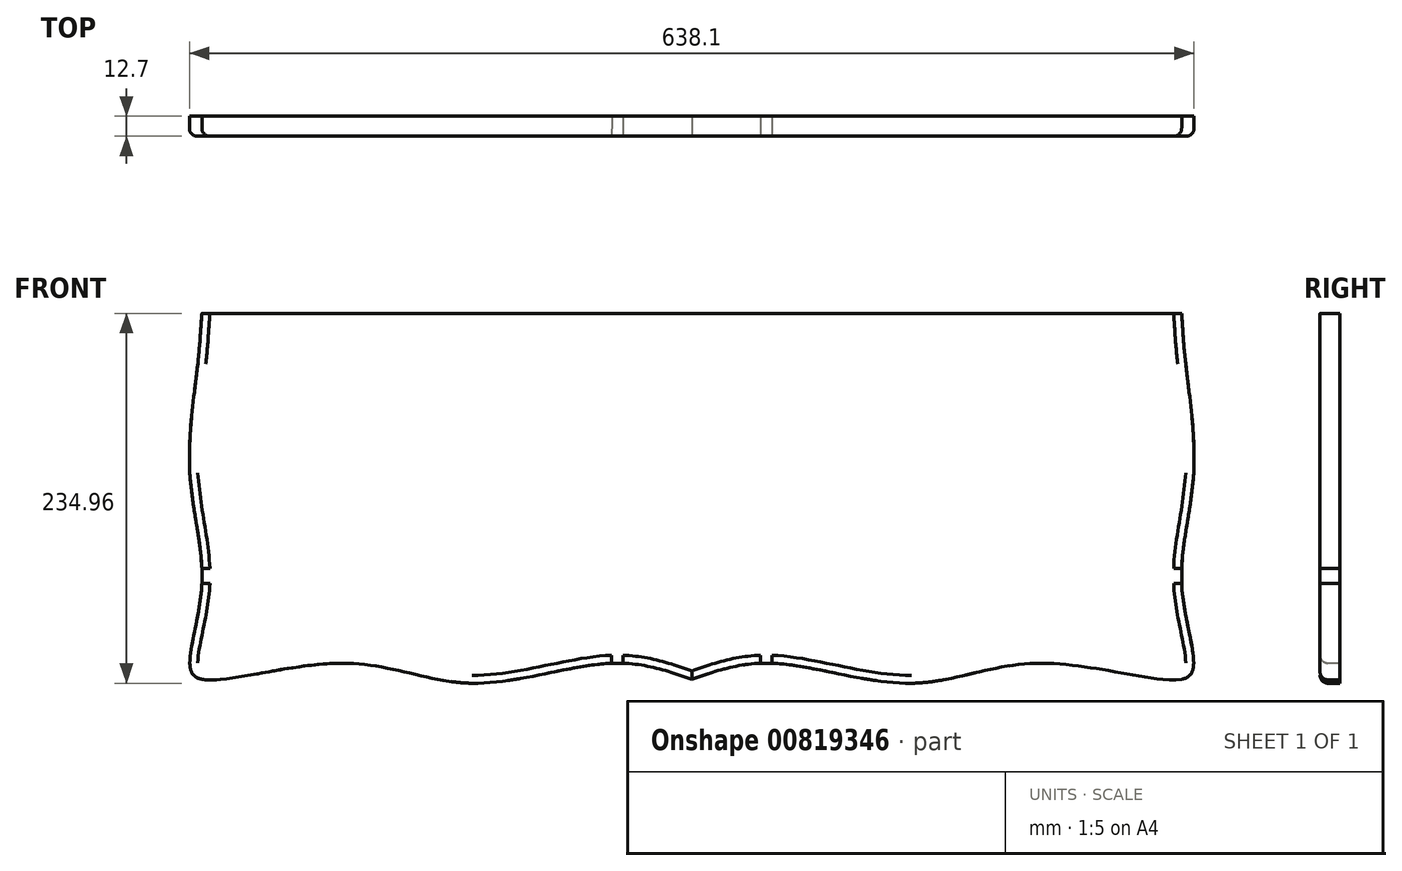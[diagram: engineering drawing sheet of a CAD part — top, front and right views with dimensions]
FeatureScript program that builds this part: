
annotation { "Feature Type Name" : "Feature", "Feature Type Description" : "" }
export const myFeature = defineFeature(function(context is Context, id is Id, definition is map)
    precondition{}
    {
        {
            var Q0;
            Q0=qCreatedBy(makeId("Front.planeOp"),FACE);
            var sketch = newSketch(context, id + "F0", { "sketchPlane" : qUnion([Q0])});
            skLineSegment(sketch, "E0.bottom", {"start": v(-290.57, 108.48) * mm, "end": v(331.73, 108.48) * mm});
            skLineSegment(sketch, "E0.top", {"start": v(-290.57, -113.77) * mm, "end": v(331.73, -113.77) * mm});
            skLineSegment(sketch, "E0.left", {"start": v(-290.57, 108.48) * mm, "end": v(-290.57, -113.77) * mm});
            skLineSegment(sketch, "E0.right", {"start": v(331.73, 108.48) * mm, "end": v(331.73, -113.77) * mm});
            skPoint(sketch, "E1", {"position": v(20.58, 108.48) * mm});
            skSolve(sketch);
        }
        {
            var Q0;
            Q0=makeQuery(id+"F0.imprint","IMPRINT",FACE,{"disambiguationData":[TD([[makeQuery(id+"F0.imprint","IMPRINT",EDGE,{"derivedFrom":sQuery(id+"F0.wireOp",EDGE,"E0.bottom")}),-1.0]])]});
            extrude(context, id + "F1", {"entities" : qUnion([Q0]), "depth" : 12.7 * mm, "offsetDistance" : 25.4 * mm});
        }
        {
            var Q0;
            {var subQ0=sQuery(id+"F0.wireOp",EDGE,"E0.right");var subQ1=sQuery(id+"F0.wireOp",EDGE,"E0.bottom");var subQ2=sQuery(id+"F0.wireOp",EDGE,"E0.left");var subQ3=sQuery(id+"F0.wireOp",EDGE,"E0.top");Q0=makeQuery(id+"FjgwLtvUwF4HY63_1.boolean.opBoolean","SPLIT",FACE,{"disambiguationData":[TD([makeQuery(id+"F1.opExtrude","SWEPT_FACE",FACE,{"disambiguationData":[OSD([subQ1])]})])],"derivedFrom":makeQuery(id+"F1.opExtrude","CAP_FACE",FACE,{"disambiguationData":[OSD([subQ1,subQ3,subQ2,subQ0])],"isStart":false})});}
            var sketch = newSketch(context, id + "F2", { "sketchPlane" : qUnion([Q0])});
            skPoint(sketch, "E2", {"position": v(-290.57, -62.97) * mm});
            skPoint(sketch, "E3", {"position": v(-290.57, 6.88) * mm});
            skPoint(sketch, "E4", {"position": v(-290.57, 76.73) * mm});
            skLineSegment(sketch, "E5", {"start": v(-290.57, 76.73) * mm, "end": v(-293.1, 76.73) * mm});
            skLineSegment(sketch, "E6", {"start": v(-290.57, 6.88) * mm, "end": v(-298.19, 6.88) * mm});
            skLineSegment(sketch, "E7", {"start": v(-290.57, -113.77) * mm, "end": v(-298.19, -113.77) * mm});
            skLineSegment(sketch, "E8", {"start": v(-290.57, -113.77) * mm, "end": v(-290.57, -123.93) * mm});
            skPoint(sketch, "E9", {"position": v(-201.67, -113.77) * mm});
            skPoint(sketch, "E10", {"position": v(20.58, -113.77) * mm});
            skPoint(sketch, "E11", {"position": v(-30.22, -113.77) * mm});
            skPoint(sketch, "E12", {"position": v(-119.12, -113.77) * mm});
            skPoint(sketch, "E13", {"position": v(71.38, -113.77) * mm});
            skPoint(sketch, "E14", {"position": v(160.28, -113.77) * mm});
            skPoint(sketch, "E15", {"position": v(242.83, -113.77) * mm});
            skPoint(sketch, "E16", {"position": v(331.73, -62.97) * mm});
            skPoint(sketch, "E17", {"position": v(331.73, 6.88) * mm});
            skPoint(sketch, "E18", {"position": v(331.73, 76.73) * mm});
            skLineSegment(sketch, "E19", {"start": v(331.73, 76.73) * mm, "end": v(334.27, 76.73) * mm});
            skLineSegment(sketch, "E20", {"start": v(331.73, 6.88) * mm, "end": v(339.35, 6.88) * mm});
            skLineSegment(sketch, "E21", {"start": v(331.73, -113.77) * mm, "end": v(339.35, -113.77) * mm});
            skLineSegment(sketch, "E22", {"start": v(331.73, -113.77) * mm, "end": v(331.73, -123.93) * mm});
            skLineSegment(sketch, "E23", {"start": v(-119.12, -113.77) * mm, "end": v(-119.12, -126.47) * mm});
            skLineSegment(sketch, "E24", {"start": v(20.58, -113.77) * mm, "end": v(20.58, -123.93) * mm});
            skLineSegment(sketch, "E25", {"start": v(160.28, -113.77) * mm, "end": v(160.28, -126.47) * mm});
            skFitSpline(sketch, "E26", {"points": [v(-290.57, 108.48) * mm, v(-293.1, 76.73) * mm, v(-298.19, 6.88) * mm, v(-290.57, -62.97) * mm, v(-298.19, -113.77) * mm, v(-290.57, -123.93) * mm, v(-201.67, -113.77) * mm, v(-119.12, -126.47) * mm, v(-30.22, -113.77) * mm, v(20.58, -123.93) * mm], "startDerivative": vector(-26.2, -341.82) * mm, "endDerivative": vector(438.15, -148.5) * mm});
            skFitSpline(sketch, "E27", {"points": [v(331.73, 108.48) * mm, v(334.27, 76.73) * mm, v(339.35, 6.88) * mm, v(331.73, -62.97) * mm, v(339.35, -113.77) * mm, v(331.73, -123.93) * mm, v(242.83, -113.77) * mm, v(160.28, -126.47) * mm, v(71.38, -113.77) * mm, v(20.58, -123.93) * mm], "startDerivative": vector(26.2, -341.82) * mm, "endDerivative": vector(-438.15, -148.5) * mm});
            skSolve(sketch);
        }
        {
            var Q0;
            {var subQ0=sQuery(id+"F2.wireOp",EDGE,"E24");Q0=makeQuery(id+"F2.imprint","IMPRINT",FACE,{"disambiguationData":[TD([[makeQuery(id+"F2.imprint","IMPRINT",EDGE,{"derivedFrom":subQ0}),-1.0]])]});}
            var Q1;
            {var subQ0=sQuery(id+"F2.wireOp",EDGE,"E24");Q1=makeQuery(id+"F2.imprint","IMPRINT",FACE,{"disambiguationData":[TD([[makeQuery(id+"F2.imprint","IMPRINT",EDGE,{"derivedFrom":subQ0}),1.0]])]});}
            var Q2;
            {var subQ0=sQuery(id+"F2.wireOp",EDGE,"E23");Q2=makeQuery(id+"F2.imprint","IMPRINT",FACE,{"disambiguationData":[TD([[makeQuery(id+"F2.imprint","IMPRINT",EDGE,{"derivedFrom":subQ0}),1.0]])]});}
            var Q3;
            {var subQ0=sQuery(id+"F2.wireOp",EDGE,"E23");Q3=makeQuery(id+"F2.imprint","IMPRINT",FACE,{"disambiguationData":[TD([[makeQuery(id+"F2.imprint","IMPRINT",EDGE,{"derivedFrom":subQ0}),-1.0]])]});}
            var Q4;
            {var subQ0=sQuery(id+"F2.wireOp",EDGE,"E8");Q4=makeQuery(id+"F2.imprint","IMPRINT",FACE,{"disambiguationData":[TD([[makeQuery(id+"F2.imprint","IMPRINT",EDGE,{"derivedFrom":subQ0}),1.0]])]});}
            var Q5;
            {var subQ0=sQuery(id+"F2.wireOp",EDGE,"E7");Q5=makeQuery(id+"F2.imprint","IMPRINT",FACE,{"disambiguationData":[TD([[makeQuery(id+"F2.imprint","IMPRINT",EDGE,{"derivedFrom":subQ0}),1.0]])]});}
            var Q6;
            {var subQ0=sQuery(id+"F2.wireOp",EDGE,"E7");Q6=makeQuery(id+"F2.imprint","IMPRINT",FACE,{"disambiguationData":[TD([[makeQuery(id+"F2.imprint","IMPRINT",EDGE,{"derivedFrom":subQ0}),-1.0]])]});}
            var Q7;
            {var subQ0=sQuery(id+"F2.wireOp",EDGE,"E6");Q7=makeQuery(id+"F2.imprint","IMPRINT",FACE,{"disambiguationData":[TD([[makeQuery(id+"F2.imprint","IMPRINT",EDGE,{"derivedFrom":subQ0}),1.0]])]});}
            var Q8;
            {var subQ0=sQuery(id+"F2.wireOp",EDGE,"E5");Q8=makeQuery(id+"F2.imprint","IMPRINT",FACE,{"disambiguationData":[TD([[makeQuery(id+"F2.imprint","IMPRINT",EDGE,{"derivedFrom":subQ0}),1.0]])]});}
            var Q9;
            {var subQ0=makeQuery(id+"F1.opExtrude","CAP_EDGE",EDGE,{"disambiguationData":[OSD([sQuery(id+"F0.wireOp",EDGE,"E0.bottom")])],"isStart":false});Q9=makeQuery(id+"F2.imprint","IMPRINT",FACE,{"disambiguationData":[TD([[makeQuery(id+"F2.imprint","IMPRINT",EDGE,{"derivedFrom":subQ0}),-1.0]])]});}
            var Q10;
            {var subQ0=sQuery(id+"F2.wireOp",EDGE,"E25");Q10=makeQuery(id+"F2.imprint","IMPRINT",FACE,{"disambiguationData":[TD([[makeQuery(id+"F2.imprint","IMPRINT",EDGE,{"derivedFrom":subQ0}),-1.0]])]});}
            var Q11;
            {var subQ0=sQuery(id+"F2.wireOp",EDGE,"E25");Q11=makeQuery(id+"F2.imprint","IMPRINT",FACE,{"disambiguationData":[TD([[makeQuery(id+"F2.imprint","IMPRINT",EDGE,{"derivedFrom":subQ0}),1.0]])]});}
            var Q12;
            {var subQ0=sQuery(id+"F2.wireOp",EDGE,"E22");Q12=makeQuery(id+"F2.imprint","IMPRINT",FACE,{"disambiguationData":[TD([[makeQuery(id+"F2.imprint","IMPRINT",EDGE,{"derivedFrom":subQ0}),-1.0]])]});}
            var Q13;
            {var subQ0=sQuery(id+"F2.wireOp",EDGE,"E21");Q13=makeQuery(id+"F2.imprint","IMPRINT",FACE,{"disambiguationData":[TD([[makeQuery(id+"F2.imprint","IMPRINT",EDGE,{"derivedFrom":subQ0}),-1.0]])]});}
            var Q14;
            {var subQ0=sQuery(id+"F2.wireOp",EDGE,"E21");Q14=makeQuery(id+"F2.imprint","IMPRINT",FACE,{"disambiguationData":[TD([[makeQuery(id+"F2.imprint","IMPRINT",EDGE,{"derivedFrom":subQ0}),1.0]])]});}
            var Q15;
            {var subQ0=sQuery(id+"F2.wireOp",EDGE,"E20");Q15=makeQuery(id+"F2.imprint","IMPRINT",FACE,{"disambiguationData":[TD([[makeQuery(id+"F2.imprint","IMPRINT",EDGE,{"derivedFrom":subQ0}),-1.0]])]});}
            var Q16;
            {var subQ0=sQuery(id+"F2.wireOp",EDGE,"E19");Q16=makeQuery(id+"F2.imprint","IMPRINT",FACE,{"disambiguationData":[TD([[makeQuery(id+"F2.imprint","IMPRINT",EDGE,{"derivedFrom":subQ0}),-1.0]])]});}
            var Q17;
            {var subQ0=sQuery(id+"F2.wireOp",EDGE,"E19");Q17=makeQuery(id+"F2.imprint","IMPRINT",FACE,{"disambiguationData":[TD([[makeQuery(id+"F2.imprint","IMPRINT",EDGE,{"derivedFrom":subQ0}),1.0]])]});}
            var Q18;
            {var subQ0=sQuery(id+"F2.wireOp",EDGE,"E5");Q18=makeQuery(id+"F2.imprint","IMPRINT",FACE,{"disambiguationData":[TD([[makeQuery(id+"F2.imprint","IMPRINT",EDGE,{"derivedFrom":subQ0}),-1.0]])]});}
            extrude(context, id + "F3", {"entities" : qUnion([Q0, Q1, Q2, Q3, Q4, Q5, Q6, Q7, Q8, Q9, Q10, Q11, Q12, Q13, Q14, Q15, Q16, Q17, Q18]), "operationType" : NewBodyOperationType.ADD, "depth" : -12.7 * mm, "offsetDistance" : 25.4 * mm});
        }
        {
            var Q0;
            {var subQ0=sQuery(id+"F2.wireOp",EDGE,"8007402e-1a4e-4a06-85a5-2af08e553504");var subQ1=sQuery(id+"F0.wireOp",EDGE,"E0.left");var subQ2=sQuery(id+"F0.wireOp",EDGE,"E0.top");var subQ3=sQuery(id+"F0.wireOp",EDGE,"E0.bottom");Q0=makeQuery(id+"F3.boolean.opBoolean","SPLIT",EDGE,{"disambiguationData":[TD([makeQuery(id+"F1.opExtrude","CAP_FACE",FACE,{"disambiguationData":[OSD([subQ3,subQ2,subQ1,sQuery(id+"F0.wireOp",EDGE,"E0.right")])],"isStart":false}),makeQuery(id+"F1.opExtrude","SWEPT_FACE",FACE,{"disambiguationData":[OSD([subQ2])]}),makeQuery(id+"F1.opExtrude","SWEPT_FACE",FACE,{"disambiguationData":[OSD([subQ1])]}),makeQuery(id+"F3.opExtrude","SWEPT_FACE",FACE,{"disambiguationData":[OSD([subQ0])]}),makeQuery(id+"F3.opExtrude","CAP_FACE",FACE,{"disambiguationData":[OSD([subQ3,sQuery(id+"FQ5JFwxVdaqARUP_1.wireOp",EDGE,"fcba4419-a2ee-464f-be9d-58f11bf3418b.sketch_text.stroke-0"),sQuery(id+"FQ5JFwxVdaqARUP_1.wireOp",EDGE,"fcba4419-a2ee-464f-be9d-58f11bf3418b.sketch_text.stroke-1"),sQuery(id+"FQ5JFwxVdaqARUP_1.wireOp",EDGE,"fcba4419-a2ee-464f-be9d-58f11bf3418b.sketch_text.stroke-2"),sQuery(id+"FQ5JFwxVdaqARUP_1.wireOp",EDGE,"fcba4419-a2ee-464f-be9d-58f11bf3418b.sketch_text.stroke-3"),sQuery(id+"FQ5JFwxVdaqARUP_1.wireOp",EDGE,"fcba4419-a2ee-464f-be9d-58f11bf3418b.sketch_text.stroke-4"),sQuery(id+"FQ5JFwxVdaqARUP_1.wireOp",EDGE,"fcba4419-a2ee-464f-be9d-58f11bf3418b.sketch_text.stroke-5"),sQuery(id+"FQ5JFwxVdaqARUP_1.wireOp",EDGE,"fcba4419-a2ee-464f-be9d-58f11bf3418b.sketch_text.stroke-6"),sQuery(id+"FQ5JFwxVdaqARUP_1.wireOp",EDGE,"fcba4419-a2ee-464f-be9d-58f11bf3418b.sketch_text.stroke-7"),sQuery(id+"FQ5JFwxVdaqARUP_1.wireOp",EDGE,"fcba4419-a2ee-464f-be9d-58f11bf3418b.sketch_text.stroke-8"),sQuery(id+"FQ5JFwxVdaqARUP_1.wireOp",EDGE,"fcba4419-a2ee-464f-be9d-58f11bf3418b.sketch_text.stroke-9"),sQuery(id+"FQ5JFwxVdaqARUP_1.wireOp",EDGE,"fcba4419-a2ee-464f-be9d-58f11bf3418b.sketch_text.stroke-10"),sQuery(id+"FQ5JFwxVdaqARUP_1.wireOp",EDGE,"fcba4419-a2ee-464f-be9d-58f11bf3418b.sketch_text.stroke-11"),sQuery(id+"FQ5JFwxVdaqARUP_1.wireOp",EDGE,"fcba4419-a2ee-464f-be9d-58f11bf3418b.sketch_text.stroke-12"),sQuery(id+"FQ5JFwxVdaqARUP_1.wireOp",EDGE,"fcba4419-a2ee-464f-be9d-58f11bf3418b.sketch_text.stroke-13"),sQuery(id+"FQ5JFwxVdaqARUP_1.wireOp",EDGE,"fcba4419-a2ee-464f-be9d-58f11bf3418b.sketch_text.stroke-14"),sQuery(id+"FQ5JFwxVdaqARUP_1.wireOp",EDGE,"fcba4419-a2ee-464f-be9d-58f11bf3418b.sketch_text.stroke-15"),sQuery(id+"FQ5JFwxVdaqARUP_1.wireOp",EDGE,"fcba4419-a2ee-464f-be9d-58f11bf3418b.sketch_text.stroke-16"),sQuery(id+"FQ5JFwxVdaqARUP_1.wireOp",EDGE,"fcba4419-a2ee-464f-be9d-58f11bf3418b.sketch_text.stroke-17"),sQuery(id+"FQ5JFwxVdaqARUP_1.wireOp",EDGE,"fcba4419-a2ee-464f-be9d-58f11bf3418b.sketch_text.stroke-18"),sQuery(id+"FQ5JFwxVdaqARUP_1.wireOp",EDGE,"fcba4419-a2ee-464f-be9d-58f11bf3418b.sketch_text.stroke-19"),sQuery(id+"FQ5JFwxVdaqARUP_1.wireOp",EDGE,"fcba4419-a2ee-464f-be9d-58f11bf3418b.sketch_text.stroke-20"),sQuery(id+"FQ5JFwxVdaqARUP_1.wireOp",EDGE,"fcba4419-a2ee-464f-be9d-58f11bf3418b.sketch_text.stroke-21"),sQuery(id+"FQ5JFwxVdaqARUP_1.wireOp",EDGE,"fcba4419-a2ee-464f-be9d-58f11bf3418b.sketch_text.stroke-22"),sQuery(id+"FQ5JFwxVdaqARUP_1.wireOp",EDGE,"fcba4419-a2ee-464f-be9d-58f11bf3418b.sketch_text.stroke-23"),sQuery(id+"FQ5JFwxVdaqARUP_1.wireOp",EDGE,"fcba4419-a2ee-464f-be9d-58f11bf3418b.sketch_text.stroke-24"),sQuery(id+"FQ5JFwxVdaqARUP_1.wireOp",EDGE,"fcba4419-a2ee-464f-be9d-58f11bf3418b.sketch_text.stroke-25"),sQuery(id+"FQ5JFwxVdaqARUP_1.wireOp",EDGE,"fcba4419-a2ee-464f-be9d-58f11bf3418b.sketch_text.stroke-26"),sQuery(id+"FQ5JFwxVdaqARUP_1.wireOp",EDGE,"fcba4419-a2ee-464f-be9d-58f11bf3418b.sketch_text.stroke-27"),sQuery(id+"FQ5JFwxVdaqARUP_1.wireOp",EDGE,"fcba4419-a2ee-464f-be9d-58f11bf3418b.sketch_text.stroke-28"),sQuery(id+"FQ5JFwxVdaqARUP_1.wireOp",EDGE,"fcba4419-a2ee-464f-be9d-58f11bf3418b.sketch_text.stroke-29"),sQuery(id+"FQ5JFwxVdaqARUP_1.wireOp",EDGE,"fcba4419-a2ee-464f-be9d-58f11bf3418b.sketch_text.stroke-30"),sQuery(id+"FQ5JFwxVdaqARUP_1.wireOp",EDGE,"fcba4419-a2ee-464f-be9d-58f11bf3418b.sketch_text.stroke-31"),sQuery(id+"FQ5JFwxVdaqARUP_1.wireOp",EDGE,"fcba4419-a2ee-464f-be9d-58f11bf3418b.sketch_text.stroke-32"),sQuery(id+"FQ5JFwxVdaqARUP_1.wireOp",EDGE,"fcba4419-a2ee-464f-be9d-58f11bf3418b.sketch_text.stroke-33"),sQuery(id+"FQ5JFwxVdaqARUP_1.wireOp",EDGE,"fcba4419-a2ee-464f-be9d-58f11bf3418b.sketch_text.stroke-34"),sQuery(id+"FQ5JFwxVdaqARUP_1.wireOp",EDGE,"fcba4419-a2ee-464f-be9d-58f11bf3418b.sketch_text.stroke-35"),sQuery(id+"FQ5JFwxVdaqARUP_1.wireOp",EDGE,"fcba4419-a2ee-464f-be9d-58f11bf3418b.sketch_text.stroke-36"),sQuery(id+"FQ5JFwxVdaqARUP_1.wireOp",EDGE,"fcba4419-a2ee-464f-be9d-58f11bf3418b.sketch_text.stroke-37"),sQuery(id+"FQ5JFwxVdaqARUP_1.wireOp",EDGE,"fcba4419-a2ee-464f-be9d-58f11bf3418b.sketch_text.stroke-38"),sQuery(id+"FQ5JFwxVdaqARUP_1.wireOp",EDGE,"fcba4419-a2ee-464f-be9d-58f11bf3418b.sketch_text.stroke-39"),sQuery(id+"FQ5JFwxVdaqARUP_1.wireOp",EDGE,"fcba4419-a2ee-464f-be9d-58f11bf3418b.sketch_text.stroke-40"),sQuery(id+"FQ5JFwxVdaqARUP_1.wireOp",EDGE,"fcba4419-a2ee-464f-be9d-58f11bf3418b.sketch_text.stroke-41"),sQuery(id+"FQ5JFwxVdaqARUP_1.wireOp",EDGE,"fcba4419-a2ee-464f-be9d-58f11bf3418b.sketch_text.stroke-42"),sQuery(id+"FQ5JFwxVdaqARUP_1.wireOp",EDGE,"fcba4419-a2ee-464f-be9d-58f11bf3418b.sketch_text.stroke-43"),sQuery(id+"FQ5JFwxVdaqARUP_1.wireOp",EDGE,"fcba4419-a2ee-464f-be9d-58f11bf3418b.sketch_text.stroke-44"),sQuery(id+"FQ5JFwxVdaqARUP_1.wireOp",EDGE,"fcba4419-a2ee-464f-be9d-58f11bf3418b.sketch_text.stroke-45"),sQuery(id+"FQ5JFwxVdaqARUP_1.wireOp",EDGE,"fcba4419-a2ee-464f-be9d-58f11bf3418b.sketch_text.stroke-46"),sQuery(id+"FQ5JFwxVdaqARUP_1.wireOp",EDGE,"fcba4419-a2ee-464f-be9d-58f11bf3418b.sketch_text.stroke-47"),sQuery(id+"FQ5JFwxVdaqARUP_1.wireOp",EDGE,"fcba4419-a2ee-464f-be9d-58f11bf3418b.sketch_text.stroke-48"),sQuery(id+"FQ5JFwxVdaqARUP_1.wireOp",EDGE,"fcba4419-a2ee-464f-be9d-58f11bf3418b.sketch_text.stroke-49"),sQuery(id+"FQ5JFwxVdaqARUP_1.wireOp",EDGE,"fcba4419-a2ee-464f-be9d-58f11bf3418b.sketch_text.stroke-50"),sQuery(id+"FQ5JFwxVdaqARUP_1.wireOp",EDGE,"fcba4419-a2ee-464f-be9d-58f11bf3418b.sketch_text.stroke-51"),sQuery(id+"FQ5JFwxVdaqARUP_1.wireOp",EDGE,"fcba4419-a2ee-464f-be9d-58f11bf3418b.sketch_text.stroke-52"),sQuery(id+"FQ5JFwxVdaqARUP_1.wireOp",EDGE,"fcba4419-a2ee-464f-be9d-58f11bf3418b.sketch_text.stroke-53"),sQuery(id+"FQ5JFwxVdaqARUP_1.wireOp",EDGE,"fcba4419-a2ee-464f-be9d-58f11bf3418b.sketch_text.stroke-54"),sQuery(id+"FQ5JFwxVdaqARUP_1.wireOp",EDGE,"fcba4419-a2ee-464f-be9d-58f11bf3418b.sketch_text.stroke-55"),sQuery(id+"FQ5JFwxVdaqARUP_1.wireOp",EDGE,"fcba4419-a2ee-464f-be9d-58f11bf3418b.sketch_text.stroke-56"),sQuery(id+"FQ5JFwxVdaqARUP_1.wireOp",EDGE,"fcba4419-a2ee-464f-be9d-58f11bf3418b.sketch_text.stroke-57"),sQuery(id+"FQ5JFwxVdaqARUP_1.wireOp",EDGE,"fcba4419-a2ee-464f-be9d-58f11bf3418b.sketch_text.stroke-58"),sQuery(id+"FQ5JFwxVdaqARUP_1.wireOp",EDGE,"fcba4419-a2ee-464f-be9d-58f11bf3418b.sketch_text.stroke-59"),sQuery(id+"FQ5JFwxVdaqARUP_1.wireOp",EDGE,"fcba4419-a2ee-464f-be9d-58f11bf3418b.sketch_text.stroke-60"),sQuery(id+"FQ5JFwxVdaqARUP_1.wireOp",EDGE,"fcba4419-a2ee-464f-be9d-58f11bf3418b.sketch_text.stroke-61"),sQuery(id+"FQ5JFwxVdaqARUP_1.wireOp",EDGE,"fcba4419-a2ee-464f-be9d-58f11bf3418b.sketch_text.stroke-62"),sQuery(id+"FQ5JFwxVdaqARUP_1.wireOp",EDGE,"fcba4419-a2ee-464f-be9d-58f11bf3418b.sketch_text.stroke-63"),sQuery(id+"FQ5JFwxVdaqARUP_1.wireOp",EDGE,"fcba4419-a2ee-464f-be9d-58f11bf3418b.sketch_text.stroke-64"),sQuery(id+"FQ5JFwxVdaqARUP_1.wireOp",EDGE,"fcba4419-a2ee-464f-be9d-58f11bf3418b.sketch_text.stroke-65"),sQuery(id+"FQ5JFwxVdaqARUP_1.wireOp",EDGE,"fcba4419-a2ee-464f-be9d-58f11bf3418b.sketch_text.stroke-66"),sQuery(id+"FQ5JFwxVdaqARUP_1.wireOp",EDGE,"fcba4419-a2ee-464f-be9d-58f11bf3418b.sketch_text.stroke-67"),sQuery(id+"FQ5JFwxVdaqARUP_1.wireOp",EDGE,"fcba4419-a2ee-464f-be9d-58f11bf3418b.sketch_text.stroke-68"),sQuery(id+"FQ5JFwxVdaqARUP_1.wireOp",EDGE,"fcba4419-a2ee-464f-be9d-58f11bf3418b.sketch_text.stroke-69"),sQuery(id+"FQ5JFwxVdaqARUP_1.wireOp",EDGE,"fcba4419-a2ee-464f-be9d-58f11bf3418b.sketch_text.stroke-70"),sQuery(id+"FQ5JFwxVdaqARUP_1.wireOp",EDGE,"fcba4419-a2ee-464f-be9d-58f11bf3418b.sketch_text.stroke-71"),sQuery(id+"FQ5JFwxVdaqARUP_1.wireOp",EDGE,"fcba4419-a2ee-464f-be9d-58f11bf3418b.sketch_text.stroke-72"),sQuery(id+"FQ5JFwxVdaqARUP_1.wireOp",EDGE,"fcba4419-a2ee-464f-be9d-58f11bf3418b.sketch_text.stroke-73"),sQuery(id+"FQ5JFwxVdaqARUP_1.wireOp",EDGE,"fcba4419-a2ee-464f-be9d-58f11bf3418b.sketch_text.stroke-74"),sQuery(id+"FQ5JFwxVdaqARUP_1.wireOp",EDGE,"fcba4419-a2ee-464f-be9d-58f11bf3418b.sketch_text.stroke-75"),sQuery(id+"FQ5JFwxVdaqARUP_1.wireOp",EDGE,"fcba4419-a2ee-464f-be9d-58f11bf3418b.sketch_text.stroke-76"),sQuery(id+"FQ5JFwxVdaqARUP_1.wireOp",EDGE,"fcba4419-a2ee-464f-be9d-58f11bf3418b.sketch_text.stroke-77"),sQuery(id+"FQ5JFwxVdaqARUP_1.wireOp",EDGE,"fcba4419-a2ee-464f-be9d-58f11bf3418b.sketch_text.stroke-78"),sQuery(id+"FQ5JFwxVdaqARUP_1.wireOp",EDGE,"fcba4419-a2ee-464f-be9d-58f11bf3418b.sketch_text.stroke-79"),sQuery(id+"FQ5JFwxVdaqARUP_1.wireOp",EDGE,"fcba4419-a2ee-464f-be9d-58f11bf3418b.sketch_text.stroke-80"),sQuery(id+"FQ5JFwxVdaqARUP_1.wireOp",EDGE,"fcba4419-a2ee-464f-be9d-58f11bf3418b.sketch_text.stroke-81"),sQuery(id+"FQ5JFwxVdaqARUP_1.wireOp",EDGE,"fcba4419-a2ee-464f-be9d-58f11bf3418b.sketch_text.stroke-82"),sQuery(id+"FQ5JFwxVdaqARUP_1.wireOp",EDGE,"fcba4419-a2ee-464f-be9d-58f11bf3418b.sketch_text.stroke-83"),sQuery(id+"FQ5JFwxVdaqARUP_1.wireOp",EDGE,"fcba4419-a2ee-464f-be9d-58f11bf3418b.sketch_text.stroke-84"),sQuery(id+"FQ5JFwxVdaqARUP_1.wireOp",EDGE,"fcba4419-a2ee-464f-be9d-58f11bf3418b.sketch_text.stroke-85"),sQuery(id+"FQ5JFwxVdaqARUP_1.wireOp",EDGE,"fcba4419-a2ee-464f-be9d-58f11bf3418b.sketch_text.stroke-86"),sQuery(id+"FQ5JFwxVdaqARUP_1.wireOp",EDGE,"fcba4419-a2ee-464f-be9d-58f11bf3418b.sketch_text.stroke-87"),sQuery(id+"FQ5JFwxVdaqARUP_1.wireOp",EDGE,"fcba4419-a2ee-464f-be9d-58f11bf3418b.sketch_text.stroke-88"),sQuery(id+"FQ5JFwxVdaqARUP_1.wireOp",EDGE,"fcba4419-a2ee-464f-be9d-58f11bf3418b.sketch_text.stroke-89"),sQuery(id+"FQ5JFwxVdaqARUP_1.wireOp",EDGE,"fcba4419-a2ee-464f-be9d-58f11bf3418b.sketch_text.stroke-90"),sQuery(id+"FQ5JFwxVdaqARUP_1.wireOp",EDGE,"fcba4419-a2ee-464f-be9d-58f11bf3418b.sketch_text.stroke-91"),sQuery(id+"FQ5JFwxVdaqARUP_1.wireOp",EDGE,"fcba4419-a2ee-464f-be9d-58f11bf3418b.sketch_text.stroke-92"),sQuery(id+"FQ5JFwxVdaqARUP_1.wireOp",EDGE,"fcba4419-a2ee-464f-be9d-58f11bf3418b.sketch_text.stroke-93"),sQuery(id+"FQ5JFwxVdaqARUP_1.wireOp",EDGE,"fcba4419-a2ee-464f-be9d-58f11bf3418b.sketch_text.stroke-94"),sQuery(id+"FQ5JFwxVdaqARUP_1.wireOp",EDGE,"fcba4419-a2ee-464f-be9d-58f11bf3418b.sketch_text.stroke-95"),sQuery(id+"FQ5JFwxVdaqARUP_1.wireOp",EDGE,"fcba4419-a2ee-464f-be9d-58f11bf3418b.sketch_text.stroke-96"),sQuery(id+"FQ5JFwxVdaqARUP_1.wireOp",EDGE,"fcba4419-a2ee-464f-be9d-58f11bf3418b.sketch_text.stroke-97"),sQuery(id+"FQ5JFwxVdaqARUP_1.wireOp",EDGE,"fcba4419-a2ee-464f-be9d-58f11bf3418b.sketch_text.stroke-98"),sQuery(id+"FQ5JFwxVdaqARUP_1.wireOp",EDGE,"fcba4419-a2ee-464f-be9d-58f11bf3418b.sketch_text.stroke-99"),sQuery(id+"FQ5JFwxVdaqARUP_1.wireOp",EDGE,"fcba4419-a2ee-464f-be9d-58f11bf3418b.sketch_text.stroke-100"),sQuery(id+"FQ5JFwxVdaqARUP_1.wireOp",EDGE,"fcba4419-a2ee-464f-be9d-58f11bf3418b.sketch_text.stroke-101"),sQuery(id+"FQ5JFwxVdaqARUP_1.wireOp",EDGE,"fcba4419-a2ee-464f-be9d-58f11bf3418b.sketch_text.stroke-102"),sQuery(id+"FQ5JFwxVdaqARUP_1.wireOp",EDGE,"fcba4419-a2ee-464f-be9d-58f11bf3418b.sketch_text.stroke-103"),sQuery(id+"FQ5JFwxVdaqARUP_1.wireOp",EDGE,"fcba4419-a2ee-464f-be9d-58f11bf3418b.sketch_text.stroke-104"),sQuery(id+"FQ5JFwxVdaqARUP_1.wireOp",EDGE,"fcba4419-a2ee-464f-be9d-58f11bf3418b.sketch_text.stroke-105"),sQuery(id+"FQ5JFwxVdaqARUP_1.wireOp",EDGE,"fcba4419-a2ee-464f-be9d-58f11bf3418b.sketch_text.stroke-106"),sQuery(id+"FQ5JFwxVdaqARUP_1.wireOp",EDGE,"fcba4419-a2ee-464f-be9d-58f11bf3418b.sketch_text.stroke-107"),sQuery(id+"FQ5JFwxVdaqARUP_1.wireOp",EDGE,"fcba4419-a2ee-464f-be9d-58f11bf3418b.sketch_text.stroke-108"),sQuery(id+"FQ5JFwxVdaqARUP_1.wireOp",EDGE,"fcba4419-a2ee-464f-be9d-58f11bf3418b.sketch_text.stroke-109"),sQuery(id+"FQ5JFwxVdaqARUP_1.wireOp",EDGE,"fcba4419-a2ee-464f-be9d-58f11bf3418b.sketch_text.stroke-110"),sQuery(id+"FQ5JFwxVdaqARUP_1.wireOp",EDGE,"fcba4419-a2ee-464f-be9d-58f11bf3418b.sketch_text.stroke-111"),sQuery(id+"FQ5JFwxVdaqARUP_1.wireOp",EDGE,"fcba4419-a2ee-464f-be9d-58f11bf3418b.sketch_text.stroke-112"),sQuery(id+"FQ5JFwxVdaqARUP_1.wireOp",EDGE,"fcba4419-a2ee-464f-be9d-58f11bf3418b.sketch_text.stroke-113"),sQuery(id+"FQ5JFwxVdaqARUP_1.wireOp",EDGE,"fcba4419-a2ee-464f-be9d-58f11bf3418b.sketch_text.stroke-114"),sQuery(id+"FQ5JFwxVdaqARUP_1.wireOp",EDGE,"fcba4419-a2ee-464f-be9d-58f11bf3418b.sketch_text.stroke-115"),sQuery(id+"FQ5JFwxVdaqARUP_1.wireOp",EDGE,"fcba4419-a2ee-464f-be9d-58f11bf3418b.sketch_text.stroke-116"),sQuery(id+"FQ5JFwxVdaqARUP_1.wireOp",EDGE,"fcba4419-a2ee-464f-be9d-58f11bf3418b.sketch_text.stroke-117"),sQuery(id+"FQ5JFwxVdaqARUP_1.wireOp",EDGE,"fcba4419-a2ee-464f-be9d-58f11bf3418b.sketch_text.stroke-118"),sQuery(id+"FQ5JFwxVdaqARUP_1.wireOp",EDGE,"fcba4419-a2ee-464f-be9d-58f11bf3418b.sketch_text.stroke-119"),sQuery(id+"FQ5JFwxVdaqARUP_1.wireOp",EDGE,"fcba4419-a2ee-464f-be9d-58f11bf3418b.sketch_text.stroke-120"),sQuery(id+"FQ5JFwxVdaqARUP_1.wireOp",EDGE,"fcba4419-a2ee-464f-be9d-58f11bf3418b.sketch_text.stroke-121"),sQuery(id+"FQ5JFwxVdaqARUP_1.wireOp",EDGE,"fcba4419-a2ee-464f-be9d-58f11bf3418b.sketch_text.stroke-122"),sQuery(id+"FQ5JFwxVdaqARUP_1.wireOp",EDGE,"fcba4419-a2ee-464f-be9d-58f11bf3418b.sketch_text.stroke-123"),sQuery(id+"FQ5JFwxVdaqARUP_1.wireOp",EDGE,"fcba4419-a2ee-464f-be9d-58f11bf3418b.sketch_text.stroke-124"),sQuery(id+"FQ5JFwxVdaqARUP_1.wireOp",EDGE,"fcba4419-a2ee-464f-be9d-58f11bf3418b.sketch_text.stroke-125"),sQuery(id+"FQ5JFwxVdaqARUP_1.wireOp",EDGE,"fcba4419-a2ee-464f-be9d-58f11bf3418b.sketch_text.stroke-126"),sQuery(id+"FQ5JFwxVdaqARUP_1.wireOp",EDGE,"fcba4419-a2ee-464f-be9d-58f11bf3418b.sketch_text.stroke-127"),sQuery(id+"FQ5JFwxVdaqARUP_1.wireOp",EDGE,"fcba4419-a2ee-464f-be9d-58f11bf3418b.sketch_text.stroke-128"),sQuery(id+"FQ5JFwxVdaqARUP_1.wireOp",EDGE,"fcba4419-a2ee-464f-be9d-58f11bf3418b.sketch_text.stroke-129"),sQuery(id+"FQ5JFwxVdaqARUP_1.wireOp",EDGE,"fcba4419-a2ee-464f-be9d-58f11bf3418b.sketch_text.stroke-130"),sQuery(id+"FQ5JFwxVdaqARUP_1.wireOp",EDGE,"fcba4419-a2ee-464f-be9d-58f11bf3418b.sketch_text.stroke-131"),sQuery(id+"FQ5JFwxVdaqARUP_1.wireOp",EDGE,"fcba4419-a2ee-464f-be9d-58f11bf3418b.sketch_text.stroke-132"),sQuery(id+"FQ5JFwxVdaqARUP_1.wireOp",EDGE,"fcba4419-a2ee-464f-be9d-58f11bf3418b.sketch_text.stroke-133"),sQuery(id+"FQ5JFwxVdaqARUP_1.wireOp",EDGE,"fcba4419-a2ee-464f-be9d-58f11bf3418b.sketch_text.stroke-134"),sQuery(id+"FQ5JFwxVdaqARUP_1.wireOp",EDGE,"fcba4419-a2ee-464f-be9d-58f11bf3418b.sketch_text.stroke-135"),sQuery(id+"FQ5JFwxVdaqARUP_1.wireOp",EDGE,"fcba4419-a2ee-464f-be9d-58f11bf3418b.sketch_text.stroke-136"),sQuery(id+"FQ5JFwxVdaqARUP_1.wireOp",EDGE,"fcba4419-a2ee-464f-be9d-58f11bf3418b.sketch_text.stroke-137"),sQuery(id+"FQ5JFwxVdaqARUP_1.wireOp",EDGE,"fcba4419-a2ee-464f-be9d-58f11bf3418b.sketch_text.stroke-138"),sQuery(id+"FQ5JFwxVdaqARUP_1.wireOp",EDGE,"fcba4419-a2ee-464f-be9d-58f11bf3418b.sketch_text.stroke-139"),sQuery(id+"FQ5JFwxVdaqARUP_1.wireOp",EDGE,"fcba4419-a2ee-464f-be9d-58f11bf3418b.sketch_text.stroke-140"),sQuery(id+"FQ5JFwxVdaqARUP_1.wireOp",EDGE,"fcba4419-a2ee-464f-be9d-58f11bf3418b.sketch_text.stroke-141"),sQuery(id+"FQ5JFwxVdaqARUP_1.wireOp",EDGE,"fcba4419-a2ee-464f-be9d-58f11bf3418b.sketch_text.stroke-142"),sQuery(id+"FQ5JFwxVdaqARUP_1.wireOp",EDGE,"fcba4419-a2ee-464f-be9d-58f11bf3418b.sketch_text.stroke-143"),sQuery(id+"FQ5JFwxVdaqARUP_1.wireOp",EDGE,"fcba4419-a2ee-464f-be9d-58f11bf3418b.sketch_text.stroke-144"),sQuery(id+"FQ5JFwxVdaqARUP_1.wireOp",EDGE,"fcba4419-a2ee-464f-be9d-58f11bf3418b.sketch_text.stroke-145"),sQuery(id+"FQ5JFwxVdaqARUP_1.wireOp",EDGE,"fcba4419-a2ee-464f-be9d-58f11bf3418b.sketch_text.stroke-146"),sQuery(id+"FQ5JFwxVdaqARUP_1.wireOp",EDGE,"fcba4419-a2ee-464f-be9d-58f11bf3418b.sketch_text.stroke-147"),sQuery(id+"FQ5JFwxVdaqARUP_1.wireOp",EDGE,"fcba4419-a2ee-464f-be9d-58f11bf3418b.sketch_text.stroke-148"),sQuery(id+"FQ5JFwxVdaqARUP_1.wireOp",EDGE,"fcba4419-a2ee-464f-be9d-58f11bf3418b.sketch_text.stroke-149"),sQuery(id+"FQ5JFwxVdaqARUP_1.wireOp",EDGE,"fcba4419-a2ee-464f-be9d-58f11bf3418b.sketch_text.stroke-150"),sQuery(id+"FQ5JFwxVdaqARUP_1.wireOp",EDGE,"fcba4419-a2ee-464f-be9d-58f11bf3418b.sketch_text.stroke-151"),sQuery(id+"FQ5JFwxVdaqARUP_1.wireOp",EDGE,"fcba4419-a2ee-464f-be9d-58f11bf3418b.sketch_text.stroke-152"),sQuery(id+"FQ5JFwxVdaqARUP_1.wireOp",EDGE,"fcba4419-a2ee-464f-be9d-58f11bf3418b.sketch_text.stroke-153"),sQuery(id+"FQ5JFwxVdaqARUP_1.wireOp",EDGE,"fcba4419-a2ee-464f-be9d-58f11bf3418b.sketch_text.stroke-154"),sQuery(id+"FQ5JFwxVdaqARUP_1.wireOp",EDGE,"fcba4419-a2ee-464f-be9d-58f11bf3418b.sketch_text.stroke-155"),sQuery(id+"FQ5JFwxVdaqARUP_1.wireOp",EDGE,"fcba4419-a2ee-464f-be9d-58f11bf3418b.sketch_text.stroke-156"),sQuery(id+"FQ5JFwxVdaqARUP_1.wireOp",EDGE,"fcba4419-a2ee-464f-be9d-58f11bf3418b.sketch_text.stroke-157"),sQuery(id+"FQ5JFwxVdaqARUP_1.wireOp",EDGE,"fcba4419-a2ee-464f-be9d-58f11bf3418b.sketch_text.stroke-158"),sQuery(id+"FQ5JFwxVdaqARUP_1.wireOp",EDGE,"fcba4419-a2ee-464f-be9d-58f11bf3418b.sketch_text.stroke-159"),sQuery(id+"FQ5JFwxVdaqARUP_1.wireOp",EDGE,"fcba4419-a2ee-464f-be9d-58f11bf3418b.sketch_text.stroke-160"),sQuery(id+"FQ5JFwxVdaqARUP_1.wireOp",EDGE,"fcba4419-a2ee-464f-be9d-58f11bf3418b.sketch_text.stroke-161"),sQuery(id+"FQ5JFwxVdaqARUP_1.wireOp",EDGE,"fcba4419-a2ee-464f-be9d-58f11bf3418b.sketch_text.stroke-162"),sQuery(id+"FQ5JFwxVdaqARUP_1.wireOp",EDGE,"fcba4419-a2ee-464f-be9d-58f11bf3418b.sketch_text.stroke-163"),sQuery(id+"FQ5JFwxVdaqARUP_1.wireOp",EDGE,"fcba4419-a2ee-464f-be9d-58f11bf3418b.sketch_text.stroke-164"),sQuery(id+"FQ5JFwxVdaqARUP_1.wireOp",EDGE,"fcba4419-a2ee-464f-be9d-58f11bf3418b.sketch_text.stroke-165"),sQuery(id+"FQ5JFwxVdaqARUP_1.wireOp",EDGE,"fcba4419-a2ee-464f-be9d-58f11bf3418b.sketch_text.stroke-166"),sQuery(id+"FQ5JFwxVdaqARUP_1.wireOp",EDGE,"fcba4419-a2ee-464f-be9d-58f11bf3418b.sketch_text.stroke-167"),sQuery(id+"FQ5JFwxVdaqARUP_1.wireOp",EDGE,"fcba4419-a2ee-464f-be9d-58f11bf3418b.sketch_text.stroke-168"),sQuery(id+"FQ5JFwxVdaqARUP_1.wireOp",EDGE,"fcba4419-a2ee-464f-be9d-58f11bf3418b.sketch_text.stroke-169"),sQuery(id+"FQ5JFwxVdaqARUP_1.wireOp",EDGE,"fcba4419-a2ee-464f-be9d-58f11bf3418b.sketch_text.stroke-170"),sQuery(id+"FQ5JFwxVdaqARUP_1.wireOp",EDGE,"fcba4419-a2ee-464f-be9d-58f11bf3418b.sketch_text.stroke-171"),sQuery(id+"FQ5JFwxVdaqARUP_1.wireOp",EDGE,"fcba4419-a2ee-464f-be9d-58f11bf3418b.sketch_text.stroke-172"),sQuery(id+"FQ5JFwxVdaqARUP_1.wireOp",EDGE,"fcba4419-a2ee-464f-be9d-58f11bf3418b.sketch_text.stroke-173"),sQuery(id+"FHMxAyK4CFUKdhS_1.wireOp",EDGE,"1cb9c079-ea9b-4899-8069-e0e3048e911d.sketch_text.stroke-0"),sQuery(id+"FHMxAyK4CFUKdhS_1.wireOp",EDGE,"1cb9c079-ea9b-4899-8069-e0e3048e911d.sketch_text.stroke-1"),sQuery(id+"FHMxAyK4CFUKdhS_1.wireOp",EDGE,"1cb9c079-ea9b-4899-8069-e0e3048e911d.sketch_text.stroke-2"),sQuery(id+"FHMxAyK4CFUKdhS_1.wireOp",EDGE,"1cb9c079-ea9b-4899-8069-e0e3048e911d.sketch_text.stroke-3"),sQuery(id+"FHMxAyK4CFUKdhS_1.wireOp",EDGE,"1cb9c079-ea9b-4899-8069-e0e3048e911d.sketch_text.stroke-4"),sQuery(id+"FHMxAyK4CFUKdhS_1.wireOp",EDGE,"1cb9c079-ea9b-4899-8069-e0e3048e911d.sketch_text.stroke-5"),sQuery(id+"FHMxAyK4CFUKdhS_1.wireOp",EDGE,"1cb9c079-ea9b-4899-8069-e0e3048e911d.sketch_text.stroke-6"),sQuery(id+"FHMxAyK4CFUKdhS_1.wireOp",EDGE,"1cb9c079-ea9b-4899-8069-e0e3048e911d.sketch_text.stroke-7"),sQuery(id+"FHMxAyK4CFUKdhS_1.wireOp",EDGE,"1cb9c079-ea9b-4899-8069-e0e3048e911d.sketch_text.stroke-8"),sQuery(id+"FHMxAyK4CFUKdhS_1.wireOp",EDGE,"1cb9c079-ea9b-4899-8069-e0e3048e911d.sketch_text.stroke-9"),sQuery(id+"FHMxAyK4CFUKdhS_1.wireOp",EDGE,"1cb9c079-ea9b-4899-8069-e0e3048e911d.sketch_text.stroke-10"),sQuery(id+"FHMxAyK4CFUKdhS_1.wireOp",EDGE,"1cb9c079-ea9b-4899-8069-e0e3048e911d.sketch_text.stroke-11"),sQuery(id+"FHMxAyK4CFUKdhS_1.wireOp",EDGE,"1cb9c079-ea9b-4899-8069-e0e3048e911d.sketch_text.stroke-12"),sQuery(id+"FHMxAyK4CFUKdhS_1.wireOp",EDGE,"1cb9c079-ea9b-4899-8069-e0e3048e911d.sketch_text.stroke-13"),sQuery(id+"FHMxAyK4CFUKdhS_1.wireOp",EDGE,"1cb9c079-ea9b-4899-8069-e0e3048e911d.sketch_text.stroke-14"),sQuery(id+"FHMxAyK4CFUKdhS_1.wireOp",EDGE,"1cb9c079-ea9b-4899-8069-e0e3048e911d.sketch_text.stroke-15"),sQuery(id+"FHMxAyK4CFUKdhS_1.wireOp",EDGE,"1cb9c079-ea9b-4899-8069-e0e3048e911d.sketch_text.stroke-16"),sQuery(id+"FHMxAyK4CFUKdhS_1.wireOp",EDGE,"1cb9c079-ea9b-4899-8069-e0e3048e911d.sketch_text.stroke-17"),sQuery(id+"FHMxAyK4CFUKdhS_1.wireOp",EDGE,"1cb9c079-ea9b-4899-8069-e0e3048e911d.sketch_text.stroke-18"),sQuery(id+"FHMxAyK4CFUKdhS_1.wireOp",EDGE,"1cb9c079-ea9b-4899-8069-e0e3048e911d.sketch_text.stroke-19"),sQuery(id+"FHMxAyK4CFUKdhS_1.wireOp",EDGE,"1cb9c079-ea9b-4899-8069-e0e3048e911d.sketch_text.stroke-20"),sQuery(id+"FHMxAyK4CFUKdhS_1.wireOp",EDGE,"1cb9c079-ea9b-4899-8069-e0e3048e911d.sketch_text.stroke-21"),sQuery(id+"FHMxAyK4CFUKdhS_1.wireOp",EDGE,"1cb9c079-ea9b-4899-8069-e0e3048e911d.sketch_text.stroke-22"),sQuery(id+"FHMxAyK4CFUKdhS_1.wireOp",EDGE,"1cb9c079-ea9b-4899-8069-e0e3048e911d.sketch_text.stroke-23"),sQuery(id+"FHMxAyK4CFUKdhS_1.wireOp",EDGE,"1cb9c079-ea9b-4899-8069-e0e3048e911d.sketch_text.stroke-24"),sQuery(id+"FHMxAyK4CFUKdhS_1.wireOp",EDGE,"1cb9c079-ea9b-4899-8069-e0e3048e911d.sketch_text.stroke-25"),sQuery(id+"FHMxAyK4CFUKdhS_1.wireOp",EDGE,"1cb9c079-ea9b-4899-8069-e0e3048e911d.sketch_text.stroke-26"),sQuery(id+"FHMxAyK4CFUKdhS_1.wireOp",EDGE,"1cb9c079-ea9b-4899-8069-e0e3048e911d.sketch_text.stroke-27"),sQuery(id+"FHMxAyK4CFUKdhS_1.wireOp",EDGE,"1cb9c079-ea9b-4899-8069-e0e3048e911d.sketch_text.stroke-28"),sQuery(id+"FHMxAyK4CFUKdhS_1.wireOp",EDGE,"1cb9c079-ea9b-4899-8069-e0e3048e911d.sketch_text.stroke-29"),sQuery(id+"FHMxAyK4CFUKdhS_1.wireOp",EDGE,"1cb9c079-ea9b-4899-8069-e0e3048e911d.sketch_text.stroke-30"),sQuery(id+"FHMxAyK4CFUKdhS_1.wireOp",EDGE,"1cb9c079-ea9b-4899-8069-e0e3048e911d.sketch_text.stroke-31"),sQuery(id+"FHMxAyK4CFUKdhS_1.wireOp",EDGE,"1cb9c079-ea9b-4899-8069-e0e3048e911d.sketch_text.stroke-32"),sQuery(id+"FHMxAyK4CFUKdhS_1.wireOp",EDGE,"1cb9c079-ea9b-4899-8069-e0e3048e911d.sketch_text.stroke-33"),sQuery(id+"FHMxAyK4CFUKdhS_1.wireOp",EDGE,"1cb9c079-ea9b-4899-8069-e0e3048e911d.sketch_text.stroke-34"),sQuery(id+"FHMxAyK4CFUKdhS_1.wireOp",EDGE,"1cb9c079-ea9b-4899-8069-e0e3048e911d.sketch_text.stroke-35"),sQuery(id+"FHMxAyK4CFUKdhS_1.wireOp",EDGE,"1cb9c079-ea9b-4899-8069-e0e3048e911d.sketch_text.stroke-36"),sQuery(id+"FHMxAyK4CFUKdhS_1.wireOp",EDGE,"1cb9c079-ea9b-4899-8069-e0e3048e911d.sketch_text.stroke-37"),sQuery(id+"FHMxAyK4CFUKdhS_1.wireOp",EDGE,"1cb9c079-ea9b-4899-8069-e0e3048e911d.sketch_text.stroke-38"),sQuery(id+"FHMxAyK4CFUKdhS_1.wireOp",EDGE,"1cb9c079-ea9b-4899-8069-e0e3048e911d.sketch_text.stroke-39"),sQuery(id+"FHMxAyK4CFUKdhS_1.wireOp",EDGE,"1cb9c079-ea9b-4899-8069-e0e3048e911d.sketch_text.stroke-40"),sQuery(id+"FHMxAyK4CFUKdhS_1.wireOp",EDGE,"1cb9c079-ea9b-4899-8069-e0e3048e911d.sketch_text.stroke-41"),sQuery(id+"FHMxAyK4CFUKdhS_1.wireOp",EDGE,"1cb9c079-ea9b-4899-8069-e0e3048e911d.sketch_text.stroke-42"),sQuery(id+"FHMxAyK4CFUKdhS_1.wireOp",EDGE,"1cb9c079-ea9b-4899-8069-e0e3048e911d.sketch_text.stroke-43"),sQuery(id+"FHMxAyK4CFUKdhS_1.wireOp",EDGE,"1cb9c079-ea9b-4899-8069-e0e3048e911d.sketch_text.stroke-44"),sQuery(id+"FHMxAyK4CFUKdhS_1.wireOp",EDGE,"1cb9c079-ea9b-4899-8069-e0e3048e911d.sketch_text.stroke-45"),sQuery(id+"FHMxAyK4CFUKdhS_1.wireOp",EDGE,"1cb9c079-ea9b-4899-8069-e0e3048e911d.sketch_text.stroke-46"),sQuery(id+"FHMxAyK4CFUKdhS_1.wireOp",EDGE,"1cb9c079-ea9b-4899-8069-e0e3048e911d.sketch_text.stroke-47"),sQuery(id+"FHMxAyK4CFUKdhS_1.wireOp",EDGE,"1cb9c079-ea9b-4899-8069-e0e3048e911d.sketch_text.stroke-48"),sQuery(id+"FHMxAyK4CFUKdhS_1.wireOp",EDGE,"1cb9c079-ea9b-4899-8069-e0e3048e911d.sketch_text.stroke-49"),sQuery(id+"FHMxAyK4CFUKdhS_1.wireOp",EDGE,"1cb9c079-ea9b-4899-8069-e0e3048e911d.sketch_text.stroke-50"),sQuery(id+"FHMxAyK4CFUKdhS_1.wireOp",EDGE,"1cb9c079-ea9b-4899-8069-e0e3048e911d.sketch_text.stroke-51"),sQuery(id+"FHMxAyK4CFUKdhS_1.wireOp",EDGE,"1cb9c079-ea9b-4899-8069-e0e3048e911d.sketch_text.stroke-52"),sQuery(id+"FHMxAyK4CFUKdhS_1.wireOp",EDGE,"1cb9c079-ea9b-4899-8069-e0e3048e911d.sketch_text.stroke-53"),sQuery(id+"FHMxAyK4CFUKdhS_1.wireOp",EDGE,"1cb9c079-ea9b-4899-8069-e0e3048e911d.sketch_text.stroke-54"),sQuery(id+"FHMxAyK4CFUKdhS_1.wireOp",EDGE,"1cb9c079-ea9b-4899-8069-e0e3048e911d.sketch_text.stroke-55"),sQuery(id+"FHMxAyK4CFUKdhS_1.wireOp",EDGE,"1cb9c079-ea9b-4899-8069-e0e3048e911d.sketch_text.stroke-56"),sQuery(id+"FHMxAyK4CFUKdhS_1.wireOp",EDGE,"1cb9c079-ea9b-4899-8069-e0e3048e911d.sketch_text.stroke-57"),sQuery(id+"FHMxAyK4CFUKdhS_1.wireOp",EDGE,"1cb9c079-ea9b-4899-8069-e0e3048e911d.sketch_text.stroke-58"),sQuery(id+"FHMxAyK4CFUKdhS_1.wireOp",EDGE,"1cb9c079-ea9b-4899-8069-e0e3048e911d.sketch_text.stroke-59"),sQuery(id+"FHMxAyK4CFUKdhS_1.wireOp",EDGE,"1cb9c079-ea9b-4899-8069-e0e3048e911d.sketch_text.stroke-60"),sQuery(id+"FHMxAyK4CFUKdhS_1.wireOp",EDGE,"1cb9c079-ea9b-4899-8069-e0e3048e911d.sketch_text.stroke-61"),sQuery(id+"FHMxAyK4CFUKdhS_1.wireOp",EDGE,"1cb9c079-ea9b-4899-8069-e0e3048e911d.sketch_text.stroke-62"),sQuery(id+"FHMxAyK4CFUKdhS_1.wireOp",EDGE,"1cb9c079-ea9b-4899-8069-e0e3048e911d.sketch_text.stroke-71"),sQuery(id+"FHMxAyK4CFUKdhS_1.wireOp",EDGE,"1cb9c079-ea9b-4899-8069-e0e3048e911d.sketch_text.stroke-72"),sQuery(id+"FHMxAyK4CFUKdhS_1.wireOp",EDGE,"1cb9c079-ea9b-4899-8069-e0e3048e911d.sketch_text.stroke-73"),sQuery(id+"FHMxAyK4CFUKdhS_1.wireOp",EDGE,"1cb9c079-ea9b-4899-8069-e0e3048e911d.sketch_text.stroke-74"),sQuery(id+"FHMxAyK4CFUKdhS_1.wireOp",EDGE,"1cb9c079-ea9b-4899-8069-e0e3048e911d.sketch_text.stroke-75"),sQuery(id+"FHMxAyK4CFUKdhS_1.wireOp",EDGE,"1cb9c079-ea9b-4899-8069-e0e3048e911d.sketch_text.stroke-76"),sQuery(id+"FHMxAyK4CFUKdhS_1.wireOp",EDGE,"1cb9c079-ea9b-4899-8069-e0e3048e911d.sketch_text.stroke-77"),sQuery(id+"FHMxAyK4CFUKdhS_1.wireOp",EDGE,"1cb9c079-ea9b-4899-8069-e0e3048e911d.sketch_text.stroke-78"),sQuery(id+"FHMxAyK4CFUKdhS_1.wireOp",EDGE,"1cb9c079-ea9b-4899-8069-e0e3048e911d.sketch_text.stroke-79"),sQuery(id+"FHMxAyK4CFUKdhS_1.wireOp",EDGE,"1cb9c079-ea9b-4899-8069-e0e3048e911d.sketch_text.stroke-80"),sQuery(id+"FHMxAyK4CFUKdhS_1.wireOp",EDGE,"1cb9c079-ea9b-4899-8069-e0e3048e911d.sketch_text.stroke-81"),sQuery(id+"FHMxAyK4CFUKdhS_1.wireOp",EDGE,"1cb9c079-ea9b-4899-8069-e0e3048e911d.sketch_text.stroke-82"),sQuery(id+"FHMxAyK4CFUKdhS_1.wireOp",EDGE,"1cb9c079-ea9b-4899-8069-e0e3048e911d.sketch_text.stroke-83"),sQuery(id+"FHMxAyK4CFUKdhS_1.wireOp",EDGE,"1cb9c079-ea9b-4899-8069-e0e3048e911d.sketch_text.stroke-84"),sQuery(id+"FHMxAyK4CFUKdhS_1.wireOp",EDGE,"1cb9c079-ea9b-4899-8069-e0e3048e911d.sketch_text.stroke-85"),sQuery(id+"FHMxAyK4CFUKdhS_1.wireOp",EDGE,"1cb9c079-ea9b-4899-8069-e0e3048e911d.sketch_text.stroke-86"),sQuery(id+"FHMxAyK4CFUKdhS_1.wireOp",EDGE,"1cb9c079-ea9b-4899-8069-e0e3048e911d.sketch_text.stroke-87"),sQuery(id+"FHMxAyK4CFUKdhS_1.wireOp",EDGE,"1cb9c079-ea9b-4899-8069-e0e3048e911d.sketch_text.stroke-88"),sQuery(id+"FHMxAyK4CFUKdhS_1.wireOp",EDGE,"1cb9c079-ea9b-4899-8069-e0e3048e911d.sketch_text.stroke-89"),sQuery(id+"FHMxAyK4CFUKdhS_1.wireOp",EDGE,"1cb9c079-ea9b-4899-8069-e0e3048e911d.sketch_text.stroke-90"),sQuery(id+"FHMxAyK4CFUKdhS_1.wireOp",EDGE,"1cb9c079-ea9b-4899-8069-e0e3048e911d.sketch_text.stroke-91"),sQuery(id+"FHMxAyK4CFUKdhS_1.wireOp",EDGE,"1cb9c079-ea9b-4899-8069-e0e3048e911d.sketch_text.stroke-92"),sQuery(id+"FHMxAyK4CFUKdhS_1.wireOp",EDGE,"1cb9c079-ea9b-4899-8069-e0e3048e911d.sketch_text.stroke-93"),sQuery(id+"FHMxAyK4CFUKdhS_1.wireOp",EDGE,"1cb9c079-ea9b-4899-8069-e0e3048e911d.sketch_text.stroke-94"),sQuery(id+"FHMxAyK4CFUKdhS_1.wireOp",EDGE,"1cb9c079-ea9b-4899-8069-e0e3048e911d.sketch_text.stroke-95"),sQuery(id+"FHMxAyK4CFUKdhS_1.wireOp",EDGE,"1cb9c079-ea9b-4899-8069-e0e3048e911d.sketch_text.stroke-96"),sQuery(id+"FHMxAyK4CFUKdhS_1.wireOp",EDGE,"1cb9c079-ea9b-4899-8069-e0e3048e911d.sketch_text.stroke-97"),sQuery(id+"FHMxAyK4CFUKdhS_1.wireOp",EDGE,"1cb9c079-ea9b-4899-8069-e0e3048e911d.sketch_text.stroke-103"),sQuery(id+"FHMxAyK4CFUKdhS_1.wireOp",EDGE,"1cb9c079-ea9b-4899-8069-e0e3048e911d.sketch_text.stroke-104"),sQuery(id+"FHMxAyK4CFUKdhS_1.wireOp",EDGE,"1cb9c079-ea9b-4899-8069-e0e3048e911d.sketch_text.stroke-105"),sQuery(id+"FHMxAyK4CFUKdhS_1.wireOp",EDGE,"1cb9c079-ea9b-4899-8069-e0e3048e911d.sketch_text.stroke-106"),sQuery(id+"FHMxAyK4CFUKdhS_1.wireOp",EDGE,"1cb9c079-ea9b-4899-8069-e0e3048e911d.sketch_text.stroke-107"),sQuery(id+"FHMxAyK4CFUKdhS_1.wireOp",EDGE,"1cb9c079-ea9b-4899-8069-e0e3048e911d.sketch_text.stroke-108"),sQuery(id+"FHMxAyK4CFUKdhS_1.wireOp",EDGE,"1cb9c079-ea9b-4899-8069-e0e3048e911d.sketch_text.stroke-109"),sQuery(id+"FHMxAyK4CFUKdhS_1.wireOp",EDGE,"1cb9c079-ea9b-4899-8069-e0e3048e911d.sketch_text.stroke-110"),sQuery(id+"FHMxAyK4CFUKdhS_1.wireOp",EDGE,"1cb9c079-ea9b-4899-8069-e0e3048e911d.sketch_text.stroke-111"),sQuery(id+"FHMxAyK4CFUKdhS_1.wireOp",EDGE,"1cb9c079-ea9b-4899-8069-e0e3048e911d.sketch_text.stroke-112"),sQuery(id+"FHMxAyK4CFUKdhS_1.wireOp",EDGE,"1cb9c079-ea9b-4899-8069-e0e3048e911d.sketch_text.stroke-113"),sQuery(id+"FHMxAyK4CFUKdhS_1.wireOp",EDGE,"1cb9c079-ea9b-4899-8069-e0e3048e911d.sketch_text.stroke-114"),sQuery(id+"FHMxAyK4CFUKdhS_1.wireOp",EDGE,"1cb9c079-ea9b-4899-8069-e0e3048e911d.sketch_text.stroke-115"),sQuery(id+"FHMxAyK4CFUKdhS_1.wireOp",EDGE,"1cb9c079-ea9b-4899-8069-e0e3048e911d.sketch_text.stroke-116"),sQuery(id+"FHMxAyK4CFUKdhS_1.wireOp",EDGE,"1cb9c079-ea9b-4899-8069-e0e3048e911d.sketch_text.stroke-117"),sQuery(id+"FHMxAyK4CFUKdhS_1.wireOp",EDGE,"1cb9c079-ea9b-4899-8069-e0e3048e911d.sketch_text.stroke-118"),sQuery(id+"FHMxAyK4CFUKdhS_1.wireOp",EDGE,"1cb9c079-ea9b-4899-8069-e0e3048e911d.sketch_text.stroke-119"),sQuery(id+"FHMxAyK4CFUKdhS_1.wireOp",EDGE,"1cb9c079-ea9b-4899-8069-e0e3048e911d.sketch_text.stroke-120"),sQuery(id+"FHMxAyK4CFUKdhS_1.wireOp",EDGE,"1cb9c079-ea9b-4899-8069-e0e3048e911d.sketch_text.stroke-121"),sQuery(id+"FHMxAyK4CFUKdhS_1.wireOp",EDGE,"1cb9c079-ea9b-4899-8069-e0e3048e911d.sketch_text.stroke-122"),sQuery(id+"FHMxAyK4CFUKdhS_1.wireOp",EDGE,"1cb9c079-ea9b-4899-8069-e0e3048e911d.sketch_text.stroke-123"),sQuery(id+"FHMxAyK4CFUKdhS_1.wireOp",EDGE,"1cb9c079-ea9b-4899-8069-e0e3048e911d.sketch_text.stroke-124"),sQuery(id+"FHMxAyK4CFUKdhS_1.wireOp",EDGE,"1cb9c079-ea9b-4899-8069-e0e3048e911d.sketch_text.stroke-125"),sQuery(id+"FHMxAyK4CFUKdhS_1.wireOp",EDGE,"1cb9c079-ea9b-4899-8069-e0e3048e911d.sketch_text.stroke-126"),sQuery(id+"FHMxAyK4CFUKdhS_1.wireOp",EDGE,"1cb9c079-ea9b-4899-8069-e0e3048e911d.sketch_text.stroke-127"),sQuery(id+"FHMxAyK4CFUKdhS_1.wireOp",EDGE,"1cb9c079-ea9b-4899-8069-e0e3048e911d.sketch_text.stroke-128"),sQuery(id+"FHMxAyK4CFUKdhS_1.wireOp",EDGE,"1cb9c079-ea9b-4899-8069-e0e3048e911d.sketch_text.stroke-129"),sQuery(id+"FHMxAyK4CFUKdhS_1.wireOp",EDGE,"1cb9c079-ea9b-4899-8069-e0e3048e911d.sketch_text.stroke-130"),sQuery(id+"FHMxAyK4CFUKdhS_1.wireOp",EDGE,"1cb9c079-ea9b-4899-8069-e0e3048e911d.sketch_text.stroke-131"),sQuery(id+"FHMxAyK4CFUKdhS_1.wireOp",EDGE,"1cb9c079-ea9b-4899-8069-e0e3048e911d.sketch_text.stroke-132"),sQuery(id+"FHMxAyK4CFUKdhS_1.wireOp",EDGE,"1cb9c079-ea9b-4899-8069-e0e3048e911d.sketch_text.stroke-133"),sQuery(id+"FHMxAyK4CFUKdhS_1.wireOp",EDGE,"1cb9c079-ea9b-4899-8069-e0e3048e911d.sketch_text.stroke-134"),sQuery(id+"FHMxAyK4CFUKdhS_1.wireOp",EDGE,"1cb9c079-ea9b-4899-8069-e0e3048e911d.sketch_text.stroke-135"),sQuery(id+"FHMxAyK4CFUKdhS_1.wireOp",EDGE,"1cb9c079-ea9b-4899-8069-e0e3048e911d.sketch_text.stroke-136"),sQuery(id+"FHMxAyK4CFUKdhS_1.wireOp",EDGE,"1cb9c079-ea9b-4899-8069-e0e3048e911d.sketch_text.stroke-137"),sQuery(id+"FHMxAyK4CFUKdhS_1.wireOp",EDGE,"1cb9c079-ea9b-4899-8069-e0e3048e911d.sketch_text.stroke-138"),sQuery(id+"FHMxAyK4CFUKdhS_1.wireOp",EDGE,"1cb9c079-ea9b-4899-8069-e0e3048e911d.sketch_text.stroke-139"),sQuery(id+"FHMxAyK4CFUKdhS_1.wireOp",EDGE,"1cb9c079-ea9b-4899-8069-e0e3048e911d.sketch_text.stroke-140"),sQuery(id+"FHMxAyK4CFUKdhS_1.wireOp",EDGE,"1cb9c079-ea9b-4899-8069-e0e3048e911d.sketch_text.stroke-141"),sQuery(id+"FHMxAyK4CFUKdhS_1.wireOp",EDGE,"1cb9c079-ea9b-4899-8069-e0e3048e911d.sketch_text.stroke-142"),sQuery(id+"FHMxAyK4CFUKdhS_1.wireOp",EDGE,"1cb9c079-ea9b-4899-8069-e0e3048e911d.sketch_text.stroke-143"),sQuery(id+"FHMxAyK4CFUKdhS_1.wireOp",EDGE,"1cb9c079-ea9b-4899-8069-e0e3048e911d.sketch_text.stroke-144"),sQuery(id+"FHMxAyK4CFUKdhS_1.wireOp",EDGE,"1cb9c079-ea9b-4899-8069-e0e3048e911d.sketch_text.stroke-145"),sQuery(id+"FHMxAyK4CFUKdhS_1.wireOp",EDGE,"1cb9c079-ea9b-4899-8069-e0e3048e911d.sketch_text.stroke-146"),sQuery(id+"FHMxAyK4CFUKdhS_1.wireOp",EDGE,"1cb9c079-ea9b-4899-8069-e0e3048e911d.sketch_text.stroke-147"),sQuery(id+"FHMxAyK4CFUKdhS_1.wireOp",EDGE,"1cb9c079-ea9b-4899-8069-e0e3048e911d.sketch_text.stroke-148"),sQuery(id+"FHMxAyK4CFUKdhS_1.wireOp",EDGE,"1cb9c079-ea9b-4899-8069-e0e3048e911d.sketch_text.stroke-149"),sQuery(id+"FHMxAyK4CFUKdhS_1.wireOp",EDGE,"1cb9c079-ea9b-4899-8069-e0e3048e911d.sketch_text.stroke-150"),sQuery(id+"FHMxAyK4CFUKdhS_1.wireOp",EDGE,"1cb9c079-ea9b-4899-8069-e0e3048e911d.sketch_text.stroke-151"),sQuery(id+"FHMxAyK4CFUKdhS_1.wireOp",EDGE,"1cb9c079-ea9b-4899-8069-e0e3048e911d.sketch_text.stroke-152"),sQuery(id+"FHMxAyK4CFUKdhS_1.wireOp",EDGE,"1cb9c079-ea9b-4899-8069-e0e3048e911d.sketch_text.stroke-153"),sQuery(id+"FHMxAyK4CFUKdhS_1.wireOp",EDGE,"1cb9c079-ea9b-4899-8069-e0e3048e911d.sketch_text.stroke-159"),sQuery(id+"FHMxAyK4CFUKdhS_1.wireOp",EDGE,"1cb9c079-ea9b-4899-8069-e0e3048e911d.sketch_text.stroke-160"),sQuery(id+"FHMxAyK4CFUKdhS_1.wireOp",EDGE,"1cb9c079-ea9b-4899-8069-e0e3048e911d.sketch_text.stroke-161"),sQuery(id+"FHMxAyK4CFUKdhS_1.wireOp",EDGE,"1cb9c079-ea9b-4899-8069-e0e3048e911d.sketch_text.stroke-162"),sQuery(id+"FHMxAyK4CFUKdhS_1.wireOp",EDGE,"1cb9c079-ea9b-4899-8069-e0e3048e911d.sketch_text.stroke-163"),sQuery(id+"FHMxAyK4CFUKdhS_1.wireOp",EDGE,"1cb9c079-ea9b-4899-8069-e0e3048e911d.sketch_text.stroke-164"),sQuery(id+"FHMxAyK4CFUKdhS_1.wireOp",EDGE,"1cb9c079-ea9b-4899-8069-e0e3048e911d.sketch_text.stroke-165"),sQuery(id+"FHMxAyK4CFUKdhS_1.wireOp",EDGE,"1cb9c079-ea9b-4899-8069-e0e3048e911d.sketch_text.stroke-166"),sQuery(id+"FHMxAyK4CFUKdhS_1.wireOp",EDGE,"1cb9c079-ea9b-4899-8069-e0e3048e911d.sketch_text.stroke-167"),sQuery(id+"FHMxAyK4CFUKdhS_1.wireOp",EDGE,"1cb9c079-ea9b-4899-8069-e0e3048e911d.sketch_text.stroke-168"),sQuery(id+"FHMxAyK4CFUKdhS_1.wireOp",EDGE,"1cb9c079-ea9b-4899-8069-e0e3048e911d.sketch_text.stroke-169"),sQuery(id+"FHMxAyK4CFUKdhS_1.wireOp",EDGE,"1cb9c079-ea9b-4899-8069-e0e3048e911d.sketch_text.stroke-170"),sQuery(id+"FHMxAyK4CFUKdhS_1.wireOp",EDGE,"1cb9c079-ea9b-4899-8069-e0e3048e911d.sketch_text.stroke-171"),sQuery(id+"FHMxAyK4CFUKdhS_1.wireOp",EDGE,"1cb9c079-ea9b-4899-8069-e0e3048e911d.sketch_text.stroke-172"),sQuery(id+"FHMxAyK4CFUKdhS_1.wireOp",EDGE,"1cb9c079-ea9b-4899-8069-e0e3048e911d.sketch_text.stroke-173"),sQuery(id+"FHMxAyK4CFUKdhS_1.wireOp",EDGE,"1cb9c079-ea9b-4899-8069-e0e3048e911d.sketch_text.stroke-174"),sQuery(id+"FHMxAyK4CFUKdhS_1.wireOp",EDGE,"1cb9c079-ea9b-4899-8069-e0e3048e911d.sketch_text.stroke-175"),sQuery(id+"FHMxAyK4CFUKdhS_1.wireOp",EDGE,"1cb9c079-ea9b-4899-8069-e0e3048e911d.sketch_text.stroke-176"),sQuery(id+"FHMxAyK4CFUKdhS_1.wireOp",EDGE,"1cb9c079-ea9b-4899-8069-e0e3048e911d.sketch_text.stroke-177"),sQuery(id+"FHMxAyK4CFUKdhS_1.wireOp",EDGE,"1cb9c079-ea9b-4899-8069-e0e3048e911d.sketch_text.stroke-178"),sQuery(id+"FHMxAyK4CFUKdhS_1.wireOp",EDGE,"1cb9c079-ea9b-4899-8069-e0e3048e911d.sketch_text.stroke-179"),sQuery(id+"FHMxAyK4CFUKdhS_1.wireOp",EDGE,"1cb9c079-ea9b-4899-8069-e0e3048e911d.sketch_text.stroke-180"),subQ0,sQuery(id+"F2.wireOp",EDGE,"6ee83ff3-586e-4dbe-aaea-af71240543bd")])],"isStart":true})])],"derivedFrom":makeQuery(id+"F3.opExtrude","CAP_EDGE",EDGE,{"disambiguationData":[OSD([subQ0])],"isStart":true})});}
            var Q1;
            Q1=makeQuery(id+"F1.opExtrude","CAP_EDGE",EDGE,{"disambiguationData":[OSD([sQuery(id+"F0.wireOp",EDGE,"E0.left")])],"isStart":false});
            var Q2;
            {var subQ0=sQuery(id+"F0.wireOp",EDGE,"E0.top");var subQ1=sQuery(id+"F0.wireOp",EDGE,"E0.bottom");var subQ2=sQuery(id+"F2.wireOp",EDGE,"8007402e-1a4e-4a06-85a5-2af08e553504");Q2=makeQuery(id+"F3.boolean.opBoolean","SPLIT",EDGE,{"disambiguationData":[TD([makeQuery(id+"F1.opExtrude","CAP_FACE",FACE,{"disambiguationData":[OSD([subQ1,subQ0,sQuery(id+"F0.wireOp",EDGE,"E0.left"),sQuery(id+"F0.wireOp",EDGE,"E0.right")])],"isStart":false}),makeQuery(id+"F1.opExtrude","SWEPT_FACE",FACE,{"disambiguationData":[OSD([subQ0])]}),makeQuery(id+"F3.opExtrude","SWEPT_FACE",FACE,{"disambiguationData":[OSD([subQ2])]}),makeQuery(id+"F3.opExtrude","CAP_FACE",FACE,{"disambiguationData":[OSD([subQ1,sQuery(id+"FQ5JFwxVdaqARUP_1.wireOp",EDGE,"fcba4419-a2ee-464f-be9d-58f11bf3418b.sketch_text.stroke-0"),sQuery(id+"FQ5JFwxVdaqARUP_1.wireOp",EDGE,"fcba4419-a2ee-464f-be9d-58f11bf3418b.sketch_text.stroke-1"),sQuery(id+"FQ5JFwxVdaqARUP_1.wireOp",EDGE,"fcba4419-a2ee-464f-be9d-58f11bf3418b.sketch_text.stroke-2"),sQuery(id+"FQ5JFwxVdaqARUP_1.wireOp",EDGE,"fcba4419-a2ee-464f-be9d-58f11bf3418b.sketch_text.stroke-3"),sQuery(id+"FQ5JFwxVdaqARUP_1.wireOp",EDGE,"fcba4419-a2ee-464f-be9d-58f11bf3418b.sketch_text.stroke-4"),sQuery(id+"FQ5JFwxVdaqARUP_1.wireOp",EDGE,"fcba4419-a2ee-464f-be9d-58f11bf3418b.sketch_text.stroke-5"),sQuery(id+"FQ5JFwxVdaqARUP_1.wireOp",EDGE,"fcba4419-a2ee-464f-be9d-58f11bf3418b.sketch_text.stroke-6"),sQuery(id+"FQ5JFwxVdaqARUP_1.wireOp",EDGE,"fcba4419-a2ee-464f-be9d-58f11bf3418b.sketch_text.stroke-7"),sQuery(id+"FQ5JFwxVdaqARUP_1.wireOp",EDGE,"fcba4419-a2ee-464f-be9d-58f11bf3418b.sketch_text.stroke-8"),sQuery(id+"FQ5JFwxVdaqARUP_1.wireOp",EDGE,"fcba4419-a2ee-464f-be9d-58f11bf3418b.sketch_text.stroke-9"),sQuery(id+"FQ5JFwxVdaqARUP_1.wireOp",EDGE,"fcba4419-a2ee-464f-be9d-58f11bf3418b.sketch_text.stroke-10"),sQuery(id+"FQ5JFwxVdaqARUP_1.wireOp",EDGE,"fcba4419-a2ee-464f-be9d-58f11bf3418b.sketch_text.stroke-11"),sQuery(id+"FQ5JFwxVdaqARUP_1.wireOp",EDGE,"fcba4419-a2ee-464f-be9d-58f11bf3418b.sketch_text.stroke-12"),sQuery(id+"FQ5JFwxVdaqARUP_1.wireOp",EDGE,"fcba4419-a2ee-464f-be9d-58f11bf3418b.sketch_text.stroke-13"),sQuery(id+"FQ5JFwxVdaqARUP_1.wireOp",EDGE,"fcba4419-a2ee-464f-be9d-58f11bf3418b.sketch_text.stroke-14"),sQuery(id+"FQ5JFwxVdaqARUP_1.wireOp",EDGE,"fcba4419-a2ee-464f-be9d-58f11bf3418b.sketch_text.stroke-15"),sQuery(id+"FQ5JFwxVdaqARUP_1.wireOp",EDGE,"fcba4419-a2ee-464f-be9d-58f11bf3418b.sketch_text.stroke-16"),sQuery(id+"FQ5JFwxVdaqARUP_1.wireOp",EDGE,"fcba4419-a2ee-464f-be9d-58f11bf3418b.sketch_text.stroke-17"),sQuery(id+"FQ5JFwxVdaqARUP_1.wireOp",EDGE,"fcba4419-a2ee-464f-be9d-58f11bf3418b.sketch_text.stroke-18"),sQuery(id+"FQ5JFwxVdaqARUP_1.wireOp",EDGE,"fcba4419-a2ee-464f-be9d-58f11bf3418b.sketch_text.stroke-19"),sQuery(id+"FQ5JFwxVdaqARUP_1.wireOp",EDGE,"fcba4419-a2ee-464f-be9d-58f11bf3418b.sketch_text.stroke-20"),sQuery(id+"FQ5JFwxVdaqARUP_1.wireOp",EDGE,"fcba4419-a2ee-464f-be9d-58f11bf3418b.sketch_text.stroke-21"),sQuery(id+"FQ5JFwxVdaqARUP_1.wireOp",EDGE,"fcba4419-a2ee-464f-be9d-58f11bf3418b.sketch_text.stroke-22"),sQuery(id+"FQ5JFwxVdaqARUP_1.wireOp",EDGE,"fcba4419-a2ee-464f-be9d-58f11bf3418b.sketch_text.stroke-23"),sQuery(id+"FQ5JFwxVdaqARUP_1.wireOp",EDGE,"fcba4419-a2ee-464f-be9d-58f11bf3418b.sketch_text.stroke-24"),sQuery(id+"FQ5JFwxVdaqARUP_1.wireOp",EDGE,"fcba4419-a2ee-464f-be9d-58f11bf3418b.sketch_text.stroke-25"),sQuery(id+"FQ5JFwxVdaqARUP_1.wireOp",EDGE,"fcba4419-a2ee-464f-be9d-58f11bf3418b.sketch_text.stroke-26"),sQuery(id+"FQ5JFwxVdaqARUP_1.wireOp",EDGE,"fcba4419-a2ee-464f-be9d-58f11bf3418b.sketch_text.stroke-27"),sQuery(id+"FQ5JFwxVdaqARUP_1.wireOp",EDGE,"fcba4419-a2ee-464f-be9d-58f11bf3418b.sketch_text.stroke-28"),sQuery(id+"FQ5JFwxVdaqARUP_1.wireOp",EDGE,"fcba4419-a2ee-464f-be9d-58f11bf3418b.sketch_text.stroke-29"),sQuery(id+"FQ5JFwxVdaqARUP_1.wireOp",EDGE,"fcba4419-a2ee-464f-be9d-58f11bf3418b.sketch_text.stroke-30"),sQuery(id+"FQ5JFwxVdaqARUP_1.wireOp",EDGE,"fcba4419-a2ee-464f-be9d-58f11bf3418b.sketch_text.stroke-31"),sQuery(id+"FQ5JFwxVdaqARUP_1.wireOp",EDGE,"fcba4419-a2ee-464f-be9d-58f11bf3418b.sketch_text.stroke-32"),sQuery(id+"FQ5JFwxVdaqARUP_1.wireOp",EDGE,"fcba4419-a2ee-464f-be9d-58f11bf3418b.sketch_text.stroke-33"),sQuery(id+"FQ5JFwxVdaqARUP_1.wireOp",EDGE,"fcba4419-a2ee-464f-be9d-58f11bf3418b.sketch_text.stroke-34"),sQuery(id+"FQ5JFwxVdaqARUP_1.wireOp",EDGE,"fcba4419-a2ee-464f-be9d-58f11bf3418b.sketch_text.stroke-35"),sQuery(id+"FQ5JFwxVdaqARUP_1.wireOp",EDGE,"fcba4419-a2ee-464f-be9d-58f11bf3418b.sketch_text.stroke-36"),sQuery(id+"FQ5JFwxVdaqARUP_1.wireOp",EDGE,"fcba4419-a2ee-464f-be9d-58f11bf3418b.sketch_text.stroke-37"),sQuery(id+"FQ5JFwxVdaqARUP_1.wireOp",EDGE,"fcba4419-a2ee-464f-be9d-58f11bf3418b.sketch_text.stroke-38"),sQuery(id+"FQ5JFwxVdaqARUP_1.wireOp",EDGE,"fcba4419-a2ee-464f-be9d-58f11bf3418b.sketch_text.stroke-39"),sQuery(id+"FQ5JFwxVdaqARUP_1.wireOp",EDGE,"fcba4419-a2ee-464f-be9d-58f11bf3418b.sketch_text.stroke-40"),sQuery(id+"FQ5JFwxVdaqARUP_1.wireOp",EDGE,"fcba4419-a2ee-464f-be9d-58f11bf3418b.sketch_text.stroke-41"),sQuery(id+"FQ5JFwxVdaqARUP_1.wireOp",EDGE,"fcba4419-a2ee-464f-be9d-58f11bf3418b.sketch_text.stroke-42"),sQuery(id+"FQ5JFwxVdaqARUP_1.wireOp",EDGE,"fcba4419-a2ee-464f-be9d-58f11bf3418b.sketch_text.stroke-43"),sQuery(id+"FQ5JFwxVdaqARUP_1.wireOp",EDGE,"fcba4419-a2ee-464f-be9d-58f11bf3418b.sketch_text.stroke-44"),sQuery(id+"FQ5JFwxVdaqARUP_1.wireOp",EDGE,"fcba4419-a2ee-464f-be9d-58f11bf3418b.sketch_text.stroke-45"),sQuery(id+"FQ5JFwxVdaqARUP_1.wireOp",EDGE,"fcba4419-a2ee-464f-be9d-58f11bf3418b.sketch_text.stroke-46"),sQuery(id+"FQ5JFwxVdaqARUP_1.wireOp",EDGE,"fcba4419-a2ee-464f-be9d-58f11bf3418b.sketch_text.stroke-47"),sQuery(id+"FQ5JFwxVdaqARUP_1.wireOp",EDGE,"fcba4419-a2ee-464f-be9d-58f11bf3418b.sketch_text.stroke-48"),sQuery(id+"FQ5JFwxVdaqARUP_1.wireOp",EDGE,"fcba4419-a2ee-464f-be9d-58f11bf3418b.sketch_text.stroke-49"),sQuery(id+"FQ5JFwxVdaqARUP_1.wireOp",EDGE,"fcba4419-a2ee-464f-be9d-58f11bf3418b.sketch_text.stroke-50"),sQuery(id+"FQ5JFwxVdaqARUP_1.wireOp",EDGE,"fcba4419-a2ee-464f-be9d-58f11bf3418b.sketch_text.stroke-51"),sQuery(id+"FQ5JFwxVdaqARUP_1.wireOp",EDGE,"fcba4419-a2ee-464f-be9d-58f11bf3418b.sketch_text.stroke-52"),sQuery(id+"FQ5JFwxVdaqARUP_1.wireOp",EDGE,"fcba4419-a2ee-464f-be9d-58f11bf3418b.sketch_text.stroke-53"),sQuery(id+"FQ5JFwxVdaqARUP_1.wireOp",EDGE,"fcba4419-a2ee-464f-be9d-58f11bf3418b.sketch_text.stroke-54"),sQuery(id+"FQ5JFwxVdaqARUP_1.wireOp",EDGE,"fcba4419-a2ee-464f-be9d-58f11bf3418b.sketch_text.stroke-55"),sQuery(id+"FQ5JFwxVdaqARUP_1.wireOp",EDGE,"fcba4419-a2ee-464f-be9d-58f11bf3418b.sketch_text.stroke-56"),sQuery(id+"FQ5JFwxVdaqARUP_1.wireOp",EDGE,"fcba4419-a2ee-464f-be9d-58f11bf3418b.sketch_text.stroke-57"),sQuery(id+"FQ5JFwxVdaqARUP_1.wireOp",EDGE,"fcba4419-a2ee-464f-be9d-58f11bf3418b.sketch_text.stroke-58"),sQuery(id+"FQ5JFwxVdaqARUP_1.wireOp",EDGE,"fcba4419-a2ee-464f-be9d-58f11bf3418b.sketch_text.stroke-59"),sQuery(id+"FQ5JFwxVdaqARUP_1.wireOp",EDGE,"fcba4419-a2ee-464f-be9d-58f11bf3418b.sketch_text.stroke-60"),sQuery(id+"FQ5JFwxVdaqARUP_1.wireOp",EDGE,"fcba4419-a2ee-464f-be9d-58f11bf3418b.sketch_text.stroke-61"),sQuery(id+"FQ5JFwxVdaqARUP_1.wireOp",EDGE,"fcba4419-a2ee-464f-be9d-58f11bf3418b.sketch_text.stroke-62"),sQuery(id+"FQ5JFwxVdaqARUP_1.wireOp",EDGE,"fcba4419-a2ee-464f-be9d-58f11bf3418b.sketch_text.stroke-63"),sQuery(id+"FQ5JFwxVdaqARUP_1.wireOp",EDGE,"fcba4419-a2ee-464f-be9d-58f11bf3418b.sketch_text.stroke-64"),sQuery(id+"FQ5JFwxVdaqARUP_1.wireOp",EDGE,"fcba4419-a2ee-464f-be9d-58f11bf3418b.sketch_text.stroke-65"),sQuery(id+"FQ5JFwxVdaqARUP_1.wireOp",EDGE,"fcba4419-a2ee-464f-be9d-58f11bf3418b.sketch_text.stroke-66"),sQuery(id+"FQ5JFwxVdaqARUP_1.wireOp",EDGE,"fcba4419-a2ee-464f-be9d-58f11bf3418b.sketch_text.stroke-67"),sQuery(id+"FQ5JFwxVdaqARUP_1.wireOp",EDGE,"fcba4419-a2ee-464f-be9d-58f11bf3418b.sketch_text.stroke-68"),sQuery(id+"FQ5JFwxVdaqARUP_1.wireOp",EDGE,"fcba4419-a2ee-464f-be9d-58f11bf3418b.sketch_text.stroke-69"),sQuery(id+"FQ5JFwxVdaqARUP_1.wireOp",EDGE,"fcba4419-a2ee-464f-be9d-58f11bf3418b.sketch_text.stroke-70"),sQuery(id+"FQ5JFwxVdaqARUP_1.wireOp",EDGE,"fcba4419-a2ee-464f-be9d-58f11bf3418b.sketch_text.stroke-71"),sQuery(id+"FQ5JFwxVdaqARUP_1.wireOp",EDGE,"fcba4419-a2ee-464f-be9d-58f11bf3418b.sketch_text.stroke-72"),sQuery(id+"FQ5JFwxVdaqARUP_1.wireOp",EDGE,"fcba4419-a2ee-464f-be9d-58f11bf3418b.sketch_text.stroke-73"),sQuery(id+"FQ5JFwxVdaqARUP_1.wireOp",EDGE,"fcba4419-a2ee-464f-be9d-58f11bf3418b.sketch_text.stroke-74"),sQuery(id+"FQ5JFwxVdaqARUP_1.wireOp",EDGE,"fcba4419-a2ee-464f-be9d-58f11bf3418b.sketch_text.stroke-75"),sQuery(id+"FQ5JFwxVdaqARUP_1.wireOp",EDGE,"fcba4419-a2ee-464f-be9d-58f11bf3418b.sketch_text.stroke-76"),sQuery(id+"FQ5JFwxVdaqARUP_1.wireOp",EDGE,"fcba4419-a2ee-464f-be9d-58f11bf3418b.sketch_text.stroke-77"),sQuery(id+"FQ5JFwxVdaqARUP_1.wireOp",EDGE,"fcba4419-a2ee-464f-be9d-58f11bf3418b.sketch_text.stroke-78"),sQuery(id+"FQ5JFwxVdaqARUP_1.wireOp",EDGE,"fcba4419-a2ee-464f-be9d-58f11bf3418b.sketch_text.stroke-79"),sQuery(id+"FQ5JFwxVdaqARUP_1.wireOp",EDGE,"fcba4419-a2ee-464f-be9d-58f11bf3418b.sketch_text.stroke-80"),sQuery(id+"FQ5JFwxVdaqARUP_1.wireOp",EDGE,"fcba4419-a2ee-464f-be9d-58f11bf3418b.sketch_text.stroke-81"),sQuery(id+"FQ5JFwxVdaqARUP_1.wireOp",EDGE,"fcba4419-a2ee-464f-be9d-58f11bf3418b.sketch_text.stroke-82"),sQuery(id+"FQ5JFwxVdaqARUP_1.wireOp",EDGE,"fcba4419-a2ee-464f-be9d-58f11bf3418b.sketch_text.stroke-83"),sQuery(id+"FQ5JFwxVdaqARUP_1.wireOp",EDGE,"fcba4419-a2ee-464f-be9d-58f11bf3418b.sketch_text.stroke-84"),sQuery(id+"FQ5JFwxVdaqARUP_1.wireOp",EDGE,"fcba4419-a2ee-464f-be9d-58f11bf3418b.sketch_text.stroke-85"),sQuery(id+"FQ5JFwxVdaqARUP_1.wireOp",EDGE,"fcba4419-a2ee-464f-be9d-58f11bf3418b.sketch_text.stroke-86"),sQuery(id+"FQ5JFwxVdaqARUP_1.wireOp",EDGE,"fcba4419-a2ee-464f-be9d-58f11bf3418b.sketch_text.stroke-87"),sQuery(id+"FQ5JFwxVdaqARUP_1.wireOp",EDGE,"fcba4419-a2ee-464f-be9d-58f11bf3418b.sketch_text.stroke-88"),sQuery(id+"FQ5JFwxVdaqARUP_1.wireOp",EDGE,"fcba4419-a2ee-464f-be9d-58f11bf3418b.sketch_text.stroke-89"),sQuery(id+"FQ5JFwxVdaqARUP_1.wireOp",EDGE,"fcba4419-a2ee-464f-be9d-58f11bf3418b.sketch_text.stroke-90"),sQuery(id+"FQ5JFwxVdaqARUP_1.wireOp",EDGE,"fcba4419-a2ee-464f-be9d-58f11bf3418b.sketch_text.stroke-91"),sQuery(id+"FQ5JFwxVdaqARUP_1.wireOp",EDGE,"fcba4419-a2ee-464f-be9d-58f11bf3418b.sketch_text.stroke-92"),sQuery(id+"FQ5JFwxVdaqARUP_1.wireOp",EDGE,"fcba4419-a2ee-464f-be9d-58f11bf3418b.sketch_text.stroke-93"),sQuery(id+"FQ5JFwxVdaqARUP_1.wireOp",EDGE,"fcba4419-a2ee-464f-be9d-58f11bf3418b.sketch_text.stroke-94"),sQuery(id+"FQ5JFwxVdaqARUP_1.wireOp",EDGE,"fcba4419-a2ee-464f-be9d-58f11bf3418b.sketch_text.stroke-95"),sQuery(id+"FQ5JFwxVdaqARUP_1.wireOp",EDGE,"fcba4419-a2ee-464f-be9d-58f11bf3418b.sketch_text.stroke-96"),sQuery(id+"FQ5JFwxVdaqARUP_1.wireOp",EDGE,"fcba4419-a2ee-464f-be9d-58f11bf3418b.sketch_text.stroke-97"),sQuery(id+"FQ5JFwxVdaqARUP_1.wireOp",EDGE,"fcba4419-a2ee-464f-be9d-58f11bf3418b.sketch_text.stroke-98"),sQuery(id+"FQ5JFwxVdaqARUP_1.wireOp",EDGE,"fcba4419-a2ee-464f-be9d-58f11bf3418b.sketch_text.stroke-99"),sQuery(id+"FQ5JFwxVdaqARUP_1.wireOp",EDGE,"fcba4419-a2ee-464f-be9d-58f11bf3418b.sketch_text.stroke-100"),sQuery(id+"FQ5JFwxVdaqARUP_1.wireOp",EDGE,"fcba4419-a2ee-464f-be9d-58f11bf3418b.sketch_text.stroke-101"),sQuery(id+"FQ5JFwxVdaqARUP_1.wireOp",EDGE,"fcba4419-a2ee-464f-be9d-58f11bf3418b.sketch_text.stroke-102"),sQuery(id+"FQ5JFwxVdaqARUP_1.wireOp",EDGE,"fcba4419-a2ee-464f-be9d-58f11bf3418b.sketch_text.stroke-103"),sQuery(id+"FQ5JFwxVdaqARUP_1.wireOp",EDGE,"fcba4419-a2ee-464f-be9d-58f11bf3418b.sketch_text.stroke-104"),sQuery(id+"FQ5JFwxVdaqARUP_1.wireOp",EDGE,"fcba4419-a2ee-464f-be9d-58f11bf3418b.sketch_text.stroke-105"),sQuery(id+"FQ5JFwxVdaqARUP_1.wireOp",EDGE,"fcba4419-a2ee-464f-be9d-58f11bf3418b.sketch_text.stroke-106"),sQuery(id+"FQ5JFwxVdaqARUP_1.wireOp",EDGE,"fcba4419-a2ee-464f-be9d-58f11bf3418b.sketch_text.stroke-107"),sQuery(id+"FQ5JFwxVdaqARUP_1.wireOp",EDGE,"fcba4419-a2ee-464f-be9d-58f11bf3418b.sketch_text.stroke-108"),sQuery(id+"FQ5JFwxVdaqARUP_1.wireOp",EDGE,"fcba4419-a2ee-464f-be9d-58f11bf3418b.sketch_text.stroke-109"),sQuery(id+"FQ5JFwxVdaqARUP_1.wireOp",EDGE,"fcba4419-a2ee-464f-be9d-58f11bf3418b.sketch_text.stroke-110"),sQuery(id+"FQ5JFwxVdaqARUP_1.wireOp",EDGE,"fcba4419-a2ee-464f-be9d-58f11bf3418b.sketch_text.stroke-111"),sQuery(id+"FQ5JFwxVdaqARUP_1.wireOp",EDGE,"fcba4419-a2ee-464f-be9d-58f11bf3418b.sketch_text.stroke-112"),sQuery(id+"FQ5JFwxVdaqARUP_1.wireOp",EDGE,"fcba4419-a2ee-464f-be9d-58f11bf3418b.sketch_text.stroke-113"),sQuery(id+"FQ5JFwxVdaqARUP_1.wireOp",EDGE,"fcba4419-a2ee-464f-be9d-58f11bf3418b.sketch_text.stroke-114"),sQuery(id+"FQ5JFwxVdaqARUP_1.wireOp",EDGE,"fcba4419-a2ee-464f-be9d-58f11bf3418b.sketch_text.stroke-115"),sQuery(id+"FQ5JFwxVdaqARUP_1.wireOp",EDGE,"fcba4419-a2ee-464f-be9d-58f11bf3418b.sketch_text.stroke-116"),sQuery(id+"FQ5JFwxVdaqARUP_1.wireOp",EDGE,"fcba4419-a2ee-464f-be9d-58f11bf3418b.sketch_text.stroke-117"),sQuery(id+"FQ5JFwxVdaqARUP_1.wireOp",EDGE,"fcba4419-a2ee-464f-be9d-58f11bf3418b.sketch_text.stroke-118"),sQuery(id+"FQ5JFwxVdaqARUP_1.wireOp",EDGE,"fcba4419-a2ee-464f-be9d-58f11bf3418b.sketch_text.stroke-119"),sQuery(id+"FQ5JFwxVdaqARUP_1.wireOp",EDGE,"fcba4419-a2ee-464f-be9d-58f11bf3418b.sketch_text.stroke-120"),sQuery(id+"FQ5JFwxVdaqARUP_1.wireOp",EDGE,"fcba4419-a2ee-464f-be9d-58f11bf3418b.sketch_text.stroke-121"),sQuery(id+"FQ5JFwxVdaqARUP_1.wireOp",EDGE,"fcba4419-a2ee-464f-be9d-58f11bf3418b.sketch_text.stroke-122"),sQuery(id+"FQ5JFwxVdaqARUP_1.wireOp",EDGE,"fcba4419-a2ee-464f-be9d-58f11bf3418b.sketch_text.stroke-123"),sQuery(id+"FQ5JFwxVdaqARUP_1.wireOp",EDGE,"fcba4419-a2ee-464f-be9d-58f11bf3418b.sketch_text.stroke-124"),sQuery(id+"FQ5JFwxVdaqARUP_1.wireOp",EDGE,"fcba4419-a2ee-464f-be9d-58f11bf3418b.sketch_text.stroke-125"),sQuery(id+"FQ5JFwxVdaqARUP_1.wireOp",EDGE,"fcba4419-a2ee-464f-be9d-58f11bf3418b.sketch_text.stroke-126"),sQuery(id+"FQ5JFwxVdaqARUP_1.wireOp",EDGE,"fcba4419-a2ee-464f-be9d-58f11bf3418b.sketch_text.stroke-127"),sQuery(id+"FQ5JFwxVdaqARUP_1.wireOp",EDGE,"fcba4419-a2ee-464f-be9d-58f11bf3418b.sketch_text.stroke-128"),sQuery(id+"FQ5JFwxVdaqARUP_1.wireOp",EDGE,"fcba4419-a2ee-464f-be9d-58f11bf3418b.sketch_text.stroke-129"),sQuery(id+"FQ5JFwxVdaqARUP_1.wireOp",EDGE,"fcba4419-a2ee-464f-be9d-58f11bf3418b.sketch_text.stroke-130"),sQuery(id+"FQ5JFwxVdaqARUP_1.wireOp",EDGE,"fcba4419-a2ee-464f-be9d-58f11bf3418b.sketch_text.stroke-131"),sQuery(id+"FQ5JFwxVdaqARUP_1.wireOp",EDGE,"fcba4419-a2ee-464f-be9d-58f11bf3418b.sketch_text.stroke-132"),sQuery(id+"FQ5JFwxVdaqARUP_1.wireOp",EDGE,"fcba4419-a2ee-464f-be9d-58f11bf3418b.sketch_text.stroke-133"),sQuery(id+"FQ5JFwxVdaqARUP_1.wireOp",EDGE,"fcba4419-a2ee-464f-be9d-58f11bf3418b.sketch_text.stroke-134"),sQuery(id+"FQ5JFwxVdaqARUP_1.wireOp",EDGE,"fcba4419-a2ee-464f-be9d-58f11bf3418b.sketch_text.stroke-135"),sQuery(id+"FQ5JFwxVdaqARUP_1.wireOp",EDGE,"fcba4419-a2ee-464f-be9d-58f11bf3418b.sketch_text.stroke-136"),sQuery(id+"FQ5JFwxVdaqARUP_1.wireOp",EDGE,"fcba4419-a2ee-464f-be9d-58f11bf3418b.sketch_text.stroke-137"),sQuery(id+"FQ5JFwxVdaqARUP_1.wireOp",EDGE,"fcba4419-a2ee-464f-be9d-58f11bf3418b.sketch_text.stroke-138"),sQuery(id+"FQ5JFwxVdaqARUP_1.wireOp",EDGE,"fcba4419-a2ee-464f-be9d-58f11bf3418b.sketch_text.stroke-139"),sQuery(id+"FQ5JFwxVdaqARUP_1.wireOp",EDGE,"fcba4419-a2ee-464f-be9d-58f11bf3418b.sketch_text.stroke-140"),sQuery(id+"FQ5JFwxVdaqARUP_1.wireOp",EDGE,"fcba4419-a2ee-464f-be9d-58f11bf3418b.sketch_text.stroke-141"),sQuery(id+"FQ5JFwxVdaqARUP_1.wireOp",EDGE,"fcba4419-a2ee-464f-be9d-58f11bf3418b.sketch_text.stroke-142"),sQuery(id+"FQ5JFwxVdaqARUP_1.wireOp",EDGE,"fcba4419-a2ee-464f-be9d-58f11bf3418b.sketch_text.stroke-143"),sQuery(id+"FQ5JFwxVdaqARUP_1.wireOp",EDGE,"fcba4419-a2ee-464f-be9d-58f11bf3418b.sketch_text.stroke-144"),sQuery(id+"FQ5JFwxVdaqARUP_1.wireOp",EDGE,"fcba4419-a2ee-464f-be9d-58f11bf3418b.sketch_text.stroke-145"),sQuery(id+"FQ5JFwxVdaqARUP_1.wireOp",EDGE,"fcba4419-a2ee-464f-be9d-58f11bf3418b.sketch_text.stroke-146"),sQuery(id+"FQ5JFwxVdaqARUP_1.wireOp",EDGE,"fcba4419-a2ee-464f-be9d-58f11bf3418b.sketch_text.stroke-147"),sQuery(id+"FQ5JFwxVdaqARUP_1.wireOp",EDGE,"fcba4419-a2ee-464f-be9d-58f11bf3418b.sketch_text.stroke-148"),sQuery(id+"FQ5JFwxVdaqARUP_1.wireOp",EDGE,"fcba4419-a2ee-464f-be9d-58f11bf3418b.sketch_text.stroke-149"),sQuery(id+"FQ5JFwxVdaqARUP_1.wireOp",EDGE,"fcba4419-a2ee-464f-be9d-58f11bf3418b.sketch_text.stroke-150"),sQuery(id+"FQ5JFwxVdaqARUP_1.wireOp",EDGE,"fcba4419-a2ee-464f-be9d-58f11bf3418b.sketch_text.stroke-151"),sQuery(id+"FQ5JFwxVdaqARUP_1.wireOp",EDGE,"fcba4419-a2ee-464f-be9d-58f11bf3418b.sketch_text.stroke-152"),sQuery(id+"FQ5JFwxVdaqARUP_1.wireOp",EDGE,"fcba4419-a2ee-464f-be9d-58f11bf3418b.sketch_text.stroke-153"),sQuery(id+"FQ5JFwxVdaqARUP_1.wireOp",EDGE,"fcba4419-a2ee-464f-be9d-58f11bf3418b.sketch_text.stroke-154"),sQuery(id+"FQ5JFwxVdaqARUP_1.wireOp",EDGE,"fcba4419-a2ee-464f-be9d-58f11bf3418b.sketch_text.stroke-155"),sQuery(id+"FQ5JFwxVdaqARUP_1.wireOp",EDGE,"fcba4419-a2ee-464f-be9d-58f11bf3418b.sketch_text.stroke-156"),sQuery(id+"FQ5JFwxVdaqARUP_1.wireOp",EDGE,"fcba4419-a2ee-464f-be9d-58f11bf3418b.sketch_text.stroke-157"),sQuery(id+"FQ5JFwxVdaqARUP_1.wireOp",EDGE,"fcba4419-a2ee-464f-be9d-58f11bf3418b.sketch_text.stroke-158"),sQuery(id+"FQ5JFwxVdaqARUP_1.wireOp",EDGE,"fcba4419-a2ee-464f-be9d-58f11bf3418b.sketch_text.stroke-159"),sQuery(id+"FQ5JFwxVdaqARUP_1.wireOp",EDGE,"fcba4419-a2ee-464f-be9d-58f11bf3418b.sketch_text.stroke-160"),sQuery(id+"FQ5JFwxVdaqARUP_1.wireOp",EDGE,"fcba4419-a2ee-464f-be9d-58f11bf3418b.sketch_text.stroke-161"),sQuery(id+"FQ5JFwxVdaqARUP_1.wireOp",EDGE,"fcba4419-a2ee-464f-be9d-58f11bf3418b.sketch_text.stroke-162"),sQuery(id+"FQ5JFwxVdaqARUP_1.wireOp",EDGE,"fcba4419-a2ee-464f-be9d-58f11bf3418b.sketch_text.stroke-163"),sQuery(id+"FQ5JFwxVdaqARUP_1.wireOp",EDGE,"fcba4419-a2ee-464f-be9d-58f11bf3418b.sketch_text.stroke-164"),sQuery(id+"FQ5JFwxVdaqARUP_1.wireOp",EDGE,"fcba4419-a2ee-464f-be9d-58f11bf3418b.sketch_text.stroke-165"),sQuery(id+"FQ5JFwxVdaqARUP_1.wireOp",EDGE,"fcba4419-a2ee-464f-be9d-58f11bf3418b.sketch_text.stroke-166"),sQuery(id+"FQ5JFwxVdaqARUP_1.wireOp",EDGE,"fcba4419-a2ee-464f-be9d-58f11bf3418b.sketch_text.stroke-167"),sQuery(id+"FQ5JFwxVdaqARUP_1.wireOp",EDGE,"fcba4419-a2ee-464f-be9d-58f11bf3418b.sketch_text.stroke-168"),sQuery(id+"FQ5JFwxVdaqARUP_1.wireOp",EDGE,"fcba4419-a2ee-464f-be9d-58f11bf3418b.sketch_text.stroke-169"),sQuery(id+"FQ5JFwxVdaqARUP_1.wireOp",EDGE,"fcba4419-a2ee-464f-be9d-58f11bf3418b.sketch_text.stroke-170"),sQuery(id+"FQ5JFwxVdaqARUP_1.wireOp",EDGE,"fcba4419-a2ee-464f-be9d-58f11bf3418b.sketch_text.stroke-171"),sQuery(id+"FQ5JFwxVdaqARUP_1.wireOp",EDGE,"fcba4419-a2ee-464f-be9d-58f11bf3418b.sketch_text.stroke-172"),sQuery(id+"FQ5JFwxVdaqARUP_1.wireOp",EDGE,"fcba4419-a2ee-464f-be9d-58f11bf3418b.sketch_text.stroke-173"),sQuery(id+"FHMxAyK4CFUKdhS_1.wireOp",EDGE,"1cb9c079-ea9b-4899-8069-e0e3048e911d.sketch_text.stroke-0"),sQuery(id+"FHMxAyK4CFUKdhS_1.wireOp",EDGE,"1cb9c079-ea9b-4899-8069-e0e3048e911d.sketch_text.stroke-1"),sQuery(id+"FHMxAyK4CFUKdhS_1.wireOp",EDGE,"1cb9c079-ea9b-4899-8069-e0e3048e911d.sketch_text.stroke-2"),sQuery(id+"FHMxAyK4CFUKdhS_1.wireOp",EDGE,"1cb9c079-ea9b-4899-8069-e0e3048e911d.sketch_text.stroke-3"),sQuery(id+"FHMxAyK4CFUKdhS_1.wireOp",EDGE,"1cb9c079-ea9b-4899-8069-e0e3048e911d.sketch_text.stroke-4"),sQuery(id+"FHMxAyK4CFUKdhS_1.wireOp",EDGE,"1cb9c079-ea9b-4899-8069-e0e3048e911d.sketch_text.stroke-5"),sQuery(id+"FHMxAyK4CFUKdhS_1.wireOp",EDGE,"1cb9c079-ea9b-4899-8069-e0e3048e911d.sketch_text.stroke-6"),sQuery(id+"FHMxAyK4CFUKdhS_1.wireOp",EDGE,"1cb9c079-ea9b-4899-8069-e0e3048e911d.sketch_text.stroke-7"),sQuery(id+"FHMxAyK4CFUKdhS_1.wireOp",EDGE,"1cb9c079-ea9b-4899-8069-e0e3048e911d.sketch_text.stroke-8"),sQuery(id+"FHMxAyK4CFUKdhS_1.wireOp",EDGE,"1cb9c079-ea9b-4899-8069-e0e3048e911d.sketch_text.stroke-9"),sQuery(id+"FHMxAyK4CFUKdhS_1.wireOp",EDGE,"1cb9c079-ea9b-4899-8069-e0e3048e911d.sketch_text.stroke-10"),sQuery(id+"FHMxAyK4CFUKdhS_1.wireOp",EDGE,"1cb9c079-ea9b-4899-8069-e0e3048e911d.sketch_text.stroke-11"),sQuery(id+"FHMxAyK4CFUKdhS_1.wireOp",EDGE,"1cb9c079-ea9b-4899-8069-e0e3048e911d.sketch_text.stroke-12"),sQuery(id+"FHMxAyK4CFUKdhS_1.wireOp",EDGE,"1cb9c079-ea9b-4899-8069-e0e3048e911d.sketch_text.stroke-13"),sQuery(id+"FHMxAyK4CFUKdhS_1.wireOp",EDGE,"1cb9c079-ea9b-4899-8069-e0e3048e911d.sketch_text.stroke-14"),sQuery(id+"FHMxAyK4CFUKdhS_1.wireOp",EDGE,"1cb9c079-ea9b-4899-8069-e0e3048e911d.sketch_text.stroke-15"),sQuery(id+"FHMxAyK4CFUKdhS_1.wireOp",EDGE,"1cb9c079-ea9b-4899-8069-e0e3048e911d.sketch_text.stroke-16"),sQuery(id+"FHMxAyK4CFUKdhS_1.wireOp",EDGE,"1cb9c079-ea9b-4899-8069-e0e3048e911d.sketch_text.stroke-17"),sQuery(id+"FHMxAyK4CFUKdhS_1.wireOp",EDGE,"1cb9c079-ea9b-4899-8069-e0e3048e911d.sketch_text.stroke-18"),sQuery(id+"FHMxAyK4CFUKdhS_1.wireOp",EDGE,"1cb9c079-ea9b-4899-8069-e0e3048e911d.sketch_text.stroke-19"),sQuery(id+"FHMxAyK4CFUKdhS_1.wireOp",EDGE,"1cb9c079-ea9b-4899-8069-e0e3048e911d.sketch_text.stroke-20"),sQuery(id+"FHMxAyK4CFUKdhS_1.wireOp",EDGE,"1cb9c079-ea9b-4899-8069-e0e3048e911d.sketch_text.stroke-21"),sQuery(id+"FHMxAyK4CFUKdhS_1.wireOp",EDGE,"1cb9c079-ea9b-4899-8069-e0e3048e911d.sketch_text.stroke-22"),sQuery(id+"FHMxAyK4CFUKdhS_1.wireOp",EDGE,"1cb9c079-ea9b-4899-8069-e0e3048e911d.sketch_text.stroke-23"),sQuery(id+"FHMxAyK4CFUKdhS_1.wireOp",EDGE,"1cb9c079-ea9b-4899-8069-e0e3048e911d.sketch_text.stroke-24"),sQuery(id+"FHMxAyK4CFUKdhS_1.wireOp",EDGE,"1cb9c079-ea9b-4899-8069-e0e3048e911d.sketch_text.stroke-25"),sQuery(id+"FHMxAyK4CFUKdhS_1.wireOp",EDGE,"1cb9c079-ea9b-4899-8069-e0e3048e911d.sketch_text.stroke-26"),sQuery(id+"FHMxAyK4CFUKdhS_1.wireOp",EDGE,"1cb9c079-ea9b-4899-8069-e0e3048e911d.sketch_text.stroke-27"),sQuery(id+"FHMxAyK4CFUKdhS_1.wireOp",EDGE,"1cb9c079-ea9b-4899-8069-e0e3048e911d.sketch_text.stroke-28"),sQuery(id+"FHMxAyK4CFUKdhS_1.wireOp",EDGE,"1cb9c079-ea9b-4899-8069-e0e3048e911d.sketch_text.stroke-29"),sQuery(id+"FHMxAyK4CFUKdhS_1.wireOp",EDGE,"1cb9c079-ea9b-4899-8069-e0e3048e911d.sketch_text.stroke-30"),sQuery(id+"FHMxAyK4CFUKdhS_1.wireOp",EDGE,"1cb9c079-ea9b-4899-8069-e0e3048e911d.sketch_text.stroke-31"),sQuery(id+"FHMxAyK4CFUKdhS_1.wireOp",EDGE,"1cb9c079-ea9b-4899-8069-e0e3048e911d.sketch_text.stroke-32"),sQuery(id+"FHMxAyK4CFUKdhS_1.wireOp",EDGE,"1cb9c079-ea9b-4899-8069-e0e3048e911d.sketch_text.stroke-33"),sQuery(id+"FHMxAyK4CFUKdhS_1.wireOp",EDGE,"1cb9c079-ea9b-4899-8069-e0e3048e911d.sketch_text.stroke-34"),sQuery(id+"FHMxAyK4CFUKdhS_1.wireOp",EDGE,"1cb9c079-ea9b-4899-8069-e0e3048e911d.sketch_text.stroke-35"),sQuery(id+"FHMxAyK4CFUKdhS_1.wireOp",EDGE,"1cb9c079-ea9b-4899-8069-e0e3048e911d.sketch_text.stroke-36"),sQuery(id+"FHMxAyK4CFUKdhS_1.wireOp",EDGE,"1cb9c079-ea9b-4899-8069-e0e3048e911d.sketch_text.stroke-37"),sQuery(id+"FHMxAyK4CFUKdhS_1.wireOp",EDGE,"1cb9c079-ea9b-4899-8069-e0e3048e911d.sketch_text.stroke-38"),sQuery(id+"FHMxAyK4CFUKdhS_1.wireOp",EDGE,"1cb9c079-ea9b-4899-8069-e0e3048e911d.sketch_text.stroke-39"),sQuery(id+"FHMxAyK4CFUKdhS_1.wireOp",EDGE,"1cb9c079-ea9b-4899-8069-e0e3048e911d.sketch_text.stroke-40"),sQuery(id+"FHMxAyK4CFUKdhS_1.wireOp",EDGE,"1cb9c079-ea9b-4899-8069-e0e3048e911d.sketch_text.stroke-41"),sQuery(id+"FHMxAyK4CFUKdhS_1.wireOp",EDGE,"1cb9c079-ea9b-4899-8069-e0e3048e911d.sketch_text.stroke-42"),sQuery(id+"FHMxAyK4CFUKdhS_1.wireOp",EDGE,"1cb9c079-ea9b-4899-8069-e0e3048e911d.sketch_text.stroke-43"),sQuery(id+"FHMxAyK4CFUKdhS_1.wireOp",EDGE,"1cb9c079-ea9b-4899-8069-e0e3048e911d.sketch_text.stroke-44"),sQuery(id+"FHMxAyK4CFUKdhS_1.wireOp",EDGE,"1cb9c079-ea9b-4899-8069-e0e3048e911d.sketch_text.stroke-45"),sQuery(id+"FHMxAyK4CFUKdhS_1.wireOp",EDGE,"1cb9c079-ea9b-4899-8069-e0e3048e911d.sketch_text.stroke-46"),sQuery(id+"FHMxAyK4CFUKdhS_1.wireOp",EDGE,"1cb9c079-ea9b-4899-8069-e0e3048e911d.sketch_text.stroke-47"),sQuery(id+"FHMxAyK4CFUKdhS_1.wireOp",EDGE,"1cb9c079-ea9b-4899-8069-e0e3048e911d.sketch_text.stroke-48"),sQuery(id+"FHMxAyK4CFUKdhS_1.wireOp",EDGE,"1cb9c079-ea9b-4899-8069-e0e3048e911d.sketch_text.stroke-49"),sQuery(id+"FHMxAyK4CFUKdhS_1.wireOp",EDGE,"1cb9c079-ea9b-4899-8069-e0e3048e911d.sketch_text.stroke-50"),sQuery(id+"FHMxAyK4CFUKdhS_1.wireOp",EDGE,"1cb9c079-ea9b-4899-8069-e0e3048e911d.sketch_text.stroke-51"),sQuery(id+"FHMxAyK4CFUKdhS_1.wireOp",EDGE,"1cb9c079-ea9b-4899-8069-e0e3048e911d.sketch_text.stroke-52"),sQuery(id+"FHMxAyK4CFUKdhS_1.wireOp",EDGE,"1cb9c079-ea9b-4899-8069-e0e3048e911d.sketch_text.stroke-53"),sQuery(id+"FHMxAyK4CFUKdhS_1.wireOp",EDGE,"1cb9c079-ea9b-4899-8069-e0e3048e911d.sketch_text.stroke-54"),sQuery(id+"FHMxAyK4CFUKdhS_1.wireOp",EDGE,"1cb9c079-ea9b-4899-8069-e0e3048e911d.sketch_text.stroke-55"),sQuery(id+"FHMxAyK4CFUKdhS_1.wireOp",EDGE,"1cb9c079-ea9b-4899-8069-e0e3048e911d.sketch_text.stroke-56"),sQuery(id+"FHMxAyK4CFUKdhS_1.wireOp",EDGE,"1cb9c079-ea9b-4899-8069-e0e3048e911d.sketch_text.stroke-57"),sQuery(id+"FHMxAyK4CFUKdhS_1.wireOp",EDGE,"1cb9c079-ea9b-4899-8069-e0e3048e911d.sketch_text.stroke-58"),sQuery(id+"FHMxAyK4CFUKdhS_1.wireOp",EDGE,"1cb9c079-ea9b-4899-8069-e0e3048e911d.sketch_text.stroke-59"),sQuery(id+"FHMxAyK4CFUKdhS_1.wireOp",EDGE,"1cb9c079-ea9b-4899-8069-e0e3048e911d.sketch_text.stroke-60"),sQuery(id+"FHMxAyK4CFUKdhS_1.wireOp",EDGE,"1cb9c079-ea9b-4899-8069-e0e3048e911d.sketch_text.stroke-61"),sQuery(id+"FHMxAyK4CFUKdhS_1.wireOp",EDGE,"1cb9c079-ea9b-4899-8069-e0e3048e911d.sketch_text.stroke-62"),sQuery(id+"FHMxAyK4CFUKdhS_1.wireOp",EDGE,"1cb9c079-ea9b-4899-8069-e0e3048e911d.sketch_text.stroke-71"),sQuery(id+"FHMxAyK4CFUKdhS_1.wireOp",EDGE,"1cb9c079-ea9b-4899-8069-e0e3048e911d.sketch_text.stroke-72"),sQuery(id+"FHMxAyK4CFUKdhS_1.wireOp",EDGE,"1cb9c079-ea9b-4899-8069-e0e3048e911d.sketch_text.stroke-73"),sQuery(id+"FHMxAyK4CFUKdhS_1.wireOp",EDGE,"1cb9c079-ea9b-4899-8069-e0e3048e911d.sketch_text.stroke-74"),sQuery(id+"FHMxAyK4CFUKdhS_1.wireOp",EDGE,"1cb9c079-ea9b-4899-8069-e0e3048e911d.sketch_text.stroke-75"),sQuery(id+"FHMxAyK4CFUKdhS_1.wireOp",EDGE,"1cb9c079-ea9b-4899-8069-e0e3048e911d.sketch_text.stroke-76"),sQuery(id+"FHMxAyK4CFUKdhS_1.wireOp",EDGE,"1cb9c079-ea9b-4899-8069-e0e3048e911d.sketch_text.stroke-77"),sQuery(id+"FHMxAyK4CFUKdhS_1.wireOp",EDGE,"1cb9c079-ea9b-4899-8069-e0e3048e911d.sketch_text.stroke-78"),sQuery(id+"FHMxAyK4CFUKdhS_1.wireOp",EDGE,"1cb9c079-ea9b-4899-8069-e0e3048e911d.sketch_text.stroke-79"),sQuery(id+"FHMxAyK4CFUKdhS_1.wireOp",EDGE,"1cb9c079-ea9b-4899-8069-e0e3048e911d.sketch_text.stroke-80"),sQuery(id+"FHMxAyK4CFUKdhS_1.wireOp",EDGE,"1cb9c079-ea9b-4899-8069-e0e3048e911d.sketch_text.stroke-81"),sQuery(id+"FHMxAyK4CFUKdhS_1.wireOp",EDGE,"1cb9c079-ea9b-4899-8069-e0e3048e911d.sketch_text.stroke-82"),sQuery(id+"FHMxAyK4CFUKdhS_1.wireOp",EDGE,"1cb9c079-ea9b-4899-8069-e0e3048e911d.sketch_text.stroke-83"),sQuery(id+"FHMxAyK4CFUKdhS_1.wireOp",EDGE,"1cb9c079-ea9b-4899-8069-e0e3048e911d.sketch_text.stroke-84"),sQuery(id+"FHMxAyK4CFUKdhS_1.wireOp",EDGE,"1cb9c079-ea9b-4899-8069-e0e3048e911d.sketch_text.stroke-85"),sQuery(id+"FHMxAyK4CFUKdhS_1.wireOp",EDGE,"1cb9c079-ea9b-4899-8069-e0e3048e911d.sketch_text.stroke-86"),sQuery(id+"FHMxAyK4CFUKdhS_1.wireOp",EDGE,"1cb9c079-ea9b-4899-8069-e0e3048e911d.sketch_text.stroke-87"),sQuery(id+"FHMxAyK4CFUKdhS_1.wireOp",EDGE,"1cb9c079-ea9b-4899-8069-e0e3048e911d.sketch_text.stroke-88"),sQuery(id+"FHMxAyK4CFUKdhS_1.wireOp",EDGE,"1cb9c079-ea9b-4899-8069-e0e3048e911d.sketch_text.stroke-89"),sQuery(id+"FHMxAyK4CFUKdhS_1.wireOp",EDGE,"1cb9c079-ea9b-4899-8069-e0e3048e911d.sketch_text.stroke-90"),sQuery(id+"FHMxAyK4CFUKdhS_1.wireOp",EDGE,"1cb9c079-ea9b-4899-8069-e0e3048e911d.sketch_text.stroke-91"),sQuery(id+"FHMxAyK4CFUKdhS_1.wireOp",EDGE,"1cb9c079-ea9b-4899-8069-e0e3048e911d.sketch_text.stroke-92"),sQuery(id+"FHMxAyK4CFUKdhS_1.wireOp",EDGE,"1cb9c079-ea9b-4899-8069-e0e3048e911d.sketch_text.stroke-93"),sQuery(id+"FHMxAyK4CFUKdhS_1.wireOp",EDGE,"1cb9c079-ea9b-4899-8069-e0e3048e911d.sketch_text.stroke-94"),sQuery(id+"FHMxAyK4CFUKdhS_1.wireOp",EDGE,"1cb9c079-ea9b-4899-8069-e0e3048e911d.sketch_text.stroke-95"),sQuery(id+"FHMxAyK4CFUKdhS_1.wireOp",EDGE,"1cb9c079-ea9b-4899-8069-e0e3048e911d.sketch_text.stroke-96"),sQuery(id+"FHMxAyK4CFUKdhS_1.wireOp",EDGE,"1cb9c079-ea9b-4899-8069-e0e3048e911d.sketch_text.stroke-97"),sQuery(id+"FHMxAyK4CFUKdhS_1.wireOp",EDGE,"1cb9c079-ea9b-4899-8069-e0e3048e911d.sketch_text.stroke-103"),sQuery(id+"FHMxAyK4CFUKdhS_1.wireOp",EDGE,"1cb9c079-ea9b-4899-8069-e0e3048e911d.sketch_text.stroke-104"),sQuery(id+"FHMxAyK4CFUKdhS_1.wireOp",EDGE,"1cb9c079-ea9b-4899-8069-e0e3048e911d.sketch_text.stroke-105"),sQuery(id+"FHMxAyK4CFUKdhS_1.wireOp",EDGE,"1cb9c079-ea9b-4899-8069-e0e3048e911d.sketch_text.stroke-106"),sQuery(id+"FHMxAyK4CFUKdhS_1.wireOp",EDGE,"1cb9c079-ea9b-4899-8069-e0e3048e911d.sketch_text.stroke-107"),sQuery(id+"FHMxAyK4CFUKdhS_1.wireOp",EDGE,"1cb9c079-ea9b-4899-8069-e0e3048e911d.sketch_text.stroke-108"),sQuery(id+"FHMxAyK4CFUKdhS_1.wireOp",EDGE,"1cb9c079-ea9b-4899-8069-e0e3048e911d.sketch_text.stroke-109"),sQuery(id+"FHMxAyK4CFUKdhS_1.wireOp",EDGE,"1cb9c079-ea9b-4899-8069-e0e3048e911d.sketch_text.stroke-110"),sQuery(id+"FHMxAyK4CFUKdhS_1.wireOp",EDGE,"1cb9c079-ea9b-4899-8069-e0e3048e911d.sketch_text.stroke-111"),sQuery(id+"FHMxAyK4CFUKdhS_1.wireOp",EDGE,"1cb9c079-ea9b-4899-8069-e0e3048e911d.sketch_text.stroke-112"),sQuery(id+"FHMxAyK4CFUKdhS_1.wireOp",EDGE,"1cb9c079-ea9b-4899-8069-e0e3048e911d.sketch_text.stroke-113"),sQuery(id+"FHMxAyK4CFUKdhS_1.wireOp",EDGE,"1cb9c079-ea9b-4899-8069-e0e3048e911d.sketch_text.stroke-114"),sQuery(id+"FHMxAyK4CFUKdhS_1.wireOp",EDGE,"1cb9c079-ea9b-4899-8069-e0e3048e911d.sketch_text.stroke-115"),sQuery(id+"FHMxAyK4CFUKdhS_1.wireOp",EDGE,"1cb9c079-ea9b-4899-8069-e0e3048e911d.sketch_text.stroke-116"),sQuery(id+"FHMxAyK4CFUKdhS_1.wireOp",EDGE,"1cb9c079-ea9b-4899-8069-e0e3048e911d.sketch_text.stroke-117"),sQuery(id+"FHMxAyK4CFUKdhS_1.wireOp",EDGE,"1cb9c079-ea9b-4899-8069-e0e3048e911d.sketch_text.stroke-118"),sQuery(id+"FHMxAyK4CFUKdhS_1.wireOp",EDGE,"1cb9c079-ea9b-4899-8069-e0e3048e911d.sketch_text.stroke-119"),sQuery(id+"FHMxAyK4CFUKdhS_1.wireOp",EDGE,"1cb9c079-ea9b-4899-8069-e0e3048e911d.sketch_text.stroke-120"),sQuery(id+"FHMxAyK4CFUKdhS_1.wireOp",EDGE,"1cb9c079-ea9b-4899-8069-e0e3048e911d.sketch_text.stroke-121"),sQuery(id+"FHMxAyK4CFUKdhS_1.wireOp",EDGE,"1cb9c079-ea9b-4899-8069-e0e3048e911d.sketch_text.stroke-122"),sQuery(id+"FHMxAyK4CFUKdhS_1.wireOp",EDGE,"1cb9c079-ea9b-4899-8069-e0e3048e911d.sketch_text.stroke-123"),sQuery(id+"FHMxAyK4CFUKdhS_1.wireOp",EDGE,"1cb9c079-ea9b-4899-8069-e0e3048e911d.sketch_text.stroke-124"),sQuery(id+"FHMxAyK4CFUKdhS_1.wireOp",EDGE,"1cb9c079-ea9b-4899-8069-e0e3048e911d.sketch_text.stroke-125"),sQuery(id+"FHMxAyK4CFUKdhS_1.wireOp",EDGE,"1cb9c079-ea9b-4899-8069-e0e3048e911d.sketch_text.stroke-126"),sQuery(id+"FHMxAyK4CFUKdhS_1.wireOp",EDGE,"1cb9c079-ea9b-4899-8069-e0e3048e911d.sketch_text.stroke-127"),sQuery(id+"FHMxAyK4CFUKdhS_1.wireOp",EDGE,"1cb9c079-ea9b-4899-8069-e0e3048e911d.sketch_text.stroke-128"),sQuery(id+"FHMxAyK4CFUKdhS_1.wireOp",EDGE,"1cb9c079-ea9b-4899-8069-e0e3048e911d.sketch_text.stroke-129"),sQuery(id+"FHMxAyK4CFUKdhS_1.wireOp",EDGE,"1cb9c079-ea9b-4899-8069-e0e3048e911d.sketch_text.stroke-130"),sQuery(id+"FHMxAyK4CFUKdhS_1.wireOp",EDGE,"1cb9c079-ea9b-4899-8069-e0e3048e911d.sketch_text.stroke-131"),sQuery(id+"FHMxAyK4CFUKdhS_1.wireOp",EDGE,"1cb9c079-ea9b-4899-8069-e0e3048e911d.sketch_text.stroke-132"),sQuery(id+"FHMxAyK4CFUKdhS_1.wireOp",EDGE,"1cb9c079-ea9b-4899-8069-e0e3048e911d.sketch_text.stroke-133"),sQuery(id+"FHMxAyK4CFUKdhS_1.wireOp",EDGE,"1cb9c079-ea9b-4899-8069-e0e3048e911d.sketch_text.stroke-134"),sQuery(id+"FHMxAyK4CFUKdhS_1.wireOp",EDGE,"1cb9c079-ea9b-4899-8069-e0e3048e911d.sketch_text.stroke-135"),sQuery(id+"FHMxAyK4CFUKdhS_1.wireOp",EDGE,"1cb9c079-ea9b-4899-8069-e0e3048e911d.sketch_text.stroke-136"),sQuery(id+"FHMxAyK4CFUKdhS_1.wireOp",EDGE,"1cb9c079-ea9b-4899-8069-e0e3048e911d.sketch_text.stroke-137"),sQuery(id+"FHMxAyK4CFUKdhS_1.wireOp",EDGE,"1cb9c079-ea9b-4899-8069-e0e3048e911d.sketch_text.stroke-138"),sQuery(id+"FHMxAyK4CFUKdhS_1.wireOp",EDGE,"1cb9c079-ea9b-4899-8069-e0e3048e911d.sketch_text.stroke-139"),sQuery(id+"FHMxAyK4CFUKdhS_1.wireOp",EDGE,"1cb9c079-ea9b-4899-8069-e0e3048e911d.sketch_text.stroke-140"),sQuery(id+"FHMxAyK4CFUKdhS_1.wireOp",EDGE,"1cb9c079-ea9b-4899-8069-e0e3048e911d.sketch_text.stroke-141"),sQuery(id+"FHMxAyK4CFUKdhS_1.wireOp",EDGE,"1cb9c079-ea9b-4899-8069-e0e3048e911d.sketch_text.stroke-142"),sQuery(id+"FHMxAyK4CFUKdhS_1.wireOp",EDGE,"1cb9c079-ea9b-4899-8069-e0e3048e911d.sketch_text.stroke-143"),sQuery(id+"FHMxAyK4CFUKdhS_1.wireOp",EDGE,"1cb9c079-ea9b-4899-8069-e0e3048e911d.sketch_text.stroke-144"),sQuery(id+"FHMxAyK4CFUKdhS_1.wireOp",EDGE,"1cb9c079-ea9b-4899-8069-e0e3048e911d.sketch_text.stroke-145"),sQuery(id+"FHMxAyK4CFUKdhS_1.wireOp",EDGE,"1cb9c079-ea9b-4899-8069-e0e3048e911d.sketch_text.stroke-146"),sQuery(id+"FHMxAyK4CFUKdhS_1.wireOp",EDGE,"1cb9c079-ea9b-4899-8069-e0e3048e911d.sketch_text.stroke-147"),sQuery(id+"FHMxAyK4CFUKdhS_1.wireOp",EDGE,"1cb9c079-ea9b-4899-8069-e0e3048e911d.sketch_text.stroke-148"),sQuery(id+"FHMxAyK4CFUKdhS_1.wireOp",EDGE,"1cb9c079-ea9b-4899-8069-e0e3048e911d.sketch_text.stroke-149"),sQuery(id+"FHMxAyK4CFUKdhS_1.wireOp",EDGE,"1cb9c079-ea9b-4899-8069-e0e3048e911d.sketch_text.stroke-150"),sQuery(id+"FHMxAyK4CFUKdhS_1.wireOp",EDGE,"1cb9c079-ea9b-4899-8069-e0e3048e911d.sketch_text.stroke-151"),sQuery(id+"FHMxAyK4CFUKdhS_1.wireOp",EDGE,"1cb9c079-ea9b-4899-8069-e0e3048e911d.sketch_text.stroke-152"),sQuery(id+"FHMxAyK4CFUKdhS_1.wireOp",EDGE,"1cb9c079-ea9b-4899-8069-e0e3048e911d.sketch_text.stroke-153"),sQuery(id+"FHMxAyK4CFUKdhS_1.wireOp",EDGE,"1cb9c079-ea9b-4899-8069-e0e3048e911d.sketch_text.stroke-159"),sQuery(id+"FHMxAyK4CFUKdhS_1.wireOp",EDGE,"1cb9c079-ea9b-4899-8069-e0e3048e911d.sketch_text.stroke-160"),sQuery(id+"FHMxAyK4CFUKdhS_1.wireOp",EDGE,"1cb9c079-ea9b-4899-8069-e0e3048e911d.sketch_text.stroke-161"),sQuery(id+"FHMxAyK4CFUKdhS_1.wireOp",EDGE,"1cb9c079-ea9b-4899-8069-e0e3048e911d.sketch_text.stroke-162"),sQuery(id+"FHMxAyK4CFUKdhS_1.wireOp",EDGE,"1cb9c079-ea9b-4899-8069-e0e3048e911d.sketch_text.stroke-163"),sQuery(id+"FHMxAyK4CFUKdhS_1.wireOp",EDGE,"1cb9c079-ea9b-4899-8069-e0e3048e911d.sketch_text.stroke-164"),sQuery(id+"FHMxAyK4CFUKdhS_1.wireOp",EDGE,"1cb9c079-ea9b-4899-8069-e0e3048e911d.sketch_text.stroke-165"),sQuery(id+"FHMxAyK4CFUKdhS_1.wireOp",EDGE,"1cb9c079-ea9b-4899-8069-e0e3048e911d.sketch_text.stroke-166"),sQuery(id+"FHMxAyK4CFUKdhS_1.wireOp",EDGE,"1cb9c079-ea9b-4899-8069-e0e3048e911d.sketch_text.stroke-167"),sQuery(id+"FHMxAyK4CFUKdhS_1.wireOp",EDGE,"1cb9c079-ea9b-4899-8069-e0e3048e911d.sketch_text.stroke-168"),sQuery(id+"FHMxAyK4CFUKdhS_1.wireOp",EDGE,"1cb9c079-ea9b-4899-8069-e0e3048e911d.sketch_text.stroke-169"),sQuery(id+"FHMxAyK4CFUKdhS_1.wireOp",EDGE,"1cb9c079-ea9b-4899-8069-e0e3048e911d.sketch_text.stroke-170"),sQuery(id+"FHMxAyK4CFUKdhS_1.wireOp",EDGE,"1cb9c079-ea9b-4899-8069-e0e3048e911d.sketch_text.stroke-171"),sQuery(id+"FHMxAyK4CFUKdhS_1.wireOp",EDGE,"1cb9c079-ea9b-4899-8069-e0e3048e911d.sketch_text.stroke-172"),sQuery(id+"FHMxAyK4CFUKdhS_1.wireOp",EDGE,"1cb9c079-ea9b-4899-8069-e0e3048e911d.sketch_text.stroke-173"),sQuery(id+"FHMxAyK4CFUKdhS_1.wireOp",EDGE,"1cb9c079-ea9b-4899-8069-e0e3048e911d.sketch_text.stroke-174"),sQuery(id+"FHMxAyK4CFUKdhS_1.wireOp",EDGE,"1cb9c079-ea9b-4899-8069-e0e3048e911d.sketch_text.stroke-175"),sQuery(id+"FHMxAyK4CFUKdhS_1.wireOp",EDGE,"1cb9c079-ea9b-4899-8069-e0e3048e911d.sketch_text.stroke-176"),sQuery(id+"FHMxAyK4CFUKdhS_1.wireOp",EDGE,"1cb9c079-ea9b-4899-8069-e0e3048e911d.sketch_text.stroke-177"),sQuery(id+"FHMxAyK4CFUKdhS_1.wireOp",EDGE,"1cb9c079-ea9b-4899-8069-e0e3048e911d.sketch_text.stroke-178"),sQuery(id+"FHMxAyK4CFUKdhS_1.wireOp",EDGE,"1cb9c079-ea9b-4899-8069-e0e3048e911d.sketch_text.stroke-179"),sQuery(id+"FHMxAyK4CFUKdhS_1.wireOp",EDGE,"1cb9c079-ea9b-4899-8069-e0e3048e911d.sketch_text.stroke-180"),subQ2,sQuery(id+"F2.wireOp",EDGE,"6ee83ff3-586e-4dbe-aaea-af71240543bd")])],"isStart":true})])],"derivedFrom":makeQuery(id+"F3.opExtrude","CAP_EDGE",EDGE,{"disambiguationData":[OSD([subQ2])],"isStart":true})});}
            var Q3;
            {var subQ0=sQuery(id+"F2.wireOp",EDGE,"8007402e-1a4e-4a06-85a5-2af08e553504");var subQ1=sQuery(id+"F0.wireOp",EDGE,"E0.top");var subQ2=sQuery(id+"F2.wireOp",EDGE,"6ee83ff3-586e-4dbe-aaea-af71240543bd");var subQ3=sQuery(id+"F0.wireOp",EDGE,"E0.bottom");Q3=makeQuery(id+"F3.boolean.opBoolean","SPLIT",EDGE,{"disambiguationData":[TD([makeQuery(id+"F1.opExtrude","CAP_FACE",FACE,{"disambiguationData":[OSD([subQ3,subQ1,sQuery(id+"F0.wireOp",EDGE,"E0.left"),sQuery(id+"F0.wireOp",EDGE,"E0.right")])],"isStart":false}),makeQuery(id+"F1.opExtrude","SWEPT_FACE",FACE,{"disambiguationData":[OSD([subQ1])]}),makeQuery(id+"F3.opExtrude","SWEPT_FACE",FACE,{"disambiguationData":[OSD([subQ0])]}),makeQuery(id+"F3.opExtrude","CAP_FACE",FACE,{"disambiguationData":[OSD([subQ3,sQuery(id+"FQ5JFwxVdaqARUP_1.wireOp",EDGE,"fcba4419-a2ee-464f-be9d-58f11bf3418b.sketch_text.stroke-0"),sQuery(id+"FQ5JFwxVdaqARUP_1.wireOp",EDGE,"fcba4419-a2ee-464f-be9d-58f11bf3418b.sketch_text.stroke-1"),sQuery(id+"FQ5JFwxVdaqARUP_1.wireOp",EDGE,"fcba4419-a2ee-464f-be9d-58f11bf3418b.sketch_text.stroke-2"),sQuery(id+"FQ5JFwxVdaqARUP_1.wireOp",EDGE,"fcba4419-a2ee-464f-be9d-58f11bf3418b.sketch_text.stroke-3"),sQuery(id+"FQ5JFwxVdaqARUP_1.wireOp",EDGE,"fcba4419-a2ee-464f-be9d-58f11bf3418b.sketch_text.stroke-4"),sQuery(id+"FQ5JFwxVdaqARUP_1.wireOp",EDGE,"fcba4419-a2ee-464f-be9d-58f11bf3418b.sketch_text.stroke-5"),sQuery(id+"FQ5JFwxVdaqARUP_1.wireOp",EDGE,"fcba4419-a2ee-464f-be9d-58f11bf3418b.sketch_text.stroke-6"),sQuery(id+"FQ5JFwxVdaqARUP_1.wireOp",EDGE,"fcba4419-a2ee-464f-be9d-58f11bf3418b.sketch_text.stroke-7"),sQuery(id+"FQ5JFwxVdaqARUP_1.wireOp",EDGE,"fcba4419-a2ee-464f-be9d-58f11bf3418b.sketch_text.stroke-8"),sQuery(id+"FQ5JFwxVdaqARUP_1.wireOp",EDGE,"fcba4419-a2ee-464f-be9d-58f11bf3418b.sketch_text.stroke-9"),sQuery(id+"FQ5JFwxVdaqARUP_1.wireOp",EDGE,"fcba4419-a2ee-464f-be9d-58f11bf3418b.sketch_text.stroke-10"),sQuery(id+"FQ5JFwxVdaqARUP_1.wireOp",EDGE,"fcba4419-a2ee-464f-be9d-58f11bf3418b.sketch_text.stroke-11"),sQuery(id+"FQ5JFwxVdaqARUP_1.wireOp",EDGE,"fcba4419-a2ee-464f-be9d-58f11bf3418b.sketch_text.stroke-12"),sQuery(id+"FQ5JFwxVdaqARUP_1.wireOp",EDGE,"fcba4419-a2ee-464f-be9d-58f11bf3418b.sketch_text.stroke-13"),sQuery(id+"FQ5JFwxVdaqARUP_1.wireOp",EDGE,"fcba4419-a2ee-464f-be9d-58f11bf3418b.sketch_text.stroke-14"),sQuery(id+"FQ5JFwxVdaqARUP_1.wireOp",EDGE,"fcba4419-a2ee-464f-be9d-58f11bf3418b.sketch_text.stroke-15"),sQuery(id+"FQ5JFwxVdaqARUP_1.wireOp",EDGE,"fcba4419-a2ee-464f-be9d-58f11bf3418b.sketch_text.stroke-16"),sQuery(id+"FQ5JFwxVdaqARUP_1.wireOp",EDGE,"fcba4419-a2ee-464f-be9d-58f11bf3418b.sketch_text.stroke-17"),sQuery(id+"FQ5JFwxVdaqARUP_1.wireOp",EDGE,"fcba4419-a2ee-464f-be9d-58f11bf3418b.sketch_text.stroke-18"),sQuery(id+"FQ5JFwxVdaqARUP_1.wireOp",EDGE,"fcba4419-a2ee-464f-be9d-58f11bf3418b.sketch_text.stroke-19"),sQuery(id+"FQ5JFwxVdaqARUP_1.wireOp",EDGE,"fcba4419-a2ee-464f-be9d-58f11bf3418b.sketch_text.stroke-20"),sQuery(id+"FQ5JFwxVdaqARUP_1.wireOp",EDGE,"fcba4419-a2ee-464f-be9d-58f11bf3418b.sketch_text.stroke-21"),sQuery(id+"FQ5JFwxVdaqARUP_1.wireOp",EDGE,"fcba4419-a2ee-464f-be9d-58f11bf3418b.sketch_text.stroke-22"),sQuery(id+"FQ5JFwxVdaqARUP_1.wireOp",EDGE,"fcba4419-a2ee-464f-be9d-58f11bf3418b.sketch_text.stroke-23"),sQuery(id+"FQ5JFwxVdaqARUP_1.wireOp",EDGE,"fcba4419-a2ee-464f-be9d-58f11bf3418b.sketch_text.stroke-24"),sQuery(id+"FQ5JFwxVdaqARUP_1.wireOp",EDGE,"fcba4419-a2ee-464f-be9d-58f11bf3418b.sketch_text.stroke-25"),sQuery(id+"FQ5JFwxVdaqARUP_1.wireOp",EDGE,"fcba4419-a2ee-464f-be9d-58f11bf3418b.sketch_text.stroke-26"),sQuery(id+"FQ5JFwxVdaqARUP_1.wireOp",EDGE,"fcba4419-a2ee-464f-be9d-58f11bf3418b.sketch_text.stroke-27"),sQuery(id+"FQ5JFwxVdaqARUP_1.wireOp",EDGE,"fcba4419-a2ee-464f-be9d-58f11bf3418b.sketch_text.stroke-28"),sQuery(id+"FQ5JFwxVdaqARUP_1.wireOp",EDGE,"fcba4419-a2ee-464f-be9d-58f11bf3418b.sketch_text.stroke-29"),sQuery(id+"FQ5JFwxVdaqARUP_1.wireOp",EDGE,"fcba4419-a2ee-464f-be9d-58f11bf3418b.sketch_text.stroke-30"),sQuery(id+"FQ5JFwxVdaqARUP_1.wireOp",EDGE,"fcba4419-a2ee-464f-be9d-58f11bf3418b.sketch_text.stroke-31"),sQuery(id+"FQ5JFwxVdaqARUP_1.wireOp",EDGE,"fcba4419-a2ee-464f-be9d-58f11bf3418b.sketch_text.stroke-32"),sQuery(id+"FQ5JFwxVdaqARUP_1.wireOp",EDGE,"fcba4419-a2ee-464f-be9d-58f11bf3418b.sketch_text.stroke-33"),sQuery(id+"FQ5JFwxVdaqARUP_1.wireOp",EDGE,"fcba4419-a2ee-464f-be9d-58f11bf3418b.sketch_text.stroke-34"),sQuery(id+"FQ5JFwxVdaqARUP_1.wireOp",EDGE,"fcba4419-a2ee-464f-be9d-58f11bf3418b.sketch_text.stroke-35"),sQuery(id+"FQ5JFwxVdaqARUP_1.wireOp",EDGE,"fcba4419-a2ee-464f-be9d-58f11bf3418b.sketch_text.stroke-36"),sQuery(id+"FQ5JFwxVdaqARUP_1.wireOp",EDGE,"fcba4419-a2ee-464f-be9d-58f11bf3418b.sketch_text.stroke-37"),sQuery(id+"FQ5JFwxVdaqARUP_1.wireOp",EDGE,"fcba4419-a2ee-464f-be9d-58f11bf3418b.sketch_text.stroke-38"),sQuery(id+"FQ5JFwxVdaqARUP_1.wireOp",EDGE,"fcba4419-a2ee-464f-be9d-58f11bf3418b.sketch_text.stroke-39"),sQuery(id+"FQ5JFwxVdaqARUP_1.wireOp",EDGE,"fcba4419-a2ee-464f-be9d-58f11bf3418b.sketch_text.stroke-40"),sQuery(id+"FQ5JFwxVdaqARUP_1.wireOp",EDGE,"fcba4419-a2ee-464f-be9d-58f11bf3418b.sketch_text.stroke-41"),sQuery(id+"FQ5JFwxVdaqARUP_1.wireOp",EDGE,"fcba4419-a2ee-464f-be9d-58f11bf3418b.sketch_text.stroke-42"),sQuery(id+"FQ5JFwxVdaqARUP_1.wireOp",EDGE,"fcba4419-a2ee-464f-be9d-58f11bf3418b.sketch_text.stroke-43"),sQuery(id+"FQ5JFwxVdaqARUP_1.wireOp",EDGE,"fcba4419-a2ee-464f-be9d-58f11bf3418b.sketch_text.stroke-44"),sQuery(id+"FQ5JFwxVdaqARUP_1.wireOp",EDGE,"fcba4419-a2ee-464f-be9d-58f11bf3418b.sketch_text.stroke-45"),sQuery(id+"FQ5JFwxVdaqARUP_1.wireOp",EDGE,"fcba4419-a2ee-464f-be9d-58f11bf3418b.sketch_text.stroke-46"),sQuery(id+"FQ5JFwxVdaqARUP_1.wireOp",EDGE,"fcba4419-a2ee-464f-be9d-58f11bf3418b.sketch_text.stroke-47"),sQuery(id+"FQ5JFwxVdaqARUP_1.wireOp",EDGE,"fcba4419-a2ee-464f-be9d-58f11bf3418b.sketch_text.stroke-48"),sQuery(id+"FQ5JFwxVdaqARUP_1.wireOp",EDGE,"fcba4419-a2ee-464f-be9d-58f11bf3418b.sketch_text.stroke-49"),sQuery(id+"FQ5JFwxVdaqARUP_1.wireOp",EDGE,"fcba4419-a2ee-464f-be9d-58f11bf3418b.sketch_text.stroke-50"),sQuery(id+"FQ5JFwxVdaqARUP_1.wireOp",EDGE,"fcba4419-a2ee-464f-be9d-58f11bf3418b.sketch_text.stroke-51"),sQuery(id+"FQ5JFwxVdaqARUP_1.wireOp",EDGE,"fcba4419-a2ee-464f-be9d-58f11bf3418b.sketch_text.stroke-52"),sQuery(id+"FQ5JFwxVdaqARUP_1.wireOp",EDGE,"fcba4419-a2ee-464f-be9d-58f11bf3418b.sketch_text.stroke-53"),sQuery(id+"FQ5JFwxVdaqARUP_1.wireOp",EDGE,"fcba4419-a2ee-464f-be9d-58f11bf3418b.sketch_text.stroke-54"),sQuery(id+"FQ5JFwxVdaqARUP_1.wireOp",EDGE,"fcba4419-a2ee-464f-be9d-58f11bf3418b.sketch_text.stroke-55"),sQuery(id+"FQ5JFwxVdaqARUP_1.wireOp",EDGE,"fcba4419-a2ee-464f-be9d-58f11bf3418b.sketch_text.stroke-56"),sQuery(id+"FQ5JFwxVdaqARUP_1.wireOp",EDGE,"fcba4419-a2ee-464f-be9d-58f11bf3418b.sketch_text.stroke-57"),sQuery(id+"FQ5JFwxVdaqARUP_1.wireOp",EDGE,"fcba4419-a2ee-464f-be9d-58f11bf3418b.sketch_text.stroke-58"),sQuery(id+"FQ5JFwxVdaqARUP_1.wireOp",EDGE,"fcba4419-a2ee-464f-be9d-58f11bf3418b.sketch_text.stroke-59"),sQuery(id+"FQ5JFwxVdaqARUP_1.wireOp",EDGE,"fcba4419-a2ee-464f-be9d-58f11bf3418b.sketch_text.stroke-60"),sQuery(id+"FQ5JFwxVdaqARUP_1.wireOp",EDGE,"fcba4419-a2ee-464f-be9d-58f11bf3418b.sketch_text.stroke-61"),sQuery(id+"FQ5JFwxVdaqARUP_1.wireOp",EDGE,"fcba4419-a2ee-464f-be9d-58f11bf3418b.sketch_text.stroke-62"),sQuery(id+"FQ5JFwxVdaqARUP_1.wireOp",EDGE,"fcba4419-a2ee-464f-be9d-58f11bf3418b.sketch_text.stroke-63"),sQuery(id+"FQ5JFwxVdaqARUP_1.wireOp",EDGE,"fcba4419-a2ee-464f-be9d-58f11bf3418b.sketch_text.stroke-64"),sQuery(id+"FQ5JFwxVdaqARUP_1.wireOp",EDGE,"fcba4419-a2ee-464f-be9d-58f11bf3418b.sketch_text.stroke-65"),sQuery(id+"FQ5JFwxVdaqARUP_1.wireOp",EDGE,"fcba4419-a2ee-464f-be9d-58f11bf3418b.sketch_text.stroke-66"),sQuery(id+"FQ5JFwxVdaqARUP_1.wireOp",EDGE,"fcba4419-a2ee-464f-be9d-58f11bf3418b.sketch_text.stroke-67"),sQuery(id+"FQ5JFwxVdaqARUP_1.wireOp",EDGE,"fcba4419-a2ee-464f-be9d-58f11bf3418b.sketch_text.stroke-68"),sQuery(id+"FQ5JFwxVdaqARUP_1.wireOp",EDGE,"fcba4419-a2ee-464f-be9d-58f11bf3418b.sketch_text.stroke-69"),sQuery(id+"FQ5JFwxVdaqARUP_1.wireOp",EDGE,"fcba4419-a2ee-464f-be9d-58f11bf3418b.sketch_text.stroke-70"),sQuery(id+"FQ5JFwxVdaqARUP_1.wireOp",EDGE,"fcba4419-a2ee-464f-be9d-58f11bf3418b.sketch_text.stroke-71"),sQuery(id+"FQ5JFwxVdaqARUP_1.wireOp",EDGE,"fcba4419-a2ee-464f-be9d-58f11bf3418b.sketch_text.stroke-72"),sQuery(id+"FQ5JFwxVdaqARUP_1.wireOp",EDGE,"fcba4419-a2ee-464f-be9d-58f11bf3418b.sketch_text.stroke-73"),sQuery(id+"FQ5JFwxVdaqARUP_1.wireOp",EDGE,"fcba4419-a2ee-464f-be9d-58f11bf3418b.sketch_text.stroke-74"),sQuery(id+"FQ5JFwxVdaqARUP_1.wireOp",EDGE,"fcba4419-a2ee-464f-be9d-58f11bf3418b.sketch_text.stroke-75"),sQuery(id+"FQ5JFwxVdaqARUP_1.wireOp",EDGE,"fcba4419-a2ee-464f-be9d-58f11bf3418b.sketch_text.stroke-76"),sQuery(id+"FQ5JFwxVdaqARUP_1.wireOp",EDGE,"fcba4419-a2ee-464f-be9d-58f11bf3418b.sketch_text.stroke-77"),sQuery(id+"FQ5JFwxVdaqARUP_1.wireOp",EDGE,"fcba4419-a2ee-464f-be9d-58f11bf3418b.sketch_text.stroke-78"),sQuery(id+"FQ5JFwxVdaqARUP_1.wireOp",EDGE,"fcba4419-a2ee-464f-be9d-58f11bf3418b.sketch_text.stroke-79"),sQuery(id+"FQ5JFwxVdaqARUP_1.wireOp",EDGE,"fcba4419-a2ee-464f-be9d-58f11bf3418b.sketch_text.stroke-80"),sQuery(id+"FQ5JFwxVdaqARUP_1.wireOp",EDGE,"fcba4419-a2ee-464f-be9d-58f11bf3418b.sketch_text.stroke-81"),sQuery(id+"FQ5JFwxVdaqARUP_1.wireOp",EDGE,"fcba4419-a2ee-464f-be9d-58f11bf3418b.sketch_text.stroke-82"),sQuery(id+"FQ5JFwxVdaqARUP_1.wireOp",EDGE,"fcba4419-a2ee-464f-be9d-58f11bf3418b.sketch_text.stroke-83"),sQuery(id+"FQ5JFwxVdaqARUP_1.wireOp",EDGE,"fcba4419-a2ee-464f-be9d-58f11bf3418b.sketch_text.stroke-84"),sQuery(id+"FQ5JFwxVdaqARUP_1.wireOp",EDGE,"fcba4419-a2ee-464f-be9d-58f11bf3418b.sketch_text.stroke-85"),sQuery(id+"FQ5JFwxVdaqARUP_1.wireOp",EDGE,"fcba4419-a2ee-464f-be9d-58f11bf3418b.sketch_text.stroke-86"),sQuery(id+"FQ5JFwxVdaqARUP_1.wireOp",EDGE,"fcba4419-a2ee-464f-be9d-58f11bf3418b.sketch_text.stroke-87"),sQuery(id+"FQ5JFwxVdaqARUP_1.wireOp",EDGE,"fcba4419-a2ee-464f-be9d-58f11bf3418b.sketch_text.stroke-88"),sQuery(id+"FQ5JFwxVdaqARUP_1.wireOp",EDGE,"fcba4419-a2ee-464f-be9d-58f11bf3418b.sketch_text.stroke-89"),sQuery(id+"FQ5JFwxVdaqARUP_1.wireOp",EDGE,"fcba4419-a2ee-464f-be9d-58f11bf3418b.sketch_text.stroke-90"),sQuery(id+"FQ5JFwxVdaqARUP_1.wireOp",EDGE,"fcba4419-a2ee-464f-be9d-58f11bf3418b.sketch_text.stroke-91"),sQuery(id+"FQ5JFwxVdaqARUP_1.wireOp",EDGE,"fcba4419-a2ee-464f-be9d-58f11bf3418b.sketch_text.stroke-92"),sQuery(id+"FQ5JFwxVdaqARUP_1.wireOp",EDGE,"fcba4419-a2ee-464f-be9d-58f11bf3418b.sketch_text.stroke-93"),sQuery(id+"FQ5JFwxVdaqARUP_1.wireOp",EDGE,"fcba4419-a2ee-464f-be9d-58f11bf3418b.sketch_text.stroke-94"),sQuery(id+"FQ5JFwxVdaqARUP_1.wireOp",EDGE,"fcba4419-a2ee-464f-be9d-58f11bf3418b.sketch_text.stroke-95"),sQuery(id+"FQ5JFwxVdaqARUP_1.wireOp",EDGE,"fcba4419-a2ee-464f-be9d-58f11bf3418b.sketch_text.stroke-96"),sQuery(id+"FQ5JFwxVdaqARUP_1.wireOp",EDGE,"fcba4419-a2ee-464f-be9d-58f11bf3418b.sketch_text.stroke-97"),sQuery(id+"FQ5JFwxVdaqARUP_1.wireOp",EDGE,"fcba4419-a2ee-464f-be9d-58f11bf3418b.sketch_text.stroke-98"),sQuery(id+"FQ5JFwxVdaqARUP_1.wireOp",EDGE,"fcba4419-a2ee-464f-be9d-58f11bf3418b.sketch_text.stroke-99"),sQuery(id+"FQ5JFwxVdaqARUP_1.wireOp",EDGE,"fcba4419-a2ee-464f-be9d-58f11bf3418b.sketch_text.stroke-100"),sQuery(id+"FQ5JFwxVdaqARUP_1.wireOp",EDGE,"fcba4419-a2ee-464f-be9d-58f11bf3418b.sketch_text.stroke-101"),sQuery(id+"FQ5JFwxVdaqARUP_1.wireOp",EDGE,"fcba4419-a2ee-464f-be9d-58f11bf3418b.sketch_text.stroke-102"),sQuery(id+"FQ5JFwxVdaqARUP_1.wireOp",EDGE,"fcba4419-a2ee-464f-be9d-58f11bf3418b.sketch_text.stroke-103"),sQuery(id+"FQ5JFwxVdaqARUP_1.wireOp",EDGE,"fcba4419-a2ee-464f-be9d-58f11bf3418b.sketch_text.stroke-104"),sQuery(id+"FQ5JFwxVdaqARUP_1.wireOp",EDGE,"fcba4419-a2ee-464f-be9d-58f11bf3418b.sketch_text.stroke-105"),sQuery(id+"FQ5JFwxVdaqARUP_1.wireOp",EDGE,"fcba4419-a2ee-464f-be9d-58f11bf3418b.sketch_text.stroke-106"),sQuery(id+"FQ5JFwxVdaqARUP_1.wireOp",EDGE,"fcba4419-a2ee-464f-be9d-58f11bf3418b.sketch_text.stroke-107"),sQuery(id+"FQ5JFwxVdaqARUP_1.wireOp",EDGE,"fcba4419-a2ee-464f-be9d-58f11bf3418b.sketch_text.stroke-108"),sQuery(id+"FQ5JFwxVdaqARUP_1.wireOp",EDGE,"fcba4419-a2ee-464f-be9d-58f11bf3418b.sketch_text.stroke-109"),sQuery(id+"FQ5JFwxVdaqARUP_1.wireOp",EDGE,"fcba4419-a2ee-464f-be9d-58f11bf3418b.sketch_text.stroke-110"),sQuery(id+"FQ5JFwxVdaqARUP_1.wireOp",EDGE,"fcba4419-a2ee-464f-be9d-58f11bf3418b.sketch_text.stroke-111"),sQuery(id+"FQ5JFwxVdaqARUP_1.wireOp",EDGE,"fcba4419-a2ee-464f-be9d-58f11bf3418b.sketch_text.stroke-112"),sQuery(id+"FQ5JFwxVdaqARUP_1.wireOp",EDGE,"fcba4419-a2ee-464f-be9d-58f11bf3418b.sketch_text.stroke-113"),sQuery(id+"FQ5JFwxVdaqARUP_1.wireOp",EDGE,"fcba4419-a2ee-464f-be9d-58f11bf3418b.sketch_text.stroke-114"),sQuery(id+"FQ5JFwxVdaqARUP_1.wireOp",EDGE,"fcba4419-a2ee-464f-be9d-58f11bf3418b.sketch_text.stroke-115"),sQuery(id+"FQ5JFwxVdaqARUP_1.wireOp",EDGE,"fcba4419-a2ee-464f-be9d-58f11bf3418b.sketch_text.stroke-116"),sQuery(id+"FQ5JFwxVdaqARUP_1.wireOp",EDGE,"fcba4419-a2ee-464f-be9d-58f11bf3418b.sketch_text.stroke-117"),sQuery(id+"FQ5JFwxVdaqARUP_1.wireOp",EDGE,"fcba4419-a2ee-464f-be9d-58f11bf3418b.sketch_text.stroke-118"),sQuery(id+"FQ5JFwxVdaqARUP_1.wireOp",EDGE,"fcba4419-a2ee-464f-be9d-58f11bf3418b.sketch_text.stroke-119"),sQuery(id+"FQ5JFwxVdaqARUP_1.wireOp",EDGE,"fcba4419-a2ee-464f-be9d-58f11bf3418b.sketch_text.stroke-120"),sQuery(id+"FQ5JFwxVdaqARUP_1.wireOp",EDGE,"fcba4419-a2ee-464f-be9d-58f11bf3418b.sketch_text.stroke-121"),sQuery(id+"FQ5JFwxVdaqARUP_1.wireOp",EDGE,"fcba4419-a2ee-464f-be9d-58f11bf3418b.sketch_text.stroke-122"),sQuery(id+"FQ5JFwxVdaqARUP_1.wireOp",EDGE,"fcba4419-a2ee-464f-be9d-58f11bf3418b.sketch_text.stroke-123"),sQuery(id+"FQ5JFwxVdaqARUP_1.wireOp",EDGE,"fcba4419-a2ee-464f-be9d-58f11bf3418b.sketch_text.stroke-124"),sQuery(id+"FQ5JFwxVdaqARUP_1.wireOp",EDGE,"fcba4419-a2ee-464f-be9d-58f11bf3418b.sketch_text.stroke-125"),sQuery(id+"FQ5JFwxVdaqARUP_1.wireOp",EDGE,"fcba4419-a2ee-464f-be9d-58f11bf3418b.sketch_text.stroke-126"),sQuery(id+"FQ5JFwxVdaqARUP_1.wireOp",EDGE,"fcba4419-a2ee-464f-be9d-58f11bf3418b.sketch_text.stroke-127"),sQuery(id+"FQ5JFwxVdaqARUP_1.wireOp",EDGE,"fcba4419-a2ee-464f-be9d-58f11bf3418b.sketch_text.stroke-128"),sQuery(id+"FQ5JFwxVdaqARUP_1.wireOp",EDGE,"fcba4419-a2ee-464f-be9d-58f11bf3418b.sketch_text.stroke-129"),sQuery(id+"FQ5JFwxVdaqARUP_1.wireOp",EDGE,"fcba4419-a2ee-464f-be9d-58f11bf3418b.sketch_text.stroke-130"),sQuery(id+"FQ5JFwxVdaqARUP_1.wireOp",EDGE,"fcba4419-a2ee-464f-be9d-58f11bf3418b.sketch_text.stroke-131"),sQuery(id+"FQ5JFwxVdaqARUP_1.wireOp",EDGE,"fcba4419-a2ee-464f-be9d-58f11bf3418b.sketch_text.stroke-132"),sQuery(id+"FQ5JFwxVdaqARUP_1.wireOp",EDGE,"fcba4419-a2ee-464f-be9d-58f11bf3418b.sketch_text.stroke-133"),sQuery(id+"FQ5JFwxVdaqARUP_1.wireOp",EDGE,"fcba4419-a2ee-464f-be9d-58f11bf3418b.sketch_text.stroke-134"),sQuery(id+"FQ5JFwxVdaqARUP_1.wireOp",EDGE,"fcba4419-a2ee-464f-be9d-58f11bf3418b.sketch_text.stroke-135"),sQuery(id+"FQ5JFwxVdaqARUP_1.wireOp",EDGE,"fcba4419-a2ee-464f-be9d-58f11bf3418b.sketch_text.stroke-136"),sQuery(id+"FQ5JFwxVdaqARUP_1.wireOp",EDGE,"fcba4419-a2ee-464f-be9d-58f11bf3418b.sketch_text.stroke-137"),sQuery(id+"FQ5JFwxVdaqARUP_1.wireOp",EDGE,"fcba4419-a2ee-464f-be9d-58f11bf3418b.sketch_text.stroke-138"),sQuery(id+"FQ5JFwxVdaqARUP_1.wireOp",EDGE,"fcba4419-a2ee-464f-be9d-58f11bf3418b.sketch_text.stroke-139"),sQuery(id+"FQ5JFwxVdaqARUP_1.wireOp",EDGE,"fcba4419-a2ee-464f-be9d-58f11bf3418b.sketch_text.stroke-140"),sQuery(id+"FQ5JFwxVdaqARUP_1.wireOp",EDGE,"fcba4419-a2ee-464f-be9d-58f11bf3418b.sketch_text.stroke-141"),sQuery(id+"FQ5JFwxVdaqARUP_1.wireOp",EDGE,"fcba4419-a2ee-464f-be9d-58f11bf3418b.sketch_text.stroke-142"),sQuery(id+"FQ5JFwxVdaqARUP_1.wireOp",EDGE,"fcba4419-a2ee-464f-be9d-58f11bf3418b.sketch_text.stroke-143"),sQuery(id+"FQ5JFwxVdaqARUP_1.wireOp",EDGE,"fcba4419-a2ee-464f-be9d-58f11bf3418b.sketch_text.stroke-144"),sQuery(id+"FQ5JFwxVdaqARUP_1.wireOp",EDGE,"fcba4419-a2ee-464f-be9d-58f11bf3418b.sketch_text.stroke-145"),sQuery(id+"FQ5JFwxVdaqARUP_1.wireOp",EDGE,"fcba4419-a2ee-464f-be9d-58f11bf3418b.sketch_text.stroke-146"),sQuery(id+"FQ5JFwxVdaqARUP_1.wireOp",EDGE,"fcba4419-a2ee-464f-be9d-58f11bf3418b.sketch_text.stroke-147"),sQuery(id+"FQ5JFwxVdaqARUP_1.wireOp",EDGE,"fcba4419-a2ee-464f-be9d-58f11bf3418b.sketch_text.stroke-148"),sQuery(id+"FQ5JFwxVdaqARUP_1.wireOp",EDGE,"fcba4419-a2ee-464f-be9d-58f11bf3418b.sketch_text.stroke-149"),sQuery(id+"FQ5JFwxVdaqARUP_1.wireOp",EDGE,"fcba4419-a2ee-464f-be9d-58f11bf3418b.sketch_text.stroke-150"),sQuery(id+"FQ5JFwxVdaqARUP_1.wireOp",EDGE,"fcba4419-a2ee-464f-be9d-58f11bf3418b.sketch_text.stroke-151"),sQuery(id+"FQ5JFwxVdaqARUP_1.wireOp",EDGE,"fcba4419-a2ee-464f-be9d-58f11bf3418b.sketch_text.stroke-152"),sQuery(id+"FQ5JFwxVdaqARUP_1.wireOp",EDGE,"fcba4419-a2ee-464f-be9d-58f11bf3418b.sketch_text.stroke-153"),sQuery(id+"FQ5JFwxVdaqARUP_1.wireOp",EDGE,"fcba4419-a2ee-464f-be9d-58f11bf3418b.sketch_text.stroke-154"),sQuery(id+"FQ5JFwxVdaqARUP_1.wireOp",EDGE,"fcba4419-a2ee-464f-be9d-58f11bf3418b.sketch_text.stroke-155"),sQuery(id+"FQ5JFwxVdaqARUP_1.wireOp",EDGE,"fcba4419-a2ee-464f-be9d-58f11bf3418b.sketch_text.stroke-156"),sQuery(id+"FQ5JFwxVdaqARUP_1.wireOp",EDGE,"fcba4419-a2ee-464f-be9d-58f11bf3418b.sketch_text.stroke-157"),sQuery(id+"FQ5JFwxVdaqARUP_1.wireOp",EDGE,"fcba4419-a2ee-464f-be9d-58f11bf3418b.sketch_text.stroke-158"),sQuery(id+"FQ5JFwxVdaqARUP_1.wireOp",EDGE,"fcba4419-a2ee-464f-be9d-58f11bf3418b.sketch_text.stroke-159"),sQuery(id+"FQ5JFwxVdaqARUP_1.wireOp",EDGE,"fcba4419-a2ee-464f-be9d-58f11bf3418b.sketch_text.stroke-160"),sQuery(id+"FQ5JFwxVdaqARUP_1.wireOp",EDGE,"fcba4419-a2ee-464f-be9d-58f11bf3418b.sketch_text.stroke-161"),sQuery(id+"FQ5JFwxVdaqARUP_1.wireOp",EDGE,"fcba4419-a2ee-464f-be9d-58f11bf3418b.sketch_text.stroke-162"),sQuery(id+"FQ5JFwxVdaqARUP_1.wireOp",EDGE,"fcba4419-a2ee-464f-be9d-58f11bf3418b.sketch_text.stroke-163"),sQuery(id+"FQ5JFwxVdaqARUP_1.wireOp",EDGE,"fcba4419-a2ee-464f-be9d-58f11bf3418b.sketch_text.stroke-164"),sQuery(id+"FQ5JFwxVdaqARUP_1.wireOp",EDGE,"fcba4419-a2ee-464f-be9d-58f11bf3418b.sketch_text.stroke-165"),sQuery(id+"FQ5JFwxVdaqARUP_1.wireOp",EDGE,"fcba4419-a2ee-464f-be9d-58f11bf3418b.sketch_text.stroke-166"),sQuery(id+"FQ5JFwxVdaqARUP_1.wireOp",EDGE,"fcba4419-a2ee-464f-be9d-58f11bf3418b.sketch_text.stroke-167"),sQuery(id+"FQ5JFwxVdaqARUP_1.wireOp",EDGE,"fcba4419-a2ee-464f-be9d-58f11bf3418b.sketch_text.stroke-168"),sQuery(id+"FQ5JFwxVdaqARUP_1.wireOp",EDGE,"fcba4419-a2ee-464f-be9d-58f11bf3418b.sketch_text.stroke-169"),sQuery(id+"FQ5JFwxVdaqARUP_1.wireOp",EDGE,"fcba4419-a2ee-464f-be9d-58f11bf3418b.sketch_text.stroke-170"),sQuery(id+"FQ5JFwxVdaqARUP_1.wireOp",EDGE,"fcba4419-a2ee-464f-be9d-58f11bf3418b.sketch_text.stroke-171"),sQuery(id+"FQ5JFwxVdaqARUP_1.wireOp",EDGE,"fcba4419-a2ee-464f-be9d-58f11bf3418b.sketch_text.stroke-172"),sQuery(id+"FQ5JFwxVdaqARUP_1.wireOp",EDGE,"fcba4419-a2ee-464f-be9d-58f11bf3418b.sketch_text.stroke-173"),sQuery(id+"FHMxAyK4CFUKdhS_1.wireOp",EDGE,"1cb9c079-ea9b-4899-8069-e0e3048e911d.sketch_text.stroke-0"),sQuery(id+"FHMxAyK4CFUKdhS_1.wireOp",EDGE,"1cb9c079-ea9b-4899-8069-e0e3048e911d.sketch_text.stroke-1"),sQuery(id+"FHMxAyK4CFUKdhS_1.wireOp",EDGE,"1cb9c079-ea9b-4899-8069-e0e3048e911d.sketch_text.stroke-2"),sQuery(id+"FHMxAyK4CFUKdhS_1.wireOp",EDGE,"1cb9c079-ea9b-4899-8069-e0e3048e911d.sketch_text.stroke-3"),sQuery(id+"FHMxAyK4CFUKdhS_1.wireOp",EDGE,"1cb9c079-ea9b-4899-8069-e0e3048e911d.sketch_text.stroke-4"),sQuery(id+"FHMxAyK4CFUKdhS_1.wireOp",EDGE,"1cb9c079-ea9b-4899-8069-e0e3048e911d.sketch_text.stroke-5"),sQuery(id+"FHMxAyK4CFUKdhS_1.wireOp",EDGE,"1cb9c079-ea9b-4899-8069-e0e3048e911d.sketch_text.stroke-6"),sQuery(id+"FHMxAyK4CFUKdhS_1.wireOp",EDGE,"1cb9c079-ea9b-4899-8069-e0e3048e911d.sketch_text.stroke-7"),sQuery(id+"FHMxAyK4CFUKdhS_1.wireOp",EDGE,"1cb9c079-ea9b-4899-8069-e0e3048e911d.sketch_text.stroke-8"),sQuery(id+"FHMxAyK4CFUKdhS_1.wireOp",EDGE,"1cb9c079-ea9b-4899-8069-e0e3048e911d.sketch_text.stroke-9"),sQuery(id+"FHMxAyK4CFUKdhS_1.wireOp",EDGE,"1cb9c079-ea9b-4899-8069-e0e3048e911d.sketch_text.stroke-10"),sQuery(id+"FHMxAyK4CFUKdhS_1.wireOp",EDGE,"1cb9c079-ea9b-4899-8069-e0e3048e911d.sketch_text.stroke-11"),sQuery(id+"FHMxAyK4CFUKdhS_1.wireOp",EDGE,"1cb9c079-ea9b-4899-8069-e0e3048e911d.sketch_text.stroke-12"),sQuery(id+"FHMxAyK4CFUKdhS_1.wireOp",EDGE,"1cb9c079-ea9b-4899-8069-e0e3048e911d.sketch_text.stroke-13"),sQuery(id+"FHMxAyK4CFUKdhS_1.wireOp",EDGE,"1cb9c079-ea9b-4899-8069-e0e3048e911d.sketch_text.stroke-14"),sQuery(id+"FHMxAyK4CFUKdhS_1.wireOp",EDGE,"1cb9c079-ea9b-4899-8069-e0e3048e911d.sketch_text.stroke-15"),sQuery(id+"FHMxAyK4CFUKdhS_1.wireOp",EDGE,"1cb9c079-ea9b-4899-8069-e0e3048e911d.sketch_text.stroke-16"),sQuery(id+"FHMxAyK4CFUKdhS_1.wireOp",EDGE,"1cb9c079-ea9b-4899-8069-e0e3048e911d.sketch_text.stroke-17"),sQuery(id+"FHMxAyK4CFUKdhS_1.wireOp",EDGE,"1cb9c079-ea9b-4899-8069-e0e3048e911d.sketch_text.stroke-18"),sQuery(id+"FHMxAyK4CFUKdhS_1.wireOp",EDGE,"1cb9c079-ea9b-4899-8069-e0e3048e911d.sketch_text.stroke-19"),sQuery(id+"FHMxAyK4CFUKdhS_1.wireOp",EDGE,"1cb9c079-ea9b-4899-8069-e0e3048e911d.sketch_text.stroke-20"),sQuery(id+"FHMxAyK4CFUKdhS_1.wireOp",EDGE,"1cb9c079-ea9b-4899-8069-e0e3048e911d.sketch_text.stroke-21"),sQuery(id+"FHMxAyK4CFUKdhS_1.wireOp",EDGE,"1cb9c079-ea9b-4899-8069-e0e3048e911d.sketch_text.stroke-22"),sQuery(id+"FHMxAyK4CFUKdhS_1.wireOp",EDGE,"1cb9c079-ea9b-4899-8069-e0e3048e911d.sketch_text.stroke-23"),sQuery(id+"FHMxAyK4CFUKdhS_1.wireOp",EDGE,"1cb9c079-ea9b-4899-8069-e0e3048e911d.sketch_text.stroke-24"),sQuery(id+"FHMxAyK4CFUKdhS_1.wireOp",EDGE,"1cb9c079-ea9b-4899-8069-e0e3048e911d.sketch_text.stroke-25"),sQuery(id+"FHMxAyK4CFUKdhS_1.wireOp",EDGE,"1cb9c079-ea9b-4899-8069-e0e3048e911d.sketch_text.stroke-26"),sQuery(id+"FHMxAyK4CFUKdhS_1.wireOp",EDGE,"1cb9c079-ea9b-4899-8069-e0e3048e911d.sketch_text.stroke-27"),sQuery(id+"FHMxAyK4CFUKdhS_1.wireOp",EDGE,"1cb9c079-ea9b-4899-8069-e0e3048e911d.sketch_text.stroke-28"),sQuery(id+"FHMxAyK4CFUKdhS_1.wireOp",EDGE,"1cb9c079-ea9b-4899-8069-e0e3048e911d.sketch_text.stroke-29"),sQuery(id+"FHMxAyK4CFUKdhS_1.wireOp",EDGE,"1cb9c079-ea9b-4899-8069-e0e3048e911d.sketch_text.stroke-30"),sQuery(id+"FHMxAyK4CFUKdhS_1.wireOp",EDGE,"1cb9c079-ea9b-4899-8069-e0e3048e911d.sketch_text.stroke-31"),sQuery(id+"FHMxAyK4CFUKdhS_1.wireOp",EDGE,"1cb9c079-ea9b-4899-8069-e0e3048e911d.sketch_text.stroke-32"),sQuery(id+"FHMxAyK4CFUKdhS_1.wireOp",EDGE,"1cb9c079-ea9b-4899-8069-e0e3048e911d.sketch_text.stroke-33"),sQuery(id+"FHMxAyK4CFUKdhS_1.wireOp",EDGE,"1cb9c079-ea9b-4899-8069-e0e3048e911d.sketch_text.stroke-34"),sQuery(id+"FHMxAyK4CFUKdhS_1.wireOp",EDGE,"1cb9c079-ea9b-4899-8069-e0e3048e911d.sketch_text.stroke-35"),sQuery(id+"FHMxAyK4CFUKdhS_1.wireOp",EDGE,"1cb9c079-ea9b-4899-8069-e0e3048e911d.sketch_text.stroke-36"),sQuery(id+"FHMxAyK4CFUKdhS_1.wireOp",EDGE,"1cb9c079-ea9b-4899-8069-e0e3048e911d.sketch_text.stroke-37"),sQuery(id+"FHMxAyK4CFUKdhS_1.wireOp",EDGE,"1cb9c079-ea9b-4899-8069-e0e3048e911d.sketch_text.stroke-38"),sQuery(id+"FHMxAyK4CFUKdhS_1.wireOp",EDGE,"1cb9c079-ea9b-4899-8069-e0e3048e911d.sketch_text.stroke-39"),sQuery(id+"FHMxAyK4CFUKdhS_1.wireOp",EDGE,"1cb9c079-ea9b-4899-8069-e0e3048e911d.sketch_text.stroke-40"),sQuery(id+"FHMxAyK4CFUKdhS_1.wireOp",EDGE,"1cb9c079-ea9b-4899-8069-e0e3048e911d.sketch_text.stroke-41"),sQuery(id+"FHMxAyK4CFUKdhS_1.wireOp",EDGE,"1cb9c079-ea9b-4899-8069-e0e3048e911d.sketch_text.stroke-42"),sQuery(id+"FHMxAyK4CFUKdhS_1.wireOp",EDGE,"1cb9c079-ea9b-4899-8069-e0e3048e911d.sketch_text.stroke-43"),sQuery(id+"FHMxAyK4CFUKdhS_1.wireOp",EDGE,"1cb9c079-ea9b-4899-8069-e0e3048e911d.sketch_text.stroke-44"),sQuery(id+"FHMxAyK4CFUKdhS_1.wireOp",EDGE,"1cb9c079-ea9b-4899-8069-e0e3048e911d.sketch_text.stroke-45"),sQuery(id+"FHMxAyK4CFUKdhS_1.wireOp",EDGE,"1cb9c079-ea9b-4899-8069-e0e3048e911d.sketch_text.stroke-46"),sQuery(id+"FHMxAyK4CFUKdhS_1.wireOp",EDGE,"1cb9c079-ea9b-4899-8069-e0e3048e911d.sketch_text.stroke-47"),sQuery(id+"FHMxAyK4CFUKdhS_1.wireOp",EDGE,"1cb9c079-ea9b-4899-8069-e0e3048e911d.sketch_text.stroke-48"),sQuery(id+"FHMxAyK4CFUKdhS_1.wireOp",EDGE,"1cb9c079-ea9b-4899-8069-e0e3048e911d.sketch_text.stroke-49"),sQuery(id+"FHMxAyK4CFUKdhS_1.wireOp",EDGE,"1cb9c079-ea9b-4899-8069-e0e3048e911d.sketch_text.stroke-50"),sQuery(id+"FHMxAyK4CFUKdhS_1.wireOp",EDGE,"1cb9c079-ea9b-4899-8069-e0e3048e911d.sketch_text.stroke-51"),sQuery(id+"FHMxAyK4CFUKdhS_1.wireOp",EDGE,"1cb9c079-ea9b-4899-8069-e0e3048e911d.sketch_text.stroke-52"),sQuery(id+"FHMxAyK4CFUKdhS_1.wireOp",EDGE,"1cb9c079-ea9b-4899-8069-e0e3048e911d.sketch_text.stroke-53"),sQuery(id+"FHMxAyK4CFUKdhS_1.wireOp",EDGE,"1cb9c079-ea9b-4899-8069-e0e3048e911d.sketch_text.stroke-54"),sQuery(id+"FHMxAyK4CFUKdhS_1.wireOp",EDGE,"1cb9c079-ea9b-4899-8069-e0e3048e911d.sketch_text.stroke-55"),sQuery(id+"FHMxAyK4CFUKdhS_1.wireOp",EDGE,"1cb9c079-ea9b-4899-8069-e0e3048e911d.sketch_text.stroke-56"),sQuery(id+"FHMxAyK4CFUKdhS_1.wireOp",EDGE,"1cb9c079-ea9b-4899-8069-e0e3048e911d.sketch_text.stroke-57"),sQuery(id+"FHMxAyK4CFUKdhS_1.wireOp",EDGE,"1cb9c079-ea9b-4899-8069-e0e3048e911d.sketch_text.stroke-58"),sQuery(id+"FHMxAyK4CFUKdhS_1.wireOp",EDGE,"1cb9c079-ea9b-4899-8069-e0e3048e911d.sketch_text.stroke-59"),sQuery(id+"FHMxAyK4CFUKdhS_1.wireOp",EDGE,"1cb9c079-ea9b-4899-8069-e0e3048e911d.sketch_text.stroke-60"),sQuery(id+"FHMxAyK4CFUKdhS_1.wireOp",EDGE,"1cb9c079-ea9b-4899-8069-e0e3048e911d.sketch_text.stroke-61"),sQuery(id+"FHMxAyK4CFUKdhS_1.wireOp",EDGE,"1cb9c079-ea9b-4899-8069-e0e3048e911d.sketch_text.stroke-62"),sQuery(id+"FHMxAyK4CFUKdhS_1.wireOp",EDGE,"1cb9c079-ea9b-4899-8069-e0e3048e911d.sketch_text.stroke-71"),sQuery(id+"FHMxAyK4CFUKdhS_1.wireOp",EDGE,"1cb9c079-ea9b-4899-8069-e0e3048e911d.sketch_text.stroke-72"),sQuery(id+"FHMxAyK4CFUKdhS_1.wireOp",EDGE,"1cb9c079-ea9b-4899-8069-e0e3048e911d.sketch_text.stroke-73"),sQuery(id+"FHMxAyK4CFUKdhS_1.wireOp",EDGE,"1cb9c079-ea9b-4899-8069-e0e3048e911d.sketch_text.stroke-74"),sQuery(id+"FHMxAyK4CFUKdhS_1.wireOp",EDGE,"1cb9c079-ea9b-4899-8069-e0e3048e911d.sketch_text.stroke-75"),sQuery(id+"FHMxAyK4CFUKdhS_1.wireOp",EDGE,"1cb9c079-ea9b-4899-8069-e0e3048e911d.sketch_text.stroke-76"),sQuery(id+"FHMxAyK4CFUKdhS_1.wireOp",EDGE,"1cb9c079-ea9b-4899-8069-e0e3048e911d.sketch_text.stroke-77"),sQuery(id+"FHMxAyK4CFUKdhS_1.wireOp",EDGE,"1cb9c079-ea9b-4899-8069-e0e3048e911d.sketch_text.stroke-78"),sQuery(id+"FHMxAyK4CFUKdhS_1.wireOp",EDGE,"1cb9c079-ea9b-4899-8069-e0e3048e911d.sketch_text.stroke-79"),sQuery(id+"FHMxAyK4CFUKdhS_1.wireOp",EDGE,"1cb9c079-ea9b-4899-8069-e0e3048e911d.sketch_text.stroke-80"),sQuery(id+"FHMxAyK4CFUKdhS_1.wireOp",EDGE,"1cb9c079-ea9b-4899-8069-e0e3048e911d.sketch_text.stroke-81"),sQuery(id+"FHMxAyK4CFUKdhS_1.wireOp",EDGE,"1cb9c079-ea9b-4899-8069-e0e3048e911d.sketch_text.stroke-82"),sQuery(id+"FHMxAyK4CFUKdhS_1.wireOp",EDGE,"1cb9c079-ea9b-4899-8069-e0e3048e911d.sketch_text.stroke-83"),sQuery(id+"FHMxAyK4CFUKdhS_1.wireOp",EDGE,"1cb9c079-ea9b-4899-8069-e0e3048e911d.sketch_text.stroke-84"),sQuery(id+"FHMxAyK4CFUKdhS_1.wireOp",EDGE,"1cb9c079-ea9b-4899-8069-e0e3048e911d.sketch_text.stroke-85"),sQuery(id+"FHMxAyK4CFUKdhS_1.wireOp",EDGE,"1cb9c079-ea9b-4899-8069-e0e3048e911d.sketch_text.stroke-86"),sQuery(id+"FHMxAyK4CFUKdhS_1.wireOp",EDGE,"1cb9c079-ea9b-4899-8069-e0e3048e911d.sketch_text.stroke-87"),sQuery(id+"FHMxAyK4CFUKdhS_1.wireOp",EDGE,"1cb9c079-ea9b-4899-8069-e0e3048e911d.sketch_text.stroke-88"),sQuery(id+"FHMxAyK4CFUKdhS_1.wireOp",EDGE,"1cb9c079-ea9b-4899-8069-e0e3048e911d.sketch_text.stroke-89"),sQuery(id+"FHMxAyK4CFUKdhS_1.wireOp",EDGE,"1cb9c079-ea9b-4899-8069-e0e3048e911d.sketch_text.stroke-90"),sQuery(id+"FHMxAyK4CFUKdhS_1.wireOp",EDGE,"1cb9c079-ea9b-4899-8069-e0e3048e911d.sketch_text.stroke-91"),sQuery(id+"FHMxAyK4CFUKdhS_1.wireOp",EDGE,"1cb9c079-ea9b-4899-8069-e0e3048e911d.sketch_text.stroke-92"),sQuery(id+"FHMxAyK4CFUKdhS_1.wireOp",EDGE,"1cb9c079-ea9b-4899-8069-e0e3048e911d.sketch_text.stroke-93"),sQuery(id+"FHMxAyK4CFUKdhS_1.wireOp",EDGE,"1cb9c079-ea9b-4899-8069-e0e3048e911d.sketch_text.stroke-94"),sQuery(id+"FHMxAyK4CFUKdhS_1.wireOp",EDGE,"1cb9c079-ea9b-4899-8069-e0e3048e911d.sketch_text.stroke-95"),sQuery(id+"FHMxAyK4CFUKdhS_1.wireOp",EDGE,"1cb9c079-ea9b-4899-8069-e0e3048e911d.sketch_text.stroke-96"),sQuery(id+"FHMxAyK4CFUKdhS_1.wireOp",EDGE,"1cb9c079-ea9b-4899-8069-e0e3048e911d.sketch_text.stroke-97"),sQuery(id+"FHMxAyK4CFUKdhS_1.wireOp",EDGE,"1cb9c079-ea9b-4899-8069-e0e3048e911d.sketch_text.stroke-103"),sQuery(id+"FHMxAyK4CFUKdhS_1.wireOp",EDGE,"1cb9c079-ea9b-4899-8069-e0e3048e911d.sketch_text.stroke-104"),sQuery(id+"FHMxAyK4CFUKdhS_1.wireOp",EDGE,"1cb9c079-ea9b-4899-8069-e0e3048e911d.sketch_text.stroke-105"),sQuery(id+"FHMxAyK4CFUKdhS_1.wireOp",EDGE,"1cb9c079-ea9b-4899-8069-e0e3048e911d.sketch_text.stroke-106"),sQuery(id+"FHMxAyK4CFUKdhS_1.wireOp",EDGE,"1cb9c079-ea9b-4899-8069-e0e3048e911d.sketch_text.stroke-107"),sQuery(id+"FHMxAyK4CFUKdhS_1.wireOp",EDGE,"1cb9c079-ea9b-4899-8069-e0e3048e911d.sketch_text.stroke-108"),sQuery(id+"FHMxAyK4CFUKdhS_1.wireOp",EDGE,"1cb9c079-ea9b-4899-8069-e0e3048e911d.sketch_text.stroke-109"),sQuery(id+"FHMxAyK4CFUKdhS_1.wireOp",EDGE,"1cb9c079-ea9b-4899-8069-e0e3048e911d.sketch_text.stroke-110"),sQuery(id+"FHMxAyK4CFUKdhS_1.wireOp",EDGE,"1cb9c079-ea9b-4899-8069-e0e3048e911d.sketch_text.stroke-111"),sQuery(id+"FHMxAyK4CFUKdhS_1.wireOp",EDGE,"1cb9c079-ea9b-4899-8069-e0e3048e911d.sketch_text.stroke-112"),sQuery(id+"FHMxAyK4CFUKdhS_1.wireOp",EDGE,"1cb9c079-ea9b-4899-8069-e0e3048e911d.sketch_text.stroke-113"),sQuery(id+"FHMxAyK4CFUKdhS_1.wireOp",EDGE,"1cb9c079-ea9b-4899-8069-e0e3048e911d.sketch_text.stroke-114"),sQuery(id+"FHMxAyK4CFUKdhS_1.wireOp",EDGE,"1cb9c079-ea9b-4899-8069-e0e3048e911d.sketch_text.stroke-115"),sQuery(id+"FHMxAyK4CFUKdhS_1.wireOp",EDGE,"1cb9c079-ea9b-4899-8069-e0e3048e911d.sketch_text.stroke-116"),sQuery(id+"FHMxAyK4CFUKdhS_1.wireOp",EDGE,"1cb9c079-ea9b-4899-8069-e0e3048e911d.sketch_text.stroke-117"),sQuery(id+"FHMxAyK4CFUKdhS_1.wireOp",EDGE,"1cb9c079-ea9b-4899-8069-e0e3048e911d.sketch_text.stroke-118"),sQuery(id+"FHMxAyK4CFUKdhS_1.wireOp",EDGE,"1cb9c079-ea9b-4899-8069-e0e3048e911d.sketch_text.stroke-119"),sQuery(id+"FHMxAyK4CFUKdhS_1.wireOp",EDGE,"1cb9c079-ea9b-4899-8069-e0e3048e911d.sketch_text.stroke-120"),sQuery(id+"FHMxAyK4CFUKdhS_1.wireOp",EDGE,"1cb9c079-ea9b-4899-8069-e0e3048e911d.sketch_text.stroke-121"),sQuery(id+"FHMxAyK4CFUKdhS_1.wireOp",EDGE,"1cb9c079-ea9b-4899-8069-e0e3048e911d.sketch_text.stroke-122"),sQuery(id+"FHMxAyK4CFUKdhS_1.wireOp",EDGE,"1cb9c079-ea9b-4899-8069-e0e3048e911d.sketch_text.stroke-123"),sQuery(id+"FHMxAyK4CFUKdhS_1.wireOp",EDGE,"1cb9c079-ea9b-4899-8069-e0e3048e911d.sketch_text.stroke-124"),sQuery(id+"FHMxAyK4CFUKdhS_1.wireOp",EDGE,"1cb9c079-ea9b-4899-8069-e0e3048e911d.sketch_text.stroke-125"),sQuery(id+"FHMxAyK4CFUKdhS_1.wireOp",EDGE,"1cb9c079-ea9b-4899-8069-e0e3048e911d.sketch_text.stroke-126"),sQuery(id+"FHMxAyK4CFUKdhS_1.wireOp",EDGE,"1cb9c079-ea9b-4899-8069-e0e3048e911d.sketch_text.stroke-127"),sQuery(id+"FHMxAyK4CFUKdhS_1.wireOp",EDGE,"1cb9c079-ea9b-4899-8069-e0e3048e911d.sketch_text.stroke-128"),sQuery(id+"FHMxAyK4CFUKdhS_1.wireOp",EDGE,"1cb9c079-ea9b-4899-8069-e0e3048e911d.sketch_text.stroke-129"),sQuery(id+"FHMxAyK4CFUKdhS_1.wireOp",EDGE,"1cb9c079-ea9b-4899-8069-e0e3048e911d.sketch_text.stroke-130"),sQuery(id+"FHMxAyK4CFUKdhS_1.wireOp",EDGE,"1cb9c079-ea9b-4899-8069-e0e3048e911d.sketch_text.stroke-131"),sQuery(id+"FHMxAyK4CFUKdhS_1.wireOp",EDGE,"1cb9c079-ea9b-4899-8069-e0e3048e911d.sketch_text.stroke-132"),sQuery(id+"FHMxAyK4CFUKdhS_1.wireOp",EDGE,"1cb9c079-ea9b-4899-8069-e0e3048e911d.sketch_text.stroke-133"),sQuery(id+"FHMxAyK4CFUKdhS_1.wireOp",EDGE,"1cb9c079-ea9b-4899-8069-e0e3048e911d.sketch_text.stroke-134"),sQuery(id+"FHMxAyK4CFUKdhS_1.wireOp",EDGE,"1cb9c079-ea9b-4899-8069-e0e3048e911d.sketch_text.stroke-135"),sQuery(id+"FHMxAyK4CFUKdhS_1.wireOp",EDGE,"1cb9c079-ea9b-4899-8069-e0e3048e911d.sketch_text.stroke-136"),sQuery(id+"FHMxAyK4CFUKdhS_1.wireOp",EDGE,"1cb9c079-ea9b-4899-8069-e0e3048e911d.sketch_text.stroke-137"),sQuery(id+"FHMxAyK4CFUKdhS_1.wireOp",EDGE,"1cb9c079-ea9b-4899-8069-e0e3048e911d.sketch_text.stroke-138"),sQuery(id+"FHMxAyK4CFUKdhS_1.wireOp",EDGE,"1cb9c079-ea9b-4899-8069-e0e3048e911d.sketch_text.stroke-139"),sQuery(id+"FHMxAyK4CFUKdhS_1.wireOp",EDGE,"1cb9c079-ea9b-4899-8069-e0e3048e911d.sketch_text.stroke-140"),sQuery(id+"FHMxAyK4CFUKdhS_1.wireOp",EDGE,"1cb9c079-ea9b-4899-8069-e0e3048e911d.sketch_text.stroke-141"),sQuery(id+"FHMxAyK4CFUKdhS_1.wireOp",EDGE,"1cb9c079-ea9b-4899-8069-e0e3048e911d.sketch_text.stroke-142"),sQuery(id+"FHMxAyK4CFUKdhS_1.wireOp",EDGE,"1cb9c079-ea9b-4899-8069-e0e3048e911d.sketch_text.stroke-143"),sQuery(id+"FHMxAyK4CFUKdhS_1.wireOp",EDGE,"1cb9c079-ea9b-4899-8069-e0e3048e911d.sketch_text.stroke-144"),sQuery(id+"FHMxAyK4CFUKdhS_1.wireOp",EDGE,"1cb9c079-ea9b-4899-8069-e0e3048e911d.sketch_text.stroke-145"),sQuery(id+"FHMxAyK4CFUKdhS_1.wireOp",EDGE,"1cb9c079-ea9b-4899-8069-e0e3048e911d.sketch_text.stroke-146"),sQuery(id+"FHMxAyK4CFUKdhS_1.wireOp",EDGE,"1cb9c079-ea9b-4899-8069-e0e3048e911d.sketch_text.stroke-147"),sQuery(id+"FHMxAyK4CFUKdhS_1.wireOp",EDGE,"1cb9c079-ea9b-4899-8069-e0e3048e911d.sketch_text.stroke-148"),sQuery(id+"FHMxAyK4CFUKdhS_1.wireOp",EDGE,"1cb9c079-ea9b-4899-8069-e0e3048e911d.sketch_text.stroke-149"),sQuery(id+"FHMxAyK4CFUKdhS_1.wireOp",EDGE,"1cb9c079-ea9b-4899-8069-e0e3048e911d.sketch_text.stroke-150"),sQuery(id+"FHMxAyK4CFUKdhS_1.wireOp",EDGE,"1cb9c079-ea9b-4899-8069-e0e3048e911d.sketch_text.stroke-151"),sQuery(id+"FHMxAyK4CFUKdhS_1.wireOp",EDGE,"1cb9c079-ea9b-4899-8069-e0e3048e911d.sketch_text.stroke-152"),sQuery(id+"FHMxAyK4CFUKdhS_1.wireOp",EDGE,"1cb9c079-ea9b-4899-8069-e0e3048e911d.sketch_text.stroke-153"),sQuery(id+"FHMxAyK4CFUKdhS_1.wireOp",EDGE,"1cb9c079-ea9b-4899-8069-e0e3048e911d.sketch_text.stroke-159"),sQuery(id+"FHMxAyK4CFUKdhS_1.wireOp",EDGE,"1cb9c079-ea9b-4899-8069-e0e3048e911d.sketch_text.stroke-160"),sQuery(id+"FHMxAyK4CFUKdhS_1.wireOp",EDGE,"1cb9c079-ea9b-4899-8069-e0e3048e911d.sketch_text.stroke-161"),sQuery(id+"FHMxAyK4CFUKdhS_1.wireOp",EDGE,"1cb9c079-ea9b-4899-8069-e0e3048e911d.sketch_text.stroke-162"),sQuery(id+"FHMxAyK4CFUKdhS_1.wireOp",EDGE,"1cb9c079-ea9b-4899-8069-e0e3048e911d.sketch_text.stroke-163"),sQuery(id+"FHMxAyK4CFUKdhS_1.wireOp",EDGE,"1cb9c079-ea9b-4899-8069-e0e3048e911d.sketch_text.stroke-164"),sQuery(id+"FHMxAyK4CFUKdhS_1.wireOp",EDGE,"1cb9c079-ea9b-4899-8069-e0e3048e911d.sketch_text.stroke-165"),sQuery(id+"FHMxAyK4CFUKdhS_1.wireOp",EDGE,"1cb9c079-ea9b-4899-8069-e0e3048e911d.sketch_text.stroke-166"),sQuery(id+"FHMxAyK4CFUKdhS_1.wireOp",EDGE,"1cb9c079-ea9b-4899-8069-e0e3048e911d.sketch_text.stroke-167"),sQuery(id+"FHMxAyK4CFUKdhS_1.wireOp",EDGE,"1cb9c079-ea9b-4899-8069-e0e3048e911d.sketch_text.stroke-168"),sQuery(id+"FHMxAyK4CFUKdhS_1.wireOp",EDGE,"1cb9c079-ea9b-4899-8069-e0e3048e911d.sketch_text.stroke-169"),sQuery(id+"FHMxAyK4CFUKdhS_1.wireOp",EDGE,"1cb9c079-ea9b-4899-8069-e0e3048e911d.sketch_text.stroke-170"),sQuery(id+"FHMxAyK4CFUKdhS_1.wireOp",EDGE,"1cb9c079-ea9b-4899-8069-e0e3048e911d.sketch_text.stroke-171"),sQuery(id+"FHMxAyK4CFUKdhS_1.wireOp",EDGE,"1cb9c079-ea9b-4899-8069-e0e3048e911d.sketch_text.stroke-172"),sQuery(id+"FHMxAyK4CFUKdhS_1.wireOp",EDGE,"1cb9c079-ea9b-4899-8069-e0e3048e911d.sketch_text.stroke-173"),sQuery(id+"FHMxAyK4CFUKdhS_1.wireOp",EDGE,"1cb9c079-ea9b-4899-8069-e0e3048e911d.sketch_text.stroke-174"),sQuery(id+"FHMxAyK4CFUKdhS_1.wireOp",EDGE,"1cb9c079-ea9b-4899-8069-e0e3048e911d.sketch_text.stroke-175"),sQuery(id+"FHMxAyK4CFUKdhS_1.wireOp",EDGE,"1cb9c079-ea9b-4899-8069-e0e3048e911d.sketch_text.stroke-176"),sQuery(id+"FHMxAyK4CFUKdhS_1.wireOp",EDGE,"1cb9c079-ea9b-4899-8069-e0e3048e911d.sketch_text.stroke-177"),sQuery(id+"FHMxAyK4CFUKdhS_1.wireOp",EDGE,"1cb9c079-ea9b-4899-8069-e0e3048e911d.sketch_text.stroke-178"),sQuery(id+"FHMxAyK4CFUKdhS_1.wireOp",EDGE,"1cb9c079-ea9b-4899-8069-e0e3048e911d.sketch_text.stroke-179"),sQuery(id+"FHMxAyK4CFUKdhS_1.wireOp",EDGE,"1cb9c079-ea9b-4899-8069-e0e3048e911d.sketch_text.stroke-180"),subQ0,subQ2])],"isStart":true}),makeQuery(id+"F3.opExtrude","SWEPT_FACE",FACE,{"disambiguationData":[OSD([subQ2])]})])],"derivedFrom":makeQuery(id+"F3.opExtrude","CAP_EDGE",EDGE,{"disambiguationData":[OSD([subQ0])],"isStart":true})});}
            var Q4;
            {var subQ0=sQuery(id+"F0.wireOp",EDGE,"E0.top");var subQ1=sQuery(id+"F0.wireOp",EDGE,"E0.bottom");var subQ2=sQuery(id+"F2.wireOp",EDGE,"8007402e-1a4e-4a06-85a5-2af08e553504");Q4=makeQuery(id+"F3.boolean.opBoolean","SPLIT",EDGE,{"disambiguationData":[TD([makeQuery(id+"F1.opExtrude","CAP_FACE",FACE,{"disambiguationData":[OSD([subQ1,subQ0,sQuery(id+"F0.wireOp",EDGE,"E0.left"),sQuery(id+"F0.wireOp",EDGE,"E0.right")])],"isStart":false}),makeQuery(id+"F1.opExtrude","SWEPT_FACE",FACE,{"disambiguationData":[OSD([subQ0])]}),makeQuery(id+"F3.opExtrude","SWEPT_FACE",FACE,{"disambiguationData":[OSD([subQ2])]}),makeQuery(id+"F3.opExtrude","CAP_FACE",FACE,{"disambiguationData":[OSD([subQ1,sQuery(id+"FQ5JFwxVdaqARUP_1.wireOp",EDGE,"fcba4419-a2ee-464f-be9d-58f11bf3418b.sketch_text.stroke-0"),sQuery(id+"FQ5JFwxVdaqARUP_1.wireOp",EDGE,"fcba4419-a2ee-464f-be9d-58f11bf3418b.sketch_text.stroke-1"),sQuery(id+"FQ5JFwxVdaqARUP_1.wireOp",EDGE,"fcba4419-a2ee-464f-be9d-58f11bf3418b.sketch_text.stroke-2"),sQuery(id+"FQ5JFwxVdaqARUP_1.wireOp",EDGE,"fcba4419-a2ee-464f-be9d-58f11bf3418b.sketch_text.stroke-3"),sQuery(id+"FQ5JFwxVdaqARUP_1.wireOp",EDGE,"fcba4419-a2ee-464f-be9d-58f11bf3418b.sketch_text.stroke-4"),sQuery(id+"FQ5JFwxVdaqARUP_1.wireOp",EDGE,"fcba4419-a2ee-464f-be9d-58f11bf3418b.sketch_text.stroke-5"),sQuery(id+"FQ5JFwxVdaqARUP_1.wireOp",EDGE,"fcba4419-a2ee-464f-be9d-58f11bf3418b.sketch_text.stroke-6"),sQuery(id+"FQ5JFwxVdaqARUP_1.wireOp",EDGE,"fcba4419-a2ee-464f-be9d-58f11bf3418b.sketch_text.stroke-7"),sQuery(id+"FQ5JFwxVdaqARUP_1.wireOp",EDGE,"fcba4419-a2ee-464f-be9d-58f11bf3418b.sketch_text.stroke-8"),sQuery(id+"FQ5JFwxVdaqARUP_1.wireOp",EDGE,"fcba4419-a2ee-464f-be9d-58f11bf3418b.sketch_text.stroke-9"),sQuery(id+"FQ5JFwxVdaqARUP_1.wireOp",EDGE,"fcba4419-a2ee-464f-be9d-58f11bf3418b.sketch_text.stroke-10"),sQuery(id+"FQ5JFwxVdaqARUP_1.wireOp",EDGE,"fcba4419-a2ee-464f-be9d-58f11bf3418b.sketch_text.stroke-11"),sQuery(id+"FQ5JFwxVdaqARUP_1.wireOp",EDGE,"fcba4419-a2ee-464f-be9d-58f11bf3418b.sketch_text.stroke-12"),sQuery(id+"FQ5JFwxVdaqARUP_1.wireOp",EDGE,"fcba4419-a2ee-464f-be9d-58f11bf3418b.sketch_text.stroke-13"),sQuery(id+"FQ5JFwxVdaqARUP_1.wireOp",EDGE,"fcba4419-a2ee-464f-be9d-58f11bf3418b.sketch_text.stroke-14"),sQuery(id+"FQ5JFwxVdaqARUP_1.wireOp",EDGE,"fcba4419-a2ee-464f-be9d-58f11bf3418b.sketch_text.stroke-15"),sQuery(id+"FQ5JFwxVdaqARUP_1.wireOp",EDGE,"fcba4419-a2ee-464f-be9d-58f11bf3418b.sketch_text.stroke-16"),sQuery(id+"FQ5JFwxVdaqARUP_1.wireOp",EDGE,"fcba4419-a2ee-464f-be9d-58f11bf3418b.sketch_text.stroke-17"),sQuery(id+"FQ5JFwxVdaqARUP_1.wireOp",EDGE,"fcba4419-a2ee-464f-be9d-58f11bf3418b.sketch_text.stroke-18"),sQuery(id+"FQ5JFwxVdaqARUP_1.wireOp",EDGE,"fcba4419-a2ee-464f-be9d-58f11bf3418b.sketch_text.stroke-19"),sQuery(id+"FQ5JFwxVdaqARUP_1.wireOp",EDGE,"fcba4419-a2ee-464f-be9d-58f11bf3418b.sketch_text.stroke-20"),sQuery(id+"FQ5JFwxVdaqARUP_1.wireOp",EDGE,"fcba4419-a2ee-464f-be9d-58f11bf3418b.sketch_text.stroke-21"),sQuery(id+"FQ5JFwxVdaqARUP_1.wireOp",EDGE,"fcba4419-a2ee-464f-be9d-58f11bf3418b.sketch_text.stroke-22"),sQuery(id+"FQ5JFwxVdaqARUP_1.wireOp",EDGE,"fcba4419-a2ee-464f-be9d-58f11bf3418b.sketch_text.stroke-23"),sQuery(id+"FQ5JFwxVdaqARUP_1.wireOp",EDGE,"fcba4419-a2ee-464f-be9d-58f11bf3418b.sketch_text.stroke-24"),sQuery(id+"FQ5JFwxVdaqARUP_1.wireOp",EDGE,"fcba4419-a2ee-464f-be9d-58f11bf3418b.sketch_text.stroke-25"),sQuery(id+"FQ5JFwxVdaqARUP_1.wireOp",EDGE,"fcba4419-a2ee-464f-be9d-58f11bf3418b.sketch_text.stroke-26"),sQuery(id+"FQ5JFwxVdaqARUP_1.wireOp",EDGE,"fcba4419-a2ee-464f-be9d-58f11bf3418b.sketch_text.stroke-27"),sQuery(id+"FQ5JFwxVdaqARUP_1.wireOp",EDGE,"fcba4419-a2ee-464f-be9d-58f11bf3418b.sketch_text.stroke-28"),sQuery(id+"FQ5JFwxVdaqARUP_1.wireOp",EDGE,"fcba4419-a2ee-464f-be9d-58f11bf3418b.sketch_text.stroke-29"),sQuery(id+"FQ5JFwxVdaqARUP_1.wireOp",EDGE,"fcba4419-a2ee-464f-be9d-58f11bf3418b.sketch_text.stroke-30"),sQuery(id+"FQ5JFwxVdaqARUP_1.wireOp",EDGE,"fcba4419-a2ee-464f-be9d-58f11bf3418b.sketch_text.stroke-31"),sQuery(id+"FQ5JFwxVdaqARUP_1.wireOp",EDGE,"fcba4419-a2ee-464f-be9d-58f11bf3418b.sketch_text.stroke-32"),sQuery(id+"FQ5JFwxVdaqARUP_1.wireOp",EDGE,"fcba4419-a2ee-464f-be9d-58f11bf3418b.sketch_text.stroke-33"),sQuery(id+"FQ5JFwxVdaqARUP_1.wireOp",EDGE,"fcba4419-a2ee-464f-be9d-58f11bf3418b.sketch_text.stroke-34"),sQuery(id+"FQ5JFwxVdaqARUP_1.wireOp",EDGE,"fcba4419-a2ee-464f-be9d-58f11bf3418b.sketch_text.stroke-35"),sQuery(id+"FQ5JFwxVdaqARUP_1.wireOp",EDGE,"fcba4419-a2ee-464f-be9d-58f11bf3418b.sketch_text.stroke-36"),sQuery(id+"FQ5JFwxVdaqARUP_1.wireOp",EDGE,"fcba4419-a2ee-464f-be9d-58f11bf3418b.sketch_text.stroke-37"),sQuery(id+"FQ5JFwxVdaqARUP_1.wireOp",EDGE,"fcba4419-a2ee-464f-be9d-58f11bf3418b.sketch_text.stroke-38"),sQuery(id+"FQ5JFwxVdaqARUP_1.wireOp",EDGE,"fcba4419-a2ee-464f-be9d-58f11bf3418b.sketch_text.stroke-39"),sQuery(id+"FQ5JFwxVdaqARUP_1.wireOp",EDGE,"fcba4419-a2ee-464f-be9d-58f11bf3418b.sketch_text.stroke-40"),sQuery(id+"FQ5JFwxVdaqARUP_1.wireOp",EDGE,"fcba4419-a2ee-464f-be9d-58f11bf3418b.sketch_text.stroke-41"),sQuery(id+"FQ5JFwxVdaqARUP_1.wireOp",EDGE,"fcba4419-a2ee-464f-be9d-58f11bf3418b.sketch_text.stroke-42"),sQuery(id+"FQ5JFwxVdaqARUP_1.wireOp",EDGE,"fcba4419-a2ee-464f-be9d-58f11bf3418b.sketch_text.stroke-43"),sQuery(id+"FQ5JFwxVdaqARUP_1.wireOp",EDGE,"fcba4419-a2ee-464f-be9d-58f11bf3418b.sketch_text.stroke-44"),sQuery(id+"FQ5JFwxVdaqARUP_1.wireOp",EDGE,"fcba4419-a2ee-464f-be9d-58f11bf3418b.sketch_text.stroke-45"),sQuery(id+"FQ5JFwxVdaqARUP_1.wireOp",EDGE,"fcba4419-a2ee-464f-be9d-58f11bf3418b.sketch_text.stroke-46"),sQuery(id+"FQ5JFwxVdaqARUP_1.wireOp",EDGE,"fcba4419-a2ee-464f-be9d-58f11bf3418b.sketch_text.stroke-47"),sQuery(id+"FQ5JFwxVdaqARUP_1.wireOp",EDGE,"fcba4419-a2ee-464f-be9d-58f11bf3418b.sketch_text.stroke-48"),sQuery(id+"FQ5JFwxVdaqARUP_1.wireOp",EDGE,"fcba4419-a2ee-464f-be9d-58f11bf3418b.sketch_text.stroke-49"),sQuery(id+"FQ5JFwxVdaqARUP_1.wireOp",EDGE,"fcba4419-a2ee-464f-be9d-58f11bf3418b.sketch_text.stroke-50"),sQuery(id+"FQ5JFwxVdaqARUP_1.wireOp",EDGE,"fcba4419-a2ee-464f-be9d-58f11bf3418b.sketch_text.stroke-51"),sQuery(id+"FQ5JFwxVdaqARUP_1.wireOp",EDGE,"fcba4419-a2ee-464f-be9d-58f11bf3418b.sketch_text.stroke-52"),sQuery(id+"FQ5JFwxVdaqARUP_1.wireOp",EDGE,"fcba4419-a2ee-464f-be9d-58f11bf3418b.sketch_text.stroke-53"),sQuery(id+"FQ5JFwxVdaqARUP_1.wireOp",EDGE,"fcba4419-a2ee-464f-be9d-58f11bf3418b.sketch_text.stroke-54"),sQuery(id+"FQ5JFwxVdaqARUP_1.wireOp",EDGE,"fcba4419-a2ee-464f-be9d-58f11bf3418b.sketch_text.stroke-55"),sQuery(id+"FQ5JFwxVdaqARUP_1.wireOp",EDGE,"fcba4419-a2ee-464f-be9d-58f11bf3418b.sketch_text.stroke-56"),sQuery(id+"FQ5JFwxVdaqARUP_1.wireOp",EDGE,"fcba4419-a2ee-464f-be9d-58f11bf3418b.sketch_text.stroke-57"),sQuery(id+"FQ5JFwxVdaqARUP_1.wireOp",EDGE,"fcba4419-a2ee-464f-be9d-58f11bf3418b.sketch_text.stroke-58"),sQuery(id+"FQ5JFwxVdaqARUP_1.wireOp",EDGE,"fcba4419-a2ee-464f-be9d-58f11bf3418b.sketch_text.stroke-59"),sQuery(id+"FQ5JFwxVdaqARUP_1.wireOp",EDGE,"fcba4419-a2ee-464f-be9d-58f11bf3418b.sketch_text.stroke-60"),sQuery(id+"FQ5JFwxVdaqARUP_1.wireOp",EDGE,"fcba4419-a2ee-464f-be9d-58f11bf3418b.sketch_text.stroke-61"),sQuery(id+"FQ5JFwxVdaqARUP_1.wireOp",EDGE,"fcba4419-a2ee-464f-be9d-58f11bf3418b.sketch_text.stroke-62"),sQuery(id+"FQ5JFwxVdaqARUP_1.wireOp",EDGE,"fcba4419-a2ee-464f-be9d-58f11bf3418b.sketch_text.stroke-63"),sQuery(id+"FQ5JFwxVdaqARUP_1.wireOp",EDGE,"fcba4419-a2ee-464f-be9d-58f11bf3418b.sketch_text.stroke-64"),sQuery(id+"FQ5JFwxVdaqARUP_1.wireOp",EDGE,"fcba4419-a2ee-464f-be9d-58f11bf3418b.sketch_text.stroke-65"),sQuery(id+"FQ5JFwxVdaqARUP_1.wireOp",EDGE,"fcba4419-a2ee-464f-be9d-58f11bf3418b.sketch_text.stroke-66"),sQuery(id+"FQ5JFwxVdaqARUP_1.wireOp",EDGE,"fcba4419-a2ee-464f-be9d-58f11bf3418b.sketch_text.stroke-67"),sQuery(id+"FQ5JFwxVdaqARUP_1.wireOp",EDGE,"fcba4419-a2ee-464f-be9d-58f11bf3418b.sketch_text.stroke-68"),sQuery(id+"FQ5JFwxVdaqARUP_1.wireOp",EDGE,"fcba4419-a2ee-464f-be9d-58f11bf3418b.sketch_text.stroke-69"),sQuery(id+"FQ5JFwxVdaqARUP_1.wireOp",EDGE,"fcba4419-a2ee-464f-be9d-58f11bf3418b.sketch_text.stroke-70"),sQuery(id+"FQ5JFwxVdaqARUP_1.wireOp",EDGE,"fcba4419-a2ee-464f-be9d-58f11bf3418b.sketch_text.stroke-71"),sQuery(id+"FQ5JFwxVdaqARUP_1.wireOp",EDGE,"fcba4419-a2ee-464f-be9d-58f11bf3418b.sketch_text.stroke-72"),sQuery(id+"FQ5JFwxVdaqARUP_1.wireOp",EDGE,"fcba4419-a2ee-464f-be9d-58f11bf3418b.sketch_text.stroke-73"),sQuery(id+"FQ5JFwxVdaqARUP_1.wireOp",EDGE,"fcba4419-a2ee-464f-be9d-58f11bf3418b.sketch_text.stroke-74"),sQuery(id+"FQ5JFwxVdaqARUP_1.wireOp",EDGE,"fcba4419-a2ee-464f-be9d-58f11bf3418b.sketch_text.stroke-75"),sQuery(id+"FQ5JFwxVdaqARUP_1.wireOp",EDGE,"fcba4419-a2ee-464f-be9d-58f11bf3418b.sketch_text.stroke-76"),sQuery(id+"FQ5JFwxVdaqARUP_1.wireOp",EDGE,"fcba4419-a2ee-464f-be9d-58f11bf3418b.sketch_text.stroke-77"),sQuery(id+"FQ5JFwxVdaqARUP_1.wireOp",EDGE,"fcba4419-a2ee-464f-be9d-58f11bf3418b.sketch_text.stroke-78"),sQuery(id+"FQ5JFwxVdaqARUP_1.wireOp",EDGE,"fcba4419-a2ee-464f-be9d-58f11bf3418b.sketch_text.stroke-79"),sQuery(id+"FQ5JFwxVdaqARUP_1.wireOp",EDGE,"fcba4419-a2ee-464f-be9d-58f11bf3418b.sketch_text.stroke-80"),sQuery(id+"FQ5JFwxVdaqARUP_1.wireOp",EDGE,"fcba4419-a2ee-464f-be9d-58f11bf3418b.sketch_text.stroke-81"),sQuery(id+"FQ5JFwxVdaqARUP_1.wireOp",EDGE,"fcba4419-a2ee-464f-be9d-58f11bf3418b.sketch_text.stroke-82"),sQuery(id+"FQ5JFwxVdaqARUP_1.wireOp",EDGE,"fcba4419-a2ee-464f-be9d-58f11bf3418b.sketch_text.stroke-83"),sQuery(id+"FQ5JFwxVdaqARUP_1.wireOp",EDGE,"fcba4419-a2ee-464f-be9d-58f11bf3418b.sketch_text.stroke-84"),sQuery(id+"FQ5JFwxVdaqARUP_1.wireOp",EDGE,"fcba4419-a2ee-464f-be9d-58f11bf3418b.sketch_text.stroke-85"),sQuery(id+"FQ5JFwxVdaqARUP_1.wireOp",EDGE,"fcba4419-a2ee-464f-be9d-58f11bf3418b.sketch_text.stroke-86"),sQuery(id+"FQ5JFwxVdaqARUP_1.wireOp",EDGE,"fcba4419-a2ee-464f-be9d-58f11bf3418b.sketch_text.stroke-87"),sQuery(id+"FQ5JFwxVdaqARUP_1.wireOp",EDGE,"fcba4419-a2ee-464f-be9d-58f11bf3418b.sketch_text.stroke-88"),sQuery(id+"FQ5JFwxVdaqARUP_1.wireOp",EDGE,"fcba4419-a2ee-464f-be9d-58f11bf3418b.sketch_text.stroke-89"),sQuery(id+"FQ5JFwxVdaqARUP_1.wireOp",EDGE,"fcba4419-a2ee-464f-be9d-58f11bf3418b.sketch_text.stroke-90"),sQuery(id+"FQ5JFwxVdaqARUP_1.wireOp",EDGE,"fcba4419-a2ee-464f-be9d-58f11bf3418b.sketch_text.stroke-91"),sQuery(id+"FQ5JFwxVdaqARUP_1.wireOp",EDGE,"fcba4419-a2ee-464f-be9d-58f11bf3418b.sketch_text.stroke-92"),sQuery(id+"FQ5JFwxVdaqARUP_1.wireOp",EDGE,"fcba4419-a2ee-464f-be9d-58f11bf3418b.sketch_text.stroke-93"),sQuery(id+"FQ5JFwxVdaqARUP_1.wireOp",EDGE,"fcba4419-a2ee-464f-be9d-58f11bf3418b.sketch_text.stroke-94"),sQuery(id+"FQ5JFwxVdaqARUP_1.wireOp",EDGE,"fcba4419-a2ee-464f-be9d-58f11bf3418b.sketch_text.stroke-95"),sQuery(id+"FQ5JFwxVdaqARUP_1.wireOp",EDGE,"fcba4419-a2ee-464f-be9d-58f11bf3418b.sketch_text.stroke-96"),sQuery(id+"FQ5JFwxVdaqARUP_1.wireOp",EDGE,"fcba4419-a2ee-464f-be9d-58f11bf3418b.sketch_text.stroke-97"),sQuery(id+"FQ5JFwxVdaqARUP_1.wireOp",EDGE,"fcba4419-a2ee-464f-be9d-58f11bf3418b.sketch_text.stroke-98"),sQuery(id+"FQ5JFwxVdaqARUP_1.wireOp",EDGE,"fcba4419-a2ee-464f-be9d-58f11bf3418b.sketch_text.stroke-99"),sQuery(id+"FQ5JFwxVdaqARUP_1.wireOp",EDGE,"fcba4419-a2ee-464f-be9d-58f11bf3418b.sketch_text.stroke-100"),sQuery(id+"FQ5JFwxVdaqARUP_1.wireOp",EDGE,"fcba4419-a2ee-464f-be9d-58f11bf3418b.sketch_text.stroke-101"),sQuery(id+"FQ5JFwxVdaqARUP_1.wireOp",EDGE,"fcba4419-a2ee-464f-be9d-58f11bf3418b.sketch_text.stroke-102"),sQuery(id+"FQ5JFwxVdaqARUP_1.wireOp",EDGE,"fcba4419-a2ee-464f-be9d-58f11bf3418b.sketch_text.stroke-103"),sQuery(id+"FQ5JFwxVdaqARUP_1.wireOp",EDGE,"fcba4419-a2ee-464f-be9d-58f11bf3418b.sketch_text.stroke-104"),sQuery(id+"FQ5JFwxVdaqARUP_1.wireOp",EDGE,"fcba4419-a2ee-464f-be9d-58f11bf3418b.sketch_text.stroke-105"),sQuery(id+"FQ5JFwxVdaqARUP_1.wireOp",EDGE,"fcba4419-a2ee-464f-be9d-58f11bf3418b.sketch_text.stroke-106"),sQuery(id+"FQ5JFwxVdaqARUP_1.wireOp",EDGE,"fcba4419-a2ee-464f-be9d-58f11bf3418b.sketch_text.stroke-107"),sQuery(id+"FQ5JFwxVdaqARUP_1.wireOp",EDGE,"fcba4419-a2ee-464f-be9d-58f11bf3418b.sketch_text.stroke-108"),sQuery(id+"FQ5JFwxVdaqARUP_1.wireOp",EDGE,"fcba4419-a2ee-464f-be9d-58f11bf3418b.sketch_text.stroke-109"),sQuery(id+"FQ5JFwxVdaqARUP_1.wireOp",EDGE,"fcba4419-a2ee-464f-be9d-58f11bf3418b.sketch_text.stroke-110"),sQuery(id+"FQ5JFwxVdaqARUP_1.wireOp",EDGE,"fcba4419-a2ee-464f-be9d-58f11bf3418b.sketch_text.stroke-111"),sQuery(id+"FQ5JFwxVdaqARUP_1.wireOp",EDGE,"fcba4419-a2ee-464f-be9d-58f11bf3418b.sketch_text.stroke-112"),sQuery(id+"FQ5JFwxVdaqARUP_1.wireOp",EDGE,"fcba4419-a2ee-464f-be9d-58f11bf3418b.sketch_text.stroke-113"),sQuery(id+"FQ5JFwxVdaqARUP_1.wireOp",EDGE,"fcba4419-a2ee-464f-be9d-58f11bf3418b.sketch_text.stroke-114"),sQuery(id+"FQ5JFwxVdaqARUP_1.wireOp",EDGE,"fcba4419-a2ee-464f-be9d-58f11bf3418b.sketch_text.stroke-115"),sQuery(id+"FQ5JFwxVdaqARUP_1.wireOp",EDGE,"fcba4419-a2ee-464f-be9d-58f11bf3418b.sketch_text.stroke-116"),sQuery(id+"FQ5JFwxVdaqARUP_1.wireOp",EDGE,"fcba4419-a2ee-464f-be9d-58f11bf3418b.sketch_text.stroke-117"),sQuery(id+"FQ5JFwxVdaqARUP_1.wireOp",EDGE,"fcba4419-a2ee-464f-be9d-58f11bf3418b.sketch_text.stroke-118"),sQuery(id+"FQ5JFwxVdaqARUP_1.wireOp",EDGE,"fcba4419-a2ee-464f-be9d-58f11bf3418b.sketch_text.stroke-119"),sQuery(id+"FQ5JFwxVdaqARUP_1.wireOp",EDGE,"fcba4419-a2ee-464f-be9d-58f11bf3418b.sketch_text.stroke-120"),sQuery(id+"FQ5JFwxVdaqARUP_1.wireOp",EDGE,"fcba4419-a2ee-464f-be9d-58f11bf3418b.sketch_text.stroke-121"),sQuery(id+"FQ5JFwxVdaqARUP_1.wireOp",EDGE,"fcba4419-a2ee-464f-be9d-58f11bf3418b.sketch_text.stroke-122"),sQuery(id+"FQ5JFwxVdaqARUP_1.wireOp",EDGE,"fcba4419-a2ee-464f-be9d-58f11bf3418b.sketch_text.stroke-123"),sQuery(id+"FQ5JFwxVdaqARUP_1.wireOp",EDGE,"fcba4419-a2ee-464f-be9d-58f11bf3418b.sketch_text.stroke-124"),sQuery(id+"FQ5JFwxVdaqARUP_1.wireOp",EDGE,"fcba4419-a2ee-464f-be9d-58f11bf3418b.sketch_text.stroke-125"),sQuery(id+"FQ5JFwxVdaqARUP_1.wireOp",EDGE,"fcba4419-a2ee-464f-be9d-58f11bf3418b.sketch_text.stroke-126"),sQuery(id+"FQ5JFwxVdaqARUP_1.wireOp",EDGE,"fcba4419-a2ee-464f-be9d-58f11bf3418b.sketch_text.stroke-127"),sQuery(id+"FQ5JFwxVdaqARUP_1.wireOp",EDGE,"fcba4419-a2ee-464f-be9d-58f11bf3418b.sketch_text.stroke-128"),sQuery(id+"FQ5JFwxVdaqARUP_1.wireOp",EDGE,"fcba4419-a2ee-464f-be9d-58f11bf3418b.sketch_text.stroke-129"),sQuery(id+"FQ5JFwxVdaqARUP_1.wireOp",EDGE,"fcba4419-a2ee-464f-be9d-58f11bf3418b.sketch_text.stroke-130"),sQuery(id+"FQ5JFwxVdaqARUP_1.wireOp",EDGE,"fcba4419-a2ee-464f-be9d-58f11bf3418b.sketch_text.stroke-131"),sQuery(id+"FQ5JFwxVdaqARUP_1.wireOp",EDGE,"fcba4419-a2ee-464f-be9d-58f11bf3418b.sketch_text.stroke-132"),sQuery(id+"FQ5JFwxVdaqARUP_1.wireOp",EDGE,"fcba4419-a2ee-464f-be9d-58f11bf3418b.sketch_text.stroke-133"),sQuery(id+"FQ5JFwxVdaqARUP_1.wireOp",EDGE,"fcba4419-a2ee-464f-be9d-58f11bf3418b.sketch_text.stroke-134"),sQuery(id+"FQ5JFwxVdaqARUP_1.wireOp",EDGE,"fcba4419-a2ee-464f-be9d-58f11bf3418b.sketch_text.stroke-135"),sQuery(id+"FQ5JFwxVdaqARUP_1.wireOp",EDGE,"fcba4419-a2ee-464f-be9d-58f11bf3418b.sketch_text.stroke-136"),sQuery(id+"FQ5JFwxVdaqARUP_1.wireOp",EDGE,"fcba4419-a2ee-464f-be9d-58f11bf3418b.sketch_text.stroke-137"),sQuery(id+"FQ5JFwxVdaqARUP_1.wireOp",EDGE,"fcba4419-a2ee-464f-be9d-58f11bf3418b.sketch_text.stroke-138"),sQuery(id+"FQ5JFwxVdaqARUP_1.wireOp",EDGE,"fcba4419-a2ee-464f-be9d-58f11bf3418b.sketch_text.stroke-139"),sQuery(id+"FQ5JFwxVdaqARUP_1.wireOp",EDGE,"fcba4419-a2ee-464f-be9d-58f11bf3418b.sketch_text.stroke-140"),sQuery(id+"FQ5JFwxVdaqARUP_1.wireOp",EDGE,"fcba4419-a2ee-464f-be9d-58f11bf3418b.sketch_text.stroke-141"),sQuery(id+"FQ5JFwxVdaqARUP_1.wireOp",EDGE,"fcba4419-a2ee-464f-be9d-58f11bf3418b.sketch_text.stroke-142"),sQuery(id+"FQ5JFwxVdaqARUP_1.wireOp",EDGE,"fcba4419-a2ee-464f-be9d-58f11bf3418b.sketch_text.stroke-143"),sQuery(id+"FQ5JFwxVdaqARUP_1.wireOp",EDGE,"fcba4419-a2ee-464f-be9d-58f11bf3418b.sketch_text.stroke-144"),sQuery(id+"FQ5JFwxVdaqARUP_1.wireOp",EDGE,"fcba4419-a2ee-464f-be9d-58f11bf3418b.sketch_text.stroke-145"),sQuery(id+"FQ5JFwxVdaqARUP_1.wireOp",EDGE,"fcba4419-a2ee-464f-be9d-58f11bf3418b.sketch_text.stroke-146"),sQuery(id+"FQ5JFwxVdaqARUP_1.wireOp",EDGE,"fcba4419-a2ee-464f-be9d-58f11bf3418b.sketch_text.stroke-147"),sQuery(id+"FQ5JFwxVdaqARUP_1.wireOp",EDGE,"fcba4419-a2ee-464f-be9d-58f11bf3418b.sketch_text.stroke-148"),sQuery(id+"FQ5JFwxVdaqARUP_1.wireOp",EDGE,"fcba4419-a2ee-464f-be9d-58f11bf3418b.sketch_text.stroke-149"),sQuery(id+"FQ5JFwxVdaqARUP_1.wireOp",EDGE,"fcba4419-a2ee-464f-be9d-58f11bf3418b.sketch_text.stroke-150"),sQuery(id+"FQ5JFwxVdaqARUP_1.wireOp",EDGE,"fcba4419-a2ee-464f-be9d-58f11bf3418b.sketch_text.stroke-151"),sQuery(id+"FQ5JFwxVdaqARUP_1.wireOp",EDGE,"fcba4419-a2ee-464f-be9d-58f11bf3418b.sketch_text.stroke-152"),sQuery(id+"FQ5JFwxVdaqARUP_1.wireOp",EDGE,"fcba4419-a2ee-464f-be9d-58f11bf3418b.sketch_text.stroke-153"),sQuery(id+"FQ5JFwxVdaqARUP_1.wireOp",EDGE,"fcba4419-a2ee-464f-be9d-58f11bf3418b.sketch_text.stroke-154"),sQuery(id+"FQ5JFwxVdaqARUP_1.wireOp",EDGE,"fcba4419-a2ee-464f-be9d-58f11bf3418b.sketch_text.stroke-155"),sQuery(id+"FQ5JFwxVdaqARUP_1.wireOp",EDGE,"fcba4419-a2ee-464f-be9d-58f11bf3418b.sketch_text.stroke-156"),sQuery(id+"FQ5JFwxVdaqARUP_1.wireOp",EDGE,"fcba4419-a2ee-464f-be9d-58f11bf3418b.sketch_text.stroke-157"),sQuery(id+"FQ5JFwxVdaqARUP_1.wireOp",EDGE,"fcba4419-a2ee-464f-be9d-58f11bf3418b.sketch_text.stroke-158"),sQuery(id+"FQ5JFwxVdaqARUP_1.wireOp",EDGE,"fcba4419-a2ee-464f-be9d-58f11bf3418b.sketch_text.stroke-159"),sQuery(id+"FQ5JFwxVdaqARUP_1.wireOp",EDGE,"fcba4419-a2ee-464f-be9d-58f11bf3418b.sketch_text.stroke-160"),sQuery(id+"FQ5JFwxVdaqARUP_1.wireOp",EDGE,"fcba4419-a2ee-464f-be9d-58f11bf3418b.sketch_text.stroke-161"),sQuery(id+"FQ5JFwxVdaqARUP_1.wireOp",EDGE,"fcba4419-a2ee-464f-be9d-58f11bf3418b.sketch_text.stroke-162"),sQuery(id+"FQ5JFwxVdaqARUP_1.wireOp",EDGE,"fcba4419-a2ee-464f-be9d-58f11bf3418b.sketch_text.stroke-163"),sQuery(id+"FQ5JFwxVdaqARUP_1.wireOp",EDGE,"fcba4419-a2ee-464f-be9d-58f11bf3418b.sketch_text.stroke-164"),sQuery(id+"FQ5JFwxVdaqARUP_1.wireOp",EDGE,"fcba4419-a2ee-464f-be9d-58f11bf3418b.sketch_text.stroke-165"),sQuery(id+"FQ5JFwxVdaqARUP_1.wireOp",EDGE,"fcba4419-a2ee-464f-be9d-58f11bf3418b.sketch_text.stroke-166"),sQuery(id+"FQ5JFwxVdaqARUP_1.wireOp",EDGE,"fcba4419-a2ee-464f-be9d-58f11bf3418b.sketch_text.stroke-167"),sQuery(id+"FQ5JFwxVdaqARUP_1.wireOp",EDGE,"fcba4419-a2ee-464f-be9d-58f11bf3418b.sketch_text.stroke-168"),sQuery(id+"FQ5JFwxVdaqARUP_1.wireOp",EDGE,"fcba4419-a2ee-464f-be9d-58f11bf3418b.sketch_text.stroke-169"),sQuery(id+"FQ5JFwxVdaqARUP_1.wireOp",EDGE,"fcba4419-a2ee-464f-be9d-58f11bf3418b.sketch_text.stroke-170"),sQuery(id+"FQ5JFwxVdaqARUP_1.wireOp",EDGE,"fcba4419-a2ee-464f-be9d-58f11bf3418b.sketch_text.stroke-171"),sQuery(id+"FQ5JFwxVdaqARUP_1.wireOp",EDGE,"fcba4419-a2ee-464f-be9d-58f11bf3418b.sketch_text.stroke-172"),sQuery(id+"FQ5JFwxVdaqARUP_1.wireOp",EDGE,"fcba4419-a2ee-464f-be9d-58f11bf3418b.sketch_text.stroke-173"),sQuery(id+"FHMxAyK4CFUKdhS_1.wireOp",EDGE,"1cb9c079-ea9b-4899-8069-e0e3048e911d.sketch_text.stroke-0"),sQuery(id+"FHMxAyK4CFUKdhS_1.wireOp",EDGE,"1cb9c079-ea9b-4899-8069-e0e3048e911d.sketch_text.stroke-1"),sQuery(id+"FHMxAyK4CFUKdhS_1.wireOp",EDGE,"1cb9c079-ea9b-4899-8069-e0e3048e911d.sketch_text.stroke-2"),sQuery(id+"FHMxAyK4CFUKdhS_1.wireOp",EDGE,"1cb9c079-ea9b-4899-8069-e0e3048e911d.sketch_text.stroke-3"),sQuery(id+"FHMxAyK4CFUKdhS_1.wireOp",EDGE,"1cb9c079-ea9b-4899-8069-e0e3048e911d.sketch_text.stroke-4"),sQuery(id+"FHMxAyK4CFUKdhS_1.wireOp",EDGE,"1cb9c079-ea9b-4899-8069-e0e3048e911d.sketch_text.stroke-5"),sQuery(id+"FHMxAyK4CFUKdhS_1.wireOp",EDGE,"1cb9c079-ea9b-4899-8069-e0e3048e911d.sketch_text.stroke-6"),sQuery(id+"FHMxAyK4CFUKdhS_1.wireOp",EDGE,"1cb9c079-ea9b-4899-8069-e0e3048e911d.sketch_text.stroke-7"),sQuery(id+"FHMxAyK4CFUKdhS_1.wireOp",EDGE,"1cb9c079-ea9b-4899-8069-e0e3048e911d.sketch_text.stroke-8"),sQuery(id+"FHMxAyK4CFUKdhS_1.wireOp",EDGE,"1cb9c079-ea9b-4899-8069-e0e3048e911d.sketch_text.stroke-9"),sQuery(id+"FHMxAyK4CFUKdhS_1.wireOp",EDGE,"1cb9c079-ea9b-4899-8069-e0e3048e911d.sketch_text.stroke-10"),sQuery(id+"FHMxAyK4CFUKdhS_1.wireOp",EDGE,"1cb9c079-ea9b-4899-8069-e0e3048e911d.sketch_text.stroke-11"),sQuery(id+"FHMxAyK4CFUKdhS_1.wireOp",EDGE,"1cb9c079-ea9b-4899-8069-e0e3048e911d.sketch_text.stroke-12"),sQuery(id+"FHMxAyK4CFUKdhS_1.wireOp",EDGE,"1cb9c079-ea9b-4899-8069-e0e3048e911d.sketch_text.stroke-13"),sQuery(id+"FHMxAyK4CFUKdhS_1.wireOp",EDGE,"1cb9c079-ea9b-4899-8069-e0e3048e911d.sketch_text.stroke-14"),sQuery(id+"FHMxAyK4CFUKdhS_1.wireOp",EDGE,"1cb9c079-ea9b-4899-8069-e0e3048e911d.sketch_text.stroke-15"),sQuery(id+"FHMxAyK4CFUKdhS_1.wireOp",EDGE,"1cb9c079-ea9b-4899-8069-e0e3048e911d.sketch_text.stroke-16"),sQuery(id+"FHMxAyK4CFUKdhS_1.wireOp",EDGE,"1cb9c079-ea9b-4899-8069-e0e3048e911d.sketch_text.stroke-17"),sQuery(id+"FHMxAyK4CFUKdhS_1.wireOp",EDGE,"1cb9c079-ea9b-4899-8069-e0e3048e911d.sketch_text.stroke-18"),sQuery(id+"FHMxAyK4CFUKdhS_1.wireOp",EDGE,"1cb9c079-ea9b-4899-8069-e0e3048e911d.sketch_text.stroke-19"),sQuery(id+"FHMxAyK4CFUKdhS_1.wireOp",EDGE,"1cb9c079-ea9b-4899-8069-e0e3048e911d.sketch_text.stroke-20"),sQuery(id+"FHMxAyK4CFUKdhS_1.wireOp",EDGE,"1cb9c079-ea9b-4899-8069-e0e3048e911d.sketch_text.stroke-21"),sQuery(id+"FHMxAyK4CFUKdhS_1.wireOp",EDGE,"1cb9c079-ea9b-4899-8069-e0e3048e911d.sketch_text.stroke-22"),sQuery(id+"FHMxAyK4CFUKdhS_1.wireOp",EDGE,"1cb9c079-ea9b-4899-8069-e0e3048e911d.sketch_text.stroke-23"),sQuery(id+"FHMxAyK4CFUKdhS_1.wireOp",EDGE,"1cb9c079-ea9b-4899-8069-e0e3048e911d.sketch_text.stroke-24"),sQuery(id+"FHMxAyK4CFUKdhS_1.wireOp",EDGE,"1cb9c079-ea9b-4899-8069-e0e3048e911d.sketch_text.stroke-25"),sQuery(id+"FHMxAyK4CFUKdhS_1.wireOp",EDGE,"1cb9c079-ea9b-4899-8069-e0e3048e911d.sketch_text.stroke-26"),sQuery(id+"FHMxAyK4CFUKdhS_1.wireOp",EDGE,"1cb9c079-ea9b-4899-8069-e0e3048e911d.sketch_text.stroke-27"),sQuery(id+"FHMxAyK4CFUKdhS_1.wireOp",EDGE,"1cb9c079-ea9b-4899-8069-e0e3048e911d.sketch_text.stroke-28"),sQuery(id+"FHMxAyK4CFUKdhS_1.wireOp",EDGE,"1cb9c079-ea9b-4899-8069-e0e3048e911d.sketch_text.stroke-29"),sQuery(id+"FHMxAyK4CFUKdhS_1.wireOp",EDGE,"1cb9c079-ea9b-4899-8069-e0e3048e911d.sketch_text.stroke-30"),sQuery(id+"FHMxAyK4CFUKdhS_1.wireOp",EDGE,"1cb9c079-ea9b-4899-8069-e0e3048e911d.sketch_text.stroke-31"),sQuery(id+"FHMxAyK4CFUKdhS_1.wireOp",EDGE,"1cb9c079-ea9b-4899-8069-e0e3048e911d.sketch_text.stroke-32"),sQuery(id+"FHMxAyK4CFUKdhS_1.wireOp",EDGE,"1cb9c079-ea9b-4899-8069-e0e3048e911d.sketch_text.stroke-33"),sQuery(id+"FHMxAyK4CFUKdhS_1.wireOp",EDGE,"1cb9c079-ea9b-4899-8069-e0e3048e911d.sketch_text.stroke-34"),sQuery(id+"FHMxAyK4CFUKdhS_1.wireOp",EDGE,"1cb9c079-ea9b-4899-8069-e0e3048e911d.sketch_text.stroke-35"),sQuery(id+"FHMxAyK4CFUKdhS_1.wireOp",EDGE,"1cb9c079-ea9b-4899-8069-e0e3048e911d.sketch_text.stroke-36"),sQuery(id+"FHMxAyK4CFUKdhS_1.wireOp",EDGE,"1cb9c079-ea9b-4899-8069-e0e3048e911d.sketch_text.stroke-37"),sQuery(id+"FHMxAyK4CFUKdhS_1.wireOp",EDGE,"1cb9c079-ea9b-4899-8069-e0e3048e911d.sketch_text.stroke-38"),sQuery(id+"FHMxAyK4CFUKdhS_1.wireOp",EDGE,"1cb9c079-ea9b-4899-8069-e0e3048e911d.sketch_text.stroke-39"),sQuery(id+"FHMxAyK4CFUKdhS_1.wireOp",EDGE,"1cb9c079-ea9b-4899-8069-e0e3048e911d.sketch_text.stroke-40"),sQuery(id+"FHMxAyK4CFUKdhS_1.wireOp",EDGE,"1cb9c079-ea9b-4899-8069-e0e3048e911d.sketch_text.stroke-41"),sQuery(id+"FHMxAyK4CFUKdhS_1.wireOp",EDGE,"1cb9c079-ea9b-4899-8069-e0e3048e911d.sketch_text.stroke-42"),sQuery(id+"FHMxAyK4CFUKdhS_1.wireOp",EDGE,"1cb9c079-ea9b-4899-8069-e0e3048e911d.sketch_text.stroke-43"),sQuery(id+"FHMxAyK4CFUKdhS_1.wireOp",EDGE,"1cb9c079-ea9b-4899-8069-e0e3048e911d.sketch_text.stroke-44"),sQuery(id+"FHMxAyK4CFUKdhS_1.wireOp",EDGE,"1cb9c079-ea9b-4899-8069-e0e3048e911d.sketch_text.stroke-45"),sQuery(id+"FHMxAyK4CFUKdhS_1.wireOp",EDGE,"1cb9c079-ea9b-4899-8069-e0e3048e911d.sketch_text.stroke-46"),sQuery(id+"FHMxAyK4CFUKdhS_1.wireOp",EDGE,"1cb9c079-ea9b-4899-8069-e0e3048e911d.sketch_text.stroke-47"),sQuery(id+"FHMxAyK4CFUKdhS_1.wireOp",EDGE,"1cb9c079-ea9b-4899-8069-e0e3048e911d.sketch_text.stroke-48"),sQuery(id+"FHMxAyK4CFUKdhS_1.wireOp",EDGE,"1cb9c079-ea9b-4899-8069-e0e3048e911d.sketch_text.stroke-49"),sQuery(id+"FHMxAyK4CFUKdhS_1.wireOp",EDGE,"1cb9c079-ea9b-4899-8069-e0e3048e911d.sketch_text.stroke-50"),sQuery(id+"FHMxAyK4CFUKdhS_1.wireOp",EDGE,"1cb9c079-ea9b-4899-8069-e0e3048e911d.sketch_text.stroke-51"),sQuery(id+"FHMxAyK4CFUKdhS_1.wireOp",EDGE,"1cb9c079-ea9b-4899-8069-e0e3048e911d.sketch_text.stroke-52"),sQuery(id+"FHMxAyK4CFUKdhS_1.wireOp",EDGE,"1cb9c079-ea9b-4899-8069-e0e3048e911d.sketch_text.stroke-53"),sQuery(id+"FHMxAyK4CFUKdhS_1.wireOp",EDGE,"1cb9c079-ea9b-4899-8069-e0e3048e911d.sketch_text.stroke-54"),sQuery(id+"FHMxAyK4CFUKdhS_1.wireOp",EDGE,"1cb9c079-ea9b-4899-8069-e0e3048e911d.sketch_text.stroke-55"),sQuery(id+"FHMxAyK4CFUKdhS_1.wireOp",EDGE,"1cb9c079-ea9b-4899-8069-e0e3048e911d.sketch_text.stroke-56"),sQuery(id+"FHMxAyK4CFUKdhS_1.wireOp",EDGE,"1cb9c079-ea9b-4899-8069-e0e3048e911d.sketch_text.stroke-57"),sQuery(id+"FHMxAyK4CFUKdhS_1.wireOp",EDGE,"1cb9c079-ea9b-4899-8069-e0e3048e911d.sketch_text.stroke-58"),sQuery(id+"FHMxAyK4CFUKdhS_1.wireOp",EDGE,"1cb9c079-ea9b-4899-8069-e0e3048e911d.sketch_text.stroke-59"),sQuery(id+"FHMxAyK4CFUKdhS_1.wireOp",EDGE,"1cb9c079-ea9b-4899-8069-e0e3048e911d.sketch_text.stroke-60"),sQuery(id+"FHMxAyK4CFUKdhS_1.wireOp",EDGE,"1cb9c079-ea9b-4899-8069-e0e3048e911d.sketch_text.stroke-61"),sQuery(id+"FHMxAyK4CFUKdhS_1.wireOp",EDGE,"1cb9c079-ea9b-4899-8069-e0e3048e911d.sketch_text.stroke-62"),sQuery(id+"FHMxAyK4CFUKdhS_1.wireOp",EDGE,"1cb9c079-ea9b-4899-8069-e0e3048e911d.sketch_text.stroke-71"),sQuery(id+"FHMxAyK4CFUKdhS_1.wireOp",EDGE,"1cb9c079-ea9b-4899-8069-e0e3048e911d.sketch_text.stroke-72"),sQuery(id+"FHMxAyK4CFUKdhS_1.wireOp",EDGE,"1cb9c079-ea9b-4899-8069-e0e3048e911d.sketch_text.stroke-73"),sQuery(id+"FHMxAyK4CFUKdhS_1.wireOp",EDGE,"1cb9c079-ea9b-4899-8069-e0e3048e911d.sketch_text.stroke-74"),sQuery(id+"FHMxAyK4CFUKdhS_1.wireOp",EDGE,"1cb9c079-ea9b-4899-8069-e0e3048e911d.sketch_text.stroke-75"),sQuery(id+"FHMxAyK4CFUKdhS_1.wireOp",EDGE,"1cb9c079-ea9b-4899-8069-e0e3048e911d.sketch_text.stroke-76"),sQuery(id+"FHMxAyK4CFUKdhS_1.wireOp",EDGE,"1cb9c079-ea9b-4899-8069-e0e3048e911d.sketch_text.stroke-77"),sQuery(id+"FHMxAyK4CFUKdhS_1.wireOp",EDGE,"1cb9c079-ea9b-4899-8069-e0e3048e911d.sketch_text.stroke-78"),sQuery(id+"FHMxAyK4CFUKdhS_1.wireOp",EDGE,"1cb9c079-ea9b-4899-8069-e0e3048e911d.sketch_text.stroke-79"),sQuery(id+"FHMxAyK4CFUKdhS_1.wireOp",EDGE,"1cb9c079-ea9b-4899-8069-e0e3048e911d.sketch_text.stroke-80"),sQuery(id+"FHMxAyK4CFUKdhS_1.wireOp",EDGE,"1cb9c079-ea9b-4899-8069-e0e3048e911d.sketch_text.stroke-81"),sQuery(id+"FHMxAyK4CFUKdhS_1.wireOp",EDGE,"1cb9c079-ea9b-4899-8069-e0e3048e911d.sketch_text.stroke-82"),sQuery(id+"FHMxAyK4CFUKdhS_1.wireOp",EDGE,"1cb9c079-ea9b-4899-8069-e0e3048e911d.sketch_text.stroke-83"),sQuery(id+"FHMxAyK4CFUKdhS_1.wireOp",EDGE,"1cb9c079-ea9b-4899-8069-e0e3048e911d.sketch_text.stroke-84"),sQuery(id+"FHMxAyK4CFUKdhS_1.wireOp",EDGE,"1cb9c079-ea9b-4899-8069-e0e3048e911d.sketch_text.stroke-85"),sQuery(id+"FHMxAyK4CFUKdhS_1.wireOp",EDGE,"1cb9c079-ea9b-4899-8069-e0e3048e911d.sketch_text.stroke-86"),sQuery(id+"FHMxAyK4CFUKdhS_1.wireOp",EDGE,"1cb9c079-ea9b-4899-8069-e0e3048e911d.sketch_text.stroke-87"),sQuery(id+"FHMxAyK4CFUKdhS_1.wireOp",EDGE,"1cb9c079-ea9b-4899-8069-e0e3048e911d.sketch_text.stroke-88"),sQuery(id+"FHMxAyK4CFUKdhS_1.wireOp",EDGE,"1cb9c079-ea9b-4899-8069-e0e3048e911d.sketch_text.stroke-89"),sQuery(id+"FHMxAyK4CFUKdhS_1.wireOp",EDGE,"1cb9c079-ea9b-4899-8069-e0e3048e911d.sketch_text.stroke-90"),sQuery(id+"FHMxAyK4CFUKdhS_1.wireOp",EDGE,"1cb9c079-ea9b-4899-8069-e0e3048e911d.sketch_text.stroke-91"),sQuery(id+"FHMxAyK4CFUKdhS_1.wireOp",EDGE,"1cb9c079-ea9b-4899-8069-e0e3048e911d.sketch_text.stroke-92"),sQuery(id+"FHMxAyK4CFUKdhS_1.wireOp",EDGE,"1cb9c079-ea9b-4899-8069-e0e3048e911d.sketch_text.stroke-93"),sQuery(id+"FHMxAyK4CFUKdhS_1.wireOp",EDGE,"1cb9c079-ea9b-4899-8069-e0e3048e911d.sketch_text.stroke-94"),sQuery(id+"FHMxAyK4CFUKdhS_1.wireOp",EDGE,"1cb9c079-ea9b-4899-8069-e0e3048e911d.sketch_text.stroke-95"),sQuery(id+"FHMxAyK4CFUKdhS_1.wireOp",EDGE,"1cb9c079-ea9b-4899-8069-e0e3048e911d.sketch_text.stroke-96"),sQuery(id+"FHMxAyK4CFUKdhS_1.wireOp",EDGE,"1cb9c079-ea9b-4899-8069-e0e3048e911d.sketch_text.stroke-97"),sQuery(id+"FHMxAyK4CFUKdhS_1.wireOp",EDGE,"1cb9c079-ea9b-4899-8069-e0e3048e911d.sketch_text.stroke-103"),sQuery(id+"FHMxAyK4CFUKdhS_1.wireOp",EDGE,"1cb9c079-ea9b-4899-8069-e0e3048e911d.sketch_text.stroke-104"),sQuery(id+"FHMxAyK4CFUKdhS_1.wireOp",EDGE,"1cb9c079-ea9b-4899-8069-e0e3048e911d.sketch_text.stroke-105"),sQuery(id+"FHMxAyK4CFUKdhS_1.wireOp",EDGE,"1cb9c079-ea9b-4899-8069-e0e3048e911d.sketch_text.stroke-106"),sQuery(id+"FHMxAyK4CFUKdhS_1.wireOp",EDGE,"1cb9c079-ea9b-4899-8069-e0e3048e911d.sketch_text.stroke-107"),sQuery(id+"FHMxAyK4CFUKdhS_1.wireOp",EDGE,"1cb9c079-ea9b-4899-8069-e0e3048e911d.sketch_text.stroke-108"),sQuery(id+"FHMxAyK4CFUKdhS_1.wireOp",EDGE,"1cb9c079-ea9b-4899-8069-e0e3048e911d.sketch_text.stroke-109"),sQuery(id+"FHMxAyK4CFUKdhS_1.wireOp",EDGE,"1cb9c079-ea9b-4899-8069-e0e3048e911d.sketch_text.stroke-110"),sQuery(id+"FHMxAyK4CFUKdhS_1.wireOp",EDGE,"1cb9c079-ea9b-4899-8069-e0e3048e911d.sketch_text.stroke-111"),sQuery(id+"FHMxAyK4CFUKdhS_1.wireOp",EDGE,"1cb9c079-ea9b-4899-8069-e0e3048e911d.sketch_text.stroke-112"),sQuery(id+"FHMxAyK4CFUKdhS_1.wireOp",EDGE,"1cb9c079-ea9b-4899-8069-e0e3048e911d.sketch_text.stroke-113"),sQuery(id+"FHMxAyK4CFUKdhS_1.wireOp",EDGE,"1cb9c079-ea9b-4899-8069-e0e3048e911d.sketch_text.stroke-114"),sQuery(id+"FHMxAyK4CFUKdhS_1.wireOp",EDGE,"1cb9c079-ea9b-4899-8069-e0e3048e911d.sketch_text.stroke-115"),sQuery(id+"FHMxAyK4CFUKdhS_1.wireOp",EDGE,"1cb9c079-ea9b-4899-8069-e0e3048e911d.sketch_text.stroke-116"),sQuery(id+"FHMxAyK4CFUKdhS_1.wireOp",EDGE,"1cb9c079-ea9b-4899-8069-e0e3048e911d.sketch_text.stroke-117"),sQuery(id+"FHMxAyK4CFUKdhS_1.wireOp",EDGE,"1cb9c079-ea9b-4899-8069-e0e3048e911d.sketch_text.stroke-118"),sQuery(id+"FHMxAyK4CFUKdhS_1.wireOp",EDGE,"1cb9c079-ea9b-4899-8069-e0e3048e911d.sketch_text.stroke-119"),sQuery(id+"FHMxAyK4CFUKdhS_1.wireOp",EDGE,"1cb9c079-ea9b-4899-8069-e0e3048e911d.sketch_text.stroke-120"),sQuery(id+"FHMxAyK4CFUKdhS_1.wireOp",EDGE,"1cb9c079-ea9b-4899-8069-e0e3048e911d.sketch_text.stroke-121"),sQuery(id+"FHMxAyK4CFUKdhS_1.wireOp",EDGE,"1cb9c079-ea9b-4899-8069-e0e3048e911d.sketch_text.stroke-122"),sQuery(id+"FHMxAyK4CFUKdhS_1.wireOp",EDGE,"1cb9c079-ea9b-4899-8069-e0e3048e911d.sketch_text.stroke-123"),sQuery(id+"FHMxAyK4CFUKdhS_1.wireOp",EDGE,"1cb9c079-ea9b-4899-8069-e0e3048e911d.sketch_text.stroke-124"),sQuery(id+"FHMxAyK4CFUKdhS_1.wireOp",EDGE,"1cb9c079-ea9b-4899-8069-e0e3048e911d.sketch_text.stroke-125"),sQuery(id+"FHMxAyK4CFUKdhS_1.wireOp",EDGE,"1cb9c079-ea9b-4899-8069-e0e3048e911d.sketch_text.stroke-126"),sQuery(id+"FHMxAyK4CFUKdhS_1.wireOp",EDGE,"1cb9c079-ea9b-4899-8069-e0e3048e911d.sketch_text.stroke-127"),sQuery(id+"FHMxAyK4CFUKdhS_1.wireOp",EDGE,"1cb9c079-ea9b-4899-8069-e0e3048e911d.sketch_text.stroke-128"),sQuery(id+"FHMxAyK4CFUKdhS_1.wireOp",EDGE,"1cb9c079-ea9b-4899-8069-e0e3048e911d.sketch_text.stroke-129"),sQuery(id+"FHMxAyK4CFUKdhS_1.wireOp",EDGE,"1cb9c079-ea9b-4899-8069-e0e3048e911d.sketch_text.stroke-130"),sQuery(id+"FHMxAyK4CFUKdhS_1.wireOp",EDGE,"1cb9c079-ea9b-4899-8069-e0e3048e911d.sketch_text.stroke-131"),sQuery(id+"FHMxAyK4CFUKdhS_1.wireOp",EDGE,"1cb9c079-ea9b-4899-8069-e0e3048e911d.sketch_text.stroke-132"),sQuery(id+"FHMxAyK4CFUKdhS_1.wireOp",EDGE,"1cb9c079-ea9b-4899-8069-e0e3048e911d.sketch_text.stroke-133"),sQuery(id+"FHMxAyK4CFUKdhS_1.wireOp",EDGE,"1cb9c079-ea9b-4899-8069-e0e3048e911d.sketch_text.stroke-134"),sQuery(id+"FHMxAyK4CFUKdhS_1.wireOp",EDGE,"1cb9c079-ea9b-4899-8069-e0e3048e911d.sketch_text.stroke-135"),sQuery(id+"FHMxAyK4CFUKdhS_1.wireOp",EDGE,"1cb9c079-ea9b-4899-8069-e0e3048e911d.sketch_text.stroke-136"),sQuery(id+"FHMxAyK4CFUKdhS_1.wireOp",EDGE,"1cb9c079-ea9b-4899-8069-e0e3048e911d.sketch_text.stroke-137"),sQuery(id+"FHMxAyK4CFUKdhS_1.wireOp",EDGE,"1cb9c079-ea9b-4899-8069-e0e3048e911d.sketch_text.stroke-138"),sQuery(id+"FHMxAyK4CFUKdhS_1.wireOp",EDGE,"1cb9c079-ea9b-4899-8069-e0e3048e911d.sketch_text.stroke-139"),sQuery(id+"FHMxAyK4CFUKdhS_1.wireOp",EDGE,"1cb9c079-ea9b-4899-8069-e0e3048e911d.sketch_text.stroke-140"),sQuery(id+"FHMxAyK4CFUKdhS_1.wireOp",EDGE,"1cb9c079-ea9b-4899-8069-e0e3048e911d.sketch_text.stroke-141"),sQuery(id+"FHMxAyK4CFUKdhS_1.wireOp",EDGE,"1cb9c079-ea9b-4899-8069-e0e3048e911d.sketch_text.stroke-142"),sQuery(id+"FHMxAyK4CFUKdhS_1.wireOp",EDGE,"1cb9c079-ea9b-4899-8069-e0e3048e911d.sketch_text.stroke-143"),sQuery(id+"FHMxAyK4CFUKdhS_1.wireOp",EDGE,"1cb9c079-ea9b-4899-8069-e0e3048e911d.sketch_text.stroke-144"),sQuery(id+"FHMxAyK4CFUKdhS_1.wireOp",EDGE,"1cb9c079-ea9b-4899-8069-e0e3048e911d.sketch_text.stroke-145"),sQuery(id+"FHMxAyK4CFUKdhS_1.wireOp",EDGE,"1cb9c079-ea9b-4899-8069-e0e3048e911d.sketch_text.stroke-146"),sQuery(id+"FHMxAyK4CFUKdhS_1.wireOp",EDGE,"1cb9c079-ea9b-4899-8069-e0e3048e911d.sketch_text.stroke-147"),sQuery(id+"FHMxAyK4CFUKdhS_1.wireOp",EDGE,"1cb9c079-ea9b-4899-8069-e0e3048e911d.sketch_text.stroke-148"),sQuery(id+"FHMxAyK4CFUKdhS_1.wireOp",EDGE,"1cb9c079-ea9b-4899-8069-e0e3048e911d.sketch_text.stroke-149"),sQuery(id+"FHMxAyK4CFUKdhS_1.wireOp",EDGE,"1cb9c079-ea9b-4899-8069-e0e3048e911d.sketch_text.stroke-150"),sQuery(id+"FHMxAyK4CFUKdhS_1.wireOp",EDGE,"1cb9c079-ea9b-4899-8069-e0e3048e911d.sketch_text.stroke-151"),sQuery(id+"FHMxAyK4CFUKdhS_1.wireOp",EDGE,"1cb9c079-ea9b-4899-8069-e0e3048e911d.sketch_text.stroke-152"),sQuery(id+"FHMxAyK4CFUKdhS_1.wireOp",EDGE,"1cb9c079-ea9b-4899-8069-e0e3048e911d.sketch_text.stroke-153"),sQuery(id+"FHMxAyK4CFUKdhS_1.wireOp",EDGE,"1cb9c079-ea9b-4899-8069-e0e3048e911d.sketch_text.stroke-159"),sQuery(id+"FHMxAyK4CFUKdhS_1.wireOp",EDGE,"1cb9c079-ea9b-4899-8069-e0e3048e911d.sketch_text.stroke-160"),sQuery(id+"FHMxAyK4CFUKdhS_1.wireOp",EDGE,"1cb9c079-ea9b-4899-8069-e0e3048e911d.sketch_text.stroke-161"),sQuery(id+"FHMxAyK4CFUKdhS_1.wireOp",EDGE,"1cb9c079-ea9b-4899-8069-e0e3048e911d.sketch_text.stroke-162"),sQuery(id+"FHMxAyK4CFUKdhS_1.wireOp",EDGE,"1cb9c079-ea9b-4899-8069-e0e3048e911d.sketch_text.stroke-163"),sQuery(id+"FHMxAyK4CFUKdhS_1.wireOp",EDGE,"1cb9c079-ea9b-4899-8069-e0e3048e911d.sketch_text.stroke-164"),sQuery(id+"FHMxAyK4CFUKdhS_1.wireOp",EDGE,"1cb9c079-ea9b-4899-8069-e0e3048e911d.sketch_text.stroke-165"),sQuery(id+"FHMxAyK4CFUKdhS_1.wireOp",EDGE,"1cb9c079-ea9b-4899-8069-e0e3048e911d.sketch_text.stroke-166"),sQuery(id+"FHMxAyK4CFUKdhS_1.wireOp",EDGE,"1cb9c079-ea9b-4899-8069-e0e3048e911d.sketch_text.stroke-167"),sQuery(id+"FHMxAyK4CFUKdhS_1.wireOp",EDGE,"1cb9c079-ea9b-4899-8069-e0e3048e911d.sketch_text.stroke-168"),sQuery(id+"FHMxAyK4CFUKdhS_1.wireOp",EDGE,"1cb9c079-ea9b-4899-8069-e0e3048e911d.sketch_text.stroke-169"),sQuery(id+"FHMxAyK4CFUKdhS_1.wireOp",EDGE,"1cb9c079-ea9b-4899-8069-e0e3048e911d.sketch_text.stroke-170"),sQuery(id+"FHMxAyK4CFUKdhS_1.wireOp",EDGE,"1cb9c079-ea9b-4899-8069-e0e3048e911d.sketch_text.stroke-171"),sQuery(id+"FHMxAyK4CFUKdhS_1.wireOp",EDGE,"1cb9c079-ea9b-4899-8069-e0e3048e911d.sketch_text.stroke-172"),sQuery(id+"FHMxAyK4CFUKdhS_1.wireOp",EDGE,"1cb9c079-ea9b-4899-8069-e0e3048e911d.sketch_text.stroke-173"),sQuery(id+"FHMxAyK4CFUKdhS_1.wireOp",EDGE,"1cb9c079-ea9b-4899-8069-e0e3048e911d.sketch_text.stroke-174"),sQuery(id+"FHMxAyK4CFUKdhS_1.wireOp",EDGE,"1cb9c079-ea9b-4899-8069-e0e3048e911d.sketch_text.stroke-175"),sQuery(id+"FHMxAyK4CFUKdhS_1.wireOp",EDGE,"1cb9c079-ea9b-4899-8069-e0e3048e911d.sketch_text.stroke-176"),sQuery(id+"FHMxAyK4CFUKdhS_1.wireOp",EDGE,"1cb9c079-ea9b-4899-8069-e0e3048e911d.sketch_text.stroke-177"),sQuery(id+"FHMxAyK4CFUKdhS_1.wireOp",EDGE,"1cb9c079-ea9b-4899-8069-e0e3048e911d.sketch_text.stroke-178"),sQuery(id+"FHMxAyK4CFUKdhS_1.wireOp",EDGE,"1cb9c079-ea9b-4899-8069-e0e3048e911d.sketch_text.stroke-179"),sQuery(id+"FHMxAyK4CFUKdhS_1.wireOp",EDGE,"1cb9c079-ea9b-4899-8069-e0e3048e911d.sketch_text.stroke-180"),subQ2,sQuery(id+"F2.wireOp",EDGE,"6ee83ff3-586e-4dbe-aaea-af71240543bd")])],"isStart":true})]),OD(1.0)],"derivedFrom":makeQuery(id+"F1.opExtrude","CAP_EDGE",EDGE,{"disambiguationData":[OSD([subQ0])],"isStart":false})});}
            var Q5;
            {var subQ0=sQuery(id+"F0.wireOp",EDGE,"E0.top");var subQ1=sQuery(id+"F0.wireOp",EDGE,"E0.bottom");var subQ2=sQuery(id+"F2.wireOp",EDGE,"8007402e-1a4e-4a06-85a5-2af08e553504");Q5=makeQuery(id+"F3.boolean.opBoolean","SPLIT",EDGE,{"disambiguationData":[TD([makeQuery(id+"F1.opExtrude","CAP_FACE",FACE,{"disambiguationData":[OSD([subQ1,subQ0,sQuery(id+"F0.wireOp",EDGE,"E0.left"),sQuery(id+"F0.wireOp",EDGE,"E0.right")])],"isStart":false}),makeQuery(id+"F1.opExtrude","SWEPT_FACE",FACE,{"disambiguationData":[OSD([subQ0])]}),makeQuery(id+"F3.opExtrude","SWEPT_FACE",FACE,{"disambiguationData":[OSD([subQ2])]}),makeQuery(id+"F3.opExtrude","CAP_FACE",FACE,{"disambiguationData":[OSD([subQ1,sQuery(id+"FQ5JFwxVdaqARUP_1.wireOp",EDGE,"fcba4419-a2ee-464f-be9d-58f11bf3418b.sketch_text.stroke-0"),sQuery(id+"FQ5JFwxVdaqARUP_1.wireOp",EDGE,"fcba4419-a2ee-464f-be9d-58f11bf3418b.sketch_text.stroke-1"),sQuery(id+"FQ5JFwxVdaqARUP_1.wireOp",EDGE,"fcba4419-a2ee-464f-be9d-58f11bf3418b.sketch_text.stroke-2"),sQuery(id+"FQ5JFwxVdaqARUP_1.wireOp",EDGE,"fcba4419-a2ee-464f-be9d-58f11bf3418b.sketch_text.stroke-3"),sQuery(id+"FQ5JFwxVdaqARUP_1.wireOp",EDGE,"fcba4419-a2ee-464f-be9d-58f11bf3418b.sketch_text.stroke-4"),sQuery(id+"FQ5JFwxVdaqARUP_1.wireOp",EDGE,"fcba4419-a2ee-464f-be9d-58f11bf3418b.sketch_text.stroke-5"),sQuery(id+"FQ5JFwxVdaqARUP_1.wireOp",EDGE,"fcba4419-a2ee-464f-be9d-58f11bf3418b.sketch_text.stroke-6"),sQuery(id+"FQ5JFwxVdaqARUP_1.wireOp",EDGE,"fcba4419-a2ee-464f-be9d-58f11bf3418b.sketch_text.stroke-7"),sQuery(id+"FQ5JFwxVdaqARUP_1.wireOp",EDGE,"fcba4419-a2ee-464f-be9d-58f11bf3418b.sketch_text.stroke-8"),sQuery(id+"FQ5JFwxVdaqARUP_1.wireOp",EDGE,"fcba4419-a2ee-464f-be9d-58f11bf3418b.sketch_text.stroke-9"),sQuery(id+"FQ5JFwxVdaqARUP_1.wireOp",EDGE,"fcba4419-a2ee-464f-be9d-58f11bf3418b.sketch_text.stroke-10"),sQuery(id+"FQ5JFwxVdaqARUP_1.wireOp",EDGE,"fcba4419-a2ee-464f-be9d-58f11bf3418b.sketch_text.stroke-11"),sQuery(id+"FQ5JFwxVdaqARUP_1.wireOp",EDGE,"fcba4419-a2ee-464f-be9d-58f11bf3418b.sketch_text.stroke-12"),sQuery(id+"FQ5JFwxVdaqARUP_1.wireOp",EDGE,"fcba4419-a2ee-464f-be9d-58f11bf3418b.sketch_text.stroke-13"),sQuery(id+"FQ5JFwxVdaqARUP_1.wireOp",EDGE,"fcba4419-a2ee-464f-be9d-58f11bf3418b.sketch_text.stroke-14"),sQuery(id+"FQ5JFwxVdaqARUP_1.wireOp",EDGE,"fcba4419-a2ee-464f-be9d-58f11bf3418b.sketch_text.stroke-15"),sQuery(id+"FQ5JFwxVdaqARUP_1.wireOp",EDGE,"fcba4419-a2ee-464f-be9d-58f11bf3418b.sketch_text.stroke-16"),sQuery(id+"FQ5JFwxVdaqARUP_1.wireOp",EDGE,"fcba4419-a2ee-464f-be9d-58f11bf3418b.sketch_text.stroke-17"),sQuery(id+"FQ5JFwxVdaqARUP_1.wireOp",EDGE,"fcba4419-a2ee-464f-be9d-58f11bf3418b.sketch_text.stroke-18"),sQuery(id+"FQ5JFwxVdaqARUP_1.wireOp",EDGE,"fcba4419-a2ee-464f-be9d-58f11bf3418b.sketch_text.stroke-19"),sQuery(id+"FQ5JFwxVdaqARUP_1.wireOp",EDGE,"fcba4419-a2ee-464f-be9d-58f11bf3418b.sketch_text.stroke-20"),sQuery(id+"FQ5JFwxVdaqARUP_1.wireOp",EDGE,"fcba4419-a2ee-464f-be9d-58f11bf3418b.sketch_text.stroke-21"),sQuery(id+"FQ5JFwxVdaqARUP_1.wireOp",EDGE,"fcba4419-a2ee-464f-be9d-58f11bf3418b.sketch_text.stroke-22"),sQuery(id+"FQ5JFwxVdaqARUP_1.wireOp",EDGE,"fcba4419-a2ee-464f-be9d-58f11bf3418b.sketch_text.stroke-23"),sQuery(id+"FQ5JFwxVdaqARUP_1.wireOp",EDGE,"fcba4419-a2ee-464f-be9d-58f11bf3418b.sketch_text.stroke-24"),sQuery(id+"FQ5JFwxVdaqARUP_1.wireOp",EDGE,"fcba4419-a2ee-464f-be9d-58f11bf3418b.sketch_text.stroke-25"),sQuery(id+"FQ5JFwxVdaqARUP_1.wireOp",EDGE,"fcba4419-a2ee-464f-be9d-58f11bf3418b.sketch_text.stroke-26"),sQuery(id+"FQ5JFwxVdaqARUP_1.wireOp",EDGE,"fcba4419-a2ee-464f-be9d-58f11bf3418b.sketch_text.stroke-27"),sQuery(id+"FQ5JFwxVdaqARUP_1.wireOp",EDGE,"fcba4419-a2ee-464f-be9d-58f11bf3418b.sketch_text.stroke-28"),sQuery(id+"FQ5JFwxVdaqARUP_1.wireOp",EDGE,"fcba4419-a2ee-464f-be9d-58f11bf3418b.sketch_text.stroke-29"),sQuery(id+"FQ5JFwxVdaqARUP_1.wireOp",EDGE,"fcba4419-a2ee-464f-be9d-58f11bf3418b.sketch_text.stroke-30"),sQuery(id+"FQ5JFwxVdaqARUP_1.wireOp",EDGE,"fcba4419-a2ee-464f-be9d-58f11bf3418b.sketch_text.stroke-31"),sQuery(id+"FQ5JFwxVdaqARUP_1.wireOp",EDGE,"fcba4419-a2ee-464f-be9d-58f11bf3418b.sketch_text.stroke-32"),sQuery(id+"FQ5JFwxVdaqARUP_1.wireOp",EDGE,"fcba4419-a2ee-464f-be9d-58f11bf3418b.sketch_text.stroke-33"),sQuery(id+"FQ5JFwxVdaqARUP_1.wireOp",EDGE,"fcba4419-a2ee-464f-be9d-58f11bf3418b.sketch_text.stroke-34"),sQuery(id+"FQ5JFwxVdaqARUP_1.wireOp",EDGE,"fcba4419-a2ee-464f-be9d-58f11bf3418b.sketch_text.stroke-35"),sQuery(id+"FQ5JFwxVdaqARUP_1.wireOp",EDGE,"fcba4419-a2ee-464f-be9d-58f11bf3418b.sketch_text.stroke-36"),sQuery(id+"FQ5JFwxVdaqARUP_1.wireOp",EDGE,"fcba4419-a2ee-464f-be9d-58f11bf3418b.sketch_text.stroke-37"),sQuery(id+"FQ5JFwxVdaqARUP_1.wireOp",EDGE,"fcba4419-a2ee-464f-be9d-58f11bf3418b.sketch_text.stroke-38"),sQuery(id+"FQ5JFwxVdaqARUP_1.wireOp",EDGE,"fcba4419-a2ee-464f-be9d-58f11bf3418b.sketch_text.stroke-39"),sQuery(id+"FQ5JFwxVdaqARUP_1.wireOp",EDGE,"fcba4419-a2ee-464f-be9d-58f11bf3418b.sketch_text.stroke-40"),sQuery(id+"FQ5JFwxVdaqARUP_1.wireOp",EDGE,"fcba4419-a2ee-464f-be9d-58f11bf3418b.sketch_text.stroke-41"),sQuery(id+"FQ5JFwxVdaqARUP_1.wireOp",EDGE,"fcba4419-a2ee-464f-be9d-58f11bf3418b.sketch_text.stroke-42"),sQuery(id+"FQ5JFwxVdaqARUP_1.wireOp",EDGE,"fcba4419-a2ee-464f-be9d-58f11bf3418b.sketch_text.stroke-43"),sQuery(id+"FQ5JFwxVdaqARUP_1.wireOp",EDGE,"fcba4419-a2ee-464f-be9d-58f11bf3418b.sketch_text.stroke-44"),sQuery(id+"FQ5JFwxVdaqARUP_1.wireOp",EDGE,"fcba4419-a2ee-464f-be9d-58f11bf3418b.sketch_text.stroke-45"),sQuery(id+"FQ5JFwxVdaqARUP_1.wireOp",EDGE,"fcba4419-a2ee-464f-be9d-58f11bf3418b.sketch_text.stroke-46"),sQuery(id+"FQ5JFwxVdaqARUP_1.wireOp",EDGE,"fcba4419-a2ee-464f-be9d-58f11bf3418b.sketch_text.stroke-47"),sQuery(id+"FQ5JFwxVdaqARUP_1.wireOp",EDGE,"fcba4419-a2ee-464f-be9d-58f11bf3418b.sketch_text.stroke-48"),sQuery(id+"FQ5JFwxVdaqARUP_1.wireOp",EDGE,"fcba4419-a2ee-464f-be9d-58f11bf3418b.sketch_text.stroke-49"),sQuery(id+"FQ5JFwxVdaqARUP_1.wireOp",EDGE,"fcba4419-a2ee-464f-be9d-58f11bf3418b.sketch_text.stroke-50"),sQuery(id+"FQ5JFwxVdaqARUP_1.wireOp",EDGE,"fcba4419-a2ee-464f-be9d-58f11bf3418b.sketch_text.stroke-51"),sQuery(id+"FQ5JFwxVdaqARUP_1.wireOp",EDGE,"fcba4419-a2ee-464f-be9d-58f11bf3418b.sketch_text.stroke-52"),sQuery(id+"FQ5JFwxVdaqARUP_1.wireOp",EDGE,"fcba4419-a2ee-464f-be9d-58f11bf3418b.sketch_text.stroke-53"),sQuery(id+"FQ5JFwxVdaqARUP_1.wireOp",EDGE,"fcba4419-a2ee-464f-be9d-58f11bf3418b.sketch_text.stroke-54"),sQuery(id+"FQ5JFwxVdaqARUP_1.wireOp",EDGE,"fcba4419-a2ee-464f-be9d-58f11bf3418b.sketch_text.stroke-55"),sQuery(id+"FQ5JFwxVdaqARUP_1.wireOp",EDGE,"fcba4419-a2ee-464f-be9d-58f11bf3418b.sketch_text.stroke-56"),sQuery(id+"FQ5JFwxVdaqARUP_1.wireOp",EDGE,"fcba4419-a2ee-464f-be9d-58f11bf3418b.sketch_text.stroke-57"),sQuery(id+"FQ5JFwxVdaqARUP_1.wireOp",EDGE,"fcba4419-a2ee-464f-be9d-58f11bf3418b.sketch_text.stroke-58"),sQuery(id+"FQ5JFwxVdaqARUP_1.wireOp",EDGE,"fcba4419-a2ee-464f-be9d-58f11bf3418b.sketch_text.stroke-59"),sQuery(id+"FQ5JFwxVdaqARUP_1.wireOp",EDGE,"fcba4419-a2ee-464f-be9d-58f11bf3418b.sketch_text.stroke-60"),sQuery(id+"FQ5JFwxVdaqARUP_1.wireOp",EDGE,"fcba4419-a2ee-464f-be9d-58f11bf3418b.sketch_text.stroke-61"),sQuery(id+"FQ5JFwxVdaqARUP_1.wireOp",EDGE,"fcba4419-a2ee-464f-be9d-58f11bf3418b.sketch_text.stroke-62"),sQuery(id+"FQ5JFwxVdaqARUP_1.wireOp",EDGE,"fcba4419-a2ee-464f-be9d-58f11bf3418b.sketch_text.stroke-63"),sQuery(id+"FQ5JFwxVdaqARUP_1.wireOp",EDGE,"fcba4419-a2ee-464f-be9d-58f11bf3418b.sketch_text.stroke-64"),sQuery(id+"FQ5JFwxVdaqARUP_1.wireOp",EDGE,"fcba4419-a2ee-464f-be9d-58f11bf3418b.sketch_text.stroke-65"),sQuery(id+"FQ5JFwxVdaqARUP_1.wireOp",EDGE,"fcba4419-a2ee-464f-be9d-58f11bf3418b.sketch_text.stroke-66"),sQuery(id+"FQ5JFwxVdaqARUP_1.wireOp",EDGE,"fcba4419-a2ee-464f-be9d-58f11bf3418b.sketch_text.stroke-67"),sQuery(id+"FQ5JFwxVdaqARUP_1.wireOp",EDGE,"fcba4419-a2ee-464f-be9d-58f11bf3418b.sketch_text.stroke-68"),sQuery(id+"FQ5JFwxVdaqARUP_1.wireOp",EDGE,"fcba4419-a2ee-464f-be9d-58f11bf3418b.sketch_text.stroke-69"),sQuery(id+"FQ5JFwxVdaqARUP_1.wireOp",EDGE,"fcba4419-a2ee-464f-be9d-58f11bf3418b.sketch_text.stroke-70"),sQuery(id+"FQ5JFwxVdaqARUP_1.wireOp",EDGE,"fcba4419-a2ee-464f-be9d-58f11bf3418b.sketch_text.stroke-71"),sQuery(id+"FQ5JFwxVdaqARUP_1.wireOp",EDGE,"fcba4419-a2ee-464f-be9d-58f11bf3418b.sketch_text.stroke-72"),sQuery(id+"FQ5JFwxVdaqARUP_1.wireOp",EDGE,"fcba4419-a2ee-464f-be9d-58f11bf3418b.sketch_text.stroke-73"),sQuery(id+"FQ5JFwxVdaqARUP_1.wireOp",EDGE,"fcba4419-a2ee-464f-be9d-58f11bf3418b.sketch_text.stroke-74"),sQuery(id+"FQ5JFwxVdaqARUP_1.wireOp",EDGE,"fcba4419-a2ee-464f-be9d-58f11bf3418b.sketch_text.stroke-75"),sQuery(id+"FQ5JFwxVdaqARUP_1.wireOp",EDGE,"fcba4419-a2ee-464f-be9d-58f11bf3418b.sketch_text.stroke-76"),sQuery(id+"FQ5JFwxVdaqARUP_1.wireOp",EDGE,"fcba4419-a2ee-464f-be9d-58f11bf3418b.sketch_text.stroke-77"),sQuery(id+"FQ5JFwxVdaqARUP_1.wireOp",EDGE,"fcba4419-a2ee-464f-be9d-58f11bf3418b.sketch_text.stroke-78"),sQuery(id+"FQ5JFwxVdaqARUP_1.wireOp",EDGE,"fcba4419-a2ee-464f-be9d-58f11bf3418b.sketch_text.stroke-79"),sQuery(id+"FQ5JFwxVdaqARUP_1.wireOp",EDGE,"fcba4419-a2ee-464f-be9d-58f11bf3418b.sketch_text.stroke-80"),sQuery(id+"FQ5JFwxVdaqARUP_1.wireOp",EDGE,"fcba4419-a2ee-464f-be9d-58f11bf3418b.sketch_text.stroke-81"),sQuery(id+"FQ5JFwxVdaqARUP_1.wireOp",EDGE,"fcba4419-a2ee-464f-be9d-58f11bf3418b.sketch_text.stroke-82"),sQuery(id+"FQ5JFwxVdaqARUP_1.wireOp",EDGE,"fcba4419-a2ee-464f-be9d-58f11bf3418b.sketch_text.stroke-83"),sQuery(id+"FQ5JFwxVdaqARUP_1.wireOp",EDGE,"fcba4419-a2ee-464f-be9d-58f11bf3418b.sketch_text.stroke-84"),sQuery(id+"FQ5JFwxVdaqARUP_1.wireOp",EDGE,"fcba4419-a2ee-464f-be9d-58f11bf3418b.sketch_text.stroke-85"),sQuery(id+"FQ5JFwxVdaqARUP_1.wireOp",EDGE,"fcba4419-a2ee-464f-be9d-58f11bf3418b.sketch_text.stroke-86"),sQuery(id+"FQ5JFwxVdaqARUP_1.wireOp",EDGE,"fcba4419-a2ee-464f-be9d-58f11bf3418b.sketch_text.stroke-87"),sQuery(id+"FQ5JFwxVdaqARUP_1.wireOp",EDGE,"fcba4419-a2ee-464f-be9d-58f11bf3418b.sketch_text.stroke-88"),sQuery(id+"FQ5JFwxVdaqARUP_1.wireOp",EDGE,"fcba4419-a2ee-464f-be9d-58f11bf3418b.sketch_text.stroke-89"),sQuery(id+"FQ5JFwxVdaqARUP_1.wireOp",EDGE,"fcba4419-a2ee-464f-be9d-58f11bf3418b.sketch_text.stroke-90"),sQuery(id+"FQ5JFwxVdaqARUP_1.wireOp",EDGE,"fcba4419-a2ee-464f-be9d-58f11bf3418b.sketch_text.stroke-91"),sQuery(id+"FQ5JFwxVdaqARUP_1.wireOp",EDGE,"fcba4419-a2ee-464f-be9d-58f11bf3418b.sketch_text.stroke-92"),sQuery(id+"FQ5JFwxVdaqARUP_1.wireOp",EDGE,"fcba4419-a2ee-464f-be9d-58f11bf3418b.sketch_text.stroke-93"),sQuery(id+"FQ5JFwxVdaqARUP_1.wireOp",EDGE,"fcba4419-a2ee-464f-be9d-58f11bf3418b.sketch_text.stroke-94"),sQuery(id+"FQ5JFwxVdaqARUP_1.wireOp",EDGE,"fcba4419-a2ee-464f-be9d-58f11bf3418b.sketch_text.stroke-95"),sQuery(id+"FQ5JFwxVdaqARUP_1.wireOp",EDGE,"fcba4419-a2ee-464f-be9d-58f11bf3418b.sketch_text.stroke-96"),sQuery(id+"FQ5JFwxVdaqARUP_1.wireOp",EDGE,"fcba4419-a2ee-464f-be9d-58f11bf3418b.sketch_text.stroke-97"),sQuery(id+"FQ5JFwxVdaqARUP_1.wireOp",EDGE,"fcba4419-a2ee-464f-be9d-58f11bf3418b.sketch_text.stroke-98"),sQuery(id+"FQ5JFwxVdaqARUP_1.wireOp",EDGE,"fcba4419-a2ee-464f-be9d-58f11bf3418b.sketch_text.stroke-99"),sQuery(id+"FQ5JFwxVdaqARUP_1.wireOp",EDGE,"fcba4419-a2ee-464f-be9d-58f11bf3418b.sketch_text.stroke-100"),sQuery(id+"FQ5JFwxVdaqARUP_1.wireOp",EDGE,"fcba4419-a2ee-464f-be9d-58f11bf3418b.sketch_text.stroke-101"),sQuery(id+"FQ5JFwxVdaqARUP_1.wireOp",EDGE,"fcba4419-a2ee-464f-be9d-58f11bf3418b.sketch_text.stroke-102"),sQuery(id+"FQ5JFwxVdaqARUP_1.wireOp",EDGE,"fcba4419-a2ee-464f-be9d-58f11bf3418b.sketch_text.stroke-103"),sQuery(id+"FQ5JFwxVdaqARUP_1.wireOp",EDGE,"fcba4419-a2ee-464f-be9d-58f11bf3418b.sketch_text.stroke-104"),sQuery(id+"FQ5JFwxVdaqARUP_1.wireOp",EDGE,"fcba4419-a2ee-464f-be9d-58f11bf3418b.sketch_text.stroke-105"),sQuery(id+"FQ5JFwxVdaqARUP_1.wireOp",EDGE,"fcba4419-a2ee-464f-be9d-58f11bf3418b.sketch_text.stroke-106"),sQuery(id+"FQ5JFwxVdaqARUP_1.wireOp",EDGE,"fcba4419-a2ee-464f-be9d-58f11bf3418b.sketch_text.stroke-107"),sQuery(id+"FQ5JFwxVdaqARUP_1.wireOp",EDGE,"fcba4419-a2ee-464f-be9d-58f11bf3418b.sketch_text.stroke-108"),sQuery(id+"FQ5JFwxVdaqARUP_1.wireOp",EDGE,"fcba4419-a2ee-464f-be9d-58f11bf3418b.sketch_text.stroke-109"),sQuery(id+"FQ5JFwxVdaqARUP_1.wireOp",EDGE,"fcba4419-a2ee-464f-be9d-58f11bf3418b.sketch_text.stroke-110"),sQuery(id+"FQ5JFwxVdaqARUP_1.wireOp",EDGE,"fcba4419-a2ee-464f-be9d-58f11bf3418b.sketch_text.stroke-111"),sQuery(id+"FQ5JFwxVdaqARUP_1.wireOp",EDGE,"fcba4419-a2ee-464f-be9d-58f11bf3418b.sketch_text.stroke-112"),sQuery(id+"FQ5JFwxVdaqARUP_1.wireOp",EDGE,"fcba4419-a2ee-464f-be9d-58f11bf3418b.sketch_text.stroke-113"),sQuery(id+"FQ5JFwxVdaqARUP_1.wireOp",EDGE,"fcba4419-a2ee-464f-be9d-58f11bf3418b.sketch_text.stroke-114"),sQuery(id+"FQ5JFwxVdaqARUP_1.wireOp",EDGE,"fcba4419-a2ee-464f-be9d-58f11bf3418b.sketch_text.stroke-115"),sQuery(id+"FQ5JFwxVdaqARUP_1.wireOp",EDGE,"fcba4419-a2ee-464f-be9d-58f11bf3418b.sketch_text.stroke-116"),sQuery(id+"FQ5JFwxVdaqARUP_1.wireOp",EDGE,"fcba4419-a2ee-464f-be9d-58f11bf3418b.sketch_text.stroke-117"),sQuery(id+"FQ5JFwxVdaqARUP_1.wireOp",EDGE,"fcba4419-a2ee-464f-be9d-58f11bf3418b.sketch_text.stroke-118"),sQuery(id+"FQ5JFwxVdaqARUP_1.wireOp",EDGE,"fcba4419-a2ee-464f-be9d-58f11bf3418b.sketch_text.stroke-119"),sQuery(id+"FQ5JFwxVdaqARUP_1.wireOp",EDGE,"fcba4419-a2ee-464f-be9d-58f11bf3418b.sketch_text.stroke-120"),sQuery(id+"FQ5JFwxVdaqARUP_1.wireOp",EDGE,"fcba4419-a2ee-464f-be9d-58f11bf3418b.sketch_text.stroke-121"),sQuery(id+"FQ5JFwxVdaqARUP_1.wireOp",EDGE,"fcba4419-a2ee-464f-be9d-58f11bf3418b.sketch_text.stroke-122"),sQuery(id+"FQ5JFwxVdaqARUP_1.wireOp",EDGE,"fcba4419-a2ee-464f-be9d-58f11bf3418b.sketch_text.stroke-123"),sQuery(id+"FQ5JFwxVdaqARUP_1.wireOp",EDGE,"fcba4419-a2ee-464f-be9d-58f11bf3418b.sketch_text.stroke-124"),sQuery(id+"FQ5JFwxVdaqARUP_1.wireOp",EDGE,"fcba4419-a2ee-464f-be9d-58f11bf3418b.sketch_text.stroke-125"),sQuery(id+"FQ5JFwxVdaqARUP_1.wireOp",EDGE,"fcba4419-a2ee-464f-be9d-58f11bf3418b.sketch_text.stroke-126"),sQuery(id+"FQ5JFwxVdaqARUP_1.wireOp",EDGE,"fcba4419-a2ee-464f-be9d-58f11bf3418b.sketch_text.stroke-127"),sQuery(id+"FQ5JFwxVdaqARUP_1.wireOp",EDGE,"fcba4419-a2ee-464f-be9d-58f11bf3418b.sketch_text.stroke-128"),sQuery(id+"FQ5JFwxVdaqARUP_1.wireOp",EDGE,"fcba4419-a2ee-464f-be9d-58f11bf3418b.sketch_text.stroke-129"),sQuery(id+"FQ5JFwxVdaqARUP_1.wireOp",EDGE,"fcba4419-a2ee-464f-be9d-58f11bf3418b.sketch_text.stroke-130"),sQuery(id+"FQ5JFwxVdaqARUP_1.wireOp",EDGE,"fcba4419-a2ee-464f-be9d-58f11bf3418b.sketch_text.stroke-131"),sQuery(id+"FQ5JFwxVdaqARUP_1.wireOp",EDGE,"fcba4419-a2ee-464f-be9d-58f11bf3418b.sketch_text.stroke-132"),sQuery(id+"FQ5JFwxVdaqARUP_1.wireOp",EDGE,"fcba4419-a2ee-464f-be9d-58f11bf3418b.sketch_text.stroke-133"),sQuery(id+"FQ5JFwxVdaqARUP_1.wireOp",EDGE,"fcba4419-a2ee-464f-be9d-58f11bf3418b.sketch_text.stroke-134"),sQuery(id+"FQ5JFwxVdaqARUP_1.wireOp",EDGE,"fcba4419-a2ee-464f-be9d-58f11bf3418b.sketch_text.stroke-135"),sQuery(id+"FQ5JFwxVdaqARUP_1.wireOp",EDGE,"fcba4419-a2ee-464f-be9d-58f11bf3418b.sketch_text.stroke-136"),sQuery(id+"FQ5JFwxVdaqARUP_1.wireOp",EDGE,"fcba4419-a2ee-464f-be9d-58f11bf3418b.sketch_text.stroke-137"),sQuery(id+"FQ5JFwxVdaqARUP_1.wireOp",EDGE,"fcba4419-a2ee-464f-be9d-58f11bf3418b.sketch_text.stroke-138"),sQuery(id+"FQ5JFwxVdaqARUP_1.wireOp",EDGE,"fcba4419-a2ee-464f-be9d-58f11bf3418b.sketch_text.stroke-139"),sQuery(id+"FQ5JFwxVdaqARUP_1.wireOp",EDGE,"fcba4419-a2ee-464f-be9d-58f11bf3418b.sketch_text.stroke-140"),sQuery(id+"FQ5JFwxVdaqARUP_1.wireOp",EDGE,"fcba4419-a2ee-464f-be9d-58f11bf3418b.sketch_text.stroke-141"),sQuery(id+"FQ5JFwxVdaqARUP_1.wireOp",EDGE,"fcba4419-a2ee-464f-be9d-58f11bf3418b.sketch_text.stroke-142"),sQuery(id+"FQ5JFwxVdaqARUP_1.wireOp",EDGE,"fcba4419-a2ee-464f-be9d-58f11bf3418b.sketch_text.stroke-143"),sQuery(id+"FQ5JFwxVdaqARUP_1.wireOp",EDGE,"fcba4419-a2ee-464f-be9d-58f11bf3418b.sketch_text.stroke-144"),sQuery(id+"FQ5JFwxVdaqARUP_1.wireOp",EDGE,"fcba4419-a2ee-464f-be9d-58f11bf3418b.sketch_text.stroke-145"),sQuery(id+"FQ5JFwxVdaqARUP_1.wireOp",EDGE,"fcba4419-a2ee-464f-be9d-58f11bf3418b.sketch_text.stroke-146"),sQuery(id+"FQ5JFwxVdaqARUP_1.wireOp",EDGE,"fcba4419-a2ee-464f-be9d-58f11bf3418b.sketch_text.stroke-147"),sQuery(id+"FQ5JFwxVdaqARUP_1.wireOp",EDGE,"fcba4419-a2ee-464f-be9d-58f11bf3418b.sketch_text.stroke-148"),sQuery(id+"FQ5JFwxVdaqARUP_1.wireOp",EDGE,"fcba4419-a2ee-464f-be9d-58f11bf3418b.sketch_text.stroke-149"),sQuery(id+"FQ5JFwxVdaqARUP_1.wireOp",EDGE,"fcba4419-a2ee-464f-be9d-58f11bf3418b.sketch_text.stroke-150"),sQuery(id+"FQ5JFwxVdaqARUP_1.wireOp",EDGE,"fcba4419-a2ee-464f-be9d-58f11bf3418b.sketch_text.stroke-151"),sQuery(id+"FQ5JFwxVdaqARUP_1.wireOp",EDGE,"fcba4419-a2ee-464f-be9d-58f11bf3418b.sketch_text.stroke-152"),sQuery(id+"FQ5JFwxVdaqARUP_1.wireOp",EDGE,"fcba4419-a2ee-464f-be9d-58f11bf3418b.sketch_text.stroke-153"),sQuery(id+"FQ5JFwxVdaqARUP_1.wireOp",EDGE,"fcba4419-a2ee-464f-be9d-58f11bf3418b.sketch_text.stroke-154"),sQuery(id+"FQ5JFwxVdaqARUP_1.wireOp",EDGE,"fcba4419-a2ee-464f-be9d-58f11bf3418b.sketch_text.stroke-155"),sQuery(id+"FQ5JFwxVdaqARUP_1.wireOp",EDGE,"fcba4419-a2ee-464f-be9d-58f11bf3418b.sketch_text.stroke-156"),sQuery(id+"FQ5JFwxVdaqARUP_1.wireOp",EDGE,"fcba4419-a2ee-464f-be9d-58f11bf3418b.sketch_text.stroke-157"),sQuery(id+"FQ5JFwxVdaqARUP_1.wireOp",EDGE,"fcba4419-a2ee-464f-be9d-58f11bf3418b.sketch_text.stroke-158"),sQuery(id+"FQ5JFwxVdaqARUP_1.wireOp",EDGE,"fcba4419-a2ee-464f-be9d-58f11bf3418b.sketch_text.stroke-159"),sQuery(id+"FQ5JFwxVdaqARUP_1.wireOp",EDGE,"fcba4419-a2ee-464f-be9d-58f11bf3418b.sketch_text.stroke-160"),sQuery(id+"FQ5JFwxVdaqARUP_1.wireOp",EDGE,"fcba4419-a2ee-464f-be9d-58f11bf3418b.sketch_text.stroke-161"),sQuery(id+"FQ5JFwxVdaqARUP_1.wireOp",EDGE,"fcba4419-a2ee-464f-be9d-58f11bf3418b.sketch_text.stroke-162"),sQuery(id+"FQ5JFwxVdaqARUP_1.wireOp",EDGE,"fcba4419-a2ee-464f-be9d-58f11bf3418b.sketch_text.stroke-163"),sQuery(id+"FQ5JFwxVdaqARUP_1.wireOp",EDGE,"fcba4419-a2ee-464f-be9d-58f11bf3418b.sketch_text.stroke-164"),sQuery(id+"FQ5JFwxVdaqARUP_1.wireOp",EDGE,"fcba4419-a2ee-464f-be9d-58f11bf3418b.sketch_text.stroke-165"),sQuery(id+"FQ5JFwxVdaqARUP_1.wireOp",EDGE,"fcba4419-a2ee-464f-be9d-58f11bf3418b.sketch_text.stroke-166"),sQuery(id+"FQ5JFwxVdaqARUP_1.wireOp",EDGE,"fcba4419-a2ee-464f-be9d-58f11bf3418b.sketch_text.stroke-167"),sQuery(id+"FQ5JFwxVdaqARUP_1.wireOp",EDGE,"fcba4419-a2ee-464f-be9d-58f11bf3418b.sketch_text.stroke-168"),sQuery(id+"FQ5JFwxVdaqARUP_1.wireOp",EDGE,"fcba4419-a2ee-464f-be9d-58f11bf3418b.sketch_text.stroke-169"),sQuery(id+"FQ5JFwxVdaqARUP_1.wireOp",EDGE,"fcba4419-a2ee-464f-be9d-58f11bf3418b.sketch_text.stroke-170"),sQuery(id+"FQ5JFwxVdaqARUP_1.wireOp",EDGE,"fcba4419-a2ee-464f-be9d-58f11bf3418b.sketch_text.stroke-171"),sQuery(id+"FQ5JFwxVdaqARUP_1.wireOp",EDGE,"fcba4419-a2ee-464f-be9d-58f11bf3418b.sketch_text.stroke-172"),sQuery(id+"FQ5JFwxVdaqARUP_1.wireOp",EDGE,"fcba4419-a2ee-464f-be9d-58f11bf3418b.sketch_text.stroke-173"),sQuery(id+"FHMxAyK4CFUKdhS_1.wireOp",EDGE,"1cb9c079-ea9b-4899-8069-e0e3048e911d.sketch_text.stroke-0"),sQuery(id+"FHMxAyK4CFUKdhS_1.wireOp",EDGE,"1cb9c079-ea9b-4899-8069-e0e3048e911d.sketch_text.stroke-1"),sQuery(id+"FHMxAyK4CFUKdhS_1.wireOp",EDGE,"1cb9c079-ea9b-4899-8069-e0e3048e911d.sketch_text.stroke-2"),sQuery(id+"FHMxAyK4CFUKdhS_1.wireOp",EDGE,"1cb9c079-ea9b-4899-8069-e0e3048e911d.sketch_text.stroke-3"),sQuery(id+"FHMxAyK4CFUKdhS_1.wireOp",EDGE,"1cb9c079-ea9b-4899-8069-e0e3048e911d.sketch_text.stroke-4"),sQuery(id+"FHMxAyK4CFUKdhS_1.wireOp",EDGE,"1cb9c079-ea9b-4899-8069-e0e3048e911d.sketch_text.stroke-5"),sQuery(id+"FHMxAyK4CFUKdhS_1.wireOp",EDGE,"1cb9c079-ea9b-4899-8069-e0e3048e911d.sketch_text.stroke-6"),sQuery(id+"FHMxAyK4CFUKdhS_1.wireOp",EDGE,"1cb9c079-ea9b-4899-8069-e0e3048e911d.sketch_text.stroke-7"),sQuery(id+"FHMxAyK4CFUKdhS_1.wireOp",EDGE,"1cb9c079-ea9b-4899-8069-e0e3048e911d.sketch_text.stroke-8"),sQuery(id+"FHMxAyK4CFUKdhS_1.wireOp",EDGE,"1cb9c079-ea9b-4899-8069-e0e3048e911d.sketch_text.stroke-9"),sQuery(id+"FHMxAyK4CFUKdhS_1.wireOp",EDGE,"1cb9c079-ea9b-4899-8069-e0e3048e911d.sketch_text.stroke-10"),sQuery(id+"FHMxAyK4CFUKdhS_1.wireOp",EDGE,"1cb9c079-ea9b-4899-8069-e0e3048e911d.sketch_text.stroke-11"),sQuery(id+"FHMxAyK4CFUKdhS_1.wireOp",EDGE,"1cb9c079-ea9b-4899-8069-e0e3048e911d.sketch_text.stroke-12"),sQuery(id+"FHMxAyK4CFUKdhS_1.wireOp",EDGE,"1cb9c079-ea9b-4899-8069-e0e3048e911d.sketch_text.stroke-13"),sQuery(id+"FHMxAyK4CFUKdhS_1.wireOp",EDGE,"1cb9c079-ea9b-4899-8069-e0e3048e911d.sketch_text.stroke-14"),sQuery(id+"FHMxAyK4CFUKdhS_1.wireOp",EDGE,"1cb9c079-ea9b-4899-8069-e0e3048e911d.sketch_text.stroke-15"),sQuery(id+"FHMxAyK4CFUKdhS_1.wireOp",EDGE,"1cb9c079-ea9b-4899-8069-e0e3048e911d.sketch_text.stroke-16"),sQuery(id+"FHMxAyK4CFUKdhS_1.wireOp",EDGE,"1cb9c079-ea9b-4899-8069-e0e3048e911d.sketch_text.stroke-17"),sQuery(id+"FHMxAyK4CFUKdhS_1.wireOp",EDGE,"1cb9c079-ea9b-4899-8069-e0e3048e911d.sketch_text.stroke-18"),sQuery(id+"FHMxAyK4CFUKdhS_1.wireOp",EDGE,"1cb9c079-ea9b-4899-8069-e0e3048e911d.sketch_text.stroke-19"),sQuery(id+"FHMxAyK4CFUKdhS_1.wireOp",EDGE,"1cb9c079-ea9b-4899-8069-e0e3048e911d.sketch_text.stroke-20"),sQuery(id+"FHMxAyK4CFUKdhS_1.wireOp",EDGE,"1cb9c079-ea9b-4899-8069-e0e3048e911d.sketch_text.stroke-21"),sQuery(id+"FHMxAyK4CFUKdhS_1.wireOp",EDGE,"1cb9c079-ea9b-4899-8069-e0e3048e911d.sketch_text.stroke-22"),sQuery(id+"FHMxAyK4CFUKdhS_1.wireOp",EDGE,"1cb9c079-ea9b-4899-8069-e0e3048e911d.sketch_text.stroke-23"),sQuery(id+"FHMxAyK4CFUKdhS_1.wireOp",EDGE,"1cb9c079-ea9b-4899-8069-e0e3048e911d.sketch_text.stroke-24"),sQuery(id+"FHMxAyK4CFUKdhS_1.wireOp",EDGE,"1cb9c079-ea9b-4899-8069-e0e3048e911d.sketch_text.stroke-25"),sQuery(id+"FHMxAyK4CFUKdhS_1.wireOp",EDGE,"1cb9c079-ea9b-4899-8069-e0e3048e911d.sketch_text.stroke-26"),sQuery(id+"FHMxAyK4CFUKdhS_1.wireOp",EDGE,"1cb9c079-ea9b-4899-8069-e0e3048e911d.sketch_text.stroke-27"),sQuery(id+"FHMxAyK4CFUKdhS_1.wireOp",EDGE,"1cb9c079-ea9b-4899-8069-e0e3048e911d.sketch_text.stroke-28"),sQuery(id+"FHMxAyK4CFUKdhS_1.wireOp",EDGE,"1cb9c079-ea9b-4899-8069-e0e3048e911d.sketch_text.stroke-29"),sQuery(id+"FHMxAyK4CFUKdhS_1.wireOp",EDGE,"1cb9c079-ea9b-4899-8069-e0e3048e911d.sketch_text.stroke-30"),sQuery(id+"FHMxAyK4CFUKdhS_1.wireOp",EDGE,"1cb9c079-ea9b-4899-8069-e0e3048e911d.sketch_text.stroke-31"),sQuery(id+"FHMxAyK4CFUKdhS_1.wireOp",EDGE,"1cb9c079-ea9b-4899-8069-e0e3048e911d.sketch_text.stroke-32"),sQuery(id+"FHMxAyK4CFUKdhS_1.wireOp",EDGE,"1cb9c079-ea9b-4899-8069-e0e3048e911d.sketch_text.stroke-33"),sQuery(id+"FHMxAyK4CFUKdhS_1.wireOp",EDGE,"1cb9c079-ea9b-4899-8069-e0e3048e911d.sketch_text.stroke-34"),sQuery(id+"FHMxAyK4CFUKdhS_1.wireOp",EDGE,"1cb9c079-ea9b-4899-8069-e0e3048e911d.sketch_text.stroke-35"),sQuery(id+"FHMxAyK4CFUKdhS_1.wireOp",EDGE,"1cb9c079-ea9b-4899-8069-e0e3048e911d.sketch_text.stroke-36"),sQuery(id+"FHMxAyK4CFUKdhS_1.wireOp",EDGE,"1cb9c079-ea9b-4899-8069-e0e3048e911d.sketch_text.stroke-37"),sQuery(id+"FHMxAyK4CFUKdhS_1.wireOp",EDGE,"1cb9c079-ea9b-4899-8069-e0e3048e911d.sketch_text.stroke-38"),sQuery(id+"FHMxAyK4CFUKdhS_1.wireOp",EDGE,"1cb9c079-ea9b-4899-8069-e0e3048e911d.sketch_text.stroke-39"),sQuery(id+"FHMxAyK4CFUKdhS_1.wireOp",EDGE,"1cb9c079-ea9b-4899-8069-e0e3048e911d.sketch_text.stroke-40"),sQuery(id+"FHMxAyK4CFUKdhS_1.wireOp",EDGE,"1cb9c079-ea9b-4899-8069-e0e3048e911d.sketch_text.stroke-41"),sQuery(id+"FHMxAyK4CFUKdhS_1.wireOp",EDGE,"1cb9c079-ea9b-4899-8069-e0e3048e911d.sketch_text.stroke-42"),sQuery(id+"FHMxAyK4CFUKdhS_1.wireOp",EDGE,"1cb9c079-ea9b-4899-8069-e0e3048e911d.sketch_text.stroke-43"),sQuery(id+"FHMxAyK4CFUKdhS_1.wireOp",EDGE,"1cb9c079-ea9b-4899-8069-e0e3048e911d.sketch_text.stroke-44"),sQuery(id+"FHMxAyK4CFUKdhS_1.wireOp",EDGE,"1cb9c079-ea9b-4899-8069-e0e3048e911d.sketch_text.stroke-45"),sQuery(id+"FHMxAyK4CFUKdhS_1.wireOp",EDGE,"1cb9c079-ea9b-4899-8069-e0e3048e911d.sketch_text.stroke-46"),sQuery(id+"FHMxAyK4CFUKdhS_1.wireOp",EDGE,"1cb9c079-ea9b-4899-8069-e0e3048e911d.sketch_text.stroke-47"),sQuery(id+"FHMxAyK4CFUKdhS_1.wireOp",EDGE,"1cb9c079-ea9b-4899-8069-e0e3048e911d.sketch_text.stroke-48"),sQuery(id+"FHMxAyK4CFUKdhS_1.wireOp",EDGE,"1cb9c079-ea9b-4899-8069-e0e3048e911d.sketch_text.stroke-49"),sQuery(id+"FHMxAyK4CFUKdhS_1.wireOp",EDGE,"1cb9c079-ea9b-4899-8069-e0e3048e911d.sketch_text.stroke-50"),sQuery(id+"FHMxAyK4CFUKdhS_1.wireOp",EDGE,"1cb9c079-ea9b-4899-8069-e0e3048e911d.sketch_text.stroke-51"),sQuery(id+"FHMxAyK4CFUKdhS_1.wireOp",EDGE,"1cb9c079-ea9b-4899-8069-e0e3048e911d.sketch_text.stroke-52"),sQuery(id+"FHMxAyK4CFUKdhS_1.wireOp",EDGE,"1cb9c079-ea9b-4899-8069-e0e3048e911d.sketch_text.stroke-53"),sQuery(id+"FHMxAyK4CFUKdhS_1.wireOp",EDGE,"1cb9c079-ea9b-4899-8069-e0e3048e911d.sketch_text.stroke-54"),sQuery(id+"FHMxAyK4CFUKdhS_1.wireOp",EDGE,"1cb9c079-ea9b-4899-8069-e0e3048e911d.sketch_text.stroke-55"),sQuery(id+"FHMxAyK4CFUKdhS_1.wireOp",EDGE,"1cb9c079-ea9b-4899-8069-e0e3048e911d.sketch_text.stroke-56"),sQuery(id+"FHMxAyK4CFUKdhS_1.wireOp",EDGE,"1cb9c079-ea9b-4899-8069-e0e3048e911d.sketch_text.stroke-57"),sQuery(id+"FHMxAyK4CFUKdhS_1.wireOp",EDGE,"1cb9c079-ea9b-4899-8069-e0e3048e911d.sketch_text.stroke-58"),sQuery(id+"FHMxAyK4CFUKdhS_1.wireOp",EDGE,"1cb9c079-ea9b-4899-8069-e0e3048e911d.sketch_text.stroke-59"),sQuery(id+"FHMxAyK4CFUKdhS_1.wireOp",EDGE,"1cb9c079-ea9b-4899-8069-e0e3048e911d.sketch_text.stroke-60"),sQuery(id+"FHMxAyK4CFUKdhS_1.wireOp",EDGE,"1cb9c079-ea9b-4899-8069-e0e3048e911d.sketch_text.stroke-61"),sQuery(id+"FHMxAyK4CFUKdhS_1.wireOp",EDGE,"1cb9c079-ea9b-4899-8069-e0e3048e911d.sketch_text.stroke-62"),sQuery(id+"FHMxAyK4CFUKdhS_1.wireOp",EDGE,"1cb9c079-ea9b-4899-8069-e0e3048e911d.sketch_text.stroke-71"),sQuery(id+"FHMxAyK4CFUKdhS_1.wireOp",EDGE,"1cb9c079-ea9b-4899-8069-e0e3048e911d.sketch_text.stroke-72"),sQuery(id+"FHMxAyK4CFUKdhS_1.wireOp",EDGE,"1cb9c079-ea9b-4899-8069-e0e3048e911d.sketch_text.stroke-73"),sQuery(id+"FHMxAyK4CFUKdhS_1.wireOp",EDGE,"1cb9c079-ea9b-4899-8069-e0e3048e911d.sketch_text.stroke-74"),sQuery(id+"FHMxAyK4CFUKdhS_1.wireOp",EDGE,"1cb9c079-ea9b-4899-8069-e0e3048e911d.sketch_text.stroke-75"),sQuery(id+"FHMxAyK4CFUKdhS_1.wireOp",EDGE,"1cb9c079-ea9b-4899-8069-e0e3048e911d.sketch_text.stroke-76"),sQuery(id+"FHMxAyK4CFUKdhS_1.wireOp",EDGE,"1cb9c079-ea9b-4899-8069-e0e3048e911d.sketch_text.stroke-77"),sQuery(id+"FHMxAyK4CFUKdhS_1.wireOp",EDGE,"1cb9c079-ea9b-4899-8069-e0e3048e911d.sketch_text.stroke-78"),sQuery(id+"FHMxAyK4CFUKdhS_1.wireOp",EDGE,"1cb9c079-ea9b-4899-8069-e0e3048e911d.sketch_text.stroke-79"),sQuery(id+"FHMxAyK4CFUKdhS_1.wireOp",EDGE,"1cb9c079-ea9b-4899-8069-e0e3048e911d.sketch_text.stroke-80"),sQuery(id+"FHMxAyK4CFUKdhS_1.wireOp",EDGE,"1cb9c079-ea9b-4899-8069-e0e3048e911d.sketch_text.stroke-81"),sQuery(id+"FHMxAyK4CFUKdhS_1.wireOp",EDGE,"1cb9c079-ea9b-4899-8069-e0e3048e911d.sketch_text.stroke-82"),sQuery(id+"FHMxAyK4CFUKdhS_1.wireOp",EDGE,"1cb9c079-ea9b-4899-8069-e0e3048e911d.sketch_text.stroke-83"),sQuery(id+"FHMxAyK4CFUKdhS_1.wireOp",EDGE,"1cb9c079-ea9b-4899-8069-e0e3048e911d.sketch_text.stroke-84"),sQuery(id+"FHMxAyK4CFUKdhS_1.wireOp",EDGE,"1cb9c079-ea9b-4899-8069-e0e3048e911d.sketch_text.stroke-85"),sQuery(id+"FHMxAyK4CFUKdhS_1.wireOp",EDGE,"1cb9c079-ea9b-4899-8069-e0e3048e911d.sketch_text.stroke-86"),sQuery(id+"FHMxAyK4CFUKdhS_1.wireOp",EDGE,"1cb9c079-ea9b-4899-8069-e0e3048e911d.sketch_text.stroke-87"),sQuery(id+"FHMxAyK4CFUKdhS_1.wireOp",EDGE,"1cb9c079-ea9b-4899-8069-e0e3048e911d.sketch_text.stroke-88"),sQuery(id+"FHMxAyK4CFUKdhS_1.wireOp",EDGE,"1cb9c079-ea9b-4899-8069-e0e3048e911d.sketch_text.stroke-89"),sQuery(id+"FHMxAyK4CFUKdhS_1.wireOp",EDGE,"1cb9c079-ea9b-4899-8069-e0e3048e911d.sketch_text.stroke-90"),sQuery(id+"FHMxAyK4CFUKdhS_1.wireOp",EDGE,"1cb9c079-ea9b-4899-8069-e0e3048e911d.sketch_text.stroke-91"),sQuery(id+"FHMxAyK4CFUKdhS_1.wireOp",EDGE,"1cb9c079-ea9b-4899-8069-e0e3048e911d.sketch_text.stroke-92"),sQuery(id+"FHMxAyK4CFUKdhS_1.wireOp",EDGE,"1cb9c079-ea9b-4899-8069-e0e3048e911d.sketch_text.stroke-93"),sQuery(id+"FHMxAyK4CFUKdhS_1.wireOp",EDGE,"1cb9c079-ea9b-4899-8069-e0e3048e911d.sketch_text.stroke-94"),sQuery(id+"FHMxAyK4CFUKdhS_1.wireOp",EDGE,"1cb9c079-ea9b-4899-8069-e0e3048e911d.sketch_text.stroke-95"),sQuery(id+"FHMxAyK4CFUKdhS_1.wireOp",EDGE,"1cb9c079-ea9b-4899-8069-e0e3048e911d.sketch_text.stroke-96"),sQuery(id+"FHMxAyK4CFUKdhS_1.wireOp",EDGE,"1cb9c079-ea9b-4899-8069-e0e3048e911d.sketch_text.stroke-97"),sQuery(id+"FHMxAyK4CFUKdhS_1.wireOp",EDGE,"1cb9c079-ea9b-4899-8069-e0e3048e911d.sketch_text.stroke-103"),sQuery(id+"FHMxAyK4CFUKdhS_1.wireOp",EDGE,"1cb9c079-ea9b-4899-8069-e0e3048e911d.sketch_text.stroke-104"),sQuery(id+"FHMxAyK4CFUKdhS_1.wireOp",EDGE,"1cb9c079-ea9b-4899-8069-e0e3048e911d.sketch_text.stroke-105"),sQuery(id+"FHMxAyK4CFUKdhS_1.wireOp",EDGE,"1cb9c079-ea9b-4899-8069-e0e3048e911d.sketch_text.stroke-106"),sQuery(id+"FHMxAyK4CFUKdhS_1.wireOp",EDGE,"1cb9c079-ea9b-4899-8069-e0e3048e911d.sketch_text.stroke-107"),sQuery(id+"FHMxAyK4CFUKdhS_1.wireOp",EDGE,"1cb9c079-ea9b-4899-8069-e0e3048e911d.sketch_text.stroke-108"),sQuery(id+"FHMxAyK4CFUKdhS_1.wireOp",EDGE,"1cb9c079-ea9b-4899-8069-e0e3048e911d.sketch_text.stroke-109"),sQuery(id+"FHMxAyK4CFUKdhS_1.wireOp",EDGE,"1cb9c079-ea9b-4899-8069-e0e3048e911d.sketch_text.stroke-110"),sQuery(id+"FHMxAyK4CFUKdhS_1.wireOp",EDGE,"1cb9c079-ea9b-4899-8069-e0e3048e911d.sketch_text.stroke-111"),sQuery(id+"FHMxAyK4CFUKdhS_1.wireOp",EDGE,"1cb9c079-ea9b-4899-8069-e0e3048e911d.sketch_text.stroke-112"),sQuery(id+"FHMxAyK4CFUKdhS_1.wireOp",EDGE,"1cb9c079-ea9b-4899-8069-e0e3048e911d.sketch_text.stroke-113"),sQuery(id+"FHMxAyK4CFUKdhS_1.wireOp",EDGE,"1cb9c079-ea9b-4899-8069-e0e3048e911d.sketch_text.stroke-114"),sQuery(id+"FHMxAyK4CFUKdhS_1.wireOp",EDGE,"1cb9c079-ea9b-4899-8069-e0e3048e911d.sketch_text.stroke-115"),sQuery(id+"FHMxAyK4CFUKdhS_1.wireOp",EDGE,"1cb9c079-ea9b-4899-8069-e0e3048e911d.sketch_text.stroke-116"),sQuery(id+"FHMxAyK4CFUKdhS_1.wireOp",EDGE,"1cb9c079-ea9b-4899-8069-e0e3048e911d.sketch_text.stroke-117"),sQuery(id+"FHMxAyK4CFUKdhS_1.wireOp",EDGE,"1cb9c079-ea9b-4899-8069-e0e3048e911d.sketch_text.stroke-118"),sQuery(id+"FHMxAyK4CFUKdhS_1.wireOp",EDGE,"1cb9c079-ea9b-4899-8069-e0e3048e911d.sketch_text.stroke-119"),sQuery(id+"FHMxAyK4CFUKdhS_1.wireOp",EDGE,"1cb9c079-ea9b-4899-8069-e0e3048e911d.sketch_text.stroke-120"),sQuery(id+"FHMxAyK4CFUKdhS_1.wireOp",EDGE,"1cb9c079-ea9b-4899-8069-e0e3048e911d.sketch_text.stroke-121"),sQuery(id+"FHMxAyK4CFUKdhS_1.wireOp",EDGE,"1cb9c079-ea9b-4899-8069-e0e3048e911d.sketch_text.stroke-122"),sQuery(id+"FHMxAyK4CFUKdhS_1.wireOp",EDGE,"1cb9c079-ea9b-4899-8069-e0e3048e911d.sketch_text.stroke-123"),sQuery(id+"FHMxAyK4CFUKdhS_1.wireOp",EDGE,"1cb9c079-ea9b-4899-8069-e0e3048e911d.sketch_text.stroke-124"),sQuery(id+"FHMxAyK4CFUKdhS_1.wireOp",EDGE,"1cb9c079-ea9b-4899-8069-e0e3048e911d.sketch_text.stroke-125"),sQuery(id+"FHMxAyK4CFUKdhS_1.wireOp",EDGE,"1cb9c079-ea9b-4899-8069-e0e3048e911d.sketch_text.stroke-126"),sQuery(id+"FHMxAyK4CFUKdhS_1.wireOp",EDGE,"1cb9c079-ea9b-4899-8069-e0e3048e911d.sketch_text.stroke-127"),sQuery(id+"FHMxAyK4CFUKdhS_1.wireOp",EDGE,"1cb9c079-ea9b-4899-8069-e0e3048e911d.sketch_text.stroke-128"),sQuery(id+"FHMxAyK4CFUKdhS_1.wireOp",EDGE,"1cb9c079-ea9b-4899-8069-e0e3048e911d.sketch_text.stroke-129"),sQuery(id+"FHMxAyK4CFUKdhS_1.wireOp",EDGE,"1cb9c079-ea9b-4899-8069-e0e3048e911d.sketch_text.stroke-130"),sQuery(id+"FHMxAyK4CFUKdhS_1.wireOp",EDGE,"1cb9c079-ea9b-4899-8069-e0e3048e911d.sketch_text.stroke-131"),sQuery(id+"FHMxAyK4CFUKdhS_1.wireOp",EDGE,"1cb9c079-ea9b-4899-8069-e0e3048e911d.sketch_text.stroke-132"),sQuery(id+"FHMxAyK4CFUKdhS_1.wireOp",EDGE,"1cb9c079-ea9b-4899-8069-e0e3048e911d.sketch_text.stroke-133"),sQuery(id+"FHMxAyK4CFUKdhS_1.wireOp",EDGE,"1cb9c079-ea9b-4899-8069-e0e3048e911d.sketch_text.stroke-134"),sQuery(id+"FHMxAyK4CFUKdhS_1.wireOp",EDGE,"1cb9c079-ea9b-4899-8069-e0e3048e911d.sketch_text.stroke-135"),sQuery(id+"FHMxAyK4CFUKdhS_1.wireOp",EDGE,"1cb9c079-ea9b-4899-8069-e0e3048e911d.sketch_text.stroke-136"),sQuery(id+"FHMxAyK4CFUKdhS_1.wireOp",EDGE,"1cb9c079-ea9b-4899-8069-e0e3048e911d.sketch_text.stroke-137"),sQuery(id+"FHMxAyK4CFUKdhS_1.wireOp",EDGE,"1cb9c079-ea9b-4899-8069-e0e3048e911d.sketch_text.stroke-138"),sQuery(id+"FHMxAyK4CFUKdhS_1.wireOp",EDGE,"1cb9c079-ea9b-4899-8069-e0e3048e911d.sketch_text.stroke-139"),sQuery(id+"FHMxAyK4CFUKdhS_1.wireOp",EDGE,"1cb9c079-ea9b-4899-8069-e0e3048e911d.sketch_text.stroke-140"),sQuery(id+"FHMxAyK4CFUKdhS_1.wireOp",EDGE,"1cb9c079-ea9b-4899-8069-e0e3048e911d.sketch_text.stroke-141"),sQuery(id+"FHMxAyK4CFUKdhS_1.wireOp",EDGE,"1cb9c079-ea9b-4899-8069-e0e3048e911d.sketch_text.stroke-142"),sQuery(id+"FHMxAyK4CFUKdhS_1.wireOp",EDGE,"1cb9c079-ea9b-4899-8069-e0e3048e911d.sketch_text.stroke-143"),sQuery(id+"FHMxAyK4CFUKdhS_1.wireOp",EDGE,"1cb9c079-ea9b-4899-8069-e0e3048e911d.sketch_text.stroke-144"),sQuery(id+"FHMxAyK4CFUKdhS_1.wireOp",EDGE,"1cb9c079-ea9b-4899-8069-e0e3048e911d.sketch_text.stroke-145"),sQuery(id+"FHMxAyK4CFUKdhS_1.wireOp",EDGE,"1cb9c079-ea9b-4899-8069-e0e3048e911d.sketch_text.stroke-146"),sQuery(id+"FHMxAyK4CFUKdhS_1.wireOp",EDGE,"1cb9c079-ea9b-4899-8069-e0e3048e911d.sketch_text.stroke-147"),sQuery(id+"FHMxAyK4CFUKdhS_1.wireOp",EDGE,"1cb9c079-ea9b-4899-8069-e0e3048e911d.sketch_text.stroke-148"),sQuery(id+"FHMxAyK4CFUKdhS_1.wireOp",EDGE,"1cb9c079-ea9b-4899-8069-e0e3048e911d.sketch_text.stroke-149"),sQuery(id+"FHMxAyK4CFUKdhS_1.wireOp",EDGE,"1cb9c079-ea9b-4899-8069-e0e3048e911d.sketch_text.stroke-150"),sQuery(id+"FHMxAyK4CFUKdhS_1.wireOp",EDGE,"1cb9c079-ea9b-4899-8069-e0e3048e911d.sketch_text.stroke-151"),sQuery(id+"FHMxAyK4CFUKdhS_1.wireOp",EDGE,"1cb9c079-ea9b-4899-8069-e0e3048e911d.sketch_text.stroke-152"),sQuery(id+"FHMxAyK4CFUKdhS_1.wireOp",EDGE,"1cb9c079-ea9b-4899-8069-e0e3048e911d.sketch_text.stroke-153"),sQuery(id+"FHMxAyK4CFUKdhS_1.wireOp",EDGE,"1cb9c079-ea9b-4899-8069-e0e3048e911d.sketch_text.stroke-159"),sQuery(id+"FHMxAyK4CFUKdhS_1.wireOp",EDGE,"1cb9c079-ea9b-4899-8069-e0e3048e911d.sketch_text.stroke-160"),sQuery(id+"FHMxAyK4CFUKdhS_1.wireOp",EDGE,"1cb9c079-ea9b-4899-8069-e0e3048e911d.sketch_text.stroke-161"),sQuery(id+"FHMxAyK4CFUKdhS_1.wireOp",EDGE,"1cb9c079-ea9b-4899-8069-e0e3048e911d.sketch_text.stroke-162"),sQuery(id+"FHMxAyK4CFUKdhS_1.wireOp",EDGE,"1cb9c079-ea9b-4899-8069-e0e3048e911d.sketch_text.stroke-163"),sQuery(id+"FHMxAyK4CFUKdhS_1.wireOp",EDGE,"1cb9c079-ea9b-4899-8069-e0e3048e911d.sketch_text.stroke-164"),sQuery(id+"FHMxAyK4CFUKdhS_1.wireOp",EDGE,"1cb9c079-ea9b-4899-8069-e0e3048e911d.sketch_text.stroke-165"),sQuery(id+"FHMxAyK4CFUKdhS_1.wireOp",EDGE,"1cb9c079-ea9b-4899-8069-e0e3048e911d.sketch_text.stroke-166"),sQuery(id+"FHMxAyK4CFUKdhS_1.wireOp",EDGE,"1cb9c079-ea9b-4899-8069-e0e3048e911d.sketch_text.stroke-167"),sQuery(id+"FHMxAyK4CFUKdhS_1.wireOp",EDGE,"1cb9c079-ea9b-4899-8069-e0e3048e911d.sketch_text.stroke-168"),sQuery(id+"FHMxAyK4CFUKdhS_1.wireOp",EDGE,"1cb9c079-ea9b-4899-8069-e0e3048e911d.sketch_text.stroke-169"),sQuery(id+"FHMxAyK4CFUKdhS_1.wireOp",EDGE,"1cb9c079-ea9b-4899-8069-e0e3048e911d.sketch_text.stroke-170"),sQuery(id+"FHMxAyK4CFUKdhS_1.wireOp",EDGE,"1cb9c079-ea9b-4899-8069-e0e3048e911d.sketch_text.stroke-171"),sQuery(id+"FHMxAyK4CFUKdhS_1.wireOp",EDGE,"1cb9c079-ea9b-4899-8069-e0e3048e911d.sketch_text.stroke-172"),sQuery(id+"FHMxAyK4CFUKdhS_1.wireOp",EDGE,"1cb9c079-ea9b-4899-8069-e0e3048e911d.sketch_text.stroke-173"),sQuery(id+"FHMxAyK4CFUKdhS_1.wireOp",EDGE,"1cb9c079-ea9b-4899-8069-e0e3048e911d.sketch_text.stroke-174"),sQuery(id+"FHMxAyK4CFUKdhS_1.wireOp",EDGE,"1cb9c079-ea9b-4899-8069-e0e3048e911d.sketch_text.stroke-175"),sQuery(id+"FHMxAyK4CFUKdhS_1.wireOp",EDGE,"1cb9c079-ea9b-4899-8069-e0e3048e911d.sketch_text.stroke-176"),sQuery(id+"FHMxAyK4CFUKdhS_1.wireOp",EDGE,"1cb9c079-ea9b-4899-8069-e0e3048e911d.sketch_text.stroke-177"),sQuery(id+"FHMxAyK4CFUKdhS_1.wireOp",EDGE,"1cb9c079-ea9b-4899-8069-e0e3048e911d.sketch_text.stroke-178"),sQuery(id+"FHMxAyK4CFUKdhS_1.wireOp",EDGE,"1cb9c079-ea9b-4899-8069-e0e3048e911d.sketch_text.stroke-179"),sQuery(id+"FHMxAyK4CFUKdhS_1.wireOp",EDGE,"1cb9c079-ea9b-4899-8069-e0e3048e911d.sketch_text.stroke-180"),subQ2,sQuery(id+"F2.wireOp",EDGE,"6ee83ff3-586e-4dbe-aaea-af71240543bd")])],"isStart":true})]),OD(0.0)],"derivedFrom":makeQuery(id+"F1.opExtrude","CAP_EDGE",EDGE,{"disambiguationData":[OSD([subQ0])],"isStart":false})});}
            var Q6;
            {var subQ0=sQuery(id+"F2.wireOp",EDGE,"6ee83ff3-586e-4dbe-aaea-af71240543bd");var subQ1=sQuery(id+"F0.wireOp",EDGE,"E0.bottom");var subQ2=sQuery(id+"F0.wireOp",EDGE,"E0.right");Q6=makeQuery(id+"F3.boolean.opBoolean","SPLIT",EDGE,{"disambiguationData":[TD([makeQuery(id+"F1.opExtrude","SWEPT_FACE",FACE,{"disambiguationData":[OSD([subQ1])]}),makeQuery(id+"F1.opExtrude","CAP_FACE",FACE,{"disambiguationData":[OSD([subQ1,sQuery(id+"F0.wireOp",EDGE,"E0.top"),sQuery(id+"F0.wireOp",EDGE,"E0.left"),subQ2])],"isStart":false}),makeQuery(id+"F1.opExtrude","SWEPT_FACE",FACE,{"disambiguationData":[OSD([subQ2])]}),makeQuery(id+"F3.opExtrude","CAP_FACE",FACE,{"disambiguationData":[OSD([subQ1,sQuery(id+"FQ5JFwxVdaqARUP_1.wireOp",EDGE,"fcba4419-a2ee-464f-be9d-58f11bf3418b.sketch_text.stroke-0"),sQuery(id+"FQ5JFwxVdaqARUP_1.wireOp",EDGE,"fcba4419-a2ee-464f-be9d-58f11bf3418b.sketch_text.stroke-1"),sQuery(id+"FQ5JFwxVdaqARUP_1.wireOp",EDGE,"fcba4419-a2ee-464f-be9d-58f11bf3418b.sketch_text.stroke-2"),sQuery(id+"FQ5JFwxVdaqARUP_1.wireOp",EDGE,"fcba4419-a2ee-464f-be9d-58f11bf3418b.sketch_text.stroke-3"),sQuery(id+"FQ5JFwxVdaqARUP_1.wireOp",EDGE,"fcba4419-a2ee-464f-be9d-58f11bf3418b.sketch_text.stroke-4"),sQuery(id+"FQ5JFwxVdaqARUP_1.wireOp",EDGE,"fcba4419-a2ee-464f-be9d-58f11bf3418b.sketch_text.stroke-5"),sQuery(id+"FQ5JFwxVdaqARUP_1.wireOp",EDGE,"fcba4419-a2ee-464f-be9d-58f11bf3418b.sketch_text.stroke-6"),sQuery(id+"FQ5JFwxVdaqARUP_1.wireOp",EDGE,"fcba4419-a2ee-464f-be9d-58f11bf3418b.sketch_text.stroke-7"),sQuery(id+"FQ5JFwxVdaqARUP_1.wireOp",EDGE,"fcba4419-a2ee-464f-be9d-58f11bf3418b.sketch_text.stroke-8"),sQuery(id+"FQ5JFwxVdaqARUP_1.wireOp",EDGE,"fcba4419-a2ee-464f-be9d-58f11bf3418b.sketch_text.stroke-9"),sQuery(id+"FQ5JFwxVdaqARUP_1.wireOp",EDGE,"fcba4419-a2ee-464f-be9d-58f11bf3418b.sketch_text.stroke-10"),sQuery(id+"FQ5JFwxVdaqARUP_1.wireOp",EDGE,"fcba4419-a2ee-464f-be9d-58f11bf3418b.sketch_text.stroke-11"),sQuery(id+"FQ5JFwxVdaqARUP_1.wireOp",EDGE,"fcba4419-a2ee-464f-be9d-58f11bf3418b.sketch_text.stroke-12"),sQuery(id+"FQ5JFwxVdaqARUP_1.wireOp",EDGE,"fcba4419-a2ee-464f-be9d-58f11bf3418b.sketch_text.stroke-13"),sQuery(id+"FQ5JFwxVdaqARUP_1.wireOp",EDGE,"fcba4419-a2ee-464f-be9d-58f11bf3418b.sketch_text.stroke-14"),sQuery(id+"FQ5JFwxVdaqARUP_1.wireOp",EDGE,"fcba4419-a2ee-464f-be9d-58f11bf3418b.sketch_text.stroke-15"),sQuery(id+"FQ5JFwxVdaqARUP_1.wireOp",EDGE,"fcba4419-a2ee-464f-be9d-58f11bf3418b.sketch_text.stroke-16"),sQuery(id+"FQ5JFwxVdaqARUP_1.wireOp",EDGE,"fcba4419-a2ee-464f-be9d-58f11bf3418b.sketch_text.stroke-17"),sQuery(id+"FQ5JFwxVdaqARUP_1.wireOp",EDGE,"fcba4419-a2ee-464f-be9d-58f11bf3418b.sketch_text.stroke-18"),sQuery(id+"FQ5JFwxVdaqARUP_1.wireOp",EDGE,"fcba4419-a2ee-464f-be9d-58f11bf3418b.sketch_text.stroke-19"),sQuery(id+"FQ5JFwxVdaqARUP_1.wireOp",EDGE,"fcba4419-a2ee-464f-be9d-58f11bf3418b.sketch_text.stroke-20"),sQuery(id+"FQ5JFwxVdaqARUP_1.wireOp",EDGE,"fcba4419-a2ee-464f-be9d-58f11bf3418b.sketch_text.stroke-21"),sQuery(id+"FQ5JFwxVdaqARUP_1.wireOp",EDGE,"fcba4419-a2ee-464f-be9d-58f11bf3418b.sketch_text.stroke-22"),sQuery(id+"FQ5JFwxVdaqARUP_1.wireOp",EDGE,"fcba4419-a2ee-464f-be9d-58f11bf3418b.sketch_text.stroke-23"),sQuery(id+"FQ5JFwxVdaqARUP_1.wireOp",EDGE,"fcba4419-a2ee-464f-be9d-58f11bf3418b.sketch_text.stroke-24"),sQuery(id+"FQ5JFwxVdaqARUP_1.wireOp",EDGE,"fcba4419-a2ee-464f-be9d-58f11bf3418b.sketch_text.stroke-25"),sQuery(id+"FQ5JFwxVdaqARUP_1.wireOp",EDGE,"fcba4419-a2ee-464f-be9d-58f11bf3418b.sketch_text.stroke-26"),sQuery(id+"FQ5JFwxVdaqARUP_1.wireOp",EDGE,"fcba4419-a2ee-464f-be9d-58f11bf3418b.sketch_text.stroke-27"),sQuery(id+"FQ5JFwxVdaqARUP_1.wireOp",EDGE,"fcba4419-a2ee-464f-be9d-58f11bf3418b.sketch_text.stroke-28"),sQuery(id+"FQ5JFwxVdaqARUP_1.wireOp",EDGE,"fcba4419-a2ee-464f-be9d-58f11bf3418b.sketch_text.stroke-29"),sQuery(id+"FQ5JFwxVdaqARUP_1.wireOp",EDGE,"fcba4419-a2ee-464f-be9d-58f11bf3418b.sketch_text.stroke-30"),sQuery(id+"FQ5JFwxVdaqARUP_1.wireOp",EDGE,"fcba4419-a2ee-464f-be9d-58f11bf3418b.sketch_text.stroke-31"),sQuery(id+"FQ5JFwxVdaqARUP_1.wireOp",EDGE,"fcba4419-a2ee-464f-be9d-58f11bf3418b.sketch_text.stroke-32"),sQuery(id+"FQ5JFwxVdaqARUP_1.wireOp",EDGE,"fcba4419-a2ee-464f-be9d-58f11bf3418b.sketch_text.stroke-33"),sQuery(id+"FQ5JFwxVdaqARUP_1.wireOp",EDGE,"fcba4419-a2ee-464f-be9d-58f11bf3418b.sketch_text.stroke-34"),sQuery(id+"FQ5JFwxVdaqARUP_1.wireOp",EDGE,"fcba4419-a2ee-464f-be9d-58f11bf3418b.sketch_text.stroke-35"),sQuery(id+"FQ5JFwxVdaqARUP_1.wireOp",EDGE,"fcba4419-a2ee-464f-be9d-58f11bf3418b.sketch_text.stroke-36"),sQuery(id+"FQ5JFwxVdaqARUP_1.wireOp",EDGE,"fcba4419-a2ee-464f-be9d-58f11bf3418b.sketch_text.stroke-37"),sQuery(id+"FQ5JFwxVdaqARUP_1.wireOp",EDGE,"fcba4419-a2ee-464f-be9d-58f11bf3418b.sketch_text.stroke-38"),sQuery(id+"FQ5JFwxVdaqARUP_1.wireOp",EDGE,"fcba4419-a2ee-464f-be9d-58f11bf3418b.sketch_text.stroke-39"),sQuery(id+"FQ5JFwxVdaqARUP_1.wireOp",EDGE,"fcba4419-a2ee-464f-be9d-58f11bf3418b.sketch_text.stroke-40"),sQuery(id+"FQ5JFwxVdaqARUP_1.wireOp",EDGE,"fcba4419-a2ee-464f-be9d-58f11bf3418b.sketch_text.stroke-41"),sQuery(id+"FQ5JFwxVdaqARUP_1.wireOp",EDGE,"fcba4419-a2ee-464f-be9d-58f11bf3418b.sketch_text.stroke-42"),sQuery(id+"FQ5JFwxVdaqARUP_1.wireOp",EDGE,"fcba4419-a2ee-464f-be9d-58f11bf3418b.sketch_text.stroke-43"),sQuery(id+"FQ5JFwxVdaqARUP_1.wireOp",EDGE,"fcba4419-a2ee-464f-be9d-58f11bf3418b.sketch_text.stroke-44"),sQuery(id+"FQ5JFwxVdaqARUP_1.wireOp",EDGE,"fcba4419-a2ee-464f-be9d-58f11bf3418b.sketch_text.stroke-45"),sQuery(id+"FQ5JFwxVdaqARUP_1.wireOp",EDGE,"fcba4419-a2ee-464f-be9d-58f11bf3418b.sketch_text.stroke-46"),sQuery(id+"FQ5JFwxVdaqARUP_1.wireOp",EDGE,"fcba4419-a2ee-464f-be9d-58f11bf3418b.sketch_text.stroke-47"),sQuery(id+"FQ5JFwxVdaqARUP_1.wireOp",EDGE,"fcba4419-a2ee-464f-be9d-58f11bf3418b.sketch_text.stroke-48"),sQuery(id+"FQ5JFwxVdaqARUP_1.wireOp",EDGE,"fcba4419-a2ee-464f-be9d-58f11bf3418b.sketch_text.stroke-49"),sQuery(id+"FQ5JFwxVdaqARUP_1.wireOp",EDGE,"fcba4419-a2ee-464f-be9d-58f11bf3418b.sketch_text.stroke-50"),sQuery(id+"FQ5JFwxVdaqARUP_1.wireOp",EDGE,"fcba4419-a2ee-464f-be9d-58f11bf3418b.sketch_text.stroke-51"),sQuery(id+"FQ5JFwxVdaqARUP_1.wireOp",EDGE,"fcba4419-a2ee-464f-be9d-58f11bf3418b.sketch_text.stroke-52"),sQuery(id+"FQ5JFwxVdaqARUP_1.wireOp",EDGE,"fcba4419-a2ee-464f-be9d-58f11bf3418b.sketch_text.stroke-53"),sQuery(id+"FQ5JFwxVdaqARUP_1.wireOp",EDGE,"fcba4419-a2ee-464f-be9d-58f11bf3418b.sketch_text.stroke-54"),sQuery(id+"FQ5JFwxVdaqARUP_1.wireOp",EDGE,"fcba4419-a2ee-464f-be9d-58f11bf3418b.sketch_text.stroke-55"),sQuery(id+"FQ5JFwxVdaqARUP_1.wireOp",EDGE,"fcba4419-a2ee-464f-be9d-58f11bf3418b.sketch_text.stroke-56"),sQuery(id+"FQ5JFwxVdaqARUP_1.wireOp",EDGE,"fcba4419-a2ee-464f-be9d-58f11bf3418b.sketch_text.stroke-57"),sQuery(id+"FQ5JFwxVdaqARUP_1.wireOp",EDGE,"fcba4419-a2ee-464f-be9d-58f11bf3418b.sketch_text.stroke-58"),sQuery(id+"FQ5JFwxVdaqARUP_1.wireOp",EDGE,"fcba4419-a2ee-464f-be9d-58f11bf3418b.sketch_text.stroke-59"),sQuery(id+"FQ5JFwxVdaqARUP_1.wireOp",EDGE,"fcba4419-a2ee-464f-be9d-58f11bf3418b.sketch_text.stroke-60"),sQuery(id+"FQ5JFwxVdaqARUP_1.wireOp",EDGE,"fcba4419-a2ee-464f-be9d-58f11bf3418b.sketch_text.stroke-61"),sQuery(id+"FQ5JFwxVdaqARUP_1.wireOp",EDGE,"fcba4419-a2ee-464f-be9d-58f11bf3418b.sketch_text.stroke-62"),sQuery(id+"FQ5JFwxVdaqARUP_1.wireOp",EDGE,"fcba4419-a2ee-464f-be9d-58f11bf3418b.sketch_text.stroke-63"),sQuery(id+"FQ5JFwxVdaqARUP_1.wireOp",EDGE,"fcba4419-a2ee-464f-be9d-58f11bf3418b.sketch_text.stroke-64"),sQuery(id+"FQ5JFwxVdaqARUP_1.wireOp",EDGE,"fcba4419-a2ee-464f-be9d-58f11bf3418b.sketch_text.stroke-65"),sQuery(id+"FQ5JFwxVdaqARUP_1.wireOp",EDGE,"fcba4419-a2ee-464f-be9d-58f11bf3418b.sketch_text.stroke-66"),sQuery(id+"FQ5JFwxVdaqARUP_1.wireOp",EDGE,"fcba4419-a2ee-464f-be9d-58f11bf3418b.sketch_text.stroke-67"),sQuery(id+"FQ5JFwxVdaqARUP_1.wireOp",EDGE,"fcba4419-a2ee-464f-be9d-58f11bf3418b.sketch_text.stroke-68"),sQuery(id+"FQ5JFwxVdaqARUP_1.wireOp",EDGE,"fcba4419-a2ee-464f-be9d-58f11bf3418b.sketch_text.stroke-69"),sQuery(id+"FQ5JFwxVdaqARUP_1.wireOp",EDGE,"fcba4419-a2ee-464f-be9d-58f11bf3418b.sketch_text.stroke-70"),sQuery(id+"FQ5JFwxVdaqARUP_1.wireOp",EDGE,"fcba4419-a2ee-464f-be9d-58f11bf3418b.sketch_text.stroke-71"),sQuery(id+"FQ5JFwxVdaqARUP_1.wireOp",EDGE,"fcba4419-a2ee-464f-be9d-58f11bf3418b.sketch_text.stroke-72"),sQuery(id+"FQ5JFwxVdaqARUP_1.wireOp",EDGE,"fcba4419-a2ee-464f-be9d-58f11bf3418b.sketch_text.stroke-73"),sQuery(id+"FQ5JFwxVdaqARUP_1.wireOp",EDGE,"fcba4419-a2ee-464f-be9d-58f11bf3418b.sketch_text.stroke-74"),sQuery(id+"FQ5JFwxVdaqARUP_1.wireOp",EDGE,"fcba4419-a2ee-464f-be9d-58f11bf3418b.sketch_text.stroke-75"),sQuery(id+"FQ5JFwxVdaqARUP_1.wireOp",EDGE,"fcba4419-a2ee-464f-be9d-58f11bf3418b.sketch_text.stroke-76"),sQuery(id+"FQ5JFwxVdaqARUP_1.wireOp",EDGE,"fcba4419-a2ee-464f-be9d-58f11bf3418b.sketch_text.stroke-77"),sQuery(id+"FQ5JFwxVdaqARUP_1.wireOp",EDGE,"fcba4419-a2ee-464f-be9d-58f11bf3418b.sketch_text.stroke-78"),sQuery(id+"FQ5JFwxVdaqARUP_1.wireOp",EDGE,"fcba4419-a2ee-464f-be9d-58f11bf3418b.sketch_text.stroke-79"),sQuery(id+"FQ5JFwxVdaqARUP_1.wireOp",EDGE,"fcba4419-a2ee-464f-be9d-58f11bf3418b.sketch_text.stroke-80"),sQuery(id+"FQ5JFwxVdaqARUP_1.wireOp",EDGE,"fcba4419-a2ee-464f-be9d-58f11bf3418b.sketch_text.stroke-81"),sQuery(id+"FQ5JFwxVdaqARUP_1.wireOp",EDGE,"fcba4419-a2ee-464f-be9d-58f11bf3418b.sketch_text.stroke-82"),sQuery(id+"FQ5JFwxVdaqARUP_1.wireOp",EDGE,"fcba4419-a2ee-464f-be9d-58f11bf3418b.sketch_text.stroke-83"),sQuery(id+"FQ5JFwxVdaqARUP_1.wireOp",EDGE,"fcba4419-a2ee-464f-be9d-58f11bf3418b.sketch_text.stroke-84"),sQuery(id+"FQ5JFwxVdaqARUP_1.wireOp",EDGE,"fcba4419-a2ee-464f-be9d-58f11bf3418b.sketch_text.stroke-85"),sQuery(id+"FQ5JFwxVdaqARUP_1.wireOp",EDGE,"fcba4419-a2ee-464f-be9d-58f11bf3418b.sketch_text.stroke-86"),sQuery(id+"FQ5JFwxVdaqARUP_1.wireOp",EDGE,"fcba4419-a2ee-464f-be9d-58f11bf3418b.sketch_text.stroke-87"),sQuery(id+"FQ5JFwxVdaqARUP_1.wireOp",EDGE,"fcba4419-a2ee-464f-be9d-58f11bf3418b.sketch_text.stroke-88"),sQuery(id+"FQ5JFwxVdaqARUP_1.wireOp",EDGE,"fcba4419-a2ee-464f-be9d-58f11bf3418b.sketch_text.stroke-89"),sQuery(id+"FQ5JFwxVdaqARUP_1.wireOp",EDGE,"fcba4419-a2ee-464f-be9d-58f11bf3418b.sketch_text.stroke-90"),sQuery(id+"FQ5JFwxVdaqARUP_1.wireOp",EDGE,"fcba4419-a2ee-464f-be9d-58f11bf3418b.sketch_text.stroke-91"),sQuery(id+"FQ5JFwxVdaqARUP_1.wireOp",EDGE,"fcba4419-a2ee-464f-be9d-58f11bf3418b.sketch_text.stroke-92"),sQuery(id+"FQ5JFwxVdaqARUP_1.wireOp",EDGE,"fcba4419-a2ee-464f-be9d-58f11bf3418b.sketch_text.stroke-93"),sQuery(id+"FQ5JFwxVdaqARUP_1.wireOp",EDGE,"fcba4419-a2ee-464f-be9d-58f11bf3418b.sketch_text.stroke-94"),sQuery(id+"FQ5JFwxVdaqARUP_1.wireOp",EDGE,"fcba4419-a2ee-464f-be9d-58f11bf3418b.sketch_text.stroke-95"),sQuery(id+"FQ5JFwxVdaqARUP_1.wireOp",EDGE,"fcba4419-a2ee-464f-be9d-58f11bf3418b.sketch_text.stroke-96"),sQuery(id+"FQ5JFwxVdaqARUP_1.wireOp",EDGE,"fcba4419-a2ee-464f-be9d-58f11bf3418b.sketch_text.stroke-97"),sQuery(id+"FQ5JFwxVdaqARUP_1.wireOp",EDGE,"fcba4419-a2ee-464f-be9d-58f11bf3418b.sketch_text.stroke-98"),sQuery(id+"FQ5JFwxVdaqARUP_1.wireOp",EDGE,"fcba4419-a2ee-464f-be9d-58f11bf3418b.sketch_text.stroke-99"),sQuery(id+"FQ5JFwxVdaqARUP_1.wireOp",EDGE,"fcba4419-a2ee-464f-be9d-58f11bf3418b.sketch_text.stroke-100"),sQuery(id+"FQ5JFwxVdaqARUP_1.wireOp",EDGE,"fcba4419-a2ee-464f-be9d-58f11bf3418b.sketch_text.stroke-101"),sQuery(id+"FQ5JFwxVdaqARUP_1.wireOp",EDGE,"fcba4419-a2ee-464f-be9d-58f11bf3418b.sketch_text.stroke-102"),sQuery(id+"FQ5JFwxVdaqARUP_1.wireOp",EDGE,"fcba4419-a2ee-464f-be9d-58f11bf3418b.sketch_text.stroke-103"),sQuery(id+"FQ5JFwxVdaqARUP_1.wireOp",EDGE,"fcba4419-a2ee-464f-be9d-58f11bf3418b.sketch_text.stroke-104"),sQuery(id+"FQ5JFwxVdaqARUP_1.wireOp",EDGE,"fcba4419-a2ee-464f-be9d-58f11bf3418b.sketch_text.stroke-105"),sQuery(id+"FQ5JFwxVdaqARUP_1.wireOp",EDGE,"fcba4419-a2ee-464f-be9d-58f11bf3418b.sketch_text.stroke-106"),sQuery(id+"FQ5JFwxVdaqARUP_1.wireOp",EDGE,"fcba4419-a2ee-464f-be9d-58f11bf3418b.sketch_text.stroke-107"),sQuery(id+"FQ5JFwxVdaqARUP_1.wireOp",EDGE,"fcba4419-a2ee-464f-be9d-58f11bf3418b.sketch_text.stroke-108"),sQuery(id+"FQ5JFwxVdaqARUP_1.wireOp",EDGE,"fcba4419-a2ee-464f-be9d-58f11bf3418b.sketch_text.stroke-109"),sQuery(id+"FQ5JFwxVdaqARUP_1.wireOp",EDGE,"fcba4419-a2ee-464f-be9d-58f11bf3418b.sketch_text.stroke-110"),sQuery(id+"FQ5JFwxVdaqARUP_1.wireOp",EDGE,"fcba4419-a2ee-464f-be9d-58f11bf3418b.sketch_text.stroke-111"),sQuery(id+"FQ5JFwxVdaqARUP_1.wireOp",EDGE,"fcba4419-a2ee-464f-be9d-58f11bf3418b.sketch_text.stroke-112"),sQuery(id+"FQ5JFwxVdaqARUP_1.wireOp",EDGE,"fcba4419-a2ee-464f-be9d-58f11bf3418b.sketch_text.stroke-113"),sQuery(id+"FQ5JFwxVdaqARUP_1.wireOp",EDGE,"fcba4419-a2ee-464f-be9d-58f11bf3418b.sketch_text.stroke-114"),sQuery(id+"FQ5JFwxVdaqARUP_1.wireOp",EDGE,"fcba4419-a2ee-464f-be9d-58f11bf3418b.sketch_text.stroke-115"),sQuery(id+"FQ5JFwxVdaqARUP_1.wireOp",EDGE,"fcba4419-a2ee-464f-be9d-58f11bf3418b.sketch_text.stroke-116"),sQuery(id+"FQ5JFwxVdaqARUP_1.wireOp",EDGE,"fcba4419-a2ee-464f-be9d-58f11bf3418b.sketch_text.stroke-117"),sQuery(id+"FQ5JFwxVdaqARUP_1.wireOp",EDGE,"fcba4419-a2ee-464f-be9d-58f11bf3418b.sketch_text.stroke-118"),sQuery(id+"FQ5JFwxVdaqARUP_1.wireOp",EDGE,"fcba4419-a2ee-464f-be9d-58f11bf3418b.sketch_text.stroke-119"),sQuery(id+"FQ5JFwxVdaqARUP_1.wireOp",EDGE,"fcba4419-a2ee-464f-be9d-58f11bf3418b.sketch_text.stroke-120"),sQuery(id+"FQ5JFwxVdaqARUP_1.wireOp",EDGE,"fcba4419-a2ee-464f-be9d-58f11bf3418b.sketch_text.stroke-121"),sQuery(id+"FQ5JFwxVdaqARUP_1.wireOp",EDGE,"fcba4419-a2ee-464f-be9d-58f11bf3418b.sketch_text.stroke-122"),sQuery(id+"FQ5JFwxVdaqARUP_1.wireOp",EDGE,"fcba4419-a2ee-464f-be9d-58f11bf3418b.sketch_text.stroke-123"),sQuery(id+"FQ5JFwxVdaqARUP_1.wireOp",EDGE,"fcba4419-a2ee-464f-be9d-58f11bf3418b.sketch_text.stroke-124"),sQuery(id+"FQ5JFwxVdaqARUP_1.wireOp",EDGE,"fcba4419-a2ee-464f-be9d-58f11bf3418b.sketch_text.stroke-125"),sQuery(id+"FQ5JFwxVdaqARUP_1.wireOp",EDGE,"fcba4419-a2ee-464f-be9d-58f11bf3418b.sketch_text.stroke-126"),sQuery(id+"FQ5JFwxVdaqARUP_1.wireOp",EDGE,"fcba4419-a2ee-464f-be9d-58f11bf3418b.sketch_text.stroke-127"),sQuery(id+"FQ5JFwxVdaqARUP_1.wireOp",EDGE,"fcba4419-a2ee-464f-be9d-58f11bf3418b.sketch_text.stroke-128"),sQuery(id+"FQ5JFwxVdaqARUP_1.wireOp",EDGE,"fcba4419-a2ee-464f-be9d-58f11bf3418b.sketch_text.stroke-129"),sQuery(id+"FQ5JFwxVdaqARUP_1.wireOp",EDGE,"fcba4419-a2ee-464f-be9d-58f11bf3418b.sketch_text.stroke-130"),sQuery(id+"FQ5JFwxVdaqARUP_1.wireOp",EDGE,"fcba4419-a2ee-464f-be9d-58f11bf3418b.sketch_text.stroke-131"),sQuery(id+"FQ5JFwxVdaqARUP_1.wireOp",EDGE,"fcba4419-a2ee-464f-be9d-58f11bf3418b.sketch_text.stroke-132"),sQuery(id+"FQ5JFwxVdaqARUP_1.wireOp",EDGE,"fcba4419-a2ee-464f-be9d-58f11bf3418b.sketch_text.stroke-133"),sQuery(id+"FQ5JFwxVdaqARUP_1.wireOp",EDGE,"fcba4419-a2ee-464f-be9d-58f11bf3418b.sketch_text.stroke-134"),sQuery(id+"FQ5JFwxVdaqARUP_1.wireOp",EDGE,"fcba4419-a2ee-464f-be9d-58f11bf3418b.sketch_text.stroke-135"),sQuery(id+"FQ5JFwxVdaqARUP_1.wireOp",EDGE,"fcba4419-a2ee-464f-be9d-58f11bf3418b.sketch_text.stroke-136"),sQuery(id+"FQ5JFwxVdaqARUP_1.wireOp",EDGE,"fcba4419-a2ee-464f-be9d-58f11bf3418b.sketch_text.stroke-137"),sQuery(id+"FQ5JFwxVdaqARUP_1.wireOp",EDGE,"fcba4419-a2ee-464f-be9d-58f11bf3418b.sketch_text.stroke-138"),sQuery(id+"FQ5JFwxVdaqARUP_1.wireOp",EDGE,"fcba4419-a2ee-464f-be9d-58f11bf3418b.sketch_text.stroke-139"),sQuery(id+"FQ5JFwxVdaqARUP_1.wireOp",EDGE,"fcba4419-a2ee-464f-be9d-58f11bf3418b.sketch_text.stroke-140"),sQuery(id+"FQ5JFwxVdaqARUP_1.wireOp",EDGE,"fcba4419-a2ee-464f-be9d-58f11bf3418b.sketch_text.stroke-141"),sQuery(id+"FQ5JFwxVdaqARUP_1.wireOp",EDGE,"fcba4419-a2ee-464f-be9d-58f11bf3418b.sketch_text.stroke-142"),sQuery(id+"FQ5JFwxVdaqARUP_1.wireOp",EDGE,"fcba4419-a2ee-464f-be9d-58f11bf3418b.sketch_text.stroke-143"),sQuery(id+"FQ5JFwxVdaqARUP_1.wireOp",EDGE,"fcba4419-a2ee-464f-be9d-58f11bf3418b.sketch_text.stroke-144"),sQuery(id+"FQ5JFwxVdaqARUP_1.wireOp",EDGE,"fcba4419-a2ee-464f-be9d-58f11bf3418b.sketch_text.stroke-145"),sQuery(id+"FQ5JFwxVdaqARUP_1.wireOp",EDGE,"fcba4419-a2ee-464f-be9d-58f11bf3418b.sketch_text.stroke-146"),sQuery(id+"FQ5JFwxVdaqARUP_1.wireOp",EDGE,"fcba4419-a2ee-464f-be9d-58f11bf3418b.sketch_text.stroke-147"),sQuery(id+"FQ5JFwxVdaqARUP_1.wireOp",EDGE,"fcba4419-a2ee-464f-be9d-58f11bf3418b.sketch_text.stroke-148"),sQuery(id+"FQ5JFwxVdaqARUP_1.wireOp",EDGE,"fcba4419-a2ee-464f-be9d-58f11bf3418b.sketch_text.stroke-149"),sQuery(id+"FQ5JFwxVdaqARUP_1.wireOp",EDGE,"fcba4419-a2ee-464f-be9d-58f11bf3418b.sketch_text.stroke-150"),sQuery(id+"FQ5JFwxVdaqARUP_1.wireOp",EDGE,"fcba4419-a2ee-464f-be9d-58f11bf3418b.sketch_text.stroke-151"),sQuery(id+"FQ5JFwxVdaqARUP_1.wireOp",EDGE,"fcba4419-a2ee-464f-be9d-58f11bf3418b.sketch_text.stroke-152"),sQuery(id+"FQ5JFwxVdaqARUP_1.wireOp",EDGE,"fcba4419-a2ee-464f-be9d-58f11bf3418b.sketch_text.stroke-153"),sQuery(id+"FQ5JFwxVdaqARUP_1.wireOp",EDGE,"fcba4419-a2ee-464f-be9d-58f11bf3418b.sketch_text.stroke-154"),sQuery(id+"FQ5JFwxVdaqARUP_1.wireOp",EDGE,"fcba4419-a2ee-464f-be9d-58f11bf3418b.sketch_text.stroke-155"),sQuery(id+"FQ5JFwxVdaqARUP_1.wireOp",EDGE,"fcba4419-a2ee-464f-be9d-58f11bf3418b.sketch_text.stroke-156"),sQuery(id+"FQ5JFwxVdaqARUP_1.wireOp",EDGE,"fcba4419-a2ee-464f-be9d-58f11bf3418b.sketch_text.stroke-157"),sQuery(id+"FQ5JFwxVdaqARUP_1.wireOp",EDGE,"fcba4419-a2ee-464f-be9d-58f11bf3418b.sketch_text.stroke-158"),sQuery(id+"FQ5JFwxVdaqARUP_1.wireOp",EDGE,"fcba4419-a2ee-464f-be9d-58f11bf3418b.sketch_text.stroke-159"),sQuery(id+"FQ5JFwxVdaqARUP_1.wireOp",EDGE,"fcba4419-a2ee-464f-be9d-58f11bf3418b.sketch_text.stroke-160"),sQuery(id+"FQ5JFwxVdaqARUP_1.wireOp",EDGE,"fcba4419-a2ee-464f-be9d-58f11bf3418b.sketch_text.stroke-161"),sQuery(id+"FQ5JFwxVdaqARUP_1.wireOp",EDGE,"fcba4419-a2ee-464f-be9d-58f11bf3418b.sketch_text.stroke-162"),sQuery(id+"FQ5JFwxVdaqARUP_1.wireOp",EDGE,"fcba4419-a2ee-464f-be9d-58f11bf3418b.sketch_text.stroke-163"),sQuery(id+"FQ5JFwxVdaqARUP_1.wireOp",EDGE,"fcba4419-a2ee-464f-be9d-58f11bf3418b.sketch_text.stroke-164"),sQuery(id+"FQ5JFwxVdaqARUP_1.wireOp",EDGE,"fcba4419-a2ee-464f-be9d-58f11bf3418b.sketch_text.stroke-165"),sQuery(id+"FQ5JFwxVdaqARUP_1.wireOp",EDGE,"fcba4419-a2ee-464f-be9d-58f11bf3418b.sketch_text.stroke-166"),sQuery(id+"FQ5JFwxVdaqARUP_1.wireOp",EDGE,"fcba4419-a2ee-464f-be9d-58f11bf3418b.sketch_text.stroke-167"),sQuery(id+"FQ5JFwxVdaqARUP_1.wireOp",EDGE,"fcba4419-a2ee-464f-be9d-58f11bf3418b.sketch_text.stroke-168"),sQuery(id+"FQ5JFwxVdaqARUP_1.wireOp",EDGE,"fcba4419-a2ee-464f-be9d-58f11bf3418b.sketch_text.stroke-169"),sQuery(id+"FQ5JFwxVdaqARUP_1.wireOp",EDGE,"fcba4419-a2ee-464f-be9d-58f11bf3418b.sketch_text.stroke-170"),sQuery(id+"FQ5JFwxVdaqARUP_1.wireOp",EDGE,"fcba4419-a2ee-464f-be9d-58f11bf3418b.sketch_text.stroke-171"),sQuery(id+"FQ5JFwxVdaqARUP_1.wireOp",EDGE,"fcba4419-a2ee-464f-be9d-58f11bf3418b.sketch_text.stroke-172"),sQuery(id+"FQ5JFwxVdaqARUP_1.wireOp",EDGE,"fcba4419-a2ee-464f-be9d-58f11bf3418b.sketch_text.stroke-173"),sQuery(id+"FHMxAyK4CFUKdhS_1.wireOp",EDGE,"1cb9c079-ea9b-4899-8069-e0e3048e911d.sketch_text.stroke-0"),sQuery(id+"FHMxAyK4CFUKdhS_1.wireOp",EDGE,"1cb9c079-ea9b-4899-8069-e0e3048e911d.sketch_text.stroke-1"),sQuery(id+"FHMxAyK4CFUKdhS_1.wireOp",EDGE,"1cb9c079-ea9b-4899-8069-e0e3048e911d.sketch_text.stroke-2"),sQuery(id+"FHMxAyK4CFUKdhS_1.wireOp",EDGE,"1cb9c079-ea9b-4899-8069-e0e3048e911d.sketch_text.stroke-3"),sQuery(id+"FHMxAyK4CFUKdhS_1.wireOp",EDGE,"1cb9c079-ea9b-4899-8069-e0e3048e911d.sketch_text.stroke-4"),sQuery(id+"FHMxAyK4CFUKdhS_1.wireOp",EDGE,"1cb9c079-ea9b-4899-8069-e0e3048e911d.sketch_text.stroke-5"),sQuery(id+"FHMxAyK4CFUKdhS_1.wireOp",EDGE,"1cb9c079-ea9b-4899-8069-e0e3048e911d.sketch_text.stroke-6"),sQuery(id+"FHMxAyK4CFUKdhS_1.wireOp",EDGE,"1cb9c079-ea9b-4899-8069-e0e3048e911d.sketch_text.stroke-7"),sQuery(id+"FHMxAyK4CFUKdhS_1.wireOp",EDGE,"1cb9c079-ea9b-4899-8069-e0e3048e911d.sketch_text.stroke-8"),sQuery(id+"FHMxAyK4CFUKdhS_1.wireOp",EDGE,"1cb9c079-ea9b-4899-8069-e0e3048e911d.sketch_text.stroke-9"),sQuery(id+"FHMxAyK4CFUKdhS_1.wireOp",EDGE,"1cb9c079-ea9b-4899-8069-e0e3048e911d.sketch_text.stroke-10"),sQuery(id+"FHMxAyK4CFUKdhS_1.wireOp",EDGE,"1cb9c079-ea9b-4899-8069-e0e3048e911d.sketch_text.stroke-11"),sQuery(id+"FHMxAyK4CFUKdhS_1.wireOp",EDGE,"1cb9c079-ea9b-4899-8069-e0e3048e911d.sketch_text.stroke-12"),sQuery(id+"FHMxAyK4CFUKdhS_1.wireOp",EDGE,"1cb9c079-ea9b-4899-8069-e0e3048e911d.sketch_text.stroke-13"),sQuery(id+"FHMxAyK4CFUKdhS_1.wireOp",EDGE,"1cb9c079-ea9b-4899-8069-e0e3048e911d.sketch_text.stroke-14"),sQuery(id+"FHMxAyK4CFUKdhS_1.wireOp",EDGE,"1cb9c079-ea9b-4899-8069-e0e3048e911d.sketch_text.stroke-15"),sQuery(id+"FHMxAyK4CFUKdhS_1.wireOp",EDGE,"1cb9c079-ea9b-4899-8069-e0e3048e911d.sketch_text.stroke-16"),sQuery(id+"FHMxAyK4CFUKdhS_1.wireOp",EDGE,"1cb9c079-ea9b-4899-8069-e0e3048e911d.sketch_text.stroke-17"),sQuery(id+"FHMxAyK4CFUKdhS_1.wireOp",EDGE,"1cb9c079-ea9b-4899-8069-e0e3048e911d.sketch_text.stroke-18"),sQuery(id+"FHMxAyK4CFUKdhS_1.wireOp",EDGE,"1cb9c079-ea9b-4899-8069-e0e3048e911d.sketch_text.stroke-19"),sQuery(id+"FHMxAyK4CFUKdhS_1.wireOp",EDGE,"1cb9c079-ea9b-4899-8069-e0e3048e911d.sketch_text.stroke-20"),sQuery(id+"FHMxAyK4CFUKdhS_1.wireOp",EDGE,"1cb9c079-ea9b-4899-8069-e0e3048e911d.sketch_text.stroke-21"),sQuery(id+"FHMxAyK4CFUKdhS_1.wireOp",EDGE,"1cb9c079-ea9b-4899-8069-e0e3048e911d.sketch_text.stroke-22"),sQuery(id+"FHMxAyK4CFUKdhS_1.wireOp",EDGE,"1cb9c079-ea9b-4899-8069-e0e3048e911d.sketch_text.stroke-23"),sQuery(id+"FHMxAyK4CFUKdhS_1.wireOp",EDGE,"1cb9c079-ea9b-4899-8069-e0e3048e911d.sketch_text.stroke-24"),sQuery(id+"FHMxAyK4CFUKdhS_1.wireOp",EDGE,"1cb9c079-ea9b-4899-8069-e0e3048e911d.sketch_text.stroke-25"),sQuery(id+"FHMxAyK4CFUKdhS_1.wireOp",EDGE,"1cb9c079-ea9b-4899-8069-e0e3048e911d.sketch_text.stroke-26"),sQuery(id+"FHMxAyK4CFUKdhS_1.wireOp",EDGE,"1cb9c079-ea9b-4899-8069-e0e3048e911d.sketch_text.stroke-27"),sQuery(id+"FHMxAyK4CFUKdhS_1.wireOp",EDGE,"1cb9c079-ea9b-4899-8069-e0e3048e911d.sketch_text.stroke-28"),sQuery(id+"FHMxAyK4CFUKdhS_1.wireOp",EDGE,"1cb9c079-ea9b-4899-8069-e0e3048e911d.sketch_text.stroke-29"),sQuery(id+"FHMxAyK4CFUKdhS_1.wireOp",EDGE,"1cb9c079-ea9b-4899-8069-e0e3048e911d.sketch_text.stroke-30"),sQuery(id+"FHMxAyK4CFUKdhS_1.wireOp",EDGE,"1cb9c079-ea9b-4899-8069-e0e3048e911d.sketch_text.stroke-31"),sQuery(id+"FHMxAyK4CFUKdhS_1.wireOp",EDGE,"1cb9c079-ea9b-4899-8069-e0e3048e911d.sketch_text.stroke-32"),sQuery(id+"FHMxAyK4CFUKdhS_1.wireOp",EDGE,"1cb9c079-ea9b-4899-8069-e0e3048e911d.sketch_text.stroke-33"),sQuery(id+"FHMxAyK4CFUKdhS_1.wireOp",EDGE,"1cb9c079-ea9b-4899-8069-e0e3048e911d.sketch_text.stroke-34"),sQuery(id+"FHMxAyK4CFUKdhS_1.wireOp",EDGE,"1cb9c079-ea9b-4899-8069-e0e3048e911d.sketch_text.stroke-35"),sQuery(id+"FHMxAyK4CFUKdhS_1.wireOp",EDGE,"1cb9c079-ea9b-4899-8069-e0e3048e911d.sketch_text.stroke-36"),sQuery(id+"FHMxAyK4CFUKdhS_1.wireOp",EDGE,"1cb9c079-ea9b-4899-8069-e0e3048e911d.sketch_text.stroke-37"),sQuery(id+"FHMxAyK4CFUKdhS_1.wireOp",EDGE,"1cb9c079-ea9b-4899-8069-e0e3048e911d.sketch_text.stroke-38"),sQuery(id+"FHMxAyK4CFUKdhS_1.wireOp",EDGE,"1cb9c079-ea9b-4899-8069-e0e3048e911d.sketch_text.stroke-39"),sQuery(id+"FHMxAyK4CFUKdhS_1.wireOp",EDGE,"1cb9c079-ea9b-4899-8069-e0e3048e911d.sketch_text.stroke-40"),sQuery(id+"FHMxAyK4CFUKdhS_1.wireOp",EDGE,"1cb9c079-ea9b-4899-8069-e0e3048e911d.sketch_text.stroke-41"),sQuery(id+"FHMxAyK4CFUKdhS_1.wireOp",EDGE,"1cb9c079-ea9b-4899-8069-e0e3048e911d.sketch_text.stroke-42"),sQuery(id+"FHMxAyK4CFUKdhS_1.wireOp",EDGE,"1cb9c079-ea9b-4899-8069-e0e3048e911d.sketch_text.stroke-43"),sQuery(id+"FHMxAyK4CFUKdhS_1.wireOp",EDGE,"1cb9c079-ea9b-4899-8069-e0e3048e911d.sketch_text.stroke-44"),sQuery(id+"FHMxAyK4CFUKdhS_1.wireOp",EDGE,"1cb9c079-ea9b-4899-8069-e0e3048e911d.sketch_text.stroke-45"),sQuery(id+"FHMxAyK4CFUKdhS_1.wireOp",EDGE,"1cb9c079-ea9b-4899-8069-e0e3048e911d.sketch_text.stroke-46"),sQuery(id+"FHMxAyK4CFUKdhS_1.wireOp",EDGE,"1cb9c079-ea9b-4899-8069-e0e3048e911d.sketch_text.stroke-47"),sQuery(id+"FHMxAyK4CFUKdhS_1.wireOp",EDGE,"1cb9c079-ea9b-4899-8069-e0e3048e911d.sketch_text.stroke-48"),sQuery(id+"FHMxAyK4CFUKdhS_1.wireOp",EDGE,"1cb9c079-ea9b-4899-8069-e0e3048e911d.sketch_text.stroke-49"),sQuery(id+"FHMxAyK4CFUKdhS_1.wireOp",EDGE,"1cb9c079-ea9b-4899-8069-e0e3048e911d.sketch_text.stroke-50"),sQuery(id+"FHMxAyK4CFUKdhS_1.wireOp",EDGE,"1cb9c079-ea9b-4899-8069-e0e3048e911d.sketch_text.stroke-51"),sQuery(id+"FHMxAyK4CFUKdhS_1.wireOp",EDGE,"1cb9c079-ea9b-4899-8069-e0e3048e911d.sketch_text.stroke-52"),sQuery(id+"FHMxAyK4CFUKdhS_1.wireOp",EDGE,"1cb9c079-ea9b-4899-8069-e0e3048e911d.sketch_text.stroke-53"),sQuery(id+"FHMxAyK4CFUKdhS_1.wireOp",EDGE,"1cb9c079-ea9b-4899-8069-e0e3048e911d.sketch_text.stroke-54"),sQuery(id+"FHMxAyK4CFUKdhS_1.wireOp",EDGE,"1cb9c079-ea9b-4899-8069-e0e3048e911d.sketch_text.stroke-55"),sQuery(id+"FHMxAyK4CFUKdhS_1.wireOp",EDGE,"1cb9c079-ea9b-4899-8069-e0e3048e911d.sketch_text.stroke-56"),sQuery(id+"FHMxAyK4CFUKdhS_1.wireOp",EDGE,"1cb9c079-ea9b-4899-8069-e0e3048e911d.sketch_text.stroke-57"),sQuery(id+"FHMxAyK4CFUKdhS_1.wireOp",EDGE,"1cb9c079-ea9b-4899-8069-e0e3048e911d.sketch_text.stroke-58"),sQuery(id+"FHMxAyK4CFUKdhS_1.wireOp",EDGE,"1cb9c079-ea9b-4899-8069-e0e3048e911d.sketch_text.stroke-59"),sQuery(id+"FHMxAyK4CFUKdhS_1.wireOp",EDGE,"1cb9c079-ea9b-4899-8069-e0e3048e911d.sketch_text.stroke-60"),sQuery(id+"FHMxAyK4CFUKdhS_1.wireOp",EDGE,"1cb9c079-ea9b-4899-8069-e0e3048e911d.sketch_text.stroke-61"),sQuery(id+"FHMxAyK4CFUKdhS_1.wireOp",EDGE,"1cb9c079-ea9b-4899-8069-e0e3048e911d.sketch_text.stroke-62"),sQuery(id+"FHMxAyK4CFUKdhS_1.wireOp",EDGE,"1cb9c079-ea9b-4899-8069-e0e3048e911d.sketch_text.stroke-71"),sQuery(id+"FHMxAyK4CFUKdhS_1.wireOp",EDGE,"1cb9c079-ea9b-4899-8069-e0e3048e911d.sketch_text.stroke-72"),sQuery(id+"FHMxAyK4CFUKdhS_1.wireOp",EDGE,"1cb9c079-ea9b-4899-8069-e0e3048e911d.sketch_text.stroke-73"),sQuery(id+"FHMxAyK4CFUKdhS_1.wireOp",EDGE,"1cb9c079-ea9b-4899-8069-e0e3048e911d.sketch_text.stroke-74"),sQuery(id+"FHMxAyK4CFUKdhS_1.wireOp",EDGE,"1cb9c079-ea9b-4899-8069-e0e3048e911d.sketch_text.stroke-75"),sQuery(id+"FHMxAyK4CFUKdhS_1.wireOp",EDGE,"1cb9c079-ea9b-4899-8069-e0e3048e911d.sketch_text.stroke-76"),sQuery(id+"FHMxAyK4CFUKdhS_1.wireOp",EDGE,"1cb9c079-ea9b-4899-8069-e0e3048e911d.sketch_text.stroke-77"),sQuery(id+"FHMxAyK4CFUKdhS_1.wireOp",EDGE,"1cb9c079-ea9b-4899-8069-e0e3048e911d.sketch_text.stroke-78"),sQuery(id+"FHMxAyK4CFUKdhS_1.wireOp",EDGE,"1cb9c079-ea9b-4899-8069-e0e3048e911d.sketch_text.stroke-79"),sQuery(id+"FHMxAyK4CFUKdhS_1.wireOp",EDGE,"1cb9c079-ea9b-4899-8069-e0e3048e911d.sketch_text.stroke-80"),sQuery(id+"FHMxAyK4CFUKdhS_1.wireOp",EDGE,"1cb9c079-ea9b-4899-8069-e0e3048e911d.sketch_text.stroke-81"),sQuery(id+"FHMxAyK4CFUKdhS_1.wireOp",EDGE,"1cb9c079-ea9b-4899-8069-e0e3048e911d.sketch_text.stroke-82"),sQuery(id+"FHMxAyK4CFUKdhS_1.wireOp",EDGE,"1cb9c079-ea9b-4899-8069-e0e3048e911d.sketch_text.stroke-83"),sQuery(id+"FHMxAyK4CFUKdhS_1.wireOp",EDGE,"1cb9c079-ea9b-4899-8069-e0e3048e911d.sketch_text.stroke-84"),sQuery(id+"FHMxAyK4CFUKdhS_1.wireOp",EDGE,"1cb9c079-ea9b-4899-8069-e0e3048e911d.sketch_text.stroke-85"),sQuery(id+"FHMxAyK4CFUKdhS_1.wireOp",EDGE,"1cb9c079-ea9b-4899-8069-e0e3048e911d.sketch_text.stroke-86"),sQuery(id+"FHMxAyK4CFUKdhS_1.wireOp",EDGE,"1cb9c079-ea9b-4899-8069-e0e3048e911d.sketch_text.stroke-87"),sQuery(id+"FHMxAyK4CFUKdhS_1.wireOp",EDGE,"1cb9c079-ea9b-4899-8069-e0e3048e911d.sketch_text.stroke-88"),sQuery(id+"FHMxAyK4CFUKdhS_1.wireOp",EDGE,"1cb9c079-ea9b-4899-8069-e0e3048e911d.sketch_text.stroke-89"),sQuery(id+"FHMxAyK4CFUKdhS_1.wireOp",EDGE,"1cb9c079-ea9b-4899-8069-e0e3048e911d.sketch_text.stroke-90"),sQuery(id+"FHMxAyK4CFUKdhS_1.wireOp",EDGE,"1cb9c079-ea9b-4899-8069-e0e3048e911d.sketch_text.stroke-91"),sQuery(id+"FHMxAyK4CFUKdhS_1.wireOp",EDGE,"1cb9c079-ea9b-4899-8069-e0e3048e911d.sketch_text.stroke-92"),sQuery(id+"FHMxAyK4CFUKdhS_1.wireOp",EDGE,"1cb9c079-ea9b-4899-8069-e0e3048e911d.sketch_text.stroke-93"),sQuery(id+"FHMxAyK4CFUKdhS_1.wireOp",EDGE,"1cb9c079-ea9b-4899-8069-e0e3048e911d.sketch_text.stroke-94"),sQuery(id+"FHMxAyK4CFUKdhS_1.wireOp",EDGE,"1cb9c079-ea9b-4899-8069-e0e3048e911d.sketch_text.stroke-95"),sQuery(id+"FHMxAyK4CFUKdhS_1.wireOp",EDGE,"1cb9c079-ea9b-4899-8069-e0e3048e911d.sketch_text.stroke-96"),sQuery(id+"FHMxAyK4CFUKdhS_1.wireOp",EDGE,"1cb9c079-ea9b-4899-8069-e0e3048e911d.sketch_text.stroke-97"),sQuery(id+"FHMxAyK4CFUKdhS_1.wireOp",EDGE,"1cb9c079-ea9b-4899-8069-e0e3048e911d.sketch_text.stroke-103"),sQuery(id+"FHMxAyK4CFUKdhS_1.wireOp",EDGE,"1cb9c079-ea9b-4899-8069-e0e3048e911d.sketch_text.stroke-104"),sQuery(id+"FHMxAyK4CFUKdhS_1.wireOp",EDGE,"1cb9c079-ea9b-4899-8069-e0e3048e911d.sketch_text.stroke-105"),sQuery(id+"FHMxAyK4CFUKdhS_1.wireOp",EDGE,"1cb9c079-ea9b-4899-8069-e0e3048e911d.sketch_text.stroke-106"),sQuery(id+"FHMxAyK4CFUKdhS_1.wireOp",EDGE,"1cb9c079-ea9b-4899-8069-e0e3048e911d.sketch_text.stroke-107"),sQuery(id+"FHMxAyK4CFUKdhS_1.wireOp",EDGE,"1cb9c079-ea9b-4899-8069-e0e3048e911d.sketch_text.stroke-108"),sQuery(id+"FHMxAyK4CFUKdhS_1.wireOp",EDGE,"1cb9c079-ea9b-4899-8069-e0e3048e911d.sketch_text.stroke-109"),sQuery(id+"FHMxAyK4CFUKdhS_1.wireOp",EDGE,"1cb9c079-ea9b-4899-8069-e0e3048e911d.sketch_text.stroke-110"),sQuery(id+"FHMxAyK4CFUKdhS_1.wireOp",EDGE,"1cb9c079-ea9b-4899-8069-e0e3048e911d.sketch_text.stroke-111"),sQuery(id+"FHMxAyK4CFUKdhS_1.wireOp",EDGE,"1cb9c079-ea9b-4899-8069-e0e3048e911d.sketch_text.stroke-112"),sQuery(id+"FHMxAyK4CFUKdhS_1.wireOp",EDGE,"1cb9c079-ea9b-4899-8069-e0e3048e911d.sketch_text.stroke-113"),sQuery(id+"FHMxAyK4CFUKdhS_1.wireOp",EDGE,"1cb9c079-ea9b-4899-8069-e0e3048e911d.sketch_text.stroke-114"),sQuery(id+"FHMxAyK4CFUKdhS_1.wireOp",EDGE,"1cb9c079-ea9b-4899-8069-e0e3048e911d.sketch_text.stroke-115"),sQuery(id+"FHMxAyK4CFUKdhS_1.wireOp",EDGE,"1cb9c079-ea9b-4899-8069-e0e3048e911d.sketch_text.stroke-116"),sQuery(id+"FHMxAyK4CFUKdhS_1.wireOp",EDGE,"1cb9c079-ea9b-4899-8069-e0e3048e911d.sketch_text.stroke-117"),sQuery(id+"FHMxAyK4CFUKdhS_1.wireOp",EDGE,"1cb9c079-ea9b-4899-8069-e0e3048e911d.sketch_text.stroke-118"),sQuery(id+"FHMxAyK4CFUKdhS_1.wireOp",EDGE,"1cb9c079-ea9b-4899-8069-e0e3048e911d.sketch_text.stroke-119"),sQuery(id+"FHMxAyK4CFUKdhS_1.wireOp",EDGE,"1cb9c079-ea9b-4899-8069-e0e3048e911d.sketch_text.stroke-120"),sQuery(id+"FHMxAyK4CFUKdhS_1.wireOp",EDGE,"1cb9c079-ea9b-4899-8069-e0e3048e911d.sketch_text.stroke-121"),sQuery(id+"FHMxAyK4CFUKdhS_1.wireOp",EDGE,"1cb9c079-ea9b-4899-8069-e0e3048e911d.sketch_text.stroke-122"),sQuery(id+"FHMxAyK4CFUKdhS_1.wireOp",EDGE,"1cb9c079-ea9b-4899-8069-e0e3048e911d.sketch_text.stroke-123"),sQuery(id+"FHMxAyK4CFUKdhS_1.wireOp",EDGE,"1cb9c079-ea9b-4899-8069-e0e3048e911d.sketch_text.stroke-124"),sQuery(id+"FHMxAyK4CFUKdhS_1.wireOp",EDGE,"1cb9c079-ea9b-4899-8069-e0e3048e911d.sketch_text.stroke-125"),sQuery(id+"FHMxAyK4CFUKdhS_1.wireOp",EDGE,"1cb9c079-ea9b-4899-8069-e0e3048e911d.sketch_text.stroke-126"),sQuery(id+"FHMxAyK4CFUKdhS_1.wireOp",EDGE,"1cb9c079-ea9b-4899-8069-e0e3048e911d.sketch_text.stroke-127"),sQuery(id+"FHMxAyK4CFUKdhS_1.wireOp",EDGE,"1cb9c079-ea9b-4899-8069-e0e3048e911d.sketch_text.stroke-128"),sQuery(id+"FHMxAyK4CFUKdhS_1.wireOp",EDGE,"1cb9c079-ea9b-4899-8069-e0e3048e911d.sketch_text.stroke-129"),sQuery(id+"FHMxAyK4CFUKdhS_1.wireOp",EDGE,"1cb9c079-ea9b-4899-8069-e0e3048e911d.sketch_text.stroke-130"),sQuery(id+"FHMxAyK4CFUKdhS_1.wireOp",EDGE,"1cb9c079-ea9b-4899-8069-e0e3048e911d.sketch_text.stroke-131"),sQuery(id+"FHMxAyK4CFUKdhS_1.wireOp",EDGE,"1cb9c079-ea9b-4899-8069-e0e3048e911d.sketch_text.stroke-132"),sQuery(id+"FHMxAyK4CFUKdhS_1.wireOp",EDGE,"1cb9c079-ea9b-4899-8069-e0e3048e911d.sketch_text.stroke-133"),sQuery(id+"FHMxAyK4CFUKdhS_1.wireOp",EDGE,"1cb9c079-ea9b-4899-8069-e0e3048e911d.sketch_text.stroke-134"),sQuery(id+"FHMxAyK4CFUKdhS_1.wireOp",EDGE,"1cb9c079-ea9b-4899-8069-e0e3048e911d.sketch_text.stroke-135"),sQuery(id+"FHMxAyK4CFUKdhS_1.wireOp",EDGE,"1cb9c079-ea9b-4899-8069-e0e3048e911d.sketch_text.stroke-136"),sQuery(id+"FHMxAyK4CFUKdhS_1.wireOp",EDGE,"1cb9c079-ea9b-4899-8069-e0e3048e911d.sketch_text.stroke-137"),sQuery(id+"FHMxAyK4CFUKdhS_1.wireOp",EDGE,"1cb9c079-ea9b-4899-8069-e0e3048e911d.sketch_text.stroke-138"),sQuery(id+"FHMxAyK4CFUKdhS_1.wireOp",EDGE,"1cb9c079-ea9b-4899-8069-e0e3048e911d.sketch_text.stroke-139"),sQuery(id+"FHMxAyK4CFUKdhS_1.wireOp",EDGE,"1cb9c079-ea9b-4899-8069-e0e3048e911d.sketch_text.stroke-140"),sQuery(id+"FHMxAyK4CFUKdhS_1.wireOp",EDGE,"1cb9c079-ea9b-4899-8069-e0e3048e911d.sketch_text.stroke-141"),sQuery(id+"FHMxAyK4CFUKdhS_1.wireOp",EDGE,"1cb9c079-ea9b-4899-8069-e0e3048e911d.sketch_text.stroke-142"),sQuery(id+"FHMxAyK4CFUKdhS_1.wireOp",EDGE,"1cb9c079-ea9b-4899-8069-e0e3048e911d.sketch_text.stroke-143"),sQuery(id+"FHMxAyK4CFUKdhS_1.wireOp",EDGE,"1cb9c079-ea9b-4899-8069-e0e3048e911d.sketch_text.stroke-144"),sQuery(id+"FHMxAyK4CFUKdhS_1.wireOp",EDGE,"1cb9c079-ea9b-4899-8069-e0e3048e911d.sketch_text.stroke-145"),sQuery(id+"FHMxAyK4CFUKdhS_1.wireOp",EDGE,"1cb9c079-ea9b-4899-8069-e0e3048e911d.sketch_text.stroke-146"),sQuery(id+"FHMxAyK4CFUKdhS_1.wireOp",EDGE,"1cb9c079-ea9b-4899-8069-e0e3048e911d.sketch_text.stroke-147"),sQuery(id+"FHMxAyK4CFUKdhS_1.wireOp",EDGE,"1cb9c079-ea9b-4899-8069-e0e3048e911d.sketch_text.stroke-148"),sQuery(id+"FHMxAyK4CFUKdhS_1.wireOp",EDGE,"1cb9c079-ea9b-4899-8069-e0e3048e911d.sketch_text.stroke-149"),sQuery(id+"FHMxAyK4CFUKdhS_1.wireOp",EDGE,"1cb9c079-ea9b-4899-8069-e0e3048e911d.sketch_text.stroke-150"),sQuery(id+"FHMxAyK4CFUKdhS_1.wireOp",EDGE,"1cb9c079-ea9b-4899-8069-e0e3048e911d.sketch_text.stroke-151"),sQuery(id+"FHMxAyK4CFUKdhS_1.wireOp",EDGE,"1cb9c079-ea9b-4899-8069-e0e3048e911d.sketch_text.stroke-152"),sQuery(id+"FHMxAyK4CFUKdhS_1.wireOp",EDGE,"1cb9c079-ea9b-4899-8069-e0e3048e911d.sketch_text.stroke-153"),sQuery(id+"FHMxAyK4CFUKdhS_1.wireOp",EDGE,"1cb9c079-ea9b-4899-8069-e0e3048e911d.sketch_text.stroke-159"),sQuery(id+"FHMxAyK4CFUKdhS_1.wireOp",EDGE,"1cb9c079-ea9b-4899-8069-e0e3048e911d.sketch_text.stroke-160"),sQuery(id+"FHMxAyK4CFUKdhS_1.wireOp",EDGE,"1cb9c079-ea9b-4899-8069-e0e3048e911d.sketch_text.stroke-161"),sQuery(id+"FHMxAyK4CFUKdhS_1.wireOp",EDGE,"1cb9c079-ea9b-4899-8069-e0e3048e911d.sketch_text.stroke-162"),sQuery(id+"FHMxAyK4CFUKdhS_1.wireOp",EDGE,"1cb9c079-ea9b-4899-8069-e0e3048e911d.sketch_text.stroke-163"),sQuery(id+"FHMxAyK4CFUKdhS_1.wireOp",EDGE,"1cb9c079-ea9b-4899-8069-e0e3048e911d.sketch_text.stroke-164"),sQuery(id+"FHMxAyK4CFUKdhS_1.wireOp",EDGE,"1cb9c079-ea9b-4899-8069-e0e3048e911d.sketch_text.stroke-165"),sQuery(id+"FHMxAyK4CFUKdhS_1.wireOp",EDGE,"1cb9c079-ea9b-4899-8069-e0e3048e911d.sketch_text.stroke-166"),sQuery(id+"FHMxAyK4CFUKdhS_1.wireOp",EDGE,"1cb9c079-ea9b-4899-8069-e0e3048e911d.sketch_text.stroke-167"),sQuery(id+"FHMxAyK4CFUKdhS_1.wireOp",EDGE,"1cb9c079-ea9b-4899-8069-e0e3048e911d.sketch_text.stroke-168"),sQuery(id+"FHMxAyK4CFUKdhS_1.wireOp",EDGE,"1cb9c079-ea9b-4899-8069-e0e3048e911d.sketch_text.stroke-169"),sQuery(id+"FHMxAyK4CFUKdhS_1.wireOp",EDGE,"1cb9c079-ea9b-4899-8069-e0e3048e911d.sketch_text.stroke-170"),sQuery(id+"FHMxAyK4CFUKdhS_1.wireOp",EDGE,"1cb9c079-ea9b-4899-8069-e0e3048e911d.sketch_text.stroke-171"),sQuery(id+"FHMxAyK4CFUKdhS_1.wireOp",EDGE,"1cb9c079-ea9b-4899-8069-e0e3048e911d.sketch_text.stroke-172"),sQuery(id+"FHMxAyK4CFUKdhS_1.wireOp",EDGE,"1cb9c079-ea9b-4899-8069-e0e3048e911d.sketch_text.stroke-173"),sQuery(id+"FHMxAyK4CFUKdhS_1.wireOp",EDGE,"1cb9c079-ea9b-4899-8069-e0e3048e911d.sketch_text.stroke-174"),sQuery(id+"FHMxAyK4CFUKdhS_1.wireOp",EDGE,"1cb9c079-ea9b-4899-8069-e0e3048e911d.sketch_text.stroke-175"),sQuery(id+"FHMxAyK4CFUKdhS_1.wireOp",EDGE,"1cb9c079-ea9b-4899-8069-e0e3048e911d.sketch_text.stroke-176"),sQuery(id+"FHMxAyK4CFUKdhS_1.wireOp",EDGE,"1cb9c079-ea9b-4899-8069-e0e3048e911d.sketch_text.stroke-177"),sQuery(id+"FHMxAyK4CFUKdhS_1.wireOp",EDGE,"1cb9c079-ea9b-4899-8069-e0e3048e911d.sketch_text.stroke-178"),sQuery(id+"FHMxAyK4CFUKdhS_1.wireOp",EDGE,"1cb9c079-ea9b-4899-8069-e0e3048e911d.sketch_text.stroke-179"),sQuery(id+"FHMxAyK4CFUKdhS_1.wireOp",EDGE,"1cb9c079-ea9b-4899-8069-e0e3048e911d.sketch_text.stroke-180"),sQuery(id+"F2.wireOp",EDGE,"8007402e-1a4e-4a06-85a5-2af08e553504"),subQ0])],"isStart":true}),makeQuery(id+"F3.opExtrude","SWEPT_FACE",FACE,{"disambiguationData":[OSD([subQ0])]})])],"derivedFrom":makeQuery(id+"F3.opExtrude","CAP_EDGE",EDGE,{"disambiguationData":[OSD([subQ0])],"isStart":true})});}
            var Q7;
            {var subQ0=sQuery(id+"F0.wireOp",EDGE,"E0.right");var subQ1=sQuery(id+"F0.wireOp",EDGE,"E0.top");var subQ2=sQuery(id+"F2.wireOp",EDGE,"6ee83ff3-586e-4dbe-aaea-af71240543bd");var subQ3=sQuery(id+"F0.wireOp",EDGE,"E0.bottom");Q7=makeQuery(id+"F3.boolean.opBoolean","SPLIT",EDGE,{"disambiguationData":[TD([makeQuery(id+"F1.opExtrude","CAP_FACE",FACE,{"disambiguationData":[OSD([subQ3,subQ1,sQuery(id+"F0.wireOp",EDGE,"E0.left"),subQ0])],"isStart":false}),makeQuery(id+"F1.opExtrude","SWEPT_FACE",FACE,{"disambiguationData":[OSD([subQ1])]}),makeQuery(id+"F1.opExtrude","SWEPT_FACE",FACE,{"disambiguationData":[OSD([subQ0])]}),makeQuery(id+"F3.opExtrude","CAP_FACE",FACE,{"disambiguationData":[OSD([subQ3,sQuery(id+"FQ5JFwxVdaqARUP_1.wireOp",EDGE,"fcba4419-a2ee-464f-be9d-58f11bf3418b.sketch_text.stroke-0"),sQuery(id+"FQ5JFwxVdaqARUP_1.wireOp",EDGE,"fcba4419-a2ee-464f-be9d-58f11bf3418b.sketch_text.stroke-1"),sQuery(id+"FQ5JFwxVdaqARUP_1.wireOp",EDGE,"fcba4419-a2ee-464f-be9d-58f11bf3418b.sketch_text.stroke-2"),sQuery(id+"FQ5JFwxVdaqARUP_1.wireOp",EDGE,"fcba4419-a2ee-464f-be9d-58f11bf3418b.sketch_text.stroke-3"),sQuery(id+"FQ5JFwxVdaqARUP_1.wireOp",EDGE,"fcba4419-a2ee-464f-be9d-58f11bf3418b.sketch_text.stroke-4"),sQuery(id+"FQ5JFwxVdaqARUP_1.wireOp",EDGE,"fcba4419-a2ee-464f-be9d-58f11bf3418b.sketch_text.stroke-5"),sQuery(id+"FQ5JFwxVdaqARUP_1.wireOp",EDGE,"fcba4419-a2ee-464f-be9d-58f11bf3418b.sketch_text.stroke-6"),sQuery(id+"FQ5JFwxVdaqARUP_1.wireOp",EDGE,"fcba4419-a2ee-464f-be9d-58f11bf3418b.sketch_text.stroke-7"),sQuery(id+"FQ5JFwxVdaqARUP_1.wireOp",EDGE,"fcba4419-a2ee-464f-be9d-58f11bf3418b.sketch_text.stroke-8"),sQuery(id+"FQ5JFwxVdaqARUP_1.wireOp",EDGE,"fcba4419-a2ee-464f-be9d-58f11bf3418b.sketch_text.stroke-9"),sQuery(id+"FQ5JFwxVdaqARUP_1.wireOp",EDGE,"fcba4419-a2ee-464f-be9d-58f11bf3418b.sketch_text.stroke-10"),sQuery(id+"FQ5JFwxVdaqARUP_1.wireOp",EDGE,"fcba4419-a2ee-464f-be9d-58f11bf3418b.sketch_text.stroke-11"),sQuery(id+"FQ5JFwxVdaqARUP_1.wireOp",EDGE,"fcba4419-a2ee-464f-be9d-58f11bf3418b.sketch_text.stroke-12"),sQuery(id+"FQ5JFwxVdaqARUP_1.wireOp",EDGE,"fcba4419-a2ee-464f-be9d-58f11bf3418b.sketch_text.stroke-13"),sQuery(id+"FQ5JFwxVdaqARUP_1.wireOp",EDGE,"fcba4419-a2ee-464f-be9d-58f11bf3418b.sketch_text.stroke-14"),sQuery(id+"FQ5JFwxVdaqARUP_1.wireOp",EDGE,"fcba4419-a2ee-464f-be9d-58f11bf3418b.sketch_text.stroke-15"),sQuery(id+"FQ5JFwxVdaqARUP_1.wireOp",EDGE,"fcba4419-a2ee-464f-be9d-58f11bf3418b.sketch_text.stroke-16"),sQuery(id+"FQ5JFwxVdaqARUP_1.wireOp",EDGE,"fcba4419-a2ee-464f-be9d-58f11bf3418b.sketch_text.stroke-17"),sQuery(id+"FQ5JFwxVdaqARUP_1.wireOp",EDGE,"fcba4419-a2ee-464f-be9d-58f11bf3418b.sketch_text.stroke-18"),sQuery(id+"FQ5JFwxVdaqARUP_1.wireOp",EDGE,"fcba4419-a2ee-464f-be9d-58f11bf3418b.sketch_text.stroke-19"),sQuery(id+"FQ5JFwxVdaqARUP_1.wireOp",EDGE,"fcba4419-a2ee-464f-be9d-58f11bf3418b.sketch_text.stroke-20"),sQuery(id+"FQ5JFwxVdaqARUP_1.wireOp",EDGE,"fcba4419-a2ee-464f-be9d-58f11bf3418b.sketch_text.stroke-21"),sQuery(id+"FQ5JFwxVdaqARUP_1.wireOp",EDGE,"fcba4419-a2ee-464f-be9d-58f11bf3418b.sketch_text.stroke-22"),sQuery(id+"FQ5JFwxVdaqARUP_1.wireOp",EDGE,"fcba4419-a2ee-464f-be9d-58f11bf3418b.sketch_text.stroke-23"),sQuery(id+"FQ5JFwxVdaqARUP_1.wireOp",EDGE,"fcba4419-a2ee-464f-be9d-58f11bf3418b.sketch_text.stroke-24"),sQuery(id+"FQ5JFwxVdaqARUP_1.wireOp",EDGE,"fcba4419-a2ee-464f-be9d-58f11bf3418b.sketch_text.stroke-25"),sQuery(id+"FQ5JFwxVdaqARUP_1.wireOp",EDGE,"fcba4419-a2ee-464f-be9d-58f11bf3418b.sketch_text.stroke-26"),sQuery(id+"FQ5JFwxVdaqARUP_1.wireOp",EDGE,"fcba4419-a2ee-464f-be9d-58f11bf3418b.sketch_text.stroke-27"),sQuery(id+"FQ5JFwxVdaqARUP_1.wireOp",EDGE,"fcba4419-a2ee-464f-be9d-58f11bf3418b.sketch_text.stroke-28"),sQuery(id+"FQ5JFwxVdaqARUP_1.wireOp",EDGE,"fcba4419-a2ee-464f-be9d-58f11bf3418b.sketch_text.stroke-29"),sQuery(id+"FQ5JFwxVdaqARUP_1.wireOp",EDGE,"fcba4419-a2ee-464f-be9d-58f11bf3418b.sketch_text.stroke-30"),sQuery(id+"FQ5JFwxVdaqARUP_1.wireOp",EDGE,"fcba4419-a2ee-464f-be9d-58f11bf3418b.sketch_text.stroke-31"),sQuery(id+"FQ5JFwxVdaqARUP_1.wireOp",EDGE,"fcba4419-a2ee-464f-be9d-58f11bf3418b.sketch_text.stroke-32"),sQuery(id+"FQ5JFwxVdaqARUP_1.wireOp",EDGE,"fcba4419-a2ee-464f-be9d-58f11bf3418b.sketch_text.stroke-33"),sQuery(id+"FQ5JFwxVdaqARUP_1.wireOp",EDGE,"fcba4419-a2ee-464f-be9d-58f11bf3418b.sketch_text.stroke-34"),sQuery(id+"FQ5JFwxVdaqARUP_1.wireOp",EDGE,"fcba4419-a2ee-464f-be9d-58f11bf3418b.sketch_text.stroke-35"),sQuery(id+"FQ5JFwxVdaqARUP_1.wireOp",EDGE,"fcba4419-a2ee-464f-be9d-58f11bf3418b.sketch_text.stroke-36"),sQuery(id+"FQ5JFwxVdaqARUP_1.wireOp",EDGE,"fcba4419-a2ee-464f-be9d-58f11bf3418b.sketch_text.stroke-37"),sQuery(id+"FQ5JFwxVdaqARUP_1.wireOp",EDGE,"fcba4419-a2ee-464f-be9d-58f11bf3418b.sketch_text.stroke-38"),sQuery(id+"FQ5JFwxVdaqARUP_1.wireOp",EDGE,"fcba4419-a2ee-464f-be9d-58f11bf3418b.sketch_text.stroke-39"),sQuery(id+"FQ5JFwxVdaqARUP_1.wireOp",EDGE,"fcba4419-a2ee-464f-be9d-58f11bf3418b.sketch_text.stroke-40"),sQuery(id+"FQ5JFwxVdaqARUP_1.wireOp",EDGE,"fcba4419-a2ee-464f-be9d-58f11bf3418b.sketch_text.stroke-41"),sQuery(id+"FQ5JFwxVdaqARUP_1.wireOp",EDGE,"fcba4419-a2ee-464f-be9d-58f11bf3418b.sketch_text.stroke-42"),sQuery(id+"FQ5JFwxVdaqARUP_1.wireOp",EDGE,"fcba4419-a2ee-464f-be9d-58f11bf3418b.sketch_text.stroke-43"),sQuery(id+"FQ5JFwxVdaqARUP_1.wireOp",EDGE,"fcba4419-a2ee-464f-be9d-58f11bf3418b.sketch_text.stroke-44"),sQuery(id+"FQ5JFwxVdaqARUP_1.wireOp",EDGE,"fcba4419-a2ee-464f-be9d-58f11bf3418b.sketch_text.stroke-45"),sQuery(id+"FQ5JFwxVdaqARUP_1.wireOp",EDGE,"fcba4419-a2ee-464f-be9d-58f11bf3418b.sketch_text.stroke-46"),sQuery(id+"FQ5JFwxVdaqARUP_1.wireOp",EDGE,"fcba4419-a2ee-464f-be9d-58f11bf3418b.sketch_text.stroke-47"),sQuery(id+"FQ5JFwxVdaqARUP_1.wireOp",EDGE,"fcba4419-a2ee-464f-be9d-58f11bf3418b.sketch_text.stroke-48"),sQuery(id+"FQ5JFwxVdaqARUP_1.wireOp",EDGE,"fcba4419-a2ee-464f-be9d-58f11bf3418b.sketch_text.stroke-49"),sQuery(id+"FQ5JFwxVdaqARUP_1.wireOp",EDGE,"fcba4419-a2ee-464f-be9d-58f11bf3418b.sketch_text.stroke-50"),sQuery(id+"FQ5JFwxVdaqARUP_1.wireOp",EDGE,"fcba4419-a2ee-464f-be9d-58f11bf3418b.sketch_text.stroke-51"),sQuery(id+"FQ5JFwxVdaqARUP_1.wireOp",EDGE,"fcba4419-a2ee-464f-be9d-58f11bf3418b.sketch_text.stroke-52"),sQuery(id+"FQ5JFwxVdaqARUP_1.wireOp",EDGE,"fcba4419-a2ee-464f-be9d-58f11bf3418b.sketch_text.stroke-53"),sQuery(id+"FQ5JFwxVdaqARUP_1.wireOp",EDGE,"fcba4419-a2ee-464f-be9d-58f11bf3418b.sketch_text.stroke-54"),sQuery(id+"FQ5JFwxVdaqARUP_1.wireOp",EDGE,"fcba4419-a2ee-464f-be9d-58f11bf3418b.sketch_text.stroke-55"),sQuery(id+"FQ5JFwxVdaqARUP_1.wireOp",EDGE,"fcba4419-a2ee-464f-be9d-58f11bf3418b.sketch_text.stroke-56"),sQuery(id+"FQ5JFwxVdaqARUP_1.wireOp",EDGE,"fcba4419-a2ee-464f-be9d-58f11bf3418b.sketch_text.stroke-57"),sQuery(id+"FQ5JFwxVdaqARUP_1.wireOp",EDGE,"fcba4419-a2ee-464f-be9d-58f11bf3418b.sketch_text.stroke-58"),sQuery(id+"FQ5JFwxVdaqARUP_1.wireOp",EDGE,"fcba4419-a2ee-464f-be9d-58f11bf3418b.sketch_text.stroke-59"),sQuery(id+"FQ5JFwxVdaqARUP_1.wireOp",EDGE,"fcba4419-a2ee-464f-be9d-58f11bf3418b.sketch_text.stroke-60"),sQuery(id+"FQ5JFwxVdaqARUP_1.wireOp",EDGE,"fcba4419-a2ee-464f-be9d-58f11bf3418b.sketch_text.stroke-61"),sQuery(id+"FQ5JFwxVdaqARUP_1.wireOp",EDGE,"fcba4419-a2ee-464f-be9d-58f11bf3418b.sketch_text.stroke-62"),sQuery(id+"FQ5JFwxVdaqARUP_1.wireOp",EDGE,"fcba4419-a2ee-464f-be9d-58f11bf3418b.sketch_text.stroke-63"),sQuery(id+"FQ5JFwxVdaqARUP_1.wireOp",EDGE,"fcba4419-a2ee-464f-be9d-58f11bf3418b.sketch_text.stroke-64"),sQuery(id+"FQ5JFwxVdaqARUP_1.wireOp",EDGE,"fcba4419-a2ee-464f-be9d-58f11bf3418b.sketch_text.stroke-65"),sQuery(id+"FQ5JFwxVdaqARUP_1.wireOp",EDGE,"fcba4419-a2ee-464f-be9d-58f11bf3418b.sketch_text.stroke-66"),sQuery(id+"FQ5JFwxVdaqARUP_1.wireOp",EDGE,"fcba4419-a2ee-464f-be9d-58f11bf3418b.sketch_text.stroke-67"),sQuery(id+"FQ5JFwxVdaqARUP_1.wireOp",EDGE,"fcba4419-a2ee-464f-be9d-58f11bf3418b.sketch_text.stroke-68"),sQuery(id+"FQ5JFwxVdaqARUP_1.wireOp",EDGE,"fcba4419-a2ee-464f-be9d-58f11bf3418b.sketch_text.stroke-69"),sQuery(id+"FQ5JFwxVdaqARUP_1.wireOp",EDGE,"fcba4419-a2ee-464f-be9d-58f11bf3418b.sketch_text.stroke-70"),sQuery(id+"FQ5JFwxVdaqARUP_1.wireOp",EDGE,"fcba4419-a2ee-464f-be9d-58f11bf3418b.sketch_text.stroke-71"),sQuery(id+"FQ5JFwxVdaqARUP_1.wireOp",EDGE,"fcba4419-a2ee-464f-be9d-58f11bf3418b.sketch_text.stroke-72"),sQuery(id+"FQ5JFwxVdaqARUP_1.wireOp",EDGE,"fcba4419-a2ee-464f-be9d-58f11bf3418b.sketch_text.stroke-73"),sQuery(id+"FQ5JFwxVdaqARUP_1.wireOp",EDGE,"fcba4419-a2ee-464f-be9d-58f11bf3418b.sketch_text.stroke-74"),sQuery(id+"FQ5JFwxVdaqARUP_1.wireOp",EDGE,"fcba4419-a2ee-464f-be9d-58f11bf3418b.sketch_text.stroke-75"),sQuery(id+"FQ5JFwxVdaqARUP_1.wireOp",EDGE,"fcba4419-a2ee-464f-be9d-58f11bf3418b.sketch_text.stroke-76"),sQuery(id+"FQ5JFwxVdaqARUP_1.wireOp",EDGE,"fcba4419-a2ee-464f-be9d-58f11bf3418b.sketch_text.stroke-77"),sQuery(id+"FQ5JFwxVdaqARUP_1.wireOp",EDGE,"fcba4419-a2ee-464f-be9d-58f11bf3418b.sketch_text.stroke-78"),sQuery(id+"FQ5JFwxVdaqARUP_1.wireOp",EDGE,"fcba4419-a2ee-464f-be9d-58f11bf3418b.sketch_text.stroke-79"),sQuery(id+"FQ5JFwxVdaqARUP_1.wireOp",EDGE,"fcba4419-a2ee-464f-be9d-58f11bf3418b.sketch_text.stroke-80"),sQuery(id+"FQ5JFwxVdaqARUP_1.wireOp",EDGE,"fcba4419-a2ee-464f-be9d-58f11bf3418b.sketch_text.stroke-81"),sQuery(id+"FQ5JFwxVdaqARUP_1.wireOp",EDGE,"fcba4419-a2ee-464f-be9d-58f11bf3418b.sketch_text.stroke-82"),sQuery(id+"FQ5JFwxVdaqARUP_1.wireOp",EDGE,"fcba4419-a2ee-464f-be9d-58f11bf3418b.sketch_text.stroke-83"),sQuery(id+"FQ5JFwxVdaqARUP_1.wireOp",EDGE,"fcba4419-a2ee-464f-be9d-58f11bf3418b.sketch_text.stroke-84"),sQuery(id+"FQ5JFwxVdaqARUP_1.wireOp",EDGE,"fcba4419-a2ee-464f-be9d-58f11bf3418b.sketch_text.stroke-85"),sQuery(id+"FQ5JFwxVdaqARUP_1.wireOp",EDGE,"fcba4419-a2ee-464f-be9d-58f11bf3418b.sketch_text.stroke-86"),sQuery(id+"FQ5JFwxVdaqARUP_1.wireOp",EDGE,"fcba4419-a2ee-464f-be9d-58f11bf3418b.sketch_text.stroke-87"),sQuery(id+"FQ5JFwxVdaqARUP_1.wireOp",EDGE,"fcba4419-a2ee-464f-be9d-58f11bf3418b.sketch_text.stroke-88"),sQuery(id+"FQ5JFwxVdaqARUP_1.wireOp",EDGE,"fcba4419-a2ee-464f-be9d-58f11bf3418b.sketch_text.stroke-89"),sQuery(id+"FQ5JFwxVdaqARUP_1.wireOp",EDGE,"fcba4419-a2ee-464f-be9d-58f11bf3418b.sketch_text.stroke-90"),sQuery(id+"FQ5JFwxVdaqARUP_1.wireOp",EDGE,"fcba4419-a2ee-464f-be9d-58f11bf3418b.sketch_text.stroke-91"),sQuery(id+"FQ5JFwxVdaqARUP_1.wireOp",EDGE,"fcba4419-a2ee-464f-be9d-58f11bf3418b.sketch_text.stroke-92"),sQuery(id+"FQ5JFwxVdaqARUP_1.wireOp",EDGE,"fcba4419-a2ee-464f-be9d-58f11bf3418b.sketch_text.stroke-93"),sQuery(id+"FQ5JFwxVdaqARUP_1.wireOp",EDGE,"fcba4419-a2ee-464f-be9d-58f11bf3418b.sketch_text.stroke-94"),sQuery(id+"FQ5JFwxVdaqARUP_1.wireOp",EDGE,"fcba4419-a2ee-464f-be9d-58f11bf3418b.sketch_text.stroke-95"),sQuery(id+"FQ5JFwxVdaqARUP_1.wireOp",EDGE,"fcba4419-a2ee-464f-be9d-58f11bf3418b.sketch_text.stroke-96"),sQuery(id+"FQ5JFwxVdaqARUP_1.wireOp",EDGE,"fcba4419-a2ee-464f-be9d-58f11bf3418b.sketch_text.stroke-97"),sQuery(id+"FQ5JFwxVdaqARUP_1.wireOp",EDGE,"fcba4419-a2ee-464f-be9d-58f11bf3418b.sketch_text.stroke-98"),sQuery(id+"FQ5JFwxVdaqARUP_1.wireOp",EDGE,"fcba4419-a2ee-464f-be9d-58f11bf3418b.sketch_text.stroke-99"),sQuery(id+"FQ5JFwxVdaqARUP_1.wireOp",EDGE,"fcba4419-a2ee-464f-be9d-58f11bf3418b.sketch_text.stroke-100"),sQuery(id+"FQ5JFwxVdaqARUP_1.wireOp",EDGE,"fcba4419-a2ee-464f-be9d-58f11bf3418b.sketch_text.stroke-101"),sQuery(id+"FQ5JFwxVdaqARUP_1.wireOp",EDGE,"fcba4419-a2ee-464f-be9d-58f11bf3418b.sketch_text.stroke-102"),sQuery(id+"FQ5JFwxVdaqARUP_1.wireOp",EDGE,"fcba4419-a2ee-464f-be9d-58f11bf3418b.sketch_text.stroke-103"),sQuery(id+"FQ5JFwxVdaqARUP_1.wireOp",EDGE,"fcba4419-a2ee-464f-be9d-58f11bf3418b.sketch_text.stroke-104"),sQuery(id+"FQ5JFwxVdaqARUP_1.wireOp",EDGE,"fcba4419-a2ee-464f-be9d-58f11bf3418b.sketch_text.stroke-105"),sQuery(id+"FQ5JFwxVdaqARUP_1.wireOp",EDGE,"fcba4419-a2ee-464f-be9d-58f11bf3418b.sketch_text.stroke-106"),sQuery(id+"FQ5JFwxVdaqARUP_1.wireOp",EDGE,"fcba4419-a2ee-464f-be9d-58f11bf3418b.sketch_text.stroke-107"),sQuery(id+"FQ5JFwxVdaqARUP_1.wireOp",EDGE,"fcba4419-a2ee-464f-be9d-58f11bf3418b.sketch_text.stroke-108"),sQuery(id+"FQ5JFwxVdaqARUP_1.wireOp",EDGE,"fcba4419-a2ee-464f-be9d-58f11bf3418b.sketch_text.stroke-109"),sQuery(id+"FQ5JFwxVdaqARUP_1.wireOp",EDGE,"fcba4419-a2ee-464f-be9d-58f11bf3418b.sketch_text.stroke-110"),sQuery(id+"FQ5JFwxVdaqARUP_1.wireOp",EDGE,"fcba4419-a2ee-464f-be9d-58f11bf3418b.sketch_text.stroke-111"),sQuery(id+"FQ5JFwxVdaqARUP_1.wireOp",EDGE,"fcba4419-a2ee-464f-be9d-58f11bf3418b.sketch_text.stroke-112"),sQuery(id+"FQ5JFwxVdaqARUP_1.wireOp",EDGE,"fcba4419-a2ee-464f-be9d-58f11bf3418b.sketch_text.stroke-113"),sQuery(id+"FQ5JFwxVdaqARUP_1.wireOp",EDGE,"fcba4419-a2ee-464f-be9d-58f11bf3418b.sketch_text.stroke-114"),sQuery(id+"FQ5JFwxVdaqARUP_1.wireOp",EDGE,"fcba4419-a2ee-464f-be9d-58f11bf3418b.sketch_text.stroke-115"),sQuery(id+"FQ5JFwxVdaqARUP_1.wireOp",EDGE,"fcba4419-a2ee-464f-be9d-58f11bf3418b.sketch_text.stroke-116"),sQuery(id+"FQ5JFwxVdaqARUP_1.wireOp",EDGE,"fcba4419-a2ee-464f-be9d-58f11bf3418b.sketch_text.stroke-117"),sQuery(id+"FQ5JFwxVdaqARUP_1.wireOp",EDGE,"fcba4419-a2ee-464f-be9d-58f11bf3418b.sketch_text.stroke-118"),sQuery(id+"FQ5JFwxVdaqARUP_1.wireOp",EDGE,"fcba4419-a2ee-464f-be9d-58f11bf3418b.sketch_text.stroke-119"),sQuery(id+"FQ5JFwxVdaqARUP_1.wireOp",EDGE,"fcba4419-a2ee-464f-be9d-58f11bf3418b.sketch_text.stroke-120"),sQuery(id+"FQ5JFwxVdaqARUP_1.wireOp",EDGE,"fcba4419-a2ee-464f-be9d-58f11bf3418b.sketch_text.stroke-121"),sQuery(id+"FQ5JFwxVdaqARUP_1.wireOp",EDGE,"fcba4419-a2ee-464f-be9d-58f11bf3418b.sketch_text.stroke-122"),sQuery(id+"FQ5JFwxVdaqARUP_1.wireOp",EDGE,"fcba4419-a2ee-464f-be9d-58f11bf3418b.sketch_text.stroke-123"),sQuery(id+"FQ5JFwxVdaqARUP_1.wireOp",EDGE,"fcba4419-a2ee-464f-be9d-58f11bf3418b.sketch_text.stroke-124"),sQuery(id+"FQ5JFwxVdaqARUP_1.wireOp",EDGE,"fcba4419-a2ee-464f-be9d-58f11bf3418b.sketch_text.stroke-125"),sQuery(id+"FQ5JFwxVdaqARUP_1.wireOp",EDGE,"fcba4419-a2ee-464f-be9d-58f11bf3418b.sketch_text.stroke-126"),sQuery(id+"FQ5JFwxVdaqARUP_1.wireOp",EDGE,"fcba4419-a2ee-464f-be9d-58f11bf3418b.sketch_text.stroke-127"),sQuery(id+"FQ5JFwxVdaqARUP_1.wireOp",EDGE,"fcba4419-a2ee-464f-be9d-58f11bf3418b.sketch_text.stroke-128"),sQuery(id+"FQ5JFwxVdaqARUP_1.wireOp",EDGE,"fcba4419-a2ee-464f-be9d-58f11bf3418b.sketch_text.stroke-129"),sQuery(id+"FQ5JFwxVdaqARUP_1.wireOp",EDGE,"fcba4419-a2ee-464f-be9d-58f11bf3418b.sketch_text.stroke-130"),sQuery(id+"FQ5JFwxVdaqARUP_1.wireOp",EDGE,"fcba4419-a2ee-464f-be9d-58f11bf3418b.sketch_text.stroke-131"),sQuery(id+"FQ5JFwxVdaqARUP_1.wireOp",EDGE,"fcba4419-a2ee-464f-be9d-58f11bf3418b.sketch_text.stroke-132"),sQuery(id+"FQ5JFwxVdaqARUP_1.wireOp",EDGE,"fcba4419-a2ee-464f-be9d-58f11bf3418b.sketch_text.stroke-133"),sQuery(id+"FQ5JFwxVdaqARUP_1.wireOp",EDGE,"fcba4419-a2ee-464f-be9d-58f11bf3418b.sketch_text.stroke-134"),sQuery(id+"FQ5JFwxVdaqARUP_1.wireOp",EDGE,"fcba4419-a2ee-464f-be9d-58f11bf3418b.sketch_text.stroke-135"),sQuery(id+"FQ5JFwxVdaqARUP_1.wireOp",EDGE,"fcba4419-a2ee-464f-be9d-58f11bf3418b.sketch_text.stroke-136"),sQuery(id+"FQ5JFwxVdaqARUP_1.wireOp",EDGE,"fcba4419-a2ee-464f-be9d-58f11bf3418b.sketch_text.stroke-137"),sQuery(id+"FQ5JFwxVdaqARUP_1.wireOp",EDGE,"fcba4419-a2ee-464f-be9d-58f11bf3418b.sketch_text.stroke-138"),sQuery(id+"FQ5JFwxVdaqARUP_1.wireOp",EDGE,"fcba4419-a2ee-464f-be9d-58f11bf3418b.sketch_text.stroke-139"),sQuery(id+"FQ5JFwxVdaqARUP_1.wireOp",EDGE,"fcba4419-a2ee-464f-be9d-58f11bf3418b.sketch_text.stroke-140"),sQuery(id+"FQ5JFwxVdaqARUP_1.wireOp",EDGE,"fcba4419-a2ee-464f-be9d-58f11bf3418b.sketch_text.stroke-141"),sQuery(id+"FQ5JFwxVdaqARUP_1.wireOp",EDGE,"fcba4419-a2ee-464f-be9d-58f11bf3418b.sketch_text.stroke-142"),sQuery(id+"FQ5JFwxVdaqARUP_1.wireOp",EDGE,"fcba4419-a2ee-464f-be9d-58f11bf3418b.sketch_text.stroke-143"),sQuery(id+"FQ5JFwxVdaqARUP_1.wireOp",EDGE,"fcba4419-a2ee-464f-be9d-58f11bf3418b.sketch_text.stroke-144"),sQuery(id+"FQ5JFwxVdaqARUP_1.wireOp",EDGE,"fcba4419-a2ee-464f-be9d-58f11bf3418b.sketch_text.stroke-145"),sQuery(id+"FQ5JFwxVdaqARUP_1.wireOp",EDGE,"fcba4419-a2ee-464f-be9d-58f11bf3418b.sketch_text.stroke-146"),sQuery(id+"FQ5JFwxVdaqARUP_1.wireOp",EDGE,"fcba4419-a2ee-464f-be9d-58f11bf3418b.sketch_text.stroke-147"),sQuery(id+"FQ5JFwxVdaqARUP_1.wireOp",EDGE,"fcba4419-a2ee-464f-be9d-58f11bf3418b.sketch_text.stroke-148"),sQuery(id+"FQ5JFwxVdaqARUP_1.wireOp",EDGE,"fcba4419-a2ee-464f-be9d-58f11bf3418b.sketch_text.stroke-149"),sQuery(id+"FQ5JFwxVdaqARUP_1.wireOp",EDGE,"fcba4419-a2ee-464f-be9d-58f11bf3418b.sketch_text.stroke-150"),sQuery(id+"FQ5JFwxVdaqARUP_1.wireOp",EDGE,"fcba4419-a2ee-464f-be9d-58f11bf3418b.sketch_text.stroke-151"),sQuery(id+"FQ5JFwxVdaqARUP_1.wireOp",EDGE,"fcba4419-a2ee-464f-be9d-58f11bf3418b.sketch_text.stroke-152"),sQuery(id+"FQ5JFwxVdaqARUP_1.wireOp",EDGE,"fcba4419-a2ee-464f-be9d-58f11bf3418b.sketch_text.stroke-153"),sQuery(id+"FQ5JFwxVdaqARUP_1.wireOp",EDGE,"fcba4419-a2ee-464f-be9d-58f11bf3418b.sketch_text.stroke-154"),sQuery(id+"FQ5JFwxVdaqARUP_1.wireOp",EDGE,"fcba4419-a2ee-464f-be9d-58f11bf3418b.sketch_text.stroke-155"),sQuery(id+"FQ5JFwxVdaqARUP_1.wireOp",EDGE,"fcba4419-a2ee-464f-be9d-58f11bf3418b.sketch_text.stroke-156"),sQuery(id+"FQ5JFwxVdaqARUP_1.wireOp",EDGE,"fcba4419-a2ee-464f-be9d-58f11bf3418b.sketch_text.stroke-157"),sQuery(id+"FQ5JFwxVdaqARUP_1.wireOp",EDGE,"fcba4419-a2ee-464f-be9d-58f11bf3418b.sketch_text.stroke-158"),sQuery(id+"FQ5JFwxVdaqARUP_1.wireOp",EDGE,"fcba4419-a2ee-464f-be9d-58f11bf3418b.sketch_text.stroke-159"),sQuery(id+"FQ5JFwxVdaqARUP_1.wireOp",EDGE,"fcba4419-a2ee-464f-be9d-58f11bf3418b.sketch_text.stroke-160"),sQuery(id+"FQ5JFwxVdaqARUP_1.wireOp",EDGE,"fcba4419-a2ee-464f-be9d-58f11bf3418b.sketch_text.stroke-161"),sQuery(id+"FQ5JFwxVdaqARUP_1.wireOp",EDGE,"fcba4419-a2ee-464f-be9d-58f11bf3418b.sketch_text.stroke-162"),sQuery(id+"FQ5JFwxVdaqARUP_1.wireOp",EDGE,"fcba4419-a2ee-464f-be9d-58f11bf3418b.sketch_text.stroke-163"),sQuery(id+"FQ5JFwxVdaqARUP_1.wireOp",EDGE,"fcba4419-a2ee-464f-be9d-58f11bf3418b.sketch_text.stroke-164"),sQuery(id+"FQ5JFwxVdaqARUP_1.wireOp",EDGE,"fcba4419-a2ee-464f-be9d-58f11bf3418b.sketch_text.stroke-165"),sQuery(id+"FQ5JFwxVdaqARUP_1.wireOp",EDGE,"fcba4419-a2ee-464f-be9d-58f11bf3418b.sketch_text.stroke-166"),sQuery(id+"FQ5JFwxVdaqARUP_1.wireOp",EDGE,"fcba4419-a2ee-464f-be9d-58f11bf3418b.sketch_text.stroke-167"),sQuery(id+"FQ5JFwxVdaqARUP_1.wireOp",EDGE,"fcba4419-a2ee-464f-be9d-58f11bf3418b.sketch_text.stroke-168"),sQuery(id+"FQ5JFwxVdaqARUP_1.wireOp",EDGE,"fcba4419-a2ee-464f-be9d-58f11bf3418b.sketch_text.stroke-169"),sQuery(id+"FQ5JFwxVdaqARUP_1.wireOp",EDGE,"fcba4419-a2ee-464f-be9d-58f11bf3418b.sketch_text.stroke-170"),sQuery(id+"FQ5JFwxVdaqARUP_1.wireOp",EDGE,"fcba4419-a2ee-464f-be9d-58f11bf3418b.sketch_text.stroke-171"),sQuery(id+"FQ5JFwxVdaqARUP_1.wireOp",EDGE,"fcba4419-a2ee-464f-be9d-58f11bf3418b.sketch_text.stroke-172"),sQuery(id+"FQ5JFwxVdaqARUP_1.wireOp",EDGE,"fcba4419-a2ee-464f-be9d-58f11bf3418b.sketch_text.stroke-173"),sQuery(id+"FHMxAyK4CFUKdhS_1.wireOp",EDGE,"1cb9c079-ea9b-4899-8069-e0e3048e911d.sketch_text.stroke-0"),sQuery(id+"FHMxAyK4CFUKdhS_1.wireOp",EDGE,"1cb9c079-ea9b-4899-8069-e0e3048e911d.sketch_text.stroke-1"),sQuery(id+"FHMxAyK4CFUKdhS_1.wireOp",EDGE,"1cb9c079-ea9b-4899-8069-e0e3048e911d.sketch_text.stroke-2"),sQuery(id+"FHMxAyK4CFUKdhS_1.wireOp",EDGE,"1cb9c079-ea9b-4899-8069-e0e3048e911d.sketch_text.stroke-3"),sQuery(id+"FHMxAyK4CFUKdhS_1.wireOp",EDGE,"1cb9c079-ea9b-4899-8069-e0e3048e911d.sketch_text.stroke-4"),sQuery(id+"FHMxAyK4CFUKdhS_1.wireOp",EDGE,"1cb9c079-ea9b-4899-8069-e0e3048e911d.sketch_text.stroke-5"),sQuery(id+"FHMxAyK4CFUKdhS_1.wireOp",EDGE,"1cb9c079-ea9b-4899-8069-e0e3048e911d.sketch_text.stroke-6"),sQuery(id+"FHMxAyK4CFUKdhS_1.wireOp",EDGE,"1cb9c079-ea9b-4899-8069-e0e3048e911d.sketch_text.stroke-7"),sQuery(id+"FHMxAyK4CFUKdhS_1.wireOp",EDGE,"1cb9c079-ea9b-4899-8069-e0e3048e911d.sketch_text.stroke-8"),sQuery(id+"FHMxAyK4CFUKdhS_1.wireOp",EDGE,"1cb9c079-ea9b-4899-8069-e0e3048e911d.sketch_text.stroke-9"),sQuery(id+"FHMxAyK4CFUKdhS_1.wireOp",EDGE,"1cb9c079-ea9b-4899-8069-e0e3048e911d.sketch_text.stroke-10"),sQuery(id+"FHMxAyK4CFUKdhS_1.wireOp",EDGE,"1cb9c079-ea9b-4899-8069-e0e3048e911d.sketch_text.stroke-11"),sQuery(id+"FHMxAyK4CFUKdhS_1.wireOp",EDGE,"1cb9c079-ea9b-4899-8069-e0e3048e911d.sketch_text.stroke-12"),sQuery(id+"FHMxAyK4CFUKdhS_1.wireOp",EDGE,"1cb9c079-ea9b-4899-8069-e0e3048e911d.sketch_text.stroke-13"),sQuery(id+"FHMxAyK4CFUKdhS_1.wireOp",EDGE,"1cb9c079-ea9b-4899-8069-e0e3048e911d.sketch_text.stroke-14"),sQuery(id+"FHMxAyK4CFUKdhS_1.wireOp",EDGE,"1cb9c079-ea9b-4899-8069-e0e3048e911d.sketch_text.stroke-15"),sQuery(id+"FHMxAyK4CFUKdhS_1.wireOp",EDGE,"1cb9c079-ea9b-4899-8069-e0e3048e911d.sketch_text.stroke-16"),sQuery(id+"FHMxAyK4CFUKdhS_1.wireOp",EDGE,"1cb9c079-ea9b-4899-8069-e0e3048e911d.sketch_text.stroke-17"),sQuery(id+"FHMxAyK4CFUKdhS_1.wireOp",EDGE,"1cb9c079-ea9b-4899-8069-e0e3048e911d.sketch_text.stroke-18"),sQuery(id+"FHMxAyK4CFUKdhS_1.wireOp",EDGE,"1cb9c079-ea9b-4899-8069-e0e3048e911d.sketch_text.stroke-19"),sQuery(id+"FHMxAyK4CFUKdhS_1.wireOp",EDGE,"1cb9c079-ea9b-4899-8069-e0e3048e911d.sketch_text.stroke-20"),sQuery(id+"FHMxAyK4CFUKdhS_1.wireOp",EDGE,"1cb9c079-ea9b-4899-8069-e0e3048e911d.sketch_text.stroke-21"),sQuery(id+"FHMxAyK4CFUKdhS_1.wireOp",EDGE,"1cb9c079-ea9b-4899-8069-e0e3048e911d.sketch_text.stroke-22"),sQuery(id+"FHMxAyK4CFUKdhS_1.wireOp",EDGE,"1cb9c079-ea9b-4899-8069-e0e3048e911d.sketch_text.stroke-23"),sQuery(id+"FHMxAyK4CFUKdhS_1.wireOp",EDGE,"1cb9c079-ea9b-4899-8069-e0e3048e911d.sketch_text.stroke-24"),sQuery(id+"FHMxAyK4CFUKdhS_1.wireOp",EDGE,"1cb9c079-ea9b-4899-8069-e0e3048e911d.sketch_text.stroke-25"),sQuery(id+"FHMxAyK4CFUKdhS_1.wireOp",EDGE,"1cb9c079-ea9b-4899-8069-e0e3048e911d.sketch_text.stroke-26"),sQuery(id+"FHMxAyK4CFUKdhS_1.wireOp",EDGE,"1cb9c079-ea9b-4899-8069-e0e3048e911d.sketch_text.stroke-27"),sQuery(id+"FHMxAyK4CFUKdhS_1.wireOp",EDGE,"1cb9c079-ea9b-4899-8069-e0e3048e911d.sketch_text.stroke-28"),sQuery(id+"FHMxAyK4CFUKdhS_1.wireOp",EDGE,"1cb9c079-ea9b-4899-8069-e0e3048e911d.sketch_text.stroke-29"),sQuery(id+"FHMxAyK4CFUKdhS_1.wireOp",EDGE,"1cb9c079-ea9b-4899-8069-e0e3048e911d.sketch_text.stroke-30"),sQuery(id+"FHMxAyK4CFUKdhS_1.wireOp",EDGE,"1cb9c079-ea9b-4899-8069-e0e3048e911d.sketch_text.stroke-31"),sQuery(id+"FHMxAyK4CFUKdhS_1.wireOp",EDGE,"1cb9c079-ea9b-4899-8069-e0e3048e911d.sketch_text.stroke-32"),sQuery(id+"FHMxAyK4CFUKdhS_1.wireOp",EDGE,"1cb9c079-ea9b-4899-8069-e0e3048e911d.sketch_text.stroke-33"),sQuery(id+"FHMxAyK4CFUKdhS_1.wireOp",EDGE,"1cb9c079-ea9b-4899-8069-e0e3048e911d.sketch_text.stroke-34"),sQuery(id+"FHMxAyK4CFUKdhS_1.wireOp",EDGE,"1cb9c079-ea9b-4899-8069-e0e3048e911d.sketch_text.stroke-35"),sQuery(id+"FHMxAyK4CFUKdhS_1.wireOp",EDGE,"1cb9c079-ea9b-4899-8069-e0e3048e911d.sketch_text.stroke-36"),sQuery(id+"FHMxAyK4CFUKdhS_1.wireOp",EDGE,"1cb9c079-ea9b-4899-8069-e0e3048e911d.sketch_text.stroke-37"),sQuery(id+"FHMxAyK4CFUKdhS_1.wireOp",EDGE,"1cb9c079-ea9b-4899-8069-e0e3048e911d.sketch_text.stroke-38"),sQuery(id+"FHMxAyK4CFUKdhS_1.wireOp",EDGE,"1cb9c079-ea9b-4899-8069-e0e3048e911d.sketch_text.stroke-39"),sQuery(id+"FHMxAyK4CFUKdhS_1.wireOp",EDGE,"1cb9c079-ea9b-4899-8069-e0e3048e911d.sketch_text.stroke-40"),sQuery(id+"FHMxAyK4CFUKdhS_1.wireOp",EDGE,"1cb9c079-ea9b-4899-8069-e0e3048e911d.sketch_text.stroke-41"),sQuery(id+"FHMxAyK4CFUKdhS_1.wireOp",EDGE,"1cb9c079-ea9b-4899-8069-e0e3048e911d.sketch_text.stroke-42"),sQuery(id+"FHMxAyK4CFUKdhS_1.wireOp",EDGE,"1cb9c079-ea9b-4899-8069-e0e3048e911d.sketch_text.stroke-43"),sQuery(id+"FHMxAyK4CFUKdhS_1.wireOp",EDGE,"1cb9c079-ea9b-4899-8069-e0e3048e911d.sketch_text.stroke-44"),sQuery(id+"FHMxAyK4CFUKdhS_1.wireOp",EDGE,"1cb9c079-ea9b-4899-8069-e0e3048e911d.sketch_text.stroke-45"),sQuery(id+"FHMxAyK4CFUKdhS_1.wireOp",EDGE,"1cb9c079-ea9b-4899-8069-e0e3048e911d.sketch_text.stroke-46"),sQuery(id+"FHMxAyK4CFUKdhS_1.wireOp",EDGE,"1cb9c079-ea9b-4899-8069-e0e3048e911d.sketch_text.stroke-47"),sQuery(id+"FHMxAyK4CFUKdhS_1.wireOp",EDGE,"1cb9c079-ea9b-4899-8069-e0e3048e911d.sketch_text.stroke-48"),sQuery(id+"FHMxAyK4CFUKdhS_1.wireOp",EDGE,"1cb9c079-ea9b-4899-8069-e0e3048e911d.sketch_text.stroke-49"),sQuery(id+"FHMxAyK4CFUKdhS_1.wireOp",EDGE,"1cb9c079-ea9b-4899-8069-e0e3048e911d.sketch_text.stroke-50"),sQuery(id+"FHMxAyK4CFUKdhS_1.wireOp",EDGE,"1cb9c079-ea9b-4899-8069-e0e3048e911d.sketch_text.stroke-51"),sQuery(id+"FHMxAyK4CFUKdhS_1.wireOp",EDGE,"1cb9c079-ea9b-4899-8069-e0e3048e911d.sketch_text.stroke-52"),sQuery(id+"FHMxAyK4CFUKdhS_1.wireOp",EDGE,"1cb9c079-ea9b-4899-8069-e0e3048e911d.sketch_text.stroke-53"),sQuery(id+"FHMxAyK4CFUKdhS_1.wireOp",EDGE,"1cb9c079-ea9b-4899-8069-e0e3048e911d.sketch_text.stroke-54"),sQuery(id+"FHMxAyK4CFUKdhS_1.wireOp",EDGE,"1cb9c079-ea9b-4899-8069-e0e3048e911d.sketch_text.stroke-55"),sQuery(id+"FHMxAyK4CFUKdhS_1.wireOp",EDGE,"1cb9c079-ea9b-4899-8069-e0e3048e911d.sketch_text.stroke-56"),sQuery(id+"FHMxAyK4CFUKdhS_1.wireOp",EDGE,"1cb9c079-ea9b-4899-8069-e0e3048e911d.sketch_text.stroke-57"),sQuery(id+"FHMxAyK4CFUKdhS_1.wireOp",EDGE,"1cb9c079-ea9b-4899-8069-e0e3048e911d.sketch_text.stroke-58"),sQuery(id+"FHMxAyK4CFUKdhS_1.wireOp",EDGE,"1cb9c079-ea9b-4899-8069-e0e3048e911d.sketch_text.stroke-59"),sQuery(id+"FHMxAyK4CFUKdhS_1.wireOp",EDGE,"1cb9c079-ea9b-4899-8069-e0e3048e911d.sketch_text.stroke-60"),sQuery(id+"FHMxAyK4CFUKdhS_1.wireOp",EDGE,"1cb9c079-ea9b-4899-8069-e0e3048e911d.sketch_text.stroke-61"),sQuery(id+"FHMxAyK4CFUKdhS_1.wireOp",EDGE,"1cb9c079-ea9b-4899-8069-e0e3048e911d.sketch_text.stroke-62"),sQuery(id+"FHMxAyK4CFUKdhS_1.wireOp",EDGE,"1cb9c079-ea9b-4899-8069-e0e3048e911d.sketch_text.stroke-71"),sQuery(id+"FHMxAyK4CFUKdhS_1.wireOp",EDGE,"1cb9c079-ea9b-4899-8069-e0e3048e911d.sketch_text.stroke-72"),sQuery(id+"FHMxAyK4CFUKdhS_1.wireOp",EDGE,"1cb9c079-ea9b-4899-8069-e0e3048e911d.sketch_text.stroke-73"),sQuery(id+"FHMxAyK4CFUKdhS_1.wireOp",EDGE,"1cb9c079-ea9b-4899-8069-e0e3048e911d.sketch_text.stroke-74"),sQuery(id+"FHMxAyK4CFUKdhS_1.wireOp",EDGE,"1cb9c079-ea9b-4899-8069-e0e3048e911d.sketch_text.stroke-75"),sQuery(id+"FHMxAyK4CFUKdhS_1.wireOp",EDGE,"1cb9c079-ea9b-4899-8069-e0e3048e911d.sketch_text.stroke-76"),sQuery(id+"FHMxAyK4CFUKdhS_1.wireOp",EDGE,"1cb9c079-ea9b-4899-8069-e0e3048e911d.sketch_text.stroke-77"),sQuery(id+"FHMxAyK4CFUKdhS_1.wireOp",EDGE,"1cb9c079-ea9b-4899-8069-e0e3048e911d.sketch_text.stroke-78"),sQuery(id+"FHMxAyK4CFUKdhS_1.wireOp",EDGE,"1cb9c079-ea9b-4899-8069-e0e3048e911d.sketch_text.stroke-79"),sQuery(id+"FHMxAyK4CFUKdhS_1.wireOp",EDGE,"1cb9c079-ea9b-4899-8069-e0e3048e911d.sketch_text.stroke-80"),sQuery(id+"FHMxAyK4CFUKdhS_1.wireOp",EDGE,"1cb9c079-ea9b-4899-8069-e0e3048e911d.sketch_text.stroke-81"),sQuery(id+"FHMxAyK4CFUKdhS_1.wireOp",EDGE,"1cb9c079-ea9b-4899-8069-e0e3048e911d.sketch_text.stroke-82"),sQuery(id+"FHMxAyK4CFUKdhS_1.wireOp",EDGE,"1cb9c079-ea9b-4899-8069-e0e3048e911d.sketch_text.stroke-83"),sQuery(id+"FHMxAyK4CFUKdhS_1.wireOp",EDGE,"1cb9c079-ea9b-4899-8069-e0e3048e911d.sketch_text.stroke-84"),sQuery(id+"FHMxAyK4CFUKdhS_1.wireOp",EDGE,"1cb9c079-ea9b-4899-8069-e0e3048e911d.sketch_text.stroke-85"),sQuery(id+"FHMxAyK4CFUKdhS_1.wireOp",EDGE,"1cb9c079-ea9b-4899-8069-e0e3048e911d.sketch_text.stroke-86"),sQuery(id+"FHMxAyK4CFUKdhS_1.wireOp",EDGE,"1cb9c079-ea9b-4899-8069-e0e3048e911d.sketch_text.stroke-87"),sQuery(id+"FHMxAyK4CFUKdhS_1.wireOp",EDGE,"1cb9c079-ea9b-4899-8069-e0e3048e911d.sketch_text.stroke-88"),sQuery(id+"FHMxAyK4CFUKdhS_1.wireOp",EDGE,"1cb9c079-ea9b-4899-8069-e0e3048e911d.sketch_text.stroke-89"),sQuery(id+"FHMxAyK4CFUKdhS_1.wireOp",EDGE,"1cb9c079-ea9b-4899-8069-e0e3048e911d.sketch_text.stroke-90"),sQuery(id+"FHMxAyK4CFUKdhS_1.wireOp",EDGE,"1cb9c079-ea9b-4899-8069-e0e3048e911d.sketch_text.stroke-91"),sQuery(id+"FHMxAyK4CFUKdhS_1.wireOp",EDGE,"1cb9c079-ea9b-4899-8069-e0e3048e911d.sketch_text.stroke-92"),sQuery(id+"FHMxAyK4CFUKdhS_1.wireOp",EDGE,"1cb9c079-ea9b-4899-8069-e0e3048e911d.sketch_text.stroke-93"),sQuery(id+"FHMxAyK4CFUKdhS_1.wireOp",EDGE,"1cb9c079-ea9b-4899-8069-e0e3048e911d.sketch_text.stroke-94"),sQuery(id+"FHMxAyK4CFUKdhS_1.wireOp",EDGE,"1cb9c079-ea9b-4899-8069-e0e3048e911d.sketch_text.stroke-95"),sQuery(id+"FHMxAyK4CFUKdhS_1.wireOp",EDGE,"1cb9c079-ea9b-4899-8069-e0e3048e911d.sketch_text.stroke-96"),sQuery(id+"FHMxAyK4CFUKdhS_1.wireOp",EDGE,"1cb9c079-ea9b-4899-8069-e0e3048e911d.sketch_text.stroke-97"),sQuery(id+"FHMxAyK4CFUKdhS_1.wireOp",EDGE,"1cb9c079-ea9b-4899-8069-e0e3048e911d.sketch_text.stroke-103"),sQuery(id+"FHMxAyK4CFUKdhS_1.wireOp",EDGE,"1cb9c079-ea9b-4899-8069-e0e3048e911d.sketch_text.stroke-104"),sQuery(id+"FHMxAyK4CFUKdhS_1.wireOp",EDGE,"1cb9c079-ea9b-4899-8069-e0e3048e911d.sketch_text.stroke-105"),sQuery(id+"FHMxAyK4CFUKdhS_1.wireOp",EDGE,"1cb9c079-ea9b-4899-8069-e0e3048e911d.sketch_text.stroke-106"),sQuery(id+"FHMxAyK4CFUKdhS_1.wireOp",EDGE,"1cb9c079-ea9b-4899-8069-e0e3048e911d.sketch_text.stroke-107"),sQuery(id+"FHMxAyK4CFUKdhS_1.wireOp",EDGE,"1cb9c079-ea9b-4899-8069-e0e3048e911d.sketch_text.stroke-108"),sQuery(id+"FHMxAyK4CFUKdhS_1.wireOp",EDGE,"1cb9c079-ea9b-4899-8069-e0e3048e911d.sketch_text.stroke-109"),sQuery(id+"FHMxAyK4CFUKdhS_1.wireOp",EDGE,"1cb9c079-ea9b-4899-8069-e0e3048e911d.sketch_text.stroke-110"),sQuery(id+"FHMxAyK4CFUKdhS_1.wireOp",EDGE,"1cb9c079-ea9b-4899-8069-e0e3048e911d.sketch_text.stroke-111"),sQuery(id+"FHMxAyK4CFUKdhS_1.wireOp",EDGE,"1cb9c079-ea9b-4899-8069-e0e3048e911d.sketch_text.stroke-112"),sQuery(id+"FHMxAyK4CFUKdhS_1.wireOp",EDGE,"1cb9c079-ea9b-4899-8069-e0e3048e911d.sketch_text.stroke-113"),sQuery(id+"FHMxAyK4CFUKdhS_1.wireOp",EDGE,"1cb9c079-ea9b-4899-8069-e0e3048e911d.sketch_text.stroke-114"),sQuery(id+"FHMxAyK4CFUKdhS_1.wireOp",EDGE,"1cb9c079-ea9b-4899-8069-e0e3048e911d.sketch_text.stroke-115"),sQuery(id+"FHMxAyK4CFUKdhS_1.wireOp",EDGE,"1cb9c079-ea9b-4899-8069-e0e3048e911d.sketch_text.stroke-116"),sQuery(id+"FHMxAyK4CFUKdhS_1.wireOp",EDGE,"1cb9c079-ea9b-4899-8069-e0e3048e911d.sketch_text.stroke-117"),sQuery(id+"FHMxAyK4CFUKdhS_1.wireOp",EDGE,"1cb9c079-ea9b-4899-8069-e0e3048e911d.sketch_text.stroke-118"),sQuery(id+"FHMxAyK4CFUKdhS_1.wireOp",EDGE,"1cb9c079-ea9b-4899-8069-e0e3048e911d.sketch_text.stroke-119"),sQuery(id+"FHMxAyK4CFUKdhS_1.wireOp",EDGE,"1cb9c079-ea9b-4899-8069-e0e3048e911d.sketch_text.stroke-120"),sQuery(id+"FHMxAyK4CFUKdhS_1.wireOp",EDGE,"1cb9c079-ea9b-4899-8069-e0e3048e911d.sketch_text.stroke-121"),sQuery(id+"FHMxAyK4CFUKdhS_1.wireOp",EDGE,"1cb9c079-ea9b-4899-8069-e0e3048e911d.sketch_text.stroke-122"),sQuery(id+"FHMxAyK4CFUKdhS_1.wireOp",EDGE,"1cb9c079-ea9b-4899-8069-e0e3048e911d.sketch_text.stroke-123"),sQuery(id+"FHMxAyK4CFUKdhS_1.wireOp",EDGE,"1cb9c079-ea9b-4899-8069-e0e3048e911d.sketch_text.stroke-124"),sQuery(id+"FHMxAyK4CFUKdhS_1.wireOp",EDGE,"1cb9c079-ea9b-4899-8069-e0e3048e911d.sketch_text.stroke-125"),sQuery(id+"FHMxAyK4CFUKdhS_1.wireOp",EDGE,"1cb9c079-ea9b-4899-8069-e0e3048e911d.sketch_text.stroke-126"),sQuery(id+"FHMxAyK4CFUKdhS_1.wireOp",EDGE,"1cb9c079-ea9b-4899-8069-e0e3048e911d.sketch_text.stroke-127"),sQuery(id+"FHMxAyK4CFUKdhS_1.wireOp",EDGE,"1cb9c079-ea9b-4899-8069-e0e3048e911d.sketch_text.stroke-128"),sQuery(id+"FHMxAyK4CFUKdhS_1.wireOp",EDGE,"1cb9c079-ea9b-4899-8069-e0e3048e911d.sketch_text.stroke-129"),sQuery(id+"FHMxAyK4CFUKdhS_1.wireOp",EDGE,"1cb9c079-ea9b-4899-8069-e0e3048e911d.sketch_text.stroke-130"),sQuery(id+"FHMxAyK4CFUKdhS_1.wireOp",EDGE,"1cb9c079-ea9b-4899-8069-e0e3048e911d.sketch_text.stroke-131"),sQuery(id+"FHMxAyK4CFUKdhS_1.wireOp",EDGE,"1cb9c079-ea9b-4899-8069-e0e3048e911d.sketch_text.stroke-132"),sQuery(id+"FHMxAyK4CFUKdhS_1.wireOp",EDGE,"1cb9c079-ea9b-4899-8069-e0e3048e911d.sketch_text.stroke-133"),sQuery(id+"FHMxAyK4CFUKdhS_1.wireOp",EDGE,"1cb9c079-ea9b-4899-8069-e0e3048e911d.sketch_text.stroke-134"),sQuery(id+"FHMxAyK4CFUKdhS_1.wireOp",EDGE,"1cb9c079-ea9b-4899-8069-e0e3048e911d.sketch_text.stroke-135"),sQuery(id+"FHMxAyK4CFUKdhS_1.wireOp",EDGE,"1cb9c079-ea9b-4899-8069-e0e3048e911d.sketch_text.stroke-136"),sQuery(id+"FHMxAyK4CFUKdhS_1.wireOp",EDGE,"1cb9c079-ea9b-4899-8069-e0e3048e911d.sketch_text.stroke-137"),sQuery(id+"FHMxAyK4CFUKdhS_1.wireOp",EDGE,"1cb9c079-ea9b-4899-8069-e0e3048e911d.sketch_text.stroke-138"),sQuery(id+"FHMxAyK4CFUKdhS_1.wireOp",EDGE,"1cb9c079-ea9b-4899-8069-e0e3048e911d.sketch_text.stroke-139"),sQuery(id+"FHMxAyK4CFUKdhS_1.wireOp",EDGE,"1cb9c079-ea9b-4899-8069-e0e3048e911d.sketch_text.stroke-140"),sQuery(id+"FHMxAyK4CFUKdhS_1.wireOp",EDGE,"1cb9c079-ea9b-4899-8069-e0e3048e911d.sketch_text.stroke-141"),sQuery(id+"FHMxAyK4CFUKdhS_1.wireOp",EDGE,"1cb9c079-ea9b-4899-8069-e0e3048e911d.sketch_text.stroke-142"),sQuery(id+"FHMxAyK4CFUKdhS_1.wireOp",EDGE,"1cb9c079-ea9b-4899-8069-e0e3048e911d.sketch_text.stroke-143"),sQuery(id+"FHMxAyK4CFUKdhS_1.wireOp",EDGE,"1cb9c079-ea9b-4899-8069-e0e3048e911d.sketch_text.stroke-144"),sQuery(id+"FHMxAyK4CFUKdhS_1.wireOp",EDGE,"1cb9c079-ea9b-4899-8069-e0e3048e911d.sketch_text.stroke-145"),sQuery(id+"FHMxAyK4CFUKdhS_1.wireOp",EDGE,"1cb9c079-ea9b-4899-8069-e0e3048e911d.sketch_text.stroke-146"),sQuery(id+"FHMxAyK4CFUKdhS_1.wireOp",EDGE,"1cb9c079-ea9b-4899-8069-e0e3048e911d.sketch_text.stroke-147"),sQuery(id+"FHMxAyK4CFUKdhS_1.wireOp",EDGE,"1cb9c079-ea9b-4899-8069-e0e3048e911d.sketch_text.stroke-148"),sQuery(id+"FHMxAyK4CFUKdhS_1.wireOp",EDGE,"1cb9c079-ea9b-4899-8069-e0e3048e911d.sketch_text.stroke-149"),sQuery(id+"FHMxAyK4CFUKdhS_1.wireOp",EDGE,"1cb9c079-ea9b-4899-8069-e0e3048e911d.sketch_text.stroke-150"),sQuery(id+"FHMxAyK4CFUKdhS_1.wireOp",EDGE,"1cb9c079-ea9b-4899-8069-e0e3048e911d.sketch_text.stroke-151"),sQuery(id+"FHMxAyK4CFUKdhS_1.wireOp",EDGE,"1cb9c079-ea9b-4899-8069-e0e3048e911d.sketch_text.stroke-152"),sQuery(id+"FHMxAyK4CFUKdhS_1.wireOp",EDGE,"1cb9c079-ea9b-4899-8069-e0e3048e911d.sketch_text.stroke-153"),sQuery(id+"FHMxAyK4CFUKdhS_1.wireOp",EDGE,"1cb9c079-ea9b-4899-8069-e0e3048e911d.sketch_text.stroke-159"),sQuery(id+"FHMxAyK4CFUKdhS_1.wireOp",EDGE,"1cb9c079-ea9b-4899-8069-e0e3048e911d.sketch_text.stroke-160"),sQuery(id+"FHMxAyK4CFUKdhS_1.wireOp",EDGE,"1cb9c079-ea9b-4899-8069-e0e3048e911d.sketch_text.stroke-161"),sQuery(id+"FHMxAyK4CFUKdhS_1.wireOp",EDGE,"1cb9c079-ea9b-4899-8069-e0e3048e911d.sketch_text.stroke-162"),sQuery(id+"FHMxAyK4CFUKdhS_1.wireOp",EDGE,"1cb9c079-ea9b-4899-8069-e0e3048e911d.sketch_text.stroke-163"),sQuery(id+"FHMxAyK4CFUKdhS_1.wireOp",EDGE,"1cb9c079-ea9b-4899-8069-e0e3048e911d.sketch_text.stroke-164"),sQuery(id+"FHMxAyK4CFUKdhS_1.wireOp",EDGE,"1cb9c079-ea9b-4899-8069-e0e3048e911d.sketch_text.stroke-165"),sQuery(id+"FHMxAyK4CFUKdhS_1.wireOp",EDGE,"1cb9c079-ea9b-4899-8069-e0e3048e911d.sketch_text.stroke-166"),sQuery(id+"FHMxAyK4CFUKdhS_1.wireOp",EDGE,"1cb9c079-ea9b-4899-8069-e0e3048e911d.sketch_text.stroke-167"),sQuery(id+"FHMxAyK4CFUKdhS_1.wireOp",EDGE,"1cb9c079-ea9b-4899-8069-e0e3048e911d.sketch_text.stroke-168"),sQuery(id+"FHMxAyK4CFUKdhS_1.wireOp",EDGE,"1cb9c079-ea9b-4899-8069-e0e3048e911d.sketch_text.stroke-169"),sQuery(id+"FHMxAyK4CFUKdhS_1.wireOp",EDGE,"1cb9c079-ea9b-4899-8069-e0e3048e911d.sketch_text.stroke-170"),sQuery(id+"FHMxAyK4CFUKdhS_1.wireOp",EDGE,"1cb9c079-ea9b-4899-8069-e0e3048e911d.sketch_text.stroke-171"),sQuery(id+"FHMxAyK4CFUKdhS_1.wireOp",EDGE,"1cb9c079-ea9b-4899-8069-e0e3048e911d.sketch_text.stroke-172"),sQuery(id+"FHMxAyK4CFUKdhS_1.wireOp",EDGE,"1cb9c079-ea9b-4899-8069-e0e3048e911d.sketch_text.stroke-173"),sQuery(id+"FHMxAyK4CFUKdhS_1.wireOp",EDGE,"1cb9c079-ea9b-4899-8069-e0e3048e911d.sketch_text.stroke-174"),sQuery(id+"FHMxAyK4CFUKdhS_1.wireOp",EDGE,"1cb9c079-ea9b-4899-8069-e0e3048e911d.sketch_text.stroke-175"),sQuery(id+"FHMxAyK4CFUKdhS_1.wireOp",EDGE,"1cb9c079-ea9b-4899-8069-e0e3048e911d.sketch_text.stroke-176"),sQuery(id+"FHMxAyK4CFUKdhS_1.wireOp",EDGE,"1cb9c079-ea9b-4899-8069-e0e3048e911d.sketch_text.stroke-177"),sQuery(id+"FHMxAyK4CFUKdhS_1.wireOp",EDGE,"1cb9c079-ea9b-4899-8069-e0e3048e911d.sketch_text.stroke-178"),sQuery(id+"FHMxAyK4CFUKdhS_1.wireOp",EDGE,"1cb9c079-ea9b-4899-8069-e0e3048e911d.sketch_text.stroke-179"),sQuery(id+"FHMxAyK4CFUKdhS_1.wireOp",EDGE,"1cb9c079-ea9b-4899-8069-e0e3048e911d.sketch_text.stroke-180"),sQuery(id+"F2.wireOp",EDGE,"8007402e-1a4e-4a06-85a5-2af08e553504"),subQ2])],"isStart":true}),makeQuery(id+"F3.opExtrude","SWEPT_FACE",FACE,{"disambiguationData":[OSD([subQ2])]})])],"derivedFrom":makeQuery(id+"F3.opExtrude","CAP_EDGE",EDGE,{"disambiguationData":[OSD([subQ2])],"isStart":true})});}
            var Q8;
            Q8=makeQuery(id+"F1.opExtrude","CAP_EDGE",EDGE,{"disambiguationData":[OSD([sQuery(id+"F0.wireOp",EDGE,"E0.right")])],"isStart":false});
            var Q9;
            {var subQ0=sQuery(id+"F0.wireOp",EDGE,"E0.top");var subQ1=sQuery(id+"F0.wireOp",EDGE,"E0.bottom");var subQ2=sQuery(id+"F2.wireOp",EDGE,"6ee83ff3-586e-4dbe-aaea-af71240543bd");Q9=makeQuery(id+"F3.boolean.opBoolean","SPLIT",EDGE,{"disambiguationData":[TD([makeQuery(id+"F1.opExtrude","CAP_FACE",FACE,{"disambiguationData":[OSD([subQ1,subQ0,sQuery(id+"F0.wireOp",EDGE,"E0.left"),sQuery(id+"F0.wireOp",EDGE,"E0.right")])],"isStart":false}),makeQuery(id+"F1.opExtrude","SWEPT_FACE",FACE,{"disambiguationData":[OSD([subQ0])]}),makeQuery(id+"F3.opExtrude","CAP_FACE",FACE,{"disambiguationData":[OSD([subQ1,sQuery(id+"FQ5JFwxVdaqARUP_1.wireOp",EDGE,"fcba4419-a2ee-464f-be9d-58f11bf3418b.sketch_text.stroke-0"),sQuery(id+"FQ5JFwxVdaqARUP_1.wireOp",EDGE,"fcba4419-a2ee-464f-be9d-58f11bf3418b.sketch_text.stroke-1"),sQuery(id+"FQ5JFwxVdaqARUP_1.wireOp",EDGE,"fcba4419-a2ee-464f-be9d-58f11bf3418b.sketch_text.stroke-2"),sQuery(id+"FQ5JFwxVdaqARUP_1.wireOp",EDGE,"fcba4419-a2ee-464f-be9d-58f11bf3418b.sketch_text.stroke-3"),sQuery(id+"FQ5JFwxVdaqARUP_1.wireOp",EDGE,"fcba4419-a2ee-464f-be9d-58f11bf3418b.sketch_text.stroke-4"),sQuery(id+"FQ5JFwxVdaqARUP_1.wireOp",EDGE,"fcba4419-a2ee-464f-be9d-58f11bf3418b.sketch_text.stroke-5"),sQuery(id+"FQ5JFwxVdaqARUP_1.wireOp",EDGE,"fcba4419-a2ee-464f-be9d-58f11bf3418b.sketch_text.stroke-6"),sQuery(id+"FQ5JFwxVdaqARUP_1.wireOp",EDGE,"fcba4419-a2ee-464f-be9d-58f11bf3418b.sketch_text.stroke-7"),sQuery(id+"FQ5JFwxVdaqARUP_1.wireOp",EDGE,"fcba4419-a2ee-464f-be9d-58f11bf3418b.sketch_text.stroke-8"),sQuery(id+"FQ5JFwxVdaqARUP_1.wireOp",EDGE,"fcba4419-a2ee-464f-be9d-58f11bf3418b.sketch_text.stroke-9"),sQuery(id+"FQ5JFwxVdaqARUP_1.wireOp",EDGE,"fcba4419-a2ee-464f-be9d-58f11bf3418b.sketch_text.stroke-10"),sQuery(id+"FQ5JFwxVdaqARUP_1.wireOp",EDGE,"fcba4419-a2ee-464f-be9d-58f11bf3418b.sketch_text.stroke-11"),sQuery(id+"FQ5JFwxVdaqARUP_1.wireOp",EDGE,"fcba4419-a2ee-464f-be9d-58f11bf3418b.sketch_text.stroke-12"),sQuery(id+"FQ5JFwxVdaqARUP_1.wireOp",EDGE,"fcba4419-a2ee-464f-be9d-58f11bf3418b.sketch_text.stroke-13"),sQuery(id+"FQ5JFwxVdaqARUP_1.wireOp",EDGE,"fcba4419-a2ee-464f-be9d-58f11bf3418b.sketch_text.stroke-14"),sQuery(id+"FQ5JFwxVdaqARUP_1.wireOp",EDGE,"fcba4419-a2ee-464f-be9d-58f11bf3418b.sketch_text.stroke-15"),sQuery(id+"FQ5JFwxVdaqARUP_1.wireOp",EDGE,"fcba4419-a2ee-464f-be9d-58f11bf3418b.sketch_text.stroke-16"),sQuery(id+"FQ5JFwxVdaqARUP_1.wireOp",EDGE,"fcba4419-a2ee-464f-be9d-58f11bf3418b.sketch_text.stroke-17"),sQuery(id+"FQ5JFwxVdaqARUP_1.wireOp",EDGE,"fcba4419-a2ee-464f-be9d-58f11bf3418b.sketch_text.stroke-18"),sQuery(id+"FQ5JFwxVdaqARUP_1.wireOp",EDGE,"fcba4419-a2ee-464f-be9d-58f11bf3418b.sketch_text.stroke-19"),sQuery(id+"FQ5JFwxVdaqARUP_1.wireOp",EDGE,"fcba4419-a2ee-464f-be9d-58f11bf3418b.sketch_text.stroke-20"),sQuery(id+"FQ5JFwxVdaqARUP_1.wireOp",EDGE,"fcba4419-a2ee-464f-be9d-58f11bf3418b.sketch_text.stroke-21"),sQuery(id+"FQ5JFwxVdaqARUP_1.wireOp",EDGE,"fcba4419-a2ee-464f-be9d-58f11bf3418b.sketch_text.stroke-22"),sQuery(id+"FQ5JFwxVdaqARUP_1.wireOp",EDGE,"fcba4419-a2ee-464f-be9d-58f11bf3418b.sketch_text.stroke-23"),sQuery(id+"FQ5JFwxVdaqARUP_1.wireOp",EDGE,"fcba4419-a2ee-464f-be9d-58f11bf3418b.sketch_text.stroke-24"),sQuery(id+"FQ5JFwxVdaqARUP_1.wireOp",EDGE,"fcba4419-a2ee-464f-be9d-58f11bf3418b.sketch_text.stroke-25"),sQuery(id+"FQ5JFwxVdaqARUP_1.wireOp",EDGE,"fcba4419-a2ee-464f-be9d-58f11bf3418b.sketch_text.stroke-26"),sQuery(id+"FQ5JFwxVdaqARUP_1.wireOp",EDGE,"fcba4419-a2ee-464f-be9d-58f11bf3418b.sketch_text.stroke-27"),sQuery(id+"FQ5JFwxVdaqARUP_1.wireOp",EDGE,"fcba4419-a2ee-464f-be9d-58f11bf3418b.sketch_text.stroke-28"),sQuery(id+"FQ5JFwxVdaqARUP_1.wireOp",EDGE,"fcba4419-a2ee-464f-be9d-58f11bf3418b.sketch_text.stroke-29"),sQuery(id+"FQ5JFwxVdaqARUP_1.wireOp",EDGE,"fcba4419-a2ee-464f-be9d-58f11bf3418b.sketch_text.stroke-30"),sQuery(id+"FQ5JFwxVdaqARUP_1.wireOp",EDGE,"fcba4419-a2ee-464f-be9d-58f11bf3418b.sketch_text.stroke-31"),sQuery(id+"FQ5JFwxVdaqARUP_1.wireOp",EDGE,"fcba4419-a2ee-464f-be9d-58f11bf3418b.sketch_text.stroke-32"),sQuery(id+"FQ5JFwxVdaqARUP_1.wireOp",EDGE,"fcba4419-a2ee-464f-be9d-58f11bf3418b.sketch_text.stroke-33"),sQuery(id+"FQ5JFwxVdaqARUP_1.wireOp",EDGE,"fcba4419-a2ee-464f-be9d-58f11bf3418b.sketch_text.stroke-34"),sQuery(id+"FQ5JFwxVdaqARUP_1.wireOp",EDGE,"fcba4419-a2ee-464f-be9d-58f11bf3418b.sketch_text.stroke-35"),sQuery(id+"FQ5JFwxVdaqARUP_1.wireOp",EDGE,"fcba4419-a2ee-464f-be9d-58f11bf3418b.sketch_text.stroke-36"),sQuery(id+"FQ5JFwxVdaqARUP_1.wireOp",EDGE,"fcba4419-a2ee-464f-be9d-58f11bf3418b.sketch_text.stroke-37"),sQuery(id+"FQ5JFwxVdaqARUP_1.wireOp",EDGE,"fcba4419-a2ee-464f-be9d-58f11bf3418b.sketch_text.stroke-38"),sQuery(id+"FQ5JFwxVdaqARUP_1.wireOp",EDGE,"fcba4419-a2ee-464f-be9d-58f11bf3418b.sketch_text.stroke-39"),sQuery(id+"FQ5JFwxVdaqARUP_1.wireOp",EDGE,"fcba4419-a2ee-464f-be9d-58f11bf3418b.sketch_text.stroke-40"),sQuery(id+"FQ5JFwxVdaqARUP_1.wireOp",EDGE,"fcba4419-a2ee-464f-be9d-58f11bf3418b.sketch_text.stroke-41"),sQuery(id+"FQ5JFwxVdaqARUP_1.wireOp",EDGE,"fcba4419-a2ee-464f-be9d-58f11bf3418b.sketch_text.stroke-42"),sQuery(id+"FQ5JFwxVdaqARUP_1.wireOp",EDGE,"fcba4419-a2ee-464f-be9d-58f11bf3418b.sketch_text.stroke-43"),sQuery(id+"FQ5JFwxVdaqARUP_1.wireOp",EDGE,"fcba4419-a2ee-464f-be9d-58f11bf3418b.sketch_text.stroke-44"),sQuery(id+"FQ5JFwxVdaqARUP_1.wireOp",EDGE,"fcba4419-a2ee-464f-be9d-58f11bf3418b.sketch_text.stroke-45"),sQuery(id+"FQ5JFwxVdaqARUP_1.wireOp",EDGE,"fcba4419-a2ee-464f-be9d-58f11bf3418b.sketch_text.stroke-46"),sQuery(id+"FQ5JFwxVdaqARUP_1.wireOp",EDGE,"fcba4419-a2ee-464f-be9d-58f11bf3418b.sketch_text.stroke-47"),sQuery(id+"FQ5JFwxVdaqARUP_1.wireOp",EDGE,"fcba4419-a2ee-464f-be9d-58f11bf3418b.sketch_text.stroke-48"),sQuery(id+"FQ5JFwxVdaqARUP_1.wireOp",EDGE,"fcba4419-a2ee-464f-be9d-58f11bf3418b.sketch_text.stroke-49"),sQuery(id+"FQ5JFwxVdaqARUP_1.wireOp",EDGE,"fcba4419-a2ee-464f-be9d-58f11bf3418b.sketch_text.stroke-50"),sQuery(id+"FQ5JFwxVdaqARUP_1.wireOp",EDGE,"fcba4419-a2ee-464f-be9d-58f11bf3418b.sketch_text.stroke-51"),sQuery(id+"FQ5JFwxVdaqARUP_1.wireOp",EDGE,"fcba4419-a2ee-464f-be9d-58f11bf3418b.sketch_text.stroke-52"),sQuery(id+"FQ5JFwxVdaqARUP_1.wireOp",EDGE,"fcba4419-a2ee-464f-be9d-58f11bf3418b.sketch_text.stroke-53"),sQuery(id+"FQ5JFwxVdaqARUP_1.wireOp",EDGE,"fcba4419-a2ee-464f-be9d-58f11bf3418b.sketch_text.stroke-54"),sQuery(id+"FQ5JFwxVdaqARUP_1.wireOp",EDGE,"fcba4419-a2ee-464f-be9d-58f11bf3418b.sketch_text.stroke-55"),sQuery(id+"FQ5JFwxVdaqARUP_1.wireOp",EDGE,"fcba4419-a2ee-464f-be9d-58f11bf3418b.sketch_text.stroke-56"),sQuery(id+"FQ5JFwxVdaqARUP_1.wireOp",EDGE,"fcba4419-a2ee-464f-be9d-58f11bf3418b.sketch_text.stroke-57"),sQuery(id+"FQ5JFwxVdaqARUP_1.wireOp",EDGE,"fcba4419-a2ee-464f-be9d-58f11bf3418b.sketch_text.stroke-58"),sQuery(id+"FQ5JFwxVdaqARUP_1.wireOp",EDGE,"fcba4419-a2ee-464f-be9d-58f11bf3418b.sketch_text.stroke-59"),sQuery(id+"FQ5JFwxVdaqARUP_1.wireOp",EDGE,"fcba4419-a2ee-464f-be9d-58f11bf3418b.sketch_text.stroke-60"),sQuery(id+"FQ5JFwxVdaqARUP_1.wireOp",EDGE,"fcba4419-a2ee-464f-be9d-58f11bf3418b.sketch_text.stroke-61"),sQuery(id+"FQ5JFwxVdaqARUP_1.wireOp",EDGE,"fcba4419-a2ee-464f-be9d-58f11bf3418b.sketch_text.stroke-62"),sQuery(id+"FQ5JFwxVdaqARUP_1.wireOp",EDGE,"fcba4419-a2ee-464f-be9d-58f11bf3418b.sketch_text.stroke-63"),sQuery(id+"FQ5JFwxVdaqARUP_1.wireOp",EDGE,"fcba4419-a2ee-464f-be9d-58f11bf3418b.sketch_text.stroke-64"),sQuery(id+"FQ5JFwxVdaqARUP_1.wireOp",EDGE,"fcba4419-a2ee-464f-be9d-58f11bf3418b.sketch_text.stroke-65"),sQuery(id+"FQ5JFwxVdaqARUP_1.wireOp",EDGE,"fcba4419-a2ee-464f-be9d-58f11bf3418b.sketch_text.stroke-66"),sQuery(id+"FQ5JFwxVdaqARUP_1.wireOp",EDGE,"fcba4419-a2ee-464f-be9d-58f11bf3418b.sketch_text.stroke-67"),sQuery(id+"FQ5JFwxVdaqARUP_1.wireOp",EDGE,"fcba4419-a2ee-464f-be9d-58f11bf3418b.sketch_text.stroke-68"),sQuery(id+"FQ5JFwxVdaqARUP_1.wireOp",EDGE,"fcba4419-a2ee-464f-be9d-58f11bf3418b.sketch_text.stroke-69"),sQuery(id+"FQ5JFwxVdaqARUP_1.wireOp",EDGE,"fcba4419-a2ee-464f-be9d-58f11bf3418b.sketch_text.stroke-70"),sQuery(id+"FQ5JFwxVdaqARUP_1.wireOp",EDGE,"fcba4419-a2ee-464f-be9d-58f11bf3418b.sketch_text.stroke-71"),sQuery(id+"FQ5JFwxVdaqARUP_1.wireOp",EDGE,"fcba4419-a2ee-464f-be9d-58f11bf3418b.sketch_text.stroke-72"),sQuery(id+"FQ5JFwxVdaqARUP_1.wireOp",EDGE,"fcba4419-a2ee-464f-be9d-58f11bf3418b.sketch_text.stroke-73"),sQuery(id+"FQ5JFwxVdaqARUP_1.wireOp",EDGE,"fcba4419-a2ee-464f-be9d-58f11bf3418b.sketch_text.stroke-74"),sQuery(id+"FQ5JFwxVdaqARUP_1.wireOp",EDGE,"fcba4419-a2ee-464f-be9d-58f11bf3418b.sketch_text.stroke-75"),sQuery(id+"FQ5JFwxVdaqARUP_1.wireOp",EDGE,"fcba4419-a2ee-464f-be9d-58f11bf3418b.sketch_text.stroke-76"),sQuery(id+"FQ5JFwxVdaqARUP_1.wireOp",EDGE,"fcba4419-a2ee-464f-be9d-58f11bf3418b.sketch_text.stroke-77"),sQuery(id+"FQ5JFwxVdaqARUP_1.wireOp",EDGE,"fcba4419-a2ee-464f-be9d-58f11bf3418b.sketch_text.stroke-78"),sQuery(id+"FQ5JFwxVdaqARUP_1.wireOp",EDGE,"fcba4419-a2ee-464f-be9d-58f11bf3418b.sketch_text.stroke-79"),sQuery(id+"FQ5JFwxVdaqARUP_1.wireOp",EDGE,"fcba4419-a2ee-464f-be9d-58f11bf3418b.sketch_text.stroke-80"),sQuery(id+"FQ5JFwxVdaqARUP_1.wireOp",EDGE,"fcba4419-a2ee-464f-be9d-58f11bf3418b.sketch_text.stroke-81"),sQuery(id+"FQ5JFwxVdaqARUP_1.wireOp",EDGE,"fcba4419-a2ee-464f-be9d-58f11bf3418b.sketch_text.stroke-82"),sQuery(id+"FQ5JFwxVdaqARUP_1.wireOp",EDGE,"fcba4419-a2ee-464f-be9d-58f11bf3418b.sketch_text.stroke-83"),sQuery(id+"FQ5JFwxVdaqARUP_1.wireOp",EDGE,"fcba4419-a2ee-464f-be9d-58f11bf3418b.sketch_text.stroke-84"),sQuery(id+"FQ5JFwxVdaqARUP_1.wireOp",EDGE,"fcba4419-a2ee-464f-be9d-58f11bf3418b.sketch_text.stroke-85"),sQuery(id+"FQ5JFwxVdaqARUP_1.wireOp",EDGE,"fcba4419-a2ee-464f-be9d-58f11bf3418b.sketch_text.stroke-86"),sQuery(id+"FQ5JFwxVdaqARUP_1.wireOp",EDGE,"fcba4419-a2ee-464f-be9d-58f11bf3418b.sketch_text.stroke-87"),sQuery(id+"FQ5JFwxVdaqARUP_1.wireOp",EDGE,"fcba4419-a2ee-464f-be9d-58f11bf3418b.sketch_text.stroke-88"),sQuery(id+"FQ5JFwxVdaqARUP_1.wireOp",EDGE,"fcba4419-a2ee-464f-be9d-58f11bf3418b.sketch_text.stroke-89"),sQuery(id+"FQ5JFwxVdaqARUP_1.wireOp",EDGE,"fcba4419-a2ee-464f-be9d-58f11bf3418b.sketch_text.stroke-90"),sQuery(id+"FQ5JFwxVdaqARUP_1.wireOp",EDGE,"fcba4419-a2ee-464f-be9d-58f11bf3418b.sketch_text.stroke-91"),sQuery(id+"FQ5JFwxVdaqARUP_1.wireOp",EDGE,"fcba4419-a2ee-464f-be9d-58f11bf3418b.sketch_text.stroke-92"),sQuery(id+"FQ5JFwxVdaqARUP_1.wireOp",EDGE,"fcba4419-a2ee-464f-be9d-58f11bf3418b.sketch_text.stroke-93"),sQuery(id+"FQ5JFwxVdaqARUP_1.wireOp",EDGE,"fcba4419-a2ee-464f-be9d-58f11bf3418b.sketch_text.stroke-94"),sQuery(id+"FQ5JFwxVdaqARUP_1.wireOp",EDGE,"fcba4419-a2ee-464f-be9d-58f11bf3418b.sketch_text.stroke-95"),sQuery(id+"FQ5JFwxVdaqARUP_1.wireOp",EDGE,"fcba4419-a2ee-464f-be9d-58f11bf3418b.sketch_text.stroke-96"),sQuery(id+"FQ5JFwxVdaqARUP_1.wireOp",EDGE,"fcba4419-a2ee-464f-be9d-58f11bf3418b.sketch_text.stroke-97"),sQuery(id+"FQ5JFwxVdaqARUP_1.wireOp",EDGE,"fcba4419-a2ee-464f-be9d-58f11bf3418b.sketch_text.stroke-98"),sQuery(id+"FQ5JFwxVdaqARUP_1.wireOp",EDGE,"fcba4419-a2ee-464f-be9d-58f11bf3418b.sketch_text.stroke-99"),sQuery(id+"FQ5JFwxVdaqARUP_1.wireOp",EDGE,"fcba4419-a2ee-464f-be9d-58f11bf3418b.sketch_text.stroke-100"),sQuery(id+"FQ5JFwxVdaqARUP_1.wireOp",EDGE,"fcba4419-a2ee-464f-be9d-58f11bf3418b.sketch_text.stroke-101"),sQuery(id+"FQ5JFwxVdaqARUP_1.wireOp",EDGE,"fcba4419-a2ee-464f-be9d-58f11bf3418b.sketch_text.stroke-102"),sQuery(id+"FQ5JFwxVdaqARUP_1.wireOp",EDGE,"fcba4419-a2ee-464f-be9d-58f11bf3418b.sketch_text.stroke-103"),sQuery(id+"FQ5JFwxVdaqARUP_1.wireOp",EDGE,"fcba4419-a2ee-464f-be9d-58f11bf3418b.sketch_text.stroke-104"),sQuery(id+"FQ5JFwxVdaqARUP_1.wireOp",EDGE,"fcba4419-a2ee-464f-be9d-58f11bf3418b.sketch_text.stroke-105"),sQuery(id+"FQ5JFwxVdaqARUP_1.wireOp",EDGE,"fcba4419-a2ee-464f-be9d-58f11bf3418b.sketch_text.stroke-106"),sQuery(id+"FQ5JFwxVdaqARUP_1.wireOp",EDGE,"fcba4419-a2ee-464f-be9d-58f11bf3418b.sketch_text.stroke-107"),sQuery(id+"FQ5JFwxVdaqARUP_1.wireOp",EDGE,"fcba4419-a2ee-464f-be9d-58f11bf3418b.sketch_text.stroke-108"),sQuery(id+"FQ5JFwxVdaqARUP_1.wireOp",EDGE,"fcba4419-a2ee-464f-be9d-58f11bf3418b.sketch_text.stroke-109"),sQuery(id+"FQ5JFwxVdaqARUP_1.wireOp",EDGE,"fcba4419-a2ee-464f-be9d-58f11bf3418b.sketch_text.stroke-110"),sQuery(id+"FQ5JFwxVdaqARUP_1.wireOp",EDGE,"fcba4419-a2ee-464f-be9d-58f11bf3418b.sketch_text.stroke-111"),sQuery(id+"FQ5JFwxVdaqARUP_1.wireOp",EDGE,"fcba4419-a2ee-464f-be9d-58f11bf3418b.sketch_text.stroke-112"),sQuery(id+"FQ5JFwxVdaqARUP_1.wireOp",EDGE,"fcba4419-a2ee-464f-be9d-58f11bf3418b.sketch_text.stroke-113"),sQuery(id+"FQ5JFwxVdaqARUP_1.wireOp",EDGE,"fcba4419-a2ee-464f-be9d-58f11bf3418b.sketch_text.stroke-114"),sQuery(id+"FQ5JFwxVdaqARUP_1.wireOp",EDGE,"fcba4419-a2ee-464f-be9d-58f11bf3418b.sketch_text.stroke-115"),sQuery(id+"FQ5JFwxVdaqARUP_1.wireOp",EDGE,"fcba4419-a2ee-464f-be9d-58f11bf3418b.sketch_text.stroke-116"),sQuery(id+"FQ5JFwxVdaqARUP_1.wireOp",EDGE,"fcba4419-a2ee-464f-be9d-58f11bf3418b.sketch_text.stroke-117"),sQuery(id+"FQ5JFwxVdaqARUP_1.wireOp",EDGE,"fcba4419-a2ee-464f-be9d-58f11bf3418b.sketch_text.stroke-118"),sQuery(id+"FQ5JFwxVdaqARUP_1.wireOp",EDGE,"fcba4419-a2ee-464f-be9d-58f11bf3418b.sketch_text.stroke-119"),sQuery(id+"FQ5JFwxVdaqARUP_1.wireOp",EDGE,"fcba4419-a2ee-464f-be9d-58f11bf3418b.sketch_text.stroke-120"),sQuery(id+"FQ5JFwxVdaqARUP_1.wireOp",EDGE,"fcba4419-a2ee-464f-be9d-58f11bf3418b.sketch_text.stroke-121"),sQuery(id+"FQ5JFwxVdaqARUP_1.wireOp",EDGE,"fcba4419-a2ee-464f-be9d-58f11bf3418b.sketch_text.stroke-122"),sQuery(id+"FQ5JFwxVdaqARUP_1.wireOp",EDGE,"fcba4419-a2ee-464f-be9d-58f11bf3418b.sketch_text.stroke-123"),sQuery(id+"FQ5JFwxVdaqARUP_1.wireOp",EDGE,"fcba4419-a2ee-464f-be9d-58f11bf3418b.sketch_text.stroke-124"),sQuery(id+"FQ5JFwxVdaqARUP_1.wireOp",EDGE,"fcba4419-a2ee-464f-be9d-58f11bf3418b.sketch_text.stroke-125"),sQuery(id+"FQ5JFwxVdaqARUP_1.wireOp",EDGE,"fcba4419-a2ee-464f-be9d-58f11bf3418b.sketch_text.stroke-126"),sQuery(id+"FQ5JFwxVdaqARUP_1.wireOp",EDGE,"fcba4419-a2ee-464f-be9d-58f11bf3418b.sketch_text.stroke-127"),sQuery(id+"FQ5JFwxVdaqARUP_1.wireOp",EDGE,"fcba4419-a2ee-464f-be9d-58f11bf3418b.sketch_text.stroke-128"),sQuery(id+"FQ5JFwxVdaqARUP_1.wireOp",EDGE,"fcba4419-a2ee-464f-be9d-58f11bf3418b.sketch_text.stroke-129"),sQuery(id+"FQ5JFwxVdaqARUP_1.wireOp",EDGE,"fcba4419-a2ee-464f-be9d-58f11bf3418b.sketch_text.stroke-130"),sQuery(id+"FQ5JFwxVdaqARUP_1.wireOp",EDGE,"fcba4419-a2ee-464f-be9d-58f11bf3418b.sketch_text.stroke-131"),sQuery(id+"FQ5JFwxVdaqARUP_1.wireOp",EDGE,"fcba4419-a2ee-464f-be9d-58f11bf3418b.sketch_text.stroke-132"),sQuery(id+"FQ5JFwxVdaqARUP_1.wireOp",EDGE,"fcba4419-a2ee-464f-be9d-58f11bf3418b.sketch_text.stroke-133"),sQuery(id+"FQ5JFwxVdaqARUP_1.wireOp",EDGE,"fcba4419-a2ee-464f-be9d-58f11bf3418b.sketch_text.stroke-134"),sQuery(id+"FQ5JFwxVdaqARUP_1.wireOp",EDGE,"fcba4419-a2ee-464f-be9d-58f11bf3418b.sketch_text.stroke-135"),sQuery(id+"FQ5JFwxVdaqARUP_1.wireOp",EDGE,"fcba4419-a2ee-464f-be9d-58f11bf3418b.sketch_text.stroke-136"),sQuery(id+"FQ5JFwxVdaqARUP_1.wireOp",EDGE,"fcba4419-a2ee-464f-be9d-58f11bf3418b.sketch_text.stroke-137"),sQuery(id+"FQ5JFwxVdaqARUP_1.wireOp",EDGE,"fcba4419-a2ee-464f-be9d-58f11bf3418b.sketch_text.stroke-138"),sQuery(id+"FQ5JFwxVdaqARUP_1.wireOp",EDGE,"fcba4419-a2ee-464f-be9d-58f11bf3418b.sketch_text.stroke-139"),sQuery(id+"FQ5JFwxVdaqARUP_1.wireOp",EDGE,"fcba4419-a2ee-464f-be9d-58f11bf3418b.sketch_text.stroke-140"),sQuery(id+"FQ5JFwxVdaqARUP_1.wireOp",EDGE,"fcba4419-a2ee-464f-be9d-58f11bf3418b.sketch_text.stroke-141"),sQuery(id+"FQ5JFwxVdaqARUP_1.wireOp",EDGE,"fcba4419-a2ee-464f-be9d-58f11bf3418b.sketch_text.stroke-142"),sQuery(id+"FQ5JFwxVdaqARUP_1.wireOp",EDGE,"fcba4419-a2ee-464f-be9d-58f11bf3418b.sketch_text.stroke-143"),sQuery(id+"FQ5JFwxVdaqARUP_1.wireOp",EDGE,"fcba4419-a2ee-464f-be9d-58f11bf3418b.sketch_text.stroke-144"),sQuery(id+"FQ5JFwxVdaqARUP_1.wireOp",EDGE,"fcba4419-a2ee-464f-be9d-58f11bf3418b.sketch_text.stroke-145"),sQuery(id+"FQ5JFwxVdaqARUP_1.wireOp",EDGE,"fcba4419-a2ee-464f-be9d-58f11bf3418b.sketch_text.stroke-146"),sQuery(id+"FQ5JFwxVdaqARUP_1.wireOp",EDGE,"fcba4419-a2ee-464f-be9d-58f11bf3418b.sketch_text.stroke-147"),sQuery(id+"FQ5JFwxVdaqARUP_1.wireOp",EDGE,"fcba4419-a2ee-464f-be9d-58f11bf3418b.sketch_text.stroke-148"),sQuery(id+"FQ5JFwxVdaqARUP_1.wireOp",EDGE,"fcba4419-a2ee-464f-be9d-58f11bf3418b.sketch_text.stroke-149"),sQuery(id+"FQ5JFwxVdaqARUP_1.wireOp",EDGE,"fcba4419-a2ee-464f-be9d-58f11bf3418b.sketch_text.stroke-150"),sQuery(id+"FQ5JFwxVdaqARUP_1.wireOp",EDGE,"fcba4419-a2ee-464f-be9d-58f11bf3418b.sketch_text.stroke-151"),sQuery(id+"FQ5JFwxVdaqARUP_1.wireOp",EDGE,"fcba4419-a2ee-464f-be9d-58f11bf3418b.sketch_text.stroke-152"),sQuery(id+"FQ5JFwxVdaqARUP_1.wireOp",EDGE,"fcba4419-a2ee-464f-be9d-58f11bf3418b.sketch_text.stroke-153"),sQuery(id+"FQ5JFwxVdaqARUP_1.wireOp",EDGE,"fcba4419-a2ee-464f-be9d-58f11bf3418b.sketch_text.stroke-154"),sQuery(id+"FQ5JFwxVdaqARUP_1.wireOp",EDGE,"fcba4419-a2ee-464f-be9d-58f11bf3418b.sketch_text.stroke-155"),sQuery(id+"FQ5JFwxVdaqARUP_1.wireOp",EDGE,"fcba4419-a2ee-464f-be9d-58f11bf3418b.sketch_text.stroke-156"),sQuery(id+"FQ5JFwxVdaqARUP_1.wireOp",EDGE,"fcba4419-a2ee-464f-be9d-58f11bf3418b.sketch_text.stroke-157"),sQuery(id+"FQ5JFwxVdaqARUP_1.wireOp",EDGE,"fcba4419-a2ee-464f-be9d-58f11bf3418b.sketch_text.stroke-158"),sQuery(id+"FQ5JFwxVdaqARUP_1.wireOp",EDGE,"fcba4419-a2ee-464f-be9d-58f11bf3418b.sketch_text.stroke-159"),sQuery(id+"FQ5JFwxVdaqARUP_1.wireOp",EDGE,"fcba4419-a2ee-464f-be9d-58f11bf3418b.sketch_text.stroke-160"),sQuery(id+"FQ5JFwxVdaqARUP_1.wireOp",EDGE,"fcba4419-a2ee-464f-be9d-58f11bf3418b.sketch_text.stroke-161"),sQuery(id+"FQ5JFwxVdaqARUP_1.wireOp",EDGE,"fcba4419-a2ee-464f-be9d-58f11bf3418b.sketch_text.stroke-162"),sQuery(id+"FQ5JFwxVdaqARUP_1.wireOp",EDGE,"fcba4419-a2ee-464f-be9d-58f11bf3418b.sketch_text.stroke-163"),sQuery(id+"FQ5JFwxVdaqARUP_1.wireOp",EDGE,"fcba4419-a2ee-464f-be9d-58f11bf3418b.sketch_text.stroke-164"),sQuery(id+"FQ5JFwxVdaqARUP_1.wireOp",EDGE,"fcba4419-a2ee-464f-be9d-58f11bf3418b.sketch_text.stroke-165"),sQuery(id+"FQ5JFwxVdaqARUP_1.wireOp",EDGE,"fcba4419-a2ee-464f-be9d-58f11bf3418b.sketch_text.stroke-166"),sQuery(id+"FQ5JFwxVdaqARUP_1.wireOp",EDGE,"fcba4419-a2ee-464f-be9d-58f11bf3418b.sketch_text.stroke-167"),sQuery(id+"FQ5JFwxVdaqARUP_1.wireOp",EDGE,"fcba4419-a2ee-464f-be9d-58f11bf3418b.sketch_text.stroke-168"),sQuery(id+"FQ5JFwxVdaqARUP_1.wireOp",EDGE,"fcba4419-a2ee-464f-be9d-58f11bf3418b.sketch_text.stroke-169"),sQuery(id+"FQ5JFwxVdaqARUP_1.wireOp",EDGE,"fcba4419-a2ee-464f-be9d-58f11bf3418b.sketch_text.stroke-170"),sQuery(id+"FQ5JFwxVdaqARUP_1.wireOp",EDGE,"fcba4419-a2ee-464f-be9d-58f11bf3418b.sketch_text.stroke-171"),sQuery(id+"FQ5JFwxVdaqARUP_1.wireOp",EDGE,"fcba4419-a2ee-464f-be9d-58f11bf3418b.sketch_text.stroke-172"),sQuery(id+"FQ5JFwxVdaqARUP_1.wireOp",EDGE,"fcba4419-a2ee-464f-be9d-58f11bf3418b.sketch_text.stroke-173"),sQuery(id+"FHMxAyK4CFUKdhS_1.wireOp",EDGE,"1cb9c079-ea9b-4899-8069-e0e3048e911d.sketch_text.stroke-0"),sQuery(id+"FHMxAyK4CFUKdhS_1.wireOp",EDGE,"1cb9c079-ea9b-4899-8069-e0e3048e911d.sketch_text.stroke-1"),sQuery(id+"FHMxAyK4CFUKdhS_1.wireOp",EDGE,"1cb9c079-ea9b-4899-8069-e0e3048e911d.sketch_text.stroke-2"),sQuery(id+"FHMxAyK4CFUKdhS_1.wireOp",EDGE,"1cb9c079-ea9b-4899-8069-e0e3048e911d.sketch_text.stroke-3"),sQuery(id+"FHMxAyK4CFUKdhS_1.wireOp",EDGE,"1cb9c079-ea9b-4899-8069-e0e3048e911d.sketch_text.stroke-4"),sQuery(id+"FHMxAyK4CFUKdhS_1.wireOp",EDGE,"1cb9c079-ea9b-4899-8069-e0e3048e911d.sketch_text.stroke-5"),sQuery(id+"FHMxAyK4CFUKdhS_1.wireOp",EDGE,"1cb9c079-ea9b-4899-8069-e0e3048e911d.sketch_text.stroke-6"),sQuery(id+"FHMxAyK4CFUKdhS_1.wireOp",EDGE,"1cb9c079-ea9b-4899-8069-e0e3048e911d.sketch_text.stroke-7"),sQuery(id+"FHMxAyK4CFUKdhS_1.wireOp",EDGE,"1cb9c079-ea9b-4899-8069-e0e3048e911d.sketch_text.stroke-8"),sQuery(id+"FHMxAyK4CFUKdhS_1.wireOp",EDGE,"1cb9c079-ea9b-4899-8069-e0e3048e911d.sketch_text.stroke-9"),sQuery(id+"FHMxAyK4CFUKdhS_1.wireOp",EDGE,"1cb9c079-ea9b-4899-8069-e0e3048e911d.sketch_text.stroke-10"),sQuery(id+"FHMxAyK4CFUKdhS_1.wireOp",EDGE,"1cb9c079-ea9b-4899-8069-e0e3048e911d.sketch_text.stroke-11"),sQuery(id+"FHMxAyK4CFUKdhS_1.wireOp",EDGE,"1cb9c079-ea9b-4899-8069-e0e3048e911d.sketch_text.stroke-12"),sQuery(id+"FHMxAyK4CFUKdhS_1.wireOp",EDGE,"1cb9c079-ea9b-4899-8069-e0e3048e911d.sketch_text.stroke-13"),sQuery(id+"FHMxAyK4CFUKdhS_1.wireOp",EDGE,"1cb9c079-ea9b-4899-8069-e0e3048e911d.sketch_text.stroke-14"),sQuery(id+"FHMxAyK4CFUKdhS_1.wireOp",EDGE,"1cb9c079-ea9b-4899-8069-e0e3048e911d.sketch_text.stroke-15"),sQuery(id+"FHMxAyK4CFUKdhS_1.wireOp",EDGE,"1cb9c079-ea9b-4899-8069-e0e3048e911d.sketch_text.stroke-16"),sQuery(id+"FHMxAyK4CFUKdhS_1.wireOp",EDGE,"1cb9c079-ea9b-4899-8069-e0e3048e911d.sketch_text.stroke-17"),sQuery(id+"FHMxAyK4CFUKdhS_1.wireOp",EDGE,"1cb9c079-ea9b-4899-8069-e0e3048e911d.sketch_text.stroke-18"),sQuery(id+"FHMxAyK4CFUKdhS_1.wireOp",EDGE,"1cb9c079-ea9b-4899-8069-e0e3048e911d.sketch_text.stroke-19"),sQuery(id+"FHMxAyK4CFUKdhS_1.wireOp",EDGE,"1cb9c079-ea9b-4899-8069-e0e3048e911d.sketch_text.stroke-20"),sQuery(id+"FHMxAyK4CFUKdhS_1.wireOp",EDGE,"1cb9c079-ea9b-4899-8069-e0e3048e911d.sketch_text.stroke-21"),sQuery(id+"FHMxAyK4CFUKdhS_1.wireOp",EDGE,"1cb9c079-ea9b-4899-8069-e0e3048e911d.sketch_text.stroke-22"),sQuery(id+"FHMxAyK4CFUKdhS_1.wireOp",EDGE,"1cb9c079-ea9b-4899-8069-e0e3048e911d.sketch_text.stroke-23"),sQuery(id+"FHMxAyK4CFUKdhS_1.wireOp",EDGE,"1cb9c079-ea9b-4899-8069-e0e3048e911d.sketch_text.stroke-24"),sQuery(id+"FHMxAyK4CFUKdhS_1.wireOp",EDGE,"1cb9c079-ea9b-4899-8069-e0e3048e911d.sketch_text.stroke-25"),sQuery(id+"FHMxAyK4CFUKdhS_1.wireOp",EDGE,"1cb9c079-ea9b-4899-8069-e0e3048e911d.sketch_text.stroke-26"),sQuery(id+"FHMxAyK4CFUKdhS_1.wireOp",EDGE,"1cb9c079-ea9b-4899-8069-e0e3048e911d.sketch_text.stroke-27"),sQuery(id+"FHMxAyK4CFUKdhS_1.wireOp",EDGE,"1cb9c079-ea9b-4899-8069-e0e3048e911d.sketch_text.stroke-28"),sQuery(id+"FHMxAyK4CFUKdhS_1.wireOp",EDGE,"1cb9c079-ea9b-4899-8069-e0e3048e911d.sketch_text.stroke-29"),sQuery(id+"FHMxAyK4CFUKdhS_1.wireOp",EDGE,"1cb9c079-ea9b-4899-8069-e0e3048e911d.sketch_text.stroke-30"),sQuery(id+"FHMxAyK4CFUKdhS_1.wireOp",EDGE,"1cb9c079-ea9b-4899-8069-e0e3048e911d.sketch_text.stroke-31"),sQuery(id+"FHMxAyK4CFUKdhS_1.wireOp",EDGE,"1cb9c079-ea9b-4899-8069-e0e3048e911d.sketch_text.stroke-32"),sQuery(id+"FHMxAyK4CFUKdhS_1.wireOp",EDGE,"1cb9c079-ea9b-4899-8069-e0e3048e911d.sketch_text.stroke-33"),sQuery(id+"FHMxAyK4CFUKdhS_1.wireOp",EDGE,"1cb9c079-ea9b-4899-8069-e0e3048e911d.sketch_text.stroke-34"),sQuery(id+"FHMxAyK4CFUKdhS_1.wireOp",EDGE,"1cb9c079-ea9b-4899-8069-e0e3048e911d.sketch_text.stroke-35"),sQuery(id+"FHMxAyK4CFUKdhS_1.wireOp",EDGE,"1cb9c079-ea9b-4899-8069-e0e3048e911d.sketch_text.stroke-36"),sQuery(id+"FHMxAyK4CFUKdhS_1.wireOp",EDGE,"1cb9c079-ea9b-4899-8069-e0e3048e911d.sketch_text.stroke-37"),sQuery(id+"FHMxAyK4CFUKdhS_1.wireOp",EDGE,"1cb9c079-ea9b-4899-8069-e0e3048e911d.sketch_text.stroke-38"),sQuery(id+"FHMxAyK4CFUKdhS_1.wireOp",EDGE,"1cb9c079-ea9b-4899-8069-e0e3048e911d.sketch_text.stroke-39"),sQuery(id+"FHMxAyK4CFUKdhS_1.wireOp",EDGE,"1cb9c079-ea9b-4899-8069-e0e3048e911d.sketch_text.stroke-40"),sQuery(id+"FHMxAyK4CFUKdhS_1.wireOp",EDGE,"1cb9c079-ea9b-4899-8069-e0e3048e911d.sketch_text.stroke-41"),sQuery(id+"FHMxAyK4CFUKdhS_1.wireOp",EDGE,"1cb9c079-ea9b-4899-8069-e0e3048e911d.sketch_text.stroke-42"),sQuery(id+"FHMxAyK4CFUKdhS_1.wireOp",EDGE,"1cb9c079-ea9b-4899-8069-e0e3048e911d.sketch_text.stroke-43"),sQuery(id+"FHMxAyK4CFUKdhS_1.wireOp",EDGE,"1cb9c079-ea9b-4899-8069-e0e3048e911d.sketch_text.stroke-44"),sQuery(id+"FHMxAyK4CFUKdhS_1.wireOp",EDGE,"1cb9c079-ea9b-4899-8069-e0e3048e911d.sketch_text.stroke-45"),sQuery(id+"FHMxAyK4CFUKdhS_1.wireOp",EDGE,"1cb9c079-ea9b-4899-8069-e0e3048e911d.sketch_text.stroke-46"),sQuery(id+"FHMxAyK4CFUKdhS_1.wireOp",EDGE,"1cb9c079-ea9b-4899-8069-e0e3048e911d.sketch_text.stroke-47"),sQuery(id+"FHMxAyK4CFUKdhS_1.wireOp",EDGE,"1cb9c079-ea9b-4899-8069-e0e3048e911d.sketch_text.stroke-48"),sQuery(id+"FHMxAyK4CFUKdhS_1.wireOp",EDGE,"1cb9c079-ea9b-4899-8069-e0e3048e911d.sketch_text.stroke-49"),sQuery(id+"FHMxAyK4CFUKdhS_1.wireOp",EDGE,"1cb9c079-ea9b-4899-8069-e0e3048e911d.sketch_text.stroke-50"),sQuery(id+"FHMxAyK4CFUKdhS_1.wireOp",EDGE,"1cb9c079-ea9b-4899-8069-e0e3048e911d.sketch_text.stroke-51"),sQuery(id+"FHMxAyK4CFUKdhS_1.wireOp",EDGE,"1cb9c079-ea9b-4899-8069-e0e3048e911d.sketch_text.stroke-52"),sQuery(id+"FHMxAyK4CFUKdhS_1.wireOp",EDGE,"1cb9c079-ea9b-4899-8069-e0e3048e911d.sketch_text.stroke-53"),sQuery(id+"FHMxAyK4CFUKdhS_1.wireOp",EDGE,"1cb9c079-ea9b-4899-8069-e0e3048e911d.sketch_text.stroke-54"),sQuery(id+"FHMxAyK4CFUKdhS_1.wireOp",EDGE,"1cb9c079-ea9b-4899-8069-e0e3048e911d.sketch_text.stroke-55"),sQuery(id+"FHMxAyK4CFUKdhS_1.wireOp",EDGE,"1cb9c079-ea9b-4899-8069-e0e3048e911d.sketch_text.stroke-56"),sQuery(id+"FHMxAyK4CFUKdhS_1.wireOp",EDGE,"1cb9c079-ea9b-4899-8069-e0e3048e911d.sketch_text.stroke-57"),sQuery(id+"FHMxAyK4CFUKdhS_1.wireOp",EDGE,"1cb9c079-ea9b-4899-8069-e0e3048e911d.sketch_text.stroke-58"),sQuery(id+"FHMxAyK4CFUKdhS_1.wireOp",EDGE,"1cb9c079-ea9b-4899-8069-e0e3048e911d.sketch_text.stroke-59"),sQuery(id+"FHMxAyK4CFUKdhS_1.wireOp",EDGE,"1cb9c079-ea9b-4899-8069-e0e3048e911d.sketch_text.stroke-60"),sQuery(id+"FHMxAyK4CFUKdhS_1.wireOp",EDGE,"1cb9c079-ea9b-4899-8069-e0e3048e911d.sketch_text.stroke-61"),sQuery(id+"FHMxAyK4CFUKdhS_1.wireOp",EDGE,"1cb9c079-ea9b-4899-8069-e0e3048e911d.sketch_text.stroke-62"),sQuery(id+"FHMxAyK4CFUKdhS_1.wireOp",EDGE,"1cb9c079-ea9b-4899-8069-e0e3048e911d.sketch_text.stroke-71"),sQuery(id+"FHMxAyK4CFUKdhS_1.wireOp",EDGE,"1cb9c079-ea9b-4899-8069-e0e3048e911d.sketch_text.stroke-72"),sQuery(id+"FHMxAyK4CFUKdhS_1.wireOp",EDGE,"1cb9c079-ea9b-4899-8069-e0e3048e911d.sketch_text.stroke-73"),sQuery(id+"FHMxAyK4CFUKdhS_1.wireOp",EDGE,"1cb9c079-ea9b-4899-8069-e0e3048e911d.sketch_text.stroke-74"),sQuery(id+"FHMxAyK4CFUKdhS_1.wireOp",EDGE,"1cb9c079-ea9b-4899-8069-e0e3048e911d.sketch_text.stroke-75"),sQuery(id+"FHMxAyK4CFUKdhS_1.wireOp",EDGE,"1cb9c079-ea9b-4899-8069-e0e3048e911d.sketch_text.stroke-76"),sQuery(id+"FHMxAyK4CFUKdhS_1.wireOp",EDGE,"1cb9c079-ea9b-4899-8069-e0e3048e911d.sketch_text.stroke-77"),sQuery(id+"FHMxAyK4CFUKdhS_1.wireOp",EDGE,"1cb9c079-ea9b-4899-8069-e0e3048e911d.sketch_text.stroke-78"),sQuery(id+"FHMxAyK4CFUKdhS_1.wireOp",EDGE,"1cb9c079-ea9b-4899-8069-e0e3048e911d.sketch_text.stroke-79"),sQuery(id+"FHMxAyK4CFUKdhS_1.wireOp",EDGE,"1cb9c079-ea9b-4899-8069-e0e3048e911d.sketch_text.stroke-80"),sQuery(id+"FHMxAyK4CFUKdhS_1.wireOp",EDGE,"1cb9c079-ea9b-4899-8069-e0e3048e911d.sketch_text.stroke-81"),sQuery(id+"FHMxAyK4CFUKdhS_1.wireOp",EDGE,"1cb9c079-ea9b-4899-8069-e0e3048e911d.sketch_text.stroke-82"),sQuery(id+"FHMxAyK4CFUKdhS_1.wireOp",EDGE,"1cb9c079-ea9b-4899-8069-e0e3048e911d.sketch_text.stroke-83"),sQuery(id+"FHMxAyK4CFUKdhS_1.wireOp",EDGE,"1cb9c079-ea9b-4899-8069-e0e3048e911d.sketch_text.stroke-84"),sQuery(id+"FHMxAyK4CFUKdhS_1.wireOp",EDGE,"1cb9c079-ea9b-4899-8069-e0e3048e911d.sketch_text.stroke-85"),sQuery(id+"FHMxAyK4CFUKdhS_1.wireOp",EDGE,"1cb9c079-ea9b-4899-8069-e0e3048e911d.sketch_text.stroke-86"),sQuery(id+"FHMxAyK4CFUKdhS_1.wireOp",EDGE,"1cb9c079-ea9b-4899-8069-e0e3048e911d.sketch_text.stroke-87"),sQuery(id+"FHMxAyK4CFUKdhS_1.wireOp",EDGE,"1cb9c079-ea9b-4899-8069-e0e3048e911d.sketch_text.stroke-88"),sQuery(id+"FHMxAyK4CFUKdhS_1.wireOp",EDGE,"1cb9c079-ea9b-4899-8069-e0e3048e911d.sketch_text.stroke-89"),sQuery(id+"FHMxAyK4CFUKdhS_1.wireOp",EDGE,"1cb9c079-ea9b-4899-8069-e0e3048e911d.sketch_text.stroke-90"),sQuery(id+"FHMxAyK4CFUKdhS_1.wireOp",EDGE,"1cb9c079-ea9b-4899-8069-e0e3048e911d.sketch_text.stroke-91"),sQuery(id+"FHMxAyK4CFUKdhS_1.wireOp",EDGE,"1cb9c079-ea9b-4899-8069-e0e3048e911d.sketch_text.stroke-92"),sQuery(id+"FHMxAyK4CFUKdhS_1.wireOp",EDGE,"1cb9c079-ea9b-4899-8069-e0e3048e911d.sketch_text.stroke-93"),sQuery(id+"FHMxAyK4CFUKdhS_1.wireOp",EDGE,"1cb9c079-ea9b-4899-8069-e0e3048e911d.sketch_text.stroke-94"),sQuery(id+"FHMxAyK4CFUKdhS_1.wireOp",EDGE,"1cb9c079-ea9b-4899-8069-e0e3048e911d.sketch_text.stroke-95"),sQuery(id+"FHMxAyK4CFUKdhS_1.wireOp",EDGE,"1cb9c079-ea9b-4899-8069-e0e3048e911d.sketch_text.stroke-96"),sQuery(id+"FHMxAyK4CFUKdhS_1.wireOp",EDGE,"1cb9c079-ea9b-4899-8069-e0e3048e911d.sketch_text.stroke-97"),sQuery(id+"FHMxAyK4CFUKdhS_1.wireOp",EDGE,"1cb9c079-ea9b-4899-8069-e0e3048e911d.sketch_text.stroke-103"),sQuery(id+"FHMxAyK4CFUKdhS_1.wireOp",EDGE,"1cb9c079-ea9b-4899-8069-e0e3048e911d.sketch_text.stroke-104"),sQuery(id+"FHMxAyK4CFUKdhS_1.wireOp",EDGE,"1cb9c079-ea9b-4899-8069-e0e3048e911d.sketch_text.stroke-105"),sQuery(id+"FHMxAyK4CFUKdhS_1.wireOp",EDGE,"1cb9c079-ea9b-4899-8069-e0e3048e911d.sketch_text.stroke-106"),sQuery(id+"FHMxAyK4CFUKdhS_1.wireOp",EDGE,"1cb9c079-ea9b-4899-8069-e0e3048e911d.sketch_text.stroke-107"),sQuery(id+"FHMxAyK4CFUKdhS_1.wireOp",EDGE,"1cb9c079-ea9b-4899-8069-e0e3048e911d.sketch_text.stroke-108"),sQuery(id+"FHMxAyK4CFUKdhS_1.wireOp",EDGE,"1cb9c079-ea9b-4899-8069-e0e3048e911d.sketch_text.stroke-109"),sQuery(id+"FHMxAyK4CFUKdhS_1.wireOp",EDGE,"1cb9c079-ea9b-4899-8069-e0e3048e911d.sketch_text.stroke-110"),sQuery(id+"FHMxAyK4CFUKdhS_1.wireOp",EDGE,"1cb9c079-ea9b-4899-8069-e0e3048e911d.sketch_text.stroke-111"),sQuery(id+"FHMxAyK4CFUKdhS_1.wireOp",EDGE,"1cb9c079-ea9b-4899-8069-e0e3048e911d.sketch_text.stroke-112"),sQuery(id+"FHMxAyK4CFUKdhS_1.wireOp",EDGE,"1cb9c079-ea9b-4899-8069-e0e3048e911d.sketch_text.stroke-113"),sQuery(id+"FHMxAyK4CFUKdhS_1.wireOp",EDGE,"1cb9c079-ea9b-4899-8069-e0e3048e911d.sketch_text.stroke-114"),sQuery(id+"FHMxAyK4CFUKdhS_1.wireOp",EDGE,"1cb9c079-ea9b-4899-8069-e0e3048e911d.sketch_text.stroke-115"),sQuery(id+"FHMxAyK4CFUKdhS_1.wireOp",EDGE,"1cb9c079-ea9b-4899-8069-e0e3048e911d.sketch_text.stroke-116"),sQuery(id+"FHMxAyK4CFUKdhS_1.wireOp",EDGE,"1cb9c079-ea9b-4899-8069-e0e3048e911d.sketch_text.stroke-117"),sQuery(id+"FHMxAyK4CFUKdhS_1.wireOp",EDGE,"1cb9c079-ea9b-4899-8069-e0e3048e911d.sketch_text.stroke-118"),sQuery(id+"FHMxAyK4CFUKdhS_1.wireOp",EDGE,"1cb9c079-ea9b-4899-8069-e0e3048e911d.sketch_text.stroke-119"),sQuery(id+"FHMxAyK4CFUKdhS_1.wireOp",EDGE,"1cb9c079-ea9b-4899-8069-e0e3048e911d.sketch_text.stroke-120"),sQuery(id+"FHMxAyK4CFUKdhS_1.wireOp",EDGE,"1cb9c079-ea9b-4899-8069-e0e3048e911d.sketch_text.stroke-121"),sQuery(id+"FHMxAyK4CFUKdhS_1.wireOp",EDGE,"1cb9c079-ea9b-4899-8069-e0e3048e911d.sketch_text.stroke-122"),sQuery(id+"FHMxAyK4CFUKdhS_1.wireOp",EDGE,"1cb9c079-ea9b-4899-8069-e0e3048e911d.sketch_text.stroke-123"),sQuery(id+"FHMxAyK4CFUKdhS_1.wireOp",EDGE,"1cb9c079-ea9b-4899-8069-e0e3048e911d.sketch_text.stroke-124"),sQuery(id+"FHMxAyK4CFUKdhS_1.wireOp",EDGE,"1cb9c079-ea9b-4899-8069-e0e3048e911d.sketch_text.stroke-125"),sQuery(id+"FHMxAyK4CFUKdhS_1.wireOp",EDGE,"1cb9c079-ea9b-4899-8069-e0e3048e911d.sketch_text.stroke-126"),sQuery(id+"FHMxAyK4CFUKdhS_1.wireOp",EDGE,"1cb9c079-ea9b-4899-8069-e0e3048e911d.sketch_text.stroke-127"),sQuery(id+"FHMxAyK4CFUKdhS_1.wireOp",EDGE,"1cb9c079-ea9b-4899-8069-e0e3048e911d.sketch_text.stroke-128"),sQuery(id+"FHMxAyK4CFUKdhS_1.wireOp",EDGE,"1cb9c079-ea9b-4899-8069-e0e3048e911d.sketch_text.stroke-129"),sQuery(id+"FHMxAyK4CFUKdhS_1.wireOp",EDGE,"1cb9c079-ea9b-4899-8069-e0e3048e911d.sketch_text.stroke-130"),sQuery(id+"FHMxAyK4CFUKdhS_1.wireOp",EDGE,"1cb9c079-ea9b-4899-8069-e0e3048e911d.sketch_text.stroke-131"),sQuery(id+"FHMxAyK4CFUKdhS_1.wireOp",EDGE,"1cb9c079-ea9b-4899-8069-e0e3048e911d.sketch_text.stroke-132"),sQuery(id+"FHMxAyK4CFUKdhS_1.wireOp",EDGE,"1cb9c079-ea9b-4899-8069-e0e3048e911d.sketch_text.stroke-133"),sQuery(id+"FHMxAyK4CFUKdhS_1.wireOp",EDGE,"1cb9c079-ea9b-4899-8069-e0e3048e911d.sketch_text.stroke-134"),sQuery(id+"FHMxAyK4CFUKdhS_1.wireOp",EDGE,"1cb9c079-ea9b-4899-8069-e0e3048e911d.sketch_text.stroke-135"),sQuery(id+"FHMxAyK4CFUKdhS_1.wireOp",EDGE,"1cb9c079-ea9b-4899-8069-e0e3048e911d.sketch_text.stroke-136"),sQuery(id+"FHMxAyK4CFUKdhS_1.wireOp",EDGE,"1cb9c079-ea9b-4899-8069-e0e3048e911d.sketch_text.stroke-137"),sQuery(id+"FHMxAyK4CFUKdhS_1.wireOp",EDGE,"1cb9c079-ea9b-4899-8069-e0e3048e911d.sketch_text.stroke-138"),sQuery(id+"FHMxAyK4CFUKdhS_1.wireOp",EDGE,"1cb9c079-ea9b-4899-8069-e0e3048e911d.sketch_text.stroke-139"),sQuery(id+"FHMxAyK4CFUKdhS_1.wireOp",EDGE,"1cb9c079-ea9b-4899-8069-e0e3048e911d.sketch_text.stroke-140"),sQuery(id+"FHMxAyK4CFUKdhS_1.wireOp",EDGE,"1cb9c079-ea9b-4899-8069-e0e3048e911d.sketch_text.stroke-141"),sQuery(id+"FHMxAyK4CFUKdhS_1.wireOp",EDGE,"1cb9c079-ea9b-4899-8069-e0e3048e911d.sketch_text.stroke-142"),sQuery(id+"FHMxAyK4CFUKdhS_1.wireOp",EDGE,"1cb9c079-ea9b-4899-8069-e0e3048e911d.sketch_text.stroke-143"),sQuery(id+"FHMxAyK4CFUKdhS_1.wireOp",EDGE,"1cb9c079-ea9b-4899-8069-e0e3048e911d.sketch_text.stroke-144"),sQuery(id+"FHMxAyK4CFUKdhS_1.wireOp",EDGE,"1cb9c079-ea9b-4899-8069-e0e3048e911d.sketch_text.stroke-145"),sQuery(id+"FHMxAyK4CFUKdhS_1.wireOp",EDGE,"1cb9c079-ea9b-4899-8069-e0e3048e911d.sketch_text.stroke-146"),sQuery(id+"FHMxAyK4CFUKdhS_1.wireOp",EDGE,"1cb9c079-ea9b-4899-8069-e0e3048e911d.sketch_text.stroke-147"),sQuery(id+"FHMxAyK4CFUKdhS_1.wireOp",EDGE,"1cb9c079-ea9b-4899-8069-e0e3048e911d.sketch_text.stroke-148"),sQuery(id+"FHMxAyK4CFUKdhS_1.wireOp",EDGE,"1cb9c079-ea9b-4899-8069-e0e3048e911d.sketch_text.stroke-149"),sQuery(id+"FHMxAyK4CFUKdhS_1.wireOp",EDGE,"1cb9c079-ea9b-4899-8069-e0e3048e911d.sketch_text.stroke-150"),sQuery(id+"FHMxAyK4CFUKdhS_1.wireOp",EDGE,"1cb9c079-ea9b-4899-8069-e0e3048e911d.sketch_text.stroke-151"),sQuery(id+"FHMxAyK4CFUKdhS_1.wireOp",EDGE,"1cb9c079-ea9b-4899-8069-e0e3048e911d.sketch_text.stroke-152"),sQuery(id+"FHMxAyK4CFUKdhS_1.wireOp",EDGE,"1cb9c079-ea9b-4899-8069-e0e3048e911d.sketch_text.stroke-153"),sQuery(id+"FHMxAyK4CFUKdhS_1.wireOp",EDGE,"1cb9c079-ea9b-4899-8069-e0e3048e911d.sketch_text.stroke-159"),sQuery(id+"FHMxAyK4CFUKdhS_1.wireOp",EDGE,"1cb9c079-ea9b-4899-8069-e0e3048e911d.sketch_text.stroke-160"),sQuery(id+"FHMxAyK4CFUKdhS_1.wireOp",EDGE,"1cb9c079-ea9b-4899-8069-e0e3048e911d.sketch_text.stroke-161"),sQuery(id+"FHMxAyK4CFUKdhS_1.wireOp",EDGE,"1cb9c079-ea9b-4899-8069-e0e3048e911d.sketch_text.stroke-162"),sQuery(id+"FHMxAyK4CFUKdhS_1.wireOp",EDGE,"1cb9c079-ea9b-4899-8069-e0e3048e911d.sketch_text.stroke-163"),sQuery(id+"FHMxAyK4CFUKdhS_1.wireOp",EDGE,"1cb9c079-ea9b-4899-8069-e0e3048e911d.sketch_text.stroke-164"),sQuery(id+"FHMxAyK4CFUKdhS_1.wireOp",EDGE,"1cb9c079-ea9b-4899-8069-e0e3048e911d.sketch_text.stroke-165"),sQuery(id+"FHMxAyK4CFUKdhS_1.wireOp",EDGE,"1cb9c079-ea9b-4899-8069-e0e3048e911d.sketch_text.stroke-166"),sQuery(id+"FHMxAyK4CFUKdhS_1.wireOp",EDGE,"1cb9c079-ea9b-4899-8069-e0e3048e911d.sketch_text.stroke-167"),sQuery(id+"FHMxAyK4CFUKdhS_1.wireOp",EDGE,"1cb9c079-ea9b-4899-8069-e0e3048e911d.sketch_text.stroke-168"),sQuery(id+"FHMxAyK4CFUKdhS_1.wireOp",EDGE,"1cb9c079-ea9b-4899-8069-e0e3048e911d.sketch_text.stroke-169"),sQuery(id+"FHMxAyK4CFUKdhS_1.wireOp",EDGE,"1cb9c079-ea9b-4899-8069-e0e3048e911d.sketch_text.stroke-170"),sQuery(id+"FHMxAyK4CFUKdhS_1.wireOp",EDGE,"1cb9c079-ea9b-4899-8069-e0e3048e911d.sketch_text.stroke-171"),sQuery(id+"FHMxAyK4CFUKdhS_1.wireOp",EDGE,"1cb9c079-ea9b-4899-8069-e0e3048e911d.sketch_text.stroke-172"),sQuery(id+"FHMxAyK4CFUKdhS_1.wireOp",EDGE,"1cb9c079-ea9b-4899-8069-e0e3048e911d.sketch_text.stroke-173"),sQuery(id+"FHMxAyK4CFUKdhS_1.wireOp",EDGE,"1cb9c079-ea9b-4899-8069-e0e3048e911d.sketch_text.stroke-174"),sQuery(id+"FHMxAyK4CFUKdhS_1.wireOp",EDGE,"1cb9c079-ea9b-4899-8069-e0e3048e911d.sketch_text.stroke-175"),sQuery(id+"FHMxAyK4CFUKdhS_1.wireOp",EDGE,"1cb9c079-ea9b-4899-8069-e0e3048e911d.sketch_text.stroke-176"),sQuery(id+"FHMxAyK4CFUKdhS_1.wireOp",EDGE,"1cb9c079-ea9b-4899-8069-e0e3048e911d.sketch_text.stroke-177"),sQuery(id+"FHMxAyK4CFUKdhS_1.wireOp",EDGE,"1cb9c079-ea9b-4899-8069-e0e3048e911d.sketch_text.stroke-178"),sQuery(id+"FHMxAyK4CFUKdhS_1.wireOp",EDGE,"1cb9c079-ea9b-4899-8069-e0e3048e911d.sketch_text.stroke-179"),sQuery(id+"FHMxAyK4CFUKdhS_1.wireOp",EDGE,"1cb9c079-ea9b-4899-8069-e0e3048e911d.sketch_text.stroke-180"),sQuery(id+"F2.wireOp",EDGE,"8007402e-1a4e-4a06-85a5-2af08e553504"),subQ2])],"isStart":true}),makeQuery(id+"F3.opExtrude","SWEPT_FACE",FACE,{"disambiguationData":[OSD([subQ2])]})])],"derivedFrom":makeQuery(id+"F3.opExtrude","CAP_EDGE",EDGE,{"disambiguationData":[OSD([subQ2])],"isStart":true})});}
            var Q10;
            {var subQ0=sQuery(id+"F2.wireOp",EDGE,"8007402e-1a4e-4a06-85a5-2af08e553504");var subQ1=sQuery(id+"F0.wireOp",EDGE,"E0.top");var subQ2=sQuery(id+"F2.wireOp",EDGE,"6ee83ff3-586e-4dbe-aaea-af71240543bd");var subQ3=sQuery(id+"F0.wireOp",EDGE,"E0.bottom");Q10=makeQuery(id+"F3.boolean.opBoolean","SPLIT",EDGE,{"disambiguationData":[TD([makeQuery(id+"F1.opExtrude","CAP_FACE",FACE,{"disambiguationData":[OSD([subQ3,subQ1,sQuery(id+"F0.wireOp",EDGE,"E0.left"),sQuery(id+"F0.wireOp",EDGE,"E0.right")])],"isStart":false}),makeQuery(id+"F1.opExtrude","SWEPT_FACE",FACE,{"disambiguationData":[OSD([subQ1])]}),makeQuery(id+"F3.opExtrude","SWEPT_FACE",FACE,{"disambiguationData":[OSD([subQ0])]}),makeQuery(id+"F3.opExtrude","CAP_FACE",FACE,{"disambiguationData":[OSD([subQ3,sQuery(id+"FQ5JFwxVdaqARUP_1.wireOp",EDGE,"fcba4419-a2ee-464f-be9d-58f11bf3418b.sketch_text.stroke-0"),sQuery(id+"FQ5JFwxVdaqARUP_1.wireOp",EDGE,"fcba4419-a2ee-464f-be9d-58f11bf3418b.sketch_text.stroke-1"),sQuery(id+"FQ5JFwxVdaqARUP_1.wireOp",EDGE,"fcba4419-a2ee-464f-be9d-58f11bf3418b.sketch_text.stroke-2"),sQuery(id+"FQ5JFwxVdaqARUP_1.wireOp",EDGE,"fcba4419-a2ee-464f-be9d-58f11bf3418b.sketch_text.stroke-3"),sQuery(id+"FQ5JFwxVdaqARUP_1.wireOp",EDGE,"fcba4419-a2ee-464f-be9d-58f11bf3418b.sketch_text.stroke-4"),sQuery(id+"FQ5JFwxVdaqARUP_1.wireOp",EDGE,"fcba4419-a2ee-464f-be9d-58f11bf3418b.sketch_text.stroke-5"),sQuery(id+"FQ5JFwxVdaqARUP_1.wireOp",EDGE,"fcba4419-a2ee-464f-be9d-58f11bf3418b.sketch_text.stroke-6"),sQuery(id+"FQ5JFwxVdaqARUP_1.wireOp",EDGE,"fcba4419-a2ee-464f-be9d-58f11bf3418b.sketch_text.stroke-7"),sQuery(id+"FQ5JFwxVdaqARUP_1.wireOp",EDGE,"fcba4419-a2ee-464f-be9d-58f11bf3418b.sketch_text.stroke-8"),sQuery(id+"FQ5JFwxVdaqARUP_1.wireOp",EDGE,"fcba4419-a2ee-464f-be9d-58f11bf3418b.sketch_text.stroke-9"),sQuery(id+"FQ5JFwxVdaqARUP_1.wireOp",EDGE,"fcba4419-a2ee-464f-be9d-58f11bf3418b.sketch_text.stroke-10"),sQuery(id+"FQ5JFwxVdaqARUP_1.wireOp",EDGE,"fcba4419-a2ee-464f-be9d-58f11bf3418b.sketch_text.stroke-11"),sQuery(id+"FQ5JFwxVdaqARUP_1.wireOp",EDGE,"fcba4419-a2ee-464f-be9d-58f11bf3418b.sketch_text.stroke-12"),sQuery(id+"FQ5JFwxVdaqARUP_1.wireOp",EDGE,"fcba4419-a2ee-464f-be9d-58f11bf3418b.sketch_text.stroke-13"),sQuery(id+"FQ5JFwxVdaqARUP_1.wireOp",EDGE,"fcba4419-a2ee-464f-be9d-58f11bf3418b.sketch_text.stroke-14"),sQuery(id+"FQ5JFwxVdaqARUP_1.wireOp",EDGE,"fcba4419-a2ee-464f-be9d-58f11bf3418b.sketch_text.stroke-15"),sQuery(id+"FQ5JFwxVdaqARUP_1.wireOp",EDGE,"fcba4419-a2ee-464f-be9d-58f11bf3418b.sketch_text.stroke-16"),sQuery(id+"FQ5JFwxVdaqARUP_1.wireOp",EDGE,"fcba4419-a2ee-464f-be9d-58f11bf3418b.sketch_text.stroke-17"),sQuery(id+"FQ5JFwxVdaqARUP_1.wireOp",EDGE,"fcba4419-a2ee-464f-be9d-58f11bf3418b.sketch_text.stroke-18"),sQuery(id+"FQ5JFwxVdaqARUP_1.wireOp",EDGE,"fcba4419-a2ee-464f-be9d-58f11bf3418b.sketch_text.stroke-19"),sQuery(id+"FQ5JFwxVdaqARUP_1.wireOp",EDGE,"fcba4419-a2ee-464f-be9d-58f11bf3418b.sketch_text.stroke-20"),sQuery(id+"FQ5JFwxVdaqARUP_1.wireOp",EDGE,"fcba4419-a2ee-464f-be9d-58f11bf3418b.sketch_text.stroke-21"),sQuery(id+"FQ5JFwxVdaqARUP_1.wireOp",EDGE,"fcba4419-a2ee-464f-be9d-58f11bf3418b.sketch_text.stroke-22"),sQuery(id+"FQ5JFwxVdaqARUP_1.wireOp",EDGE,"fcba4419-a2ee-464f-be9d-58f11bf3418b.sketch_text.stroke-23"),sQuery(id+"FQ5JFwxVdaqARUP_1.wireOp",EDGE,"fcba4419-a2ee-464f-be9d-58f11bf3418b.sketch_text.stroke-24"),sQuery(id+"FQ5JFwxVdaqARUP_1.wireOp",EDGE,"fcba4419-a2ee-464f-be9d-58f11bf3418b.sketch_text.stroke-25"),sQuery(id+"FQ5JFwxVdaqARUP_1.wireOp",EDGE,"fcba4419-a2ee-464f-be9d-58f11bf3418b.sketch_text.stroke-26"),sQuery(id+"FQ5JFwxVdaqARUP_1.wireOp",EDGE,"fcba4419-a2ee-464f-be9d-58f11bf3418b.sketch_text.stroke-27"),sQuery(id+"FQ5JFwxVdaqARUP_1.wireOp",EDGE,"fcba4419-a2ee-464f-be9d-58f11bf3418b.sketch_text.stroke-28"),sQuery(id+"FQ5JFwxVdaqARUP_1.wireOp",EDGE,"fcba4419-a2ee-464f-be9d-58f11bf3418b.sketch_text.stroke-29"),sQuery(id+"FQ5JFwxVdaqARUP_1.wireOp",EDGE,"fcba4419-a2ee-464f-be9d-58f11bf3418b.sketch_text.stroke-30"),sQuery(id+"FQ5JFwxVdaqARUP_1.wireOp",EDGE,"fcba4419-a2ee-464f-be9d-58f11bf3418b.sketch_text.stroke-31"),sQuery(id+"FQ5JFwxVdaqARUP_1.wireOp",EDGE,"fcba4419-a2ee-464f-be9d-58f11bf3418b.sketch_text.stroke-32"),sQuery(id+"FQ5JFwxVdaqARUP_1.wireOp",EDGE,"fcba4419-a2ee-464f-be9d-58f11bf3418b.sketch_text.stroke-33"),sQuery(id+"FQ5JFwxVdaqARUP_1.wireOp",EDGE,"fcba4419-a2ee-464f-be9d-58f11bf3418b.sketch_text.stroke-34"),sQuery(id+"FQ5JFwxVdaqARUP_1.wireOp",EDGE,"fcba4419-a2ee-464f-be9d-58f11bf3418b.sketch_text.stroke-35"),sQuery(id+"FQ5JFwxVdaqARUP_1.wireOp",EDGE,"fcba4419-a2ee-464f-be9d-58f11bf3418b.sketch_text.stroke-36"),sQuery(id+"FQ5JFwxVdaqARUP_1.wireOp",EDGE,"fcba4419-a2ee-464f-be9d-58f11bf3418b.sketch_text.stroke-37"),sQuery(id+"FQ5JFwxVdaqARUP_1.wireOp",EDGE,"fcba4419-a2ee-464f-be9d-58f11bf3418b.sketch_text.stroke-38"),sQuery(id+"FQ5JFwxVdaqARUP_1.wireOp",EDGE,"fcba4419-a2ee-464f-be9d-58f11bf3418b.sketch_text.stroke-39"),sQuery(id+"FQ5JFwxVdaqARUP_1.wireOp",EDGE,"fcba4419-a2ee-464f-be9d-58f11bf3418b.sketch_text.stroke-40"),sQuery(id+"FQ5JFwxVdaqARUP_1.wireOp",EDGE,"fcba4419-a2ee-464f-be9d-58f11bf3418b.sketch_text.stroke-41"),sQuery(id+"FQ5JFwxVdaqARUP_1.wireOp",EDGE,"fcba4419-a2ee-464f-be9d-58f11bf3418b.sketch_text.stroke-42"),sQuery(id+"FQ5JFwxVdaqARUP_1.wireOp",EDGE,"fcba4419-a2ee-464f-be9d-58f11bf3418b.sketch_text.stroke-43"),sQuery(id+"FQ5JFwxVdaqARUP_1.wireOp",EDGE,"fcba4419-a2ee-464f-be9d-58f11bf3418b.sketch_text.stroke-44"),sQuery(id+"FQ5JFwxVdaqARUP_1.wireOp",EDGE,"fcba4419-a2ee-464f-be9d-58f11bf3418b.sketch_text.stroke-45"),sQuery(id+"FQ5JFwxVdaqARUP_1.wireOp",EDGE,"fcba4419-a2ee-464f-be9d-58f11bf3418b.sketch_text.stroke-46"),sQuery(id+"FQ5JFwxVdaqARUP_1.wireOp",EDGE,"fcba4419-a2ee-464f-be9d-58f11bf3418b.sketch_text.stroke-47"),sQuery(id+"FQ5JFwxVdaqARUP_1.wireOp",EDGE,"fcba4419-a2ee-464f-be9d-58f11bf3418b.sketch_text.stroke-48"),sQuery(id+"FQ5JFwxVdaqARUP_1.wireOp",EDGE,"fcba4419-a2ee-464f-be9d-58f11bf3418b.sketch_text.stroke-49"),sQuery(id+"FQ5JFwxVdaqARUP_1.wireOp",EDGE,"fcba4419-a2ee-464f-be9d-58f11bf3418b.sketch_text.stroke-50"),sQuery(id+"FQ5JFwxVdaqARUP_1.wireOp",EDGE,"fcba4419-a2ee-464f-be9d-58f11bf3418b.sketch_text.stroke-51"),sQuery(id+"FQ5JFwxVdaqARUP_1.wireOp",EDGE,"fcba4419-a2ee-464f-be9d-58f11bf3418b.sketch_text.stroke-52"),sQuery(id+"FQ5JFwxVdaqARUP_1.wireOp",EDGE,"fcba4419-a2ee-464f-be9d-58f11bf3418b.sketch_text.stroke-53"),sQuery(id+"FQ5JFwxVdaqARUP_1.wireOp",EDGE,"fcba4419-a2ee-464f-be9d-58f11bf3418b.sketch_text.stroke-54"),sQuery(id+"FQ5JFwxVdaqARUP_1.wireOp",EDGE,"fcba4419-a2ee-464f-be9d-58f11bf3418b.sketch_text.stroke-55"),sQuery(id+"FQ5JFwxVdaqARUP_1.wireOp",EDGE,"fcba4419-a2ee-464f-be9d-58f11bf3418b.sketch_text.stroke-56"),sQuery(id+"FQ5JFwxVdaqARUP_1.wireOp",EDGE,"fcba4419-a2ee-464f-be9d-58f11bf3418b.sketch_text.stroke-57"),sQuery(id+"FQ5JFwxVdaqARUP_1.wireOp",EDGE,"fcba4419-a2ee-464f-be9d-58f11bf3418b.sketch_text.stroke-58"),sQuery(id+"FQ5JFwxVdaqARUP_1.wireOp",EDGE,"fcba4419-a2ee-464f-be9d-58f11bf3418b.sketch_text.stroke-59"),sQuery(id+"FQ5JFwxVdaqARUP_1.wireOp",EDGE,"fcba4419-a2ee-464f-be9d-58f11bf3418b.sketch_text.stroke-60"),sQuery(id+"FQ5JFwxVdaqARUP_1.wireOp",EDGE,"fcba4419-a2ee-464f-be9d-58f11bf3418b.sketch_text.stroke-61"),sQuery(id+"FQ5JFwxVdaqARUP_1.wireOp",EDGE,"fcba4419-a2ee-464f-be9d-58f11bf3418b.sketch_text.stroke-62"),sQuery(id+"FQ5JFwxVdaqARUP_1.wireOp",EDGE,"fcba4419-a2ee-464f-be9d-58f11bf3418b.sketch_text.stroke-63"),sQuery(id+"FQ5JFwxVdaqARUP_1.wireOp",EDGE,"fcba4419-a2ee-464f-be9d-58f11bf3418b.sketch_text.stroke-64"),sQuery(id+"FQ5JFwxVdaqARUP_1.wireOp",EDGE,"fcba4419-a2ee-464f-be9d-58f11bf3418b.sketch_text.stroke-65"),sQuery(id+"FQ5JFwxVdaqARUP_1.wireOp",EDGE,"fcba4419-a2ee-464f-be9d-58f11bf3418b.sketch_text.stroke-66"),sQuery(id+"FQ5JFwxVdaqARUP_1.wireOp",EDGE,"fcba4419-a2ee-464f-be9d-58f11bf3418b.sketch_text.stroke-67"),sQuery(id+"FQ5JFwxVdaqARUP_1.wireOp",EDGE,"fcba4419-a2ee-464f-be9d-58f11bf3418b.sketch_text.stroke-68"),sQuery(id+"FQ5JFwxVdaqARUP_1.wireOp",EDGE,"fcba4419-a2ee-464f-be9d-58f11bf3418b.sketch_text.stroke-69"),sQuery(id+"FQ5JFwxVdaqARUP_1.wireOp",EDGE,"fcba4419-a2ee-464f-be9d-58f11bf3418b.sketch_text.stroke-70"),sQuery(id+"FQ5JFwxVdaqARUP_1.wireOp",EDGE,"fcba4419-a2ee-464f-be9d-58f11bf3418b.sketch_text.stroke-71"),sQuery(id+"FQ5JFwxVdaqARUP_1.wireOp",EDGE,"fcba4419-a2ee-464f-be9d-58f11bf3418b.sketch_text.stroke-72"),sQuery(id+"FQ5JFwxVdaqARUP_1.wireOp",EDGE,"fcba4419-a2ee-464f-be9d-58f11bf3418b.sketch_text.stroke-73"),sQuery(id+"FQ5JFwxVdaqARUP_1.wireOp",EDGE,"fcba4419-a2ee-464f-be9d-58f11bf3418b.sketch_text.stroke-74"),sQuery(id+"FQ5JFwxVdaqARUP_1.wireOp",EDGE,"fcba4419-a2ee-464f-be9d-58f11bf3418b.sketch_text.stroke-75"),sQuery(id+"FQ5JFwxVdaqARUP_1.wireOp",EDGE,"fcba4419-a2ee-464f-be9d-58f11bf3418b.sketch_text.stroke-76"),sQuery(id+"FQ5JFwxVdaqARUP_1.wireOp",EDGE,"fcba4419-a2ee-464f-be9d-58f11bf3418b.sketch_text.stroke-77"),sQuery(id+"FQ5JFwxVdaqARUP_1.wireOp",EDGE,"fcba4419-a2ee-464f-be9d-58f11bf3418b.sketch_text.stroke-78"),sQuery(id+"FQ5JFwxVdaqARUP_1.wireOp",EDGE,"fcba4419-a2ee-464f-be9d-58f11bf3418b.sketch_text.stroke-79"),sQuery(id+"FQ5JFwxVdaqARUP_1.wireOp",EDGE,"fcba4419-a2ee-464f-be9d-58f11bf3418b.sketch_text.stroke-80"),sQuery(id+"FQ5JFwxVdaqARUP_1.wireOp",EDGE,"fcba4419-a2ee-464f-be9d-58f11bf3418b.sketch_text.stroke-81"),sQuery(id+"FQ5JFwxVdaqARUP_1.wireOp",EDGE,"fcba4419-a2ee-464f-be9d-58f11bf3418b.sketch_text.stroke-82"),sQuery(id+"FQ5JFwxVdaqARUP_1.wireOp",EDGE,"fcba4419-a2ee-464f-be9d-58f11bf3418b.sketch_text.stroke-83"),sQuery(id+"FQ5JFwxVdaqARUP_1.wireOp",EDGE,"fcba4419-a2ee-464f-be9d-58f11bf3418b.sketch_text.stroke-84"),sQuery(id+"FQ5JFwxVdaqARUP_1.wireOp",EDGE,"fcba4419-a2ee-464f-be9d-58f11bf3418b.sketch_text.stroke-85"),sQuery(id+"FQ5JFwxVdaqARUP_1.wireOp",EDGE,"fcba4419-a2ee-464f-be9d-58f11bf3418b.sketch_text.stroke-86"),sQuery(id+"FQ5JFwxVdaqARUP_1.wireOp",EDGE,"fcba4419-a2ee-464f-be9d-58f11bf3418b.sketch_text.stroke-87"),sQuery(id+"FQ5JFwxVdaqARUP_1.wireOp",EDGE,"fcba4419-a2ee-464f-be9d-58f11bf3418b.sketch_text.stroke-88"),sQuery(id+"FQ5JFwxVdaqARUP_1.wireOp",EDGE,"fcba4419-a2ee-464f-be9d-58f11bf3418b.sketch_text.stroke-89"),sQuery(id+"FQ5JFwxVdaqARUP_1.wireOp",EDGE,"fcba4419-a2ee-464f-be9d-58f11bf3418b.sketch_text.stroke-90"),sQuery(id+"FQ5JFwxVdaqARUP_1.wireOp",EDGE,"fcba4419-a2ee-464f-be9d-58f11bf3418b.sketch_text.stroke-91"),sQuery(id+"FQ5JFwxVdaqARUP_1.wireOp",EDGE,"fcba4419-a2ee-464f-be9d-58f11bf3418b.sketch_text.stroke-92"),sQuery(id+"FQ5JFwxVdaqARUP_1.wireOp",EDGE,"fcba4419-a2ee-464f-be9d-58f11bf3418b.sketch_text.stroke-93"),sQuery(id+"FQ5JFwxVdaqARUP_1.wireOp",EDGE,"fcba4419-a2ee-464f-be9d-58f11bf3418b.sketch_text.stroke-94"),sQuery(id+"FQ5JFwxVdaqARUP_1.wireOp",EDGE,"fcba4419-a2ee-464f-be9d-58f11bf3418b.sketch_text.stroke-95"),sQuery(id+"FQ5JFwxVdaqARUP_1.wireOp",EDGE,"fcba4419-a2ee-464f-be9d-58f11bf3418b.sketch_text.stroke-96"),sQuery(id+"FQ5JFwxVdaqARUP_1.wireOp",EDGE,"fcba4419-a2ee-464f-be9d-58f11bf3418b.sketch_text.stroke-97"),sQuery(id+"FQ5JFwxVdaqARUP_1.wireOp",EDGE,"fcba4419-a2ee-464f-be9d-58f11bf3418b.sketch_text.stroke-98"),sQuery(id+"FQ5JFwxVdaqARUP_1.wireOp",EDGE,"fcba4419-a2ee-464f-be9d-58f11bf3418b.sketch_text.stroke-99"),sQuery(id+"FQ5JFwxVdaqARUP_1.wireOp",EDGE,"fcba4419-a2ee-464f-be9d-58f11bf3418b.sketch_text.stroke-100"),sQuery(id+"FQ5JFwxVdaqARUP_1.wireOp",EDGE,"fcba4419-a2ee-464f-be9d-58f11bf3418b.sketch_text.stroke-101"),sQuery(id+"FQ5JFwxVdaqARUP_1.wireOp",EDGE,"fcba4419-a2ee-464f-be9d-58f11bf3418b.sketch_text.stroke-102"),sQuery(id+"FQ5JFwxVdaqARUP_1.wireOp",EDGE,"fcba4419-a2ee-464f-be9d-58f11bf3418b.sketch_text.stroke-103"),sQuery(id+"FQ5JFwxVdaqARUP_1.wireOp",EDGE,"fcba4419-a2ee-464f-be9d-58f11bf3418b.sketch_text.stroke-104"),sQuery(id+"FQ5JFwxVdaqARUP_1.wireOp",EDGE,"fcba4419-a2ee-464f-be9d-58f11bf3418b.sketch_text.stroke-105"),sQuery(id+"FQ5JFwxVdaqARUP_1.wireOp",EDGE,"fcba4419-a2ee-464f-be9d-58f11bf3418b.sketch_text.stroke-106"),sQuery(id+"FQ5JFwxVdaqARUP_1.wireOp",EDGE,"fcba4419-a2ee-464f-be9d-58f11bf3418b.sketch_text.stroke-107"),sQuery(id+"FQ5JFwxVdaqARUP_1.wireOp",EDGE,"fcba4419-a2ee-464f-be9d-58f11bf3418b.sketch_text.stroke-108"),sQuery(id+"FQ5JFwxVdaqARUP_1.wireOp",EDGE,"fcba4419-a2ee-464f-be9d-58f11bf3418b.sketch_text.stroke-109"),sQuery(id+"FQ5JFwxVdaqARUP_1.wireOp",EDGE,"fcba4419-a2ee-464f-be9d-58f11bf3418b.sketch_text.stroke-110"),sQuery(id+"FQ5JFwxVdaqARUP_1.wireOp",EDGE,"fcba4419-a2ee-464f-be9d-58f11bf3418b.sketch_text.stroke-111"),sQuery(id+"FQ5JFwxVdaqARUP_1.wireOp",EDGE,"fcba4419-a2ee-464f-be9d-58f11bf3418b.sketch_text.stroke-112"),sQuery(id+"FQ5JFwxVdaqARUP_1.wireOp",EDGE,"fcba4419-a2ee-464f-be9d-58f11bf3418b.sketch_text.stroke-113"),sQuery(id+"FQ5JFwxVdaqARUP_1.wireOp",EDGE,"fcba4419-a2ee-464f-be9d-58f11bf3418b.sketch_text.stroke-114"),sQuery(id+"FQ5JFwxVdaqARUP_1.wireOp",EDGE,"fcba4419-a2ee-464f-be9d-58f11bf3418b.sketch_text.stroke-115"),sQuery(id+"FQ5JFwxVdaqARUP_1.wireOp",EDGE,"fcba4419-a2ee-464f-be9d-58f11bf3418b.sketch_text.stroke-116"),sQuery(id+"FQ5JFwxVdaqARUP_1.wireOp",EDGE,"fcba4419-a2ee-464f-be9d-58f11bf3418b.sketch_text.stroke-117"),sQuery(id+"FQ5JFwxVdaqARUP_1.wireOp",EDGE,"fcba4419-a2ee-464f-be9d-58f11bf3418b.sketch_text.stroke-118"),sQuery(id+"FQ5JFwxVdaqARUP_1.wireOp",EDGE,"fcba4419-a2ee-464f-be9d-58f11bf3418b.sketch_text.stroke-119"),sQuery(id+"FQ5JFwxVdaqARUP_1.wireOp",EDGE,"fcba4419-a2ee-464f-be9d-58f11bf3418b.sketch_text.stroke-120"),sQuery(id+"FQ5JFwxVdaqARUP_1.wireOp",EDGE,"fcba4419-a2ee-464f-be9d-58f11bf3418b.sketch_text.stroke-121"),sQuery(id+"FQ5JFwxVdaqARUP_1.wireOp",EDGE,"fcba4419-a2ee-464f-be9d-58f11bf3418b.sketch_text.stroke-122"),sQuery(id+"FQ5JFwxVdaqARUP_1.wireOp",EDGE,"fcba4419-a2ee-464f-be9d-58f11bf3418b.sketch_text.stroke-123"),sQuery(id+"FQ5JFwxVdaqARUP_1.wireOp",EDGE,"fcba4419-a2ee-464f-be9d-58f11bf3418b.sketch_text.stroke-124"),sQuery(id+"FQ5JFwxVdaqARUP_1.wireOp",EDGE,"fcba4419-a2ee-464f-be9d-58f11bf3418b.sketch_text.stroke-125"),sQuery(id+"FQ5JFwxVdaqARUP_1.wireOp",EDGE,"fcba4419-a2ee-464f-be9d-58f11bf3418b.sketch_text.stroke-126"),sQuery(id+"FQ5JFwxVdaqARUP_1.wireOp",EDGE,"fcba4419-a2ee-464f-be9d-58f11bf3418b.sketch_text.stroke-127"),sQuery(id+"FQ5JFwxVdaqARUP_1.wireOp",EDGE,"fcba4419-a2ee-464f-be9d-58f11bf3418b.sketch_text.stroke-128"),sQuery(id+"FQ5JFwxVdaqARUP_1.wireOp",EDGE,"fcba4419-a2ee-464f-be9d-58f11bf3418b.sketch_text.stroke-129"),sQuery(id+"FQ5JFwxVdaqARUP_1.wireOp",EDGE,"fcba4419-a2ee-464f-be9d-58f11bf3418b.sketch_text.stroke-130"),sQuery(id+"FQ5JFwxVdaqARUP_1.wireOp",EDGE,"fcba4419-a2ee-464f-be9d-58f11bf3418b.sketch_text.stroke-131"),sQuery(id+"FQ5JFwxVdaqARUP_1.wireOp",EDGE,"fcba4419-a2ee-464f-be9d-58f11bf3418b.sketch_text.stroke-132"),sQuery(id+"FQ5JFwxVdaqARUP_1.wireOp",EDGE,"fcba4419-a2ee-464f-be9d-58f11bf3418b.sketch_text.stroke-133"),sQuery(id+"FQ5JFwxVdaqARUP_1.wireOp",EDGE,"fcba4419-a2ee-464f-be9d-58f11bf3418b.sketch_text.stroke-134"),sQuery(id+"FQ5JFwxVdaqARUP_1.wireOp",EDGE,"fcba4419-a2ee-464f-be9d-58f11bf3418b.sketch_text.stroke-135"),sQuery(id+"FQ5JFwxVdaqARUP_1.wireOp",EDGE,"fcba4419-a2ee-464f-be9d-58f11bf3418b.sketch_text.stroke-136"),sQuery(id+"FQ5JFwxVdaqARUP_1.wireOp",EDGE,"fcba4419-a2ee-464f-be9d-58f11bf3418b.sketch_text.stroke-137"),sQuery(id+"FQ5JFwxVdaqARUP_1.wireOp",EDGE,"fcba4419-a2ee-464f-be9d-58f11bf3418b.sketch_text.stroke-138"),sQuery(id+"FQ5JFwxVdaqARUP_1.wireOp",EDGE,"fcba4419-a2ee-464f-be9d-58f11bf3418b.sketch_text.stroke-139"),sQuery(id+"FQ5JFwxVdaqARUP_1.wireOp",EDGE,"fcba4419-a2ee-464f-be9d-58f11bf3418b.sketch_text.stroke-140"),sQuery(id+"FQ5JFwxVdaqARUP_1.wireOp",EDGE,"fcba4419-a2ee-464f-be9d-58f11bf3418b.sketch_text.stroke-141"),sQuery(id+"FQ5JFwxVdaqARUP_1.wireOp",EDGE,"fcba4419-a2ee-464f-be9d-58f11bf3418b.sketch_text.stroke-142"),sQuery(id+"FQ5JFwxVdaqARUP_1.wireOp",EDGE,"fcba4419-a2ee-464f-be9d-58f11bf3418b.sketch_text.stroke-143"),sQuery(id+"FQ5JFwxVdaqARUP_1.wireOp",EDGE,"fcba4419-a2ee-464f-be9d-58f11bf3418b.sketch_text.stroke-144"),sQuery(id+"FQ5JFwxVdaqARUP_1.wireOp",EDGE,"fcba4419-a2ee-464f-be9d-58f11bf3418b.sketch_text.stroke-145"),sQuery(id+"FQ5JFwxVdaqARUP_1.wireOp",EDGE,"fcba4419-a2ee-464f-be9d-58f11bf3418b.sketch_text.stroke-146"),sQuery(id+"FQ5JFwxVdaqARUP_1.wireOp",EDGE,"fcba4419-a2ee-464f-be9d-58f11bf3418b.sketch_text.stroke-147"),sQuery(id+"FQ5JFwxVdaqARUP_1.wireOp",EDGE,"fcba4419-a2ee-464f-be9d-58f11bf3418b.sketch_text.stroke-148"),sQuery(id+"FQ5JFwxVdaqARUP_1.wireOp",EDGE,"fcba4419-a2ee-464f-be9d-58f11bf3418b.sketch_text.stroke-149"),sQuery(id+"FQ5JFwxVdaqARUP_1.wireOp",EDGE,"fcba4419-a2ee-464f-be9d-58f11bf3418b.sketch_text.stroke-150"),sQuery(id+"FQ5JFwxVdaqARUP_1.wireOp",EDGE,"fcba4419-a2ee-464f-be9d-58f11bf3418b.sketch_text.stroke-151"),sQuery(id+"FQ5JFwxVdaqARUP_1.wireOp",EDGE,"fcba4419-a2ee-464f-be9d-58f11bf3418b.sketch_text.stroke-152"),sQuery(id+"FQ5JFwxVdaqARUP_1.wireOp",EDGE,"fcba4419-a2ee-464f-be9d-58f11bf3418b.sketch_text.stroke-153"),sQuery(id+"FQ5JFwxVdaqARUP_1.wireOp",EDGE,"fcba4419-a2ee-464f-be9d-58f11bf3418b.sketch_text.stroke-154"),sQuery(id+"FQ5JFwxVdaqARUP_1.wireOp",EDGE,"fcba4419-a2ee-464f-be9d-58f11bf3418b.sketch_text.stroke-155"),sQuery(id+"FQ5JFwxVdaqARUP_1.wireOp",EDGE,"fcba4419-a2ee-464f-be9d-58f11bf3418b.sketch_text.stroke-156"),sQuery(id+"FQ5JFwxVdaqARUP_1.wireOp",EDGE,"fcba4419-a2ee-464f-be9d-58f11bf3418b.sketch_text.stroke-157"),sQuery(id+"FQ5JFwxVdaqARUP_1.wireOp",EDGE,"fcba4419-a2ee-464f-be9d-58f11bf3418b.sketch_text.stroke-158"),sQuery(id+"FQ5JFwxVdaqARUP_1.wireOp",EDGE,"fcba4419-a2ee-464f-be9d-58f11bf3418b.sketch_text.stroke-159"),sQuery(id+"FQ5JFwxVdaqARUP_1.wireOp",EDGE,"fcba4419-a2ee-464f-be9d-58f11bf3418b.sketch_text.stroke-160"),sQuery(id+"FQ5JFwxVdaqARUP_1.wireOp",EDGE,"fcba4419-a2ee-464f-be9d-58f11bf3418b.sketch_text.stroke-161"),sQuery(id+"FQ5JFwxVdaqARUP_1.wireOp",EDGE,"fcba4419-a2ee-464f-be9d-58f11bf3418b.sketch_text.stroke-162"),sQuery(id+"FQ5JFwxVdaqARUP_1.wireOp",EDGE,"fcba4419-a2ee-464f-be9d-58f11bf3418b.sketch_text.stroke-163"),sQuery(id+"FQ5JFwxVdaqARUP_1.wireOp",EDGE,"fcba4419-a2ee-464f-be9d-58f11bf3418b.sketch_text.stroke-164"),sQuery(id+"FQ5JFwxVdaqARUP_1.wireOp",EDGE,"fcba4419-a2ee-464f-be9d-58f11bf3418b.sketch_text.stroke-165"),sQuery(id+"FQ5JFwxVdaqARUP_1.wireOp",EDGE,"fcba4419-a2ee-464f-be9d-58f11bf3418b.sketch_text.stroke-166"),sQuery(id+"FQ5JFwxVdaqARUP_1.wireOp",EDGE,"fcba4419-a2ee-464f-be9d-58f11bf3418b.sketch_text.stroke-167"),sQuery(id+"FQ5JFwxVdaqARUP_1.wireOp",EDGE,"fcba4419-a2ee-464f-be9d-58f11bf3418b.sketch_text.stroke-168"),sQuery(id+"FQ5JFwxVdaqARUP_1.wireOp",EDGE,"fcba4419-a2ee-464f-be9d-58f11bf3418b.sketch_text.stroke-169"),sQuery(id+"FQ5JFwxVdaqARUP_1.wireOp",EDGE,"fcba4419-a2ee-464f-be9d-58f11bf3418b.sketch_text.stroke-170"),sQuery(id+"FQ5JFwxVdaqARUP_1.wireOp",EDGE,"fcba4419-a2ee-464f-be9d-58f11bf3418b.sketch_text.stroke-171"),sQuery(id+"FQ5JFwxVdaqARUP_1.wireOp",EDGE,"fcba4419-a2ee-464f-be9d-58f11bf3418b.sketch_text.stroke-172"),sQuery(id+"FQ5JFwxVdaqARUP_1.wireOp",EDGE,"fcba4419-a2ee-464f-be9d-58f11bf3418b.sketch_text.stroke-173"),sQuery(id+"FHMxAyK4CFUKdhS_1.wireOp",EDGE,"1cb9c079-ea9b-4899-8069-e0e3048e911d.sketch_text.stroke-0"),sQuery(id+"FHMxAyK4CFUKdhS_1.wireOp",EDGE,"1cb9c079-ea9b-4899-8069-e0e3048e911d.sketch_text.stroke-1"),sQuery(id+"FHMxAyK4CFUKdhS_1.wireOp",EDGE,"1cb9c079-ea9b-4899-8069-e0e3048e911d.sketch_text.stroke-2"),sQuery(id+"FHMxAyK4CFUKdhS_1.wireOp",EDGE,"1cb9c079-ea9b-4899-8069-e0e3048e911d.sketch_text.stroke-3"),sQuery(id+"FHMxAyK4CFUKdhS_1.wireOp",EDGE,"1cb9c079-ea9b-4899-8069-e0e3048e911d.sketch_text.stroke-4"),sQuery(id+"FHMxAyK4CFUKdhS_1.wireOp",EDGE,"1cb9c079-ea9b-4899-8069-e0e3048e911d.sketch_text.stroke-5"),sQuery(id+"FHMxAyK4CFUKdhS_1.wireOp",EDGE,"1cb9c079-ea9b-4899-8069-e0e3048e911d.sketch_text.stroke-6"),sQuery(id+"FHMxAyK4CFUKdhS_1.wireOp",EDGE,"1cb9c079-ea9b-4899-8069-e0e3048e911d.sketch_text.stroke-7"),sQuery(id+"FHMxAyK4CFUKdhS_1.wireOp",EDGE,"1cb9c079-ea9b-4899-8069-e0e3048e911d.sketch_text.stroke-8"),sQuery(id+"FHMxAyK4CFUKdhS_1.wireOp",EDGE,"1cb9c079-ea9b-4899-8069-e0e3048e911d.sketch_text.stroke-9"),sQuery(id+"FHMxAyK4CFUKdhS_1.wireOp",EDGE,"1cb9c079-ea9b-4899-8069-e0e3048e911d.sketch_text.stroke-10"),sQuery(id+"FHMxAyK4CFUKdhS_1.wireOp",EDGE,"1cb9c079-ea9b-4899-8069-e0e3048e911d.sketch_text.stroke-11"),sQuery(id+"FHMxAyK4CFUKdhS_1.wireOp",EDGE,"1cb9c079-ea9b-4899-8069-e0e3048e911d.sketch_text.stroke-12"),sQuery(id+"FHMxAyK4CFUKdhS_1.wireOp",EDGE,"1cb9c079-ea9b-4899-8069-e0e3048e911d.sketch_text.stroke-13"),sQuery(id+"FHMxAyK4CFUKdhS_1.wireOp",EDGE,"1cb9c079-ea9b-4899-8069-e0e3048e911d.sketch_text.stroke-14"),sQuery(id+"FHMxAyK4CFUKdhS_1.wireOp",EDGE,"1cb9c079-ea9b-4899-8069-e0e3048e911d.sketch_text.stroke-15"),sQuery(id+"FHMxAyK4CFUKdhS_1.wireOp",EDGE,"1cb9c079-ea9b-4899-8069-e0e3048e911d.sketch_text.stroke-16"),sQuery(id+"FHMxAyK4CFUKdhS_1.wireOp",EDGE,"1cb9c079-ea9b-4899-8069-e0e3048e911d.sketch_text.stroke-17"),sQuery(id+"FHMxAyK4CFUKdhS_1.wireOp",EDGE,"1cb9c079-ea9b-4899-8069-e0e3048e911d.sketch_text.stroke-18"),sQuery(id+"FHMxAyK4CFUKdhS_1.wireOp",EDGE,"1cb9c079-ea9b-4899-8069-e0e3048e911d.sketch_text.stroke-19"),sQuery(id+"FHMxAyK4CFUKdhS_1.wireOp",EDGE,"1cb9c079-ea9b-4899-8069-e0e3048e911d.sketch_text.stroke-20"),sQuery(id+"FHMxAyK4CFUKdhS_1.wireOp",EDGE,"1cb9c079-ea9b-4899-8069-e0e3048e911d.sketch_text.stroke-21"),sQuery(id+"FHMxAyK4CFUKdhS_1.wireOp",EDGE,"1cb9c079-ea9b-4899-8069-e0e3048e911d.sketch_text.stroke-22"),sQuery(id+"FHMxAyK4CFUKdhS_1.wireOp",EDGE,"1cb9c079-ea9b-4899-8069-e0e3048e911d.sketch_text.stroke-23"),sQuery(id+"FHMxAyK4CFUKdhS_1.wireOp",EDGE,"1cb9c079-ea9b-4899-8069-e0e3048e911d.sketch_text.stroke-24"),sQuery(id+"FHMxAyK4CFUKdhS_1.wireOp",EDGE,"1cb9c079-ea9b-4899-8069-e0e3048e911d.sketch_text.stroke-25"),sQuery(id+"FHMxAyK4CFUKdhS_1.wireOp",EDGE,"1cb9c079-ea9b-4899-8069-e0e3048e911d.sketch_text.stroke-26"),sQuery(id+"FHMxAyK4CFUKdhS_1.wireOp",EDGE,"1cb9c079-ea9b-4899-8069-e0e3048e911d.sketch_text.stroke-27"),sQuery(id+"FHMxAyK4CFUKdhS_1.wireOp",EDGE,"1cb9c079-ea9b-4899-8069-e0e3048e911d.sketch_text.stroke-28"),sQuery(id+"FHMxAyK4CFUKdhS_1.wireOp",EDGE,"1cb9c079-ea9b-4899-8069-e0e3048e911d.sketch_text.stroke-29"),sQuery(id+"FHMxAyK4CFUKdhS_1.wireOp",EDGE,"1cb9c079-ea9b-4899-8069-e0e3048e911d.sketch_text.stroke-30"),sQuery(id+"FHMxAyK4CFUKdhS_1.wireOp",EDGE,"1cb9c079-ea9b-4899-8069-e0e3048e911d.sketch_text.stroke-31"),sQuery(id+"FHMxAyK4CFUKdhS_1.wireOp",EDGE,"1cb9c079-ea9b-4899-8069-e0e3048e911d.sketch_text.stroke-32"),sQuery(id+"FHMxAyK4CFUKdhS_1.wireOp",EDGE,"1cb9c079-ea9b-4899-8069-e0e3048e911d.sketch_text.stroke-33"),sQuery(id+"FHMxAyK4CFUKdhS_1.wireOp",EDGE,"1cb9c079-ea9b-4899-8069-e0e3048e911d.sketch_text.stroke-34"),sQuery(id+"FHMxAyK4CFUKdhS_1.wireOp",EDGE,"1cb9c079-ea9b-4899-8069-e0e3048e911d.sketch_text.stroke-35"),sQuery(id+"FHMxAyK4CFUKdhS_1.wireOp",EDGE,"1cb9c079-ea9b-4899-8069-e0e3048e911d.sketch_text.stroke-36"),sQuery(id+"FHMxAyK4CFUKdhS_1.wireOp",EDGE,"1cb9c079-ea9b-4899-8069-e0e3048e911d.sketch_text.stroke-37"),sQuery(id+"FHMxAyK4CFUKdhS_1.wireOp",EDGE,"1cb9c079-ea9b-4899-8069-e0e3048e911d.sketch_text.stroke-38"),sQuery(id+"FHMxAyK4CFUKdhS_1.wireOp",EDGE,"1cb9c079-ea9b-4899-8069-e0e3048e911d.sketch_text.stroke-39"),sQuery(id+"FHMxAyK4CFUKdhS_1.wireOp",EDGE,"1cb9c079-ea9b-4899-8069-e0e3048e911d.sketch_text.stroke-40"),sQuery(id+"FHMxAyK4CFUKdhS_1.wireOp",EDGE,"1cb9c079-ea9b-4899-8069-e0e3048e911d.sketch_text.stroke-41"),sQuery(id+"FHMxAyK4CFUKdhS_1.wireOp",EDGE,"1cb9c079-ea9b-4899-8069-e0e3048e911d.sketch_text.stroke-42"),sQuery(id+"FHMxAyK4CFUKdhS_1.wireOp",EDGE,"1cb9c079-ea9b-4899-8069-e0e3048e911d.sketch_text.stroke-43"),sQuery(id+"FHMxAyK4CFUKdhS_1.wireOp",EDGE,"1cb9c079-ea9b-4899-8069-e0e3048e911d.sketch_text.stroke-44"),sQuery(id+"FHMxAyK4CFUKdhS_1.wireOp",EDGE,"1cb9c079-ea9b-4899-8069-e0e3048e911d.sketch_text.stroke-45"),sQuery(id+"FHMxAyK4CFUKdhS_1.wireOp",EDGE,"1cb9c079-ea9b-4899-8069-e0e3048e911d.sketch_text.stroke-46"),sQuery(id+"FHMxAyK4CFUKdhS_1.wireOp",EDGE,"1cb9c079-ea9b-4899-8069-e0e3048e911d.sketch_text.stroke-47"),sQuery(id+"FHMxAyK4CFUKdhS_1.wireOp",EDGE,"1cb9c079-ea9b-4899-8069-e0e3048e911d.sketch_text.stroke-48"),sQuery(id+"FHMxAyK4CFUKdhS_1.wireOp",EDGE,"1cb9c079-ea9b-4899-8069-e0e3048e911d.sketch_text.stroke-49"),sQuery(id+"FHMxAyK4CFUKdhS_1.wireOp",EDGE,"1cb9c079-ea9b-4899-8069-e0e3048e911d.sketch_text.stroke-50"),sQuery(id+"FHMxAyK4CFUKdhS_1.wireOp",EDGE,"1cb9c079-ea9b-4899-8069-e0e3048e911d.sketch_text.stroke-51"),sQuery(id+"FHMxAyK4CFUKdhS_1.wireOp",EDGE,"1cb9c079-ea9b-4899-8069-e0e3048e911d.sketch_text.stroke-52"),sQuery(id+"FHMxAyK4CFUKdhS_1.wireOp",EDGE,"1cb9c079-ea9b-4899-8069-e0e3048e911d.sketch_text.stroke-53"),sQuery(id+"FHMxAyK4CFUKdhS_1.wireOp",EDGE,"1cb9c079-ea9b-4899-8069-e0e3048e911d.sketch_text.stroke-54"),sQuery(id+"FHMxAyK4CFUKdhS_1.wireOp",EDGE,"1cb9c079-ea9b-4899-8069-e0e3048e911d.sketch_text.stroke-55"),sQuery(id+"FHMxAyK4CFUKdhS_1.wireOp",EDGE,"1cb9c079-ea9b-4899-8069-e0e3048e911d.sketch_text.stroke-56"),sQuery(id+"FHMxAyK4CFUKdhS_1.wireOp",EDGE,"1cb9c079-ea9b-4899-8069-e0e3048e911d.sketch_text.stroke-57"),sQuery(id+"FHMxAyK4CFUKdhS_1.wireOp",EDGE,"1cb9c079-ea9b-4899-8069-e0e3048e911d.sketch_text.stroke-58"),sQuery(id+"FHMxAyK4CFUKdhS_1.wireOp",EDGE,"1cb9c079-ea9b-4899-8069-e0e3048e911d.sketch_text.stroke-59"),sQuery(id+"FHMxAyK4CFUKdhS_1.wireOp",EDGE,"1cb9c079-ea9b-4899-8069-e0e3048e911d.sketch_text.stroke-60"),sQuery(id+"FHMxAyK4CFUKdhS_1.wireOp",EDGE,"1cb9c079-ea9b-4899-8069-e0e3048e911d.sketch_text.stroke-61"),sQuery(id+"FHMxAyK4CFUKdhS_1.wireOp",EDGE,"1cb9c079-ea9b-4899-8069-e0e3048e911d.sketch_text.stroke-62"),sQuery(id+"FHMxAyK4CFUKdhS_1.wireOp",EDGE,"1cb9c079-ea9b-4899-8069-e0e3048e911d.sketch_text.stroke-71"),sQuery(id+"FHMxAyK4CFUKdhS_1.wireOp",EDGE,"1cb9c079-ea9b-4899-8069-e0e3048e911d.sketch_text.stroke-72"),sQuery(id+"FHMxAyK4CFUKdhS_1.wireOp",EDGE,"1cb9c079-ea9b-4899-8069-e0e3048e911d.sketch_text.stroke-73"),sQuery(id+"FHMxAyK4CFUKdhS_1.wireOp",EDGE,"1cb9c079-ea9b-4899-8069-e0e3048e911d.sketch_text.stroke-74"),sQuery(id+"FHMxAyK4CFUKdhS_1.wireOp",EDGE,"1cb9c079-ea9b-4899-8069-e0e3048e911d.sketch_text.stroke-75"),sQuery(id+"FHMxAyK4CFUKdhS_1.wireOp",EDGE,"1cb9c079-ea9b-4899-8069-e0e3048e911d.sketch_text.stroke-76"),sQuery(id+"FHMxAyK4CFUKdhS_1.wireOp",EDGE,"1cb9c079-ea9b-4899-8069-e0e3048e911d.sketch_text.stroke-77"),sQuery(id+"FHMxAyK4CFUKdhS_1.wireOp",EDGE,"1cb9c079-ea9b-4899-8069-e0e3048e911d.sketch_text.stroke-78"),sQuery(id+"FHMxAyK4CFUKdhS_1.wireOp",EDGE,"1cb9c079-ea9b-4899-8069-e0e3048e911d.sketch_text.stroke-79"),sQuery(id+"FHMxAyK4CFUKdhS_1.wireOp",EDGE,"1cb9c079-ea9b-4899-8069-e0e3048e911d.sketch_text.stroke-80"),sQuery(id+"FHMxAyK4CFUKdhS_1.wireOp",EDGE,"1cb9c079-ea9b-4899-8069-e0e3048e911d.sketch_text.stroke-81"),sQuery(id+"FHMxAyK4CFUKdhS_1.wireOp",EDGE,"1cb9c079-ea9b-4899-8069-e0e3048e911d.sketch_text.stroke-82"),sQuery(id+"FHMxAyK4CFUKdhS_1.wireOp",EDGE,"1cb9c079-ea9b-4899-8069-e0e3048e911d.sketch_text.stroke-83"),sQuery(id+"FHMxAyK4CFUKdhS_1.wireOp",EDGE,"1cb9c079-ea9b-4899-8069-e0e3048e911d.sketch_text.stroke-84"),sQuery(id+"FHMxAyK4CFUKdhS_1.wireOp",EDGE,"1cb9c079-ea9b-4899-8069-e0e3048e911d.sketch_text.stroke-85"),sQuery(id+"FHMxAyK4CFUKdhS_1.wireOp",EDGE,"1cb9c079-ea9b-4899-8069-e0e3048e911d.sketch_text.stroke-86"),sQuery(id+"FHMxAyK4CFUKdhS_1.wireOp",EDGE,"1cb9c079-ea9b-4899-8069-e0e3048e911d.sketch_text.stroke-87"),sQuery(id+"FHMxAyK4CFUKdhS_1.wireOp",EDGE,"1cb9c079-ea9b-4899-8069-e0e3048e911d.sketch_text.stroke-88"),sQuery(id+"FHMxAyK4CFUKdhS_1.wireOp",EDGE,"1cb9c079-ea9b-4899-8069-e0e3048e911d.sketch_text.stroke-89"),sQuery(id+"FHMxAyK4CFUKdhS_1.wireOp",EDGE,"1cb9c079-ea9b-4899-8069-e0e3048e911d.sketch_text.stroke-90"),sQuery(id+"FHMxAyK4CFUKdhS_1.wireOp",EDGE,"1cb9c079-ea9b-4899-8069-e0e3048e911d.sketch_text.stroke-91"),sQuery(id+"FHMxAyK4CFUKdhS_1.wireOp",EDGE,"1cb9c079-ea9b-4899-8069-e0e3048e911d.sketch_text.stroke-92"),sQuery(id+"FHMxAyK4CFUKdhS_1.wireOp",EDGE,"1cb9c079-ea9b-4899-8069-e0e3048e911d.sketch_text.stroke-93"),sQuery(id+"FHMxAyK4CFUKdhS_1.wireOp",EDGE,"1cb9c079-ea9b-4899-8069-e0e3048e911d.sketch_text.stroke-94"),sQuery(id+"FHMxAyK4CFUKdhS_1.wireOp",EDGE,"1cb9c079-ea9b-4899-8069-e0e3048e911d.sketch_text.stroke-95"),sQuery(id+"FHMxAyK4CFUKdhS_1.wireOp",EDGE,"1cb9c079-ea9b-4899-8069-e0e3048e911d.sketch_text.stroke-96"),sQuery(id+"FHMxAyK4CFUKdhS_1.wireOp",EDGE,"1cb9c079-ea9b-4899-8069-e0e3048e911d.sketch_text.stroke-97"),sQuery(id+"FHMxAyK4CFUKdhS_1.wireOp",EDGE,"1cb9c079-ea9b-4899-8069-e0e3048e911d.sketch_text.stroke-103"),sQuery(id+"FHMxAyK4CFUKdhS_1.wireOp",EDGE,"1cb9c079-ea9b-4899-8069-e0e3048e911d.sketch_text.stroke-104"),sQuery(id+"FHMxAyK4CFUKdhS_1.wireOp",EDGE,"1cb9c079-ea9b-4899-8069-e0e3048e911d.sketch_text.stroke-105"),sQuery(id+"FHMxAyK4CFUKdhS_1.wireOp",EDGE,"1cb9c079-ea9b-4899-8069-e0e3048e911d.sketch_text.stroke-106"),sQuery(id+"FHMxAyK4CFUKdhS_1.wireOp",EDGE,"1cb9c079-ea9b-4899-8069-e0e3048e911d.sketch_text.stroke-107"),sQuery(id+"FHMxAyK4CFUKdhS_1.wireOp",EDGE,"1cb9c079-ea9b-4899-8069-e0e3048e911d.sketch_text.stroke-108"),sQuery(id+"FHMxAyK4CFUKdhS_1.wireOp",EDGE,"1cb9c079-ea9b-4899-8069-e0e3048e911d.sketch_text.stroke-109"),sQuery(id+"FHMxAyK4CFUKdhS_1.wireOp",EDGE,"1cb9c079-ea9b-4899-8069-e0e3048e911d.sketch_text.stroke-110"),sQuery(id+"FHMxAyK4CFUKdhS_1.wireOp",EDGE,"1cb9c079-ea9b-4899-8069-e0e3048e911d.sketch_text.stroke-111"),sQuery(id+"FHMxAyK4CFUKdhS_1.wireOp",EDGE,"1cb9c079-ea9b-4899-8069-e0e3048e911d.sketch_text.stroke-112"),sQuery(id+"FHMxAyK4CFUKdhS_1.wireOp",EDGE,"1cb9c079-ea9b-4899-8069-e0e3048e911d.sketch_text.stroke-113"),sQuery(id+"FHMxAyK4CFUKdhS_1.wireOp",EDGE,"1cb9c079-ea9b-4899-8069-e0e3048e911d.sketch_text.stroke-114"),sQuery(id+"FHMxAyK4CFUKdhS_1.wireOp",EDGE,"1cb9c079-ea9b-4899-8069-e0e3048e911d.sketch_text.stroke-115"),sQuery(id+"FHMxAyK4CFUKdhS_1.wireOp",EDGE,"1cb9c079-ea9b-4899-8069-e0e3048e911d.sketch_text.stroke-116"),sQuery(id+"FHMxAyK4CFUKdhS_1.wireOp",EDGE,"1cb9c079-ea9b-4899-8069-e0e3048e911d.sketch_text.stroke-117"),sQuery(id+"FHMxAyK4CFUKdhS_1.wireOp",EDGE,"1cb9c079-ea9b-4899-8069-e0e3048e911d.sketch_text.stroke-118"),sQuery(id+"FHMxAyK4CFUKdhS_1.wireOp",EDGE,"1cb9c079-ea9b-4899-8069-e0e3048e911d.sketch_text.stroke-119"),sQuery(id+"FHMxAyK4CFUKdhS_1.wireOp",EDGE,"1cb9c079-ea9b-4899-8069-e0e3048e911d.sketch_text.stroke-120"),sQuery(id+"FHMxAyK4CFUKdhS_1.wireOp",EDGE,"1cb9c079-ea9b-4899-8069-e0e3048e911d.sketch_text.stroke-121"),sQuery(id+"FHMxAyK4CFUKdhS_1.wireOp",EDGE,"1cb9c079-ea9b-4899-8069-e0e3048e911d.sketch_text.stroke-122"),sQuery(id+"FHMxAyK4CFUKdhS_1.wireOp",EDGE,"1cb9c079-ea9b-4899-8069-e0e3048e911d.sketch_text.stroke-123"),sQuery(id+"FHMxAyK4CFUKdhS_1.wireOp",EDGE,"1cb9c079-ea9b-4899-8069-e0e3048e911d.sketch_text.stroke-124"),sQuery(id+"FHMxAyK4CFUKdhS_1.wireOp",EDGE,"1cb9c079-ea9b-4899-8069-e0e3048e911d.sketch_text.stroke-125"),sQuery(id+"FHMxAyK4CFUKdhS_1.wireOp",EDGE,"1cb9c079-ea9b-4899-8069-e0e3048e911d.sketch_text.stroke-126"),sQuery(id+"FHMxAyK4CFUKdhS_1.wireOp",EDGE,"1cb9c079-ea9b-4899-8069-e0e3048e911d.sketch_text.stroke-127"),sQuery(id+"FHMxAyK4CFUKdhS_1.wireOp",EDGE,"1cb9c079-ea9b-4899-8069-e0e3048e911d.sketch_text.stroke-128"),sQuery(id+"FHMxAyK4CFUKdhS_1.wireOp",EDGE,"1cb9c079-ea9b-4899-8069-e0e3048e911d.sketch_text.stroke-129"),sQuery(id+"FHMxAyK4CFUKdhS_1.wireOp",EDGE,"1cb9c079-ea9b-4899-8069-e0e3048e911d.sketch_text.stroke-130"),sQuery(id+"FHMxAyK4CFUKdhS_1.wireOp",EDGE,"1cb9c079-ea9b-4899-8069-e0e3048e911d.sketch_text.stroke-131"),sQuery(id+"FHMxAyK4CFUKdhS_1.wireOp",EDGE,"1cb9c079-ea9b-4899-8069-e0e3048e911d.sketch_text.stroke-132"),sQuery(id+"FHMxAyK4CFUKdhS_1.wireOp",EDGE,"1cb9c079-ea9b-4899-8069-e0e3048e911d.sketch_text.stroke-133"),sQuery(id+"FHMxAyK4CFUKdhS_1.wireOp",EDGE,"1cb9c079-ea9b-4899-8069-e0e3048e911d.sketch_text.stroke-134"),sQuery(id+"FHMxAyK4CFUKdhS_1.wireOp",EDGE,"1cb9c079-ea9b-4899-8069-e0e3048e911d.sketch_text.stroke-135"),sQuery(id+"FHMxAyK4CFUKdhS_1.wireOp",EDGE,"1cb9c079-ea9b-4899-8069-e0e3048e911d.sketch_text.stroke-136"),sQuery(id+"FHMxAyK4CFUKdhS_1.wireOp",EDGE,"1cb9c079-ea9b-4899-8069-e0e3048e911d.sketch_text.stroke-137"),sQuery(id+"FHMxAyK4CFUKdhS_1.wireOp",EDGE,"1cb9c079-ea9b-4899-8069-e0e3048e911d.sketch_text.stroke-138"),sQuery(id+"FHMxAyK4CFUKdhS_1.wireOp",EDGE,"1cb9c079-ea9b-4899-8069-e0e3048e911d.sketch_text.stroke-139"),sQuery(id+"FHMxAyK4CFUKdhS_1.wireOp",EDGE,"1cb9c079-ea9b-4899-8069-e0e3048e911d.sketch_text.stroke-140"),sQuery(id+"FHMxAyK4CFUKdhS_1.wireOp",EDGE,"1cb9c079-ea9b-4899-8069-e0e3048e911d.sketch_text.stroke-141"),sQuery(id+"FHMxAyK4CFUKdhS_1.wireOp",EDGE,"1cb9c079-ea9b-4899-8069-e0e3048e911d.sketch_text.stroke-142"),sQuery(id+"FHMxAyK4CFUKdhS_1.wireOp",EDGE,"1cb9c079-ea9b-4899-8069-e0e3048e911d.sketch_text.stroke-143"),sQuery(id+"FHMxAyK4CFUKdhS_1.wireOp",EDGE,"1cb9c079-ea9b-4899-8069-e0e3048e911d.sketch_text.stroke-144"),sQuery(id+"FHMxAyK4CFUKdhS_1.wireOp",EDGE,"1cb9c079-ea9b-4899-8069-e0e3048e911d.sketch_text.stroke-145"),sQuery(id+"FHMxAyK4CFUKdhS_1.wireOp",EDGE,"1cb9c079-ea9b-4899-8069-e0e3048e911d.sketch_text.stroke-146"),sQuery(id+"FHMxAyK4CFUKdhS_1.wireOp",EDGE,"1cb9c079-ea9b-4899-8069-e0e3048e911d.sketch_text.stroke-147"),sQuery(id+"FHMxAyK4CFUKdhS_1.wireOp",EDGE,"1cb9c079-ea9b-4899-8069-e0e3048e911d.sketch_text.stroke-148"),sQuery(id+"FHMxAyK4CFUKdhS_1.wireOp",EDGE,"1cb9c079-ea9b-4899-8069-e0e3048e911d.sketch_text.stroke-149"),sQuery(id+"FHMxAyK4CFUKdhS_1.wireOp",EDGE,"1cb9c079-ea9b-4899-8069-e0e3048e911d.sketch_text.stroke-150"),sQuery(id+"FHMxAyK4CFUKdhS_1.wireOp",EDGE,"1cb9c079-ea9b-4899-8069-e0e3048e911d.sketch_text.stroke-151"),sQuery(id+"FHMxAyK4CFUKdhS_1.wireOp",EDGE,"1cb9c079-ea9b-4899-8069-e0e3048e911d.sketch_text.stroke-152"),sQuery(id+"FHMxAyK4CFUKdhS_1.wireOp",EDGE,"1cb9c079-ea9b-4899-8069-e0e3048e911d.sketch_text.stroke-153"),sQuery(id+"FHMxAyK4CFUKdhS_1.wireOp",EDGE,"1cb9c079-ea9b-4899-8069-e0e3048e911d.sketch_text.stroke-159"),sQuery(id+"FHMxAyK4CFUKdhS_1.wireOp",EDGE,"1cb9c079-ea9b-4899-8069-e0e3048e911d.sketch_text.stroke-160"),sQuery(id+"FHMxAyK4CFUKdhS_1.wireOp",EDGE,"1cb9c079-ea9b-4899-8069-e0e3048e911d.sketch_text.stroke-161"),sQuery(id+"FHMxAyK4CFUKdhS_1.wireOp",EDGE,"1cb9c079-ea9b-4899-8069-e0e3048e911d.sketch_text.stroke-162"),sQuery(id+"FHMxAyK4CFUKdhS_1.wireOp",EDGE,"1cb9c079-ea9b-4899-8069-e0e3048e911d.sketch_text.stroke-163"),sQuery(id+"FHMxAyK4CFUKdhS_1.wireOp",EDGE,"1cb9c079-ea9b-4899-8069-e0e3048e911d.sketch_text.stroke-164"),sQuery(id+"FHMxAyK4CFUKdhS_1.wireOp",EDGE,"1cb9c079-ea9b-4899-8069-e0e3048e911d.sketch_text.stroke-165"),sQuery(id+"FHMxAyK4CFUKdhS_1.wireOp",EDGE,"1cb9c079-ea9b-4899-8069-e0e3048e911d.sketch_text.stroke-166"),sQuery(id+"FHMxAyK4CFUKdhS_1.wireOp",EDGE,"1cb9c079-ea9b-4899-8069-e0e3048e911d.sketch_text.stroke-167"),sQuery(id+"FHMxAyK4CFUKdhS_1.wireOp",EDGE,"1cb9c079-ea9b-4899-8069-e0e3048e911d.sketch_text.stroke-168"),sQuery(id+"FHMxAyK4CFUKdhS_1.wireOp",EDGE,"1cb9c079-ea9b-4899-8069-e0e3048e911d.sketch_text.stroke-169"),sQuery(id+"FHMxAyK4CFUKdhS_1.wireOp",EDGE,"1cb9c079-ea9b-4899-8069-e0e3048e911d.sketch_text.stroke-170"),sQuery(id+"FHMxAyK4CFUKdhS_1.wireOp",EDGE,"1cb9c079-ea9b-4899-8069-e0e3048e911d.sketch_text.stroke-171"),sQuery(id+"FHMxAyK4CFUKdhS_1.wireOp",EDGE,"1cb9c079-ea9b-4899-8069-e0e3048e911d.sketch_text.stroke-172"),sQuery(id+"FHMxAyK4CFUKdhS_1.wireOp",EDGE,"1cb9c079-ea9b-4899-8069-e0e3048e911d.sketch_text.stroke-173"),sQuery(id+"FHMxAyK4CFUKdhS_1.wireOp",EDGE,"1cb9c079-ea9b-4899-8069-e0e3048e911d.sketch_text.stroke-174"),sQuery(id+"FHMxAyK4CFUKdhS_1.wireOp",EDGE,"1cb9c079-ea9b-4899-8069-e0e3048e911d.sketch_text.stroke-175"),sQuery(id+"FHMxAyK4CFUKdhS_1.wireOp",EDGE,"1cb9c079-ea9b-4899-8069-e0e3048e911d.sketch_text.stroke-176"),sQuery(id+"FHMxAyK4CFUKdhS_1.wireOp",EDGE,"1cb9c079-ea9b-4899-8069-e0e3048e911d.sketch_text.stroke-177"),sQuery(id+"FHMxAyK4CFUKdhS_1.wireOp",EDGE,"1cb9c079-ea9b-4899-8069-e0e3048e911d.sketch_text.stroke-178"),sQuery(id+"FHMxAyK4CFUKdhS_1.wireOp",EDGE,"1cb9c079-ea9b-4899-8069-e0e3048e911d.sketch_text.stroke-179"),sQuery(id+"FHMxAyK4CFUKdhS_1.wireOp",EDGE,"1cb9c079-ea9b-4899-8069-e0e3048e911d.sketch_text.stroke-180"),subQ0,subQ2])],"isStart":true}),makeQuery(id+"F3.opExtrude","SWEPT_FACE",FACE,{"disambiguationData":[OSD([subQ2])]})])],"derivedFrom":makeQuery(id+"F3.opExtrude","CAP_EDGE",EDGE,{"disambiguationData":[OSD([subQ2])],"isStart":true})});}
            var Q11;
            {var subQ0=sQuery(id+"F0.wireOp",EDGE,"E0.top");var subQ1=sQuery(id+"F0.wireOp",EDGE,"E0.bottom");var subQ2=sQuery(id+"F2.wireOp",EDGE,"6ee83ff3-586e-4dbe-aaea-af71240543bd");Q11=makeQuery(id+"F3.boolean.opBoolean","SPLIT",EDGE,{"disambiguationData":[TD([makeQuery(id+"F1.opExtrude","CAP_FACE",FACE,{"disambiguationData":[OSD([subQ1,subQ0,sQuery(id+"F0.wireOp",EDGE,"E0.left"),sQuery(id+"F0.wireOp",EDGE,"E0.right")])],"isStart":false}),makeQuery(id+"F1.opExtrude","SWEPT_FACE",FACE,{"disambiguationData":[OSD([subQ0])]}),makeQuery(id+"F3.opExtrude","CAP_FACE",FACE,{"disambiguationData":[OSD([subQ1,sQuery(id+"FQ5JFwxVdaqARUP_1.wireOp",EDGE,"fcba4419-a2ee-464f-be9d-58f11bf3418b.sketch_text.stroke-0"),sQuery(id+"FQ5JFwxVdaqARUP_1.wireOp",EDGE,"fcba4419-a2ee-464f-be9d-58f11bf3418b.sketch_text.stroke-1"),sQuery(id+"FQ5JFwxVdaqARUP_1.wireOp",EDGE,"fcba4419-a2ee-464f-be9d-58f11bf3418b.sketch_text.stroke-2"),sQuery(id+"FQ5JFwxVdaqARUP_1.wireOp",EDGE,"fcba4419-a2ee-464f-be9d-58f11bf3418b.sketch_text.stroke-3"),sQuery(id+"FQ5JFwxVdaqARUP_1.wireOp",EDGE,"fcba4419-a2ee-464f-be9d-58f11bf3418b.sketch_text.stroke-4"),sQuery(id+"FQ5JFwxVdaqARUP_1.wireOp",EDGE,"fcba4419-a2ee-464f-be9d-58f11bf3418b.sketch_text.stroke-5"),sQuery(id+"FQ5JFwxVdaqARUP_1.wireOp",EDGE,"fcba4419-a2ee-464f-be9d-58f11bf3418b.sketch_text.stroke-6"),sQuery(id+"FQ5JFwxVdaqARUP_1.wireOp",EDGE,"fcba4419-a2ee-464f-be9d-58f11bf3418b.sketch_text.stroke-7"),sQuery(id+"FQ5JFwxVdaqARUP_1.wireOp",EDGE,"fcba4419-a2ee-464f-be9d-58f11bf3418b.sketch_text.stroke-8"),sQuery(id+"FQ5JFwxVdaqARUP_1.wireOp",EDGE,"fcba4419-a2ee-464f-be9d-58f11bf3418b.sketch_text.stroke-9"),sQuery(id+"FQ5JFwxVdaqARUP_1.wireOp",EDGE,"fcba4419-a2ee-464f-be9d-58f11bf3418b.sketch_text.stroke-10"),sQuery(id+"FQ5JFwxVdaqARUP_1.wireOp",EDGE,"fcba4419-a2ee-464f-be9d-58f11bf3418b.sketch_text.stroke-11"),sQuery(id+"FQ5JFwxVdaqARUP_1.wireOp",EDGE,"fcba4419-a2ee-464f-be9d-58f11bf3418b.sketch_text.stroke-12"),sQuery(id+"FQ5JFwxVdaqARUP_1.wireOp",EDGE,"fcba4419-a2ee-464f-be9d-58f11bf3418b.sketch_text.stroke-13"),sQuery(id+"FQ5JFwxVdaqARUP_1.wireOp",EDGE,"fcba4419-a2ee-464f-be9d-58f11bf3418b.sketch_text.stroke-14"),sQuery(id+"FQ5JFwxVdaqARUP_1.wireOp",EDGE,"fcba4419-a2ee-464f-be9d-58f11bf3418b.sketch_text.stroke-15"),sQuery(id+"FQ5JFwxVdaqARUP_1.wireOp",EDGE,"fcba4419-a2ee-464f-be9d-58f11bf3418b.sketch_text.stroke-16"),sQuery(id+"FQ5JFwxVdaqARUP_1.wireOp",EDGE,"fcba4419-a2ee-464f-be9d-58f11bf3418b.sketch_text.stroke-17"),sQuery(id+"FQ5JFwxVdaqARUP_1.wireOp",EDGE,"fcba4419-a2ee-464f-be9d-58f11bf3418b.sketch_text.stroke-18"),sQuery(id+"FQ5JFwxVdaqARUP_1.wireOp",EDGE,"fcba4419-a2ee-464f-be9d-58f11bf3418b.sketch_text.stroke-19"),sQuery(id+"FQ5JFwxVdaqARUP_1.wireOp",EDGE,"fcba4419-a2ee-464f-be9d-58f11bf3418b.sketch_text.stroke-20"),sQuery(id+"FQ5JFwxVdaqARUP_1.wireOp",EDGE,"fcba4419-a2ee-464f-be9d-58f11bf3418b.sketch_text.stroke-21"),sQuery(id+"FQ5JFwxVdaqARUP_1.wireOp",EDGE,"fcba4419-a2ee-464f-be9d-58f11bf3418b.sketch_text.stroke-22"),sQuery(id+"FQ5JFwxVdaqARUP_1.wireOp",EDGE,"fcba4419-a2ee-464f-be9d-58f11bf3418b.sketch_text.stroke-23"),sQuery(id+"FQ5JFwxVdaqARUP_1.wireOp",EDGE,"fcba4419-a2ee-464f-be9d-58f11bf3418b.sketch_text.stroke-24"),sQuery(id+"FQ5JFwxVdaqARUP_1.wireOp",EDGE,"fcba4419-a2ee-464f-be9d-58f11bf3418b.sketch_text.stroke-25"),sQuery(id+"FQ5JFwxVdaqARUP_1.wireOp",EDGE,"fcba4419-a2ee-464f-be9d-58f11bf3418b.sketch_text.stroke-26"),sQuery(id+"FQ5JFwxVdaqARUP_1.wireOp",EDGE,"fcba4419-a2ee-464f-be9d-58f11bf3418b.sketch_text.stroke-27"),sQuery(id+"FQ5JFwxVdaqARUP_1.wireOp",EDGE,"fcba4419-a2ee-464f-be9d-58f11bf3418b.sketch_text.stroke-28"),sQuery(id+"FQ5JFwxVdaqARUP_1.wireOp",EDGE,"fcba4419-a2ee-464f-be9d-58f11bf3418b.sketch_text.stroke-29"),sQuery(id+"FQ5JFwxVdaqARUP_1.wireOp",EDGE,"fcba4419-a2ee-464f-be9d-58f11bf3418b.sketch_text.stroke-30"),sQuery(id+"FQ5JFwxVdaqARUP_1.wireOp",EDGE,"fcba4419-a2ee-464f-be9d-58f11bf3418b.sketch_text.stroke-31"),sQuery(id+"FQ5JFwxVdaqARUP_1.wireOp",EDGE,"fcba4419-a2ee-464f-be9d-58f11bf3418b.sketch_text.stroke-32"),sQuery(id+"FQ5JFwxVdaqARUP_1.wireOp",EDGE,"fcba4419-a2ee-464f-be9d-58f11bf3418b.sketch_text.stroke-33"),sQuery(id+"FQ5JFwxVdaqARUP_1.wireOp",EDGE,"fcba4419-a2ee-464f-be9d-58f11bf3418b.sketch_text.stroke-34"),sQuery(id+"FQ5JFwxVdaqARUP_1.wireOp",EDGE,"fcba4419-a2ee-464f-be9d-58f11bf3418b.sketch_text.stroke-35"),sQuery(id+"FQ5JFwxVdaqARUP_1.wireOp",EDGE,"fcba4419-a2ee-464f-be9d-58f11bf3418b.sketch_text.stroke-36"),sQuery(id+"FQ5JFwxVdaqARUP_1.wireOp",EDGE,"fcba4419-a2ee-464f-be9d-58f11bf3418b.sketch_text.stroke-37"),sQuery(id+"FQ5JFwxVdaqARUP_1.wireOp",EDGE,"fcba4419-a2ee-464f-be9d-58f11bf3418b.sketch_text.stroke-38"),sQuery(id+"FQ5JFwxVdaqARUP_1.wireOp",EDGE,"fcba4419-a2ee-464f-be9d-58f11bf3418b.sketch_text.stroke-39"),sQuery(id+"FQ5JFwxVdaqARUP_1.wireOp",EDGE,"fcba4419-a2ee-464f-be9d-58f11bf3418b.sketch_text.stroke-40"),sQuery(id+"FQ5JFwxVdaqARUP_1.wireOp",EDGE,"fcba4419-a2ee-464f-be9d-58f11bf3418b.sketch_text.stroke-41"),sQuery(id+"FQ5JFwxVdaqARUP_1.wireOp",EDGE,"fcba4419-a2ee-464f-be9d-58f11bf3418b.sketch_text.stroke-42"),sQuery(id+"FQ5JFwxVdaqARUP_1.wireOp",EDGE,"fcba4419-a2ee-464f-be9d-58f11bf3418b.sketch_text.stroke-43"),sQuery(id+"FQ5JFwxVdaqARUP_1.wireOp",EDGE,"fcba4419-a2ee-464f-be9d-58f11bf3418b.sketch_text.stroke-44"),sQuery(id+"FQ5JFwxVdaqARUP_1.wireOp",EDGE,"fcba4419-a2ee-464f-be9d-58f11bf3418b.sketch_text.stroke-45"),sQuery(id+"FQ5JFwxVdaqARUP_1.wireOp",EDGE,"fcba4419-a2ee-464f-be9d-58f11bf3418b.sketch_text.stroke-46"),sQuery(id+"FQ5JFwxVdaqARUP_1.wireOp",EDGE,"fcba4419-a2ee-464f-be9d-58f11bf3418b.sketch_text.stroke-47"),sQuery(id+"FQ5JFwxVdaqARUP_1.wireOp",EDGE,"fcba4419-a2ee-464f-be9d-58f11bf3418b.sketch_text.stroke-48"),sQuery(id+"FQ5JFwxVdaqARUP_1.wireOp",EDGE,"fcba4419-a2ee-464f-be9d-58f11bf3418b.sketch_text.stroke-49"),sQuery(id+"FQ5JFwxVdaqARUP_1.wireOp",EDGE,"fcba4419-a2ee-464f-be9d-58f11bf3418b.sketch_text.stroke-50"),sQuery(id+"FQ5JFwxVdaqARUP_1.wireOp",EDGE,"fcba4419-a2ee-464f-be9d-58f11bf3418b.sketch_text.stroke-51"),sQuery(id+"FQ5JFwxVdaqARUP_1.wireOp",EDGE,"fcba4419-a2ee-464f-be9d-58f11bf3418b.sketch_text.stroke-52"),sQuery(id+"FQ5JFwxVdaqARUP_1.wireOp",EDGE,"fcba4419-a2ee-464f-be9d-58f11bf3418b.sketch_text.stroke-53"),sQuery(id+"FQ5JFwxVdaqARUP_1.wireOp",EDGE,"fcba4419-a2ee-464f-be9d-58f11bf3418b.sketch_text.stroke-54"),sQuery(id+"FQ5JFwxVdaqARUP_1.wireOp",EDGE,"fcba4419-a2ee-464f-be9d-58f11bf3418b.sketch_text.stroke-55"),sQuery(id+"FQ5JFwxVdaqARUP_1.wireOp",EDGE,"fcba4419-a2ee-464f-be9d-58f11bf3418b.sketch_text.stroke-56"),sQuery(id+"FQ5JFwxVdaqARUP_1.wireOp",EDGE,"fcba4419-a2ee-464f-be9d-58f11bf3418b.sketch_text.stroke-57"),sQuery(id+"FQ5JFwxVdaqARUP_1.wireOp",EDGE,"fcba4419-a2ee-464f-be9d-58f11bf3418b.sketch_text.stroke-58"),sQuery(id+"FQ5JFwxVdaqARUP_1.wireOp",EDGE,"fcba4419-a2ee-464f-be9d-58f11bf3418b.sketch_text.stroke-59"),sQuery(id+"FQ5JFwxVdaqARUP_1.wireOp",EDGE,"fcba4419-a2ee-464f-be9d-58f11bf3418b.sketch_text.stroke-60"),sQuery(id+"FQ5JFwxVdaqARUP_1.wireOp",EDGE,"fcba4419-a2ee-464f-be9d-58f11bf3418b.sketch_text.stroke-61"),sQuery(id+"FQ5JFwxVdaqARUP_1.wireOp",EDGE,"fcba4419-a2ee-464f-be9d-58f11bf3418b.sketch_text.stroke-62"),sQuery(id+"FQ5JFwxVdaqARUP_1.wireOp",EDGE,"fcba4419-a2ee-464f-be9d-58f11bf3418b.sketch_text.stroke-63"),sQuery(id+"FQ5JFwxVdaqARUP_1.wireOp",EDGE,"fcba4419-a2ee-464f-be9d-58f11bf3418b.sketch_text.stroke-64"),sQuery(id+"FQ5JFwxVdaqARUP_1.wireOp",EDGE,"fcba4419-a2ee-464f-be9d-58f11bf3418b.sketch_text.stroke-65"),sQuery(id+"FQ5JFwxVdaqARUP_1.wireOp",EDGE,"fcba4419-a2ee-464f-be9d-58f11bf3418b.sketch_text.stroke-66"),sQuery(id+"FQ5JFwxVdaqARUP_1.wireOp",EDGE,"fcba4419-a2ee-464f-be9d-58f11bf3418b.sketch_text.stroke-67"),sQuery(id+"FQ5JFwxVdaqARUP_1.wireOp",EDGE,"fcba4419-a2ee-464f-be9d-58f11bf3418b.sketch_text.stroke-68"),sQuery(id+"FQ5JFwxVdaqARUP_1.wireOp",EDGE,"fcba4419-a2ee-464f-be9d-58f11bf3418b.sketch_text.stroke-69"),sQuery(id+"FQ5JFwxVdaqARUP_1.wireOp",EDGE,"fcba4419-a2ee-464f-be9d-58f11bf3418b.sketch_text.stroke-70"),sQuery(id+"FQ5JFwxVdaqARUP_1.wireOp",EDGE,"fcba4419-a2ee-464f-be9d-58f11bf3418b.sketch_text.stroke-71"),sQuery(id+"FQ5JFwxVdaqARUP_1.wireOp",EDGE,"fcba4419-a2ee-464f-be9d-58f11bf3418b.sketch_text.stroke-72"),sQuery(id+"FQ5JFwxVdaqARUP_1.wireOp",EDGE,"fcba4419-a2ee-464f-be9d-58f11bf3418b.sketch_text.stroke-73"),sQuery(id+"FQ5JFwxVdaqARUP_1.wireOp",EDGE,"fcba4419-a2ee-464f-be9d-58f11bf3418b.sketch_text.stroke-74"),sQuery(id+"FQ5JFwxVdaqARUP_1.wireOp",EDGE,"fcba4419-a2ee-464f-be9d-58f11bf3418b.sketch_text.stroke-75"),sQuery(id+"FQ5JFwxVdaqARUP_1.wireOp",EDGE,"fcba4419-a2ee-464f-be9d-58f11bf3418b.sketch_text.stroke-76"),sQuery(id+"FQ5JFwxVdaqARUP_1.wireOp",EDGE,"fcba4419-a2ee-464f-be9d-58f11bf3418b.sketch_text.stroke-77"),sQuery(id+"FQ5JFwxVdaqARUP_1.wireOp",EDGE,"fcba4419-a2ee-464f-be9d-58f11bf3418b.sketch_text.stroke-78"),sQuery(id+"FQ5JFwxVdaqARUP_1.wireOp",EDGE,"fcba4419-a2ee-464f-be9d-58f11bf3418b.sketch_text.stroke-79"),sQuery(id+"FQ5JFwxVdaqARUP_1.wireOp",EDGE,"fcba4419-a2ee-464f-be9d-58f11bf3418b.sketch_text.stroke-80"),sQuery(id+"FQ5JFwxVdaqARUP_1.wireOp",EDGE,"fcba4419-a2ee-464f-be9d-58f11bf3418b.sketch_text.stroke-81"),sQuery(id+"FQ5JFwxVdaqARUP_1.wireOp",EDGE,"fcba4419-a2ee-464f-be9d-58f11bf3418b.sketch_text.stroke-82"),sQuery(id+"FQ5JFwxVdaqARUP_1.wireOp",EDGE,"fcba4419-a2ee-464f-be9d-58f11bf3418b.sketch_text.stroke-83"),sQuery(id+"FQ5JFwxVdaqARUP_1.wireOp",EDGE,"fcba4419-a2ee-464f-be9d-58f11bf3418b.sketch_text.stroke-84"),sQuery(id+"FQ5JFwxVdaqARUP_1.wireOp",EDGE,"fcba4419-a2ee-464f-be9d-58f11bf3418b.sketch_text.stroke-85"),sQuery(id+"FQ5JFwxVdaqARUP_1.wireOp",EDGE,"fcba4419-a2ee-464f-be9d-58f11bf3418b.sketch_text.stroke-86"),sQuery(id+"FQ5JFwxVdaqARUP_1.wireOp",EDGE,"fcba4419-a2ee-464f-be9d-58f11bf3418b.sketch_text.stroke-87"),sQuery(id+"FQ5JFwxVdaqARUP_1.wireOp",EDGE,"fcba4419-a2ee-464f-be9d-58f11bf3418b.sketch_text.stroke-88"),sQuery(id+"FQ5JFwxVdaqARUP_1.wireOp",EDGE,"fcba4419-a2ee-464f-be9d-58f11bf3418b.sketch_text.stroke-89"),sQuery(id+"FQ5JFwxVdaqARUP_1.wireOp",EDGE,"fcba4419-a2ee-464f-be9d-58f11bf3418b.sketch_text.stroke-90"),sQuery(id+"FQ5JFwxVdaqARUP_1.wireOp",EDGE,"fcba4419-a2ee-464f-be9d-58f11bf3418b.sketch_text.stroke-91"),sQuery(id+"FQ5JFwxVdaqARUP_1.wireOp",EDGE,"fcba4419-a2ee-464f-be9d-58f11bf3418b.sketch_text.stroke-92"),sQuery(id+"FQ5JFwxVdaqARUP_1.wireOp",EDGE,"fcba4419-a2ee-464f-be9d-58f11bf3418b.sketch_text.stroke-93"),sQuery(id+"FQ5JFwxVdaqARUP_1.wireOp",EDGE,"fcba4419-a2ee-464f-be9d-58f11bf3418b.sketch_text.stroke-94"),sQuery(id+"FQ5JFwxVdaqARUP_1.wireOp",EDGE,"fcba4419-a2ee-464f-be9d-58f11bf3418b.sketch_text.stroke-95"),sQuery(id+"FQ5JFwxVdaqARUP_1.wireOp",EDGE,"fcba4419-a2ee-464f-be9d-58f11bf3418b.sketch_text.stroke-96"),sQuery(id+"FQ5JFwxVdaqARUP_1.wireOp",EDGE,"fcba4419-a2ee-464f-be9d-58f11bf3418b.sketch_text.stroke-97"),sQuery(id+"FQ5JFwxVdaqARUP_1.wireOp",EDGE,"fcba4419-a2ee-464f-be9d-58f11bf3418b.sketch_text.stroke-98"),sQuery(id+"FQ5JFwxVdaqARUP_1.wireOp",EDGE,"fcba4419-a2ee-464f-be9d-58f11bf3418b.sketch_text.stroke-99"),sQuery(id+"FQ5JFwxVdaqARUP_1.wireOp",EDGE,"fcba4419-a2ee-464f-be9d-58f11bf3418b.sketch_text.stroke-100"),sQuery(id+"FQ5JFwxVdaqARUP_1.wireOp",EDGE,"fcba4419-a2ee-464f-be9d-58f11bf3418b.sketch_text.stroke-101"),sQuery(id+"FQ5JFwxVdaqARUP_1.wireOp",EDGE,"fcba4419-a2ee-464f-be9d-58f11bf3418b.sketch_text.stroke-102"),sQuery(id+"FQ5JFwxVdaqARUP_1.wireOp",EDGE,"fcba4419-a2ee-464f-be9d-58f11bf3418b.sketch_text.stroke-103"),sQuery(id+"FQ5JFwxVdaqARUP_1.wireOp",EDGE,"fcba4419-a2ee-464f-be9d-58f11bf3418b.sketch_text.stroke-104"),sQuery(id+"FQ5JFwxVdaqARUP_1.wireOp",EDGE,"fcba4419-a2ee-464f-be9d-58f11bf3418b.sketch_text.stroke-105"),sQuery(id+"FQ5JFwxVdaqARUP_1.wireOp",EDGE,"fcba4419-a2ee-464f-be9d-58f11bf3418b.sketch_text.stroke-106"),sQuery(id+"FQ5JFwxVdaqARUP_1.wireOp",EDGE,"fcba4419-a2ee-464f-be9d-58f11bf3418b.sketch_text.stroke-107"),sQuery(id+"FQ5JFwxVdaqARUP_1.wireOp",EDGE,"fcba4419-a2ee-464f-be9d-58f11bf3418b.sketch_text.stroke-108"),sQuery(id+"FQ5JFwxVdaqARUP_1.wireOp",EDGE,"fcba4419-a2ee-464f-be9d-58f11bf3418b.sketch_text.stroke-109"),sQuery(id+"FQ5JFwxVdaqARUP_1.wireOp",EDGE,"fcba4419-a2ee-464f-be9d-58f11bf3418b.sketch_text.stroke-110"),sQuery(id+"FQ5JFwxVdaqARUP_1.wireOp",EDGE,"fcba4419-a2ee-464f-be9d-58f11bf3418b.sketch_text.stroke-111"),sQuery(id+"FQ5JFwxVdaqARUP_1.wireOp",EDGE,"fcba4419-a2ee-464f-be9d-58f11bf3418b.sketch_text.stroke-112"),sQuery(id+"FQ5JFwxVdaqARUP_1.wireOp",EDGE,"fcba4419-a2ee-464f-be9d-58f11bf3418b.sketch_text.stroke-113"),sQuery(id+"FQ5JFwxVdaqARUP_1.wireOp",EDGE,"fcba4419-a2ee-464f-be9d-58f11bf3418b.sketch_text.stroke-114"),sQuery(id+"FQ5JFwxVdaqARUP_1.wireOp",EDGE,"fcba4419-a2ee-464f-be9d-58f11bf3418b.sketch_text.stroke-115"),sQuery(id+"FQ5JFwxVdaqARUP_1.wireOp",EDGE,"fcba4419-a2ee-464f-be9d-58f11bf3418b.sketch_text.stroke-116"),sQuery(id+"FQ5JFwxVdaqARUP_1.wireOp",EDGE,"fcba4419-a2ee-464f-be9d-58f11bf3418b.sketch_text.stroke-117"),sQuery(id+"FQ5JFwxVdaqARUP_1.wireOp",EDGE,"fcba4419-a2ee-464f-be9d-58f11bf3418b.sketch_text.stroke-118"),sQuery(id+"FQ5JFwxVdaqARUP_1.wireOp",EDGE,"fcba4419-a2ee-464f-be9d-58f11bf3418b.sketch_text.stroke-119"),sQuery(id+"FQ5JFwxVdaqARUP_1.wireOp",EDGE,"fcba4419-a2ee-464f-be9d-58f11bf3418b.sketch_text.stroke-120"),sQuery(id+"FQ5JFwxVdaqARUP_1.wireOp",EDGE,"fcba4419-a2ee-464f-be9d-58f11bf3418b.sketch_text.stroke-121"),sQuery(id+"FQ5JFwxVdaqARUP_1.wireOp",EDGE,"fcba4419-a2ee-464f-be9d-58f11bf3418b.sketch_text.stroke-122"),sQuery(id+"FQ5JFwxVdaqARUP_1.wireOp",EDGE,"fcba4419-a2ee-464f-be9d-58f11bf3418b.sketch_text.stroke-123"),sQuery(id+"FQ5JFwxVdaqARUP_1.wireOp",EDGE,"fcba4419-a2ee-464f-be9d-58f11bf3418b.sketch_text.stroke-124"),sQuery(id+"FQ5JFwxVdaqARUP_1.wireOp",EDGE,"fcba4419-a2ee-464f-be9d-58f11bf3418b.sketch_text.stroke-125"),sQuery(id+"FQ5JFwxVdaqARUP_1.wireOp",EDGE,"fcba4419-a2ee-464f-be9d-58f11bf3418b.sketch_text.stroke-126"),sQuery(id+"FQ5JFwxVdaqARUP_1.wireOp",EDGE,"fcba4419-a2ee-464f-be9d-58f11bf3418b.sketch_text.stroke-127"),sQuery(id+"FQ5JFwxVdaqARUP_1.wireOp",EDGE,"fcba4419-a2ee-464f-be9d-58f11bf3418b.sketch_text.stroke-128"),sQuery(id+"FQ5JFwxVdaqARUP_1.wireOp",EDGE,"fcba4419-a2ee-464f-be9d-58f11bf3418b.sketch_text.stroke-129"),sQuery(id+"FQ5JFwxVdaqARUP_1.wireOp",EDGE,"fcba4419-a2ee-464f-be9d-58f11bf3418b.sketch_text.stroke-130"),sQuery(id+"FQ5JFwxVdaqARUP_1.wireOp",EDGE,"fcba4419-a2ee-464f-be9d-58f11bf3418b.sketch_text.stroke-131"),sQuery(id+"FQ5JFwxVdaqARUP_1.wireOp",EDGE,"fcba4419-a2ee-464f-be9d-58f11bf3418b.sketch_text.stroke-132"),sQuery(id+"FQ5JFwxVdaqARUP_1.wireOp",EDGE,"fcba4419-a2ee-464f-be9d-58f11bf3418b.sketch_text.stroke-133"),sQuery(id+"FQ5JFwxVdaqARUP_1.wireOp",EDGE,"fcba4419-a2ee-464f-be9d-58f11bf3418b.sketch_text.stroke-134"),sQuery(id+"FQ5JFwxVdaqARUP_1.wireOp",EDGE,"fcba4419-a2ee-464f-be9d-58f11bf3418b.sketch_text.stroke-135"),sQuery(id+"FQ5JFwxVdaqARUP_1.wireOp",EDGE,"fcba4419-a2ee-464f-be9d-58f11bf3418b.sketch_text.stroke-136"),sQuery(id+"FQ5JFwxVdaqARUP_1.wireOp",EDGE,"fcba4419-a2ee-464f-be9d-58f11bf3418b.sketch_text.stroke-137"),sQuery(id+"FQ5JFwxVdaqARUP_1.wireOp",EDGE,"fcba4419-a2ee-464f-be9d-58f11bf3418b.sketch_text.stroke-138"),sQuery(id+"FQ5JFwxVdaqARUP_1.wireOp",EDGE,"fcba4419-a2ee-464f-be9d-58f11bf3418b.sketch_text.stroke-139"),sQuery(id+"FQ5JFwxVdaqARUP_1.wireOp",EDGE,"fcba4419-a2ee-464f-be9d-58f11bf3418b.sketch_text.stroke-140"),sQuery(id+"FQ5JFwxVdaqARUP_1.wireOp",EDGE,"fcba4419-a2ee-464f-be9d-58f11bf3418b.sketch_text.stroke-141"),sQuery(id+"FQ5JFwxVdaqARUP_1.wireOp",EDGE,"fcba4419-a2ee-464f-be9d-58f11bf3418b.sketch_text.stroke-142"),sQuery(id+"FQ5JFwxVdaqARUP_1.wireOp",EDGE,"fcba4419-a2ee-464f-be9d-58f11bf3418b.sketch_text.stroke-143"),sQuery(id+"FQ5JFwxVdaqARUP_1.wireOp",EDGE,"fcba4419-a2ee-464f-be9d-58f11bf3418b.sketch_text.stroke-144"),sQuery(id+"FQ5JFwxVdaqARUP_1.wireOp",EDGE,"fcba4419-a2ee-464f-be9d-58f11bf3418b.sketch_text.stroke-145"),sQuery(id+"FQ5JFwxVdaqARUP_1.wireOp",EDGE,"fcba4419-a2ee-464f-be9d-58f11bf3418b.sketch_text.stroke-146"),sQuery(id+"FQ5JFwxVdaqARUP_1.wireOp",EDGE,"fcba4419-a2ee-464f-be9d-58f11bf3418b.sketch_text.stroke-147"),sQuery(id+"FQ5JFwxVdaqARUP_1.wireOp",EDGE,"fcba4419-a2ee-464f-be9d-58f11bf3418b.sketch_text.stroke-148"),sQuery(id+"FQ5JFwxVdaqARUP_1.wireOp",EDGE,"fcba4419-a2ee-464f-be9d-58f11bf3418b.sketch_text.stroke-149"),sQuery(id+"FQ5JFwxVdaqARUP_1.wireOp",EDGE,"fcba4419-a2ee-464f-be9d-58f11bf3418b.sketch_text.stroke-150"),sQuery(id+"FQ5JFwxVdaqARUP_1.wireOp",EDGE,"fcba4419-a2ee-464f-be9d-58f11bf3418b.sketch_text.stroke-151"),sQuery(id+"FQ5JFwxVdaqARUP_1.wireOp",EDGE,"fcba4419-a2ee-464f-be9d-58f11bf3418b.sketch_text.stroke-152"),sQuery(id+"FQ5JFwxVdaqARUP_1.wireOp",EDGE,"fcba4419-a2ee-464f-be9d-58f11bf3418b.sketch_text.stroke-153"),sQuery(id+"FQ5JFwxVdaqARUP_1.wireOp",EDGE,"fcba4419-a2ee-464f-be9d-58f11bf3418b.sketch_text.stroke-154"),sQuery(id+"FQ5JFwxVdaqARUP_1.wireOp",EDGE,"fcba4419-a2ee-464f-be9d-58f11bf3418b.sketch_text.stroke-155"),sQuery(id+"FQ5JFwxVdaqARUP_1.wireOp",EDGE,"fcba4419-a2ee-464f-be9d-58f11bf3418b.sketch_text.stroke-156"),sQuery(id+"FQ5JFwxVdaqARUP_1.wireOp",EDGE,"fcba4419-a2ee-464f-be9d-58f11bf3418b.sketch_text.stroke-157"),sQuery(id+"FQ5JFwxVdaqARUP_1.wireOp",EDGE,"fcba4419-a2ee-464f-be9d-58f11bf3418b.sketch_text.stroke-158"),sQuery(id+"FQ5JFwxVdaqARUP_1.wireOp",EDGE,"fcba4419-a2ee-464f-be9d-58f11bf3418b.sketch_text.stroke-159"),sQuery(id+"FQ5JFwxVdaqARUP_1.wireOp",EDGE,"fcba4419-a2ee-464f-be9d-58f11bf3418b.sketch_text.stroke-160"),sQuery(id+"FQ5JFwxVdaqARUP_1.wireOp",EDGE,"fcba4419-a2ee-464f-be9d-58f11bf3418b.sketch_text.stroke-161"),sQuery(id+"FQ5JFwxVdaqARUP_1.wireOp",EDGE,"fcba4419-a2ee-464f-be9d-58f11bf3418b.sketch_text.stroke-162"),sQuery(id+"FQ5JFwxVdaqARUP_1.wireOp",EDGE,"fcba4419-a2ee-464f-be9d-58f11bf3418b.sketch_text.stroke-163"),sQuery(id+"FQ5JFwxVdaqARUP_1.wireOp",EDGE,"fcba4419-a2ee-464f-be9d-58f11bf3418b.sketch_text.stroke-164"),sQuery(id+"FQ5JFwxVdaqARUP_1.wireOp",EDGE,"fcba4419-a2ee-464f-be9d-58f11bf3418b.sketch_text.stroke-165"),sQuery(id+"FQ5JFwxVdaqARUP_1.wireOp",EDGE,"fcba4419-a2ee-464f-be9d-58f11bf3418b.sketch_text.stroke-166"),sQuery(id+"FQ5JFwxVdaqARUP_1.wireOp",EDGE,"fcba4419-a2ee-464f-be9d-58f11bf3418b.sketch_text.stroke-167"),sQuery(id+"FQ5JFwxVdaqARUP_1.wireOp",EDGE,"fcba4419-a2ee-464f-be9d-58f11bf3418b.sketch_text.stroke-168"),sQuery(id+"FQ5JFwxVdaqARUP_1.wireOp",EDGE,"fcba4419-a2ee-464f-be9d-58f11bf3418b.sketch_text.stroke-169"),sQuery(id+"FQ5JFwxVdaqARUP_1.wireOp",EDGE,"fcba4419-a2ee-464f-be9d-58f11bf3418b.sketch_text.stroke-170"),sQuery(id+"FQ5JFwxVdaqARUP_1.wireOp",EDGE,"fcba4419-a2ee-464f-be9d-58f11bf3418b.sketch_text.stroke-171"),sQuery(id+"FQ5JFwxVdaqARUP_1.wireOp",EDGE,"fcba4419-a2ee-464f-be9d-58f11bf3418b.sketch_text.stroke-172"),sQuery(id+"FQ5JFwxVdaqARUP_1.wireOp",EDGE,"fcba4419-a2ee-464f-be9d-58f11bf3418b.sketch_text.stroke-173"),sQuery(id+"FHMxAyK4CFUKdhS_1.wireOp",EDGE,"1cb9c079-ea9b-4899-8069-e0e3048e911d.sketch_text.stroke-0"),sQuery(id+"FHMxAyK4CFUKdhS_1.wireOp",EDGE,"1cb9c079-ea9b-4899-8069-e0e3048e911d.sketch_text.stroke-1"),sQuery(id+"FHMxAyK4CFUKdhS_1.wireOp",EDGE,"1cb9c079-ea9b-4899-8069-e0e3048e911d.sketch_text.stroke-2"),sQuery(id+"FHMxAyK4CFUKdhS_1.wireOp",EDGE,"1cb9c079-ea9b-4899-8069-e0e3048e911d.sketch_text.stroke-3"),sQuery(id+"FHMxAyK4CFUKdhS_1.wireOp",EDGE,"1cb9c079-ea9b-4899-8069-e0e3048e911d.sketch_text.stroke-4"),sQuery(id+"FHMxAyK4CFUKdhS_1.wireOp",EDGE,"1cb9c079-ea9b-4899-8069-e0e3048e911d.sketch_text.stroke-5"),sQuery(id+"FHMxAyK4CFUKdhS_1.wireOp",EDGE,"1cb9c079-ea9b-4899-8069-e0e3048e911d.sketch_text.stroke-6"),sQuery(id+"FHMxAyK4CFUKdhS_1.wireOp",EDGE,"1cb9c079-ea9b-4899-8069-e0e3048e911d.sketch_text.stroke-7"),sQuery(id+"FHMxAyK4CFUKdhS_1.wireOp",EDGE,"1cb9c079-ea9b-4899-8069-e0e3048e911d.sketch_text.stroke-8"),sQuery(id+"FHMxAyK4CFUKdhS_1.wireOp",EDGE,"1cb9c079-ea9b-4899-8069-e0e3048e911d.sketch_text.stroke-9"),sQuery(id+"FHMxAyK4CFUKdhS_1.wireOp",EDGE,"1cb9c079-ea9b-4899-8069-e0e3048e911d.sketch_text.stroke-10"),sQuery(id+"FHMxAyK4CFUKdhS_1.wireOp",EDGE,"1cb9c079-ea9b-4899-8069-e0e3048e911d.sketch_text.stroke-11"),sQuery(id+"FHMxAyK4CFUKdhS_1.wireOp",EDGE,"1cb9c079-ea9b-4899-8069-e0e3048e911d.sketch_text.stroke-12"),sQuery(id+"FHMxAyK4CFUKdhS_1.wireOp",EDGE,"1cb9c079-ea9b-4899-8069-e0e3048e911d.sketch_text.stroke-13"),sQuery(id+"FHMxAyK4CFUKdhS_1.wireOp",EDGE,"1cb9c079-ea9b-4899-8069-e0e3048e911d.sketch_text.stroke-14"),sQuery(id+"FHMxAyK4CFUKdhS_1.wireOp",EDGE,"1cb9c079-ea9b-4899-8069-e0e3048e911d.sketch_text.stroke-15"),sQuery(id+"FHMxAyK4CFUKdhS_1.wireOp",EDGE,"1cb9c079-ea9b-4899-8069-e0e3048e911d.sketch_text.stroke-16"),sQuery(id+"FHMxAyK4CFUKdhS_1.wireOp",EDGE,"1cb9c079-ea9b-4899-8069-e0e3048e911d.sketch_text.stroke-17"),sQuery(id+"FHMxAyK4CFUKdhS_1.wireOp",EDGE,"1cb9c079-ea9b-4899-8069-e0e3048e911d.sketch_text.stroke-18"),sQuery(id+"FHMxAyK4CFUKdhS_1.wireOp",EDGE,"1cb9c079-ea9b-4899-8069-e0e3048e911d.sketch_text.stroke-19"),sQuery(id+"FHMxAyK4CFUKdhS_1.wireOp",EDGE,"1cb9c079-ea9b-4899-8069-e0e3048e911d.sketch_text.stroke-20"),sQuery(id+"FHMxAyK4CFUKdhS_1.wireOp",EDGE,"1cb9c079-ea9b-4899-8069-e0e3048e911d.sketch_text.stroke-21"),sQuery(id+"FHMxAyK4CFUKdhS_1.wireOp",EDGE,"1cb9c079-ea9b-4899-8069-e0e3048e911d.sketch_text.stroke-22"),sQuery(id+"FHMxAyK4CFUKdhS_1.wireOp",EDGE,"1cb9c079-ea9b-4899-8069-e0e3048e911d.sketch_text.stroke-23"),sQuery(id+"FHMxAyK4CFUKdhS_1.wireOp",EDGE,"1cb9c079-ea9b-4899-8069-e0e3048e911d.sketch_text.stroke-24"),sQuery(id+"FHMxAyK4CFUKdhS_1.wireOp",EDGE,"1cb9c079-ea9b-4899-8069-e0e3048e911d.sketch_text.stroke-25"),sQuery(id+"FHMxAyK4CFUKdhS_1.wireOp",EDGE,"1cb9c079-ea9b-4899-8069-e0e3048e911d.sketch_text.stroke-26"),sQuery(id+"FHMxAyK4CFUKdhS_1.wireOp",EDGE,"1cb9c079-ea9b-4899-8069-e0e3048e911d.sketch_text.stroke-27"),sQuery(id+"FHMxAyK4CFUKdhS_1.wireOp",EDGE,"1cb9c079-ea9b-4899-8069-e0e3048e911d.sketch_text.stroke-28"),sQuery(id+"FHMxAyK4CFUKdhS_1.wireOp",EDGE,"1cb9c079-ea9b-4899-8069-e0e3048e911d.sketch_text.stroke-29"),sQuery(id+"FHMxAyK4CFUKdhS_1.wireOp",EDGE,"1cb9c079-ea9b-4899-8069-e0e3048e911d.sketch_text.stroke-30"),sQuery(id+"FHMxAyK4CFUKdhS_1.wireOp",EDGE,"1cb9c079-ea9b-4899-8069-e0e3048e911d.sketch_text.stroke-31"),sQuery(id+"FHMxAyK4CFUKdhS_1.wireOp",EDGE,"1cb9c079-ea9b-4899-8069-e0e3048e911d.sketch_text.stroke-32"),sQuery(id+"FHMxAyK4CFUKdhS_1.wireOp",EDGE,"1cb9c079-ea9b-4899-8069-e0e3048e911d.sketch_text.stroke-33"),sQuery(id+"FHMxAyK4CFUKdhS_1.wireOp",EDGE,"1cb9c079-ea9b-4899-8069-e0e3048e911d.sketch_text.stroke-34"),sQuery(id+"FHMxAyK4CFUKdhS_1.wireOp",EDGE,"1cb9c079-ea9b-4899-8069-e0e3048e911d.sketch_text.stroke-35"),sQuery(id+"FHMxAyK4CFUKdhS_1.wireOp",EDGE,"1cb9c079-ea9b-4899-8069-e0e3048e911d.sketch_text.stroke-36"),sQuery(id+"FHMxAyK4CFUKdhS_1.wireOp",EDGE,"1cb9c079-ea9b-4899-8069-e0e3048e911d.sketch_text.stroke-37"),sQuery(id+"FHMxAyK4CFUKdhS_1.wireOp",EDGE,"1cb9c079-ea9b-4899-8069-e0e3048e911d.sketch_text.stroke-38"),sQuery(id+"FHMxAyK4CFUKdhS_1.wireOp",EDGE,"1cb9c079-ea9b-4899-8069-e0e3048e911d.sketch_text.stroke-39"),sQuery(id+"FHMxAyK4CFUKdhS_1.wireOp",EDGE,"1cb9c079-ea9b-4899-8069-e0e3048e911d.sketch_text.stroke-40"),sQuery(id+"FHMxAyK4CFUKdhS_1.wireOp",EDGE,"1cb9c079-ea9b-4899-8069-e0e3048e911d.sketch_text.stroke-41"),sQuery(id+"FHMxAyK4CFUKdhS_1.wireOp",EDGE,"1cb9c079-ea9b-4899-8069-e0e3048e911d.sketch_text.stroke-42"),sQuery(id+"FHMxAyK4CFUKdhS_1.wireOp",EDGE,"1cb9c079-ea9b-4899-8069-e0e3048e911d.sketch_text.stroke-43"),sQuery(id+"FHMxAyK4CFUKdhS_1.wireOp",EDGE,"1cb9c079-ea9b-4899-8069-e0e3048e911d.sketch_text.stroke-44"),sQuery(id+"FHMxAyK4CFUKdhS_1.wireOp",EDGE,"1cb9c079-ea9b-4899-8069-e0e3048e911d.sketch_text.stroke-45"),sQuery(id+"FHMxAyK4CFUKdhS_1.wireOp",EDGE,"1cb9c079-ea9b-4899-8069-e0e3048e911d.sketch_text.stroke-46"),sQuery(id+"FHMxAyK4CFUKdhS_1.wireOp",EDGE,"1cb9c079-ea9b-4899-8069-e0e3048e911d.sketch_text.stroke-47"),sQuery(id+"FHMxAyK4CFUKdhS_1.wireOp",EDGE,"1cb9c079-ea9b-4899-8069-e0e3048e911d.sketch_text.stroke-48"),sQuery(id+"FHMxAyK4CFUKdhS_1.wireOp",EDGE,"1cb9c079-ea9b-4899-8069-e0e3048e911d.sketch_text.stroke-49"),sQuery(id+"FHMxAyK4CFUKdhS_1.wireOp",EDGE,"1cb9c079-ea9b-4899-8069-e0e3048e911d.sketch_text.stroke-50"),sQuery(id+"FHMxAyK4CFUKdhS_1.wireOp",EDGE,"1cb9c079-ea9b-4899-8069-e0e3048e911d.sketch_text.stroke-51"),sQuery(id+"FHMxAyK4CFUKdhS_1.wireOp",EDGE,"1cb9c079-ea9b-4899-8069-e0e3048e911d.sketch_text.stroke-52"),sQuery(id+"FHMxAyK4CFUKdhS_1.wireOp",EDGE,"1cb9c079-ea9b-4899-8069-e0e3048e911d.sketch_text.stroke-53"),sQuery(id+"FHMxAyK4CFUKdhS_1.wireOp",EDGE,"1cb9c079-ea9b-4899-8069-e0e3048e911d.sketch_text.stroke-54"),sQuery(id+"FHMxAyK4CFUKdhS_1.wireOp",EDGE,"1cb9c079-ea9b-4899-8069-e0e3048e911d.sketch_text.stroke-55"),sQuery(id+"FHMxAyK4CFUKdhS_1.wireOp",EDGE,"1cb9c079-ea9b-4899-8069-e0e3048e911d.sketch_text.stroke-56"),sQuery(id+"FHMxAyK4CFUKdhS_1.wireOp",EDGE,"1cb9c079-ea9b-4899-8069-e0e3048e911d.sketch_text.stroke-57"),sQuery(id+"FHMxAyK4CFUKdhS_1.wireOp",EDGE,"1cb9c079-ea9b-4899-8069-e0e3048e911d.sketch_text.stroke-58"),sQuery(id+"FHMxAyK4CFUKdhS_1.wireOp",EDGE,"1cb9c079-ea9b-4899-8069-e0e3048e911d.sketch_text.stroke-59"),sQuery(id+"FHMxAyK4CFUKdhS_1.wireOp",EDGE,"1cb9c079-ea9b-4899-8069-e0e3048e911d.sketch_text.stroke-60"),sQuery(id+"FHMxAyK4CFUKdhS_1.wireOp",EDGE,"1cb9c079-ea9b-4899-8069-e0e3048e911d.sketch_text.stroke-61"),sQuery(id+"FHMxAyK4CFUKdhS_1.wireOp",EDGE,"1cb9c079-ea9b-4899-8069-e0e3048e911d.sketch_text.stroke-62"),sQuery(id+"FHMxAyK4CFUKdhS_1.wireOp",EDGE,"1cb9c079-ea9b-4899-8069-e0e3048e911d.sketch_text.stroke-71"),sQuery(id+"FHMxAyK4CFUKdhS_1.wireOp",EDGE,"1cb9c079-ea9b-4899-8069-e0e3048e911d.sketch_text.stroke-72"),sQuery(id+"FHMxAyK4CFUKdhS_1.wireOp",EDGE,"1cb9c079-ea9b-4899-8069-e0e3048e911d.sketch_text.stroke-73"),sQuery(id+"FHMxAyK4CFUKdhS_1.wireOp",EDGE,"1cb9c079-ea9b-4899-8069-e0e3048e911d.sketch_text.stroke-74"),sQuery(id+"FHMxAyK4CFUKdhS_1.wireOp",EDGE,"1cb9c079-ea9b-4899-8069-e0e3048e911d.sketch_text.stroke-75"),sQuery(id+"FHMxAyK4CFUKdhS_1.wireOp",EDGE,"1cb9c079-ea9b-4899-8069-e0e3048e911d.sketch_text.stroke-76"),sQuery(id+"FHMxAyK4CFUKdhS_1.wireOp",EDGE,"1cb9c079-ea9b-4899-8069-e0e3048e911d.sketch_text.stroke-77"),sQuery(id+"FHMxAyK4CFUKdhS_1.wireOp",EDGE,"1cb9c079-ea9b-4899-8069-e0e3048e911d.sketch_text.stroke-78"),sQuery(id+"FHMxAyK4CFUKdhS_1.wireOp",EDGE,"1cb9c079-ea9b-4899-8069-e0e3048e911d.sketch_text.stroke-79"),sQuery(id+"FHMxAyK4CFUKdhS_1.wireOp",EDGE,"1cb9c079-ea9b-4899-8069-e0e3048e911d.sketch_text.stroke-80"),sQuery(id+"FHMxAyK4CFUKdhS_1.wireOp",EDGE,"1cb9c079-ea9b-4899-8069-e0e3048e911d.sketch_text.stroke-81"),sQuery(id+"FHMxAyK4CFUKdhS_1.wireOp",EDGE,"1cb9c079-ea9b-4899-8069-e0e3048e911d.sketch_text.stroke-82"),sQuery(id+"FHMxAyK4CFUKdhS_1.wireOp",EDGE,"1cb9c079-ea9b-4899-8069-e0e3048e911d.sketch_text.stroke-83"),sQuery(id+"FHMxAyK4CFUKdhS_1.wireOp",EDGE,"1cb9c079-ea9b-4899-8069-e0e3048e911d.sketch_text.stroke-84"),sQuery(id+"FHMxAyK4CFUKdhS_1.wireOp",EDGE,"1cb9c079-ea9b-4899-8069-e0e3048e911d.sketch_text.stroke-85"),sQuery(id+"FHMxAyK4CFUKdhS_1.wireOp",EDGE,"1cb9c079-ea9b-4899-8069-e0e3048e911d.sketch_text.stroke-86"),sQuery(id+"FHMxAyK4CFUKdhS_1.wireOp",EDGE,"1cb9c079-ea9b-4899-8069-e0e3048e911d.sketch_text.stroke-87"),sQuery(id+"FHMxAyK4CFUKdhS_1.wireOp",EDGE,"1cb9c079-ea9b-4899-8069-e0e3048e911d.sketch_text.stroke-88"),sQuery(id+"FHMxAyK4CFUKdhS_1.wireOp",EDGE,"1cb9c079-ea9b-4899-8069-e0e3048e911d.sketch_text.stroke-89"),sQuery(id+"FHMxAyK4CFUKdhS_1.wireOp",EDGE,"1cb9c079-ea9b-4899-8069-e0e3048e911d.sketch_text.stroke-90"),sQuery(id+"FHMxAyK4CFUKdhS_1.wireOp",EDGE,"1cb9c079-ea9b-4899-8069-e0e3048e911d.sketch_text.stroke-91"),sQuery(id+"FHMxAyK4CFUKdhS_1.wireOp",EDGE,"1cb9c079-ea9b-4899-8069-e0e3048e911d.sketch_text.stroke-92"),sQuery(id+"FHMxAyK4CFUKdhS_1.wireOp",EDGE,"1cb9c079-ea9b-4899-8069-e0e3048e911d.sketch_text.stroke-93"),sQuery(id+"FHMxAyK4CFUKdhS_1.wireOp",EDGE,"1cb9c079-ea9b-4899-8069-e0e3048e911d.sketch_text.stroke-94"),sQuery(id+"FHMxAyK4CFUKdhS_1.wireOp",EDGE,"1cb9c079-ea9b-4899-8069-e0e3048e911d.sketch_text.stroke-95"),sQuery(id+"FHMxAyK4CFUKdhS_1.wireOp",EDGE,"1cb9c079-ea9b-4899-8069-e0e3048e911d.sketch_text.stroke-96"),sQuery(id+"FHMxAyK4CFUKdhS_1.wireOp",EDGE,"1cb9c079-ea9b-4899-8069-e0e3048e911d.sketch_text.stroke-97"),sQuery(id+"FHMxAyK4CFUKdhS_1.wireOp",EDGE,"1cb9c079-ea9b-4899-8069-e0e3048e911d.sketch_text.stroke-103"),sQuery(id+"FHMxAyK4CFUKdhS_1.wireOp",EDGE,"1cb9c079-ea9b-4899-8069-e0e3048e911d.sketch_text.stroke-104"),sQuery(id+"FHMxAyK4CFUKdhS_1.wireOp",EDGE,"1cb9c079-ea9b-4899-8069-e0e3048e911d.sketch_text.stroke-105"),sQuery(id+"FHMxAyK4CFUKdhS_1.wireOp",EDGE,"1cb9c079-ea9b-4899-8069-e0e3048e911d.sketch_text.stroke-106"),sQuery(id+"FHMxAyK4CFUKdhS_1.wireOp",EDGE,"1cb9c079-ea9b-4899-8069-e0e3048e911d.sketch_text.stroke-107"),sQuery(id+"FHMxAyK4CFUKdhS_1.wireOp",EDGE,"1cb9c079-ea9b-4899-8069-e0e3048e911d.sketch_text.stroke-108"),sQuery(id+"FHMxAyK4CFUKdhS_1.wireOp",EDGE,"1cb9c079-ea9b-4899-8069-e0e3048e911d.sketch_text.stroke-109"),sQuery(id+"FHMxAyK4CFUKdhS_1.wireOp",EDGE,"1cb9c079-ea9b-4899-8069-e0e3048e911d.sketch_text.stroke-110"),sQuery(id+"FHMxAyK4CFUKdhS_1.wireOp",EDGE,"1cb9c079-ea9b-4899-8069-e0e3048e911d.sketch_text.stroke-111"),sQuery(id+"FHMxAyK4CFUKdhS_1.wireOp",EDGE,"1cb9c079-ea9b-4899-8069-e0e3048e911d.sketch_text.stroke-112"),sQuery(id+"FHMxAyK4CFUKdhS_1.wireOp",EDGE,"1cb9c079-ea9b-4899-8069-e0e3048e911d.sketch_text.stroke-113"),sQuery(id+"FHMxAyK4CFUKdhS_1.wireOp",EDGE,"1cb9c079-ea9b-4899-8069-e0e3048e911d.sketch_text.stroke-114"),sQuery(id+"FHMxAyK4CFUKdhS_1.wireOp",EDGE,"1cb9c079-ea9b-4899-8069-e0e3048e911d.sketch_text.stroke-115"),sQuery(id+"FHMxAyK4CFUKdhS_1.wireOp",EDGE,"1cb9c079-ea9b-4899-8069-e0e3048e911d.sketch_text.stroke-116"),sQuery(id+"FHMxAyK4CFUKdhS_1.wireOp",EDGE,"1cb9c079-ea9b-4899-8069-e0e3048e911d.sketch_text.stroke-117"),sQuery(id+"FHMxAyK4CFUKdhS_1.wireOp",EDGE,"1cb9c079-ea9b-4899-8069-e0e3048e911d.sketch_text.stroke-118"),sQuery(id+"FHMxAyK4CFUKdhS_1.wireOp",EDGE,"1cb9c079-ea9b-4899-8069-e0e3048e911d.sketch_text.stroke-119"),sQuery(id+"FHMxAyK4CFUKdhS_1.wireOp",EDGE,"1cb9c079-ea9b-4899-8069-e0e3048e911d.sketch_text.stroke-120"),sQuery(id+"FHMxAyK4CFUKdhS_1.wireOp",EDGE,"1cb9c079-ea9b-4899-8069-e0e3048e911d.sketch_text.stroke-121"),sQuery(id+"FHMxAyK4CFUKdhS_1.wireOp",EDGE,"1cb9c079-ea9b-4899-8069-e0e3048e911d.sketch_text.stroke-122"),sQuery(id+"FHMxAyK4CFUKdhS_1.wireOp",EDGE,"1cb9c079-ea9b-4899-8069-e0e3048e911d.sketch_text.stroke-123"),sQuery(id+"FHMxAyK4CFUKdhS_1.wireOp",EDGE,"1cb9c079-ea9b-4899-8069-e0e3048e911d.sketch_text.stroke-124"),sQuery(id+"FHMxAyK4CFUKdhS_1.wireOp",EDGE,"1cb9c079-ea9b-4899-8069-e0e3048e911d.sketch_text.stroke-125"),sQuery(id+"FHMxAyK4CFUKdhS_1.wireOp",EDGE,"1cb9c079-ea9b-4899-8069-e0e3048e911d.sketch_text.stroke-126"),sQuery(id+"FHMxAyK4CFUKdhS_1.wireOp",EDGE,"1cb9c079-ea9b-4899-8069-e0e3048e911d.sketch_text.stroke-127"),sQuery(id+"FHMxAyK4CFUKdhS_1.wireOp",EDGE,"1cb9c079-ea9b-4899-8069-e0e3048e911d.sketch_text.stroke-128"),sQuery(id+"FHMxAyK4CFUKdhS_1.wireOp",EDGE,"1cb9c079-ea9b-4899-8069-e0e3048e911d.sketch_text.stroke-129"),sQuery(id+"FHMxAyK4CFUKdhS_1.wireOp",EDGE,"1cb9c079-ea9b-4899-8069-e0e3048e911d.sketch_text.stroke-130"),sQuery(id+"FHMxAyK4CFUKdhS_1.wireOp",EDGE,"1cb9c079-ea9b-4899-8069-e0e3048e911d.sketch_text.stroke-131"),sQuery(id+"FHMxAyK4CFUKdhS_1.wireOp",EDGE,"1cb9c079-ea9b-4899-8069-e0e3048e911d.sketch_text.stroke-132"),sQuery(id+"FHMxAyK4CFUKdhS_1.wireOp",EDGE,"1cb9c079-ea9b-4899-8069-e0e3048e911d.sketch_text.stroke-133"),sQuery(id+"FHMxAyK4CFUKdhS_1.wireOp",EDGE,"1cb9c079-ea9b-4899-8069-e0e3048e911d.sketch_text.stroke-134"),sQuery(id+"FHMxAyK4CFUKdhS_1.wireOp",EDGE,"1cb9c079-ea9b-4899-8069-e0e3048e911d.sketch_text.stroke-135"),sQuery(id+"FHMxAyK4CFUKdhS_1.wireOp",EDGE,"1cb9c079-ea9b-4899-8069-e0e3048e911d.sketch_text.stroke-136"),sQuery(id+"FHMxAyK4CFUKdhS_1.wireOp",EDGE,"1cb9c079-ea9b-4899-8069-e0e3048e911d.sketch_text.stroke-137"),sQuery(id+"FHMxAyK4CFUKdhS_1.wireOp",EDGE,"1cb9c079-ea9b-4899-8069-e0e3048e911d.sketch_text.stroke-138"),sQuery(id+"FHMxAyK4CFUKdhS_1.wireOp",EDGE,"1cb9c079-ea9b-4899-8069-e0e3048e911d.sketch_text.stroke-139"),sQuery(id+"FHMxAyK4CFUKdhS_1.wireOp",EDGE,"1cb9c079-ea9b-4899-8069-e0e3048e911d.sketch_text.stroke-140"),sQuery(id+"FHMxAyK4CFUKdhS_1.wireOp",EDGE,"1cb9c079-ea9b-4899-8069-e0e3048e911d.sketch_text.stroke-141"),sQuery(id+"FHMxAyK4CFUKdhS_1.wireOp",EDGE,"1cb9c079-ea9b-4899-8069-e0e3048e911d.sketch_text.stroke-142"),sQuery(id+"FHMxAyK4CFUKdhS_1.wireOp",EDGE,"1cb9c079-ea9b-4899-8069-e0e3048e911d.sketch_text.stroke-143"),sQuery(id+"FHMxAyK4CFUKdhS_1.wireOp",EDGE,"1cb9c079-ea9b-4899-8069-e0e3048e911d.sketch_text.stroke-144"),sQuery(id+"FHMxAyK4CFUKdhS_1.wireOp",EDGE,"1cb9c079-ea9b-4899-8069-e0e3048e911d.sketch_text.stroke-145"),sQuery(id+"FHMxAyK4CFUKdhS_1.wireOp",EDGE,"1cb9c079-ea9b-4899-8069-e0e3048e911d.sketch_text.stroke-146"),sQuery(id+"FHMxAyK4CFUKdhS_1.wireOp",EDGE,"1cb9c079-ea9b-4899-8069-e0e3048e911d.sketch_text.stroke-147"),sQuery(id+"FHMxAyK4CFUKdhS_1.wireOp",EDGE,"1cb9c079-ea9b-4899-8069-e0e3048e911d.sketch_text.stroke-148"),sQuery(id+"FHMxAyK4CFUKdhS_1.wireOp",EDGE,"1cb9c079-ea9b-4899-8069-e0e3048e911d.sketch_text.stroke-149"),sQuery(id+"FHMxAyK4CFUKdhS_1.wireOp",EDGE,"1cb9c079-ea9b-4899-8069-e0e3048e911d.sketch_text.stroke-150"),sQuery(id+"FHMxAyK4CFUKdhS_1.wireOp",EDGE,"1cb9c079-ea9b-4899-8069-e0e3048e911d.sketch_text.stroke-151"),sQuery(id+"FHMxAyK4CFUKdhS_1.wireOp",EDGE,"1cb9c079-ea9b-4899-8069-e0e3048e911d.sketch_text.stroke-152"),sQuery(id+"FHMxAyK4CFUKdhS_1.wireOp",EDGE,"1cb9c079-ea9b-4899-8069-e0e3048e911d.sketch_text.stroke-153"),sQuery(id+"FHMxAyK4CFUKdhS_1.wireOp",EDGE,"1cb9c079-ea9b-4899-8069-e0e3048e911d.sketch_text.stroke-159"),sQuery(id+"FHMxAyK4CFUKdhS_1.wireOp",EDGE,"1cb9c079-ea9b-4899-8069-e0e3048e911d.sketch_text.stroke-160"),sQuery(id+"FHMxAyK4CFUKdhS_1.wireOp",EDGE,"1cb9c079-ea9b-4899-8069-e0e3048e911d.sketch_text.stroke-161"),sQuery(id+"FHMxAyK4CFUKdhS_1.wireOp",EDGE,"1cb9c079-ea9b-4899-8069-e0e3048e911d.sketch_text.stroke-162"),sQuery(id+"FHMxAyK4CFUKdhS_1.wireOp",EDGE,"1cb9c079-ea9b-4899-8069-e0e3048e911d.sketch_text.stroke-163"),sQuery(id+"FHMxAyK4CFUKdhS_1.wireOp",EDGE,"1cb9c079-ea9b-4899-8069-e0e3048e911d.sketch_text.stroke-164"),sQuery(id+"FHMxAyK4CFUKdhS_1.wireOp",EDGE,"1cb9c079-ea9b-4899-8069-e0e3048e911d.sketch_text.stroke-165"),sQuery(id+"FHMxAyK4CFUKdhS_1.wireOp",EDGE,"1cb9c079-ea9b-4899-8069-e0e3048e911d.sketch_text.stroke-166"),sQuery(id+"FHMxAyK4CFUKdhS_1.wireOp",EDGE,"1cb9c079-ea9b-4899-8069-e0e3048e911d.sketch_text.stroke-167"),sQuery(id+"FHMxAyK4CFUKdhS_1.wireOp",EDGE,"1cb9c079-ea9b-4899-8069-e0e3048e911d.sketch_text.stroke-168"),sQuery(id+"FHMxAyK4CFUKdhS_1.wireOp",EDGE,"1cb9c079-ea9b-4899-8069-e0e3048e911d.sketch_text.stroke-169"),sQuery(id+"FHMxAyK4CFUKdhS_1.wireOp",EDGE,"1cb9c079-ea9b-4899-8069-e0e3048e911d.sketch_text.stroke-170"),sQuery(id+"FHMxAyK4CFUKdhS_1.wireOp",EDGE,"1cb9c079-ea9b-4899-8069-e0e3048e911d.sketch_text.stroke-171"),sQuery(id+"FHMxAyK4CFUKdhS_1.wireOp",EDGE,"1cb9c079-ea9b-4899-8069-e0e3048e911d.sketch_text.stroke-172"),sQuery(id+"FHMxAyK4CFUKdhS_1.wireOp",EDGE,"1cb9c079-ea9b-4899-8069-e0e3048e911d.sketch_text.stroke-173"),sQuery(id+"FHMxAyK4CFUKdhS_1.wireOp",EDGE,"1cb9c079-ea9b-4899-8069-e0e3048e911d.sketch_text.stroke-174"),sQuery(id+"FHMxAyK4CFUKdhS_1.wireOp",EDGE,"1cb9c079-ea9b-4899-8069-e0e3048e911d.sketch_text.stroke-175"),sQuery(id+"FHMxAyK4CFUKdhS_1.wireOp",EDGE,"1cb9c079-ea9b-4899-8069-e0e3048e911d.sketch_text.stroke-176"),sQuery(id+"FHMxAyK4CFUKdhS_1.wireOp",EDGE,"1cb9c079-ea9b-4899-8069-e0e3048e911d.sketch_text.stroke-177"),sQuery(id+"FHMxAyK4CFUKdhS_1.wireOp",EDGE,"1cb9c079-ea9b-4899-8069-e0e3048e911d.sketch_text.stroke-178"),sQuery(id+"FHMxAyK4CFUKdhS_1.wireOp",EDGE,"1cb9c079-ea9b-4899-8069-e0e3048e911d.sketch_text.stroke-179"),sQuery(id+"FHMxAyK4CFUKdhS_1.wireOp",EDGE,"1cb9c079-ea9b-4899-8069-e0e3048e911d.sketch_text.stroke-180"),sQuery(id+"F2.wireOp",EDGE,"8007402e-1a4e-4a06-85a5-2af08e553504"),subQ2])],"isStart":true}),makeQuery(id+"F3.opExtrude","SWEPT_FACE",FACE,{"disambiguationData":[OSD([subQ2])]})]),OD(0.0)],"derivedFrom":makeQuery(id+"F1.opExtrude","CAP_EDGE",EDGE,{"disambiguationData":[OSD([subQ0])],"isStart":false})});}
            var Q12;
            {var subQ0=sQuery(id+"F0.wireOp",EDGE,"E0.top");var subQ1=sQuery(id+"F0.wireOp",EDGE,"E0.bottom");var subQ2=sQuery(id+"F2.wireOp",EDGE,"6ee83ff3-586e-4dbe-aaea-af71240543bd");Q12=makeQuery(id+"F3.boolean.opBoolean","SPLIT",EDGE,{"disambiguationData":[TD([makeQuery(id+"F1.opExtrude","CAP_FACE",FACE,{"disambiguationData":[OSD([subQ1,subQ0,sQuery(id+"F0.wireOp",EDGE,"E0.left"),sQuery(id+"F0.wireOp",EDGE,"E0.right")])],"isStart":false}),makeQuery(id+"F1.opExtrude","SWEPT_FACE",FACE,{"disambiguationData":[OSD([subQ0])]}),makeQuery(id+"F3.opExtrude","CAP_FACE",FACE,{"disambiguationData":[OSD([subQ1,sQuery(id+"FQ5JFwxVdaqARUP_1.wireOp",EDGE,"fcba4419-a2ee-464f-be9d-58f11bf3418b.sketch_text.stroke-0"),sQuery(id+"FQ5JFwxVdaqARUP_1.wireOp",EDGE,"fcba4419-a2ee-464f-be9d-58f11bf3418b.sketch_text.stroke-1"),sQuery(id+"FQ5JFwxVdaqARUP_1.wireOp",EDGE,"fcba4419-a2ee-464f-be9d-58f11bf3418b.sketch_text.stroke-2"),sQuery(id+"FQ5JFwxVdaqARUP_1.wireOp",EDGE,"fcba4419-a2ee-464f-be9d-58f11bf3418b.sketch_text.stroke-3"),sQuery(id+"FQ5JFwxVdaqARUP_1.wireOp",EDGE,"fcba4419-a2ee-464f-be9d-58f11bf3418b.sketch_text.stroke-4"),sQuery(id+"FQ5JFwxVdaqARUP_1.wireOp",EDGE,"fcba4419-a2ee-464f-be9d-58f11bf3418b.sketch_text.stroke-5"),sQuery(id+"FQ5JFwxVdaqARUP_1.wireOp",EDGE,"fcba4419-a2ee-464f-be9d-58f11bf3418b.sketch_text.stroke-6"),sQuery(id+"FQ5JFwxVdaqARUP_1.wireOp",EDGE,"fcba4419-a2ee-464f-be9d-58f11bf3418b.sketch_text.stroke-7"),sQuery(id+"FQ5JFwxVdaqARUP_1.wireOp",EDGE,"fcba4419-a2ee-464f-be9d-58f11bf3418b.sketch_text.stroke-8"),sQuery(id+"FQ5JFwxVdaqARUP_1.wireOp",EDGE,"fcba4419-a2ee-464f-be9d-58f11bf3418b.sketch_text.stroke-9"),sQuery(id+"FQ5JFwxVdaqARUP_1.wireOp",EDGE,"fcba4419-a2ee-464f-be9d-58f11bf3418b.sketch_text.stroke-10"),sQuery(id+"FQ5JFwxVdaqARUP_1.wireOp",EDGE,"fcba4419-a2ee-464f-be9d-58f11bf3418b.sketch_text.stroke-11"),sQuery(id+"FQ5JFwxVdaqARUP_1.wireOp",EDGE,"fcba4419-a2ee-464f-be9d-58f11bf3418b.sketch_text.stroke-12"),sQuery(id+"FQ5JFwxVdaqARUP_1.wireOp",EDGE,"fcba4419-a2ee-464f-be9d-58f11bf3418b.sketch_text.stroke-13"),sQuery(id+"FQ5JFwxVdaqARUP_1.wireOp",EDGE,"fcba4419-a2ee-464f-be9d-58f11bf3418b.sketch_text.stroke-14"),sQuery(id+"FQ5JFwxVdaqARUP_1.wireOp",EDGE,"fcba4419-a2ee-464f-be9d-58f11bf3418b.sketch_text.stroke-15"),sQuery(id+"FQ5JFwxVdaqARUP_1.wireOp",EDGE,"fcba4419-a2ee-464f-be9d-58f11bf3418b.sketch_text.stroke-16"),sQuery(id+"FQ5JFwxVdaqARUP_1.wireOp",EDGE,"fcba4419-a2ee-464f-be9d-58f11bf3418b.sketch_text.stroke-17"),sQuery(id+"FQ5JFwxVdaqARUP_1.wireOp",EDGE,"fcba4419-a2ee-464f-be9d-58f11bf3418b.sketch_text.stroke-18"),sQuery(id+"FQ5JFwxVdaqARUP_1.wireOp",EDGE,"fcba4419-a2ee-464f-be9d-58f11bf3418b.sketch_text.stroke-19"),sQuery(id+"FQ5JFwxVdaqARUP_1.wireOp",EDGE,"fcba4419-a2ee-464f-be9d-58f11bf3418b.sketch_text.stroke-20"),sQuery(id+"FQ5JFwxVdaqARUP_1.wireOp",EDGE,"fcba4419-a2ee-464f-be9d-58f11bf3418b.sketch_text.stroke-21"),sQuery(id+"FQ5JFwxVdaqARUP_1.wireOp",EDGE,"fcba4419-a2ee-464f-be9d-58f11bf3418b.sketch_text.stroke-22"),sQuery(id+"FQ5JFwxVdaqARUP_1.wireOp",EDGE,"fcba4419-a2ee-464f-be9d-58f11bf3418b.sketch_text.stroke-23"),sQuery(id+"FQ5JFwxVdaqARUP_1.wireOp",EDGE,"fcba4419-a2ee-464f-be9d-58f11bf3418b.sketch_text.stroke-24"),sQuery(id+"FQ5JFwxVdaqARUP_1.wireOp",EDGE,"fcba4419-a2ee-464f-be9d-58f11bf3418b.sketch_text.stroke-25"),sQuery(id+"FQ5JFwxVdaqARUP_1.wireOp",EDGE,"fcba4419-a2ee-464f-be9d-58f11bf3418b.sketch_text.stroke-26"),sQuery(id+"FQ5JFwxVdaqARUP_1.wireOp",EDGE,"fcba4419-a2ee-464f-be9d-58f11bf3418b.sketch_text.stroke-27"),sQuery(id+"FQ5JFwxVdaqARUP_1.wireOp",EDGE,"fcba4419-a2ee-464f-be9d-58f11bf3418b.sketch_text.stroke-28"),sQuery(id+"FQ5JFwxVdaqARUP_1.wireOp",EDGE,"fcba4419-a2ee-464f-be9d-58f11bf3418b.sketch_text.stroke-29"),sQuery(id+"FQ5JFwxVdaqARUP_1.wireOp",EDGE,"fcba4419-a2ee-464f-be9d-58f11bf3418b.sketch_text.stroke-30"),sQuery(id+"FQ5JFwxVdaqARUP_1.wireOp",EDGE,"fcba4419-a2ee-464f-be9d-58f11bf3418b.sketch_text.stroke-31"),sQuery(id+"FQ5JFwxVdaqARUP_1.wireOp",EDGE,"fcba4419-a2ee-464f-be9d-58f11bf3418b.sketch_text.stroke-32"),sQuery(id+"FQ5JFwxVdaqARUP_1.wireOp",EDGE,"fcba4419-a2ee-464f-be9d-58f11bf3418b.sketch_text.stroke-33"),sQuery(id+"FQ5JFwxVdaqARUP_1.wireOp",EDGE,"fcba4419-a2ee-464f-be9d-58f11bf3418b.sketch_text.stroke-34"),sQuery(id+"FQ5JFwxVdaqARUP_1.wireOp",EDGE,"fcba4419-a2ee-464f-be9d-58f11bf3418b.sketch_text.stroke-35"),sQuery(id+"FQ5JFwxVdaqARUP_1.wireOp",EDGE,"fcba4419-a2ee-464f-be9d-58f11bf3418b.sketch_text.stroke-36"),sQuery(id+"FQ5JFwxVdaqARUP_1.wireOp",EDGE,"fcba4419-a2ee-464f-be9d-58f11bf3418b.sketch_text.stroke-37"),sQuery(id+"FQ5JFwxVdaqARUP_1.wireOp",EDGE,"fcba4419-a2ee-464f-be9d-58f11bf3418b.sketch_text.stroke-38"),sQuery(id+"FQ5JFwxVdaqARUP_1.wireOp",EDGE,"fcba4419-a2ee-464f-be9d-58f11bf3418b.sketch_text.stroke-39"),sQuery(id+"FQ5JFwxVdaqARUP_1.wireOp",EDGE,"fcba4419-a2ee-464f-be9d-58f11bf3418b.sketch_text.stroke-40"),sQuery(id+"FQ5JFwxVdaqARUP_1.wireOp",EDGE,"fcba4419-a2ee-464f-be9d-58f11bf3418b.sketch_text.stroke-41"),sQuery(id+"FQ5JFwxVdaqARUP_1.wireOp",EDGE,"fcba4419-a2ee-464f-be9d-58f11bf3418b.sketch_text.stroke-42"),sQuery(id+"FQ5JFwxVdaqARUP_1.wireOp",EDGE,"fcba4419-a2ee-464f-be9d-58f11bf3418b.sketch_text.stroke-43"),sQuery(id+"FQ5JFwxVdaqARUP_1.wireOp",EDGE,"fcba4419-a2ee-464f-be9d-58f11bf3418b.sketch_text.stroke-44"),sQuery(id+"FQ5JFwxVdaqARUP_1.wireOp",EDGE,"fcba4419-a2ee-464f-be9d-58f11bf3418b.sketch_text.stroke-45"),sQuery(id+"FQ5JFwxVdaqARUP_1.wireOp",EDGE,"fcba4419-a2ee-464f-be9d-58f11bf3418b.sketch_text.stroke-46"),sQuery(id+"FQ5JFwxVdaqARUP_1.wireOp",EDGE,"fcba4419-a2ee-464f-be9d-58f11bf3418b.sketch_text.stroke-47"),sQuery(id+"FQ5JFwxVdaqARUP_1.wireOp",EDGE,"fcba4419-a2ee-464f-be9d-58f11bf3418b.sketch_text.stroke-48"),sQuery(id+"FQ5JFwxVdaqARUP_1.wireOp",EDGE,"fcba4419-a2ee-464f-be9d-58f11bf3418b.sketch_text.stroke-49"),sQuery(id+"FQ5JFwxVdaqARUP_1.wireOp",EDGE,"fcba4419-a2ee-464f-be9d-58f11bf3418b.sketch_text.stroke-50"),sQuery(id+"FQ5JFwxVdaqARUP_1.wireOp",EDGE,"fcba4419-a2ee-464f-be9d-58f11bf3418b.sketch_text.stroke-51"),sQuery(id+"FQ5JFwxVdaqARUP_1.wireOp",EDGE,"fcba4419-a2ee-464f-be9d-58f11bf3418b.sketch_text.stroke-52"),sQuery(id+"FQ5JFwxVdaqARUP_1.wireOp",EDGE,"fcba4419-a2ee-464f-be9d-58f11bf3418b.sketch_text.stroke-53"),sQuery(id+"FQ5JFwxVdaqARUP_1.wireOp",EDGE,"fcba4419-a2ee-464f-be9d-58f11bf3418b.sketch_text.stroke-54"),sQuery(id+"FQ5JFwxVdaqARUP_1.wireOp",EDGE,"fcba4419-a2ee-464f-be9d-58f11bf3418b.sketch_text.stroke-55"),sQuery(id+"FQ5JFwxVdaqARUP_1.wireOp",EDGE,"fcba4419-a2ee-464f-be9d-58f11bf3418b.sketch_text.stroke-56"),sQuery(id+"FQ5JFwxVdaqARUP_1.wireOp",EDGE,"fcba4419-a2ee-464f-be9d-58f11bf3418b.sketch_text.stroke-57"),sQuery(id+"FQ5JFwxVdaqARUP_1.wireOp",EDGE,"fcba4419-a2ee-464f-be9d-58f11bf3418b.sketch_text.stroke-58"),sQuery(id+"FQ5JFwxVdaqARUP_1.wireOp",EDGE,"fcba4419-a2ee-464f-be9d-58f11bf3418b.sketch_text.stroke-59"),sQuery(id+"FQ5JFwxVdaqARUP_1.wireOp",EDGE,"fcba4419-a2ee-464f-be9d-58f11bf3418b.sketch_text.stroke-60"),sQuery(id+"FQ5JFwxVdaqARUP_1.wireOp",EDGE,"fcba4419-a2ee-464f-be9d-58f11bf3418b.sketch_text.stroke-61"),sQuery(id+"FQ5JFwxVdaqARUP_1.wireOp",EDGE,"fcba4419-a2ee-464f-be9d-58f11bf3418b.sketch_text.stroke-62"),sQuery(id+"FQ5JFwxVdaqARUP_1.wireOp",EDGE,"fcba4419-a2ee-464f-be9d-58f11bf3418b.sketch_text.stroke-63"),sQuery(id+"FQ5JFwxVdaqARUP_1.wireOp",EDGE,"fcba4419-a2ee-464f-be9d-58f11bf3418b.sketch_text.stroke-64"),sQuery(id+"FQ5JFwxVdaqARUP_1.wireOp",EDGE,"fcba4419-a2ee-464f-be9d-58f11bf3418b.sketch_text.stroke-65"),sQuery(id+"FQ5JFwxVdaqARUP_1.wireOp",EDGE,"fcba4419-a2ee-464f-be9d-58f11bf3418b.sketch_text.stroke-66"),sQuery(id+"FQ5JFwxVdaqARUP_1.wireOp",EDGE,"fcba4419-a2ee-464f-be9d-58f11bf3418b.sketch_text.stroke-67"),sQuery(id+"FQ5JFwxVdaqARUP_1.wireOp",EDGE,"fcba4419-a2ee-464f-be9d-58f11bf3418b.sketch_text.stroke-68"),sQuery(id+"FQ5JFwxVdaqARUP_1.wireOp",EDGE,"fcba4419-a2ee-464f-be9d-58f11bf3418b.sketch_text.stroke-69"),sQuery(id+"FQ5JFwxVdaqARUP_1.wireOp",EDGE,"fcba4419-a2ee-464f-be9d-58f11bf3418b.sketch_text.stroke-70"),sQuery(id+"FQ5JFwxVdaqARUP_1.wireOp",EDGE,"fcba4419-a2ee-464f-be9d-58f11bf3418b.sketch_text.stroke-71"),sQuery(id+"FQ5JFwxVdaqARUP_1.wireOp",EDGE,"fcba4419-a2ee-464f-be9d-58f11bf3418b.sketch_text.stroke-72"),sQuery(id+"FQ5JFwxVdaqARUP_1.wireOp",EDGE,"fcba4419-a2ee-464f-be9d-58f11bf3418b.sketch_text.stroke-73"),sQuery(id+"FQ5JFwxVdaqARUP_1.wireOp",EDGE,"fcba4419-a2ee-464f-be9d-58f11bf3418b.sketch_text.stroke-74"),sQuery(id+"FQ5JFwxVdaqARUP_1.wireOp",EDGE,"fcba4419-a2ee-464f-be9d-58f11bf3418b.sketch_text.stroke-75"),sQuery(id+"FQ5JFwxVdaqARUP_1.wireOp",EDGE,"fcba4419-a2ee-464f-be9d-58f11bf3418b.sketch_text.stroke-76"),sQuery(id+"FQ5JFwxVdaqARUP_1.wireOp",EDGE,"fcba4419-a2ee-464f-be9d-58f11bf3418b.sketch_text.stroke-77"),sQuery(id+"FQ5JFwxVdaqARUP_1.wireOp",EDGE,"fcba4419-a2ee-464f-be9d-58f11bf3418b.sketch_text.stroke-78"),sQuery(id+"FQ5JFwxVdaqARUP_1.wireOp",EDGE,"fcba4419-a2ee-464f-be9d-58f11bf3418b.sketch_text.stroke-79"),sQuery(id+"FQ5JFwxVdaqARUP_1.wireOp",EDGE,"fcba4419-a2ee-464f-be9d-58f11bf3418b.sketch_text.stroke-80"),sQuery(id+"FQ5JFwxVdaqARUP_1.wireOp",EDGE,"fcba4419-a2ee-464f-be9d-58f11bf3418b.sketch_text.stroke-81"),sQuery(id+"FQ5JFwxVdaqARUP_1.wireOp",EDGE,"fcba4419-a2ee-464f-be9d-58f11bf3418b.sketch_text.stroke-82"),sQuery(id+"FQ5JFwxVdaqARUP_1.wireOp",EDGE,"fcba4419-a2ee-464f-be9d-58f11bf3418b.sketch_text.stroke-83"),sQuery(id+"FQ5JFwxVdaqARUP_1.wireOp",EDGE,"fcba4419-a2ee-464f-be9d-58f11bf3418b.sketch_text.stroke-84"),sQuery(id+"FQ5JFwxVdaqARUP_1.wireOp",EDGE,"fcba4419-a2ee-464f-be9d-58f11bf3418b.sketch_text.stroke-85"),sQuery(id+"FQ5JFwxVdaqARUP_1.wireOp",EDGE,"fcba4419-a2ee-464f-be9d-58f11bf3418b.sketch_text.stroke-86"),sQuery(id+"FQ5JFwxVdaqARUP_1.wireOp",EDGE,"fcba4419-a2ee-464f-be9d-58f11bf3418b.sketch_text.stroke-87"),sQuery(id+"FQ5JFwxVdaqARUP_1.wireOp",EDGE,"fcba4419-a2ee-464f-be9d-58f11bf3418b.sketch_text.stroke-88"),sQuery(id+"FQ5JFwxVdaqARUP_1.wireOp",EDGE,"fcba4419-a2ee-464f-be9d-58f11bf3418b.sketch_text.stroke-89"),sQuery(id+"FQ5JFwxVdaqARUP_1.wireOp",EDGE,"fcba4419-a2ee-464f-be9d-58f11bf3418b.sketch_text.stroke-90"),sQuery(id+"FQ5JFwxVdaqARUP_1.wireOp",EDGE,"fcba4419-a2ee-464f-be9d-58f11bf3418b.sketch_text.stroke-91"),sQuery(id+"FQ5JFwxVdaqARUP_1.wireOp",EDGE,"fcba4419-a2ee-464f-be9d-58f11bf3418b.sketch_text.stroke-92"),sQuery(id+"FQ5JFwxVdaqARUP_1.wireOp",EDGE,"fcba4419-a2ee-464f-be9d-58f11bf3418b.sketch_text.stroke-93"),sQuery(id+"FQ5JFwxVdaqARUP_1.wireOp",EDGE,"fcba4419-a2ee-464f-be9d-58f11bf3418b.sketch_text.stroke-94"),sQuery(id+"FQ5JFwxVdaqARUP_1.wireOp",EDGE,"fcba4419-a2ee-464f-be9d-58f11bf3418b.sketch_text.stroke-95"),sQuery(id+"FQ5JFwxVdaqARUP_1.wireOp",EDGE,"fcba4419-a2ee-464f-be9d-58f11bf3418b.sketch_text.stroke-96"),sQuery(id+"FQ5JFwxVdaqARUP_1.wireOp",EDGE,"fcba4419-a2ee-464f-be9d-58f11bf3418b.sketch_text.stroke-97"),sQuery(id+"FQ5JFwxVdaqARUP_1.wireOp",EDGE,"fcba4419-a2ee-464f-be9d-58f11bf3418b.sketch_text.stroke-98"),sQuery(id+"FQ5JFwxVdaqARUP_1.wireOp",EDGE,"fcba4419-a2ee-464f-be9d-58f11bf3418b.sketch_text.stroke-99"),sQuery(id+"FQ5JFwxVdaqARUP_1.wireOp",EDGE,"fcba4419-a2ee-464f-be9d-58f11bf3418b.sketch_text.stroke-100"),sQuery(id+"FQ5JFwxVdaqARUP_1.wireOp",EDGE,"fcba4419-a2ee-464f-be9d-58f11bf3418b.sketch_text.stroke-101"),sQuery(id+"FQ5JFwxVdaqARUP_1.wireOp",EDGE,"fcba4419-a2ee-464f-be9d-58f11bf3418b.sketch_text.stroke-102"),sQuery(id+"FQ5JFwxVdaqARUP_1.wireOp",EDGE,"fcba4419-a2ee-464f-be9d-58f11bf3418b.sketch_text.stroke-103"),sQuery(id+"FQ5JFwxVdaqARUP_1.wireOp",EDGE,"fcba4419-a2ee-464f-be9d-58f11bf3418b.sketch_text.stroke-104"),sQuery(id+"FQ5JFwxVdaqARUP_1.wireOp",EDGE,"fcba4419-a2ee-464f-be9d-58f11bf3418b.sketch_text.stroke-105"),sQuery(id+"FQ5JFwxVdaqARUP_1.wireOp",EDGE,"fcba4419-a2ee-464f-be9d-58f11bf3418b.sketch_text.stroke-106"),sQuery(id+"FQ5JFwxVdaqARUP_1.wireOp",EDGE,"fcba4419-a2ee-464f-be9d-58f11bf3418b.sketch_text.stroke-107"),sQuery(id+"FQ5JFwxVdaqARUP_1.wireOp",EDGE,"fcba4419-a2ee-464f-be9d-58f11bf3418b.sketch_text.stroke-108"),sQuery(id+"FQ5JFwxVdaqARUP_1.wireOp",EDGE,"fcba4419-a2ee-464f-be9d-58f11bf3418b.sketch_text.stroke-109"),sQuery(id+"FQ5JFwxVdaqARUP_1.wireOp",EDGE,"fcba4419-a2ee-464f-be9d-58f11bf3418b.sketch_text.stroke-110"),sQuery(id+"FQ5JFwxVdaqARUP_1.wireOp",EDGE,"fcba4419-a2ee-464f-be9d-58f11bf3418b.sketch_text.stroke-111"),sQuery(id+"FQ5JFwxVdaqARUP_1.wireOp",EDGE,"fcba4419-a2ee-464f-be9d-58f11bf3418b.sketch_text.stroke-112"),sQuery(id+"FQ5JFwxVdaqARUP_1.wireOp",EDGE,"fcba4419-a2ee-464f-be9d-58f11bf3418b.sketch_text.stroke-113"),sQuery(id+"FQ5JFwxVdaqARUP_1.wireOp",EDGE,"fcba4419-a2ee-464f-be9d-58f11bf3418b.sketch_text.stroke-114"),sQuery(id+"FQ5JFwxVdaqARUP_1.wireOp",EDGE,"fcba4419-a2ee-464f-be9d-58f11bf3418b.sketch_text.stroke-115"),sQuery(id+"FQ5JFwxVdaqARUP_1.wireOp",EDGE,"fcba4419-a2ee-464f-be9d-58f11bf3418b.sketch_text.stroke-116"),sQuery(id+"FQ5JFwxVdaqARUP_1.wireOp",EDGE,"fcba4419-a2ee-464f-be9d-58f11bf3418b.sketch_text.stroke-117"),sQuery(id+"FQ5JFwxVdaqARUP_1.wireOp",EDGE,"fcba4419-a2ee-464f-be9d-58f11bf3418b.sketch_text.stroke-118"),sQuery(id+"FQ5JFwxVdaqARUP_1.wireOp",EDGE,"fcba4419-a2ee-464f-be9d-58f11bf3418b.sketch_text.stroke-119"),sQuery(id+"FQ5JFwxVdaqARUP_1.wireOp",EDGE,"fcba4419-a2ee-464f-be9d-58f11bf3418b.sketch_text.stroke-120"),sQuery(id+"FQ5JFwxVdaqARUP_1.wireOp",EDGE,"fcba4419-a2ee-464f-be9d-58f11bf3418b.sketch_text.stroke-121"),sQuery(id+"FQ5JFwxVdaqARUP_1.wireOp",EDGE,"fcba4419-a2ee-464f-be9d-58f11bf3418b.sketch_text.stroke-122"),sQuery(id+"FQ5JFwxVdaqARUP_1.wireOp",EDGE,"fcba4419-a2ee-464f-be9d-58f11bf3418b.sketch_text.stroke-123"),sQuery(id+"FQ5JFwxVdaqARUP_1.wireOp",EDGE,"fcba4419-a2ee-464f-be9d-58f11bf3418b.sketch_text.stroke-124"),sQuery(id+"FQ5JFwxVdaqARUP_1.wireOp",EDGE,"fcba4419-a2ee-464f-be9d-58f11bf3418b.sketch_text.stroke-125"),sQuery(id+"FQ5JFwxVdaqARUP_1.wireOp",EDGE,"fcba4419-a2ee-464f-be9d-58f11bf3418b.sketch_text.stroke-126"),sQuery(id+"FQ5JFwxVdaqARUP_1.wireOp",EDGE,"fcba4419-a2ee-464f-be9d-58f11bf3418b.sketch_text.stroke-127"),sQuery(id+"FQ5JFwxVdaqARUP_1.wireOp",EDGE,"fcba4419-a2ee-464f-be9d-58f11bf3418b.sketch_text.stroke-128"),sQuery(id+"FQ5JFwxVdaqARUP_1.wireOp",EDGE,"fcba4419-a2ee-464f-be9d-58f11bf3418b.sketch_text.stroke-129"),sQuery(id+"FQ5JFwxVdaqARUP_1.wireOp",EDGE,"fcba4419-a2ee-464f-be9d-58f11bf3418b.sketch_text.stroke-130"),sQuery(id+"FQ5JFwxVdaqARUP_1.wireOp",EDGE,"fcba4419-a2ee-464f-be9d-58f11bf3418b.sketch_text.stroke-131"),sQuery(id+"FQ5JFwxVdaqARUP_1.wireOp",EDGE,"fcba4419-a2ee-464f-be9d-58f11bf3418b.sketch_text.stroke-132"),sQuery(id+"FQ5JFwxVdaqARUP_1.wireOp",EDGE,"fcba4419-a2ee-464f-be9d-58f11bf3418b.sketch_text.stroke-133"),sQuery(id+"FQ5JFwxVdaqARUP_1.wireOp",EDGE,"fcba4419-a2ee-464f-be9d-58f11bf3418b.sketch_text.stroke-134"),sQuery(id+"FQ5JFwxVdaqARUP_1.wireOp",EDGE,"fcba4419-a2ee-464f-be9d-58f11bf3418b.sketch_text.stroke-135"),sQuery(id+"FQ5JFwxVdaqARUP_1.wireOp",EDGE,"fcba4419-a2ee-464f-be9d-58f11bf3418b.sketch_text.stroke-136"),sQuery(id+"FQ5JFwxVdaqARUP_1.wireOp",EDGE,"fcba4419-a2ee-464f-be9d-58f11bf3418b.sketch_text.stroke-137"),sQuery(id+"FQ5JFwxVdaqARUP_1.wireOp",EDGE,"fcba4419-a2ee-464f-be9d-58f11bf3418b.sketch_text.stroke-138"),sQuery(id+"FQ5JFwxVdaqARUP_1.wireOp",EDGE,"fcba4419-a2ee-464f-be9d-58f11bf3418b.sketch_text.stroke-139"),sQuery(id+"FQ5JFwxVdaqARUP_1.wireOp",EDGE,"fcba4419-a2ee-464f-be9d-58f11bf3418b.sketch_text.stroke-140"),sQuery(id+"FQ5JFwxVdaqARUP_1.wireOp",EDGE,"fcba4419-a2ee-464f-be9d-58f11bf3418b.sketch_text.stroke-141"),sQuery(id+"FQ5JFwxVdaqARUP_1.wireOp",EDGE,"fcba4419-a2ee-464f-be9d-58f11bf3418b.sketch_text.stroke-142"),sQuery(id+"FQ5JFwxVdaqARUP_1.wireOp",EDGE,"fcba4419-a2ee-464f-be9d-58f11bf3418b.sketch_text.stroke-143"),sQuery(id+"FQ5JFwxVdaqARUP_1.wireOp",EDGE,"fcba4419-a2ee-464f-be9d-58f11bf3418b.sketch_text.stroke-144"),sQuery(id+"FQ5JFwxVdaqARUP_1.wireOp",EDGE,"fcba4419-a2ee-464f-be9d-58f11bf3418b.sketch_text.stroke-145"),sQuery(id+"FQ5JFwxVdaqARUP_1.wireOp",EDGE,"fcba4419-a2ee-464f-be9d-58f11bf3418b.sketch_text.stroke-146"),sQuery(id+"FQ5JFwxVdaqARUP_1.wireOp",EDGE,"fcba4419-a2ee-464f-be9d-58f11bf3418b.sketch_text.stroke-147"),sQuery(id+"FQ5JFwxVdaqARUP_1.wireOp",EDGE,"fcba4419-a2ee-464f-be9d-58f11bf3418b.sketch_text.stroke-148"),sQuery(id+"FQ5JFwxVdaqARUP_1.wireOp",EDGE,"fcba4419-a2ee-464f-be9d-58f11bf3418b.sketch_text.stroke-149"),sQuery(id+"FQ5JFwxVdaqARUP_1.wireOp",EDGE,"fcba4419-a2ee-464f-be9d-58f11bf3418b.sketch_text.stroke-150"),sQuery(id+"FQ5JFwxVdaqARUP_1.wireOp",EDGE,"fcba4419-a2ee-464f-be9d-58f11bf3418b.sketch_text.stroke-151"),sQuery(id+"FQ5JFwxVdaqARUP_1.wireOp",EDGE,"fcba4419-a2ee-464f-be9d-58f11bf3418b.sketch_text.stroke-152"),sQuery(id+"FQ5JFwxVdaqARUP_1.wireOp",EDGE,"fcba4419-a2ee-464f-be9d-58f11bf3418b.sketch_text.stroke-153"),sQuery(id+"FQ5JFwxVdaqARUP_1.wireOp",EDGE,"fcba4419-a2ee-464f-be9d-58f11bf3418b.sketch_text.stroke-154"),sQuery(id+"FQ5JFwxVdaqARUP_1.wireOp",EDGE,"fcba4419-a2ee-464f-be9d-58f11bf3418b.sketch_text.stroke-155"),sQuery(id+"FQ5JFwxVdaqARUP_1.wireOp",EDGE,"fcba4419-a2ee-464f-be9d-58f11bf3418b.sketch_text.stroke-156"),sQuery(id+"FQ5JFwxVdaqARUP_1.wireOp",EDGE,"fcba4419-a2ee-464f-be9d-58f11bf3418b.sketch_text.stroke-157"),sQuery(id+"FQ5JFwxVdaqARUP_1.wireOp",EDGE,"fcba4419-a2ee-464f-be9d-58f11bf3418b.sketch_text.stroke-158"),sQuery(id+"FQ5JFwxVdaqARUP_1.wireOp",EDGE,"fcba4419-a2ee-464f-be9d-58f11bf3418b.sketch_text.stroke-159"),sQuery(id+"FQ5JFwxVdaqARUP_1.wireOp",EDGE,"fcba4419-a2ee-464f-be9d-58f11bf3418b.sketch_text.stroke-160"),sQuery(id+"FQ5JFwxVdaqARUP_1.wireOp",EDGE,"fcba4419-a2ee-464f-be9d-58f11bf3418b.sketch_text.stroke-161"),sQuery(id+"FQ5JFwxVdaqARUP_1.wireOp",EDGE,"fcba4419-a2ee-464f-be9d-58f11bf3418b.sketch_text.stroke-162"),sQuery(id+"FQ5JFwxVdaqARUP_1.wireOp",EDGE,"fcba4419-a2ee-464f-be9d-58f11bf3418b.sketch_text.stroke-163"),sQuery(id+"FQ5JFwxVdaqARUP_1.wireOp",EDGE,"fcba4419-a2ee-464f-be9d-58f11bf3418b.sketch_text.stroke-164"),sQuery(id+"FQ5JFwxVdaqARUP_1.wireOp",EDGE,"fcba4419-a2ee-464f-be9d-58f11bf3418b.sketch_text.stroke-165"),sQuery(id+"FQ5JFwxVdaqARUP_1.wireOp",EDGE,"fcba4419-a2ee-464f-be9d-58f11bf3418b.sketch_text.stroke-166"),sQuery(id+"FQ5JFwxVdaqARUP_1.wireOp",EDGE,"fcba4419-a2ee-464f-be9d-58f11bf3418b.sketch_text.stroke-167"),sQuery(id+"FQ5JFwxVdaqARUP_1.wireOp",EDGE,"fcba4419-a2ee-464f-be9d-58f11bf3418b.sketch_text.stroke-168"),sQuery(id+"FQ5JFwxVdaqARUP_1.wireOp",EDGE,"fcba4419-a2ee-464f-be9d-58f11bf3418b.sketch_text.stroke-169"),sQuery(id+"FQ5JFwxVdaqARUP_1.wireOp",EDGE,"fcba4419-a2ee-464f-be9d-58f11bf3418b.sketch_text.stroke-170"),sQuery(id+"FQ5JFwxVdaqARUP_1.wireOp",EDGE,"fcba4419-a2ee-464f-be9d-58f11bf3418b.sketch_text.stroke-171"),sQuery(id+"FQ5JFwxVdaqARUP_1.wireOp",EDGE,"fcba4419-a2ee-464f-be9d-58f11bf3418b.sketch_text.stroke-172"),sQuery(id+"FQ5JFwxVdaqARUP_1.wireOp",EDGE,"fcba4419-a2ee-464f-be9d-58f11bf3418b.sketch_text.stroke-173"),sQuery(id+"FHMxAyK4CFUKdhS_1.wireOp",EDGE,"1cb9c079-ea9b-4899-8069-e0e3048e911d.sketch_text.stroke-0"),sQuery(id+"FHMxAyK4CFUKdhS_1.wireOp",EDGE,"1cb9c079-ea9b-4899-8069-e0e3048e911d.sketch_text.stroke-1"),sQuery(id+"FHMxAyK4CFUKdhS_1.wireOp",EDGE,"1cb9c079-ea9b-4899-8069-e0e3048e911d.sketch_text.stroke-2"),sQuery(id+"FHMxAyK4CFUKdhS_1.wireOp",EDGE,"1cb9c079-ea9b-4899-8069-e0e3048e911d.sketch_text.stroke-3"),sQuery(id+"FHMxAyK4CFUKdhS_1.wireOp",EDGE,"1cb9c079-ea9b-4899-8069-e0e3048e911d.sketch_text.stroke-4"),sQuery(id+"FHMxAyK4CFUKdhS_1.wireOp",EDGE,"1cb9c079-ea9b-4899-8069-e0e3048e911d.sketch_text.stroke-5"),sQuery(id+"FHMxAyK4CFUKdhS_1.wireOp",EDGE,"1cb9c079-ea9b-4899-8069-e0e3048e911d.sketch_text.stroke-6"),sQuery(id+"FHMxAyK4CFUKdhS_1.wireOp",EDGE,"1cb9c079-ea9b-4899-8069-e0e3048e911d.sketch_text.stroke-7"),sQuery(id+"FHMxAyK4CFUKdhS_1.wireOp",EDGE,"1cb9c079-ea9b-4899-8069-e0e3048e911d.sketch_text.stroke-8"),sQuery(id+"FHMxAyK4CFUKdhS_1.wireOp",EDGE,"1cb9c079-ea9b-4899-8069-e0e3048e911d.sketch_text.stroke-9"),sQuery(id+"FHMxAyK4CFUKdhS_1.wireOp",EDGE,"1cb9c079-ea9b-4899-8069-e0e3048e911d.sketch_text.stroke-10"),sQuery(id+"FHMxAyK4CFUKdhS_1.wireOp",EDGE,"1cb9c079-ea9b-4899-8069-e0e3048e911d.sketch_text.stroke-11"),sQuery(id+"FHMxAyK4CFUKdhS_1.wireOp",EDGE,"1cb9c079-ea9b-4899-8069-e0e3048e911d.sketch_text.stroke-12"),sQuery(id+"FHMxAyK4CFUKdhS_1.wireOp",EDGE,"1cb9c079-ea9b-4899-8069-e0e3048e911d.sketch_text.stroke-13"),sQuery(id+"FHMxAyK4CFUKdhS_1.wireOp",EDGE,"1cb9c079-ea9b-4899-8069-e0e3048e911d.sketch_text.stroke-14"),sQuery(id+"FHMxAyK4CFUKdhS_1.wireOp",EDGE,"1cb9c079-ea9b-4899-8069-e0e3048e911d.sketch_text.stroke-15"),sQuery(id+"FHMxAyK4CFUKdhS_1.wireOp",EDGE,"1cb9c079-ea9b-4899-8069-e0e3048e911d.sketch_text.stroke-16"),sQuery(id+"FHMxAyK4CFUKdhS_1.wireOp",EDGE,"1cb9c079-ea9b-4899-8069-e0e3048e911d.sketch_text.stroke-17"),sQuery(id+"FHMxAyK4CFUKdhS_1.wireOp",EDGE,"1cb9c079-ea9b-4899-8069-e0e3048e911d.sketch_text.stroke-18"),sQuery(id+"FHMxAyK4CFUKdhS_1.wireOp",EDGE,"1cb9c079-ea9b-4899-8069-e0e3048e911d.sketch_text.stroke-19"),sQuery(id+"FHMxAyK4CFUKdhS_1.wireOp",EDGE,"1cb9c079-ea9b-4899-8069-e0e3048e911d.sketch_text.stroke-20"),sQuery(id+"FHMxAyK4CFUKdhS_1.wireOp",EDGE,"1cb9c079-ea9b-4899-8069-e0e3048e911d.sketch_text.stroke-21"),sQuery(id+"FHMxAyK4CFUKdhS_1.wireOp",EDGE,"1cb9c079-ea9b-4899-8069-e0e3048e911d.sketch_text.stroke-22"),sQuery(id+"FHMxAyK4CFUKdhS_1.wireOp",EDGE,"1cb9c079-ea9b-4899-8069-e0e3048e911d.sketch_text.stroke-23"),sQuery(id+"FHMxAyK4CFUKdhS_1.wireOp",EDGE,"1cb9c079-ea9b-4899-8069-e0e3048e911d.sketch_text.stroke-24"),sQuery(id+"FHMxAyK4CFUKdhS_1.wireOp",EDGE,"1cb9c079-ea9b-4899-8069-e0e3048e911d.sketch_text.stroke-25"),sQuery(id+"FHMxAyK4CFUKdhS_1.wireOp",EDGE,"1cb9c079-ea9b-4899-8069-e0e3048e911d.sketch_text.stroke-26"),sQuery(id+"FHMxAyK4CFUKdhS_1.wireOp",EDGE,"1cb9c079-ea9b-4899-8069-e0e3048e911d.sketch_text.stroke-27"),sQuery(id+"FHMxAyK4CFUKdhS_1.wireOp",EDGE,"1cb9c079-ea9b-4899-8069-e0e3048e911d.sketch_text.stroke-28"),sQuery(id+"FHMxAyK4CFUKdhS_1.wireOp",EDGE,"1cb9c079-ea9b-4899-8069-e0e3048e911d.sketch_text.stroke-29"),sQuery(id+"FHMxAyK4CFUKdhS_1.wireOp",EDGE,"1cb9c079-ea9b-4899-8069-e0e3048e911d.sketch_text.stroke-30"),sQuery(id+"FHMxAyK4CFUKdhS_1.wireOp",EDGE,"1cb9c079-ea9b-4899-8069-e0e3048e911d.sketch_text.stroke-31"),sQuery(id+"FHMxAyK4CFUKdhS_1.wireOp",EDGE,"1cb9c079-ea9b-4899-8069-e0e3048e911d.sketch_text.stroke-32"),sQuery(id+"FHMxAyK4CFUKdhS_1.wireOp",EDGE,"1cb9c079-ea9b-4899-8069-e0e3048e911d.sketch_text.stroke-33"),sQuery(id+"FHMxAyK4CFUKdhS_1.wireOp",EDGE,"1cb9c079-ea9b-4899-8069-e0e3048e911d.sketch_text.stroke-34"),sQuery(id+"FHMxAyK4CFUKdhS_1.wireOp",EDGE,"1cb9c079-ea9b-4899-8069-e0e3048e911d.sketch_text.stroke-35"),sQuery(id+"FHMxAyK4CFUKdhS_1.wireOp",EDGE,"1cb9c079-ea9b-4899-8069-e0e3048e911d.sketch_text.stroke-36"),sQuery(id+"FHMxAyK4CFUKdhS_1.wireOp",EDGE,"1cb9c079-ea9b-4899-8069-e0e3048e911d.sketch_text.stroke-37"),sQuery(id+"FHMxAyK4CFUKdhS_1.wireOp",EDGE,"1cb9c079-ea9b-4899-8069-e0e3048e911d.sketch_text.stroke-38"),sQuery(id+"FHMxAyK4CFUKdhS_1.wireOp",EDGE,"1cb9c079-ea9b-4899-8069-e0e3048e911d.sketch_text.stroke-39"),sQuery(id+"FHMxAyK4CFUKdhS_1.wireOp",EDGE,"1cb9c079-ea9b-4899-8069-e0e3048e911d.sketch_text.stroke-40"),sQuery(id+"FHMxAyK4CFUKdhS_1.wireOp",EDGE,"1cb9c079-ea9b-4899-8069-e0e3048e911d.sketch_text.stroke-41"),sQuery(id+"FHMxAyK4CFUKdhS_1.wireOp",EDGE,"1cb9c079-ea9b-4899-8069-e0e3048e911d.sketch_text.stroke-42"),sQuery(id+"FHMxAyK4CFUKdhS_1.wireOp",EDGE,"1cb9c079-ea9b-4899-8069-e0e3048e911d.sketch_text.stroke-43"),sQuery(id+"FHMxAyK4CFUKdhS_1.wireOp",EDGE,"1cb9c079-ea9b-4899-8069-e0e3048e911d.sketch_text.stroke-44"),sQuery(id+"FHMxAyK4CFUKdhS_1.wireOp",EDGE,"1cb9c079-ea9b-4899-8069-e0e3048e911d.sketch_text.stroke-45"),sQuery(id+"FHMxAyK4CFUKdhS_1.wireOp",EDGE,"1cb9c079-ea9b-4899-8069-e0e3048e911d.sketch_text.stroke-46"),sQuery(id+"FHMxAyK4CFUKdhS_1.wireOp",EDGE,"1cb9c079-ea9b-4899-8069-e0e3048e911d.sketch_text.stroke-47"),sQuery(id+"FHMxAyK4CFUKdhS_1.wireOp",EDGE,"1cb9c079-ea9b-4899-8069-e0e3048e911d.sketch_text.stroke-48"),sQuery(id+"FHMxAyK4CFUKdhS_1.wireOp",EDGE,"1cb9c079-ea9b-4899-8069-e0e3048e911d.sketch_text.stroke-49"),sQuery(id+"FHMxAyK4CFUKdhS_1.wireOp",EDGE,"1cb9c079-ea9b-4899-8069-e0e3048e911d.sketch_text.stroke-50"),sQuery(id+"FHMxAyK4CFUKdhS_1.wireOp",EDGE,"1cb9c079-ea9b-4899-8069-e0e3048e911d.sketch_text.stroke-51"),sQuery(id+"FHMxAyK4CFUKdhS_1.wireOp",EDGE,"1cb9c079-ea9b-4899-8069-e0e3048e911d.sketch_text.stroke-52"),sQuery(id+"FHMxAyK4CFUKdhS_1.wireOp",EDGE,"1cb9c079-ea9b-4899-8069-e0e3048e911d.sketch_text.stroke-53"),sQuery(id+"FHMxAyK4CFUKdhS_1.wireOp",EDGE,"1cb9c079-ea9b-4899-8069-e0e3048e911d.sketch_text.stroke-54"),sQuery(id+"FHMxAyK4CFUKdhS_1.wireOp",EDGE,"1cb9c079-ea9b-4899-8069-e0e3048e911d.sketch_text.stroke-55"),sQuery(id+"FHMxAyK4CFUKdhS_1.wireOp",EDGE,"1cb9c079-ea9b-4899-8069-e0e3048e911d.sketch_text.stroke-56"),sQuery(id+"FHMxAyK4CFUKdhS_1.wireOp",EDGE,"1cb9c079-ea9b-4899-8069-e0e3048e911d.sketch_text.stroke-57"),sQuery(id+"FHMxAyK4CFUKdhS_1.wireOp",EDGE,"1cb9c079-ea9b-4899-8069-e0e3048e911d.sketch_text.stroke-58"),sQuery(id+"FHMxAyK4CFUKdhS_1.wireOp",EDGE,"1cb9c079-ea9b-4899-8069-e0e3048e911d.sketch_text.stroke-59"),sQuery(id+"FHMxAyK4CFUKdhS_1.wireOp",EDGE,"1cb9c079-ea9b-4899-8069-e0e3048e911d.sketch_text.stroke-60"),sQuery(id+"FHMxAyK4CFUKdhS_1.wireOp",EDGE,"1cb9c079-ea9b-4899-8069-e0e3048e911d.sketch_text.stroke-61"),sQuery(id+"FHMxAyK4CFUKdhS_1.wireOp",EDGE,"1cb9c079-ea9b-4899-8069-e0e3048e911d.sketch_text.stroke-62"),sQuery(id+"FHMxAyK4CFUKdhS_1.wireOp",EDGE,"1cb9c079-ea9b-4899-8069-e0e3048e911d.sketch_text.stroke-71"),sQuery(id+"FHMxAyK4CFUKdhS_1.wireOp",EDGE,"1cb9c079-ea9b-4899-8069-e0e3048e911d.sketch_text.stroke-72"),sQuery(id+"FHMxAyK4CFUKdhS_1.wireOp",EDGE,"1cb9c079-ea9b-4899-8069-e0e3048e911d.sketch_text.stroke-73"),sQuery(id+"FHMxAyK4CFUKdhS_1.wireOp",EDGE,"1cb9c079-ea9b-4899-8069-e0e3048e911d.sketch_text.stroke-74"),sQuery(id+"FHMxAyK4CFUKdhS_1.wireOp",EDGE,"1cb9c079-ea9b-4899-8069-e0e3048e911d.sketch_text.stroke-75"),sQuery(id+"FHMxAyK4CFUKdhS_1.wireOp",EDGE,"1cb9c079-ea9b-4899-8069-e0e3048e911d.sketch_text.stroke-76"),sQuery(id+"FHMxAyK4CFUKdhS_1.wireOp",EDGE,"1cb9c079-ea9b-4899-8069-e0e3048e911d.sketch_text.stroke-77"),sQuery(id+"FHMxAyK4CFUKdhS_1.wireOp",EDGE,"1cb9c079-ea9b-4899-8069-e0e3048e911d.sketch_text.stroke-78"),sQuery(id+"FHMxAyK4CFUKdhS_1.wireOp",EDGE,"1cb9c079-ea9b-4899-8069-e0e3048e911d.sketch_text.stroke-79"),sQuery(id+"FHMxAyK4CFUKdhS_1.wireOp",EDGE,"1cb9c079-ea9b-4899-8069-e0e3048e911d.sketch_text.stroke-80"),sQuery(id+"FHMxAyK4CFUKdhS_1.wireOp",EDGE,"1cb9c079-ea9b-4899-8069-e0e3048e911d.sketch_text.stroke-81"),sQuery(id+"FHMxAyK4CFUKdhS_1.wireOp",EDGE,"1cb9c079-ea9b-4899-8069-e0e3048e911d.sketch_text.stroke-82"),sQuery(id+"FHMxAyK4CFUKdhS_1.wireOp",EDGE,"1cb9c079-ea9b-4899-8069-e0e3048e911d.sketch_text.stroke-83"),sQuery(id+"FHMxAyK4CFUKdhS_1.wireOp",EDGE,"1cb9c079-ea9b-4899-8069-e0e3048e911d.sketch_text.stroke-84"),sQuery(id+"FHMxAyK4CFUKdhS_1.wireOp",EDGE,"1cb9c079-ea9b-4899-8069-e0e3048e911d.sketch_text.stroke-85"),sQuery(id+"FHMxAyK4CFUKdhS_1.wireOp",EDGE,"1cb9c079-ea9b-4899-8069-e0e3048e911d.sketch_text.stroke-86"),sQuery(id+"FHMxAyK4CFUKdhS_1.wireOp",EDGE,"1cb9c079-ea9b-4899-8069-e0e3048e911d.sketch_text.stroke-87"),sQuery(id+"FHMxAyK4CFUKdhS_1.wireOp",EDGE,"1cb9c079-ea9b-4899-8069-e0e3048e911d.sketch_text.stroke-88"),sQuery(id+"FHMxAyK4CFUKdhS_1.wireOp",EDGE,"1cb9c079-ea9b-4899-8069-e0e3048e911d.sketch_text.stroke-89"),sQuery(id+"FHMxAyK4CFUKdhS_1.wireOp",EDGE,"1cb9c079-ea9b-4899-8069-e0e3048e911d.sketch_text.stroke-90"),sQuery(id+"FHMxAyK4CFUKdhS_1.wireOp",EDGE,"1cb9c079-ea9b-4899-8069-e0e3048e911d.sketch_text.stroke-91"),sQuery(id+"FHMxAyK4CFUKdhS_1.wireOp",EDGE,"1cb9c079-ea9b-4899-8069-e0e3048e911d.sketch_text.stroke-92"),sQuery(id+"FHMxAyK4CFUKdhS_1.wireOp",EDGE,"1cb9c079-ea9b-4899-8069-e0e3048e911d.sketch_text.stroke-93"),sQuery(id+"FHMxAyK4CFUKdhS_1.wireOp",EDGE,"1cb9c079-ea9b-4899-8069-e0e3048e911d.sketch_text.stroke-94"),sQuery(id+"FHMxAyK4CFUKdhS_1.wireOp",EDGE,"1cb9c079-ea9b-4899-8069-e0e3048e911d.sketch_text.stroke-95"),sQuery(id+"FHMxAyK4CFUKdhS_1.wireOp",EDGE,"1cb9c079-ea9b-4899-8069-e0e3048e911d.sketch_text.stroke-96"),sQuery(id+"FHMxAyK4CFUKdhS_1.wireOp",EDGE,"1cb9c079-ea9b-4899-8069-e0e3048e911d.sketch_text.stroke-97"),sQuery(id+"FHMxAyK4CFUKdhS_1.wireOp",EDGE,"1cb9c079-ea9b-4899-8069-e0e3048e911d.sketch_text.stroke-103"),sQuery(id+"FHMxAyK4CFUKdhS_1.wireOp",EDGE,"1cb9c079-ea9b-4899-8069-e0e3048e911d.sketch_text.stroke-104"),sQuery(id+"FHMxAyK4CFUKdhS_1.wireOp",EDGE,"1cb9c079-ea9b-4899-8069-e0e3048e911d.sketch_text.stroke-105"),sQuery(id+"FHMxAyK4CFUKdhS_1.wireOp",EDGE,"1cb9c079-ea9b-4899-8069-e0e3048e911d.sketch_text.stroke-106"),sQuery(id+"FHMxAyK4CFUKdhS_1.wireOp",EDGE,"1cb9c079-ea9b-4899-8069-e0e3048e911d.sketch_text.stroke-107"),sQuery(id+"FHMxAyK4CFUKdhS_1.wireOp",EDGE,"1cb9c079-ea9b-4899-8069-e0e3048e911d.sketch_text.stroke-108"),sQuery(id+"FHMxAyK4CFUKdhS_1.wireOp",EDGE,"1cb9c079-ea9b-4899-8069-e0e3048e911d.sketch_text.stroke-109"),sQuery(id+"FHMxAyK4CFUKdhS_1.wireOp",EDGE,"1cb9c079-ea9b-4899-8069-e0e3048e911d.sketch_text.stroke-110"),sQuery(id+"FHMxAyK4CFUKdhS_1.wireOp",EDGE,"1cb9c079-ea9b-4899-8069-e0e3048e911d.sketch_text.stroke-111"),sQuery(id+"FHMxAyK4CFUKdhS_1.wireOp",EDGE,"1cb9c079-ea9b-4899-8069-e0e3048e911d.sketch_text.stroke-112"),sQuery(id+"FHMxAyK4CFUKdhS_1.wireOp",EDGE,"1cb9c079-ea9b-4899-8069-e0e3048e911d.sketch_text.stroke-113"),sQuery(id+"FHMxAyK4CFUKdhS_1.wireOp",EDGE,"1cb9c079-ea9b-4899-8069-e0e3048e911d.sketch_text.stroke-114"),sQuery(id+"FHMxAyK4CFUKdhS_1.wireOp",EDGE,"1cb9c079-ea9b-4899-8069-e0e3048e911d.sketch_text.stroke-115"),sQuery(id+"FHMxAyK4CFUKdhS_1.wireOp",EDGE,"1cb9c079-ea9b-4899-8069-e0e3048e911d.sketch_text.stroke-116"),sQuery(id+"FHMxAyK4CFUKdhS_1.wireOp",EDGE,"1cb9c079-ea9b-4899-8069-e0e3048e911d.sketch_text.stroke-117"),sQuery(id+"FHMxAyK4CFUKdhS_1.wireOp",EDGE,"1cb9c079-ea9b-4899-8069-e0e3048e911d.sketch_text.stroke-118"),sQuery(id+"FHMxAyK4CFUKdhS_1.wireOp",EDGE,"1cb9c079-ea9b-4899-8069-e0e3048e911d.sketch_text.stroke-119"),sQuery(id+"FHMxAyK4CFUKdhS_1.wireOp",EDGE,"1cb9c079-ea9b-4899-8069-e0e3048e911d.sketch_text.stroke-120"),sQuery(id+"FHMxAyK4CFUKdhS_1.wireOp",EDGE,"1cb9c079-ea9b-4899-8069-e0e3048e911d.sketch_text.stroke-121"),sQuery(id+"FHMxAyK4CFUKdhS_1.wireOp",EDGE,"1cb9c079-ea9b-4899-8069-e0e3048e911d.sketch_text.stroke-122"),sQuery(id+"FHMxAyK4CFUKdhS_1.wireOp",EDGE,"1cb9c079-ea9b-4899-8069-e0e3048e911d.sketch_text.stroke-123"),sQuery(id+"FHMxAyK4CFUKdhS_1.wireOp",EDGE,"1cb9c079-ea9b-4899-8069-e0e3048e911d.sketch_text.stroke-124"),sQuery(id+"FHMxAyK4CFUKdhS_1.wireOp",EDGE,"1cb9c079-ea9b-4899-8069-e0e3048e911d.sketch_text.stroke-125"),sQuery(id+"FHMxAyK4CFUKdhS_1.wireOp",EDGE,"1cb9c079-ea9b-4899-8069-e0e3048e911d.sketch_text.stroke-126"),sQuery(id+"FHMxAyK4CFUKdhS_1.wireOp",EDGE,"1cb9c079-ea9b-4899-8069-e0e3048e911d.sketch_text.stroke-127"),sQuery(id+"FHMxAyK4CFUKdhS_1.wireOp",EDGE,"1cb9c079-ea9b-4899-8069-e0e3048e911d.sketch_text.stroke-128"),sQuery(id+"FHMxAyK4CFUKdhS_1.wireOp",EDGE,"1cb9c079-ea9b-4899-8069-e0e3048e911d.sketch_text.stroke-129"),sQuery(id+"FHMxAyK4CFUKdhS_1.wireOp",EDGE,"1cb9c079-ea9b-4899-8069-e0e3048e911d.sketch_text.stroke-130"),sQuery(id+"FHMxAyK4CFUKdhS_1.wireOp",EDGE,"1cb9c079-ea9b-4899-8069-e0e3048e911d.sketch_text.stroke-131"),sQuery(id+"FHMxAyK4CFUKdhS_1.wireOp",EDGE,"1cb9c079-ea9b-4899-8069-e0e3048e911d.sketch_text.stroke-132"),sQuery(id+"FHMxAyK4CFUKdhS_1.wireOp",EDGE,"1cb9c079-ea9b-4899-8069-e0e3048e911d.sketch_text.stroke-133"),sQuery(id+"FHMxAyK4CFUKdhS_1.wireOp",EDGE,"1cb9c079-ea9b-4899-8069-e0e3048e911d.sketch_text.stroke-134"),sQuery(id+"FHMxAyK4CFUKdhS_1.wireOp",EDGE,"1cb9c079-ea9b-4899-8069-e0e3048e911d.sketch_text.stroke-135"),sQuery(id+"FHMxAyK4CFUKdhS_1.wireOp",EDGE,"1cb9c079-ea9b-4899-8069-e0e3048e911d.sketch_text.stroke-136"),sQuery(id+"FHMxAyK4CFUKdhS_1.wireOp",EDGE,"1cb9c079-ea9b-4899-8069-e0e3048e911d.sketch_text.stroke-137"),sQuery(id+"FHMxAyK4CFUKdhS_1.wireOp",EDGE,"1cb9c079-ea9b-4899-8069-e0e3048e911d.sketch_text.stroke-138"),sQuery(id+"FHMxAyK4CFUKdhS_1.wireOp",EDGE,"1cb9c079-ea9b-4899-8069-e0e3048e911d.sketch_text.stroke-139"),sQuery(id+"FHMxAyK4CFUKdhS_1.wireOp",EDGE,"1cb9c079-ea9b-4899-8069-e0e3048e911d.sketch_text.stroke-140"),sQuery(id+"FHMxAyK4CFUKdhS_1.wireOp",EDGE,"1cb9c079-ea9b-4899-8069-e0e3048e911d.sketch_text.stroke-141"),sQuery(id+"FHMxAyK4CFUKdhS_1.wireOp",EDGE,"1cb9c079-ea9b-4899-8069-e0e3048e911d.sketch_text.stroke-142"),sQuery(id+"FHMxAyK4CFUKdhS_1.wireOp",EDGE,"1cb9c079-ea9b-4899-8069-e0e3048e911d.sketch_text.stroke-143"),sQuery(id+"FHMxAyK4CFUKdhS_1.wireOp",EDGE,"1cb9c079-ea9b-4899-8069-e0e3048e911d.sketch_text.stroke-144"),sQuery(id+"FHMxAyK4CFUKdhS_1.wireOp",EDGE,"1cb9c079-ea9b-4899-8069-e0e3048e911d.sketch_text.stroke-145"),sQuery(id+"FHMxAyK4CFUKdhS_1.wireOp",EDGE,"1cb9c079-ea9b-4899-8069-e0e3048e911d.sketch_text.stroke-146"),sQuery(id+"FHMxAyK4CFUKdhS_1.wireOp",EDGE,"1cb9c079-ea9b-4899-8069-e0e3048e911d.sketch_text.stroke-147"),sQuery(id+"FHMxAyK4CFUKdhS_1.wireOp",EDGE,"1cb9c079-ea9b-4899-8069-e0e3048e911d.sketch_text.stroke-148"),sQuery(id+"FHMxAyK4CFUKdhS_1.wireOp",EDGE,"1cb9c079-ea9b-4899-8069-e0e3048e911d.sketch_text.stroke-149"),sQuery(id+"FHMxAyK4CFUKdhS_1.wireOp",EDGE,"1cb9c079-ea9b-4899-8069-e0e3048e911d.sketch_text.stroke-150"),sQuery(id+"FHMxAyK4CFUKdhS_1.wireOp",EDGE,"1cb9c079-ea9b-4899-8069-e0e3048e911d.sketch_text.stroke-151"),sQuery(id+"FHMxAyK4CFUKdhS_1.wireOp",EDGE,"1cb9c079-ea9b-4899-8069-e0e3048e911d.sketch_text.stroke-152"),sQuery(id+"FHMxAyK4CFUKdhS_1.wireOp",EDGE,"1cb9c079-ea9b-4899-8069-e0e3048e911d.sketch_text.stroke-153"),sQuery(id+"FHMxAyK4CFUKdhS_1.wireOp",EDGE,"1cb9c079-ea9b-4899-8069-e0e3048e911d.sketch_text.stroke-159"),sQuery(id+"FHMxAyK4CFUKdhS_1.wireOp",EDGE,"1cb9c079-ea9b-4899-8069-e0e3048e911d.sketch_text.stroke-160"),sQuery(id+"FHMxAyK4CFUKdhS_1.wireOp",EDGE,"1cb9c079-ea9b-4899-8069-e0e3048e911d.sketch_text.stroke-161"),sQuery(id+"FHMxAyK4CFUKdhS_1.wireOp",EDGE,"1cb9c079-ea9b-4899-8069-e0e3048e911d.sketch_text.stroke-162"),sQuery(id+"FHMxAyK4CFUKdhS_1.wireOp",EDGE,"1cb9c079-ea9b-4899-8069-e0e3048e911d.sketch_text.stroke-163"),sQuery(id+"FHMxAyK4CFUKdhS_1.wireOp",EDGE,"1cb9c079-ea9b-4899-8069-e0e3048e911d.sketch_text.stroke-164"),sQuery(id+"FHMxAyK4CFUKdhS_1.wireOp",EDGE,"1cb9c079-ea9b-4899-8069-e0e3048e911d.sketch_text.stroke-165"),sQuery(id+"FHMxAyK4CFUKdhS_1.wireOp",EDGE,"1cb9c079-ea9b-4899-8069-e0e3048e911d.sketch_text.stroke-166"),sQuery(id+"FHMxAyK4CFUKdhS_1.wireOp",EDGE,"1cb9c079-ea9b-4899-8069-e0e3048e911d.sketch_text.stroke-167"),sQuery(id+"FHMxAyK4CFUKdhS_1.wireOp",EDGE,"1cb9c079-ea9b-4899-8069-e0e3048e911d.sketch_text.stroke-168"),sQuery(id+"FHMxAyK4CFUKdhS_1.wireOp",EDGE,"1cb9c079-ea9b-4899-8069-e0e3048e911d.sketch_text.stroke-169"),sQuery(id+"FHMxAyK4CFUKdhS_1.wireOp",EDGE,"1cb9c079-ea9b-4899-8069-e0e3048e911d.sketch_text.stroke-170"),sQuery(id+"FHMxAyK4CFUKdhS_1.wireOp",EDGE,"1cb9c079-ea9b-4899-8069-e0e3048e911d.sketch_text.stroke-171"),sQuery(id+"FHMxAyK4CFUKdhS_1.wireOp",EDGE,"1cb9c079-ea9b-4899-8069-e0e3048e911d.sketch_text.stroke-172"),sQuery(id+"FHMxAyK4CFUKdhS_1.wireOp",EDGE,"1cb9c079-ea9b-4899-8069-e0e3048e911d.sketch_text.stroke-173"),sQuery(id+"FHMxAyK4CFUKdhS_1.wireOp",EDGE,"1cb9c079-ea9b-4899-8069-e0e3048e911d.sketch_text.stroke-174"),sQuery(id+"FHMxAyK4CFUKdhS_1.wireOp",EDGE,"1cb9c079-ea9b-4899-8069-e0e3048e911d.sketch_text.stroke-175"),sQuery(id+"FHMxAyK4CFUKdhS_1.wireOp",EDGE,"1cb9c079-ea9b-4899-8069-e0e3048e911d.sketch_text.stroke-176"),sQuery(id+"FHMxAyK4CFUKdhS_1.wireOp",EDGE,"1cb9c079-ea9b-4899-8069-e0e3048e911d.sketch_text.stroke-177"),sQuery(id+"FHMxAyK4CFUKdhS_1.wireOp",EDGE,"1cb9c079-ea9b-4899-8069-e0e3048e911d.sketch_text.stroke-178"),sQuery(id+"FHMxAyK4CFUKdhS_1.wireOp",EDGE,"1cb9c079-ea9b-4899-8069-e0e3048e911d.sketch_text.stroke-179"),sQuery(id+"FHMxAyK4CFUKdhS_1.wireOp",EDGE,"1cb9c079-ea9b-4899-8069-e0e3048e911d.sketch_text.stroke-180"),sQuery(id+"F2.wireOp",EDGE,"8007402e-1a4e-4a06-85a5-2af08e553504"),subQ2])],"isStart":true}),makeQuery(id+"F3.opExtrude","SWEPT_FACE",FACE,{"disambiguationData":[OSD([subQ2])]})]),OD(1.0)],"derivedFrom":makeQuery(id+"F1.opExtrude","CAP_EDGE",EDGE,{"disambiguationData":[OSD([subQ0])],"isStart":false})});}
            var Q13;
            {var subQ0=sQuery(id+"F0.wireOp",EDGE,"E0.top");var subQ1=sQuery(id+"F0.wireOp",EDGE,"E0.bottom");var subQ2=sQuery(id+"F2.wireOp",EDGE,"727ac2c1-f511-4829-95a7-a443ef16a4cd");Q13=makeQuery(id+"F3.boolean.opBoolean","SPLIT",EDGE,{"disambiguationData":[TD([makeQuery(id+"F1.opExtrude","CAP_FACE",FACE,{"disambiguationData":[OSD([subQ1,subQ0,sQuery(id+"F0.wireOp",EDGE,"E0.left"),sQuery(id+"F0.wireOp",EDGE,"E0.right")])],"isStart":false}),makeQuery(id+"F1.opExtrude","SWEPT_FACE",FACE,{"disambiguationData":[OSD([subQ0])]}),makeQuery(id+"F3.opExtrude","CAP_FACE",FACE,{"disambiguationData":[OSD([subQ1,sQuery(id+"FQ5JFwxVdaqARUP_1.wireOp",EDGE,"fcba4419-a2ee-464f-be9d-58f11bf3418b.sketch_text.stroke-0"),sQuery(id+"FQ5JFwxVdaqARUP_1.wireOp",EDGE,"fcba4419-a2ee-464f-be9d-58f11bf3418b.sketch_text.stroke-1"),sQuery(id+"FQ5JFwxVdaqARUP_1.wireOp",EDGE,"fcba4419-a2ee-464f-be9d-58f11bf3418b.sketch_text.stroke-2"),sQuery(id+"FQ5JFwxVdaqARUP_1.wireOp",EDGE,"fcba4419-a2ee-464f-be9d-58f11bf3418b.sketch_text.stroke-3"),sQuery(id+"FQ5JFwxVdaqARUP_1.wireOp",EDGE,"fcba4419-a2ee-464f-be9d-58f11bf3418b.sketch_text.stroke-4"),sQuery(id+"FQ5JFwxVdaqARUP_1.wireOp",EDGE,"fcba4419-a2ee-464f-be9d-58f11bf3418b.sketch_text.stroke-5"),sQuery(id+"FQ5JFwxVdaqARUP_1.wireOp",EDGE,"fcba4419-a2ee-464f-be9d-58f11bf3418b.sketch_text.stroke-6"),sQuery(id+"FQ5JFwxVdaqARUP_1.wireOp",EDGE,"fcba4419-a2ee-464f-be9d-58f11bf3418b.sketch_text.stroke-7"),sQuery(id+"FQ5JFwxVdaqARUP_1.wireOp",EDGE,"fcba4419-a2ee-464f-be9d-58f11bf3418b.sketch_text.stroke-8"),sQuery(id+"FQ5JFwxVdaqARUP_1.wireOp",EDGE,"fcba4419-a2ee-464f-be9d-58f11bf3418b.sketch_text.stroke-9"),sQuery(id+"FQ5JFwxVdaqARUP_1.wireOp",EDGE,"fcba4419-a2ee-464f-be9d-58f11bf3418b.sketch_text.stroke-10"),sQuery(id+"FQ5JFwxVdaqARUP_1.wireOp",EDGE,"fcba4419-a2ee-464f-be9d-58f11bf3418b.sketch_text.stroke-11"),sQuery(id+"FQ5JFwxVdaqARUP_1.wireOp",EDGE,"fcba4419-a2ee-464f-be9d-58f11bf3418b.sketch_text.stroke-12"),sQuery(id+"FQ5JFwxVdaqARUP_1.wireOp",EDGE,"fcba4419-a2ee-464f-be9d-58f11bf3418b.sketch_text.stroke-13"),sQuery(id+"FQ5JFwxVdaqARUP_1.wireOp",EDGE,"fcba4419-a2ee-464f-be9d-58f11bf3418b.sketch_text.stroke-14"),sQuery(id+"FQ5JFwxVdaqARUP_1.wireOp",EDGE,"fcba4419-a2ee-464f-be9d-58f11bf3418b.sketch_text.stroke-15"),sQuery(id+"FQ5JFwxVdaqARUP_1.wireOp",EDGE,"fcba4419-a2ee-464f-be9d-58f11bf3418b.sketch_text.stroke-16"),sQuery(id+"FQ5JFwxVdaqARUP_1.wireOp",EDGE,"fcba4419-a2ee-464f-be9d-58f11bf3418b.sketch_text.stroke-17"),sQuery(id+"FQ5JFwxVdaqARUP_1.wireOp",EDGE,"fcba4419-a2ee-464f-be9d-58f11bf3418b.sketch_text.stroke-18"),sQuery(id+"FQ5JFwxVdaqARUP_1.wireOp",EDGE,"fcba4419-a2ee-464f-be9d-58f11bf3418b.sketch_text.stroke-19"),sQuery(id+"FQ5JFwxVdaqARUP_1.wireOp",EDGE,"fcba4419-a2ee-464f-be9d-58f11bf3418b.sketch_text.stroke-20"),sQuery(id+"FQ5JFwxVdaqARUP_1.wireOp",EDGE,"fcba4419-a2ee-464f-be9d-58f11bf3418b.sketch_text.stroke-21"),sQuery(id+"FQ5JFwxVdaqARUP_1.wireOp",EDGE,"fcba4419-a2ee-464f-be9d-58f11bf3418b.sketch_text.stroke-22"),sQuery(id+"FQ5JFwxVdaqARUP_1.wireOp",EDGE,"fcba4419-a2ee-464f-be9d-58f11bf3418b.sketch_text.stroke-23"),sQuery(id+"FQ5JFwxVdaqARUP_1.wireOp",EDGE,"fcba4419-a2ee-464f-be9d-58f11bf3418b.sketch_text.stroke-24"),sQuery(id+"FQ5JFwxVdaqARUP_1.wireOp",EDGE,"fcba4419-a2ee-464f-be9d-58f11bf3418b.sketch_text.stroke-25"),sQuery(id+"FQ5JFwxVdaqARUP_1.wireOp",EDGE,"fcba4419-a2ee-464f-be9d-58f11bf3418b.sketch_text.stroke-26"),sQuery(id+"FQ5JFwxVdaqARUP_1.wireOp",EDGE,"fcba4419-a2ee-464f-be9d-58f11bf3418b.sketch_text.stroke-27"),sQuery(id+"FQ5JFwxVdaqARUP_1.wireOp",EDGE,"fcba4419-a2ee-464f-be9d-58f11bf3418b.sketch_text.stroke-28"),sQuery(id+"FQ5JFwxVdaqARUP_1.wireOp",EDGE,"fcba4419-a2ee-464f-be9d-58f11bf3418b.sketch_text.stroke-29"),sQuery(id+"FQ5JFwxVdaqARUP_1.wireOp",EDGE,"fcba4419-a2ee-464f-be9d-58f11bf3418b.sketch_text.stroke-30"),sQuery(id+"FQ5JFwxVdaqARUP_1.wireOp",EDGE,"fcba4419-a2ee-464f-be9d-58f11bf3418b.sketch_text.stroke-31"),sQuery(id+"FQ5JFwxVdaqARUP_1.wireOp",EDGE,"fcba4419-a2ee-464f-be9d-58f11bf3418b.sketch_text.stroke-32"),sQuery(id+"FQ5JFwxVdaqARUP_1.wireOp",EDGE,"fcba4419-a2ee-464f-be9d-58f11bf3418b.sketch_text.stroke-33"),sQuery(id+"FQ5JFwxVdaqARUP_1.wireOp",EDGE,"fcba4419-a2ee-464f-be9d-58f11bf3418b.sketch_text.stroke-34"),sQuery(id+"FQ5JFwxVdaqARUP_1.wireOp",EDGE,"fcba4419-a2ee-464f-be9d-58f11bf3418b.sketch_text.stroke-35"),sQuery(id+"FQ5JFwxVdaqARUP_1.wireOp",EDGE,"fcba4419-a2ee-464f-be9d-58f11bf3418b.sketch_text.stroke-36"),sQuery(id+"FQ5JFwxVdaqARUP_1.wireOp",EDGE,"fcba4419-a2ee-464f-be9d-58f11bf3418b.sketch_text.stroke-37"),sQuery(id+"FQ5JFwxVdaqARUP_1.wireOp",EDGE,"fcba4419-a2ee-464f-be9d-58f11bf3418b.sketch_text.stroke-38"),sQuery(id+"FQ5JFwxVdaqARUP_1.wireOp",EDGE,"fcba4419-a2ee-464f-be9d-58f11bf3418b.sketch_text.stroke-39"),sQuery(id+"FQ5JFwxVdaqARUP_1.wireOp",EDGE,"fcba4419-a2ee-464f-be9d-58f11bf3418b.sketch_text.stroke-40"),sQuery(id+"FQ5JFwxVdaqARUP_1.wireOp",EDGE,"fcba4419-a2ee-464f-be9d-58f11bf3418b.sketch_text.stroke-41"),sQuery(id+"FQ5JFwxVdaqARUP_1.wireOp",EDGE,"fcba4419-a2ee-464f-be9d-58f11bf3418b.sketch_text.stroke-42"),sQuery(id+"FQ5JFwxVdaqARUP_1.wireOp",EDGE,"fcba4419-a2ee-464f-be9d-58f11bf3418b.sketch_text.stroke-43"),sQuery(id+"FQ5JFwxVdaqARUP_1.wireOp",EDGE,"fcba4419-a2ee-464f-be9d-58f11bf3418b.sketch_text.stroke-44"),sQuery(id+"FQ5JFwxVdaqARUP_1.wireOp",EDGE,"fcba4419-a2ee-464f-be9d-58f11bf3418b.sketch_text.stroke-45"),sQuery(id+"FQ5JFwxVdaqARUP_1.wireOp",EDGE,"fcba4419-a2ee-464f-be9d-58f11bf3418b.sketch_text.stroke-46"),sQuery(id+"FQ5JFwxVdaqARUP_1.wireOp",EDGE,"fcba4419-a2ee-464f-be9d-58f11bf3418b.sketch_text.stroke-47"),sQuery(id+"FQ5JFwxVdaqARUP_1.wireOp",EDGE,"fcba4419-a2ee-464f-be9d-58f11bf3418b.sketch_text.stroke-48"),sQuery(id+"FQ5JFwxVdaqARUP_1.wireOp",EDGE,"fcba4419-a2ee-464f-be9d-58f11bf3418b.sketch_text.stroke-49"),sQuery(id+"FQ5JFwxVdaqARUP_1.wireOp",EDGE,"fcba4419-a2ee-464f-be9d-58f11bf3418b.sketch_text.stroke-50"),sQuery(id+"FQ5JFwxVdaqARUP_1.wireOp",EDGE,"fcba4419-a2ee-464f-be9d-58f11bf3418b.sketch_text.stroke-51"),sQuery(id+"FQ5JFwxVdaqARUP_1.wireOp",EDGE,"fcba4419-a2ee-464f-be9d-58f11bf3418b.sketch_text.stroke-52"),sQuery(id+"FQ5JFwxVdaqARUP_1.wireOp",EDGE,"fcba4419-a2ee-464f-be9d-58f11bf3418b.sketch_text.stroke-53"),sQuery(id+"FQ5JFwxVdaqARUP_1.wireOp",EDGE,"fcba4419-a2ee-464f-be9d-58f11bf3418b.sketch_text.stroke-54"),sQuery(id+"FQ5JFwxVdaqARUP_1.wireOp",EDGE,"fcba4419-a2ee-464f-be9d-58f11bf3418b.sketch_text.stroke-55"),sQuery(id+"FQ5JFwxVdaqARUP_1.wireOp",EDGE,"fcba4419-a2ee-464f-be9d-58f11bf3418b.sketch_text.stroke-56"),sQuery(id+"FQ5JFwxVdaqARUP_1.wireOp",EDGE,"fcba4419-a2ee-464f-be9d-58f11bf3418b.sketch_text.stroke-57"),sQuery(id+"FQ5JFwxVdaqARUP_1.wireOp",EDGE,"fcba4419-a2ee-464f-be9d-58f11bf3418b.sketch_text.stroke-58"),sQuery(id+"FQ5JFwxVdaqARUP_1.wireOp",EDGE,"fcba4419-a2ee-464f-be9d-58f11bf3418b.sketch_text.stroke-59"),sQuery(id+"FQ5JFwxVdaqARUP_1.wireOp",EDGE,"fcba4419-a2ee-464f-be9d-58f11bf3418b.sketch_text.stroke-60"),sQuery(id+"FQ5JFwxVdaqARUP_1.wireOp",EDGE,"fcba4419-a2ee-464f-be9d-58f11bf3418b.sketch_text.stroke-61"),sQuery(id+"FQ5JFwxVdaqARUP_1.wireOp",EDGE,"fcba4419-a2ee-464f-be9d-58f11bf3418b.sketch_text.stroke-62"),sQuery(id+"FQ5JFwxVdaqARUP_1.wireOp",EDGE,"fcba4419-a2ee-464f-be9d-58f11bf3418b.sketch_text.stroke-63"),sQuery(id+"FQ5JFwxVdaqARUP_1.wireOp",EDGE,"fcba4419-a2ee-464f-be9d-58f11bf3418b.sketch_text.stroke-64"),sQuery(id+"FQ5JFwxVdaqARUP_1.wireOp",EDGE,"fcba4419-a2ee-464f-be9d-58f11bf3418b.sketch_text.stroke-65"),sQuery(id+"FQ5JFwxVdaqARUP_1.wireOp",EDGE,"fcba4419-a2ee-464f-be9d-58f11bf3418b.sketch_text.stroke-66"),sQuery(id+"FQ5JFwxVdaqARUP_1.wireOp",EDGE,"fcba4419-a2ee-464f-be9d-58f11bf3418b.sketch_text.stroke-67"),sQuery(id+"FQ5JFwxVdaqARUP_1.wireOp",EDGE,"fcba4419-a2ee-464f-be9d-58f11bf3418b.sketch_text.stroke-68"),sQuery(id+"FQ5JFwxVdaqARUP_1.wireOp",EDGE,"fcba4419-a2ee-464f-be9d-58f11bf3418b.sketch_text.stroke-69"),sQuery(id+"FQ5JFwxVdaqARUP_1.wireOp",EDGE,"fcba4419-a2ee-464f-be9d-58f11bf3418b.sketch_text.stroke-70"),sQuery(id+"FQ5JFwxVdaqARUP_1.wireOp",EDGE,"fcba4419-a2ee-464f-be9d-58f11bf3418b.sketch_text.stroke-71"),sQuery(id+"FQ5JFwxVdaqARUP_1.wireOp",EDGE,"fcba4419-a2ee-464f-be9d-58f11bf3418b.sketch_text.stroke-72"),sQuery(id+"FQ5JFwxVdaqARUP_1.wireOp",EDGE,"fcba4419-a2ee-464f-be9d-58f11bf3418b.sketch_text.stroke-73"),sQuery(id+"FQ5JFwxVdaqARUP_1.wireOp",EDGE,"fcba4419-a2ee-464f-be9d-58f11bf3418b.sketch_text.stroke-74"),sQuery(id+"FQ5JFwxVdaqARUP_1.wireOp",EDGE,"fcba4419-a2ee-464f-be9d-58f11bf3418b.sketch_text.stroke-75"),sQuery(id+"FQ5JFwxVdaqARUP_1.wireOp",EDGE,"fcba4419-a2ee-464f-be9d-58f11bf3418b.sketch_text.stroke-76"),sQuery(id+"FQ5JFwxVdaqARUP_1.wireOp",EDGE,"fcba4419-a2ee-464f-be9d-58f11bf3418b.sketch_text.stroke-77"),sQuery(id+"FQ5JFwxVdaqARUP_1.wireOp",EDGE,"fcba4419-a2ee-464f-be9d-58f11bf3418b.sketch_text.stroke-78"),sQuery(id+"FQ5JFwxVdaqARUP_1.wireOp",EDGE,"fcba4419-a2ee-464f-be9d-58f11bf3418b.sketch_text.stroke-79"),sQuery(id+"FQ5JFwxVdaqARUP_1.wireOp",EDGE,"fcba4419-a2ee-464f-be9d-58f11bf3418b.sketch_text.stroke-80"),sQuery(id+"FQ5JFwxVdaqARUP_1.wireOp",EDGE,"fcba4419-a2ee-464f-be9d-58f11bf3418b.sketch_text.stroke-81"),sQuery(id+"FQ5JFwxVdaqARUP_1.wireOp",EDGE,"fcba4419-a2ee-464f-be9d-58f11bf3418b.sketch_text.stroke-82"),sQuery(id+"FQ5JFwxVdaqARUP_1.wireOp",EDGE,"fcba4419-a2ee-464f-be9d-58f11bf3418b.sketch_text.stroke-83"),sQuery(id+"FQ5JFwxVdaqARUP_1.wireOp",EDGE,"fcba4419-a2ee-464f-be9d-58f11bf3418b.sketch_text.stroke-84"),sQuery(id+"FQ5JFwxVdaqARUP_1.wireOp",EDGE,"fcba4419-a2ee-464f-be9d-58f11bf3418b.sketch_text.stroke-85"),sQuery(id+"FQ5JFwxVdaqARUP_1.wireOp",EDGE,"fcba4419-a2ee-464f-be9d-58f11bf3418b.sketch_text.stroke-86"),sQuery(id+"FQ5JFwxVdaqARUP_1.wireOp",EDGE,"fcba4419-a2ee-464f-be9d-58f11bf3418b.sketch_text.stroke-87"),sQuery(id+"FQ5JFwxVdaqARUP_1.wireOp",EDGE,"fcba4419-a2ee-464f-be9d-58f11bf3418b.sketch_text.stroke-88"),sQuery(id+"FQ5JFwxVdaqARUP_1.wireOp",EDGE,"fcba4419-a2ee-464f-be9d-58f11bf3418b.sketch_text.stroke-89"),sQuery(id+"FQ5JFwxVdaqARUP_1.wireOp",EDGE,"fcba4419-a2ee-464f-be9d-58f11bf3418b.sketch_text.stroke-90"),sQuery(id+"FQ5JFwxVdaqARUP_1.wireOp",EDGE,"fcba4419-a2ee-464f-be9d-58f11bf3418b.sketch_text.stroke-91"),sQuery(id+"FQ5JFwxVdaqARUP_1.wireOp",EDGE,"fcba4419-a2ee-464f-be9d-58f11bf3418b.sketch_text.stroke-92"),sQuery(id+"FQ5JFwxVdaqARUP_1.wireOp",EDGE,"fcba4419-a2ee-464f-be9d-58f11bf3418b.sketch_text.stroke-93"),sQuery(id+"FQ5JFwxVdaqARUP_1.wireOp",EDGE,"fcba4419-a2ee-464f-be9d-58f11bf3418b.sketch_text.stroke-94"),sQuery(id+"FQ5JFwxVdaqARUP_1.wireOp",EDGE,"fcba4419-a2ee-464f-be9d-58f11bf3418b.sketch_text.stroke-95"),sQuery(id+"FQ5JFwxVdaqARUP_1.wireOp",EDGE,"fcba4419-a2ee-464f-be9d-58f11bf3418b.sketch_text.stroke-96"),sQuery(id+"FQ5JFwxVdaqARUP_1.wireOp",EDGE,"fcba4419-a2ee-464f-be9d-58f11bf3418b.sketch_text.stroke-97"),sQuery(id+"FQ5JFwxVdaqARUP_1.wireOp",EDGE,"fcba4419-a2ee-464f-be9d-58f11bf3418b.sketch_text.stroke-98"),sQuery(id+"FQ5JFwxVdaqARUP_1.wireOp",EDGE,"fcba4419-a2ee-464f-be9d-58f11bf3418b.sketch_text.stroke-99"),sQuery(id+"FQ5JFwxVdaqARUP_1.wireOp",EDGE,"fcba4419-a2ee-464f-be9d-58f11bf3418b.sketch_text.stroke-100"),sQuery(id+"FQ5JFwxVdaqARUP_1.wireOp",EDGE,"fcba4419-a2ee-464f-be9d-58f11bf3418b.sketch_text.stroke-101"),sQuery(id+"FQ5JFwxVdaqARUP_1.wireOp",EDGE,"fcba4419-a2ee-464f-be9d-58f11bf3418b.sketch_text.stroke-102"),sQuery(id+"FQ5JFwxVdaqARUP_1.wireOp",EDGE,"fcba4419-a2ee-464f-be9d-58f11bf3418b.sketch_text.stroke-103"),sQuery(id+"FQ5JFwxVdaqARUP_1.wireOp",EDGE,"fcba4419-a2ee-464f-be9d-58f11bf3418b.sketch_text.stroke-104"),sQuery(id+"FQ5JFwxVdaqARUP_1.wireOp",EDGE,"fcba4419-a2ee-464f-be9d-58f11bf3418b.sketch_text.stroke-105"),sQuery(id+"FQ5JFwxVdaqARUP_1.wireOp",EDGE,"fcba4419-a2ee-464f-be9d-58f11bf3418b.sketch_text.stroke-106"),sQuery(id+"FQ5JFwxVdaqARUP_1.wireOp",EDGE,"fcba4419-a2ee-464f-be9d-58f11bf3418b.sketch_text.stroke-107"),sQuery(id+"FQ5JFwxVdaqARUP_1.wireOp",EDGE,"fcba4419-a2ee-464f-be9d-58f11bf3418b.sketch_text.stroke-108"),sQuery(id+"FQ5JFwxVdaqARUP_1.wireOp",EDGE,"fcba4419-a2ee-464f-be9d-58f11bf3418b.sketch_text.stroke-109"),sQuery(id+"FQ5JFwxVdaqARUP_1.wireOp",EDGE,"fcba4419-a2ee-464f-be9d-58f11bf3418b.sketch_text.stroke-110"),sQuery(id+"FQ5JFwxVdaqARUP_1.wireOp",EDGE,"fcba4419-a2ee-464f-be9d-58f11bf3418b.sketch_text.stroke-111"),sQuery(id+"FQ5JFwxVdaqARUP_1.wireOp",EDGE,"fcba4419-a2ee-464f-be9d-58f11bf3418b.sketch_text.stroke-112"),sQuery(id+"FQ5JFwxVdaqARUP_1.wireOp",EDGE,"fcba4419-a2ee-464f-be9d-58f11bf3418b.sketch_text.stroke-113"),sQuery(id+"FQ5JFwxVdaqARUP_1.wireOp",EDGE,"fcba4419-a2ee-464f-be9d-58f11bf3418b.sketch_text.stroke-114"),sQuery(id+"FQ5JFwxVdaqARUP_1.wireOp",EDGE,"fcba4419-a2ee-464f-be9d-58f11bf3418b.sketch_text.stroke-115"),sQuery(id+"FQ5JFwxVdaqARUP_1.wireOp",EDGE,"fcba4419-a2ee-464f-be9d-58f11bf3418b.sketch_text.stroke-116"),sQuery(id+"FQ5JFwxVdaqARUP_1.wireOp",EDGE,"fcba4419-a2ee-464f-be9d-58f11bf3418b.sketch_text.stroke-117"),sQuery(id+"FQ5JFwxVdaqARUP_1.wireOp",EDGE,"fcba4419-a2ee-464f-be9d-58f11bf3418b.sketch_text.stroke-118"),sQuery(id+"FQ5JFwxVdaqARUP_1.wireOp",EDGE,"fcba4419-a2ee-464f-be9d-58f11bf3418b.sketch_text.stroke-119"),sQuery(id+"FQ5JFwxVdaqARUP_1.wireOp",EDGE,"fcba4419-a2ee-464f-be9d-58f11bf3418b.sketch_text.stroke-120"),sQuery(id+"FQ5JFwxVdaqARUP_1.wireOp",EDGE,"fcba4419-a2ee-464f-be9d-58f11bf3418b.sketch_text.stroke-121"),sQuery(id+"FQ5JFwxVdaqARUP_1.wireOp",EDGE,"fcba4419-a2ee-464f-be9d-58f11bf3418b.sketch_text.stroke-122"),sQuery(id+"FQ5JFwxVdaqARUP_1.wireOp",EDGE,"fcba4419-a2ee-464f-be9d-58f11bf3418b.sketch_text.stroke-123"),sQuery(id+"FQ5JFwxVdaqARUP_1.wireOp",EDGE,"fcba4419-a2ee-464f-be9d-58f11bf3418b.sketch_text.stroke-124"),sQuery(id+"FQ5JFwxVdaqARUP_1.wireOp",EDGE,"fcba4419-a2ee-464f-be9d-58f11bf3418b.sketch_text.stroke-125"),sQuery(id+"FQ5JFwxVdaqARUP_1.wireOp",EDGE,"fcba4419-a2ee-464f-be9d-58f11bf3418b.sketch_text.stroke-126"),sQuery(id+"FQ5JFwxVdaqARUP_1.wireOp",EDGE,"fcba4419-a2ee-464f-be9d-58f11bf3418b.sketch_text.stroke-127"),sQuery(id+"FQ5JFwxVdaqARUP_1.wireOp",EDGE,"fcba4419-a2ee-464f-be9d-58f11bf3418b.sketch_text.stroke-128"),sQuery(id+"FQ5JFwxVdaqARUP_1.wireOp",EDGE,"fcba4419-a2ee-464f-be9d-58f11bf3418b.sketch_text.stroke-129"),sQuery(id+"FQ5JFwxVdaqARUP_1.wireOp",EDGE,"fcba4419-a2ee-464f-be9d-58f11bf3418b.sketch_text.stroke-130"),sQuery(id+"FQ5JFwxVdaqARUP_1.wireOp",EDGE,"fcba4419-a2ee-464f-be9d-58f11bf3418b.sketch_text.stroke-131"),sQuery(id+"FQ5JFwxVdaqARUP_1.wireOp",EDGE,"fcba4419-a2ee-464f-be9d-58f11bf3418b.sketch_text.stroke-132"),sQuery(id+"FQ5JFwxVdaqARUP_1.wireOp",EDGE,"fcba4419-a2ee-464f-be9d-58f11bf3418b.sketch_text.stroke-133"),sQuery(id+"FQ5JFwxVdaqARUP_1.wireOp",EDGE,"fcba4419-a2ee-464f-be9d-58f11bf3418b.sketch_text.stroke-134"),sQuery(id+"FQ5JFwxVdaqARUP_1.wireOp",EDGE,"fcba4419-a2ee-464f-be9d-58f11bf3418b.sketch_text.stroke-135"),sQuery(id+"FQ5JFwxVdaqARUP_1.wireOp",EDGE,"fcba4419-a2ee-464f-be9d-58f11bf3418b.sketch_text.stroke-136"),sQuery(id+"FQ5JFwxVdaqARUP_1.wireOp",EDGE,"fcba4419-a2ee-464f-be9d-58f11bf3418b.sketch_text.stroke-137"),sQuery(id+"FQ5JFwxVdaqARUP_1.wireOp",EDGE,"fcba4419-a2ee-464f-be9d-58f11bf3418b.sketch_text.stroke-138"),sQuery(id+"FQ5JFwxVdaqARUP_1.wireOp",EDGE,"fcba4419-a2ee-464f-be9d-58f11bf3418b.sketch_text.stroke-139"),sQuery(id+"FQ5JFwxVdaqARUP_1.wireOp",EDGE,"fcba4419-a2ee-464f-be9d-58f11bf3418b.sketch_text.stroke-140"),sQuery(id+"FQ5JFwxVdaqARUP_1.wireOp",EDGE,"fcba4419-a2ee-464f-be9d-58f11bf3418b.sketch_text.stroke-141"),sQuery(id+"FQ5JFwxVdaqARUP_1.wireOp",EDGE,"fcba4419-a2ee-464f-be9d-58f11bf3418b.sketch_text.stroke-142"),sQuery(id+"FQ5JFwxVdaqARUP_1.wireOp",EDGE,"fcba4419-a2ee-464f-be9d-58f11bf3418b.sketch_text.stroke-143"),sQuery(id+"FQ5JFwxVdaqARUP_1.wireOp",EDGE,"fcba4419-a2ee-464f-be9d-58f11bf3418b.sketch_text.stroke-144"),sQuery(id+"FQ5JFwxVdaqARUP_1.wireOp",EDGE,"fcba4419-a2ee-464f-be9d-58f11bf3418b.sketch_text.stroke-145"),sQuery(id+"FQ5JFwxVdaqARUP_1.wireOp",EDGE,"fcba4419-a2ee-464f-be9d-58f11bf3418b.sketch_text.stroke-146"),sQuery(id+"FQ5JFwxVdaqARUP_1.wireOp",EDGE,"fcba4419-a2ee-464f-be9d-58f11bf3418b.sketch_text.stroke-147"),sQuery(id+"FQ5JFwxVdaqARUP_1.wireOp",EDGE,"fcba4419-a2ee-464f-be9d-58f11bf3418b.sketch_text.stroke-148"),sQuery(id+"FQ5JFwxVdaqARUP_1.wireOp",EDGE,"fcba4419-a2ee-464f-be9d-58f11bf3418b.sketch_text.stroke-149"),sQuery(id+"FQ5JFwxVdaqARUP_1.wireOp",EDGE,"fcba4419-a2ee-464f-be9d-58f11bf3418b.sketch_text.stroke-150"),sQuery(id+"FQ5JFwxVdaqARUP_1.wireOp",EDGE,"fcba4419-a2ee-464f-be9d-58f11bf3418b.sketch_text.stroke-151"),sQuery(id+"FQ5JFwxVdaqARUP_1.wireOp",EDGE,"fcba4419-a2ee-464f-be9d-58f11bf3418b.sketch_text.stroke-152"),sQuery(id+"FQ5JFwxVdaqARUP_1.wireOp",EDGE,"fcba4419-a2ee-464f-be9d-58f11bf3418b.sketch_text.stroke-153"),sQuery(id+"FQ5JFwxVdaqARUP_1.wireOp",EDGE,"fcba4419-a2ee-464f-be9d-58f11bf3418b.sketch_text.stroke-154"),sQuery(id+"FQ5JFwxVdaqARUP_1.wireOp",EDGE,"fcba4419-a2ee-464f-be9d-58f11bf3418b.sketch_text.stroke-155"),sQuery(id+"FQ5JFwxVdaqARUP_1.wireOp",EDGE,"fcba4419-a2ee-464f-be9d-58f11bf3418b.sketch_text.stroke-156"),sQuery(id+"FQ5JFwxVdaqARUP_1.wireOp",EDGE,"fcba4419-a2ee-464f-be9d-58f11bf3418b.sketch_text.stroke-157"),sQuery(id+"FQ5JFwxVdaqARUP_1.wireOp",EDGE,"fcba4419-a2ee-464f-be9d-58f11bf3418b.sketch_text.stroke-158"),sQuery(id+"FQ5JFwxVdaqARUP_1.wireOp",EDGE,"fcba4419-a2ee-464f-be9d-58f11bf3418b.sketch_text.stroke-159"),sQuery(id+"FQ5JFwxVdaqARUP_1.wireOp",EDGE,"fcba4419-a2ee-464f-be9d-58f11bf3418b.sketch_text.stroke-160"),sQuery(id+"FQ5JFwxVdaqARUP_1.wireOp",EDGE,"fcba4419-a2ee-464f-be9d-58f11bf3418b.sketch_text.stroke-161"),sQuery(id+"FQ5JFwxVdaqARUP_1.wireOp",EDGE,"fcba4419-a2ee-464f-be9d-58f11bf3418b.sketch_text.stroke-162"),sQuery(id+"FQ5JFwxVdaqARUP_1.wireOp",EDGE,"fcba4419-a2ee-464f-be9d-58f11bf3418b.sketch_text.stroke-163"),sQuery(id+"FQ5JFwxVdaqARUP_1.wireOp",EDGE,"fcba4419-a2ee-464f-be9d-58f11bf3418b.sketch_text.stroke-164"),sQuery(id+"FQ5JFwxVdaqARUP_1.wireOp",EDGE,"fcba4419-a2ee-464f-be9d-58f11bf3418b.sketch_text.stroke-165"),sQuery(id+"FQ5JFwxVdaqARUP_1.wireOp",EDGE,"fcba4419-a2ee-464f-be9d-58f11bf3418b.sketch_text.stroke-166"),sQuery(id+"FQ5JFwxVdaqARUP_1.wireOp",EDGE,"fcba4419-a2ee-464f-be9d-58f11bf3418b.sketch_text.stroke-167"),sQuery(id+"FQ5JFwxVdaqARUP_1.wireOp",EDGE,"fcba4419-a2ee-464f-be9d-58f11bf3418b.sketch_text.stroke-168"),sQuery(id+"FQ5JFwxVdaqARUP_1.wireOp",EDGE,"fcba4419-a2ee-464f-be9d-58f11bf3418b.sketch_text.stroke-169"),sQuery(id+"FQ5JFwxVdaqARUP_1.wireOp",EDGE,"fcba4419-a2ee-464f-be9d-58f11bf3418b.sketch_text.stroke-170"),sQuery(id+"FQ5JFwxVdaqARUP_1.wireOp",EDGE,"fcba4419-a2ee-464f-be9d-58f11bf3418b.sketch_text.stroke-171"),sQuery(id+"FQ5JFwxVdaqARUP_1.wireOp",EDGE,"fcba4419-a2ee-464f-be9d-58f11bf3418b.sketch_text.stroke-172"),sQuery(id+"FQ5JFwxVdaqARUP_1.wireOp",EDGE,"fcba4419-a2ee-464f-be9d-58f11bf3418b.sketch_text.stroke-173"),sQuery(id+"FHMxAyK4CFUKdhS_1.wireOp",EDGE,"1cb9c079-ea9b-4899-8069-e0e3048e911d.sketch_text.stroke-0"),sQuery(id+"FHMxAyK4CFUKdhS_1.wireOp",EDGE,"1cb9c079-ea9b-4899-8069-e0e3048e911d.sketch_text.stroke-1"),sQuery(id+"FHMxAyK4CFUKdhS_1.wireOp",EDGE,"1cb9c079-ea9b-4899-8069-e0e3048e911d.sketch_text.stroke-2"),sQuery(id+"FHMxAyK4CFUKdhS_1.wireOp",EDGE,"1cb9c079-ea9b-4899-8069-e0e3048e911d.sketch_text.stroke-3"),sQuery(id+"FHMxAyK4CFUKdhS_1.wireOp",EDGE,"1cb9c079-ea9b-4899-8069-e0e3048e911d.sketch_text.stroke-4"),sQuery(id+"FHMxAyK4CFUKdhS_1.wireOp",EDGE,"1cb9c079-ea9b-4899-8069-e0e3048e911d.sketch_text.stroke-5"),sQuery(id+"FHMxAyK4CFUKdhS_1.wireOp",EDGE,"1cb9c079-ea9b-4899-8069-e0e3048e911d.sketch_text.stroke-6"),sQuery(id+"FHMxAyK4CFUKdhS_1.wireOp",EDGE,"1cb9c079-ea9b-4899-8069-e0e3048e911d.sketch_text.stroke-7"),sQuery(id+"FHMxAyK4CFUKdhS_1.wireOp",EDGE,"1cb9c079-ea9b-4899-8069-e0e3048e911d.sketch_text.stroke-8"),sQuery(id+"FHMxAyK4CFUKdhS_1.wireOp",EDGE,"1cb9c079-ea9b-4899-8069-e0e3048e911d.sketch_text.stroke-9"),sQuery(id+"FHMxAyK4CFUKdhS_1.wireOp",EDGE,"1cb9c079-ea9b-4899-8069-e0e3048e911d.sketch_text.stroke-10"),sQuery(id+"FHMxAyK4CFUKdhS_1.wireOp",EDGE,"1cb9c079-ea9b-4899-8069-e0e3048e911d.sketch_text.stroke-11"),sQuery(id+"FHMxAyK4CFUKdhS_1.wireOp",EDGE,"1cb9c079-ea9b-4899-8069-e0e3048e911d.sketch_text.stroke-12"),sQuery(id+"FHMxAyK4CFUKdhS_1.wireOp",EDGE,"1cb9c079-ea9b-4899-8069-e0e3048e911d.sketch_text.stroke-13"),sQuery(id+"FHMxAyK4CFUKdhS_1.wireOp",EDGE,"1cb9c079-ea9b-4899-8069-e0e3048e911d.sketch_text.stroke-14"),sQuery(id+"FHMxAyK4CFUKdhS_1.wireOp",EDGE,"1cb9c079-ea9b-4899-8069-e0e3048e911d.sketch_text.stroke-15"),sQuery(id+"FHMxAyK4CFUKdhS_1.wireOp",EDGE,"1cb9c079-ea9b-4899-8069-e0e3048e911d.sketch_text.stroke-16"),sQuery(id+"FHMxAyK4CFUKdhS_1.wireOp",EDGE,"1cb9c079-ea9b-4899-8069-e0e3048e911d.sketch_text.stroke-17"),sQuery(id+"FHMxAyK4CFUKdhS_1.wireOp",EDGE,"1cb9c079-ea9b-4899-8069-e0e3048e911d.sketch_text.stroke-18"),sQuery(id+"FHMxAyK4CFUKdhS_1.wireOp",EDGE,"1cb9c079-ea9b-4899-8069-e0e3048e911d.sketch_text.stroke-19"),sQuery(id+"FHMxAyK4CFUKdhS_1.wireOp",EDGE,"1cb9c079-ea9b-4899-8069-e0e3048e911d.sketch_text.stroke-20"),sQuery(id+"FHMxAyK4CFUKdhS_1.wireOp",EDGE,"1cb9c079-ea9b-4899-8069-e0e3048e911d.sketch_text.stroke-21"),sQuery(id+"FHMxAyK4CFUKdhS_1.wireOp",EDGE,"1cb9c079-ea9b-4899-8069-e0e3048e911d.sketch_text.stroke-22"),sQuery(id+"FHMxAyK4CFUKdhS_1.wireOp",EDGE,"1cb9c079-ea9b-4899-8069-e0e3048e911d.sketch_text.stroke-23"),sQuery(id+"FHMxAyK4CFUKdhS_1.wireOp",EDGE,"1cb9c079-ea9b-4899-8069-e0e3048e911d.sketch_text.stroke-24"),sQuery(id+"FHMxAyK4CFUKdhS_1.wireOp",EDGE,"1cb9c079-ea9b-4899-8069-e0e3048e911d.sketch_text.stroke-25"),sQuery(id+"FHMxAyK4CFUKdhS_1.wireOp",EDGE,"1cb9c079-ea9b-4899-8069-e0e3048e911d.sketch_text.stroke-26"),sQuery(id+"FHMxAyK4CFUKdhS_1.wireOp",EDGE,"1cb9c079-ea9b-4899-8069-e0e3048e911d.sketch_text.stroke-27"),sQuery(id+"FHMxAyK4CFUKdhS_1.wireOp",EDGE,"1cb9c079-ea9b-4899-8069-e0e3048e911d.sketch_text.stroke-28"),sQuery(id+"FHMxAyK4CFUKdhS_1.wireOp",EDGE,"1cb9c079-ea9b-4899-8069-e0e3048e911d.sketch_text.stroke-29"),sQuery(id+"FHMxAyK4CFUKdhS_1.wireOp",EDGE,"1cb9c079-ea9b-4899-8069-e0e3048e911d.sketch_text.stroke-30"),sQuery(id+"FHMxAyK4CFUKdhS_1.wireOp",EDGE,"1cb9c079-ea9b-4899-8069-e0e3048e911d.sketch_text.stroke-31"),sQuery(id+"FHMxAyK4CFUKdhS_1.wireOp",EDGE,"1cb9c079-ea9b-4899-8069-e0e3048e911d.sketch_text.stroke-32"),sQuery(id+"FHMxAyK4CFUKdhS_1.wireOp",EDGE,"1cb9c079-ea9b-4899-8069-e0e3048e911d.sketch_text.stroke-33"),sQuery(id+"FHMxAyK4CFUKdhS_1.wireOp",EDGE,"1cb9c079-ea9b-4899-8069-e0e3048e911d.sketch_text.stroke-34"),sQuery(id+"FHMxAyK4CFUKdhS_1.wireOp",EDGE,"1cb9c079-ea9b-4899-8069-e0e3048e911d.sketch_text.stroke-35"),sQuery(id+"FHMxAyK4CFUKdhS_1.wireOp",EDGE,"1cb9c079-ea9b-4899-8069-e0e3048e911d.sketch_text.stroke-36"),sQuery(id+"FHMxAyK4CFUKdhS_1.wireOp",EDGE,"1cb9c079-ea9b-4899-8069-e0e3048e911d.sketch_text.stroke-37"),sQuery(id+"FHMxAyK4CFUKdhS_1.wireOp",EDGE,"1cb9c079-ea9b-4899-8069-e0e3048e911d.sketch_text.stroke-38"),sQuery(id+"FHMxAyK4CFUKdhS_1.wireOp",EDGE,"1cb9c079-ea9b-4899-8069-e0e3048e911d.sketch_text.stroke-39"),sQuery(id+"FHMxAyK4CFUKdhS_1.wireOp",EDGE,"1cb9c079-ea9b-4899-8069-e0e3048e911d.sketch_text.stroke-40"),sQuery(id+"FHMxAyK4CFUKdhS_1.wireOp",EDGE,"1cb9c079-ea9b-4899-8069-e0e3048e911d.sketch_text.stroke-41"),sQuery(id+"FHMxAyK4CFUKdhS_1.wireOp",EDGE,"1cb9c079-ea9b-4899-8069-e0e3048e911d.sketch_text.stroke-42"),sQuery(id+"FHMxAyK4CFUKdhS_1.wireOp",EDGE,"1cb9c079-ea9b-4899-8069-e0e3048e911d.sketch_text.stroke-43"),sQuery(id+"FHMxAyK4CFUKdhS_1.wireOp",EDGE,"1cb9c079-ea9b-4899-8069-e0e3048e911d.sketch_text.stroke-44"),sQuery(id+"FHMxAyK4CFUKdhS_1.wireOp",EDGE,"1cb9c079-ea9b-4899-8069-e0e3048e911d.sketch_text.stroke-45"),sQuery(id+"FHMxAyK4CFUKdhS_1.wireOp",EDGE,"1cb9c079-ea9b-4899-8069-e0e3048e911d.sketch_text.stroke-46"),sQuery(id+"FHMxAyK4CFUKdhS_1.wireOp",EDGE,"1cb9c079-ea9b-4899-8069-e0e3048e911d.sketch_text.stroke-47"),sQuery(id+"FHMxAyK4CFUKdhS_1.wireOp",EDGE,"1cb9c079-ea9b-4899-8069-e0e3048e911d.sketch_text.stroke-48"),sQuery(id+"FHMxAyK4CFUKdhS_1.wireOp",EDGE,"1cb9c079-ea9b-4899-8069-e0e3048e911d.sketch_text.stroke-49"),sQuery(id+"FHMxAyK4CFUKdhS_1.wireOp",EDGE,"1cb9c079-ea9b-4899-8069-e0e3048e911d.sketch_text.stroke-50"),sQuery(id+"FHMxAyK4CFUKdhS_1.wireOp",EDGE,"1cb9c079-ea9b-4899-8069-e0e3048e911d.sketch_text.stroke-51"),sQuery(id+"FHMxAyK4CFUKdhS_1.wireOp",EDGE,"1cb9c079-ea9b-4899-8069-e0e3048e911d.sketch_text.stroke-52"),sQuery(id+"FHMxAyK4CFUKdhS_1.wireOp",EDGE,"1cb9c079-ea9b-4899-8069-e0e3048e911d.sketch_text.stroke-53"),sQuery(id+"FHMxAyK4CFUKdhS_1.wireOp",EDGE,"1cb9c079-ea9b-4899-8069-e0e3048e911d.sketch_text.stroke-54"),sQuery(id+"FHMxAyK4CFUKdhS_1.wireOp",EDGE,"1cb9c079-ea9b-4899-8069-e0e3048e911d.sketch_text.stroke-55"),sQuery(id+"FHMxAyK4CFUKdhS_1.wireOp",EDGE,"1cb9c079-ea9b-4899-8069-e0e3048e911d.sketch_text.stroke-56"),sQuery(id+"FHMxAyK4CFUKdhS_1.wireOp",EDGE,"1cb9c079-ea9b-4899-8069-e0e3048e911d.sketch_text.stroke-57"),sQuery(id+"FHMxAyK4CFUKdhS_1.wireOp",EDGE,"1cb9c079-ea9b-4899-8069-e0e3048e911d.sketch_text.stroke-58"),sQuery(id+"FHMxAyK4CFUKdhS_1.wireOp",EDGE,"1cb9c079-ea9b-4899-8069-e0e3048e911d.sketch_text.stroke-59"),sQuery(id+"FHMxAyK4CFUKdhS_1.wireOp",EDGE,"1cb9c079-ea9b-4899-8069-e0e3048e911d.sketch_text.stroke-60"),sQuery(id+"FHMxAyK4CFUKdhS_1.wireOp",EDGE,"1cb9c079-ea9b-4899-8069-e0e3048e911d.sketch_text.stroke-61"),sQuery(id+"FHMxAyK4CFUKdhS_1.wireOp",EDGE,"1cb9c079-ea9b-4899-8069-e0e3048e911d.sketch_text.stroke-62"),sQuery(id+"FHMxAyK4CFUKdhS_1.wireOp",EDGE,"1cb9c079-ea9b-4899-8069-e0e3048e911d.sketch_text.stroke-71"),sQuery(id+"FHMxAyK4CFUKdhS_1.wireOp",EDGE,"1cb9c079-ea9b-4899-8069-e0e3048e911d.sketch_text.stroke-72"),sQuery(id+"FHMxAyK4CFUKdhS_1.wireOp",EDGE,"1cb9c079-ea9b-4899-8069-e0e3048e911d.sketch_text.stroke-73"),sQuery(id+"FHMxAyK4CFUKdhS_1.wireOp",EDGE,"1cb9c079-ea9b-4899-8069-e0e3048e911d.sketch_text.stroke-74"),sQuery(id+"FHMxAyK4CFUKdhS_1.wireOp",EDGE,"1cb9c079-ea9b-4899-8069-e0e3048e911d.sketch_text.stroke-75"),sQuery(id+"FHMxAyK4CFUKdhS_1.wireOp",EDGE,"1cb9c079-ea9b-4899-8069-e0e3048e911d.sketch_text.stroke-76"),sQuery(id+"FHMxAyK4CFUKdhS_1.wireOp",EDGE,"1cb9c079-ea9b-4899-8069-e0e3048e911d.sketch_text.stroke-77"),sQuery(id+"FHMxAyK4CFUKdhS_1.wireOp",EDGE,"1cb9c079-ea9b-4899-8069-e0e3048e911d.sketch_text.stroke-78"),sQuery(id+"FHMxAyK4CFUKdhS_1.wireOp",EDGE,"1cb9c079-ea9b-4899-8069-e0e3048e911d.sketch_text.stroke-79"),sQuery(id+"FHMxAyK4CFUKdhS_1.wireOp",EDGE,"1cb9c079-ea9b-4899-8069-e0e3048e911d.sketch_text.stroke-80"),sQuery(id+"FHMxAyK4CFUKdhS_1.wireOp",EDGE,"1cb9c079-ea9b-4899-8069-e0e3048e911d.sketch_text.stroke-81"),sQuery(id+"FHMxAyK4CFUKdhS_1.wireOp",EDGE,"1cb9c079-ea9b-4899-8069-e0e3048e911d.sketch_text.stroke-82"),sQuery(id+"FHMxAyK4CFUKdhS_1.wireOp",EDGE,"1cb9c079-ea9b-4899-8069-e0e3048e911d.sketch_text.stroke-83"),sQuery(id+"FHMxAyK4CFUKdhS_1.wireOp",EDGE,"1cb9c079-ea9b-4899-8069-e0e3048e911d.sketch_text.stroke-84"),sQuery(id+"FHMxAyK4CFUKdhS_1.wireOp",EDGE,"1cb9c079-ea9b-4899-8069-e0e3048e911d.sketch_text.stroke-85"),sQuery(id+"FHMxAyK4CFUKdhS_1.wireOp",EDGE,"1cb9c079-ea9b-4899-8069-e0e3048e911d.sketch_text.stroke-86"),sQuery(id+"FHMxAyK4CFUKdhS_1.wireOp",EDGE,"1cb9c079-ea9b-4899-8069-e0e3048e911d.sketch_text.stroke-87"),sQuery(id+"FHMxAyK4CFUKdhS_1.wireOp",EDGE,"1cb9c079-ea9b-4899-8069-e0e3048e911d.sketch_text.stroke-88"),sQuery(id+"FHMxAyK4CFUKdhS_1.wireOp",EDGE,"1cb9c079-ea9b-4899-8069-e0e3048e911d.sketch_text.stroke-89"),sQuery(id+"FHMxAyK4CFUKdhS_1.wireOp",EDGE,"1cb9c079-ea9b-4899-8069-e0e3048e911d.sketch_text.stroke-90"),sQuery(id+"FHMxAyK4CFUKdhS_1.wireOp",EDGE,"1cb9c079-ea9b-4899-8069-e0e3048e911d.sketch_text.stroke-91"),sQuery(id+"FHMxAyK4CFUKdhS_1.wireOp",EDGE,"1cb9c079-ea9b-4899-8069-e0e3048e911d.sketch_text.stroke-92"),sQuery(id+"FHMxAyK4CFUKdhS_1.wireOp",EDGE,"1cb9c079-ea9b-4899-8069-e0e3048e911d.sketch_text.stroke-93"),sQuery(id+"FHMxAyK4CFUKdhS_1.wireOp",EDGE,"1cb9c079-ea9b-4899-8069-e0e3048e911d.sketch_text.stroke-94"),sQuery(id+"FHMxAyK4CFUKdhS_1.wireOp",EDGE,"1cb9c079-ea9b-4899-8069-e0e3048e911d.sketch_text.stroke-95"),sQuery(id+"FHMxAyK4CFUKdhS_1.wireOp",EDGE,"1cb9c079-ea9b-4899-8069-e0e3048e911d.sketch_text.stroke-96"),sQuery(id+"FHMxAyK4CFUKdhS_1.wireOp",EDGE,"1cb9c079-ea9b-4899-8069-e0e3048e911d.sketch_text.stroke-97"),sQuery(id+"FHMxAyK4CFUKdhS_1.wireOp",EDGE,"1cb9c079-ea9b-4899-8069-e0e3048e911d.sketch_text.stroke-103"),sQuery(id+"FHMxAyK4CFUKdhS_1.wireOp",EDGE,"1cb9c079-ea9b-4899-8069-e0e3048e911d.sketch_text.stroke-104"),sQuery(id+"FHMxAyK4CFUKdhS_1.wireOp",EDGE,"1cb9c079-ea9b-4899-8069-e0e3048e911d.sketch_text.stroke-105"),sQuery(id+"FHMxAyK4CFUKdhS_1.wireOp",EDGE,"1cb9c079-ea9b-4899-8069-e0e3048e911d.sketch_text.stroke-106"),sQuery(id+"FHMxAyK4CFUKdhS_1.wireOp",EDGE,"1cb9c079-ea9b-4899-8069-e0e3048e911d.sketch_text.stroke-107"),sQuery(id+"FHMxAyK4CFUKdhS_1.wireOp",EDGE,"1cb9c079-ea9b-4899-8069-e0e3048e911d.sketch_text.stroke-108"),sQuery(id+"FHMxAyK4CFUKdhS_1.wireOp",EDGE,"1cb9c079-ea9b-4899-8069-e0e3048e911d.sketch_text.stroke-109"),sQuery(id+"FHMxAyK4CFUKdhS_1.wireOp",EDGE,"1cb9c079-ea9b-4899-8069-e0e3048e911d.sketch_text.stroke-110"),sQuery(id+"FHMxAyK4CFUKdhS_1.wireOp",EDGE,"1cb9c079-ea9b-4899-8069-e0e3048e911d.sketch_text.stroke-111"),sQuery(id+"FHMxAyK4CFUKdhS_1.wireOp",EDGE,"1cb9c079-ea9b-4899-8069-e0e3048e911d.sketch_text.stroke-112"),sQuery(id+"FHMxAyK4CFUKdhS_1.wireOp",EDGE,"1cb9c079-ea9b-4899-8069-e0e3048e911d.sketch_text.stroke-113"),sQuery(id+"FHMxAyK4CFUKdhS_1.wireOp",EDGE,"1cb9c079-ea9b-4899-8069-e0e3048e911d.sketch_text.stroke-114"),sQuery(id+"FHMxAyK4CFUKdhS_1.wireOp",EDGE,"1cb9c079-ea9b-4899-8069-e0e3048e911d.sketch_text.stroke-115"),sQuery(id+"FHMxAyK4CFUKdhS_1.wireOp",EDGE,"1cb9c079-ea9b-4899-8069-e0e3048e911d.sketch_text.stroke-116"),sQuery(id+"FHMxAyK4CFUKdhS_1.wireOp",EDGE,"1cb9c079-ea9b-4899-8069-e0e3048e911d.sketch_text.stroke-117"),sQuery(id+"FHMxAyK4CFUKdhS_1.wireOp",EDGE,"1cb9c079-ea9b-4899-8069-e0e3048e911d.sketch_text.stroke-118"),sQuery(id+"FHMxAyK4CFUKdhS_1.wireOp",EDGE,"1cb9c079-ea9b-4899-8069-e0e3048e911d.sketch_text.stroke-119"),sQuery(id+"FHMxAyK4CFUKdhS_1.wireOp",EDGE,"1cb9c079-ea9b-4899-8069-e0e3048e911d.sketch_text.stroke-120"),sQuery(id+"FHMxAyK4CFUKdhS_1.wireOp",EDGE,"1cb9c079-ea9b-4899-8069-e0e3048e911d.sketch_text.stroke-121"),sQuery(id+"FHMxAyK4CFUKdhS_1.wireOp",EDGE,"1cb9c079-ea9b-4899-8069-e0e3048e911d.sketch_text.stroke-122"),sQuery(id+"FHMxAyK4CFUKdhS_1.wireOp",EDGE,"1cb9c079-ea9b-4899-8069-e0e3048e911d.sketch_text.stroke-123"),sQuery(id+"FHMxAyK4CFUKdhS_1.wireOp",EDGE,"1cb9c079-ea9b-4899-8069-e0e3048e911d.sketch_text.stroke-124"),sQuery(id+"FHMxAyK4CFUKdhS_1.wireOp",EDGE,"1cb9c079-ea9b-4899-8069-e0e3048e911d.sketch_text.stroke-125"),sQuery(id+"FHMxAyK4CFUKdhS_1.wireOp",EDGE,"1cb9c079-ea9b-4899-8069-e0e3048e911d.sketch_text.stroke-126"),sQuery(id+"FHMxAyK4CFUKdhS_1.wireOp",EDGE,"1cb9c079-ea9b-4899-8069-e0e3048e911d.sketch_text.stroke-127"),sQuery(id+"FHMxAyK4CFUKdhS_1.wireOp",EDGE,"1cb9c079-ea9b-4899-8069-e0e3048e911d.sketch_text.stroke-128"),sQuery(id+"FHMxAyK4CFUKdhS_1.wireOp",EDGE,"1cb9c079-ea9b-4899-8069-e0e3048e911d.sketch_text.stroke-129"),sQuery(id+"FHMxAyK4CFUKdhS_1.wireOp",EDGE,"1cb9c079-ea9b-4899-8069-e0e3048e911d.sketch_text.stroke-130"),sQuery(id+"FHMxAyK4CFUKdhS_1.wireOp",EDGE,"1cb9c079-ea9b-4899-8069-e0e3048e911d.sketch_text.stroke-131"),sQuery(id+"FHMxAyK4CFUKdhS_1.wireOp",EDGE,"1cb9c079-ea9b-4899-8069-e0e3048e911d.sketch_text.stroke-132"),sQuery(id+"FHMxAyK4CFUKdhS_1.wireOp",EDGE,"1cb9c079-ea9b-4899-8069-e0e3048e911d.sketch_text.stroke-133"),sQuery(id+"FHMxAyK4CFUKdhS_1.wireOp",EDGE,"1cb9c079-ea9b-4899-8069-e0e3048e911d.sketch_text.stroke-134"),sQuery(id+"FHMxAyK4CFUKdhS_1.wireOp",EDGE,"1cb9c079-ea9b-4899-8069-e0e3048e911d.sketch_text.stroke-135"),sQuery(id+"FHMxAyK4CFUKdhS_1.wireOp",EDGE,"1cb9c079-ea9b-4899-8069-e0e3048e911d.sketch_text.stroke-136"),sQuery(id+"FHMxAyK4CFUKdhS_1.wireOp",EDGE,"1cb9c079-ea9b-4899-8069-e0e3048e911d.sketch_text.stroke-137"),sQuery(id+"FHMxAyK4CFUKdhS_1.wireOp",EDGE,"1cb9c079-ea9b-4899-8069-e0e3048e911d.sketch_text.stroke-138"),sQuery(id+"FHMxAyK4CFUKdhS_1.wireOp",EDGE,"1cb9c079-ea9b-4899-8069-e0e3048e911d.sketch_text.stroke-139"),sQuery(id+"FHMxAyK4CFUKdhS_1.wireOp",EDGE,"1cb9c079-ea9b-4899-8069-e0e3048e911d.sketch_text.stroke-140"),sQuery(id+"FHMxAyK4CFUKdhS_1.wireOp",EDGE,"1cb9c079-ea9b-4899-8069-e0e3048e911d.sketch_text.stroke-141"),sQuery(id+"FHMxAyK4CFUKdhS_1.wireOp",EDGE,"1cb9c079-ea9b-4899-8069-e0e3048e911d.sketch_text.stroke-142"),sQuery(id+"FHMxAyK4CFUKdhS_1.wireOp",EDGE,"1cb9c079-ea9b-4899-8069-e0e3048e911d.sketch_text.stroke-143"),sQuery(id+"FHMxAyK4CFUKdhS_1.wireOp",EDGE,"1cb9c079-ea9b-4899-8069-e0e3048e911d.sketch_text.stroke-144"),sQuery(id+"FHMxAyK4CFUKdhS_1.wireOp",EDGE,"1cb9c079-ea9b-4899-8069-e0e3048e911d.sketch_text.stroke-145"),sQuery(id+"FHMxAyK4CFUKdhS_1.wireOp",EDGE,"1cb9c079-ea9b-4899-8069-e0e3048e911d.sketch_text.stroke-146"),sQuery(id+"FHMxAyK4CFUKdhS_1.wireOp",EDGE,"1cb9c079-ea9b-4899-8069-e0e3048e911d.sketch_text.stroke-147"),sQuery(id+"FHMxAyK4CFUKdhS_1.wireOp",EDGE,"1cb9c079-ea9b-4899-8069-e0e3048e911d.sketch_text.stroke-148"),sQuery(id+"FHMxAyK4CFUKdhS_1.wireOp",EDGE,"1cb9c079-ea9b-4899-8069-e0e3048e911d.sketch_text.stroke-149"),sQuery(id+"FHMxAyK4CFUKdhS_1.wireOp",EDGE,"1cb9c079-ea9b-4899-8069-e0e3048e911d.sketch_text.stroke-150"),sQuery(id+"FHMxAyK4CFUKdhS_1.wireOp",EDGE,"1cb9c079-ea9b-4899-8069-e0e3048e911d.sketch_text.stroke-151"),sQuery(id+"FHMxAyK4CFUKdhS_1.wireOp",EDGE,"1cb9c079-ea9b-4899-8069-e0e3048e911d.sketch_text.stroke-152"),sQuery(id+"FHMxAyK4CFUKdhS_1.wireOp",EDGE,"1cb9c079-ea9b-4899-8069-e0e3048e911d.sketch_text.stroke-153"),sQuery(id+"FHMxAyK4CFUKdhS_1.wireOp",EDGE,"1cb9c079-ea9b-4899-8069-e0e3048e911d.sketch_text.stroke-159"),sQuery(id+"FHMxAyK4CFUKdhS_1.wireOp",EDGE,"1cb9c079-ea9b-4899-8069-e0e3048e911d.sketch_text.stroke-160"),sQuery(id+"FHMxAyK4CFUKdhS_1.wireOp",EDGE,"1cb9c079-ea9b-4899-8069-e0e3048e911d.sketch_text.stroke-161"),sQuery(id+"FHMxAyK4CFUKdhS_1.wireOp",EDGE,"1cb9c079-ea9b-4899-8069-e0e3048e911d.sketch_text.stroke-162"),sQuery(id+"FHMxAyK4CFUKdhS_1.wireOp",EDGE,"1cb9c079-ea9b-4899-8069-e0e3048e911d.sketch_text.stroke-163"),sQuery(id+"FHMxAyK4CFUKdhS_1.wireOp",EDGE,"1cb9c079-ea9b-4899-8069-e0e3048e911d.sketch_text.stroke-164"),sQuery(id+"FHMxAyK4CFUKdhS_1.wireOp",EDGE,"1cb9c079-ea9b-4899-8069-e0e3048e911d.sketch_text.stroke-165"),sQuery(id+"FHMxAyK4CFUKdhS_1.wireOp",EDGE,"1cb9c079-ea9b-4899-8069-e0e3048e911d.sketch_text.stroke-166"),sQuery(id+"FHMxAyK4CFUKdhS_1.wireOp",EDGE,"1cb9c079-ea9b-4899-8069-e0e3048e911d.sketch_text.stroke-167"),sQuery(id+"FHMxAyK4CFUKdhS_1.wireOp",EDGE,"1cb9c079-ea9b-4899-8069-e0e3048e911d.sketch_text.stroke-168"),sQuery(id+"FHMxAyK4CFUKdhS_1.wireOp",EDGE,"1cb9c079-ea9b-4899-8069-e0e3048e911d.sketch_text.stroke-169"),sQuery(id+"FHMxAyK4CFUKdhS_1.wireOp",EDGE,"1cb9c079-ea9b-4899-8069-e0e3048e911d.sketch_text.stroke-170"),sQuery(id+"FHMxAyK4CFUKdhS_1.wireOp",EDGE,"1cb9c079-ea9b-4899-8069-e0e3048e911d.sketch_text.stroke-171"),sQuery(id+"FHMxAyK4CFUKdhS_1.wireOp",EDGE,"1cb9c079-ea9b-4899-8069-e0e3048e911d.sketch_text.stroke-172"),sQuery(id+"FHMxAyK4CFUKdhS_1.wireOp",EDGE,"1cb9c079-ea9b-4899-8069-e0e3048e911d.sketch_text.stroke-173"),sQuery(id+"FHMxAyK4CFUKdhS_1.wireOp",EDGE,"1cb9c079-ea9b-4899-8069-e0e3048e911d.sketch_text.stroke-174"),sQuery(id+"FHMxAyK4CFUKdhS_1.wireOp",EDGE,"1cb9c079-ea9b-4899-8069-e0e3048e911d.sketch_text.stroke-175"),sQuery(id+"FHMxAyK4CFUKdhS_1.wireOp",EDGE,"1cb9c079-ea9b-4899-8069-e0e3048e911d.sketch_text.stroke-176"),sQuery(id+"FHMxAyK4CFUKdhS_1.wireOp",EDGE,"1cb9c079-ea9b-4899-8069-e0e3048e911d.sketch_text.stroke-177"),sQuery(id+"FHMxAyK4CFUKdhS_1.wireOp",EDGE,"1cb9c079-ea9b-4899-8069-e0e3048e911d.sketch_text.stroke-178"),sQuery(id+"FHMxAyK4CFUKdhS_1.wireOp",EDGE,"1cb9c079-ea9b-4899-8069-e0e3048e911d.sketch_text.stroke-179"),sQuery(id+"FHMxAyK4CFUKdhS_1.wireOp",EDGE,"1cb9c079-ea9b-4899-8069-e0e3048e911d.sketch_text.stroke-180"),sQuery(id+"F2.wireOp",EDGE,"8007402e-1a4e-4a06-85a5-2af08e553504"),subQ2])],"isStart":true}),makeQuery(id+"F3.opExtrude","SWEPT_FACE",FACE,{"disambiguationData":[OSD([subQ2])]})])],"derivedFrom":makeQuery(id+"F3.opExtrude","CAP_EDGE",EDGE,{"disambiguationData":[OSD([subQ2])],"isStart":true})});}
            var Q14;
            {var subQ0=sQuery(id+"F0.wireOp",EDGE,"E0.top");var subQ1=sQuery(id+"F0.wireOp",EDGE,"E0.bottom");var subQ2=sQuery(id+"F2.wireOp",EDGE,"727ac2c1-f511-4829-95a7-a443ef16a4cd");Q14=makeQuery(id+"F3.boolean.opBoolean","SPLIT",EDGE,{"disambiguationData":[TD([makeQuery(id+"F1.opExtrude","CAP_FACE",FACE,{"disambiguationData":[OSD([subQ1,subQ0,sQuery(id+"F0.wireOp",EDGE,"E0.left"),sQuery(id+"F0.wireOp",EDGE,"E0.right")])],"isStart":false}),makeQuery(id+"F1.opExtrude","SWEPT_FACE",FACE,{"disambiguationData":[OSD([subQ0])]}),makeQuery(id+"F3.opExtrude","CAP_FACE",FACE,{"disambiguationData":[OSD([subQ1,sQuery(id+"FQ5JFwxVdaqARUP_1.wireOp",EDGE,"fcba4419-a2ee-464f-be9d-58f11bf3418b.sketch_text.stroke-0"),sQuery(id+"FQ5JFwxVdaqARUP_1.wireOp",EDGE,"fcba4419-a2ee-464f-be9d-58f11bf3418b.sketch_text.stroke-1"),sQuery(id+"FQ5JFwxVdaqARUP_1.wireOp",EDGE,"fcba4419-a2ee-464f-be9d-58f11bf3418b.sketch_text.stroke-2"),sQuery(id+"FQ5JFwxVdaqARUP_1.wireOp",EDGE,"fcba4419-a2ee-464f-be9d-58f11bf3418b.sketch_text.stroke-3"),sQuery(id+"FQ5JFwxVdaqARUP_1.wireOp",EDGE,"fcba4419-a2ee-464f-be9d-58f11bf3418b.sketch_text.stroke-4"),sQuery(id+"FQ5JFwxVdaqARUP_1.wireOp",EDGE,"fcba4419-a2ee-464f-be9d-58f11bf3418b.sketch_text.stroke-5"),sQuery(id+"FQ5JFwxVdaqARUP_1.wireOp",EDGE,"fcba4419-a2ee-464f-be9d-58f11bf3418b.sketch_text.stroke-6"),sQuery(id+"FQ5JFwxVdaqARUP_1.wireOp",EDGE,"fcba4419-a2ee-464f-be9d-58f11bf3418b.sketch_text.stroke-7"),sQuery(id+"FQ5JFwxVdaqARUP_1.wireOp",EDGE,"fcba4419-a2ee-464f-be9d-58f11bf3418b.sketch_text.stroke-8"),sQuery(id+"FQ5JFwxVdaqARUP_1.wireOp",EDGE,"fcba4419-a2ee-464f-be9d-58f11bf3418b.sketch_text.stroke-9"),sQuery(id+"FQ5JFwxVdaqARUP_1.wireOp",EDGE,"fcba4419-a2ee-464f-be9d-58f11bf3418b.sketch_text.stroke-10"),sQuery(id+"FQ5JFwxVdaqARUP_1.wireOp",EDGE,"fcba4419-a2ee-464f-be9d-58f11bf3418b.sketch_text.stroke-11"),sQuery(id+"FQ5JFwxVdaqARUP_1.wireOp",EDGE,"fcba4419-a2ee-464f-be9d-58f11bf3418b.sketch_text.stroke-12"),sQuery(id+"FQ5JFwxVdaqARUP_1.wireOp",EDGE,"fcba4419-a2ee-464f-be9d-58f11bf3418b.sketch_text.stroke-13"),sQuery(id+"FQ5JFwxVdaqARUP_1.wireOp",EDGE,"fcba4419-a2ee-464f-be9d-58f11bf3418b.sketch_text.stroke-14"),sQuery(id+"FQ5JFwxVdaqARUP_1.wireOp",EDGE,"fcba4419-a2ee-464f-be9d-58f11bf3418b.sketch_text.stroke-15"),sQuery(id+"FQ5JFwxVdaqARUP_1.wireOp",EDGE,"fcba4419-a2ee-464f-be9d-58f11bf3418b.sketch_text.stroke-16"),sQuery(id+"FQ5JFwxVdaqARUP_1.wireOp",EDGE,"fcba4419-a2ee-464f-be9d-58f11bf3418b.sketch_text.stroke-17"),sQuery(id+"FQ5JFwxVdaqARUP_1.wireOp",EDGE,"fcba4419-a2ee-464f-be9d-58f11bf3418b.sketch_text.stroke-18"),sQuery(id+"FQ5JFwxVdaqARUP_1.wireOp",EDGE,"fcba4419-a2ee-464f-be9d-58f11bf3418b.sketch_text.stroke-19"),sQuery(id+"FQ5JFwxVdaqARUP_1.wireOp",EDGE,"fcba4419-a2ee-464f-be9d-58f11bf3418b.sketch_text.stroke-20"),sQuery(id+"FQ5JFwxVdaqARUP_1.wireOp",EDGE,"fcba4419-a2ee-464f-be9d-58f11bf3418b.sketch_text.stroke-21"),sQuery(id+"FQ5JFwxVdaqARUP_1.wireOp",EDGE,"fcba4419-a2ee-464f-be9d-58f11bf3418b.sketch_text.stroke-22"),sQuery(id+"FQ5JFwxVdaqARUP_1.wireOp",EDGE,"fcba4419-a2ee-464f-be9d-58f11bf3418b.sketch_text.stroke-23"),sQuery(id+"FQ5JFwxVdaqARUP_1.wireOp",EDGE,"fcba4419-a2ee-464f-be9d-58f11bf3418b.sketch_text.stroke-24"),sQuery(id+"FQ5JFwxVdaqARUP_1.wireOp",EDGE,"fcba4419-a2ee-464f-be9d-58f11bf3418b.sketch_text.stroke-25"),sQuery(id+"FQ5JFwxVdaqARUP_1.wireOp",EDGE,"fcba4419-a2ee-464f-be9d-58f11bf3418b.sketch_text.stroke-26"),sQuery(id+"FQ5JFwxVdaqARUP_1.wireOp",EDGE,"fcba4419-a2ee-464f-be9d-58f11bf3418b.sketch_text.stroke-27"),sQuery(id+"FQ5JFwxVdaqARUP_1.wireOp",EDGE,"fcba4419-a2ee-464f-be9d-58f11bf3418b.sketch_text.stroke-28"),sQuery(id+"FQ5JFwxVdaqARUP_1.wireOp",EDGE,"fcba4419-a2ee-464f-be9d-58f11bf3418b.sketch_text.stroke-29"),sQuery(id+"FQ5JFwxVdaqARUP_1.wireOp",EDGE,"fcba4419-a2ee-464f-be9d-58f11bf3418b.sketch_text.stroke-30"),sQuery(id+"FQ5JFwxVdaqARUP_1.wireOp",EDGE,"fcba4419-a2ee-464f-be9d-58f11bf3418b.sketch_text.stroke-31"),sQuery(id+"FQ5JFwxVdaqARUP_1.wireOp",EDGE,"fcba4419-a2ee-464f-be9d-58f11bf3418b.sketch_text.stroke-32"),sQuery(id+"FQ5JFwxVdaqARUP_1.wireOp",EDGE,"fcba4419-a2ee-464f-be9d-58f11bf3418b.sketch_text.stroke-33"),sQuery(id+"FQ5JFwxVdaqARUP_1.wireOp",EDGE,"fcba4419-a2ee-464f-be9d-58f11bf3418b.sketch_text.stroke-34"),sQuery(id+"FQ5JFwxVdaqARUP_1.wireOp",EDGE,"fcba4419-a2ee-464f-be9d-58f11bf3418b.sketch_text.stroke-35"),sQuery(id+"FQ5JFwxVdaqARUP_1.wireOp",EDGE,"fcba4419-a2ee-464f-be9d-58f11bf3418b.sketch_text.stroke-36"),sQuery(id+"FQ5JFwxVdaqARUP_1.wireOp",EDGE,"fcba4419-a2ee-464f-be9d-58f11bf3418b.sketch_text.stroke-37"),sQuery(id+"FQ5JFwxVdaqARUP_1.wireOp",EDGE,"fcba4419-a2ee-464f-be9d-58f11bf3418b.sketch_text.stroke-38"),sQuery(id+"FQ5JFwxVdaqARUP_1.wireOp",EDGE,"fcba4419-a2ee-464f-be9d-58f11bf3418b.sketch_text.stroke-39"),sQuery(id+"FQ5JFwxVdaqARUP_1.wireOp",EDGE,"fcba4419-a2ee-464f-be9d-58f11bf3418b.sketch_text.stroke-40"),sQuery(id+"FQ5JFwxVdaqARUP_1.wireOp",EDGE,"fcba4419-a2ee-464f-be9d-58f11bf3418b.sketch_text.stroke-41"),sQuery(id+"FQ5JFwxVdaqARUP_1.wireOp",EDGE,"fcba4419-a2ee-464f-be9d-58f11bf3418b.sketch_text.stroke-42"),sQuery(id+"FQ5JFwxVdaqARUP_1.wireOp",EDGE,"fcba4419-a2ee-464f-be9d-58f11bf3418b.sketch_text.stroke-43"),sQuery(id+"FQ5JFwxVdaqARUP_1.wireOp",EDGE,"fcba4419-a2ee-464f-be9d-58f11bf3418b.sketch_text.stroke-44"),sQuery(id+"FQ5JFwxVdaqARUP_1.wireOp",EDGE,"fcba4419-a2ee-464f-be9d-58f11bf3418b.sketch_text.stroke-45"),sQuery(id+"FQ5JFwxVdaqARUP_1.wireOp",EDGE,"fcba4419-a2ee-464f-be9d-58f11bf3418b.sketch_text.stroke-46"),sQuery(id+"FQ5JFwxVdaqARUP_1.wireOp",EDGE,"fcba4419-a2ee-464f-be9d-58f11bf3418b.sketch_text.stroke-47"),sQuery(id+"FQ5JFwxVdaqARUP_1.wireOp",EDGE,"fcba4419-a2ee-464f-be9d-58f11bf3418b.sketch_text.stroke-48"),sQuery(id+"FQ5JFwxVdaqARUP_1.wireOp",EDGE,"fcba4419-a2ee-464f-be9d-58f11bf3418b.sketch_text.stroke-49"),sQuery(id+"FQ5JFwxVdaqARUP_1.wireOp",EDGE,"fcba4419-a2ee-464f-be9d-58f11bf3418b.sketch_text.stroke-50"),sQuery(id+"FQ5JFwxVdaqARUP_1.wireOp",EDGE,"fcba4419-a2ee-464f-be9d-58f11bf3418b.sketch_text.stroke-51"),sQuery(id+"FQ5JFwxVdaqARUP_1.wireOp",EDGE,"fcba4419-a2ee-464f-be9d-58f11bf3418b.sketch_text.stroke-52"),sQuery(id+"FQ5JFwxVdaqARUP_1.wireOp",EDGE,"fcba4419-a2ee-464f-be9d-58f11bf3418b.sketch_text.stroke-53"),sQuery(id+"FQ5JFwxVdaqARUP_1.wireOp",EDGE,"fcba4419-a2ee-464f-be9d-58f11bf3418b.sketch_text.stroke-54"),sQuery(id+"FQ5JFwxVdaqARUP_1.wireOp",EDGE,"fcba4419-a2ee-464f-be9d-58f11bf3418b.sketch_text.stroke-55"),sQuery(id+"FQ5JFwxVdaqARUP_1.wireOp",EDGE,"fcba4419-a2ee-464f-be9d-58f11bf3418b.sketch_text.stroke-56"),sQuery(id+"FQ5JFwxVdaqARUP_1.wireOp",EDGE,"fcba4419-a2ee-464f-be9d-58f11bf3418b.sketch_text.stroke-57"),sQuery(id+"FQ5JFwxVdaqARUP_1.wireOp",EDGE,"fcba4419-a2ee-464f-be9d-58f11bf3418b.sketch_text.stroke-58"),sQuery(id+"FQ5JFwxVdaqARUP_1.wireOp",EDGE,"fcba4419-a2ee-464f-be9d-58f11bf3418b.sketch_text.stroke-59"),sQuery(id+"FQ5JFwxVdaqARUP_1.wireOp",EDGE,"fcba4419-a2ee-464f-be9d-58f11bf3418b.sketch_text.stroke-60"),sQuery(id+"FQ5JFwxVdaqARUP_1.wireOp",EDGE,"fcba4419-a2ee-464f-be9d-58f11bf3418b.sketch_text.stroke-61"),sQuery(id+"FQ5JFwxVdaqARUP_1.wireOp",EDGE,"fcba4419-a2ee-464f-be9d-58f11bf3418b.sketch_text.stroke-62"),sQuery(id+"FQ5JFwxVdaqARUP_1.wireOp",EDGE,"fcba4419-a2ee-464f-be9d-58f11bf3418b.sketch_text.stroke-63"),sQuery(id+"FQ5JFwxVdaqARUP_1.wireOp",EDGE,"fcba4419-a2ee-464f-be9d-58f11bf3418b.sketch_text.stroke-64"),sQuery(id+"FQ5JFwxVdaqARUP_1.wireOp",EDGE,"fcba4419-a2ee-464f-be9d-58f11bf3418b.sketch_text.stroke-65"),sQuery(id+"FQ5JFwxVdaqARUP_1.wireOp",EDGE,"fcba4419-a2ee-464f-be9d-58f11bf3418b.sketch_text.stroke-66"),sQuery(id+"FQ5JFwxVdaqARUP_1.wireOp",EDGE,"fcba4419-a2ee-464f-be9d-58f11bf3418b.sketch_text.stroke-67"),sQuery(id+"FQ5JFwxVdaqARUP_1.wireOp",EDGE,"fcba4419-a2ee-464f-be9d-58f11bf3418b.sketch_text.stroke-68"),sQuery(id+"FQ5JFwxVdaqARUP_1.wireOp",EDGE,"fcba4419-a2ee-464f-be9d-58f11bf3418b.sketch_text.stroke-69"),sQuery(id+"FQ5JFwxVdaqARUP_1.wireOp",EDGE,"fcba4419-a2ee-464f-be9d-58f11bf3418b.sketch_text.stroke-70"),sQuery(id+"FQ5JFwxVdaqARUP_1.wireOp",EDGE,"fcba4419-a2ee-464f-be9d-58f11bf3418b.sketch_text.stroke-71"),sQuery(id+"FQ5JFwxVdaqARUP_1.wireOp",EDGE,"fcba4419-a2ee-464f-be9d-58f11bf3418b.sketch_text.stroke-72"),sQuery(id+"FQ5JFwxVdaqARUP_1.wireOp",EDGE,"fcba4419-a2ee-464f-be9d-58f11bf3418b.sketch_text.stroke-73"),sQuery(id+"FQ5JFwxVdaqARUP_1.wireOp",EDGE,"fcba4419-a2ee-464f-be9d-58f11bf3418b.sketch_text.stroke-74"),sQuery(id+"FQ5JFwxVdaqARUP_1.wireOp",EDGE,"fcba4419-a2ee-464f-be9d-58f11bf3418b.sketch_text.stroke-75"),sQuery(id+"FQ5JFwxVdaqARUP_1.wireOp",EDGE,"fcba4419-a2ee-464f-be9d-58f11bf3418b.sketch_text.stroke-76"),sQuery(id+"FQ5JFwxVdaqARUP_1.wireOp",EDGE,"fcba4419-a2ee-464f-be9d-58f11bf3418b.sketch_text.stroke-77"),sQuery(id+"FQ5JFwxVdaqARUP_1.wireOp",EDGE,"fcba4419-a2ee-464f-be9d-58f11bf3418b.sketch_text.stroke-78"),sQuery(id+"FQ5JFwxVdaqARUP_1.wireOp",EDGE,"fcba4419-a2ee-464f-be9d-58f11bf3418b.sketch_text.stroke-79"),sQuery(id+"FQ5JFwxVdaqARUP_1.wireOp",EDGE,"fcba4419-a2ee-464f-be9d-58f11bf3418b.sketch_text.stroke-80"),sQuery(id+"FQ5JFwxVdaqARUP_1.wireOp",EDGE,"fcba4419-a2ee-464f-be9d-58f11bf3418b.sketch_text.stroke-81"),sQuery(id+"FQ5JFwxVdaqARUP_1.wireOp",EDGE,"fcba4419-a2ee-464f-be9d-58f11bf3418b.sketch_text.stroke-82"),sQuery(id+"FQ5JFwxVdaqARUP_1.wireOp",EDGE,"fcba4419-a2ee-464f-be9d-58f11bf3418b.sketch_text.stroke-83"),sQuery(id+"FQ5JFwxVdaqARUP_1.wireOp",EDGE,"fcba4419-a2ee-464f-be9d-58f11bf3418b.sketch_text.stroke-84"),sQuery(id+"FQ5JFwxVdaqARUP_1.wireOp",EDGE,"fcba4419-a2ee-464f-be9d-58f11bf3418b.sketch_text.stroke-85"),sQuery(id+"FQ5JFwxVdaqARUP_1.wireOp",EDGE,"fcba4419-a2ee-464f-be9d-58f11bf3418b.sketch_text.stroke-86"),sQuery(id+"FQ5JFwxVdaqARUP_1.wireOp",EDGE,"fcba4419-a2ee-464f-be9d-58f11bf3418b.sketch_text.stroke-87"),sQuery(id+"FQ5JFwxVdaqARUP_1.wireOp",EDGE,"fcba4419-a2ee-464f-be9d-58f11bf3418b.sketch_text.stroke-88"),sQuery(id+"FQ5JFwxVdaqARUP_1.wireOp",EDGE,"fcba4419-a2ee-464f-be9d-58f11bf3418b.sketch_text.stroke-89"),sQuery(id+"FQ5JFwxVdaqARUP_1.wireOp",EDGE,"fcba4419-a2ee-464f-be9d-58f11bf3418b.sketch_text.stroke-90"),sQuery(id+"FQ5JFwxVdaqARUP_1.wireOp",EDGE,"fcba4419-a2ee-464f-be9d-58f11bf3418b.sketch_text.stroke-91"),sQuery(id+"FQ5JFwxVdaqARUP_1.wireOp",EDGE,"fcba4419-a2ee-464f-be9d-58f11bf3418b.sketch_text.stroke-92"),sQuery(id+"FQ5JFwxVdaqARUP_1.wireOp",EDGE,"fcba4419-a2ee-464f-be9d-58f11bf3418b.sketch_text.stroke-93"),sQuery(id+"FQ5JFwxVdaqARUP_1.wireOp",EDGE,"fcba4419-a2ee-464f-be9d-58f11bf3418b.sketch_text.stroke-94"),sQuery(id+"FQ5JFwxVdaqARUP_1.wireOp",EDGE,"fcba4419-a2ee-464f-be9d-58f11bf3418b.sketch_text.stroke-95"),sQuery(id+"FQ5JFwxVdaqARUP_1.wireOp",EDGE,"fcba4419-a2ee-464f-be9d-58f11bf3418b.sketch_text.stroke-96"),sQuery(id+"FQ5JFwxVdaqARUP_1.wireOp",EDGE,"fcba4419-a2ee-464f-be9d-58f11bf3418b.sketch_text.stroke-97"),sQuery(id+"FQ5JFwxVdaqARUP_1.wireOp",EDGE,"fcba4419-a2ee-464f-be9d-58f11bf3418b.sketch_text.stroke-98"),sQuery(id+"FQ5JFwxVdaqARUP_1.wireOp",EDGE,"fcba4419-a2ee-464f-be9d-58f11bf3418b.sketch_text.stroke-99"),sQuery(id+"FQ5JFwxVdaqARUP_1.wireOp",EDGE,"fcba4419-a2ee-464f-be9d-58f11bf3418b.sketch_text.stroke-100"),sQuery(id+"FQ5JFwxVdaqARUP_1.wireOp",EDGE,"fcba4419-a2ee-464f-be9d-58f11bf3418b.sketch_text.stroke-101"),sQuery(id+"FQ5JFwxVdaqARUP_1.wireOp",EDGE,"fcba4419-a2ee-464f-be9d-58f11bf3418b.sketch_text.stroke-102"),sQuery(id+"FQ5JFwxVdaqARUP_1.wireOp",EDGE,"fcba4419-a2ee-464f-be9d-58f11bf3418b.sketch_text.stroke-103"),sQuery(id+"FQ5JFwxVdaqARUP_1.wireOp",EDGE,"fcba4419-a2ee-464f-be9d-58f11bf3418b.sketch_text.stroke-104"),sQuery(id+"FQ5JFwxVdaqARUP_1.wireOp",EDGE,"fcba4419-a2ee-464f-be9d-58f11bf3418b.sketch_text.stroke-105"),sQuery(id+"FQ5JFwxVdaqARUP_1.wireOp",EDGE,"fcba4419-a2ee-464f-be9d-58f11bf3418b.sketch_text.stroke-106"),sQuery(id+"FQ5JFwxVdaqARUP_1.wireOp",EDGE,"fcba4419-a2ee-464f-be9d-58f11bf3418b.sketch_text.stroke-107"),sQuery(id+"FQ5JFwxVdaqARUP_1.wireOp",EDGE,"fcba4419-a2ee-464f-be9d-58f11bf3418b.sketch_text.stroke-108"),sQuery(id+"FQ5JFwxVdaqARUP_1.wireOp",EDGE,"fcba4419-a2ee-464f-be9d-58f11bf3418b.sketch_text.stroke-109"),sQuery(id+"FQ5JFwxVdaqARUP_1.wireOp",EDGE,"fcba4419-a2ee-464f-be9d-58f11bf3418b.sketch_text.stroke-110"),sQuery(id+"FQ5JFwxVdaqARUP_1.wireOp",EDGE,"fcba4419-a2ee-464f-be9d-58f11bf3418b.sketch_text.stroke-111"),sQuery(id+"FQ5JFwxVdaqARUP_1.wireOp",EDGE,"fcba4419-a2ee-464f-be9d-58f11bf3418b.sketch_text.stroke-112"),sQuery(id+"FQ5JFwxVdaqARUP_1.wireOp",EDGE,"fcba4419-a2ee-464f-be9d-58f11bf3418b.sketch_text.stroke-113"),sQuery(id+"FQ5JFwxVdaqARUP_1.wireOp",EDGE,"fcba4419-a2ee-464f-be9d-58f11bf3418b.sketch_text.stroke-114"),sQuery(id+"FQ5JFwxVdaqARUP_1.wireOp",EDGE,"fcba4419-a2ee-464f-be9d-58f11bf3418b.sketch_text.stroke-115"),sQuery(id+"FQ5JFwxVdaqARUP_1.wireOp",EDGE,"fcba4419-a2ee-464f-be9d-58f11bf3418b.sketch_text.stroke-116"),sQuery(id+"FQ5JFwxVdaqARUP_1.wireOp",EDGE,"fcba4419-a2ee-464f-be9d-58f11bf3418b.sketch_text.stroke-117"),sQuery(id+"FQ5JFwxVdaqARUP_1.wireOp",EDGE,"fcba4419-a2ee-464f-be9d-58f11bf3418b.sketch_text.stroke-118"),sQuery(id+"FQ5JFwxVdaqARUP_1.wireOp",EDGE,"fcba4419-a2ee-464f-be9d-58f11bf3418b.sketch_text.stroke-119"),sQuery(id+"FQ5JFwxVdaqARUP_1.wireOp",EDGE,"fcba4419-a2ee-464f-be9d-58f11bf3418b.sketch_text.stroke-120"),sQuery(id+"FQ5JFwxVdaqARUP_1.wireOp",EDGE,"fcba4419-a2ee-464f-be9d-58f11bf3418b.sketch_text.stroke-121"),sQuery(id+"FQ5JFwxVdaqARUP_1.wireOp",EDGE,"fcba4419-a2ee-464f-be9d-58f11bf3418b.sketch_text.stroke-122"),sQuery(id+"FQ5JFwxVdaqARUP_1.wireOp",EDGE,"fcba4419-a2ee-464f-be9d-58f11bf3418b.sketch_text.stroke-123"),sQuery(id+"FQ5JFwxVdaqARUP_1.wireOp",EDGE,"fcba4419-a2ee-464f-be9d-58f11bf3418b.sketch_text.stroke-124"),sQuery(id+"FQ5JFwxVdaqARUP_1.wireOp",EDGE,"fcba4419-a2ee-464f-be9d-58f11bf3418b.sketch_text.stroke-125"),sQuery(id+"FQ5JFwxVdaqARUP_1.wireOp",EDGE,"fcba4419-a2ee-464f-be9d-58f11bf3418b.sketch_text.stroke-126"),sQuery(id+"FQ5JFwxVdaqARUP_1.wireOp",EDGE,"fcba4419-a2ee-464f-be9d-58f11bf3418b.sketch_text.stroke-127"),sQuery(id+"FQ5JFwxVdaqARUP_1.wireOp",EDGE,"fcba4419-a2ee-464f-be9d-58f11bf3418b.sketch_text.stroke-128"),sQuery(id+"FQ5JFwxVdaqARUP_1.wireOp",EDGE,"fcba4419-a2ee-464f-be9d-58f11bf3418b.sketch_text.stroke-129"),sQuery(id+"FQ5JFwxVdaqARUP_1.wireOp",EDGE,"fcba4419-a2ee-464f-be9d-58f11bf3418b.sketch_text.stroke-130"),sQuery(id+"FQ5JFwxVdaqARUP_1.wireOp",EDGE,"fcba4419-a2ee-464f-be9d-58f11bf3418b.sketch_text.stroke-131"),sQuery(id+"FQ5JFwxVdaqARUP_1.wireOp",EDGE,"fcba4419-a2ee-464f-be9d-58f11bf3418b.sketch_text.stroke-132"),sQuery(id+"FQ5JFwxVdaqARUP_1.wireOp",EDGE,"fcba4419-a2ee-464f-be9d-58f11bf3418b.sketch_text.stroke-133"),sQuery(id+"FQ5JFwxVdaqARUP_1.wireOp",EDGE,"fcba4419-a2ee-464f-be9d-58f11bf3418b.sketch_text.stroke-134"),sQuery(id+"FQ5JFwxVdaqARUP_1.wireOp",EDGE,"fcba4419-a2ee-464f-be9d-58f11bf3418b.sketch_text.stroke-135"),sQuery(id+"FQ5JFwxVdaqARUP_1.wireOp",EDGE,"fcba4419-a2ee-464f-be9d-58f11bf3418b.sketch_text.stroke-136"),sQuery(id+"FQ5JFwxVdaqARUP_1.wireOp",EDGE,"fcba4419-a2ee-464f-be9d-58f11bf3418b.sketch_text.stroke-137"),sQuery(id+"FQ5JFwxVdaqARUP_1.wireOp",EDGE,"fcba4419-a2ee-464f-be9d-58f11bf3418b.sketch_text.stroke-138"),sQuery(id+"FQ5JFwxVdaqARUP_1.wireOp",EDGE,"fcba4419-a2ee-464f-be9d-58f11bf3418b.sketch_text.stroke-139"),sQuery(id+"FQ5JFwxVdaqARUP_1.wireOp",EDGE,"fcba4419-a2ee-464f-be9d-58f11bf3418b.sketch_text.stroke-140"),sQuery(id+"FQ5JFwxVdaqARUP_1.wireOp",EDGE,"fcba4419-a2ee-464f-be9d-58f11bf3418b.sketch_text.stroke-141"),sQuery(id+"FQ5JFwxVdaqARUP_1.wireOp",EDGE,"fcba4419-a2ee-464f-be9d-58f11bf3418b.sketch_text.stroke-142"),sQuery(id+"FQ5JFwxVdaqARUP_1.wireOp",EDGE,"fcba4419-a2ee-464f-be9d-58f11bf3418b.sketch_text.stroke-143"),sQuery(id+"FQ5JFwxVdaqARUP_1.wireOp",EDGE,"fcba4419-a2ee-464f-be9d-58f11bf3418b.sketch_text.stroke-144"),sQuery(id+"FQ5JFwxVdaqARUP_1.wireOp",EDGE,"fcba4419-a2ee-464f-be9d-58f11bf3418b.sketch_text.stroke-145"),sQuery(id+"FQ5JFwxVdaqARUP_1.wireOp",EDGE,"fcba4419-a2ee-464f-be9d-58f11bf3418b.sketch_text.stroke-146"),sQuery(id+"FQ5JFwxVdaqARUP_1.wireOp",EDGE,"fcba4419-a2ee-464f-be9d-58f11bf3418b.sketch_text.stroke-147"),sQuery(id+"FQ5JFwxVdaqARUP_1.wireOp",EDGE,"fcba4419-a2ee-464f-be9d-58f11bf3418b.sketch_text.stroke-148"),sQuery(id+"FQ5JFwxVdaqARUP_1.wireOp",EDGE,"fcba4419-a2ee-464f-be9d-58f11bf3418b.sketch_text.stroke-149"),sQuery(id+"FQ5JFwxVdaqARUP_1.wireOp",EDGE,"fcba4419-a2ee-464f-be9d-58f11bf3418b.sketch_text.stroke-150"),sQuery(id+"FQ5JFwxVdaqARUP_1.wireOp",EDGE,"fcba4419-a2ee-464f-be9d-58f11bf3418b.sketch_text.stroke-151"),sQuery(id+"FQ5JFwxVdaqARUP_1.wireOp",EDGE,"fcba4419-a2ee-464f-be9d-58f11bf3418b.sketch_text.stroke-152"),sQuery(id+"FQ5JFwxVdaqARUP_1.wireOp",EDGE,"fcba4419-a2ee-464f-be9d-58f11bf3418b.sketch_text.stroke-153"),sQuery(id+"FQ5JFwxVdaqARUP_1.wireOp",EDGE,"fcba4419-a2ee-464f-be9d-58f11bf3418b.sketch_text.stroke-154"),sQuery(id+"FQ5JFwxVdaqARUP_1.wireOp",EDGE,"fcba4419-a2ee-464f-be9d-58f11bf3418b.sketch_text.stroke-155"),sQuery(id+"FQ5JFwxVdaqARUP_1.wireOp",EDGE,"fcba4419-a2ee-464f-be9d-58f11bf3418b.sketch_text.stroke-156"),sQuery(id+"FQ5JFwxVdaqARUP_1.wireOp",EDGE,"fcba4419-a2ee-464f-be9d-58f11bf3418b.sketch_text.stroke-157"),sQuery(id+"FQ5JFwxVdaqARUP_1.wireOp",EDGE,"fcba4419-a2ee-464f-be9d-58f11bf3418b.sketch_text.stroke-158"),sQuery(id+"FQ5JFwxVdaqARUP_1.wireOp",EDGE,"fcba4419-a2ee-464f-be9d-58f11bf3418b.sketch_text.stroke-159"),sQuery(id+"FQ5JFwxVdaqARUP_1.wireOp",EDGE,"fcba4419-a2ee-464f-be9d-58f11bf3418b.sketch_text.stroke-160"),sQuery(id+"FQ5JFwxVdaqARUP_1.wireOp",EDGE,"fcba4419-a2ee-464f-be9d-58f11bf3418b.sketch_text.stroke-161"),sQuery(id+"FQ5JFwxVdaqARUP_1.wireOp",EDGE,"fcba4419-a2ee-464f-be9d-58f11bf3418b.sketch_text.stroke-162"),sQuery(id+"FQ5JFwxVdaqARUP_1.wireOp",EDGE,"fcba4419-a2ee-464f-be9d-58f11bf3418b.sketch_text.stroke-163"),sQuery(id+"FQ5JFwxVdaqARUP_1.wireOp",EDGE,"fcba4419-a2ee-464f-be9d-58f11bf3418b.sketch_text.stroke-164"),sQuery(id+"FQ5JFwxVdaqARUP_1.wireOp",EDGE,"fcba4419-a2ee-464f-be9d-58f11bf3418b.sketch_text.stroke-165"),sQuery(id+"FQ5JFwxVdaqARUP_1.wireOp",EDGE,"fcba4419-a2ee-464f-be9d-58f11bf3418b.sketch_text.stroke-166"),sQuery(id+"FQ5JFwxVdaqARUP_1.wireOp",EDGE,"fcba4419-a2ee-464f-be9d-58f11bf3418b.sketch_text.stroke-167"),sQuery(id+"FQ5JFwxVdaqARUP_1.wireOp",EDGE,"fcba4419-a2ee-464f-be9d-58f11bf3418b.sketch_text.stroke-168"),sQuery(id+"FQ5JFwxVdaqARUP_1.wireOp",EDGE,"fcba4419-a2ee-464f-be9d-58f11bf3418b.sketch_text.stroke-169"),sQuery(id+"FQ5JFwxVdaqARUP_1.wireOp",EDGE,"fcba4419-a2ee-464f-be9d-58f11bf3418b.sketch_text.stroke-170"),sQuery(id+"FQ5JFwxVdaqARUP_1.wireOp",EDGE,"fcba4419-a2ee-464f-be9d-58f11bf3418b.sketch_text.stroke-171"),sQuery(id+"FQ5JFwxVdaqARUP_1.wireOp",EDGE,"fcba4419-a2ee-464f-be9d-58f11bf3418b.sketch_text.stroke-172"),sQuery(id+"FQ5JFwxVdaqARUP_1.wireOp",EDGE,"fcba4419-a2ee-464f-be9d-58f11bf3418b.sketch_text.stroke-173"),sQuery(id+"FHMxAyK4CFUKdhS_1.wireOp",EDGE,"1cb9c079-ea9b-4899-8069-e0e3048e911d.sketch_text.stroke-0"),sQuery(id+"FHMxAyK4CFUKdhS_1.wireOp",EDGE,"1cb9c079-ea9b-4899-8069-e0e3048e911d.sketch_text.stroke-1"),sQuery(id+"FHMxAyK4CFUKdhS_1.wireOp",EDGE,"1cb9c079-ea9b-4899-8069-e0e3048e911d.sketch_text.stroke-2"),sQuery(id+"FHMxAyK4CFUKdhS_1.wireOp",EDGE,"1cb9c079-ea9b-4899-8069-e0e3048e911d.sketch_text.stroke-3"),sQuery(id+"FHMxAyK4CFUKdhS_1.wireOp",EDGE,"1cb9c079-ea9b-4899-8069-e0e3048e911d.sketch_text.stroke-4"),sQuery(id+"FHMxAyK4CFUKdhS_1.wireOp",EDGE,"1cb9c079-ea9b-4899-8069-e0e3048e911d.sketch_text.stroke-5"),sQuery(id+"FHMxAyK4CFUKdhS_1.wireOp",EDGE,"1cb9c079-ea9b-4899-8069-e0e3048e911d.sketch_text.stroke-6"),sQuery(id+"FHMxAyK4CFUKdhS_1.wireOp",EDGE,"1cb9c079-ea9b-4899-8069-e0e3048e911d.sketch_text.stroke-7"),sQuery(id+"FHMxAyK4CFUKdhS_1.wireOp",EDGE,"1cb9c079-ea9b-4899-8069-e0e3048e911d.sketch_text.stroke-8"),sQuery(id+"FHMxAyK4CFUKdhS_1.wireOp",EDGE,"1cb9c079-ea9b-4899-8069-e0e3048e911d.sketch_text.stroke-9"),sQuery(id+"FHMxAyK4CFUKdhS_1.wireOp",EDGE,"1cb9c079-ea9b-4899-8069-e0e3048e911d.sketch_text.stroke-10"),sQuery(id+"FHMxAyK4CFUKdhS_1.wireOp",EDGE,"1cb9c079-ea9b-4899-8069-e0e3048e911d.sketch_text.stroke-11"),sQuery(id+"FHMxAyK4CFUKdhS_1.wireOp",EDGE,"1cb9c079-ea9b-4899-8069-e0e3048e911d.sketch_text.stroke-12"),sQuery(id+"FHMxAyK4CFUKdhS_1.wireOp",EDGE,"1cb9c079-ea9b-4899-8069-e0e3048e911d.sketch_text.stroke-13"),sQuery(id+"FHMxAyK4CFUKdhS_1.wireOp",EDGE,"1cb9c079-ea9b-4899-8069-e0e3048e911d.sketch_text.stroke-14"),sQuery(id+"FHMxAyK4CFUKdhS_1.wireOp",EDGE,"1cb9c079-ea9b-4899-8069-e0e3048e911d.sketch_text.stroke-15"),sQuery(id+"FHMxAyK4CFUKdhS_1.wireOp",EDGE,"1cb9c079-ea9b-4899-8069-e0e3048e911d.sketch_text.stroke-16"),sQuery(id+"FHMxAyK4CFUKdhS_1.wireOp",EDGE,"1cb9c079-ea9b-4899-8069-e0e3048e911d.sketch_text.stroke-17"),sQuery(id+"FHMxAyK4CFUKdhS_1.wireOp",EDGE,"1cb9c079-ea9b-4899-8069-e0e3048e911d.sketch_text.stroke-18"),sQuery(id+"FHMxAyK4CFUKdhS_1.wireOp",EDGE,"1cb9c079-ea9b-4899-8069-e0e3048e911d.sketch_text.stroke-19"),sQuery(id+"FHMxAyK4CFUKdhS_1.wireOp",EDGE,"1cb9c079-ea9b-4899-8069-e0e3048e911d.sketch_text.stroke-20"),sQuery(id+"FHMxAyK4CFUKdhS_1.wireOp",EDGE,"1cb9c079-ea9b-4899-8069-e0e3048e911d.sketch_text.stroke-21"),sQuery(id+"FHMxAyK4CFUKdhS_1.wireOp",EDGE,"1cb9c079-ea9b-4899-8069-e0e3048e911d.sketch_text.stroke-22"),sQuery(id+"FHMxAyK4CFUKdhS_1.wireOp",EDGE,"1cb9c079-ea9b-4899-8069-e0e3048e911d.sketch_text.stroke-23"),sQuery(id+"FHMxAyK4CFUKdhS_1.wireOp",EDGE,"1cb9c079-ea9b-4899-8069-e0e3048e911d.sketch_text.stroke-24"),sQuery(id+"FHMxAyK4CFUKdhS_1.wireOp",EDGE,"1cb9c079-ea9b-4899-8069-e0e3048e911d.sketch_text.stroke-25"),sQuery(id+"FHMxAyK4CFUKdhS_1.wireOp",EDGE,"1cb9c079-ea9b-4899-8069-e0e3048e911d.sketch_text.stroke-26"),sQuery(id+"FHMxAyK4CFUKdhS_1.wireOp",EDGE,"1cb9c079-ea9b-4899-8069-e0e3048e911d.sketch_text.stroke-27"),sQuery(id+"FHMxAyK4CFUKdhS_1.wireOp",EDGE,"1cb9c079-ea9b-4899-8069-e0e3048e911d.sketch_text.stroke-28"),sQuery(id+"FHMxAyK4CFUKdhS_1.wireOp",EDGE,"1cb9c079-ea9b-4899-8069-e0e3048e911d.sketch_text.stroke-29"),sQuery(id+"FHMxAyK4CFUKdhS_1.wireOp",EDGE,"1cb9c079-ea9b-4899-8069-e0e3048e911d.sketch_text.stroke-30"),sQuery(id+"FHMxAyK4CFUKdhS_1.wireOp",EDGE,"1cb9c079-ea9b-4899-8069-e0e3048e911d.sketch_text.stroke-31"),sQuery(id+"FHMxAyK4CFUKdhS_1.wireOp",EDGE,"1cb9c079-ea9b-4899-8069-e0e3048e911d.sketch_text.stroke-32"),sQuery(id+"FHMxAyK4CFUKdhS_1.wireOp",EDGE,"1cb9c079-ea9b-4899-8069-e0e3048e911d.sketch_text.stroke-33"),sQuery(id+"FHMxAyK4CFUKdhS_1.wireOp",EDGE,"1cb9c079-ea9b-4899-8069-e0e3048e911d.sketch_text.stroke-34"),sQuery(id+"FHMxAyK4CFUKdhS_1.wireOp",EDGE,"1cb9c079-ea9b-4899-8069-e0e3048e911d.sketch_text.stroke-35"),sQuery(id+"FHMxAyK4CFUKdhS_1.wireOp",EDGE,"1cb9c079-ea9b-4899-8069-e0e3048e911d.sketch_text.stroke-36"),sQuery(id+"FHMxAyK4CFUKdhS_1.wireOp",EDGE,"1cb9c079-ea9b-4899-8069-e0e3048e911d.sketch_text.stroke-37"),sQuery(id+"FHMxAyK4CFUKdhS_1.wireOp",EDGE,"1cb9c079-ea9b-4899-8069-e0e3048e911d.sketch_text.stroke-38"),sQuery(id+"FHMxAyK4CFUKdhS_1.wireOp",EDGE,"1cb9c079-ea9b-4899-8069-e0e3048e911d.sketch_text.stroke-39"),sQuery(id+"FHMxAyK4CFUKdhS_1.wireOp",EDGE,"1cb9c079-ea9b-4899-8069-e0e3048e911d.sketch_text.stroke-40"),sQuery(id+"FHMxAyK4CFUKdhS_1.wireOp",EDGE,"1cb9c079-ea9b-4899-8069-e0e3048e911d.sketch_text.stroke-41"),sQuery(id+"FHMxAyK4CFUKdhS_1.wireOp",EDGE,"1cb9c079-ea9b-4899-8069-e0e3048e911d.sketch_text.stroke-42"),sQuery(id+"FHMxAyK4CFUKdhS_1.wireOp",EDGE,"1cb9c079-ea9b-4899-8069-e0e3048e911d.sketch_text.stroke-43"),sQuery(id+"FHMxAyK4CFUKdhS_1.wireOp",EDGE,"1cb9c079-ea9b-4899-8069-e0e3048e911d.sketch_text.stroke-44"),sQuery(id+"FHMxAyK4CFUKdhS_1.wireOp",EDGE,"1cb9c079-ea9b-4899-8069-e0e3048e911d.sketch_text.stroke-45"),sQuery(id+"FHMxAyK4CFUKdhS_1.wireOp",EDGE,"1cb9c079-ea9b-4899-8069-e0e3048e911d.sketch_text.stroke-46"),sQuery(id+"FHMxAyK4CFUKdhS_1.wireOp",EDGE,"1cb9c079-ea9b-4899-8069-e0e3048e911d.sketch_text.stroke-47"),sQuery(id+"FHMxAyK4CFUKdhS_1.wireOp",EDGE,"1cb9c079-ea9b-4899-8069-e0e3048e911d.sketch_text.stroke-48"),sQuery(id+"FHMxAyK4CFUKdhS_1.wireOp",EDGE,"1cb9c079-ea9b-4899-8069-e0e3048e911d.sketch_text.stroke-49"),sQuery(id+"FHMxAyK4CFUKdhS_1.wireOp",EDGE,"1cb9c079-ea9b-4899-8069-e0e3048e911d.sketch_text.stroke-50"),sQuery(id+"FHMxAyK4CFUKdhS_1.wireOp",EDGE,"1cb9c079-ea9b-4899-8069-e0e3048e911d.sketch_text.stroke-51"),sQuery(id+"FHMxAyK4CFUKdhS_1.wireOp",EDGE,"1cb9c079-ea9b-4899-8069-e0e3048e911d.sketch_text.stroke-52"),sQuery(id+"FHMxAyK4CFUKdhS_1.wireOp",EDGE,"1cb9c079-ea9b-4899-8069-e0e3048e911d.sketch_text.stroke-53"),sQuery(id+"FHMxAyK4CFUKdhS_1.wireOp",EDGE,"1cb9c079-ea9b-4899-8069-e0e3048e911d.sketch_text.stroke-54"),sQuery(id+"FHMxAyK4CFUKdhS_1.wireOp",EDGE,"1cb9c079-ea9b-4899-8069-e0e3048e911d.sketch_text.stroke-55"),sQuery(id+"FHMxAyK4CFUKdhS_1.wireOp",EDGE,"1cb9c079-ea9b-4899-8069-e0e3048e911d.sketch_text.stroke-56"),sQuery(id+"FHMxAyK4CFUKdhS_1.wireOp",EDGE,"1cb9c079-ea9b-4899-8069-e0e3048e911d.sketch_text.stroke-57"),sQuery(id+"FHMxAyK4CFUKdhS_1.wireOp",EDGE,"1cb9c079-ea9b-4899-8069-e0e3048e911d.sketch_text.stroke-58"),sQuery(id+"FHMxAyK4CFUKdhS_1.wireOp",EDGE,"1cb9c079-ea9b-4899-8069-e0e3048e911d.sketch_text.stroke-59"),sQuery(id+"FHMxAyK4CFUKdhS_1.wireOp",EDGE,"1cb9c079-ea9b-4899-8069-e0e3048e911d.sketch_text.stroke-60"),sQuery(id+"FHMxAyK4CFUKdhS_1.wireOp",EDGE,"1cb9c079-ea9b-4899-8069-e0e3048e911d.sketch_text.stroke-61"),sQuery(id+"FHMxAyK4CFUKdhS_1.wireOp",EDGE,"1cb9c079-ea9b-4899-8069-e0e3048e911d.sketch_text.stroke-62"),sQuery(id+"FHMxAyK4CFUKdhS_1.wireOp",EDGE,"1cb9c079-ea9b-4899-8069-e0e3048e911d.sketch_text.stroke-71"),sQuery(id+"FHMxAyK4CFUKdhS_1.wireOp",EDGE,"1cb9c079-ea9b-4899-8069-e0e3048e911d.sketch_text.stroke-72"),sQuery(id+"FHMxAyK4CFUKdhS_1.wireOp",EDGE,"1cb9c079-ea9b-4899-8069-e0e3048e911d.sketch_text.stroke-73"),sQuery(id+"FHMxAyK4CFUKdhS_1.wireOp",EDGE,"1cb9c079-ea9b-4899-8069-e0e3048e911d.sketch_text.stroke-74"),sQuery(id+"FHMxAyK4CFUKdhS_1.wireOp",EDGE,"1cb9c079-ea9b-4899-8069-e0e3048e911d.sketch_text.stroke-75"),sQuery(id+"FHMxAyK4CFUKdhS_1.wireOp",EDGE,"1cb9c079-ea9b-4899-8069-e0e3048e911d.sketch_text.stroke-76"),sQuery(id+"FHMxAyK4CFUKdhS_1.wireOp",EDGE,"1cb9c079-ea9b-4899-8069-e0e3048e911d.sketch_text.stroke-77"),sQuery(id+"FHMxAyK4CFUKdhS_1.wireOp",EDGE,"1cb9c079-ea9b-4899-8069-e0e3048e911d.sketch_text.stroke-78"),sQuery(id+"FHMxAyK4CFUKdhS_1.wireOp",EDGE,"1cb9c079-ea9b-4899-8069-e0e3048e911d.sketch_text.stroke-79"),sQuery(id+"FHMxAyK4CFUKdhS_1.wireOp",EDGE,"1cb9c079-ea9b-4899-8069-e0e3048e911d.sketch_text.stroke-80"),sQuery(id+"FHMxAyK4CFUKdhS_1.wireOp",EDGE,"1cb9c079-ea9b-4899-8069-e0e3048e911d.sketch_text.stroke-81"),sQuery(id+"FHMxAyK4CFUKdhS_1.wireOp",EDGE,"1cb9c079-ea9b-4899-8069-e0e3048e911d.sketch_text.stroke-82"),sQuery(id+"FHMxAyK4CFUKdhS_1.wireOp",EDGE,"1cb9c079-ea9b-4899-8069-e0e3048e911d.sketch_text.stroke-83"),sQuery(id+"FHMxAyK4CFUKdhS_1.wireOp",EDGE,"1cb9c079-ea9b-4899-8069-e0e3048e911d.sketch_text.stroke-84"),sQuery(id+"FHMxAyK4CFUKdhS_1.wireOp",EDGE,"1cb9c079-ea9b-4899-8069-e0e3048e911d.sketch_text.stroke-85"),sQuery(id+"FHMxAyK4CFUKdhS_1.wireOp",EDGE,"1cb9c079-ea9b-4899-8069-e0e3048e911d.sketch_text.stroke-86"),sQuery(id+"FHMxAyK4CFUKdhS_1.wireOp",EDGE,"1cb9c079-ea9b-4899-8069-e0e3048e911d.sketch_text.stroke-87"),sQuery(id+"FHMxAyK4CFUKdhS_1.wireOp",EDGE,"1cb9c079-ea9b-4899-8069-e0e3048e911d.sketch_text.stroke-88"),sQuery(id+"FHMxAyK4CFUKdhS_1.wireOp",EDGE,"1cb9c079-ea9b-4899-8069-e0e3048e911d.sketch_text.stroke-89"),sQuery(id+"FHMxAyK4CFUKdhS_1.wireOp",EDGE,"1cb9c079-ea9b-4899-8069-e0e3048e911d.sketch_text.stroke-90"),sQuery(id+"FHMxAyK4CFUKdhS_1.wireOp",EDGE,"1cb9c079-ea9b-4899-8069-e0e3048e911d.sketch_text.stroke-91"),sQuery(id+"FHMxAyK4CFUKdhS_1.wireOp",EDGE,"1cb9c079-ea9b-4899-8069-e0e3048e911d.sketch_text.stroke-92"),sQuery(id+"FHMxAyK4CFUKdhS_1.wireOp",EDGE,"1cb9c079-ea9b-4899-8069-e0e3048e911d.sketch_text.stroke-93"),sQuery(id+"FHMxAyK4CFUKdhS_1.wireOp",EDGE,"1cb9c079-ea9b-4899-8069-e0e3048e911d.sketch_text.stroke-94"),sQuery(id+"FHMxAyK4CFUKdhS_1.wireOp",EDGE,"1cb9c079-ea9b-4899-8069-e0e3048e911d.sketch_text.stroke-95"),sQuery(id+"FHMxAyK4CFUKdhS_1.wireOp",EDGE,"1cb9c079-ea9b-4899-8069-e0e3048e911d.sketch_text.stroke-96"),sQuery(id+"FHMxAyK4CFUKdhS_1.wireOp",EDGE,"1cb9c079-ea9b-4899-8069-e0e3048e911d.sketch_text.stroke-97"),sQuery(id+"FHMxAyK4CFUKdhS_1.wireOp",EDGE,"1cb9c079-ea9b-4899-8069-e0e3048e911d.sketch_text.stroke-103"),sQuery(id+"FHMxAyK4CFUKdhS_1.wireOp",EDGE,"1cb9c079-ea9b-4899-8069-e0e3048e911d.sketch_text.stroke-104"),sQuery(id+"FHMxAyK4CFUKdhS_1.wireOp",EDGE,"1cb9c079-ea9b-4899-8069-e0e3048e911d.sketch_text.stroke-105"),sQuery(id+"FHMxAyK4CFUKdhS_1.wireOp",EDGE,"1cb9c079-ea9b-4899-8069-e0e3048e911d.sketch_text.stroke-106"),sQuery(id+"FHMxAyK4CFUKdhS_1.wireOp",EDGE,"1cb9c079-ea9b-4899-8069-e0e3048e911d.sketch_text.stroke-107"),sQuery(id+"FHMxAyK4CFUKdhS_1.wireOp",EDGE,"1cb9c079-ea9b-4899-8069-e0e3048e911d.sketch_text.stroke-108"),sQuery(id+"FHMxAyK4CFUKdhS_1.wireOp",EDGE,"1cb9c079-ea9b-4899-8069-e0e3048e911d.sketch_text.stroke-109"),sQuery(id+"FHMxAyK4CFUKdhS_1.wireOp",EDGE,"1cb9c079-ea9b-4899-8069-e0e3048e911d.sketch_text.stroke-110"),sQuery(id+"FHMxAyK4CFUKdhS_1.wireOp",EDGE,"1cb9c079-ea9b-4899-8069-e0e3048e911d.sketch_text.stroke-111"),sQuery(id+"FHMxAyK4CFUKdhS_1.wireOp",EDGE,"1cb9c079-ea9b-4899-8069-e0e3048e911d.sketch_text.stroke-112"),sQuery(id+"FHMxAyK4CFUKdhS_1.wireOp",EDGE,"1cb9c079-ea9b-4899-8069-e0e3048e911d.sketch_text.stroke-113"),sQuery(id+"FHMxAyK4CFUKdhS_1.wireOp",EDGE,"1cb9c079-ea9b-4899-8069-e0e3048e911d.sketch_text.stroke-114"),sQuery(id+"FHMxAyK4CFUKdhS_1.wireOp",EDGE,"1cb9c079-ea9b-4899-8069-e0e3048e911d.sketch_text.stroke-115"),sQuery(id+"FHMxAyK4CFUKdhS_1.wireOp",EDGE,"1cb9c079-ea9b-4899-8069-e0e3048e911d.sketch_text.stroke-116"),sQuery(id+"FHMxAyK4CFUKdhS_1.wireOp",EDGE,"1cb9c079-ea9b-4899-8069-e0e3048e911d.sketch_text.stroke-117"),sQuery(id+"FHMxAyK4CFUKdhS_1.wireOp",EDGE,"1cb9c079-ea9b-4899-8069-e0e3048e911d.sketch_text.stroke-118"),sQuery(id+"FHMxAyK4CFUKdhS_1.wireOp",EDGE,"1cb9c079-ea9b-4899-8069-e0e3048e911d.sketch_text.stroke-119"),sQuery(id+"FHMxAyK4CFUKdhS_1.wireOp",EDGE,"1cb9c079-ea9b-4899-8069-e0e3048e911d.sketch_text.stroke-120"),sQuery(id+"FHMxAyK4CFUKdhS_1.wireOp",EDGE,"1cb9c079-ea9b-4899-8069-e0e3048e911d.sketch_text.stroke-121"),sQuery(id+"FHMxAyK4CFUKdhS_1.wireOp",EDGE,"1cb9c079-ea9b-4899-8069-e0e3048e911d.sketch_text.stroke-122"),sQuery(id+"FHMxAyK4CFUKdhS_1.wireOp",EDGE,"1cb9c079-ea9b-4899-8069-e0e3048e911d.sketch_text.stroke-123"),sQuery(id+"FHMxAyK4CFUKdhS_1.wireOp",EDGE,"1cb9c079-ea9b-4899-8069-e0e3048e911d.sketch_text.stroke-124"),sQuery(id+"FHMxAyK4CFUKdhS_1.wireOp",EDGE,"1cb9c079-ea9b-4899-8069-e0e3048e911d.sketch_text.stroke-125"),sQuery(id+"FHMxAyK4CFUKdhS_1.wireOp",EDGE,"1cb9c079-ea9b-4899-8069-e0e3048e911d.sketch_text.stroke-126"),sQuery(id+"FHMxAyK4CFUKdhS_1.wireOp",EDGE,"1cb9c079-ea9b-4899-8069-e0e3048e911d.sketch_text.stroke-127"),sQuery(id+"FHMxAyK4CFUKdhS_1.wireOp",EDGE,"1cb9c079-ea9b-4899-8069-e0e3048e911d.sketch_text.stroke-128"),sQuery(id+"FHMxAyK4CFUKdhS_1.wireOp",EDGE,"1cb9c079-ea9b-4899-8069-e0e3048e911d.sketch_text.stroke-129"),sQuery(id+"FHMxAyK4CFUKdhS_1.wireOp",EDGE,"1cb9c079-ea9b-4899-8069-e0e3048e911d.sketch_text.stroke-130"),sQuery(id+"FHMxAyK4CFUKdhS_1.wireOp",EDGE,"1cb9c079-ea9b-4899-8069-e0e3048e911d.sketch_text.stroke-131"),sQuery(id+"FHMxAyK4CFUKdhS_1.wireOp",EDGE,"1cb9c079-ea9b-4899-8069-e0e3048e911d.sketch_text.stroke-132"),sQuery(id+"FHMxAyK4CFUKdhS_1.wireOp",EDGE,"1cb9c079-ea9b-4899-8069-e0e3048e911d.sketch_text.stroke-133"),sQuery(id+"FHMxAyK4CFUKdhS_1.wireOp",EDGE,"1cb9c079-ea9b-4899-8069-e0e3048e911d.sketch_text.stroke-134"),sQuery(id+"FHMxAyK4CFUKdhS_1.wireOp",EDGE,"1cb9c079-ea9b-4899-8069-e0e3048e911d.sketch_text.stroke-135"),sQuery(id+"FHMxAyK4CFUKdhS_1.wireOp",EDGE,"1cb9c079-ea9b-4899-8069-e0e3048e911d.sketch_text.stroke-136"),sQuery(id+"FHMxAyK4CFUKdhS_1.wireOp",EDGE,"1cb9c079-ea9b-4899-8069-e0e3048e911d.sketch_text.stroke-137"),sQuery(id+"FHMxAyK4CFUKdhS_1.wireOp",EDGE,"1cb9c079-ea9b-4899-8069-e0e3048e911d.sketch_text.stroke-138"),sQuery(id+"FHMxAyK4CFUKdhS_1.wireOp",EDGE,"1cb9c079-ea9b-4899-8069-e0e3048e911d.sketch_text.stroke-139"),sQuery(id+"FHMxAyK4CFUKdhS_1.wireOp",EDGE,"1cb9c079-ea9b-4899-8069-e0e3048e911d.sketch_text.stroke-140"),sQuery(id+"FHMxAyK4CFUKdhS_1.wireOp",EDGE,"1cb9c079-ea9b-4899-8069-e0e3048e911d.sketch_text.stroke-141"),sQuery(id+"FHMxAyK4CFUKdhS_1.wireOp",EDGE,"1cb9c079-ea9b-4899-8069-e0e3048e911d.sketch_text.stroke-142"),sQuery(id+"FHMxAyK4CFUKdhS_1.wireOp",EDGE,"1cb9c079-ea9b-4899-8069-e0e3048e911d.sketch_text.stroke-143"),sQuery(id+"FHMxAyK4CFUKdhS_1.wireOp",EDGE,"1cb9c079-ea9b-4899-8069-e0e3048e911d.sketch_text.stroke-144"),sQuery(id+"FHMxAyK4CFUKdhS_1.wireOp",EDGE,"1cb9c079-ea9b-4899-8069-e0e3048e911d.sketch_text.stroke-145"),sQuery(id+"FHMxAyK4CFUKdhS_1.wireOp",EDGE,"1cb9c079-ea9b-4899-8069-e0e3048e911d.sketch_text.stroke-146"),sQuery(id+"FHMxAyK4CFUKdhS_1.wireOp",EDGE,"1cb9c079-ea9b-4899-8069-e0e3048e911d.sketch_text.stroke-147"),sQuery(id+"FHMxAyK4CFUKdhS_1.wireOp",EDGE,"1cb9c079-ea9b-4899-8069-e0e3048e911d.sketch_text.stroke-148"),sQuery(id+"FHMxAyK4CFUKdhS_1.wireOp",EDGE,"1cb9c079-ea9b-4899-8069-e0e3048e911d.sketch_text.stroke-149"),sQuery(id+"FHMxAyK4CFUKdhS_1.wireOp",EDGE,"1cb9c079-ea9b-4899-8069-e0e3048e911d.sketch_text.stroke-150"),sQuery(id+"FHMxAyK4CFUKdhS_1.wireOp",EDGE,"1cb9c079-ea9b-4899-8069-e0e3048e911d.sketch_text.stroke-151"),sQuery(id+"FHMxAyK4CFUKdhS_1.wireOp",EDGE,"1cb9c079-ea9b-4899-8069-e0e3048e911d.sketch_text.stroke-152"),sQuery(id+"FHMxAyK4CFUKdhS_1.wireOp",EDGE,"1cb9c079-ea9b-4899-8069-e0e3048e911d.sketch_text.stroke-153"),sQuery(id+"FHMxAyK4CFUKdhS_1.wireOp",EDGE,"1cb9c079-ea9b-4899-8069-e0e3048e911d.sketch_text.stroke-159"),sQuery(id+"FHMxAyK4CFUKdhS_1.wireOp",EDGE,"1cb9c079-ea9b-4899-8069-e0e3048e911d.sketch_text.stroke-160"),sQuery(id+"FHMxAyK4CFUKdhS_1.wireOp",EDGE,"1cb9c079-ea9b-4899-8069-e0e3048e911d.sketch_text.stroke-161"),sQuery(id+"FHMxAyK4CFUKdhS_1.wireOp",EDGE,"1cb9c079-ea9b-4899-8069-e0e3048e911d.sketch_text.stroke-162"),sQuery(id+"FHMxAyK4CFUKdhS_1.wireOp",EDGE,"1cb9c079-ea9b-4899-8069-e0e3048e911d.sketch_text.stroke-163"),sQuery(id+"FHMxAyK4CFUKdhS_1.wireOp",EDGE,"1cb9c079-ea9b-4899-8069-e0e3048e911d.sketch_text.stroke-164"),sQuery(id+"FHMxAyK4CFUKdhS_1.wireOp",EDGE,"1cb9c079-ea9b-4899-8069-e0e3048e911d.sketch_text.stroke-165"),sQuery(id+"FHMxAyK4CFUKdhS_1.wireOp",EDGE,"1cb9c079-ea9b-4899-8069-e0e3048e911d.sketch_text.stroke-166"),sQuery(id+"FHMxAyK4CFUKdhS_1.wireOp",EDGE,"1cb9c079-ea9b-4899-8069-e0e3048e911d.sketch_text.stroke-167"),sQuery(id+"FHMxAyK4CFUKdhS_1.wireOp",EDGE,"1cb9c079-ea9b-4899-8069-e0e3048e911d.sketch_text.stroke-168"),sQuery(id+"FHMxAyK4CFUKdhS_1.wireOp",EDGE,"1cb9c079-ea9b-4899-8069-e0e3048e911d.sketch_text.stroke-169"),sQuery(id+"FHMxAyK4CFUKdhS_1.wireOp",EDGE,"1cb9c079-ea9b-4899-8069-e0e3048e911d.sketch_text.stroke-170"),sQuery(id+"FHMxAyK4CFUKdhS_1.wireOp",EDGE,"1cb9c079-ea9b-4899-8069-e0e3048e911d.sketch_text.stroke-171"),sQuery(id+"FHMxAyK4CFUKdhS_1.wireOp",EDGE,"1cb9c079-ea9b-4899-8069-e0e3048e911d.sketch_text.stroke-172"),sQuery(id+"FHMxAyK4CFUKdhS_1.wireOp",EDGE,"1cb9c079-ea9b-4899-8069-e0e3048e911d.sketch_text.stroke-173"),sQuery(id+"FHMxAyK4CFUKdhS_1.wireOp",EDGE,"1cb9c079-ea9b-4899-8069-e0e3048e911d.sketch_text.stroke-174"),sQuery(id+"FHMxAyK4CFUKdhS_1.wireOp",EDGE,"1cb9c079-ea9b-4899-8069-e0e3048e911d.sketch_text.stroke-175"),sQuery(id+"FHMxAyK4CFUKdhS_1.wireOp",EDGE,"1cb9c079-ea9b-4899-8069-e0e3048e911d.sketch_text.stroke-176"),sQuery(id+"FHMxAyK4CFUKdhS_1.wireOp",EDGE,"1cb9c079-ea9b-4899-8069-e0e3048e911d.sketch_text.stroke-177"),sQuery(id+"FHMxAyK4CFUKdhS_1.wireOp",EDGE,"1cb9c079-ea9b-4899-8069-e0e3048e911d.sketch_text.stroke-178"),sQuery(id+"FHMxAyK4CFUKdhS_1.wireOp",EDGE,"1cb9c079-ea9b-4899-8069-e0e3048e911d.sketch_text.stroke-179"),sQuery(id+"FHMxAyK4CFUKdhS_1.wireOp",EDGE,"1cb9c079-ea9b-4899-8069-e0e3048e911d.sketch_text.stroke-180"),sQuery(id+"F2.wireOp",EDGE,"8007402e-1a4e-4a06-85a5-2af08e553504"),subQ2])],"isStart":true}),makeQuery(id+"F3.opExtrude","SWEPT_FACE",FACE,{"disambiguationData":[OSD([subQ2])]})]),OD(1.0)],"derivedFrom":makeQuery(id+"F1.opExtrude","CAP_EDGE",EDGE,{"disambiguationData":[OSD([subQ0])],"isStart":false})});}
            var Q15;
            {var subQ0=sQuery(id+"F2.wireOp",EDGE,"8007402e-1a4e-4a06-85a5-2af08e553504");var subQ1=sQuery(id+"F0.wireOp",EDGE,"E0.top");var subQ2=sQuery(id+"F2.wireOp",EDGE,"727ac2c1-f511-4829-95a7-a443ef16a4cd");var subQ3=sQuery(id+"F0.wireOp",EDGE,"E0.bottom");Q15=makeQuery(id+"F3.boolean.opBoolean","SPLIT",EDGE,{"disambiguationData":[TD([makeQuery(id+"F1.opExtrude","CAP_FACE",FACE,{"disambiguationData":[OSD([subQ3,subQ1,sQuery(id+"F0.wireOp",EDGE,"E0.left"),sQuery(id+"F0.wireOp",EDGE,"E0.right")])],"isStart":false}),makeQuery(id+"F1.opExtrude","SWEPT_FACE",FACE,{"disambiguationData":[OSD([subQ1])]}),makeQuery(id+"F3.opExtrude","SWEPT_FACE",FACE,{"disambiguationData":[OSD([subQ0])]}),makeQuery(id+"F3.opExtrude","CAP_FACE",FACE,{"disambiguationData":[OSD([subQ3,sQuery(id+"FQ5JFwxVdaqARUP_1.wireOp",EDGE,"fcba4419-a2ee-464f-be9d-58f11bf3418b.sketch_text.stroke-0"),sQuery(id+"FQ5JFwxVdaqARUP_1.wireOp",EDGE,"fcba4419-a2ee-464f-be9d-58f11bf3418b.sketch_text.stroke-1"),sQuery(id+"FQ5JFwxVdaqARUP_1.wireOp",EDGE,"fcba4419-a2ee-464f-be9d-58f11bf3418b.sketch_text.stroke-2"),sQuery(id+"FQ5JFwxVdaqARUP_1.wireOp",EDGE,"fcba4419-a2ee-464f-be9d-58f11bf3418b.sketch_text.stroke-3"),sQuery(id+"FQ5JFwxVdaqARUP_1.wireOp",EDGE,"fcba4419-a2ee-464f-be9d-58f11bf3418b.sketch_text.stroke-4"),sQuery(id+"FQ5JFwxVdaqARUP_1.wireOp",EDGE,"fcba4419-a2ee-464f-be9d-58f11bf3418b.sketch_text.stroke-5"),sQuery(id+"FQ5JFwxVdaqARUP_1.wireOp",EDGE,"fcba4419-a2ee-464f-be9d-58f11bf3418b.sketch_text.stroke-6"),sQuery(id+"FQ5JFwxVdaqARUP_1.wireOp",EDGE,"fcba4419-a2ee-464f-be9d-58f11bf3418b.sketch_text.stroke-7"),sQuery(id+"FQ5JFwxVdaqARUP_1.wireOp",EDGE,"fcba4419-a2ee-464f-be9d-58f11bf3418b.sketch_text.stroke-8"),sQuery(id+"FQ5JFwxVdaqARUP_1.wireOp",EDGE,"fcba4419-a2ee-464f-be9d-58f11bf3418b.sketch_text.stroke-9"),sQuery(id+"FQ5JFwxVdaqARUP_1.wireOp",EDGE,"fcba4419-a2ee-464f-be9d-58f11bf3418b.sketch_text.stroke-10"),sQuery(id+"FQ5JFwxVdaqARUP_1.wireOp",EDGE,"fcba4419-a2ee-464f-be9d-58f11bf3418b.sketch_text.stroke-11"),sQuery(id+"FQ5JFwxVdaqARUP_1.wireOp",EDGE,"fcba4419-a2ee-464f-be9d-58f11bf3418b.sketch_text.stroke-12"),sQuery(id+"FQ5JFwxVdaqARUP_1.wireOp",EDGE,"fcba4419-a2ee-464f-be9d-58f11bf3418b.sketch_text.stroke-13"),sQuery(id+"FQ5JFwxVdaqARUP_1.wireOp",EDGE,"fcba4419-a2ee-464f-be9d-58f11bf3418b.sketch_text.stroke-14"),sQuery(id+"FQ5JFwxVdaqARUP_1.wireOp",EDGE,"fcba4419-a2ee-464f-be9d-58f11bf3418b.sketch_text.stroke-15"),sQuery(id+"FQ5JFwxVdaqARUP_1.wireOp",EDGE,"fcba4419-a2ee-464f-be9d-58f11bf3418b.sketch_text.stroke-16"),sQuery(id+"FQ5JFwxVdaqARUP_1.wireOp",EDGE,"fcba4419-a2ee-464f-be9d-58f11bf3418b.sketch_text.stroke-17"),sQuery(id+"FQ5JFwxVdaqARUP_1.wireOp",EDGE,"fcba4419-a2ee-464f-be9d-58f11bf3418b.sketch_text.stroke-18"),sQuery(id+"FQ5JFwxVdaqARUP_1.wireOp",EDGE,"fcba4419-a2ee-464f-be9d-58f11bf3418b.sketch_text.stroke-19"),sQuery(id+"FQ5JFwxVdaqARUP_1.wireOp",EDGE,"fcba4419-a2ee-464f-be9d-58f11bf3418b.sketch_text.stroke-20"),sQuery(id+"FQ5JFwxVdaqARUP_1.wireOp",EDGE,"fcba4419-a2ee-464f-be9d-58f11bf3418b.sketch_text.stroke-21"),sQuery(id+"FQ5JFwxVdaqARUP_1.wireOp",EDGE,"fcba4419-a2ee-464f-be9d-58f11bf3418b.sketch_text.stroke-22"),sQuery(id+"FQ5JFwxVdaqARUP_1.wireOp",EDGE,"fcba4419-a2ee-464f-be9d-58f11bf3418b.sketch_text.stroke-23"),sQuery(id+"FQ5JFwxVdaqARUP_1.wireOp",EDGE,"fcba4419-a2ee-464f-be9d-58f11bf3418b.sketch_text.stroke-24"),sQuery(id+"FQ5JFwxVdaqARUP_1.wireOp",EDGE,"fcba4419-a2ee-464f-be9d-58f11bf3418b.sketch_text.stroke-25"),sQuery(id+"FQ5JFwxVdaqARUP_1.wireOp",EDGE,"fcba4419-a2ee-464f-be9d-58f11bf3418b.sketch_text.stroke-26"),sQuery(id+"FQ5JFwxVdaqARUP_1.wireOp",EDGE,"fcba4419-a2ee-464f-be9d-58f11bf3418b.sketch_text.stroke-27"),sQuery(id+"FQ5JFwxVdaqARUP_1.wireOp",EDGE,"fcba4419-a2ee-464f-be9d-58f11bf3418b.sketch_text.stroke-28"),sQuery(id+"FQ5JFwxVdaqARUP_1.wireOp",EDGE,"fcba4419-a2ee-464f-be9d-58f11bf3418b.sketch_text.stroke-29"),sQuery(id+"FQ5JFwxVdaqARUP_1.wireOp",EDGE,"fcba4419-a2ee-464f-be9d-58f11bf3418b.sketch_text.stroke-30"),sQuery(id+"FQ5JFwxVdaqARUP_1.wireOp",EDGE,"fcba4419-a2ee-464f-be9d-58f11bf3418b.sketch_text.stroke-31"),sQuery(id+"FQ5JFwxVdaqARUP_1.wireOp",EDGE,"fcba4419-a2ee-464f-be9d-58f11bf3418b.sketch_text.stroke-32"),sQuery(id+"FQ5JFwxVdaqARUP_1.wireOp",EDGE,"fcba4419-a2ee-464f-be9d-58f11bf3418b.sketch_text.stroke-33"),sQuery(id+"FQ5JFwxVdaqARUP_1.wireOp",EDGE,"fcba4419-a2ee-464f-be9d-58f11bf3418b.sketch_text.stroke-34"),sQuery(id+"FQ5JFwxVdaqARUP_1.wireOp",EDGE,"fcba4419-a2ee-464f-be9d-58f11bf3418b.sketch_text.stroke-35"),sQuery(id+"FQ5JFwxVdaqARUP_1.wireOp",EDGE,"fcba4419-a2ee-464f-be9d-58f11bf3418b.sketch_text.stroke-36"),sQuery(id+"FQ5JFwxVdaqARUP_1.wireOp",EDGE,"fcba4419-a2ee-464f-be9d-58f11bf3418b.sketch_text.stroke-37"),sQuery(id+"FQ5JFwxVdaqARUP_1.wireOp",EDGE,"fcba4419-a2ee-464f-be9d-58f11bf3418b.sketch_text.stroke-38"),sQuery(id+"FQ5JFwxVdaqARUP_1.wireOp",EDGE,"fcba4419-a2ee-464f-be9d-58f11bf3418b.sketch_text.stroke-39"),sQuery(id+"FQ5JFwxVdaqARUP_1.wireOp",EDGE,"fcba4419-a2ee-464f-be9d-58f11bf3418b.sketch_text.stroke-40"),sQuery(id+"FQ5JFwxVdaqARUP_1.wireOp",EDGE,"fcba4419-a2ee-464f-be9d-58f11bf3418b.sketch_text.stroke-41"),sQuery(id+"FQ5JFwxVdaqARUP_1.wireOp",EDGE,"fcba4419-a2ee-464f-be9d-58f11bf3418b.sketch_text.stroke-42"),sQuery(id+"FQ5JFwxVdaqARUP_1.wireOp",EDGE,"fcba4419-a2ee-464f-be9d-58f11bf3418b.sketch_text.stroke-43"),sQuery(id+"FQ5JFwxVdaqARUP_1.wireOp",EDGE,"fcba4419-a2ee-464f-be9d-58f11bf3418b.sketch_text.stroke-44"),sQuery(id+"FQ5JFwxVdaqARUP_1.wireOp",EDGE,"fcba4419-a2ee-464f-be9d-58f11bf3418b.sketch_text.stroke-45"),sQuery(id+"FQ5JFwxVdaqARUP_1.wireOp",EDGE,"fcba4419-a2ee-464f-be9d-58f11bf3418b.sketch_text.stroke-46"),sQuery(id+"FQ5JFwxVdaqARUP_1.wireOp",EDGE,"fcba4419-a2ee-464f-be9d-58f11bf3418b.sketch_text.stroke-47"),sQuery(id+"FQ5JFwxVdaqARUP_1.wireOp",EDGE,"fcba4419-a2ee-464f-be9d-58f11bf3418b.sketch_text.stroke-48"),sQuery(id+"FQ5JFwxVdaqARUP_1.wireOp",EDGE,"fcba4419-a2ee-464f-be9d-58f11bf3418b.sketch_text.stroke-49"),sQuery(id+"FQ5JFwxVdaqARUP_1.wireOp",EDGE,"fcba4419-a2ee-464f-be9d-58f11bf3418b.sketch_text.stroke-50"),sQuery(id+"FQ5JFwxVdaqARUP_1.wireOp",EDGE,"fcba4419-a2ee-464f-be9d-58f11bf3418b.sketch_text.stroke-51"),sQuery(id+"FQ5JFwxVdaqARUP_1.wireOp",EDGE,"fcba4419-a2ee-464f-be9d-58f11bf3418b.sketch_text.stroke-52"),sQuery(id+"FQ5JFwxVdaqARUP_1.wireOp",EDGE,"fcba4419-a2ee-464f-be9d-58f11bf3418b.sketch_text.stroke-53"),sQuery(id+"FQ5JFwxVdaqARUP_1.wireOp",EDGE,"fcba4419-a2ee-464f-be9d-58f11bf3418b.sketch_text.stroke-54"),sQuery(id+"FQ5JFwxVdaqARUP_1.wireOp",EDGE,"fcba4419-a2ee-464f-be9d-58f11bf3418b.sketch_text.stroke-55"),sQuery(id+"FQ5JFwxVdaqARUP_1.wireOp",EDGE,"fcba4419-a2ee-464f-be9d-58f11bf3418b.sketch_text.stroke-56"),sQuery(id+"FQ5JFwxVdaqARUP_1.wireOp",EDGE,"fcba4419-a2ee-464f-be9d-58f11bf3418b.sketch_text.stroke-57"),sQuery(id+"FQ5JFwxVdaqARUP_1.wireOp",EDGE,"fcba4419-a2ee-464f-be9d-58f11bf3418b.sketch_text.stroke-58"),sQuery(id+"FQ5JFwxVdaqARUP_1.wireOp",EDGE,"fcba4419-a2ee-464f-be9d-58f11bf3418b.sketch_text.stroke-59"),sQuery(id+"FQ5JFwxVdaqARUP_1.wireOp",EDGE,"fcba4419-a2ee-464f-be9d-58f11bf3418b.sketch_text.stroke-60"),sQuery(id+"FQ5JFwxVdaqARUP_1.wireOp",EDGE,"fcba4419-a2ee-464f-be9d-58f11bf3418b.sketch_text.stroke-61"),sQuery(id+"FQ5JFwxVdaqARUP_1.wireOp",EDGE,"fcba4419-a2ee-464f-be9d-58f11bf3418b.sketch_text.stroke-62"),sQuery(id+"FQ5JFwxVdaqARUP_1.wireOp",EDGE,"fcba4419-a2ee-464f-be9d-58f11bf3418b.sketch_text.stroke-63"),sQuery(id+"FQ5JFwxVdaqARUP_1.wireOp",EDGE,"fcba4419-a2ee-464f-be9d-58f11bf3418b.sketch_text.stroke-64"),sQuery(id+"FQ5JFwxVdaqARUP_1.wireOp",EDGE,"fcba4419-a2ee-464f-be9d-58f11bf3418b.sketch_text.stroke-65"),sQuery(id+"FQ5JFwxVdaqARUP_1.wireOp",EDGE,"fcba4419-a2ee-464f-be9d-58f11bf3418b.sketch_text.stroke-66"),sQuery(id+"FQ5JFwxVdaqARUP_1.wireOp",EDGE,"fcba4419-a2ee-464f-be9d-58f11bf3418b.sketch_text.stroke-67"),sQuery(id+"FQ5JFwxVdaqARUP_1.wireOp",EDGE,"fcba4419-a2ee-464f-be9d-58f11bf3418b.sketch_text.stroke-68"),sQuery(id+"FQ5JFwxVdaqARUP_1.wireOp",EDGE,"fcba4419-a2ee-464f-be9d-58f11bf3418b.sketch_text.stroke-69"),sQuery(id+"FQ5JFwxVdaqARUP_1.wireOp",EDGE,"fcba4419-a2ee-464f-be9d-58f11bf3418b.sketch_text.stroke-70"),sQuery(id+"FQ5JFwxVdaqARUP_1.wireOp",EDGE,"fcba4419-a2ee-464f-be9d-58f11bf3418b.sketch_text.stroke-71"),sQuery(id+"FQ5JFwxVdaqARUP_1.wireOp",EDGE,"fcba4419-a2ee-464f-be9d-58f11bf3418b.sketch_text.stroke-72"),sQuery(id+"FQ5JFwxVdaqARUP_1.wireOp",EDGE,"fcba4419-a2ee-464f-be9d-58f11bf3418b.sketch_text.stroke-73"),sQuery(id+"FQ5JFwxVdaqARUP_1.wireOp",EDGE,"fcba4419-a2ee-464f-be9d-58f11bf3418b.sketch_text.stroke-74"),sQuery(id+"FQ5JFwxVdaqARUP_1.wireOp",EDGE,"fcba4419-a2ee-464f-be9d-58f11bf3418b.sketch_text.stroke-75"),sQuery(id+"FQ5JFwxVdaqARUP_1.wireOp",EDGE,"fcba4419-a2ee-464f-be9d-58f11bf3418b.sketch_text.stroke-76"),sQuery(id+"FQ5JFwxVdaqARUP_1.wireOp",EDGE,"fcba4419-a2ee-464f-be9d-58f11bf3418b.sketch_text.stroke-77"),sQuery(id+"FQ5JFwxVdaqARUP_1.wireOp",EDGE,"fcba4419-a2ee-464f-be9d-58f11bf3418b.sketch_text.stroke-78"),sQuery(id+"FQ5JFwxVdaqARUP_1.wireOp",EDGE,"fcba4419-a2ee-464f-be9d-58f11bf3418b.sketch_text.stroke-79"),sQuery(id+"FQ5JFwxVdaqARUP_1.wireOp",EDGE,"fcba4419-a2ee-464f-be9d-58f11bf3418b.sketch_text.stroke-80"),sQuery(id+"FQ5JFwxVdaqARUP_1.wireOp",EDGE,"fcba4419-a2ee-464f-be9d-58f11bf3418b.sketch_text.stroke-81"),sQuery(id+"FQ5JFwxVdaqARUP_1.wireOp",EDGE,"fcba4419-a2ee-464f-be9d-58f11bf3418b.sketch_text.stroke-82"),sQuery(id+"FQ5JFwxVdaqARUP_1.wireOp",EDGE,"fcba4419-a2ee-464f-be9d-58f11bf3418b.sketch_text.stroke-83"),sQuery(id+"FQ5JFwxVdaqARUP_1.wireOp",EDGE,"fcba4419-a2ee-464f-be9d-58f11bf3418b.sketch_text.stroke-84"),sQuery(id+"FQ5JFwxVdaqARUP_1.wireOp",EDGE,"fcba4419-a2ee-464f-be9d-58f11bf3418b.sketch_text.stroke-85"),sQuery(id+"FQ5JFwxVdaqARUP_1.wireOp",EDGE,"fcba4419-a2ee-464f-be9d-58f11bf3418b.sketch_text.stroke-86"),sQuery(id+"FQ5JFwxVdaqARUP_1.wireOp",EDGE,"fcba4419-a2ee-464f-be9d-58f11bf3418b.sketch_text.stroke-87"),sQuery(id+"FQ5JFwxVdaqARUP_1.wireOp",EDGE,"fcba4419-a2ee-464f-be9d-58f11bf3418b.sketch_text.stroke-88"),sQuery(id+"FQ5JFwxVdaqARUP_1.wireOp",EDGE,"fcba4419-a2ee-464f-be9d-58f11bf3418b.sketch_text.stroke-89"),sQuery(id+"FQ5JFwxVdaqARUP_1.wireOp",EDGE,"fcba4419-a2ee-464f-be9d-58f11bf3418b.sketch_text.stroke-90"),sQuery(id+"FQ5JFwxVdaqARUP_1.wireOp",EDGE,"fcba4419-a2ee-464f-be9d-58f11bf3418b.sketch_text.stroke-91"),sQuery(id+"FQ5JFwxVdaqARUP_1.wireOp",EDGE,"fcba4419-a2ee-464f-be9d-58f11bf3418b.sketch_text.stroke-92"),sQuery(id+"FQ5JFwxVdaqARUP_1.wireOp",EDGE,"fcba4419-a2ee-464f-be9d-58f11bf3418b.sketch_text.stroke-93"),sQuery(id+"FQ5JFwxVdaqARUP_1.wireOp",EDGE,"fcba4419-a2ee-464f-be9d-58f11bf3418b.sketch_text.stroke-94"),sQuery(id+"FQ5JFwxVdaqARUP_1.wireOp",EDGE,"fcba4419-a2ee-464f-be9d-58f11bf3418b.sketch_text.stroke-95"),sQuery(id+"FQ5JFwxVdaqARUP_1.wireOp",EDGE,"fcba4419-a2ee-464f-be9d-58f11bf3418b.sketch_text.stroke-96"),sQuery(id+"FQ5JFwxVdaqARUP_1.wireOp",EDGE,"fcba4419-a2ee-464f-be9d-58f11bf3418b.sketch_text.stroke-97"),sQuery(id+"FQ5JFwxVdaqARUP_1.wireOp",EDGE,"fcba4419-a2ee-464f-be9d-58f11bf3418b.sketch_text.stroke-98"),sQuery(id+"FQ5JFwxVdaqARUP_1.wireOp",EDGE,"fcba4419-a2ee-464f-be9d-58f11bf3418b.sketch_text.stroke-99"),sQuery(id+"FQ5JFwxVdaqARUP_1.wireOp",EDGE,"fcba4419-a2ee-464f-be9d-58f11bf3418b.sketch_text.stroke-100"),sQuery(id+"FQ5JFwxVdaqARUP_1.wireOp",EDGE,"fcba4419-a2ee-464f-be9d-58f11bf3418b.sketch_text.stroke-101"),sQuery(id+"FQ5JFwxVdaqARUP_1.wireOp",EDGE,"fcba4419-a2ee-464f-be9d-58f11bf3418b.sketch_text.stroke-102"),sQuery(id+"FQ5JFwxVdaqARUP_1.wireOp",EDGE,"fcba4419-a2ee-464f-be9d-58f11bf3418b.sketch_text.stroke-103"),sQuery(id+"FQ5JFwxVdaqARUP_1.wireOp",EDGE,"fcba4419-a2ee-464f-be9d-58f11bf3418b.sketch_text.stroke-104"),sQuery(id+"FQ5JFwxVdaqARUP_1.wireOp",EDGE,"fcba4419-a2ee-464f-be9d-58f11bf3418b.sketch_text.stroke-105"),sQuery(id+"FQ5JFwxVdaqARUP_1.wireOp",EDGE,"fcba4419-a2ee-464f-be9d-58f11bf3418b.sketch_text.stroke-106"),sQuery(id+"FQ5JFwxVdaqARUP_1.wireOp",EDGE,"fcba4419-a2ee-464f-be9d-58f11bf3418b.sketch_text.stroke-107"),sQuery(id+"FQ5JFwxVdaqARUP_1.wireOp",EDGE,"fcba4419-a2ee-464f-be9d-58f11bf3418b.sketch_text.stroke-108"),sQuery(id+"FQ5JFwxVdaqARUP_1.wireOp",EDGE,"fcba4419-a2ee-464f-be9d-58f11bf3418b.sketch_text.stroke-109"),sQuery(id+"FQ5JFwxVdaqARUP_1.wireOp",EDGE,"fcba4419-a2ee-464f-be9d-58f11bf3418b.sketch_text.stroke-110"),sQuery(id+"FQ5JFwxVdaqARUP_1.wireOp",EDGE,"fcba4419-a2ee-464f-be9d-58f11bf3418b.sketch_text.stroke-111"),sQuery(id+"FQ5JFwxVdaqARUP_1.wireOp",EDGE,"fcba4419-a2ee-464f-be9d-58f11bf3418b.sketch_text.stroke-112"),sQuery(id+"FQ5JFwxVdaqARUP_1.wireOp",EDGE,"fcba4419-a2ee-464f-be9d-58f11bf3418b.sketch_text.stroke-113"),sQuery(id+"FQ5JFwxVdaqARUP_1.wireOp",EDGE,"fcba4419-a2ee-464f-be9d-58f11bf3418b.sketch_text.stroke-114"),sQuery(id+"FQ5JFwxVdaqARUP_1.wireOp",EDGE,"fcba4419-a2ee-464f-be9d-58f11bf3418b.sketch_text.stroke-115"),sQuery(id+"FQ5JFwxVdaqARUP_1.wireOp",EDGE,"fcba4419-a2ee-464f-be9d-58f11bf3418b.sketch_text.stroke-116"),sQuery(id+"FQ5JFwxVdaqARUP_1.wireOp",EDGE,"fcba4419-a2ee-464f-be9d-58f11bf3418b.sketch_text.stroke-117"),sQuery(id+"FQ5JFwxVdaqARUP_1.wireOp",EDGE,"fcba4419-a2ee-464f-be9d-58f11bf3418b.sketch_text.stroke-118"),sQuery(id+"FQ5JFwxVdaqARUP_1.wireOp",EDGE,"fcba4419-a2ee-464f-be9d-58f11bf3418b.sketch_text.stroke-119"),sQuery(id+"FQ5JFwxVdaqARUP_1.wireOp",EDGE,"fcba4419-a2ee-464f-be9d-58f11bf3418b.sketch_text.stroke-120"),sQuery(id+"FQ5JFwxVdaqARUP_1.wireOp",EDGE,"fcba4419-a2ee-464f-be9d-58f11bf3418b.sketch_text.stroke-121"),sQuery(id+"FQ5JFwxVdaqARUP_1.wireOp",EDGE,"fcba4419-a2ee-464f-be9d-58f11bf3418b.sketch_text.stroke-122"),sQuery(id+"FQ5JFwxVdaqARUP_1.wireOp",EDGE,"fcba4419-a2ee-464f-be9d-58f11bf3418b.sketch_text.stroke-123"),sQuery(id+"FQ5JFwxVdaqARUP_1.wireOp",EDGE,"fcba4419-a2ee-464f-be9d-58f11bf3418b.sketch_text.stroke-124"),sQuery(id+"FQ5JFwxVdaqARUP_1.wireOp",EDGE,"fcba4419-a2ee-464f-be9d-58f11bf3418b.sketch_text.stroke-125"),sQuery(id+"FQ5JFwxVdaqARUP_1.wireOp",EDGE,"fcba4419-a2ee-464f-be9d-58f11bf3418b.sketch_text.stroke-126"),sQuery(id+"FQ5JFwxVdaqARUP_1.wireOp",EDGE,"fcba4419-a2ee-464f-be9d-58f11bf3418b.sketch_text.stroke-127"),sQuery(id+"FQ5JFwxVdaqARUP_1.wireOp",EDGE,"fcba4419-a2ee-464f-be9d-58f11bf3418b.sketch_text.stroke-128"),sQuery(id+"FQ5JFwxVdaqARUP_1.wireOp",EDGE,"fcba4419-a2ee-464f-be9d-58f11bf3418b.sketch_text.stroke-129"),sQuery(id+"FQ5JFwxVdaqARUP_1.wireOp",EDGE,"fcba4419-a2ee-464f-be9d-58f11bf3418b.sketch_text.stroke-130"),sQuery(id+"FQ5JFwxVdaqARUP_1.wireOp",EDGE,"fcba4419-a2ee-464f-be9d-58f11bf3418b.sketch_text.stroke-131"),sQuery(id+"FQ5JFwxVdaqARUP_1.wireOp",EDGE,"fcba4419-a2ee-464f-be9d-58f11bf3418b.sketch_text.stroke-132"),sQuery(id+"FQ5JFwxVdaqARUP_1.wireOp",EDGE,"fcba4419-a2ee-464f-be9d-58f11bf3418b.sketch_text.stroke-133"),sQuery(id+"FQ5JFwxVdaqARUP_1.wireOp",EDGE,"fcba4419-a2ee-464f-be9d-58f11bf3418b.sketch_text.stroke-134"),sQuery(id+"FQ5JFwxVdaqARUP_1.wireOp",EDGE,"fcba4419-a2ee-464f-be9d-58f11bf3418b.sketch_text.stroke-135"),sQuery(id+"FQ5JFwxVdaqARUP_1.wireOp",EDGE,"fcba4419-a2ee-464f-be9d-58f11bf3418b.sketch_text.stroke-136"),sQuery(id+"FQ5JFwxVdaqARUP_1.wireOp",EDGE,"fcba4419-a2ee-464f-be9d-58f11bf3418b.sketch_text.stroke-137"),sQuery(id+"FQ5JFwxVdaqARUP_1.wireOp",EDGE,"fcba4419-a2ee-464f-be9d-58f11bf3418b.sketch_text.stroke-138"),sQuery(id+"FQ5JFwxVdaqARUP_1.wireOp",EDGE,"fcba4419-a2ee-464f-be9d-58f11bf3418b.sketch_text.stroke-139"),sQuery(id+"FQ5JFwxVdaqARUP_1.wireOp",EDGE,"fcba4419-a2ee-464f-be9d-58f11bf3418b.sketch_text.stroke-140"),sQuery(id+"FQ5JFwxVdaqARUP_1.wireOp",EDGE,"fcba4419-a2ee-464f-be9d-58f11bf3418b.sketch_text.stroke-141"),sQuery(id+"FQ5JFwxVdaqARUP_1.wireOp",EDGE,"fcba4419-a2ee-464f-be9d-58f11bf3418b.sketch_text.stroke-142"),sQuery(id+"FQ5JFwxVdaqARUP_1.wireOp",EDGE,"fcba4419-a2ee-464f-be9d-58f11bf3418b.sketch_text.stroke-143"),sQuery(id+"FQ5JFwxVdaqARUP_1.wireOp",EDGE,"fcba4419-a2ee-464f-be9d-58f11bf3418b.sketch_text.stroke-144"),sQuery(id+"FQ5JFwxVdaqARUP_1.wireOp",EDGE,"fcba4419-a2ee-464f-be9d-58f11bf3418b.sketch_text.stroke-145"),sQuery(id+"FQ5JFwxVdaqARUP_1.wireOp",EDGE,"fcba4419-a2ee-464f-be9d-58f11bf3418b.sketch_text.stroke-146"),sQuery(id+"FQ5JFwxVdaqARUP_1.wireOp",EDGE,"fcba4419-a2ee-464f-be9d-58f11bf3418b.sketch_text.stroke-147"),sQuery(id+"FQ5JFwxVdaqARUP_1.wireOp",EDGE,"fcba4419-a2ee-464f-be9d-58f11bf3418b.sketch_text.stroke-148"),sQuery(id+"FQ5JFwxVdaqARUP_1.wireOp",EDGE,"fcba4419-a2ee-464f-be9d-58f11bf3418b.sketch_text.stroke-149"),sQuery(id+"FQ5JFwxVdaqARUP_1.wireOp",EDGE,"fcba4419-a2ee-464f-be9d-58f11bf3418b.sketch_text.stroke-150"),sQuery(id+"FQ5JFwxVdaqARUP_1.wireOp",EDGE,"fcba4419-a2ee-464f-be9d-58f11bf3418b.sketch_text.stroke-151"),sQuery(id+"FQ5JFwxVdaqARUP_1.wireOp",EDGE,"fcba4419-a2ee-464f-be9d-58f11bf3418b.sketch_text.stroke-152"),sQuery(id+"FQ5JFwxVdaqARUP_1.wireOp",EDGE,"fcba4419-a2ee-464f-be9d-58f11bf3418b.sketch_text.stroke-153"),sQuery(id+"FQ5JFwxVdaqARUP_1.wireOp",EDGE,"fcba4419-a2ee-464f-be9d-58f11bf3418b.sketch_text.stroke-154"),sQuery(id+"FQ5JFwxVdaqARUP_1.wireOp",EDGE,"fcba4419-a2ee-464f-be9d-58f11bf3418b.sketch_text.stroke-155"),sQuery(id+"FQ5JFwxVdaqARUP_1.wireOp",EDGE,"fcba4419-a2ee-464f-be9d-58f11bf3418b.sketch_text.stroke-156"),sQuery(id+"FQ5JFwxVdaqARUP_1.wireOp",EDGE,"fcba4419-a2ee-464f-be9d-58f11bf3418b.sketch_text.stroke-157"),sQuery(id+"FQ5JFwxVdaqARUP_1.wireOp",EDGE,"fcba4419-a2ee-464f-be9d-58f11bf3418b.sketch_text.stroke-158"),sQuery(id+"FQ5JFwxVdaqARUP_1.wireOp",EDGE,"fcba4419-a2ee-464f-be9d-58f11bf3418b.sketch_text.stroke-159"),sQuery(id+"FQ5JFwxVdaqARUP_1.wireOp",EDGE,"fcba4419-a2ee-464f-be9d-58f11bf3418b.sketch_text.stroke-160"),sQuery(id+"FQ5JFwxVdaqARUP_1.wireOp",EDGE,"fcba4419-a2ee-464f-be9d-58f11bf3418b.sketch_text.stroke-161"),sQuery(id+"FQ5JFwxVdaqARUP_1.wireOp",EDGE,"fcba4419-a2ee-464f-be9d-58f11bf3418b.sketch_text.stroke-162"),sQuery(id+"FQ5JFwxVdaqARUP_1.wireOp",EDGE,"fcba4419-a2ee-464f-be9d-58f11bf3418b.sketch_text.stroke-163"),sQuery(id+"FQ5JFwxVdaqARUP_1.wireOp",EDGE,"fcba4419-a2ee-464f-be9d-58f11bf3418b.sketch_text.stroke-164"),sQuery(id+"FQ5JFwxVdaqARUP_1.wireOp",EDGE,"fcba4419-a2ee-464f-be9d-58f11bf3418b.sketch_text.stroke-165"),sQuery(id+"FQ5JFwxVdaqARUP_1.wireOp",EDGE,"fcba4419-a2ee-464f-be9d-58f11bf3418b.sketch_text.stroke-166"),sQuery(id+"FQ5JFwxVdaqARUP_1.wireOp",EDGE,"fcba4419-a2ee-464f-be9d-58f11bf3418b.sketch_text.stroke-167"),sQuery(id+"FQ5JFwxVdaqARUP_1.wireOp",EDGE,"fcba4419-a2ee-464f-be9d-58f11bf3418b.sketch_text.stroke-168"),sQuery(id+"FQ5JFwxVdaqARUP_1.wireOp",EDGE,"fcba4419-a2ee-464f-be9d-58f11bf3418b.sketch_text.stroke-169"),sQuery(id+"FQ5JFwxVdaqARUP_1.wireOp",EDGE,"fcba4419-a2ee-464f-be9d-58f11bf3418b.sketch_text.stroke-170"),sQuery(id+"FQ5JFwxVdaqARUP_1.wireOp",EDGE,"fcba4419-a2ee-464f-be9d-58f11bf3418b.sketch_text.stroke-171"),sQuery(id+"FQ5JFwxVdaqARUP_1.wireOp",EDGE,"fcba4419-a2ee-464f-be9d-58f11bf3418b.sketch_text.stroke-172"),sQuery(id+"FQ5JFwxVdaqARUP_1.wireOp",EDGE,"fcba4419-a2ee-464f-be9d-58f11bf3418b.sketch_text.stroke-173"),sQuery(id+"FHMxAyK4CFUKdhS_1.wireOp",EDGE,"1cb9c079-ea9b-4899-8069-e0e3048e911d.sketch_text.stroke-0"),sQuery(id+"FHMxAyK4CFUKdhS_1.wireOp",EDGE,"1cb9c079-ea9b-4899-8069-e0e3048e911d.sketch_text.stroke-1"),sQuery(id+"FHMxAyK4CFUKdhS_1.wireOp",EDGE,"1cb9c079-ea9b-4899-8069-e0e3048e911d.sketch_text.stroke-2"),sQuery(id+"FHMxAyK4CFUKdhS_1.wireOp",EDGE,"1cb9c079-ea9b-4899-8069-e0e3048e911d.sketch_text.stroke-3"),sQuery(id+"FHMxAyK4CFUKdhS_1.wireOp",EDGE,"1cb9c079-ea9b-4899-8069-e0e3048e911d.sketch_text.stroke-4"),sQuery(id+"FHMxAyK4CFUKdhS_1.wireOp",EDGE,"1cb9c079-ea9b-4899-8069-e0e3048e911d.sketch_text.stroke-5"),sQuery(id+"FHMxAyK4CFUKdhS_1.wireOp",EDGE,"1cb9c079-ea9b-4899-8069-e0e3048e911d.sketch_text.stroke-6"),sQuery(id+"FHMxAyK4CFUKdhS_1.wireOp",EDGE,"1cb9c079-ea9b-4899-8069-e0e3048e911d.sketch_text.stroke-7"),sQuery(id+"FHMxAyK4CFUKdhS_1.wireOp",EDGE,"1cb9c079-ea9b-4899-8069-e0e3048e911d.sketch_text.stroke-8"),sQuery(id+"FHMxAyK4CFUKdhS_1.wireOp",EDGE,"1cb9c079-ea9b-4899-8069-e0e3048e911d.sketch_text.stroke-9"),sQuery(id+"FHMxAyK4CFUKdhS_1.wireOp",EDGE,"1cb9c079-ea9b-4899-8069-e0e3048e911d.sketch_text.stroke-10"),sQuery(id+"FHMxAyK4CFUKdhS_1.wireOp",EDGE,"1cb9c079-ea9b-4899-8069-e0e3048e911d.sketch_text.stroke-11"),sQuery(id+"FHMxAyK4CFUKdhS_1.wireOp",EDGE,"1cb9c079-ea9b-4899-8069-e0e3048e911d.sketch_text.stroke-12"),sQuery(id+"FHMxAyK4CFUKdhS_1.wireOp",EDGE,"1cb9c079-ea9b-4899-8069-e0e3048e911d.sketch_text.stroke-13"),sQuery(id+"FHMxAyK4CFUKdhS_1.wireOp",EDGE,"1cb9c079-ea9b-4899-8069-e0e3048e911d.sketch_text.stroke-14"),sQuery(id+"FHMxAyK4CFUKdhS_1.wireOp",EDGE,"1cb9c079-ea9b-4899-8069-e0e3048e911d.sketch_text.stroke-15"),sQuery(id+"FHMxAyK4CFUKdhS_1.wireOp",EDGE,"1cb9c079-ea9b-4899-8069-e0e3048e911d.sketch_text.stroke-16"),sQuery(id+"FHMxAyK4CFUKdhS_1.wireOp",EDGE,"1cb9c079-ea9b-4899-8069-e0e3048e911d.sketch_text.stroke-17"),sQuery(id+"FHMxAyK4CFUKdhS_1.wireOp",EDGE,"1cb9c079-ea9b-4899-8069-e0e3048e911d.sketch_text.stroke-18"),sQuery(id+"FHMxAyK4CFUKdhS_1.wireOp",EDGE,"1cb9c079-ea9b-4899-8069-e0e3048e911d.sketch_text.stroke-19"),sQuery(id+"FHMxAyK4CFUKdhS_1.wireOp",EDGE,"1cb9c079-ea9b-4899-8069-e0e3048e911d.sketch_text.stroke-20"),sQuery(id+"FHMxAyK4CFUKdhS_1.wireOp",EDGE,"1cb9c079-ea9b-4899-8069-e0e3048e911d.sketch_text.stroke-21"),sQuery(id+"FHMxAyK4CFUKdhS_1.wireOp",EDGE,"1cb9c079-ea9b-4899-8069-e0e3048e911d.sketch_text.stroke-22"),sQuery(id+"FHMxAyK4CFUKdhS_1.wireOp",EDGE,"1cb9c079-ea9b-4899-8069-e0e3048e911d.sketch_text.stroke-23"),sQuery(id+"FHMxAyK4CFUKdhS_1.wireOp",EDGE,"1cb9c079-ea9b-4899-8069-e0e3048e911d.sketch_text.stroke-24"),sQuery(id+"FHMxAyK4CFUKdhS_1.wireOp",EDGE,"1cb9c079-ea9b-4899-8069-e0e3048e911d.sketch_text.stroke-25"),sQuery(id+"FHMxAyK4CFUKdhS_1.wireOp",EDGE,"1cb9c079-ea9b-4899-8069-e0e3048e911d.sketch_text.stroke-26"),sQuery(id+"FHMxAyK4CFUKdhS_1.wireOp",EDGE,"1cb9c079-ea9b-4899-8069-e0e3048e911d.sketch_text.stroke-27"),sQuery(id+"FHMxAyK4CFUKdhS_1.wireOp",EDGE,"1cb9c079-ea9b-4899-8069-e0e3048e911d.sketch_text.stroke-28"),sQuery(id+"FHMxAyK4CFUKdhS_1.wireOp",EDGE,"1cb9c079-ea9b-4899-8069-e0e3048e911d.sketch_text.stroke-29"),sQuery(id+"FHMxAyK4CFUKdhS_1.wireOp",EDGE,"1cb9c079-ea9b-4899-8069-e0e3048e911d.sketch_text.stroke-30"),sQuery(id+"FHMxAyK4CFUKdhS_1.wireOp",EDGE,"1cb9c079-ea9b-4899-8069-e0e3048e911d.sketch_text.stroke-31"),sQuery(id+"FHMxAyK4CFUKdhS_1.wireOp",EDGE,"1cb9c079-ea9b-4899-8069-e0e3048e911d.sketch_text.stroke-32"),sQuery(id+"FHMxAyK4CFUKdhS_1.wireOp",EDGE,"1cb9c079-ea9b-4899-8069-e0e3048e911d.sketch_text.stroke-33"),sQuery(id+"FHMxAyK4CFUKdhS_1.wireOp",EDGE,"1cb9c079-ea9b-4899-8069-e0e3048e911d.sketch_text.stroke-34"),sQuery(id+"FHMxAyK4CFUKdhS_1.wireOp",EDGE,"1cb9c079-ea9b-4899-8069-e0e3048e911d.sketch_text.stroke-35"),sQuery(id+"FHMxAyK4CFUKdhS_1.wireOp",EDGE,"1cb9c079-ea9b-4899-8069-e0e3048e911d.sketch_text.stroke-36"),sQuery(id+"FHMxAyK4CFUKdhS_1.wireOp",EDGE,"1cb9c079-ea9b-4899-8069-e0e3048e911d.sketch_text.stroke-37"),sQuery(id+"FHMxAyK4CFUKdhS_1.wireOp",EDGE,"1cb9c079-ea9b-4899-8069-e0e3048e911d.sketch_text.stroke-38"),sQuery(id+"FHMxAyK4CFUKdhS_1.wireOp",EDGE,"1cb9c079-ea9b-4899-8069-e0e3048e911d.sketch_text.stroke-39"),sQuery(id+"FHMxAyK4CFUKdhS_1.wireOp",EDGE,"1cb9c079-ea9b-4899-8069-e0e3048e911d.sketch_text.stroke-40"),sQuery(id+"FHMxAyK4CFUKdhS_1.wireOp",EDGE,"1cb9c079-ea9b-4899-8069-e0e3048e911d.sketch_text.stroke-41"),sQuery(id+"FHMxAyK4CFUKdhS_1.wireOp",EDGE,"1cb9c079-ea9b-4899-8069-e0e3048e911d.sketch_text.stroke-42"),sQuery(id+"FHMxAyK4CFUKdhS_1.wireOp",EDGE,"1cb9c079-ea9b-4899-8069-e0e3048e911d.sketch_text.stroke-43"),sQuery(id+"FHMxAyK4CFUKdhS_1.wireOp",EDGE,"1cb9c079-ea9b-4899-8069-e0e3048e911d.sketch_text.stroke-44"),sQuery(id+"FHMxAyK4CFUKdhS_1.wireOp",EDGE,"1cb9c079-ea9b-4899-8069-e0e3048e911d.sketch_text.stroke-45"),sQuery(id+"FHMxAyK4CFUKdhS_1.wireOp",EDGE,"1cb9c079-ea9b-4899-8069-e0e3048e911d.sketch_text.stroke-46"),sQuery(id+"FHMxAyK4CFUKdhS_1.wireOp",EDGE,"1cb9c079-ea9b-4899-8069-e0e3048e911d.sketch_text.stroke-47"),sQuery(id+"FHMxAyK4CFUKdhS_1.wireOp",EDGE,"1cb9c079-ea9b-4899-8069-e0e3048e911d.sketch_text.stroke-48"),sQuery(id+"FHMxAyK4CFUKdhS_1.wireOp",EDGE,"1cb9c079-ea9b-4899-8069-e0e3048e911d.sketch_text.stroke-49"),sQuery(id+"FHMxAyK4CFUKdhS_1.wireOp",EDGE,"1cb9c079-ea9b-4899-8069-e0e3048e911d.sketch_text.stroke-50"),sQuery(id+"FHMxAyK4CFUKdhS_1.wireOp",EDGE,"1cb9c079-ea9b-4899-8069-e0e3048e911d.sketch_text.stroke-51"),sQuery(id+"FHMxAyK4CFUKdhS_1.wireOp",EDGE,"1cb9c079-ea9b-4899-8069-e0e3048e911d.sketch_text.stroke-52"),sQuery(id+"FHMxAyK4CFUKdhS_1.wireOp",EDGE,"1cb9c079-ea9b-4899-8069-e0e3048e911d.sketch_text.stroke-53"),sQuery(id+"FHMxAyK4CFUKdhS_1.wireOp",EDGE,"1cb9c079-ea9b-4899-8069-e0e3048e911d.sketch_text.stroke-54"),sQuery(id+"FHMxAyK4CFUKdhS_1.wireOp",EDGE,"1cb9c079-ea9b-4899-8069-e0e3048e911d.sketch_text.stroke-55"),sQuery(id+"FHMxAyK4CFUKdhS_1.wireOp",EDGE,"1cb9c079-ea9b-4899-8069-e0e3048e911d.sketch_text.stroke-56"),sQuery(id+"FHMxAyK4CFUKdhS_1.wireOp",EDGE,"1cb9c079-ea9b-4899-8069-e0e3048e911d.sketch_text.stroke-57"),sQuery(id+"FHMxAyK4CFUKdhS_1.wireOp",EDGE,"1cb9c079-ea9b-4899-8069-e0e3048e911d.sketch_text.stroke-58"),sQuery(id+"FHMxAyK4CFUKdhS_1.wireOp",EDGE,"1cb9c079-ea9b-4899-8069-e0e3048e911d.sketch_text.stroke-59"),sQuery(id+"FHMxAyK4CFUKdhS_1.wireOp",EDGE,"1cb9c079-ea9b-4899-8069-e0e3048e911d.sketch_text.stroke-60"),sQuery(id+"FHMxAyK4CFUKdhS_1.wireOp",EDGE,"1cb9c079-ea9b-4899-8069-e0e3048e911d.sketch_text.stroke-61"),sQuery(id+"FHMxAyK4CFUKdhS_1.wireOp",EDGE,"1cb9c079-ea9b-4899-8069-e0e3048e911d.sketch_text.stroke-62"),sQuery(id+"FHMxAyK4CFUKdhS_1.wireOp",EDGE,"1cb9c079-ea9b-4899-8069-e0e3048e911d.sketch_text.stroke-71"),sQuery(id+"FHMxAyK4CFUKdhS_1.wireOp",EDGE,"1cb9c079-ea9b-4899-8069-e0e3048e911d.sketch_text.stroke-72"),sQuery(id+"FHMxAyK4CFUKdhS_1.wireOp",EDGE,"1cb9c079-ea9b-4899-8069-e0e3048e911d.sketch_text.stroke-73"),sQuery(id+"FHMxAyK4CFUKdhS_1.wireOp",EDGE,"1cb9c079-ea9b-4899-8069-e0e3048e911d.sketch_text.stroke-74"),sQuery(id+"FHMxAyK4CFUKdhS_1.wireOp",EDGE,"1cb9c079-ea9b-4899-8069-e0e3048e911d.sketch_text.stroke-75"),sQuery(id+"FHMxAyK4CFUKdhS_1.wireOp",EDGE,"1cb9c079-ea9b-4899-8069-e0e3048e911d.sketch_text.stroke-76"),sQuery(id+"FHMxAyK4CFUKdhS_1.wireOp",EDGE,"1cb9c079-ea9b-4899-8069-e0e3048e911d.sketch_text.stroke-77"),sQuery(id+"FHMxAyK4CFUKdhS_1.wireOp",EDGE,"1cb9c079-ea9b-4899-8069-e0e3048e911d.sketch_text.stroke-78"),sQuery(id+"FHMxAyK4CFUKdhS_1.wireOp",EDGE,"1cb9c079-ea9b-4899-8069-e0e3048e911d.sketch_text.stroke-79"),sQuery(id+"FHMxAyK4CFUKdhS_1.wireOp",EDGE,"1cb9c079-ea9b-4899-8069-e0e3048e911d.sketch_text.stroke-80"),sQuery(id+"FHMxAyK4CFUKdhS_1.wireOp",EDGE,"1cb9c079-ea9b-4899-8069-e0e3048e911d.sketch_text.stroke-81"),sQuery(id+"FHMxAyK4CFUKdhS_1.wireOp",EDGE,"1cb9c079-ea9b-4899-8069-e0e3048e911d.sketch_text.stroke-82"),sQuery(id+"FHMxAyK4CFUKdhS_1.wireOp",EDGE,"1cb9c079-ea9b-4899-8069-e0e3048e911d.sketch_text.stroke-83"),sQuery(id+"FHMxAyK4CFUKdhS_1.wireOp",EDGE,"1cb9c079-ea9b-4899-8069-e0e3048e911d.sketch_text.stroke-84"),sQuery(id+"FHMxAyK4CFUKdhS_1.wireOp",EDGE,"1cb9c079-ea9b-4899-8069-e0e3048e911d.sketch_text.stroke-85"),sQuery(id+"FHMxAyK4CFUKdhS_1.wireOp",EDGE,"1cb9c079-ea9b-4899-8069-e0e3048e911d.sketch_text.stroke-86"),sQuery(id+"FHMxAyK4CFUKdhS_1.wireOp",EDGE,"1cb9c079-ea9b-4899-8069-e0e3048e911d.sketch_text.stroke-87"),sQuery(id+"FHMxAyK4CFUKdhS_1.wireOp",EDGE,"1cb9c079-ea9b-4899-8069-e0e3048e911d.sketch_text.stroke-88"),sQuery(id+"FHMxAyK4CFUKdhS_1.wireOp",EDGE,"1cb9c079-ea9b-4899-8069-e0e3048e911d.sketch_text.stroke-89"),sQuery(id+"FHMxAyK4CFUKdhS_1.wireOp",EDGE,"1cb9c079-ea9b-4899-8069-e0e3048e911d.sketch_text.stroke-90"),sQuery(id+"FHMxAyK4CFUKdhS_1.wireOp",EDGE,"1cb9c079-ea9b-4899-8069-e0e3048e911d.sketch_text.stroke-91"),sQuery(id+"FHMxAyK4CFUKdhS_1.wireOp",EDGE,"1cb9c079-ea9b-4899-8069-e0e3048e911d.sketch_text.stroke-92"),sQuery(id+"FHMxAyK4CFUKdhS_1.wireOp",EDGE,"1cb9c079-ea9b-4899-8069-e0e3048e911d.sketch_text.stroke-93"),sQuery(id+"FHMxAyK4CFUKdhS_1.wireOp",EDGE,"1cb9c079-ea9b-4899-8069-e0e3048e911d.sketch_text.stroke-94"),sQuery(id+"FHMxAyK4CFUKdhS_1.wireOp",EDGE,"1cb9c079-ea9b-4899-8069-e0e3048e911d.sketch_text.stroke-95"),sQuery(id+"FHMxAyK4CFUKdhS_1.wireOp",EDGE,"1cb9c079-ea9b-4899-8069-e0e3048e911d.sketch_text.stroke-96"),sQuery(id+"FHMxAyK4CFUKdhS_1.wireOp",EDGE,"1cb9c079-ea9b-4899-8069-e0e3048e911d.sketch_text.stroke-97"),sQuery(id+"FHMxAyK4CFUKdhS_1.wireOp",EDGE,"1cb9c079-ea9b-4899-8069-e0e3048e911d.sketch_text.stroke-103"),sQuery(id+"FHMxAyK4CFUKdhS_1.wireOp",EDGE,"1cb9c079-ea9b-4899-8069-e0e3048e911d.sketch_text.stroke-104"),sQuery(id+"FHMxAyK4CFUKdhS_1.wireOp",EDGE,"1cb9c079-ea9b-4899-8069-e0e3048e911d.sketch_text.stroke-105"),sQuery(id+"FHMxAyK4CFUKdhS_1.wireOp",EDGE,"1cb9c079-ea9b-4899-8069-e0e3048e911d.sketch_text.stroke-106"),sQuery(id+"FHMxAyK4CFUKdhS_1.wireOp",EDGE,"1cb9c079-ea9b-4899-8069-e0e3048e911d.sketch_text.stroke-107"),sQuery(id+"FHMxAyK4CFUKdhS_1.wireOp",EDGE,"1cb9c079-ea9b-4899-8069-e0e3048e911d.sketch_text.stroke-108"),sQuery(id+"FHMxAyK4CFUKdhS_1.wireOp",EDGE,"1cb9c079-ea9b-4899-8069-e0e3048e911d.sketch_text.stroke-109"),sQuery(id+"FHMxAyK4CFUKdhS_1.wireOp",EDGE,"1cb9c079-ea9b-4899-8069-e0e3048e911d.sketch_text.stroke-110"),sQuery(id+"FHMxAyK4CFUKdhS_1.wireOp",EDGE,"1cb9c079-ea9b-4899-8069-e0e3048e911d.sketch_text.stroke-111"),sQuery(id+"FHMxAyK4CFUKdhS_1.wireOp",EDGE,"1cb9c079-ea9b-4899-8069-e0e3048e911d.sketch_text.stroke-112"),sQuery(id+"FHMxAyK4CFUKdhS_1.wireOp",EDGE,"1cb9c079-ea9b-4899-8069-e0e3048e911d.sketch_text.stroke-113"),sQuery(id+"FHMxAyK4CFUKdhS_1.wireOp",EDGE,"1cb9c079-ea9b-4899-8069-e0e3048e911d.sketch_text.stroke-114"),sQuery(id+"FHMxAyK4CFUKdhS_1.wireOp",EDGE,"1cb9c079-ea9b-4899-8069-e0e3048e911d.sketch_text.stroke-115"),sQuery(id+"FHMxAyK4CFUKdhS_1.wireOp",EDGE,"1cb9c079-ea9b-4899-8069-e0e3048e911d.sketch_text.stroke-116"),sQuery(id+"FHMxAyK4CFUKdhS_1.wireOp",EDGE,"1cb9c079-ea9b-4899-8069-e0e3048e911d.sketch_text.stroke-117"),sQuery(id+"FHMxAyK4CFUKdhS_1.wireOp",EDGE,"1cb9c079-ea9b-4899-8069-e0e3048e911d.sketch_text.stroke-118"),sQuery(id+"FHMxAyK4CFUKdhS_1.wireOp",EDGE,"1cb9c079-ea9b-4899-8069-e0e3048e911d.sketch_text.stroke-119"),sQuery(id+"FHMxAyK4CFUKdhS_1.wireOp",EDGE,"1cb9c079-ea9b-4899-8069-e0e3048e911d.sketch_text.stroke-120"),sQuery(id+"FHMxAyK4CFUKdhS_1.wireOp",EDGE,"1cb9c079-ea9b-4899-8069-e0e3048e911d.sketch_text.stroke-121"),sQuery(id+"FHMxAyK4CFUKdhS_1.wireOp",EDGE,"1cb9c079-ea9b-4899-8069-e0e3048e911d.sketch_text.stroke-122"),sQuery(id+"FHMxAyK4CFUKdhS_1.wireOp",EDGE,"1cb9c079-ea9b-4899-8069-e0e3048e911d.sketch_text.stroke-123"),sQuery(id+"FHMxAyK4CFUKdhS_1.wireOp",EDGE,"1cb9c079-ea9b-4899-8069-e0e3048e911d.sketch_text.stroke-124"),sQuery(id+"FHMxAyK4CFUKdhS_1.wireOp",EDGE,"1cb9c079-ea9b-4899-8069-e0e3048e911d.sketch_text.stroke-125"),sQuery(id+"FHMxAyK4CFUKdhS_1.wireOp",EDGE,"1cb9c079-ea9b-4899-8069-e0e3048e911d.sketch_text.stroke-126"),sQuery(id+"FHMxAyK4CFUKdhS_1.wireOp",EDGE,"1cb9c079-ea9b-4899-8069-e0e3048e911d.sketch_text.stroke-127"),sQuery(id+"FHMxAyK4CFUKdhS_1.wireOp",EDGE,"1cb9c079-ea9b-4899-8069-e0e3048e911d.sketch_text.stroke-128"),sQuery(id+"FHMxAyK4CFUKdhS_1.wireOp",EDGE,"1cb9c079-ea9b-4899-8069-e0e3048e911d.sketch_text.stroke-129"),sQuery(id+"FHMxAyK4CFUKdhS_1.wireOp",EDGE,"1cb9c079-ea9b-4899-8069-e0e3048e911d.sketch_text.stroke-130"),sQuery(id+"FHMxAyK4CFUKdhS_1.wireOp",EDGE,"1cb9c079-ea9b-4899-8069-e0e3048e911d.sketch_text.stroke-131"),sQuery(id+"FHMxAyK4CFUKdhS_1.wireOp",EDGE,"1cb9c079-ea9b-4899-8069-e0e3048e911d.sketch_text.stroke-132"),sQuery(id+"FHMxAyK4CFUKdhS_1.wireOp",EDGE,"1cb9c079-ea9b-4899-8069-e0e3048e911d.sketch_text.stroke-133"),sQuery(id+"FHMxAyK4CFUKdhS_1.wireOp",EDGE,"1cb9c079-ea9b-4899-8069-e0e3048e911d.sketch_text.stroke-134"),sQuery(id+"FHMxAyK4CFUKdhS_1.wireOp",EDGE,"1cb9c079-ea9b-4899-8069-e0e3048e911d.sketch_text.stroke-135"),sQuery(id+"FHMxAyK4CFUKdhS_1.wireOp",EDGE,"1cb9c079-ea9b-4899-8069-e0e3048e911d.sketch_text.stroke-136"),sQuery(id+"FHMxAyK4CFUKdhS_1.wireOp",EDGE,"1cb9c079-ea9b-4899-8069-e0e3048e911d.sketch_text.stroke-137"),sQuery(id+"FHMxAyK4CFUKdhS_1.wireOp",EDGE,"1cb9c079-ea9b-4899-8069-e0e3048e911d.sketch_text.stroke-138"),sQuery(id+"FHMxAyK4CFUKdhS_1.wireOp",EDGE,"1cb9c079-ea9b-4899-8069-e0e3048e911d.sketch_text.stroke-139"),sQuery(id+"FHMxAyK4CFUKdhS_1.wireOp",EDGE,"1cb9c079-ea9b-4899-8069-e0e3048e911d.sketch_text.stroke-140"),sQuery(id+"FHMxAyK4CFUKdhS_1.wireOp",EDGE,"1cb9c079-ea9b-4899-8069-e0e3048e911d.sketch_text.stroke-141"),sQuery(id+"FHMxAyK4CFUKdhS_1.wireOp",EDGE,"1cb9c079-ea9b-4899-8069-e0e3048e911d.sketch_text.stroke-142"),sQuery(id+"FHMxAyK4CFUKdhS_1.wireOp",EDGE,"1cb9c079-ea9b-4899-8069-e0e3048e911d.sketch_text.stroke-143"),sQuery(id+"FHMxAyK4CFUKdhS_1.wireOp",EDGE,"1cb9c079-ea9b-4899-8069-e0e3048e911d.sketch_text.stroke-144"),sQuery(id+"FHMxAyK4CFUKdhS_1.wireOp",EDGE,"1cb9c079-ea9b-4899-8069-e0e3048e911d.sketch_text.stroke-145"),sQuery(id+"FHMxAyK4CFUKdhS_1.wireOp",EDGE,"1cb9c079-ea9b-4899-8069-e0e3048e911d.sketch_text.stroke-146"),sQuery(id+"FHMxAyK4CFUKdhS_1.wireOp",EDGE,"1cb9c079-ea9b-4899-8069-e0e3048e911d.sketch_text.stroke-147"),sQuery(id+"FHMxAyK4CFUKdhS_1.wireOp",EDGE,"1cb9c079-ea9b-4899-8069-e0e3048e911d.sketch_text.stroke-148"),sQuery(id+"FHMxAyK4CFUKdhS_1.wireOp",EDGE,"1cb9c079-ea9b-4899-8069-e0e3048e911d.sketch_text.stroke-149"),sQuery(id+"FHMxAyK4CFUKdhS_1.wireOp",EDGE,"1cb9c079-ea9b-4899-8069-e0e3048e911d.sketch_text.stroke-150"),sQuery(id+"FHMxAyK4CFUKdhS_1.wireOp",EDGE,"1cb9c079-ea9b-4899-8069-e0e3048e911d.sketch_text.stroke-151"),sQuery(id+"FHMxAyK4CFUKdhS_1.wireOp",EDGE,"1cb9c079-ea9b-4899-8069-e0e3048e911d.sketch_text.stroke-152"),sQuery(id+"FHMxAyK4CFUKdhS_1.wireOp",EDGE,"1cb9c079-ea9b-4899-8069-e0e3048e911d.sketch_text.stroke-153"),sQuery(id+"FHMxAyK4CFUKdhS_1.wireOp",EDGE,"1cb9c079-ea9b-4899-8069-e0e3048e911d.sketch_text.stroke-159"),sQuery(id+"FHMxAyK4CFUKdhS_1.wireOp",EDGE,"1cb9c079-ea9b-4899-8069-e0e3048e911d.sketch_text.stroke-160"),sQuery(id+"FHMxAyK4CFUKdhS_1.wireOp",EDGE,"1cb9c079-ea9b-4899-8069-e0e3048e911d.sketch_text.stroke-161"),sQuery(id+"FHMxAyK4CFUKdhS_1.wireOp",EDGE,"1cb9c079-ea9b-4899-8069-e0e3048e911d.sketch_text.stroke-162"),sQuery(id+"FHMxAyK4CFUKdhS_1.wireOp",EDGE,"1cb9c079-ea9b-4899-8069-e0e3048e911d.sketch_text.stroke-163"),sQuery(id+"FHMxAyK4CFUKdhS_1.wireOp",EDGE,"1cb9c079-ea9b-4899-8069-e0e3048e911d.sketch_text.stroke-164"),sQuery(id+"FHMxAyK4CFUKdhS_1.wireOp",EDGE,"1cb9c079-ea9b-4899-8069-e0e3048e911d.sketch_text.stroke-165"),sQuery(id+"FHMxAyK4CFUKdhS_1.wireOp",EDGE,"1cb9c079-ea9b-4899-8069-e0e3048e911d.sketch_text.stroke-166"),sQuery(id+"FHMxAyK4CFUKdhS_1.wireOp",EDGE,"1cb9c079-ea9b-4899-8069-e0e3048e911d.sketch_text.stroke-167"),sQuery(id+"FHMxAyK4CFUKdhS_1.wireOp",EDGE,"1cb9c079-ea9b-4899-8069-e0e3048e911d.sketch_text.stroke-168"),sQuery(id+"FHMxAyK4CFUKdhS_1.wireOp",EDGE,"1cb9c079-ea9b-4899-8069-e0e3048e911d.sketch_text.stroke-169"),sQuery(id+"FHMxAyK4CFUKdhS_1.wireOp",EDGE,"1cb9c079-ea9b-4899-8069-e0e3048e911d.sketch_text.stroke-170"),sQuery(id+"FHMxAyK4CFUKdhS_1.wireOp",EDGE,"1cb9c079-ea9b-4899-8069-e0e3048e911d.sketch_text.stroke-171"),sQuery(id+"FHMxAyK4CFUKdhS_1.wireOp",EDGE,"1cb9c079-ea9b-4899-8069-e0e3048e911d.sketch_text.stroke-172"),sQuery(id+"FHMxAyK4CFUKdhS_1.wireOp",EDGE,"1cb9c079-ea9b-4899-8069-e0e3048e911d.sketch_text.stroke-173"),sQuery(id+"FHMxAyK4CFUKdhS_1.wireOp",EDGE,"1cb9c079-ea9b-4899-8069-e0e3048e911d.sketch_text.stroke-174"),sQuery(id+"FHMxAyK4CFUKdhS_1.wireOp",EDGE,"1cb9c079-ea9b-4899-8069-e0e3048e911d.sketch_text.stroke-175"),sQuery(id+"FHMxAyK4CFUKdhS_1.wireOp",EDGE,"1cb9c079-ea9b-4899-8069-e0e3048e911d.sketch_text.stroke-176"),sQuery(id+"FHMxAyK4CFUKdhS_1.wireOp",EDGE,"1cb9c079-ea9b-4899-8069-e0e3048e911d.sketch_text.stroke-177"),sQuery(id+"FHMxAyK4CFUKdhS_1.wireOp",EDGE,"1cb9c079-ea9b-4899-8069-e0e3048e911d.sketch_text.stroke-178"),sQuery(id+"FHMxAyK4CFUKdhS_1.wireOp",EDGE,"1cb9c079-ea9b-4899-8069-e0e3048e911d.sketch_text.stroke-179"),sQuery(id+"FHMxAyK4CFUKdhS_1.wireOp",EDGE,"1cb9c079-ea9b-4899-8069-e0e3048e911d.sketch_text.stroke-180"),subQ0,subQ2])],"isStart":true}),makeQuery(id+"F3.opExtrude","SWEPT_FACE",FACE,{"disambiguationData":[OSD([subQ2])]})])],"derivedFrom":makeQuery(id+"F3.opExtrude","CAP_EDGE",EDGE,{"disambiguationData":[OSD([subQ2])],"isStart":true})});}
            var Q16;
            {var subQ0=sQuery(id+"F0.wireOp",EDGE,"E0.top");var subQ1=sQuery(id+"F0.wireOp",EDGE,"E0.bottom");var subQ2=sQuery(id+"F2.wireOp",EDGE,"727ac2c1-f511-4829-95a7-a443ef16a4cd");Q16=makeQuery(id+"F3.boolean.opBoolean","SPLIT",EDGE,{"disambiguationData":[TD([makeQuery(id+"F1.opExtrude","CAP_FACE",FACE,{"disambiguationData":[OSD([subQ1,subQ0,sQuery(id+"F0.wireOp",EDGE,"E0.left"),sQuery(id+"F0.wireOp",EDGE,"E0.right")])],"isStart":false}),makeQuery(id+"F1.opExtrude","SWEPT_FACE",FACE,{"disambiguationData":[OSD([subQ0])]}),makeQuery(id+"F3.opExtrude","CAP_FACE",FACE,{"disambiguationData":[OSD([subQ1,sQuery(id+"FQ5JFwxVdaqARUP_1.wireOp",EDGE,"fcba4419-a2ee-464f-be9d-58f11bf3418b.sketch_text.stroke-0"),sQuery(id+"FQ5JFwxVdaqARUP_1.wireOp",EDGE,"fcba4419-a2ee-464f-be9d-58f11bf3418b.sketch_text.stroke-1"),sQuery(id+"FQ5JFwxVdaqARUP_1.wireOp",EDGE,"fcba4419-a2ee-464f-be9d-58f11bf3418b.sketch_text.stroke-2"),sQuery(id+"FQ5JFwxVdaqARUP_1.wireOp",EDGE,"fcba4419-a2ee-464f-be9d-58f11bf3418b.sketch_text.stroke-3"),sQuery(id+"FQ5JFwxVdaqARUP_1.wireOp",EDGE,"fcba4419-a2ee-464f-be9d-58f11bf3418b.sketch_text.stroke-4"),sQuery(id+"FQ5JFwxVdaqARUP_1.wireOp",EDGE,"fcba4419-a2ee-464f-be9d-58f11bf3418b.sketch_text.stroke-5"),sQuery(id+"FQ5JFwxVdaqARUP_1.wireOp",EDGE,"fcba4419-a2ee-464f-be9d-58f11bf3418b.sketch_text.stroke-6"),sQuery(id+"FQ5JFwxVdaqARUP_1.wireOp",EDGE,"fcba4419-a2ee-464f-be9d-58f11bf3418b.sketch_text.stroke-7"),sQuery(id+"FQ5JFwxVdaqARUP_1.wireOp",EDGE,"fcba4419-a2ee-464f-be9d-58f11bf3418b.sketch_text.stroke-8"),sQuery(id+"FQ5JFwxVdaqARUP_1.wireOp",EDGE,"fcba4419-a2ee-464f-be9d-58f11bf3418b.sketch_text.stroke-9"),sQuery(id+"FQ5JFwxVdaqARUP_1.wireOp",EDGE,"fcba4419-a2ee-464f-be9d-58f11bf3418b.sketch_text.stroke-10"),sQuery(id+"FQ5JFwxVdaqARUP_1.wireOp",EDGE,"fcba4419-a2ee-464f-be9d-58f11bf3418b.sketch_text.stroke-11"),sQuery(id+"FQ5JFwxVdaqARUP_1.wireOp",EDGE,"fcba4419-a2ee-464f-be9d-58f11bf3418b.sketch_text.stroke-12"),sQuery(id+"FQ5JFwxVdaqARUP_1.wireOp",EDGE,"fcba4419-a2ee-464f-be9d-58f11bf3418b.sketch_text.stroke-13"),sQuery(id+"FQ5JFwxVdaqARUP_1.wireOp",EDGE,"fcba4419-a2ee-464f-be9d-58f11bf3418b.sketch_text.stroke-14"),sQuery(id+"FQ5JFwxVdaqARUP_1.wireOp",EDGE,"fcba4419-a2ee-464f-be9d-58f11bf3418b.sketch_text.stroke-15"),sQuery(id+"FQ5JFwxVdaqARUP_1.wireOp",EDGE,"fcba4419-a2ee-464f-be9d-58f11bf3418b.sketch_text.stroke-16"),sQuery(id+"FQ5JFwxVdaqARUP_1.wireOp",EDGE,"fcba4419-a2ee-464f-be9d-58f11bf3418b.sketch_text.stroke-17"),sQuery(id+"FQ5JFwxVdaqARUP_1.wireOp",EDGE,"fcba4419-a2ee-464f-be9d-58f11bf3418b.sketch_text.stroke-18"),sQuery(id+"FQ5JFwxVdaqARUP_1.wireOp",EDGE,"fcba4419-a2ee-464f-be9d-58f11bf3418b.sketch_text.stroke-19"),sQuery(id+"FQ5JFwxVdaqARUP_1.wireOp",EDGE,"fcba4419-a2ee-464f-be9d-58f11bf3418b.sketch_text.stroke-20"),sQuery(id+"FQ5JFwxVdaqARUP_1.wireOp",EDGE,"fcba4419-a2ee-464f-be9d-58f11bf3418b.sketch_text.stroke-21"),sQuery(id+"FQ5JFwxVdaqARUP_1.wireOp",EDGE,"fcba4419-a2ee-464f-be9d-58f11bf3418b.sketch_text.stroke-22"),sQuery(id+"FQ5JFwxVdaqARUP_1.wireOp",EDGE,"fcba4419-a2ee-464f-be9d-58f11bf3418b.sketch_text.stroke-23"),sQuery(id+"FQ5JFwxVdaqARUP_1.wireOp",EDGE,"fcba4419-a2ee-464f-be9d-58f11bf3418b.sketch_text.stroke-24"),sQuery(id+"FQ5JFwxVdaqARUP_1.wireOp",EDGE,"fcba4419-a2ee-464f-be9d-58f11bf3418b.sketch_text.stroke-25"),sQuery(id+"FQ5JFwxVdaqARUP_1.wireOp",EDGE,"fcba4419-a2ee-464f-be9d-58f11bf3418b.sketch_text.stroke-26"),sQuery(id+"FQ5JFwxVdaqARUP_1.wireOp",EDGE,"fcba4419-a2ee-464f-be9d-58f11bf3418b.sketch_text.stroke-27"),sQuery(id+"FQ5JFwxVdaqARUP_1.wireOp",EDGE,"fcba4419-a2ee-464f-be9d-58f11bf3418b.sketch_text.stroke-28"),sQuery(id+"FQ5JFwxVdaqARUP_1.wireOp",EDGE,"fcba4419-a2ee-464f-be9d-58f11bf3418b.sketch_text.stroke-29"),sQuery(id+"FQ5JFwxVdaqARUP_1.wireOp",EDGE,"fcba4419-a2ee-464f-be9d-58f11bf3418b.sketch_text.stroke-30"),sQuery(id+"FQ5JFwxVdaqARUP_1.wireOp",EDGE,"fcba4419-a2ee-464f-be9d-58f11bf3418b.sketch_text.stroke-31"),sQuery(id+"FQ5JFwxVdaqARUP_1.wireOp",EDGE,"fcba4419-a2ee-464f-be9d-58f11bf3418b.sketch_text.stroke-32"),sQuery(id+"FQ5JFwxVdaqARUP_1.wireOp",EDGE,"fcba4419-a2ee-464f-be9d-58f11bf3418b.sketch_text.stroke-33"),sQuery(id+"FQ5JFwxVdaqARUP_1.wireOp",EDGE,"fcba4419-a2ee-464f-be9d-58f11bf3418b.sketch_text.stroke-34"),sQuery(id+"FQ5JFwxVdaqARUP_1.wireOp",EDGE,"fcba4419-a2ee-464f-be9d-58f11bf3418b.sketch_text.stroke-35"),sQuery(id+"FQ5JFwxVdaqARUP_1.wireOp",EDGE,"fcba4419-a2ee-464f-be9d-58f11bf3418b.sketch_text.stroke-36"),sQuery(id+"FQ5JFwxVdaqARUP_1.wireOp",EDGE,"fcba4419-a2ee-464f-be9d-58f11bf3418b.sketch_text.stroke-37"),sQuery(id+"FQ5JFwxVdaqARUP_1.wireOp",EDGE,"fcba4419-a2ee-464f-be9d-58f11bf3418b.sketch_text.stroke-38"),sQuery(id+"FQ5JFwxVdaqARUP_1.wireOp",EDGE,"fcba4419-a2ee-464f-be9d-58f11bf3418b.sketch_text.stroke-39"),sQuery(id+"FQ5JFwxVdaqARUP_1.wireOp",EDGE,"fcba4419-a2ee-464f-be9d-58f11bf3418b.sketch_text.stroke-40"),sQuery(id+"FQ5JFwxVdaqARUP_1.wireOp",EDGE,"fcba4419-a2ee-464f-be9d-58f11bf3418b.sketch_text.stroke-41"),sQuery(id+"FQ5JFwxVdaqARUP_1.wireOp",EDGE,"fcba4419-a2ee-464f-be9d-58f11bf3418b.sketch_text.stroke-42"),sQuery(id+"FQ5JFwxVdaqARUP_1.wireOp",EDGE,"fcba4419-a2ee-464f-be9d-58f11bf3418b.sketch_text.stroke-43"),sQuery(id+"FQ5JFwxVdaqARUP_1.wireOp",EDGE,"fcba4419-a2ee-464f-be9d-58f11bf3418b.sketch_text.stroke-44"),sQuery(id+"FQ5JFwxVdaqARUP_1.wireOp",EDGE,"fcba4419-a2ee-464f-be9d-58f11bf3418b.sketch_text.stroke-45"),sQuery(id+"FQ5JFwxVdaqARUP_1.wireOp",EDGE,"fcba4419-a2ee-464f-be9d-58f11bf3418b.sketch_text.stroke-46"),sQuery(id+"FQ5JFwxVdaqARUP_1.wireOp",EDGE,"fcba4419-a2ee-464f-be9d-58f11bf3418b.sketch_text.stroke-47"),sQuery(id+"FQ5JFwxVdaqARUP_1.wireOp",EDGE,"fcba4419-a2ee-464f-be9d-58f11bf3418b.sketch_text.stroke-48"),sQuery(id+"FQ5JFwxVdaqARUP_1.wireOp",EDGE,"fcba4419-a2ee-464f-be9d-58f11bf3418b.sketch_text.stroke-49"),sQuery(id+"FQ5JFwxVdaqARUP_1.wireOp",EDGE,"fcba4419-a2ee-464f-be9d-58f11bf3418b.sketch_text.stroke-50"),sQuery(id+"FQ5JFwxVdaqARUP_1.wireOp",EDGE,"fcba4419-a2ee-464f-be9d-58f11bf3418b.sketch_text.stroke-51"),sQuery(id+"FQ5JFwxVdaqARUP_1.wireOp",EDGE,"fcba4419-a2ee-464f-be9d-58f11bf3418b.sketch_text.stroke-52"),sQuery(id+"FQ5JFwxVdaqARUP_1.wireOp",EDGE,"fcba4419-a2ee-464f-be9d-58f11bf3418b.sketch_text.stroke-53"),sQuery(id+"FQ5JFwxVdaqARUP_1.wireOp",EDGE,"fcba4419-a2ee-464f-be9d-58f11bf3418b.sketch_text.stroke-54"),sQuery(id+"FQ5JFwxVdaqARUP_1.wireOp",EDGE,"fcba4419-a2ee-464f-be9d-58f11bf3418b.sketch_text.stroke-55"),sQuery(id+"FQ5JFwxVdaqARUP_1.wireOp",EDGE,"fcba4419-a2ee-464f-be9d-58f11bf3418b.sketch_text.stroke-56"),sQuery(id+"FQ5JFwxVdaqARUP_1.wireOp",EDGE,"fcba4419-a2ee-464f-be9d-58f11bf3418b.sketch_text.stroke-57"),sQuery(id+"FQ5JFwxVdaqARUP_1.wireOp",EDGE,"fcba4419-a2ee-464f-be9d-58f11bf3418b.sketch_text.stroke-58"),sQuery(id+"FQ5JFwxVdaqARUP_1.wireOp",EDGE,"fcba4419-a2ee-464f-be9d-58f11bf3418b.sketch_text.stroke-59"),sQuery(id+"FQ5JFwxVdaqARUP_1.wireOp",EDGE,"fcba4419-a2ee-464f-be9d-58f11bf3418b.sketch_text.stroke-60"),sQuery(id+"FQ5JFwxVdaqARUP_1.wireOp",EDGE,"fcba4419-a2ee-464f-be9d-58f11bf3418b.sketch_text.stroke-61"),sQuery(id+"FQ5JFwxVdaqARUP_1.wireOp",EDGE,"fcba4419-a2ee-464f-be9d-58f11bf3418b.sketch_text.stroke-62"),sQuery(id+"FQ5JFwxVdaqARUP_1.wireOp",EDGE,"fcba4419-a2ee-464f-be9d-58f11bf3418b.sketch_text.stroke-63"),sQuery(id+"FQ5JFwxVdaqARUP_1.wireOp",EDGE,"fcba4419-a2ee-464f-be9d-58f11bf3418b.sketch_text.stroke-64"),sQuery(id+"FQ5JFwxVdaqARUP_1.wireOp",EDGE,"fcba4419-a2ee-464f-be9d-58f11bf3418b.sketch_text.stroke-65"),sQuery(id+"FQ5JFwxVdaqARUP_1.wireOp",EDGE,"fcba4419-a2ee-464f-be9d-58f11bf3418b.sketch_text.stroke-66"),sQuery(id+"FQ5JFwxVdaqARUP_1.wireOp",EDGE,"fcba4419-a2ee-464f-be9d-58f11bf3418b.sketch_text.stroke-67"),sQuery(id+"FQ5JFwxVdaqARUP_1.wireOp",EDGE,"fcba4419-a2ee-464f-be9d-58f11bf3418b.sketch_text.stroke-68"),sQuery(id+"FQ5JFwxVdaqARUP_1.wireOp",EDGE,"fcba4419-a2ee-464f-be9d-58f11bf3418b.sketch_text.stroke-69"),sQuery(id+"FQ5JFwxVdaqARUP_1.wireOp",EDGE,"fcba4419-a2ee-464f-be9d-58f11bf3418b.sketch_text.stroke-70"),sQuery(id+"FQ5JFwxVdaqARUP_1.wireOp",EDGE,"fcba4419-a2ee-464f-be9d-58f11bf3418b.sketch_text.stroke-71"),sQuery(id+"FQ5JFwxVdaqARUP_1.wireOp",EDGE,"fcba4419-a2ee-464f-be9d-58f11bf3418b.sketch_text.stroke-72"),sQuery(id+"FQ5JFwxVdaqARUP_1.wireOp",EDGE,"fcba4419-a2ee-464f-be9d-58f11bf3418b.sketch_text.stroke-73"),sQuery(id+"FQ5JFwxVdaqARUP_1.wireOp",EDGE,"fcba4419-a2ee-464f-be9d-58f11bf3418b.sketch_text.stroke-74"),sQuery(id+"FQ5JFwxVdaqARUP_1.wireOp",EDGE,"fcba4419-a2ee-464f-be9d-58f11bf3418b.sketch_text.stroke-75"),sQuery(id+"FQ5JFwxVdaqARUP_1.wireOp",EDGE,"fcba4419-a2ee-464f-be9d-58f11bf3418b.sketch_text.stroke-76"),sQuery(id+"FQ5JFwxVdaqARUP_1.wireOp",EDGE,"fcba4419-a2ee-464f-be9d-58f11bf3418b.sketch_text.stroke-77"),sQuery(id+"FQ5JFwxVdaqARUP_1.wireOp",EDGE,"fcba4419-a2ee-464f-be9d-58f11bf3418b.sketch_text.stroke-78"),sQuery(id+"FQ5JFwxVdaqARUP_1.wireOp",EDGE,"fcba4419-a2ee-464f-be9d-58f11bf3418b.sketch_text.stroke-79"),sQuery(id+"FQ5JFwxVdaqARUP_1.wireOp",EDGE,"fcba4419-a2ee-464f-be9d-58f11bf3418b.sketch_text.stroke-80"),sQuery(id+"FQ5JFwxVdaqARUP_1.wireOp",EDGE,"fcba4419-a2ee-464f-be9d-58f11bf3418b.sketch_text.stroke-81"),sQuery(id+"FQ5JFwxVdaqARUP_1.wireOp",EDGE,"fcba4419-a2ee-464f-be9d-58f11bf3418b.sketch_text.stroke-82"),sQuery(id+"FQ5JFwxVdaqARUP_1.wireOp",EDGE,"fcba4419-a2ee-464f-be9d-58f11bf3418b.sketch_text.stroke-83"),sQuery(id+"FQ5JFwxVdaqARUP_1.wireOp",EDGE,"fcba4419-a2ee-464f-be9d-58f11bf3418b.sketch_text.stroke-84"),sQuery(id+"FQ5JFwxVdaqARUP_1.wireOp",EDGE,"fcba4419-a2ee-464f-be9d-58f11bf3418b.sketch_text.stroke-85"),sQuery(id+"FQ5JFwxVdaqARUP_1.wireOp",EDGE,"fcba4419-a2ee-464f-be9d-58f11bf3418b.sketch_text.stroke-86"),sQuery(id+"FQ5JFwxVdaqARUP_1.wireOp",EDGE,"fcba4419-a2ee-464f-be9d-58f11bf3418b.sketch_text.stroke-87"),sQuery(id+"FQ5JFwxVdaqARUP_1.wireOp",EDGE,"fcba4419-a2ee-464f-be9d-58f11bf3418b.sketch_text.stroke-88"),sQuery(id+"FQ5JFwxVdaqARUP_1.wireOp",EDGE,"fcba4419-a2ee-464f-be9d-58f11bf3418b.sketch_text.stroke-89"),sQuery(id+"FQ5JFwxVdaqARUP_1.wireOp",EDGE,"fcba4419-a2ee-464f-be9d-58f11bf3418b.sketch_text.stroke-90"),sQuery(id+"FQ5JFwxVdaqARUP_1.wireOp",EDGE,"fcba4419-a2ee-464f-be9d-58f11bf3418b.sketch_text.stroke-91"),sQuery(id+"FQ5JFwxVdaqARUP_1.wireOp",EDGE,"fcba4419-a2ee-464f-be9d-58f11bf3418b.sketch_text.stroke-92"),sQuery(id+"FQ5JFwxVdaqARUP_1.wireOp",EDGE,"fcba4419-a2ee-464f-be9d-58f11bf3418b.sketch_text.stroke-93"),sQuery(id+"FQ5JFwxVdaqARUP_1.wireOp",EDGE,"fcba4419-a2ee-464f-be9d-58f11bf3418b.sketch_text.stroke-94"),sQuery(id+"FQ5JFwxVdaqARUP_1.wireOp",EDGE,"fcba4419-a2ee-464f-be9d-58f11bf3418b.sketch_text.stroke-95"),sQuery(id+"FQ5JFwxVdaqARUP_1.wireOp",EDGE,"fcba4419-a2ee-464f-be9d-58f11bf3418b.sketch_text.stroke-96"),sQuery(id+"FQ5JFwxVdaqARUP_1.wireOp",EDGE,"fcba4419-a2ee-464f-be9d-58f11bf3418b.sketch_text.stroke-97"),sQuery(id+"FQ5JFwxVdaqARUP_1.wireOp",EDGE,"fcba4419-a2ee-464f-be9d-58f11bf3418b.sketch_text.stroke-98"),sQuery(id+"FQ5JFwxVdaqARUP_1.wireOp",EDGE,"fcba4419-a2ee-464f-be9d-58f11bf3418b.sketch_text.stroke-99"),sQuery(id+"FQ5JFwxVdaqARUP_1.wireOp",EDGE,"fcba4419-a2ee-464f-be9d-58f11bf3418b.sketch_text.stroke-100"),sQuery(id+"FQ5JFwxVdaqARUP_1.wireOp",EDGE,"fcba4419-a2ee-464f-be9d-58f11bf3418b.sketch_text.stroke-101"),sQuery(id+"FQ5JFwxVdaqARUP_1.wireOp",EDGE,"fcba4419-a2ee-464f-be9d-58f11bf3418b.sketch_text.stroke-102"),sQuery(id+"FQ5JFwxVdaqARUP_1.wireOp",EDGE,"fcba4419-a2ee-464f-be9d-58f11bf3418b.sketch_text.stroke-103"),sQuery(id+"FQ5JFwxVdaqARUP_1.wireOp",EDGE,"fcba4419-a2ee-464f-be9d-58f11bf3418b.sketch_text.stroke-104"),sQuery(id+"FQ5JFwxVdaqARUP_1.wireOp",EDGE,"fcba4419-a2ee-464f-be9d-58f11bf3418b.sketch_text.stroke-105"),sQuery(id+"FQ5JFwxVdaqARUP_1.wireOp",EDGE,"fcba4419-a2ee-464f-be9d-58f11bf3418b.sketch_text.stroke-106"),sQuery(id+"FQ5JFwxVdaqARUP_1.wireOp",EDGE,"fcba4419-a2ee-464f-be9d-58f11bf3418b.sketch_text.stroke-107"),sQuery(id+"FQ5JFwxVdaqARUP_1.wireOp",EDGE,"fcba4419-a2ee-464f-be9d-58f11bf3418b.sketch_text.stroke-108"),sQuery(id+"FQ5JFwxVdaqARUP_1.wireOp",EDGE,"fcba4419-a2ee-464f-be9d-58f11bf3418b.sketch_text.stroke-109"),sQuery(id+"FQ5JFwxVdaqARUP_1.wireOp",EDGE,"fcba4419-a2ee-464f-be9d-58f11bf3418b.sketch_text.stroke-110"),sQuery(id+"FQ5JFwxVdaqARUP_1.wireOp",EDGE,"fcba4419-a2ee-464f-be9d-58f11bf3418b.sketch_text.stroke-111"),sQuery(id+"FQ5JFwxVdaqARUP_1.wireOp",EDGE,"fcba4419-a2ee-464f-be9d-58f11bf3418b.sketch_text.stroke-112"),sQuery(id+"FQ5JFwxVdaqARUP_1.wireOp",EDGE,"fcba4419-a2ee-464f-be9d-58f11bf3418b.sketch_text.stroke-113"),sQuery(id+"FQ5JFwxVdaqARUP_1.wireOp",EDGE,"fcba4419-a2ee-464f-be9d-58f11bf3418b.sketch_text.stroke-114"),sQuery(id+"FQ5JFwxVdaqARUP_1.wireOp",EDGE,"fcba4419-a2ee-464f-be9d-58f11bf3418b.sketch_text.stroke-115"),sQuery(id+"FQ5JFwxVdaqARUP_1.wireOp",EDGE,"fcba4419-a2ee-464f-be9d-58f11bf3418b.sketch_text.stroke-116"),sQuery(id+"FQ5JFwxVdaqARUP_1.wireOp",EDGE,"fcba4419-a2ee-464f-be9d-58f11bf3418b.sketch_text.stroke-117"),sQuery(id+"FQ5JFwxVdaqARUP_1.wireOp",EDGE,"fcba4419-a2ee-464f-be9d-58f11bf3418b.sketch_text.stroke-118"),sQuery(id+"FQ5JFwxVdaqARUP_1.wireOp",EDGE,"fcba4419-a2ee-464f-be9d-58f11bf3418b.sketch_text.stroke-119"),sQuery(id+"FQ5JFwxVdaqARUP_1.wireOp",EDGE,"fcba4419-a2ee-464f-be9d-58f11bf3418b.sketch_text.stroke-120"),sQuery(id+"FQ5JFwxVdaqARUP_1.wireOp",EDGE,"fcba4419-a2ee-464f-be9d-58f11bf3418b.sketch_text.stroke-121"),sQuery(id+"FQ5JFwxVdaqARUP_1.wireOp",EDGE,"fcba4419-a2ee-464f-be9d-58f11bf3418b.sketch_text.stroke-122"),sQuery(id+"FQ5JFwxVdaqARUP_1.wireOp",EDGE,"fcba4419-a2ee-464f-be9d-58f11bf3418b.sketch_text.stroke-123"),sQuery(id+"FQ5JFwxVdaqARUP_1.wireOp",EDGE,"fcba4419-a2ee-464f-be9d-58f11bf3418b.sketch_text.stroke-124"),sQuery(id+"FQ5JFwxVdaqARUP_1.wireOp",EDGE,"fcba4419-a2ee-464f-be9d-58f11bf3418b.sketch_text.stroke-125"),sQuery(id+"FQ5JFwxVdaqARUP_1.wireOp",EDGE,"fcba4419-a2ee-464f-be9d-58f11bf3418b.sketch_text.stroke-126"),sQuery(id+"FQ5JFwxVdaqARUP_1.wireOp",EDGE,"fcba4419-a2ee-464f-be9d-58f11bf3418b.sketch_text.stroke-127"),sQuery(id+"FQ5JFwxVdaqARUP_1.wireOp",EDGE,"fcba4419-a2ee-464f-be9d-58f11bf3418b.sketch_text.stroke-128"),sQuery(id+"FQ5JFwxVdaqARUP_1.wireOp",EDGE,"fcba4419-a2ee-464f-be9d-58f11bf3418b.sketch_text.stroke-129"),sQuery(id+"FQ5JFwxVdaqARUP_1.wireOp",EDGE,"fcba4419-a2ee-464f-be9d-58f11bf3418b.sketch_text.stroke-130"),sQuery(id+"FQ5JFwxVdaqARUP_1.wireOp",EDGE,"fcba4419-a2ee-464f-be9d-58f11bf3418b.sketch_text.stroke-131"),sQuery(id+"FQ5JFwxVdaqARUP_1.wireOp",EDGE,"fcba4419-a2ee-464f-be9d-58f11bf3418b.sketch_text.stroke-132"),sQuery(id+"FQ5JFwxVdaqARUP_1.wireOp",EDGE,"fcba4419-a2ee-464f-be9d-58f11bf3418b.sketch_text.stroke-133"),sQuery(id+"FQ5JFwxVdaqARUP_1.wireOp",EDGE,"fcba4419-a2ee-464f-be9d-58f11bf3418b.sketch_text.stroke-134"),sQuery(id+"FQ5JFwxVdaqARUP_1.wireOp",EDGE,"fcba4419-a2ee-464f-be9d-58f11bf3418b.sketch_text.stroke-135"),sQuery(id+"FQ5JFwxVdaqARUP_1.wireOp",EDGE,"fcba4419-a2ee-464f-be9d-58f11bf3418b.sketch_text.stroke-136"),sQuery(id+"FQ5JFwxVdaqARUP_1.wireOp",EDGE,"fcba4419-a2ee-464f-be9d-58f11bf3418b.sketch_text.stroke-137"),sQuery(id+"FQ5JFwxVdaqARUP_1.wireOp",EDGE,"fcba4419-a2ee-464f-be9d-58f11bf3418b.sketch_text.stroke-138"),sQuery(id+"FQ5JFwxVdaqARUP_1.wireOp",EDGE,"fcba4419-a2ee-464f-be9d-58f11bf3418b.sketch_text.stroke-139"),sQuery(id+"FQ5JFwxVdaqARUP_1.wireOp",EDGE,"fcba4419-a2ee-464f-be9d-58f11bf3418b.sketch_text.stroke-140"),sQuery(id+"FQ5JFwxVdaqARUP_1.wireOp",EDGE,"fcba4419-a2ee-464f-be9d-58f11bf3418b.sketch_text.stroke-141"),sQuery(id+"FQ5JFwxVdaqARUP_1.wireOp",EDGE,"fcba4419-a2ee-464f-be9d-58f11bf3418b.sketch_text.stroke-142"),sQuery(id+"FQ5JFwxVdaqARUP_1.wireOp",EDGE,"fcba4419-a2ee-464f-be9d-58f11bf3418b.sketch_text.stroke-143"),sQuery(id+"FQ5JFwxVdaqARUP_1.wireOp",EDGE,"fcba4419-a2ee-464f-be9d-58f11bf3418b.sketch_text.stroke-144"),sQuery(id+"FQ5JFwxVdaqARUP_1.wireOp",EDGE,"fcba4419-a2ee-464f-be9d-58f11bf3418b.sketch_text.stroke-145"),sQuery(id+"FQ5JFwxVdaqARUP_1.wireOp",EDGE,"fcba4419-a2ee-464f-be9d-58f11bf3418b.sketch_text.stroke-146"),sQuery(id+"FQ5JFwxVdaqARUP_1.wireOp",EDGE,"fcba4419-a2ee-464f-be9d-58f11bf3418b.sketch_text.stroke-147"),sQuery(id+"FQ5JFwxVdaqARUP_1.wireOp",EDGE,"fcba4419-a2ee-464f-be9d-58f11bf3418b.sketch_text.stroke-148"),sQuery(id+"FQ5JFwxVdaqARUP_1.wireOp",EDGE,"fcba4419-a2ee-464f-be9d-58f11bf3418b.sketch_text.stroke-149"),sQuery(id+"FQ5JFwxVdaqARUP_1.wireOp",EDGE,"fcba4419-a2ee-464f-be9d-58f11bf3418b.sketch_text.stroke-150"),sQuery(id+"FQ5JFwxVdaqARUP_1.wireOp",EDGE,"fcba4419-a2ee-464f-be9d-58f11bf3418b.sketch_text.stroke-151"),sQuery(id+"FQ5JFwxVdaqARUP_1.wireOp",EDGE,"fcba4419-a2ee-464f-be9d-58f11bf3418b.sketch_text.stroke-152"),sQuery(id+"FQ5JFwxVdaqARUP_1.wireOp",EDGE,"fcba4419-a2ee-464f-be9d-58f11bf3418b.sketch_text.stroke-153"),sQuery(id+"FQ5JFwxVdaqARUP_1.wireOp",EDGE,"fcba4419-a2ee-464f-be9d-58f11bf3418b.sketch_text.stroke-154"),sQuery(id+"FQ5JFwxVdaqARUP_1.wireOp",EDGE,"fcba4419-a2ee-464f-be9d-58f11bf3418b.sketch_text.stroke-155"),sQuery(id+"FQ5JFwxVdaqARUP_1.wireOp",EDGE,"fcba4419-a2ee-464f-be9d-58f11bf3418b.sketch_text.stroke-156"),sQuery(id+"FQ5JFwxVdaqARUP_1.wireOp",EDGE,"fcba4419-a2ee-464f-be9d-58f11bf3418b.sketch_text.stroke-157"),sQuery(id+"FQ5JFwxVdaqARUP_1.wireOp",EDGE,"fcba4419-a2ee-464f-be9d-58f11bf3418b.sketch_text.stroke-158"),sQuery(id+"FQ5JFwxVdaqARUP_1.wireOp",EDGE,"fcba4419-a2ee-464f-be9d-58f11bf3418b.sketch_text.stroke-159"),sQuery(id+"FQ5JFwxVdaqARUP_1.wireOp",EDGE,"fcba4419-a2ee-464f-be9d-58f11bf3418b.sketch_text.stroke-160"),sQuery(id+"FQ5JFwxVdaqARUP_1.wireOp",EDGE,"fcba4419-a2ee-464f-be9d-58f11bf3418b.sketch_text.stroke-161"),sQuery(id+"FQ5JFwxVdaqARUP_1.wireOp",EDGE,"fcba4419-a2ee-464f-be9d-58f11bf3418b.sketch_text.stroke-162"),sQuery(id+"FQ5JFwxVdaqARUP_1.wireOp",EDGE,"fcba4419-a2ee-464f-be9d-58f11bf3418b.sketch_text.stroke-163"),sQuery(id+"FQ5JFwxVdaqARUP_1.wireOp",EDGE,"fcba4419-a2ee-464f-be9d-58f11bf3418b.sketch_text.stroke-164"),sQuery(id+"FQ5JFwxVdaqARUP_1.wireOp",EDGE,"fcba4419-a2ee-464f-be9d-58f11bf3418b.sketch_text.stroke-165"),sQuery(id+"FQ5JFwxVdaqARUP_1.wireOp",EDGE,"fcba4419-a2ee-464f-be9d-58f11bf3418b.sketch_text.stroke-166"),sQuery(id+"FQ5JFwxVdaqARUP_1.wireOp",EDGE,"fcba4419-a2ee-464f-be9d-58f11bf3418b.sketch_text.stroke-167"),sQuery(id+"FQ5JFwxVdaqARUP_1.wireOp",EDGE,"fcba4419-a2ee-464f-be9d-58f11bf3418b.sketch_text.stroke-168"),sQuery(id+"FQ5JFwxVdaqARUP_1.wireOp",EDGE,"fcba4419-a2ee-464f-be9d-58f11bf3418b.sketch_text.stroke-169"),sQuery(id+"FQ5JFwxVdaqARUP_1.wireOp",EDGE,"fcba4419-a2ee-464f-be9d-58f11bf3418b.sketch_text.stroke-170"),sQuery(id+"FQ5JFwxVdaqARUP_1.wireOp",EDGE,"fcba4419-a2ee-464f-be9d-58f11bf3418b.sketch_text.stroke-171"),sQuery(id+"FQ5JFwxVdaqARUP_1.wireOp",EDGE,"fcba4419-a2ee-464f-be9d-58f11bf3418b.sketch_text.stroke-172"),sQuery(id+"FQ5JFwxVdaqARUP_1.wireOp",EDGE,"fcba4419-a2ee-464f-be9d-58f11bf3418b.sketch_text.stroke-173"),sQuery(id+"FHMxAyK4CFUKdhS_1.wireOp",EDGE,"1cb9c079-ea9b-4899-8069-e0e3048e911d.sketch_text.stroke-0"),sQuery(id+"FHMxAyK4CFUKdhS_1.wireOp",EDGE,"1cb9c079-ea9b-4899-8069-e0e3048e911d.sketch_text.stroke-1"),sQuery(id+"FHMxAyK4CFUKdhS_1.wireOp",EDGE,"1cb9c079-ea9b-4899-8069-e0e3048e911d.sketch_text.stroke-2"),sQuery(id+"FHMxAyK4CFUKdhS_1.wireOp",EDGE,"1cb9c079-ea9b-4899-8069-e0e3048e911d.sketch_text.stroke-3"),sQuery(id+"FHMxAyK4CFUKdhS_1.wireOp",EDGE,"1cb9c079-ea9b-4899-8069-e0e3048e911d.sketch_text.stroke-4"),sQuery(id+"FHMxAyK4CFUKdhS_1.wireOp",EDGE,"1cb9c079-ea9b-4899-8069-e0e3048e911d.sketch_text.stroke-5"),sQuery(id+"FHMxAyK4CFUKdhS_1.wireOp",EDGE,"1cb9c079-ea9b-4899-8069-e0e3048e911d.sketch_text.stroke-6"),sQuery(id+"FHMxAyK4CFUKdhS_1.wireOp",EDGE,"1cb9c079-ea9b-4899-8069-e0e3048e911d.sketch_text.stroke-7"),sQuery(id+"FHMxAyK4CFUKdhS_1.wireOp",EDGE,"1cb9c079-ea9b-4899-8069-e0e3048e911d.sketch_text.stroke-8"),sQuery(id+"FHMxAyK4CFUKdhS_1.wireOp",EDGE,"1cb9c079-ea9b-4899-8069-e0e3048e911d.sketch_text.stroke-9"),sQuery(id+"FHMxAyK4CFUKdhS_1.wireOp",EDGE,"1cb9c079-ea9b-4899-8069-e0e3048e911d.sketch_text.stroke-10"),sQuery(id+"FHMxAyK4CFUKdhS_1.wireOp",EDGE,"1cb9c079-ea9b-4899-8069-e0e3048e911d.sketch_text.stroke-11"),sQuery(id+"FHMxAyK4CFUKdhS_1.wireOp",EDGE,"1cb9c079-ea9b-4899-8069-e0e3048e911d.sketch_text.stroke-12"),sQuery(id+"FHMxAyK4CFUKdhS_1.wireOp",EDGE,"1cb9c079-ea9b-4899-8069-e0e3048e911d.sketch_text.stroke-13"),sQuery(id+"FHMxAyK4CFUKdhS_1.wireOp",EDGE,"1cb9c079-ea9b-4899-8069-e0e3048e911d.sketch_text.stroke-14"),sQuery(id+"FHMxAyK4CFUKdhS_1.wireOp",EDGE,"1cb9c079-ea9b-4899-8069-e0e3048e911d.sketch_text.stroke-15"),sQuery(id+"FHMxAyK4CFUKdhS_1.wireOp",EDGE,"1cb9c079-ea9b-4899-8069-e0e3048e911d.sketch_text.stroke-16"),sQuery(id+"FHMxAyK4CFUKdhS_1.wireOp",EDGE,"1cb9c079-ea9b-4899-8069-e0e3048e911d.sketch_text.stroke-17"),sQuery(id+"FHMxAyK4CFUKdhS_1.wireOp",EDGE,"1cb9c079-ea9b-4899-8069-e0e3048e911d.sketch_text.stroke-18"),sQuery(id+"FHMxAyK4CFUKdhS_1.wireOp",EDGE,"1cb9c079-ea9b-4899-8069-e0e3048e911d.sketch_text.stroke-19"),sQuery(id+"FHMxAyK4CFUKdhS_1.wireOp",EDGE,"1cb9c079-ea9b-4899-8069-e0e3048e911d.sketch_text.stroke-20"),sQuery(id+"FHMxAyK4CFUKdhS_1.wireOp",EDGE,"1cb9c079-ea9b-4899-8069-e0e3048e911d.sketch_text.stroke-21"),sQuery(id+"FHMxAyK4CFUKdhS_1.wireOp",EDGE,"1cb9c079-ea9b-4899-8069-e0e3048e911d.sketch_text.stroke-22"),sQuery(id+"FHMxAyK4CFUKdhS_1.wireOp",EDGE,"1cb9c079-ea9b-4899-8069-e0e3048e911d.sketch_text.stroke-23"),sQuery(id+"FHMxAyK4CFUKdhS_1.wireOp",EDGE,"1cb9c079-ea9b-4899-8069-e0e3048e911d.sketch_text.stroke-24"),sQuery(id+"FHMxAyK4CFUKdhS_1.wireOp",EDGE,"1cb9c079-ea9b-4899-8069-e0e3048e911d.sketch_text.stroke-25"),sQuery(id+"FHMxAyK4CFUKdhS_1.wireOp",EDGE,"1cb9c079-ea9b-4899-8069-e0e3048e911d.sketch_text.stroke-26"),sQuery(id+"FHMxAyK4CFUKdhS_1.wireOp",EDGE,"1cb9c079-ea9b-4899-8069-e0e3048e911d.sketch_text.stroke-27"),sQuery(id+"FHMxAyK4CFUKdhS_1.wireOp",EDGE,"1cb9c079-ea9b-4899-8069-e0e3048e911d.sketch_text.stroke-28"),sQuery(id+"FHMxAyK4CFUKdhS_1.wireOp",EDGE,"1cb9c079-ea9b-4899-8069-e0e3048e911d.sketch_text.stroke-29"),sQuery(id+"FHMxAyK4CFUKdhS_1.wireOp",EDGE,"1cb9c079-ea9b-4899-8069-e0e3048e911d.sketch_text.stroke-30"),sQuery(id+"FHMxAyK4CFUKdhS_1.wireOp",EDGE,"1cb9c079-ea9b-4899-8069-e0e3048e911d.sketch_text.stroke-31"),sQuery(id+"FHMxAyK4CFUKdhS_1.wireOp",EDGE,"1cb9c079-ea9b-4899-8069-e0e3048e911d.sketch_text.stroke-32"),sQuery(id+"FHMxAyK4CFUKdhS_1.wireOp",EDGE,"1cb9c079-ea9b-4899-8069-e0e3048e911d.sketch_text.stroke-33"),sQuery(id+"FHMxAyK4CFUKdhS_1.wireOp",EDGE,"1cb9c079-ea9b-4899-8069-e0e3048e911d.sketch_text.stroke-34"),sQuery(id+"FHMxAyK4CFUKdhS_1.wireOp",EDGE,"1cb9c079-ea9b-4899-8069-e0e3048e911d.sketch_text.stroke-35"),sQuery(id+"FHMxAyK4CFUKdhS_1.wireOp",EDGE,"1cb9c079-ea9b-4899-8069-e0e3048e911d.sketch_text.stroke-36"),sQuery(id+"FHMxAyK4CFUKdhS_1.wireOp",EDGE,"1cb9c079-ea9b-4899-8069-e0e3048e911d.sketch_text.stroke-37"),sQuery(id+"FHMxAyK4CFUKdhS_1.wireOp",EDGE,"1cb9c079-ea9b-4899-8069-e0e3048e911d.sketch_text.stroke-38"),sQuery(id+"FHMxAyK4CFUKdhS_1.wireOp",EDGE,"1cb9c079-ea9b-4899-8069-e0e3048e911d.sketch_text.stroke-39"),sQuery(id+"FHMxAyK4CFUKdhS_1.wireOp",EDGE,"1cb9c079-ea9b-4899-8069-e0e3048e911d.sketch_text.stroke-40"),sQuery(id+"FHMxAyK4CFUKdhS_1.wireOp",EDGE,"1cb9c079-ea9b-4899-8069-e0e3048e911d.sketch_text.stroke-41"),sQuery(id+"FHMxAyK4CFUKdhS_1.wireOp",EDGE,"1cb9c079-ea9b-4899-8069-e0e3048e911d.sketch_text.stroke-42"),sQuery(id+"FHMxAyK4CFUKdhS_1.wireOp",EDGE,"1cb9c079-ea9b-4899-8069-e0e3048e911d.sketch_text.stroke-43"),sQuery(id+"FHMxAyK4CFUKdhS_1.wireOp",EDGE,"1cb9c079-ea9b-4899-8069-e0e3048e911d.sketch_text.stroke-44"),sQuery(id+"FHMxAyK4CFUKdhS_1.wireOp",EDGE,"1cb9c079-ea9b-4899-8069-e0e3048e911d.sketch_text.stroke-45"),sQuery(id+"FHMxAyK4CFUKdhS_1.wireOp",EDGE,"1cb9c079-ea9b-4899-8069-e0e3048e911d.sketch_text.stroke-46"),sQuery(id+"FHMxAyK4CFUKdhS_1.wireOp",EDGE,"1cb9c079-ea9b-4899-8069-e0e3048e911d.sketch_text.stroke-47"),sQuery(id+"FHMxAyK4CFUKdhS_1.wireOp",EDGE,"1cb9c079-ea9b-4899-8069-e0e3048e911d.sketch_text.stroke-48"),sQuery(id+"FHMxAyK4CFUKdhS_1.wireOp",EDGE,"1cb9c079-ea9b-4899-8069-e0e3048e911d.sketch_text.stroke-49"),sQuery(id+"FHMxAyK4CFUKdhS_1.wireOp",EDGE,"1cb9c079-ea9b-4899-8069-e0e3048e911d.sketch_text.stroke-50"),sQuery(id+"FHMxAyK4CFUKdhS_1.wireOp",EDGE,"1cb9c079-ea9b-4899-8069-e0e3048e911d.sketch_text.stroke-51"),sQuery(id+"FHMxAyK4CFUKdhS_1.wireOp",EDGE,"1cb9c079-ea9b-4899-8069-e0e3048e911d.sketch_text.stroke-52"),sQuery(id+"FHMxAyK4CFUKdhS_1.wireOp",EDGE,"1cb9c079-ea9b-4899-8069-e0e3048e911d.sketch_text.stroke-53"),sQuery(id+"FHMxAyK4CFUKdhS_1.wireOp",EDGE,"1cb9c079-ea9b-4899-8069-e0e3048e911d.sketch_text.stroke-54"),sQuery(id+"FHMxAyK4CFUKdhS_1.wireOp",EDGE,"1cb9c079-ea9b-4899-8069-e0e3048e911d.sketch_text.stroke-55"),sQuery(id+"FHMxAyK4CFUKdhS_1.wireOp",EDGE,"1cb9c079-ea9b-4899-8069-e0e3048e911d.sketch_text.stroke-56"),sQuery(id+"FHMxAyK4CFUKdhS_1.wireOp",EDGE,"1cb9c079-ea9b-4899-8069-e0e3048e911d.sketch_text.stroke-57"),sQuery(id+"FHMxAyK4CFUKdhS_1.wireOp",EDGE,"1cb9c079-ea9b-4899-8069-e0e3048e911d.sketch_text.stroke-58"),sQuery(id+"FHMxAyK4CFUKdhS_1.wireOp",EDGE,"1cb9c079-ea9b-4899-8069-e0e3048e911d.sketch_text.stroke-59"),sQuery(id+"FHMxAyK4CFUKdhS_1.wireOp",EDGE,"1cb9c079-ea9b-4899-8069-e0e3048e911d.sketch_text.stroke-60"),sQuery(id+"FHMxAyK4CFUKdhS_1.wireOp",EDGE,"1cb9c079-ea9b-4899-8069-e0e3048e911d.sketch_text.stroke-61"),sQuery(id+"FHMxAyK4CFUKdhS_1.wireOp",EDGE,"1cb9c079-ea9b-4899-8069-e0e3048e911d.sketch_text.stroke-62"),sQuery(id+"FHMxAyK4CFUKdhS_1.wireOp",EDGE,"1cb9c079-ea9b-4899-8069-e0e3048e911d.sketch_text.stroke-71"),sQuery(id+"FHMxAyK4CFUKdhS_1.wireOp",EDGE,"1cb9c079-ea9b-4899-8069-e0e3048e911d.sketch_text.stroke-72"),sQuery(id+"FHMxAyK4CFUKdhS_1.wireOp",EDGE,"1cb9c079-ea9b-4899-8069-e0e3048e911d.sketch_text.stroke-73"),sQuery(id+"FHMxAyK4CFUKdhS_1.wireOp",EDGE,"1cb9c079-ea9b-4899-8069-e0e3048e911d.sketch_text.stroke-74"),sQuery(id+"FHMxAyK4CFUKdhS_1.wireOp",EDGE,"1cb9c079-ea9b-4899-8069-e0e3048e911d.sketch_text.stroke-75"),sQuery(id+"FHMxAyK4CFUKdhS_1.wireOp",EDGE,"1cb9c079-ea9b-4899-8069-e0e3048e911d.sketch_text.stroke-76"),sQuery(id+"FHMxAyK4CFUKdhS_1.wireOp",EDGE,"1cb9c079-ea9b-4899-8069-e0e3048e911d.sketch_text.stroke-77"),sQuery(id+"FHMxAyK4CFUKdhS_1.wireOp",EDGE,"1cb9c079-ea9b-4899-8069-e0e3048e911d.sketch_text.stroke-78"),sQuery(id+"FHMxAyK4CFUKdhS_1.wireOp",EDGE,"1cb9c079-ea9b-4899-8069-e0e3048e911d.sketch_text.stroke-79"),sQuery(id+"FHMxAyK4CFUKdhS_1.wireOp",EDGE,"1cb9c079-ea9b-4899-8069-e0e3048e911d.sketch_text.stroke-80"),sQuery(id+"FHMxAyK4CFUKdhS_1.wireOp",EDGE,"1cb9c079-ea9b-4899-8069-e0e3048e911d.sketch_text.stroke-81"),sQuery(id+"FHMxAyK4CFUKdhS_1.wireOp",EDGE,"1cb9c079-ea9b-4899-8069-e0e3048e911d.sketch_text.stroke-82"),sQuery(id+"FHMxAyK4CFUKdhS_1.wireOp",EDGE,"1cb9c079-ea9b-4899-8069-e0e3048e911d.sketch_text.stroke-83"),sQuery(id+"FHMxAyK4CFUKdhS_1.wireOp",EDGE,"1cb9c079-ea9b-4899-8069-e0e3048e911d.sketch_text.stroke-84"),sQuery(id+"FHMxAyK4CFUKdhS_1.wireOp",EDGE,"1cb9c079-ea9b-4899-8069-e0e3048e911d.sketch_text.stroke-85"),sQuery(id+"FHMxAyK4CFUKdhS_1.wireOp",EDGE,"1cb9c079-ea9b-4899-8069-e0e3048e911d.sketch_text.stroke-86"),sQuery(id+"FHMxAyK4CFUKdhS_1.wireOp",EDGE,"1cb9c079-ea9b-4899-8069-e0e3048e911d.sketch_text.stroke-87"),sQuery(id+"FHMxAyK4CFUKdhS_1.wireOp",EDGE,"1cb9c079-ea9b-4899-8069-e0e3048e911d.sketch_text.stroke-88"),sQuery(id+"FHMxAyK4CFUKdhS_1.wireOp",EDGE,"1cb9c079-ea9b-4899-8069-e0e3048e911d.sketch_text.stroke-89"),sQuery(id+"FHMxAyK4CFUKdhS_1.wireOp",EDGE,"1cb9c079-ea9b-4899-8069-e0e3048e911d.sketch_text.stroke-90"),sQuery(id+"FHMxAyK4CFUKdhS_1.wireOp",EDGE,"1cb9c079-ea9b-4899-8069-e0e3048e911d.sketch_text.stroke-91"),sQuery(id+"FHMxAyK4CFUKdhS_1.wireOp",EDGE,"1cb9c079-ea9b-4899-8069-e0e3048e911d.sketch_text.stroke-92"),sQuery(id+"FHMxAyK4CFUKdhS_1.wireOp",EDGE,"1cb9c079-ea9b-4899-8069-e0e3048e911d.sketch_text.stroke-93"),sQuery(id+"FHMxAyK4CFUKdhS_1.wireOp",EDGE,"1cb9c079-ea9b-4899-8069-e0e3048e911d.sketch_text.stroke-94"),sQuery(id+"FHMxAyK4CFUKdhS_1.wireOp",EDGE,"1cb9c079-ea9b-4899-8069-e0e3048e911d.sketch_text.stroke-95"),sQuery(id+"FHMxAyK4CFUKdhS_1.wireOp",EDGE,"1cb9c079-ea9b-4899-8069-e0e3048e911d.sketch_text.stroke-96"),sQuery(id+"FHMxAyK4CFUKdhS_1.wireOp",EDGE,"1cb9c079-ea9b-4899-8069-e0e3048e911d.sketch_text.stroke-97"),sQuery(id+"FHMxAyK4CFUKdhS_1.wireOp",EDGE,"1cb9c079-ea9b-4899-8069-e0e3048e911d.sketch_text.stroke-103"),sQuery(id+"FHMxAyK4CFUKdhS_1.wireOp",EDGE,"1cb9c079-ea9b-4899-8069-e0e3048e911d.sketch_text.stroke-104"),sQuery(id+"FHMxAyK4CFUKdhS_1.wireOp",EDGE,"1cb9c079-ea9b-4899-8069-e0e3048e911d.sketch_text.stroke-105"),sQuery(id+"FHMxAyK4CFUKdhS_1.wireOp",EDGE,"1cb9c079-ea9b-4899-8069-e0e3048e911d.sketch_text.stroke-106"),sQuery(id+"FHMxAyK4CFUKdhS_1.wireOp",EDGE,"1cb9c079-ea9b-4899-8069-e0e3048e911d.sketch_text.stroke-107"),sQuery(id+"FHMxAyK4CFUKdhS_1.wireOp",EDGE,"1cb9c079-ea9b-4899-8069-e0e3048e911d.sketch_text.stroke-108"),sQuery(id+"FHMxAyK4CFUKdhS_1.wireOp",EDGE,"1cb9c079-ea9b-4899-8069-e0e3048e911d.sketch_text.stroke-109"),sQuery(id+"FHMxAyK4CFUKdhS_1.wireOp",EDGE,"1cb9c079-ea9b-4899-8069-e0e3048e911d.sketch_text.stroke-110"),sQuery(id+"FHMxAyK4CFUKdhS_1.wireOp",EDGE,"1cb9c079-ea9b-4899-8069-e0e3048e911d.sketch_text.stroke-111"),sQuery(id+"FHMxAyK4CFUKdhS_1.wireOp",EDGE,"1cb9c079-ea9b-4899-8069-e0e3048e911d.sketch_text.stroke-112"),sQuery(id+"FHMxAyK4CFUKdhS_1.wireOp",EDGE,"1cb9c079-ea9b-4899-8069-e0e3048e911d.sketch_text.stroke-113"),sQuery(id+"FHMxAyK4CFUKdhS_1.wireOp",EDGE,"1cb9c079-ea9b-4899-8069-e0e3048e911d.sketch_text.stroke-114"),sQuery(id+"FHMxAyK4CFUKdhS_1.wireOp",EDGE,"1cb9c079-ea9b-4899-8069-e0e3048e911d.sketch_text.stroke-115"),sQuery(id+"FHMxAyK4CFUKdhS_1.wireOp",EDGE,"1cb9c079-ea9b-4899-8069-e0e3048e911d.sketch_text.stroke-116"),sQuery(id+"FHMxAyK4CFUKdhS_1.wireOp",EDGE,"1cb9c079-ea9b-4899-8069-e0e3048e911d.sketch_text.stroke-117"),sQuery(id+"FHMxAyK4CFUKdhS_1.wireOp",EDGE,"1cb9c079-ea9b-4899-8069-e0e3048e911d.sketch_text.stroke-118"),sQuery(id+"FHMxAyK4CFUKdhS_1.wireOp",EDGE,"1cb9c079-ea9b-4899-8069-e0e3048e911d.sketch_text.stroke-119"),sQuery(id+"FHMxAyK4CFUKdhS_1.wireOp",EDGE,"1cb9c079-ea9b-4899-8069-e0e3048e911d.sketch_text.stroke-120"),sQuery(id+"FHMxAyK4CFUKdhS_1.wireOp",EDGE,"1cb9c079-ea9b-4899-8069-e0e3048e911d.sketch_text.stroke-121"),sQuery(id+"FHMxAyK4CFUKdhS_1.wireOp",EDGE,"1cb9c079-ea9b-4899-8069-e0e3048e911d.sketch_text.stroke-122"),sQuery(id+"FHMxAyK4CFUKdhS_1.wireOp",EDGE,"1cb9c079-ea9b-4899-8069-e0e3048e911d.sketch_text.stroke-123"),sQuery(id+"FHMxAyK4CFUKdhS_1.wireOp",EDGE,"1cb9c079-ea9b-4899-8069-e0e3048e911d.sketch_text.stroke-124"),sQuery(id+"FHMxAyK4CFUKdhS_1.wireOp",EDGE,"1cb9c079-ea9b-4899-8069-e0e3048e911d.sketch_text.stroke-125"),sQuery(id+"FHMxAyK4CFUKdhS_1.wireOp",EDGE,"1cb9c079-ea9b-4899-8069-e0e3048e911d.sketch_text.stroke-126"),sQuery(id+"FHMxAyK4CFUKdhS_1.wireOp",EDGE,"1cb9c079-ea9b-4899-8069-e0e3048e911d.sketch_text.stroke-127"),sQuery(id+"FHMxAyK4CFUKdhS_1.wireOp",EDGE,"1cb9c079-ea9b-4899-8069-e0e3048e911d.sketch_text.stroke-128"),sQuery(id+"FHMxAyK4CFUKdhS_1.wireOp",EDGE,"1cb9c079-ea9b-4899-8069-e0e3048e911d.sketch_text.stroke-129"),sQuery(id+"FHMxAyK4CFUKdhS_1.wireOp",EDGE,"1cb9c079-ea9b-4899-8069-e0e3048e911d.sketch_text.stroke-130"),sQuery(id+"FHMxAyK4CFUKdhS_1.wireOp",EDGE,"1cb9c079-ea9b-4899-8069-e0e3048e911d.sketch_text.stroke-131"),sQuery(id+"FHMxAyK4CFUKdhS_1.wireOp",EDGE,"1cb9c079-ea9b-4899-8069-e0e3048e911d.sketch_text.stroke-132"),sQuery(id+"FHMxAyK4CFUKdhS_1.wireOp",EDGE,"1cb9c079-ea9b-4899-8069-e0e3048e911d.sketch_text.stroke-133"),sQuery(id+"FHMxAyK4CFUKdhS_1.wireOp",EDGE,"1cb9c079-ea9b-4899-8069-e0e3048e911d.sketch_text.stroke-134"),sQuery(id+"FHMxAyK4CFUKdhS_1.wireOp",EDGE,"1cb9c079-ea9b-4899-8069-e0e3048e911d.sketch_text.stroke-135"),sQuery(id+"FHMxAyK4CFUKdhS_1.wireOp",EDGE,"1cb9c079-ea9b-4899-8069-e0e3048e911d.sketch_text.stroke-136"),sQuery(id+"FHMxAyK4CFUKdhS_1.wireOp",EDGE,"1cb9c079-ea9b-4899-8069-e0e3048e911d.sketch_text.stroke-137"),sQuery(id+"FHMxAyK4CFUKdhS_1.wireOp",EDGE,"1cb9c079-ea9b-4899-8069-e0e3048e911d.sketch_text.stroke-138"),sQuery(id+"FHMxAyK4CFUKdhS_1.wireOp",EDGE,"1cb9c079-ea9b-4899-8069-e0e3048e911d.sketch_text.stroke-139"),sQuery(id+"FHMxAyK4CFUKdhS_1.wireOp",EDGE,"1cb9c079-ea9b-4899-8069-e0e3048e911d.sketch_text.stroke-140"),sQuery(id+"FHMxAyK4CFUKdhS_1.wireOp",EDGE,"1cb9c079-ea9b-4899-8069-e0e3048e911d.sketch_text.stroke-141"),sQuery(id+"FHMxAyK4CFUKdhS_1.wireOp",EDGE,"1cb9c079-ea9b-4899-8069-e0e3048e911d.sketch_text.stroke-142"),sQuery(id+"FHMxAyK4CFUKdhS_1.wireOp",EDGE,"1cb9c079-ea9b-4899-8069-e0e3048e911d.sketch_text.stroke-143"),sQuery(id+"FHMxAyK4CFUKdhS_1.wireOp",EDGE,"1cb9c079-ea9b-4899-8069-e0e3048e911d.sketch_text.stroke-144"),sQuery(id+"FHMxAyK4CFUKdhS_1.wireOp",EDGE,"1cb9c079-ea9b-4899-8069-e0e3048e911d.sketch_text.stroke-145"),sQuery(id+"FHMxAyK4CFUKdhS_1.wireOp",EDGE,"1cb9c079-ea9b-4899-8069-e0e3048e911d.sketch_text.stroke-146"),sQuery(id+"FHMxAyK4CFUKdhS_1.wireOp",EDGE,"1cb9c079-ea9b-4899-8069-e0e3048e911d.sketch_text.stroke-147"),sQuery(id+"FHMxAyK4CFUKdhS_1.wireOp",EDGE,"1cb9c079-ea9b-4899-8069-e0e3048e911d.sketch_text.stroke-148"),sQuery(id+"FHMxAyK4CFUKdhS_1.wireOp",EDGE,"1cb9c079-ea9b-4899-8069-e0e3048e911d.sketch_text.stroke-149"),sQuery(id+"FHMxAyK4CFUKdhS_1.wireOp",EDGE,"1cb9c079-ea9b-4899-8069-e0e3048e911d.sketch_text.stroke-150"),sQuery(id+"FHMxAyK4CFUKdhS_1.wireOp",EDGE,"1cb9c079-ea9b-4899-8069-e0e3048e911d.sketch_text.stroke-151"),sQuery(id+"FHMxAyK4CFUKdhS_1.wireOp",EDGE,"1cb9c079-ea9b-4899-8069-e0e3048e911d.sketch_text.stroke-152"),sQuery(id+"FHMxAyK4CFUKdhS_1.wireOp",EDGE,"1cb9c079-ea9b-4899-8069-e0e3048e911d.sketch_text.stroke-153"),sQuery(id+"FHMxAyK4CFUKdhS_1.wireOp",EDGE,"1cb9c079-ea9b-4899-8069-e0e3048e911d.sketch_text.stroke-159"),sQuery(id+"FHMxAyK4CFUKdhS_1.wireOp",EDGE,"1cb9c079-ea9b-4899-8069-e0e3048e911d.sketch_text.stroke-160"),sQuery(id+"FHMxAyK4CFUKdhS_1.wireOp",EDGE,"1cb9c079-ea9b-4899-8069-e0e3048e911d.sketch_text.stroke-161"),sQuery(id+"FHMxAyK4CFUKdhS_1.wireOp",EDGE,"1cb9c079-ea9b-4899-8069-e0e3048e911d.sketch_text.stroke-162"),sQuery(id+"FHMxAyK4CFUKdhS_1.wireOp",EDGE,"1cb9c079-ea9b-4899-8069-e0e3048e911d.sketch_text.stroke-163"),sQuery(id+"FHMxAyK4CFUKdhS_1.wireOp",EDGE,"1cb9c079-ea9b-4899-8069-e0e3048e911d.sketch_text.stroke-164"),sQuery(id+"FHMxAyK4CFUKdhS_1.wireOp",EDGE,"1cb9c079-ea9b-4899-8069-e0e3048e911d.sketch_text.stroke-165"),sQuery(id+"FHMxAyK4CFUKdhS_1.wireOp",EDGE,"1cb9c079-ea9b-4899-8069-e0e3048e911d.sketch_text.stroke-166"),sQuery(id+"FHMxAyK4CFUKdhS_1.wireOp",EDGE,"1cb9c079-ea9b-4899-8069-e0e3048e911d.sketch_text.stroke-167"),sQuery(id+"FHMxAyK4CFUKdhS_1.wireOp",EDGE,"1cb9c079-ea9b-4899-8069-e0e3048e911d.sketch_text.stroke-168"),sQuery(id+"FHMxAyK4CFUKdhS_1.wireOp",EDGE,"1cb9c079-ea9b-4899-8069-e0e3048e911d.sketch_text.stroke-169"),sQuery(id+"FHMxAyK4CFUKdhS_1.wireOp",EDGE,"1cb9c079-ea9b-4899-8069-e0e3048e911d.sketch_text.stroke-170"),sQuery(id+"FHMxAyK4CFUKdhS_1.wireOp",EDGE,"1cb9c079-ea9b-4899-8069-e0e3048e911d.sketch_text.stroke-171"),sQuery(id+"FHMxAyK4CFUKdhS_1.wireOp",EDGE,"1cb9c079-ea9b-4899-8069-e0e3048e911d.sketch_text.stroke-172"),sQuery(id+"FHMxAyK4CFUKdhS_1.wireOp",EDGE,"1cb9c079-ea9b-4899-8069-e0e3048e911d.sketch_text.stroke-173"),sQuery(id+"FHMxAyK4CFUKdhS_1.wireOp",EDGE,"1cb9c079-ea9b-4899-8069-e0e3048e911d.sketch_text.stroke-174"),sQuery(id+"FHMxAyK4CFUKdhS_1.wireOp",EDGE,"1cb9c079-ea9b-4899-8069-e0e3048e911d.sketch_text.stroke-175"),sQuery(id+"FHMxAyK4CFUKdhS_1.wireOp",EDGE,"1cb9c079-ea9b-4899-8069-e0e3048e911d.sketch_text.stroke-176"),sQuery(id+"FHMxAyK4CFUKdhS_1.wireOp",EDGE,"1cb9c079-ea9b-4899-8069-e0e3048e911d.sketch_text.stroke-177"),sQuery(id+"FHMxAyK4CFUKdhS_1.wireOp",EDGE,"1cb9c079-ea9b-4899-8069-e0e3048e911d.sketch_text.stroke-178"),sQuery(id+"FHMxAyK4CFUKdhS_1.wireOp",EDGE,"1cb9c079-ea9b-4899-8069-e0e3048e911d.sketch_text.stroke-179"),sQuery(id+"FHMxAyK4CFUKdhS_1.wireOp",EDGE,"1cb9c079-ea9b-4899-8069-e0e3048e911d.sketch_text.stroke-180"),sQuery(id+"F2.wireOp",EDGE,"8007402e-1a4e-4a06-85a5-2af08e553504"),subQ2])],"isStart":true}),makeQuery(id+"F3.opExtrude","SWEPT_FACE",FACE,{"disambiguationData":[OSD([subQ2])]})]),OD(0.0)],"derivedFrom":makeQuery(id+"F1.opExtrude","CAP_EDGE",EDGE,{"disambiguationData":[OSD([subQ0])],"isStart":false})});}
            var Q17;
            {var subQ0=sQuery(id+"F0.wireOp",EDGE,"E0.top");var subQ1=sQuery(id+"F0.wireOp",EDGE,"E0.bottom");var subQ2=sQuery(id+"F2.wireOp",EDGE,"1a034e28-a7c2-419d-97de-c33d70a47301");Q17=makeQuery(id+"F3.boolean.opBoolean","SPLIT",EDGE,{"disambiguationData":[TD([makeQuery(id+"F1.opExtrude","CAP_FACE",FACE,{"disambiguationData":[OSD([subQ1,subQ0,sQuery(id+"F0.wireOp",EDGE,"E0.left"),sQuery(id+"F0.wireOp",EDGE,"E0.right")])],"isStart":false}),makeQuery(id+"F1.opExtrude","SWEPT_FACE",FACE,{"disambiguationData":[OSD([subQ0])]}),makeQuery(id+"F3.opExtrude","CAP_FACE",FACE,{"disambiguationData":[OSD([subQ1,sQuery(id+"FQ5JFwxVdaqARUP_1.wireOp",EDGE,"fcba4419-a2ee-464f-be9d-58f11bf3418b.sketch_text.stroke-0"),sQuery(id+"FQ5JFwxVdaqARUP_1.wireOp",EDGE,"fcba4419-a2ee-464f-be9d-58f11bf3418b.sketch_text.stroke-1"),sQuery(id+"FQ5JFwxVdaqARUP_1.wireOp",EDGE,"fcba4419-a2ee-464f-be9d-58f11bf3418b.sketch_text.stroke-2"),sQuery(id+"FQ5JFwxVdaqARUP_1.wireOp",EDGE,"fcba4419-a2ee-464f-be9d-58f11bf3418b.sketch_text.stroke-3"),sQuery(id+"FQ5JFwxVdaqARUP_1.wireOp",EDGE,"fcba4419-a2ee-464f-be9d-58f11bf3418b.sketch_text.stroke-4"),sQuery(id+"FQ5JFwxVdaqARUP_1.wireOp",EDGE,"fcba4419-a2ee-464f-be9d-58f11bf3418b.sketch_text.stroke-5"),sQuery(id+"FQ5JFwxVdaqARUP_1.wireOp",EDGE,"fcba4419-a2ee-464f-be9d-58f11bf3418b.sketch_text.stroke-6"),sQuery(id+"FQ5JFwxVdaqARUP_1.wireOp",EDGE,"fcba4419-a2ee-464f-be9d-58f11bf3418b.sketch_text.stroke-7"),sQuery(id+"FQ5JFwxVdaqARUP_1.wireOp",EDGE,"fcba4419-a2ee-464f-be9d-58f11bf3418b.sketch_text.stroke-8"),sQuery(id+"FQ5JFwxVdaqARUP_1.wireOp",EDGE,"fcba4419-a2ee-464f-be9d-58f11bf3418b.sketch_text.stroke-9"),sQuery(id+"FQ5JFwxVdaqARUP_1.wireOp",EDGE,"fcba4419-a2ee-464f-be9d-58f11bf3418b.sketch_text.stroke-10"),sQuery(id+"FQ5JFwxVdaqARUP_1.wireOp",EDGE,"fcba4419-a2ee-464f-be9d-58f11bf3418b.sketch_text.stroke-11"),sQuery(id+"FQ5JFwxVdaqARUP_1.wireOp",EDGE,"fcba4419-a2ee-464f-be9d-58f11bf3418b.sketch_text.stroke-12"),sQuery(id+"FQ5JFwxVdaqARUP_1.wireOp",EDGE,"fcba4419-a2ee-464f-be9d-58f11bf3418b.sketch_text.stroke-13"),sQuery(id+"FQ5JFwxVdaqARUP_1.wireOp",EDGE,"fcba4419-a2ee-464f-be9d-58f11bf3418b.sketch_text.stroke-14"),sQuery(id+"FQ5JFwxVdaqARUP_1.wireOp",EDGE,"fcba4419-a2ee-464f-be9d-58f11bf3418b.sketch_text.stroke-15"),sQuery(id+"FQ5JFwxVdaqARUP_1.wireOp",EDGE,"fcba4419-a2ee-464f-be9d-58f11bf3418b.sketch_text.stroke-16"),sQuery(id+"FQ5JFwxVdaqARUP_1.wireOp",EDGE,"fcba4419-a2ee-464f-be9d-58f11bf3418b.sketch_text.stroke-17"),sQuery(id+"FQ5JFwxVdaqARUP_1.wireOp",EDGE,"fcba4419-a2ee-464f-be9d-58f11bf3418b.sketch_text.stroke-18"),sQuery(id+"FQ5JFwxVdaqARUP_1.wireOp",EDGE,"fcba4419-a2ee-464f-be9d-58f11bf3418b.sketch_text.stroke-19"),sQuery(id+"FQ5JFwxVdaqARUP_1.wireOp",EDGE,"fcba4419-a2ee-464f-be9d-58f11bf3418b.sketch_text.stroke-20"),sQuery(id+"FQ5JFwxVdaqARUP_1.wireOp",EDGE,"fcba4419-a2ee-464f-be9d-58f11bf3418b.sketch_text.stroke-21"),sQuery(id+"FQ5JFwxVdaqARUP_1.wireOp",EDGE,"fcba4419-a2ee-464f-be9d-58f11bf3418b.sketch_text.stroke-22"),sQuery(id+"FQ5JFwxVdaqARUP_1.wireOp",EDGE,"fcba4419-a2ee-464f-be9d-58f11bf3418b.sketch_text.stroke-23"),sQuery(id+"FQ5JFwxVdaqARUP_1.wireOp",EDGE,"fcba4419-a2ee-464f-be9d-58f11bf3418b.sketch_text.stroke-24"),sQuery(id+"FQ5JFwxVdaqARUP_1.wireOp",EDGE,"fcba4419-a2ee-464f-be9d-58f11bf3418b.sketch_text.stroke-25"),sQuery(id+"FQ5JFwxVdaqARUP_1.wireOp",EDGE,"fcba4419-a2ee-464f-be9d-58f11bf3418b.sketch_text.stroke-26"),sQuery(id+"FQ5JFwxVdaqARUP_1.wireOp",EDGE,"fcba4419-a2ee-464f-be9d-58f11bf3418b.sketch_text.stroke-27"),sQuery(id+"FQ5JFwxVdaqARUP_1.wireOp",EDGE,"fcba4419-a2ee-464f-be9d-58f11bf3418b.sketch_text.stroke-28"),sQuery(id+"FQ5JFwxVdaqARUP_1.wireOp",EDGE,"fcba4419-a2ee-464f-be9d-58f11bf3418b.sketch_text.stroke-29"),sQuery(id+"FQ5JFwxVdaqARUP_1.wireOp",EDGE,"fcba4419-a2ee-464f-be9d-58f11bf3418b.sketch_text.stroke-30"),sQuery(id+"FQ5JFwxVdaqARUP_1.wireOp",EDGE,"fcba4419-a2ee-464f-be9d-58f11bf3418b.sketch_text.stroke-31"),sQuery(id+"FQ5JFwxVdaqARUP_1.wireOp",EDGE,"fcba4419-a2ee-464f-be9d-58f11bf3418b.sketch_text.stroke-32"),sQuery(id+"FQ5JFwxVdaqARUP_1.wireOp",EDGE,"fcba4419-a2ee-464f-be9d-58f11bf3418b.sketch_text.stroke-33"),sQuery(id+"FQ5JFwxVdaqARUP_1.wireOp",EDGE,"fcba4419-a2ee-464f-be9d-58f11bf3418b.sketch_text.stroke-34"),sQuery(id+"FQ5JFwxVdaqARUP_1.wireOp",EDGE,"fcba4419-a2ee-464f-be9d-58f11bf3418b.sketch_text.stroke-35"),sQuery(id+"FQ5JFwxVdaqARUP_1.wireOp",EDGE,"fcba4419-a2ee-464f-be9d-58f11bf3418b.sketch_text.stroke-36"),sQuery(id+"FQ5JFwxVdaqARUP_1.wireOp",EDGE,"fcba4419-a2ee-464f-be9d-58f11bf3418b.sketch_text.stroke-37"),sQuery(id+"FQ5JFwxVdaqARUP_1.wireOp",EDGE,"fcba4419-a2ee-464f-be9d-58f11bf3418b.sketch_text.stroke-38"),sQuery(id+"FQ5JFwxVdaqARUP_1.wireOp",EDGE,"fcba4419-a2ee-464f-be9d-58f11bf3418b.sketch_text.stroke-39"),sQuery(id+"FQ5JFwxVdaqARUP_1.wireOp",EDGE,"fcba4419-a2ee-464f-be9d-58f11bf3418b.sketch_text.stroke-40"),sQuery(id+"FQ5JFwxVdaqARUP_1.wireOp",EDGE,"fcba4419-a2ee-464f-be9d-58f11bf3418b.sketch_text.stroke-41"),sQuery(id+"FQ5JFwxVdaqARUP_1.wireOp",EDGE,"fcba4419-a2ee-464f-be9d-58f11bf3418b.sketch_text.stroke-42"),sQuery(id+"FQ5JFwxVdaqARUP_1.wireOp",EDGE,"fcba4419-a2ee-464f-be9d-58f11bf3418b.sketch_text.stroke-43"),sQuery(id+"FQ5JFwxVdaqARUP_1.wireOp",EDGE,"fcba4419-a2ee-464f-be9d-58f11bf3418b.sketch_text.stroke-44"),sQuery(id+"FQ5JFwxVdaqARUP_1.wireOp",EDGE,"fcba4419-a2ee-464f-be9d-58f11bf3418b.sketch_text.stroke-45"),sQuery(id+"FQ5JFwxVdaqARUP_1.wireOp",EDGE,"fcba4419-a2ee-464f-be9d-58f11bf3418b.sketch_text.stroke-46"),sQuery(id+"FQ5JFwxVdaqARUP_1.wireOp",EDGE,"fcba4419-a2ee-464f-be9d-58f11bf3418b.sketch_text.stroke-47"),sQuery(id+"FQ5JFwxVdaqARUP_1.wireOp",EDGE,"fcba4419-a2ee-464f-be9d-58f11bf3418b.sketch_text.stroke-48"),sQuery(id+"FQ5JFwxVdaqARUP_1.wireOp",EDGE,"fcba4419-a2ee-464f-be9d-58f11bf3418b.sketch_text.stroke-49"),sQuery(id+"FQ5JFwxVdaqARUP_1.wireOp",EDGE,"fcba4419-a2ee-464f-be9d-58f11bf3418b.sketch_text.stroke-50"),sQuery(id+"FQ5JFwxVdaqARUP_1.wireOp",EDGE,"fcba4419-a2ee-464f-be9d-58f11bf3418b.sketch_text.stroke-51"),sQuery(id+"FQ5JFwxVdaqARUP_1.wireOp",EDGE,"fcba4419-a2ee-464f-be9d-58f11bf3418b.sketch_text.stroke-52"),sQuery(id+"FQ5JFwxVdaqARUP_1.wireOp",EDGE,"fcba4419-a2ee-464f-be9d-58f11bf3418b.sketch_text.stroke-53"),sQuery(id+"FQ5JFwxVdaqARUP_1.wireOp",EDGE,"fcba4419-a2ee-464f-be9d-58f11bf3418b.sketch_text.stroke-54"),sQuery(id+"FQ5JFwxVdaqARUP_1.wireOp",EDGE,"fcba4419-a2ee-464f-be9d-58f11bf3418b.sketch_text.stroke-55"),sQuery(id+"FQ5JFwxVdaqARUP_1.wireOp",EDGE,"fcba4419-a2ee-464f-be9d-58f11bf3418b.sketch_text.stroke-56"),sQuery(id+"FQ5JFwxVdaqARUP_1.wireOp",EDGE,"fcba4419-a2ee-464f-be9d-58f11bf3418b.sketch_text.stroke-57"),sQuery(id+"FQ5JFwxVdaqARUP_1.wireOp",EDGE,"fcba4419-a2ee-464f-be9d-58f11bf3418b.sketch_text.stroke-58"),sQuery(id+"FQ5JFwxVdaqARUP_1.wireOp",EDGE,"fcba4419-a2ee-464f-be9d-58f11bf3418b.sketch_text.stroke-59"),sQuery(id+"FQ5JFwxVdaqARUP_1.wireOp",EDGE,"fcba4419-a2ee-464f-be9d-58f11bf3418b.sketch_text.stroke-60"),sQuery(id+"FQ5JFwxVdaqARUP_1.wireOp",EDGE,"fcba4419-a2ee-464f-be9d-58f11bf3418b.sketch_text.stroke-61"),sQuery(id+"FQ5JFwxVdaqARUP_1.wireOp",EDGE,"fcba4419-a2ee-464f-be9d-58f11bf3418b.sketch_text.stroke-62"),sQuery(id+"FQ5JFwxVdaqARUP_1.wireOp",EDGE,"fcba4419-a2ee-464f-be9d-58f11bf3418b.sketch_text.stroke-63"),sQuery(id+"FQ5JFwxVdaqARUP_1.wireOp",EDGE,"fcba4419-a2ee-464f-be9d-58f11bf3418b.sketch_text.stroke-64"),sQuery(id+"FQ5JFwxVdaqARUP_1.wireOp",EDGE,"fcba4419-a2ee-464f-be9d-58f11bf3418b.sketch_text.stroke-65"),sQuery(id+"FQ5JFwxVdaqARUP_1.wireOp",EDGE,"fcba4419-a2ee-464f-be9d-58f11bf3418b.sketch_text.stroke-66"),sQuery(id+"FQ5JFwxVdaqARUP_1.wireOp",EDGE,"fcba4419-a2ee-464f-be9d-58f11bf3418b.sketch_text.stroke-67"),sQuery(id+"FQ5JFwxVdaqARUP_1.wireOp",EDGE,"fcba4419-a2ee-464f-be9d-58f11bf3418b.sketch_text.stroke-68"),sQuery(id+"FQ5JFwxVdaqARUP_1.wireOp",EDGE,"fcba4419-a2ee-464f-be9d-58f11bf3418b.sketch_text.stroke-69"),sQuery(id+"FQ5JFwxVdaqARUP_1.wireOp",EDGE,"fcba4419-a2ee-464f-be9d-58f11bf3418b.sketch_text.stroke-70"),sQuery(id+"FQ5JFwxVdaqARUP_1.wireOp",EDGE,"fcba4419-a2ee-464f-be9d-58f11bf3418b.sketch_text.stroke-71"),sQuery(id+"FQ5JFwxVdaqARUP_1.wireOp",EDGE,"fcba4419-a2ee-464f-be9d-58f11bf3418b.sketch_text.stroke-72"),sQuery(id+"FQ5JFwxVdaqARUP_1.wireOp",EDGE,"fcba4419-a2ee-464f-be9d-58f11bf3418b.sketch_text.stroke-73"),sQuery(id+"FQ5JFwxVdaqARUP_1.wireOp",EDGE,"fcba4419-a2ee-464f-be9d-58f11bf3418b.sketch_text.stroke-74"),sQuery(id+"FQ5JFwxVdaqARUP_1.wireOp",EDGE,"fcba4419-a2ee-464f-be9d-58f11bf3418b.sketch_text.stroke-75"),sQuery(id+"FQ5JFwxVdaqARUP_1.wireOp",EDGE,"fcba4419-a2ee-464f-be9d-58f11bf3418b.sketch_text.stroke-76"),sQuery(id+"FQ5JFwxVdaqARUP_1.wireOp",EDGE,"fcba4419-a2ee-464f-be9d-58f11bf3418b.sketch_text.stroke-77"),sQuery(id+"FQ5JFwxVdaqARUP_1.wireOp",EDGE,"fcba4419-a2ee-464f-be9d-58f11bf3418b.sketch_text.stroke-78"),sQuery(id+"FQ5JFwxVdaqARUP_1.wireOp",EDGE,"fcba4419-a2ee-464f-be9d-58f11bf3418b.sketch_text.stroke-79"),sQuery(id+"FQ5JFwxVdaqARUP_1.wireOp",EDGE,"fcba4419-a2ee-464f-be9d-58f11bf3418b.sketch_text.stroke-80"),sQuery(id+"FQ5JFwxVdaqARUP_1.wireOp",EDGE,"fcba4419-a2ee-464f-be9d-58f11bf3418b.sketch_text.stroke-81"),sQuery(id+"FQ5JFwxVdaqARUP_1.wireOp",EDGE,"fcba4419-a2ee-464f-be9d-58f11bf3418b.sketch_text.stroke-82"),sQuery(id+"FQ5JFwxVdaqARUP_1.wireOp",EDGE,"fcba4419-a2ee-464f-be9d-58f11bf3418b.sketch_text.stroke-83"),sQuery(id+"FQ5JFwxVdaqARUP_1.wireOp",EDGE,"fcba4419-a2ee-464f-be9d-58f11bf3418b.sketch_text.stroke-84"),sQuery(id+"FQ5JFwxVdaqARUP_1.wireOp",EDGE,"fcba4419-a2ee-464f-be9d-58f11bf3418b.sketch_text.stroke-85"),sQuery(id+"FQ5JFwxVdaqARUP_1.wireOp",EDGE,"fcba4419-a2ee-464f-be9d-58f11bf3418b.sketch_text.stroke-86"),sQuery(id+"FQ5JFwxVdaqARUP_1.wireOp",EDGE,"fcba4419-a2ee-464f-be9d-58f11bf3418b.sketch_text.stroke-87"),sQuery(id+"FQ5JFwxVdaqARUP_1.wireOp",EDGE,"fcba4419-a2ee-464f-be9d-58f11bf3418b.sketch_text.stroke-88"),sQuery(id+"FQ5JFwxVdaqARUP_1.wireOp",EDGE,"fcba4419-a2ee-464f-be9d-58f11bf3418b.sketch_text.stroke-89"),sQuery(id+"FQ5JFwxVdaqARUP_1.wireOp",EDGE,"fcba4419-a2ee-464f-be9d-58f11bf3418b.sketch_text.stroke-90"),sQuery(id+"FQ5JFwxVdaqARUP_1.wireOp",EDGE,"fcba4419-a2ee-464f-be9d-58f11bf3418b.sketch_text.stroke-91"),sQuery(id+"FQ5JFwxVdaqARUP_1.wireOp",EDGE,"fcba4419-a2ee-464f-be9d-58f11bf3418b.sketch_text.stroke-92"),sQuery(id+"FQ5JFwxVdaqARUP_1.wireOp",EDGE,"fcba4419-a2ee-464f-be9d-58f11bf3418b.sketch_text.stroke-93"),sQuery(id+"FQ5JFwxVdaqARUP_1.wireOp",EDGE,"fcba4419-a2ee-464f-be9d-58f11bf3418b.sketch_text.stroke-94"),sQuery(id+"FQ5JFwxVdaqARUP_1.wireOp",EDGE,"fcba4419-a2ee-464f-be9d-58f11bf3418b.sketch_text.stroke-95"),sQuery(id+"FQ5JFwxVdaqARUP_1.wireOp",EDGE,"fcba4419-a2ee-464f-be9d-58f11bf3418b.sketch_text.stroke-96"),sQuery(id+"FQ5JFwxVdaqARUP_1.wireOp",EDGE,"fcba4419-a2ee-464f-be9d-58f11bf3418b.sketch_text.stroke-97"),sQuery(id+"FQ5JFwxVdaqARUP_1.wireOp",EDGE,"fcba4419-a2ee-464f-be9d-58f11bf3418b.sketch_text.stroke-98"),sQuery(id+"FQ5JFwxVdaqARUP_1.wireOp",EDGE,"fcba4419-a2ee-464f-be9d-58f11bf3418b.sketch_text.stroke-99"),sQuery(id+"FQ5JFwxVdaqARUP_1.wireOp",EDGE,"fcba4419-a2ee-464f-be9d-58f11bf3418b.sketch_text.stroke-100"),sQuery(id+"FQ5JFwxVdaqARUP_1.wireOp",EDGE,"fcba4419-a2ee-464f-be9d-58f11bf3418b.sketch_text.stroke-101"),sQuery(id+"FQ5JFwxVdaqARUP_1.wireOp",EDGE,"fcba4419-a2ee-464f-be9d-58f11bf3418b.sketch_text.stroke-102"),sQuery(id+"FQ5JFwxVdaqARUP_1.wireOp",EDGE,"fcba4419-a2ee-464f-be9d-58f11bf3418b.sketch_text.stroke-103"),sQuery(id+"FQ5JFwxVdaqARUP_1.wireOp",EDGE,"fcba4419-a2ee-464f-be9d-58f11bf3418b.sketch_text.stroke-104"),sQuery(id+"FQ5JFwxVdaqARUP_1.wireOp",EDGE,"fcba4419-a2ee-464f-be9d-58f11bf3418b.sketch_text.stroke-105"),sQuery(id+"FQ5JFwxVdaqARUP_1.wireOp",EDGE,"fcba4419-a2ee-464f-be9d-58f11bf3418b.sketch_text.stroke-106"),sQuery(id+"FQ5JFwxVdaqARUP_1.wireOp",EDGE,"fcba4419-a2ee-464f-be9d-58f11bf3418b.sketch_text.stroke-107"),sQuery(id+"FQ5JFwxVdaqARUP_1.wireOp",EDGE,"fcba4419-a2ee-464f-be9d-58f11bf3418b.sketch_text.stroke-108"),sQuery(id+"FQ5JFwxVdaqARUP_1.wireOp",EDGE,"fcba4419-a2ee-464f-be9d-58f11bf3418b.sketch_text.stroke-109"),sQuery(id+"FQ5JFwxVdaqARUP_1.wireOp",EDGE,"fcba4419-a2ee-464f-be9d-58f11bf3418b.sketch_text.stroke-110"),sQuery(id+"FQ5JFwxVdaqARUP_1.wireOp",EDGE,"fcba4419-a2ee-464f-be9d-58f11bf3418b.sketch_text.stroke-111"),sQuery(id+"FQ5JFwxVdaqARUP_1.wireOp",EDGE,"fcba4419-a2ee-464f-be9d-58f11bf3418b.sketch_text.stroke-112"),sQuery(id+"FQ5JFwxVdaqARUP_1.wireOp",EDGE,"fcba4419-a2ee-464f-be9d-58f11bf3418b.sketch_text.stroke-113"),sQuery(id+"FQ5JFwxVdaqARUP_1.wireOp",EDGE,"fcba4419-a2ee-464f-be9d-58f11bf3418b.sketch_text.stroke-114"),sQuery(id+"FQ5JFwxVdaqARUP_1.wireOp",EDGE,"fcba4419-a2ee-464f-be9d-58f11bf3418b.sketch_text.stroke-115"),sQuery(id+"FQ5JFwxVdaqARUP_1.wireOp",EDGE,"fcba4419-a2ee-464f-be9d-58f11bf3418b.sketch_text.stroke-116"),sQuery(id+"FQ5JFwxVdaqARUP_1.wireOp",EDGE,"fcba4419-a2ee-464f-be9d-58f11bf3418b.sketch_text.stroke-117"),sQuery(id+"FQ5JFwxVdaqARUP_1.wireOp",EDGE,"fcba4419-a2ee-464f-be9d-58f11bf3418b.sketch_text.stroke-118"),sQuery(id+"FQ5JFwxVdaqARUP_1.wireOp",EDGE,"fcba4419-a2ee-464f-be9d-58f11bf3418b.sketch_text.stroke-119"),sQuery(id+"FQ5JFwxVdaqARUP_1.wireOp",EDGE,"fcba4419-a2ee-464f-be9d-58f11bf3418b.sketch_text.stroke-120"),sQuery(id+"FQ5JFwxVdaqARUP_1.wireOp",EDGE,"fcba4419-a2ee-464f-be9d-58f11bf3418b.sketch_text.stroke-121"),sQuery(id+"FQ5JFwxVdaqARUP_1.wireOp",EDGE,"fcba4419-a2ee-464f-be9d-58f11bf3418b.sketch_text.stroke-122"),sQuery(id+"FQ5JFwxVdaqARUP_1.wireOp",EDGE,"fcba4419-a2ee-464f-be9d-58f11bf3418b.sketch_text.stroke-123"),sQuery(id+"FQ5JFwxVdaqARUP_1.wireOp",EDGE,"fcba4419-a2ee-464f-be9d-58f11bf3418b.sketch_text.stroke-124"),sQuery(id+"FQ5JFwxVdaqARUP_1.wireOp",EDGE,"fcba4419-a2ee-464f-be9d-58f11bf3418b.sketch_text.stroke-125"),sQuery(id+"FQ5JFwxVdaqARUP_1.wireOp",EDGE,"fcba4419-a2ee-464f-be9d-58f11bf3418b.sketch_text.stroke-126"),sQuery(id+"FQ5JFwxVdaqARUP_1.wireOp",EDGE,"fcba4419-a2ee-464f-be9d-58f11bf3418b.sketch_text.stroke-127"),sQuery(id+"FQ5JFwxVdaqARUP_1.wireOp",EDGE,"fcba4419-a2ee-464f-be9d-58f11bf3418b.sketch_text.stroke-128"),sQuery(id+"FQ5JFwxVdaqARUP_1.wireOp",EDGE,"fcba4419-a2ee-464f-be9d-58f11bf3418b.sketch_text.stroke-129"),sQuery(id+"FQ5JFwxVdaqARUP_1.wireOp",EDGE,"fcba4419-a2ee-464f-be9d-58f11bf3418b.sketch_text.stroke-130"),sQuery(id+"FQ5JFwxVdaqARUP_1.wireOp",EDGE,"fcba4419-a2ee-464f-be9d-58f11bf3418b.sketch_text.stroke-131"),sQuery(id+"FQ5JFwxVdaqARUP_1.wireOp",EDGE,"fcba4419-a2ee-464f-be9d-58f11bf3418b.sketch_text.stroke-132"),sQuery(id+"FQ5JFwxVdaqARUP_1.wireOp",EDGE,"fcba4419-a2ee-464f-be9d-58f11bf3418b.sketch_text.stroke-133"),sQuery(id+"FQ5JFwxVdaqARUP_1.wireOp",EDGE,"fcba4419-a2ee-464f-be9d-58f11bf3418b.sketch_text.stroke-134"),sQuery(id+"FQ5JFwxVdaqARUP_1.wireOp",EDGE,"fcba4419-a2ee-464f-be9d-58f11bf3418b.sketch_text.stroke-135"),sQuery(id+"FQ5JFwxVdaqARUP_1.wireOp",EDGE,"fcba4419-a2ee-464f-be9d-58f11bf3418b.sketch_text.stroke-136"),sQuery(id+"FQ5JFwxVdaqARUP_1.wireOp",EDGE,"fcba4419-a2ee-464f-be9d-58f11bf3418b.sketch_text.stroke-137"),sQuery(id+"FQ5JFwxVdaqARUP_1.wireOp",EDGE,"fcba4419-a2ee-464f-be9d-58f11bf3418b.sketch_text.stroke-138"),sQuery(id+"FQ5JFwxVdaqARUP_1.wireOp",EDGE,"fcba4419-a2ee-464f-be9d-58f11bf3418b.sketch_text.stroke-139"),sQuery(id+"FQ5JFwxVdaqARUP_1.wireOp",EDGE,"fcba4419-a2ee-464f-be9d-58f11bf3418b.sketch_text.stroke-140"),sQuery(id+"FQ5JFwxVdaqARUP_1.wireOp",EDGE,"fcba4419-a2ee-464f-be9d-58f11bf3418b.sketch_text.stroke-141"),sQuery(id+"FQ5JFwxVdaqARUP_1.wireOp",EDGE,"fcba4419-a2ee-464f-be9d-58f11bf3418b.sketch_text.stroke-142"),sQuery(id+"FQ5JFwxVdaqARUP_1.wireOp",EDGE,"fcba4419-a2ee-464f-be9d-58f11bf3418b.sketch_text.stroke-143"),sQuery(id+"FQ5JFwxVdaqARUP_1.wireOp",EDGE,"fcba4419-a2ee-464f-be9d-58f11bf3418b.sketch_text.stroke-144"),sQuery(id+"FQ5JFwxVdaqARUP_1.wireOp",EDGE,"fcba4419-a2ee-464f-be9d-58f11bf3418b.sketch_text.stroke-145"),sQuery(id+"FQ5JFwxVdaqARUP_1.wireOp",EDGE,"fcba4419-a2ee-464f-be9d-58f11bf3418b.sketch_text.stroke-146"),sQuery(id+"FQ5JFwxVdaqARUP_1.wireOp",EDGE,"fcba4419-a2ee-464f-be9d-58f11bf3418b.sketch_text.stroke-147"),sQuery(id+"FQ5JFwxVdaqARUP_1.wireOp",EDGE,"fcba4419-a2ee-464f-be9d-58f11bf3418b.sketch_text.stroke-148"),sQuery(id+"FQ5JFwxVdaqARUP_1.wireOp",EDGE,"fcba4419-a2ee-464f-be9d-58f11bf3418b.sketch_text.stroke-149"),sQuery(id+"FQ5JFwxVdaqARUP_1.wireOp",EDGE,"fcba4419-a2ee-464f-be9d-58f11bf3418b.sketch_text.stroke-150"),sQuery(id+"FQ5JFwxVdaqARUP_1.wireOp",EDGE,"fcba4419-a2ee-464f-be9d-58f11bf3418b.sketch_text.stroke-151"),sQuery(id+"FQ5JFwxVdaqARUP_1.wireOp",EDGE,"fcba4419-a2ee-464f-be9d-58f11bf3418b.sketch_text.stroke-152"),sQuery(id+"FQ5JFwxVdaqARUP_1.wireOp",EDGE,"fcba4419-a2ee-464f-be9d-58f11bf3418b.sketch_text.stroke-153"),sQuery(id+"FQ5JFwxVdaqARUP_1.wireOp",EDGE,"fcba4419-a2ee-464f-be9d-58f11bf3418b.sketch_text.stroke-154"),sQuery(id+"FQ5JFwxVdaqARUP_1.wireOp",EDGE,"fcba4419-a2ee-464f-be9d-58f11bf3418b.sketch_text.stroke-155"),sQuery(id+"FQ5JFwxVdaqARUP_1.wireOp",EDGE,"fcba4419-a2ee-464f-be9d-58f11bf3418b.sketch_text.stroke-156"),sQuery(id+"FQ5JFwxVdaqARUP_1.wireOp",EDGE,"fcba4419-a2ee-464f-be9d-58f11bf3418b.sketch_text.stroke-157"),sQuery(id+"FQ5JFwxVdaqARUP_1.wireOp",EDGE,"fcba4419-a2ee-464f-be9d-58f11bf3418b.sketch_text.stroke-158"),sQuery(id+"FQ5JFwxVdaqARUP_1.wireOp",EDGE,"fcba4419-a2ee-464f-be9d-58f11bf3418b.sketch_text.stroke-159"),sQuery(id+"FQ5JFwxVdaqARUP_1.wireOp",EDGE,"fcba4419-a2ee-464f-be9d-58f11bf3418b.sketch_text.stroke-160"),sQuery(id+"FQ5JFwxVdaqARUP_1.wireOp",EDGE,"fcba4419-a2ee-464f-be9d-58f11bf3418b.sketch_text.stroke-161"),sQuery(id+"FQ5JFwxVdaqARUP_1.wireOp",EDGE,"fcba4419-a2ee-464f-be9d-58f11bf3418b.sketch_text.stroke-162"),sQuery(id+"FQ5JFwxVdaqARUP_1.wireOp",EDGE,"fcba4419-a2ee-464f-be9d-58f11bf3418b.sketch_text.stroke-163"),sQuery(id+"FQ5JFwxVdaqARUP_1.wireOp",EDGE,"fcba4419-a2ee-464f-be9d-58f11bf3418b.sketch_text.stroke-164"),sQuery(id+"FQ5JFwxVdaqARUP_1.wireOp",EDGE,"fcba4419-a2ee-464f-be9d-58f11bf3418b.sketch_text.stroke-165"),sQuery(id+"FQ5JFwxVdaqARUP_1.wireOp",EDGE,"fcba4419-a2ee-464f-be9d-58f11bf3418b.sketch_text.stroke-166"),sQuery(id+"FQ5JFwxVdaqARUP_1.wireOp",EDGE,"fcba4419-a2ee-464f-be9d-58f11bf3418b.sketch_text.stroke-167"),sQuery(id+"FQ5JFwxVdaqARUP_1.wireOp",EDGE,"fcba4419-a2ee-464f-be9d-58f11bf3418b.sketch_text.stroke-168"),sQuery(id+"FQ5JFwxVdaqARUP_1.wireOp",EDGE,"fcba4419-a2ee-464f-be9d-58f11bf3418b.sketch_text.stroke-169"),sQuery(id+"FQ5JFwxVdaqARUP_1.wireOp",EDGE,"fcba4419-a2ee-464f-be9d-58f11bf3418b.sketch_text.stroke-170"),sQuery(id+"FQ5JFwxVdaqARUP_1.wireOp",EDGE,"fcba4419-a2ee-464f-be9d-58f11bf3418b.sketch_text.stroke-171"),sQuery(id+"FQ5JFwxVdaqARUP_1.wireOp",EDGE,"fcba4419-a2ee-464f-be9d-58f11bf3418b.sketch_text.stroke-172"),sQuery(id+"FQ5JFwxVdaqARUP_1.wireOp",EDGE,"fcba4419-a2ee-464f-be9d-58f11bf3418b.sketch_text.stroke-173"),sQuery(id+"FHMxAyK4CFUKdhS_1.wireOp",EDGE,"1cb9c079-ea9b-4899-8069-e0e3048e911d.sketch_text.stroke-0"),sQuery(id+"FHMxAyK4CFUKdhS_1.wireOp",EDGE,"1cb9c079-ea9b-4899-8069-e0e3048e911d.sketch_text.stroke-1"),sQuery(id+"FHMxAyK4CFUKdhS_1.wireOp",EDGE,"1cb9c079-ea9b-4899-8069-e0e3048e911d.sketch_text.stroke-2"),sQuery(id+"FHMxAyK4CFUKdhS_1.wireOp",EDGE,"1cb9c079-ea9b-4899-8069-e0e3048e911d.sketch_text.stroke-3"),sQuery(id+"FHMxAyK4CFUKdhS_1.wireOp",EDGE,"1cb9c079-ea9b-4899-8069-e0e3048e911d.sketch_text.stroke-4"),sQuery(id+"FHMxAyK4CFUKdhS_1.wireOp",EDGE,"1cb9c079-ea9b-4899-8069-e0e3048e911d.sketch_text.stroke-5"),sQuery(id+"FHMxAyK4CFUKdhS_1.wireOp",EDGE,"1cb9c079-ea9b-4899-8069-e0e3048e911d.sketch_text.stroke-6"),sQuery(id+"FHMxAyK4CFUKdhS_1.wireOp",EDGE,"1cb9c079-ea9b-4899-8069-e0e3048e911d.sketch_text.stroke-7"),sQuery(id+"FHMxAyK4CFUKdhS_1.wireOp",EDGE,"1cb9c079-ea9b-4899-8069-e0e3048e911d.sketch_text.stroke-8"),sQuery(id+"FHMxAyK4CFUKdhS_1.wireOp",EDGE,"1cb9c079-ea9b-4899-8069-e0e3048e911d.sketch_text.stroke-9"),sQuery(id+"FHMxAyK4CFUKdhS_1.wireOp",EDGE,"1cb9c079-ea9b-4899-8069-e0e3048e911d.sketch_text.stroke-10"),sQuery(id+"FHMxAyK4CFUKdhS_1.wireOp",EDGE,"1cb9c079-ea9b-4899-8069-e0e3048e911d.sketch_text.stroke-11"),sQuery(id+"FHMxAyK4CFUKdhS_1.wireOp",EDGE,"1cb9c079-ea9b-4899-8069-e0e3048e911d.sketch_text.stroke-12"),sQuery(id+"FHMxAyK4CFUKdhS_1.wireOp",EDGE,"1cb9c079-ea9b-4899-8069-e0e3048e911d.sketch_text.stroke-13"),sQuery(id+"FHMxAyK4CFUKdhS_1.wireOp",EDGE,"1cb9c079-ea9b-4899-8069-e0e3048e911d.sketch_text.stroke-14"),sQuery(id+"FHMxAyK4CFUKdhS_1.wireOp",EDGE,"1cb9c079-ea9b-4899-8069-e0e3048e911d.sketch_text.stroke-15"),sQuery(id+"FHMxAyK4CFUKdhS_1.wireOp",EDGE,"1cb9c079-ea9b-4899-8069-e0e3048e911d.sketch_text.stroke-16"),sQuery(id+"FHMxAyK4CFUKdhS_1.wireOp",EDGE,"1cb9c079-ea9b-4899-8069-e0e3048e911d.sketch_text.stroke-17"),sQuery(id+"FHMxAyK4CFUKdhS_1.wireOp",EDGE,"1cb9c079-ea9b-4899-8069-e0e3048e911d.sketch_text.stroke-18"),sQuery(id+"FHMxAyK4CFUKdhS_1.wireOp",EDGE,"1cb9c079-ea9b-4899-8069-e0e3048e911d.sketch_text.stroke-19"),sQuery(id+"FHMxAyK4CFUKdhS_1.wireOp",EDGE,"1cb9c079-ea9b-4899-8069-e0e3048e911d.sketch_text.stroke-20"),sQuery(id+"FHMxAyK4CFUKdhS_1.wireOp",EDGE,"1cb9c079-ea9b-4899-8069-e0e3048e911d.sketch_text.stroke-21"),sQuery(id+"FHMxAyK4CFUKdhS_1.wireOp",EDGE,"1cb9c079-ea9b-4899-8069-e0e3048e911d.sketch_text.stroke-22"),sQuery(id+"FHMxAyK4CFUKdhS_1.wireOp",EDGE,"1cb9c079-ea9b-4899-8069-e0e3048e911d.sketch_text.stroke-23"),sQuery(id+"FHMxAyK4CFUKdhS_1.wireOp",EDGE,"1cb9c079-ea9b-4899-8069-e0e3048e911d.sketch_text.stroke-24"),sQuery(id+"FHMxAyK4CFUKdhS_1.wireOp",EDGE,"1cb9c079-ea9b-4899-8069-e0e3048e911d.sketch_text.stroke-25"),sQuery(id+"FHMxAyK4CFUKdhS_1.wireOp",EDGE,"1cb9c079-ea9b-4899-8069-e0e3048e911d.sketch_text.stroke-26"),sQuery(id+"FHMxAyK4CFUKdhS_1.wireOp",EDGE,"1cb9c079-ea9b-4899-8069-e0e3048e911d.sketch_text.stroke-27"),sQuery(id+"FHMxAyK4CFUKdhS_1.wireOp",EDGE,"1cb9c079-ea9b-4899-8069-e0e3048e911d.sketch_text.stroke-28"),sQuery(id+"FHMxAyK4CFUKdhS_1.wireOp",EDGE,"1cb9c079-ea9b-4899-8069-e0e3048e911d.sketch_text.stroke-29"),sQuery(id+"FHMxAyK4CFUKdhS_1.wireOp",EDGE,"1cb9c079-ea9b-4899-8069-e0e3048e911d.sketch_text.stroke-30"),sQuery(id+"FHMxAyK4CFUKdhS_1.wireOp",EDGE,"1cb9c079-ea9b-4899-8069-e0e3048e911d.sketch_text.stroke-31"),sQuery(id+"FHMxAyK4CFUKdhS_1.wireOp",EDGE,"1cb9c079-ea9b-4899-8069-e0e3048e911d.sketch_text.stroke-32"),sQuery(id+"FHMxAyK4CFUKdhS_1.wireOp",EDGE,"1cb9c079-ea9b-4899-8069-e0e3048e911d.sketch_text.stroke-33"),sQuery(id+"FHMxAyK4CFUKdhS_1.wireOp",EDGE,"1cb9c079-ea9b-4899-8069-e0e3048e911d.sketch_text.stroke-34"),sQuery(id+"FHMxAyK4CFUKdhS_1.wireOp",EDGE,"1cb9c079-ea9b-4899-8069-e0e3048e911d.sketch_text.stroke-35"),sQuery(id+"FHMxAyK4CFUKdhS_1.wireOp",EDGE,"1cb9c079-ea9b-4899-8069-e0e3048e911d.sketch_text.stroke-36"),sQuery(id+"FHMxAyK4CFUKdhS_1.wireOp",EDGE,"1cb9c079-ea9b-4899-8069-e0e3048e911d.sketch_text.stroke-37"),sQuery(id+"FHMxAyK4CFUKdhS_1.wireOp",EDGE,"1cb9c079-ea9b-4899-8069-e0e3048e911d.sketch_text.stroke-38"),sQuery(id+"FHMxAyK4CFUKdhS_1.wireOp",EDGE,"1cb9c079-ea9b-4899-8069-e0e3048e911d.sketch_text.stroke-39"),sQuery(id+"FHMxAyK4CFUKdhS_1.wireOp",EDGE,"1cb9c079-ea9b-4899-8069-e0e3048e911d.sketch_text.stroke-40"),sQuery(id+"FHMxAyK4CFUKdhS_1.wireOp",EDGE,"1cb9c079-ea9b-4899-8069-e0e3048e911d.sketch_text.stroke-41"),sQuery(id+"FHMxAyK4CFUKdhS_1.wireOp",EDGE,"1cb9c079-ea9b-4899-8069-e0e3048e911d.sketch_text.stroke-42"),sQuery(id+"FHMxAyK4CFUKdhS_1.wireOp",EDGE,"1cb9c079-ea9b-4899-8069-e0e3048e911d.sketch_text.stroke-43"),sQuery(id+"FHMxAyK4CFUKdhS_1.wireOp",EDGE,"1cb9c079-ea9b-4899-8069-e0e3048e911d.sketch_text.stroke-44"),sQuery(id+"FHMxAyK4CFUKdhS_1.wireOp",EDGE,"1cb9c079-ea9b-4899-8069-e0e3048e911d.sketch_text.stroke-45"),sQuery(id+"FHMxAyK4CFUKdhS_1.wireOp",EDGE,"1cb9c079-ea9b-4899-8069-e0e3048e911d.sketch_text.stroke-46"),sQuery(id+"FHMxAyK4CFUKdhS_1.wireOp",EDGE,"1cb9c079-ea9b-4899-8069-e0e3048e911d.sketch_text.stroke-47"),sQuery(id+"FHMxAyK4CFUKdhS_1.wireOp",EDGE,"1cb9c079-ea9b-4899-8069-e0e3048e911d.sketch_text.stroke-48"),sQuery(id+"FHMxAyK4CFUKdhS_1.wireOp",EDGE,"1cb9c079-ea9b-4899-8069-e0e3048e911d.sketch_text.stroke-49"),sQuery(id+"FHMxAyK4CFUKdhS_1.wireOp",EDGE,"1cb9c079-ea9b-4899-8069-e0e3048e911d.sketch_text.stroke-50"),sQuery(id+"FHMxAyK4CFUKdhS_1.wireOp",EDGE,"1cb9c079-ea9b-4899-8069-e0e3048e911d.sketch_text.stroke-51"),sQuery(id+"FHMxAyK4CFUKdhS_1.wireOp",EDGE,"1cb9c079-ea9b-4899-8069-e0e3048e911d.sketch_text.stroke-52"),sQuery(id+"FHMxAyK4CFUKdhS_1.wireOp",EDGE,"1cb9c079-ea9b-4899-8069-e0e3048e911d.sketch_text.stroke-53"),sQuery(id+"FHMxAyK4CFUKdhS_1.wireOp",EDGE,"1cb9c079-ea9b-4899-8069-e0e3048e911d.sketch_text.stroke-54"),sQuery(id+"FHMxAyK4CFUKdhS_1.wireOp",EDGE,"1cb9c079-ea9b-4899-8069-e0e3048e911d.sketch_text.stroke-55"),sQuery(id+"FHMxAyK4CFUKdhS_1.wireOp",EDGE,"1cb9c079-ea9b-4899-8069-e0e3048e911d.sketch_text.stroke-56"),sQuery(id+"FHMxAyK4CFUKdhS_1.wireOp",EDGE,"1cb9c079-ea9b-4899-8069-e0e3048e911d.sketch_text.stroke-57"),sQuery(id+"FHMxAyK4CFUKdhS_1.wireOp",EDGE,"1cb9c079-ea9b-4899-8069-e0e3048e911d.sketch_text.stroke-58"),sQuery(id+"FHMxAyK4CFUKdhS_1.wireOp",EDGE,"1cb9c079-ea9b-4899-8069-e0e3048e911d.sketch_text.stroke-59"),sQuery(id+"FHMxAyK4CFUKdhS_1.wireOp",EDGE,"1cb9c079-ea9b-4899-8069-e0e3048e911d.sketch_text.stroke-60"),sQuery(id+"FHMxAyK4CFUKdhS_1.wireOp",EDGE,"1cb9c079-ea9b-4899-8069-e0e3048e911d.sketch_text.stroke-61"),sQuery(id+"FHMxAyK4CFUKdhS_1.wireOp",EDGE,"1cb9c079-ea9b-4899-8069-e0e3048e911d.sketch_text.stroke-62"),sQuery(id+"FHMxAyK4CFUKdhS_1.wireOp",EDGE,"1cb9c079-ea9b-4899-8069-e0e3048e911d.sketch_text.stroke-71"),sQuery(id+"FHMxAyK4CFUKdhS_1.wireOp",EDGE,"1cb9c079-ea9b-4899-8069-e0e3048e911d.sketch_text.stroke-72"),sQuery(id+"FHMxAyK4CFUKdhS_1.wireOp",EDGE,"1cb9c079-ea9b-4899-8069-e0e3048e911d.sketch_text.stroke-73"),sQuery(id+"FHMxAyK4CFUKdhS_1.wireOp",EDGE,"1cb9c079-ea9b-4899-8069-e0e3048e911d.sketch_text.stroke-74"),sQuery(id+"FHMxAyK4CFUKdhS_1.wireOp",EDGE,"1cb9c079-ea9b-4899-8069-e0e3048e911d.sketch_text.stroke-75"),sQuery(id+"FHMxAyK4CFUKdhS_1.wireOp",EDGE,"1cb9c079-ea9b-4899-8069-e0e3048e911d.sketch_text.stroke-76"),sQuery(id+"FHMxAyK4CFUKdhS_1.wireOp",EDGE,"1cb9c079-ea9b-4899-8069-e0e3048e911d.sketch_text.stroke-77"),sQuery(id+"FHMxAyK4CFUKdhS_1.wireOp",EDGE,"1cb9c079-ea9b-4899-8069-e0e3048e911d.sketch_text.stroke-78"),sQuery(id+"FHMxAyK4CFUKdhS_1.wireOp",EDGE,"1cb9c079-ea9b-4899-8069-e0e3048e911d.sketch_text.stroke-79"),sQuery(id+"FHMxAyK4CFUKdhS_1.wireOp",EDGE,"1cb9c079-ea9b-4899-8069-e0e3048e911d.sketch_text.stroke-80"),sQuery(id+"FHMxAyK4CFUKdhS_1.wireOp",EDGE,"1cb9c079-ea9b-4899-8069-e0e3048e911d.sketch_text.stroke-81"),sQuery(id+"FHMxAyK4CFUKdhS_1.wireOp",EDGE,"1cb9c079-ea9b-4899-8069-e0e3048e911d.sketch_text.stroke-82"),sQuery(id+"FHMxAyK4CFUKdhS_1.wireOp",EDGE,"1cb9c079-ea9b-4899-8069-e0e3048e911d.sketch_text.stroke-83"),sQuery(id+"FHMxAyK4CFUKdhS_1.wireOp",EDGE,"1cb9c079-ea9b-4899-8069-e0e3048e911d.sketch_text.stroke-84"),sQuery(id+"FHMxAyK4CFUKdhS_1.wireOp",EDGE,"1cb9c079-ea9b-4899-8069-e0e3048e911d.sketch_text.stroke-85"),sQuery(id+"FHMxAyK4CFUKdhS_1.wireOp",EDGE,"1cb9c079-ea9b-4899-8069-e0e3048e911d.sketch_text.stroke-86"),sQuery(id+"FHMxAyK4CFUKdhS_1.wireOp",EDGE,"1cb9c079-ea9b-4899-8069-e0e3048e911d.sketch_text.stroke-87"),sQuery(id+"FHMxAyK4CFUKdhS_1.wireOp",EDGE,"1cb9c079-ea9b-4899-8069-e0e3048e911d.sketch_text.stroke-88"),sQuery(id+"FHMxAyK4CFUKdhS_1.wireOp",EDGE,"1cb9c079-ea9b-4899-8069-e0e3048e911d.sketch_text.stroke-89"),sQuery(id+"FHMxAyK4CFUKdhS_1.wireOp",EDGE,"1cb9c079-ea9b-4899-8069-e0e3048e911d.sketch_text.stroke-90"),sQuery(id+"FHMxAyK4CFUKdhS_1.wireOp",EDGE,"1cb9c079-ea9b-4899-8069-e0e3048e911d.sketch_text.stroke-91"),sQuery(id+"FHMxAyK4CFUKdhS_1.wireOp",EDGE,"1cb9c079-ea9b-4899-8069-e0e3048e911d.sketch_text.stroke-92"),sQuery(id+"FHMxAyK4CFUKdhS_1.wireOp",EDGE,"1cb9c079-ea9b-4899-8069-e0e3048e911d.sketch_text.stroke-93"),sQuery(id+"FHMxAyK4CFUKdhS_1.wireOp",EDGE,"1cb9c079-ea9b-4899-8069-e0e3048e911d.sketch_text.stroke-94"),sQuery(id+"FHMxAyK4CFUKdhS_1.wireOp",EDGE,"1cb9c079-ea9b-4899-8069-e0e3048e911d.sketch_text.stroke-95"),sQuery(id+"FHMxAyK4CFUKdhS_1.wireOp",EDGE,"1cb9c079-ea9b-4899-8069-e0e3048e911d.sketch_text.stroke-96"),sQuery(id+"FHMxAyK4CFUKdhS_1.wireOp",EDGE,"1cb9c079-ea9b-4899-8069-e0e3048e911d.sketch_text.stroke-97"),sQuery(id+"FHMxAyK4CFUKdhS_1.wireOp",EDGE,"1cb9c079-ea9b-4899-8069-e0e3048e911d.sketch_text.stroke-103"),sQuery(id+"FHMxAyK4CFUKdhS_1.wireOp",EDGE,"1cb9c079-ea9b-4899-8069-e0e3048e911d.sketch_text.stroke-104"),sQuery(id+"FHMxAyK4CFUKdhS_1.wireOp",EDGE,"1cb9c079-ea9b-4899-8069-e0e3048e911d.sketch_text.stroke-105"),sQuery(id+"FHMxAyK4CFUKdhS_1.wireOp",EDGE,"1cb9c079-ea9b-4899-8069-e0e3048e911d.sketch_text.stroke-106"),sQuery(id+"FHMxAyK4CFUKdhS_1.wireOp",EDGE,"1cb9c079-ea9b-4899-8069-e0e3048e911d.sketch_text.stroke-107"),sQuery(id+"FHMxAyK4CFUKdhS_1.wireOp",EDGE,"1cb9c079-ea9b-4899-8069-e0e3048e911d.sketch_text.stroke-108"),sQuery(id+"FHMxAyK4CFUKdhS_1.wireOp",EDGE,"1cb9c079-ea9b-4899-8069-e0e3048e911d.sketch_text.stroke-109"),sQuery(id+"FHMxAyK4CFUKdhS_1.wireOp",EDGE,"1cb9c079-ea9b-4899-8069-e0e3048e911d.sketch_text.stroke-110"),sQuery(id+"FHMxAyK4CFUKdhS_1.wireOp",EDGE,"1cb9c079-ea9b-4899-8069-e0e3048e911d.sketch_text.stroke-111"),sQuery(id+"FHMxAyK4CFUKdhS_1.wireOp",EDGE,"1cb9c079-ea9b-4899-8069-e0e3048e911d.sketch_text.stroke-112"),sQuery(id+"FHMxAyK4CFUKdhS_1.wireOp",EDGE,"1cb9c079-ea9b-4899-8069-e0e3048e911d.sketch_text.stroke-113"),sQuery(id+"FHMxAyK4CFUKdhS_1.wireOp",EDGE,"1cb9c079-ea9b-4899-8069-e0e3048e911d.sketch_text.stroke-114"),sQuery(id+"FHMxAyK4CFUKdhS_1.wireOp",EDGE,"1cb9c079-ea9b-4899-8069-e0e3048e911d.sketch_text.stroke-115"),sQuery(id+"FHMxAyK4CFUKdhS_1.wireOp",EDGE,"1cb9c079-ea9b-4899-8069-e0e3048e911d.sketch_text.stroke-116"),sQuery(id+"FHMxAyK4CFUKdhS_1.wireOp",EDGE,"1cb9c079-ea9b-4899-8069-e0e3048e911d.sketch_text.stroke-117"),sQuery(id+"FHMxAyK4CFUKdhS_1.wireOp",EDGE,"1cb9c079-ea9b-4899-8069-e0e3048e911d.sketch_text.stroke-118"),sQuery(id+"FHMxAyK4CFUKdhS_1.wireOp",EDGE,"1cb9c079-ea9b-4899-8069-e0e3048e911d.sketch_text.stroke-119"),sQuery(id+"FHMxAyK4CFUKdhS_1.wireOp",EDGE,"1cb9c079-ea9b-4899-8069-e0e3048e911d.sketch_text.stroke-120"),sQuery(id+"FHMxAyK4CFUKdhS_1.wireOp",EDGE,"1cb9c079-ea9b-4899-8069-e0e3048e911d.sketch_text.stroke-121"),sQuery(id+"FHMxAyK4CFUKdhS_1.wireOp",EDGE,"1cb9c079-ea9b-4899-8069-e0e3048e911d.sketch_text.stroke-122"),sQuery(id+"FHMxAyK4CFUKdhS_1.wireOp",EDGE,"1cb9c079-ea9b-4899-8069-e0e3048e911d.sketch_text.stroke-123"),sQuery(id+"FHMxAyK4CFUKdhS_1.wireOp",EDGE,"1cb9c079-ea9b-4899-8069-e0e3048e911d.sketch_text.stroke-124"),sQuery(id+"FHMxAyK4CFUKdhS_1.wireOp",EDGE,"1cb9c079-ea9b-4899-8069-e0e3048e911d.sketch_text.stroke-125"),sQuery(id+"FHMxAyK4CFUKdhS_1.wireOp",EDGE,"1cb9c079-ea9b-4899-8069-e0e3048e911d.sketch_text.stroke-126"),sQuery(id+"FHMxAyK4CFUKdhS_1.wireOp",EDGE,"1cb9c079-ea9b-4899-8069-e0e3048e911d.sketch_text.stroke-127"),sQuery(id+"FHMxAyK4CFUKdhS_1.wireOp",EDGE,"1cb9c079-ea9b-4899-8069-e0e3048e911d.sketch_text.stroke-128"),sQuery(id+"FHMxAyK4CFUKdhS_1.wireOp",EDGE,"1cb9c079-ea9b-4899-8069-e0e3048e911d.sketch_text.stroke-129"),sQuery(id+"FHMxAyK4CFUKdhS_1.wireOp",EDGE,"1cb9c079-ea9b-4899-8069-e0e3048e911d.sketch_text.stroke-130"),sQuery(id+"FHMxAyK4CFUKdhS_1.wireOp",EDGE,"1cb9c079-ea9b-4899-8069-e0e3048e911d.sketch_text.stroke-131"),sQuery(id+"FHMxAyK4CFUKdhS_1.wireOp",EDGE,"1cb9c079-ea9b-4899-8069-e0e3048e911d.sketch_text.stroke-132"),sQuery(id+"FHMxAyK4CFUKdhS_1.wireOp",EDGE,"1cb9c079-ea9b-4899-8069-e0e3048e911d.sketch_text.stroke-133"),sQuery(id+"FHMxAyK4CFUKdhS_1.wireOp",EDGE,"1cb9c079-ea9b-4899-8069-e0e3048e911d.sketch_text.stroke-134"),sQuery(id+"FHMxAyK4CFUKdhS_1.wireOp",EDGE,"1cb9c079-ea9b-4899-8069-e0e3048e911d.sketch_text.stroke-135"),sQuery(id+"FHMxAyK4CFUKdhS_1.wireOp",EDGE,"1cb9c079-ea9b-4899-8069-e0e3048e911d.sketch_text.stroke-136"),sQuery(id+"FHMxAyK4CFUKdhS_1.wireOp",EDGE,"1cb9c079-ea9b-4899-8069-e0e3048e911d.sketch_text.stroke-137"),sQuery(id+"FHMxAyK4CFUKdhS_1.wireOp",EDGE,"1cb9c079-ea9b-4899-8069-e0e3048e911d.sketch_text.stroke-138"),sQuery(id+"FHMxAyK4CFUKdhS_1.wireOp",EDGE,"1cb9c079-ea9b-4899-8069-e0e3048e911d.sketch_text.stroke-139"),sQuery(id+"FHMxAyK4CFUKdhS_1.wireOp",EDGE,"1cb9c079-ea9b-4899-8069-e0e3048e911d.sketch_text.stroke-140"),sQuery(id+"FHMxAyK4CFUKdhS_1.wireOp",EDGE,"1cb9c079-ea9b-4899-8069-e0e3048e911d.sketch_text.stroke-141"),sQuery(id+"FHMxAyK4CFUKdhS_1.wireOp",EDGE,"1cb9c079-ea9b-4899-8069-e0e3048e911d.sketch_text.stroke-142"),sQuery(id+"FHMxAyK4CFUKdhS_1.wireOp",EDGE,"1cb9c079-ea9b-4899-8069-e0e3048e911d.sketch_text.stroke-143"),sQuery(id+"FHMxAyK4CFUKdhS_1.wireOp",EDGE,"1cb9c079-ea9b-4899-8069-e0e3048e911d.sketch_text.stroke-144"),sQuery(id+"FHMxAyK4CFUKdhS_1.wireOp",EDGE,"1cb9c079-ea9b-4899-8069-e0e3048e911d.sketch_text.stroke-145"),sQuery(id+"FHMxAyK4CFUKdhS_1.wireOp",EDGE,"1cb9c079-ea9b-4899-8069-e0e3048e911d.sketch_text.stroke-146"),sQuery(id+"FHMxAyK4CFUKdhS_1.wireOp",EDGE,"1cb9c079-ea9b-4899-8069-e0e3048e911d.sketch_text.stroke-147"),sQuery(id+"FHMxAyK4CFUKdhS_1.wireOp",EDGE,"1cb9c079-ea9b-4899-8069-e0e3048e911d.sketch_text.stroke-148"),sQuery(id+"FHMxAyK4CFUKdhS_1.wireOp",EDGE,"1cb9c079-ea9b-4899-8069-e0e3048e911d.sketch_text.stroke-149"),sQuery(id+"FHMxAyK4CFUKdhS_1.wireOp",EDGE,"1cb9c079-ea9b-4899-8069-e0e3048e911d.sketch_text.stroke-150"),sQuery(id+"FHMxAyK4CFUKdhS_1.wireOp",EDGE,"1cb9c079-ea9b-4899-8069-e0e3048e911d.sketch_text.stroke-151"),sQuery(id+"FHMxAyK4CFUKdhS_1.wireOp",EDGE,"1cb9c079-ea9b-4899-8069-e0e3048e911d.sketch_text.stroke-152"),sQuery(id+"FHMxAyK4CFUKdhS_1.wireOp",EDGE,"1cb9c079-ea9b-4899-8069-e0e3048e911d.sketch_text.stroke-153"),sQuery(id+"FHMxAyK4CFUKdhS_1.wireOp",EDGE,"1cb9c079-ea9b-4899-8069-e0e3048e911d.sketch_text.stroke-159"),sQuery(id+"FHMxAyK4CFUKdhS_1.wireOp",EDGE,"1cb9c079-ea9b-4899-8069-e0e3048e911d.sketch_text.stroke-160"),sQuery(id+"FHMxAyK4CFUKdhS_1.wireOp",EDGE,"1cb9c079-ea9b-4899-8069-e0e3048e911d.sketch_text.stroke-161"),sQuery(id+"FHMxAyK4CFUKdhS_1.wireOp",EDGE,"1cb9c079-ea9b-4899-8069-e0e3048e911d.sketch_text.stroke-162"),sQuery(id+"FHMxAyK4CFUKdhS_1.wireOp",EDGE,"1cb9c079-ea9b-4899-8069-e0e3048e911d.sketch_text.stroke-163"),sQuery(id+"FHMxAyK4CFUKdhS_1.wireOp",EDGE,"1cb9c079-ea9b-4899-8069-e0e3048e911d.sketch_text.stroke-164"),sQuery(id+"FHMxAyK4CFUKdhS_1.wireOp",EDGE,"1cb9c079-ea9b-4899-8069-e0e3048e911d.sketch_text.stroke-165"),sQuery(id+"FHMxAyK4CFUKdhS_1.wireOp",EDGE,"1cb9c079-ea9b-4899-8069-e0e3048e911d.sketch_text.stroke-166"),sQuery(id+"FHMxAyK4CFUKdhS_1.wireOp",EDGE,"1cb9c079-ea9b-4899-8069-e0e3048e911d.sketch_text.stroke-167"),sQuery(id+"FHMxAyK4CFUKdhS_1.wireOp",EDGE,"1cb9c079-ea9b-4899-8069-e0e3048e911d.sketch_text.stroke-168"),sQuery(id+"FHMxAyK4CFUKdhS_1.wireOp",EDGE,"1cb9c079-ea9b-4899-8069-e0e3048e911d.sketch_text.stroke-169"),sQuery(id+"FHMxAyK4CFUKdhS_1.wireOp",EDGE,"1cb9c079-ea9b-4899-8069-e0e3048e911d.sketch_text.stroke-170"),sQuery(id+"FHMxAyK4CFUKdhS_1.wireOp",EDGE,"1cb9c079-ea9b-4899-8069-e0e3048e911d.sketch_text.stroke-171"),sQuery(id+"FHMxAyK4CFUKdhS_1.wireOp",EDGE,"1cb9c079-ea9b-4899-8069-e0e3048e911d.sketch_text.stroke-172"),sQuery(id+"FHMxAyK4CFUKdhS_1.wireOp",EDGE,"1cb9c079-ea9b-4899-8069-e0e3048e911d.sketch_text.stroke-173"),sQuery(id+"FHMxAyK4CFUKdhS_1.wireOp",EDGE,"1cb9c079-ea9b-4899-8069-e0e3048e911d.sketch_text.stroke-174"),sQuery(id+"FHMxAyK4CFUKdhS_1.wireOp",EDGE,"1cb9c079-ea9b-4899-8069-e0e3048e911d.sketch_text.stroke-175"),sQuery(id+"FHMxAyK4CFUKdhS_1.wireOp",EDGE,"1cb9c079-ea9b-4899-8069-e0e3048e911d.sketch_text.stroke-176"),sQuery(id+"FHMxAyK4CFUKdhS_1.wireOp",EDGE,"1cb9c079-ea9b-4899-8069-e0e3048e911d.sketch_text.stroke-177"),sQuery(id+"FHMxAyK4CFUKdhS_1.wireOp",EDGE,"1cb9c079-ea9b-4899-8069-e0e3048e911d.sketch_text.stroke-178"),sQuery(id+"FHMxAyK4CFUKdhS_1.wireOp",EDGE,"1cb9c079-ea9b-4899-8069-e0e3048e911d.sketch_text.stroke-179"),sQuery(id+"FHMxAyK4CFUKdhS_1.wireOp",EDGE,"1cb9c079-ea9b-4899-8069-e0e3048e911d.sketch_text.stroke-180"),sQuery(id+"F2.wireOp",EDGE,"727ac2c1-f511-4829-95a7-a443ef16a4cd"),subQ2])],"isStart":true}),makeQuery(id+"F3.opExtrude","SWEPT_FACE",FACE,{"disambiguationData":[OSD([subQ2])]})])],"derivedFrom":makeQuery(id+"F3.opExtrude","CAP_EDGE",EDGE,{"disambiguationData":[OSD([subQ2])],"isStart":true})});}
            var Q18;
            {var subQ0=sQuery(id+"F0.wireOp",EDGE,"E0.top");var subQ1=sQuery(id+"F0.wireOp",EDGE,"E0.bottom");var subQ2=sQuery(id+"F2.wireOp",EDGE,"1a034e28-a7c2-419d-97de-c33d70a47301");Q18=makeQuery(id+"F3.boolean.opBoolean","SPLIT",EDGE,{"disambiguationData":[TD([makeQuery(id+"F1.opExtrude","CAP_FACE",FACE,{"disambiguationData":[OSD([subQ1,subQ0,sQuery(id+"F0.wireOp",EDGE,"E0.left"),sQuery(id+"F0.wireOp",EDGE,"E0.right")])],"isStart":false}),makeQuery(id+"F1.opExtrude","SWEPT_FACE",FACE,{"disambiguationData":[OSD([subQ0])]}),makeQuery(id+"F3.opExtrude","CAP_FACE",FACE,{"disambiguationData":[OSD([subQ1,sQuery(id+"FQ5JFwxVdaqARUP_1.wireOp",EDGE,"fcba4419-a2ee-464f-be9d-58f11bf3418b.sketch_text.stroke-0"),sQuery(id+"FQ5JFwxVdaqARUP_1.wireOp",EDGE,"fcba4419-a2ee-464f-be9d-58f11bf3418b.sketch_text.stroke-1"),sQuery(id+"FQ5JFwxVdaqARUP_1.wireOp",EDGE,"fcba4419-a2ee-464f-be9d-58f11bf3418b.sketch_text.stroke-2"),sQuery(id+"FQ5JFwxVdaqARUP_1.wireOp",EDGE,"fcba4419-a2ee-464f-be9d-58f11bf3418b.sketch_text.stroke-3"),sQuery(id+"FQ5JFwxVdaqARUP_1.wireOp",EDGE,"fcba4419-a2ee-464f-be9d-58f11bf3418b.sketch_text.stroke-4"),sQuery(id+"FQ5JFwxVdaqARUP_1.wireOp",EDGE,"fcba4419-a2ee-464f-be9d-58f11bf3418b.sketch_text.stroke-5"),sQuery(id+"FQ5JFwxVdaqARUP_1.wireOp",EDGE,"fcba4419-a2ee-464f-be9d-58f11bf3418b.sketch_text.stroke-6"),sQuery(id+"FQ5JFwxVdaqARUP_1.wireOp",EDGE,"fcba4419-a2ee-464f-be9d-58f11bf3418b.sketch_text.stroke-7"),sQuery(id+"FQ5JFwxVdaqARUP_1.wireOp",EDGE,"fcba4419-a2ee-464f-be9d-58f11bf3418b.sketch_text.stroke-8"),sQuery(id+"FQ5JFwxVdaqARUP_1.wireOp",EDGE,"fcba4419-a2ee-464f-be9d-58f11bf3418b.sketch_text.stroke-9"),sQuery(id+"FQ5JFwxVdaqARUP_1.wireOp",EDGE,"fcba4419-a2ee-464f-be9d-58f11bf3418b.sketch_text.stroke-10"),sQuery(id+"FQ5JFwxVdaqARUP_1.wireOp",EDGE,"fcba4419-a2ee-464f-be9d-58f11bf3418b.sketch_text.stroke-11"),sQuery(id+"FQ5JFwxVdaqARUP_1.wireOp",EDGE,"fcba4419-a2ee-464f-be9d-58f11bf3418b.sketch_text.stroke-12"),sQuery(id+"FQ5JFwxVdaqARUP_1.wireOp",EDGE,"fcba4419-a2ee-464f-be9d-58f11bf3418b.sketch_text.stroke-13"),sQuery(id+"FQ5JFwxVdaqARUP_1.wireOp",EDGE,"fcba4419-a2ee-464f-be9d-58f11bf3418b.sketch_text.stroke-14"),sQuery(id+"FQ5JFwxVdaqARUP_1.wireOp",EDGE,"fcba4419-a2ee-464f-be9d-58f11bf3418b.sketch_text.stroke-15"),sQuery(id+"FQ5JFwxVdaqARUP_1.wireOp",EDGE,"fcba4419-a2ee-464f-be9d-58f11bf3418b.sketch_text.stroke-16"),sQuery(id+"FQ5JFwxVdaqARUP_1.wireOp",EDGE,"fcba4419-a2ee-464f-be9d-58f11bf3418b.sketch_text.stroke-17"),sQuery(id+"FQ5JFwxVdaqARUP_1.wireOp",EDGE,"fcba4419-a2ee-464f-be9d-58f11bf3418b.sketch_text.stroke-18"),sQuery(id+"FQ5JFwxVdaqARUP_1.wireOp",EDGE,"fcba4419-a2ee-464f-be9d-58f11bf3418b.sketch_text.stroke-19"),sQuery(id+"FQ5JFwxVdaqARUP_1.wireOp",EDGE,"fcba4419-a2ee-464f-be9d-58f11bf3418b.sketch_text.stroke-20"),sQuery(id+"FQ5JFwxVdaqARUP_1.wireOp",EDGE,"fcba4419-a2ee-464f-be9d-58f11bf3418b.sketch_text.stroke-21"),sQuery(id+"FQ5JFwxVdaqARUP_1.wireOp",EDGE,"fcba4419-a2ee-464f-be9d-58f11bf3418b.sketch_text.stroke-22"),sQuery(id+"FQ5JFwxVdaqARUP_1.wireOp",EDGE,"fcba4419-a2ee-464f-be9d-58f11bf3418b.sketch_text.stroke-23"),sQuery(id+"FQ5JFwxVdaqARUP_1.wireOp",EDGE,"fcba4419-a2ee-464f-be9d-58f11bf3418b.sketch_text.stroke-24"),sQuery(id+"FQ5JFwxVdaqARUP_1.wireOp",EDGE,"fcba4419-a2ee-464f-be9d-58f11bf3418b.sketch_text.stroke-25"),sQuery(id+"FQ5JFwxVdaqARUP_1.wireOp",EDGE,"fcba4419-a2ee-464f-be9d-58f11bf3418b.sketch_text.stroke-26"),sQuery(id+"FQ5JFwxVdaqARUP_1.wireOp",EDGE,"fcba4419-a2ee-464f-be9d-58f11bf3418b.sketch_text.stroke-27"),sQuery(id+"FQ5JFwxVdaqARUP_1.wireOp",EDGE,"fcba4419-a2ee-464f-be9d-58f11bf3418b.sketch_text.stroke-28"),sQuery(id+"FQ5JFwxVdaqARUP_1.wireOp",EDGE,"fcba4419-a2ee-464f-be9d-58f11bf3418b.sketch_text.stroke-29"),sQuery(id+"FQ5JFwxVdaqARUP_1.wireOp",EDGE,"fcba4419-a2ee-464f-be9d-58f11bf3418b.sketch_text.stroke-30"),sQuery(id+"FQ5JFwxVdaqARUP_1.wireOp",EDGE,"fcba4419-a2ee-464f-be9d-58f11bf3418b.sketch_text.stroke-31"),sQuery(id+"FQ5JFwxVdaqARUP_1.wireOp",EDGE,"fcba4419-a2ee-464f-be9d-58f11bf3418b.sketch_text.stroke-32"),sQuery(id+"FQ5JFwxVdaqARUP_1.wireOp",EDGE,"fcba4419-a2ee-464f-be9d-58f11bf3418b.sketch_text.stroke-33"),sQuery(id+"FQ5JFwxVdaqARUP_1.wireOp",EDGE,"fcba4419-a2ee-464f-be9d-58f11bf3418b.sketch_text.stroke-34"),sQuery(id+"FQ5JFwxVdaqARUP_1.wireOp",EDGE,"fcba4419-a2ee-464f-be9d-58f11bf3418b.sketch_text.stroke-35"),sQuery(id+"FQ5JFwxVdaqARUP_1.wireOp",EDGE,"fcba4419-a2ee-464f-be9d-58f11bf3418b.sketch_text.stroke-36"),sQuery(id+"FQ5JFwxVdaqARUP_1.wireOp",EDGE,"fcba4419-a2ee-464f-be9d-58f11bf3418b.sketch_text.stroke-37"),sQuery(id+"FQ5JFwxVdaqARUP_1.wireOp",EDGE,"fcba4419-a2ee-464f-be9d-58f11bf3418b.sketch_text.stroke-38"),sQuery(id+"FQ5JFwxVdaqARUP_1.wireOp",EDGE,"fcba4419-a2ee-464f-be9d-58f11bf3418b.sketch_text.stroke-39"),sQuery(id+"FQ5JFwxVdaqARUP_1.wireOp",EDGE,"fcba4419-a2ee-464f-be9d-58f11bf3418b.sketch_text.stroke-40"),sQuery(id+"FQ5JFwxVdaqARUP_1.wireOp",EDGE,"fcba4419-a2ee-464f-be9d-58f11bf3418b.sketch_text.stroke-41"),sQuery(id+"FQ5JFwxVdaqARUP_1.wireOp",EDGE,"fcba4419-a2ee-464f-be9d-58f11bf3418b.sketch_text.stroke-42"),sQuery(id+"FQ5JFwxVdaqARUP_1.wireOp",EDGE,"fcba4419-a2ee-464f-be9d-58f11bf3418b.sketch_text.stroke-43"),sQuery(id+"FQ5JFwxVdaqARUP_1.wireOp",EDGE,"fcba4419-a2ee-464f-be9d-58f11bf3418b.sketch_text.stroke-44"),sQuery(id+"FQ5JFwxVdaqARUP_1.wireOp",EDGE,"fcba4419-a2ee-464f-be9d-58f11bf3418b.sketch_text.stroke-45"),sQuery(id+"FQ5JFwxVdaqARUP_1.wireOp",EDGE,"fcba4419-a2ee-464f-be9d-58f11bf3418b.sketch_text.stroke-46"),sQuery(id+"FQ5JFwxVdaqARUP_1.wireOp",EDGE,"fcba4419-a2ee-464f-be9d-58f11bf3418b.sketch_text.stroke-47"),sQuery(id+"FQ5JFwxVdaqARUP_1.wireOp",EDGE,"fcba4419-a2ee-464f-be9d-58f11bf3418b.sketch_text.stroke-48"),sQuery(id+"FQ5JFwxVdaqARUP_1.wireOp",EDGE,"fcba4419-a2ee-464f-be9d-58f11bf3418b.sketch_text.stroke-49"),sQuery(id+"FQ5JFwxVdaqARUP_1.wireOp",EDGE,"fcba4419-a2ee-464f-be9d-58f11bf3418b.sketch_text.stroke-50"),sQuery(id+"FQ5JFwxVdaqARUP_1.wireOp",EDGE,"fcba4419-a2ee-464f-be9d-58f11bf3418b.sketch_text.stroke-51"),sQuery(id+"FQ5JFwxVdaqARUP_1.wireOp",EDGE,"fcba4419-a2ee-464f-be9d-58f11bf3418b.sketch_text.stroke-52"),sQuery(id+"FQ5JFwxVdaqARUP_1.wireOp",EDGE,"fcba4419-a2ee-464f-be9d-58f11bf3418b.sketch_text.stroke-53"),sQuery(id+"FQ5JFwxVdaqARUP_1.wireOp",EDGE,"fcba4419-a2ee-464f-be9d-58f11bf3418b.sketch_text.stroke-54"),sQuery(id+"FQ5JFwxVdaqARUP_1.wireOp",EDGE,"fcba4419-a2ee-464f-be9d-58f11bf3418b.sketch_text.stroke-55"),sQuery(id+"FQ5JFwxVdaqARUP_1.wireOp",EDGE,"fcba4419-a2ee-464f-be9d-58f11bf3418b.sketch_text.stroke-56"),sQuery(id+"FQ5JFwxVdaqARUP_1.wireOp",EDGE,"fcba4419-a2ee-464f-be9d-58f11bf3418b.sketch_text.stroke-57"),sQuery(id+"FQ5JFwxVdaqARUP_1.wireOp",EDGE,"fcba4419-a2ee-464f-be9d-58f11bf3418b.sketch_text.stroke-58"),sQuery(id+"FQ5JFwxVdaqARUP_1.wireOp",EDGE,"fcba4419-a2ee-464f-be9d-58f11bf3418b.sketch_text.stroke-59"),sQuery(id+"FQ5JFwxVdaqARUP_1.wireOp",EDGE,"fcba4419-a2ee-464f-be9d-58f11bf3418b.sketch_text.stroke-60"),sQuery(id+"FQ5JFwxVdaqARUP_1.wireOp",EDGE,"fcba4419-a2ee-464f-be9d-58f11bf3418b.sketch_text.stroke-61"),sQuery(id+"FQ5JFwxVdaqARUP_1.wireOp",EDGE,"fcba4419-a2ee-464f-be9d-58f11bf3418b.sketch_text.stroke-62"),sQuery(id+"FQ5JFwxVdaqARUP_1.wireOp",EDGE,"fcba4419-a2ee-464f-be9d-58f11bf3418b.sketch_text.stroke-63"),sQuery(id+"FQ5JFwxVdaqARUP_1.wireOp",EDGE,"fcba4419-a2ee-464f-be9d-58f11bf3418b.sketch_text.stroke-64"),sQuery(id+"FQ5JFwxVdaqARUP_1.wireOp",EDGE,"fcba4419-a2ee-464f-be9d-58f11bf3418b.sketch_text.stroke-65"),sQuery(id+"FQ5JFwxVdaqARUP_1.wireOp",EDGE,"fcba4419-a2ee-464f-be9d-58f11bf3418b.sketch_text.stroke-66"),sQuery(id+"FQ5JFwxVdaqARUP_1.wireOp",EDGE,"fcba4419-a2ee-464f-be9d-58f11bf3418b.sketch_text.stroke-67"),sQuery(id+"FQ5JFwxVdaqARUP_1.wireOp",EDGE,"fcba4419-a2ee-464f-be9d-58f11bf3418b.sketch_text.stroke-68"),sQuery(id+"FQ5JFwxVdaqARUP_1.wireOp",EDGE,"fcba4419-a2ee-464f-be9d-58f11bf3418b.sketch_text.stroke-69"),sQuery(id+"FQ5JFwxVdaqARUP_1.wireOp",EDGE,"fcba4419-a2ee-464f-be9d-58f11bf3418b.sketch_text.stroke-70"),sQuery(id+"FQ5JFwxVdaqARUP_1.wireOp",EDGE,"fcba4419-a2ee-464f-be9d-58f11bf3418b.sketch_text.stroke-71"),sQuery(id+"FQ5JFwxVdaqARUP_1.wireOp",EDGE,"fcba4419-a2ee-464f-be9d-58f11bf3418b.sketch_text.stroke-72"),sQuery(id+"FQ5JFwxVdaqARUP_1.wireOp",EDGE,"fcba4419-a2ee-464f-be9d-58f11bf3418b.sketch_text.stroke-73"),sQuery(id+"FQ5JFwxVdaqARUP_1.wireOp",EDGE,"fcba4419-a2ee-464f-be9d-58f11bf3418b.sketch_text.stroke-74"),sQuery(id+"FQ5JFwxVdaqARUP_1.wireOp",EDGE,"fcba4419-a2ee-464f-be9d-58f11bf3418b.sketch_text.stroke-75"),sQuery(id+"FQ5JFwxVdaqARUP_1.wireOp",EDGE,"fcba4419-a2ee-464f-be9d-58f11bf3418b.sketch_text.stroke-76"),sQuery(id+"FQ5JFwxVdaqARUP_1.wireOp",EDGE,"fcba4419-a2ee-464f-be9d-58f11bf3418b.sketch_text.stroke-77"),sQuery(id+"FQ5JFwxVdaqARUP_1.wireOp",EDGE,"fcba4419-a2ee-464f-be9d-58f11bf3418b.sketch_text.stroke-78"),sQuery(id+"FQ5JFwxVdaqARUP_1.wireOp",EDGE,"fcba4419-a2ee-464f-be9d-58f11bf3418b.sketch_text.stroke-79"),sQuery(id+"FQ5JFwxVdaqARUP_1.wireOp",EDGE,"fcba4419-a2ee-464f-be9d-58f11bf3418b.sketch_text.stroke-80"),sQuery(id+"FQ5JFwxVdaqARUP_1.wireOp",EDGE,"fcba4419-a2ee-464f-be9d-58f11bf3418b.sketch_text.stroke-81"),sQuery(id+"FQ5JFwxVdaqARUP_1.wireOp",EDGE,"fcba4419-a2ee-464f-be9d-58f11bf3418b.sketch_text.stroke-82"),sQuery(id+"FQ5JFwxVdaqARUP_1.wireOp",EDGE,"fcba4419-a2ee-464f-be9d-58f11bf3418b.sketch_text.stroke-83"),sQuery(id+"FQ5JFwxVdaqARUP_1.wireOp",EDGE,"fcba4419-a2ee-464f-be9d-58f11bf3418b.sketch_text.stroke-84"),sQuery(id+"FQ5JFwxVdaqARUP_1.wireOp",EDGE,"fcba4419-a2ee-464f-be9d-58f11bf3418b.sketch_text.stroke-85"),sQuery(id+"FQ5JFwxVdaqARUP_1.wireOp",EDGE,"fcba4419-a2ee-464f-be9d-58f11bf3418b.sketch_text.stroke-86"),sQuery(id+"FQ5JFwxVdaqARUP_1.wireOp",EDGE,"fcba4419-a2ee-464f-be9d-58f11bf3418b.sketch_text.stroke-87"),sQuery(id+"FQ5JFwxVdaqARUP_1.wireOp",EDGE,"fcba4419-a2ee-464f-be9d-58f11bf3418b.sketch_text.stroke-88"),sQuery(id+"FQ5JFwxVdaqARUP_1.wireOp",EDGE,"fcba4419-a2ee-464f-be9d-58f11bf3418b.sketch_text.stroke-89"),sQuery(id+"FQ5JFwxVdaqARUP_1.wireOp",EDGE,"fcba4419-a2ee-464f-be9d-58f11bf3418b.sketch_text.stroke-90"),sQuery(id+"FQ5JFwxVdaqARUP_1.wireOp",EDGE,"fcba4419-a2ee-464f-be9d-58f11bf3418b.sketch_text.stroke-91"),sQuery(id+"FQ5JFwxVdaqARUP_1.wireOp",EDGE,"fcba4419-a2ee-464f-be9d-58f11bf3418b.sketch_text.stroke-92"),sQuery(id+"FQ5JFwxVdaqARUP_1.wireOp",EDGE,"fcba4419-a2ee-464f-be9d-58f11bf3418b.sketch_text.stroke-93"),sQuery(id+"FQ5JFwxVdaqARUP_1.wireOp",EDGE,"fcba4419-a2ee-464f-be9d-58f11bf3418b.sketch_text.stroke-94"),sQuery(id+"FQ5JFwxVdaqARUP_1.wireOp",EDGE,"fcba4419-a2ee-464f-be9d-58f11bf3418b.sketch_text.stroke-95"),sQuery(id+"FQ5JFwxVdaqARUP_1.wireOp",EDGE,"fcba4419-a2ee-464f-be9d-58f11bf3418b.sketch_text.stroke-96"),sQuery(id+"FQ5JFwxVdaqARUP_1.wireOp",EDGE,"fcba4419-a2ee-464f-be9d-58f11bf3418b.sketch_text.stroke-97"),sQuery(id+"FQ5JFwxVdaqARUP_1.wireOp",EDGE,"fcba4419-a2ee-464f-be9d-58f11bf3418b.sketch_text.stroke-98"),sQuery(id+"FQ5JFwxVdaqARUP_1.wireOp",EDGE,"fcba4419-a2ee-464f-be9d-58f11bf3418b.sketch_text.stroke-99"),sQuery(id+"FQ5JFwxVdaqARUP_1.wireOp",EDGE,"fcba4419-a2ee-464f-be9d-58f11bf3418b.sketch_text.stroke-100"),sQuery(id+"FQ5JFwxVdaqARUP_1.wireOp",EDGE,"fcba4419-a2ee-464f-be9d-58f11bf3418b.sketch_text.stroke-101"),sQuery(id+"FQ5JFwxVdaqARUP_1.wireOp",EDGE,"fcba4419-a2ee-464f-be9d-58f11bf3418b.sketch_text.stroke-102"),sQuery(id+"FQ5JFwxVdaqARUP_1.wireOp",EDGE,"fcba4419-a2ee-464f-be9d-58f11bf3418b.sketch_text.stroke-103"),sQuery(id+"FQ5JFwxVdaqARUP_1.wireOp",EDGE,"fcba4419-a2ee-464f-be9d-58f11bf3418b.sketch_text.stroke-104"),sQuery(id+"FQ5JFwxVdaqARUP_1.wireOp",EDGE,"fcba4419-a2ee-464f-be9d-58f11bf3418b.sketch_text.stroke-105"),sQuery(id+"FQ5JFwxVdaqARUP_1.wireOp",EDGE,"fcba4419-a2ee-464f-be9d-58f11bf3418b.sketch_text.stroke-106"),sQuery(id+"FQ5JFwxVdaqARUP_1.wireOp",EDGE,"fcba4419-a2ee-464f-be9d-58f11bf3418b.sketch_text.stroke-107"),sQuery(id+"FQ5JFwxVdaqARUP_1.wireOp",EDGE,"fcba4419-a2ee-464f-be9d-58f11bf3418b.sketch_text.stroke-108"),sQuery(id+"FQ5JFwxVdaqARUP_1.wireOp",EDGE,"fcba4419-a2ee-464f-be9d-58f11bf3418b.sketch_text.stroke-109"),sQuery(id+"FQ5JFwxVdaqARUP_1.wireOp",EDGE,"fcba4419-a2ee-464f-be9d-58f11bf3418b.sketch_text.stroke-110"),sQuery(id+"FQ5JFwxVdaqARUP_1.wireOp",EDGE,"fcba4419-a2ee-464f-be9d-58f11bf3418b.sketch_text.stroke-111"),sQuery(id+"FQ5JFwxVdaqARUP_1.wireOp",EDGE,"fcba4419-a2ee-464f-be9d-58f11bf3418b.sketch_text.stroke-112"),sQuery(id+"FQ5JFwxVdaqARUP_1.wireOp",EDGE,"fcba4419-a2ee-464f-be9d-58f11bf3418b.sketch_text.stroke-113"),sQuery(id+"FQ5JFwxVdaqARUP_1.wireOp",EDGE,"fcba4419-a2ee-464f-be9d-58f11bf3418b.sketch_text.stroke-114"),sQuery(id+"FQ5JFwxVdaqARUP_1.wireOp",EDGE,"fcba4419-a2ee-464f-be9d-58f11bf3418b.sketch_text.stroke-115"),sQuery(id+"FQ5JFwxVdaqARUP_1.wireOp",EDGE,"fcba4419-a2ee-464f-be9d-58f11bf3418b.sketch_text.stroke-116"),sQuery(id+"FQ5JFwxVdaqARUP_1.wireOp",EDGE,"fcba4419-a2ee-464f-be9d-58f11bf3418b.sketch_text.stroke-117"),sQuery(id+"FQ5JFwxVdaqARUP_1.wireOp",EDGE,"fcba4419-a2ee-464f-be9d-58f11bf3418b.sketch_text.stroke-118"),sQuery(id+"FQ5JFwxVdaqARUP_1.wireOp",EDGE,"fcba4419-a2ee-464f-be9d-58f11bf3418b.sketch_text.stroke-119"),sQuery(id+"FQ5JFwxVdaqARUP_1.wireOp",EDGE,"fcba4419-a2ee-464f-be9d-58f11bf3418b.sketch_text.stroke-120"),sQuery(id+"FQ5JFwxVdaqARUP_1.wireOp",EDGE,"fcba4419-a2ee-464f-be9d-58f11bf3418b.sketch_text.stroke-121"),sQuery(id+"FQ5JFwxVdaqARUP_1.wireOp",EDGE,"fcba4419-a2ee-464f-be9d-58f11bf3418b.sketch_text.stroke-122"),sQuery(id+"FQ5JFwxVdaqARUP_1.wireOp",EDGE,"fcba4419-a2ee-464f-be9d-58f11bf3418b.sketch_text.stroke-123"),sQuery(id+"FQ5JFwxVdaqARUP_1.wireOp",EDGE,"fcba4419-a2ee-464f-be9d-58f11bf3418b.sketch_text.stroke-124"),sQuery(id+"FQ5JFwxVdaqARUP_1.wireOp",EDGE,"fcba4419-a2ee-464f-be9d-58f11bf3418b.sketch_text.stroke-125"),sQuery(id+"FQ5JFwxVdaqARUP_1.wireOp",EDGE,"fcba4419-a2ee-464f-be9d-58f11bf3418b.sketch_text.stroke-126"),sQuery(id+"FQ5JFwxVdaqARUP_1.wireOp",EDGE,"fcba4419-a2ee-464f-be9d-58f11bf3418b.sketch_text.stroke-127"),sQuery(id+"FQ5JFwxVdaqARUP_1.wireOp",EDGE,"fcba4419-a2ee-464f-be9d-58f11bf3418b.sketch_text.stroke-128"),sQuery(id+"FQ5JFwxVdaqARUP_1.wireOp",EDGE,"fcba4419-a2ee-464f-be9d-58f11bf3418b.sketch_text.stroke-129"),sQuery(id+"FQ5JFwxVdaqARUP_1.wireOp",EDGE,"fcba4419-a2ee-464f-be9d-58f11bf3418b.sketch_text.stroke-130"),sQuery(id+"FQ5JFwxVdaqARUP_1.wireOp",EDGE,"fcba4419-a2ee-464f-be9d-58f11bf3418b.sketch_text.stroke-131"),sQuery(id+"FQ5JFwxVdaqARUP_1.wireOp",EDGE,"fcba4419-a2ee-464f-be9d-58f11bf3418b.sketch_text.stroke-132"),sQuery(id+"FQ5JFwxVdaqARUP_1.wireOp",EDGE,"fcba4419-a2ee-464f-be9d-58f11bf3418b.sketch_text.stroke-133"),sQuery(id+"FQ5JFwxVdaqARUP_1.wireOp",EDGE,"fcba4419-a2ee-464f-be9d-58f11bf3418b.sketch_text.stroke-134"),sQuery(id+"FQ5JFwxVdaqARUP_1.wireOp",EDGE,"fcba4419-a2ee-464f-be9d-58f11bf3418b.sketch_text.stroke-135"),sQuery(id+"FQ5JFwxVdaqARUP_1.wireOp",EDGE,"fcba4419-a2ee-464f-be9d-58f11bf3418b.sketch_text.stroke-136"),sQuery(id+"FQ5JFwxVdaqARUP_1.wireOp",EDGE,"fcba4419-a2ee-464f-be9d-58f11bf3418b.sketch_text.stroke-137"),sQuery(id+"FQ5JFwxVdaqARUP_1.wireOp",EDGE,"fcba4419-a2ee-464f-be9d-58f11bf3418b.sketch_text.stroke-138"),sQuery(id+"FQ5JFwxVdaqARUP_1.wireOp",EDGE,"fcba4419-a2ee-464f-be9d-58f11bf3418b.sketch_text.stroke-139"),sQuery(id+"FQ5JFwxVdaqARUP_1.wireOp",EDGE,"fcba4419-a2ee-464f-be9d-58f11bf3418b.sketch_text.stroke-140"),sQuery(id+"FQ5JFwxVdaqARUP_1.wireOp",EDGE,"fcba4419-a2ee-464f-be9d-58f11bf3418b.sketch_text.stroke-141"),sQuery(id+"FQ5JFwxVdaqARUP_1.wireOp",EDGE,"fcba4419-a2ee-464f-be9d-58f11bf3418b.sketch_text.stroke-142"),sQuery(id+"FQ5JFwxVdaqARUP_1.wireOp",EDGE,"fcba4419-a2ee-464f-be9d-58f11bf3418b.sketch_text.stroke-143"),sQuery(id+"FQ5JFwxVdaqARUP_1.wireOp",EDGE,"fcba4419-a2ee-464f-be9d-58f11bf3418b.sketch_text.stroke-144"),sQuery(id+"FQ5JFwxVdaqARUP_1.wireOp",EDGE,"fcba4419-a2ee-464f-be9d-58f11bf3418b.sketch_text.stroke-145"),sQuery(id+"FQ5JFwxVdaqARUP_1.wireOp",EDGE,"fcba4419-a2ee-464f-be9d-58f11bf3418b.sketch_text.stroke-146"),sQuery(id+"FQ5JFwxVdaqARUP_1.wireOp",EDGE,"fcba4419-a2ee-464f-be9d-58f11bf3418b.sketch_text.stroke-147"),sQuery(id+"FQ5JFwxVdaqARUP_1.wireOp",EDGE,"fcba4419-a2ee-464f-be9d-58f11bf3418b.sketch_text.stroke-148"),sQuery(id+"FQ5JFwxVdaqARUP_1.wireOp",EDGE,"fcba4419-a2ee-464f-be9d-58f11bf3418b.sketch_text.stroke-149"),sQuery(id+"FQ5JFwxVdaqARUP_1.wireOp",EDGE,"fcba4419-a2ee-464f-be9d-58f11bf3418b.sketch_text.stroke-150"),sQuery(id+"FQ5JFwxVdaqARUP_1.wireOp",EDGE,"fcba4419-a2ee-464f-be9d-58f11bf3418b.sketch_text.stroke-151"),sQuery(id+"FQ5JFwxVdaqARUP_1.wireOp",EDGE,"fcba4419-a2ee-464f-be9d-58f11bf3418b.sketch_text.stroke-152"),sQuery(id+"FQ5JFwxVdaqARUP_1.wireOp",EDGE,"fcba4419-a2ee-464f-be9d-58f11bf3418b.sketch_text.stroke-153"),sQuery(id+"FQ5JFwxVdaqARUP_1.wireOp",EDGE,"fcba4419-a2ee-464f-be9d-58f11bf3418b.sketch_text.stroke-154"),sQuery(id+"FQ5JFwxVdaqARUP_1.wireOp",EDGE,"fcba4419-a2ee-464f-be9d-58f11bf3418b.sketch_text.stroke-155"),sQuery(id+"FQ5JFwxVdaqARUP_1.wireOp",EDGE,"fcba4419-a2ee-464f-be9d-58f11bf3418b.sketch_text.stroke-156"),sQuery(id+"FQ5JFwxVdaqARUP_1.wireOp",EDGE,"fcba4419-a2ee-464f-be9d-58f11bf3418b.sketch_text.stroke-157"),sQuery(id+"FQ5JFwxVdaqARUP_1.wireOp",EDGE,"fcba4419-a2ee-464f-be9d-58f11bf3418b.sketch_text.stroke-158"),sQuery(id+"FQ5JFwxVdaqARUP_1.wireOp",EDGE,"fcba4419-a2ee-464f-be9d-58f11bf3418b.sketch_text.stroke-159"),sQuery(id+"FQ5JFwxVdaqARUP_1.wireOp",EDGE,"fcba4419-a2ee-464f-be9d-58f11bf3418b.sketch_text.stroke-160"),sQuery(id+"FQ5JFwxVdaqARUP_1.wireOp",EDGE,"fcba4419-a2ee-464f-be9d-58f11bf3418b.sketch_text.stroke-161"),sQuery(id+"FQ5JFwxVdaqARUP_1.wireOp",EDGE,"fcba4419-a2ee-464f-be9d-58f11bf3418b.sketch_text.stroke-162"),sQuery(id+"FQ5JFwxVdaqARUP_1.wireOp",EDGE,"fcba4419-a2ee-464f-be9d-58f11bf3418b.sketch_text.stroke-163"),sQuery(id+"FQ5JFwxVdaqARUP_1.wireOp",EDGE,"fcba4419-a2ee-464f-be9d-58f11bf3418b.sketch_text.stroke-164"),sQuery(id+"FQ5JFwxVdaqARUP_1.wireOp",EDGE,"fcba4419-a2ee-464f-be9d-58f11bf3418b.sketch_text.stroke-165"),sQuery(id+"FQ5JFwxVdaqARUP_1.wireOp",EDGE,"fcba4419-a2ee-464f-be9d-58f11bf3418b.sketch_text.stroke-166"),sQuery(id+"FQ5JFwxVdaqARUP_1.wireOp",EDGE,"fcba4419-a2ee-464f-be9d-58f11bf3418b.sketch_text.stroke-167"),sQuery(id+"FQ5JFwxVdaqARUP_1.wireOp",EDGE,"fcba4419-a2ee-464f-be9d-58f11bf3418b.sketch_text.stroke-168"),sQuery(id+"FQ5JFwxVdaqARUP_1.wireOp",EDGE,"fcba4419-a2ee-464f-be9d-58f11bf3418b.sketch_text.stroke-169"),sQuery(id+"FQ5JFwxVdaqARUP_1.wireOp",EDGE,"fcba4419-a2ee-464f-be9d-58f11bf3418b.sketch_text.stroke-170"),sQuery(id+"FQ5JFwxVdaqARUP_1.wireOp",EDGE,"fcba4419-a2ee-464f-be9d-58f11bf3418b.sketch_text.stroke-171"),sQuery(id+"FQ5JFwxVdaqARUP_1.wireOp",EDGE,"fcba4419-a2ee-464f-be9d-58f11bf3418b.sketch_text.stroke-172"),sQuery(id+"FQ5JFwxVdaqARUP_1.wireOp",EDGE,"fcba4419-a2ee-464f-be9d-58f11bf3418b.sketch_text.stroke-173"),sQuery(id+"FHMxAyK4CFUKdhS_1.wireOp",EDGE,"1cb9c079-ea9b-4899-8069-e0e3048e911d.sketch_text.stroke-0"),sQuery(id+"FHMxAyK4CFUKdhS_1.wireOp",EDGE,"1cb9c079-ea9b-4899-8069-e0e3048e911d.sketch_text.stroke-1"),sQuery(id+"FHMxAyK4CFUKdhS_1.wireOp",EDGE,"1cb9c079-ea9b-4899-8069-e0e3048e911d.sketch_text.stroke-2"),sQuery(id+"FHMxAyK4CFUKdhS_1.wireOp",EDGE,"1cb9c079-ea9b-4899-8069-e0e3048e911d.sketch_text.stroke-3"),sQuery(id+"FHMxAyK4CFUKdhS_1.wireOp",EDGE,"1cb9c079-ea9b-4899-8069-e0e3048e911d.sketch_text.stroke-4"),sQuery(id+"FHMxAyK4CFUKdhS_1.wireOp",EDGE,"1cb9c079-ea9b-4899-8069-e0e3048e911d.sketch_text.stroke-5"),sQuery(id+"FHMxAyK4CFUKdhS_1.wireOp",EDGE,"1cb9c079-ea9b-4899-8069-e0e3048e911d.sketch_text.stroke-6"),sQuery(id+"FHMxAyK4CFUKdhS_1.wireOp",EDGE,"1cb9c079-ea9b-4899-8069-e0e3048e911d.sketch_text.stroke-7"),sQuery(id+"FHMxAyK4CFUKdhS_1.wireOp",EDGE,"1cb9c079-ea9b-4899-8069-e0e3048e911d.sketch_text.stroke-8"),sQuery(id+"FHMxAyK4CFUKdhS_1.wireOp",EDGE,"1cb9c079-ea9b-4899-8069-e0e3048e911d.sketch_text.stroke-9"),sQuery(id+"FHMxAyK4CFUKdhS_1.wireOp",EDGE,"1cb9c079-ea9b-4899-8069-e0e3048e911d.sketch_text.stroke-10"),sQuery(id+"FHMxAyK4CFUKdhS_1.wireOp",EDGE,"1cb9c079-ea9b-4899-8069-e0e3048e911d.sketch_text.stroke-11"),sQuery(id+"FHMxAyK4CFUKdhS_1.wireOp",EDGE,"1cb9c079-ea9b-4899-8069-e0e3048e911d.sketch_text.stroke-12"),sQuery(id+"FHMxAyK4CFUKdhS_1.wireOp",EDGE,"1cb9c079-ea9b-4899-8069-e0e3048e911d.sketch_text.stroke-13"),sQuery(id+"FHMxAyK4CFUKdhS_1.wireOp",EDGE,"1cb9c079-ea9b-4899-8069-e0e3048e911d.sketch_text.stroke-14"),sQuery(id+"FHMxAyK4CFUKdhS_1.wireOp",EDGE,"1cb9c079-ea9b-4899-8069-e0e3048e911d.sketch_text.stroke-15"),sQuery(id+"FHMxAyK4CFUKdhS_1.wireOp",EDGE,"1cb9c079-ea9b-4899-8069-e0e3048e911d.sketch_text.stroke-16"),sQuery(id+"FHMxAyK4CFUKdhS_1.wireOp",EDGE,"1cb9c079-ea9b-4899-8069-e0e3048e911d.sketch_text.stroke-17"),sQuery(id+"FHMxAyK4CFUKdhS_1.wireOp",EDGE,"1cb9c079-ea9b-4899-8069-e0e3048e911d.sketch_text.stroke-18"),sQuery(id+"FHMxAyK4CFUKdhS_1.wireOp",EDGE,"1cb9c079-ea9b-4899-8069-e0e3048e911d.sketch_text.stroke-19"),sQuery(id+"FHMxAyK4CFUKdhS_1.wireOp",EDGE,"1cb9c079-ea9b-4899-8069-e0e3048e911d.sketch_text.stroke-20"),sQuery(id+"FHMxAyK4CFUKdhS_1.wireOp",EDGE,"1cb9c079-ea9b-4899-8069-e0e3048e911d.sketch_text.stroke-21"),sQuery(id+"FHMxAyK4CFUKdhS_1.wireOp",EDGE,"1cb9c079-ea9b-4899-8069-e0e3048e911d.sketch_text.stroke-22"),sQuery(id+"FHMxAyK4CFUKdhS_1.wireOp",EDGE,"1cb9c079-ea9b-4899-8069-e0e3048e911d.sketch_text.stroke-23"),sQuery(id+"FHMxAyK4CFUKdhS_1.wireOp",EDGE,"1cb9c079-ea9b-4899-8069-e0e3048e911d.sketch_text.stroke-24"),sQuery(id+"FHMxAyK4CFUKdhS_1.wireOp",EDGE,"1cb9c079-ea9b-4899-8069-e0e3048e911d.sketch_text.stroke-25"),sQuery(id+"FHMxAyK4CFUKdhS_1.wireOp",EDGE,"1cb9c079-ea9b-4899-8069-e0e3048e911d.sketch_text.stroke-26"),sQuery(id+"FHMxAyK4CFUKdhS_1.wireOp",EDGE,"1cb9c079-ea9b-4899-8069-e0e3048e911d.sketch_text.stroke-27"),sQuery(id+"FHMxAyK4CFUKdhS_1.wireOp",EDGE,"1cb9c079-ea9b-4899-8069-e0e3048e911d.sketch_text.stroke-28"),sQuery(id+"FHMxAyK4CFUKdhS_1.wireOp",EDGE,"1cb9c079-ea9b-4899-8069-e0e3048e911d.sketch_text.stroke-29"),sQuery(id+"FHMxAyK4CFUKdhS_1.wireOp",EDGE,"1cb9c079-ea9b-4899-8069-e0e3048e911d.sketch_text.stroke-30"),sQuery(id+"FHMxAyK4CFUKdhS_1.wireOp",EDGE,"1cb9c079-ea9b-4899-8069-e0e3048e911d.sketch_text.stroke-31"),sQuery(id+"FHMxAyK4CFUKdhS_1.wireOp",EDGE,"1cb9c079-ea9b-4899-8069-e0e3048e911d.sketch_text.stroke-32"),sQuery(id+"FHMxAyK4CFUKdhS_1.wireOp",EDGE,"1cb9c079-ea9b-4899-8069-e0e3048e911d.sketch_text.stroke-33"),sQuery(id+"FHMxAyK4CFUKdhS_1.wireOp",EDGE,"1cb9c079-ea9b-4899-8069-e0e3048e911d.sketch_text.stroke-34"),sQuery(id+"FHMxAyK4CFUKdhS_1.wireOp",EDGE,"1cb9c079-ea9b-4899-8069-e0e3048e911d.sketch_text.stroke-35"),sQuery(id+"FHMxAyK4CFUKdhS_1.wireOp",EDGE,"1cb9c079-ea9b-4899-8069-e0e3048e911d.sketch_text.stroke-36"),sQuery(id+"FHMxAyK4CFUKdhS_1.wireOp",EDGE,"1cb9c079-ea9b-4899-8069-e0e3048e911d.sketch_text.stroke-37"),sQuery(id+"FHMxAyK4CFUKdhS_1.wireOp",EDGE,"1cb9c079-ea9b-4899-8069-e0e3048e911d.sketch_text.stroke-38"),sQuery(id+"FHMxAyK4CFUKdhS_1.wireOp",EDGE,"1cb9c079-ea9b-4899-8069-e0e3048e911d.sketch_text.stroke-39"),sQuery(id+"FHMxAyK4CFUKdhS_1.wireOp",EDGE,"1cb9c079-ea9b-4899-8069-e0e3048e911d.sketch_text.stroke-40"),sQuery(id+"FHMxAyK4CFUKdhS_1.wireOp",EDGE,"1cb9c079-ea9b-4899-8069-e0e3048e911d.sketch_text.stroke-41"),sQuery(id+"FHMxAyK4CFUKdhS_1.wireOp",EDGE,"1cb9c079-ea9b-4899-8069-e0e3048e911d.sketch_text.stroke-42"),sQuery(id+"FHMxAyK4CFUKdhS_1.wireOp",EDGE,"1cb9c079-ea9b-4899-8069-e0e3048e911d.sketch_text.stroke-43"),sQuery(id+"FHMxAyK4CFUKdhS_1.wireOp",EDGE,"1cb9c079-ea9b-4899-8069-e0e3048e911d.sketch_text.stroke-44"),sQuery(id+"FHMxAyK4CFUKdhS_1.wireOp",EDGE,"1cb9c079-ea9b-4899-8069-e0e3048e911d.sketch_text.stroke-45"),sQuery(id+"FHMxAyK4CFUKdhS_1.wireOp",EDGE,"1cb9c079-ea9b-4899-8069-e0e3048e911d.sketch_text.stroke-46"),sQuery(id+"FHMxAyK4CFUKdhS_1.wireOp",EDGE,"1cb9c079-ea9b-4899-8069-e0e3048e911d.sketch_text.stroke-47"),sQuery(id+"FHMxAyK4CFUKdhS_1.wireOp",EDGE,"1cb9c079-ea9b-4899-8069-e0e3048e911d.sketch_text.stroke-48"),sQuery(id+"FHMxAyK4CFUKdhS_1.wireOp",EDGE,"1cb9c079-ea9b-4899-8069-e0e3048e911d.sketch_text.stroke-49"),sQuery(id+"FHMxAyK4CFUKdhS_1.wireOp",EDGE,"1cb9c079-ea9b-4899-8069-e0e3048e911d.sketch_text.stroke-50"),sQuery(id+"FHMxAyK4CFUKdhS_1.wireOp",EDGE,"1cb9c079-ea9b-4899-8069-e0e3048e911d.sketch_text.stroke-51"),sQuery(id+"FHMxAyK4CFUKdhS_1.wireOp",EDGE,"1cb9c079-ea9b-4899-8069-e0e3048e911d.sketch_text.stroke-52"),sQuery(id+"FHMxAyK4CFUKdhS_1.wireOp",EDGE,"1cb9c079-ea9b-4899-8069-e0e3048e911d.sketch_text.stroke-53"),sQuery(id+"FHMxAyK4CFUKdhS_1.wireOp",EDGE,"1cb9c079-ea9b-4899-8069-e0e3048e911d.sketch_text.stroke-54"),sQuery(id+"FHMxAyK4CFUKdhS_1.wireOp",EDGE,"1cb9c079-ea9b-4899-8069-e0e3048e911d.sketch_text.stroke-55"),sQuery(id+"FHMxAyK4CFUKdhS_1.wireOp",EDGE,"1cb9c079-ea9b-4899-8069-e0e3048e911d.sketch_text.stroke-56"),sQuery(id+"FHMxAyK4CFUKdhS_1.wireOp",EDGE,"1cb9c079-ea9b-4899-8069-e0e3048e911d.sketch_text.stroke-57"),sQuery(id+"FHMxAyK4CFUKdhS_1.wireOp",EDGE,"1cb9c079-ea9b-4899-8069-e0e3048e911d.sketch_text.stroke-58"),sQuery(id+"FHMxAyK4CFUKdhS_1.wireOp",EDGE,"1cb9c079-ea9b-4899-8069-e0e3048e911d.sketch_text.stroke-59"),sQuery(id+"FHMxAyK4CFUKdhS_1.wireOp",EDGE,"1cb9c079-ea9b-4899-8069-e0e3048e911d.sketch_text.stroke-60"),sQuery(id+"FHMxAyK4CFUKdhS_1.wireOp",EDGE,"1cb9c079-ea9b-4899-8069-e0e3048e911d.sketch_text.stroke-61"),sQuery(id+"FHMxAyK4CFUKdhS_1.wireOp",EDGE,"1cb9c079-ea9b-4899-8069-e0e3048e911d.sketch_text.stroke-62"),sQuery(id+"FHMxAyK4CFUKdhS_1.wireOp",EDGE,"1cb9c079-ea9b-4899-8069-e0e3048e911d.sketch_text.stroke-71"),sQuery(id+"FHMxAyK4CFUKdhS_1.wireOp",EDGE,"1cb9c079-ea9b-4899-8069-e0e3048e911d.sketch_text.stroke-72"),sQuery(id+"FHMxAyK4CFUKdhS_1.wireOp",EDGE,"1cb9c079-ea9b-4899-8069-e0e3048e911d.sketch_text.stroke-73"),sQuery(id+"FHMxAyK4CFUKdhS_1.wireOp",EDGE,"1cb9c079-ea9b-4899-8069-e0e3048e911d.sketch_text.stroke-74"),sQuery(id+"FHMxAyK4CFUKdhS_1.wireOp",EDGE,"1cb9c079-ea9b-4899-8069-e0e3048e911d.sketch_text.stroke-75"),sQuery(id+"FHMxAyK4CFUKdhS_1.wireOp",EDGE,"1cb9c079-ea9b-4899-8069-e0e3048e911d.sketch_text.stroke-76"),sQuery(id+"FHMxAyK4CFUKdhS_1.wireOp",EDGE,"1cb9c079-ea9b-4899-8069-e0e3048e911d.sketch_text.stroke-77"),sQuery(id+"FHMxAyK4CFUKdhS_1.wireOp",EDGE,"1cb9c079-ea9b-4899-8069-e0e3048e911d.sketch_text.stroke-78"),sQuery(id+"FHMxAyK4CFUKdhS_1.wireOp",EDGE,"1cb9c079-ea9b-4899-8069-e0e3048e911d.sketch_text.stroke-79"),sQuery(id+"FHMxAyK4CFUKdhS_1.wireOp",EDGE,"1cb9c079-ea9b-4899-8069-e0e3048e911d.sketch_text.stroke-80"),sQuery(id+"FHMxAyK4CFUKdhS_1.wireOp",EDGE,"1cb9c079-ea9b-4899-8069-e0e3048e911d.sketch_text.stroke-81"),sQuery(id+"FHMxAyK4CFUKdhS_1.wireOp",EDGE,"1cb9c079-ea9b-4899-8069-e0e3048e911d.sketch_text.stroke-82"),sQuery(id+"FHMxAyK4CFUKdhS_1.wireOp",EDGE,"1cb9c079-ea9b-4899-8069-e0e3048e911d.sketch_text.stroke-83"),sQuery(id+"FHMxAyK4CFUKdhS_1.wireOp",EDGE,"1cb9c079-ea9b-4899-8069-e0e3048e911d.sketch_text.stroke-84"),sQuery(id+"FHMxAyK4CFUKdhS_1.wireOp",EDGE,"1cb9c079-ea9b-4899-8069-e0e3048e911d.sketch_text.stroke-85"),sQuery(id+"FHMxAyK4CFUKdhS_1.wireOp",EDGE,"1cb9c079-ea9b-4899-8069-e0e3048e911d.sketch_text.stroke-86"),sQuery(id+"FHMxAyK4CFUKdhS_1.wireOp",EDGE,"1cb9c079-ea9b-4899-8069-e0e3048e911d.sketch_text.stroke-87"),sQuery(id+"FHMxAyK4CFUKdhS_1.wireOp",EDGE,"1cb9c079-ea9b-4899-8069-e0e3048e911d.sketch_text.stroke-88"),sQuery(id+"FHMxAyK4CFUKdhS_1.wireOp",EDGE,"1cb9c079-ea9b-4899-8069-e0e3048e911d.sketch_text.stroke-89"),sQuery(id+"FHMxAyK4CFUKdhS_1.wireOp",EDGE,"1cb9c079-ea9b-4899-8069-e0e3048e911d.sketch_text.stroke-90"),sQuery(id+"FHMxAyK4CFUKdhS_1.wireOp",EDGE,"1cb9c079-ea9b-4899-8069-e0e3048e911d.sketch_text.stroke-91"),sQuery(id+"FHMxAyK4CFUKdhS_1.wireOp",EDGE,"1cb9c079-ea9b-4899-8069-e0e3048e911d.sketch_text.stroke-92"),sQuery(id+"FHMxAyK4CFUKdhS_1.wireOp",EDGE,"1cb9c079-ea9b-4899-8069-e0e3048e911d.sketch_text.stroke-93"),sQuery(id+"FHMxAyK4CFUKdhS_1.wireOp",EDGE,"1cb9c079-ea9b-4899-8069-e0e3048e911d.sketch_text.stroke-94"),sQuery(id+"FHMxAyK4CFUKdhS_1.wireOp",EDGE,"1cb9c079-ea9b-4899-8069-e0e3048e911d.sketch_text.stroke-95"),sQuery(id+"FHMxAyK4CFUKdhS_1.wireOp",EDGE,"1cb9c079-ea9b-4899-8069-e0e3048e911d.sketch_text.stroke-96"),sQuery(id+"FHMxAyK4CFUKdhS_1.wireOp",EDGE,"1cb9c079-ea9b-4899-8069-e0e3048e911d.sketch_text.stroke-97"),sQuery(id+"FHMxAyK4CFUKdhS_1.wireOp",EDGE,"1cb9c079-ea9b-4899-8069-e0e3048e911d.sketch_text.stroke-103"),sQuery(id+"FHMxAyK4CFUKdhS_1.wireOp",EDGE,"1cb9c079-ea9b-4899-8069-e0e3048e911d.sketch_text.stroke-104"),sQuery(id+"FHMxAyK4CFUKdhS_1.wireOp",EDGE,"1cb9c079-ea9b-4899-8069-e0e3048e911d.sketch_text.stroke-105"),sQuery(id+"FHMxAyK4CFUKdhS_1.wireOp",EDGE,"1cb9c079-ea9b-4899-8069-e0e3048e911d.sketch_text.stroke-106"),sQuery(id+"FHMxAyK4CFUKdhS_1.wireOp",EDGE,"1cb9c079-ea9b-4899-8069-e0e3048e911d.sketch_text.stroke-107"),sQuery(id+"FHMxAyK4CFUKdhS_1.wireOp",EDGE,"1cb9c079-ea9b-4899-8069-e0e3048e911d.sketch_text.stroke-108"),sQuery(id+"FHMxAyK4CFUKdhS_1.wireOp",EDGE,"1cb9c079-ea9b-4899-8069-e0e3048e911d.sketch_text.stroke-109"),sQuery(id+"FHMxAyK4CFUKdhS_1.wireOp",EDGE,"1cb9c079-ea9b-4899-8069-e0e3048e911d.sketch_text.stroke-110"),sQuery(id+"FHMxAyK4CFUKdhS_1.wireOp",EDGE,"1cb9c079-ea9b-4899-8069-e0e3048e911d.sketch_text.stroke-111"),sQuery(id+"FHMxAyK4CFUKdhS_1.wireOp",EDGE,"1cb9c079-ea9b-4899-8069-e0e3048e911d.sketch_text.stroke-112"),sQuery(id+"FHMxAyK4CFUKdhS_1.wireOp",EDGE,"1cb9c079-ea9b-4899-8069-e0e3048e911d.sketch_text.stroke-113"),sQuery(id+"FHMxAyK4CFUKdhS_1.wireOp",EDGE,"1cb9c079-ea9b-4899-8069-e0e3048e911d.sketch_text.stroke-114"),sQuery(id+"FHMxAyK4CFUKdhS_1.wireOp",EDGE,"1cb9c079-ea9b-4899-8069-e0e3048e911d.sketch_text.stroke-115"),sQuery(id+"FHMxAyK4CFUKdhS_1.wireOp",EDGE,"1cb9c079-ea9b-4899-8069-e0e3048e911d.sketch_text.stroke-116"),sQuery(id+"FHMxAyK4CFUKdhS_1.wireOp",EDGE,"1cb9c079-ea9b-4899-8069-e0e3048e911d.sketch_text.stroke-117"),sQuery(id+"FHMxAyK4CFUKdhS_1.wireOp",EDGE,"1cb9c079-ea9b-4899-8069-e0e3048e911d.sketch_text.stroke-118"),sQuery(id+"FHMxAyK4CFUKdhS_1.wireOp",EDGE,"1cb9c079-ea9b-4899-8069-e0e3048e911d.sketch_text.stroke-119"),sQuery(id+"FHMxAyK4CFUKdhS_1.wireOp",EDGE,"1cb9c079-ea9b-4899-8069-e0e3048e911d.sketch_text.stroke-120"),sQuery(id+"FHMxAyK4CFUKdhS_1.wireOp",EDGE,"1cb9c079-ea9b-4899-8069-e0e3048e911d.sketch_text.stroke-121"),sQuery(id+"FHMxAyK4CFUKdhS_1.wireOp",EDGE,"1cb9c079-ea9b-4899-8069-e0e3048e911d.sketch_text.stroke-122"),sQuery(id+"FHMxAyK4CFUKdhS_1.wireOp",EDGE,"1cb9c079-ea9b-4899-8069-e0e3048e911d.sketch_text.stroke-123"),sQuery(id+"FHMxAyK4CFUKdhS_1.wireOp",EDGE,"1cb9c079-ea9b-4899-8069-e0e3048e911d.sketch_text.stroke-124"),sQuery(id+"FHMxAyK4CFUKdhS_1.wireOp",EDGE,"1cb9c079-ea9b-4899-8069-e0e3048e911d.sketch_text.stroke-125"),sQuery(id+"FHMxAyK4CFUKdhS_1.wireOp",EDGE,"1cb9c079-ea9b-4899-8069-e0e3048e911d.sketch_text.stroke-126"),sQuery(id+"FHMxAyK4CFUKdhS_1.wireOp",EDGE,"1cb9c079-ea9b-4899-8069-e0e3048e911d.sketch_text.stroke-127"),sQuery(id+"FHMxAyK4CFUKdhS_1.wireOp",EDGE,"1cb9c079-ea9b-4899-8069-e0e3048e911d.sketch_text.stroke-128"),sQuery(id+"FHMxAyK4CFUKdhS_1.wireOp",EDGE,"1cb9c079-ea9b-4899-8069-e0e3048e911d.sketch_text.stroke-129"),sQuery(id+"FHMxAyK4CFUKdhS_1.wireOp",EDGE,"1cb9c079-ea9b-4899-8069-e0e3048e911d.sketch_text.stroke-130"),sQuery(id+"FHMxAyK4CFUKdhS_1.wireOp",EDGE,"1cb9c079-ea9b-4899-8069-e0e3048e911d.sketch_text.stroke-131"),sQuery(id+"FHMxAyK4CFUKdhS_1.wireOp",EDGE,"1cb9c079-ea9b-4899-8069-e0e3048e911d.sketch_text.stroke-132"),sQuery(id+"FHMxAyK4CFUKdhS_1.wireOp",EDGE,"1cb9c079-ea9b-4899-8069-e0e3048e911d.sketch_text.stroke-133"),sQuery(id+"FHMxAyK4CFUKdhS_1.wireOp",EDGE,"1cb9c079-ea9b-4899-8069-e0e3048e911d.sketch_text.stroke-134"),sQuery(id+"FHMxAyK4CFUKdhS_1.wireOp",EDGE,"1cb9c079-ea9b-4899-8069-e0e3048e911d.sketch_text.stroke-135"),sQuery(id+"FHMxAyK4CFUKdhS_1.wireOp",EDGE,"1cb9c079-ea9b-4899-8069-e0e3048e911d.sketch_text.stroke-136"),sQuery(id+"FHMxAyK4CFUKdhS_1.wireOp",EDGE,"1cb9c079-ea9b-4899-8069-e0e3048e911d.sketch_text.stroke-137"),sQuery(id+"FHMxAyK4CFUKdhS_1.wireOp",EDGE,"1cb9c079-ea9b-4899-8069-e0e3048e911d.sketch_text.stroke-138"),sQuery(id+"FHMxAyK4CFUKdhS_1.wireOp",EDGE,"1cb9c079-ea9b-4899-8069-e0e3048e911d.sketch_text.stroke-139"),sQuery(id+"FHMxAyK4CFUKdhS_1.wireOp",EDGE,"1cb9c079-ea9b-4899-8069-e0e3048e911d.sketch_text.stroke-140"),sQuery(id+"FHMxAyK4CFUKdhS_1.wireOp",EDGE,"1cb9c079-ea9b-4899-8069-e0e3048e911d.sketch_text.stroke-141"),sQuery(id+"FHMxAyK4CFUKdhS_1.wireOp",EDGE,"1cb9c079-ea9b-4899-8069-e0e3048e911d.sketch_text.stroke-142"),sQuery(id+"FHMxAyK4CFUKdhS_1.wireOp",EDGE,"1cb9c079-ea9b-4899-8069-e0e3048e911d.sketch_text.stroke-143"),sQuery(id+"FHMxAyK4CFUKdhS_1.wireOp",EDGE,"1cb9c079-ea9b-4899-8069-e0e3048e911d.sketch_text.stroke-144"),sQuery(id+"FHMxAyK4CFUKdhS_1.wireOp",EDGE,"1cb9c079-ea9b-4899-8069-e0e3048e911d.sketch_text.stroke-145"),sQuery(id+"FHMxAyK4CFUKdhS_1.wireOp",EDGE,"1cb9c079-ea9b-4899-8069-e0e3048e911d.sketch_text.stroke-146"),sQuery(id+"FHMxAyK4CFUKdhS_1.wireOp",EDGE,"1cb9c079-ea9b-4899-8069-e0e3048e911d.sketch_text.stroke-147"),sQuery(id+"FHMxAyK4CFUKdhS_1.wireOp",EDGE,"1cb9c079-ea9b-4899-8069-e0e3048e911d.sketch_text.stroke-148"),sQuery(id+"FHMxAyK4CFUKdhS_1.wireOp",EDGE,"1cb9c079-ea9b-4899-8069-e0e3048e911d.sketch_text.stroke-149"),sQuery(id+"FHMxAyK4CFUKdhS_1.wireOp",EDGE,"1cb9c079-ea9b-4899-8069-e0e3048e911d.sketch_text.stroke-150"),sQuery(id+"FHMxAyK4CFUKdhS_1.wireOp",EDGE,"1cb9c079-ea9b-4899-8069-e0e3048e911d.sketch_text.stroke-151"),sQuery(id+"FHMxAyK4CFUKdhS_1.wireOp",EDGE,"1cb9c079-ea9b-4899-8069-e0e3048e911d.sketch_text.stroke-152"),sQuery(id+"FHMxAyK4CFUKdhS_1.wireOp",EDGE,"1cb9c079-ea9b-4899-8069-e0e3048e911d.sketch_text.stroke-153"),sQuery(id+"FHMxAyK4CFUKdhS_1.wireOp",EDGE,"1cb9c079-ea9b-4899-8069-e0e3048e911d.sketch_text.stroke-159"),sQuery(id+"FHMxAyK4CFUKdhS_1.wireOp",EDGE,"1cb9c079-ea9b-4899-8069-e0e3048e911d.sketch_text.stroke-160"),sQuery(id+"FHMxAyK4CFUKdhS_1.wireOp",EDGE,"1cb9c079-ea9b-4899-8069-e0e3048e911d.sketch_text.stroke-161"),sQuery(id+"FHMxAyK4CFUKdhS_1.wireOp",EDGE,"1cb9c079-ea9b-4899-8069-e0e3048e911d.sketch_text.stroke-162"),sQuery(id+"FHMxAyK4CFUKdhS_1.wireOp",EDGE,"1cb9c079-ea9b-4899-8069-e0e3048e911d.sketch_text.stroke-163"),sQuery(id+"FHMxAyK4CFUKdhS_1.wireOp",EDGE,"1cb9c079-ea9b-4899-8069-e0e3048e911d.sketch_text.stroke-164"),sQuery(id+"FHMxAyK4CFUKdhS_1.wireOp",EDGE,"1cb9c079-ea9b-4899-8069-e0e3048e911d.sketch_text.stroke-165"),sQuery(id+"FHMxAyK4CFUKdhS_1.wireOp",EDGE,"1cb9c079-ea9b-4899-8069-e0e3048e911d.sketch_text.stroke-166"),sQuery(id+"FHMxAyK4CFUKdhS_1.wireOp",EDGE,"1cb9c079-ea9b-4899-8069-e0e3048e911d.sketch_text.stroke-167"),sQuery(id+"FHMxAyK4CFUKdhS_1.wireOp",EDGE,"1cb9c079-ea9b-4899-8069-e0e3048e911d.sketch_text.stroke-168"),sQuery(id+"FHMxAyK4CFUKdhS_1.wireOp",EDGE,"1cb9c079-ea9b-4899-8069-e0e3048e911d.sketch_text.stroke-169"),sQuery(id+"FHMxAyK4CFUKdhS_1.wireOp",EDGE,"1cb9c079-ea9b-4899-8069-e0e3048e911d.sketch_text.stroke-170"),sQuery(id+"FHMxAyK4CFUKdhS_1.wireOp",EDGE,"1cb9c079-ea9b-4899-8069-e0e3048e911d.sketch_text.stroke-171"),sQuery(id+"FHMxAyK4CFUKdhS_1.wireOp",EDGE,"1cb9c079-ea9b-4899-8069-e0e3048e911d.sketch_text.stroke-172"),sQuery(id+"FHMxAyK4CFUKdhS_1.wireOp",EDGE,"1cb9c079-ea9b-4899-8069-e0e3048e911d.sketch_text.stroke-173"),sQuery(id+"FHMxAyK4CFUKdhS_1.wireOp",EDGE,"1cb9c079-ea9b-4899-8069-e0e3048e911d.sketch_text.stroke-174"),sQuery(id+"FHMxAyK4CFUKdhS_1.wireOp",EDGE,"1cb9c079-ea9b-4899-8069-e0e3048e911d.sketch_text.stroke-175"),sQuery(id+"FHMxAyK4CFUKdhS_1.wireOp",EDGE,"1cb9c079-ea9b-4899-8069-e0e3048e911d.sketch_text.stroke-176"),sQuery(id+"FHMxAyK4CFUKdhS_1.wireOp",EDGE,"1cb9c079-ea9b-4899-8069-e0e3048e911d.sketch_text.stroke-177"),sQuery(id+"FHMxAyK4CFUKdhS_1.wireOp",EDGE,"1cb9c079-ea9b-4899-8069-e0e3048e911d.sketch_text.stroke-178"),sQuery(id+"FHMxAyK4CFUKdhS_1.wireOp",EDGE,"1cb9c079-ea9b-4899-8069-e0e3048e911d.sketch_text.stroke-179"),sQuery(id+"FHMxAyK4CFUKdhS_1.wireOp",EDGE,"1cb9c079-ea9b-4899-8069-e0e3048e911d.sketch_text.stroke-180"),sQuery(id+"F2.wireOp",EDGE,"727ac2c1-f511-4829-95a7-a443ef16a4cd"),subQ2])],"isStart":true}),makeQuery(id+"F3.opExtrude","SWEPT_FACE",FACE,{"disambiguationData":[OSD([subQ2])]})]),OD(0.0)],"derivedFrom":makeQuery(id+"F1.opExtrude","CAP_EDGE",EDGE,{"disambiguationData":[OSD([subQ0])],"isStart":false})});}
            var Q19;
            {var subQ0=sQuery(id+"F0.wireOp",EDGE,"E0.top");var subQ1=sQuery(id+"F0.wireOp",EDGE,"E0.bottom");var subQ2=sQuery(id+"F2.wireOp",EDGE,"1a034e28-a7c2-419d-97de-c33d70a47301");Q19=makeQuery(id+"F3.boolean.opBoolean","SPLIT",EDGE,{"disambiguationData":[TD([makeQuery(id+"F1.opExtrude","CAP_FACE",FACE,{"disambiguationData":[OSD([subQ1,subQ0,sQuery(id+"F0.wireOp",EDGE,"E0.left"),sQuery(id+"F0.wireOp",EDGE,"E0.right")])],"isStart":false}),makeQuery(id+"F1.opExtrude","SWEPT_FACE",FACE,{"disambiguationData":[OSD([subQ0])]}),makeQuery(id+"F3.opExtrude","CAP_FACE",FACE,{"disambiguationData":[OSD([subQ1,sQuery(id+"FQ5JFwxVdaqARUP_1.wireOp",EDGE,"fcba4419-a2ee-464f-be9d-58f11bf3418b.sketch_text.stroke-0"),sQuery(id+"FQ5JFwxVdaqARUP_1.wireOp",EDGE,"fcba4419-a2ee-464f-be9d-58f11bf3418b.sketch_text.stroke-1"),sQuery(id+"FQ5JFwxVdaqARUP_1.wireOp",EDGE,"fcba4419-a2ee-464f-be9d-58f11bf3418b.sketch_text.stroke-2"),sQuery(id+"FQ5JFwxVdaqARUP_1.wireOp",EDGE,"fcba4419-a2ee-464f-be9d-58f11bf3418b.sketch_text.stroke-3"),sQuery(id+"FQ5JFwxVdaqARUP_1.wireOp",EDGE,"fcba4419-a2ee-464f-be9d-58f11bf3418b.sketch_text.stroke-4"),sQuery(id+"FQ5JFwxVdaqARUP_1.wireOp",EDGE,"fcba4419-a2ee-464f-be9d-58f11bf3418b.sketch_text.stroke-5"),sQuery(id+"FQ5JFwxVdaqARUP_1.wireOp",EDGE,"fcba4419-a2ee-464f-be9d-58f11bf3418b.sketch_text.stroke-6"),sQuery(id+"FQ5JFwxVdaqARUP_1.wireOp",EDGE,"fcba4419-a2ee-464f-be9d-58f11bf3418b.sketch_text.stroke-7"),sQuery(id+"FQ5JFwxVdaqARUP_1.wireOp",EDGE,"fcba4419-a2ee-464f-be9d-58f11bf3418b.sketch_text.stroke-8"),sQuery(id+"FQ5JFwxVdaqARUP_1.wireOp",EDGE,"fcba4419-a2ee-464f-be9d-58f11bf3418b.sketch_text.stroke-9"),sQuery(id+"FQ5JFwxVdaqARUP_1.wireOp",EDGE,"fcba4419-a2ee-464f-be9d-58f11bf3418b.sketch_text.stroke-10"),sQuery(id+"FQ5JFwxVdaqARUP_1.wireOp",EDGE,"fcba4419-a2ee-464f-be9d-58f11bf3418b.sketch_text.stroke-11"),sQuery(id+"FQ5JFwxVdaqARUP_1.wireOp",EDGE,"fcba4419-a2ee-464f-be9d-58f11bf3418b.sketch_text.stroke-12"),sQuery(id+"FQ5JFwxVdaqARUP_1.wireOp",EDGE,"fcba4419-a2ee-464f-be9d-58f11bf3418b.sketch_text.stroke-13"),sQuery(id+"FQ5JFwxVdaqARUP_1.wireOp",EDGE,"fcba4419-a2ee-464f-be9d-58f11bf3418b.sketch_text.stroke-14"),sQuery(id+"FQ5JFwxVdaqARUP_1.wireOp",EDGE,"fcba4419-a2ee-464f-be9d-58f11bf3418b.sketch_text.stroke-15"),sQuery(id+"FQ5JFwxVdaqARUP_1.wireOp",EDGE,"fcba4419-a2ee-464f-be9d-58f11bf3418b.sketch_text.stroke-16"),sQuery(id+"FQ5JFwxVdaqARUP_1.wireOp",EDGE,"fcba4419-a2ee-464f-be9d-58f11bf3418b.sketch_text.stroke-17"),sQuery(id+"FQ5JFwxVdaqARUP_1.wireOp",EDGE,"fcba4419-a2ee-464f-be9d-58f11bf3418b.sketch_text.stroke-18"),sQuery(id+"FQ5JFwxVdaqARUP_1.wireOp",EDGE,"fcba4419-a2ee-464f-be9d-58f11bf3418b.sketch_text.stroke-19"),sQuery(id+"FQ5JFwxVdaqARUP_1.wireOp",EDGE,"fcba4419-a2ee-464f-be9d-58f11bf3418b.sketch_text.stroke-20"),sQuery(id+"FQ5JFwxVdaqARUP_1.wireOp",EDGE,"fcba4419-a2ee-464f-be9d-58f11bf3418b.sketch_text.stroke-21"),sQuery(id+"FQ5JFwxVdaqARUP_1.wireOp",EDGE,"fcba4419-a2ee-464f-be9d-58f11bf3418b.sketch_text.stroke-22"),sQuery(id+"FQ5JFwxVdaqARUP_1.wireOp",EDGE,"fcba4419-a2ee-464f-be9d-58f11bf3418b.sketch_text.stroke-23"),sQuery(id+"FQ5JFwxVdaqARUP_1.wireOp",EDGE,"fcba4419-a2ee-464f-be9d-58f11bf3418b.sketch_text.stroke-24"),sQuery(id+"FQ5JFwxVdaqARUP_1.wireOp",EDGE,"fcba4419-a2ee-464f-be9d-58f11bf3418b.sketch_text.stroke-25"),sQuery(id+"FQ5JFwxVdaqARUP_1.wireOp",EDGE,"fcba4419-a2ee-464f-be9d-58f11bf3418b.sketch_text.stroke-26"),sQuery(id+"FQ5JFwxVdaqARUP_1.wireOp",EDGE,"fcba4419-a2ee-464f-be9d-58f11bf3418b.sketch_text.stroke-27"),sQuery(id+"FQ5JFwxVdaqARUP_1.wireOp",EDGE,"fcba4419-a2ee-464f-be9d-58f11bf3418b.sketch_text.stroke-28"),sQuery(id+"FQ5JFwxVdaqARUP_1.wireOp",EDGE,"fcba4419-a2ee-464f-be9d-58f11bf3418b.sketch_text.stroke-29"),sQuery(id+"FQ5JFwxVdaqARUP_1.wireOp",EDGE,"fcba4419-a2ee-464f-be9d-58f11bf3418b.sketch_text.stroke-30"),sQuery(id+"FQ5JFwxVdaqARUP_1.wireOp",EDGE,"fcba4419-a2ee-464f-be9d-58f11bf3418b.sketch_text.stroke-31"),sQuery(id+"FQ5JFwxVdaqARUP_1.wireOp",EDGE,"fcba4419-a2ee-464f-be9d-58f11bf3418b.sketch_text.stroke-32"),sQuery(id+"FQ5JFwxVdaqARUP_1.wireOp",EDGE,"fcba4419-a2ee-464f-be9d-58f11bf3418b.sketch_text.stroke-33"),sQuery(id+"FQ5JFwxVdaqARUP_1.wireOp",EDGE,"fcba4419-a2ee-464f-be9d-58f11bf3418b.sketch_text.stroke-34"),sQuery(id+"FQ5JFwxVdaqARUP_1.wireOp",EDGE,"fcba4419-a2ee-464f-be9d-58f11bf3418b.sketch_text.stroke-35"),sQuery(id+"FQ5JFwxVdaqARUP_1.wireOp",EDGE,"fcba4419-a2ee-464f-be9d-58f11bf3418b.sketch_text.stroke-36"),sQuery(id+"FQ5JFwxVdaqARUP_1.wireOp",EDGE,"fcba4419-a2ee-464f-be9d-58f11bf3418b.sketch_text.stroke-37"),sQuery(id+"FQ5JFwxVdaqARUP_1.wireOp",EDGE,"fcba4419-a2ee-464f-be9d-58f11bf3418b.sketch_text.stroke-38"),sQuery(id+"FQ5JFwxVdaqARUP_1.wireOp",EDGE,"fcba4419-a2ee-464f-be9d-58f11bf3418b.sketch_text.stroke-39"),sQuery(id+"FQ5JFwxVdaqARUP_1.wireOp",EDGE,"fcba4419-a2ee-464f-be9d-58f11bf3418b.sketch_text.stroke-40"),sQuery(id+"FQ5JFwxVdaqARUP_1.wireOp",EDGE,"fcba4419-a2ee-464f-be9d-58f11bf3418b.sketch_text.stroke-41"),sQuery(id+"FQ5JFwxVdaqARUP_1.wireOp",EDGE,"fcba4419-a2ee-464f-be9d-58f11bf3418b.sketch_text.stroke-42"),sQuery(id+"FQ5JFwxVdaqARUP_1.wireOp",EDGE,"fcba4419-a2ee-464f-be9d-58f11bf3418b.sketch_text.stroke-43"),sQuery(id+"FQ5JFwxVdaqARUP_1.wireOp",EDGE,"fcba4419-a2ee-464f-be9d-58f11bf3418b.sketch_text.stroke-44"),sQuery(id+"FQ5JFwxVdaqARUP_1.wireOp",EDGE,"fcba4419-a2ee-464f-be9d-58f11bf3418b.sketch_text.stroke-45"),sQuery(id+"FQ5JFwxVdaqARUP_1.wireOp",EDGE,"fcba4419-a2ee-464f-be9d-58f11bf3418b.sketch_text.stroke-46"),sQuery(id+"FQ5JFwxVdaqARUP_1.wireOp",EDGE,"fcba4419-a2ee-464f-be9d-58f11bf3418b.sketch_text.stroke-47"),sQuery(id+"FQ5JFwxVdaqARUP_1.wireOp",EDGE,"fcba4419-a2ee-464f-be9d-58f11bf3418b.sketch_text.stroke-48"),sQuery(id+"FQ5JFwxVdaqARUP_1.wireOp",EDGE,"fcba4419-a2ee-464f-be9d-58f11bf3418b.sketch_text.stroke-49"),sQuery(id+"FQ5JFwxVdaqARUP_1.wireOp",EDGE,"fcba4419-a2ee-464f-be9d-58f11bf3418b.sketch_text.stroke-50"),sQuery(id+"FQ5JFwxVdaqARUP_1.wireOp",EDGE,"fcba4419-a2ee-464f-be9d-58f11bf3418b.sketch_text.stroke-51"),sQuery(id+"FQ5JFwxVdaqARUP_1.wireOp",EDGE,"fcba4419-a2ee-464f-be9d-58f11bf3418b.sketch_text.stroke-52"),sQuery(id+"FQ5JFwxVdaqARUP_1.wireOp",EDGE,"fcba4419-a2ee-464f-be9d-58f11bf3418b.sketch_text.stroke-53"),sQuery(id+"FQ5JFwxVdaqARUP_1.wireOp",EDGE,"fcba4419-a2ee-464f-be9d-58f11bf3418b.sketch_text.stroke-54"),sQuery(id+"FQ5JFwxVdaqARUP_1.wireOp",EDGE,"fcba4419-a2ee-464f-be9d-58f11bf3418b.sketch_text.stroke-55"),sQuery(id+"FQ5JFwxVdaqARUP_1.wireOp",EDGE,"fcba4419-a2ee-464f-be9d-58f11bf3418b.sketch_text.stroke-56"),sQuery(id+"FQ5JFwxVdaqARUP_1.wireOp",EDGE,"fcba4419-a2ee-464f-be9d-58f11bf3418b.sketch_text.stroke-57"),sQuery(id+"FQ5JFwxVdaqARUP_1.wireOp",EDGE,"fcba4419-a2ee-464f-be9d-58f11bf3418b.sketch_text.stroke-58"),sQuery(id+"FQ5JFwxVdaqARUP_1.wireOp",EDGE,"fcba4419-a2ee-464f-be9d-58f11bf3418b.sketch_text.stroke-59"),sQuery(id+"FQ5JFwxVdaqARUP_1.wireOp",EDGE,"fcba4419-a2ee-464f-be9d-58f11bf3418b.sketch_text.stroke-60"),sQuery(id+"FQ5JFwxVdaqARUP_1.wireOp",EDGE,"fcba4419-a2ee-464f-be9d-58f11bf3418b.sketch_text.stroke-61"),sQuery(id+"FQ5JFwxVdaqARUP_1.wireOp",EDGE,"fcba4419-a2ee-464f-be9d-58f11bf3418b.sketch_text.stroke-62"),sQuery(id+"FQ5JFwxVdaqARUP_1.wireOp",EDGE,"fcba4419-a2ee-464f-be9d-58f11bf3418b.sketch_text.stroke-63"),sQuery(id+"FQ5JFwxVdaqARUP_1.wireOp",EDGE,"fcba4419-a2ee-464f-be9d-58f11bf3418b.sketch_text.stroke-64"),sQuery(id+"FQ5JFwxVdaqARUP_1.wireOp",EDGE,"fcba4419-a2ee-464f-be9d-58f11bf3418b.sketch_text.stroke-65"),sQuery(id+"FQ5JFwxVdaqARUP_1.wireOp",EDGE,"fcba4419-a2ee-464f-be9d-58f11bf3418b.sketch_text.stroke-66"),sQuery(id+"FQ5JFwxVdaqARUP_1.wireOp",EDGE,"fcba4419-a2ee-464f-be9d-58f11bf3418b.sketch_text.stroke-67"),sQuery(id+"FQ5JFwxVdaqARUP_1.wireOp",EDGE,"fcba4419-a2ee-464f-be9d-58f11bf3418b.sketch_text.stroke-68"),sQuery(id+"FQ5JFwxVdaqARUP_1.wireOp",EDGE,"fcba4419-a2ee-464f-be9d-58f11bf3418b.sketch_text.stroke-69"),sQuery(id+"FQ5JFwxVdaqARUP_1.wireOp",EDGE,"fcba4419-a2ee-464f-be9d-58f11bf3418b.sketch_text.stroke-70"),sQuery(id+"FQ5JFwxVdaqARUP_1.wireOp",EDGE,"fcba4419-a2ee-464f-be9d-58f11bf3418b.sketch_text.stroke-71"),sQuery(id+"FQ5JFwxVdaqARUP_1.wireOp",EDGE,"fcba4419-a2ee-464f-be9d-58f11bf3418b.sketch_text.stroke-72"),sQuery(id+"FQ5JFwxVdaqARUP_1.wireOp",EDGE,"fcba4419-a2ee-464f-be9d-58f11bf3418b.sketch_text.stroke-73"),sQuery(id+"FQ5JFwxVdaqARUP_1.wireOp",EDGE,"fcba4419-a2ee-464f-be9d-58f11bf3418b.sketch_text.stroke-74"),sQuery(id+"FQ5JFwxVdaqARUP_1.wireOp",EDGE,"fcba4419-a2ee-464f-be9d-58f11bf3418b.sketch_text.stroke-75"),sQuery(id+"FQ5JFwxVdaqARUP_1.wireOp",EDGE,"fcba4419-a2ee-464f-be9d-58f11bf3418b.sketch_text.stroke-76"),sQuery(id+"FQ5JFwxVdaqARUP_1.wireOp",EDGE,"fcba4419-a2ee-464f-be9d-58f11bf3418b.sketch_text.stroke-77"),sQuery(id+"FQ5JFwxVdaqARUP_1.wireOp",EDGE,"fcba4419-a2ee-464f-be9d-58f11bf3418b.sketch_text.stroke-78"),sQuery(id+"FQ5JFwxVdaqARUP_1.wireOp",EDGE,"fcba4419-a2ee-464f-be9d-58f11bf3418b.sketch_text.stroke-79"),sQuery(id+"FQ5JFwxVdaqARUP_1.wireOp",EDGE,"fcba4419-a2ee-464f-be9d-58f11bf3418b.sketch_text.stroke-80"),sQuery(id+"FQ5JFwxVdaqARUP_1.wireOp",EDGE,"fcba4419-a2ee-464f-be9d-58f11bf3418b.sketch_text.stroke-81"),sQuery(id+"FQ5JFwxVdaqARUP_1.wireOp",EDGE,"fcba4419-a2ee-464f-be9d-58f11bf3418b.sketch_text.stroke-82"),sQuery(id+"FQ5JFwxVdaqARUP_1.wireOp",EDGE,"fcba4419-a2ee-464f-be9d-58f11bf3418b.sketch_text.stroke-83"),sQuery(id+"FQ5JFwxVdaqARUP_1.wireOp",EDGE,"fcba4419-a2ee-464f-be9d-58f11bf3418b.sketch_text.stroke-84"),sQuery(id+"FQ5JFwxVdaqARUP_1.wireOp",EDGE,"fcba4419-a2ee-464f-be9d-58f11bf3418b.sketch_text.stroke-85"),sQuery(id+"FQ5JFwxVdaqARUP_1.wireOp",EDGE,"fcba4419-a2ee-464f-be9d-58f11bf3418b.sketch_text.stroke-86"),sQuery(id+"FQ5JFwxVdaqARUP_1.wireOp",EDGE,"fcba4419-a2ee-464f-be9d-58f11bf3418b.sketch_text.stroke-87"),sQuery(id+"FQ5JFwxVdaqARUP_1.wireOp",EDGE,"fcba4419-a2ee-464f-be9d-58f11bf3418b.sketch_text.stroke-88"),sQuery(id+"FQ5JFwxVdaqARUP_1.wireOp",EDGE,"fcba4419-a2ee-464f-be9d-58f11bf3418b.sketch_text.stroke-89"),sQuery(id+"FQ5JFwxVdaqARUP_1.wireOp",EDGE,"fcba4419-a2ee-464f-be9d-58f11bf3418b.sketch_text.stroke-90"),sQuery(id+"FQ5JFwxVdaqARUP_1.wireOp",EDGE,"fcba4419-a2ee-464f-be9d-58f11bf3418b.sketch_text.stroke-91"),sQuery(id+"FQ5JFwxVdaqARUP_1.wireOp",EDGE,"fcba4419-a2ee-464f-be9d-58f11bf3418b.sketch_text.stroke-92"),sQuery(id+"FQ5JFwxVdaqARUP_1.wireOp",EDGE,"fcba4419-a2ee-464f-be9d-58f11bf3418b.sketch_text.stroke-93"),sQuery(id+"FQ5JFwxVdaqARUP_1.wireOp",EDGE,"fcba4419-a2ee-464f-be9d-58f11bf3418b.sketch_text.stroke-94"),sQuery(id+"FQ5JFwxVdaqARUP_1.wireOp",EDGE,"fcba4419-a2ee-464f-be9d-58f11bf3418b.sketch_text.stroke-95"),sQuery(id+"FQ5JFwxVdaqARUP_1.wireOp",EDGE,"fcba4419-a2ee-464f-be9d-58f11bf3418b.sketch_text.stroke-96"),sQuery(id+"FQ5JFwxVdaqARUP_1.wireOp",EDGE,"fcba4419-a2ee-464f-be9d-58f11bf3418b.sketch_text.stroke-97"),sQuery(id+"FQ5JFwxVdaqARUP_1.wireOp",EDGE,"fcba4419-a2ee-464f-be9d-58f11bf3418b.sketch_text.stroke-98"),sQuery(id+"FQ5JFwxVdaqARUP_1.wireOp",EDGE,"fcba4419-a2ee-464f-be9d-58f11bf3418b.sketch_text.stroke-99"),sQuery(id+"FQ5JFwxVdaqARUP_1.wireOp",EDGE,"fcba4419-a2ee-464f-be9d-58f11bf3418b.sketch_text.stroke-100"),sQuery(id+"FQ5JFwxVdaqARUP_1.wireOp",EDGE,"fcba4419-a2ee-464f-be9d-58f11bf3418b.sketch_text.stroke-101"),sQuery(id+"FQ5JFwxVdaqARUP_1.wireOp",EDGE,"fcba4419-a2ee-464f-be9d-58f11bf3418b.sketch_text.stroke-102"),sQuery(id+"FQ5JFwxVdaqARUP_1.wireOp",EDGE,"fcba4419-a2ee-464f-be9d-58f11bf3418b.sketch_text.stroke-103"),sQuery(id+"FQ5JFwxVdaqARUP_1.wireOp",EDGE,"fcba4419-a2ee-464f-be9d-58f11bf3418b.sketch_text.stroke-104"),sQuery(id+"FQ5JFwxVdaqARUP_1.wireOp",EDGE,"fcba4419-a2ee-464f-be9d-58f11bf3418b.sketch_text.stroke-105"),sQuery(id+"FQ5JFwxVdaqARUP_1.wireOp",EDGE,"fcba4419-a2ee-464f-be9d-58f11bf3418b.sketch_text.stroke-106"),sQuery(id+"FQ5JFwxVdaqARUP_1.wireOp",EDGE,"fcba4419-a2ee-464f-be9d-58f11bf3418b.sketch_text.stroke-107"),sQuery(id+"FQ5JFwxVdaqARUP_1.wireOp",EDGE,"fcba4419-a2ee-464f-be9d-58f11bf3418b.sketch_text.stroke-108"),sQuery(id+"FQ5JFwxVdaqARUP_1.wireOp",EDGE,"fcba4419-a2ee-464f-be9d-58f11bf3418b.sketch_text.stroke-109"),sQuery(id+"FQ5JFwxVdaqARUP_1.wireOp",EDGE,"fcba4419-a2ee-464f-be9d-58f11bf3418b.sketch_text.stroke-110"),sQuery(id+"FQ5JFwxVdaqARUP_1.wireOp",EDGE,"fcba4419-a2ee-464f-be9d-58f11bf3418b.sketch_text.stroke-111"),sQuery(id+"FQ5JFwxVdaqARUP_1.wireOp",EDGE,"fcba4419-a2ee-464f-be9d-58f11bf3418b.sketch_text.stroke-112"),sQuery(id+"FQ5JFwxVdaqARUP_1.wireOp",EDGE,"fcba4419-a2ee-464f-be9d-58f11bf3418b.sketch_text.stroke-113"),sQuery(id+"FQ5JFwxVdaqARUP_1.wireOp",EDGE,"fcba4419-a2ee-464f-be9d-58f11bf3418b.sketch_text.stroke-114"),sQuery(id+"FQ5JFwxVdaqARUP_1.wireOp",EDGE,"fcba4419-a2ee-464f-be9d-58f11bf3418b.sketch_text.stroke-115"),sQuery(id+"FQ5JFwxVdaqARUP_1.wireOp",EDGE,"fcba4419-a2ee-464f-be9d-58f11bf3418b.sketch_text.stroke-116"),sQuery(id+"FQ5JFwxVdaqARUP_1.wireOp",EDGE,"fcba4419-a2ee-464f-be9d-58f11bf3418b.sketch_text.stroke-117"),sQuery(id+"FQ5JFwxVdaqARUP_1.wireOp",EDGE,"fcba4419-a2ee-464f-be9d-58f11bf3418b.sketch_text.stroke-118"),sQuery(id+"FQ5JFwxVdaqARUP_1.wireOp",EDGE,"fcba4419-a2ee-464f-be9d-58f11bf3418b.sketch_text.stroke-119"),sQuery(id+"FQ5JFwxVdaqARUP_1.wireOp",EDGE,"fcba4419-a2ee-464f-be9d-58f11bf3418b.sketch_text.stroke-120"),sQuery(id+"FQ5JFwxVdaqARUP_1.wireOp",EDGE,"fcba4419-a2ee-464f-be9d-58f11bf3418b.sketch_text.stroke-121"),sQuery(id+"FQ5JFwxVdaqARUP_1.wireOp",EDGE,"fcba4419-a2ee-464f-be9d-58f11bf3418b.sketch_text.stroke-122"),sQuery(id+"FQ5JFwxVdaqARUP_1.wireOp",EDGE,"fcba4419-a2ee-464f-be9d-58f11bf3418b.sketch_text.stroke-123"),sQuery(id+"FQ5JFwxVdaqARUP_1.wireOp",EDGE,"fcba4419-a2ee-464f-be9d-58f11bf3418b.sketch_text.stroke-124"),sQuery(id+"FQ5JFwxVdaqARUP_1.wireOp",EDGE,"fcba4419-a2ee-464f-be9d-58f11bf3418b.sketch_text.stroke-125"),sQuery(id+"FQ5JFwxVdaqARUP_1.wireOp",EDGE,"fcba4419-a2ee-464f-be9d-58f11bf3418b.sketch_text.stroke-126"),sQuery(id+"FQ5JFwxVdaqARUP_1.wireOp",EDGE,"fcba4419-a2ee-464f-be9d-58f11bf3418b.sketch_text.stroke-127"),sQuery(id+"FQ5JFwxVdaqARUP_1.wireOp",EDGE,"fcba4419-a2ee-464f-be9d-58f11bf3418b.sketch_text.stroke-128"),sQuery(id+"FQ5JFwxVdaqARUP_1.wireOp",EDGE,"fcba4419-a2ee-464f-be9d-58f11bf3418b.sketch_text.stroke-129"),sQuery(id+"FQ5JFwxVdaqARUP_1.wireOp",EDGE,"fcba4419-a2ee-464f-be9d-58f11bf3418b.sketch_text.stroke-130"),sQuery(id+"FQ5JFwxVdaqARUP_1.wireOp",EDGE,"fcba4419-a2ee-464f-be9d-58f11bf3418b.sketch_text.stroke-131"),sQuery(id+"FQ5JFwxVdaqARUP_1.wireOp",EDGE,"fcba4419-a2ee-464f-be9d-58f11bf3418b.sketch_text.stroke-132"),sQuery(id+"FQ5JFwxVdaqARUP_1.wireOp",EDGE,"fcba4419-a2ee-464f-be9d-58f11bf3418b.sketch_text.stroke-133"),sQuery(id+"FQ5JFwxVdaqARUP_1.wireOp",EDGE,"fcba4419-a2ee-464f-be9d-58f11bf3418b.sketch_text.stroke-134"),sQuery(id+"FQ5JFwxVdaqARUP_1.wireOp",EDGE,"fcba4419-a2ee-464f-be9d-58f11bf3418b.sketch_text.stroke-135"),sQuery(id+"FQ5JFwxVdaqARUP_1.wireOp",EDGE,"fcba4419-a2ee-464f-be9d-58f11bf3418b.sketch_text.stroke-136"),sQuery(id+"FQ5JFwxVdaqARUP_1.wireOp",EDGE,"fcba4419-a2ee-464f-be9d-58f11bf3418b.sketch_text.stroke-137"),sQuery(id+"FQ5JFwxVdaqARUP_1.wireOp",EDGE,"fcba4419-a2ee-464f-be9d-58f11bf3418b.sketch_text.stroke-138"),sQuery(id+"FQ5JFwxVdaqARUP_1.wireOp",EDGE,"fcba4419-a2ee-464f-be9d-58f11bf3418b.sketch_text.stroke-139"),sQuery(id+"FQ5JFwxVdaqARUP_1.wireOp",EDGE,"fcba4419-a2ee-464f-be9d-58f11bf3418b.sketch_text.stroke-140"),sQuery(id+"FQ5JFwxVdaqARUP_1.wireOp",EDGE,"fcba4419-a2ee-464f-be9d-58f11bf3418b.sketch_text.stroke-141"),sQuery(id+"FQ5JFwxVdaqARUP_1.wireOp",EDGE,"fcba4419-a2ee-464f-be9d-58f11bf3418b.sketch_text.stroke-142"),sQuery(id+"FQ5JFwxVdaqARUP_1.wireOp",EDGE,"fcba4419-a2ee-464f-be9d-58f11bf3418b.sketch_text.stroke-143"),sQuery(id+"FQ5JFwxVdaqARUP_1.wireOp",EDGE,"fcba4419-a2ee-464f-be9d-58f11bf3418b.sketch_text.stroke-144"),sQuery(id+"FQ5JFwxVdaqARUP_1.wireOp",EDGE,"fcba4419-a2ee-464f-be9d-58f11bf3418b.sketch_text.stroke-145"),sQuery(id+"FQ5JFwxVdaqARUP_1.wireOp",EDGE,"fcba4419-a2ee-464f-be9d-58f11bf3418b.sketch_text.stroke-146"),sQuery(id+"FQ5JFwxVdaqARUP_1.wireOp",EDGE,"fcba4419-a2ee-464f-be9d-58f11bf3418b.sketch_text.stroke-147"),sQuery(id+"FQ5JFwxVdaqARUP_1.wireOp",EDGE,"fcba4419-a2ee-464f-be9d-58f11bf3418b.sketch_text.stroke-148"),sQuery(id+"FQ5JFwxVdaqARUP_1.wireOp",EDGE,"fcba4419-a2ee-464f-be9d-58f11bf3418b.sketch_text.stroke-149"),sQuery(id+"FQ5JFwxVdaqARUP_1.wireOp",EDGE,"fcba4419-a2ee-464f-be9d-58f11bf3418b.sketch_text.stroke-150"),sQuery(id+"FQ5JFwxVdaqARUP_1.wireOp",EDGE,"fcba4419-a2ee-464f-be9d-58f11bf3418b.sketch_text.stroke-151"),sQuery(id+"FQ5JFwxVdaqARUP_1.wireOp",EDGE,"fcba4419-a2ee-464f-be9d-58f11bf3418b.sketch_text.stroke-152"),sQuery(id+"FQ5JFwxVdaqARUP_1.wireOp",EDGE,"fcba4419-a2ee-464f-be9d-58f11bf3418b.sketch_text.stroke-153"),sQuery(id+"FQ5JFwxVdaqARUP_1.wireOp",EDGE,"fcba4419-a2ee-464f-be9d-58f11bf3418b.sketch_text.stroke-154"),sQuery(id+"FQ5JFwxVdaqARUP_1.wireOp",EDGE,"fcba4419-a2ee-464f-be9d-58f11bf3418b.sketch_text.stroke-155"),sQuery(id+"FQ5JFwxVdaqARUP_1.wireOp",EDGE,"fcba4419-a2ee-464f-be9d-58f11bf3418b.sketch_text.stroke-156"),sQuery(id+"FQ5JFwxVdaqARUP_1.wireOp",EDGE,"fcba4419-a2ee-464f-be9d-58f11bf3418b.sketch_text.stroke-157"),sQuery(id+"FQ5JFwxVdaqARUP_1.wireOp",EDGE,"fcba4419-a2ee-464f-be9d-58f11bf3418b.sketch_text.stroke-158"),sQuery(id+"FQ5JFwxVdaqARUP_1.wireOp",EDGE,"fcba4419-a2ee-464f-be9d-58f11bf3418b.sketch_text.stroke-159"),sQuery(id+"FQ5JFwxVdaqARUP_1.wireOp",EDGE,"fcba4419-a2ee-464f-be9d-58f11bf3418b.sketch_text.stroke-160"),sQuery(id+"FQ5JFwxVdaqARUP_1.wireOp",EDGE,"fcba4419-a2ee-464f-be9d-58f11bf3418b.sketch_text.stroke-161"),sQuery(id+"FQ5JFwxVdaqARUP_1.wireOp",EDGE,"fcba4419-a2ee-464f-be9d-58f11bf3418b.sketch_text.stroke-162"),sQuery(id+"FQ5JFwxVdaqARUP_1.wireOp",EDGE,"fcba4419-a2ee-464f-be9d-58f11bf3418b.sketch_text.stroke-163"),sQuery(id+"FQ5JFwxVdaqARUP_1.wireOp",EDGE,"fcba4419-a2ee-464f-be9d-58f11bf3418b.sketch_text.stroke-164"),sQuery(id+"FQ5JFwxVdaqARUP_1.wireOp",EDGE,"fcba4419-a2ee-464f-be9d-58f11bf3418b.sketch_text.stroke-165"),sQuery(id+"FQ5JFwxVdaqARUP_1.wireOp",EDGE,"fcba4419-a2ee-464f-be9d-58f11bf3418b.sketch_text.stroke-166"),sQuery(id+"FQ5JFwxVdaqARUP_1.wireOp",EDGE,"fcba4419-a2ee-464f-be9d-58f11bf3418b.sketch_text.stroke-167"),sQuery(id+"FQ5JFwxVdaqARUP_1.wireOp",EDGE,"fcba4419-a2ee-464f-be9d-58f11bf3418b.sketch_text.stroke-168"),sQuery(id+"FQ5JFwxVdaqARUP_1.wireOp",EDGE,"fcba4419-a2ee-464f-be9d-58f11bf3418b.sketch_text.stroke-169"),sQuery(id+"FQ5JFwxVdaqARUP_1.wireOp",EDGE,"fcba4419-a2ee-464f-be9d-58f11bf3418b.sketch_text.stroke-170"),sQuery(id+"FQ5JFwxVdaqARUP_1.wireOp",EDGE,"fcba4419-a2ee-464f-be9d-58f11bf3418b.sketch_text.stroke-171"),sQuery(id+"FQ5JFwxVdaqARUP_1.wireOp",EDGE,"fcba4419-a2ee-464f-be9d-58f11bf3418b.sketch_text.stroke-172"),sQuery(id+"FQ5JFwxVdaqARUP_1.wireOp",EDGE,"fcba4419-a2ee-464f-be9d-58f11bf3418b.sketch_text.stroke-173"),sQuery(id+"FHMxAyK4CFUKdhS_1.wireOp",EDGE,"1cb9c079-ea9b-4899-8069-e0e3048e911d.sketch_text.stroke-0"),sQuery(id+"FHMxAyK4CFUKdhS_1.wireOp",EDGE,"1cb9c079-ea9b-4899-8069-e0e3048e911d.sketch_text.stroke-1"),sQuery(id+"FHMxAyK4CFUKdhS_1.wireOp",EDGE,"1cb9c079-ea9b-4899-8069-e0e3048e911d.sketch_text.stroke-2"),sQuery(id+"FHMxAyK4CFUKdhS_1.wireOp",EDGE,"1cb9c079-ea9b-4899-8069-e0e3048e911d.sketch_text.stroke-3"),sQuery(id+"FHMxAyK4CFUKdhS_1.wireOp",EDGE,"1cb9c079-ea9b-4899-8069-e0e3048e911d.sketch_text.stroke-4"),sQuery(id+"FHMxAyK4CFUKdhS_1.wireOp",EDGE,"1cb9c079-ea9b-4899-8069-e0e3048e911d.sketch_text.stroke-5"),sQuery(id+"FHMxAyK4CFUKdhS_1.wireOp",EDGE,"1cb9c079-ea9b-4899-8069-e0e3048e911d.sketch_text.stroke-6"),sQuery(id+"FHMxAyK4CFUKdhS_1.wireOp",EDGE,"1cb9c079-ea9b-4899-8069-e0e3048e911d.sketch_text.stroke-7"),sQuery(id+"FHMxAyK4CFUKdhS_1.wireOp",EDGE,"1cb9c079-ea9b-4899-8069-e0e3048e911d.sketch_text.stroke-8"),sQuery(id+"FHMxAyK4CFUKdhS_1.wireOp",EDGE,"1cb9c079-ea9b-4899-8069-e0e3048e911d.sketch_text.stroke-9"),sQuery(id+"FHMxAyK4CFUKdhS_1.wireOp",EDGE,"1cb9c079-ea9b-4899-8069-e0e3048e911d.sketch_text.stroke-10"),sQuery(id+"FHMxAyK4CFUKdhS_1.wireOp",EDGE,"1cb9c079-ea9b-4899-8069-e0e3048e911d.sketch_text.stroke-11"),sQuery(id+"FHMxAyK4CFUKdhS_1.wireOp",EDGE,"1cb9c079-ea9b-4899-8069-e0e3048e911d.sketch_text.stroke-12"),sQuery(id+"FHMxAyK4CFUKdhS_1.wireOp",EDGE,"1cb9c079-ea9b-4899-8069-e0e3048e911d.sketch_text.stroke-13"),sQuery(id+"FHMxAyK4CFUKdhS_1.wireOp",EDGE,"1cb9c079-ea9b-4899-8069-e0e3048e911d.sketch_text.stroke-14"),sQuery(id+"FHMxAyK4CFUKdhS_1.wireOp",EDGE,"1cb9c079-ea9b-4899-8069-e0e3048e911d.sketch_text.stroke-15"),sQuery(id+"FHMxAyK4CFUKdhS_1.wireOp",EDGE,"1cb9c079-ea9b-4899-8069-e0e3048e911d.sketch_text.stroke-16"),sQuery(id+"FHMxAyK4CFUKdhS_1.wireOp",EDGE,"1cb9c079-ea9b-4899-8069-e0e3048e911d.sketch_text.stroke-17"),sQuery(id+"FHMxAyK4CFUKdhS_1.wireOp",EDGE,"1cb9c079-ea9b-4899-8069-e0e3048e911d.sketch_text.stroke-18"),sQuery(id+"FHMxAyK4CFUKdhS_1.wireOp",EDGE,"1cb9c079-ea9b-4899-8069-e0e3048e911d.sketch_text.stroke-19"),sQuery(id+"FHMxAyK4CFUKdhS_1.wireOp",EDGE,"1cb9c079-ea9b-4899-8069-e0e3048e911d.sketch_text.stroke-20"),sQuery(id+"FHMxAyK4CFUKdhS_1.wireOp",EDGE,"1cb9c079-ea9b-4899-8069-e0e3048e911d.sketch_text.stroke-21"),sQuery(id+"FHMxAyK4CFUKdhS_1.wireOp",EDGE,"1cb9c079-ea9b-4899-8069-e0e3048e911d.sketch_text.stroke-22"),sQuery(id+"FHMxAyK4CFUKdhS_1.wireOp",EDGE,"1cb9c079-ea9b-4899-8069-e0e3048e911d.sketch_text.stroke-23"),sQuery(id+"FHMxAyK4CFUKdhS_1.wireOp",EDGE,"1cb9c079-ea9b-4899-8069-e0e3048e911d.sketch_text.stroke-24"),sQuery(id+"FHMxAyK4CFUKdhS_1.wireOp",EDGE,"1cb9c079-ea9b-4899-8069-e0e3048e911d.sketch_text.stroke-25"),sQuery(id+"FHMxAyK4CFUKdhS_1.wireOp",EDGE,"1cb9c079-ea9b-4899-8069-e0e3048e911d.sketch_text.stroke-26"),sQuery(id+"FHMxAyK4CFUKdhS_1.wireOp",EDGE,"1cb9c079-ea9b-4899-8069-e0e3048e911d.sketch_text.stroke-27"),sQuery(id+"FHMxAyK4CFUKdhS_1.wireOp",EDGE,"1cb9c079-ea9b-4899-8069-e0e3048e911d.sketch_text.stroke-28"),sQuery(id+"FHMxAyK4CFUKdhS_1.wireOp",EDGE,"1cb9c079-ea9b-4899-8069-e0e3048e911d.sketch_text.stroke-29"),sQuery(id+"FHMxAyK4CFUKdhS_1.wireOp",EDGE,"1cb9c079-ea9b-4899-8069-e0e3048e911d.sketch_text.stroke-30"),sQuery(id+"FHMxAyK4CFUKdhS_1.wireOp",EDGE,"1cb9c079-ea9b-4899-8069-e0e3048e911d.sketch_text.stroke-31"),sQuery(id+"FHMxAyK4CFUKdhS_1.wireOp",EDGE,"1cb9c079-ea9b-4899-8069-e0e3048e911d.sketch_text.stroke-32"),sQuery(id+"FHMxAyK4CFUKdhS_1.wireOp",EDGE,"1cb9c079-ea9b-4899-8069-e0e3048e911d.sketch_text.stroke-33"),sQuery(id+"FHMxAyK4CFUKdhS_1.wireOp",EDGE,"1cb9c079-ea9b-4899-8069-e0e3048e911d.sketch_text.stroke-34"),sQuery(id+"FHMxAyK4CFUKdhS_1.wireOp",EDGE,"1cb9c079-ea9b-4899-8069-e0e3048e911d.sketch_text.stroke-35"),sQuery(id+"FHMxAyK4CFUKdhS_1.wireOp",EDGE,"1cb9c079-ea9b-4899-8069-e0e3048e911d.sketch_text.stroke-36"),sQuery(id+"FHMxAyK4CFUKdhS_1.wireOp",EDGE,"1cb9c079-ea9b-4899-8069-e0e3048e911d.sketch_text.stroke-37"),sQuery(id+"FHMxAyK4CFUKdhS_1.wireOp",EDGE,"1cb9c079-ea9b-4899-8069-e0e3048e911d.sketch_text.stroke-38"),sQuery(id+"FHMxAyK4CFUKdhS_1.wireOp",EDGE,"1cb9c079-ea9b-4899-8069-e0e3048e911d.sketch_text.stroke-39"),sQuery(id+"FHMxAyK4CFUKdhS_1.wireOp",EDGE,"1cb9c079-ea9b-4899-8069-e0e3048e911d.sketch_text.stroke-40"),sQuery(id+"FHMxAyK4CFUKdhS_1.wireOp",EDGE,"1cb9c079-ea9b-4899-8069-e0e3048e911d.sketch_text.stroke-41"),sQuery(id+"FHMxAyK4CFUKdhS_1.wireOp",EDGE,"1cb9c079-ea9b-4899-8069-e0e3048e911d.sketch_text.stroke-42"),sQuery(id+"FHMxAyK4CFUKdhS_1.wireOp",EDGE,"1cb9c079-ea9b-4899-8069-e0e3048e911d.sketch_text.stroke-43"),sQuery(id+"FHMxAyK4CFUKdhS_1.wireOp",EDGE,"1cb9c079-ea9b-4899-8069-e0e3048e911d.sketch_text.stroke-44"),sQuery(id+"FHMxAyK4CFUKdhS_1.wireOp",EDGE,"1cb9c079-ea9b-4899-8069-e0e3048e911d.sketch_text.stroke-45"),sQuery(id+"FHMxAyK4CFUKdhS_1.wireOp",EDGE,"1cb9c079-ea9b-4899-8069-e0e3048e911d.sketch_text.stroke-46"),sQuery(id+"FHMxAyK4CFUKdhS_1.wireOp",EDGE,"1cb9c079-ea9b-4899-8069-e0e3048e911d.sketch_text.stroke-47"),sQuery(id+"FHMxAyK4CFUKdhS_1.wireOp",EDGE,"1cb9c079-ea9b-4899-8069-e0e3048e911d.sketch_text.stroke-48"),sQuery(id+"FHMxAyK4CFUKdhS_1.wireOp",EDGE,"1cb9c079-ea9b-4899-8069-e0e3048e911d.sketch_text.stroke-49"),sQuery(id+"FHMxAyK4CFUKdhS_1.wireOp",EDGE,"1cb9c079-ea9b-4899-8069-e0e3048e911d.sketch_text.stroke-50"),sQuery(id+"FHMxAyK4CFUKdhS_1.wireOp",EDGE,"1cb9c079-ea9b-4899-8069-e0e3048e911d.sketch_text.stroke-51"),sQuery(id+"FHMxAyK4CFUKdhS_1.wireOp",EDGE,"1cb9c079-ea9b-4899-8069-e0e3048e911d.sketch_text.stroke-52"),sQuery(id+"FHMxAyK4CFUKdhS_1.wireOp",EDGE,"1cb9c079-ea9b-4899-8069-e0e3048e911d.sketch_text.stroke-53"),sQuery(id+"FHMxAyK4CFUKdhS_1.wireOp",EDGE,"1cb9c079-ea9b-4899-8069-e0e3048e911d.sketch_text.stroke-54"),sQuery(id+"FHMxAyK4CFUKdhS_1.wireOp",EDGE,"1cb9c079-ea9b-4899-8069-e0e3048e911d.sketch_text.stroke-55"),sQuery(id+"FHMxAyK4CFUKdhS_1.wireOp",EDGE,"1cb9c079-ea9b-4899-8069-e0e3048e911d.sketch_text.stroke-56"),sQuery(id+"FHMxAyK4CFUKdhS_1.wireOp",EDGE,"1cb9c079-ea9b-4899-8069-e0e3048e911d.sketch_text.stroke-57"),sQuery(id+"FHMxAyK4CFUKdhS_1.wireOp",EDGE,"1cb9c079-ea9b-4899-8069-e0e3048e911d.sketch_text.stroke-58"),sQuery(id+"FHMxAyK4CFUKdhS_1.wireOp",EDGE,"1cb9c079-ea9b-4899-8069-e0e3048e911d.sketch_text.stroke-59"),sQuery(id+"FHMxAyK4CFUKdhS_1.wireOp",EDGE,"1cb9c079-ea9b-4899-8069-e0e3048e911d.sketch_text.stroke-60"),sQuery(id+"FHMxAyK4CFUKdhS_1.wireOp",EDGE,"1cb9c079-ea9b-4899-8069-e0e3048e911d.sketch_text.stroke-61"),sQuery(id+"FHMxAyK4CFUKdhS_1.wireOp",EDGE,"1cb9c079-ea9b-4899-8069-e0e3048e911d.sketch_text.stroke-62"),sQuery(id+"FHMxAyK4CFUKdhS_1.wireOp",EDGE,"1cb9c079-ea9b-4899-8069-e0e3048e911d.sketch_text.stroke-71"),sQuery(id+"FHMxAyK4CFUKdhS_1.wireOp",EDGE,"1cb9c079-ea9b-4899-8069-e0e3048e911d.sketch_text.stroke-72"),sQuery(id+"FHMxAyK4CFUKdhS_1.wireOp",EDGE,"1cb9c079-ea9b-4899-8069-e0e3048e911d.sketch_text.stroke-73"),sQuery(id+"FHMxAyK4CFUKdhS_1.wireOp",EDGE,"1cb9c079-ea9b-4899-8069-e0e3048e911d.sketch_text.stroke-74"),sQuery(id+"FHMxAyK4CFUKdhS_1.wireOp",EDGE,"1cb9c079-ea9b-4899-8069-e0e3048e911d.sketch_text.stroke-75"),sQuery(id+"FHMxAyK4CFUKdhS_1.wireOp",EDGE,"1cb9c079-ea9b-4899-8069-e0e3048e911d.sketch_text.stroke-76"),sQuery(id+"FHMxAyK4CFUKdhS_1.wireOp",EDGE,"1cb9c079-ea9b-4899-8069-e0e3048e911d.sketch_text.stroke-77"),sQuery(id+"FHMxAyK4CFUKdhS_1.wireOp",EDGE,"1cb9c079-ea9b-4899-8069-e0e3048e911d.sketch_text.stroke-78"),sQuery(id+"FHMxAyK4CFUKdhS_1.wireOp",EDGE,"1cb9c079-ea9b-4899-8069-e0e3048e911d.sketch_text.stroke-79"),sQuery(id+"FHMxAyK4CFUKdhS_1.wireOp",EDGE,"1cb9c079-ea9b-4899-8069-e0e3048e911d.sketch_text.stroke-80"),sQuery(id+"FHMxAyK4CFUKdhS_1.wireOp",EDGE,"1cb9c079-ea9b-4899-8069-e0e3048e911d.sketch_text.stroke-81"),sQuery(id+"FHMxAyK4CFUKdhS_1.wireOp",EDGE,"1cb9c079-ea9b-4899-8069-e0e3048e911d.sketch_text.stroke-82"),sQuery(id+"FHMxAyK4CFUKdhS_1.wireOp",EDGE,"1cb9c079-ea9b-4899-8069-e0e3048e911d.sketch_text.stroke-83"),sQuery(id+"FHMxAyK4CFUKdhS_1.wireOp",EDGE,"1cb9c079-ea9b-4899-8069-e0e3048e911d.sketch_text.stroke-84"),sQuery(id+"FHMxAyK4CFUKdhS_1.wireOp",EDGE,"1cb9c079-ea9b-4899-8069-e0e3048e911d.sketch_text.stroke-85"),sQuery(id+"FHMxAyK4CFUKdhS_1.wireOp",EDGE,"1cb9c079-ea9b-4899-8069-e0e3048e911d.sketch_text.stroke-86"),sQuery(id+"FHMxAyK4CFUKdhS_1.wireOp",EDGE,"1cb9c079-ea9b-4899-8069-e0e3048e911d.sketch_text.stroke-87"),sQuery(id+"FHMxAyK4CFUKdhS_1.wireOp",EDGE,"1cb9c079-ea9b-4899-8069-e0e3048e911d.sketch_text.stroke-88"),sQuery(id+"FHMxAyK4CFUKdhS_1.wireOp",EDGE,"1cb9c079-ea9b-4899-8069-e0e3048e911d.sketch_text.stroke-89"),sQuery(id+"FHMxAyK4CFUKdhS_1.wireOp",EDGE,"1cb9c079-ea9b-4899-8069-e0e3048e911d.sketch_text.stroke-90"),sQuery(id+"FHMxAyK4CFUKdhS_1.wireOp",EDGE,"1cb9c079-ea9b-4899-8069-e0e3048e911d.sketch_text.stroke-91"),sQuery(id+"FHMxAyK4CFUKdhS_1.wireOp",EDGE,"1cb9c079-ea9b-4899-8069-e0e3048e911d.sketch_text.stroke-92"),sQuery(id+"FHMxAyK4CFUKdhS_1.wireOp",EDGE,"1cb9c079-ea9b-4899-8069-e0e3048e911d.sketch_text.stroke-93"),sQuery(id+"FHMxAyK4CFUKdhS_1.wireOp",EDGE,"1cb9c079-ea9b-4899-8069-e0e3048e911d.sketch_text.stroke-94"),sQuery(id+"FHMxAyK4CFUKdhS_1.wireOp",EDGE,"1cb9c079-ea9b-4899-8069-e0e3048e911d.sketch_text.stroke-95"),sQuery(id+"FHMxAyK4CFUKdhS_1.wireOp",EDGE,"1cb9c079-ea9b-4899-8069-e0e3048e911d.sketch_text.stroke-96"),sQuery(id+"FHMxAyK4CFUKdhS_1.wireOp",EDGE,"1cb9c079-ea9b-4899-8069-e0e3048e911d.sketch_text.stroke-97"),sQuery(id+"FHMxAyK4CFUKdhS_1.wireOp",EDGE,"1cb9c079-ea9b-4899-8069-e0e3048e911d.sketch_text.stroke-103"),sQuery(id+"FHMxAyK4CFUKdhS_1.wireOp",EDGE,"1cb9c079-ea9b-4899-8069-e0e3048e911d.sketch_text.stroke-104"),sQuery(id+"FHMxAyK4CFUKdhS_1.wireOp",EDGE,"1cb9c079-ea9b-4899-8069-e0e3048e911d.sketch_text.stroke-105"),sQuery(id+"FHMxAyK4CFUKdhS_1.wireOp",EDGE,"1cb9c079-ea9b-4899-8069-e0e3048e911d.sketch_text.stroke-106"),sQuery(id+"FHMxAyK4CFUKdhS_1.wireOp",EDGE,"1cb9c079-ea9b-4899-8069-e0e3048e911d.sketch_text.stroke-107"),sQuery(id+"FHMxAyK4CFUKdhS_1.wireOp",EDGE,"1cb9c079-ea9b-4899-8069-e0e3048e911d.sketch_text.stroke-108"),sQuery(id+"FHMxAyK4CFUKdhS_1.wireOp",EDGE,"1cb9c079-ea9b-4899-8069-e0e3048e911d.sketch_text.stroke-109"),sQuery(id+"FHMxAyK4CFUKdhS_1.wireOp",EDGE,"1cb9c079-ea9b-4899-8069-e0e3048e911d.sketch_text.stroke-110"),sQuery(id+"FHMxAyK4CFUKdhS_1.wireOp",EDGE,"1cb9c079-ea9b-4899-8069-e0e3048e911d.sketch_text.stroke-111"),sQuery(id+"FHMxAyK4CFUKdhS_1.wireOp",EDGE,"1cb9c079-ea9b-4899-8069-e0e3048e911d.sketch_text.stroke-112"),sQuery(id+"FHMxAyK4CFUKdhS_1.wireOp",EDGE,"1cb9c079-ea9b-4899-8069-e0e3048e911d.sketch_text.stroke-113"),sQuery(id+"FHMxAyK4CFUKdhS_1.wireOp",EDGE,"1cb9c079-ea9b-4899-8069-e0e3048e911d.sketch_text.stroke-114"),sQuery(id+"FHMxAyK4CFUKdhS_1.wireOp",EDGE,"1cb9c079-ea9b-4899-8069-e0e3048e911d.sketch_text.stroke-115"),sQuery(id+"FHMxAyK4CFUKdhS_1.wireOp",EDGE,"1cb9c079-ea9b-4899-8069-e0e3048e911d.sketch_text.stroke-116"),sQuery(id+"FHMxAyK4CFUKdhS_1.wireOp",EDGE,"1cb9c079-ea9b-4899-8069-e0e3048e911d.sketch_text.stroke-117"),sQuery(id+"FHMxAyK4CFUKdhS_1.wireOp",EDGE,"1cb9c079-ea9b-4899-8069-e0e3048e911d.sketch_text.stroke-118"),sQuery(id+"FHMxAyK4CFUKdhS_1.wireOp",EDGE,"1cb9c079-ea9b-4899-8069-e0e3048e911d.sketch_text.stroke-119"),sQuery(id+"FHMxAyK4CFUKdhS_1.wireOp",EDGE,"1cb9c079-ea9b-4899-8069-e0e3048e911d.sketch_text.stroke-120"),sQuery(id+"FHMxAyK4CFUKdhS_1.wireOp",EDGE,"1cb9c079-ea9b-4899-8069-e0e3048e911d.sketch_text.stroke-121"),sQuery(id+"FHMxAyK4CFUKdhS_1.wireOp",EDGE,"1cb9c079-ea9b-4899-8069-e0e3048e911d.sketch_text.stroke-122"),sQuery(id+"FHMxAyK4CFUKdhS_1.wireOp",EDGE,"1cb9c079-ea9b-4899-8069-e0e3048e911d.sketch_text.stroke-123"),sQuery(id+"FHMxAyK4CFUKdhS_1.wireOp",EDGE,"1cb9c079-ea9b-4899-8069-e0e3048e911d.sketch_text.stroke-124"),sQuery(id+"FHMxAyK4CFUKdhS_1.wireOp",EDGE,"1cb9c079-ea9b-4899-8069-e0e3048e911d.sketch_text.stroke-125"),sQuery(id+"FHMxAyK4CFUKdhS_1.wireOp",EDGE,"1cb9c079-ea9b-4899-8069-e0e3048e911d.sketch_text.stroke-126"),sQuery(id+"FHMxAyK4CFUKdhS_1.wireOp",EDGE,"1cb9c079-ea9b-4899-8069-e0e3048e911d.sketch_text.stroke-127"),sQuery(id+"FHMxAyK4CFUKdhS_1.wireOp",EDGE,"1cb9c079-ea9b-4899-8069-e0e3048e911d.sketch_text.stroke-128"),sQuery(id+"FHMxAyK4CFUKdhS_1.wireOp",EDGE,"1cb9c079-ea9b-4899-8069-e0e3048e911d.sketch_text.stroke-129"),sQuery(id+"FHMxAyK4CFUKdhS_1.wireOp",EDGE,"1cb9c079-ea9b-4899-8069-e0e3048e911d.sketch_text.stroke-130"),sQuery(id+"FHMxAyK4CFUKdhS_1.wireOp",EDGE,"1cb9c079-ea9b-4899-8069-e0e3048e911d.sketch_text.stroke-131"),sQuery(id+"FHMxAyK4CFUKdhS_1.wireOp",EDGE,"1cb9c079-ea9b-4899-8069-e0e3048e911d.sketch_text.stroke-132"),sQuery(id+"FHMxAyK4CFUKdhS_1.wireOp",EDGE,"1cb9c079-ea9b-4899-8069-e0e3048e911d.sketch_text.stroke-133"),sQuery(id+"FHMxAyK4CFUKdhS_1.wireOp",EDGE,"1cb9c079-ea9b-4899-8069-e0e3048e911d.sketch_text.stroke-134"),sQuery(id+"FHMxAyK4CFUKdhS_1.wireOp",EDGE,"1cb9c079-ea9b-4899-8069-e0e3048e911d.sketch_text.stroke-135"),sQuery(id+"FHMxAyK4CFUKdhS_1.wireOp",EDGE,"1cb9c079-ea9b-4899-8069-e0e3048e911d.sketch_text.stroke-136"),sQuery(id+"FHMxAyK4CFUKdhS_1.wireOp",EDGE,"1cb9c079-ea9b-4899-8069-e0e3048e911d.sketch_text.stroke-137"),sQuery(id+"FHMxAyK4CFUKdhS_1.wireOp",EDGE,"1cb9c079-ea9b-4899-8069-e0e3048e911d.sketch_text.stroke-138"),sQuery(id+"FHMxAyK4CFUKdhS_1.wireOp",EDGE,"1cb9c079-ea9b-4899-8069-e0e3048e911d.sketch_text.stroke-139"),sQuery(id+"FHMxAyK4CFUKdhS_1.wireOp",EDGE,"1cb9c079-ea9b-4899-8069-e0e3048e911d.sketch_text.stroke-140"),sQuery(id+"FHMxAyK4CFUKdhS_1.wireOp",EDGE,"1cb9c079-ea9b-4899-8069-e0e3048e911d.sketch_text.stroke-141"),sQuery(id+"FHMxAyK4CFUKdhS_1.wireOp",EDGE,"1cb9c079-ea9b-4899-8069-e0e3048e911d.sketch_text.stroke-142"),sQuery(id+"FHMxAyK4CFUKdhS_1.wireOp",EDGE,"1cb9c079-ea9b-4899-8069-e0e3048e911d.sketch_text.stroke-143"),sQuery(id+"FHMxAyK4CFUKdhS_1.wireOp",EDGE,"1cb9c079-ea9b-4899-8069-e0e3048e911d.sketch_text.stroke-144"),sQuery(id+"FHMxAyK4CFUKdhS_1.wireOp",EDGE,"1cb9c079-ea9b-4899-8069-e0e3048e911d.sketch_text.stroke-145"),sQuery(id+"FHMxAyK4CFUKdhS_1.wireOp",EDGE,"1cb9c079-ea9b-4899-8069-e0e3048e911d.sketch_text.stroke-146"),sQuery(id+"FHMxAyK4CFUKdhS_1.wireOp",EDGE,"1cb9c079-ea9b-4899-8069-e0e3048e911d.sketch_text.stroke-147"),sQuery(id+"FHMxAyK4CFUKdhS_1.wireOp",EDGE,"1cb9c079-ea9b-4899-8069-e0e3048e911d.sketch_text.stroke-148"),sQuery(id+"FHMxAyK4CFUKdhS_1.wireOp",EDGE,"1cb9c079-ea9b-4899-8069-e0e3048e911d.sketch_text.stroke-149"),sQuery(id+"FHMxAyK4CFUKdhS_1.wireOp",EDGE,"1cb9c079-ea9b-4899-8069-e0e3048e911d.sketch_text.stroke-150"),sQuery(id+"FHMxAyK4CFUKdhS_1.wireOp",EDGE,"1cb9c079-ea9b-4899-8069-e0e3048e911d.sketch_text.stroke-151"),sQuery(id+"FHMxAyK4CFUKdhS_1.wireOp",EDGE,"1cb9c079-ea9b-4899-8069-e0e3048e911d.sketch_text.stroke-152"),sQuery(id+"FHMxAyK4CFUKdhS_1.wireOp",EDGE,"1cb9c079-ea9b-4899-8069-e0e3048e911d.sketch_text.stroke-153"),sQuery(id+"FHMxAyK4CFUKdhS_1.wireOp",EDGE,"1cb9c079-ea9b-4899-8069-e0e3048e911d.sketch_text.stroke-159"),sQuery(id+"FHMxAyK4CFUKdhS_1.wireOp",EDGE,"1cb9c079-ea9b-4899-8069-e0e3048e911d.sketch_text.stroke-160"),sQuery(id+"FHMxAyK4CFUKdhS_1.wireOp",EDGE,"1cb9c079-ea9b-4899-8069-e0e3048e911d.sketch_text.stroke-161"),sQuery(id+"FHMxAyK4CFUKdhS_1.wireOp",EDGE,"1cb9c079-ea9b-4899-8069-e0e3048e911d.sketch_text.stroke-162"),sQuery(id+"FHMxAyK4CFUKdhS_1.wireOp",EDGE,"1cb9c079-ea9b-4899-8069-e0e3048e911d.sketch_text.stroke-163"),sQuery(id+"FHMxAyK4CFUKdhS_1.wireOp",EDGE,"1cb9c079-ea9b-4899-8069-e0e3048e911d.sketch_text.stroke-164"),sQuery(id+"FHMxAyK4CFUKdhS_1.wireOp",EDGE,"1cb9c079-ea9b-4899-8069-e0e3048e911d.sketch_text.stroke-165"),sQuery(id+"FHMxAyK4CFUKdhS_1.wireOp",EDGE,"1cb9c079-ea9b-4899-8069-e0e3048e911d.sketch_text.stroke-166"),sQuery(id+"FHMxAyK4CFUKdhS_1.wireOp",EDGE,"1cb9c079-ea9b-4899-8069-e0e3048e911d.sketch_text.stroke-167"),sQuery(id+"FHMxAyK4CFUKdhS_1.wireOp",EDGE,"1cb9c079-ea9b-4899-8069-e0e3048e911d.sketch_text.stroke-168"),sQuery(id+"FHMxAyK4CFUKdhS_1.wireOp",EDGE,"1cb9c079-ea9b-4899-8069-e0e3048e911d.sketch_text.stroke-169"),sQuery(id+"FHMxAyK4CFUKdhS_1.wireOp",EDGE,"1cb9c079-ea9b-4899-8069-e0e3048e911d.sketch_text.stroke-170"),sQuery(id+"FHMxAyK4CFUKdhS_1.wireOp",EDGE,"1cb9c079-ea9b-4899-8069-e0e3048e911d.sketch_text.stroke-171"),sQuery(id+"FHMxAyK4CFUKdhS_1.wireOp",EDGE,"1cb9c079-ea9b-4899-8069-e0e3048e911d.sketch_text.stroke-172"),sQuery(id+"FHMxAyK4CFUKdhS_1.wireOp",EDGE,"1cb9c079-ea9b-4899-8069-e0e3048e911d.sketch_text.stroke-173"),sQuery(id+"FHMxAyK4CFUKdhS_1.wireOp",EDGE,"1cb9c079-ea9b-4899-8069-e0e3048e911d.sketch_text.stroke-174"),sQuery(id+"FHMxAyK4CFUKdhS_1.wireOp",EDGE,"1cb9c079-ea9b-4899-8069-e0e3048e911d.sketch_text.stroke-175"),sQuery(id+"FHMxAyK4CFUKdhS_1.wireOp",EDGE,"1cb9c079-ea9b-4899-8069-e0e3048e911d.sketch_text.stroke-176"),sQuery(id+"FHMxAyK4CFUKdhS_1.wireOp",EDGE,"1cb9c079-ea9b-4899-8069-e0e3048e911d.sketch_text.stroke-177"),sQuery(id+"FHMxAyK4CFUKdhS_1.wireOp",EDGE,"1cb9c079-ea9b-4899-8069-e0e3048e911d.sketch_text.stroke-178"),sQuery(id+"FHMxAyK4CFUKdhS_1.wireOp",EDGE,"1cb9c079-ea9b-4899-8069-e0e3048e911d.sketch_text.stroke-179"),sQuery(id+"FHMxAyK4CFUKdhS_1.wireOp",EDGE,"1cb9c079-ea9b-4899-8069-e0e3048e911d.sketch_text.stroke-180"),sQuery(id+"F2.wireOp",EDGE,"727ac2c1-f511-4829-95a7-a443ef16a4cd"),subQ2])],"isStart":true}),makeQuery(id+"F3.opExtrude","SWEPT_FACE",FACE,{"disambiguationData":[OSD([subQ2])]})]),OD(1.0)],"derivedFrom":makeQuery(id+"F1.opExtrude","CAP_EDGE",EDGE,{"disambiguationData":[OSD([subQ0])],"isStart":false})});}
            var Q20;
            {var subQ0=sQuery(id+"F0.wireOp",EDGE,"E0.top");var subQ1=sQuery(id+"F0.wireOp",EDGE,"E0.bottom");var subQ2=sQuery(id+"F2.wireOp",EDGE,"E26");Q20=makeQuery(id+"F3.boolean.opBoolean","SPLIT",EDGE,{"disambiguationData":[TD([makeQuery(id+"F1.opExtrude","CAP_FACE",FACE,{"disambiguationData":[OSD([subQ1,subQ0,sQuery(id+"F0.wireOp",EDGE,"E0.left"),sQuery(id+"F0.wireOp",EDGE,"E0.right")])],"isStart":false}),makeQuery(id+"F1.opExtrude","SWEPT_FACE",FACE,{"disambiguationData":[OSD([subQ0])]}),makeQuery(id+"F3.opExtrude","SWEPT_FACE",FACE,{"disambiguationData":[OSD([subQ2])]}),makeQuery(id+"F3.opExtrude","CAP_FACE",FACE,{"disambiguationData":[OSD([subQ1,sQuery(id+"FQ5JFwxVdaqARUP_1.wireOp",EDGE,"fcba4419-a2ee-464f-be9d-58f11bf3418b.sketch_text.stroke-0"),sQuery(id+"FQ5JFwxVdaqARUP_1.wireOp",EDGE,"fcba4419-a2ee-464f-be9d-58f11bf3418b.sketch_text.stroke-1"),sQuery(id+"FQ5JFwxVdaqARUP_1.wireOp",EDGE,"fcba4419-a2ee-464f-be9d-58f11bf3418b.sketch_text.stroke-2"),sQuery(id+"FQ5JFwxVdaqARUP_1.wireOp",EDGE,"fcba4419-a2ee-464f-be9d-58f11bf3418b.sketch_text.stroke-3"),sQuery(id+"FQ5JFwxVdaqARUP_1.wireOp",EDGE,"fcba4419-a2ee-464f-be9d-58f11bf3418b.sketch_text.stroke-4"),sQuery(id+"FQ5JFwxVdaqARUP_1.wireOp",EDGE,"fcba4419-a2ee-464f-be9d-58f11bf3418b.sketch_text.stroke-5"),sQuery(id+"FQ5JFwxVdaqARUP_1.wireOp",EDGE,"fcba4419-a2ee-464f-be9d-58f11bf3418b.sketch_text.stroke-6"),sQuery(id+"FQ5JFwxVdaqARUP_1.wireOp",EDGE,"fcba4419-a2ee-464f-be9d-58f11bf3418b.sketch_text.stroke-7"),sQuery(id+"FQ5JFwxVdaqARUP_1.wireOp",EDGE,"fcba4419-a2ee-464f-be9d-58f11bf3418b.sketch_text.stroke-8"),sQuery(id+"FQ5JFwxVdaqARUP_1.wireOp",EDGE,"fcba4419-a2ee-464f-be9d-58f11bf3418b.sketch_text.stroke-9"),sQuery(id+"FQ5JFwxVdaqARUP_1.wireOp",EDGE,"fcba4419-a2ee-464f-be9d-58f11bf3418b.sketch_text.stroke-10"),sQuery(id+"FQ5JFwxVdaqARUP_1.wireOp",EDGE,"fcba4419-a2ee-464f-be9d-58f11bf3418b.sketch_text.stroke-11"),sQuery(id+"FQ5JFwxVdaqARUP_1.wireOp",EDGE,"fcba4419-a2ee-464f-be9d-58f11bf3418b.sketch_text.stroke-12"),sQuery(id+"FQ5JFwxVdaqARUP_1.wireOp",EDGE,"fcba4419-a2ee-464f-be9d-58f11bf3418b.sketch_text.stroke-13"),sQuery(id+"FQ5JFwxVdaqARUP_1.wireOp",EDGE,"fcba4419-a2ee-464f-be9d-58f11bf3418b.sketch_text.stroke-14"),sQuery(id+"FQ5JFwxVdaqARUP_1.wireOp",EDGE,"fcba4419-a2ee-464f-be9d-58f11bf3418b.sketch_text.stroke-15"),sQuery(id+"FQ5JFwxVdaqARUP_1.wireOp",EDGE,"fcba4419-a2ee-464f-be9d-58f11bf3418b.sketch_text.stroke-16"),sQuery(id+"FQ5JFwxVdaqARUP_1.wireOp",EDGE,"fcba4419-a2ee-464f-be9d-58f11bf3418b.sketch_text.stroke-17"),sQuery(id+"FQ5JFwxVdaqARUP_1.wireOp",EDGE,"fcba4419-a2ee-464f-be9d-58f11bf3418b.sketch_text.stroke-18"),sQuery(id+"FQ5JFwxVdaqARUP_1.wireOp",EDGE,"fcba4419-a2ee-464f-be9d-58f11bf3418b.sketch_text.stroke-19"),sQuery(id+"FQ5JFwxVdaqARUP_1.wireOp",EDGE,"fcba4419-a2ee-464f-be9d-58f11bf3418b.sketch_text.stroke-20"),sQuery(id+"FQ5JFwxVdaqARUP_1.wireOp",EDGE,"fcba4419-a2ee-464f-be9d-58f11bf3418b.sketch_text.stroke-21"),sQuery(id+"FQ5JFwxVdaqARUP_1.wireOp",EDGE,"fcba4419-a2ee-464f-be9d-58f11bf3418b.sketch_text.stroke-22"),sQuery(id+"FQ5JFwxVdaqARUP_1.wireOp",EDGE,"fcba4419-a2ee-464f-be9d-58f11bf3418b.sketch_text.stroke-23"),sQuery(id+"FQ5JFwxVdaqARUP_1.wireOp",EDGE,"fcba4419-a2ee-464f-be9d-58f11bf3418b.sketch_text.stroke-24"),sQuery(id+"FQ5JFwxVdaqARUP_1.wireOp",EDGE,"fcba4419-a2ee-464f-be9d-58f11bf3418b.sketch_text.stroke-25"),sQuery(id+"FQ5JFwxVdaqARUP_1.wireOp",EDGE,"fcba4419-a2ee-464f-be9d-58f11bf3418b.sketch_text.stroke-26"),sQuery(id+"FQ5JFwxVdaqARUP_1.wireOp",EDGE,"fcba4419-a2ee-464f-be9d-58f11bf3418b.sketch_text.stroke-27"),sQuery(id+"FQ5JFwxVdaqARUP_1.wireOp",EDGE,"fcba4419-a2ee-464f-be9d-58f11bf3418b.sketch_text.stroke-28"),sQuery(id+"FQ5JFwxVdaqARUP_1.wireOp",EDGE,"fcba4419-a2ee-464f-be9d-58f11bf3418b.sketch_text.stroke-29"),sQuery(id+"FQ5JFwxVdaqARUP_1.wireOp",EDGE,"fcba4419-a2ee-464f-be9d-58f11bf3418b.sketch_text.stroke-30"),sQuery(id+"FQ5JFwxVdaqARUP_1.wireOp",EDGE,"fcba4419-a2ee-464f-be9d-58f11bf3418b.sketch_text.stroke-31"),sQuery(id+"FQ5JFwxVdaqARUP_1.wireOp",EDGE,"fcba4419-a2ee-464f-be9d-58f11bf3418b.sketch_text.stroke-32"),sQuery(id+"FQ5JFwxVdaqARUP_1.wireOp",EDGE,"fcba4419-a2ee-464f-be9d-58f11bf3418b.sketch_text.stroke-33"),sQuery(id+"FQ5JFwxVdaqARUP_1.wireOp",EDGE,"fcba4419-a2ee-464f-be9d-58f11bf3418b.sketch_text.stroke-34"),sQuery(id+"FQ5JFwxVdaqARUP_1.wireOp",EDGE,"fcba4419-a2ee-464f-be9d-58f11bf3418b.sketch_text.stroke-35"),sQuery(id+"FQ5JFwxVdaqARUP_1.wireOp",EDGE,"fcba4419-a2ee-464f-be9d-58f11bf3418b.sketch_text.stroke-36"),sQuery(id+"FQ5JFwxVdaqARUP_1.wireOp",EDGE,"fcba4419-a2ee-464f-be9d-58f11bf3418b.sketch_text.stroke-37"),sQuery(id+"FQ5JFwxVdaqARUP_1.wireOp",EDGE,"fcba4419-a2ee-464f-be9d-58f11bf3418b.sketch_text.stroke-38"),sQuery(id+"FQ5JFwxVdaqARUP_1.wireOp",EDGE,"fcba4419-a2ee-464f-be9d-58f11bf3418b.sketch_text.stroke-39"),sQuery(id+"FQ5JFwxVdaqARUP_1.wireOp",EDGE,"fcba4419-a2ee-464f-be9d-58f11bf3418b.sketch_text.stroke-40"),sQuery(id+"FQ5JFwxVdaqARUP_1.wireOp",EDGE,"fcba4419-a2ee-464f-be9d-58f11bf3418b.sketch_text.stroke-41"),sQuery(id+"FQ5JFwxVdaqARUP_1.wireOp",EDGE,"fcba4419-a2ee-464f-be9d-58f11bf3418b.sketch_text.stroke-42"),sQuery(id+"FQ5JFwxVdaqARUP_1.wireOp",EDGE,"fcba4419-a2ee-464f-be9d-58f11bf3418b.sketch_text.stroke-43"),sQuery(id+"FQ5JFwxVdaqARUP_1.wireOp",EDGE,"fcba4419-a2ee-464f-be9d-58f11bf3418b.sketch_text.stroke-44"),sQuery(id+"FQ5JFwxVdaqARUP_1.wireOp",EDGE,"fcba4419-a2ee-464f-be9d-58f11bf3418b.sketch_text.stroke-45"),sQuery(id+"FQ5JFwxVdaqARUP_1.wireOp",EDGE,"fcba4419-a2ee-464f-be9d-58f11bf3418b.sketch_text.stroke-46"),sQuery(id+"FQ5JFwxVdaqARUP_1.wireOp",EDGE,"fcba4419-a2ee-464f-be9d-58f11bf3418b.sketch_text.stroke-47"),sQuery(id+"FQ5JFwxVdaqARUP_1.wireOp",EDGE,"fcba4419-a2ee-464f-be9d-58f11bf3418b.sketch_text.stroke-48"),sQuery(id+"FQ5JFwxVdaqARUP_1.wireOp",EDGE,"fcba4419-a2ee-464f-be9d-58f11bf3418b.sketch_text.stroke-49"),sQuery(id+"FQ5JFwxVdaqARUP_1.wireOp",EDGE,"fcba4419-a2ee-464f-be9d-58f11bf3418b.sketch_text.stroke-50"),sQuery(id+"FQ5JFwxVdaqARUP_1.wireOp",EDGE,"fcba4419-a2ee-464f-be9d-58f11bf3418b.sketch_text.stroke-51"),sQuery(id+"FQ5JFwxVdaqARUP_1.wireOp",EDGE,"fcba4419-a2ee-464f-be9d-58f11bf3418b.sketch_text.stroke-52"),sQuery(id+"FQ5JFwxVdaqARUP_1.wireOp",EDGE,"fcba4419-a2ee-464f-be9d-58f11bf3418b.sketch_text.stroke-53"),sQuery(id+"FQ5JFwxVdaqARUP_1.wireOp",EDGE,"fcba4419-a2ee-464f-be9d-58f11bf3418b.sketch_text.stroke-54"),sQuery(id+"FQ5JFwxVdaqARUP_1.wireOp",EDGE,"fcba4419-a2ee-464f-be9d-58f11bf3418b.sketch_text.stroke-55"),sQuery(id+"FQ5JFwxVdaqARUP_1.wireOp",EDGE,"fcba4419-a2ee-464f-be9d-58f11bf3418b.sketch_text.stroke-56"),sQuery(id+"FQ5JFwxVdaqARUP_1.wireOp",EDGE,"fcba4419-a2ee-464f-be9d-58f11bf3418b.sketch_text.stroke-57"),sQuery(id+"FQ5JFwxVdaqARUP_1.wireOp",EDGE,"fcba4419-a2ee-464f-be9d-58f11bf3418b.sketch_text.stroke-58"),sQuery(id+"FQ5JFwxVdaqARUP_1.wireOp",EDGE,"fcba4419-a2ee-464f-be9d-58f11bf3418b.sketch_text.stroke-59"),sQuery(id+"FQ5JFwxVdaqARUP_1.wireOp",EDGE,"fcba4419-a2ee-464f-be9d-58f11bf3418b.sketch_text.stroke-60"),sQuery(id+"FQ5JFwxVdaqARUP_1.wireOp",EDGE,"fcba4419-a2ee-464f-be9d-58f11bf3418b.sketch_text.stroke-61"),sQuery(id+"FQ5JFwxVdaqARUP_1.wireOp",EDGE,"fcba4419-a2ee-464f-be9d-58f11bf3418b.sketch_text.stroke-62"),sQuery(id+"FQ5JFwxVdaqARUP_1.wireOp",EDGE,"fcba4419-a2ee-464f-be9d-58f11bf3418b.sketch_text.stroke-63"),sQuery(id+"FQ5JFwxVdaqARUP_1.wireOp",EDGE,"fcba4419-a2ee-464f-be9d-58f11bf3418b.sketch_text.stroke-64"),sQuery(id+"FQ5JFwxVdaqARUP_1.wireOp",EDGE,"fcba4419-a2ee-464f-be9d-58f11bf3418b.sketch_text.stroke-65"),sQuery(id+"FQ5JFwxVdaqARUP_1.wireOp",EDGE,"fcba4419-a2ee-464f-be9d-58f11bf3418b.sketch_text.stroke-66"),sQuery(id+"FQ5JFwxVdaqARUP_1.wireOp",EDGE,"fcba4419-a2ee-464f-be9d-58f11bf3418b.sketch_text.stroke-67"),sQuery(id+"FQ5JFwxVdaqARUP_1.wireOp",EDGE,"fcba4419-a2ee-464f-be9d-58f11bf3418b.sketch_text.stroke-68"),sQuery(id+"FQ5JFwxVdaqARUP_1.wireOp",EDGE,"fcba4419-a2ee-464f-be9d-58f11bf3418b.sketch_text.stroke-69"),sQuery(id+"FQ5JFwxVdaqARUP_1.wireOp",EDGE,"fcba4419-a2ee-464f-be9d-58f11bf3418b.sketch_text.stroke-70"),sQuery(id+"FQ5JFwxVdaqARUP_1.wireOp",EDGE,"fcba4419-a2ee-464f-be9d-58f11bf3418b.sketch_text.stroke-71"),sQuery(id+"FQ5JFwxVdaqARUP_1.wireOp",EDGE,"fcba4419-a2ee-464f-be9d-58f11bf3418b.sketch_text.stroke-72"),sQuery(id+"FQ5JFwxVdaqARUP_1.wireOp",EDGE,"fcba4419-a2ee-464f-be9d-58f11bf3418b.sketch_text.stroke-73"),sQuery(id+"FQ5JFwxVdaqARUP_1.wireOp",EDGE,"fcba4419-a2ee-464f-be9d-58f11bf3418b.sketch_text.stroke-74"),sQuery(id+"FQ5JFwxVdaqARUP_1.wireOp",EDGE,"fcba4419-a2ee-464f-be9d-58f11bf3418b.sketch_text.stroke-75"),sQuery(id+"FQ5JFwxVdaqARUP_1.wireOp",EDGE,"fcba4419-a2ee-464f-be9d-58f11bf3418b.sketch_text.stroke-76"),sQuery(id+"FQ5JFwxVdaqARUP_1.wireOp",EDGE,"fcba4419-a2ee-464f-be9d-58f11bf3418b.sketch_text.stroke-77"),sQuery(id+"FQ5JFwxVdaqARUP_1.wireOp",EDGE,"fcba4419-a2ee-464f-be9d-58f11bf3418b.sketch_text.stroke-78"),sQuery(id+"FQ5JFwxVdaqARUP_1.wireOp",EDGE,"fcba4419-a2ee-464f-be9d-58f11bf3418b.sketch_text.stroke-79"),sQuery(id+"FQ5JFwxVdaqARUP_1.wireOp",EDGE,"fcba4419-a2ee-464f-be9d-58f11bf3418b.sketch_text.stroke-80"),sQuery(id+"FQ5JFwxVdaqARUP_1.wireOp",EDGE,"fcba4419-a2ee-464f-be9d-58f11bf3418b.sketch_text.stroke-81"),sQuery(id+"FQ5JFwxVdaqARUP_1.wireOp",EDGE,"fcba4419-a2ee-464f-be9d-58f11bf3418b.sketch_text.stroke-82"),sQuery(id+"FQ5JFwxVdaqARUP_1.wireOp",EDGE,"fcba4419-a2ee-464f-be9d-58f11bf3418b.sketch_text.stroke-83"),sQuery(id+"FQ5JFwxVdaqARUP_1.wireOp",EDGE,"fcba4419-a2ee-464f-be9d-58f11bf3418b.sketch_text.stroke-84"),sQuery(id+"FQ5JFwxVdaqARUP_1.wireOp",EDGE,"fcba4419-a2ee-464f-be9d-58f11bf3418b.sketch_text.stroke-85"),sQuery(id+"FQ5JFwxVdaqARUP_1.wireOp",EDGE,"fcba4419-a2ee-464f-be9d-58f11bf3418b.sketch_text.stroke-86"),sQuery(id+"FQ5JFwxVdaqARUP_1.wireOp",EDGE,"fcba4419-a2ee-464f-be9d-58f11bf3418b.sketch_text.stroke-87"),sQuery(id+"FQ5JFwxVdaqARUP_1.wireOp",EDGE,"fcba4419-a2ee-464f-be9d-58f11bf3418b.sketch_text.stroke-88"),sQuery(id+"FQ5JFwxVdaqARUP_1.wireOp",EDGE,"fcba4419-a2ee-464f-be9d-58f11bf3418b.sketch_text.stroke-89"),sQuery(id+"FQ5JFwxVdaqARUP_1.wireOp",EDGE,"fcba4419-a2ee-464f-be9d-58f11bf3418b.sketch_text.stroke-90"),sQuery(id+"FQ5JFwxVdaqARUP_1.wireOp",EDGE,"fcba4419-a2ee-464f-be9d-58f11bf3418b.sketch_text.stroke-91"),sQuery(id+"FQ5JFwxVdaqARUP_1.wireOp",EDGE,"fcba4419-a2ee-464f-be9d-58f11bf3418b.sketch_text.stroke-92"),sQuery(id+"FQ5JFwxVdaqARUP_1.wireOp",EDGE,"fcba4419-a2ee-464f-be9d-58f11bf3418b.sketch_text.stroke-93"),sQuery(id+"FQ5JFwxVdaqARUP_1.wireOp",EDGE,"fcba4419-a2ee-464f-be9d-58f11bf3418b.sketch_text.stroke-94"),sQuery(id+"FQ5JFwxVdaqARUP_1.wireOp",EDGE,"fcba4419-a2ee-464f-be9d-58f11bf3418b.sketch_text.stroke-95"),sQuery(id+"FQ5JFwxVdaqARUP_1.wireOp",EDGE,"fcba4419-a2ee-464f-be9d-58f11bf3418b.sketch_text.stroke-96"),sQuery(id+"FQ5JFwxVdaqARUP_1.wireOp",EDGE,"fcba4419-a2ee-464f-be9d-58f11bf3418b.sketch_text.stroke-97"),sQuery(id+"FQ5JFwxVdaqARUP_1.wireOp",EDGE,"fcba4419-a2ee-464f-be9d-58f11bf3418b.sketch_text.stroke-98"),sQuery(id+"FQ5JFwxVdaqARUP_1.wireOp",EDGE,"fcba4419-a2ee-464f-be9d-58f11bf3418b.sketch_text.stroke-99"),sQuery(id+"FQ5JFwxVdaqARUP_1.wireOp",EDGE,"fcba4419-a2ee-464f-be9d-58f11bf3418b.sketch_text.stroke-100"),sQuery(id+"FQ5JFwxVdaqARUP_1.wireOp",EDGE,"fcba4419-a2ee-464f-be9d-58f11bf3418b.sketch_text.stroke-101"),sQuery(id+"FQ5JFwxVdaqARUP_1.wireOp",EDGE,"fcba4419-a2ee-464f-be9d-58f11bf3418b.sketch_text.stroke-102"),sQuery(id+"FQ5JFwxVdaqARUP_1.wireOp",EDGE,"fcba4419-a2ee-464f-be9d-58f11bf3418b.sketch_text.stroke-103"),sQuery(id+"FQ5JFwxVdaqARUP_1.wireOp",EDGE,"fcba4419-a2ee-464f-be9d-58f11bf3418b.sketch_text.stroke-104"),sQuery(id+"FQ5JFwxVdaqARUP_1.wireOp",EDGE,"fcba4419-a2ee-464f-be9d-58f11bf3418b.sketch_text.stroke-105"),sQuery(id+"FQ5JFwxVdaqARUP_1.wireOp",EDGE,"fcba4419-a2ee-464f-be9d-58f11bf3418b.sketch_text.stroke-106"),sQuery(id+"FQ5JFwxVdaqARUP_1.wireOp",EDGE,"fcba4419-a2ee-464f-be9d-58f11bf3418b.sketch_text.stroke-107"),sQuery(id+"FQ5JFwxVdaqARUP_1.wireOp",EDGE,"fcba4419-a2ee-464f-be9d-58f11bf3418b.sketch_text.stroke-108"),sQuery(id+"FQ5JFwxVdaqARUP_1.wireOp",EDGE,"fcba4419-a2ee-464f-be9d-58f11bf3418b.sketch_text.stroke-109"),sQuery(id+"FQ5JFwxVdaqARUP_1.wireOp",EDGE,"fcba4419-a2ee-464f-be9d-58f11bf3418b.sketch_text.stroke-110"),sQuery(id+"FQ5JFwxVdaqARUP_1.wireOp",EDGE,"fcba4419-a2ee-464f-be9d-58f11bf3418b.sketch_text.stroke-111"),sQuery(id+"FQ5JFwxVdaqARUP_1.wireOp",EDGE,"fcba4419-a2ee-464f-be9d-58f11bf3418b.sketch_text.stroke-112"),sQuery(id+"FQ5JFwxVdaqARUP_1.wireOp",EDGE,"fcba4419-a2ee-464f-be9d-58f11bf3418b.sketch_text.stroke-113"),sQuery(id+"FQ5JFwxVdaqARUP_1.wireOp",EDGE,"fcba4419-a2ee-464f-be9d-58f11bf3418b.sketch_text.stroke-114"),sQuery(id+"FQ5JFwxVdaqARUP_1.wireOp",EDGE,"fcba4419-a2ee-464f-be9d-58f11bf3418b.sketch_text.stroke-115"),sQuery(id+"FQ5JFwxVdaqARUP_1.wireOp",EDGE,"fcba4419-a2ee-464f-be9d-58f11bf3418b.sketch_text.stroke-116"),sQuery(id+"FQ5JFwxVdaqARUP_1.wireOp",EDGE,"fcba4419-a2ee-464f-be9d-58f11bf3418b.sketch_text.stroke-117"),sQuery(id+"FQ5JFwxVdaqARUP_1.wireOp",EDGE,"fcba4419-a2ee-464f-be9d-58f11bf3418b.sketch_text.stroke-118"),sQuery(id+"FQ5JFwxVdaqARUP_1.wireOp",EDGE,"fcba4419-a2ee-464f-be9d-58f11bf3418b.sketch_text.stroke-119"),sQuery(id+"FQ5JFwxVdaqARUP_1.wireOp",EDGE,"fcba4419-a2ee-464f-be9d-58f11bf3418b.sketch_text.stroke-120"),sQuery(id+"FQ5JFwxVdaqARUP_1.wireOp",EDGE,"fcba4419-a2ee-464f-be9d-58f11bf3418b.sketch_text.stroke-121"),sQuery(id+"FQ5JFwxVdaqARUP_1.wireOp",EDGE,"fcba4419-a2ee-464f-be9d-58f11bf3418b.sketch_text.stroke-122"),sQuery(id+"FQ5JFwxVdaqARUP_1.wireOp",EDGE,"fcba4419-a2ee-464f-be9d-58f11bf3418b.sketch_text.stroke-123"),sQuery(id+"FQ5JFwxVdaqARUP_1.wireOp",EDGE,"fcba4419-a2ee-464f-be9d-58f11bf3418b.sketch_text.stroke-124"),sQuery(id+"FQ5JFwxVdaqARUP_1.wireOp",EDGE,"fcba4419-a2ee-464f-be9d-58f11bf3418b.sketch_text.stroke-125"),sQuery(id+"FQ5JFwxVdaqARUP_1.wireOp",EDGE,"fcba4419-a2ee-464f-be9d-58f11bf3418b.sketch_text.stroke-126"),sQuery(id+"FQ5JFwxVdaqARUP_1.wireOp",EDGE,"fcba4419-a2ee-464f-be9d-58f11bf3418b.sketch_text.stroke-127"),sQuery(id+"FQ5JFwxVdaqARUP_1.wireOp",EDGE,"fcba4419-a2ee-464f-be9d-58f11bf3418b.sketch_text.stroke-128"),sQuery(id+"FQ5JFwxVdaqARUP_1.wireOp",EDGE,"fcba4419-a2ee-464f-be9d-58f11bf3418b.sketch_text.stroke-129"),sQuery(id+"FQ5JFwxVdaqARUP_1.wireOp",EDGE,"fcba4419-a2ee-464f-be9d-58f11bf3418b.sketch_text.stroke-130"),sQuery(id+"FQ5JFwxVdaqARUP_1.wireOp",EDGE,"fcba4419-a2ee-464f-be9d-58f11bf3418b.sketch_text.stroke-131"),sQuery(id+"FQ5JFwxVdaqARUP_1.wireOp",EDGE,"fcba4419-a2ee-464f-be9d-58f11bf3418b.sketch_text.stroke-132"),sQuery(id+"FQ5JFwxVdaqARUP_1.wireOp",EDGE,"fcba4419-a2ee-464f-be9d-58f11bf3418b.sketch_text.stroke-133"),sQuery(id+"FQ5JFwxVdaqARUP_1.wireOp",EDGE,"fcba4419-a2ee-464f-be9d-58f11bf3418b.sketch_text.stroke-134"),sQuery(id+"FQ5JFwxVdaqARUP_1.wireOp",EDGE,"fcba4419-a2ee-464f-be9d-58f11bf3418b.sketch_text.stroke-135"),sQuery(id+"FQ5JFwxVdaqARUP_1.wireOp",EDGE,"fcba4419-a2ee-464f-be9d-58f11bf3418b.sketch_text.stroke-136"),sQuery(id+"FQ5JFwxVdaqARUP_1.wireOp",EDGE,"fcba4419-a2ee-464f-be9d-58f11bf3418b.sketch_text.stroke-137"),sQuery(id+"FQ5JFwxVdaqARUP_1.wireOp",EDGE,"fcba4419-a2ee-464f-be9d-58f11bf3418b.sketch_text.stroke-138"),sQuery(id+"FQ5JFwxVdaqARUP_1.wireOp",EDGE,"fcba4419-a2ee-464f-be9d-58f11bf3418b.sketch_text.stroke-139"),sQuery(id+"FQ5JFwxVdaqARUP_1.wireOp",EDGE,"fcba4419-a2ee-464f-be9d-58f11bf3418b.sketch_text.stroke-140"),sQuery(id+"FQ5JFwxVdaqARUP_1.wireOp",EDGE,"fcba4419-a2ee-464f-be9d-58f11bf3418b.sketch_text.stroke-141"),sQuery(id+"FQ5JFwxVdaqARUP_1.wireOp",EDGE,"fcba4419-a2ee-464f-be9d-58f11bf3418b.sketch_text.stroke-142"),sQuery(id+"FQ5JFwxVdaqARUP_1.wireOp",EDGE,"fcba4419-a2ee-464f-be9d-58f11bf3418b.sketch_text.stroke-143"),sQuery(id+"FQ5JFwxVdaqARUP_1.wireOp",EDGE,"fcba4419-a2ee-464f-be9d-58f11bf3418b.sketch_text.stroke-144"),sQuery(id+"FQ5JFwxVdaqARUP_1.wireOp",EDGE,"fcba4419-a2ee-464f-be9d-58f11bf3418b.sketch_text.stroke-145"),sQuery(id+"FQ5JFwxVdaqARUP_1.wireOp",EDGE,"fcba4419-a2ee-464f-be9d-58f11bf3418b.sketch_text.stroke-146"),sQuery(id+"FQ5JFwxVdaqARUP_1.wireOp",EDGE,"fcba4419-a2ee-464f-be9d-58f11bf3418b.sketch_text.stroke-147"),sQuery(id+"FQ5JFwxVdaqARUP_1.wireOp",EDGE,"fcba4419-a2ee-464f-be9d-58f11bf3418b.sketch_text.stroke-148"),sQuery(id+"FQ5JFwxVdaqARUP_1.wireOp",EDGE,"fcba4419-a2ee-464f-be9d-58f11bf3418b.sketch_text.stroke-149"),sQuery(id+"FQ5JFwxVdaqARUP_1.wireOp",EDGE,"fcba4419-a2ee-464f-be9d-58f11bf3418b.sketch_text.stroke-150"),sQuery(id+"FQ5JFwxVdaqARUP_1.wireOp",EDGE,"fcba4419-a2ee-464f-be9d-58f11bf3418b.sketch_text.stroke-151"),sQuery(id+"FQ5JFwxVdaqARUP_1.wireOp",EDGE,"fcba4419-a2ee-464f-be9d-58f11bf3418b.sketch_text.stroke-152"),sQuery(id+"FQ5JFwxVdaqARUP_1.wireOp",EDGE,"fcba4419-a2ee-464f-be9d-58f11bf3418b.sketch_text.stroke-153"),sQuery(id+"FQ5JFwxVdaqARUP_1.wireOp",EDGE,"fcba4419-a2ee-464f-be9d-58f11bf3418b.sketch_text.stroke-154"),sQuery(id+"FQ5JFwxVdaqARUP_1.wireOp",EDGE,"fcba4419-a2ee-464f-be9d-58f11bf3418b.sketch_text.stroke-155"),sQuery(id+"FQ5JFwxVdaqARUP_1.wireOp",EDGE,"fcba4419-a2ee-464f-be9d-58f11bf3418b.sketch_text.stroke-156"),sQuery(id+"FQ5JFwxVdaqARUP_1.wireOp",EDGE,"fcba4419-a2ee-464f-be9d-58f11bf3418b.sketch_text.stroke-157"),sQuery(id+"FQ5JFwxVdaqARUP_1.wireOp",EDGE,"fcba4419-a2ee-464f-be9d-58f11bf3418b.sketch_text.stroke-158"),sQuery(id+"FQ5JFwxVdaqARUP_1.wireOp",EDGE,"fcba4419-a2ee-464f-be9d-58f11bf3418b.sketch_text.stroke-159"),sQuery(id+"FQ5JFwxVdaqARUP_1.wireOp",EDGE,"fcba4419-a2ee-464f-be9d-58f11bf3418b.sketch_text.stroke-160"),sQuery(id+"FQ5JFwxVdaqARUP_1.wireOp",EDGE,"fcba4419-a2ee-464f-be9d-58f11bf3418b.sketch_text.stroke-161"),sQuery(id+"FQ5JFwxVdaqARUP_1.wireOp",EDGE,"fcba4419-a2ee-464f-be9d-58f11bf3418b.sketch_text.stroke-162"),sQuery(id+"FQ5JFwxVdaqARUP_1.wireOp",EDGE,"fcba4419-a2ee-464f-be9d-58f11bf3418b.sketch_text.stroke-163"),sQuery(id+"FQ5JFwxVdaqARUP_1.wireOp",EDGE,"fcba4419-a2ee-464f-be9d-58f11bf3418b.sketch_text.stroke-164"),sQuery(id+"FQ5JFwxVdaqARUP_1.wireOp",EDGE,"fcba4419-a2ee-464f-be9d-58f11bf3418b.sketch_text.stroke-165"),sQuery(id+"FQ5JFwxVdaqARUP_1.wireOp",EDGE,"fcba4419-a2ee-464f-be9d-58f11bf3418b.sketch_text.stroke-166"),sQuery(id+"FQ5JFwxVdaqARUP_1.wireOp",EDGE,"fcba4419-a2ee-464f-be9d-58f11bf3418b.sketch_text.stroke-167"),sQuery(id+"FQ5JFwxVdaqARUP_1.wireOp",EDGE,"fcba4419-a2ee-464f-be9d-58f11bf3418b.sketch_text.stroke-168"),sQuery(id+"FQ5JFwxVdaqARUP_1.wireOp",EDGE,"fcba4419-a2ee-464f-be9d-58f11bf3418b.sketch_text.stroke-169"),sQuery(id+"FQ5JFwxVdaqARUP_1.wireOp",EDGE,"fcba4419-a2ee-464f-be9d-58f11bf3418b.sketch_text.stroke-170"),sQuery(id+"FQ5JFwxVdaqARUP_1.wireOp",EDGE,"fcba4419-a2ee-464f-be9d-58f11bf3418b.sketch_text.stroke-171"),sQuery(id+"FQ5JFwxVdaqARUP_1.wireOp",EDGE,"fcba4419-a2ee-464f-be9d-58f11bf3418b.sketch_text.stroke-172"),sQuery(id+"FQ5JFwxVdaqARUP_1.wireOp",EDGE,"fcba4419-a2ee-464f-be9d-58f11bf3418b.sketch_text.stroke-173"),sQuery(id+"FHMxAyK4CFUKdhS_1.wireOp",EDGE,"1cb9c079-ea9b-4899-8069-e0e3048e911d.sketch_text.stroke-0"),sQuery(id+"FHMxAyK4CFUKdhS_1.wireOp",EDGE,"1cb9c079-ea9b-4899-8069-e0e3048e911d.sketch_text.stroke-1"),sQuery(id+"FHMxAyK4CFUKdhS_1.wireOp",EDGE,"1cb9c079-ea9b-4899-8069-e0e3048e911d.sketch_text.stroke-2"),sQuery(id+"FHMxAyK4CFUKdhS_1.wireOp",EDGE,"1cb9c079-ea9b-4899-8069-e0e3048e911d.sketch_text.stroke-3"),sQuery(id+"FHMxAyK4CFUKdhS_1.wireOp",EDGE,"1cb9c079-ea9b-4899-8069-e0e3048e911d.sketch_text.stroke-4"),sQuery(id+"FHMxAyK4CFUKdhS_1.wireOp",EDGE,"1cb9c079-ea9b-4899-8069-e0e3048e911d.sketch_text.stroke-5"),sQuery(id+"FHMxAyK4CFUKdhS_1.wireOp",EDGE,"1cb9c079-ea9b-4899-8069-e0e3048e911d.sketch_text.stroke-6"),sQuery(id+"FHMxAyK4CFUKdhS_1.wireOp",EDGE,"1cb9c079-ea9b-4899-8069-e0e3048e911d.sketch_text.stroke-7"),sQuery(id+"FHMxAyK4CFUKdhS_1.wireOp",EDGE,"1cb9c079-ea9b-4899-8069-e0e3048e911d.sketch_text.stroke-8"),sQuery(id+"FHMxAyK4CFUKdhS_1.wireOp",EDGE,"1cb9c079-ea9b-4899-8069-e0e3048e911d.sketch_text.stroke-9"),sQuery(id+"FHMxAyK4CFUKdhS_1.wireOp",EDGE,"1cb9c079-ea9b-4899-8069-e0e3048e911d.sketch_text.stroke-10"),sQuery(id+"FHMxAyK4CFUKdhS_1.wireOp",EDGE,"1cb9c079-ea9b-4899-8069-e0e3048e911d.sketch_text.stroke-11"),sQuery(id+"FHMxAyK4CFUKdhS_1.wireOp",EDGE,"1cb9c079-ea9b-4899-8069-e0e3048e911d.sketch_text.stroke-12"),sQuery(id+"FHMxAyK4CFUKdhS_1.wireOp",EDGE,"1cb9c079-ea9b-4899-8069-e0e3048e911d.sketch_text.stroke-13"),sQuery(id+"FHMxAyK4CFUKdhS_1.wireOp",EDGE,"1cb9c079-ea9b-4899-8069-e0e3048e911d.sketch_text.stroke-14"),sQuery(id+"FHMxAyK4CFUKdhS_1.wireOp",EDGE,"1cb9c079-ea9b-4899-8069-e0e3048e911d.sketch_text.stroke-15"),sQuery(id+"FHMxAyK4CFUKdhS_1.wireOp",EDGE,"1cb9c079-ea9b-4899-8069-e0e3048e911d.sketch_text.stroke-16"),sQuery(id+"FHMxAyK4CFUKdhS_1.wireOp",EDGE,"1cb9c079-ea9b-4899-8069-e0e3048e911d.sketch_text.stroke-17"),sQuery(id+"FHMxAyK4CFUKdhS_1.wireOp",EDGE,"1cb9c079-ea9b-4899-8069-e0e3048e911d.sketch_text.stroke-18"),sQuery(id+"FHMxAyK4CFUKdhS_1.wireOp",EDGE,"1cb9c079-ea9b-4899-8069-e0e3048e911d.sketch_text.stroke-19"),sQuery(id+"FHMxAyK4CFUKdhS_1.wireOp",EDGE,"1cb9c079-ea9b-4899-8069-e0e3048e911d.sketch_text.stroke-20"),sQuery(id+"FHMxAyK4CFUKdhS_1.wireOp",EDGE,"1cb9c079-ea9b-4899-8069-e0e3048e911d.sketch_text.stroke-21"),sQuery(id+"FHMxAyK4CFUKdhS_1.wireOp",EDGE,"1cb9c079-ea9b-4899-8069-e0e3048e911d.sketch_text.stroke-22"),sQuery(id+"FHMxAyK4CFUKdhS_1.wireOp",EDGE,"1cb9c079-ea9b-4899-8069-e0e3048e911d.sketch_text.stroke-23"),sQuery(id+"FHMxAyK4CFUKdhS_1.wireOp",EDGE,"1cb9c079-ea9b-4899-8069-e0e3048e911d.sketch_text.stroke-24"),sQuery(id+"FHMxAyK4CFUKdhS_1.wireOp",EDGE,"1cb9c079-ea9b-4899-8069-e0e3048e911d.sketch_text.stroke-25"),sQuery(id+"FHMxAyK4CFUKdhS_1.wireOp",EDGE,"1cb9c079-ea9b-4899-8069-e0e3048e911d.sketch_text.stroke-26"),sQuery(id+"FHMxAyK4CFUKdhS_1.wireOp",EDGE,"1cb9c079-ea9b-4899-8069-e0e3048e911d.sketch_text.stroke-27"),sQuery(id+"FHMxAyK4CFUKdhS_1.wireOp",EDGE,"1cb9c079-ea9b-4899-8069-e0e3048e911d.sketch_text.stroke-28"),sQuery(id+"FHMxAyK4CFUKdhS_1.wireOp",EDGE,"1cb9c079-ea9b-4899-8069-e0e3048e911d.sketch_text.stroke-29"),sQuery(id+"FHMxAyK4CFUKdhS_1.wireOp",EDGE,"1cb9c079-ea9b-4899-8069-e0e3048e911d.sketch_text.stroke-30"),sQuery(id+"FHMxAyK4CFUKdhS_1.wireOp",EDGE,"1cb9c079-ea9b-4899-8069-e0e3048e911d.sketch_text.stroke-31"),sQuery(id+"FHMxAyK4CFUKdhS_1.wireOp",EDGE,"1cb9c079-ea9b-4899-8069-e0e3048e911d.sketch_text.stroke-32"),sQuery(id+"FHMxAyK4CFUKdhS_1.wireOp",EDGE,"1cb9c079-ea9b-4899-8069-e0e3048e911d.sketch_text.stroke-33"),sQuery(id+"FHMxAyK4CFUKdhS_1.wireOp",EDGE,"1cb9c079-ea9b-4899-8069-e0e3048e911d.sketch_text.stroke-34"),sQuery(id+"FHMxAyK4CFUKdhS_1.wireOp",EDGE,"1cb9c079-ea9b-4899-8069-e0e3048e911d.sketch_text.stroke-35"),sQuery(id+"FHMxAyK4CFUKdhS_1.wireOp",EDGE,"1cb9c079-ea9b-4899-8069-e0e3048e911d.sketch_text.stroke-36"),sQuery(id+"FHMxAyK4CFUKdhS_1.wireOp",EDGE,"1cb9c079-ea9b-4899-8069-e0e3048e911d.sketch_text.stroke-37"),sQuery(id+"FHMxAyK4CFUKdhS_1.wireOp",EDGE,"1cb9c079-ea9b-4899-8069-e0e3048e911d.sketch_text.stroke-38"),sQuery(id+"FHMxAyK4CFUKdhS_1.wireOp",EDGE,"1cb9c079-ea9b-4899-8069-e0e3048e911d.sketch_text.stroke-39"),sQuery(id+"FHMxAyK4CFUKdhS_1.wireOp",EDGE,"1cb9c079-ea9b-4899-8069-e0e3048e911d.sketch_text.stroke-40"),sQuery(id+"FHMxAyK4CFUKdhS_1.wireOp",EDGE,"1cb9c079-ea9b-4899-8069-e0e3048e911d.sketch_text.stroke-41"),sQuery(id+"FHMxAyK4CFUKdhS_1.wireOp",EDGE,"1cb9c079-ea9b-4899-8069-e0e3048e911d.sketch_text.stroke-42"),sQuery(id+"FHMxAyK4CFUKdhS_1.wireOp",EDGE,"1cb9c079-ea9b-4899-8069-e0e3048e911d.sketch_text.stroke-43"),sQuery(id+"FHMxAyK4CFUKdhS_1.wireOp",EDGE,"1cb9c079-ea9b-4899-8069-e0e3048e911d.sketch_text.stroke-44"),sQuery(id+"FHMxAyK4CFUKdhS_1.wireOp",EDGE,"1cb9c079-ea9b-4899-8069-e0e3048e911d.sketch_text.stroke-45"),sQuery(id+"FHMxAyK4CFUKdhS_1.wireOp",EDGE,"1cb9c079-ea9b-4899-8069-e0e3048e911d.sketch_text.stroke-46"),sQuery(id+"FHMxAyK4CFUKdhS_1.wireOp",EDGE,"1cb9c079-ea9b-4899-8069-e0e3048e911d.sketch_text.stroke-47"),sQuery(id+"FHMxAyK4CFUKdhS_1.wireOp",EDGE,"1cb9c079-ea9b-4899-8069-e0e3048e911d.sketch_text.stroke-48"),sQuery(id+"FHMxAyK4CFUKdhS_1.wireOp",EDGE,"1cb9c079-ea9b-4899-8069-e0e3048e911d.sketch_text.stroke-49"),sQuery(id+"FHMxAyK4CFUKdhS_1.wireOp",EDGE,"1cb9c079-ea9b-4899-8069-e0e3048e911d.sketch_text.stroke-50"),sQuery(id+"FHMxAyK4CFUKdhS_1.wireOp",EDGE,"1cb9c079-ea9b-4899-8069-e0e3048e911d.sketch_text.stroke-51"),sQuery(id+"FHMxAyK4CFUKdhS_1.wireOp",EDGE,"1cb9c079-ea9b-4899-8069-e0e3048e911d.sketch_text.stroke-52"),sQuery(id+"FHMxAyK4CFUKdhS_1.wireOp",EDGE,"1cb9c079-ea9b-4899-8069-e0e3048e911d.sketch_text.stroke-53"),sQuery(id+"FHMxAyK4CFUKdhS_1.wireOp",EDGE,"1cb9c079-ea9b-4899-8069-e0e3048e911d.sketch_text.stroke-54"),sQuery(id+"FHMxAyK4CFUKdhS_1.wireOp",EDGE,"1cb9c079-ea9b-4899-8069-e0e3048e911d.sketch_text.stroke-55"),sQuery(id+"FHMxAyK4CFUKdhS_1.wireOp",EDGE,"1cb9c079-ea9b-4899-8069-e0e3048e911d.sketch_text.stroke-56"),sQuery(id+"FHMxAyK4CFUKdhS_1.wireOp",EDGE,"1cb9c079-ea9b-4899-8069-e0e3048e911d.sketch_text.stroke-57"),sQuery(id+"FHMxAyK4CFUKdhS_1.wireOp",EDGE,"1cb9c079-ea9b-4899-8069-e0e3048e911d.sketch_text.stroke-58"),sQuery(id+"FHMxAyK4CFUKdhS_1.wireOp",EDGE,"1cb9c079-ea9b-4899-8069-e0e3048e911d.sketch_text.stroke-59"),sQuery(id+"FHMxAyK4CFUKdhS_1.wireOp",EDGE,"1cb9c079-ea9b-4899-8069-e0e3048e911d.sketch_text.stroke-60"),sQuery(id+"FHMxAyK4CFUKdhS_1.wireOp",EDGE,"1cb9c079-ea9b-4899-8069-e0e3048e911d.sketch_text.stroke-61"),sQuery(id+"FHMxAyK4CFUKdhS_1.wireOp",EDGE,"1cb9c079-ea9b-4899-8069-e0e3048e911d.sketch_text.stroke-62"),sQuery(id+"FHMxAyK4CFUKdhS_1.wireOp",EDGE,"1cb9c079-ea9b-4899-8069-e0e3048e911d.sketch_text.stroke-71"),sQuery(id+"FHMxAyK4CFUKdhS_1.wireOp",EDGE,"1cb9c079-ea9b-4899-8069-e0e3048e911d.sketch_text.stroke-72"),sQuery(id+"FHMxAyK4CFUKdhS_1.wireOp",EDGE,"1cb9c079-ea9b-4899-8069-e0e3048e911d.sketch_text.stroke-73"),sQuery(id+"FHMxAyK4CFUKdhS_1.wireOp",EDGE,"1cb9c079-ea9b-4899-8069-e0e3048e911d.sketch_text.stroke-74"),sQuery(id+"FHMxAyK4CFUKdhS_1.wireOp",EDGE,"1cb9c079-ea9b-4899-8069-e0e3048e911d.sketch_text.stroke-75"),sQuery(id+"FHMxAyK4CFUKdhS_1.wireOp",EDGE,"1cb9c079-ea9b-4899-8069-e0e3048e911d.sketch_text.stroke-76"),sQuery(id+"FHMxAyK4CFUKdhS_1.wireOp",EDGE,"1cb9c079-ea9b-4899-8069-e0e3048e911d.sketch_text.stroke-77"),sQuery(id+"FHMxAyK4CFUKdhS_1.wireOp",EDGE,"1cb9c079-ea9b-4899-8069-e0e3048e911d.sketch_text.stroke-78"),sQuery(id+"FHMxAyK4CFUKdhS_1.wireOp",EDGE,"1cb9c079-ea9b-4899-8069-e0e3048e911d.sketch_text.stroke-79"),sQuery(id+"FHMxAyK4CFUKdhS_1.wireOp",EDGE,"1cb9c079-ea9b-4899-8069-e0e3048e911d.sketch_text.stroke-80"),sQuery(id+"FHMxAyK4CFUKdhS_1.wireOp",EDGE,"1cb9c079-ea9b-4899-8069-e0e3048e911d.sketch_text.stroke-81"),sQuery(id+"FHMxAyK4CFUKdhS_1.wireOp",EDGE,"1cb9c079-ea9b-4899-8069-e0e3048e911d.sketch_text.stroke-82"),sQuery(id+"FHMxAyK4CFUKdhS_1.wireOp",EDGE,"1cb9c079-ea9b-4899-8069-e0e3048e911d.sketch_text.stroke-83"),sQuery(id+"FHMxAyK4CFUKdhS_1.wireOp",EDGE,"1cb9c079-ea9b-4899-8069-e0e3048e911d.sketch_text.stroke-84"),sQuery(id+"FHMxAyK4CFUKdhS_1.wireOp",EDGE,"1cb9c079-ea9b-4899-8069-e0e3048e911d.sketch_text.stroke-85"),sQuery(id+"FHMxAyK4CFUKdhS_1.wireOp",EDGE,"1cb9c079-ea9b-4899-8069-e0e3048e911d.sketch_text.stroke-86"),sQuery(id+"FHMxAyK4CFUKdhS_1.wireOp",EDGE,"1cb9c079-ea9b-4899-8069-e0e3048e911d.sketch_text.stroke-87"),sQuery(id+"FHMxAyK4CFUKdhS_1.wireOp",EDGE,"1cb9c079-ea9b-4899-8069-e0e3048e911d.sketch_text.stroke-88"),sQuery(id+"FHMxAyK4CFUKdhS_1.wireOp",EDGE,"1cb9c079-ea9b-4899-8069-e0e3048e911d.sketch_text.stroke-89"),sQuery(id+"FHMxAyK4CFUKdhS_1.wireOp",EDGE,"1cb9c079-ea9b-4899-8069-e0e3048e911d.sketch_text.stroke-90"),sQuery(id+"FHMxAyK4CFUKdhS_1.wireOp",EDGE,"1cb9c079-ea9b-4899-8069-e0e3048e911d.sketch_text.stroke-91"),sQuery(id+"FHMxAyK4CFUKdhS_1.wireOp",EDGE,"1cb9c079-ea9b-4899-8069-e0e3048e911d.sketch_text.stroke-92"),sQuery(id+"FHMxAyK4CFUKdhS_1.wireOp",EDGE,"1cb9c079-ea9b-4899-8069-e0e3048e911d.sketch_text.stroke-93"),sQuery(id+"FHMxAyK4CFUKdhS_1.wireOp",EDGE,"1cb9c079-ea9b-4899-8069-e0e3048e911d.sketch_text.stroke-94"),sQuery(id+"FHMxAyK4CFUKdhS_1.wireOp",EDGE,"1cb9c079-ea9b-4899-8069-e0e3048e911d.sketch_text.stroke-95"),sQuery(id+"FHMxAyK4CFUKdhS_1.wireOp",EDGE,"1cb9c079-ea9b-4899-8069-e0e3048e911d.sketch_text.stroke-96"),sQuery(id+"FHMxAyK4CFUKdhS_1.wireOp",EDGE,"1cb9c079-ea9b-4899-8069-e0e3048e911d.sketch_text.stroke-97"),sQuery(id+"FHMxAyK4CFUKdhS_1.wireOp",EDGE,"1cb9c079-ea9b-4899-8069-e0e3048e911d.sketch_text.stroke-103"),sQuery(id+"FHMxAyK4CFUKdhS_1.wireOp",EDGE,"1cb9c079-ea9b-4899-8069-e0e3048e911d.sketch_text.stroke-104"),sQuery(id+"FHMxAyK4CFUKdhS_1.wireOp",EDGE,"1cb9c079-ea9b-4899-8069-e0e3048e911d.sketch_text.stroke-105"),sQuery(id+"FHMxAyK4CFUKdhS_1.wireOp",EDGE,"1cb9c079-ea9b-4899-8069-e0e3048e911d.sketch_text.stroke-106"),sQuery(id+"FHMxAyK4CFUKdhS_1.wireOp",EDGE,"1cb9c079-ea9b-4899-8069-e0e3048e911d.sketch_text.stroke-107"),sQuery(id+"FHMxAyK4CFUKdhS_1.wireOp",EDGE,"1cb9c079-ea9b-4899-8069-e0e3048e911d.sketch_text.stroke-108"),sQuery(id+"FHMxAyK4CFUKdhS_1.wireOp",EDGE,"1cb9c079-ea9b-4899-8069-e0e3048e911d.sketch_text.stroke-109"),sQuery(id+"FHMxAyK4CFUKdhS_1.wireOp",EDGE,"1cb9c079-ea9b-4899-8069-e0e3048e911d.sketch_text.stroke-110"),sQuery(id+"FHMxAyK4CFUKdhS_1.wireOp",EDGE,"1cb9c079-ea9b-4899-8069-e0e3048e911d.sketch_text.stroke-111"),sQuery(id+"FHMxAyK4CFUKdhS_1.wireOp",EDGE,"1cb9c079-ea9b-4899-8069-e0e3048e911d.sketch_text.stroke-112"),sQuery(id+"FHMxAyK4CFUKdhS_1.wireOp",EDGE,"1cb9c079-ea9b-4899-8069-e0e3048e911d.sketch_text.stroke-113"),sQuery(id+"FHMxAyK4CFUKdhS_1.wireOp",EDGE,"1cb9c079-ea9b-4899-8069-e0e3048e911d.sketch_text.stroke-114"),sQuery(id+"FHMxAyK4CFUKdhS_1.wireOp",EDGE,"1cb9c079-ea9b-4899-8069-e0e3048e911d.sketch_text.stroke-115"),sQuery(id+"FHMxAyK4CFUKdhS_1.wireOp",EDGE,"1cb9c079-ea9b-4899-8069-e0e3048e911d.sketch_text.stroke-116"),sQuery(id+"FHMxAyK4CFUKdhS_1.wireOp",EDGE,"1cb9c079-ea9b-4899-8069-e0e3048e911d.sketch_text.stroke-117"),sQuery(id+"FHMxAyK4CFUKdhS_1.wireOp",EDGE,"1cb9c079-ea9b-4899-8069-e0e3048e911d.sketch_text.stroke-118"),sQuery(id+"FHMxAyK4CFUKdhS_1.wireOp",EDGE,"1cb9c079-ea9b-4899-8069-e0e3048e911d.sketch_text.stroke-119"),sQuery(id+"FHMxAyK4CFUKdhS_1.wireOp",EDGE,"1cb9c079-ea9b-4899-8069-e0e3048e911d.sketch_text.stroke-120"),sQuery(id+"FHMxAyK4CFUKdhS_1.wireOp",EDGE,"1cb9c079-ea9b-4899-8069-e0e3048e911d.sketch_text.stroke-121"),sQuery(id+"FHMxAyK4CFUKdhS_1.wireOp",EDGE,"1cb9c079-ea9b-4899-8069-e0e3048e911d.sketch_text.stroke-122"),sQuery(id+"FHMxAyK4CFUKdhS_1.wireOp",EDGE,"1cb9c079-ea9b-4899-8069-e0e3048e911d.sketch_text.stroke-123"),sQuery(id+"FHMxAyK4CFUKdhS_1.wireOp",EDGE,"1cb9c079-ea9b-4899-8069-e0e3048e911d.sketch_text.stroke-124"),sQuery(id+"FHMxAyK4CFUKdhS_1.wireOp",EDGE,"1cb9c079-ea9b-4899-8069-e0e3048e911d.sketch_text.stroke-125"),sQuery(id+"FHMxAyK4CFUKdhS_1.wireOp",EDGE,"1cb9c079-ea9b-4899-8069-e0e3048e911d.sketch_text.stroke-126"),sQuery(id+"FHMxAyK4CFUKdhS_1.wireOp",EDGE,"1cb9c079-ea9b-4899-8069-e0e3048e911d.sketch_text.stroke-127"),sQuery(id+"FHMxAyK4CFUKdhS_1.wireOp",EDGE,"1cb9c079-ea9b-4899-8069-e0e3048e911d.sketch_text.stroke-128"),sQuery(id+"FHMxAyK4CFUKdhS_1.wireOp",EDGE,"1cb9c079-ea9b-4899-8069-e0e3048e911d.sketch_text.stroke-129"),sQuery(id+"FHMxAyK4CFUKdhS_1.wireOp",EDGE,"1cb9c079-ea9b-4899-8069-e0e3048e911d.sketch_text.stroke-130"),sQuery(id+"FHMxAyK4CFUKdhS_1.wireOp",EDGE,"1cb9c079-ea9b-4899-8069-e0e3048e911d.sketch_text.stroke-131"),sQuery(id+"FHMxAyK4CFUKdhS_1.wireOp",EDGE,"1cb9c079-ea9b-4899-8069-e0e3048e911d.sketch_text.stroke-132"),sQuery(id+"FHMxAyK4CFUKdhS_1.wireOp",EDGE,"1cb9c079-ea9b-4899-8069-e0e3048e911d.sketch_text.stroke-133"),sQuery(id+"FHMxAyK4CFUKdhS_1.wireOp",EDGE,"1cb9c079-ea9b-4899-8069-e0e3048e911d.sketch_text.stroke-134"),sQuery(id+"FHMxAyK4CFUKdhS_1.wireOp",EDGE,"1cb9c079-ea9b-4899-8069-e0e3048e911d.sketch_text.stroke-135"),sQuery(id+"FHMxAyK4CFUKdhS_1.wireOp",EDGE,"1cb9c079-ea9b-4899-8069-e0e3048e911d.sketch_text.stroke-136"),sQuery(id+"FHMxAyK4CFUKdhS_1.wireOp",EDGE,"1cb9c079-ea9b-4899-8069-e0e3048e911d.sketch_text.stroke-137"),sQuery(id+"FHMxAyK4CFUKdhS_1.wireOp",EDGE,"1cb9c079-ea9b-4899-8069-e0e3048e911d.sketch_text.stroke-138"),sQuery(id+"FHMxAyK4CFUKdhS_1.wireOp",EDGE,"1cb9c079-ea9b-4899-8069-e0e3048e911d.sketch_text.stroke-139"),sQuery(id+"FHMxAyK4CFUKdhS_1.wireOp",EDGE,"1cb9c079-ea9b-4899-8069-e0e3048e911d.sketch_text.stroke-140"),sQuery(id+"FHMxAyK4CFUKdhS_1.wireOp",EDGE,"1cb9c079-ea9b-4899-8069-e0e3048e911d.sketch_text.stroke-141"),sQuery(id+"FHMxAyK4CFUKdhS_1.wireOp",EDGE,"1cb9c079-ea9b-4899-8069-e0e3048e911d.sketch_text.stroke-142"),sQuery(id+"FHMxAyK4CFUKdhS_1.wireOp",EDGE,"1cb9c079-ea9b-4899-8069-e0e3048e911d.sketch_text.stroke-143"),sQuery(id+"FHMxAyK4CFUKdhS_1.wireOp",EDGE,"1cb9c079-ea9b-4899-8069-e0e3048e911d.sketch_text.stroke-144"),sQuery(id+"FHMxAyK4CFUKdhS_1.wireOp",EDGE,"1cb9c079-ea9b-4899-8069-e0e3048e911d.sketch_text.stroke-145"),sQuery(id+"FHMxAyK4CFUKdhS_1.wireOp",EDGE,"1cb9c079-ea9b-4899-8069-e0e3048e911d.sketch_text.stroke-146"),sQuery(id+"FHMxAyK4CFUKdhS_1.wireOp",EDGE,"1cb9c079-ea9b-4899-8069-e0e3048e911d.sketch_text.stroke-147"),sQuery(id+"FHMxAyK4CFUKdhS_1.wireOp",EDGE,"1cb9c079-ea9b-4899-8069-e0e3048e911d.sketch_text.stroke-148"),sQuery(id+"FHMxAyK4CFUKdhS_1.wireOp",EDGE,"1cb9c079-ea9b-4899-8069-e0e3048e911d.sketch_text.stroke-149"),sQuery(id+"FHMxAyK4CFUKdhS_1.wireOp",EDGE,"1cb9c079-ea9b-4899-8069-e0e3048e911d.sketch_text.stroke-150"),sQuery(id+"FHMxAyK4CFUKdhS_1.wireOp",EDGE,"1cb9c079-ea9b-4899-8069-e0e3048e911d.sketch_text.stroke-151"),sQuery(id+"FHMxAyK4CFUKdhS_1.wireOp",EDGE,"1cb9c079-ea9b-4899-8069-e0e3048e911d.sketch_text.stroke-152"),sQuery(id+"FHMxAyK4CFUKdhS_1.wireOp",EDGE,"1cb9c079-ea9b-4899-8069-e0e3048e911d.sketch_text.stroke-153"),sQuery(id+"FHMxAyK4CFUKdhS_1.wireOp",EDGE,"1cb9c079-ea9b-4899-8069-e0e3048e911d.sketch_text.stroke-159"),sQuery(id+"FHMxAyK4CFUKdhS_1.wireOp",EDGE,"1cb9c079-ea9b-4899-8069-e0e3048e911d.sketch_text.stroke-160"),sQuery(id+"FHMxAyK4CFUKdhS_1.wireOp",EDGE,"1cb9c079-ea9b-4899-8069-e0e3048e911d.sketch_text.stroke-161"),sQuery(id+"FHMxAyK4CFUKdhS_1.wireOp",EDGE,"1cb9c079-ea9b-4899-8069-e0e3048e911d.sketch_text.stroke-162"),sQuery(id+"FHMxAyK4CFUKdhS_1.wireOp",EDGE,"1cb9c079-ea9b-4899-8069-e0e3048e911d.sketch_text.stroke-163"),sQuery(id+"FHMxAyK4CFUKdhS_1.wireOp",EDGE,"1cb9c079-ea9b-4899-8069-e0e3048e911d.sketch_text.stroke-164"),sQuery(id+"FHMxAyK4CFUKdhS_1.wireOp",EDGE,"1cb9c079-ea9b-4899-8069-e0e3048e911d.sketch_text.stroke-165"),sQuery(id+"FHMxAyK4CFUKdhS_1.wireOp",EDGE,"1cb9c079-ea9b-4899-8069-e0e3048e911d.sketch_text.stroke-166"),sQuery(id+"FHMxAyK4CFUKdhS_1.wireOp",EDGE,"1cb9c079-ea9b-4899-8069-e0e3048e911d.sketch_text.stroke-167"),sQuery(id+"FHMxAyK4CFUKdhS_1.wireOp",EDGE,"1cb9c079-ea9b-4899-8069-e0e3048e911d.sketch_text.stroke-168"),sQuery(id+"FHMxAyK4CFUKdhS_1.wireOp",EDGE,"1cb9c079-ea9b-4899-8069-e0e3048e911d.sketch_text.stroke-169"),sQuery(id+"FHMxAyK4CFUKdhS_1.wireOp",EDGE,"1cb9c079-ea9b-4899-8069-e0e3048e911d.sketch_text.stroke-170"),sQuery(id+"FHMxAyK4CFUKdhS_1.wireOp",EDGE,"1cb9c079-ea9b-4899-8069-e0e3048e911d.sketch_text.stroke-171"),sQuery(id+"FHMxAyK4CFUKdhS_1.wireOp",EDGE,"1cb9c079-ea9b-4899-8069-e0e3048e911d.sketch_text.stroke-172"),sQuery(id+"FHMxAyK4CFUKdhS_1.wireOp",EDGE,"1cb9c079-ea9b-4899-8069-e0e3048e911d.sketch_text.stroke-173"),sQuery(id+"FHMxAyK4CFUKdhS_1.wireOp",EDGE,"1cb9c079-ea9b-4899-8069-e0e3048e911d.sketch_text.stroke-174"),sQuery(id+"FHMxAyK4CFUKdhS_1.wireOp",EDGE,"1cb9c079-ea9b-4899-8069-e0e3048e911d.sketch_text.stroke-175"),sQuery(id+"FHMxAyK4CFUKdhS_1.wireOp",EDGE,"1cb9c079-ea9b-4899-8069-e0e3048e911d.sketch_text.stroke-176"),sQuery(id+"FHMxAyK4CFUKdhS_1.wireOp",EDGE,"1cb9c079-ea9b-4899-8069-e0e3048e911d.sketch_text.stroke-177"),sQuery(id+"FHMxAyK4CFUKdhS_1.wireOp",EDGE,"1cb9c079-ea9b-4899-8069-e0e3048e911d.sketch_text.stroke-178"),sQuery(id+"FHMxAyK4CFUKdhS_1.wireOp",EDGE,"1cb9c079-ea9b-4899-8069-e0e3048e911d.sketch_text.stroke-179"),sQuery(id+"FHMxAyK4CFUKdhS_1.wireOp",EDGE,"1cb9c079-ea9b-4899-8069-e0e3048e911d.sketch_text.stroke-180"),subQ2,sQuery(id+"F2.wireOp",EDGE,"E27")])],"isStart":true})])],"derivedFrom":makeQuery(id+"F3.opExtrude","CAP_EDGE",EDGE,{"disambiguationData":[OSD([subQ2])],"isStart":true})});}
            var Q21;
            {var subQ0=sQuery(id+"F2.wireOp",EDGE,"E26");var subQ1=sQuery(id+"F0.wireOp",EDGE,"E0.top");var subQ2=sQuery(id+"F2.wireOp",EDGE,"E27");var subQ3=sQuery(id+"F0.wireOp",EDGE,"E0.bottom");Q21=makeQuery(id+"F3.boolean.opBoolean","SPLIT",EDGE,{"disambiguationData":[TD([makeQuery(id+"F1.opExtrude","CAP_FACE",FACE,{"disambiguationData":[OSD([subQ3,subQ1,sQuery(id+"F0.wireOp",EDGE,"E0.left"),sQuery(id+"F0.wireOp",EDGE,"E0.right")])],"isStart":false}),makeQuery(id+"F1.opExtrude","SWEPT_FACE",FACE,{"disambiguationData":[OSD([subQ1])]}),makeQuery(id+"F3.opExtrude","SWEPT_FACE",FACE,{"disambiguationData":[OSD([subQ0])]}),makeQuery(id+"F3.opExtrude","CAP_FACE",FACE,{"disambiguationData":[OSD([subQ3,sQuery(id+"FQ5JFwxVdaqARUP_1.wireOp",EDGE,"fcba4419-a2ee-464f-be9d-58f11bf3418b.sketch_text.stroke-0"),sQuery(id+"FQ5JFwxVdaqARUP_1.wireOp",EDGE,"fcba4419-a2ee-464f-be9d-58f11bf3418b.sketch_text.stroke-1"),sQuery(id+"FQ5JFwxVdaqARUP_1.wireOp",EDGE,"fcba4419-a2ee-464f-be9d-58f11bf3418b.sketch_text.stroke-2"),sQuery(id+"FQ5JFwxVdaqARUP_1.wireOp",EDGE,"fcba4419-a2ee-464f-be9d-58f11bf3418b.sketch_text.stroke-3"),sQuery(id+"FQ5JFwxVdaqARUP_1.wireOp",EDGE,"fcba4419-a2ee-464f-be9d-58f11bf3418b.sketch_text.stroke-4"),sQuery(id+"FQ5JFwxVdaqARUP_1.wireOp",EDGE,"fcba4419-a2ee-464f-be9d-58f11bf3418b.sketch_text.stroke-5"),sQuery(id+"FQ5JFwxVdaqARUP_1.wireOp",EDGE,"fcba4419-a2ee-464f-be9d-58f11bf3418b.sketch_text.stroke-6"),sQuery(id+"FQ5JFwxVdaqARUP_1.wireOp",EDGE,"fcba4419-a2ee-464f-be9d-58f11bf3418b.sketch_text.stroke-7"),sQuery(id+"FQ5JFwxVdaqARUP_1.wireOp",EDGE,"fcba4419-a2ee-464f-be9d-58f11bf3418b.sketch_text.stroke-8"),sQuery(id+"FQ5JFwxVdaqARUP_1.wireOp",EDGE,"fcba4419-a2ee-464f-be9d-58f11bf3418b.sketch_text.stroke-9"),sQuery(id+"FQ5JFwxVdaqARUP_1.wireOp",EDGE,"fcba4419-a2ee-464f-be9d-58f11bf3418b.sketch_text.stroke-10"),sQuery(id+"FQ5JFwxVdaqARUP_1.wireOp",EDGE,"fcba4419-a2ee-464f-be9d-58f11bf3418b.sketch_text.stroke-11"),sQuery(id+"FQ5JFwxVdaqARUP_1.wireOp",EDGE,"fcba4419-a2ee-464f-be9d-58f11bf3418b.sketch_text.stroke-12"),sQuery(id+"FQ5JFwxVdaqARUP_1.wireOp",EDGE,"fcba4419-a2ee-464f-be9d-58f11bf3418b.sketch_text.stroke-13"),sQuery(id+"FQ5JFwxVdaqARUP_1.wireOp",EDGE,"fcba4419-a2ee-464f-be9d-58f11bf3418b.sketch_text.stroke-14"),sQuery(id+"FQ5JFwxVdaqARUP_1.wireOp",EDGE,"fcba4419-a2ee-464f-be9d-58f11bf3418b.sketch_text.stroke-15"),sQuery(id+"FQ5JFwxVdaqARUP_1.wireOp",EDGE,"fcba4419-a2ee-464f-be9d-58f11bf3418b.sketch_text.stroke-16"),sQuery(id+"FQ5JFwxVdaqARUP_1.wireOp",EDGE,"fcba4419-a2ee-464f-be9d-58f11bf3418b.sketch_text.stroke-17"),sQuery(id+"FQ5JFwxVdaqARUP_1.wireOp",EDGE,"fcba4419-a2ee-464f-be9d-58f11bf3418b.sketch_text.stroke-18"),sQuery(id+"FQ5JFwxVdaqARUP_1.wireOp",EDGE,"fcba4419-a2ee-464f-be9d-58f11bf3418b.sketch_text.stroke-19"),sQuery(id+"FQ5JFwxVdaqARUP_1.wireOp",EDGE,"fcba4419-a2ee-464f-be9d-58f11bf3418b.sketch_text.stroke-20"),sQuery(id+"FQ5JFwxVdaqARUP_1.wireOp",EDGE,"fcba4419-a2ee-464f-be9d-58f11bf3418b.sketch_text.stroke-21"),sQuery(id+"FQ5JFwxVdaqARUP_1.wireOp",EDGE,"fcba4419-a2ee-464f-be9d-58f11bf3418b.sketch_text.stroke-22"),sQuery(id+"FQ5JFwxVdaqARUP_1.wireOp",EDGE,"fcba4419-a2ee-464f-be9d-58f11bf3418b.sketch_text.stroke-23"),sQuery(id+"FQ5JFwxVdaqARUP_1.wireOp",EDGE,"fcba4419-a2ee-464f-be9d-58f11bf3418b.sketch_text.stroke-24"),sQuery(id+"FQ5JFwxVdaqARUP_1.wireOp",EDGE,"fcba4419-a2ee-464f-be9d-58f11bf3418b.sketch_text.stroke-25"),sQuery(id+"FQ5JFwxVdaqARUP_1.wireOp",EDGE,"fcba4419-a2ee-464f-be9d-58f11bf3418b.sketch_text.stroke-26"),sQuery(id+"FQ5JFwxVdaqARUP_1.wireOp",EDGE,"fcba4419-a2ee-464f-be9d-58f11bf3418b.sketch_text.stroke-27"),sQuery(id+"FQ5JFwxVdaqARUP_1.wireOp",EDGE,"fcba4419-a2ee-464f-be9d-58f11bf3418b.sketch_text.stroke-28"),sQuery(id+"FQ5JFwxVdaqARUP_1.wireOp",EDGE,"fcba4419-a2ee-464f-be9d-58f11bf3418b.sketch_text.stroke-29"),sQuery(id+"FQ5JFwxVdaqARUP_1.wireOp",EDGE,"fcba4419-a2ee-464f-be9d-58f11bf3418b.sketch_text.stroke-30"),sQuery(id+"FQ5JFwxVdaqARUP_1.wireOp",EDGE,"fcba4419-a2ee-464f-be9d-58f11bf3418b.sketch_text.stroke-31"),sQuery(id+"FQ5JFwxVdaqARUP_1.wireOp",EDGE,"fcba4419-a2ee-464f-be9d-58f11bf3418b.sketch_text.stroke-32"),sQuery(id+"FQ5JFwxVdaqARUP_1.wireOp",EDGE,"fcba4419-a2ee-464f-be9d-58f11bf3418b.sketch_text.stroke-33"),sQuery(id+"FQ5JFwxVdaqARUP_1.wireOp",EDGE,"fcba4419-a2ee-464f-be9d-58f11bf3418b.sketch_text.stroke-34"),sQuery(id+"FQ5JFwxVdaqARUP_1.wireOp",EDGE,"fcba4419-a2ee-464f-be9d-58f11bf3418b.sketch_text.stroke-35"),sQuery(id+"FQ5JFwxVdaqARUP_1.wireOp",EDGE,"fcba4419-a2ee-464f-be9d-58f11bf3418b.sketch_text.stroke-36"),sQuery(id+"FQ5JFwxVdaqARUP_1.wireOp",EDGE,"fcba4419-a2ee-464f-be9d-58f11bf3418b.sketch_text.stroke-37"),sQuery(id+"FQ5JFwxVdaqARUP_1.wireOp",EDGE,"fcba4419-a2ee-464f-be9d-58f11bf3418b.sketch_text.stroke-38"),sQuery(id+"FQ5JFwxVdaqARUP_1.wireOp",EDGE,"fcba4419-a2ee-464f-be9d-58f11bf3418b.sketch_text.stroke-39"),sQuery(id+"FQ5JFwxVdaqARUP_1.wireOp",EDGE,"fcba4419-a2ee-464f-be9d-58f11bf3418b.sketch_text.stroke-40"),sQuery(id+"FQ5JFwxVdaqARUP_1.wireOp",EDGE,"fcba4419-a2ee-464f-be9d-58f11bf3418b.sketch_text.stroke-41"),sQuery(id+"FQ5JFwxVdaqARUP_1.wireOp",EDGE,"fcba4419-a2ee-464f-be9d-58f11bf3418b.sketch_text.stroke-42"),sQuery(id+"FQ5JFwxVdaqARUP_1.wireOp",EDGE,"fcba4419-a2ee-464f-be9d-58f11bf3418b.sketch_text.stroke-43"),sQuery(id+"FQ5JFwxVdaqARUP_1.wireOp",EDGE,"fcba4419-a2ee-464f-be9d-58f11bf3418b.sketch_text.stroke-44"),sQuery(id+"FQ5JFwxVdaqARUP_1.wireOp",EDGE,"fcba4419-a2ee-464f-be9d-58f11bf3418b.sketch_text.stroke-45"),sQuery(id+"FQ5JFwxVdaqARUP_1.wireOp",EDGE,"fcba4419-a2ee-464f-be9d-58f11bf3418b.sketch_text.stroke-46"),sQuery(id+"FQ5JFwxVdaqARUP_1.wireOp",EDGE,"fcba4419-a2ee-464f-be9d-58f11bf3418b.sketch_text.stroke-47"),sQuery(id+"FQ5JFwxVdaqARUP_1.wireOp",EDGE,"fcba4419-a2ee-464f-be9d-58f11bf3418b.sketch_text.stroke-48"),sQuery(id+"FQ5JFwxVdaqARUP_1.wireOp",EDGE,"fcba4419-a2ee-464f-be9d-58f11bf3418b.sketch_text.stroke-49"),sQuery(id+"FQ5JFwxVdaqARUP_1.wireOp",EDGE,"fcba4419-a2ee-464f-be9d-58f11bf3418b.sketch_text.stroke-50"),sQuery(id+"FQ5JFwxVdaqARUP_1.wireOp",EDGE,"fcba4419-a2ee-464f-be9d-58f11bf3418b.sketch_text.stroke-51"),sQuery(id+"FQ5JFwxVdaqARUP_1.wireOp",EDGE,"fcba4419-a2ee-464f-be9d-58f11bf3418b.sketch_text.stroke-52"),sQuery(id+"FQ5JFwxVdaqARUP_1.wireOp",EDGE,"fcba4419-a2ee-464f-be9d-58f11bf3418b.sketch_text.stroke-53"),sQuery(id+"FQ5JFwxVdaqARUP_1.wireOp",EDGE,"fcba4419-a2ee-464f-be9d-58f11bf3418b.sketch_text.stroke-54"),sQuery(id+"FQ5JFwxVdaqARUP_1.wireOp",EDGE,"fcba4419-a2ee-464f-be9d-58f11bf3418b.sketch_text.stroke-55"),sQuery(id+"FQ5JFwxVdaqARUP_1.wireOp",EDGE,"fcba4419-a2ee-464f-be9d-58f11bf3418b.sketch_text.stroke-56"),sQuery(id+"FQ5JFwxVdaqARUP_1.wireOp",EDGE,"fcba4419-a2ee-464f-be9d-58f11bf3418b.sketch_text.stroke-57"),sQuery(id+"FQ5JFwxVdaqARUP_1.wireOp",EDGE,"fcba4419-a2ee-464f-be9d-58f11bf3418b.sketch_text.stroke-58"),sQuery(id+"FQ5JFwxVdaqARUP_1.wireOp",EDGE,"fcba4419-a2ee-464f-be9d-58f11bf3418b.sketch_text.stroke-59"),sQuery(id+"FQ5JFwxVdaqARUP_1.wireOp",EDGE,"fcba4419-a2ee-464f-be9d-58f11bf3418b.sketch_text.stroke-60"),sQuery(id+"FQ5JFwxVdaqARUP_1.wireOp",EDGE,"fcba4419-a2ee-464f-be9d-58f11bf3418b.sketch_text.stroke-61"),sQuery(id+"FQ5JFwxVdaqARUP_1.wireOp",EDGE,"fcba4419-a2ee-464f-be9d-58f11bf3418b.sketch_text.stroke-62"),sQuery(id+"FQ5JFwxVdaqARUP_1.wireOp",EDGE,"fcba4419-a2ee-464f-be9d-58f11bf3418b.sketch_text.stroke-63"),sQuery(id+"FQ5JFwxVdaqARUP_1.wireOp",EDGE,"fcba4419-a2ee-464f-be9d-58f11bf3418b.sketch_text.stroke-64"),sQuery(id+"FQ5JFwxVdaqARUP_1.wireOp",EDGE,"fcba4419-a2ee-464f-be9d-58f11bf3418b.sketch_text.stroke-65"),sQuery(id+"FQ5JFwxVdaqARUP_1.wireOp",EDGE,"fcba4419-a2ee-464f-be9d-58f11bf3418b.sketch_text.stroke-66"),sQuery(id+"FQ5JFwxVdaqARUP_1.wireOp",EDGE,"fcba4419-a2ee-464f-be9d-58f11bf3418b.sketch_text.stroke-67"),sQuery(id+"FQ5JFwxVdaqARUP_1.wireOp",EDGE,"fcba4419-a2ee-464f-be9d-58f11bf3418b.sketch_text.stroke-68"),sQuery(id+"FQ5JFwxVdaqARUP_1.wireOp",EDGE,"fcba4419-a2ee-464f-be9d-58f11bf3418b.sketch_text.stroke-69"),sQuery(id+"FQ5JFwxVdaqARUP_1.wireOp",EDGE,"fcba4419-a2ee-464f-be9d-58f11bf3418b.sketch_text.stroke-70"),sQuery(id+"FQ5JFwxVdaqARUP_1.wireOp",EDGE,"fcba4419-a2ee-464f-be9d-58f11bf3418b.sketch_text.stroke-71"),sQuery(id+"FQ5JFwxVdaqARUP_1.wireOp",EDGE,"fcba4419-a2ee-464f-be9d-58f11bf3418b.sketch_text.stroke-72"),sQuery(id+"FQ5JFwxVdaqARUP_1.wireOp",EDGE,"fcba4419-a2ee-464f-be9d-58f11bf3418b.sketch_text.stroke-73"),sQuery(id+"FQ5JFwxVdaqARUP_1.wireOp",EDGE,"fcba4419-a2ee-464f-be9d-58f11bf3418b.sketch_text.stroke-74"),sQuery(id+"FQ5JFwxVdaqARUP_1.wireOp",EDGE,"fcba4419-a2ee-464f-be9d-58f11bf3418b.sketch_text.stroke-75"),sQuery(id+"FQ5JFwxVdaqARUP_1.wireOp",EDGE,"fcba4419-a2ee-464f-be9d-58f11bf3418b.sketch_text.stroke-76"),sQuery(id+"FQ5JFwxVdaqARUP_1.wireOp",EDGE,"fcba4419-a2ee-464f-be9d-58f11bf3418b.sketch_text.stroke-77"),sQuery(id+"FQ5JFwxVdaqARUP_1.wireOp",EDGE,"fcba4419-a2ee-464f-be9d-58f11bf3418b.sketch_text.stroke-78"),sQuery(id+"FQ5JFwxVdaqARUP_1.wireOp",EDGE,"fcba4419-a2ee-464f-be9d-58f11bf3418b.sketch_text.stroke-79"),sQuery(id+"FQ5JFwxVdaqARUP_1.wireOp",EDGE,"fcba4419-a2ee-464f-be9d-58f11bf3418b.sketch_text.stroke-80"),sQuery(id+"FQ5JFwxVdaqARUP_1.wireOp",EDGE,"fcba4419-a2ee-464f-be9d-58f11bf3418b.sketch_text.stroke-81"),sQuery(id+"FQ5JFwxVdaqARUP_1.wireOp",EDGE,"fcba4419-a2ee-464f-be9d-58f11bf3418b.sketch_text.stroke-82"),sQuery(id+"FQ5JFwxVdaqARUP_1.wireOp",EDGE,"fcba4419-a2ee-464f-be9d-58f11bf3418b.sketch_text.stroke-83"),sQuery(id+"FQ5JFwxVdaqARUP_1.wireOp",EDGE,"fcba4419-a2ee-464f-be9d-58f11bf3418b.sketch_text.stroke-84"),sQuery(id+"FQ5JFwxVdaqARUP_1.wireOp",EDGE,"fcba4419-a2ee-464f-be9d-58f11bf3418b.sketch_text.stroke-85"),sQuery(id+"FQ5JFwxVdaqARUP_1.wireOp",EDGE,"fcba4419-a2ee-464f-be9d-58f11bf3418b.sketch_text.stroke-86"),sQuery(id+"FQ5JFwxVdaqARUP_1.wireOp",EDGE,"fcba4419-a2ee-464f-be9d-58f11bf3418b.sketch_text.stroke-87"),sQuery(id+"FQ5JFwxVdaqARUP_1.wireOp",EDGE,"fcba4419-a2ee-464f-be9d-58f11bf3418b.sketch_text.stroke-88"),sQuery(id+"FQ5JFwxVdaqARUP_1.wireOp",EDGE,"fcba4419-a2ee-464f-be9d-58f11bf3418b.sketch_text.stroke-89"),sQuery(id+"FQ5JFwxVdaqARUP_1.wireOp",EDGE,"fcba4419-a2ee-464f-be9d-58f11bf3418b.sketch_text.stroke-90"),sQuery(id+"FQ5JFwxVdaqARUP_1.wireOp",EDGE,"fcba4419-a2ee-464f-be9d-58f11bf3418b.sketch_text.stroke-91"),sQuery(id+"FQ5JFwxVdaqARUP_1.wireOp",EDGE,"fcba4419-a2ee-464f-be9d-58f11bf3418b.sketch_text.stroke-92"),sQuery(id+"FQ5JFwxVdaqARUP_1.wireOp",EDGE,"fcba4419-a2ee-464f-be9d-58f11bf3418b.sketch_text.stroke-93"),sQuery(id+"FQ5JFwxVdaqARUP_1.wireOp",EDGE,"fcba4419-a2ee-464f-be9d-58f11bf3418b.sketch_text.stroke-94"),sQuery(id+"FQ5JFwxVdaqARUP_1.wireOp",EDGE,"fcba4419-a2ee-464f-be9d-58f11bf3418b.sketch_text.stroke-95"),sQuery(id+"FQ5JFwxVdaqARUP_1.wireOp",EDGE,"fcba4419-a2ee-464f-be9d-58f11bf3418b.sketch_text.stroke-96"),sQuery(id+"FQ5JFwxVdaqARUP_1.wireOp",EDGE,"fcba4419-a2ee-464f-be9d-58f11bf3418b.sketch_text.stroke-97"),sQuery(id+"FQ5JFwxVdaqARUP_1.wireOp",EDGE,"fcba4419-a2ee-464f-be9d-58f11bf3418b.sketch_text.stroke-98"),sQuery(id+"FQ5JFwxVdaqARUP_1.wireOp",EDGE,"fcba4419-a2ee-464f-be9d-58f11bf3418b.sketch_text.stroke-99"),sQuery(id+"FQ5JFwxVdaqARUP_1.wireOp",EDGE,"fcba4419-a2ee-464f-be9d-58f11bf3418b.sketch_text.stroke-100"),sQuery(id+"FQ5JFwxVdaqARUP_1.wireOp",EDGE,"fcba4419-a2ee-464f-be9d-58f11bf3418b.sketch_text.stroke-101"),sQuery(id+"FQ5JFwxVdaqARUP_1.wireOp",EDGE,"fcba4419-a2ee-464f-be9d-58f11bf3418b.sketch_text.stroke-102"),sQuery(id+"FQ5JFwxVdaqARUP_1.wireOp",EDGE,"fcba4419-a2ee-464f-be9d-58f11bf3418b.sketch_text.stroke-103"),sQuery(id+"FQ5JFwxVdaqARUP_1.wireOp",EDGE,"fcba4419-a2ee-464f-be9d-58f11bf3418b.sketch_text.stroke-104"),sQuery(id+"FQ5JFwxVdaqARUP_1.wireOp",EDGE,"fcba4419-a2ee-464f-be9d-58f11bf3418b.sketch_text.stroke-105"),sQuery(id+"FQ5JFwxVdaqARUP_1.wireOp",EDGE,"fcba4419-a2ee-464f-be9d-58f11bf3418b.sketch_text.stroke-106"),sQuery(id+"FQ5JFwxVdaqARUP_1.wireOp",EDGE,"fcba4419-a2ee-464f-be9d-58f11bf3418b.sketch_text.stroke-107"),sQuery(id+"FQ5JFwxVdaqARUP_1.wireOp",EDGE,"fcba4419-a2ee-464f-be9d-58f11bf3418b.sketch_text.stroke-108"),sQuery(id+"FQ5JFwxVdaqARUP_1.wireOp",EDGE,"fcba4419-a2ee-464f-be9d-58f11bf3418b.sketch_text.stroke-109"),sQuery(id+"FQ5JFwxVdaqARUP_1.wireOp",EDGE,"fcba4419-a2ee-464f-be9d-58f11bf3418b.sketch_text.stroke-110"),sQuery(id+"FQ5JFwxVdaqARUP_1.wireOp",EDGE,"fcba4419-a2ee-464f-be9d-58f11bf3418b.sketch_text.stroke-111"),sQuery(id+"FQ5JFwxVdaqARUP_1.wireOp",EDGE,"fcba4419-a2ee-464f-be9d-58f11bf3418b.sketch_text.stroke-112"),sQuery(id+"FQ5JFwxVdaqARUP_1.wireOp",EDGE,"fcba4419-a2ee-464f-be9d-58f11bf3418b.sketch_text.stroke-113"),sQuery(id+"FQ5JFwxVdaqARUP_1.wireOp",EDGE,"fcba4419-a2ee-464f-be9d-58f11bf3418b.sketch_text.stroke-114"),sQuery(id+"FQ5JFwxVdaqARUP_1.wireOp",EDGE,"fcba4419-a2ee-464f-be9d-58f11bf3418b.sketch_text.stroke-115"),sQuery(id+"FQ5JFwxVdaqARUP_1.wireOp",EDGE,"fcba4419-a2ee-464f-be9d-58f11bf3418b.sketch_text.stroke-116"),sQuery(id+"FQ5JFwxVdaqARUP_1.wireOp",EDGE,"fcba4419-a2ee-464f-be9d-58f11bf3418b.sketch_text.stroke-117"),sQuery(id+"FQ5JFwxVdaqARUP_1.wireOp",EDGE,"fcba4419-a2ee-464f-be9d-58f11bf3418b.sketch_text.stroke-118"),sQuery(id+"FQ5JFwxVdaqARUP_1.wireOp",EDGE,"fcba4419-a2ee-464f-be9d-58f11bf3418b.sketch_text.stroke-119"),sQuery(id+"FQ5JFwxVdaqARUP_1.wireOp",EDGE,"fcba4419-a2ee-464f-be9d-58f11bf3418b.sketch_text.stroke-120"),sQuery(id+"FQ5JFwxVdaqARUP_1.wireOp",EDGE,"fcba4419-a2ee-464f-be9d-58f11bf3418b.sketch_text.stroke-121"),sQuery(id+"FQ5JFwxVdaqARUP_1.wireOp",EDGE,"fcba4419-a2ee-464f-be9d-58f11bf3418b.sketch_text.stroke-122"),sQuery(id+"FQ5JFwxVdaqARUP_1.wireOp",EDGE,"fcba4419-a2ee-464f-be9d-58f11bf3418b.sketch_text.stroke-123"),sQuery(id+"FQ5JFwxVdaqARUP_1.wireOp",EDGE,"fcba4419-a2ee-464f-be9d-58f11bf3418b.sketch_text.stroke-124"),sQuery(id+"FQ5JFwxVdaqARUP_1.wireOp",EDGE,"fcba4419-a2ee-464f-be9d-58f11bf3418b.sketch_text.stroke-125"),sQuery(id+"FQ5JFwxVdaqARUP_1.wireOp",EDGE,"fcba4419-a2ee-464f-be9d-58f11bf3418b.sketch_text.stroke-126"),sQuery(id+"FQ5JFwxVdaqARUP_1.wireOp",EDGE,"fcba4419-a2ee-464f-be9d-58f11bf3418b.sketch_text.stroke-127"),sQuery(id+"FQ5JFwxVdaqARUP_1.wireOp",EDGE,"fcba4419-a2ee-464f-be9d-58f11bf3418b.sketch_text.stroke-128"),sQuery(id+"FQ5JFwxVdaqARUP_1.wireOp",EDGE,"fcba4419-a2ee-464f-be9d-58f11bf3418b.sketch_text.stroke-129"),sQuery(id+"FQ5JFwxVdaqARUP_1.wireOp",EDGE,"fcba4419-a2ee-464f-be9d-58f11bf3418b.sketch_text.stroke-130"),sQuery(id+"FQ5JFwxVdaqARUP_1.wireOp",EDGE,"fcba4419-a2ee-464f-be9d-58f11bf3418b.sketch_text.stroke-131"),sQuery(id+"FQ5JFwxVdaqARUP_1.wireOp",EDGE,"fcba4419-a2ee-464f-be9d-58f11bf3418b.sketch_text.stroke-132"),sQuery(id+"FQ5JFwxVdaqARUP_1.wireOp",EDGE,"fcba4419-a2ee-464f-be9d-58f11bf3418b.sketch_text.stroke-133"),sQuery(id+"FQ5JFwxVdaqARUP_1.wireOp",EDGE,"fcba4419-a2ee-464f-be9d-58f11bf3418b.sketch_text.stroke-134"),sQuery(id+"FQ5JFwxVdaqARUP_1.wireOp",EDGE,"fcba4419-a2ee-464f-be9d-58f11bf3418b.sketch_text.stroke-135"),sQuery(id+"FQ5JFwxVdaqARUP_1.wireOp",EDGE,"fcba4419-a2ee-464f-be9d-58f11bf3418b.sketch_text.stroke-136"),sQuery(id+"FQ5JFwxVdaqARUP_1.wireOp",EDGE,"fcba4419-a2ee-464f-be9d-58f11bf3418b.sketch_text.stroke-137"),sQuery(id+"FQ5JFwxVdaqARUP_1.wireOp",EDGE,"fcba4419-a2ee-464f-be9d-58f11bf3418b.sketch_text.stroke-138"),sQuery(id+"FQ5JFwxVdaqARUP_1.wireOp",EDGE,"fcba4419-a2ee-464f-be9d-58f11bf3418b.sketch_text.stroke-139"),sQuery(id+"FQ5JFwxVdaqARUP_1.wireOp",EDGE,"fcba4419-a2ee-464f-be9d-58f11bf3418b.sketch_text.stroke-140"),sQuery(id+"FQ5JFwxVdaqARUP_1.wireOp",EDGE,"fcba4419-a2ee-464f-be9d-58f11bf3418b.sketch_text.stroke-141"),sQuery(id+"FQ5JFwxVdaqARUP_1.wireOp",EDGE,"fcba4419-a2ee-464f-be9d-58f11bf3418b.sketch_text.stroke-142"),sQuery(id+"FQ5JFwxVdaqARUP_1.wireOp",EDGE,"fcba4419-a2ee-464f-be9d-58f11bf3418b.sketch_text.stroke-143"),sQuery(id+"FQ5JFwxVdaqARUP_1.wireOp",EDGE,"fcba4419-a2ee-464f-be9d-58f11bf3418b.sketch_text.stroke-144"),sQuery(id+"FQ5JFwxVdaqARUP_1.wireOp",EDGE,"fcba4419-a2ee-464f-be9d-58f11bf3418b.sketch_text.stroke-145"),sQuery(id+"FQ5JFwxVdaqARUP_1.wireOp",EDGE,"fcba4419-a2ee-464f-be9d-58f11bf3418b.sketch_text.stroke-146"),sQuery(id+"FQ5JFwxVdaqARUP_1.wireOp",EDGE,"fcba4419-a2ee-464f-be9d-58f11bf3418b.sketch_text.stroke-147"),sQuery(id+"FQ5JFwxVdaqARUP_1.wireOp",EDGE,"fcba4419-a2ee-464f-be9d-58f11bf3418b.sketch_text.stroke-148"),sQuery(id+"FQ5JFwxVdaqARUP_1.wireOp",EDGE,"fcba4419-a2ee-464f-be9d-58f11bf3418b.sketch_text.stroke-149"),sQuery(id+"FQ5JFwxVdaqARUP_1.wireOp",EDGE,"fcba4419-a2ee-464f-be9d-58f11bf3418b.sketch_text.stroke-150"),sQuery(id+"FQ5JFwxVdaqARUP_1.wireOp",EDGE,"fcba4419-a2ee-464f-be9d-58f11bf3418b.sketch_text.stroke-151"),sQuery(id+"FQ5JFwxVdaqARUP_1.wireOp",EDGE,"fcba4419-a2ee-464f-be9d-58f11bf3418b.sketch_text.stroke-152"),sQuery(id+"FQ5JFwxVdaqARUP_1.wireOp",EDGE,"fcba4419-a2ee-464f-be9d-58f11bf3418b.sketch_text.stroke-153"),sQuery(id+"FQ5JFwxVdaqARUP_1.wireOp",EDGE,"fcba4419-a2ee-464f-be9d-58f11bf3418b.sketch_text.stroke-154"),sQuery(id+"FQ5JFwxVdaqARUP_1.wireOp",EDGE,"fcba4419-a2ee-464f-be9d-58f11bf3418b.sketch_text.stroke-155"),sQuery(id+"FQ5JFwxVdaqARUP_1.wireOp",EDGE,"fcba4419-a2ee-464f-be9d-58f11bf3418b.sketch_text.stroke-156"),sQuery(id+"FQ5JFwxVdaqARUP_1.wireOp",EDGE,"fcba4419-a2ee-464f-be9d-58f11bf3418b.sketch_text.stroke-157"),sQuery(id+"FQ5JFwxVdaqARUP_1.wireOp",EDGE,"fcba4419-a2ee-464f-be9d-58f11bf3418b.sketch_text.stroke-158"),sQuery(id+"FQ5JFwxVdaqARUP_1.wireOp",EDGE,"fcba4419-a2ee-464f-be9d-58f11bf3418b.sketch_text.stroke-159"),sQuery(id+"FQ5JFwxVdaqARUP_1.wireOp",EDGE,"fcba4419-a2ee-464f-be9d-58f11bf3418b.sketch_text.stroke-160"),sQuery(id+"FQ5JFwxVdaqARUP_1.wireOp",EDGE,"fcba4419-a2ee-464f-be9d-58f11bf3418b.sketch_text.stroke-161"),sQuery(id+"FQ5JFwxVdaqARUP_1.wireOp",EDGE,"fcba4419-a2ee-464f-be9d-58f11bf3418b.sketch_text.stroke-162"),sQuery(id+"FQ5JFwxVdaqARUP_1.wireOp",EDGE,"fcba4419-a2ee-464f-be9d-58f11bf3418b.sketch_text.stroke-163"),sQuery(id+"FQ5JFwxVdaqARUP_1.wireOp",EDGE,"fcba4419-a2ee-464f-be9d-58f11bf3418b.sketch_text.stroke-164"),sQuery(id+"FQ5JFwxVdaqARUP_1.wireOp",EDGE,"fcba4419-a2ee-464f-be9d-58f11bf3418b.sketch_text.stroke-165"),sQuery(id+"FQ5JFwxVdaqARUP_1.wireOp",EDGE,"fcba4419-a2ee-464f-be9d-58f11bf3418b.sketch_text.stroke-166"),sQuery(id+"FQ5JFwxVdaqARUP_1.wireOp",EDGE,"fcba4419-a2ee-464f-be9d-58f11bf3418b.sketch_text.stroke-167"),sQuery(id+"FQ5JFwxVdaqARUP_1.wireOp",EDGE,"fcba4419-a2ee-464f-be9d-58f11bf3418b.sketch_text.stroke-168"),sQuery(id+"FQ5JFwxVdaqARUP_1.wireOp",EDGE,"fcba4419-a2ee-464f-be9d-58f11bf3418b.sketch_text.stroke-169"),sQuery(id+"FQ5JFwxVdaqARUP_1.wireOp",EDGE,"fcba4419-a2ee-464f-be9d-58f11bf3418b.sketch_text.stroke-170"),sQuery(id+"FQ5JFwxVdaqARUP_1.wireOp",EDGE,"fcba4419-a2ee-464f-be9d-58f11bf3418b.sketch_text.stroke-171"),sQuery(id+"FQ5JFwxVdaqARUP_1.wireOp",EDGE,"fcba4419-a2ee-464f-be9d-58f11bf3418b.sketch_text.stroke-172"),sQuery(id+"FQ5JFwxVdaqARUP_1.wireOp",EDGE,"fcba4419-a2ee-464f-be9d-58f11bf3418b.sketch_text.stroke-173"),sQuery(id+"FHMxAyK4CFUKdhS_1.wireOp",EDGE,"1cb9c079-ea9b-4899-8069-e0e3048e911d.sketch_text.stroke-0"),sQuery(id+"FHMxAyK4CFUKdhS_1.wireOp",EDGE,"1cb9c079-ea9b-4899-8069-e0e3048e911d.sketch_text.stroke-1"),sQuery(id+"FHMxAyK4CFUKdhS_1.wireOp",EDGE,"1cb9c079-ea9b-4899-8069-e0e3048e911d.sketch_text.stroke-2"),sQuery(id+"FHMxAyK4CFUKdhS_1.wireOp",EDGE,"1cb9c079-ea9b-4899-8069-e0e3048e911d.sketch_text.stroke-3"),sQuery(id+"FHMxAyK4CFUKdhS_1.wireOp",EDGE,"1cb9c079-ea9b-4899-8069-e0e3048e911d.sketch_text.stroke-4"),sQuery(id+"FHMxAyK4CFUKdhS_1.wireOp",EDGE,"1cb9c079-ea9b-4899-8069-e0e3048e911d.sketch_text.stroke-5"),sQuery(id+"FHMxAyK4CFUKdhS_1.wireOp",EDGE,"1cb9c079-ea9b-4899-8069-e0e3048e911d.sketch_text.stroke-6"),sQuery(id+"FHMxAyK4CFUKdhS_1.wireOp",EDGE,"1cb9c079-ea9b-4899-8069-e0e3048e911d.sketch_text.stroke-7"),sQuery(id+"FHMxAyK4CFUKdhS_1.wireOp",EDGE,"1cb9c079-ea9b-4899-8069-e0e3048e911d.sketch_text.stroke-8"),sQuery(id+"FHMxAyK4CFUKdhS_1.wireOp",EDGE,"1cb9c079-ea9b-4899-8069-e0e3048e911d.sketch_text.stroke-9"),sQuery(id+"FHMxAyK4CFUKdhS_1.wireOp",EDGE,"1cb9c079-ea9b-4899-8069-e0e3048e911d.sketch_text.stroke-10"),sQuery(id+"FHMxAyK4CFUKdhS_1.wireOp",EDGE,"1cb9c079-ea9b-4899-8069-e0e3048e911d.sketch_text.stroke-11"),sQuery(id+"FHMxAyK4CFUKdhS_1.wireOp",EDGE,"1cb9c079-ea9b-4899-8069-e0e3048e911d.sketch_text.stroke-12"),sQuery(id+"FHMxAyK4CFUKdhS_1.wireOp",EDGE,"1cb9c079-ea9b-4899-8069-e0e3048e911d.sketch_text.stroke-13"),sQuery(id+"FHMxAyK4CFUKdhS_1.wireOp",EDGE,"1cb9c079-ea9b-4899-8069-e0e3048e911d.sketch_text.stroke-14"),sQuery(id+"FHMxAyK4CFUKdhS_1.wireOp",EDGE,"1cb9c079-ea9b-4899-8069-e0e3048e911d.sketch_text.stroke-15"),sQuery(id+"FHMxAyK4CFUKdhS_1.wireOp",EDGE,"1cb9c079-ea9b-4899-8069-e0e3048e911d.sketch_text.stroke-16"),sQuery(id+"FHMxAyK4CFUKdhS_1.wireOp",EDGE,"1cb9c079-ea9b-4899-8069-e0e3048e911d.sketch_text.stroke-17"),sQuery(id+"FHMxAyK4CFUKdhS_1.wireOp",EDGE,"1cb9c079-ea9b-4899-8069-e0e3048e911d.sketch_text.stroke-18"),sQuery(id+"FHMxAyK4CFUKdhS_1.wireOp",EDGE,"1cb9c079-ea9b-4899-8069-e0e3048e911d.sketch_text.stroke-19"),sQuery(id+"FHMxAyK4CFUKdhS_1.wireOp",EDGE,"1cb9c079-ea9b-4899-8069-e0e3048e911d.sketch_text.stroke-20"),sQuery(id+"FHMxAyK4CFUKdhS_1.wireOp",EDGE,"1cb9c079-ea9b-4899-8069-e0e3048e911d.sketch_text.stroke-21"),sQuery(id+"FHMxAyK4CFUKdhS_1.wireOp",EDGE,"1cb9c079-ea9b-4899-8069-e0e3048e911d.sketch_text.stroke-22"),sQuery(id+"FHMxAyK4CFUKdhS_1.wireOp",EDGE,"1cb9c079-ea9b-4899-8069-e0e3048e911d.sketch_text.stroke-23"),sQuery(id+"FHMxAyK4CFUKdhS_1.wireOp",EDGE,"1cb9c079-ea9b-4899-8069-e0e3048e911d.sketch_text.stroke-24"),sQuery(id+"FHMxAyK4CFUKdhS_1.wireOp",EDGE,"1cb9c079-ea9b-4899-8069-e0e3048e911d.sketch_text.stroke-25"),sQuery(id+"FHMxAyK4CFUKdhS_1.wireOp",EDGE,"1cb9c079-ea9b-4899-8069-e0e3048e911d.sketch_text.stroke-26"),sQuery(id+"FHMxAyK4CFUKdhS_1.wireOp",EDGE,"1cb9c079-ea9b-4899-8069-e0e3048e911d.sketch_text.stroke-27"),sQuery(id+"FHMxAyK4CFUKdhS_1.wireOp",EDGE,"1cb9c079-ea9b-4899-8069-e0e3048e911d.sketch_text.stroke-28"),sQuery(id+"FHMxAyK4CFUKdhS_1.wireOp",EDGE,"1cb9c079-ea9b-4899-8069-e0e3048e911d.sketch_text.stroke-29"),sQuery(id+"FHMxAyK4CFUKdhS_1.wireOp",EDGE,"1cb9c079-ea9b-4899-8069-e0e3048e911d.sketch_text.stroke-30"),sQuery(id+"FHMxAyK4CFUKdhS_1.wireOp",EDGE,"1cb9c079-ea9b-4899-8069-e0e3048e911d.sketch_text.stroke-31"),sQuery(id+"FHMxAyK4CFUKdhS_1.wireOp",EDGE,"1cb9c079-ea9b-4899-8069-e0e3048e911d.sketch_text.stroke-32"),sQuery(id+"FHMxAyK4CFUKdhS_1.wireOp",EDGE,"1cb9c079-ea9b-4899-8069-e0e3048e911d.sketch_text.stroke-33"),sQuery(id+"FHMxAyK4CFUKdhS_1.wireOp",EDGE,"1cb9c079-ea9b-4899-8069-e0e3048e911d.sketch_text.stroke-34"),sQuery(id+"FHMxAyK4CFUKdhS_1.wireOp",EDGE,"1cb9c079-ea9b-4899-8069-e0e3048e911d.sketch_text.stroke-35"),sQuery(id+"FHMxAyK4CFUKdhS_1.wireOp",EDGE,"1cb9c079-ea9b-4899-8069-e0e3048e911d.sketch_text.stroke-36"),sQuery(id+"FHMxAyK4CFUKdhS_1.wireOp",EDGE,"1cb9c079-ea9b-4899-8069-e0e3048e911d.sketch_text.stroke-37"),sQuery(id+"FHMxAyK4CFUKdhS_1.wireOp",EDGE,"1cb9c079-ea9b-4899-8069-e0e3048e911d.sketch_text.stroke-38"),sQuery(id+"FHMxAyK4CFUKdhS_1.wireOp",EDGE,"1cb9c079-ea9b-4899-8069-e0e3048e911d.sketch_text.stroke-39"),sQuery(id+"FHMxAyK4CFUKdhS_1.wireOp",EDGE,"1cb9c079-ea9b-4899-8069-e0e3048e911d.sketch_text.stroke-40"),sQuery(id+"FHMxAyK4CFUKdhS_1.wireOp",EDGE,"1cb9c079-ea9b-4899-8069-e0e3048e911d.sketch_text.stroke-41"),sQuery(id+"FHMxAyK4CFUKdhS_1.wireOp",EDGE,"1cb9c079-ea9b-4899-8069-e0e3048e911d.sketch_text.stroke-42"),sQuery(id+"FHMxAyK4CFUKdhS_1.wireOp",EDGE,"1cb9c079-ea9b-4899-8069-e0e3048e911d.sketch_text.stroke-43"),sQuery(id+"FHMxAyK4CFUKdhS_1.wireOp",EDGE,"1cb9c079-ea9b-4899-8069-e0e3048e911d.sketch_text.stroke-44"),sQuery(id+"FHMxAyK4CFUKdhS_1.wireOp",EDGE,"1cb9c079-ea9b-4899-8069-e0e3048e911d.sketch_text.stroke-45"),sQuery(id+"FHMxAyK4CFUKdhS_1.wireOp",EDGE,"1cb9c079-ea9b-4899-8069-e0e3048e911d.sketch_text.stroke-46"),sQuery(id+"FHMxAyK4CFUKdhS_1.wireOp",EDGE,"1cb9c079-ea9b-4899-8069-e0e3048e911d.sketch_text.stroke-47"),sQuery(id+"FHMxAyK4CFUKdhS_1.wireOp",EDGE,"1cb9c079-ea9b-4899-8069-e0e3048e911d.sketch_text.stroke-48"),sQuery(id+"FHMxAyK4CFUKdhS_1.wireOp",EDGE,"1cb9c079-ea9b-4899-8069-e0e3048e911d.sketch_text.stroke-49"),sQuery(id+"FHMxAyK4CFUKdhS_1.wireOp",EDGE,"1cb9c079-ea9b-4899-8069-e0e3048e911d.sketch_text.stroke-50"),sQuery(id+"FHMxAyK4CFUKdhS_1.wireOp",EDGE,"1cb9c079-ea9b-4899-8069-e0e3048e911d.sketch_text.stroke-51"),sQuery(id+"FHMxAyK4CFUKdhS_1.wireOp",EDGE,"1cb9c079-ea9b-4899-8069-e0e3048e911d.sketch_text.stroke-52"),sQuery(id+"FHMxAyK4CFUKdhS_1.wireOp",EDGE,"1cb9c079-ea9b-4899-8069-e0e3048e911d.sketch_text.stroke-53"),sQuery(id+"FHMxAyK4CFUKdhS_1.wireOp",EDGE,"1cb9c079-ea9b-4899-8069-e0e3048e911d.sketch_text.stroke-54"),sQuery(id+"FHMxAyK4CFUKdhS_1.wireOp",EDGE,"1cb9c079-ea9b-4899-8069-e0e3048e911d.sketch_text.stroke-55"),sQuery(id+"FHMxAyK4CFUKdhS_1.wireOp",EDGE,"1cb9c079-ea9b-4899-8069-e0e3048e911d.sketch_text.stroke-56"),sQuery(id+"FHMxAyK4CFUKdhS_1.wireOp",EDGE,"1cb9c079-ea9b-4899-8069-e0e3048e911d.sketch_text.stroke-57"),sQuery(id+"FHMxAyK4CFUKdhS_1.wireOp",EDGE,"1cb9c079-ea9b-4899-8069-e0e3048e911d.sketch_text.stroke-58"),sQuery(id+"FHMxAyK4CFUKdhS_1.wireOp",EDGE,"1cb9c079-ea9b-4899-8069-e0e3048e911d.sketch_text.stroke-59"),sQuery(id+"FHMxAyK4CFUKdhS_1.wireOp",EDGE,"1cb9c079-ea9b-4899-8069-e0e3048e911d.sketch_text.stroke-60"),sQuery(id+"FHMxAyK4CFUKdhS_1.wireOp",EDGE,"1cb9c079-ea9b-4899-8069-e0e3048e911d.sketch_text.stroke-61"),sQuery(id+"FHMxAyK4CFUKdhS_1.wireOp",EDGE,"1cb9c079-ea9b-4899-8069-e0e3048e911d.sketch_text.stroke-62"),sQuery(id+"FHMxAyK4CFUKdhS_1.wireOp",EDGE,"1cb9c079-ea9b-4899-8069-e0e3048e911d.sketch_text.stroke-71"),sQuery(id+"FHMxAyK4CFUKdhS_1.wireOp",EDGE,"1cb9c079-ea9b-4899-8069-e0e3048e911d.sketch_text.stroke-72"),sQuery(id+"FHMxAyK4CFUKdhS_1.wireOp",EDGE,"1cb9c079-ea9b-4899-8069-e0e3048e911d.sketch_text.stroke-73"),sQuery(id+"FHMxAyK4CFUKdhS_1.wireOp",EDGE,"1cb9c079-ea9b-4899-8069-e0e3048e911d.sketch_text.stroke-74"),sQuery(id+"FHMxAyK4CFUKdhS_1.wireOp",EDGE,"1cb9c079-ea9b-4899-8069-e0e3048e911d.sketch_text.stroke-75"),sQuery(id+"FHMxAyK4CFUKdhS_1.wireOp",EDGE,"1cb9c079-ea9b-4899-8069-e0e3048e911d.sketch_text.stroke-76"),sQuery(id+"FHMxAyK4CFUKdhS_1.wireOp",EDGE,"1cb9c079-ea9b-4899-8069-e0e3048e911d.sketch_text.stroke-77"),sQuery(id+"FHMxAyK4CFUKdhS_1.wireOp",EDGE,"1cb9c079-ea9b-4899-8069-e0e3048e911d.sketch_text.stroke-78"),sQuery(id+"FHMxAyK4CFUKdhS_1.wireOp",EDGE,"1cb9c079-ea9b-4899-8069-e0e3048e911d.sketch_text.stroke-79"),sQuery(id+"FHMxAyK4CFUKdhS_1.wireOp",EDGE,"1cb9c079-ea9b-4899-8069-e0e3048e911d.sketch_text.stroke-80"),sQuery(id+"FHMxAyK4CFUKdhS_1.wireOp",EDGE,"1cb9c079-ea9b-4899-8069-e0e3048e911d.sketch_text.stroke-81"),sQuery(id+"FHMxAyK4CFUKdhS_1.wireOp",EDGE,"1cb9c079-ea9b-4899-8069-e0e3048e911d.sketch_text.stroke-82"),sQuery(id+"FHMxAyK4CFUKdhS_1.wireOp",EDGE,"1cb9c079-ea9b-4899-8069-e0e3048e911d.sketch_text.stroke-83"),sQuery(id+"FHMxAyK4CFUKdhS_1.wireOp",EDGE,"1cb9c079-ea9b-4899-8069-e0e3048e911d.sketch_text.stroke-84"),sQuery(id+"FHMxAyK4CFUKdhS_1.wireOp",EDGE,"1cb9c079-ea9b-4899-8069-e0e3048e911d.sketch_text.stroke-85"),sQuery(id+"FHMxAyK4CFUKdhS_1.wireOp",EDGE,"1cb9c079-ea9b-4899-8069-e0e3048e911d.sketch_text.stroke-86"),sQuery(id+"FHMxAyK4CFUKdhS_1.wireOp",EDGE,"1cb9c079-ea9b-4899-8069-e0e3048e911d.sketch_text.stroke-87"),sQuery(id+"FHMxAyK4CFUKdhS_1.wireOp",EDGE,"1cb9c079-ea9b-4899-8069-e0e3048e911d.sketch_text.stroke-88"),sQuery(id+"FHMxAyK4CFUKdhS_1.wireOp",EDGE,"1cb9c079-ea9b-4899-8069-e0e3048e911d.sketch_text.stroke-89"),sQuery(id+"FHMxAyK4CFUKdhS_1.wireOp",EDGE,"1cb9c079-ea9b-4899-8069-e0e3048e911d.sketch_text.stroke-90"),sQuery(id+"FHMxAyK4CFUKdhS_1.wireOp",EDGE,"1cb9c079-ea9b-4899-8069-e0e3048e911d.sketch_text.stroke-91"),sQuery(id+"FHMxAyK4CFUKdhS_1.wireOp",EDGE,"1cb9c079-ea9b-4899-8069-e0e3048e911d.sketch_text.stroke-92"),sQuery(id+"FHMxAyK4CFUKdhS_1.wireOp",EDGE,"1cb9c079-ea9b-4899-8069-e0e3048e911d.sketch_text.stroke-93"),sQuery(id+"FHMxAyK4CFUKdhS_1.wireOp",EDGE,"1cb9c079-ea9b-4899-8069-e0e3048e911d.sketch_text.stroke-94"),sQuery(id+"FHMxAyK4CFUKdhS_1.wireOp",EDGE,"1cb9c079-ea9b-4899-8069-e0e3048e911d.sketch_text.stroke-95"),sQuery(id+"FHMxAyK4CFUKdhS_1.wireOp",EDGE,"1cb9c079-ea9b-4899-8069-e0e3048e911d.sketch_text.stroke-96"),sQuery(id+"FHMxAyK4CFUKdhS_1.wireOp",EDGE,"1cb9c079-ea9b-4899-8069-e0e3048e911d.sketch_text.stroke-97"),sQuery(id+"FHMxAyK4CFUKdhS_1.wireOp",EDGE,"1cb9c079-ea9b-4899-8069-e0e3048e911d.sketch_text.stroke-103"),sQuery(id+"FHMxAyK4CFUKdhS_1.wireOp",EDGE,"1cb9c079-ea9b-4899-8069-e0e3048e911d.sketch_text.stroke-104"),sQuery(id+"FHMxAyK4CFUKdhS_1.wireOp",EDGE,"1cb9c079-ea9b-4899-8069-e0e3048e911d.sketch_text.stroke-105"),sQuery(id+"FHMxAyK4CFUKdhS_1.wireOp",EDGE,"1cb9c079-ea9b-4899-8069-e0e3048e911d.sketch_text.stroke-106"),sQuery(id+"FHMxAyK4CFUKdhS_1.wireOp",EDGE,"1cb9c079-ea9b-4899-8069-e0e3048e911d.sketch_text.stroke-107"),sQuery(id+"FHMxAyK4CFUKdhS_1.wireOp",EDGE,"1cb9c079-ea9b-4899-8069-e0e3048e911d.sketch_text.stroke-108"),sQuery(id+"FHMxAyK4CFUKdhS_1.wireOp",EDGE,"1cb9c079-ea9b-4899-8069-e0e3048e911d.sketch_text.stroke-109"),sQuery(id+"FHMxAyK4CFUKdhS_1.wireOp",EDGE,"1cb9c079-ea9b-4899-8069-e0e3048e911d.sketch_text.stroke-110"),sQuery(id+"FHMxAyK4CFUKdhS_1.wireOp",EDGE,"1cb9c079-ea9b-4899-8069-e0e3048e911d.sketch_text.stroke-111"),sQuery(id+"FHMxAyK4CFUKdhS_1.wireOp",EDGE,"1cb9c079-ea9b-4899-8069-e0e3048e911d.sketch_text.stroke-112"),sQuery(id+"FHMxAyK4CFUKdhS_1.wireOp",EDGE,"1cb9c079-ea9b-4899-8069-e0e3048e911d.sketch_text.stroke-113"),sQuery(id+"FHMxAyK4CFUKdhS_1.wireOp",EDGE,"1cb9c079-ea9b-4899-8069-e0e3048e911d.sketch_text.stroke-114"),sQuery(id+"FHMxAyK4CFUKdhS_1.wireOp",EDGE,"1cb9c079-ea9b-4899-8069-e0e3048e911d.sketch_text.stroke-115"),sQuery(id+"FHMxAyK4CFUKdhS_1.wireOp",EDGE,"1cb9c079-ea9b-4899-8069-e0e3048e911d.sketch_text.stroke-116"),sQuery(id+"FHMxAyK4CFUKdhS_1.wireOp",EDGE,"1cb9c079-ea9b-4899-8069-e0e3048e911d.sketch_text.stroke-117"),sQuery(id+"FHMxAyK4CFUKdhS_1.wireOp",EDGE,"1cb9c079-ea9b-4899-8069-e0e3048e911d.sketch_text.stroke-118"),sQuery(id+"FHMxAyK4CFUKdhS_1.wireOp",EDGE,"1cb9c079-ea9b-4899-8069-e0e3048e911d.sketch_text.stroke-119"),sQuery(id+"FHMxAyK4CFUKdhS_1.wireOp",EDGE,"1cb9c079-ea9b-4899-8069-e0e3048e911d.sketch_text.stroke-120"),sQuery(id+"FHMxAyK4CFUKdhS_1.wireOp",EDGE,"1cb9c079-ea9b-4899-8069-e0e3048e911d.sketch_text.stroke-121"),sQuery(id+"FHMxAyK4CFUKdhS_1.wireOp",EDGE,"1cb9c079-ea9b-4899-8069-e0e3048e911d.sketch_text.stroke-122"),sQuery(id+"FHMxAyK4CFUKdhS_1.wireOp",EDGE,"1cb9c079-ea9b-4899-8069-e0e3048e911d.sketch_text.stroke-123"),sQuery(id+"FHMxAyK4CFUKdhS_1.wireOp",EDGE,"1cb9c079-ea9b-4899-8069-e0e3048e911d.sketch_text.stroke-124"),sQuery(id+"FHMxAyK4CFUKdhS_1.wireOp",EDGE,"1cb9c079-ea9b-4899-8069-e0e3048e911d.sketch_text.stroke-125"),sQuery(id+"FHMxAyK4CFUKdhS_1.wireOp",EDGE,"1cb9c079-ea9b-4899-8069-e0e3048e911d.sketch_text.stroke-126"),sQuery(id+"FHMxAyK4CFUKdhS_1.wireOp",EDGE,"1cb9c079-ea9b-4899-8069-e0e3048e911d.sketch_text.stroke-127"),sQuery(id+"FHMxAyK4CFUKdhS_1.wireOp",EDGE,"1cb9c079-ea9b-4899-8069-e0e3048e911d.sketch_text.stroke-128"),sQuery(id+"FHMxAyK4CFUKdhS_1.wireOp",EDGE,"1cb9c079-ea9b-4899-8069-e0e3048e911d.sketch_text.stroke-129"),sQuery(id+"FHMxAyK4CFUKdhS_1.wireOp",EDGE,"1cb9c079-ea9b-4899-8069-e0e3048e911d.sketch_text.stroke-130"),sQuery(id+"FHMxAyK4CFUKdhS_1.wireOp",EDGE,"1cb9c079-ea9b-4899-8069-e0e3048e911d.sketch_text.stroke-131"),sQuery(id+"FHMxAyK4CFUKdhS_1.wireOp",EDGE,"1cb9c079-ea9b-4899-8069-e0e3048e911d.sketch_text.stroke-132"),sQuery(id+"FHMxAyK4CFUKdhS_1.wireOp",EDGE,"1cb9c079-ea9b-4899-8069-e0e3048e911d.sketch_text.stroke-133"),sQuery(id+"FHMxAyK4CFUKdhS_1.wireOp",EDGE,"1cb9c079-ea9b-4899-8069-e0e3048e911d.sketch_text.stroke-134"),sQuery(id+"FHMxAyK4CFUKdhS_1.wireOp",EDGE,"1cb9c079-ea9b-4899-8069-e0e3048e911d.sketch_text.stroke-135"),sQuery(id+"FHMxAyK4CFUKdhS_1.wireOp",EDGE,"1cb9c079-ea9b-4899-8069-e0e3048e911d.sketch_text.stroke-136"),sQuery(id+"FHMxAyK4CFUKdhS_1.wireOp",EDGE,"1cb9c079-ea9b-4899-8069-e0e3048e911d.sketch_text.stroke-137"),sQuery(id+"FHMxAyK4CFUKdhS_1.wireOp",EDGE,"1cb9c079-ea9b-4899-8069-e0e3048e911d.sketch_text.stroke-138"),sQuery(id+"FHMxAyK4CFUKdhS_1.wireOp",EDGE,"1cb9c079-ea9b-4899-8069-e0e3048e911d.sketch_text.stroke-139"),sQuery(id+"FHMxAyK4CFUKdhS_1.wireOp",EDGE,"1cb9c079-ea9b-4899-8069-e0e3048e911d.sketch_text.stroke-140"),sQuery(id+"FHMxAyK4CFUKdhS_1.wireOp",EDGE,"1cb9c079-ea9b-4899-8069-e0e3048e911d.sketch_text.stroke-141"),sQuery(id+"FHMxAyK4CFUKdhS_1.wireOp",EDGE,"1cb9c079-ea9b-4899-8069-e0e3048e911d.sketch_text.stroke-142"),sQuery(id+"FHMxAyK4CFUKdhS_1.wireOp",EDGE,"1cb9c079-ea9b-4899-8069-e0e3048e911d.sketch_text.stroke-143"),sQuery(id+"FHMxAyK4CFUKdhS_1.wireOp",EDGE,"1cb9c079-ea9b-4899-8069-e0e3048e911d.sketch_text.stroke-144"),sQuery(id+"FHMxAyK4CFUKdhS_1.wireOp",EDGE,"1cb9c079-ea9b-4899-8069-e0e3048e911d.sketch_text.stroke-145"),sQuery(id+"FHMxAyK4CFUKdhS_1.wireOp",EDGE,"1cb9c079-ea9b-4899-8069-e0e3048e911d.sketch_text.stroke-146"),sQuery(id+"FHMxAyK4CFUKdhS_1.wireOp",EDGE,"1cb9c079-ea9b-4899-8069-e0e3048e911d.sketch_text.stroke-147"),sQuery(id+"FHMxAyK4CFUKdhS_1.wireOp",EDGE,"1cb9c079-ea9b-4899-8069-e0e3048e911d.sketch_text.stroke-148"),sQuery(id+"FHMxAyK4CFUKdhS_1.wireOp",EDGE,"1cb9c079-ea9b-4899-8069-e0e3048e911d.sketch_text.stroke-149"),sQuery(id+"FHMxAyK4CFUKdhS_1.wireOp",EDGE,"1cb9c079-ea9b-4899-8069-e0e3048e911d.sketch_text.stroke-150"),sQuery(id+"FHMxAyK4CFUKdhS_1.wireOp",EDGE,"1cb9c079-ea9b-4899-8069-e0e3048e911d.sketch_text.stroke-151"),sQuery(id+"FHMxAyK4CFUKdhS_1.wireOp",EDGE,"1cb9c079-ea9b-4899-8069-e0e3048e911d.sketch_text.stroke-152"),sQuery(id+"FHMxAyK4CFUKdhS_1.wireOp",EDGE,"1cb9c079-ea9b-4899-8069-e0e3048e911d.sketch_text.stroke-153"),sQuery(id+"FHMxAyK4CFUKdhS_1.wireOp",EDGE,"1cb9c079-ea9b-4899-8069-e0e3048e911d.sketch_text.stroke-159"),sQuery(id+"FHMxAyK4CFUKdhS_1.wireOp",EDGE,"1cb9c079-ea9b-4899-8069-e0e3048e911d.sketch_text.stroke-160"),sQuery(id+"FHMxAyK4CFUKdhS_1.wireOp",EDGE,"1cb9c079-ea9b-4899-8069-e0e3048e911d.sketch_text.stroke-161"),sQuery(id+"FHMxAyK4CFUKdhS_1.wireOp",EDGE,"1cb9c079-ea9b-4899-8069-e0e3048e911d.sketch_text.stroke-162"),sQuery(id+"FHMxAyK4CFUKdhS_1.wireOp",EDGE,"1cb9c079-ea9b-4899-8069-e0e3048e911d.sketch_text.stroke-163"),sQuery(id+"FHMxAyK4CFUKdhS_1.wireOp",EDGE,"1cb9c079-ea9b-4899-8069-e0e3048e911d.sketch_text.stroke-164"),sQuery(id+"FHMxAyK4CFUKdhS_1.wireOp",EDGE,"1cb9c079-ea9b-4899-8069-e0e3048e911d.sketch_text.stroke-165"),sQuery(id+"FHMxAyK4CFUKdhS_1.wireOp",EDGE,"1cb9c079-ea9b-4899-8069-e0e3048e911d.sketch_text.stroke-166"),sQuery(id+"FHMxAyK4CFUKdhS_1.wireOp",EDGE,"1cb9c079-ea9b-4899-8069-e0e3048e911d.sketch_text.stroke-167"),sQuery(id+"FHMxAyK4CFUKdhS_1.wireOp",EDGE,"1cb9c079-ea9b-4899-8069-e0e3048e911d.sketch_text.stroke-168"),sQuery(id+"FHMxAyK4CFUKdhS_1.wireOp",EDGE,"1cb9c079-ea9b-4899-8069-e0e3048e911d.sketch_text.stroke-169"),sQuery(id+"FHMxAyK4CFUKdhS_1.wireOp",EDGE,"1cb9c079-ea9b-4899-8069-e0e3048e911d.sketch_text.stroke-170"),sQuery(id+"FHMxAyK4CFUKdhS_1.wireOp",EDGE,"1cb9c079-ea9b-4899-8069-e0e3048e911d.sketch_text.stroke-171"),sQuery(id+"FHMxAyK4CFUKdhS_1.wireOp",EDGE,"1cb9c079-ea9b-4899-8069-e0e3048e911d.sketch_text.stroke-172"),sQuery(id+"FHMxAyK4CFUKdhS_1.wireOp",EDGE,"1cb9c079-ea9b-4899-8069-e0e3048e911d.sketch_text.stroke-173"),sQuery(id+"FHMxAyK4CFUKdhS_1.wireOp",EDGE,"1cb9c079-ea9b-4899-8069-e0e3048e911d.sketch_text.stroke-174"),sQuery(id+"FHMxAyK4CFUKdhS_1.wireOp",EDGE,"1cb9c079-ea9b-4899-8069-e0e3048e911d.sketch_text.stroke-175"),sQuery(id+"FHMxAyK4CFUKdhS_1.wireOp",EDGE,"1cb9c079-ea9b-4899-8069-e0e3048e911d.sketch_text.stroke-176"),sQuery(id+"FHMxAyK4CFUKdhS_1.wireOp",EDGE,"1cb9c079-ea9b-4899-8069-e0e3048e911d.sketch_text.stroke-177"),sQuery(id+"FHMxAyK4CFUKdhS_1.wireOp",EDGE,"1cb9c079-ea9b-4899-8069-e0e3048e911d.sketch_text.stroke-178"),sQuery(id+"FHMxAyK4CFUKdhS_1.wireOp",EDGE,"1cb9c079-ea9b-4899-8069-e0e3048e911d.sketch_text.stroke-179"),sQuery(id+"FHMxAyK4CFUKdhS_1.wireOp",EDGE,"1cb9c079-ea9b-4899-8069-e0e3048e911d.sketch_text.stroke-180"),subQ0,subQ2])],"isStart":true}),makeQuery(id+"F3.opExtrude","SWEPT_FACE",FACE,{"disambiguationData":[OSD([subQ2])]})])],"derivedFrom":makeQuery(id+"F3.opExtrude","CAP_EDGE",EDGE,{"disambiguationData":[OSD([subQ0])],"isStart":true})});}
            var Q22;
            {var subQ0=sQuery(id+"F2.wireOp",EDGE,"E26");var subQ1=sQuery(id+"F0.wireOp",EDGE,"E0.top");var subQ2=sQuery(id+"F2.wireOp",EDGE,"E27");var subQ3=sQuery(id+"F0.wireOp",EDGE,"E0.bottom");Q22=makeQuery(id+"F3.boolean.opBoolean","SPLIT",EDGE,{"disambiguationData":[TD([makeQuery(id+"F1.opExtrude","CAP_FACE",FACE,{"disambiguationData":[OSD([subQ3,subQ1,sQuery(id+"F0.wireOp",EDGE,"E0.left"),sQuery(id+"F0.wireOp",EDGE,"E0.right")])],"isStart":false}),makeQuery(id+"F1.opExtrude","SWEPT_FACE",FACE,{"disambiguationData":[OSD([subQ1])]}),makeQuery(id+"F3.opExtrude","SWEPT_FACE",FACE,{"disambiguationData":[OSD([subQ0])]}),makeQuery(id+"F3.opExtrude","CAP_FACE",FACE,{"disambiguationData":[OSD([subQ3,sQuery(id+"FQ5JFwxVdaqARUP_1.wireOp",EDGE,"fcba4419-a2ee-464f-be9d-58f11bf3418b.sketch_text.stroke-0"),sQuery(id+"FQ5JFwxVdaqARUP_1.wireOp",EDGE,"fcba4419-a2ee-464f-be9d-58f11bf3418b.sketch_text.stroke-1"),sQuery(id+"FQ5JFwxVdaqARUP_1.wireOp",EDGE,"fcba4419-a2ee-464f-be9d-58f11bf3418b.sketch_text.stroke-2"),sQuery(id+"FQ5JFwxVdaqARUP_1.wireOp",EDGE,"fcba4419-a2ee-464f-be9d-58f11bf3418b.sketch_text.stroke-3"),sQuery(id+"FQ5JFwxVdaqARUP_1.wireOp",EDGE,"fcba4419-a2ee-464f-be9d-58f11bf3418b.sketch_text.stroke-4"),sQuery(id+"FQ5JFwxVdaqARUP_1.wireOp",EDGE,"fcba4419-a2ee-464f-be9d-58f11bf3418b.sketch_text.stroke-5"),sQuery(id+"FQ5JFwxVdaqARUP_1.wireOp",EDGE,"fcba4419-a2ee-464f-be9d-58f11bf3418b.sketch_text.stroke-6"),sQuery(id+"FQ5JFwxVdaqARUP_1.wireOp",EDGE,"fcba4419-a2ee-464f-be9d-58f11bf3418b.sketch_text.stroke-7"),sQuery(id+"FQ5JFwxVdaqARUP_1.wireOp",EDGE,"fcba4419-a2ee-464f-be9d-58f11bf3418b.sketch_text.stroke-8"),sQuery(id+"FQ5JFwxVdaqARUP_1.wireOp",EDGE,"fcba4419-a2ee-464f-be9d-58f11bf3418b.sketch_text.stroke-9"),sQuery(id+"FQ5JFwxVdaqARUP_1.wireOp",EDGE,"fcba4419-a2ee-464f-be9d-58f11bf3418b.sketch_text.stroke-10"),sQuery(id+"FQ5JFwxVdaqARUP_1.wireOp",EDGE,"fcba4419-a2ee-464f-be9d-58f11bf3418b.sketch_text.stroke-11"),sQuery(id+"FQ5JFwxVdaqARUP_1.wireOp",EDGE,"fcba4419-a2ee-464f-be9d-58f11bf3418b.sketch_text.stroke-12"),sQuery(id+"FQ5JFwxVdaqARUP_1.wireOp",EDGE,"fcba4419-a2ee-464f-be9d-58f11bf3418b.sketch_text.stroke-13"),sQuery(id+"FQ5JFwxVdaqARUP_1.wireOp",EDGE,"fcba4419-a2ee-464f-be9d-58f11bf3418b.sketch_text.stroke-14"),sQuery(id+"FQ5JFwxVdaqARUP_1.wireOp",EDGE,"fcba4419-a2ee-464f-be9d-58f11bf3418b.sketch_text.stroke-15"),sQuery(id+"FQ5JFwxVdaqARUP_1.wireOp",EDGE,"fcba4419-a2ee-464f-be9d-58f11bf3418b.sketch_text.stroke-16"),sQuery(id+"FQ5JFwxVdaqARUP_1.wireOp",EDGE,"fcba4419-a2ee-464f-be9d-58f11bf3418b.sketch_text.stroke-17"),sQuery(id+"FQ5JFwxVdaqARUP_1.wireOp",EDGE,"fcba4419-a2ee-464f-be9d-58f11bf3418b.sketch_text.stroke-18"),sQuery(id+"FQ5JFwxVdaqARUP_1.wireOp",EDGE,"fcba4419-a2ee-464f-be9d-58f11bf3418b.sketch_text.stroke-19"),sQuery(id+"FQ5JFwxVdaqARUP_1.wireOp",EDGE,"fcba4419-a2ee-464f-be9d-58f11bf3418b.sketch_text.stroke-20"),sQuery(id+"FQ5JFwxVdaqARUP_1.wireOp",EDGE,"fcba4419-a2ee-464f-be9d-58f11bf3418b.sketch_text.stroke-21"),sQuery(id+"FQ5JFwxVdaqARUP_1.wireOp",EDGE,"fcba4419-a2ee-464f-be9d-58f11bf3418b.sketch_text.stroke-22"),sQuery(id+"FQ5JFwxVdaqARUP_1.wireOp",EDGE,"fcba4419-a2ee-464f-be9d-58f11bf3418b.sketch_text.stroke-23"),sQuery(id+"FQ5JFwxVdaqARUP_1.wireOp",EDGE,"fcba4419-a2ee-464f-be9d-58f11bf3418b.sketch_text.stroke-24"),sQuery(id+"FQ5JFwxVdaqARUP_1.wireOp",EDGE,"fcba4419-a2ee-464f-be9d-58f11bf3418b.sketch_text.stroke-25"),sQuery(id+"FQ5JFwxVdaqARUP_1.wireOp",EDGE,"fcba4419-a2ee-464f-be9d-58f11bf3418b.sketch_text.stroke-26"),sQuery(id+"FQ5JFwxVdaqARUP_1.wireOp",EDGE,"fcba4419-a2ee-464f-be9d-58f11bf3418b.sketch_text.stroke-27"),sQuery(id+"FQ5JFwxVdaqARUP_1.wireOp",EDGE,"fcba4419-a2ee-464f-be9d-58f11bf3418b.sketch_text.stroke-28"),sQuery(id+"FQ5JFwxVdaqARUP_1.wireOp",EDGE,"fcba4419-a2ee-464f-be9d-58f11bf3418b.sketch_text.stroke-29"),sQuery(id+"FQ5JFwxVdaqARUP_1.wireOp",EDGE,"fcba4419-a2ee-464f-be9d-58f11bf3418b.sketch_text.stroke-30"),sQuery(id+"FQ5JFwxVdaqARUP_1.wireOp",EDGE,"fcba4419-a2ee-464f-be9d-58f11bf3418b.sketch_text.stroke-31"),sQuery(id+"FQ5JFwxVdaqARUP_1.wireOp",EDGE,"fcba4419-a2ee-464f-be9d-58f11bf3418b.sketch_text.stroke-32"),sQuery(id+"FQ5JFwxVdaqARUP_1.wireOp",EDGE,"fcba4419-a2ee-464f-be9d-58f11bf3418b.sketch_text.stroke-33"),sQuery(id+"FQ5JFwxVdaqARUP_1.wireOp",EDGE,"fcba4419-a2ee-464f-be9d-58f11bf3418b.sketch_text.stroke-34"),sQuery(id+"FQ5JFwxVdaqARUP_1.wireOp",EDGE,"fcba4419-a2ee-464f-be9d-58f11bf3418b.sketch_text.stroke-35"),sQuery(id+"FQ5JFwxVdaqARUP_1.wireOp",EDGE,"fcba4419-a2ee-464f-be9d-58f11bf3418b.sketch_text.stroke-36"),sQuery(id+"FQ5JFwxVdaqARUP_1.wireOp",EDGE,"fcba4419-a2ee-464f-be9d-58f11bf3418b.sketch_text.stroke-37"),sQuery(id+"FQ5JFwxVdaqARUP_1.wireOp",EDGE,"fcba4419-a2ee-464f-be9d-58f11bf3418b.sketch_text.stroke-38"),sQuery(id+"FQ5JFwxVdaqARUP_1.wireOp",EDGE,"fcba4419-a2ee-464f-be9d-58f11bf3418b.sketch_text.stroke-39"),sQuery(id+"FQ5JFwxVdaqARUP_1.wireOp",EDGE,"fcba4419-a2ee-464f-be9d-58f11bf3418b.sketch_text.stroke-40"),sQuery(id+"FQ5JFwxVdaqARUP_1.wireOp",EDGE,"fcba4419-a2ee-464f-be9d-58f11bf3418b.sketch_text.stroke-41"),sQuery(id+"FQ5JFwxVdaqARUP_1.wireOp",EDGE,"fcba4419-a2ee-464f-be9d-58f11bf3418b.sketch_text.stroke-42"),sQuery(id+"FQ5JFwxVdaqARUP_1.wireOp",EDGE,"fcba4419-a2ee-464f-be9d-58f11bf3418b.sketch_text.stroke-43"),sQuery(id+"FQ5JFwxVdaqARUP_1.wireOp",EDGE,"fcba4419-a2ee-464f-be9d-58f11bf3418b.sketch_text.stroke-44"),sQuery(id+"FQ5JFwxVdaqARUP_1.wireOp",EDGE,"fcba4419-a2ee-464f-be9d-58f11bf3418b.sketch_text.stroke-45"),sQuery(id+"FQ5JFwxVdaqARUP_1.wireOp",EDGE,"fcba4419-a2ee-464f-be9d-58f11bf3418b.sketch_text.stroke-46"),sQuery(id+"FQ5JFwxVdaqARUP_1.wireOp",EDGE,"fcba4419-a2ee-464f-be9d-58f11bf3418b.sketch_text.stroke-47"),sQuery(id+"FQ5JFwxVdaqARUP_1.wireOp",EDGE,"fcba4419-a2ee-464f-be9d-58f11bf3418b.sketch_text.stroke-48"),sQuery(id+"FQ5JFwxVdaqARUP_1.wireOp",EDGE,"fcba4419-a2ee-464f-be9d-58f11bf3418b.sketch_text.stroke-49"),sQuery(id+"FQ5JFwxVdaqARUP_1.wireOp",EDGE,"fcba4419-a2ee-464f-be9d-58f11bf3418b.sketch_text.stroke-50"),sQuery(id+"FQ5JFwxVdaqARUP_1.wireOp",EDGE,"fcba4419-a2ee-464f-be9d-58f11bf3418b.sketch_text.stroke-51"),sQuery(id+"FQ5JFwxVdaqARUP_1.wireOp",EDGE,"fcba4419-a2ee-464f-be9d-58f11bf3418b.sketch_text.stroke-52"),sQuery(id+"FQ5JFwxVdaqARUP_1.wireOp",EDGE,"fcba4419-a2ee-464f-be9d-58f11bf3418b.sketch_text.stroke-53"),sQuery(id+"FQ5JFwxVdaqARUP_1.wireOp",EDGE,"fcba4419-a2ee-464f-be9d-58f11bf3418b.sketch_text.stroke-54"),sQuery(id+"FQ5JFwxVdaqARUP_1.wireOp",EDGE,"fcba4419-a2ee-464f-be9d-58f11bf3418b.sketch_text.stroke-55"),sQuery(id+"FQ5JFwxVdaqARUP_1.wireOp",EDGE,"fcba4419-a2ee-464f-be9d-58f11bf3418b.sketch_text.stroke-56"),sQuery(id+"FQ5JFwxVdaqARUP_1.wireOp",EDGE,"fcba4419-a2ee-464f-be9d-58f11bf3418b.sketch_text.stroke-57"),sQuery(id+"FQ5JFwxVdaqARUP_1.wireOp",EDGE,"fcba4419-a2ee-464f-be9d-58f11bf3418b.sketch_text.stroke-58"),sQuery(id+"FQ5JFwxVdaqARUP_1.wireOp",EDGE,"fcba4419-a2ee-464f-be9d-58f11bf3418b.sketch_text.stroke-59"),sQuery(id+"FQ5JFwxVdaqARUP_1.wireOp",EDGE,"fcba4419-a2ee-464f-be9d-58f11bf3418b.sketch_text.stroke-60"),sQuery(id+"FQ5JFwxVdaqARUP_1.wireOp",EDGE,"fcba4419-a2ee-464f-be9d-58f11bf3418b.sketch_text.stroke-61"),sQuery(id+"FQ5JFwxVdaqARUP_1.wireOp",EDGE,"fcba4419-a2ee-464f-be9d-58f11bf3418b.sketch_text.stroke-62"),sQuery(id+"FQ5JFwxVdaqARUP_1.wireOp",EDGE,"fcba4419-a2ee-464f-be9d-58f11bf3418b.sketch_text.stroke-63"),sQuery(id+"FQ5JFwxVdaqARUP_1.wireOp",EDGE,"fcba4419-a2ee-464f-be9d-58f11bf3418b.sketch_text.stroke-64"),sQuery(id+"FQ5JFwxVdaqARUP_1.wireOp",EDGE,"fcba4419-a2ee-464f-be9d-58f11bf3418b.sketch_text.stroke-65"),sQuery(id+"FQ5JFwxVdaqARUP_1.wireOp",EDGE,"fcba4419-a2ee-464f-be9d-58f11bf3418b.sketch_text.stroke-66"),sQuery(id+"FQ5JFwxVdaqARUP_1.wireOp",EDGE,"fcba4419-a2ee-464f-be9d-58f11bf3418b.sketch_text.stroke-67"),sQuery(id+"FQ5JFwxVdaqARUP_1.wireOp",EDGE,"fcba4419-a2ee-464f-be9d-58f11bf3418b.sketch_text.stroke-68"),sQuery(id+"FQ5JFwxVdaqARUP_1.wireOp",EDGE,"fcba4419-a2ee-464f-be9d-58f11bf3418b.sketch_text.stroke-69"),sQuery(id+"FQ5JFwxVdaqARUP_1.wireOp",EDGE,"fcba4419-a2ee-464f-be9d-58f11bf3418b.sketch_text.stroke-70"),sQuery(id+"FQ5JFwxVdaqARUP_1.wireOp",EDGE,"fcba4419-a2ee-464f-be9d-58f11bf3418b.sketch_text.stroke-71"),sQuery(id+"FQ5JFwxVdaqARUP_1.wireOp",EDGE,"fcba4419-a2ee-464f-be9d-58f11bf3418b.sketch_text.stroke-72"),sQuery(id+"FQ5JFwxVdaqARUP_1.wireOp",EDGE,"fcba4419-a2ee-464f-be9d-58f11bf3418b.sketch_text.stroke-73"),sQuery(id+"FQ5JFwxVdaqARUP_1.wireOp",EDGE,"fcba4419-a2ee-464f-be9d-58f11bf3418b.sketch_text.stroke-74"),sQuery(id+"FQ5JFwxVdaqARUP_1.wireOp",EDGE,"fcba4419-a2ee-464f-be9d-58f11bf3418b.sketch_text.stroke-75"),sQuery(id+"FQ5JFwxVdaqARUP_1.wireOp",EDGE,"fcba4419-a2ee-464f-be9d-58f11bf3418b.sketch_text.stroke-76"),sQuery(id+"FQ5JFwxVdaqARUP_1.wireOp",EDGE,"fcba4419-a2ee-464f-be9d-58f11bf3418b.sketch_text.stroke-77"),sQuery(id+"FQ5JFwxVdaqARUP_1.wireOp",EDGE,"fcba4419-a2ee-464f-be9d-58f11bf3418b.sketch_text.stroke-78"),sQuery(id+"FQ5JFwxVdaqARUP_1.wireOp",EDGE,"fcba4419-a2ee-464f-be9d-58f11bf3418b.sketch_text.stroke-79"),sQuery(id+"FQ5JFwxVdaqARUP_1.wireOp",EDGE,"fcba4419-a2ee-464f-be9d-58f11bf3418b.sketch_text.stroke-80"),sQuery(id+"FQ5JFwxVdaqARUP_1.wireOp",EDGE,"fcba4419-a2ee-464f-be9d-58f11bf3418b.sketch_text.stroke-81"),sQuery(id+"FQ5JFwxVdaqARUP_1.wireOp",EDGE,"fcba4419-a2ee-464f-be9d-58f11bf3418b.sketch_text.stroke-82"),sQuery(id+"FQ5JFwxVdaqARUP_1.wireOp",EDGE,"fcba4419-a2ee-464f-be9d-58f11bf3418b.sketch_text.stroke-83"),sQuery(id+"FQ5JFwxVdaqARUP_1.wireOp",EDGE,"fcba4419-a2ee-464f-be9d-58f11bf3418b.sketch_text.stroke-84"),sQuery(id+"FQ5JFwxVdaqARUP_1.wireOp",EDGE,"fcba4419-a2ee-464f-be9d-58f11bf3418b.sketch_text.stroke-85"),sQuery(id+"FQ5JFwxVdaqARUP_1.wireOp",EDGE,"fcba4419-a2ee-464f-be9d-58f11bf3418b.sketch_text.stroke-86"),sQuery(id+"FQ5JFwxVdaqARUP_1.wireOp",EDGE,"fcba4419-a2ee-464f-be9d-58f11bf3418b.sketch_text.stroke-87"),sQuery(id+"FQ5JFwxVdaqARUP_1.wireOp",EDGE,"fcba4419-a2ee-464f-be9d-58f11bf3418b.sketch_text.stroke-88"),sQuery(id+"FQ5JFwxVdaqARUP_1.wireOp",EDGE,"fcba4419-a2ee-464f-be9d-58f11bf3418b.sketch_text.stroke-89"),sQuery(id+"FQ5JFwxVdaqARUP_1.wireOp",EDGE,"fcba4419-a2ee-464f-be9d-58f11bf3418b.sketch_text.stroke-90"),sQuery(id+"FQ5JFwxVdaqARUP_1.wireOp",EDGE,"fcba4419-a2ee-464f-be9d-58f11bf3418b.sketch_text.stroke-91"),sQuery(id+"FQ5JFwxVdaqARUP_1.wireOp",EDGE,"fcba4419-a2ee-464f-be9d-58f11bf3418b.sketch_text.stroke-92"),sQuery(id+"FQ5JFwxVdaqARUP_1.wireOp",EDGE,"fcba4419-a2ee-464f-be9d-58f11bf3418b.sketch_text.stroke-93"),sQuery(id+"FQ5JFwxVdaqARUP_1.wireOp",EDGE,"fcba4419-a2ee-464f-be9d-58f11bf3418b.sketch_text.stroke-94"),sQuery(id+"FQ5JFwxVdaqARUP_1.wireOp",EDGE,"fcba4419-a2ee-464f-be9d-58f11bf3418b.sketch_text.stroke-95"),sQuery(id+"FQ5JFwxVdaqARUP_1.wireOp",EDGE,"fcba4419-a2ee-464f-be9d-58f11bf3418b.sketch_text.stroke-96"),sQuery(id+"FQ5JFwxVdaqARUP_1.wireOp",EDGE,"fcba4419-a2ee-464f-be9d-58f11bf3418b.sketch_text.stroke-97"),sQuery(id+"FQ5JFwxVdaqARUP_1.wireOp",EDGE,"fcba4419-a2ee-464f-be9d-58f11bf3418b.sketch_text.stroke-98"),sQuery(id+"FQ5JFwxVdaqARUP_1.wireOp",EDGE,"fcba4419-a2ee-464f-be9d-58f11bf3418b.sketch_text.stroke-99"),sQuery(id+"FQ5JFwxVdaqARUP_1.wireOp",EDGE,"fcba4419-a2ee-464f-be9d-58f11bf3418b.sketch_text.stroke-100"),sQuery(id+"FQ5JFwxVdaqARUP_1.wireOp",EDGE,"fcba4419-a2ee-464f-be9d-58f11bf3418b.sketch_text.stroke-101"),sQuery(id+"FQ5JFwxVdaqARUP_1.wireOp",EDGE,"fcba4419-a2ee-464f-be9d-58f11bf3418b.sketch_text.stroke-102"),sQuery(id+"FQ5JFwxVdaqARUP_1.wireOp",EDGE,"fcba4419-a2ee-464f-be9d-58f11bf3418b.sketch_text.stroke-103"),sQuery(id+"FQ5JFwxVdaqARUP_1.wireOp",EDGE,"fcba4419-a2ee-464f-be9d-58f11bf3418b.sketch_text.stroke-104"),sQuery(id+"FQ5JFwxVdaqARUP_1.wireOp",EDGE,"fcba4419-a2ee-464f-be9d-58f11bf3418b.sketch_text.stroke-105"),sQuery(id+"FQ5JFwxVdaqARUP_1.wireOp",EDGE,"fcba4419-a2ee-464f-be9d-58f11bf3418b.sketch_text.stroke-106"),sQuery(id+"FQ5JFwxVdaqARUP_1.wireOp",EDGE,"fcba4419-a2ee-464f-be9d-58f11bf3418b.sketch_text.stroke-107"),sQuery(id+"FQ5JFwxVdaqARUP_1.wireOp",EDGE,"fcba4419-a2ee-464f-be9d-58f11bf3418b.sketch_text.stroke-108"),sQuery(id+"FQ5JFwxVdaqARUP_1.wireOp",EDGE,"fcba4419-a2ee-464f-be9d-58f11bf3418b.sketch_text.stroke-109"),sQuery(id+"FQ5JFwxVdaqARUP_1.wireOp",EDGE,"fcba4419-a2ee-464f-be9d-58f11bf3418b.sketch_text.stroke-110"),sQuery(id+"FQ5JFwxVdaqARUP_1.wireOp",EDGE,"fcba4419-a2ee-464f-be9d-58f11bf3418b.sketch_text.stroke-111"),sQuery(id+"FQ5JFwxVdaqARUP_1.wireOp",EDGE,"fcba4419-a2ee-464f-be9d-58f11bf3418b.sketch_text.stroke-112"),sQuery(id+"FQ5JFwxVdaqARUP_1.wireOp",EDGE,"fcba4419-a2ee-464f-be9d-58f11bf3418b.sketch_text.stroke-113"),sQuery(id+"FQ5JFwxVdaqARUP_1.wireOp",EDGE,"fcba4419-a2ee-464f-be9d-58f11bf3418b.sketch_text.stroke-114"),sQuery(id+"FQ5JFwxVdaqARUP_1.wireOp",EDGE,"fcba4419-a2ee-464f-be9d-58f11bf3418b.sketch_text.stroke-115"),sQuery(id+"FQ5JFwxVdaqARUP_1.wireOp",EDGE,"fcba4419-a2ee-464f-be9d-58f11bf3418b.sketch_text.stroke-116"),sQuery(id+"FQ5JFwxVdaqARUP_1.wireOp",EDGE,"fcba4419-a2ee-464f-be9d-58f11bf3418b.sketch_text.stroke-117"),sQuery(id+"FQ5JFwxVdaqARUP_1.wireOp",EDGE,"fcba4419-a2ee-464f-be9d-58f11bf3418b.sketch_text.stroke-118"),sQuery(id+"FQ5JFwxVdaqARUP_1.wireOp",EDGE,"fcba4419-a2ee-464f-be9d-58f11bf3418b.sketch_text.stroke-119"),sQuery(id+"FQ5JFwxVdaqARUP_1.wireOp",EDGE,"fcba4419-a2ee-464f-be9d-58f11bf3418b.sketch_text.stroke-120"),sQuery(id+"FQ5JFwxVdaqARUP_1.wireOp",EDGE,"fcba4419-a2ee-464f-be9d-58f11bf3418b.sketch_text.stroke-121"),sQuery(id+"FQ5JFwxVdaqARUP_1.wireOp",EDGE,"fcba4419-a2ee-464f-be9d-58f11bf3418b.sketch_text.stroke-122"),sQuery(id+"FQ5JFwxVdaqARUP_1.wireOp",EDGE,"fcba4419-a2ee-464f-be9d-58f11bf3418b.sketch_text.stroke-123"),sQuery(id+"FQ5JFwxVdaqARUP_1.wireOp",EDGE,"fcba4419-a2ee-464f-be9d-58f11bf3418b.sketch_text.stroke-124"),sQuery(id+"FQ5JFwxVdaqARUP_1.wireOp",EDGE,"fcba4419-a2ee-464f-be9d-58f11bf3418b.sketch_text.stroke-125"),sQuery(id+"FQ5JFwxVdaqARUP_1.wireOp",EDGE,"fcba4419-a2ee-464f-be9d-58f11bf3418b.sketch_text.stroke-126"),sQuery(id+"FQ5JFwxVdaqARUP_1.wireOp",EDGE,"fcba4419-a2ee-464f-be9d-58f11bf3418b.sketch_text.stroke-127"),sQuery(id+"FQ5JFwxVdaqARUP_1.wireOp",EDGE,"fcba4419-a2ee-464f-be9d-58f11bf3418b.sketch_text.stroke-128"),sQuery(id+"FQ5JFwxVdaqARUP_1.wireOp",EDGE,"fcba4419-a2ee-464f-be9d-58f11bf3418b.sketch_text.stroke-129"),sQuery(id+"FQ5JFwxVdaqARUP_1.wireOp",EDGE,"fcba4419-a2ee-464f-be9d-58f11bf3418b.sketch_text.stroke-130"),sQuery(id+"FQ5JFwxVdaqARUP_1.wireOp",EDGE,"fcba4419-a2ee-464f-be9d-58f11bf3418b.sketch_text.stroke-131"),sQuery(id+"FQ5JFwxVdaqARUP_1.wireOp",EDGE,"fcba4419-a2ee-464f-be9d-58f11bf3418b.sketch_text.stroke-132"),sQuery(id+"FQ5JFwxVdaqARUP_1.wireOp",EDGE,"fcba4419-a2ee-464f-be9d-58f11bf3418b.sketch_text.stroke-133"),sQuery(id+"FQ5JFwxVdaqARUP_1.wireOp",EDGE,"fcba4419-a2ee-464f-be9d-58f11bf3418b.sketch_text.stroke-134"),sQuery(id+"FQ5JFwxVdaqARUP_1.wireOp",EDGE,"fcba4419-a2ee-464f-be9d-58f11bf3418b.sketch_text.stroke-135"),sQuery(id+"FQ5JFwxVdaqARUP_1.wireOp",EDGE,"fcba4419-a2ee-464f-be9d-58f11bf3418b.sketch_text.stroke-136"),sQuery(id+"FQ5JFwxVdaqARUP_1.wireOp",EDGE,"fcba4419-a2ee-464f-be9d-58f11bf3418b.sketch_text.stroke-137"),sQuery(id+"FQ5JFwxVdaqARUP_1.wireOp",EDGE,"fcba4419-a2ee-464f-be9d-58f11bf3418b.sketch_text.stroke-138"),sQuery(id+"FQ5JFwxVdaqARUP_1.wireOp",EDGE,"fcba4419-a2ee-464f-be9d-58f11bf3418b.sketch_text.stroke-139"),sQuery(id+"FQ5JFwxVdaqARUP_1.wireOp",EDGE,"fcba4419-a2ee-464f-be9d-58f11bf3418b.sketch_text.stroke-140"),sQuery(id+"FQ5JFwxVdaqARUP_1.wireOp",EDGE,"fcba4419-a2ee-464f-be9d-58f11bf3418b.sketch_text.stroke-141"),sQuery(id+"FQ5JFwxVdaqARUP_1.wireOp",EDGE,"fcba4419-a2ee-464f-be9d-58f11bf3418b.sketch_text.stroke-142"),sQuery(id+"FQ5JFwxVdaqARUP_1.wireOp",EDGE,"fcba4419-a2ee-464f-be9d-58f11bf3418b.sketch_text.stroke-143"),sQuery(id+"FQ5JFwxVdaqARUP_1.wireOp",EDGE,"fcba4419-a2ee-464f-be9d-58f11bf3418b.sketch_text.stroke-144"),sQuery(id+"FQ5JFwxVdaqARUP_1.wireOp",EDGE,"fcba4419-a2ee-464f-be9d-58f11bf3418b.sketch_text.stroke-145"),sQuery(id+"FQ5JFwxVdaqARUP_1.wireOp",EDGE,"fcba4419-a2ee-464f-be9d-58f11bf3418b.sketch_text.stroke-146"),sQuery(id+"FQ5JFwxVdaqARUP_1.wireOp",EDGE,"fcba4419-a2ee-464f-be9d-58f11bf3418b.sketch_text.stroke-147"),sQuery(id+"FQ5JFwxVdaqARUP_1.wireOp",EDGE,"fcba4419-a2ee-464f-be9d-58f11bf3418b.sketch_text.stroke-148"),sQuery(id+"FQ5JFwxVdaqARUP_1.wireOp",EDGE,"fcba4419-a2ee-464f-be9d-58f11bf3418b.sketch_text.stroke-149"),sQuery(id+"FQ5JFwxVdaqARUP_1.wireOp",EDGE,"fcba4419-a2ee-464f-be9d-58f11bf3418b.sketch_text.stroke-150"),sQuery(id+"FQ5JFwxVdaqARUP_1.wireOp",EDGE,"fcba4419-a2ee-464f-be9d-58f11bf3418b.sketch_text.stroke-151"),sQuery(id+"FQ5JFwxVdaqARUP_1.wireOp",EDGE,"fcba4419-a2ee-464f-be9d-58f11bf3418b.sketch_text.stroke-152"),sQuery(id+"FQ5JFwxVdaqARUP_1.wireOp",EDGE,"fcba4419-a2ee-464f-be9d-58f11bf3418b.sketch_text.stroke-153"),sQuery(id+"FQ5JFwxVdaqARUP_1.wireOp",EDGE,"fcba4419-a2ee-464f-be9d-58f11bf3418b.sketch_text.stroke-154"),sQuery(id+"FQ5JFwxVdaqARUP_1.wireOp",EDGE,"fcba4419-a2ee-464f-be9d-58f11bf3418b.sketch_text.stroke-155"),sQuery(id+"FQ5JFwxVdaqARUP_1.wireOp",EDGE,"fcba4419-a2ee-464f-be9d-58f11bf3418b.sketch_text.stroke-156"),sQuery(id+"FQ5JFwxVdaqARUP_1.wireOp",EDGE,"fcba4419-a2ee-464f-be9d-58f11bf3418b.sketch_text.stroke-157"),sQuery(id+"FQ5JFwxVdaqARUP_1.wireOp",EDGE,"fcba4419-a2ee-464f-be9d-58f11bf3418b.sketch_text.stroke-158"),sQuery(id+"FQ5JFwxVdaqARUP_1.wireOp",EDGE,"fcba4419-a2ee-464f-be9d-58f11bf3418b.sketch_text.stroke-159"),sQuery(id+"FQ5JFwxVdaqARUP_1.wireOp",EDGE,"fcba4419-a2ee-464f-be9d-58f11bf3418b.sketch_text.stroke-160"),sQuery(id+"FQ5JFwxVdaqARUP_1.wireOp",EDGE,"fcba4419-a2ee-464f-be9d-58f11bf3418b.sketch_text.stroke-161"),sQuery(id+"FQ5JFwxVdaqARUP_1.wireOp",EDGE,"fcba4419-a2ee-464f-be9d-58f11bf3418b.sketch_text.stroke-162"),sQuery(id+"FQ5JFwxVdaqARUP_1.wireOp",EDGE,"fcba4419-a2ee-464f-be9d-58f11bf3418b.sketch_text.stroke-163"),sQuery(id+"FQ5JFwxVdaqARUP_1.wireOp",EDGE,"fcba4419-a2ee-464f-be9d-58f11bf3418b.sketch_text.stroke-164"),sQuery(id+"FQ5JFwxVdaqARUP_1.wireOp",EDGE,"fcba4419-a2ee-464f-be9d-58f11bf3418b.sketch_text.stroke-165"),sQuery(id+"FQ5JFwxVdaqARUP_1.wireOp",EDGE,"fcba4419-a2ee-464f-be9d-58f11bf3418b.sketch_text.stroke-166"),sQuery(id+"FQ5JFwxVdaqARUP_1.wireOp",EDGE,"fcba4419-a2ee-464f-be9d-58f11bf3418b.sketch_text.stroke-167"),sQuery(id+"FQ5JFwxVdaqARUP_1.wireOp",EDGE,"fcba4419-a2ee-464f-be9d-58f11bf3418b.sketch_text.stroke-168"),sQuery(id+"FQ5JFwxVdaqARUP_1.wireOp",EDGE,"fcba4419-a2ee-464f-be9d-58f11bf3418b.sketch_text.stroke-169"),sQuery(id+"FQ5JFwxVdaqARUP_1.wireOp",EDGE,"fcba4419-a2ee-464f-be9d-58f11bf3418b.sketch_text.stroke-170"),sQuery(id+"FQ5JFwxVdaqARUP_1.wireOp",EDGE,"fcba4419-a2ee-464f-be9d-58f11bf3418b.sketch_text.stroke-171"),sQuery(id+"FQ5JFwxVdaqARUP_1.wireOp",EDGE,"fcba4419-a2ee-464f-be9d-58f11bf3418b.sketch_text.stroke-172"),sQuery(id+"FQ5JFwxVdaqARUP_1.wireOp",EDGE,"fcba4419-a2ee-464f-be9d-58f11bf3418b.sketch_text.stroke-173"),sQuery(id+"FHMxAyK4CFUKdhS_1.wireOp",EDGE,"1cb9c079-ea9b-4899-8069-e0e3048e911d.sketch_text.stroke-0"),sQuery(id+"FHMxAyK4CFUKdhS_1.wireOp",EDGE,"1cb9c079-ea9b-4899-8069-e0e3048e911d.sketch_text.stroke-1"),sQuery(id+"FHMxAyK4CFUKdhS_1.wireOp",EDGE,"1cb9c079-ea9b-4899-8069-e0e3048e911d.sketch_text.stroke-2"),sQuery(id+"FHMxAyK4CFUKdhS_1.wireOp",EDGE,"1cb9c079-ea9b-4899-8069-e0e3048e911d.sketch_text.stroke-3"),sQuery(id+"FHMxAyK4CFUKdhS_1.wireOp",EDGE,"1cb9c079-ea9b-4899-8069-e0e3048e911d.sketch_text.stroke-4"),sQuery(id+"FHMxAyK4CFUKdhS_1.wireOp",EDGE,"1cb9c079-ea9b-4899-8069-e0e3048e911d.sketch_text.stroke-5"),sQuery(id+"FHMxAyK4CFUKdhS_1.wireOp",EDGE,"1cb9c079-ea9b-4899-8069-e0e3048e911d.sketch_text.stroke-6"),sQuery(id+"FHMxAyK4CFUKdhS_1.wireOp",EDGE,"1cb9c079-ea9b-4899-8069-e0e3048e911d.sketch_text.stroke-7"),sQuery(id+"FHMxAyK4CFUKdhS_1.wireOp",EDGE,"1cb9c079-ea9b-4899-8069-e0e3048e911d.sketch_text.stroke-8"),sQuery(id+"FHMxAyK4CFUKdhS_1.wireOp",EDGE,"1cb9c079-ea9b-4899-8069-e0e3048e911d.sketch_text.stroke-9"),sQuery(id+"FHMxAyK4CFUKdhS_1.wireOp",EDGE,"1cb9c079-ea9b-4899-8069-e0e3048e911d.sketch_text.stroke-10"),sQuery(id+"FHMxAyK4CFUKdhS_1.wireOp",EDGE,"1cb9c079-ea9b-4899-8069-e0e3048e911d.sketch_text.stroke-11"),sQuery(id+"FHMxAyK4CFUKdhS_1.wireOp",EDGE,"1cb9c079-ea9b-4899-8069-e0e3048e911d.sketch_text.stroke-12"),sQuery(id+"FHMxAyK4CFUKdhS_1.wireOp",EDGE,"1cb9c079-ea9b-4899-8069-e0e3048e911d.sketch_text.stroke-13"),sQuery(id+"FHMxAyK4CFUKdhS_1.wireOp",EDGE,"1cb9c079-ea9b-4899-8069-e0e3048e911d.sketch_text.stroke-14"),sQuery(id+"FHMxAyK4CFUKdhS_1.wireOp",EDGE,"1cb9c079-ea9b-4899-8069-e0e3048e911d.sketch_text.stroke-15"),sQuery(id+"FHMxAyK4CFUKdhS_1.wireOp",EDGE,"1cb9c079-ea9b-4899-8069-e0e3048e911d.sketch_text.stroke-16"),sQuery(id+"FHMxAyK4CFUKdhS_1.wireOp",EDGE,"1cb9c079-ea9b-4899-8069-e0e3048e911d.sketch_text.stroke-17"),sQuery(id+"FHMxAyK4CFUKdhS_1.wireOp",EDGE,"1cb9c079-ea9b-4899-8069-e0e3048e911d.sketch_text.stroke-18"),sQuery(id+"FHMxAyK4CFUKdhS_1.wireOp",EDGE,"1cb9c079-ea9b-4899-8069-e0e3048e911d.sketch_text.stroke-19"),sQuery(id+"FHMxAyK4CFUKdhS_1.wireOp",EDGE,"1cb9c079-ea9b-4899-8069-e0e3048e911d.sketch_text.stroke-20"),sQuery(id+"FHMxAyK4CFUKdhS_1.wireOp",EDGE,"1cb9c079-ea9b-4899-8069-e0e3048e911d.sketch_text.stroke-21"),sQuery(id+"FHMxAyK4CFUKdhS_1.wireOp",EDGE,"1cb9c079-ea9b-4899-8069-e0e3048e911d.sketch_text.stroke-22"),sQuery(id+"FHMxAyK4CFUKdhS_1.wireOp",EDGE,"1cb9c079-ea9b-4899-8069-e0e3048e911d.sketch_text.stroke-23"),sQuery(id+"FHMxAyK4CFUKdhS_1.wireOp",EDGE,"1cb9c079-ea9b-4899-8069-e0e3048e911d.sketch_text.stroke-24"),sQuery(id+"FHMxAyK4CFUKdhS_1.wireOp",EDGE,"1cb9c079-ea9b-4899-8069-e0e3048e911d.sketch_text.stroke-25"),sQuery(id+"FHMxAyK4CFUKdhS_1.wireOp",EDGE,"1cb9c079-ea9b-4899-8069-e0e3048e911d.sketch_text.stroke-26"),sQuery(id+"FHMxAyK4CFUKdhS_1.wireOp",EDGE,"1cb9c079-ea9b-4899-8069-e0e3048e911d.sketch_text.stroke-27"),sQuery(id+"FHMxAyK4CFUKdhS_1.wireOp",EDGE,"1cb9c079-ea9b-4899-8069-e0e3048e911d.sketch_text.stroke-28"),sQuery(id+"FHMxAyK4CFUKdhS_1.wireOp",EDGE,"1cb9c079-ea9b-4899-8069-e0e3048e911d.sketch_text.stroke-29"),sQuery(id+"FHMxAyK4CFUKdhS_1.wireOp",EDGE,"1cb9c079-ea9b-4899-8069-e0e3048e911d.sketch_text.stroke-30"),sQuery(id+"FHMxAyK4CFUKdhS_1.wireOp",EDGE,"1cb9c079-ea9b-4899-8069-e0e3048e911d.sketch_text.stroke-31"),sQuery(id+"FHMxAyK4CFUKdhS_1.wireOp",EDGE,"1cb9c079-ea9b-4899-8069-e0e3048e911d.sketch_text.stroke-32"),sQuery(id+"FHMxAyK4CFUKdhS_1.wireOp",EDGE,"1cb9c079-ea9b-4899-8069-e0e3048e911d.sketch_text.stroke-33"),sQuery(id+"FHMxAyK4CFUKdhS_1.wireOp",EDGE,"1cb9c079-ea9b-4899-8069-e0e3048e911d.sketch_text.stroke-34"),sQuery(id+"FHMxAyK4CFUKdhS_1.wireOp",EDGE,"1cb9c079-ea9b-4899-8069-e0e3048e911d.sketch_text.stroke-35"),sQuery(id+"FHMxAyK4CFUKdhS_1.wireOp",EDGE,"1cb9c079-ea9b-4899-8069-e0e3048e911d.sketch_text.stroke-36"),sQuery(id+"FHMxAyK4CFUKdhS_1.wireOp",EDGE,"1cb9c079-ea9b-4899-8069-e0e3048e911d.sketch_text.stroke-37"),sQuery(id+"FHMxAyK4CFUKdhS_1.wireOp",EDGE,"1cb9c079-ea9b-4899-8069-e0e3048e911d.sketch_text.stroke-38"),sQuery(id+"FHMxAyK4CFUKdhS_1.wireOp",EDGE,"1cb9c079-ea9b-4899-8069-e0e3048e911d.sketch_text.stroke-39"),sQuery(id+"FHMxAyK4CFUKdhS_1.wireOp",EDGE,"1cb9c079-ea9b-4899-8069-e0e3048e911d.sketch_text.stroke-40"),sQuery(id+"FHMxAyK4CFUKdhS_1.wireOp",EDGE,"1cb9c079-ea9b-4899-8069-e0e3048e911d.sketch_text.stroke-41"),sQuery(id+"FHMxAyK4CFUKdhS_1.wireOp",EDGE,"1cb9c079-ea9b-4899-8069-e0e3048e911d.sketch_text.stroke-42"),sQuery(id+"FHMxAyK4CFUKdhS_1.wireOp",EDGE,"1cb9c079-ea9b-4899-8069-e0e3048e911d.sketch_text.stroke-43"),sQuery(id+"FHMxAyK4CFUKdhS_1.wireOp",EDGE,"1cb9c079-ea9b-4899-8069-e0e3048e911d.sketch_text.stroke-44"),sQuery(id+"FHMxAyK4CFUKdhS_1.wireOp",EDGE,"1cb9c079-ea9b-4899-8069-e0e3048e911d.sketch_text.stroke-45"),sQuery(id+"FHMxAyK4CFUKdhS_1.wireOp",EDGE,"1cb9c079-ea9b-4899-8069-e0e3048e911d.sketch_text.stroke-46"),sQuery(id+"FHMxAyK4CFUKdhS_1.wireOp",EDGE,"1cb9c079-ea9b-4899-8069-e0e3048e911d.sketch_text.stroke-47"),sQuery(id+"FHMxAyK4CFUKdhS_1.wireOp",EDGE,"1cb9c079-ea9b-4899-8069-e0e3048e911d.sketch_text.stroke-48"),sQuery(id+"FHMxAyK4CFUKdhS_1.wireOp",EDGE,"1cb9c079-ea9b-4899-8069-e0e3048e911d.sketch_text.stroke-49"),sQuery(id+"FHMxAyK4CFUKdhS_1.wireOp",EDGE,"1cb9c079-ea9b-4899-8069-e0e3048e911d.sketch_text.stroke-50"),sQuery(id+"FHMxAyK4CFUKdhS_1.wireOp",EDGE,"1cb9c079-ea9b-4899-8069-e0e3048e911d.sketch_text.stroke-51"),sQuery(id+"FHMxAyK4CFUKdhS_1.wireOp",EDGE,"1cb9c079-ea9b-4899-8069-e0e3048e911d.sketch_text.stroke-52"),sQuery(id+"FHMxAyK4CFUKdhS_1.wireOp",EDGE,"1cb9c079-ea9b-4899-8069-e0e3048e911d.sketch_text.stroke-53"),sQuery(id+"FHMxAyK4CFUKdhS_1.wireOp",EDGE,"1cb9c079-ea9b-4899-8069-e0e3048e911d.sketch_text.stroke-54"),sQuery(id+"FHMxAyK4CFUKdhS_1.wireOp",EDGE,"1cb9c079-ea9b-4899-8069-e0e3048e911d.sketch_text.stroke-55"),sQuery(id+"FHMxAyK4CFUKdhS_1.wireOp",EDGE,"1cb9c079-ea9b-4899-8069-e0e3048e911d.sketch_text.stroke-56"),sQuery(id+"FHMxAyK4CFUKdhS_1.wireOp",EDGE,"1cb9c079-ea9b-4899-8069-e0e3048e911d.sketch_text.stroke-57"),sQuery(id+"FHMxAyK4CFUKdhS_1.wireOp",EDGE,"1cb9c079-ea9b-4899-8069-e0e3048e911d.sketch_text.stroke-58"),sQuery(id+"FHMxAyK4CFUKdhS_1.wireOp",EDGE,"1cb9c079-ea9b-4899-8069-e0e3048e911d.sketch_text.stroke-59"),sQuery(id+"FHMxAyK4CFUKdhS_1.wireOp",EDGE,"1cb9c079-ea9b-4899-8069-e0e3048e911d.sketch_text.stroke-60"),sQuery(id+"FHMxAyK4CFUKdhS_1.wireOp",EDGE,"1cb9c079-ea9b-4899-8069-e0e3048e911d.sketch_text.stroke-61"),sQuery(id+"FHMxAyK4CFUKdhS_1.wireOp",EDGE,"1cb9c079-ea9b-4899-8069-e0e3048e911d.sketch_text.stroke-62"),sQuery(id+"FHMxAyK4CFUKdhS_1.wireOp",EDGE,"1cb9c079-ea9b-4899-8069-e0e3048e911d.sketch_text.stroke-71"),sQuery(id+"FHMxAyK4CFUKdhS_1.wireOp",EDGE,"1cb9c079-ea9b-4899-8069-e0e3048e911d.sketch_text.stroke-72"),sQuery(id+"FHMxAyK4CFUKdhS_1.wireOp",EDGE,"1cb9c079-ea9b-4899-8069-e0e3048e911d.sketch_text.stroke-73"),sQuery(id+"FHMxAyK4CFUKdhS_1.wireOp",EDGE,"1cb9c079-ea9b-4899-8069-e0e3048e911d.sketch_text.stroke-74"),sQuery(id+"FHMxAyK4CFUKdhS_1.wireOp",EDGE,"1cb9c079-ea9b-4899-8069-e0e3048e911d.sketch_text.stroke-75"),sQuery(id+"FHMxAyK4CFUKdhS_1.wireOp",EDGE,"1cb9c079-ea9b-4899-8069-e0e3048e911d.sketch_text.stroke-76"),sQuery(id+"FHMxAyK4CFUKdhS_1.wireOp",EDGE,"1cb9c079-ea9b-4899-8069-e0e3048e911d.sketch_text.stroke-77"),sQuery(id+"FHMxAyK4CFUKdhS_1.wireOp",EDGE,"1cb9c079-ea9b-4899-8069-e0e3048e911d.sketch_text.stroke-78"),sQuery(id+"FHMxAyK4CFUKdhS_1.wireOp",EDGE,"1cb9c079-ea9b-4899-8069-e0e3048e911d.sketch_text.stroke-79"),sQuery(id+"FHMxAyK4CFUKdhS_1.wireOp",EDGE,"1cb9c079-ea9b-4899-8069-e0e3048e911d.sketch_text.stroke-80"),sQuery(id+"FHMxAyK4CFUKdhS_1.wireOp",EDGE,"1cb9c079-ea9b-4899-8069-e0e3048e911d.sketch_text.stroke-81"),sQuery(id+"FHMxAyK4CFUKdhS_1.wireOp",EDGE,"1cb9c079-ea9b-4899-8069-e0e3048e911d.sketch_text.stroke-82"),sQuery(id+"FHMxAyK4CFUKdhS_1.wireOp",EDGE,"1cb9c079-ea9b-4899-8069-e0e3048e911d.sketch_text.stroke-83"),sQuery(id+"FHMxAyK4CFUKdhS_1.wireOp",EDGE,"1cb9c079-ea9b-4899-8069-e0e3048e911d.sketch_text.stroke-84"),sQuery(id+"FHMxAyK4CFUKdhS_1.wireOp",EDGE,"1cb9c079-ea9b-4899-8069-e0e3048e911d.sketch_text.stroke-85"),sQuery(id+"FHMxAyK4CFUKdhS_1.wireOp",EDGE,"1cb9c079-ea9b-4899-8069-e0e3048e911d.sketch_text.stroke-86"),sQuery(id+"FHMxAyK4CFUKdhS_1.wireOp",EDGE,"1cb9c079-ea9b-4899-8069-e0e3048e911d.sketch_text.stroke-87"),sQuery(id+"FHMxAyK4CFUKdhS_1.wireOp",EDGE,"1cb9c079-ea9b-4899-8069-e0e3048e911d.sketch_text.stroke-88"),sQuery(id+"FHMxAyK4CFUKdhS_1.wireOp",EDGE,"1cb9c079-ea9b-4899-8069-e0e3048e911d.sketch_text.stroke-89"),sQuery(id+"FHMxAyK4CFUKdhS_1.wireOp",EDGE,"1cb9c079-ea9b-4899-8069-e0e3048e911d.sketch_text.stroke-90"),sQuery(id+"FHMxAyK4CFUKdhS_1.wireOp",EDGE,"1cb9c079-ea9b-4899-8069-e0e3048e911d.sketch_text.stroke-91"),sQuery(id+"FHMxAyK4CFUKdhS_1.wireOp",EDGE,"1cb9c079-ea9b-4899-8069-e0e3048e911d.sketch_text.stroke-92"),sQuery(id+"FHMxAyK4CFUKdhS_1.wireOp",EDGE,"1cb9c079-ea9b-4899-8069-e0e3048e911d.sketch_text.stroke-93"),sQuery(id+"FHMxAyK4CFUKdhS_1.wireOp",EDGE,"1cb9c079-ea9b-4899-8069-e0e3048e911d.sketch_text.stroke-94"),sQuery(id+"FHMxAyK4CFUKdhS_1.wireOp",EDGE,"1cb9c079-ea9b-4899-8069-e0e3048e911d.sketch_text.stroke-95"),sQuery(id+"FHMxAyK4CFUKdhS_1.wireOp",EDGE,"1cb9c079-ea9b-4899-8069-e0e3048e911d.sketch_text.stroke-96"),sQuery(id+"FHMxAyK4CFUKdhS_1.wireOp",EDGE,"1cb9c079-ea9b-4899-8069-e0e3048e911d.sketch_text.stroke-97"),sQuery(id+"FHMxAyK4CFUKdhS_1.wireOp",EDGE,"1cb9c079-ea9b-4899-8069-e0e3048e911d.sketch_text.stroke-103"),sQuery(id+"FHMxAyK4CFUKdhS_1.wireOp",EDGE,"1cb9c079-ea9b-4899-8069-e0e3048e911d.sketch_text.stroke-104"),sQuery(id+"FHMxAyK4CFUKdhS_1.wireOp",EDGE,"1cb9c079-ea9b-4899-8069-e0e3048e911d.sketch_text.stroke-105"),sQuery(id+"FHMxAyK4CFUKdhS_1.wireOp",EDGE,"1cb9c079-ea9b-4899-8069-e0e3048e911d.sketch_text.stroke-106"),sQuery(id+"FHMxAyK4CFUKdhS_1.wireOp",EDGE,"1cb9c079-ea9b-4899-8069-e0e3048e911d.sketch_text.stroke-107"),sQuery(id+"FHMxAyK4CFUKdhS_1.wireOp",EDGE,"1cb9c079-ea9b-4899-8069-e0e3048e911d.sketch_text.stroke-108"),sQuery(id+"FHMxAyK4CFUKdhS_1.wireOp",EDGE,"1cb9c079-ea9b-4899-8069-e0e3048e911d.sketch_text.stroke-109"),sQuery(id+"FHMxAyK4CFUKdhS_1.wireOp",EDGE,"1cb9c079-ea9b-4899-8069-e0e3048e911d.sketch_text.stroke-110"),sQuery(id+"FHMxAyK4CFUKdhS_1.wireOp",EDGE,"1cb9c079-ea9b-4899-8069-e0e3048e911d.sketch_text.stroke-111"),sQuery(id+"FHMxAyK4CFUKdhS_1.wireOp",EDGE,"1cb9c079-ea9b-4899-8069-e0e3048e911d.sketch_text.stroke-112"),sQuery(id+"FHMxAyK4CFUKdhS_1.wireOp",EDGE,"1cb9c079-ea9b-4899-8069-e0e3048e911d.sketch_text.stroke-113"),sQuery(id+"FHMxAyK4CFUKdhS_1.wireOp",EDGE,"1cb9c079-ea9b-4899-8069-e0e3048e911d.sketch_text.stroke-114"),sQuery(id+"FHMxAyK4CFUKdhS_1.wireOp",EDGE,"1cb9c079-ea9b-4899-8069-e0e3048e911d.sketch_text.stroke-115"),sQuery(id+"FHMxAyK4CFUKdhS_1.wireOp",EDGE,"1cb9c079-ea9b-4899-8069-e0e3048e911d.sketch_text.stroke-116"),sQuery(id+"FHMxAyK4CFUKdhS_1.wireOp",EDGE,"1cb9c079-ea9b-4899-8069-e0e3048e911d.sketch_text.stroke-117"),sQuery(id+"FHMxAyK4CFUKdhS_1.wireOp",EDGE,"1cb9c079-ea9b-4899-8069-e0e3048e911d.sketch_text.stroke-118"),sQuery(id+"FHMxAyK4CFUKdhS_1.wireOp",EDGE,"1cb9c079-ea9b-4899-8069-e0e3048e911d.sketch_text.stroke-119"),sQuery(id+"FHMxAyK4CFUKdhS_1.wireOp",EDGE,"1cb9c079-ea9b-4899-8069-e0e3048e911d.sketch_text.stroke-120"),sQuery(id+"FHMxAyK4CFUKdhS_1.wireOp",EDGE,"1cb9c079-ea9b-4899-8069-e0e3048e911d.sketch_text.stroke-121"),sQuery(id+"FHMxAyK4CFUKdhS_1.wireOp",EDGE,"1cb9c079-ea9b-4899-8069-e0e3048e911d.sketch_text.stroke-122"),sQuery(id+"FHMxAyK4CFUKdhS_1.wireOp",EDGE,"1cb9c079-ea9b-4899-8069-e0e3048e911d.sketch_text.stroke-123"),sQuery(id+"FHMxAyK4CFUKdhS_1.wireOp",EDGE,"1cb9c079-ea9b-4899-8069-e0e3048e911d.sketch_text.stroke-124"),sQuery(id+"FHMxAyK4CFUKdhS_1.wireOp",EDGE,"1cb9c079-ea9b-4899-8069-e0e3048e911d.sketch_text.stroke-125"),sQuery(id+"FHMxAyK4CFUKdhS_1.wireOp",EDGE,"1cb9c079-ea9b-4899-8069-e0e3048e911d.sketch_text.stroke-126"),sQuery(id+"FHMxAyK4CFUKdhS_1.wireOp",EDGE,"1cb9c079-ea9b-4899-8069-e0e3048e911d.sketch_text.stroke-127"),sQuery(id+"FHMxAyK4CFUKdhS_1.wireOp",EDGE,"1cb9c079-ea9b-4899-8069-e0e3048e911d.sketch_text.stroke-128"),sQuery(id+"FHMxAyK4CFUKdhS_1.wireOp",EDGE,"1cb9c079-ea9b-4899-8069-e0e3048e911d.sketch_text.stroke-129"),sQuery(id+"FHMxAyK4CFUKdhS_1.wireOp",EDGE,"1cb9c079-ea9b-4899-8069-e0e3048e911d.sketch_text.stroke-130"),sQuery(id+"FHMxAyK4CFUKdhS_1.wireOp",EDGE,"1cb9c079-ea9b-4899-8069-e0e3048e911d.sketch_text.stroke-131"),sQuery(id+"FHMxAyK4CFUKdhS_1.wireOp",EDGE,"1cb9c079-ea9b-4899-8069-e0e3048e911d.sketch_text.stroke-132"),sQuery(id+"FHMxAyK4CFUKdhS_1.wireOp",EDGE,"1cb9c079-ea9b-4899-8069-e0e3048e911d.sketch_text.stroke-133"),sQuery(id+"FHMxAyK4CFUKdhS_1.wireOp",EDGE,"1cb9c079-ea9b-4899-8069-e0e3048e911d.sketch_text.stroke-134"),sQuery(id+"FHMxAyK4CFUKdhS_1.wireOp",EDGE,"1cb9c079-ea9b-4899-8069-e0e3048e911d.sketch_text.stroke-135"),sQuery(id+"FHMxAyK4CFUKdhS_1.wireOp",EDGE,"1cb9c079-ea9b-4899-8069-e0e3048e911d.sketch_text.stroke-136"),sQuery(id+"FHMxAyK4CFUKdhS_1.wireOp",EDGE,"1cb9c079-ea9b-4899-8069-e0e3048e911d.sketch_text.stroke-137"),sQuery(id+"FHMxAyK4CFUKdhS_1.wireOp",EDGE,"1cb9c079-ea9b-4899-8069-e0e3048e911d.sketch_text.stroke-138"),sQuery(id+"FHMxAyK4CFUKdhS_1.wireOp",EDGE,"1cb9c079-ea9b-4899-8069-e0e3048e911d.sketch_text.stroke-139"),sQuery(id+"FHMxAyK4CFUKdhS_1.wireOp",EDGE,"1cb9c079-ea9b-4899-8069-e0e3048e911d.sketch_text.stroke-140"),sQuery(id+"FHMxAyK4CFUKdhS_1.wireOp",EDGE,"1cb9c079-ea9b-4899-8069-e0e3048e911d.sketch_text.stroke-141"),sQuery(id+"FHMxAyK4CFUKdhS_1.wireOp",EDGE,"1cb9c079-ea9b-4899-8069-e0e3048e911d.sketch_text.stroke-142"),sQuery(id+"FHMxAyK4CFUKdhS_1.wireOp",EDGE,"1cb9c079-ea9b-4899-8069-e0e3048e911d.sketch_text.stroke-143"),sQuery(id+"FHMxAyK4CFUKdhS_1.wireOp",EDGE,"1cb9c079-ea9b-4899-8069-e0e3048e911d.sketch_text.stroke-144"),sQuery(id+"FHMxAyK4CFUKdhS_1.wireOp",EDGE,"1cb9c079-ea9b-4899-8069-e0e3048e911d.sketch_text.stroke-145"),sQuery(id+"FHMxAyK4CFUKdhS_1.wireOp",EDGE,"1cb9c079-ea9b-4899-8069-e0e3048e911d.sketch_text.stroke-146"),sQuery(id+"FHMxAyK4CFUKdhS_1.wireOp",EDGE,"1cb9c079-ea9b-4899-8069-e0e3048e911d.sketch_text.stroke-147"),sQuery(id+"FHMxAyK4CFUKdhS_1.wireOp",EDGE,"1cb9c079-ea9b-4899-8069-e0e3048e911d.sketch_text.stroke-148"),sQuery(id+"FHMxAyK4CFUKdhS_1.wireOp",EDGE,"1cb9c079-ea9b-4899-8069-e0e3048e911d.sketch_text.stroke-149"),sQuery(id+"FHMxAyK4CFUKdhS_1.wireOp",EDGE,"1cb9c079-ea9b-4899-8069-e0e3048e911d.sketch_text.stroke-150"),sQuery(id+"FHMxAyK4CFUKdhS_1.wireOp",EDGE,"1cb9c079-ea9b-4899-8069-e0e3048e911d.sketch_text.stroke-151"),sQuery(id+"FHMxAyK4CFUKdhS_1.wireOp",EDGE,"1cb9c079-ea9b-4899-8069-e0e3048e911d.sketch_text.stroke-152"),sQuery(id+"FHMxAyK4CFUKdhS_1.wireOp",EDGE,"1cb9c079-ea9b-4899-8069-e0e3048e911d.sketch_text.stroke-153"),sQuery(id+"FHMxAyK4CFUKdhS_1.wireOp",EDGE,"1cb9c079-ea9b-4899-8069-e0e3048e911d.sketch_text.stroke-159"),sQuery(id+"FHMxAyK4CFUKdhS_1.wireOp",EDGE,"1cb9c079-ea9b-4899-8069-e0e3048e911d.sketch_text.stroke-160"),sQuery(id+"FHMxAyK4CFUKdhS_1.wireOp",EDGE,"1cb9c079-ea9b-4899-8069-e0e3048e911d.sketch_text.stroke-161"),sQuery(id+"FHMxAyK4CFUKdhS_1.wireOp",EDGE,"1cb9c079-ea9b-4899-8069-e0e3048e911d.sketch_text.stroke-162"),sQuery(id+"FHMxAyK4CFUKdhS_1.wireOp",EDGE,"1cb9c079-ea9b-4899-8069-e0e3048e911d.sketch_text.stroke-163"),sQuery(id+"FHMxAyK4CFUKdhS_1.wireOp",EDGE,"1cb9c079-ea9b-4899-8069-e0e3048e911d.sketch_text.stroke-164"),sQuery(id+"FHMxAyK4CFUKdhS_1.wireOp",EDGE,"1cb9c079-ea9b-4899-8069-e0e3048e911d.sketch_text.stroke-165"),sQuery(id+"FHMxAyK4CFUKdhS_1.wireOp",EDGE,"1cb9c079-ea9b-4899-8069-e0e3048e911d.sketch_text.stroke-166"),sQuery(id+"FHMxAyK4CFUKdhS_1.wireOp",EDGE,"1cb9c079-ea9b-4899-8069-e0e3048e911d.sketch_text.stroke-167"),sQuery(id+"FHMxAyK4CFUKdhS_1.wireOp",EDGE,"1cb9c079-ea9b-4899-8069-e0e3048e911d.sketch_text.stroke-168"),sQuery(id+"FHMxAyK4CFUKdhS_1.wireOp",EDGE,"1cb9c079-ea9b-4899-8069-e0e3048e911d.sketch_text.stroke-169"),sQuery(id+"FHMxAyK4CFUKdhS_1.wireOp",EDGE,"1cb9c079-ea9b-4899-8069-e0e3048e911d.sketch_text.stroke-170"),sQuery(id+"FHMxAyK4CFUKdhS_1.wireOp",EDGE,"1cb9c079-ea9b-4899-8069-e0e3048e911d.sketch_text.stroke-171"),sQuery(id+"FHMxAyK4CFUKdhS_1.wireOp",EDGE,"1cb9c079-ea9b-4899-8069-e0e3048e911d.sketch_text.stroke-172"),sQuery(id+"FHMxAyK4CFUKdhS_1.wireOp",EDGE,"1cb9c079-ea9b-4899-8069-e0e3048e911d.sketch_text.stroke-173"),sQuery(id+"FHMxAyK4CFUKdhS_1.wireOp",EDGE,"1cb9c079-ea9b-4899-8069-e0e3048e911d.sketch_text.stroke-174"),sQuery(id+"FHMxAyK4CFUKdhS_1.wireOp",EDGE,"1cb9c079-ea9b-4899-8069-e0e3048e911d.sketch_text.stroke-175"),sQuery(id+"FHMxAyK4CFUKdhS_1.wireOp",EDGE,"1cb9c079-ea9b-4899-8069-e0e3048e911d.sketch_text.stroke-176"),sQuery(id+"FHMxAyK4CFUKdhS_1.wireOp",EDGE,"1cb9c079-ea9b-4899-8069-e0e3048e911d.sketch_text.stroke-177"),sQuery(id+"FHMxAyK4CFUKdhS_1.wireOp",EDGE,"1cb9c079-ea9b-4899-8069-e0e3048e911d.sketch_text.stroke-178"),sQuery(id+"FHMxAyK4CFUKdhS_1.wireOp",EDGE,"1cb9c079-ea9b-4899-8069-e0e3048e911d.sketch_text.stroke-179"),sQuery(id+"FHMxAyK4CFUKdhS_1.wireOp",EDGE,"1cb9c079-ea9b-4899-8069-e0e3048e911d.sketch_text.stroke-180"),subQ0,subQ2])],"isStart":true}),makeQuery(id+"F3.opExtrude","SWEPT_FACE",FACE,{"disambiguationData":[OSD([subQ2])]})])],"derivedFrom":makeQuery(id+"F3.opExtrude","CAP_EDGE",EDGE,{"disambiguationData":[OSD([subQ2])],"isStart":true})});}
            var Q23;
            {var subQ0=sQuery(id+"F0.wireOp",EDGE,"E0.top");var subQ1=sQuery(id+"F0.wireOp",EDGE,"E0.bottom");var subQ2=sQuery(id+"F2.wireOp",EDGE,"E27");Q23=makeQuery(id+"F3.boolean.opBoolean","SPLIT",EDGE,{"disambiguationData":[TD([makeQuery(id+"F1.opExtrude","CAP_FACE",FACE,{"disambiguationData":[OSD([subQ1,subQ0,sQuery(id+"F0.wireOp",EDGE,"E0.left"),sQuery(id+"F0.wireOp",EDGE,"E0.right")])],"isStart":false}),makeQuery(id+"F1.opExtrude","SWEPT_FACE",FACE,{"disambiguationData":[OSD([subQ0])]}),makeQuery(id+"F3.opExtrude","CAP_FACE",FACE,{"disambiguationData":[OSD([subQ1,sQuery(id+"FQ5JFwxVdaqARUP_1.wireOp",EDGE,"fcba4419-a2ee-464f-be9d-58f11bf3418b.sketch_text.stroke-0"),sQuery(id+"FQ5JFwxVdaqARUP_1.wireOp",EDGE,"fcba4419-a2ee-464f-be9d-58f11bf3418b.sketch_text.stroke-1"),sQuery(id+"FQ5JFwxVdaqARUP_1.wireOp",EDGE,"fcba4419-a2ee-464f-be9d-58f11bf3418b.sketch_text.stroke-2"),sQuery(id+"FQ5JFwxVdaqARUP_1.wireOp",EDGE,"fcba4419-a2ee-464f-be9d-58f11bf3418b.sketch_text.stroke-3"),sQuery(id+"FQ5JFwxVdaqARUP_1.wireOp",EDGE,"fcba4419-a2ee-464f-be9d-58f11bf3418b.sketch_text.stroke-4"),sQuery(id+"FQ5JFwxVdaqARUP_1.wireOp",EDGE,"fcba4419-a2ee-464f-be9d-58f11bf3418b.sketch_text.stroke-5"),sQuery(id+"FQ5JFwxVdaqARUP_1.wireOp",EDGE,"fcba4419-a2ee-464f-be9d-58f11bf3418b.sketch_text.stroke-6"),sQuery(id+"FQ5JFwxVdaqARUP_1.wireOp",EDGE,"fcba4419-a2ee-464f-be9d-58f11bf3418b.sketch_text.stroke-7"),sQuery(id+"FQ5JFwxVdaqARUP_1.wireOp",EDGE,"fcba4419-a2ee-464f-be9d-58f11bf3418b.sketch_text.stroke-8"),sQuery(id+"FQ5JFwxVdaqARUP_1.wireOp",EDGE,"fcba4419-a2ee-464f-be9d-58f11bf3418b.sketch_text.stroke-9"),sQuery(id+"FQ5JFwxVdaqARUP_1.wireOp",EDGE,"fcba4419-a2ee-464f-be9d-58f11bf3418b.sketch_text.stroke-10"),sQuery(id+"FQ5JFwxVdaqARUP_1.wireOp",EDGE,"fcba4419-a2ee-464f-be9d-58f11bf3418b.sketch_text.stroke-11"),sQuery(id+"FQ5JFwxVdaqARUP_1.wireOp",EDGE,"fcba4419-a2ee-464f-be9d-58f11bf3418b.sketch_text.stroke-12"),sQuery(id+"FQ5JFwxVdaqARUP_1.wireOp",EDGE,"fcba4419-a2ee-464f-be9d-58f11bf3418b.sketch_text.stroke-13"),sQuery(id+"FQ5JFwxVdaqARUP_1.wireOp",EDGE,"fcba4419-a2ee-464f-be9d-58f11bf3418b.sketch_text.stroke-14"),sQuery(id+"FQ5JFwxVdaqARUP_1.wireOp",EDGE,"fcba4419-a2ee-464f-be9d-58f11bf3418b.sketch_text.stroke-15"),sQuery(id+"FQ5JFwxVdaqARUP_1.wireOp",EDGE,"fcba4419-a2ee-464f-be9d-58f11bf3418b.sketch_text.stroke-16"),sQuery(id+"FQ5JFwxVdaqARUP_1.wireOp",EDGE,"fcba4419-a2ee-464f-be9d-58f11bf3418b.sketch_text.stroke-17"),sQuery(id+"FQ5JFwxVdaqARUP_1.wireOp",EDGE,"fcba4419-a2ee-464f-be9d-58f11bf3418b.sketch_text.stroke-18"),sQuery(id+"FQ5JFwxVdaqARUP_1.wireOp",EDGE,"fcba4419-a2ee-464f-be9d-58f11bf3418b.sketch_text.stroke-19"),sQuery(id+"FQ5JFwxVdaqARUP_1.wireOp",EDGE,"fcba4419-a2ee-464f-be9d-58f11bf3418b.sketch_text.stroke-20"),sQuery(id+"FQ5JFwxVdaqARUP_1.wireOp",EDGE,"fcba4419-a2ee-464f-be9d-58f11bf3418b.sketch_text.stroke-21"),sQuery(id+"FQ5JFwxVdaqARUP_1.wireOp",EDGE,"fcba4419-a2ee-464f-be9d-58f11bf3418b.sketch_text.stroke-22"),sQuery(id+"FQ5JFwxVdaqARUP_1.wireOp",EDGE,"fcba4419-a2ee-464f-be9d-58f11bf3418b.sketch_text.stroke-23"),sQuery(id+"FQ5JFwxVdaqARUP_1.wireOp",EDGE,"fcba4419-a2ee-464f-be9d-58f11bf3418b.sketch_text.stroke-24"),sQuery(id+"FQ5JFwxVdaqARUP_1.wireOp",EDGE,"fcba4419-a2ee-464f-be9d-58f11bf3418b.sketch_text.stroke-25"),sQuery(id+"FQ5JFwxVdaqARUP_1.wireOp",EDGE,"fcba4419-a2ee-464f-be9d-58f11bf3418b.sketch_text.stroke-26"),sQuery(id+"FQ5JFwxVdaqARUP_1.wireOp",EDGE,"fcba4419-a2ee-464f-be9d-58f11bf3418b.sketch_text.stroke-27"),sQuery(id+"FQ5JFwxVdaqARUP_1.wireOp",EDGE,"fcba4419-a2ee-464f-be9d-58f11bf3418b.sketch_text.stroke-28"),sQuery(id+"FQ5JFwxVdaqARUP_1.wireOp",EDGE,"fcba4419-a2ee-464f-be9d-58f11bf3418b.sketch_text.stroke-29"),sQuery(id+"FQ5JFwxVdaqARUP_1.wireOp",EDGE,"fcba4419-a2ee-464f-be9d-58f11bf3418b.sketch_text.stroke-30"),sQuery(id+"FQ5JFwxVdaqARUP_1.wireOp",EDGE,"fcba4419-a2ee-464f-be9d-58f11bf3418b.sketch_text.stroke-31"),sQuery(id+"FQ5JFwxVdaqARUP_1.wireOp",EDGE,"fcba4419-a2ee-464f-be9d-58f11bf3418b.sketch_text.stroke-32"),sQuery(id+"FQ5JFwxVdaqARUP_1.wireOp",EDGE,"fcba4419-a2ee-464f-be9d-58f11bf3418b.sketch_text.stroke-33"),sQuery(id+"FQ5JFwxVdaqARUP_1.wireOp",EDGE,"fcba4419-a2ee-464f-be9d-58f11bf3418b.sketch_text.stroke-34"),sQuery(id+"FQ5JFwxVdaqARUP_1.wireOp",EDGE,"fcba4419-a2ee-464f-be9d-58f11bf3418b.sketch_text.stroke-35"),sQuery(id+"FQ5JFwxVdaqARUP_1.wireOp",EDGE,"fcba4419-a2ee-464f-be9d-58f11bf3418b.sketch_text.stroke-36"),sQuery(id+"FQ5JFwxVdaqARUP_1.wireOp",EDGE,"fcba4419-a2ee-464f-be9d-58f11bf3418b.sketch_text.stroke-37"),sQuery(id+"FQ5JFwxVdaqARUP_1.wireOp",EDGE,"fcba4419-a2ee-464f-be9d-58f11bf3418b.sketch_text.stroke-38"),sQuery(id+"FQ5JFwxVdaqARUP_1.wireOp",EDGE,"fcba4419-a2ee-464f-be9d-58f11bf3418b.sketch_text.stroke-39"),sQuery(id+"FQ5JFwxVdaqARUP_1.wireOp",EDGE,"fcba4419-a2ee-464f-be9d-58f11bf3418b.sketch_text.stroke-40"),sQuery(id+"FQ5JFwxVdaqARUP_1.wireOp",EDGE,"fcba4419-a2ee-464f-be9d-58f11bf3418b.sketch_text.stroke-41"),sQuery(id+"FQ5JFwxVdaqARUP_1.wireOp",EDGE,"fcba4419-a2ee-464f-be9d-58f11bf3418b.sketch_text.stroke-42"),sQuery(id+"FQ5JFwxVdaqARUP_1.wireOp",EDGE,"fcba4419-a2ee-464f-be9d-58f11bf3418b.sketch_text.stroke-43"),sQuery(id+"FQ5JFwxVdaqARUP_1.wireOp",EDGE,"fcba4419-a2ee-464f-be9d-58f11bf3418b.sketch_text.stroke-44"),sQuery(id+"FQ5JFwxVdaqARUP_1.wireOp",EDGE,"fcba4419-a2ee-464f-be9d-58f11bf3418b.sketch_text.stroke-45"),sQuery(id+"FQ5JFwxVdaqARUP_1.wireOp",EDGE,"fcba4419-a2ee-464f-be9d-58f11bf3418b.sketch_text.stroke-46"),sQuery(id+"FQ5JFwxVdaqARUP_1.wireOp",EDGE,"fcba4419-a2ee-464f-be9d-58f11bf3418b.sketch_text.stroke-47"),sQuery(id+"FQ5JFwxVdaqARUP_1.wireOp",EDGE,"fcba4419-a2ee-464f-be9d-58f11bf3418b.sketch_text.stroke-48"),sQuery(id+"FQ5JFwxVdaqARUP_1.wireOp",EDGE,"fcba4419-a2ee-464f-be9d-58f11bf3418b.sketch_text.stroke-49"),sQuery(id+"FQ5JFwxVdaqARUP_1.wireOp",EDGE,"fcba4419-a2ee-464f-be9d-58f11bf3418b.sketch_text.stroke-50"),sQuery(id+"FQ5JFwxVdaqARUP_1.wireOp",EDGE,"fcba4419-a2ee-464f-be9d-58f11bf3418b.sketch_text.stroke-51"),sQuery(id+"FQ5JFwxVdaqARUP_1.wireOp",EDGE,"fcba4419-a2ee-464f-be9d-58f11bf3418b.sketch_text.stroke-52"),sQuery(id+"FQ5JFwxVdaqARUP_1.wireOp",EDGE,"fcba4419-a2ee-464f-be9d-58f11bf3418b.sketch_text.stroke-53"),sQuery(id+"FQ5JFwxVdaqARUP_1.wireOp",EDGE,"fcba4419-a2ee-464f-be9d-58f11bf3418b.sketch_text.stroke-54"),sQuery(id+"FQ5JFwxVdaqARUP_1.wireOp",EDGE,"fcba4419-a2ee-464f-be9d-58f11bf3418b.sketch_text.stroke-55"),sQuery(id+"FQ5JFwxVdaqARUP_1.wireOp",EDGE,"fcba4419-a2ee-464f-be9d-58f11bf3418b.sketch_text.stroke-56"),sQuery(id+"FQ5JFwxVdaqARUP_1.wireOp",EDGE,"fcba4419-a2ee-464f-be9d-58f11bf3418b.sketch_text.stroke-57"),sQuery(id+"FQ5JFwxVdaqARUP_1.wireOp",EDGE,"fcba4419-a2ee-464f-be9d-58f11bf3418b.sketch_text.stroke-58"),sQuery(id+"FQ5JFwxVdaqARUP_1.wireOp",EDGE,"fcba4419-a2ee-464f-be9d-58f11bf3418b.sketch_text.stroke-59"),sQuery(id+"FQ5JFwxVdaqARUP_1.wireOp",EDGE,"fcba4419-a2ee-464f-be9d-58f11bf3418b.sketch_text.stroke-60"),sQuery(id+"FQ5JFwxVdaqARUP_1.wireOp",EDGE,"fcba4419-a2ee-464f-be9d-58f11bf3418b.sketch_text.stroke-61"),sQuery(id+"FQ5JFwxVdaqARUP_1.wireOp",EDGE,"fcba4419-a2ee-464f-be9d-58f11bf3418b.sketch_text.stroke-62"),sQuery(id+"FQ5JFwxVdaqARUP_1.wireOp",EDGE,"fcba4419-a2ee-464f-be9d-58f11bf3418b.sketch_text.stroke-63"),sQuery(id+"FQ5JFwxVdaqARUP_1.wireOp",EDGE,"fcba4419-a2ee-464f-be9d-58f11bf3418b.sketch_text.stroke-64"),sQuery(id+"FQ5JFwxVdaqARUP_1.wireOp",EDGE,"fcba4419-a2ee-464f-be9d-58f11bf3418b.sketch_text.stroke-65"),sQuery(id+"FQ5JFwxVdaqARUP_1.wireOp",EDGE,"fcba4419-a2ee-464f-be9d-58f11bf3418b.sketch_text.stroke-66"),sQuery(id+"FQ5JFwxVdaqARUP_1.wireOp",EDGE,"fcba4419-a2ee-464f-be9d-58f11bf3418b.sketch_text.stroke-67"),sQuery(id+"FQ5JFwxVdaqARUP_1.wireOp",EDGE,"fcba4419-a2ee-464f-be9d-58f11bf3418b.sketch_text.stroke-68"),sQuery(id+"FQ5JFwxVdaqARUP_1.wireOp",EDGE,"fcba4419-a2ee-464f-be9d-58f11bf3418b.sketch_text.stroke-69"),sQuery(id+"FQ5JFwxVdaqARUP_1.wireOp",EDGE,"fcba4419-a2ee-464f-be9d-58f11bf3418b.sketch_text.stroke-70"),sQuery(id+"FQ5JFwxVdaqARUP_1.wireOp",EDGE,"fcba4419-a2ee-464f-be9d-58f11bf3418b.sketch_text.stroke-71"),sQuery(id+"FQ5JFwxVdaqARUP_1.wireOp",EDGE,"fcba4419-a2ee-464f-be9d-58f11bf3418b.sketch_text.stroke-72"),sQuery(id+"FQ5JFwxVdaqARUP_1.wireOp",EDGE,"fcba4419-a2ee-464f-be9d-58f11bf3418b.sketch_text.stroke-73"),sQuery(id+"FQ5JFwxVdaqARUP_1.wireOp",EDGE,"fcba4419-a2ee-464f-be9d-58f11bf3418b.sketch_text.stroke-74"),sQuery(id+"FQ5JFwxVdaqARUP_1.wireOp",EDGE,"fcba4419-a2ee-464f-be9d-58f11bf3418b.sketch_text.stroke-75"),sQuery(id+"FQ5JFwxVdaqARUP_1.wireOp",EDGE,"fcba4419-a2ee-464f-be9d-58f11bf3418b.sketch_text.stroke-76"),sQuery(id+"FQ5JFwxVdaqARUP_1.wireOp",EDGE,"fcba4419-a2ee-464f-be9d-58f11bf3418b.sketch_text.stroke-77"),sQuery(id+"FQ5JFwxVdaqARUP_1.wireOp",EDGE,"fcba4419-a2ee-464f-be9d-58f11bf3418b.sketch_text.stroke-78"),sQuery(id+"FQ5JFwxVdaqARUP_1.wireOp",EDGE,"fcba4419-a2ee-464f-be9d-58f11bf3418b.sketch_text.stroke-79"),sQuery(id+"FQ5JFwxVdaqARUP_1.wireOp",EDGE,"fcba4419-a2ee-464f-be9d-58f11bf3418b.sketch_text.stroke-80"),sQuery(id+"FQ5JFwxVdaqARUP_1.wireOp",EDGE,"fcba4419-a2ee-464f-be9d-58f11bf3418b.sketch_text.stroke-81"),sQuery(id+"FQ5JFwxVdaqARUP_1.wireOp",EDGE,"fcba4419-a2ee-464f-be9d-58f11bf3418b.sketch_text.stroke-82"),sQuery(id+"FQ5JFwxVdaqARUP_1.wireOp",EDGE,"fcba4419-a2ee-464f-be9d-58f11bf3418b.sketch_text.stroke-83"),sQuery(id+"FQ5JFwxVdaqARUP_1.wireOp",EDGE,"fcba4419-a2ee-464f-be9d-58f11bf3418b.sketch_text.stroke-84"),sQuery(id+"FQ5JFwxVdaqARUP_1.wireOp",EDGE,"fcba4419-a2ee-464f-be9d-58f11bf3418b.sketch_text.stroke-85"),sQuery(id+"FQ5JFwxVdaqARUP_1.wireOp",EDGE,"fcba4419-a2ee-464f-be9d-58f11bf3418b.sketch_text.stroke-86"),sQuery(id+"FQ5JFwxVdaqARUP_1.wireOp",EDGE,"fcba4419-a2ee-464f-be9d-58f11bf3418b.sketch_text.stroke-87"),sQuery(id+"FQ5JFwxVdaqARUP_1.wireOp",EDGE,"fcba4419-a2ee-464f-be9d-58f11bf3418b.sketch_text.stroke-88"),sQuery(id+"FQ5JFwxVdaqARUP_1.wireOp",EDGE,"fcba4419-a2ee-464f-be9d-58f11bf3418b.sketch_text.stroke-89"),sQuery(id+"FQ5JFwxVdaqARUP_1.wireOp",EDGE,"fcba4419-a2ee-464f-be9d-58f11bf3418b.sketch_text.stroke-90"),sQuery(id+"FQ5JFwxVdaqARUP_1.wireOp",EDGE,"fcba4419-a2ee-464f-be9d-58f11bf3418b.sketch_text.stroke-91"),sQuery(id+"FQ5JFwxVdaqARUP_1.wireOp",EDGE,"fcba4419-a2ee-464f-be9d-58f11bf3418b.sketch_text.stroke-92"),sQuery(id+"FQ5JFwxVdaqARUP_1.wireOp",EDGE,"fcba4419-a2ee-464f-be9d-58f11bf3418b.sketch_text.stroke-93"),sQuery(id+"FQ5JFwxVdaqARUP_1.wireOp",EDGE,"fcba4419-a2ee-464f-be9d-58f11bf3418b.sketch_text.stroke-94"),sQuery(id+"FQ5JFwxVdaqARUP_1.wireOp",EDGE,"fcba4419-a2ee-464f-be9d-58f11bf3418b.sketch_text.stroke-95"),sQuery(id+"FQ5JFwxVdaqARUP_1.wireOp",EDGE,"fcba4419-a2ee-464f-be9d-58f11bf3418b.sketch_text.stroke-96"),sQuery(id+"FQ5JFwxVdaqARUP_1.wireOp",EDGE,"fcba4419-a2ee-464f-be9d-58f11bf3418b.sketch_text.stroke-97"),sQuery(id+"FQ5JFwxVdaqARUP_1.wireOp",EDGE,"fcba4419-a2ee-464f-be9d-58f11bf3418b.sketch_text.stroke-98"),sQuery(id+"FQ5JFwxVdaqARUP_1.wireOp",EDGE,"fcba4419-a2ee-464f-be9d-58f11bf3418b.sketch_text.stroke-99"),sQuery(id+"FQ5JFwxVdaqARUP_1.wireOp",EDGE,"fcba4419-a2ee-464f-be9d-58f11bf3418b.sketch_text.stroke-100"),sQuery(id+"FQ5JFwxVdaqARUP_1.wireOp",EDGE,"fcba4419-a2ee-464f-be9d-58f11bf3418b.sketch_text.stroke-101"),sQuery(id+"FQ5JFwxVdaqARUP_1.wireOp",EDGE,"fcba4419-a2ee-464f-be9d-58f11bf3418b.sketch_text.stroke-102"),sQuery(id+"FQ5JFwxVdaqARUP_1.wireOp",EDGE,"fcba4419-a2ee-464f-be9d-58f11bf3418b.sketch_text.stroke-103"),sQuery(id+"FQ5JFwxVdaqARUP_1.wireOp",EDGE,"fcba4419-a2ee-464f-be9d-58f11bf3418b.sketch_text.stroke-104"),sQuery(id+"FQ5JFwxVdaqARUP_1.wireOp",EDGE,"fcba4419-a2ee-464f-be9d-58f11bf3418b.sketch_text.stroke-105"),sQuery(id+"FQ5JFwxVdaqARUP_1.wireOp",EDGE,"fcba4419-a2ee-464f-be9d-58f11bf3418b.sketch_text.stroke-106"),sQuery(id+"FQ5JFwxVdaqARUP_1.wireOp",EDGE,"fcba4419-a2ee-464f-be9d-58f11bf3418b.sketch_text.stroke-107"),sQuery(id+"FQ5JFwxVdaqARUP_1.wireOp",EDGE,"fcba4419-a2ee-464f-be9d-58f11bf3418b.sketch_text.stroke-108"),sQuery(id+"FQ5JFwxVdaqARUP_1.wireOp",EDGE,"fcba4419-a2ee-464f-be9d-58f11bf3418b.sketch_text.stroke-109"),sQuery(id+"FQ5JFwxVdaqARUP_1.wireOp",EDGE,"fcba4419-a2ee-464f-be9d-58f11bf3418b.sketch_text.stroke-110"),sQuery(id+"FQ5JFwxVdaqARUP_1.wireOp",EDGE,"fcba4419-a2ee-464f-be9d-58f11bf3418b.sketch_text.stroke-111"),sQuery(id+"FQ5JFwxVdaqARUP_1.wireOp",EDGE,"fcba4419-a2ee-464f-be9d-58f11bf3418b.sketch_text.stroke-112"),sQuery(id+"FQ5JFwxVdaqARUP_1.wireOp",EDGE,"fcba4419-a2ee-464f-be9d-58f11bf3418b.sketch_text.stroke-113"),sQuery(id+"FQ5JFwxVdaqARUP_1.wireOp",EDGE,"fcba4419-a2ee-464f-be9d-58f11bf3418b.sketch_text.stroke-114"),sQuery(id+"FQ5JFwxVdaqARUP_1.wireOp",EDGE,"fcba4419-a2ee-464f-be9d-58f11bf3418b.sketch_text.stroke-115"),sQuery(id+"FQ5JFwxVdaqARUP_1.wireOp",EDGE,"fcba4419-a2ee-464f-be9d-58f11bf3418b.sketch_text.stroke-116"),sQuery(id+"FQ5JFwxVdaqARUP_1.wireOp",EDGE,"fcba4419-a2ee-464f-be9d-58f11bf3418b.sketch_text.stroke-117"),sQuery(id+"FQ5JFwxVdaqARUP_1.wireOp",EDGE,"fcba4419-a2ee-464f-be9d-58f11bf3418b.sketch_text.stroke-118"),sQuery(id+"FQ5JFwxVdaqARUP_1.wireOp",EDGE,"fcba4419-a2ee-464f-be9d-58f11bf3418b.sketch_text.stroke-119"),sQuery(id+"FQ5JFwxVdaqARUP_1.wireOp",EDGE,"fcba4419-a2ee-464f-be9d-58f11bf3418b.sketch_text.stroke-120"),sQuery(id+"FQ5JFwxVdaqARUP_1.wireOp",EDGE,"fcba4419-a2ee-464f-be9d-58f11bf3418b.sketch_text.stroke-121"),sQuery(id+"FQ5JFwxVdaqARUP_1.wireOp",EDGE,"fcba4419-a2ee-464f-be9d-58f11bf3418b.sketch_text.stroke-122"),sQuery(id+"FQ5JFwxVdaqARUP_1.wireOp",EDGE,"fcba4419-a2ee-464f-be9d-58f11bf3418b.sketch_text.stroke-123"),sQuery(id+"FQ5JFwxVdaqARUP_1.wireOp",EDGE,"fcba4419-a2ee-464f-be9d-58f11bf3418b.sketch_text.stroke-124"),sQuery(id+"FQ5JFwxVdaqARUP_1.wireOp",EDGE,"fcba4419-a2ee-464f-be9d-58f11bf3418b.sketch_text.stroke-125"),sQuery(id+"FQ5JFwxVdaqARUP_1.wireOp",EDGE,"fcba4419-a2ee-464f-be9d-58f11bf3418b.sketch_text.stroke-126"),sQuery(id+"FQ5JFwxVdaqARUP_1.wireOp",EDGE,"fcba4419-a2ee-464f-be9d-58f11bf3418b.sketch_text.stroke-127"),sQuery(id+"FQ5JFwxVdaqARUP_1.wireOp",EDGE,"fcba4419-a2ee-464f-be9d-58f11bf3418b.sketch_text.stroke-128"),sQuery(id+"FQ5JFwxVdaqARUP_1.wireOp",EDGE,"fcba4419-a2ee-464f-be9d-58f11bf3418b.sketch_text.stroke-129"),sQuery(id+"FQ5JFwxVdaqARUP_1.wireOp",EDGE,"fcba4419-a2ee-464f-be9d-58f11bf3418b.sketch_text.stroke-130"),sQuery(id+"FQ5JFwxVdaqARUP_1.wireOp",EDGE,"fcba4419-a2ee-464f-be9d-58f11bf3418b.sketch_text.stroke-131"),sQuery(id+"FQ5JFwxVdaqARUP_1.wireOp",EDGE,"fcba4419-a2ee-464f-be9d-58f11bf3418b.sketch_text.stroke-132"),sQuery(id+"FQ5JFwxVdaqARUP_1.wireOp",EDGE,"fcba4419-a2ee-464f-be9d-58f11bf3418b.sketch_text.stroke-133"),sQuery(id+"FQ5JFwxVdaqARUP_1.wireOp",EDGE,"fcba4419-a2ee-464f-be9d-58f11bf3418b.sketch_text.stroke-134"),sQuery(id+"FQ5JFwxVdaqARUP_1.wireOp",EDGE,"fcba4419-a2ee-464f-be9d-58f11bf3418b.sketch_text.stroke-135"),sQuery(id+"FQ5JFwxVdaqARUP_1.wireOp",EDGE,"fcba4419-a2ee-464f-be9d-58f11bf3418b.sketch_text.stroke-136"),sQuery(id+"FQ5JFwxVdaqARUP_1.wireOp",EDGE,"fcba4419-a2ee-464f-be9d-58f11bf3418b.sketch_text.stroke-137"),sQuery(id+"FQ5JFwxVdaqARUP_1.wireOp",EDGE,"fcba4419-a2ee-464f-be9d-58f11bf3418b.sketch_text.stroke-138"),sQuery(id+"FQ5JFwxVdaqARUP_1.wireOp",EDGE,"fcba4419-a2ee-464f-be9d-58f11bf3418b.sketch_text.stroke-139"),sQuery(id+"FQ5JFwxVdaqARUP_1.wireOp",EDGE,"fcba4419-a2ee-464f-be9d-58f11bf3418b.sketch_text.stroke-140"),sQuery(id+"FQ5JFwxVdaqARUP_1.wireOp",EDGE,"fcba4419-a2ee-464f-be9d-58f11bf3418b.sketch_text.stroke-141"),sQuery(id+"FQ5JFwxVdaqARUP_1.wireOp",EDGE,"fcba4419-a2ee-464f-be9d-58f11bf3418b.sketch_text.stroke-142"),sQuery(id+"FQ5JFwxVdaqARUP_1.wireOp",EDGE,"fcba4419-a2ee-464f-be9d-58f11bf3418b.sketch_text.stroke-143"),sQuery(id+"FQ5JFwxVdaqARUP_1.wireOp",EDGE,"fcba4419-a2ee-464f-be9d-58f11bf3418b.sketch_text.stroke-144"),sQuery(id+"FQ5JFwxVdaqARUP_1.wireOp",EDGE,"fcba4419-a2ee-464f-be9d-58f11bf3418b.sketch_text.stroke-145"),sQuery(id+"FQ5JFwxVdaqARUP_1.wireOp",EDGE,"fcba4419-a2ee-464f-be9d-58f11bf3418b.sketch_text.stroke-146"),sQuery(id+"FQ5JFwxVdaqARUP_1.wireOp",EDGE,"fcba4419-a2ee-464f-be9d-58f11bf3418b.sketch_text.stroke-147"),sQuery(id+"FQ5JFwxVdaqARUP_1.wireOp",EDGE,"fcba4419-a2ee-464f-be9d-58f11bf3418b.sketch_text.stroke-148"),sQuery(id+"FQ5JFwxVdaqARUP_1.wireOp",EDGE,"fcba4419-a2ee-464f-be9d-58f11bf3418b.sketch_text.stroke-149"),sQuery(id+"FQ5JFwxVdaqARUP_1.wireOp",EDGE,"fcba4419-a2ee-464f-be9d-58f11bf3418b.sketch_text.stroke-150"),sQuery(id+"FQ5JFwxVdaqARUP_1.wireOp",EDGE,"fcba4419-a2ee-464f-be9d-58f11bf3418b.sketch_text.stroke-151"),sQuery(id+"FQ5JFwxVdaqARUP_1.wireOp",EDGE,"fcba4419-a2ee-464f-be9d-58f11bf3418b.sketch_text.stroke-152"),sQuery(id+"FQ5JFwxVdaqARUP_1.wireOp",EDGE,"fcba4419-a2ee-464f-be9d-58f11bf3418b.sketch_text.stroke-153"),sQuery(id+"FQ5JFwxVdaqARUP_1.wireOp",EDGE,"fcba4419-a2ee-464f-be9d-58f11bf3418b.sketch_text.stroke-154"),sQuery(id+"FQ5JFwxVdaqARUP_1.wireOp",EDGE,"fcba4419-a2ee-464f-be9d-58f11bf3418b.sketch_text.stroke-155"),sQuery(id+"FQ5JFwxVdaqARUP_1.wireOp",EDGE,"fcba4419-a2ee-464f-be9d-58f11bf3418b.sketch_text.stroke-156"),sQuery(id+"FQ5JFwxVdaqARUP_1.wireOp",EDGE,"fcba4419-a2ee-464f-be9d-58f11bf3418b.sketch_text.stroke-157"),sQuery(id+"FQ5JFwxVdaqARUP_1.wireOp",EDGE,"fcba4419-a2ee-464f-be9d-58f11bf3418b.sketch_text.stroke-158"),sQuery(id+"FQ5JFwxVdaqARUP_1.wireOp",EDGE,"fcba4419-a2ee-464f-be9d-58f11bf3418b.sketch_text.stroke-159"),sQuery(id+"FQ5JFwxVdaqARUP_1.wireOp",EDGE,"fcba4419-a2ee-464f-be9d-58f11bf3418b.sketch_text.stroke-160"),sQuery(id+"FQ5JFwxVdaqARUP_1.wireOp",EDGE,"fcba4419-a2ee-464f-be9d-58f11bf3418b.sketch_text.stroke-161"),sQuery(id+"FQ5JFwxVdaqARUP_1.wireOp",EDGE,"fcba4419-a2ee-464f-be9d-58f11bf3418b.sketch_text.stroke-162"),sQuery(id+"FQ5JFwxVdaqARUP_1.wireOp",EDGE,"fcba4419-a2ee-464f-be9d-58f11bf3418b.sketch_text.stroke-163"),sQuery(id+"FQ5JFwxVdaqARUP_1.wireOp",EDGE,"fcba4419-a2ee-464f-be9d-58f11bf3418b.sketch_text.stroke-164"),sQuery(id+"FQ5JFwxVdaqARUP_1.wireOp",EDGE,"fcba4419-a2ee-464f-be9d-58f11bf3418b.sketch_text.stroke-165"),sQuery(id+"FQ5JFwxVdaqARUP_1.wireOp",EDGE,"fcba4419-a2ee-464f-be9d-58f11bf3418b.sketch_text.stroke-166"),sQuery(id+"FQ5JFwxVdaqARUP_1.wireOp",EDGE,"fcba4419-a2ee-464f-be9d-58f11bf3418b.sketch_text.stroke-167"),sQuery(id+"FQ5JFwxVdaqARUP_1.wireOp",EDGE,"fcba4419-a2ee-464f-be9d-58f11bf3418b.sketch_text.stroke-168"),sQuery(id+"FQ5JFwxVdaqARUP_1.wireOp",EDGE,"fcba4419-a2ee-464f-be9d-58f11bf3418b.sketch_text.stroke-169"),sQuery(id+"FQ5JFwxVdaqARUP_1.wireOp",EDGE,"fcba4419-a2ee-464f-be9d-58f11bf3418b.sketch_text.stroke-170"),sQuery(id+"FQ5JFwxVdaqARUP_1.wireOp",EDGE,"fcba4419-a2ee-464f-be9d-58f11bf3418b.sketch_text.stroke-171"),sQuery(id+"FQ5JFwxVdaqARUP_1.wireOp",EDGE,"fcba4419-a2ee-464f-be9d-58f11bf3418b.sketch_text.stroke-172"),sQuery(id+"FQ5JFwxVdaqARUP_1.wireOp",EDGE,"fcba4419-a2ee-464f-be9d-58f11bf3418b.sketch_text.stroke-173"),sQuery(id+"FHMxAyK4CFUKdhS_1.wireOp",EDGE,"1cb9c079-ea9b-4899-8069-e0e3048e911d.sketch_text.stroke-0"),sQuery(id+"FHMxAyK4CFUKdhS_1.wireOp",EDGE,"1cb9c079-ea9b-4899-8069-e0e3048e911d.sketch_text.stroke-1"),sQuery(id+"FHMxAyK4CFUKdhS_1.wireOp",EDGE,"1cb9c079-ea9b-4899-8069-e0e3048e911d.sketch_text.stroke-2"),sQuery(id+"FHMxAyK4CFUKdhS_1.wireOp",EDGE,"1cb9c079-ea9b-4899-8069-e0e3048e911d.sketch_text.stroke-3"),sQuery(id+"FHMxAyK4CFUKdhS_1.wireOp",EDGE,"1cb9c079-ea9b-4899-8069-e0e3048e911d.sketch_text.stroke-4"),sQuery(id+"FHMxAyK4CFUKdhS_1.wireOp",EDGE,"1cb9c079-ea9b-4899-8069-e0e3048e911d.sketch_text.stroke-5"),sQuery(id+"FHMxAyK4CFUKdhS_1.wireOp",EDGE,"1cb9c079-ea9b-4899-8069-e0e3048e911d.sketch_text.stroke-6"),sQuery(id+"FHMxAyK4CFUKdhS_1.wireOp",EDGE,"1cb9c079-ea9b-4899-8069-e0e3048e911d.sketch_text.stroke-7"),sQuery(id+"FHMxAyK4CFUKdhS_1.wireOp",EDGE,"1cb9c079-ea9b-4899-8069-e0e3048e911d.sketch_text.stroke-8"),sQuery(id+"FHMxAyK4CFUKdhS_1.wireOp",EDGE,"1cb9c079-ea9b-4899-8069-e0e3048e911d.sketch_text.stroke-9"),sQuery(id+"FHMxAyK4CFUKdhS_1.wireOp",EDGE,"1cb9c079-ea9b-4899-8069-e0e3048e911d.sketch_text.stroke-10"),sQuery(id+"FHMxAyK4CFUKdhS_1.wireOp",EDGE,"1cb9c079-ea9b-4899-8069-e0e3048e911d.sketch_text.stroke-11"),sQuery(id+"FHMxAyK4CFUKdhS_1.wireOp",EDGE,"1cb9c079-ea9b-4899-8069-e0e3048e911d.sketch_text.stroke-12"),sQuery(id+"FHMxAyK4CFUKdhS_1.wireOp",EDGE,"1cb9c079-ea9b-4899-8069-e0e3048e911d.sketch_text.stroke-13"),sQuery(id+"FHMxAyK4CFUKdhS_1.wireOp",EDGE,"1cb9c079-ea9b-4899-8069-e0e3048e911d.sketch_text.stroke-14"),sQuery(id+"FHMxAyK4CFUKdhS_1.wireOp",EDGE,"1cb9c079-ea9b-4899-8069-e0e3048e911d.sketch_text.stroke-15"),sQuery(id+"FHMxAyK4CFUKdhS_1.wireOp",EDGE,"1cb9c079-ea9b-4899-8069-e0e3048e911d.sketch_text.stroke-16"),sQuery(id+"FHMxAyK4CFUKdhS_1.wireOp",EDGE,"1cb9c079-ea9b-4899-8069-e0e3048e911d.sketch_text.stroke-17"),sQuery(id+"FHMxAyK4CFUKdhS_1.wireOp",EDGE,"1cb9c079-ea9b-4899-8069-e0e3048e911d.sketch_text.stroke-18"),sQuery(id+"FHMxAyK4CFUKdhS_1.wireOp",EDGE,"1cb9c079-ea9b-4899-8069-e0e3048e911d.sketch_text.stroke-19"),sQuery(id+"FHMxAyK4CFUKdhS_1.wireOp",EDGE,"1cb9c079-ea9b-4899-8069-e0e3048e911d.sketch_text.stroke-20"),sQuery(id+"FHMxAyK4CFUKdhS_1.wireOp",EDGE,"1cb9c079-ea9b-4899-8069-e0e3048e911d.sketch_text.stroke-21"),sQuery(id+"FHMxAyK4CFUKdhS_1.wireOp",EDGE,"1cb9c079-ea9b-4899-8069-e0e3048e911d.sketch_text.stroke-22"),sQuery(id+"FHMxAyK4CFUKdhS_1.wireOp",EDGE,"1cb9c079-ea9b-4899-8069-e0e3048e911d.sketch_text.stroke-23"),sQuery(id+"FHMxAyK4CFUKdhS_1.wireOp",EDGE,"1cb9c079-ea9b-4899-8069-e0e3048e911d.sketch_text.stroke-24"),sQuery(id+"FHMxAyK4CFUKdhS_1.wireOp",EDGE,"1cb9c079-ea9b-4899-8069-e0e3048e911d.sketch_text.stroke-25"),sQuery(id+"FHMxAyK4CFUKdhS_1.wireOp",EDGE,"1cb9c079-ea9b-4899-8069-e0e3048e911d.sketch_text.stroke-26"),sQuery(id+"FHMxAyK4CFUKdhS_1.wireOp",EDGE,"1cb9c079-ea9b-4899-8069-e0e3048e911d.sketch_text.stroke-27"),sQuery(id+"FHMxAyK4CFUKdhS_1.wireOp",EDGE,"1cb9c079-ea9b-4899-8069-e0e3048e911d.sketch_text.stroke-28"),sQuery(id+"FHMxAyK4CFUKdhS_1.wireOp",EDGE,"1cb9c079-ea9b-4899-8069-e0e3048e911d.sketch_text.stroke-29"),sQuery(id+"FHMxAyK4CFUKdhS_1.wireOp",EDGE,"1cb9c079-ea9b-4899-8069-e0e3048e911d.sketch_text.stroke-30"),sQuery(id+"FHMxAyK4CFUKdhS_1.wireOp",EDGE,"1cb9c079-ea9b-4899-8069-e0e3048e911d.sketch_text.stroke-31"),sQuery(id+"FHMxAyK4CFUKdhS_1.wireOp",EDGE,"1cb9c079-ea9b-4899-8069-e0e3048e911d.sketch_text.stroke-32"),sQuery(id+"FHMxAyK4CFUKdhS_1.wireOp",EDGE,"1cb9c079-ea9b-4899-8069-e0e3048e911d.sketch_text.stroke-33"),sQuery(id+"FHMxAyK4CFUKdhS_1.wireOp",EDGE,"1cb9c079-ea9b-4899-8069-e0e3048e911d.sketch_text.stroke-34"),sQuery(id+"FHMxAyK4CFUKdhS_1.wireOp",EDGE,"1cb9c079-ea9b-4899-8069-e0e3048e911d.sketch_text.stroke-35"),sQuery(id+"FHMxAyK4CFUKdhS_1.wireOp",EDGE,"1cb9c079-ea9b-4899-8069-e0e3048e911d.sketch_text.stroke-36"),sQuery(id+"FHMxAyK4CFUKdhS_1.wireOp",EDGE,"1cb9c079-ea9b-4899-8069-e0e3048e911d.sketch_text.stroke-37"),sQuery(id+"FHMxAyK4CFUKdhS_1.wireOp",EDGE,"1cb9c079-ea9b-4899-8069-e0e3048e911d.sketch_text.stroke-38"),sQuery(id+"FHMxAyK4CFUKdhS_1.wireOp",EDGE,"1cb9c079-ea9b-4899-8069-e0e3048e911d.sketch_text.stroke-39"),sQuery(id+"FHMxAyK4CFUKdhS_1.wireOp",EDGE,"1cb9c079-ea9b-4899-8069-e0e3048e911d.sketch_text.stroke-40"),sQuery(id+"FHMxAyK4CFUKdhS_1.wireOp",EDGE,"1cb9c079-ea9b-4899-8069-e0e3048e911d.sketch_text.stroke-41"),sQuery(id+"FHMxAyK4CFUKdhS_1.wireOp",EDGE,"1cb9c079-ea9b-4899-8069-e0e3048e911d.sketch_text.stroke-42"),sQuery(id+"FHMxAyK4CFUKdhS_1.wireOp",EDGE,"1cb9c079-ea9b-4899-8069-e0e3048e911d.sketch_text.stroke-43"),sQuery(id+"FHMxAyK4CFUKdhS_1.wireOp",EDGE,"1cb9c079-ea9b-4899-8069-e0e3048e911d.sketch_text.stroke-44"),sQuery(id+"FHMxAyK4CFUKdhS_1.wireOp",EDGE,"1cb9c079-ea9b-4899-8069-e0e3048e911d.sketch_text.stroke-45"),sQuery(id+"FHMxAyK4CFUKdhS_1.wireOp",EDGE,"1cb9c079-ea9b-4899-8069-e0e3048e911d.sketch_text.stroke-46"),sQuery(id+"FHMxAyK4CFUKdhS_1.wireOp",EDGE,"1cb9c079-ea9b-4899-8069-e0e3048e911d.sketch_text.stroke-47"),sQuery(id+"FHMxAyK4CFUKdhS_1.wireOp",EDGE,"1cb9c079-ea9b-4899-8069-e0e3048e911d.sketch_text.stroke-48"),sQuery(id+"FHMxAyK4CFUKdhS_1.wireOp",EDGE,"1cb9c079-ea9b-4899-8069-e0e3048e911d.sketch_text.stroke-49"),sQuery(id+"FHMxAyK4CFUKdhS_1.wireOp",EDGE,"1cb9c079-ea9b-4899-8069-e0e3048e911d.sketch_text.stroke-50"),sQuery(id+"FHMxAyK4CFUKdhS_1.wireOp",EDGE,"1cb9c079-ea9b-4899-8069-e0e3048e911d.sketch_text.stroke-51"),sQuery(id+"FHMxAyK4CFUKdhS_1.wireOp",EDGE,"1cb9c079-ea9b-4899-8069-e0e3048e911d.sketch_text.stroke-52"),sQuery(id+"FHMxAyK4CFUKdhS_1.wireOp",EDGE,"1cb9c079-ea9b-4899-8069-e0e3048e911d.sketch_text.stroke-53"),sQuery(id+"FHMxAyK4CFUKdhS_1.wireOp",EDGE,"1cb9c079-ea9b-4899-8069-e0e3048e911d.sketch_text.stroke-54"),sQuery(id+"FHMxAyK4CFUKdhS_1.wireOp",EDGE,"1cb9c079-ea9b-4899-8069-e0e3048e911d.sketch_text.stroke-55"),sQuery(id+"FHMxAyK4CFUKdhS_1.wireOp",EDGE,"1cb9c079-ea9b-4899-8069-e0e3048e911d.sketch_text.stroke-56"),sQuery(id+"FHMxAyK4CFUKdhS_1.wireOp",EDGE,"1cb9c079-ea9b-4899-8069-e0e3048e911d.sketch_text.stroke-57"),sQuery(id+"FHMxAyK4CFUKdhS_1.wireOp",EDGE,"1cb9c079-ea9b-4899-8069-e0e3048e911d.sketch_text.stroke-58"),sQuery(id+"FHMxAyK4CFUKdhS_1.wireOp",EDGE,"1cb9c079-ea9b-4899-8069-e0e3048e911d.sketch_text.stroke-59"),sQuery(id+"FHMxAyK4CFUKdhS_1.wireOp",EDGE,"1cb9c079-ea9b-4899-8069-e0e3048e911d.sketch_text.stroke-60"),sQuery(id+"FHMxAyK4CFUKdhS_1.wireOp",EDGE,"1cb9c079-ea9b-4899-8069-e0e3048e911d.sketch_text.stroke-61"),sQuery(id+"FHMxAyK4CFUKdhS_1.wireOp",EDGE,"1cb9c079-ea9b-4899-8069-e0e3048e911d.sketch_text.stroke-62"),sQuery(id+"FHMxAyK4CFUKdhS_1.wireOp",EDGE,"1cb9c079-ea9b-4899-8069-e0e3048e911d.sketch_text.stroke-71"),sQuery(id+"FHMxAyK4CFUKdhS_1.wireOp",EDGE,"1cb9c079-ea9b-4899-8069-e0e3048e911d.sketch_text.stroke-72"),sQuery(id+"FHMxAyK4CFUKdhS_1.wireOp",EDGE,"1cb9c079-ea9b-4899-8069-e0e3048e911d.sketch_text.stroke-73"),sQuery(id+"FHMxAyK4CFUKdhS_1.wireOp",EDGE,"1cb9c079-ea9b-4899-8069-e0e3048e911d.sketch_text.stroke-74"),sQuery(id+"FHMxAyK4CFUKdhS_1.wireOp",EDGE,"1cb9c079-ea9b-4899-8069-e0e3048e911d.sketch_text.stroke-75"),sQuery(id+"FHMxAyK4CFUKdhS_1.wireOp",EDGE,"1cb9c079-ea9b-4899-8069-e0e3048e911d.sketch_text.stroke-76"),sQuery(id+"FHMxAyK4CFUKdhS_1.wireOp",EDGE,"1cb9c079-ea9b-4899-8069-e0e3048e911d.sketch_text.stroke-77"),sQuery(id+"FHMxAyK4CFUKdhS_1.wireOp",EDGE,"1cb9c079-ea9b-4899-8069-e0e3048e911d.sketch_text.stroke-78"),sQuery(id+"FHMxAyK4CFUKdhS_1.wireOp",EDGE,"1cb9c079-ea9b-4899-8069-e0e3048e911d.sketch_text.stroke-79"),sQuery(id+"FHMxAyK4CFUKdhS_1.wireOp",EDGE,"1cb9c079-ea9b-4899-8069-e0e3048e911d.sketch_text.stroke-80"),sQuery(id+"FHMxAyK4CFUKdhS_1.wireOp",EDGE,"1cb9c079-ea9b-4899-8069-e0e3048e911d.sketch_text.stroke-81"),sQuery(id+"FHMxAyK4CFUKdhS_1.wireOp",EDGE,"1cb9c079-ea9b-4899-8069-e0e3048e911d.sketch_text.stroke-82"),sQuery(id+"FHMxAyK4CFUKdhS_1.wireOp",EDGE,"1cb9c079-ea9b-4899-8069-e0e3048e911d.sketch_text.stroke-83"),sQuery(id+"FHMxAyK4CFUKdhS_1.wireOp",EDGE,"1cb9c079-ea9b-4899-8069-e0e3048e911d.sketch_text.stroke-84"),sQuery(id+"FHMxAyK4CFUKdhS_1.wireOp",EDGE,"1cb9c079-ea9b-4899-8069-e0e3048e911d.sketch_text.stroke-85"),sQuery(id+"FHMxAyK4CFUKdhS_1.wireOp",EDGE,"1cb9c079-ea9b-4899-8069-e0e3048e911d.sketch_text.stroke-86"),sQuery(id+"FHMxAyK4CFUKdhS_1.wireOp",EDGE,"1cb9c079-ea9b-4899-8069-e0e3048e911d.sketch_text.stroke-87"),sQuery(id+"FHMxAyK4CFUKdhS_1.wireOp",EDGE,"1cb9c079-ea9b-4899-8069-e0e3048e911d.sketch_text.stroke-88"),sQuery(id+"FHMxAyK4CFUKdhS_1.wireOp",EDGE,"1cb9c079-ea9b-4899-8069-e0e3048e911d.sketch_text.stroke-89"),sQuery(id+"FHMxAyK4CFUKdhS_1.wireOp",EDGE,"1cb9c079-ea9b-4899-8069-e0e3048e911d.sketch_text.stroke-90"),sQuery(id+"FHMxAyK4CFUKdhS_1.wireOp",EDGE,"1cb9c079-ea9b-4899-8069-e0e3048e911d.sketch_text.stroke-91"),sQuery(id+"FHMxAyK4CFUKdhS_1.wireOp",EDGE,"1cb9c079-ea9b-4899-8069-e0e3048e911d.sketch_text.stroke-92"),sQuery(id+"FHMxAyK4CFUKdhS_1.wireOp",EDGE,"1cb9c079-ea9b-4899-8069-e0e3048e911d.sketch_text.stroke-93"),sQuery(id+"FHMxAyK4CFUKdhS_1.wireOp",EDGE,"1cb9c079-ea9b-4899-8069-e0e3048e911d.sketch_text.stroke-94"),sQuery(id+"FHMxAyK4CFUKdhS_1.wireOp",EDGE,"1cb9c079-ea9b-4899-8069-e0e3048e911d.sketch_text.stroke-95"),sQuery(id+"FHMxAyK4CFUKdhS_1.wireOp",EDGE,"1cb9c079-ea9b-4899-8069-e0e3048e911d.sketch_text.stroke-96"),sQuery(id+"FHMxAyK4CFUKdhS_1.wireOp",EDGE,"1cb9c079-ea9b-4899-8069-e0e3048e911d.sketch_text.stroke-97"),sQuery(id+"FHMxAyK4CFUKdhS_1.wireOp",EDGE,"1cb9c079-ea9b-4899-8069-e0e3048e911d.sketch_text.stroke-103"),sQuery(id+"FHMxAyK4CFUKdhS_1.wireOp",EDGE,"1cb9c079-ea9b-4899-8069-e0e3048e911d.sketch_text.stroke-104"),sQuery(id+"FHMxAyK4CFUKdhS_1.wireOp",EDGE,"1cb9c079-ea9b-4899-8069-e0e3048e911d.sketch_text.stroke-105"),sQuery(id+"FHMxAyK4CFUKdhS_1.wireOp",EDGE,"1cb9c079-ea9b-4899-8069-e0e3048e911d.sketch_text.stroke-106"),sQuery(id+"FHMxAyK4CFUKdhS_1.wireOp",EDGE,"1cb9c079-ea9b-4899-8069-e0e3048e911d.sketch_text.stroke-107"),sQuery(id+"FHMxAyK4CFUKdhS_1.wireOp",EDGE,"1cb9c079-ea9b-4899-8069-e0e3048e911d.sketch_text.stroke-108"),sQuery(id+"FHMxAyK4CFUKdhS_1.wireOp",EDGE,"1cb9c079-ea9b-4899-8069-e0e3048e911d.sketch_text.stroke-109"),sQuery(id+"FHMxAyK4CFUKdhS_1.wireOp",EDGE,"1cb9c079-ea9b-4899-8069-e0e3048e911d.sketch_text.stroke-110"),sQuery(id+"FHMxAyK4CFUKdhS_1.wireOp",EDGE,"1cb9c079-ea9b-4899-8069-e0e3048e911d.sketch_text.stroke-111"),sQuery(id+"FHMxAyK4CFUKdhS_1.wireOp",EDGE,"1cb9c079-ea9b-4899-8069-e0e3048e911d.sketch_text.stroke-112"),sQuery(id+"FHMxAyK4CFUKdhS_1.wireOp",EDGE,"1cb9c079-ea9b-4899-8069-e0e3048e911d.sketch_text.stroke-113"),sQuery(id+"FHMxAyK4CFUKdhS_1.wireOp",EDGE,"1cb9c079-ea9b-4899-8069-e0e3048e911d.sketch_text.stroke-114"),sQuery(id+"FHMxAyK4CFUKdhS_1.wireOp",EDGE,"1cb9c079-ea9b-4899-8069-e0e3048e911d.sketch_text.stroke-115"),sQuery(id+"FHMxAyK4CFUKdhS_1.wireOp",EDGE,"1cb9c079-ea9b-4899-8069-e0e3048e911d.sketch_text.stroke-116"),sQuery(id+"FHMxAyK4CFUKdhS_1.wireOp",EDGE,"1cb9c079-ea9b-4899-8069-e0e3048e911d.sketch_text.stroke-117"),sQuery(id+"FHMxAyK4CFUKdhS_1.wireOp",EDGE,"1cb9c079-ea9b-4899-8069-e0e3048e911d.sketch_text.stroke-118"),sQuery(id+"FHMxAyK4CFUKdhS_1.wireOp",EDGE,"1cb9c079-ea9b-4899-8069-e0e3048e911d.sketch_text.stroke-119"),sQuery(id+"FHMxAyK4CFUKdhS_1.wireOp",EDGE,"1cb9c079-ea9b-4899-8069-e0e3048e911d.sketch_text.stroke-120"),sQuery(id+"FHMxAyK4CFUKdhS_1.wireOp",EDGE,"1cb9c079-ea9b-4899-8069-e0e3048e911d.sketch_text.stroke-121"),sQuery(id+"FHMxAyK4CFUKdhS_1.wireOp",EDGE,"1cb9c079-ea9b-4899-8069-e0e3048e911d.sketch_text.stroke-122"),sQuery(id+"FHMxAyK4CFUKdhS_1.wireOp",EDGE,"1cb9c079-ea9b-4899-8069-e0e3048e911d.sketch_text.stroke-123"),sQuery(id+"FHMxAyK4CFUKdhS_1.wireOp",EDGE,"1cb9c079-ea9b-4899-8069-e0e3048e911d.sketch_text.stroke-124"),sQuery(id+"FHMxAyK4CFUKdhS_1.wireOp",EDGE,"1cb9c079-ea9b-4899-8069-e0e3048e911d.sketch_text.stroke-125"),sQuery(id+"FHMxAyK4CFUKdhS_1.wireOp",EDGE,"1cb9c079-ea9b-4899-8069-e0e3048e911d.sketch_text.stroke-126"),sQuery(id+"FHMxAyK4CFUKdhS_1.wireOp",EDGE,"1cb9c079-ea9b-4899-8069-e0e3048e911d.sketch_text.stroke-127"),sQuery(id+"FHMxAyK4CFUKdhS_1.wireOp",EDGE,"1cb9c079-ea9b-4899-8069-e0e3048e911d.sketch_text.stroke-128"),sQuery(id+"FHMxAyK4CFUKdhS_1.wireOp",EDGE,"1cb9c079-ea9b-4899-8069-e0e3048e911d.sketch_text.stroke-129"),sQuery(id+"FHMxAyK4CFUKdhS_1.wireOp",EDGE,"1cb9c079-ea9b-4899-8069-e0e3048e911d.sketch_text.stroke-130"),sQuery(id+"FHMxAyK4CFUKdhS_1.wireOp",EDGE,"1cb9c079-ea9b-4899-8069-e0e3048e911d.sketch_text.stroke-131"),sQuery(id+"FHMxAyK4CFUKdhS_1.wireOp",EDGE,"1cb9c079-ea9b-4899-8069-e0e3048e911d.sketch_text.stroke-132"),sQuery(id+"FHMxAyK4CFUKdhS_1.wireOp",EDGE,"1cb9c079-ea9b-4899-8069-e0e3048e911d.sketch_text.stroke-133"),sQuery(id+"FHMxAyK4CFUKdhS_1.wireOp",EDGE,"1cb9c079-ea9b-4899-8069-e0e3048e911d.sketch_text.stroke-134"),sQuery(id+"FHMxAyK4CFUKdhS_1.wireOp",EDGE,"1cb9c079-ea9b-4899-8069-e0e3048e911d.sketch_text.stroke-135"),sQuery(id+"FHMxAyK4CFUKdhS_1.wireOp",EDGE,"1cb9c079-ea9b-4899-8069-e0e3048e911d.sketch_text.stroke-136"),sQuery(id+"FHMxAyK4CFUKdhS_1.wireOp",EDGE,"1cb9c079-ea9b-4899-8069-e0e3048e911d.sketch_text.stroke-137"),sQuery(id+"FHMxAyK4CFUKdhS_1.wireOp",EDGE,"1cb9c079-ea9b-4899-8069-e0e3048e911d.sketch_text.stroke-138"),sQuery(id+"FHMxAyK4CFUKdhS_1.wireOp",EDGE,"1cb9c079-ea9b-4899-8069-e0e3048e911d.sketch_text.stroke-139"),sQuery(id+"FHMxAyK4CFUKdhS_1.wireOp",EDGE,"1cb9c079-ea9b-4899-8069-e0e3048e911d.sketch_text.stroke-140"),sQuery(id+"FHMxAyK4CFUKdhS_1.wireOp",EDGE,"1cb9c079-ea9b-4899-8069-e0e3048e911d.sketch_text.stroke-141"),sQuery(id+"FHMxAyK4CFUKdhS_1.wireOp",EDGE,"1cb9c079-ea9b-4899-8069-e0e3048e911d.sketch_text.stroke-142"),sQuery(id+"FHMxAyK4CFUKdhS_1.wireOp",EDGE,"1cb9c079-ea9b-4899-8069-e0e3048e911d.sketch_text.stroke-143"),sQuery(id+"FHMxAyK4CFUKdhS_1.wireOp",EDGE,"1cb9c079-ea9b-4899-8069-e0e3048e911d.sketch_text.stroke-144"),sQuery(id+"FHMxAyK4CFUKdhS_1.wireOp",EDGE,"1cb9c079-ea9b-4899-8069-e0e3048e911d.sketch_text.stroke-145"),sQuery(id+"FHMxAyK4CFUKdhS_1.wireOp",EDGE,"1cb9c079-ea9b-4899-8069-e0e3048e911d.sketch_text.stroke-146"),sQuery(id+"FHMxAyK4CFUKdhS_1.wireOp",EDGE,"1cb9c079-ea9b-4899-8069-e0e3048e911d.sketch_text.stroke-147"),sQuery(id+"FHMxAyK4CFUKdhS_1.wireOp",EDGE,"1cb9c079-ea9b-4899-8069-e0e3048e911d.sketch_text.stroke-148"),sQuery(id+"FHMxAyK4CFUKdhS_1.wireOp",EDGE,"1cb9c079-ea9b-4899-8069-e0e3048e911d.sketch_text.stroke-149"),sQuery(id+"FHMxAyK4CFUKdhS_1.wireOp",EDGE,"1cb9c079-ea9b-4899-8069-e0e3048e911d.sketch_text.stroke-150"),sQuery(id+"FHMxAyK4CFUKdhS_1.wireOp",EDGE,"1cb9c079-ea9b-4899-8069-e0e3048e911d.sketch_text.stroke-151"),sQuery(id+"FHMxAyK4CFUKdhS_1.wireOp",EDGE,"1cb9c079-ea9b-4899-8069-e0e3048e911d.sketch_text.stroke-152"),sQuery(id+"FHMxAyK4CFUKdhS_1.wireOp",EDGE,"1cb9c079-ea9b-4899-8069-e0e3048e911d.sketch_text.stroke-153"),sQuery(id+"FHMxAyK4CFUKdhS_1.wireOp",EDGE,"1cb9c079-ea9b-4899-8069-e0e3048e911d.sketch_text.stroke-159"),sQuery(id+"FHMxAyK4CFUKdhS_1.wireOp",EDGE,"1cb9c079-ea9b-4899-8069-e0e3048e911d.sketch_text.stroke-160"),sQuery(id+"FHMxAyK4CFUKdhS_1.wireOp",EDGE,"1cb9c079-ea9b-4899-8069-e0e3048e911d.sketch_text.stroke-161"),sQuery(id+"FHMxAyK4CFUKdhS_1.wireOp",EDGE,"1cb9c079-ea9b-4899-8069-e0e3048e911d.sketch_text.stroke-162"),sQuery(id+"FHMxAyK4CFUKdhS_1.wireOp",EDGE,"1cb9c079-ea9b-4899-8069-e0e3048e911d.sketch_text.stroke-163"),sQuery(id+"FHMxAyK4CFUKdhS_1.wireOp",EDGE,"1cb9c079-ea9b-4899-8069-e0e3048e911d.sketch_text.stroke-164"),sQuery(id+"FHMxAyK4CFUKdhS_1.wireOp",EDGE,"1cb9c079-ea9b-4899-8069-e0e3048e911d.sketch_text.stroke-165"),sQuery(id+"FHMxAyK4CFUKdhS_1.wireOp",EDGE,"1cb9c079-ea9b-4899-8069-e0e3048e911d.sketch_text.stroke-166"),sQuery(id+"FHMxAyK4CFUKdhS_1.wireOp",EDGE,"1cb9c079-ea9b-4899-8069-e0e3048e911d.sketch_text.stroke-167"),sQuery(id+"FHMxAyK4CFUKdhS_1.wireOp",EDGE,"1cb9c079-ea9b-4899-8069-e0e3048e911d.sketch_text.stroke-168"),sQuery(id+"FHMxAyK4CFUKdhS_1.wireOp",EDGE,"1cb9c079-ea9b-4899-8069-e0e3048e911d.sketch_text.stroke-169"),sQuery(id+"FHMxAyK4CFUKdhS_1.wireOp",EDGE,"1cb9c079-ea9b-4899-8069-e0e3048e911d.sketch_text.stroke-170"),sQuery(id+"FHMxAyK4CFUKdhS_1.wireOp",EDGE,"1cb9c079-ea9b-4899-8069-e0e3048e911d.sketch_text.stroke-171"),sQuery(id+"FHMxAyK4CFUKdhS_1.wireOp",EDGE,"1cb9c079-ea9b-4899-8069-e0e3048e911d.sketch_text.stroke-172"),sQuery(id+"FHMxAyK4CFUKdhS_1.wireOp",EDGE,"1cb9c079-ea9b-4899-8069-e0e3048e911d.sketch_text.stroke-173"),sQuery(id+"FHMxAyK4CFUKdhS_1.wireOp",EDGE,"1cb9c079-ea9b-4899-8069-e0e3048e911d.sketch_text.stroke-174"),sQuery(id+"FHMxAyK4CFUKdhS_1.wireOp",EDGE,"1cb9c079-ea9b-4899-8069-e0e3048e911d.sketch_text.stroke-175"),sQuery(id+"FHMxAyK4CFUKdhS_1.wireOp",EDGE,"1cb9c079-ea9b-4899-8069-e0e3048e911d.sketch_text.stroke-176"),sQuery(id+"FHMxAyK4CFUKdhS_1.wireOp",EDGE,"1cb9c079-ea9b-4899-8069-e0e3048e911d.sketch_text.stroke-177"),sQuery(id+"FHMxAyK4CFUKdhS_1.wireOp",EDGE,"1cb9c079-ea9b-4899-8069-e0e3048e911d.sketch_text.stroke-178"),sQuery(id+"FHMxAyK4CFUKdhS_1.wireOp",EDGE,"1cb9c079-ea9b-4899-8069-e0e3048e911d.sketch_text.stroke-179"),sQuery(id+"FHMxAyK4CFUKdhS_1.wireOp",EDGE,"1cb9c079-ea9b-4899-8069-e0e3048e911d.sketch_text.stroke-180"),sQuery(id+"F2.wireOp",EDGE,"E26"),subQ2])],"isStart":true}),makeQuery(id+"F3.opExtrude","SWEPT_FACE",FACE,{"disambiguationData":[OSD([subQ2])]})])],"derivedFrom":makeQuery(id+"F3.opExtrude","CAP_EDGE",EDGE,{"disambiguationData":[OSD([subQ2])],"isStart":true})});}
            var Q24;
            {var subQ0=sQuery(id+"F0.wireOp",EDGE,"E0.top");var subQ1=sQuery(id+"F0.wireOp",EDGE,"E0.bottom");var subQ2=sQuery(id+"F2.wireOp",EDGE,"E26");Q24=makeQuery(id+"F3.boolean.opBoolean","SPLIT",EDGE,{"disambiguationData":[TD([makeQuery(id+"F1.opExtrude","CAP_FACE",FACE,{"disambiguationData":[OSD([subQ1,subQ0,sQuery(id+"F0.wireOp",EDGE,"E0.left"),sQuery(id+"F0.wireOp",EDGE,"E0.right")])],"isStart":false}),makeQuery(id+"F1.opExtrude","SWEPT_FACE",FACE,{"disambiguationData":[OSD([subQ0])]}),makeQuery(id+"F3.opExtrude","SWEPT_FACE",FACE,{"disambiguationData":[OSD([subQ2])]}),makeQuery(id+"F3.opExtrude","CAP_FACE",FACE,{"disambiguationData":[OSD([subQ1,sQuery(id+"FQ5JFwxVdaqARUP_1.wireOp",EDGE,"fcba4419-a2ee-464f-be9d-58f11bf3418b.sketch_text.stroke-0"),sQuery(id+"FQ5JFwxVdaqARUP_1.wireOp",EDGE,"fcba4419-a2ee-464f-be9d-58f11bf3418b.sketch_text.stroke-1"),sQuery(id+"FQ5JFwxVdaqARUP_1.wireOp",EDGE,"fcba4419-a2ee-464f-be9d-58f11bf3418b.sketch_text.stroke-2"),sQuery(id+"FQ5JFwxVdaqARUP_1.wireOp",EDGE,"fcba4419-a2ee-464f-be9d-58f11bf3418b.sketch_text.stroke-3"),sQuery(id+"FQ5JFwxVdaqARUP_1.wireOp",EDGE,"fcba4419-a2ee-464f-be9d-58f11bf3418b.sketch_text.stroke-4"),sQuery(id+"FQ5JFwxVdaqARUP_1.wireOp",EDGE,"fcba4419-a2ee-464f-be9d-58f11bf3418b.sketch_text.stroke-5"),sQuery(id+"FQ5JFwxVdaqARUP_1.wireOp",EDGE,"fcba4419-a2ee-464f-be9d-58f11bf3418b.sketch_text.stroke-6"),sQuery(id+"FQ5JFwxVdaqARUP_1.wireOp",EDGE,"fcba4419-a2ee-464f-be9d-58f11bf3418b.sketch_text.stroke-7"),sQuery(id+"FQ5JFwxVdaqARUP_1.wireOp",EDGE,"fcba4419-a2ee-464f-be9d-58f11bf3418b.sketch_text.stroke-8"),sQuery(id+"FQ5JFwxVdaqARUP_1.wireOp",EDGE,"fcba4419-a2ee-464f-be9d-58f11bf3418b.sketch_text.stroke-9"),sQuery(id+"FQ5JFwxVdaqARUP_1.wireOp",EDGE,"fcba4419-a2ee-464f-be9d-58f11bf3418b.sketch_text.stroke-10"),sQuery(id+"FQ5JFwxVdaqARUP_1.wireOp",EDGE,"fcba4419-a2ee-464f-be9d-58f11bf3418b.sketch_text.stroke-11"),sQuery(id+"FQ5JFwxVdaqARUP_1.wireOp",EDGE,"fcba4419-a2ee-464f-be9d-58f11bf3418b.sketch_text.stroke-12"),sQuery(id+"FQ5JFwxVdaqARUP_1.wireOp",EDGE,"fcba4419-a2ee-464f-be9d-58f11bf3418b.sketch_text.stroke-13"),sQuery(id+"FQ5JFwxVdaqARUP_1.wireOp",EDGE,"fcba4419-a2ee-464f-be9d-58f11bf3418b.sketch_text.stroke-14"),sQuery(id+"FQ5JFwxVdaqARUP_1.wireOp",EDGE,"fcba4419-a2ee-464f-be9d-58f11bf3418b.sketch_text.stroke-15"),sQuery(id+"FQ5JFwxVdaqARUP_1.wireOp",EDGE,"fcba4419-a2ee-464f-be9d-58f11bf3418b.sketch_text.stroke-16"),sQuery(id+"FQ5JFwxVdaqARUP_1.wireOp",EDGE,"fcba4419-a2ee-464f-be9d-58f11bf3418b.sketch_text.stroke-17"),sQuery(id+"FQ5JFwxVdaqARUP_1.wireOp",EDGE,"fcba4419-a2ee-464f-be9d-58f11bf3418b.sketch_text.stroke-18"),sQuery(id+"FQ5JFwxVdaqARUP_1.wireOp",EDGE,"fcba4419-a2ee-464f-be9d-58f11bf3418b.sketch_text.stroke-19"),sQuery(id+"FQ5JFwxVdaqARUP_1.wireOp",EDGE,"fcba4419-a2ee-464f-be9d-58f11bf3418b.sketch_text.stroke-20"),sQuery(id+"FQ5JFwxVdaqARUP_1.wireOp",EDGE,"fcba4419-a2ee-464f-be9d-58f11bf3418b.sketch_text.stroke-21"),sQuery(id+"FQ5JFwxVdaqARUP_1.wireOp",EDGE,"fcba4419-a2ee-464f-be9d-58f11bf3418b.sketch_text.stroke-22"),sQuery(id+"FQ5JFwxVdaqARUP_1.wireOp",EDGE,"fcba4419-a2ee-464f-be9d-58f11bf3418b.sketch_text.stroke-23"),sQuery(id+"FQ5JFwxVdaqARUP_1.wireOp",EDGE,"fcba4419-a2ee-464f-be9d-58f11bf3418b.sketch_text.stroke-24"),sQuery(id+"FQ5JFwxVdaqARUP_1.wireOp",EDGE,"fcba4419-a2ee-464f-be9d-58f11bf3418b.sketch_text.stroke-25"),sQuery(id+"FQ5JFwxVdaqARUP_1.wireOp",EDGE,"fcba4419-a2ee-464f-be9d-58f11bf3418b.sketch_text.stroke-26"),sQuery(id+"FQ5JFwxVdaqARUP_1.wireOp",EDGE,"fcba4419-a2ee-464f-be9d-58f11bf3418b.sketch_text.stroke-27"),sQuery(id+"FQ5JFwxVdaqARUP_1.wireOp",EDGE,"fcba4419-a2ee-464f-be9d-58f11bf3418b.sketch_text.stroke-28"),sQuery(id+"FQ5JFwxVdaqARUP_1.wireOp",EDGE,"fcba4419-a2ee-464f-be9d-58f11bf3418b.sketch_text.stroke-29"),sQuery(id+"FQ5JFwxVdaqARUP_1.wireOp",EDGE,"fcba4419-a2ee-464f-be9d-58f11bf3418b.sketch_text.stroke-30"),sQuery(id+"FQ5JFwxVdaqARUP_1.wireOp",EDGE,"fcba4419-a2ee-464f-be9d-58f11bf3418b.sketch_text.stroke-31"),sQuery(id+"FQ5JFwxVdaqARUP_1.wireOp",EDGE,"fcba4419-a2ee-464f-be9d-58f11bf3418b.sketch_text.stroke-32"),sQuery(id+"FQ5JFwxVdaqARUP_1.wireOp",EDGE,"fcba4419-a2ee-464f-be9d-58f11bf3418b.sketch_text.stroke-33"),sQuery(id+"FQ5JFwxVdaqARUP_1.wireOp",EDGE,"fcba4419-a2ee-464f-be9d-58f11bf3418b.sketch_text.stroke-34"),sQuery(id+"FQ5JFwxVdaqARUP_1.wireOp",EDGE,"fcba4419-a2ee-464f-be9d-58f11bf3418b.sketch_text.stroke-35"),sQuery(id+"FQ5JFwxVdaqARUP_1.wireOp",EDGE,"fcba4419-a2ee-464f-be9d-58f11bf3418b.sketch_text.stroke-36"),sQuery(id+"FQ5JFwxVdaqARUP_1.wireOp",EDGE,"fcba4419-a2ee-464f-be9d-58f11bf3418b.sketch_text.stroke-37"),sQuery(id+"FQ5JFwxVdaqARUP_1.wireOp",EDGE,"fcba4419-a2ee-464f-be9d-58f11bf3418b.sketch_text.stroke-38"),sQuery(id+"FQ5JFwxVdaqARUP_1.wireOp",EDGE,"fcba4419-a2ee-464f-be9d-58f11bf3418b.sketch_text.stroke-39"),sQuery(id+"FQ5JFwxVdaqARUP_1.wireOp",EDGE,"fcba4419-a2ee-464f-be9d-58f11bf3418b.sketch_text.stroke-40"),sQuery(id+"FQ5JFwxVdaqARUP_1.wireOp",EDGE,"fcba4419-a2ee-464f-be9d-58f11bf3418b.sketch_text.stroke-41"),sQuery(id+"FQ5JFwxVdaqARUP_1.wireOp",EDGE,"fcba4419-a2ee-464f-be9d-58f11bf3418b.sketch_text.stroke-42"),sQuery(id+"FQ5JFwxVdaqARUP_1.wireOp",EDGE,"fcba4419-a2ee-464f-be9d-58f11bf3418b.sketch_text.stroke-43"),sQuery(id+"FQ5JFwxVdaqARUP_1.wireOp",EDGE,"fcba4419-a2ee-464f-be9d-58f11bf3418b.sketch_text.stroke-44"),sQuery(id+"FQ5JFwxVdaqARUP_1.wireOp",EDGE,"fcba4419-a2ee-464f-be9d-58f11bf3418b.sketch_text.stroke-45"),sQuery(id+"FQ5JFwxVdaqARUP_1.wireOp",EDGE,"fcba4419-a2ee-464f-be9d-58f11bf3418b.sketch_text.stroke-46"),sQuery(id+"FQ5JFwxVdaqARUP_1.wireOp",EDGE,"fcba4419-a2ee-464f-be9d-58f11bf3418b.sketch_text.stroke-47"),sQuery(id+"FQ5JFwxVdaqARUP_1.wireOp",EDGE,"fcba4419-a2ee-464f-be9d-58f11bf3418b.sketch_text.stroke-48"),sQuery(id+"FQ5JFwxVdaqARUP_1.wireOp",EDGE,"fcba4419-a2ee-464f-be9d-58f11bf3418b.sketch_text.stroke-49"),sQuery(id+"FQ5JFwxVdaqARUP_1.wireOp",EDGE,"fcba4419-a2ee-464f-be9d-58f11bf3418b.sketch_text.stroke-50"),sQuery(id+"FQ5JFwxVdaqARUP_1.wireOp",EDGE,"fcba4419-a2ee-464f-be9d-58f11bf3418b.sketch_text.stroke-51"),sQuery(id+"FQ5JFwxVdaqARUP_1.wireOp",EDGE,"fcba4419-a2ee-464f-be9d-58f11bf3418b.sketch_text.stroke-52"),sQuery(id+"FQ5JFwxVdaqARUP_1.wireOp",EDGE,"fcba4419-a2ee-464f-be9d-58f11bf3418b.sketch_text.stroke-53"),sQuery(id+"FQ5JFwxVdaqARUP_1.wireOp",EDGE,"fcba4419-a2ee-464f-be9d-58f11bf3418b.sketch_text.stroke-54"),sQuery(id+"FQ5JFwxVdaqARUP_1.wireOp",EDGE,"fcba4419-a2ee-464f-be9d-58f11bf3418b.sketch_text.stroke-55"),sQuery(id+"FQ5JFwxVdaqARUP_1.wireOp",EDGE,"fcba4419-a2ee-464f-be9d-58f11bf3418b.sketch_text.stroke-56"),sQuery(id+"FQ5JFwxVdaqARUP_1.wireOp",EDGE,"fcba4419-a2ee-464f-be9d-58f11bf3418b.sketch_text.stroke-57"),sQuery(id+"FQ5JFwxVdaqARUP_1.wireOp",EDGE,"fcba4419-a2ee-464f-be9d-58f11bf3418b.sketch_text.stroke-58"),sQuery(id+"FQ5JFwxVdaqARUP_1.wireOp",EDGE,"fcba4419-a2ee-464f-be9d-58f11bf3418b.sketch_text.stroke-59"),sQuery(id+"FQ5JFwxVdaqARUP_1.wireOp",EDGE,"fcba4419-a2ee-464f-be9d-58f11bf3418b.sketch_text.stroke-60"),sQuery(id+"FQ5JFwxVdaqARUP_1.wireOp",EDGE,"fcba4419-a2ee-464f-be9d-58f11bf3418b.sketch_text.stroke-61"),sQuery(id+"FQ5JFwxVdaqARUP_1.wireOp",EDGE,"fcba4419-a2ee-464f-be9d-58f11bf3418b.sketch_text.stroke-62"),sQuery(id+"FQ5JFwxVdaqARUP_1.wireOp",EDGE,"fcba4419-a2ee-464f-be9d-58f11bf3418b.sketch_text.stroke-63"),sQuery(id+"FQ5JFwxVdaqARUP_1.wireOp",EDGE,"fcba4419-a2ee-464f-be9d-58f11bf3418b.sketch_text.stroke-64"),sQuery(id+"FQ5JFwxVdaqARUP_1.wireOp",EDGE,"fcba4419-a2ee-464f-be9d-58f11bf3418b.sketch_text.stroke-65"),sQuery(id+"FQ5JFwxVdaqARUP_1.wireOp",EDGE,"fcba4419-a2ee-464f-be9d-58f11bf3418b.sketch_text.stroke-66"),sQuery(id+"FQ5JFwxVdaqARUP_1.wireOp",EDGE,"fcba4419-a2ee-464f-be9d-58f11bf3418b.sketch_text.stroke-67"),sQuery(id+"FQ5JFwxVdaqARUP_1.wireOp",EDGE,"fcba4419-a2ee-464f-be9d-58f11bf3418b.sketch_text.stroke-68"),sQuery(id+"FQ5JFwxVdaqARUP_1.wireOp",EDGE,"fcba4419-a2ee-464f-be9d-58f11bf3418b.sketch_text.stroke-69"),sQuery(id+"FQ5JFwxVdaqARUP_1.wireOp",EDGE,"fcba4419-a2ee-464f-be9d-58f11bf3418b.sketch_text.stroke-70"),sQuery(id+"FQ5JFwxVdaqARUP_1.wireOp",EDGE,"fcba4419-a2ee-464f-be9d-58f11bf3418b.sketch_text.stroke-71"),sQuery(id+"FQ5JFwxVdaqARUP_1.wireOp",EDGE,"fcba4419-a2ee-464f-be9d-58f11bf3418b.sketch_text.stroke-72"),sQuery(id+"FQ5JFwxVdaqARUP_1.wireOp",EDGE,"fcba4419-a2ee-464f-be9d-58f11bf3418b.sketch_text.stroke-73"),sQuery(id+"FQ5JFwxVdaqARUP_1.wireOp",EDGE,"fcba4419-a2ee-464f-be9d-58f11bf3418b.sketch_text.stroke-74"),sQuery(id+"FQ5JFwxVdaqARUP_1.wireOp",EDGE,"fcba4419-a2ee-464f-be9d-58f11bf3418b.sketch_text.stroke-75"),sQuery(id+"FQ5JFwxVdaqARUP_1.wireOp",EDGE,"fcba4419-a2ee-464f-be9d-58f11bf3418b.sketch_text.stroke-76"),sQuery(id+"FQ5JFwxVdaqARUP_1.wireOp",EDGE,"fcba4419-a2ee-464f-be9d-58f11bf3418b.sketch_text.stroke-77"),sQuery(id+"FQ5JFwxVdaqARUP_1.wireOp",EDGE,"fcba4419-a2ee-464f-be9d-58f11bf3418b.sketch_text.stroke-78"),sQuery(id+"FQ5JFwxVdaqARUP_1.wireOp",EDGE,"fcba4419-a2ee-464f-be9d-58f11bf3418b.sketch_text.stroke-79"),sQuery(id+"FQ5JFwxVdaqARUP_1.wireOp",EDGE,"fcba4419-a2ee-464f-be9d-58f11bf3418b.sketch_text.stroke-80"),sQuery(id+"FQ5JFwxVdaqARUP_1.wireOp",EDGE,"fcba4419-a2ee-464f-be9d-58f11bf3418b.sketch_text.stroke-81"),sQuery(id+"FQ5JFwxVdaqARUP_1.wireOp",EDGE,"fcba4419-a2ee-464f-be9d-58f11bf3418b.sketch_text.stroke-82"),sQuery(id+"FQ5JFwxVdaqARUP_1.wireOp",EDGE,"fcba4419-a2ee-464f-be9d-58f11bf3418b.sketch_text.stroke-83"),sQuery(id+"FQ5JFwxVdaqARUP_1.wireOp",EDGE,"fcba4419-a2ee-464f-be9d-58f11bf3418b.sketch_text.stroke-84"),sQuery(id+"FQ5JFwxVdaqARUP_1.wireOp",EDGE,"fcba4419-a2ee-464f-be9d-58f11bf3418b.sketch_text.stroke-85"),sQuery(id+"FQ5JFwxVdaqARUP_1.wireOp",EDGE,"fcba4419-a2ee-464f-be9d-58f11bf3418b.sketch_text.stroke-86"),sQuery(id+"FQ5JFwxVdaqARUP_1.wireOp",EDGE,"fcba4419-a2ee-464f-be9d-58f11bf3418b.sketch_text.stroke-87"),sQuery(id+"FQ5JFwxVdaqARUP_1.wireOp",EDGE,"fcba4419-a2ee-464f-be9d-58f11bf3418b.sketch_text.stroke-88"),sQuery(id+"FQ5JFwxVdaqARUP_1.wireOp",EDGE,"fcba4419-a2ee-464f-be9d-58f11bf3418b.sketch_text.stroke-89"),sQuery(id+"FQ5JFwxVdaqARUP_1.wireOp",EDGE,"fcba4419-a2ee-464f-be9d-58f11bf3418b.sketch_text.stroke-90"),sQuery(id+"FQ5JFwxVdaqARUP_1.wireOp",EDGE,"fcba4419-a2ee-464f-be9d-58f11bf3418b.sketch_text.stroke-91"),sQuery(id+"FQ5JFwxVdaqARUP_1.wireOp",EDGE,"fcba4419-a2ee-464f-be9d-58f11bf3418b.sketch_text.stroke-92"),sQuery(id+"FQ5JFwxVdaqARUP_1.wireOp",EDGE,"fcba4419-a2ee-464f-be9d-58f11bf3418b.sketch_text.stroke-93"),sQuery(id+"FQ5JFwxVdaqARUP_1.wireOp",EDGE,"fcba4419-a2ee-464f-be9d-58f11bf3418b.sketch_text.stroke-94"),sQuery(id+"FQ5JFwxVdaqARUP_1.wireOp",EDGE,"fcba4419-a2ee-464f-be9d-58f11bf3418b.sketch_text.stroke-95"),sQuery(id+"FQ5JFwxVdaqARUP_1.wireOp",EDGE,"fcba4419-a2ee-464f-be9d-58f11bf3418b.sketch_text.stroke-96"),sQuery(id+"FQ5JFwxVdaqARUP_1.wireOp",EDGE,"fcba4419-a2ee-464f-be9d-58f11bf3418b.sketch_text.stroke-97"),sQuery(id+"FQ5JFwxVdaqARUP_1.wireOp",EDGE,"fcba4419-a2ee-464f-be9d-58f11bf3418b.sketch_text.stroke-98"),sQuery(id+"FQ5JFwxVdaqARUP_1.wireOp",EDGE,"fcba4419-a2ee-464f-be9d-58f11bf3418b.sketch_text.stroke-99"),sQuery(id+"FQ5JFwxVdaqARUP_1.wireOp",EDGE,"fcba4419-a2ee-464f-be9d-58f11bf3418b.sketch_text.stroke-100"),sQuery(id+"FQ5JFwxVdaqARUP_1.wireOp",EDGE,"fcba4419-a2ee-464f-be9d-58f11bf3418b.sketch_text.stroke-101"),sQuery(id+"FQ5JFwxVdaqARUP_1.wireOp",EDGE,"fcba4419-a2ee-464f-be9d-58f11bf3418b.sketch_text.stroke-102"),sQuery(id+"FQ5JFwxVdaqARUP_1.wireOp",EDGE,"fcba4419-a2ee-464f-be9d-58f11bf3418b.sketch_text.stroke-103"),sQuery(id+"FQ5JFwxVdaqARUP_1.wireOp",EDGE,"fcba4419-a2ee-464f-be9d-58f11bf3418b.sketch_text.stroke-104"),sQuery(id+"FQ5JFwxVdaqARUP_1.wireOp",EDGE,"fcba4419-a2ee-464f-be9d-58f11bf3418b.sketch_text.stroke-105"),sQuery(id+"FQ5JFwxVdaqARUP_1.wireOp",EDGE,"fcba4419-a2ee-464f-be9d-58f11bf3418b.sketch_text.stroke-106"),sQuery(id+"FQ5JFwxVdaqARUP_1.wireOp",EDGE,"fcba4419-a2ee-464f-be9d-58f11bf3418b.sketch_text.stroke-107"),sQuery(id+"FQ5JFwxVdaqARUP_1.wireOp",EDGE,"fcba4419-a2ee-464f-be9d-58f11bf3418b.sketch_text.stroke-108"),sQuery(id+"FQ5JFwxVdaqARUP_1.wireOp",EDGE,"fcba4419-a2ee-464f-be9d-58f11bf3418b.sketch_text.stroke-109"),sQuery(id+"FQ5JFwxVdaqARUP_1.wireOp",EDGE,"fcba4419-a2ee-464f-be9d-58f11bf3418b.sketch_text.stroke-110"),sQuery(id+"FQ5JFwxVdaqARUP_1.wireOp",EDGE,"fcba4419-a2ee-464f-be9d-58f11bf3418b.sketch_text.stroke-111"),sQuery(id+"FQ5JFwxVdaqARUP_1.wireOp",EDGE,"fcba4419-a2ee-464f-be9d-58f11bf3418b.sketch_text.stroke-112"),sQuery(id+"FQ5JFwxVdaqARUP_1.wireOp",EDGE,"fcba4419-a2ee-464f-be9d-58f11bf3418b.sketch_text.stroke-113"),sQuery(id+"FQ5JFwxVdaqARUP_1.wireOp",EDGE,"fcba4419-a2ee-464f-be9d-58f11bf3418b.sketch_text.stroke-114"),sQuery(id+"FQ5JFwxVdaqARUP_1.wireOp",EDGE,"fcba4419-a2ee-464f-be9d-58f11bf3418b.sketch_text.stroke-115"),sQuery(id+"FQ5JFwxVdaqARUP_1.wireOp",EDGE,"fcba4419-a2ee-464f-be9d-58f11bf3418b.sketch_text.stroke-116"),sQuery(id+"FQ5JFwxVdaqARUP_1.wireOp",EDGE,"fcba4419-a2ee-464f-be9d-58f11bf3418b.sketch_text.stroke-117"),sQuery(id+"FQ5JFwxVdaqARUP_1.wireOp",EDGE,"fcba4419-a2ee-464f-be9d-58f11bf3418b.sketch_text.stroke-118"),sQuery(id+"FQ5JFwxVdaqARUP_1.wireOp",EDGE,"fcba4419-a2ee-464f-be9d-58f11bf3418b.sketch_text.stroke-119"),sQuery(id+"FQ5JFwxVdaqARUP_1.wireOp",EDGE,"fcba4419-a2ee-464f-be9d-58f11bf3418b.sketch_text.stroke-120"),sQuery(id+"FQ5JFwxVdaqARUP_1.wireOp",EDGE,"fcba4419-a2ee-464f-be9d-58f11bf3418b.sketch_text.stroke-121"),sQuery(id+"FQ5JFwxVdaqARUP_1.wireOp",EDGE,"fcba4419-a2ee-464f-be9d-58f11bf3418b.sketch_text.stroke-122"),sQuery(id+"FQ5JFwxVdaqARUP_1.wireOp",EDGE,"fcba4419-a2ee-464f-be9d-58f11bf3418b.sketch_text.stroke-123"),sQuery(id+"FQ5JFwxVdaqARUP_1.wireOp",EDGE,"fcba4419-a2ee-464f-be9d-58f11bf3418b.sketch_text.stroke-124"),sQuery(id+"FQ5JFwxVdaqARUP_1.wireOp",EDGE,"fcba4419-a2ee-464f-be9d-58f11bf3418b.sketch_text.stroke-125"),sQuery(id+"FQ5JFwxVdaqARUP_1.wireOp",EDGE,"fcba4419-a2ee-464f-be9d-58f11bf3418b.sketch_text.stroke-126"),sQuery(id+"FQ5JFwxVdaqARUP_1.wireOp",EDGE,"fcba4419-a2ee-464f-be9d-58f11bf3418b.sketch_text.stroke-127"),sQuery(id+"FQ5JFwxVdaqARUP_1.wireOp",EDGE,"fcba4419-a2ee-464f-be9d-58f11bf3418b.sketch_text.stroke-128"),sQuery(id+"FQ5JFwxVdaqARUP_1.wireOp",EDGE,"fcba4419-a2ee-464f-be9d-58f11bf3418b.sketch_text.stroke-129"),sQuery(id+"FQ5JFwxVdaqARUP_1.wireOp",EDGE,"fcba4419-a2ee-464f-be9d-58f11bf3418b.sketch_text.stroke-130"),sQuery(id+"FQ5JFwxVdaqARUP_1.wireOp",EDGE,"fcba4419-a2ee-464f-be9d-58f11bf3418b.sketch_text.stroke-131"),sQuery(id+"FQ5JFwxVdaqARUP_1.wireOp",EDGE,"fcba4419-a2ee-464f-be9d-58f11bf3418b.sketch_text.stroke-132"),sQuery(id+"FQ5JFwxVdaqARUP_1.wireOp",EDGE,"fcba4419-a2ee-464f-be9d-58f11bf3418b.sketch_text.stroke-133"),sQuery(id+"FQ5JFwxVdaqARUP_1.wireOp",EDGE,"fcba4419-a2ee-464f-be9d-58f11bf3418b.sketch_text.stroke-134"),sQuery(id+"FQ5JFwxVdaqARUP_1.wireOp",EDGE,"fcba4419-a2ee-464f-be9d-58f11bf3418b.sketch_text.stroke-135"),sQuery(id+"FQ5JFwxVdaqARUP_1.wireOp",EDGE,"fcba4419-a2ee-464f-be9d-58f11bf3418b.sketch_text.stroke-136"),sQuery(id+"FQ5JFwxVdaqARUP_1.wireOp",EDGE,"fcba4419-a2ee-464f-be9d-58f11bf3418b.sketch_text.stroke-137"),sQuery(id+"FQ5JFwxVdaqARUP_1.wireOp",EDGE,"fcba4419-a2ee-464f-be9d-58f11bf3418b.sketch_text.stroke-138"),sQuery(id+"FQ5JFwxVdaqARUP_1.wireOp",EDGE,"fcba4419-a2ee-464f-be9d-58f11bf3418b.sketch_text.stroke-139"),sQuery(id+"FQ5JFwxVdaqARUP_1.wireOp",EDGE,"fcba4419-a2ee-464f-be9d-58f11bf3418b.sketch_text.stroke-140"),sQuery(id+"FQ5JFwxVdaqARUP_1.wireOp",EDGE,"fcba4419-a2ee-464f-be9d-58f11bf3418b.sketch_text.stroke-141"),sQuery(id+"FQ5JFwxVdaqARUP_1.wireOp",EDGE,"fcba4419-a2ee-464f-be9d-58f11bf3418b.sketch_text.stroke-142"),sQuery(id+"FQ5JFwxVdaqARUP_1.wireOp",EDGE,"fcba4419-a2ee-464f-be9d-58f11bf3418b.sketch_text.stroke-143"),sQuery(id+"FQ5JFwxVdaqARUP_1.wireOp",EDGE,"fcba4419-a2ee-464f-be9d-58f11bf3418b.sketch_text.stroke-144"),sQuery(id+"FQ5JFwxVdaqARUP_1.wireOp",EDGE,"fcba4419-a2ee-464f-be9d-58f11bf3418b.sketch_text.stroke-145"),sQuery(id+"FQ5JFwxVdaqARUP_1.wireOp",EDGE,"fcba4419-a2ee-464f-be9d-58f11bf3418b.sketch_text.stroke-146"),sQuery(id+"FQ5JFwxVdaqARUP_1.wireOp",EDGE,"fcba4419-a2ee-464f-be9d-58f11bf3418b.sketch_text.stroke-147"),sQuery(id+"FQ5JFwxVdaqARUP_1.wireOp",EDGE,"fcba4419-a2ee-464f-be9d-58f11bf3418b.sketch_text.stroke-148"),sQuery(id+"FQ5JFwxVdaqARUP_1.wireOp",EDGE,"fcba4419-a2ee-464f-be9d-58f11bf3418b.sketch_text.stroke-149"),sQuery(id+"FQ5JFwxVdaqARUP_1.wireOp",EDGE,"fcba4419-a2ee-464f-be9d-58f11bf3418b.sketch_text.stroke-150"),sQuery(id+"FQ5JFwxVdaqARUP_1.wireOp",EDGE,"fcba4419-a2ee-464f-be9d-58f11bf3418b.sketch_text.stroke-151"),sQuery(id+"FQ5JFwxVdaqARUP_1.wireOp",EDGE,"fcba4419-a2ee-464f-be9d-58f11bf3418b.sketch_text.stroke-152"),sQuery(id+"FQ5JFwxVdaqARUP_1.wireOp",EDGE,"fcba4419-a2ee-464f-be9d-58f11bf3418b.sketch_text.stroke-153"),sQuery(id+"FQ5JFwxVdaqARUP_1.wireOp",EDGE,"fcba4419-a2ee-464f-be9d-58f11bf3418b.sketch_text.stroke-154"),sQuery(id+"FQ5JFwxVdaqARUP_1.wireOp",EDGE,"fcba4419-a2ee-464f-be9d-58f11bf3418b.sketch_text.stroke-155"),sQuery(id+"FQ5JFwxVdaqARUP_1.wireOp",EDGE,"fcba4419-a2ee-464f-be9d-58f11bf3418b.sketch_text.stroke-156"),sQuery(id+"FQ5JFwxVdaqARUP_1.wireOp",EDGE,"fcba4419-a2ee-464f-be9d-58f11bf3418b.sketch_text.stroke-157"),sQuery(id+"FQ5JFwxVdaqARUP_1.wireOp",EDGE,"fcba4419-a2ee-464f-be9d-58f11bf3418b.sketch_text.stroke-158"),sQuery(id+"FQ5JFwxVdaqARUP_1.wireOp",EDGE,"fcba4419-a2ee-464f-be9d-58f11bf3418b.sketch_text.stroke-159"),sQuery(id+"FQ5JFwxVdaqARUP_1.wireOp",EDGE,"fcba4419-a2ee-464f-be9d-58f11bf3418b.sketch_text.stroke-160"),sQuery(id+"FQ5JFwxVdaqARUP_1.wireOp",EDGE,"fcba4419-a2ee-464f-be9d-58f11bf3418b.sketch_text.stroke-161"),sQuery(id+"FQ5JFwxVdaqARUP_1.wireOp",EDGE,"fcba4419-a2ee-464f-be9d-58f11bf3418b.sketch_text.stroke-162"),sQuery(id+"FQ5JFwxVdaqARUP_1.wireOp",EDGE,"fcba4419-a2ee-464f-be9d-58f11bf3418b.sketch_text.stroke-163"),sQuery(id+"FQ5JFwxVdaqARUP_1.wireOp",EDGE,"fcba4419-a2ee-464f-be9d-58f11bf3418b.sketch_text.stroke-164"),sQuery(id+"FQ5JFwxVdaqARUP_1.wireOp",EDGE,"fcba4419-a2ee-464f-be9d-58f11bf3418b.sketch_text.stroke-165"),sQuery(id+"FQ5JFwxVdaqARUP_1.wireOp",EDGE,"fcba4419-a2ee-464f-be9d-58f11bf3418b.sketch_text.stroke-166"),sQuery(id+"FQ5JFwxVdaqARUP_1.wireOp",EDGE,"fcba4419-a2ee-464f-be9d-58f11bf3418b.sketch_text.stroke-167"),sQuery(id+"FQ5JFwxVdaqARUP_1.wireOp",EDGE,"fcba4419-a2ee-464f-be9d-58f11bf3418b.sketch_text.stroke-168"),sQuery(id+"FQ5JFwxVdaqARUP_1.wireOp",EDGE,"fcba4419-a2ee-464f-be9d-58f11bf3418b.sketch_text.stroke-169"),sQuery(id+"FQ5JFwxVdaqARUP_1.wireOp",EDGE,"fcba4419-a2ee-464f-be9d-58f11bf3418b.sketch_text.stroke-170"),sQuery(id+"FQ5JFwxVdaqARUP_1.wireOp",EDGE,"fcba4419-a2ee-464f-be9d-58f11bf3418b.sketch_text.stroke-171"),sQuery(id+"FQ5JFwxVdaqARUP_1.wireOp",EDGE,"fcba4419-a2ee-464f-be9d-58f11bf3418b.sketch_text.stroke-172"),sQuery(id+"FQ5JFwxVdaqARUP_1.wireOp",EDGE,"fcba4419-a2ee-464f-be9d-58f11bf3418b.sketch_text.stroke-173"),sQuery(id+"FHMxAyK4CFUKdhS_1.wireOp",EDGE,"1cb9c079-ea9b-4899-8069-e0e3048e911d.sketch_text.stroke-0"),sQuery(id+"FHMxAyK4CFUKdhS_1.wireOp",EDGE,"1cb9c079-ea9b-4899-8069-e0e3048e911d.sketch_text.stroke-1"),sQuery(id+"FHMxAyK4CFUKdhS_1.wireOp",EDGE,"1cb9c079-ea9b-4899-8069-e0e3048e911d.sketch_text.stroke-2"),sQuery(id+"FHMxAyK4CFUKdhS_1.wireOp",EDGE,"1cb9c079-ea9b-4899-8069-e0e3048e911d.sketch_text.stroke-3"),sQuery(id+"FHMxAyK4CFUKdhS_1.wireOp",EDGE,"1cb9c079-ea9b-4899-8069-e0e3048e911d.sketch_text.stroke-4"),sQuery(id+"FHMxAyK4CFUKdhS_1.wireOp",EDGE,"1cb9c079-ea9b-4899-8069-e0e3048e911d.sketch_text.stroke-5"),sQuery(id+"FHMxAyK4CFUKdhS_1.wireOp",EDGE,"1cb9c079-ea9b-4899-8069-e0e3048e911d.sketch_text.stroke-6"),sQuery(id+"FHMxAyK4CFUKdhS_1.wireOp",EDGE,"1cb9c079-ea9b-4899-8069-e0e3048e911d.sketch_text.stroke-7"),sQuery(id+"FHMxAyK4CFUKdhS_1.wireOp",EDGE,"1cb9c079-ea9b-4899-8069-e0e3048e911d.sketch_text.stroke-8"),sQuery(id+"FHMxAyK4CFUKdhS_1.wireOp",EDGE,"1cb9c079-ea9b-4899-8069-e0e3048e911d.sketch_text.stroke-9"),sQuery(id+"FHMxAyK4CFUKdhS_1.wireOp",EDGE,"1cb9c079-ea9b-4899-8069-e0e3048e911d.sketch_text.stroke-10"),sQuery(id+"FHMxAyK4CFUKdhS_1.wireOp",EDGE,"1cb9c079-ea9b-4899-8069-e0e3048e911d.sketch_text.stroke-11"),sQuery(id+"FHMxAyK4CFUKdhS_1.wireOp",EDGE,"1cb9c079-ea9b-4899-8069-e0e3048e911d.sketch_text.stroke-12"),sQuery(id+"FHMxAyK4CFUKdhS_1.wireOp",EDGE,"1cb9c079-ea9b-4899-8069-e0e3048e911d.sketch_text.stroke-13"),sQuery(id+"FHMxAyK4CFUKdhS_1.wireOp",EDGE,"1cb9c079-ea9b-4899-8069-e0e3048e911d.sketch_text.stroke-14"),sQuery(id+"FHMxAyK4CFUKdhS_1.wireOp",EDGE,"1cb9c079-ea9b-4899-8069-e0e3048e911d.sketch_text.stroke-15"),sQuery(id+"FHMxAyK4CFUKdhS_1.wireOp",EDGE,"1cb9c079-ea9b-4899-8069-e0e3048e911d.sketch_text.stroke-16"),sQuery(id+"FHMxAyK4CFUKdhS_1.wireOp",EDGE,"1cb9c079-ea9b-4899-8069-e0e3048e911d.sketch_text.stroke-17"),sQuery(id+"FHMxAyK4CFUKdhS_1.wireOp",EDGE,"1cb9c079-ea9b-4899-8069-e0e3048e911d.sketch_text.stroke-18"),sQuery(id+"FHMxAyK4CFUKdhS_1.wireOp",EDGE,"1cb9c079-ea9b-4899-8069-e0e3048e911d.sketch_text.stroke-19"),sQuery(id+"FHMxAyK4CFUKdhS_1.wireOp",EDGE,"1cb9c079-ea9b-4899-8069-e0e3048e911d.sketch_text.stroke-20"),sQuery(id+"FHMxAyK4CFUKdhS_1.wireOp",EDGE,"1cb9c079-ea9b-4899-8069-e0e3048e911d.sketch_text.stroke-21"),sQuery(id+"FHMxAyK4CFUKdhS_1.wireOp",EDGE,"1cb9c079-ea9b-4899-8069-e0e3048e911d.sketch_text.stroke-22"),sQuery(id+"FHMxAyK4CFUKdhS_1.wireOp",EDGE,"1cb9c079-ea9b-4899-8069-e0e3048e911d.sketch_text.stroke-23"),sQuery(id+"FHMxAyK4CFUKdhS_1.wireOp",EDGE,"1cb9c079-ea9b-4899-8069-e0e3048e911d.sketch_text.stroke-24"),sQuery(id+"FHMxAyK4CFUKdhS_1.wireOp",EDGE,"1cb9c079-ea9b-4899-8069-e0e3048e911d.sketch_text.stroke-25"),sQuery(id+"FHMxAyK4CFUKdhS_1.wireOp",EDGE,"1cb9c079-ea9b-4899-8069-e0e3048e911d.sketch_text.stroke-26"),sQuery(id+"FHMxAyK4CFUKdhS_1.wireOp",EDGE,"1cb9c079-ea9b-4899-8069-e0e3048e911d.sketch_text.stroke-27"),sQuery(id+"FHMxAyK4CFUKdhS_1.wireOp",EDGE,"1cb9c079-ea9b-4899-8069-e0e3048e911d.sketch_text.stroke-28"),sQuery(id+"FHMxAyK4CFUKdhS_1.wireOp",EDGE,"1cb9c079-ea9b-4899-8069-e0e3048e911d.sketch_text.stroke-29"),sQuery(id+"FHMxAyK4CFUKdhS_1.wireOp",EDGE,"1cb9c079-ea9b-4899-8069-e0e3048e911d.sketch_text.stroke-30"),sQuery(id+"FHMxAyK4CFUKdhS_1.wireOp",EDGE,"1cb9c079-ea9b-4899-8069-e0e3048e911d.sketch_text.stroke-31"),sQuery(id+"FHMxAyK4CFUKdhS_1.wireOp",EDGE,"1cb9c079-ea9b-4899-8069-e0e3048e911d.sketch_text.stroke-32"),sQuery(id+"FHMxAyK4CFUKdhS_1.wireOp",EDGE,"1cb9c079-ea9b-4899-8069-e0e3048e911d.sketch_text.stroke-33"),sQuery(id+"FHMxAyK4CFUKdhS_1.wireOp",EDGE,"1cb9c079-ea9b-4899-8069-e0e3048e911d.sketch_text.stroke-34"),sQuery(id+"FHMxAyK4CFUKdhS_1.wireOp",EDGE,"1cb9c079-ea9b-4899-8069-e0e3048e911d.sketch_text.stroke-35"),sQuery(id+"FHMxAyK4CFUKdhS_1.wireOp",EDGE,"1cb9c079-ea9b-4899-8069-e0e3048e911d.sketch_text.stroke-36"),sQuery(id+"FHMxAyK4CFUKdhS_1.wireOp",EDGE,"1cb9c079-ea9b-4899-8069-e0e3048e911d.sketch_text.stroke-37"),sQuery(id+"FHMxAyK4CFUKdhS_1.wireOp",EDGE,"1cb9c079-ea9b-4899-8069-e0e3048e911d.sketch_text.stroke-38"),sQuery(id+"FHMxAyK4CFUKdhS_1.wireOp",EDGE,"1cb9c079-ea9b-4899-8069-e0e3048e911d.sketch_text.stroke-39"),sQuery(id+"FHMxAyK4CFUKdhS_1.wireOp",EDGE,"1cb9c079-ea9b-4899-8069-e0e3048e911d.sketch_text.stroke-40"),sQuery(id+"FHMxAyK4CFUKdhS_1.wireOp",EDGE,"1cb9c079-ea9b-4899-8069-e0e3048e911d.sketch_text.stroke-41"),sQuery(id+"FHMxAyK4CFUKdhS_1.wireOp",EDGE,"1cb9c079-ea9b-4899-8069-e0e3048e911d.sketch_text.stroke-42"),sQuery(id+"FHMxAyK4CFUKdhS_1.wireOp",EDGE,"1cb9c079-ea9b-4899-8069-e0e3048e911d.sketch_text.stroke-43"),sQuery(id+"FHMxAyK4CFUKdhS_1.wireOp",EDGE,"1cb9c079-ea9b-4899-8069-e0e3048e911d.sketch_text.stroke-44"),sQuery(id+"FHMxAyK4CFUKdhS_1.wireOp",EDGE,"1cb9c079-ea9b-4899-8069-e0e3048e911d.sketch_text.stroke-45"),sQuery(id+"FHMxAyK4CFUKdhS_1.wireOp",EDGE,"1cb9c079-ea9b-4899-8069-e0e3048e911d.sketch_text.stroke-46"),sQuery(id+"FHMxAyK4CFUKdhS_1.wireOp",EDGE,"1cb9c079-ea9b-4899-8069-e0e3048e911d.sketch_text.stroke-47"),sQuery(id+"FHMxAyK4CFUKdhS_1.wireOp",EDGE,"1cb9c079-ea9b-4899-8069-e0e3048e911d.sketch_text.stroke-48"),sQuery(id+"FHMxAyK4CFUKdhS_1.wireOp",EDGE,"1cb9c079-ea9b-4899-8069-e0e3048e911d.sketch_text.stroke-49"),sQuery(id+"FHMxAyK4CFUKdhS_1.wireOp",EDGE,"1cb9c079-ea9b-4899-8069-e0e3048e911d.sketch_text.stroke-50"),sQuery(id+"FHMxAyK4CFUKdhS_1.wireOp",EDGE,"1cb9c079-ea9b-4899-8069-e0e3048e911d.sketch_text.stroke-51"),sQuery(id+"FHMxAyK4CFUKdhS_1.wireOp",EDGE,"1cb9c079-ea9b-4899-8069-e0e3048e911d.sketch_text.stroke-52"),sQuery(id+"FHMxAyK4CFUKdhS_1.wireOp",EDGE,"1cb9c079-ea9b-4899-8069-e0e3048e911d.sketch_text.stroke-53"),sQuery(id+"FHMxAyK4CFUKdhS_1.wireOp",EDGE,"1cb9c079-ea9b-4899-8069-e0e3048e911d.sketch_text.stroke-54"),sQuery(id+"FHMxAyK4CFUKdhS_1.wireOp",EDGE,"1cb9c079-ea9b-4899-8069-e0e3048e911d.sketch_text.stroke-55"),sQuery(id+"FHMxAyK4CFUKdhS_1.wireOp",EDGE,"1cb9c079-ea9b-4899-8069-e0e3048e911d.sketch_text.stroke-56"),sQuery(id+"FHMxAyK4CFUKdhS_1.wireOp",EDGE,"1cb9c079-ea9b-4899-8069-e0e3048e911d.sketch_text.stroke-57"),sQuery(id+"FHMxAyK4CFUKdhS_1.wireOp",EDGE,"1cb9c079-ea9b-4899-8069-e0e3048e911d.sketch_text.stroke-58"),sQuery(id+"FHMxAyK4CFUKdhS_1.wireOp",EDGE,"1cb9c079-ea9b-4899-8069-e0e3048e911d.sketch_text.stroke-59"),sQuery(id+"FHMxAyK4CFUKdhS_1.wireOp",EDGE,"1cb9c079-ea9b-4899-8069-e0e3048e911d.sketch_text.stroke-60"),sQuery(id+"FHMxAyK4CFUKdhS_1.wireOp",EDGE,"1cb9c079-ea9b-4899-8069-e0e3048e911d.sketch_text.stroke-61"),sQuery(id+"FHMxAyK4CFUKdhS_1.wireOp",EDGE,"1cb9c079-ea9b-4899-8069-e0e3048e911d.sketch_text.stroke-62"),sQuery(id+"FHMxAyK4CFUKdhS_1.wireOp",EDGE,"1cb9c079-ea9b-4899-8069-e0e3048e911d.sketch_text.stroke-71"),sQuery(id+"FHMxAyK4CFUKdhS_1.wireOp",EDGE,"1cb9c079-ea9b-4899-8069-e0e3048e911d.sketch_text.stroke-72"),sQuery(id+"FHMxAyK4CFUKdhS_1.wireOp",EDGE,"1cb9c079-ea9b-4899-8069-e0e3048e911d.sketch_text.stroke-73"),sQuery(id+"FHMxAyK4CFUKdhS_1.wireOp",EDGE,"1cb9c079-ea9b-4899-8069-e0e3048e911d.sketch_text.stroke-74"),sQuery(id+"FHMxAyK4CFUKdhS_1.wireOp",EDGE,"1cb9c079-ea9b-4899-8069-e0e3048e911d.sketch_text.stroke-75"),sQuery(id+"FHMxAyK4CFUKdhS_1.wireOp",EDGE,"1cb9c079-ea9b-4899-8069-e0e3048e911d.sketch_text.stroke-76"),sQuery(id+"FHMxAyK4CFUKdhS_1.wireOp",EDGE,"1cb9c079-ea9b-4899-8069-e0e3048e911d.sketch_text.stroke-77"),sQuery(id+"FHMxAyK4CFUKdhS_1.wireOp",EDGE,"1cb9c079-ea9b-4899-8069-e0e3048e911d.sketch_text.stroke-78"),sQuery(id+"FHMxAyK4CFUKdhS_1.wireOp",EDGE,"1cb9c079-ea9b-4899-8069-e0e3048e911d.sketch_text.stroke-79"),sQuery(id+"FHMxAyK4CFUKdhS_1.wireOp",EDGE,"1cb9c079-ea9b-4899-8069-e0e3048e911d.sketch_text.stroke-80"),sQuery(id+"FHMxAyK4CFUKdhS_1.wireOp",EDGE,"1cb9c079-ea9b-4899-8069-e0e3048e911d.sketch_text.stroke-81"),sQuery(id+"FHMxAyK4CFUKdhS_1.wireOp",EDGE,"1cb9c079-ea9b-4899-8069-e0e3048e911d.sketch_text.stroke-82"),sQuery(id+"FHMxAyK4CFUKdhS_1.wireOp",EDGE,"1cb9c079-ea9b-4899-8069-e0e3048e911d.sketch_text.stroke-83"),sQuery(id+"FHMxAyK4CFUKdhS_1.wireOp",EDGE,"1cb9c079-ea9b-4899-8069-e0e3048e911d.sketch_text.stroke-84"),sQuery(id+"FHMxAyK4CFUKdhS_1.wireOp",EDGE,"1cb9c079-ea9b-4899-8069-e0e3048e911d.sketch_text.stroke-85"),sQuery(id+"FHMxAyK4CFUKdhS_1.wireOp",EDGE,"1cb9c079-ea9b-4899-8069-e0e3048e911d.sketch_text.stroke-86"),sQuery(id+"FHMxAyK4CFUKdhS_1.wireOp",EDGE,"1cb9c079-ea9b-4899-8069-e0e3048e911d.sketch_text.stroke-87"),sQuery(id+"FHMxAyK4CFUKdhS_1.wireOp",EDGE,"1cb9c079-ea9b-4899-8069-e0e3048e911d.sketch_text.stroke-88"),sQuery(id+"FHMxAyK4CFUKdhS_1.wireOp",EDGE,"1cb9c079-ea9b-4899-8069-e0e3048e911d.sketch_text.stroke-89"),sQuery(id+"FHMxAyK4CFUKdhS_1.wireOp",EDGE,"1cb9c079-ea9b-4899-8069-e0e3048e911d.sketch_text.stroke-90"),sQuery(id+"FHMxAyK4CFUKdhS_1.wireOp",EDGE,"1cb9c079-ea9b-4899-8069-e0e3048e911d.sketch_text.stroke-91"),sQuery(id+"FHMxAyK4CFUKdhS_1.wireOp",EDGE,"1cb9c079-ea9b-4899-8069-e0e3048e911d.sketch_text.stroke-92"),sQuery(id+"FHMxAyK4CFUKdhS_1.wireOp",EDGE,"1cb9c079-ea9b-4899-8069-e0e3048e911d.sketch_text.stroke-93"),sQuery(id+"FHMxAyK4CFUKdhS_1.wireOp",EDGE,"1cb9c079-ea9b-4899-8069-e0e3048e911d.sketch_text.stroke-94"),sQuery(id+"FHMxAyK4CFUKdhS_1.wireOp",EDGE,"1cb9c079-ea9b-4899-8069-e0e3048e911d.sketch_text.stroke-95"),sQuery(id+"FHMxAyK4CFUKdhS_1.wireOp",EDGE,"1cb9c079-ea9b-4899-8069-e0e3048e911d.sketch_text.stroke-96"),sQuery(id+"FHMxAyK4CFUKdhS_1.wireOp",EDGE,"1cb9c079-ea9b-4899-8069-e0e3048e911d.sketch_text.stroke-97"),sQuery(id+"FHMxAyK4CFUKdhS_1.wireOp",EDGE,"1cb9c079-ea9b-4899-8069-e0e3048e911d.sketch_text.stroke-103"),sQuery(id+"FHMxAyK4CFUKdhS_1.wireOp",EDGE,"1cb9c079-ea9b-4899-8069-e0e3048e911d.sketch_text.stroke-104"),sQuery(id+"FHMxAyK4CFUKdhS_1.wireOp",EDGE,"1cb9c079-ea9b-4899-8069-e0e3048e911d.sketch_text.stroke-105"),sQuery(id+"FHMxAyK4CFUKdhS_1.wireOp",EDGE,"1cb9c079-ea9b-4899-8069-e0e3048e911d.sketch_text.stroke-106"),sQuery(id+"FHMxAyK4CFUKdhS_1.wireOp",EDGE,"1cb9c079-ea9b-4899-8069-e0e3048e911d.sketch_text.stroke-107"),sQuery(id+"FHMxAyK4CFUKdhS_1.wireOp",EDGE,"1cb9c079-ea9b-4899-8069-e0e3048e911d.sketch_text.stroke-108"),sQuery(id+"FHMxAyK4CFUKdhS_1.wireOp",EDGE,"1cb9c079-ea9b-4899-8069-e0e3048e911d.sketch_text.stroke-109"),sQuery(id+"FHMxAyK4CFUKdhS_1.wireOp",EDGE,"1cb9c079-ea9b-4899-8069-e0e3048e911d.sketch_text.stroke-110"),sQuery(id+"FHMxAyK4CFUKdhS_1.wireOp",EDGE,"1cb9c079-ea9b-4899-8069-e0e3048e911d.sketch_text.stroke-111"),sQuery(id+"FHMxAyK4CFUKdhS_1.wireOp",EDGE,"1cb9c079-ea9b-4899-8069-e0e3048e911d.sketch_text.stroke-112"),sQuery(id+"FHMxAyK4CFUKdhS_1.wireOp",EDGE,"1cb9c079-ea9b-4899-8069-e0e3048e911d.sketch_text.stroke-113"),sQuery(id+"FHMxAyK4CFUKdhS_1.wireOp",EDGE,"1cb9c079-ea9b-4899-8069-e0e3048e911d.sketch_text.stroke-114"),sQuery(id+"FHMxAyK4CFUKdhS_1.wireOp",EDGE,"1cb9c079-ea9b-4899-8069-e0e3048e911d.sketch_text.stroke-115"),sQuery(id+"FHMxAyK4CFUKdhS_1.wireOp",EDGE,"1cb9c079-ea9b-4899-8069-e0e3048e911d.sketch_text.stroke-116"),sQuery(id+"FHMxAyK4CFUKdhS_1.wireOp",EDGE,"1cb9c079-ea9b-4899-8069-e0e3048e911d.sketch_text.stroke-117"),sQuery(id+"FHMxAyK4CFUKdhS_1.wireOp",EDGE,"1cb9c079-ea9b-4899-8069-e0e3048e911d.sketch_text.stroke-118"),sQuery(id+"FHMxAyK4CFUKdhS_1.wireOp",EDGE,"1cb9c079-ea9b-4899-8069-e0e3048e911d.sketch_text.stroke-119"),sQuery(id+"FHMxAyK4CFUKdhS_1.wireOp",EDGE,"1cb9c079-ea9b-4899-8069-e0e3048e911d.sketch_text.stroke-120"),sQuery(id+"FHMxAyK4CFUKdhS_1.wireOp",EDGE,"1cb9c079-ea9b-4899-8069-e0e3048e911d.sketch_text.stroke-121"),sQuery(id+"FHMxAyK4CFUKdhS_1.wireOp",EDGE,"1cb9c079-ea9b-4899-8069-e0e3048e911d.sketch_text.stroke-122"),sQuery(id+"FHMxAyK4CFUKdhS_1.wireOp",EDGE,"1cb9c079-ea9b-4899-8069-e0e3048e911d.sketch_text.stroke-123"),sQuery(id+"FHMxAyK4CFUKdhS_1.wireOp",EDGE,"1cb9c079-ea9b-4899-8069-e0e3048e911d.sketch_text.stroke-124"),sQuery(id+"FHMxAyK4CFUKdhS_1.wireOp",EDGE,"1cb9c079-ea9b-4899-8069-e0e3048e911d.sketch_text.stroke-125"),sQuery(id+"FHMxAyK4CFUKdhS_1.wireOp",EDGE,"1cb9c079-ea9b-4899-8069-e0e3048e911d.sketch_text.stroke-126"),sQuery(id+"FHMxAyK4CFUKdhS_1.wireOp",EDGE,"1cb9c079-ea9b-4899-8069-e0e3048e911d.sketch_text.stroke-127"),sQuery(id+"FHMxAyK4CFUKdhS_1.wireOp",EDGE,"1cb9c079-ea9b-4899-8069-e0e3048e911d.sketch_text.stroke-128"),sQuery(id+"FHMxAyK4CFUKdhS_1.wireOp",EDGE,"1cb9c079-ea9b-4899-8069-e0e3048e911d.sketch_text.stroke-129"),sQuery(id+"FHMxAyK4CFUKdhS_1.wireOp",EDGE,"1cb9c079-ea9b-4899-8069-e0e3048e911d.sketch_text.stroke-130"),sQuery(id+"FHMxAyK4CFUKdhS_1.wireOp",EDGE,"1cb9c079-ea9b-4899-8069-e0e3048e911d.sketch_text.stroke-131"),sQuery(id+"FHMxAyK4CFUKdhS_1.wireOp",EDGE,"1cb9c079-ea9b-4899-8069-e0e3048e911d.sketch_text.stroke-132"),sQuery(id+"FHMxAyK4CFUKdhS_1.wireOp",EDGE,"1cb9c079-ea9b-4899-8069-e0e3048e911d.sketch_text.stroke-133"),sQuery(id+"FHMxAyK4CFUKdhS_1.wireOp",EDGE,"1cb9c079-ea9b-4899-8069-e0e3048e911d.sketch_text.stroke-134"),sQuery(id+"FHMxAyK4CFUKdhS_1.wireOp",EDGE,"1cb9c079-ea9b-4899-8069-e0e3048e911d.sketch_text.stroke-135"),sQuery(id+"FHMxAyK4CFUKdhS_1.wireOp",EDGE,"1cb9c079-ea9b-4899-8069-e0e3048e911d.sketch_text.stroke-136"),sQuery(id+"FHMxAyK4CFUKdhS_1.wireOp",EDGE,"1cb9c079-ea9b-4899-8069-e0e3048e911d.sketch_text.stroke-137"),sQuery(id+"FHMxAyK4CFUKdhS_1.wireOp",EDGE,"1cb9c079-ea9b-4899-8069-e0e3048e911d.sketch_text.stroke-138"),sQuery(id+"FHMxAyK4CFUKdhS_1.wireOp",EDGE,"1cb9c079-ea9b-4899-8069-e0e3048e911d.sketch_text.stroke-139"),sQuery(id+"FHMxAyK4CFUKdhS_1.wireOp",EDGE,"1cb9c079-ea9b-4899-8069-e0e3048e911d.sketch_text.stroke-140"),sQuery(id+"FHMxAyK4CFUKdhS_1.wireOp",EDGE,"1cb9c079-ea9b-4899-8069-e0e3048e911d.sketch_text.stroke-141"),sQuery(id+"FHMxAyK4CFUKdhS_1.wireOp",EDGE,"1cb9c079-ea9b-4899-8069-e0e3048e911d.sketch_text.stroke-142"),sQuery(id+"FHMxAyK4CFUKdhS_1.wireOp",EDGE,"1cb9c079-ea9b-4899-8069-e0e3048e911d.sketch_text.stroke-143"),sQuery(id+"FHMxAyK4CFUKdhS_1.wireOp",EDGE,"1cb9c079-ea9b-4899-8069-e0e3048e911d.sketch_text.stroke-144"),sQuery(id+"FHMxAyK4CFUKdhS_1.wireOp",EDGE,"1cb9c079-ea9b-4899-8069-e0e3048e911d.sketch_text.stroke-145"),sQuery(id+"FHMxAyK4CFUKdhS_1.wireOp",EDGE,"1cb9c079-ea9b-4899-8069-e0e3048e911d.sketch_text.stroke-146"),sQuery(id+"FHMxAyK4CFUKdhS_1.wireOp",EDGE,"1cb9c079-ea9b-4899-8069-e0e3048e911d.sketch_text.stroke-147"),sQuery(id+"FHMxAyK4CFUKdhS_1.wireOp",EDGE,"1cb9c079-ea9b-4899-8069-e0e3048e911d.sketch_text.stroke-148"),sQuery(id+"FHMxAyK4CFUKdhS_1.wireOp",EDGE,"1cb9c079-ea9b-4899-8069-e0e3048e911d.sketch_text.stroke-149"),sQuery(id+"FHMxAyK4CFUKdhS_1.wireOp",EDGE,"1cb9c079-ea9b-4899-8069-e0e3048e911d.sketch_text.stroke-150"),sQuery(id+"FHMxAyK4CFUKdhS_1.wireOp",EDGE,"1cb9c079-ea9b-4899-8069-e0e3048e911d.sketch_text.stroke-151"),sQuery(id+"FHMxAyK4CFUKdhS_1.wireOp",EDGE,"1cb9c079-ea9b-4899-8069-e0e3048e911d.sketch_text.stroke-152"),sQuery(id+"FHMxAyK4CFUKdhS_1.wireOp",EDGE,"1cb9c079-ea9b-4899-8069-e0e3048e911d.sketch_text.stroke-153"),sQuery(id+"FHMxAyK4CFUKdhS_1.wireOp",EDGE,"1cb9c079-ea9b-4899-8069-e0e3048e911d.sketch_text.stroke-159"),sQuery(id+"FHMxAyK4CFUKdhS_1.wireOp",EDGE,"1cb9c079-ea9b-4899-8069-e0e3048e911d.sketch_text.stroke-160"),sQuery(id+"FHMxAyK4CFUKdhS_1.wireOp",EDGE,"1cb9c079-ea9b-4899-8069-e0e3048e911d.sketch_text.stroke-161"),sQuery(id+"FHMxAyK4CFUKdhS_1.wireOp",EDGE,"1cb9c079-ea9b-4899-8069-e0e3048e911d.sketch_text.stroke-162"),sQuery(id+"FHMxAyK4CFUKdhS_1.wireOp",EDGE,"1cb9c079-ea9b-4899-8069-e0e3048e911d.sketch_text.stroke-163"),sQuery(id+"FHMxAyK4CFUKdhS_1.wireOp",EDGE,"1cb9c079-ea9b-4899-8069-e0e3048e911d.sketch_text.stroke-164"),sQuery(id+"FHMxAyK4CFUKdhS_1.wireOp",EDGE,"1cb9c079-ea9b-4899-8069-e0e3048e911d.sketch_text.stroke-165"),sQuery(id+"FHMxAyK4CFUKdhS_1.wireOp",EDGE,"1cb9c079-ea9b-4899-8069-e0e3048e911d.sketch_text.stroke-166"),sQuery(id+"FHMxAyK4CFUKdhS_1.wireOp",EDGE,"1cb9c079-ea9b-4899-8069-e0e3048e911d.sketch_text.stroke-167"),sQuery(id+"FHMxAyK4CFUKdhS_1.wireOp",EDGE,"1cb9c079-ea9b-4899-8069-e0e3048e911d.sketch_text.stroke-168"),sQuery(id+"FHMxAyK4CFUKdhS_1.wireOp",EDGE,"1cb9c079-ea9b-4899-8069-e0e3048e911d.sketch_text.stroke-169"),sQuery(id+"FHMxAyK4CFUKdhS_1.wireOp",EDGE,"1cb9c079-ea9b-4899-8069-e0e3048e911d.sketch_text.stroke-170"),sQuery(id+"FHMxAyK4CFUKdhS_1.wireOp",EDGE,"1cb9c079-ea9b-4899-8069-e0e3048e911d.sketch_text.stroke-171"),sQuery(id+"FHMxAyK4CFUKdhS_1.wireOp",EDGE,"1cb9c079-ea9b-4899-8069-e0e3048e911d.sketch_text.stroke-172"),sQuery(id+"FHMxAyK4CFUKdhS_1.wireOp",EDGE,"1cb9c079-ea9b-4899-8069-e0e3048e911d.sketch_text.stroke-173"),sQuery(id+"FHMxAyK4CFUKdhS_1.wireOp",EDGE,"1cb9c079-ea9b-4899-8069-e0e3048e911d.sketch_text.stroke-174"),sQuery(id+"FHMxAyK4CFUKdhS_1.wireOp",EDGE,"1cb9c079-ea9b-4899-8069-e0e3048e911d.sketch_text.stroke-175"),sQuery(id+"FHMxAyK4CFUKdhS_1.wireOp",EDGE,"1cb9c079-ea9b-4899-8069-e0e3048e911d.sketch_text.stroke-176"),sQuery(id+"FHMxAyK4CFUKdhS_1.wireOp",EDGE,"1cb9c079-ea9b-4899-8069-e0e3048e911d.sketch_text.stroke-177"),sQuery(id+"FHMxAyK4CFUKdhS_1.wireOp",EDGE,"1cb9c079-ea9b-4899-8069-e0e3048e911d.sketch_text.stroke-178"),sQuery(id+"FHMxAyK4CFUKdhS_1.wireOp",EDGE,"1cb9c079-ea9b-4899-8069-e0e3048e911d.sketch_text.stroke-179"),sQuery(id+"FHMxAyK4CFUKdhS_1.wireOp",EDGE,"1cb9c079-ea9b-4899-8069-e0e3048e911d.sketch_text.stroke-180"),subQ2,sQuery(id+"F2.wireOp",EDGE,"E27")])],"isStart":true})]),OD(1.0)],"derivedFrom":makeQuery(id+"F1.opExtrude","CAP_EDGE",EDGE,{"disambiguationData":[OSD([subQ0])],"isStart":false})});}
            var Q25;
            {var subQ0=sQuery(id+"F0.wireOp",EDGE,"E0.top");var subQ1=sQuery(id+"F0.wireOp",EDGE,"E0.bottom");var subQ2=sQuery(id+"F2.wireOp",EDGE,"E26");Q25=makeQuery(id+"F3.boolean.opBoolean","SPLIT",EDGE,{"disambiguationData":[TD([makeQuery(id+"F1.opExtrude","CAP_FACE",FACE,{"disambiguationData":[OSD([subQ1,subQ0,sQuery(id+"F0.wireOp",EDGE,"E0.left"),sQuery(id+"F0.wireOp",EDGE,"E0.right")])],"isStart":false}),makeQuery(id+"F1.opExtrude","SWEPT_FACE",FACE,{"disambiguationData":[OSD([subQ0])]}),makeQuery(id+"F3.opExtrude","SWEPT_FACE",FACE,{"disambiguationData":[OSD([subQ2])]}),makeQuery(id+"F3.opExtrude","CAP_FACE",FACE,{"disambiguationData":[OSD([subQ1,sQuery(id+"FQ5JFwxVdaqARUP_1.wireOp",EDGE,"fcba4419-a2ee-464f-be9d-58f11bf3418b.sketch_text.stroke-0"),sQuery(id+"FQ5JFwxVdaqARUP_1.wireOp",EDGE,"fcba4419-a2ee-464f-be9d-58f11bf3418b.sketch_text.stroke-1"),sQuery(id+"FQ5JFwxVdaqARUP_1.wireOp",EDGE,"fcba4419-a2ee-464f-be9d-58f11bf3418b.sketch_text.stroke-2"),sQuery(id+"FQ5JFwxVdaqARUP_1.wireOp",EDGE,"fcba4419-a2ee-464f-be9d-58f11bf3418b.sketch_text.stroke-3"),sQuery(id+"FQ5JFwxVdaqARUP_1.wireOp",EDGE,"fcba4419-a2ee-464f-be9d-58f11bf3418b.sketch_text.stroke-4"),sQuery(id+"FQ5JFwxVdaqARUP_1.wireOp",EDGE,"fcba4419-a2ee-464f-be9d-58f11bf3418b.sketch_text.stroke-5"),sQuery(id+"FQ5JFwxVdaqARUP_1.wireOp",EDGE,"fcba4419-a2ee-464f-be9d-58f11bf3418b.sketch_text.stroke-6"),sQuery(id+"FQ5JFwxVdaqARUP_1.wireOp",EDGE,"fcba4419-a2ee-464f-be9d-58f11bf3418b.sketch_text.stroke-7"),sQuery(id+"FQ5JFwxVdaqARUP_1.wireOp",EDGE,"fcba4419-a2ee-464f-be9d-58f11bf3418b.sketch_text.stroke-8"),sQuery(id+"FQ5JFwxVdaqARUP_1.wireOp",EDGE,"fcba4419-a2ee-464f-be9d-58f11bf3418b.sketch_text.stroke-9"),sQuery(id+"FQ5JFwxVdaqARUP_1.wireOp",EDGE,"fcba4419-a2ee-464f-be9d-58f11bf3418b.sketch_text.stroke-10"),sQuery(id+"FQ5JFwxVdaqARUP_1.wireOp",EDGE,"fcba4419-a2ee-464f-be9d-58f11bf3418b.sketch_text.stroke-11"),sQuery(id+"FQ5JFwxVdaqARUP_1.wireOp",EDGE,"fcba4419-a2ee-464f-be9d-58f11bf3418b.sketch_text.stroke-12"),sQuery(id+"FQ5JFwxVdaqARUP_1.wireOp",EDGE,"fcba4419-a2ee-464f-be9d-58f11bf3418b.sketch_text.stroke-13"),sQuery(id+"FQ5JFwxVdaqARUP_1.wireOp",EDGE,"fcba4419-a2ee-464f-be9d-58f11bf3418b.sketch_text.stroke-14"),sQuery(id+"FQ5JFwxVdaqARUP_1.wireOp",EDGE,"fcba4419-a2ee-464f-be9d-58f11bf3418b.sketch_text.stroke-15"),sQuery(id+"FQ5JFwxVdaqARUP_1.wireOp",EDGE,"fcba4419-a2ee-464f-be9d-58f11bf3418b.sketch_text.stroke-16"),sQuery(id+"FQ5JFwxVdaqARUP_1.wireOp",EDGE,"fcba4419-a2ee-464f-be9d-58f11bf3418b.sketch_text.stroke-17"),sQuery(id+"FQ5JFwxVdaqARUP_1.wireOp",EDGE,"fcba4419-a2ee-464f-be9d-58f11bf3418b.sketch_text.stroke-18"),sQuery(id+"FQ5JFwxVdaqARUP_1.wireOp",EDGE,"fcba4419-a2ee-464f-be9d-58f11bf3418b.sketch_text.stroke-19"),sQuery(id+"FQ5JFwxVdaqARUP_1.wireOp",EDGE,"fcba4419-a2ee-464f-be9d-58f11bf3418b.sketch_text.stroke-20"),sQuery(id+"FQ5JFwxVdaqARUP_1.wireOp",EDGE,"fcba4419-a2ee-464f-be9d-58f11bf3418b.sketch_text.stroke-21"),sQuery(id+"FQ5JFwxVdaqARUP_1.wireOp",EDGE,"fcba4419-a2ee-464f-be9d-58f11bf3418b.sketch_text.stroke-22"),sQuery(id+"FQ5JFwxVdaqARUP_1.wireOp",EDGE,"fcba4419-a2ee-464f-be9d-58f11bf3418b.sketch_text.stroke-23"),sQuery(id+"FQ5JFwxVdaqARUP_1.wireOp",EDGE,"fcba4419-a2ee-464f-be9d-58f11bf3418b.sketch_text.stroke-24"),sQuery(id+"FQ5JFwxVdaqARUP_1.wireOp",EDGE,"fcba4419-a2ee-464f-be9d-58f11bf3418b.sketch_text.stroke-25"),sQuery(id+"FQ5JFwxVdaqARUP_1.wireOp",EDGE,"fcba4419-a2ee-464f-be9d-58f11bf3418b.sketch_text.stroke-26"),sQuery(id+"FQ5JFwxVdaqARUP_1.wireOp",EDGE,"fcba4419-a2ee-464f-be9d-58f11bf3418b.sketch_text.stroke-27"),sQuery(id+"FQ5JFwxVdaqARUP_1.wireOp",EDGE,"fcba4419-a2ee-464f-be9d-58f11bf3418b.sketch_text.stroke-28"),sQuery(id+"FQ5JFwxVdaqARUP_1.wireOp",EDGE,"fcba4419-a2ee-464f-be9d-58f11bf3418b.sketch_text.stroke-29"),sQuery(id+"FQ5JFwxVdaqARUP_1.wireOp",EDGE,"fcba4419-a2ee-464f-be9d-58f11bf3418b.sketch_text.stroke-30"),sQuery(id+"FQ5JFwxVdaqARUP_1.wireOp",EDGE,"fcba4419-a2ee-464f-be9d-58f11bf3418b.sketch_text.stroke-31"),sQuery(id+"FQ5JFwxVdaqARUP_1.wireOp",EDGE,"fcba4419-a2ee-464f-be9d-58f11bf3418b.sketch_text.stroke-32"),sQuery(id+"FQ5JFwxVdaqARUP_1.wireOp",EDGE,"fcba4419-a2ee-464f-be9d-58f11bf3418b.sketch_text.stroke-33"),sQuery(id+"FQ5JFwxVdaqARUP_1.wireOp",EDGE,"fcba4419-a2ee-464f-be9d-58f11bf3418b.sketch_text.stroke-34"),sQuery(id+"FQ5JFwxVdaqARUP_1.wireOp",EDGE,"fcba4419-a2ee-464f-be9d-58f11bf3418b.sketch_text.stroke-35"),sQuery(id+"FQ5JFwxVdaqARUP_1.wireOp",EDGE,"fcba4419-a2ee-464f-be9d-58f11bf3418b.sketch_text.stroke-36"),sQuery(id+"FQ5JFwxVdaqARUP_1.wireOp",EDGE,"fcba4419-a2ee-464f-be9d-58f11bf3418b.sketch_text.stroke-37"),sQuery(id+"FQ5JFwxVdaqARUP_1.wireOp",EDGE,"fcba4419-a2ee-464f-be9d-58f11bf3418b.sketch_text.stroke-38"),sQuery(id+"FQ5JFwxVdaqARUP_1.wireOp",EDGE,"fcba4419-a2ee-464f-be9d-58f11bf3418b.sketch_text.stroke-39"),sQuery(id+"FQ5JFwxVdaqARUP_1.wireOp",EDGE,"fcba4419-a2ee-464f-be9d-58f11bf3418b.sketch_text.stroke-40"),sQuery(id+"FQ5JFwxVdaqARUP_1.wireOp",EDGE,"fcba4419-a2ee-464f-be9d-58f11bf3418b.sketch_text.stroke-41"),sQuery(id+"FQ5JFwxVdaqARUP_1.wireOp",EDGE,"fcba4419-a2ee-464f-be9d-58f11bf3418b.sketch_text.stroke-42"),sQuery(id+"FQ5JFwxVdaqARUP_1.wireOp",EDGE,"fcba4419-a2ee-464f-be9d-58f11bf3418b.sketch_text.stroke-43"),sQuery(id+"FQ5JFwxVdaqARUP_1.wireOp",EDGE,"fcba4419-a2ee-464f-be9d-58f11bf3418b.sketch_text.stroke-44"),sQuery(id+"FQ5JFwxVdaqARUP_1.wireOp",EDGE,"fcba4419-a2ee-464f-be9d-58f11bf3418b.sketch_text.stroke-45"),sQuery(id+"FQ5JFwxVdaqARUP_1.wireOp",EDGE,"fcba4419-a2ee-464f-be9d-58f11bf3418b.sketch_text.stroke-46"),sQuery(id+"FQ5JFwxVdaqARUP_1.wireOp",EDGE,"fcba4419-a2ee-464f-be9d-58f11bf3418b.sketch_text.stroke-47"),sQuery(id+"FQ5JFwxVdaqARUP_1.wireOp",EDGE,"fcba4419-a2ee-464f-be9d-58f11bf3418b.sketch_text.stroke-48"),sQuery(id+"FQ5JFwxVdaqARUP_1.wireOp",EDGE,"fcba4419-a2ee-464f-be9d-58f11bf3418b.sketch_text.stroke-49"),sQuery(id+"FQ5JFwxVdaqARUP_1.wireOp",EDGE,"fcba4419-a2ee-464f-be9d-58f11bf3418b.sketch_text.stroke-50"),sQuery(id+"FQ5JFwxVdaqARUP_1.wireOp",EDGE,"fcba4419-a2ee-464f-be9d-58f11bf3418b.sketch_text.stroke-51"),sQuery(id+"FQ5JFwxVdaqARUP_1.wireOp",EDGE,"fcba4419-a2ee-464f-be9d-58f11bf3418b.sketch_text.stroke-52"),sQuery(id+"FQ5JFwxVdaqARUP_1.wireOp",EDGE,"fcba4419-a2ee-464f-be9d-58f11bf3418b.sketch_text.stroke-53"),sQuery(id+"FQ5JFwxVdaqARUP_1.wireOp",EDGE,"fcba4419-a2ee-464f-be9d-58f11bf3418b.sketch_text.stroke-54"),sQuery(id+"FQ5JFwxVdaqARUP_1.wireOp",EDGE,"fcba4419-a2ee-464f-be9d-58f11bf3418b.sketch_text.stroke-55"),sQuery(id+"FQ5JFwxVdaqARUP_1.wireOp",EDGE,"fcba4419-a2ee-464f-be9d-58f11bf3418b.sketch_text.stroke-56"),sQuery(id+"FQ5JFwxVdaqARUP_1.wireOp",EDGE,"fcba4419-a2ee-464f-be9d-58f11bf3418b.sketch_text.stroke-57"),sQuery(id+"FQ5JFwxVdaqARUP_1.wireOp",EDGE,"fcba4419-a2ee-464f-be9d-58f11bf3418b.sketch_text.stroke-58"),sQuery(id+"FQ5JFwxVdaqARUP_1.wireOp",EDGE,"fcba4419-a2ee-464f-be9d-58f11bf3418b.sketch_text.stroke-59"),sQuery(id+"FQ5JFwxVdaqARUP_1.wireOp",EDGE,"fcba4419-a2ee-464f-be9d-58f11bf3418b.sketch_text.stroke-60"),sQuery(id+"FQ5JFwxVdaqARUP_1.wireOp",EDGE,"fcba4419-a2ee-464f-be9d-58f11bf3418b.sketch_text.stroke-61"),sQuery(id+"FQ5JFwxVdaqARUP_1.wireOp",EDGE,"fcba4419-a2ee-464f-be9d-58f11bf3418b.sketch_text.stroke-62"),sQuery(id+"FQ5JFwxVdaqARUP_1.wireOp",EDGE,"fcba4419-a2ee-464f-be9d-58f11bf3418b.sketch_text.stroke-63"),sQuery(id+"FQ5JFwxVdaqARUP_1.wireOp",EDGE,"fcba4419-a2ee-464f-be9d-58f11bf3418b.sketch_text.stroke-64"),sQuery(id+"FQ5JFwxVdaqARUP_1.wireOp",EDGE,"fcba4419-a2ee-464f-be9d-58f11bf3418b.sketch_text.stroke-65"),sQuery(id+"FQ5JFwxVdaqARUP_1.wireOp",EDGE,"fcba4419-a2ee-464f-be9d-58f11bf3418b.sketch_text.stroke-66"),sQuery(id+"FQ5JFwxVdaqARUP_1.wireOp",EDGE,"fcba4419-a2ee-464f-be9d-58f11bf3418b.sketch_text.stroke-67"),sQuery(id+"FQ5JFwxVdaqARUP_1.wireOp",EDGE,"fcba4419-a2ee-464f-be9d-58f11bf3418b.sketch_text.stroke-68"),sQuery(id+"FQ5JFwxVdaqARUP_1.wireOp",EDGE,"fcba4419-a2ee-464f-be9d-58f11bf3418b.sketch_text.stroke-69"),sQuery(id+"FQ5JFwxVdaqARUP_1.wireOp",EDGE,"fcba4419-a2ee-464f-be9d-58f11bf3418b.sketch_text.stroke-70"),sQuery(id+"FQ5JFwxVdaqARUP_1.wireOp",EDGE,"fcba4419-a2ee-464f-be9d-58f11bf3418b.sketch_text.stroke-71"),sQuery(id+"FQ5JFwxVdaqARUP_1.wireOp",EDGE,"fcba4419-a2ee-464f-be9d-58f11bf3418b.sketch_text.stroke-72"),sQuery(id+"FQ5JFwxVdaqARUP_1.wireOp",EDGE,"fcba4419-a2ee-464f-be9d-58f11bf3418b.sketch_text.stroke-73"),sQuery(id+"FQ5JFwxVdaqARUP_1.wireOp",EDGE,"fcba4419-a2ee-464f-be9d-58f11bf3418b.sketch_text.stroke-74"),sQuery(id+"FQ5JFwxVdaqARUP_1.wireOp",EDGE,"fcba4419-a2ee-464f-be9d-58f11bf3418b.sketch_text.stroke-75"),sQuery(id+"FQ5JFwxVdaqARUP_1.wireOp",EDGE,"fcba4419-a2ee-464f-be9d-58f11bf3418b.sketch_text.stroke-76"),sQuery(id+"FQ5JFwxVdaqARUP_1.wireOp",EDGE,"fcba4419-a2ee-464f-be9d-58f11bf3418b.sketch_text.stroke-77"),sQuery(id+"FQ5JFwxVdaqARUP_1.wireOp",EDGE,"fcba4419-a2ee-464f-be9d-58f11bf3418b.sketch_text.stroke-78"),sQuery(id+"FQ5JFwxVdaqARUP_1.wireOp",EDGE,"fcba4419-a2ee-464f-be9d-58f11bf3418b.sketch_text.stroke-79"),sQuery(id+"FQ5JFwxVdaqARUP_1.wireOp",EDGE,"fcba4419-a2ee-464f-be9d-58f11bf3418b.sketch_text.stroke-80"),sQuery(id+"FQ5JFwxVdaqARUP_1.wireOp",EDGE,"fcba4419-a2ee-464f-be9d-58f11bf3418b.sketch_text.stroke-81"),sQuery(id+"FQ5JFwxVdaqARUP_1.wireOp",EDGE,"fcba4419-a2ee-464f-be9d-58f11bf3418b.sketch_text.stroke-82"),sQuery(id+"FQ5JFwxVdaqARUP_1.wireOp",EDGE,"fcba4419-a2ee-464f-be9d-58f11bf3418b.sketch_text.stroke-83"),sQuery(id+"FQ5JFwxVdaqARUP_1.wireOp",EDGE,"fcba4419-a2ee-464f-be9d-58f11bf3418b.sketch_text.stroke-84"),sQuery(id+"FQ5JFwxVdaqARUP_1.wireOp",EDGE,"fcba4419-a2ee-464f-be9d-58f11bf3418b.sketch_text.stroke-85"),sQuery(id+"FQ5JFwxVdaqARUP_1.wireOp",EDGE,"fcba4419-a2ee-464f-be9d-58f11bf3418b.sketch_text.stroke-86"),sQuery(id+"FQ5JFwxVdaqARUP_1.wireOp",EDGE,"fcba4419-a2ee-464f-be9d-58f11bf3418b.sketch_text.stroke-87"),sQuery(id+"FQ5JFwxVdaqARUP_1.wireOp",EDGE,"fcba4419-a2ee-464f-be9d-58f11bf3418b.sketch_text.stroke-88"),sQuery(id+"FQ5JFwxVdaqARUP_1.wireOp",EDGE,"fcba4419-a2ee-464f-be9d-58f11bf3418b.sketch_text.stroke-89"),sQuery(id+"FQ5JFwxVdaqARUP_1.wireOp",EDGE,"fcba4419-a2ee-464f-be9d-58f11bf3418b.sketch_text.stroke-90"),sQuery(id+"FQ5JFwxVdaqARUP_1.wireOp",EDGE,"fcba4419-a2ee-464f-be9d-58f11bf3418b.sketch_text.stroke-91"),sQuery(id+"FQ5JFwxVdaqARUP_1.wireOp",EDGE,"fcba4419-a2ee-464f-be9d-58f11bf3418b.sketch_text.stroke-92"),sQuery(id+"FQ5JFwxVdaqARUP_1.wireOp",EDGE,"fcba4419-a2ee-464f-be9d-58f11bf3418b.sketch_text.stroke-93"),sQuery(id+"FQ5JFwxVdaqARUP_1.wireOp",EDGE,"fcba4419-a2ee-464f-be9d-58f11bf3418b.sketch_text.stroke-94"),sQuery(id+"FQ5JFwxVdaqARUP_1.wireOp",EDGE,"fcba4419-a2ee-464f-be9d-58f11bf3418b.sketch_text.stroke-95"),sQuery(id+"FQ5JFwxVdaqARUP_1.wireOp",EDGE,"fcba4419-a2ee-464f-be9d-58f11bf3418b.sketch_text.stroke-96"),sQuery(id+"FQ5JFwxVdaqARUP_1.wireOp",EDGE,"fcba4419-a2ee-464f-be9d-58f11bf3418b.sketch_text.stroke-97"),sQuery(id+"FQ5JFwxVdaqARUP_1.wireOp",EDGE,"fcba4419-a2ee-464f-be9d-58f11bf3418b.sketch_text.stroke-98"),sQuery(id+"FQ5JFwxVdaqARUP_1.wireOp",EDGE,"fcba4419-a2ee-464f-be9d-58f11bf3418b.sketch_text.stroke-99"),sQuery(id+"FQ5JFwxVdaqARUP_1.wireOp",EDGE,"fcba4419-a2ee-464f-be9d-58f11bf3418b.sketch_text.stroke-100"),sQuery(id+"FQ5JFwxVdaqARUP_1.wireOp",EDGE,"fcba4419-a2ee-464f-be9d-58f11bf3418b.sketch_text.stroke-101"),sQuery(id+"FQ5JFwxVdaqARUP_1.wireOp",EDGE,"fcba4419-a2ee-464f-be9d-58f11bf3418b.sketch_text.stroke-102"),sQuery(id+"FQ5JFwxVdaqARUP_1.wireOp",EDGE,"fcba4419-a2ee-464f-be9d-58f11bf3418b.sketch_text.stroke-103"),sQuery(id+"FQ5JFwxVdaqARUP_1.wireOp",EDGE,"fcba4419-a2ee-464f-be9d-58f11bf3418b.sketch_text.stroke-104"),sQuery(id+"FQ5JFwxVdaqARUP_1.wireOp",EDGE,"fcba4419-a2ee-464f-be9d-58f11bf3418b.sketch_text.stroke-105"),sQuery(id+"FQ5JFwxVdaqARUP_1.wireOp",EDGE,"fcba4419-a2ee-464f-be9d-58f11bf3418b.sketch_text.stroke-106"),sQuery(id+"FQ5JFwxVdaqARUP_1.wireOp",EDGE,"fcba4419-a2ee-464f-be9d-58f11bf3418b.sketch_text.stroke-107"),sQuery(id+"FQ5JFwxVdaqARUP_1.wireOp",EDGE,"fcba4419-a2ee-464f-be9d-58f11bf3418b.sketch_text.stroke-108"),sQuery(id+"FQ5JFwxVdaqARUP_1.wireOp",EDGE,"fcba4419-a2ee-464f-be9d-58f11bf3418b.sketch_text.stroke-109"),sQuery(id+"FQ5JFwxVdaqARUP_1.wireOp",EDGE,"fcba4419-a2ee-464f-be9d-58f11bf3418b.sketch_text.stroke-110"),sQuery(id+"FQ5JFwxVdaqARUP_1.wireOp",EDGE,"fcba4419-a2ee-464f-be9d-58f11bf3418b.sketch_text.stroke-111"),sQuery(id+"FQ5JFwxVdaqARUP_1.wireOp",EDGE,"fcba4419-a2ee-464f-be9d-58f11bf3418b.sketch_text.stroke-112"),sQuery(id+"FQ5JFwxVdaqARUP_1.wireOp",EDGE,"fcba4419-a2ee-464f-be9d-58f11bf3418b.sketch_text.stroke-113"),sQuery(id+"FQ5JFwxVdaqARUP_1.wireOp",EDGE,"fcba4419-a2ee-464f-be9d-58f11bf3418b.sketch_text.stroke-114"),sQuery(id+"FQ5JFwxVdaqARUP_1.wireOp",EDGE,"fcba4419-a2ee-464f-be9d-58f11bf3418b.sketch_text.stroke-115"),sQuery(id+"FQ5JFwxVdaqARUP_1.wireOp",EDGE,"fcba4419-a2ee-464f-be9d-58f11bf3418b.sketch_text.stroke-116"),sQuery(id+"FQ5JFwxVdaqARUP_1.wireOp",EDGE,"fcba4419-a2ee-464f-be9d-58f11bf3418b.sketch_text.stroke-117"),sQuery(id+"FQ5JFwxVdaqARUP_1.wireOp",EDGE,"fcba4419-a2ee-464f-be9d-58f11bf3418b.sketch_text.stroke-118"),sQuery(id+"FQ5JFwxVdaqARUP_1.wireOp",EDGE,"fcba4419-a2ee-464f-be9d-58f11bf3418b.sketch_text.stroke-119"),sQuery(id+"FQ5JFwxVdaqARUP_1.wireOp",EDGE,"fcba4419-a2ee-464f-be9d-58f11bf3418b.sketch_text.stroke-120"),sQuery(id+"FQ5JFwxVdaqARUP_1.wireOp",EDGE,"fcba4419-a2ee-464f-be9d-58f11bf3418b.sketch_text.stroke-121"),sQuery(id+"FQ5JFwxVdaqARUP_1.wireOp",EDGE,"fcba4419-a2ee-464f-be9d-58f11bf3418b.sketch_text.stroke-122"),sQuery(id+"FQ5JFwxVdaqARUP_1.wireOp",EDGE,"fcba4419-a2ee-464f-be9d-58f11bf3418b.sketch_text.stroke-123"),sQuery(id+"FQ5JFwxVdaqARUP_1.wireOp",EDGE,"fcba4419-a2ee-464f-be9d-58f11bf3418b.sketch_text.stroke-124"),sQuery(id+"FQ5JFwxVdaqARUP_1.wireOp",EDGE,"fcba4419-a2ee-464f-be9d-58f11bf3418b.sketch_text.stroke-125"),sQuery(id+"FQ5JFwxVdaqARUP_1.wireOp",EDGE,"fcba4419-a2ee-464f-be9d-58f11bf3418b.sketch_text.stroke-126"),sQuery(id+"FQ5JFwxVdaqARUP_1.wireOp",EDGE,"fcba4419-a2ee-464f-be9d-58f11bf3418b.sketch_text.stroke-127"),sQuery(id+"FQ5JFwxVdaqARUP_1.wireOp",EDGE,"fcba4419-a2ee-464f-be9d-58f11bf3418b.sketch_text.stroke-128"),sQuery(id+"FQ5JFwxVdaqARUP_1.wireOp",EDGE,"fcba4419-a2ee-464f-be9d-58f11bf3418b.sketch_text.stroke-129"),sQuery(id+"FQ5JFwxVdaqARUP_1.wireOp",EDGE,"fcba4419-a2ee-464f-be9d-58f11bf3418b.sketch_text.stroke-130"),sQuery(id+"FQ5JFwxVdaqARUP_1.wireOp",EDGE,"fcba4419-a2ee-464f-be9d-58f11bf3418b.sketch_text.stroke-131"),sQuery(id+"FQ5JFwxVdaqARUP_1.wireOp",EDGE,"fcba4419-a2ee-464f-be9d-58f11bf3418b.sketch_text.stroke-132"),sQuery(id+"FQ5JFwxVdaqARUP_1.wireOp",EDGE,"fcba4419-a2ee-464f-be9d-58f11bf3418b.sketch_text.stroke-133"),sQuery(id+"FQ5JFwxVdaqARUP_1.wireOp",EDGE,"fcba4419-a2ee-464f-be9d-58f11bf3418b.sketch_text.stroke-134"),sQuery(id+"FQ5JFwxVdaqARUP_1.wireOp",EDGE,"fcba4419-a2ee-464f-be9d-58f11bf3418b.sketch_text.stroke-135"),sQuery(id+"FQ5JFwxVdaqARUP_1.wireOp",EDGE,"fcba4419-a2ee-464f-be9d-58f11bf3418b.sketch_text.stroke-136"),sQuery(id+"FQ5JFwxVdaqARUP_1.wireOp",EDGE,"fcba4419-a2ee-464f-be9d-58f11bf3418b.sketch_text.stroke-137"),sQuery(id+"FQ5JFwxVdaqARUP_1.wireOp",EDGE,"fcba4419-a2ee-464f-be9d-58f11bf3418b.sketch_text.stroke-138"),sQuery(id+"FQ5JFwxVdaqARUP_1.wireOp",EDGE,"fcba4419-a2ee-464f-be9d-58f11bf3418b.sketch_text.stroke-139"),sQuery(id+"FQ5JFwxVdaqARUP_1.wireOp",EDGE,"fcba4419-a2ee-464f-be9d-58f11bf3418b.sketch_text.stroke-140"),sQuery(id+"FQ5JFwxVdaqARUP_1.wireOp",EDGE,"fcba4419-a2ee-464f-be9d-58f11bf3418b.sketch_text.stroke-141"),sQuery(id+"FQ5JFwxVdaqARUP_1.wireOp",EDGE,"fcba4419-a2ee-464f-be9d-58f11bf3418b.sketch_text.stroke-142"),sQuery(id+"FQ5JFwxVdaqARUP_1.wireOp",EDGE,"fcba4419-a2ee-464f-be9d-58f11bf3418b.sketch_text.stroke-143"),sQuery(id+"FQ5JFwxVdaqARUP_1.wireOp",EDGE,"fcba4419-a2ee-464f-be9d-58f11bf3418b.sketch_text.stroke-144"),sQuery(id+"FQ5JFwxVdaqARUP_1.wireOp",EDGE,"fcba4419-a2ee-464f-be9d-58f11bf3418b.sketch_text.stroke-145"),sQuery(id+"FQ5JFwxVdaqARUP_1.wireOp",EDGE,"fcba4419-a2ee-464f-be9d-58f11bf3418b.sketch_text.stroke-146"),sQuery(id+"FQ5JFwxVdaqARUP_1.wireOp",EDGE,"fcba4419-a2ee-464f-be9d-58f11bf3418b.sketch_text.stroke-147"),sQuery(id+"FQ5JFwxVdaqARUP_1.wireOp",EDGE,"fcba4419-a2ee-464f-be9d-58f11bf3418b.sketch_text.stroke-148"),sQuery(id+"FQ5JFwxVdaqARUP_1.wireOp",EDGE,"fcba4419-a2ee-464f-be9d-58f11bf3418b.sketch_text.stroke-149"),sQuery(id+"FQ5JFwxVdaqARUP_1.wireOp",EDGE,"fcba4419-a2ee-464f-be9d-58f11bf3418b.sketch_text.stroke-150"),sQuery(id+"FQ5JFwxVdaqARUP_1.wireOp",EDGE,"fcba4419-a2ee-464f-be9d-58f11bf3418b.sketch_text.stroke-151"),sQuery(id+"FQ5JFwxVdaqARUP_1.wireOp",EDGE,"fcba4419-a2ee-464f-be9d-58f11bf3418b.sketch_text.stroke-152"),sQuery(id+"FQ5JFwxVdaqARUP_1.wireOp",EDGE,"fcba4419-a2ee-464f-be9d-58f11bf3418b.sketch_text.stroke-153"),sQuery(id+"FQ5JFwxVdaqARUP_1.wireOp",EDGE,"fcba4419-a2ee-464f-be9d-58f11bf3418b.sketch_text.stroke-154"),sQuery(id+"FQ5JFwxVdaqARUP_1.wireOp",EDGE,"fcba4419-a2ee-464f-be9d-58f11bf3418b.sketch_text.stroke-155"),sQuery(id+"FQ5JFwxVdaqARUP_1.wireOp",EDGE,"fcba4419-a2ee-464f-be9d-58f11bf3418b.sketch_text.stroke-156"),sQuery(id+"FQ5JFwxVdaqARUP_1.wireOp",EDGE,"fcba4419-a2ee-464f-be9d-58f11bf3418b.sketch_text.stroke-157"),sQuery(id+"FQ5JFwxVdaqARUP_1.wireOp",EDGE,"fcba4419-a2ee-464f-be9d-58f11bf3418b.sketch_text.stroke-158"),sQuery(id+"FQ5JFwxVdaqARUP_1.wireOp",EDGE,"fcba4419-a2ee-464f-be9d-58f11bf3418b.sketch_text.stroke-159"),sQuery(id+"FQ5JFwxVdaqARUP_1.wireOp",EDGE,"fcba4419-a2ee-464f-be9d-58f11bf3418b.sketch_text.stroke-160"),sQuery(id+"FQ5JFwxVdaqARUP_1.wireOp",EDGE,"fcba4419-a2ee-464f-be9d-58f11bf3418b.sketch_text.stroke-161"),sQuery(id+"FQ5JFwxVdaqARUP_1.wireOp",EDGE,"fcba4419-a2ee-464f-be9d-58f11bf3418b.sketch_text.stroke-162"),sQuery(id+"FQ5JFwxVdaqARUP_1.wireOp",EDGE,"fcba4419-a2ee-464f-be9d-58f11bf3418b.sketch_text.stroke-163"),sQuery(id+"FQ5JFwxVdaqARUP_1.wireOp",EDGE,"fcba4419-a2ee-464f-be9d-58f11bf3418b.sketch_text.stroke-164"),sQuery(id+"FQ5JFwxVdaqARUP_1.wireOp",EDGE,"fcba4419-a2ee-464f-be9d-58f11bf3418b.sketch_text.stroke-165"),sQuery(id+"FQ5JFwxVdaqARUP_1.wireOp",EDGE,"fcba4419-a2ee-464f-be9d-58f11bf3418b.sketch_text.stroke-166"),sQuery(id+"FQ5JFwxVdaqARUP_1.wireOp",EDGE,"fcba4419-a2ee-464f-be9d-58f11bf3418b.sketch_text.stroke-167"),sQuery(id+"FQ5JFwxVdaqARUP_1.wireOp",EDGE,"fcba4419-a2ee-464f-be9d-58f11bf3418b.sketch_text.stroke-168"),sQuery(id+"FQ5JFwxVdaqARUP_1.wireOp",EDGE,"fcba4419-a2ee-464f-be9d-58f11bf3418b.sketch_text.stroke-169"),sQuery(id+"FQ5JFwxVdaqARUP_1.wireOp",EDGE,"fcba4419-a2ee-464f-be9d-58f11bf3418b.sketch_text.stroke-170"),sQuery(id+"FQ5JFwxVdaqARUP_1.wireOp",EDGE,"fcba4419-a2ee-464f-be9d-58f11bf3418b.sketch_text.stroke-171"),sQuery(id+"FQ5JFwxVdaqARUP_1.wireOp",EDGE,"fcba4419-a2ee-464f-be9d-58f11bf3418b.sketch_text.stroke-172"),sQuery(id+"FQ5JFwxVdaqARUP_1.wireOp",EDGE,"fcba4419-a2ee-464f-be9d-58f11bf3418b.sketch_text.stroke-173"),sQuery(id+"FHMxAyK4CFUKdhS_1.wireOp",EDGE,"1cb9c079-ea9b-4899-8069-e0e3048e911d.sketch_text.stroke-0"),sQuery(id+"FHMxAyK4CFUKdhS_1.wireOp",EDGE,"1cb9c079-ea9b-4899-8069-e0e3048e911d.sketch_text.stroke-1"),sQuery(id+"FHMxAyK4CFUKdhS_1.wireOp",EDGE,"1cb9c079-ea9b-4899-8069-e0e3048e911d.sketch_text.stroke-2"),sQuery(id+"FHMxAyK4CFUKdhS_1.wireOp",EDGE,"1cb9c079-ea9b-4899-8069-e0e3048e911d.sketch_text.stroke-3"),sQuery(id+"FHMxAyK4CFUKdhS_1.wireOp",EDGE,"1cb9c079-ea9b-4899-8069-e0e3048e911d.sketch_text.stroke-4"),sQuery(id+"FHMxAyK4CFUKdhS_1.wireOp",EDGE,"1cb9c079-ea9b-4899-8069-e0e3048e911d.sketch_text.stroke-5"),sQuery(id+"FHMxAyK4CFUKdhS_1.wireOp",EDGE,"1cb9c079-ea9b-4899-8069-e0e3048e911d.sketch_text.stroke-6"),sQuery(id+"FHMxAyK4CFUKdhS_1.wireOp",EDGE,"1cb9c079-ea9b-4899-8069-e0e3048e911d.sketch_text.stroke-7"),sQuery(id+"FHMxAyK4CFUKdhS_1.wireOp",EDGE,"1cb9c079-ea9b-4899-8069-e0e3048e911d.sketch_text.stroke-8"),sQuery(id+"FHMxAyK4CFUKdhS_1.wireOp",EDGE,"1cb9c079-ea9b-4899-8069-e0e3048e911d.sketch_text.stroke-9"),sQuery(id+"FHMxAyK4CFUKdhS_1.wireOp",EDGE,"1cb9c079-ea9b-4899-8069-e0e3048e911d.sketch_text.stroke-10"),sQuery(id+"FHMxAyK4CFUKdhS_1.wireOp",EDGE,"1cb9c079-ea9b-4899-8069-e0e3048e911d.sketch_text.stroke-11"),sQuery(id+"FHMxAyK4CFUKdhS_1.wireOp",EDGE,"1cb9c079-ea9b-4899-8069-e0e3048e911d.sketch_text.stroke-12"),sQuery(id+"FHMxAyK4CFUKdhS_1.wireOp",EDGE,"1cb9c079-ea9b-4899-8069-e0e3048e911d.sketch_text.stroke-13"),sQuery(id+"FHMxAyK4CFUKdhS_1.wireOp",EDGE,"1cb9c079-ea9b-4899-8069-e0e3048e911d.sketch_text.stroke-14"),sQuery(id+"FHMxAyK4CFUKdhS_1.wireOp",EDGE,"1cb9c079-ea9b-4899-8069-e0e3048e911d.sketch_text.stroke-15"),sQuery(id+"FHMxAyK4CFUKdhS_1.wireOp",EDGE,"1cb9c079-ea9b-4899-8069-e0e3048e911d.sketch_text.stroke-16"),sQuery(id+"FHMxAyK4CFUKdhS_1.wireOp",EDGE,"1cb9c079-ea9b-4899-8069-e0e3048e911d.sketch_text.stroke-17"),sQuery(id+"FHMxAyK4CFUKdhS_1.wireOp",EDGE,"1cb9c079-ea9b-4899-8069-e0e3048e911d.sketch_text.stroke-18"),sQuery(id+"FHMxAyK4CFUKdhS_1.wireOp",EDGE,"1cb9c079-ea9b-4899-8069-e0e3048e911d.sketch_text.stroke-19"),sQuery(id+"FHMxAyK4CFUKdhS_1.wireOp",EDGE,"1cb9c079-ea9b-4899-8069-e0e3048e911d.sketch_text.stroke-20"),sQuery(id+"FHMxAyK4CFUKdhS_1.wireOp",EDGE,"1cb9c079-ea9b-4899-8069-e0e3048e911d.sketch_text.stroke-21"),sQuery(id+"FHMxAyK4CFUKdhS_1.wireOp",EDGE,"1cb9c079-ea9b-4899-8069-e0e3048e911d.sketch_text.stroke-22"),sQuery(id+"FHMxAyK4CFUKdhS_1.wireOp",EDGE,"1cb9c079-ea9b-4899-8069-e0e3048e911d.sketch_text.stroke-23"),sQuery(id+"FHMxAyK4CFUKdhS_1.wireOp",EDGE,"1cb9c079-ea9b-4899-8069-e0e3048e911d.sketch_text.stroke-24"),sQuery(id+"FHMxAyK4CFUKdhS_1.wireOp",EDGE,"1cb9c079-ea9b-4899-8069-e0e3048e911d.sketch_text.stroke-25"),sQuery(id+"FHMxAyK4CFUKdhS_1.wireOp",EDGE,"1cb9c079-ea9b-4899-8069-e0e3048e911d.sketch_text.stroke-26"),sQuery(id+"FHMxAyK4CFUKdhS_1.wireOp",EDGE,"1cb9c079-ea9b-4899-8069-e0e3048e911d.sketch_text.stroke-27"),sQuery(id+"FHMxAyK4CFUKdhS_1.wireOp",EDGE,"1cb9c079-ea9b-4899-8069-e0e3048e911d.sketch_text.stroke-28"),sQuery(id+"FHMxAyK4CFUKdhS_1.wireOp",EDGE,"1cb9c079-ea9b-4899-8069-e0e3048e911d.sketch_text.stroke-29"),sQuery(id+"FHMxAyK4CFUKdhS_1.wireOp",EDGE,"1cb9c079-ea9b-4899-8069-e0e3048e911d.sketch_text.stroke-30"),sQuery(id+"FHMxAyK4CFUKdhS_1.wireOp",EDGE,"1cb9c079-ea9b-4899-8069-e0e3048e911d.sketch_text.stroke-31"),sQuery(id+"FHMxAyK4CFUKdhS_1.wireOp",EDGE,"1cb9c079-ea9b-4899-8069-e0e3048e911d.sketch_text.stroke-32"),sQuery(id+"FHMxAyK4CFUKdhS_1.wireOp",EDGE,"1cb9c079-ea9b-4899-8069-e0e3048e911d.sketch_text.stroke-33"),sQuery(id+"FHMxAyK4CFUKdhS_1.wireOp",EDGE,"1cb9c079-ea9b-4899-8069-e0e3048e911d.sketch_text.stroke-34"),sQuery(id+"FHMxAyK4CFUKdhS_1.wireOp",EDGE,"1cb9c079-ea9b-4899-8069-e0e3048e911d.sketch_text.stroke-35"),sQuery(id+"FHMxAyK4CFUKdhS_1.wireOp",EDGE,"1cb9c079-ea9b-4899-8069-e0e3048e911d.sketch_text.stroke-36"),sQuery(id+"FHMxAyK4CFUKdhS_1.wireOp",EDGE,"1cb9c079-ea9b-4899-8069-e0e3048e911d.sketch_text.stroke-37"),sQuery(id+"FHMxAyK4CFUKdhS_1.wireOp",EDGE,"1cb9c079-ea9b-4899-8069-e0e3048e911d.sketch_text.stroke-38"),sQuery(id+"FHMxAyK4CFUKdhS_1.wireOp",EDGE,"1cb9c079-ea9b-4899-8069-e0e3048e911d.sketch_text.stroke-39"),sQuery(id+"FHMxAyK4CFUKdhS_1.wireOp",EDGE,"1cb9c079-ea9b-4899-8069-e0e3048e911d.sketch_text.stroke-40"),sQuery(id+"FHMxAyK4CFUKdhS_1.wireOp",EDGE,"1cb9c079-ea9b-4899-8069-e0e3048e911d.sketch_text.stroke-41"),sQuery(id+"FHMxAyK4CFUKdhS_1.wireOp",EDGE,"1cb9c079-ea9b-4899-8069-e0e3048e911d.sketch_text.stroke-42"),sQuery(id+"FHMxAyK4CFUKdhS_1.wireOp",EDGE,"1cb9c079-ea9b-4899-8069-e0e3048e911d.sketch_text.stroke-43"),sQuery(id+"FHMxAyK4CFUKdhS_1.wireOp",EDGE,"1cb9c079-ea9b-4899-8069-e0e3048e911d.sketch_text.stroke-44"),sQuery(id+"FHMxAyK4CFUKdhS_1.wireOp",EDGE,"1cb9c079-ea9b-4899-8069-e0e3048e911d.sketch_text.stroke-45"),sQuery(id+"FHMxAyK4CFUKdhS_1.wireOp",EDGE,"1cb9c079-ea9b-4899-8069-e0e3048e911d.sketch_text.stroke-46"),sQuery(id+"FHMxAyK4CFUKdhS_1.wireOp",EDGE,"1cb9c079-ea9b-4899-8069-e0e3048e911d.sketch_text.stroke-47"),sQuery(id+"FHMxAyK4CFUKdhS_1.wireOp",EDGE,"1cb9c079-ea9b-4899-8069-e0e3048e911d.sketch_text.stroke-48"),sQuery(id+"FHMxAyK4CFUKdhS_1.wireOp",EDGE,"1cb9c079-ea9b-4899-8069-e0e3048e911d.sketch_text.stroke-49"),sQuery(id+"FHMxAyK4CFUKdhS_1.wireOp",EDGE,"1cb9c079-ea9b-4899-8069-e0e3048e911d.sketch_text.stroke-50"),sQuery(id+"FHMxAyK4CFUKdhS_1.wireOp",EDGE,"1cb9c079-ea9b-4899-8069-e0e3048e911d.sketch_text.stroke-51"),sQuery(id+"FHMxAyK4CFUKdhS_1.wireOp",EDGE,"1cb9c079-ea9b-4899-8069-e0e3048e911d.sketch_text.stroke-52"),sQuery(id+"FHMxAyK4CFUKdhS_1.wireOp",EDGE,"1cb9c079-ea9b-4899-8069-e0e3048e911d.sketch_text.stroke-53"),sQuery(id+"FHMxAyK4CFUKdhS_1.wireOp",EDGE,"1cb9c079-ea9b-4899-8069-e0e3048e911d.sketch_text.stroke-54"),sQuery(id+"FHMxAyK4CFUKdhS_1.wireOp",EDGE,"1cb9c079-ea9b-4899-8069-e0e3048e911d.sketch_text.stroke-55"),sQuery(id+"FHMxAyK4CFUKdhS_1.wireOp",EDGE,"1cb9c079-ea9b-4899-8069-e0e3048e911d.sketch_text.stroke-56"),sQuery(id+"FHMxAyK4CFUKdhS_1.wireOp",EDGE,"1cb9c079-ea9b-4899-8069-e0e3048e911d.sketch_text.stroke-57"),sQuery(id+"FHMxAyK4CFUKdhS_1.wireOp",EDGE,"1cb9c079-ea9b-4899-8069-e0e3048e911d.sketch_text.stroke-58"),sQuery(id+"FHMxAyK4CFUKdhS_1.wireOp",EDGE,"1cb9c079-ea9b-4899-8069-e0e3048e911d.sketch_text.stroke-59"),sQuery(id+"FHMxAyK4CFUKdhS_1.wireOp",EDGE,"1cb9c079-ea9b-4899-8069-e0e3048e911d.sketch_text.stroke-60"),sQuery(id+"FHMxAyK4CFUKdhS_1.wireOp",EDGE,"1cb9c079-ea9b-4899-8069-e0e3048e911d.sketch_text.stroke-61"),sQuery(id+"FHMxAyK4CFUKdhS_1.wireOp",EDGE,"1cb9c079-ea9b-4899-8069-e0e3048e911d.sketch_text.stroke-62"),sQuery(id+"FHMxAyK4CFUKdhS_1.wireOp",EDGE,"1cb9c079-ea9b-4899-8069-e0e3048e911d.sketch_text.stroke-71"),sQuery(id+"FHMxAyK4CFUKdhS_1.wireOp",EDGE,"1cb9c079-ea9b-4899-8069-e0e3048e911d.sketch_text.stroke-72"),sQuery(id+"FHMxAyK4CFUKdhS_1.wireOp",EDGE,"1cb9c079-ea9b-4899-8069-e0e3048e911d.sketch_text.stroke-73"),sQuery(id+"FHMxAyK4CFUKdhS_1.wireOp",EDGE,"1cb9c079-ea9b-4899-8069-e0e3048e911d.sketch_text.stroke-74"),sQuery(id+"FHMxAyK4CFUKdhS_1.wireOp",EDGE,"1cb9c079-ea9b-4899-8069-e0e3048e911d.sketch_text.stroke-75"),sQuery(id+"FHMxAyK4CFUKdhS_1.wireOp",EDGE,"1cb9c079-ea9b-4899-8069-e0e3048e911d.sketch_text.stroke-76"),sQuery(id+"FHMxAyK4CFUKdhS_1.wireOp",EDGE,"1cb9c079-ea9b-4899-8069-e0e3048e911d.sketch_text.stroke-77"),sQuery(id+"FHMxAyK4CFUKdhS_1.wireOp",EDGE,"1cb9c079-ea9b-4899-8069-e0e3048e911d.sketch_text.stroke-78"),sQuery(id+"FHMxAyK4CFUKdhS_1.wireOp",EDGE,"1cb9c079-ea9b-4899-8069-e0e3048e911d.sketch_text.stroke-79"),sQuery(id+"FHMxAyK4CFUKdhS_1.wireOp",EDGE,"1cb9c079-ea9b-4899-8069-e0e3048e911d.sketch_text.stroke-80"),sQuery(id+"FHMxAyK4CFUKdhS_1.wireOp",EDGE,"1cb9c079-ea9b-4899-8069-e0e3048e911d.sketch_text.stroke-81"),sQuery(id+"FHMxAyK4CFUKdhS_1.wireOp",EDGE,"1cb9c079-ea9b-4899-8069-e0e3048e911d.sketch_text.stroke-82"),sQuery(id+"FHMxAyK4CFUKdhS_1.wireOp",EDGE,"1cb9c079-ea9b-4899-8069-e0e3048e911d.sketch_text.stroke-83"),sQuery(id+"FHMxAyK4CFUKdhS_1.wireOp",EDGE,"1cb9c079-ea9b-4899-8069-e0e3048e911d.sketch_text.stroke-84"),sQuery(id+"FHMxAyK4CFUKdhS_1.wireOp",EDGE,"1cb9c079-ea9b-4899-8069-e0e3048e911d.sketch_text.stroke-85"),sQuery(id+"FHMxAyK4CFUKdhS_1.wireOp",EDGE,"1cb9c079-ea9b-4899-8069-e0e3048e911d.sketch_text.stroke-86"),sQuery(id+"FHMxAyK4CFUKdhS_1.wireOp",EDGE,"1cb9c079-ea9b-4899-8069-e0e3048e911d.sketch_text.stroke-87"),sQuery(id+"FHMxAyK4CFUKdhS_1.wireOp",EDGE,"1cb9c079-ea9b-4899-8069-e0e3048e911d.sketch_text.stroke-88"),sQuery(id+"FHMxAyK4CFUKdhS_1.wireOp",EDGE,"1cb9c079-ea9b-4899-8069-e0e3048e911d.sketch_text.stroke-89"),sQuery(id+"FHMxAyK4CFUKdhS_1.wireOp",EDGE,"1cb9c079-ea9b-4899-8069-e0e3048e911d.sketch_text.stroke-90"),sQuery(id+"FHMxAyK4CFUKdhS_1.wireOp",EDGE,"1cb9c079-ea9b-4899-8069-e0e3048e911d.sketch_text.stroke-91"),sQuery(id+"FHMxAyK4CFUKdhS_1.wireOp",EDGE,"1cb9c079-ea9b-4899-8069-e0e3048e911d.sketch_text.stroke-92"),sQuery(id+"FHMxAyK4CFUKdhS_1.wireOp",EDGE,"1cb9c079-ea9b-4899-8069-e0e3048e911d.sketch_text.stroke-93"),sQuery(id+"FHMxAyK4CFUKdhS_1.wireOp",EDGE,"1cb9c079-ea9b-4899-8069-e0e3048e911d.sketch_text.stroke-94"),sQuery(id+"FHMxAyK4CFUKdhS_1.wireOp",EDGE,"1cb9c079-ea9b-4899-8069-e0e3048e911d.sketch_text.stroke-95"),sQuery(id+"FHMxAyK4CFUKdhS_1.wireOp",EDGE,"1cb9c079-ea9b-4899-8069-e0e3048e911d.sketch_text.stroke-96"),sQuery(id+"FHMxAyK4CFUKdhS_1.wireOp",EDGE,"1cb9c079-ea9b-4899-8069-e0e3048e911d.sketch_text.stroke-97"),sQuery(id+"FHMxAyK4CFUKdhS_1.wireOp",EDGE,"1cb9c079-ea9b-4899-8069-e0e3048e911d.sketch_text.stroke-103"),sQuery(id+"FHMxAyK4CFUKdhS_1.wireOp",EDGE,"1cb9c079-ea9b-4899-8069-e0e3048e911d.sketch_text.stroke-104"),sQuery(id+"FHMxAyK4CFUKdhS_1.wireOp",EDGE,"1cb9c079-ea9b-4899-8069-e0e3048e911d.sketch_text.stroke-105"),sQuery(id+"FHMxAyK4CFUKdhS_1.wireOp",EDGE,"1cb9c079-ea9b-4899-8069-e0e3048e911d.sketch_text.stroke-106"),sQuery(id+"FHMxAyK4CFUKdhS_1.wireOp",EDGE,"1cb9c079-ea9b-4899-8069-e0e3048e911d.sketch_text.stroke-107"),sQuery(id+"FHMxAyK4CFUKdhS_1.wireOp",EDGE,"1cb9c079-ea9b-4899-8069-e0e3048e911d.sketch_text.stroke-108"),sQuery(id+"FHMxAyK4CFUKdhS_1.wireOp",EDGE,"1cb9c079-ea9b-4899-8069-e0e3048e911d.sketch_text.stroke-109"),sQuery(id+"FHMxAyK4CFUKdhS_1.wireOp",EDGE,"1cb9c079-ea9b-4899-8069-e0e3048e911d.sketch_text.stroke-110"),sQuery(id+"FHMxAyK4CFUKdhS_1.wireOp",EDGE,"1cb9c079-ea9b-4899-8069-e0e3048e911d.sketch_text.stroke-111"),sQuery(id+"FHMxAyK4CFUKdhS_1.wireOp",EDGE,"1cb9c079-ea9b-4899-8069-e0e3048e911d.sketch_text.stroke-112"),sQuery(id+"FHMxAyK4CFUKdhS_1.wireOp",EDGE,"1cb9c079-ea9b-4899-8069-e0e3048e911d.sketch_text.stroke-113"),sQuery(id+"FHMxAyK4CFUKdhS_1.wireOp",EDGE,"1cb9c079-ea9b-4899-8069-e0e3048e911d.sketch_text.stroke-114"),sQuery(id+"FHMxAyK4CFUKdhS_1.wireOp",EDGE,"1cb9c079-ea9b-4899-8069-e0e3048e911d.sketch_text.stroke-115"),sQuery(id+"FHMxAyK4CFUKdhS_1.wireOp",EDGE,"1cb9c079-ea9b-4899-8069-e0e3048e911d.sketch_text.stroke-116"),sQuery(id+"FHMxAyK4CFUKdhS_1.wireOp",EDGE,"1cb9c079-ea9b-4899-8069-e0e3048e911d.sketch_text.stroke-117"),sQuery(id+"FHMxAyK4CFUKdhS_1.wireOp",EDGE,"1cb9c079-ea9b-4899-8069-e0e3048e911d.sketch_text.stroke-118"),sQuery(id+"FHMxAyK4CFUKdhS_1.wireOp",EDGE,"1cb9c079-ea9b-4899-8069-e0e3048e911d.sketch_text.stroke-119"),sQuery(id+"FHMxAyK4CFUKdhS_1.wireOp",EDGE,"1cb9c079-ea9b-4899-8069-e0e3048e911d.sketch_text.stroke-120"),sQuery(id+"FHMxAyK4CFUKdhS_1.wireOp",EDGE,"1cb9c079-ea9b-4899-8069-e0e3048e911d.sketch_text.stroke-121"),sQuery(id+"FHMxAyK4CFUKdhS_1.wireOp",EDGE,"1cb9c079-ea9b-4899-8069-e0e3048e911d.sketch_text.stroke-122"),sQuery(id+"FHMxAyK4CFUKdhS_1.wireOp",EDGE,"1cb9c079-ea9b-4899-8069-e0e3048e911d.sketch_text.stroke-123"),sQuery(id+"FHMxAyK4CFUKdhS_1.wireOp",EDGE,"1cb9c079-ea9b-4899-8069-e0e3048e911d.sketch_text.stroke-124"),sQuery(id+"FHMxAyK4CFUKdhS_1.wireOp",EDGE,"1cb9c079-ea9b-4899-8069-e0e3048e911d.sketch_text.stroke-125"),sQuery(id+"FHMxAyK4CFUKdhS_1.wireOp",EDGE,"1cb9c079-ea9b-4899-8069-e0e3048e911d.sketch_text.stroke-126"),sQuery(id+"FHMxAyK4CFUKdhS_1.wireOp",EDGE,"1cb9c079-ea9b-4899-8069-e0e3048e911d.sketch_text.stroke-127"),sQuery(id+"FHMxAyK4CFUKdhS_1.wireOp",EDGE,"1cb9c079-ea9b-4899-8069-e0e3048e911d.sketch_text.stroke-128"),sQuery(id+"FHMxAyK4CFUKdhS_1.wireOp",EDGE,"1cb9c079-ea9b-4899-8069-e0e3048e911d.sketch_text.stroke-129"),sQuery(id+"FHMxAyK4CFUKdhS_1.wireOp",EDGE,"1cb9c079-ea9b-4899-8069-e0e3048e911d.sketch_text.stroke-130"),sQuery(id+"FHMxAyK4CFUKdhS_1.wireOp",EDGE,"1cb9c079-ea9b-4899-8069-e0e3048e911d.sketch_text.stroke-131"),sQuery(id+"FHMxAyK4CFUKdhS_1.wireOp",EDGE,"1cb9c079-ea9b-4899-8069-e0e3048e911d.sketch_text.stroke-132"),sQuery(id+"FHMxAyK4CFUKdhS_1.wireOp",EDGE,"1cb9c079-ea9b-4899-8069-e0e3048e911d.sketch_text.stroke-133"),sQuery(id+"FHMxAyK4CFUKdhS_1.wireOp",EDGE,"1cb9c079-ea9b-4899-8069-e0e3048e911d.sketch_text.stroke-134"),sQuery(id+"FHMxAyK4CFUKdhS_1.wireOp",EDGE,"1cb9c079-ea9b-4899-8069-e0e3048e911d.sketch_text.stroke-135"),sQuery(id+"FHMxAyK4CFUKdhS_1.wireOp",EDGE,"1cb9c079-ea9b-4899-8069-e0e3048e911d.sketch_text.stroke-136"),sQuery(id+"FHMxAyK4CFUKdhS_1.wireOp",EDGE,"1cb9c079-ea9b-4899-8069-e0e3048e911d.sketch_text.stroke-137"),sQuery(id+"FHMxAyK4CFUKdhS_1.wireOp",EDGE,"1cb9c079-ea9b-4899-8069-e0e3048e911d.sketch_text.stroke-138"),sQuery(id+"FHMxAyK4CFUKdhS_1.wireOp",EDGE,"1cb9c079-ea9b-4899-8069-e0e3048e911d.sketch_text.stroke-139"),sQuery(id+"FHMxAyK4CFUKdhS_1.wireOp",EDGE,"1cb9c079-ea9b-4899-8069-e0e3048e911d.sketch_text.stroke-140"),sQuery(id+"FHMxAyK4CFUKdhS_1.wireOp",EDGE,"1cb9c079-ea9b-4899-8069-e0e3048e911d.sketch_text.stroke-141"),sQuery(id+"FHMxAyK4CFUKdhS_1.wireOp",EDGE,"1cb9c079-ea9b-4899-8069-e0e3048e911d.sketch_text.stroke-142"),sQuery(id+"FHMxAyK4CFUKdhS_1.wireOp",EDGE,"1cb9c079-ea9b-4899-8069-e0e3048e911d.sketch_text.stroke-143"),sQuery(id+"FHMxAyK4CFUKdhS_1.wireOp",EDGE,"1cb9c079-ea9b-4899-8069-e0e3048e911d.sketch_text.stroke-144"),sQuery(id+"FHMxAyK4CFUKdhS_1.wireOp",EDGE,"1cb9c079-ea9b-4899-8069-e0e3048e911d.sketch_text.stroke-145"),sQuery(id+"FHMxAyK4CFUKdhS_1.wireOp",EDGE,"1cb9c079-ea9b-4899-8069-e0e3048e911d.sketch_text.stroke-146"),sQuery(id+"FHMxAyK4CFUKdhS_1.wireOp",EDGE,"1cb9c079-ea9b-4899-8069-e0e3048e911d.sketch_text.stroke-147"),sQuery(id+"FHMxAyK4CFUKdhS_1.wireOp",EDGE,"1cb9c079-ea9b-4899-8069-e0e3048e911d.sketch_text.stroke-148"),sQuery(id+"FHMxAyK4CFUKdhS_1.wireOp",EDGE,"1cb9c079-ea9b-4899-8069-e0e3048e911d.sketch_text.stroke-149"),sQuery(id+"FHMxAyK4CFUKdhS_1.wireOp",EDGE,"1cb9c079-ea9b-4899-8069-e0e3048e911d.sketch_text.stroke-150"),sQuery(id+"FHMxAyK4CFUKdhS_1.wireOp",EDGE,"1cb9c079-ea9b-4899-8069-e0e3048e911d.sketch_text.stroke-151"),sQuery(id+"FHMxAyK4CFUKdhS_1.wireOp",EDGE,"1cb9c079-ea9b-4899-8069-e0e3048e911d.sketch_text.stroke-152"),sQuery(id+"FHMxAyK4CFUKdhS_1.wireOp",EDGE,"1cb9c079-ea9b-4899-8069-e0e3048e911d.sketch_text.stroke-153"),sQuery(id+"FHMxAyK4CFUKdhS_1.wireOp",EDGE,"1cb9c079-ea9b-4899-8069-e0e3048e911d.sketch_text.stroke-159"),sQuery(id+"FHMxAyK4CFUKdhS_1.wireOp",EDGE,"1cb9c079-ea9b-4899-8069-e0e3048e911d.sketch_text.stroke-160"),sQuery(id+"FHMxAyK4CFUKdhS_1.wireOp",EDGE,"1cb9c079-ea9b-4899-8069-e0e3048e911d.sketch_text.stroke-161"),sQuery(id+"FHMxAyK4CFUKdhS_1.wireOp",EDGE,"1cb9c079-ea9b-4899-8069-e0e3048e911d.sketch_text.stroke-162"),sQuery(id+"FHMxAyK4CFUKdhS_1.wireOp",EDGE,"1cb9c079-ea9b-4899-8069-e0e3048e911d.sketch_text.stroke-163"),sQuery(id+"FHMxAyK4CFUKdhS_1.wireOp",EDGE,"1cb9c079-ea9b-4899-8069-e0e3048e911d.sketch_text.stroke-164"),sQuery(id+"FHMxAyK4CFUKdhS_1.wireOp",EDGE,"1cb9c079-ea9b-4899-8069-e0e3048e911d.sketch_text.stroke-165"),sQuery(id+"FHMxAyK4CFUKdhS_1.wireOp",EDGE,"1cb9c079-ea9b-4899-8069-e0e3048e911d.sketch_text.stroke-166"),sQuery(id+"FHMxAyK4CFUKdhS_1.wireOp",EDGE,"1cb9c079-ea9b-4899-8069-e0e3048e911d.sketch_text.stroke-167"),sQuery(id+"FHMxAyK4CFUKdhS_1.wireOp",EDGE,"1cb9c079-ea9b-4899-8069-e0e3048e911d.sketch_text.stroke-168"),sQuery(id+"FHMxAyK4CFUKdhS_1.wireOp",EDGE,"1cb9c079-ea9b-4899-8069-e0e3048e911d.sketch_text.stroke-169"),sQuery(id+"FHMxAyK4CFUKdhS_1.wireOp",EDGE,"1cb9c079-ea9b-4899-8069-e0e3048e911d.sketch_text.stroke-170"),sQuery(id+"FHMxAyK4CFUKdhS_1.wireOp",EDGE,"1cb9c079-ea9b-4899-8069-e0e3048e911d.sketch_text.stroke-171"),sQuery(id+"FHMxAyK4CFUKdhS_1.wireOp",EDGE,"1cb9c079-ea9b-4899-8069-e0e3048e911d.sketch_text.stroke-172"),sQuery(id+"FHMxAyK4CFUKdhS_1.wireOp",EDGE,"1cb9c079-ea9b-4899-8069-e0e3048e911d.sketch_text.stroke-173"),sQuery(id+"FHMxAyK4CFUKdhS_1.wireOp",EDGE,"1cb9c079-ea9b-4899-8069-e0e3048e911d.sketch_text.stroke-174"),sQuery(id+"FHMxAyK4CFUKdhS_1.wireOp",EDGE,"1cb9c079-ea9b-4899-8069-e0e3048e911d.sketch_text.stroke-175"),sQuery(id+"FHMxAyK4CFUKdhS_1.wireOp",EDGE,"1cb9c079-ea9b-4899-8069-e0e3048e911d.sketch_text.stroke-176"),sQuery(id+"FHMxAyK4CFUKdhS_1.wireOp",EDGE,"1cb9c079-ea9b-4899-8069-e0e3048e911d.sketch_text.stroke-177"),sQuery(id+"FHMxAyK4CFUKdhS_1.wireOp",EDGE,"1cb9c079-ea9b-4899-8069-e0e3048e911d.sketch_text.stroke-178"),sQuery(id+"FHMxAyK4CFUKdhS_1.wireOp",EDGE,"1cb9c079-ea9b-4899-8069-e0e3048e911d.sketch_text.stroke-179"),sQuery(id+"FHMxAyK4CFUKdhS_1.wireOp",EDGE,"1cb9c079-ea9b-4899-8069-e0e3048e911d.sketch_text.stroke-180"),subQ2,sQuery(id+"F2.wireOp",EDGE,"E27")])],"isStart":true})]),OD(0.0)],"derivedFrom":makeQuery(id+"F1.opExtrude","CAP_EDGE",EDGE,{"disambiguationData":[OSD([subQ0])],"isStart":false})});}
            var Q26;
            {var subQ0=sQuery(id+"F0.wireOp",EDGE,"E0.top");var subQ1=sQuery(id+"F0.wireOp",EDGE,"E0.bottom");var subQ2=sQuery(id+"F2.wireOp",EDGE,"E27");Q26=makeQuery(id+"F3.boolean.opBoolean","SPLIT",EDGE,{"disambiguationData":[TD([makeQuery(id+"F1.opExtrude","CAP_FACE",FACE,{"disambiguationData":[OSD([subQ1,subQ0,sQuery(id+"F0.wireOp",EDGE,"E0.left"),sQuery(id+"F0.wireOp",EDGE,"E0.right")])],"isStart":false}),makeQuery(id+"F1.opExtrude","SWEPT_FACE",FACE,{"disambiguationData":[OSD([subQ0])]}),makeQuery(id+"F3.opExtrude","CAP_FACE",FACE,{"disambiguationData":[OSD([subQ1,sQuery(id+"FQ5JFwxVdaqARUP_1.wireOp",EDGE,"fcba4419-a2ee-464f-be9d-58f11bf3418b.sketch_text.stroke-0"),sQuery(id+"FQ5JFwxVdaqARUP_1.wireOp",EDGE,"fcba4419-a2ee-464f-be9d-58f11bf3418b.sketch_text.stroke-1"),sQuery(id+"FQ5JFwxVdaqARUP_1.wireOp",EDGE,"fcba4419-a2ee-464f-be9d-58f11bf3418b.sketch_text.stroke-2"),sQuery(id+"FQ5JFwxVdaqARUP_1.wireOp",EDGE,"fcba4419-a2ee-464f-be9d-58f11bf3418b.sketch_text.stroke-3"),sQuery(id+"FQ5JFwxVdaqARUP_1.wireOp",EDGE,"fcba4419-a2ee-464f-be9d-58f11bf3418b.sketch_text.stroke-4"),sQuery(id+"FQ5JFwxVdaqARUP_1.wireOp",EDGE,"fcba4419-a2ee-464f-be9d-58f11bf3418b.sketch_text.stroke-5"),sQuery(id+"FQ5JFwxVdaqARUP_1.wireOp",EDGE,"fcba4419-a2ee-464f-be9d-58f11bf3418b.sketch_text.stroke-6"),sQuery(id+"FQ5JFwxVdaqARUP_1.wireOp",EDGE,"fcba4419-a2ee-464f-be9d-58f11bf3418b.sketch_text.stroke-7"),sQuery(id+"FQ5JFwxVdaqARUP_1.wireOp",EDGE,"fcba4419-a2ee-464f-be9d-58f11bf3418b.sketch_text.stroke-8"),sQuery(id+"FQ5JFwxVdaqARUP_1.wireOp",EDGE,"fcba4419-a2ee-464f-be9d-58f11bf3418b.sketch_text.stroke-9"),sQuery(id+"FQ5JFwxVdaqARUP_1.wireOp",EDGE,"fcba4419-a2ee-464f-be9d-58f11bf3418b.sketch_text.stroke-10"),sQuery(id+"FQ5JFwxVdaqARUP_1.wireOp",EDGE,"fcba4419-a2ee-464f-be9d-58f11bf3418b.sketch_text.stroke-11"),sQuery(id+"FQ5JFwxVdaqARUP_1.wireOp",EDGE,"fcba4419-a2ee-464f-be9d-58f11bf3418b.sketch_text.stroke-12"),sQuery(id+"FQ5JFwxVdaqARUP_1.wireOp",EDGE,"fcba4419-a2ee-464f-be9d-58f11bf3418b.sketch_text.stroke-13"),sQuery(id+"FQ5JFwxVdaqARUP_1.wireOp",EDGE,"fcba4419-a2ee-464f-be9d-58f11bf3418b.sketch_text.stroke-14"),sQuery(id+"FQ5JFwxVdaqARUP_1.wireOp",EDGE,"fcba4419-a2ee-464f-be9d-58f11bf3418b.sketch_text.stroke-15"),sQuery(id+"FQ5JFwxVdaqARUP_1.wireOp",EDGE,"fcba4419-a2ee-464f-be9d-58f11bf3418b.sketch_text.stroke-16"),sQuery(id+"FQ5JFwxVdaqARUP_1.wireOp",EDGE,"fcba4419-a2ee-464f-be9d-58f11bf3418b.sketch_text.stroke-17"),sQuery(id+"FQ5JFwxVdaqARUP_1.wireOp",EDGE,"fcba4419-a2ee-464f-be9d-58f11bf3418b.sketch_text.stroke-18"),sQuery(id+"FQ5JFwxVdaqARUP_1.wireOp",EDGE,"fcba4419-a2ee-464f-be9d-58f11bf3418b.sketch_text.stroke-19"),sQuery(id+"FQ5JFwxVdaqARUP_1.wireOp",EDGE,"fcba4419-a2ee-464f-be9d-58f11bf3418b.sketch_text.stroke-20"),sQuery(id+"FQ5JFwxVdaqARUP_1.wireOp",EDGE,"fcba4419-a2ee-464f-be9d-58f11bf3418b.sketch_text.stroke-21"),sQuery(id+"FQ5JFwxVdaqARUP_1.wireOp",EDGE,"fcba4419-a2ee-464f-be9d-58f11bf3418b.sketch_text.stroke-22"),sQuery(id+"FQ5JFwxVdaqARUP_1.wireOp",EDGE,"fcba4419-a2ee-464f-be9d-58f11bf3418b.sketch_text.stroke-23"),sQuery(id+"FQ5JFwxVdaqARUP_1.wireOp",EDGE,"fcba4419-a2ee-464f-be9d-58f11bf3418b.sketch_text.stroke-24"),sQuery(id+"FQ5JFwxVdaqARUP_1.wireOp",EDGE,"fcba4419-a2ee-464f-be9d-58f11bf3418b.sketch_text.stroke-25"),sQuery(id+"FQ5JFwxVdaqARUP_1.wireOp",EDGE,"fcba4419-a2ee-464f-be9d-58f11bf3418b.sketch_text.stroke-26"),sQuery(id+"FQ5JFwxVdaqARUP_1.wireOp",EDGE,"fcba4419-a2ee-464f-be9d-58f11bf3418b.sketch_text.stroke-27"),sQuery(id+"FQ5JFwxVdaqARUP_1.wireOp",EDGE,"fcba4419-a2ee-464f-be9d-58f11bf3418b.sketch_text.stroke-28"),sQuery(id+"FQ5JFwxVdaqARUP_1.wireOp",EDGE,"fcba4419-a2ee-464f-be9d-58f11bf3418b.sketch_text.stroke-29"),sQuery(id+"FQ5JFwxVdaqARUP_1.wireOp",EDGE,"fcba4419-a2ee-464f-be9d-58f11bf3418b.sketch_text.stroke-30"),sQuery(id+"FQ5JFwxVdaqARUP_1.wireOp",EDGE,"fcba4419-a2ee-464f-be9d-58f11bf3418b.sketch_text.stroke-31"),sQuery(id+"FQ5JFwxVdaqARUP_1.wireOp",EDGE,"fcba4419-a2ee-464f-be9d-58f11bf3418b.sketch_text.stroke-32"),sQuery(id+"FQ5JFwxVdaqARUP_1.wireOp",EDGE,"fcba4419-a2ee-464f-be9d-58f11bf3418b.sketch_text.stroke-33"),sQuery(id+"FQ5JFwxVdaqARUP_1.wireOp",EDGE,"fcba4419-a2ee-464f-be9d-58f11bf3418b.sketch_text.stroke-34"),sQuery(id+"FQ5JFwxVdaqARUP_1.wireOp",EDGE,"fcba4419-a2ee-464f-be9d-58f11bf3418b.sketch_text.stroke-35"),sQuery(id+"FQ5JFwxVdaqARUP_1.wireOp",EDGE,"fcba4419-a2ee-464f-be9d-58f11bf3418b.sketch_text.stroke-36"),sQuery(id+"FQ5JFwxVdaqARUP_1.wireOp",EDGE,"fcba4419-a2ee-464f-be9d-58f11bf3418b.sketch_text.stroke-37"),sQuery(id+"FQ5JFwxVdaqARUP_1.wireOp",EDGE,"fcba4419-a2ee-464f-be9d-58f11bf3418b.sketch_text.stroke-38"),sQuery(id+"FQ5JFwxVdaqARUP_1.wireOp",EDGE,"fcba4419-a2ee-464f-be9d-58f11bf3418b.sketch_text.stroke-39"),sQuery(id+"FQ5JFwxVdaqARUP_1.wireOp",EDGE,"fcba4419-a2ee-464f-be9d-58f11bf3418b.sketch_text.stroke-40"),sQuery(id+"FQ5JFwxVdaqARUP_1.wireOp",EDGE,"fcba4419-a2ee-464f-be9d-58f11bf3418b.sketch_text.stroke-41"),sQuery(id+"FQ5JFwxVdaqARUP_1.wireOp",EDGE,"fcba4419-a2ee-464f-be9d-58f11bf3418b.sketch_text.stroke-42"),sQuery(id+"FQ5JFwxVdaqARUP_1.wireOp",EDGE,"fcba4419-a2ee-464f-be9d-58f11bf3418b.sketch_text.stroke-43"),sQuery(id+"FQ5JFwxVdaqARUP_1.wireOp",EDGE,"fcba4419-a2ee-464f-be9d-58f11bf3418b.sketch_text.stroke-44"),sQuery(id+"FQ5JFwxVdaqARUP_1.wireOp",EDGE,"fcba4419-a2ee-464f-be9d-58f11bf3418b.sketch_text.stroke-45"),sQuery(id+"FQ5JFwxVdaqARUP_1.wireOp",EDGE,"fcba4419-a2ee-464f-be9d-58f11bf3418b.sketch_text.stroke-46"),sQuery(id+"FQ5JFwxVdaqARUP_1.wireOp",EDGE,"fcba4419-a2ee-464f-be9d-58f11bf3418b.sketch_text.stroke-47"),sQuery(id+"FQ5JFwxVdaqARUP_1.wireOp",EDGE,"fcba4419-a2ee-464f-be9d-58f11bf3418b.sketch_text.stroke-48"),sQuery(id+"FQ5JFwxVdaqARUP_1.wireOp",EDGE,"fcba4419-a2ee-464f-be9d-58f11bf3418b.sketch_text.stroke-49"),sQuery(id+"FQ5JFwxVdaqARUP_1.wireOp",EDGE,"fcba4419-a2ee-464f-be9d-58f11bf3418b.sketch_text.stroke-50"),sQuery(id+"FQ5JFwxVdaqARUP_1.wireOp",EDGE,"fcba4419-a2ee-464f-be9d-58f11bf3418b.sketch_text.stroke-51"),sQuery(id+"FQ5JFwxVdaqARUP_1.wireOp",EDGE,"fcba4419-a2ee-464f-be9d-58f11bf3418b.sketch_text.stroke-52"),sQuery(id+"FQ5JFwxVdaqARUP_1.wireOp",EDGE,"fcba4419-a2ee-464f-be9d-58f11bf3418b.sketch_text.stroke-53"),sQuery(id+"FQ5JFwxVdaqARUP_1.wireOp",EDGE,"fcba4419-a2ee-464f-be9d-58f11bf3418b.sketch_text.stroke-54"),sQuery(id+"FQ5JFwxVdaqARUP_1.wireOp",EDGE,"fcba4419-a2ee-464f-be9d-58f11bf3418b.sketch_text.stroke-55"),sQuery(id+"FQ5JFwxVdaqARUP_1.wireOp",EDGE,"fcba4419-a2ee-464f-be9d-58f11bf3418b.sketch_text.stroke-56"),sQuery(id+"FQ5JFwxVdaqARUP_1.wireOp",EDGE,"fcba4419-a2ee-464f-be9d-58f11bf3418b.sketch_text.stroke-57"),sQuery(id+"FQ5JFwxVdaqARUP_1.wireOp",EDGE,"fcba4419-a2ee-464f-be9d-58f11bf3418b.sketch_text.stroke-58"),sQuery(id+"FQ5JFwxVdaqARUP_1.wireOp",EDGE,"fcba4419-a2ee-464f-be9d-58f11bf3418b.sketch_text.stroke-59"),sQuery(id+"FQ5JFwxVdaqARUP_1.wireOp",EDGE,"fcba4419-a2ee-464f-be9d-58f11bf3418b.sketch_text.stroke-60"),sQuery(id+"FQ5JFwxVdaqARUP_1.wireOp",EDGE,"fcba4419-a2ee-464f-be9d-58f11bf3418b.sketch_text.stroke-61"),sQuery(id+"FQ5JFwxVdaqARUP_1.wireOp",EDGE,"fcba4419-a2ee-464f-be9d-58f11bf3418b.sketch_text.stroke-62"),sQuery(id+"FQ5JFwxVdaqARUP_1.wireOp",EDGE,"fcba4419-a2ee-464f-be9d-58f11bf3418b.sketch_text.stroke-63"),sQuery(id+"FQ5JFwxVdaqARUP_1.wireOp",EDGE,"fcba4419-a2ee-464f-be9d-58f11bf3418b.sketch_text.stroke-64"),sQuery(id+"FQ5JFwxVdaqARUP_1.wireOp",EDGE,"fcba4419-a2ee-464f-be9d-58f11bf3418b.sketch_text.stroke-65"),sQuery(id+"FQ5JFwxVdaqARUP_1.wireOp",EDGE,"fcba4419-a2ee-464f-be9d-58f11bf3418b.sketch_text.stroke-66"),sQuery(id+"FQ5JFwxVdaqARUP_1.wireOp",EDGE,"fcba4419-a2ee-464f-be9d-58f11bf3418b.sketch_text.stroke-67"),sQuery(id+"FQ5JFwxVdaqARUP_1.wireOp",EDGE,"fcba4419-a2ee-464f-be9d-58f11bf3418b.sketch_text.stroke-68"),sQuery(id+"FQ5JFwxVdaqARUP_1.wireOp",EDGE,"fcba4419-a2ee-464f-be9d-58f11bf3418b.sketch_text.stroke-69"),sQuery(id+"FQ5JFwxVdaqARUP_1.wireOp",EDGE,"fcba4419-a2ee-464f-be9d-58f11bf3418b.sketch_text.stroke-70"),sQuery(id+"FQ5JFwxVdaqARUP_1.wireOp",EDGE,"fcba4419-a2ee-464f-be9d-58f11bf3418b.sketch_text.stroke-71"),sQuery(id+"FQ5JFwxVdaqARUP_1.wireOp",EDGE,"fcba4419-a2ee-464f-be9d-58f11bf3418b.sketch_text.stroke-72"),sQuery(id+"FQ5JFwxVdaqARUP_1.wireOp",EDGE,"fcba4419-a2ee-464f-be9d-58f11bf3418b.sketch_text.stroke-73"),sQuery(id+"FQ5JFwxVdaqARUP_1.wireOp",EDGE,"fcba4419-a2ee-464f-be9d-58f11bf3418b.sketch_text.stroke-74"),sQuery(id+"FQ5JFwxVdaqARUP_1.wireOp",EDGE,"fcba4419-a2ee-464f-be9d-58f11bf3418b.sketch_text.stroke-75"),sQuery(id+"FQ5JFwxVdaqARUP_1.wireOp",EDGE,"fcba4419-a2ee-464f-be9d-58f11bf3418b.sketch_text.stroke-76"),sQuery(id+"FQ5JFwxVdaqARUP_1.wireOp",EDGE,"fcba4419-a2ee-464f-be9d-58f11bf3418b.sketch_text.stroke-77"),sQuery(id+"FQ5JFwxVdaqARUP_1.wireOp",EDGE,"fcba4419-a2ee-464f-be9d-58f11bf3418b.sketch_text.stroke-78"),sQuery(id+"FQ5JFwxVdaqARUP_1.wireOp",EDGE,"fcba4419-a2ee-464f-be9d-58f11bf3418b.sketch_text.stroke-79"),sQuery(id+"FQ5JFwxVdaqARUP_1.wireOp",EDGE,"fcba4419-a2ee-464f-be9d-58f11bf3418b.sketch_text.stroke-80"),sQuery(id+"FQ5JFwxVdaqARUP_1.wireOp",EDGE,"fcba4419-a2ee-464f-be9d-58f11bf3418b.sketch_text.stroke-81"),sQuery(id+"FQ5JFwxVdaqARUP_1.wireOp",EDGE,"fcba4419-a2ee-464f-be9d-58f11bf3418b.sketch_text.stroke-82"),sQuery(id+"FQ5JFwxVdaqARUP_1.wireOp",EDGE,"fcba4419-a2ee-464f-be9d-58f11bf3418b.sketch_text.stroke-83"),sQuery(id+"FQ5JFwxVdaqARUP_1.wireOp",EDGE,"fcba4419-a2ee-464f-be9d-58f11bf3418b.sketch_text.stroke-84"),sQuery(id+"FQ5JFwxVdaqARUP_1.wireOp",EDGE,"fcba4419-a2ee-464f-be9d-58f11bf3418b.sketch_text.stroke-85"),sQuery(id+"FQ5JFwxVdaqARUP_1.wireOp",EDGE,"fcba4419-a2ee-464f-be9d-58f11bf3418b.sketch_text.stroke-86"),sQuery(id+"FQ5JFwxVdaqARUP_1.wireOp",EDGE,"fcba4419-a2ee-464f-be9d-58f11bf3418b.sketch_text.stroke-87"),sQuery(id+"FQ5JFwxVdaqARUP_1.wireOp",EDGE,"fcba4419-a2ee-464f-be9d-58f11bf3418b.sketch_text.stroke-88"),sQuery(id+"FQ5JFwxVdaqARUP_1.wireOp",EDGE,"fcba4419-a2ee-464f-be9d-58f11bf3418b.sketch_text.stroke-89"),sQuery(id+"FQ5JFwxVdaqARUP_1.wireOp",EDGE,"fcba4419-a2ee-464f-be9d-58f11bf3418b.sketch_text.stroke-90"),sQuery(id+"FQ5JFwxVdaqARUP_1.wireOp",EDGE,"fcba4419-a2ee-464f-be9d-58f11bf3418b.sketch_text.stroke-91"),sQuery(id+"FQ5JFwxVdaqARUP_1.wireOp",EDGE,"fcba4419-a2ee-464f-be9d-58f11bf3418b.sketch_text.stroke-92"),sQuery(id+"FQ5JFwxVdaqARUP_1.wireOp",EDGE,"fcba4419-a2ee-464f-be9d-58f11bf3418b.sketch_text.stroke-93"),sQuery(id+"FQ5JFwxVdaqARUP_1.wireOp",EDGE,"fcba4419-a2ee-464f-be9d-58f11bf3418b.sketch_text.stroke-94"),sQuery(id+"FQ5JFwxVdaqARUP_1.wireOp",EDGE,"fcba4419-a2ee-464f-be9d-58f11bf3418b.sketch_text.stroke-95"),sQuery(id+"FQ5JFwxVdaqARUP_1.wireOp",EDGE,"fcba4419-a2ee-464f-be9d-58f11bf3418b.sketch_text.stroke-96"),sQuery(id+"FQ5JFwxVdaqARUP_1.wireOp",EDGE,"fcba4419-a2ee-464f-be9d-58f11bf3418b.sketch_text.stroke-97"),sQuery(id+"FQ5JFwxVdaqARUP_1.wireOp",EDGE,"fcba4419-a2ee-464f-be9d-58f11bf3418b.sketch_text.stroke-98"),sQuery(id+"FQ5JFwxVdaqARUP_1.wireOp",EDGE,"fcba4419-a2ee-464f-be9d-58f11bf3418b.sketch_text.stroke-99"),sQuery(id+"FQ5JFwxVdaqARUP_1.wireOp",EDGE,"fcba4419-a2ee-464f-be9d-58f11bf3418b.sketch_text.stroke-100"),sQuery(id+"FQ5JFwxVdaqARUP_1.wireOp",EDGE,"fcba4419-a2ee-464f-be9d-58f11bf3418b.sketch_text.stroke-101"),sQuery(id+"FQ5JFwxVdaqARUP_1.wireOp",EDGE,"fcba4419-a2ee-464f-be9d-58f11bf3418b.sketch_text.stroke-102"),sQuery(id+"FQ5JFwxVdaqARUP_1.wireOp",EDGE,"fcba4419-a2ee-464f-be9d-58f11bf3418b.sketch_text.stroke-103"),sQuery(id+"FQ5JFwxVdaqARUP_1.wireOp",EDGE,"fcba4419-a2ee-464f-be9d-58f11bf3418b.sketch_text.stroke-104"),sQuery(id+"FQ5JFwxVdaqARUP_1.wireOp",EDGE,"fcba4419-a2ee-464f-be9d-58f11bf3418b.sketch_text.stroke-105"),sQuery(id+"FQ5JFwxVdaqARUP_1.wireOp",EDGE,"fcba4419-a2ee-464f-be9d-58f11bf3418b.sketch_text.stroke-106"),sQuery(id+"FQ5JFwxVdaqARUP_1.wireOp",EDGE,"fcba4419-a2ee-464f-be9d-58f11bf3418b.sketch_text.stroke-107"),sQuery(id+"FQ5JFwxVdaqARUP_1.wireOp",EDGE,"fcba4419-a2ee-464f-be9d-58f11bf3418b.sketch_text.stroke-108"),sQuery(id+"FQ5JFwxVdaqARUP_1.wireOp",EDGE,"fcba4419-a2ee-464f-be9d-58f11bf3418b.sketch_text.stroke-109"),sQuery(id+"FQ5JFwxVdaqARUP_1.wireOp",EDGE,"fcba4419-a2ee-464f-be9d-58f11bf3418b.sketch_text.stroke-110"),sQuery(id+"FQ5JFwxVdaqARUP_1.wireOp",EDGE,"fcba4419-a2ee-464f-be9d-58f11bf3418b.sketch_text.stroke-111"),sQuery(id+"FQ5JFwxVdaqARUP_1.wireOp",EDGE,"fcba4419-a2ee-464f-be9d-58f11bf3418b.sketch_text.stroke-112"),sQuery(id+"FQ5JFwxVdaqARUP_1.wireOp",EDGE,"fcba4419-a2ee-464f-be9d-58f11bf3418b.sketch_text.stroke-113"),sQuery(id+"FQ5JFwxVdaqARUP_1.wireOp",EDGE,"fcba4419-a2ee-464f-be9d-58f11bf3418b.sketch_text.stroke-114"),sQuery(id+"FQ5JFwxVdaqARUP_1.wireOp",EDGE,"fcba4419-a2ee-464f-be9d-58f11bf3418b.sketch_text.stroke-115"),sQuery(id+"FQ5JFwxVdaqARUP_1.wireOp",EDGE,"fcba4419-a2ee-464f-be9d-58f11bf3418b.sketch_text.stroke-116"),sQuery(id+"FQ5JFwxVdaqARUP_1.wireOp",EDGE,"fcba4419-a2ee-464f-be9d-58f11bf3418b.sketch_text.stroke-117"),sQuery(id+"FQ5JFwxVdaqARUP_1.wireOp",EDGE,"fcba4419-a2ee-464f-be9d-58f11bf3418b.sketch_text.stroke-118"),sQuery(id+"FQ5JFwxVdaqARUP_1.wireOp",EDGE,"fcba4419-a2ee-464f-be9d-58f11bf3418b.sketch_text.stroke-119"),sQuery(id+"FQ5JFwxVdaqARUP_1.wireOp",EDGE,"fcba4419-a2ee-464f-be9d-58f11bf3418b.sketch_text.stroke-120"),sQuery(id+"FQ5JFwxVdaqARUP_1.wireOp",EDGE,"fcba4419-a2ee-464f-be9d-58f11bf3418b.sketch_text.stroke-121"),sQuery(id+"FQ5JFwxVdaqARUP_1.wireOp",EDGE,"fcba4419-a2ee-464f-be9d-58f11bf3418b.sketch_text.stroke-122"),sQuery(id+"FQ5JFwxVdaqARUP_1.wireOp",EDGE,"fcba4419-a2ee-464f-be9d-58f11bf3418b.sketch_text.stroke-123"),sQuery(id+"FQ5JFwxVdaqARUP_1.wireOp",EDGE,"fcba4419-a2ee-464f-be9d-58f11bf3418b.sketch_text.stroke-124"),sQuery(id+"FQ5JFwxVdaqARUP_1.wireOp",EDGE,"fcba4419-a2ee-464f-be9d-58f11bf3418b.sketch_text.stroke-125"),sQuery(id+"FQ5JFwxVdaqARUP_1.wireOp",EDGE,"fcba4419-a2ee-464f-be9d-58f11bf3418b.sketch_text.stroke-126"),sQuery(id+"FQ5JFwxVdaqARUP_1.wireOp",EDGE,"fcba4419-a2ee-464f-be9d-58f11bf3418b.sketch_text.stroke-127"),sQuery(id+"FQ5JFwxVdaqARUP_1.wireOp",EDGE,"fcba4419-a2ee-464f-be9d-58f11bf3418b.sketch_text.stroke-128"),sQuery(id+"FQ5JFwxVdaqARUP_1.wireOp",EDGE,"fcba4419-a2ee-464f-be9d-58f11bf3418b.sketch_text.stroke-129"),sQuery(id+"FQ5JFwxVdaqARUP_1.wireOp",EDGE,"fcba4419-a2ee-464f-be9d-58f11bf3418b.sketch_text.stroke-130"),sQuery(id+"FQ5JFwxVdaqARUP_1.wireOp",EDGE,"fcba4419-a2ee-464f-be9d-58f11bf3418b.sketch_text.stroke-131"),sQuery(id+"FQ5JFwxVdaqARUP_1.wireOp",EDGE,"fcba4419-a2ee-464f-be9d-58f11bf3418b.sketch_text.stroke-132"),sQuery(id+"FQ5JFwxVdaqARUP_1.wireOp",EDGE,"fcba4419-a2ee-464f-be9d-58f11bf3418b.sketch_text.stroke-133"),sQuery(id+"FQ5JFwxVdaqARUP_1.wireOp",EDGE,"fcba4419-a2ee-464f-be9d-58f11bf3418b.sketch_text.stroke-134"),sQuery(id+"FQ5JFwxVdaqARUP_1.wireOp",EDGE,"fcba4419-a2ee-464f-be9d-58f11bf3418b.sketch_text.stroke-135"),sQuery(id+"FQ5JFwxVdaqARUP_1.wireOp",EDGE,"fcba4419-a2ee-464f-be9d-58f11bf3418b.sketch_text.stroke-136"),sQuery(id+"FQ5JFwxVdaqARUP_1.wireOp",EDGE,"fcba4419-a2ee-464f-be9d-58f11bf3418b.sketch_text.stroke-137"),sQuery(id+"FQ5JFwxVdaqARUP_1.wireOp",EDGE,"fcba4419-a2ee-464f-be9d-58f11bf3418b.sketch_text.stroke-138"),sQuery(id+"FQ5JFwxVdaqARUP_1.wireOp",EDGE,"fcba4419-a2ee-464f-be9d-58f11bf3418b.sketch_text.stroke-139"),sQuery(id+"FQ5JFwxVdaqARUP_1.wireOp",EDGE,"fcba4419-a2ee-464f-be9d-58f11bf3418b.sketch_text.stroke-140"),sQuery(id+"FQ5JFwxVdaqARUP_1.wireOp",EDGE,"fcba4419-a2ee-464f-be9d-58f11bf3418b.sketch_text.stroke-141"),sQuery(id+"FQ5JFwxVdaqARUP_1.wireOp",EDGE,"fcba4419-a2ee-464f-be9d-58f11bf3418b.sketch_text.stroke-142"),sQuery(id+"FQ5JFwxVdaqARUP_1.wireOp",EDGE,"fcba4419-a2ee-464f-be9d-58f11bf3418b.sketch_text.stroke-143"),sQuery(id+"FQ5JFwxVdaqARUP_1.wireOp",EDGE,"fcba4419-a2ee-464f-be9d-58f11bf3418b.sketch_text.stroke-144"),sQuery(id+"FQ5JFwxVdaqARUP_1.wireOp",EDGE,"fcba4419-a2ee-464f-be9d-58f11bf3418b.sketch_text.stroke-145"),sQuery(id+"FQ5JFwxVdaqARUP_1.wireOp",EDGE,"fcba4419-a2ee-464f-be9d-58f11bf3418b.sketch_text.stroke-146"),sQuery(id+"FQ5JFwxVdaqARUP_1.wireOp",EDGE,"fcba4419-a2ee-464f-be9d-58f11bf3418b.sketch_text.stroke-147"),sQuery(id+"FQ5JFwxVdaqARUP_1.wireOp",EDGE,"fcba4419-a2ee-464f-be9d-58f11bf3418b.sketch_text.stroke-148"),sQuery(id+"FQ5JFwxVdaqARUP_1.wireOp",EDGE,"fcba4419-a2ee-464f-be9d-58f11bf3418b.sketch_text.stroke-149"),sQuery(id+"FQ5JFwxVdaqARUP_1.wireOp",EDGE,"fcba4419-a2ee-464f-be9d-58f11bf3418b.sketch_text.stroke-150"),sQuery(id+"FQ5JFwxVdaqARUP_1.wireOp",EDGE,"fcba4419-a2ee-464f-be9d-58f11bf3418b.sketch_text.stroke-151"),sQuery(id+"FQ5JFwxVdaqARUP_1.wireOp",EDGE,"fcba4419-a2ee-464f-be9d-58f11bf3418b.sketch_text.stroke-152"),sQuery(id+"FQ5JFwxVdaqARUP_1.wireOp",EDGE,"fcba4419-a2ee-464f-be9d-58f11bf3418b.sketch_text.stroke-153"),sQuery(id+"FQ5JFwxVdaqARUP_1.wireOp",EDGE,"fcba4419-a2ee-464f-be9d-58f11bf3418b.sketch_text.stroke-154"),sQuery(id+"FQ5JFwxVdaqARUP_1.wireOp",EDGE,"fcba4419-a2ee-464f-be9d-58f11bf3418b.sketch_text.stroke-155"),sQuery(id+"FQ5JFwxVdaqARUP_1.wireOp",EDGE,"fcba4419-a2ee-464f-be9d-58f11bf3418b.sketch_text.stroke-156"),sQuery(id+"FQ5JFwxVdaqARUP_1.wireOp",EDGE,"fcba4419-a2ee-464f-be9d-58f11bf3418b.sketch_text.stroke-157"),sQuery(id+"FQ5JFwxVdaqARUP_1.wireOp",EDGE,"fcba4419-a2ee-464f-be9d-58f11bf3418b.sketch_text.stroke-158"),sQuery(id+"FQ5JFwxVdaqARUP_1.wireOp",EDGE,"fcba4419-a2ee-464f-be9d-58f11bf3418b.sketch_text.stroke-159"),sQuery(id+"FQ5JFwxVdaqARUP_1.wireOp",EDGE,"fcba4419-a2ee-464f-be9d-58f11bf3418b.sketch_text.stroke-160"),sQuery(id+"FQ5JFwxVdaqARUP_1.wireOp",EDGE,"fcba4419-a2ee-464f-be9d-58f11bf3418b.sketch_text.stroke-161"),sQuery(id+"FQ5JFwxVdaqARUP_1.wireOp",EDGE,"fcba4419-a2ee-464f-be9d-58f11bf3418b.sketch_text.stroke-162"),sQuery(id+"FQ5JFwxVdaqARUP_1.wireOp",EDGE,"fcba4419-a2ee-464f-be9d-58f11bf3418b.sketch_text.stroke-163"),sQuery(id+"FQ5JFwxVdaqARUP_1.wireOp",EDGE,"fcba4419-a2ee-464f-be9d-58f11bf3418b.sketch_text.stroke-164"),sQuery(id+"FQ5JFwxVdaqARUP_1.wireOp",EDGE,"fcba4419-a2ee-464f-be9d-58f11bf3418b.sketch_text.stroke-165"),sQuery(id+"FQ5JFwxVdaqARUP_1.wireOp",EDGE,"fcba4419-a2ee-464f-be9d-58f11bf3418b.sketch_text.stroke-166"),sQuery(id+"FQ5JFwxVdaqARUP_1.wireOp",EDGE,"fcba4419-a2ee-464f-be9d-58f11bf3418b.sketch_text.stroke-167"),sQuery(id+"FQ5JFwxVdaqARUP_1.wireOp",EDGE,"fcba4419-a2ee-464f-be9d-58f11bf3418b.sketch_text.stroke-168"),sQuery(id+"FQ5JFwxVdaqARUP_1.wireOp",EDGE,"fcba4419-a2ee-464f-be9d-58f11bf3418b.sketch_text.stroke-169"),sQuery(id+"FQ5JFwxVdaqARUP_1.wireOp",EDGE,"fcba4419-a2ee-464f-be9d-58f11bf3418b.sketch_text.stroke-170"),sQuery(id+"FQ5JFwxVdaqARUP_1.wireOp",EDGE,"fcba4419-a2ee-464f-be9d-58f11bf3418b.sketch_text.stroke-171"),sQuery(id+"FQ5JFwxVdaqARUP_1.wireOp",EDGE,"fcba4419-a2ee-464f-be9d-58f11bf3418b.sketch_text.stroke-172"),sQuery(id+"FQ5JFwxVdaqARUP_1.wireOp",EDGE,"fcba4419-a2ee-464f-be9d-58f11bf3418b.sketch_text.stroke-173"),sQuery(id+"FHMxAyK4CFUKdhS_1.wireOp",EDGE,"1cb9c079-ea9b-4899-8069-e0e3048e911d.sketch_text.stroke-0"),sQuery(id+"FHMxAyK4CFUKdhS_1.wireOp",EDGE,"1cb9c079-ea9b-4899-8069-e0e3048e911d.sketch_text.stroke-1"),sQuery(id+"FHMxAyK4CFUKdhS_1.wireOp",EDGE,"1cb9c079-ea9b-4899-8069-e0e3048e911d.sketch_text.stroke-2"),sQuery(id+"FHMxAyK4CFUKdhS_1.wireOp",EDGE,"1cb9c079-ea9b-4899-8069-e0e3048e911d.sketch_text.stroke-3"),sQuery(id+"FHMxAyK4CFUKdhS_1.wireOp",EDGE,"1cb9c079-ea9b-4899-8069-e0e3048e911d.sketch_text.stroke-4"),sQuery(id+"FHMxAyK4CFUKdhS_1.wireOp",EDGE,"1cb9c079-ea9b-4899-8069-e0e3048e911d.sketch_text.stroke-5"),sQuery(id+"FHMxAyK4CFUKdhS_1.wireOp",EDGE,"1cb9c079-ea9b-4899-8069-e0e3048e911d.sketch_text.stroke-6"),sQuery(id+"FHMxAyK4CFUKdhS_1.wireOp",EDGE,"1cb9c079-ea9b-4899-8069-e0e3048e911d.sketch_text.stroke-7"),sQuery(id+"FHMxAyK4CFUKdhS_1.wireOp",EDGE,"1cb9c079-ea9b-4899-8069-e0e3048e911d.sketch_text.stroke-8"),sQuery(id+"FHMxAyK4CFUKdhS_1.wireOp",EDGE,"1cb9c079-ea9b-4899-8069-e0e3048e911d.sketch_text.stroke-9"),sQuery(id+"FHMxAyK4CFUKdhS_1.wireOp",EDGE,"1cb9c079-ea9b-4899-8069-e0e3048e911d.sketch_text.stroke-10"),sQuery(id+"FHMxAyK4CFUKdhS_1.wireOp",EDGE,"1cb9c079-ea9b-4899-8069-e0e3048e911d.sketch_text.stroke-11"),sQuery(id+"FHMxAyK4CFUKdhS_1.wireOp",EDGE,"1cb9c079-ea9b-4899-8069-e0e3048e911d.sketch_text.stroke-12"),sQuery(id+"FHMxAyK4CFUKdhS_1.wireOp",EDGE,"1cb9c079-ea9b-4899-8069-e0e3048e911d.sketch_text.stroke-13"),sQuery(id+"FHMxAyK4CFUKdhS_1.wireOp",EDGE,"1cb9c079-ea9b-4899-8069-e0e3048e911d.sketch_text.stroke-14"),sQuery(id+"FHMxAyK4CFUKdhS_1.wireOp",EDGE,"1cb9c079-ea9b-4899-8069-e0e3048e911d.sketch_text.stroke-15"),sQuery(id+"FHMxAyK4CFUKdhS_1.wireOp",EDGE,"1cb9c079-ea9b-4899-8069-e0e3048e911d.sketch_text.stroke-16"),sQuery(id+"FHMxAyK4CFUKdhS_1.wireOp",EDGE,"1cb9c079-ea9b-4899-8069-e0e3048e911d.sketch_text.stroke-17"),sQuery(id+"FHMxAyK4CFUKdhS_1.wireOp",EDGE,"1cb9c079-ea9b-4899-8069-e0e3048e911d.sketch_text.stroke-18"),sQuery(id+"FHMxAyK4CFUKdhS_1.wireOp",EDGE,"1cb9c079-ea9b-4899-8069-e0e3048e911d.sketch_text.stroke-19"),sQuery(id+"FHMxAyK4CFUKdhS_1.wireOp",EDGE,"1cb9c079-ea9b-4899-8069-e0e3048e911d.sketch_text.stroke-20"),sQuery(id+"FHMxAyK4CFUKdhS_1.wireOp",EDGE,"1cb9c079-ea9b-4899-8069-e0e3048e911d.sketch_text.stroke-21"),sQuery(id+"FHMxAyK4CFUKdhS_1.wireOp",EDGE,"1cb9c079-ea9b-4899-8069-e0e3048e911d.sketch_text.stroke-22"),sQuery(id+"FHMxAyK4CFUKdhS_1.wireOp",EDGE,"1cb9c079-ea9b-4899-8069-e0e3048e911d.sketch_text.stroke-23"),sQuery(id+"FHMxAyK4CFUKdhS_1.wireOp",EDGE,"1cb9c079-ea9b-4899-8069-e0e3048e911d.sketch_text.stroke-24"),sQuery(id+"FHMxAyK4CFUKdhS_1.wireOp",EDGE,"1cb9c079-ea9b-4899-8069-e0e3048e911d.sketch_text.stroke-25"),sQuery(id+"FHMxAyK4CFUKdhS_1.wireOp",EDGE,"1cb9c079-ea9b-4899-8069-e0e3048e911d.sketch_text.stroke-26"),sQuery(id+"FHMxAyK4CFUKdhS_1.wireOp",EDGE,"1cb9c079-ea9b-4899-8069-e0e3048e911d.sketch_text.stroke-27"),sQuery(id+"FHMxAyK4CFUKdhS_1.wireOp",EDGE,"1cb9c079-ea9b-4899-8069-e0e3048e911d.sketch_text.stroke-28"),sQuery(id+"FHMxAyK4CFUKdhS_1.wireOp",EDGE,"1cb9c079-ea9b-4899-8069-e0e3048e911d.sketch_text.stroke-29"),sQuery(id+"FHMxAyK4CFUKdhS_1.wireOp",EDGE,"1cb9c079-ea9b-4899-8069-e0e3048e911d.sketch_text.stroke-30"),sQuery(id+"FHMxAyK4CFUKdhS_1.wireOp",EDGE,"1cb9c079-ea9b-4899-8069-e0e3048e911d.sketch_text.stroke-31"),sQuery(id+"FHMxAyK4CFUKdhS_1.wireOp",EDGE,"1cb9c079-ea9b-4899-8069-e0e3048e911d.sketch_text.stroke-32"),sQuery(id+"FHMxAyK4CFUKdhS_1.wireOp",EDGE,"1cb9c079-ea9b-4899-8069-e0e3048e911d.sketch_text.stroke-33"),sQuery(id+"FHMxAyK4CFUKdhS_1.wireOp",EDGE,"1cb9c079-ea9b-4899-8069-e0e3048e911d.sketch_text.stroke-34"),sQuery(id+"FHMxAyK4CFUKdhS_1.wireOp",EDGE,"1cb9c079-ea9b-4899-8069-e0e3048e911d.sketch_text.stroke-35"),sQuery(id+"FHMxAyK4CFUKdhS_1.wireOp",EDGE,"1cb9c079-ea9b-4899-8069-e0e3048e911d.sketch_text.stroke-36"),sQuery(id+"FHMxAyK4CFUKdhS_1.wireOp",EDGE,"1cb9c079-ea9b-4899-8069-e0e3048e911d.sketch_text.stroke-37"),sQuery(id+"FHMxAyK4CFUKdhS_1.wireOp",EDGE,"1cb9c079-ea9b-4899-8069-e0e3048e911d.sketch_text.stroke-38"),sQuery(id+"FHMxAyK4CFUKdhS_1.wireOp",EDGE,"1cb9c079-ea9b-4899-8069-e0e3048e911d.sketch_text.stroke-39"),sQuery(id+"FHMxAyK4CFUKdhS_1.wireOp",EDGE,"1cb9c079-ea9b-4899-8069-e0e3048e911d.sketch_text.stroke-40"),sQuery(id+"FHMxAyK4CFUKdhS_1.wireOp",EDGE,"1cb9c079-ea9b-4899-8069-e0e3048e911d.sketch_text.stroke-41"),sQuery(id+"FHMxAyK4CFUKdhS_1.wireOp",EDGE,"1cb9c079-ea9b-4899-8069-e0e3048e911d.sketch_text.stroke-42"),sQuery(id+"FHMxAyK4CFUKdhS_1.wireOp",EDGE,"1cb9c079-ea9b-4899-8069-e0e3048e911d.sketch_text.stroke-43"),sQuery(id+"FHMxAyK4CFUKdhS_1.wireOp",EDGE,"1cb9c079-ea9b-4899-8069-e0e3048e911d.sketch_text.stroke-44"),sQuery(id+"FHMxAyK4CFUKdhS_1.wireOp",EDGE,"1cb9c079-ea9b-4899-8069-e0e3048e911d.sketch_text.stroke-45"),sQuery(id+"FHMxAyK4CFUKdhS_1.wireOp",EDGE,"1cb9c079-ea9b-4899-8069-e0e3048e911d.sketch_text.stroke-46"),sQuery(id+"FHMxAyK4CFUKdhS_1.wireOp",EDGE,"1cb9c079-ea9b-4899-8069-e0e3048e911d.sketch_text.stroke-47"),sQuery(id+"FHMxAyK4CFUKdhS_1.wireOp",EDGE,"1cb9c079-ea9b-4899-8069-e0e3048e911d.sketch_text.stroke-48"),sQuery(id+"FHMxAyK4CFUKdhS_1.wireOp",EDGE,"1cb9c079-ea9b-4899-8069-e0e3048e911d.sketch_text.stroke-49"),sQuery(id+"FHMxAyK4CFUKdhS_1.wireOp",EDGE,"1cb9c079-ea9b-4899-8069-e0e3048e911d.sketch_text.stroke-50"),sQuery(id+"FHMxAyK4CFUKdhS_1.wireOp",EDGE,"1cb9c079-ea9b-4899-8069-e0e3048e911d.sketch_text.stroke-51"),sQuery(id+"FHMxAyK4CFUKdhS_1.wireOp",EDGE,"1cb9c079-ea9b-4899-8069-e0e3048e911d.sketch_text.stroke-52"),sQuery(id+"FHMxAyK4CFUKdhS_1.wireOp",EDGE,"1cb9c079-ea9b-4899-8069-e0e3048e911d.sketch_text.stroke-53"),sQuery(id+"FHMxAyK4CFUKdhS_1.wireOp",EDGE,"1cb9c079-ea9b-4899-8069-e0e3048e911d.sketch_text.stroke-54"),sQuery(id+"FHMxAyK4CFUKdhS_1.wireOp",EDGE,"1cb9c079-ea9b-4899-8069-e0e3048e911d.sketch_text.stroke-55"),sQuery(id+"FHMxAyK4CFUKdhS_1.wireOp",EDGE,"1cb9c079-ea9b-4899-8069-e0e3048e911d.sketch_text.stroke-56"),sQuery(id+"FHMxAyK4CFUKdhS_1.wireOp",EDGE,"1cb9c079-ea9b-4899-8069-e0e3048e911d.sketch_text.stroke-57"),sQuery(id+"FHMxAyK4CFUKdhS_1.wireOp",EDGE,"1cb9c079-ea9b-4899-8069-e0e3048e911d.sketch_text.stroke-58"),sQuery(id+"FHMxAyK4CFUKdhS_1.wireOp",EDGE,"1cb9c079-ea9b-4899-8069-e0e3048e911d.sketch_text.stroke-59"),sQuery(id+"FHMxAyK4CFUKdhS_1.wireOp",EDGE,"1cb9c079-ea9b-4899-8069-e0e3048e911d.sketch_text.stroke-60"),sQuery(id+"FHMxAyK4CFUKdhS_1.wireOp",EDGE,"1cb9c079-ea9b-4899-8069-e0e3048e911d.sketch_text.stroke-61"),sQuery(id+"FHMxAyK4CFUKdhS_1.wireOp",EDGE,"1cb9c079-ea9b-4899-8069-e0e3048e911d.sketch_text.stroke-62"),sQuery(id+"FHMxAyK4CFUKdhS_1.wireOp",EDGE,"1cb9c079-ea9b-4899-8069-e0e3048e911d.sketch_text.stroke-71"),sQuery(id+"FHMxAyK4CFUKdhS_1.wireOp",EDGE,"1cb9c079-ea9b-4899-8069-e0e3048e911d.sketch_text.stroke-72"),sQuery(id+"FHMxAyK4CFUKdhS_1.wireOp",EDGE,"1cb9c079-ea9b-4899-8069-e0e3048e911d.sketch_text.stroke-73"),sQuery(id+"FHMxAyK4CFUKdhS_1.wireOp",EDGE,"1cb9c079-ea9b-4899-8069-e0e3048e911d.sketch_text.stroke-74"),sQuery(id+"FHMxAyK4CFUKdhS_1.wireOp",EDGE,"1cb9c079-ea9b-4899-8069-e0e3048e911d.sketch_text.stroke-75"),sQuery(id+"FHMxAyK4CFUKdhS_1.wireOp",EDGE,"1cb9c079-ea9b-4899-8069-e0e3048e911d.sketch_text.stroke-76"),sQuery(id+"FHMxAyK4CFUKdhS_1.wireOp",EDGE,"1cb9c079-ea9b-4899-8069-e0e3048e911d.sketch_text.stroke-77"),sQuery(id+"FHMxAyK4CFUKdhS_1.wireOp",EDGE,"1cb9c079-ea9b-4899-8069-e0e3048e911d.sketch_text.stroke-78"),sQuery(id+"FHMxAyK4CFUKdhS_1.wireOp",EDGE,"1cb9c079-ea9b-4899-8069-e0e3048e911d.sketch_text.stroke-79"),sQuery(id+"FHMxAyK4CFUKdhS_1.wireOp",EDGE,"1cb9c079-ea9b-4899-8069-e0e3048e911d.sketch_text.stroke-80"),sQuery(id+"FHMxAyK4CFUKdhS_1.wireOp",EDGE,"1cb9c079-ea9b-4899-8069-e0e3048e911d.sketch_text.stroke-81"),sQuery(id+"FHMxAyK4CFUKdhS_1.wireOp",EDGE,"1cb9c079-ea9b-4899-8069-e0e3048e911d.sketch_text.stroke-82"),sQuery(id+"FHMxAyK4CFUKdhS_1.wireOp",EDGE,"1cb9c079-ea9b-4899-8069-e0e3048e911d.sketch_text.stroke-83"),sQuery(id+"FHMxAyK4CFUKdhS_1.wireOp",EDGE,"1cb9c079-ea9b-4899-8069-e0e3048e911d.sketch_text.stroke-84"),sQuery(id+"FHMxAyK4CFUKdhS_1.wireOp",EDGE,"1cb9c079-ea9b-4899-8069-e0e3048e911d.sketch_text.stroke-85"),sQuery(id+"FHMxAyK4CFUKdhS_1.wireOp",EDGE,"1cb9c079-ea9b-4899-8069-e0e3048e911d.sketch_text.stroke-86"),sQuery(id+"FHMxAyK4CFUKdhS_1.wireOp",EDGE,"1cb9c079-ea9b-4899-8069-e0e3048e911d.sketch_text.stroke-87"),sQuery(id+"FHMxAyK4CFUKdhS_1.wireOp",EDGE,"1cb9c079-ea9b-4899-8069-e0e3048e911d.sketch_text.stroke-88"),sQuery(id+"FHMxAyK4CFUKdhS_1.wireOp",EDGE,"1cb9c079-ea9b-4899-8069-e0e3048e911d.sketch_text.stroke-89"),sQuery(id+"FHMxAyK4CFUKdhS_1.wireOp",EDGE,"1cb9c079-ea9b-4899-8069-e0e3048e911d.sketch_text.stroke-90"),sQuery(id+"FHMxAyK4CFUKdhS_1.wireOp",EDGE,"1cb9c079-ea9b-4899-8069-e0e3048e911d.sketch_text.stroke-91"),sQuery(id+"FHMxAyK4CFUKdhS_1.wireOp",EDGE,"1cb9c079-ea9b-4899-8069-e0e3048e911d.sketch_text.stroke-92"),sQuery(id+"FHMxAyK4CFUKdhS_1.wireOp",EDGE,"1cb9c079-ea9b-4899-8069-e0e3048e911d.sketch_text.stroke-93"),sQuery(id+"FHMxAyK4CFUKdhS_1.wireOp",EDGE,"1cb9c079-ea9b-4899-8069-e0e3048e911d.sketch_text.stroke-94"),sQuery(id+"FHMxAyK4CFUKdhS_1.wireOp",EDGE,"1cb9c079-ea9b-4899-8069-e0e3048e911d.sketch_text.stroke-95"),sQuery(id+"FHMxAyK4CFUKdhS_1.wireOp",EDGE,"1cb9c079-ea9b-4899-8069-e0e3048e911d.sketch_text.stroke-96"),sQuery(id+"FHMxAyK4CFUKdhS_1.wireOp",EDGE,"1cb9c079-ea9b-4899-8069-e0e3048e911d.sketch_text.stroke-97"),sQuery(id+"FHMxAyK4CFUKdhS_1.wireOp",EDGE,"1cb9c079-ea9b-4899-8069-e0e3048e911d.sketch_text.stroke-103"),sQuery(id+"FHMxAyK4CFUKdhS_1.wireOp",EDGE,"1cb9c079-ea9b-4899-8069-e0e3048e911d.sketch_text.stroke-104"),sQuery(id+"FHMxAyK4CFUKdhS_1.wireOp",EDGE,"1cb9c079-ea9b-4899-8069-e0e3048e911d.sketch_text.stroke-105"),sQuery(id+"FHMxAyK4CFUKdhS_1.wireOp",EDGE,"1cb9c079-ea9b-4899-8069-e0e3048e911d.sketch_text.stroke-106"),sQuery(id+"FHMxAyK4CFUKdhS_1.wireOp",EDGE,"1cb9c079-ea9b-4899-8069-e0e3048e911d.sketch_text.stroke-107"),sQuery(id+"FHMxAyK4CFUKdhS_1.wireOp",EDGE,"1cb9c079-ea9b-4899-8069-e0e3048e911d.sketch_text.stroke-108"),sQuery(id+"FHMxAyK4CFUKdhS_1.wireOp",EDGE,"1cb9c079-ea9b-4899-8069-e0e3048e911d.sketch_text.stroke-109"),sQuery(id+"FHMxAyK4CFUKdhS_1.wireOp",EDGE,"1cb9c079-ea9b-4899-8069-e0e3048e911d.sketch_text.stroke-110"),sQuery(id+"FHMxAyK4CFUKdhS_1.wireOp",EDGE,"1cb9c079-ea9b-4899-8069-e0e3048e911d.sketch_text.stroke-111"),sQuery(id+"FHMxAyK4CFUKdhS_1.wireOp",EDGE,"1cb9c079-ea9b-4899-8069-e0e3048e911d.sketch_text.stroke-112"),sQuery(id+"FHMxAyK4CFUKdhS_1.wireOp",EDGE,"1cb9c079-ea9b-4899-8069-e0e3048e911d.sketch_text.stroke-113"),sQuery(id+"FHMxAyK4CFUKdhS_1.wireOp",EDGE,"1cb9c079-ea9b-4899-8069-e0e3048e911d.sketch_text.stroke-114"),sQuery(id+"FHMxAyK4CFUKdhS_1.wireOp",EDGE,"1cb9c079-ea9b-4899-8069-e0e3048e911d.sketch_text.stroke-115"),sQuery(id+"FHMxAyK4CFUKdhS_1.wireOp",EDGE,"1cb9c079-ea9b-4899-8069-e0e3048e911d.sketch_text.stroke-116"),sQuery(id+"FHMxAyK4CFUKdhS_1.wireOp",EDGE,"1cb9c079-ea9b-4899-8069-e0e3048e911d.sketch_text.stroke-117"),sQuery(id+"FHMxAyK4CFUKdhS_1.wireOp",EDGE,"1cb9c079-ea9b-4899-8069-e0e3048e911d.sketch_text.stroke-118"),sQuery(id+"FHMxAyK4CFUKdhS_1.wireOp",EDGE,"1cb9c079-ea9b-4899-8069-e0e3048e911d.sketch_text.stroke-119"),sQuery(id+"FHMxAyK4CFUKdhS_1.wireOp",EDGE,"1cb9c079-ea9b-4899-8069-e0e3048e911d.sketch_text.stroke-120"),sQuery(id+"FHMxAyK4CFUKdhS_1.wireOp",EDGE,"1cb9c079-ea9b-4899-8069-e0e3048e911d.sketch_text.stroke-121"),sQuery(id+"FHMxAyK4CFUKdhS_1.wireOp",EDGE,"1cb9c079-ea9b-4899-8069-e0e3048e911d.sketch_text.stroke-122"),sQuery(id+"FHMxAyK4CFUKdhS_1.wireOp",EDGE,"1cb9c079-ea9b-4899-8069-e0e3048e911d.sketch_text.stroke-123"),sQuery(id+"FHMxAyK4CFUKdhS_1.wireOp",EDGE,"1cb9c079-ea9b-4899-8069-e0e3048e911d.sketch_text.stroke-124"),sQuery(id+"FHMxAyK4CFUKdhS_1.wireOp",EDGE,"1cb9c079-ea9b-4899-8069-e0e3048e911d.sketch_text.stroke-125"),sQuery(id+"FHMxAyK4CFUKdhS_1.wireOp",EDGE,"1cb9c079-ea9b-4899-8069-e0e3048e911d.sketch_text.stroke-126"),sQuery(id+"FHMxAyK4CFUKdhS_1.wireOp",EDGE,"1cb9c079-ea9b-4899-8069-e0e3048e911d.sketch_text.stroke-127"),sQuery(id+"FHMxAyK4CFUKdhS_1.wireOp",EDGE,"1cb9c079-ea9b-4899-8069-e0e3048e911d.sketch_text.stroke-128"),sQuery(id+"FHMxAyK4CFUKdhS_1.wireOp",EDGE,"1cb9c079-ea9b-4899-8069-e0e3048e911d.sketch_text.stroke-129"),sQuery(id+"FHMxAyK4CFUKdhS_1.wireOp",EDGE,"1cb9c079-ea9b-4899-8069-e0e3048e911d.sketch_text.stroke-130"),sQuery(id+"FHMxAyK4CFUKdhS_1.wireOp",EDGE,"1cb9c079-ea9b-4899-8069-e0e3048e911d.sketch_text.stroke-131"),sQuery(id+"FHMxAyK4CFUKdhS_1.wireOp",EDGE,"1cb9c079-ea9b-4899-8069-e0e3048e911d.sketch_text.stroke-132"),sQuery(id+"FHMxAyK4CFUKdhS_1.wireOp",EDGE,"1cb9c079-ea9b-4899-8069-e0e3048e911d.sketch_text.stroke-133"),sQuery(id+"FHMxAyK4CFUKdhS_1.wireOp",EDGE,"1cb9c079-ea9b-4899-8069-e0e3048e911d.sketch_text.stroke-134"),sQuery(id+"FHMxAyK4CFUKdhS_1.wireOp",EDGE,"1cb9c079-ea9b-4899-8069-e0e3048e911d.sketch_text.stroke-135"),sQuery(id+"FHMxAyK4CFUKdhS_1.wireOp",EDGE,"1cb9c079-ea9b-4899-8069-e0e3048e911d.sketch_text.stroke-136"),sQuery(id+"FHMxAyK4CFUKdhS_1.wireOp",EDGE,"1cb9c079-ea9b-4899-8069-e0e3048e911d.sketch_text.stroke-137"),sQuery(id+"FHMxAyK4CFUKdhS_1.wireOp",EDGE,"1cb9c079-ea9b-4899-8069-e0e3048e911d.sketch_text.stroke-138"),sQuery(id+"FHMxAyK4CFUKdhS_1.wireOp",EDGE,"1cb9c079-ea9b-4899-8069-e0e3048e911d.sketch_text.stroke-139"),sQuery(id+"FHMxAyK4CFUKdhS_1.wireOp",EDGE,"1cb9c079-ea9b-4899-8069-e0e3048e911d.sketch_text.stroke-140"),sQuery(id+"FHMxAyK4CFUKdhS_1.wireOp",EDGE,"1cb9c079-ea9b-4899-8069-e0e3048e911d.sketch_text.stroke-141"),sQuery(id+"FHMxAyK4CFUKdhS_1.wireOp",EDGE,"1cb9c079-ea9b-4899-8069-e0e3048e911d.sketch_text.stroke-142"),sQuery(id+"FHMxAyK4CFUKdhS_1.wireOp",EDGE,"1cb9c079-ea9b-4899-8069-e0e3048e911d.sketch_text.stroke-143"),sQuery(id+"FHMxAyK4CFUKdhS_1.wireOp",EDGE,"1cb9c079-ea9b-4899-8069-e0e3048e911d.sketch_text.stroke-144"),sQuery(id+"FHMxAyK4CFUKdhS_1.wireOp",EDGE,"1cb9c079-ea9b-4899-8069-e0e3048e911d.sketch_text.stroke-145"),sQuery(id+"FHMxAyK4CFUKdhS_1.wireOp",EDGE,"1cb9c079-ea9b-4899-8069-e0e3048e911d.sketch_text.stroke-146"),sQuery(id+"FHMxAyK4CFUKdhS_1.wireOp",EDGE,"1cb9c079-ea9b-4899-8069-e0e3048e911d.sketch_text.stroke-147"),sQuery(id+"FHMxAyK4CFUKdhS_1.wireOp",EDGE,"1cb9c079-ea9b-4899-8069-e0e3048e911d.sketch_text.stroke-148"),sQuery(id+"FHMxAyK4CFUKdhS_1.wireOp",EDGE,"1cb9c079-ea9b-4899-8069-e0e3048e911d.sketch_text.stroke-149"),sQuery(id+"FHMxAyK4CFUKdhS_1.wireOp",EDGE,"1cb9c079-ea9b-4899-8069-e0e3048e911d.sketch_text.stroke-150"),sQuery(id+"FHMxAyK4CFUKdhS_1.wireOp",EDGE,"1cb9c079-ea9b-4899-8069-e0e3048e911d.sketch_text.stroke-151"),sQuery(id+"FHMxAyK4CFUKdhS_1.wireOp",EDGE,"1cb9c079-ea9b-4899-8069-e0e3048e911d.sketch_text.stroke-152"),sQuery(id+"FHMxAyK4CFUKdhS_1.wireOp",EDGE,"1cb9c079-ea9b-4899-8069-e0e3048e911d.sketch_text.stroke-153"),sQuery(id+"FHMxAyK4CFUKdhS_1.wireOp",EDGE,"1cb9c079-ea9b-4899-8069-e0e3048e911d.sketch_text.stroke-159"),sQuery(id+"FHMxAyK4CFUKdhS_1.wireOp",EDGE,"1cb9c079-ea9b-4899-8069-e0e3048e911d.sketch_text.stroke-160"),sQuery(id+"FHMxAyK4CFUKdhS_1.wireOp",EDGE,"1cb9c079-ea9b-4899-8069-e0e3048e911d.sketch_text.stroke-161"),sQuery(id+"FHMxAyK4CFUKdhS_1.wireOp",EDGE,"1cb9c079-ea9b-4899-8069-e0e3048e911d.sketch_text.stroke-162"),sQuery(id+"FHMxAyK4CFUKdhS_1.wireOp",EDGE,"1cb9c079-ea9b-4899-8069-e0e3048e911d.sketch_text.stroke-163"),sQuery(id+"FHMxAyK4CFUKdhS_1.wireOp",EDGE,"1cb9c079-ea9b-4899-8069-e0e3048e911d.sketch_text.stroke-164"),sQuery(id+"FHMxAyK4CFUKdhS_1.wireOp",EDGE,"1cb9c079-ea9b-4899-8069-e0e3048e911d.sketch_text.stroke-165"),sQuery(id+"FHMxAyK4CFUKdhS_1.wireOp",EDGE,"1cb9c079-ea9b-4899-8069-e0e3048e911d.sketch_text.stroke-166"),sQuery(id+"FHMxAyK4CFUKdhS_1.wireOp",EDGE,"1cb9c079-ea9b-4899-8069-e0e3048e911d.sketch_text.stroke-167"),sQuery(id+"FHMxAyK4CFUKdhS_1.wireOp",EDGE,"1cb9c079-ea9b-4899-8069-e0e3048e911d.sketch_text.stroke-168"),sQuery(id+"FHMxAyK4CFUKdhS_1.wireOp",EDGE,"1cb9c079-ea9b-4899-8069-e0e3048e911d.sketch_text.stroke-169"),sQuery(id+"FHMxAyK4CFUKdhS_1.wireOp",EDGE,"1cb9c079-ea9b-4899-8069-e0e3048e911d.sketch_text.stroke-170"),sQuery(id+"FHMxAyK4CFUKdhS_1.wireOp",EDGE,"1cb9c079-ea9b-4899-8069-e0e3048e911d.sketch_text.stroke-171"),sQuery(id+"FHMxAyK4CFUKdhS_1.wireOp",EDGE,"1cb9c079-ea9b-4899-8069-e0e3048e911d.sketch_text.stroke-172"),sQuery(id+"FHMxAyK4CFUKdhS_1.wireOp",EDGE,"1cb9c079-ea9b-4899-8069-e0e3048e911d.sketch_text.stroke-173"),sQuery(id+"FHMxAyK4CFUKdhS_1.wireOp",EDGE,"1cb9c079-ea9b-4899-8069-e0e3048e911d.sketch_text.stroke-174"),sQuery(id+"FHMxAyK4CFUKdhS_1.wireOp",EDGE,"1cb9c079-ea9b-4899-8069-e0e3048e911d.sketch_text.stroke-175"),sQuery(id+"FHMxAyK4CFUKdhS_1.wireOp",EDGE,"1cb9c079-ea9b-4899-8069-e0e3048e911d.sketch_text.stroke-176"),sQuery(id+"FHMxAyK4CFUKdhS_1.wireOp",EDGE,"1cb9c079-ea9b-4899-8069-e0e3048e911d.sketch_text.stroke-177"),sQuery(id+"FHMxAyK4CFUKdhS_1.wireOp",EDGE,"1cb9c079-ea9b-4899-8069-e0e3048e911d.sketch_text.stroke-178"),sQuery(id+"FHMxAyK4CFUKdhS_1.wireOp",EDGE,"1cb9c079-ea9b-4899-8069-e0e3048e911d.sketch_text.stroke-179"),sQuery(id+"FHMxAyK4CFUKdhS_1.wireOp",EDGE,"1cb9c079-ea9b-4899-8069-e0e3048e911d.sketch_text.stroke-180"),sQuery(id+"F2.wireOp",EDGE,"E26"),subQ2])],"isStart":true}),makeQuery(id+"F3.opExtrude","SWEPT_FACE",FACE,{"disambiguationData":[OSD([subQ2])]})]),OD(0.0)],"derivedFrom":makeQuery(id+"F1.opExtrude","CAP_EDGE",EDGE,{"disambiguationData":[OSD([subQ0])],"isStart":false})});}
            var Q27;
            {var subQ0=sQuery(id+"F0.wireOp",EDGE,"E0.top");var subQ1=sQuery(id+"F0.wireOp",EDGE,"E0.bottom");var subQ2=sQuery(id+"F2.wireOp",EDGE,"E27");Q27=makeQuery(id+"F3.boolean.opBoolean","SPLIT",EDGE,{"disambiguationData":[TD([makeQuery(id+"F1.opExtrude","CAP_FACE",FACE,{"disambiguationData":[OSD([subQ1,subQ0,sQuery(id+"F0.wireOp",EDGE,"E0.left"),sQuery(id+"F0.wireOp",EDGE,"E0.right")])],"isStart":false}),makeQuery(id+"F1.opExtrude","SWEPT_FACE",FACE,{"disambiguationData":[OSD([subQ0])]}),makeQuery(id+"F3.opExtrude","CAP_FACE",FACE,{"disambiguationData":[OSD([subQ1,sQuery(id+"FQ5JFwxVdaqARUP_1.wireOp",EDGE,"fcba4419-a2ee-464f-be9d-58f11bf3418b.sketch_text.stroke-0"),sQuery(id+"FQ5JFwxVdaqARUP_1.wireOp",EDGE,"fcba4419-a2ee-464f-be9d-58f11bf3418b.sketch_text.stroke-1"),sQuery(id+"FQ5JFwxVdaqARUP_1.wireOp",EDGE,"fcba4419-a2ee-464f-be9d-58f11bf3418b.sketch_text.stroke-2"),sQuery(id+"FQ5JFwxVdaqARUP_1.wireOp",EDGE,"fcba4419-a2ee-464f-be9d-58f11bf3418b.sketch_text.stroke-3"),sQuery(id+"FQ5JFwxVdaqARUP_1.wireOp",EDGE,"fcba4419-a2ee-464f-be9d-58f11bf3418b.sketch_text.stroke-4"),sQuery(id+"FQ5JFwxVdaqARUP_1.wireOp",EDGE,"fcba4419-a2ee-464f-be9d-58f11bf3418b.sketch_text.stroke-5"),sQuery(id+"FQ5JFwxVdaqARUP_1.wireOp",EDGE,"fcba4419-a2ee-464f-be9d-58f11bf3418b.sketch_text.stroke-6"),sQuery(id+"FQ5JFwxVdaqARUP_1.wireOp",EDGE,"fcba4419-a2ee-464f-be9d-58f11bf3418b.sketch_text.stroke-7"),sQuery(id+"FQ5JFwxVdaqARUP_1.wireOp",EDGE,"fcba4419-a2ee-464f-be9d-58f11bf3418b.sketch_text.stroke-8"),sQuery(id+"FQ5JFwxVdaqARUP_1.wireOp",EDGE,"fcba4419-a2ee-464f-be9d-58f11bf3418b.sketch_text.stroke-9"),sQuery(id+"FQ5JFwxVdaqARUP_1.wireOp",EDGE,"fcba4419-a2ee-464f-be9d-58f11bf3418b.sketch_text.stroke-10"),sQuery(id+"FQ5JFwxVdaqARUP_1.wireOp",EDGE,"fcba4419-a2ee-464f-be9d-58f11bf3418b.sketch_text.stroke-11"),sQuery(id+"FQ5JFwxVdaqARUP_1.wireOp",EDGE,"fcba4419-a2ee-464f-be9d-58f11bf3418b.sketch_text.stroke-12"),sQuery(id+"FQ5JFwxVdaqARUP_1.wireOp",EDGE,"fcba4419-a2ee-464f-be9d-58f11bf3418b.sketch_text.stroke-13"),sQuery(id+"FQ5JFwxVdaqARUP_1.wireOp",EDGE,"fcba4419-a2ee-464f-be9d-58f11bf3418b.sketch_text.stroke-14"),sQuery(id+"FQ5JFwxVdaqARUP_1.wireOp",EDGE,"fcba4419-a2ee-464f-be9d-58f11bf3418b.sketch_text.stroke-15"),sQuery(id+"FQ5JFwxVdaqARUP_1.wireOp",EDGE,"fcba4419-a2ee-464f-be9d-58f11bf3418b.sketch_text.stroke-16"),sQuery(id+"FQ5JFwxVdaqARUP_1.wireOp",EDGE,"fcba4419-a2ee-464f-be9d-58f11bf3418b.sketch_text.stroke-17"),sQuery(id+"FQ5JFwxVdaqARUP_1.wireOp",EDGE,"fcba4419-a2ee-464f-be9d-58f11bf3418b.sketch_text.stroke-18"),sQuery(id+"FQ5JFwxVdaqARUP_1.wireOp",EDGE,"fcba4419-a2ee-464f-be9d-58f11bf3418b.sketch_text.stroke-19"),sQuery(id+"FQ5JFwxVdaqARUP_1.wireOp",EDGE,"fcba4419-a2ee-464f-be9d-58f11bf3418b.sketch_text.stroke-20"),sQuery(id+"FQ5JFwxVdaqARUP_1.wireOp",EDGE,"fcba4419-a2ee-464f-be9d-58f11bf3418b.sketch_text.stroke-21"),sQuery(id+"FQ5JFwxVdaqARUP_1.wireOp",EDGE,"fcba4419-a2ee-464f-be9d-58f11bf3418b.sketch_text.stroke-22"),sQuery(id+"FQ5JFwxVdaqARUP_1.wireOp",EDGE,"fcba4419-a2ee-464f-be9d-58f11bf3418b.sketch_text.stroke-23"),sQuery(id+"FQ5JFwxVdaqARUP_1.wireOp",EDGE,"fcba4419-a2ee-464f-be9d-58f11bf3418b.sketch_text.stroke-24"),sQuery(id+"FQ5JFwxVdaqARUP_1.wireOp",EDGE,"fcba4419-a2ee-464f-be9d-58f11bf3418b.sketch_text.stroke-25"),sQuery(id+"FQ5JFwxVdaqARUP_1.wireOp",EDGE,"fcba4419-a2ee-464f-be9d-58f11bf3418b.sketch_text.stroke-26"),sQuery(id+"FQ5JFwxVdaqARUP_1.wireOp",EDGE,"fcba4419-a2ee-464f-be9d-58f11bf3418b.sketch_text.stroke-27"),sQuery(id+"FQ5JFwxVdaqARUP_1.wireOp",EDGE,"fcba4419-a2ee-464f-be9d-58f11bf3418b.sketch_text.stroke-28"),sQuery(id+"FQ5JFwxVdaqARUP_1.wireOp",EDGE,"fcba4419-a2ee-464f-be9d-58f11bf3418b.sketch_text.stroke-29"),sQuery(id+"FQ5JFwxVdaqARUP_1.wireOp",EDGE,"fcba4419-a2ee-464f-be9d-58f11bf3418b.sketch_text.stroke-30"),sQuery(id+"FQ5JFwxVdaqARUP_1.wireOp",EDGE,"fcba4419-a2ee-464f-be9d-58f11bf3418b.sketch_text.stroke-31"),sQuery(id+"FQ5JFwxVdaqARUP_1.wireOp",EDGE,"fcba4419-a2ee-464f-be9d-58f11bf3418b.sketch_text.stroke-32"),sQuery(id+"FQ5JFwxVdaqARUP_1.wireOp",EDGE,"fcba4419-a2ee-464f-be9d-58f11bf3418b.sketch_text.stroke-33"),sQuery(id+"FQ5JFwxVdaqARUP_1.wireOp",EDGE,"fcba4419-a2ee-464f-be9d-58f11bf3418b.sketch_text.stroke-34"),sQuery(id+"FQ5JFwxVdaqARUP_1.wireOp",EDGE,"fcba4419-a2ee-464f-be9d-58f11bf3418b.sketch_text.stroke-35"),sQuery(id+"FQ5JFwxVdaqARUP_1.wireOp",EDGE,"fcba4419-a2ee-464f-be9d-58f11bf3418b.sketch_text.stroke-36"),sQuery(id+"FQ5JFwxVdaqARUP_1.wireOp",EDGE,"fcba4419-a2ee-464f-be9d-58f11bf3418b.sketch_text.stroke-37"),sQuery(id+"FQ5JFwxVdaqARUP_1.wireOp",EDGE,"fcba4419-a2ee-464f-be9d-58f11bf3418b.sketch_text.stroke-38"),sQuery(id+"FQ5JFwxVdaqARUP_1.wireOp",EDGE,"fcba4419-a2ee-464f-be9d-58f11bf3418b.sketch_text.stroke-39"),sQuery(id+"FQ5JFwxVdaqARUP_1.wireOp",EDGE,"fcba4419-a2ee-464f-be9d-58f11bf3418b.sketch_text.stroke-40"),sQuery(id+"FQ5JFwxVdaqARUP_1.wireOp",EDGE,"fcba4419-a2ee-464f-be9d-58f11bf3418b.sketch_text.stroke-41"),sQuery(id+"FQ5JFwxVdaqARUP_1.wireOp",EDGE,"fcba4419-a2ee-464f-be9d-58f11bf3418b.sketch_text.stroke-42"),sQuery(id+"FQ5JFwxVdaqARUP_1.wireOp",EDGE,"fcba4419-a2ee-464f-be9d-58f11bf3418b.sketch_text.stroke-43"),sQuery(id+"FQ5JFwxVdaqARUP_1.wireOp",EDGE,"fcba4419-a2ee-464f-be9d-58f11bf3418b.sketch_text.stroke-44"),sQuery(id+"FQ5JFwxVdaqARUP_1.wireOp",EDGE,"fcba4419-a2ee-464f-be9d-58f11bf3418b.sketch_text.stroke-45"),sQuery(id+"FQ5JFwxVdaqARUP_1.wireOp",EDGE,"fcba4419-a2ee-464f-be9d-58f11bf3418b.sketch_text.stroke-46"),sQuery(id+"FQ5JFwxVdaqARUP_1.wireOp",EDGE,"fcba4419-a2ee-464f-be9d-58f11bf3418b.sketch_text.stroke-47"),sQuery(id+"FQ5JFwxVdaqARUP_1.wireOp",EDGE,"fcba4419-a2ee-464f-be9d-58f11bf3418b.sketch_text.stroke-48"),sQuery(id+"FQ5JFwxVdaqARUP_1.wireOp",EDGE,"fcba4419-a2ee-464f-be9d-58f11bf3418b.sketch_text.stroke-49"),sQuery(id+"FQ5JFwxVdaqARUP_1.wireOp",EDGE,"fcba4419-a2ee-464f-be9d-58f11bf3418b.sketch_text.stroke-50"),sQuery(id+"FQ5JFwxVdaqARUP_1.wireOp",EDGE,"fcba4419-a2ee-464f-be9d-58f11bf3418b.sketch_text.stroke-51"),sQuery(id+"FQ5JFwxVdaqARUP_1.wireOp",EDGE,"fcba4419-a2ee-464f-be9d-58f11bf3418b.sketch_text.stroke-52"),sQuery(id+"FQ5JFwxVdaqARUP_1.wireOp",EDGE,"fcba4419-a2ee-464f-be9d-58f11bf3418b.sketch_text.stroke-53"),sQuery(id+"FQ5JFwxVdaqARUP_1.wireOp",EDGE,"fcba4419-a2ee-464f-be9d-58f11bf3418b.sketch_text.stroke-54"),sQuery(id+"FQ5JFwxVdaqARUP_1.wireOp",EDGE,"fcba4419-a2ee-464f-be9d-58f11bf3418b.sketch_text.stroke-55"),sQuery(id+"FQ5JFwxVdaqARUP_1.wireOp",EDGE,"fcba4419-a2ee-464f-be9d-58f11bf3418b.sketch_text.stroke-56"),sQuery(id+"FQ5JFwxVdaqARUP_1.wireOp",EDGE,"fcba4419-a2ee-464f-be9d-58f11bf3418b.sketch_text.stroke-57"),sQuery(id+"FQ5JFwxVdaqARUP_1.wireOp",EDGE,"fcba4419-a2ee-464f-be9d-58f11bf3418b.sketch_text.stroke-58"),sQuery(id+"FQ5JFwxVdaqARUP_1.wireOp",EDGE,"fcba4419-a2ee-464f-be9d-58f11bf3418b.sketch_text.stroke-59"),sQuery(id+"FQ5JFwxVdaqARUP_1.wireOp",EDGE,"fcba4419-a2ee-464f-be9d-58f11bf3418b.sketch_text.stroke-60"),sQuery(id+"FQ5JFwxVdaqARUP_1.wireOp",EDGE,"fcba4419-a2ee-464f-be9d-58f11bf3418b.sketch_text.stroke-61"),sQuery(id+"FQ5JFwxVdaqARUP_1.wireOp",EDGE,"fcba4419-a2ee-464f-be9d-58f11bf3418b.sketch_text.stroke-62"),sQuery(id+"FQ5JFwxVdaqARUP_1.wireOp",EDGE,"fcba4419-a2ee-464f-be9d-58f11bf3418b.sketch_text.stroke-63"),sQuery(id+"FQ5JFwxVdaqARUP_1.wireOp",EDGE,"fcba4419-a2ee-464f-be9d-58f11bf3418b.sketch_text.stroke-64"),sQuery(id+"FQ5JFwxVdaqARUP_1.wireOp",EDGE,"fcba4419-a2ee-464f-be9d-58f11bf3418b.sketch_text.stroke-65"),sQuery(id+"FQ5JFwxVdaqARUP_1.wireOp",EDGE,"fcba4419-a2ee-464f-be9d-58f11bf3418b.sketch_text.stroke-66"),sQuery(id+"FQ5JFwxVdaqARUP_1.wireOp",EDGE,"fcba4419-a2ee-464f-be9d-58f11bf3418b.sketch_text.stroke-67"),sQuery(id+"FQ5JFwxVdaqARUP_1.wireOp",EDGE,"fcba4419-a2ee-464f-be9d-58f11bf3418b.sketch_text.stroke-68"),sQuery(id+"FQ5JFwxVdaqARUP_1.wireOp",EDGE,"fcba4419-a2ee-464f-be9d-58f11bf3418b.sketch_text.stroke-69"),sQuery(id+"FQ5JFwxVdaqARUP_1.wireOp",EDGE,"fcba4419-a2ee-464f-be9d-58f11bf3418b.sketch_text.stroke-70"),sQuery(id+"FQ5JFwxVdaqARUP_1.wireOp",EDGE,"fcba4419-a2ee-464f-be9d-58f11bf3418b.sketch_text.stroke-71"),sQuery(id+"FQ5JFwxVdaqARUP_1.wireOp",EDGE,"fcba4419-a2ee-464f-be9d-58f11bf3418b.sketch_text.stroke-72"),sQuery(id+"FQ5JFwxVdaqARUP_1.wireOp",EDGE,"fcba4419-a2ee-464f-be9d-58f11bf3418b.sketch_text.stroke-73"),sQuery(id+"FQ5JFwxVdaqARUP_1.wireOp",EDGE,"fcba4419-a2ee-464f-be9d-58f11bf3418b.sketch_text.stroke-74"),sQuery(id+"FQ5JFwxVdaqARUP_1.wireOp",EDGE,"fcba4419-a2ee-464f-be9d-58f11bf3418b.sketch_text.stroke-75"),sQuery(id+"FQ5JFwxVdaqARUP_1.wireOp",EDGE,"fcba4419-a2ee-464f-be9d-58f11bf3418b.sketch_text.stroke-76"),sQuery(id+"FQ5JFwxVdaqARUP_1.wireOp",EDGE,"fcba4419-a2ee-464f-be9d-58f11bf3418b.sketch_text.stroke-77"),sQuery(id+"FQ5JFwxVdaqARUP_1.wireOp",EDGE,"fcba4419-a2ee-464f-be9d-58f11bf3418b.sketch_text.stroke-78"),sQuery(id+"FQ5JFwxVdaqARUP_1.wireOp",EDGE,"fcba4419-a2ee-464f-be9d-58f11bf3418b.sketch_text.stroke-79"),sQuery(id+"FQ5JFwxVdaqARUP_1.wireOp",EDGE,"fcba4419-a2ee-464f-be9d-58f11bf3418b.sketch_text.stroke-80"),sQuery(id+"FQ5JFwxVdaqARUP_1.wireOp",EDGE,"fcba4419-a2ee-464f-be9d-58f11bf3418b.sketch_text.stroke-81"),sQuery(id+"FQ5JFwxVdaqARUP_1.wireOp",EDGE,"fcba4419-a2ee-464f-be9d-58f11bf3418b.sketch_text.stroke-82"),sQuery(id+"FQ5JFwxVdaqARUP_1.wireOp",EDGE,"fcba4419-a2ee-464f-be9d-58f11bf3418b.sketch_text.stroke-83"),sQuery(id+"FQ5JFwxVdaqARUP_1.wireOp",EDGE,"fcba4419-a2ee-464f-be9d-58f11bf3418b.sketch_text.stroke-84"),sQuery(id+"FQ5JFwxVdaqARUP_1.wireOp",EDGE,"fcba4419-a2ee-464f-be9d-58f11bf3418b.sketch_text.stroke-85"),sQuery(id+"FQ5JFwxVdaqARUP_1.wireOp",EDGE,"fcba4419-a2ee-464f-be9d-58f11bf3418b.sketch_text.stroke-86"),sQuery(id+"FQ5JFwxVdaqARUP_1.wireOp",EDGE,"fcba4419-a2ee-464f-be9d-58f11bf3418b.sketch_text.stroke-87"),sQuery(id+"FQ5JFwxVdaqARUP_1.wireOp",EDGE,"fcba4419-a2ee-464f-be9d-58f11bf3418b.sketch_text.stroke-88"),sQuery(id+"FQ5JFwxVdaqARUP_1.wireOp",EDGE,"fcba4419-a2ee-464f-be9d-58f11bf3418b.sketch_text.stroke-89"),sQuery(id+"FQ5JFwxVdaqARUP_1.wireOp",EDGE,"fcba4419-a2ee-464f-be9d-58f11bf3418b.sketch_text.stroke-90"),sQuery(id+"FQ5JFwxVdaqARUP_1.wireOp",EDGE,"fcba4419-a2ee-464f-be9d-58f11bf3418b.sketch_text.stroke-91"),sQuery(id+"FQ5JFwxVdaqARUP_1.wireOp",EDGE,"fcba4419-a2ee-464f-be9d-58f11bf3418b.sketch_text.stroke-92"),sQuery(id+"FQ5JFwxVdaqARUP_1.wireOp",EDGE,"fcba4419-a2ee-464f-be9d-58f11bf3418b.sketch_text.stroke-93"),sQuery(id+"FQ5JFwxVdaqARUP_1.wireOp",EDGE,"fcba4419-a2ee-464f-be9d-58f11bf3418b.sketch_text.stroke-94"),sQuery(id+"FQ5JFwxVdaqARUP_1.wireOp",EDGE,"fcba4419-a2ee-464f-be9d-58f11bf3418b.sketch_text.stroke-95"),sQuery(id+"FQ5JFwxVdaqARUP_1.wireOp",EDGE,"fcba4419-a2ee-464f-be9d-58f11bf3418b.sketch_text.stroke-96"),sQuery(id+"FQ5JFwxVdaqARUP_1.wireOp",EDGE,"fcba4419-a2ee-464f-be9d-58f11bf3418b.sketch_text.stroke-97"),sQuery(id+"FQ5JFwxVdaqARUP_1.wireOp",EDGE,"fcba4419-a2ee-464f-be9d-58f11bf3418b.sketch_text.stroke-98"),sQuery(id+"FQ5JFwxVdaqARUP_1.wireOp",EDGE,"fcba4419-a2ee-464f-be9d-58f11bf3418b.sketch_text.stroke-99"),sQuery(id+"FQ5JFwxVdaqARUP_1.wireOp",EDGE,"fcba4419-a2ee-464f-be9d-58f11bf3418b.sketch_text.stroke-100"),sQuery(id+"FQ5JFwxVdaqARUP_1.wireOp",EDGE,"fcba4419-a2ee-464f-be9d-58f11bf3418b.sketch_text.stroke-101"),sQuery(id+"FQ5JFwxVdaqARUP_1.wireOp",EDGE,"fcba4419-a2ee-464f-be9d-58f11bf3418b.sketch_text.stroke-102"),sQuery(id+"FQ5JFwxVdaqARUP_1.wireOp",EDGE,"fcba4419-a2ee-464f-be9d-58f11bf3418b.sketch_text.stroke-103"),sQuery(id+"FQ5JFwxVdaqARUP_1.wireOp",EDGE,"fcba4419-a2ee-464f-be9d-58f11bf3418b.sketch_text.stroke-104"),sQuery(id+"FQ5JFwxVdaqARUP_1.wireOp",EDGE,"fcba4419-a2ee-464f-be9d-58f11bf3418b.sketch_text.stroke-105"),sQuery(id+"FQ5JFwxVdaqARUP_1.wireOp",EDGE,"fcba4419-a2ee-464f-be9d-58f11bf3418b.sketch_text.stroke-106"),sQuery(id+"FQ5JFwxVdaqARUP_1.wireOp",EDGE,"fcba4419-a2ee-464f-be9d-58f11bf3418b.sketch_text.stroke-107"),sQuery(id+"FQ5JFwxVdaqARUP_1.wireOp",EDGE,"fcba4419-a2ee-464f-be9d-58f11bf3418b.sketch_text.stroke-108"),sQuery(id+"FQ5JFwxVdaqARUP_1.wireOp",EDGE,"fcba4419-a2ee-464f-be9d-58f11bf3418b.sketch_text.stroke-109"),sQuery(id+"FQ5JFwxVdaqARUP_1.wireOp",EDGE,"fcba4419-a2ee-464f-be9d-58f11bf3418b.sketch_text.stroke-110"),sQuery(id+"FQ5JFwxVdaqARUP_1.wireOp",EDGE,"fcba4419-a2ee-464f-be9d-58f11bf3418b.sketch_text.stroke-111"),sQuery(id+"FQ5JFwxVdaqARUP_1.wireOp",EDGE,"fcba4419-a2ee-464f-be9d-58f11bf3418b.sketch_text.stroke-112"),sQuery(id+"FQ5JFwxVdaqARUP_1.wireOp",EDGE,"fcba4419-a2ee-464f-be9d-58f11bf3418b.sketch_text.stroke-113"),sQuery(id+"FQ5JFwxVdaqARUP_1.wireOp",EDGE,"fcba4419-a2ee-464f-be9d-58f11bf3418b.sketch_text.stroke-114"),sQuery(id+"FQ5JFwxVdaqARUP_1.wireOp",EDGE,"fcba4419-a2ee-464f-be9d-58f11bf3418b.sketch_text.stroke-115"),sQuery(id+"FQ5JFwxVdaqARUP_1.wireOp",EDGE,"fcba4419-a2ee-464f-be9d-58f11bf3418b.sketch_text.stroke-116"),sQuery(id+"FQ5JFwxVdaqARUP_1.wireOp",EDGE,"fcba4419-a2ee-464f-be9d-58f11bf3418b.sketch_text.stroke-117"),sQuery(id+"FQ5JFwxVdaqARUP_1.wireOp",EDGE,"fcba4419-a2ee-464f-be9d-58f11bf3418b.sketch_text.stroke-118"),sQuery(id+"FQ5JFwxVdaqARUP_1.wireOp",EDGE,"fcba4419-a2ee-464f-be9d-58f11bf3418b.sketch_text.stroke-119"),sQuery(id+"FQ5JFwxVdaqARUP_1.wireOp",EDGE,"fcba4419-a2ee-464f-be9d-58f11bf3418b.sketch_text.stroke-120"),sQuery(id+"FQ5JFwxVdaqARUP_1.wireOp",EDGE,"fcba4419-a2ee-464f-be9d-58f11bf3418b.sketch_text.stroke-121"),sQuery(id+"FQ5JFwxVdaqARUP_1.wireOp",EDGE,"fcba4419-a2ee-464f-be9d-58f11bf3418b.sketch_text.stroke-122"),sQuery(id+"FQ5JFwxVdaqARUP_1.wireOp",EDGE,"fcba4419-a2ee-464f-be9d-58f11bf3418b.sketch_text.stroke-123"),sQuery(id+"FQ5JFwxVdaqARUP_1.wireOp",EDGE,"fcba4419-a2ee-464f-be9d-58f11bf3418b.sketch_text.stroke-124"),sQuery(id+"FQ5JFwxVdaqARUP_1.wireOp",EDGE,"fcba4419-a2ee-464f-be9d-58f11bf3418b.sketch_text.stroke-125"),sQuery(id+"FQ5JFwxVdaqARUP_1.wireOp",EDGE,"fcba4419-a2ee-464f-be9d-58f11bf3418b.sketch_text.stroke-126"),sQuery(id+"FQ5JFwxVdaqARUP_1.wireOp",EDGE,"fcba4419-a2ee-464f-be9d-58f11bf3418b.sketch_text.stroke-127"),sQuery(id+"FQ5JFwxVdaqARUP_1.wireOp",EDGE,"fcba4419-a2ee-464f-be9d-58f11bf3418b.sketch_text.stroke-128"),sQuery(id+"FQ5JFwxVdaqARUP_1.wireOp",EDGE,"fcba4419-a2ee-464f-be9d-58f11bf3418b.sketch_text.stroke-129"),sQuery(id+"FQ5JFwxVdaqARUP_1.wireOp",EDGE,"fcba4419-a2ee-464f-be9d-58f11bf3418b.sketch_text.stroke-130"),sQuery(id+"FQ5JFwxVdaqARUP_1.wireOp",EDGE,"fcba4419-a2ee-464f-be9d-58f11bf3418b.sketch_text.stroke-131"),sQuery(id+"FQ5JFwxVdaqARUP_1.wireOp",EDGE,"fcba4419-a2ee-464f-be9d-58f11bf3418b.sketch_text.stroke-132"),sQuery(id+"FQ5JFwxVdaqARUP_1.wireOp",EDGE,"fcba4419-a2ee-464f-be9d-58f11bf3418b.sketch_text.stroke-133"),sQuery(id+"FQ5JFwxVdaqARUP_1.wireOp",EDGE,"fcba4419-a2ee-464f-be9d-58f11bf3418b.sketch_text.stroke-134"),sQuery(id+"FQ5JFwxVdaqARUP_1.wireOp",EDGE,"fcba4419-a2ee-464f-be9d-58f11bf3418b.sketch_text.stroke-135"),sQuery(id+"FQ5JFwxVdaqARUP_1.wireOp",EDGE,"fcba4419-a2ee-464f-be9d-58f11bf3418b.sketch_text.stroke-136"),sQuery(id+"FQ5JFwxVdaqARUP_1.wireOp",EDGE,"fcba4419-a2ee-464f-be9d-58f11bf3418b.sketch_text.stroke-137"),sQuery(id+"FQ5JFwxVdaqARUP_1.wireOp",EDGE,"fcba4419-a2ee-464f-be9d-58f11bf3418b.sketch_text.stroke-138"),sQuery(id+"FQ5JFwxVdaqARUP_1.wireOp",EDGE,"fcba4419-a2ee-464f-be9d-58f11bf3418b.sketch_text.stroke-139"),sQuery(id+"FQ5JFwxVdaqARUP_1.wireOp",EDGE,"fcba4419-a2ee-464f-be9d-58f11bf3418b.sketch_text.stroke-140"),sQuery(id+"FQ5JFwxVdaqARUP_1.wireOp",EDGE,"fcba4419-a2ee-464f-be9d-58f11bf3418b.sketch_text.stroke-141"),sQuery(id+"FQ5JFwxVdaqARUP_1.wireOp",EDGE,"fcba4419-a2ee-464f-be9d-58f11bf3418b.sketch_text.stroke-142"),sQuery(id+"FQ5JFwxVdaqARUP_1.wireOp",EDGE,"fcba4419-a2ee-464f-be9d-58f11bf3418b.sketch_text.stroke-143"),sQuery(id+"FQ5JFwxVdaqARUP_1.wireOp",EDGE,"fcba4419-a2ee-464f-be9d-58f11bf3418b.sketch_text.stroke-144"),sQuery(id+"FQ5JFwxVdaqARUP_1.wireOp",EDGE,"fcba4419-a2ee-464f-be9d-58f11bf3418b.sketch_text.stroke-145"),sQuery(id+"FQ5JFwxVdaqARUP_1.wireOp",EDGE,"fcba4419-a2ee-464f-be9d-58f11bf3418b.sketch_text.stroke-146"),sQuery(id+"FQ5JFwxVdaqARUP_1.wireOp",EDGE,"fcba4419-a2ee-464f-be9d-58f11bf3418b.sketch_text.stroke-147"),sQuery(id+"FQ5JFwxVdaqARUP_1.wireOp",EDGE,"fcba4419-a2ee-464f-be9d-58f11bf3418b.sketch_text.stroke-148"),sQuery(id+"FQ5JFwxVdaqARUP_1.wireOp",EDGE,"fcba4419-a2ee-464f-be9d-58f11bf3418b.sketch_text.stroke-149"),sQuery(id+"FQ5JFwxVdaqARUP_1.wireOp",EDGE,"fcba4419-a2ee-464f-be9d-58f11bf3418b.sketch_text.stroke-150"),sQuery(id+"FQ5JFwxVdaqARUP_1.wireOp",EDGE,"fcba4419-a2ee-464f-be9d-58f11bf3418b.sketch_text.stroke-151"),sQuery(id+"FQ5JFwxVdaqARUP_1.wireOp",EDGE,"fcba4419-a2ee-464f-be9d-58f11bf3418b.sketch_text.stroke-152"),sQuery(id+"FQ5JFwxVdaqARUP_1.wireOp",EDGE,"fcba4419-a2ee-464f-be9d-58f11bf3418b.sketch_text.stroke-153"),sQuery(id+"FQ5JFwxVdaqARUP_1.wireOp",EDGE,"fcba4419-a2ee-464f-be9d-58f11bf3418b.sketch_text.stroke-154"),sQuery(id+"FQ5JFwxVdaqARUP_1.wireOp",EDGE,"fcba4419-a2ee-464f-be9d-58f11bf3418b.sketch_text.stroke-155"),sQuery(id+"FQ5JFwxVdaqARUP_1.wireOp",EDGE,"fcba4419-a2ee-464f-be9d-58f11bf3418b.sketch_text.stroke-156"),sQuery(id+"FQ5JFwxVdaqARUP_1.wireOp",EDGE,"fcba4419-a2ee-464f-be9d-58f11bf3418b.sketch_text.stroke-157"),sQuery(id+"FQ5JFwxVdaqARUP_1.wireOp",EDGE,"fcba4419-a2ee-464f-be9d-58f11bf3418b.sketch_text.stroke-158"),sQuery(id+"FQ5JFwxVdaqARUP_1.wireOp",EDGE,"fcba4419-a2ee-464f-be9d-58f11bf3418b.sketch_text.stroke-159"),sQuery(id+"FQ5JFwxVdaqARUP_1.wireOp",EDGE,"fcba4419-a2ee-464f-be9d-58f11bf3418b.sketch_text.stroke-160"),sQuery(id+"FQ5JFwxVdaqARUP_1.wireOp",EDGE,"fcba4419-a2ee-464f-be9d-58f11bf3418b.sketch_text.stroke-161"),sQuery(id+"FQ5JFwxVdaqARUP_1.wireOp",EDGE,"fcba4419-a2ee-464f-be9d-58f11bf3418b.sketch_text.stroke-162"),sQuery(id+"FQ5JFwxVdaqARUP_1.wireOp",EDGE,"fcba4419-a2ee-464f-be9d-58f11bf3418b.sketch_text.stroke-163"),sQuery(id+"FQ5JFwxVdaqARUP_1.wireOp",EDGE,"fcba4419-a2ee-464f-be9d-58f11bf3418b.sketch_text.stroke-164"),sQuery(id+"FQ5JFwxVdaqARUP_1.wireOp",EDGE,"fcba4419-a2ee-464f-be9d-58f11bf3418b.sketch_text.stroke-165"),sQuery(id+"FQ5JFwxVdaqARUP_1.wireOp",EDGE,"fcba4419-a2ee-464f-be9d-58f11bf3418b.sketch_text.stroke-166"),sQuery(id+"FQ5JFwxVdaqARUP_1.wireOp",EDGE,"fcba4419-a2ee-464f-be9d-58f11bf3418b.sketch_text.stroke-167"),sQuery(id+"FQ5JFwxVdaqARUP_1.wireOp",EDGE,"fcba4419-a2ee-464f-be9d-58f11bf3418b.sketch_text.stroke-168"),sQuery(id+"FQ5JFwxVdaqARUP_1.wireOp",EDGE,"fcba4419-a2ee-464f-be9d-58f11bf3418b.sketch_text.stroke-169"),sQuery(id+"FQ5JFwxVdaqARUP_1.wireOp",EDGE,"fcba4419-a2ee-464f-be9d-58f11bf3418b.sketch_text.stroke-170"),sQuery(id+"FQ5JFwxVdaqARUP_1.wireOp",EDGE,"fcba4419-a2ee-464f-be9d-58f11bf3418b.sketch_text.stroke-171"),sQuery(id+"FQ5JFwxVdaqARUP_1.wireOp",EDGE,"fcba4419-a2ee-464f-be9d-58f11bf3418b.sketch_text.stroke-172"),sQuery(id+"FQ5JFwxVdaqARUP_1.wireOp",EDGE,"fcba4419-a2ee-464f-be9d-58f11bf3418b.sketch_text.stroke-173"),sQuery(id+"FHMxAyK4CFUKdhS_1.wireOp",EDGE,"1cb9c079-ea9b-4899-8069-e0e3048e911d.sketch_text.stroke-0"),sQuery(id+"FHMxAyK4CFUKdhS_1.wireOp",EDGE,"1cb9c079-ea9b-4899-8069-e0e3048e911d.sketch_text.stroke-1"),sQuery(id+"FHMxAyK4CFUKdhS_1.wireOp",EDGE,"1cb9c079-ea9b-4899-8069-e0e3048e911d.sketch_text.stroke-2"),sQuery(id+"FHMxAyK4CFUKdhS_1.wireOp",EDGE,"1cb9c079-ea9b-4899-8069-e0e3048e911d.sketch_text.stroke-3"),sQuery(id+"FHMxAyK4CFUKdhS_1.wireOp",EDGE,"1cb9c079-ea9b-4899-8069-e0e3048e911d.sketch_text.stroke-4"),sQuery(id+"FHMxAyK4CFUKdhS_1.wireOp",EDGE,"1cb9c079-ea9b-4899-8069-e0e3048e911d.sketch_text.stroke-5"),sQuery(id+"FHMxAyK4CFUKdhS_1.wireOp",EDGE,"1cb9c079-ea9b-4899-8069-e0e3048e911d.sketch_text.stroke-6"),sQuery(id+"FHMxAyK4CFUKdhS_1.wireOp",EDGE,"1cb9c079-ea9b-4899-8069-e0e3048e911d.sketch_text.stroke-7"),sQuery(id+"FHMxAyK4CFUKdhS_1.wireOp",EDGE,"1cb9c079-ea9b-4899-8069-e0e3048e911d.sketch_text.stroke-8"),sQuery(id+"FHMxAyK4CFUKdhS_1.wireOp",EDGE,"1cb9c079-ea9b-4899-8069-e0e3048e911d.sketch_text.stroke-9"),sQuery(id+"FHMxAyK4CFUKdhS_1.wireOp",EDGE,"1cb9c079-ea9b-4899-8069-e0e3048e911d.sketch_text.stroke-10"),sQuery(id+"FHMxAyK4CFUKdhS_1.wireOp",EDGE,"1cb9c079-ea9b-4899-8069-e0e3048e911d.sketch_text.stroke-11"),sQuery(id+"FHMxAyK4CFUKdhS_1.wireOp",EDGE,"1cb9c079-ea9b-4899-8069-e0e3048e911d.sketch_text.stroke-12"),sQuery(id+"FHMxAyK4CFUKdhS_1.wireOp",EDGE,"1cb9c079-ea9b-4899-8069-e0e3048e911d.sketch_text.stroke-13"),sQuery(id+"FHMxAyK4CFUKdhS_1.wireOp",EDGE,"1cb9c079-ea9b-4899-8069-e0e3048e911d.sketch_text.stroke-14"),sQuery(id+"FHMxAyK4CFUKdhS_1.wireOp",EDGE,"1cb9c079-ea9b-4899-8069-e0e3048e911d.sketch_text.stroke-15"),sQuery(id+"FHMxAyK4CFUKdhS_1.wireOp",EDGE,"1cb9c079-ea9b-4899-8069-e0e3048e911d.sketch_text.stroke-16"),sQuery(id+"FHMxAyK4CFUKdhS_1.wireOp",EDGE,"1cb9c079-ea9b-4899-8069-e0e3048e911d.sketch_text.stroke-17"),sQuery(id+"FHMxAyK4CFUKdhS_1.wireOp",EDGE,"1cb9c079-ea9b-4899-8069-e0e3048e911d.sketch_text.stroke-18"),sQuery(id+"FHMxAyK4CFUKdhS_1.wireOp",EDGE,"1cb9c079-ea9b-4899-8069-e0e3048e911d.sketch_text.stroke-19"),sQuery(id+"FHMxAyK4CFUKdhS_1.wireOp",EDGE,"1cb9c079-ea9b-4899-8069-e0e3048e911d.sketch_text.stroke-20"),sQuery(id+"FHMxAyK4CFUKdhS_1.wireOp",EDGE,"1cb9c079-ea9b-4899-8069-e0e3048e911d.sketch_text.stroke-21"),sQuery(id+"FHMxAyK4CFUKdhS_1.wireOp",EDGE,"1cb9c079-ea9b-4899-8069-e0e3048e911d.sketch_text.stroke-22"),sQuery(id+"FHMxAyK4CFUKdhS_1.wireOp",EDGE,"1cb9c079-ea9b-4899-8069-e0e3048e911d.sketch_text.stroke-23"),sQuery(id+"FHMxAyK4CFUKdhS_1.wireOp",EDGE,"1cb9c079-ea9b-4899-8069-e0e3048e911d.sketch_text.stroke-24"),sQuery(id+"FHMxAyK4CFUKdhS_1.wireOp",EDGE,"1cb9c079-ea9b-4899-8069-e0e3048e911d.sketch_text.stroke-25"),sQuery(id+"FHMxAyK4CFUKdhS_1.wireOp",EDGE,"1cb9c079-ea9b-4899-8069-e0e3048e911d.sketch_text.stroke-26"),sQuery(id+"FHMxAyK4CFUKdhS_1.wireOp",EDGE,"1cb9c079-ea9b-4899-8069-e0e3048e911d.sketch_text.stroke-27"),sQuery(id+"FHMxAyK4CFUKdhS_1.wireOp",EDGE,"1cb9c079-ea9b-4899-8069-e0e3048e911d.sketch_text.stroke-28"),sQuery(id+"FHMxAyK4CFUKdhS_1.wireOp",EDGE,"1cb9c079-ea9b-4899-8069-e0e3048e911d.sketch_text.stroke-29"),sQuery(id+"FHMxAyK4CFUKdhS_1.wireOp",EDGE,"1cb9c079-ea9b-4899-8069-e0e3048e911d.sketch_text.stroke-30"),sQuery(id+"FHMxAyK4CFUKdhS_1.wireOp",EDGE,"1cb9c079-ea9b-4899-8069-e0e3048e911d.sketch_text.stroke-31"),sQuery(id+"FHMxAyK4CFUKdhS_1.wireOp",EDGE,"1cb9c079-ea9b-4899-8069-e0e3048e911d.sketch_text.stroke-32"),sQuery(id+"FHMxAyK4CFUKdhS_1.wireOp",EDGE,"1cb9c079-ea9b-4899-8069-e0e3048e911d.sketch_text.stroke-33"),sQuery(id+"FHMxAyK4CFUKdhS_1.wireOp",EDGE,"1cb9c079-ea9b-4899-8069-e0e3048e911d.sketch_text.stroke-34"),sQuery(id+"FHMxAyK4CFUKdhS_1.wireOp",EDGE,"1cb9c079-ea9b-4899-8069-e0e3048e911d.sketch_text.stroke-35"),sQuery(id+"FHMxAyK4CFUKdhS_1.wireOp",EDGE,"1cb9c079-ea9b-4899-8069-e0e3048e911d.sketch_text.stroke-36"),sQuery(id+"FHMxAyK4CFUKdhS_1.wireOp",EDGE,"1cb9c079-ea9b-4899-8069-e0e3048e911d.sketch_text.stroke-37"),sQuery(id+"FHMxAyK4CFUKdhS_1.wireOp",EDGE,"1cb9c079-ea9b-4899-8069-e0e3048e911d.sketch_text.stroke-38"),sQuery(id+"FHMxAyK4CFUKdhS_1.wireOp",EDGE,"1cb9c079-ea9b-4899-8069-e0e3048e911d.sketch_text.stroke-39"),sQuery(id+"FHMxAyK4CFUKdhS_1.wireOp",EDGE,"1cb9c079-ea9b-4899-8069-e0e3048e911d.sketch_text.stroke-40"),sQuery(id+"FHMxAyK4CFUKdhS_1.wireOp",EDGE,"1cb9c079-ea9b-4899-8069-e0e3048e911d.sketch_text.stroke-41"),sQuery(id+"FHMxAyK4CFUKdhS_1.wireOp",EDGE,"1cb9c079-ea9b-4899-8069-e0e3048e911d.sketch_text.stroke-42"),sQuery(id+"FHMxAyK4CFUKdhS_1.wireOp",EDGE,"1cb9c079-ea9b-4899-8069-e0e3048e911d.sketch_text.stroke-43"),sQuery(id+"FHMxAyK4CFUKdhS_1.wireOp",EDGE,"1cb9c079-ea9b-4899-8069-e0e3048e911d.sketch_text.stroke-44"),sQuery(id+"FHMxAyK4CFUKdhS_1.wireOp",EDGE,"1cb9c079-ea9b-4899-8069-e0e3048e911d.sketch_text.stroke-45"),sQuery(id+"FHMxAyK4CFUKdhS_1.wireOp",EDGE,"1cb9c079-ea9b-4899-8069-e0e3048e911d.sketch_text.stroke-46"),sQuery(id+"FHMxAyK4CFUKdhS_1.wireOp",EDGE,"1cb9c079-ea9b-4899-8069-e0e3048e911d.sketch_text.stroke-47"),sQuery(id+"FHMxAyK4CFUKdhS_1.wireOp",EDGE,"1cb9c079-ea9b-4899-8069-e0e3048e911d.sketch_text.stroke-48"),sQuery(id+"FHMxAyK4CFUKdhS_1.wireOp",EDGE,"1cb9c079-ea9b-4899-8069-e0e3048e911d.sketch_text.stroke-49"),sQuery(id+"FHMxAyK4CFUKdhS_1.wireOp",EDGE,"1cb9c079-ea9b-4899-8069-e0e3048e911d.sketch_text.stroke-50"),sQuery(id+"FHMxAyK4CFUKdhS_1.wireOp",EDGE,"1cb9c079-ea9b-4899-8069-e0e3048e911d.sketch_text.stroke-51"),sQuery(id+"FHMxAyK4CFUKdhS_1.wireOp",EDGE,"1cb9c079-ea9b-4899-8069-e0e3048e911d.sketch_text.stroke-52"),sQuery(id+"FHMxAyK4CFUKdhS_1.wireOp",EDGE,"1cb9c079-ea9b-4899-8069-e0e3048e911d.sketch_text.stroke-53"),sQuery(id+"FHMxAyK4CFUKdhS_1.wireOp",EDGE,"1cb9c079-ea9b-4899-8069-e0e3048e911d.sketch_text.stroke-54"),sQuery(id+"FHMxAyK4CFUKdhS_1.wireOp",EDGE,"1cb9c079-ea9b-4899-8069-e0e3048e911d.sketch_text.stroke-55"),sQuery(id+"FHMxAyK4CFUKdhS_1.wireOp",EDGE,"1cb9c079-ea9b-4899-8069-e0e3048e911d.sketch_text.stroke-56"),sQuery(id+"FHMxAyK4CFUKdhS_1.wireOp",EDGE,"1cb9c079-ea9b-4899-8069-e0e3048e911d.sketch_text.stroke-57"),sQuery(id+"FHMxAyK4CFUKdhS_1.wireOp",EDGE,"1cb9c079-ea9b-4899-8069-e0e3048e911d.sketch_text.stroke-58"),sQuery(id+"FHMxAyK4CFUKdhS_1.wireOp",EDGE,"1cb9c079-ea9b-4899-8069-e0e3048e911d.sketch_text.stroke-59"),sQuery(id+"FHMxAyK4CFUKdhS_1.wireOp",EDGE,"1cb9c079-ea9b-4899-8069-e0e3048e911d.sketch_text.stroke-60"),sQuery(id+"FHMxAyK4CFUKdhS_1.wireOp",EDGE,"1cb9c079-ea9b-4899-8069-e0e3048e911d.sketch_text.stroke-61"),sQuery(id+"FHMxAyK4CFUKdhS_1.wireOp",EDGE,"1cb9c079-ea9b-4899-8069-e0e3048e911d.sketch_text.stroke-62"),sQuery(id+"FHMxAyK4CFUKdhS_1.wireOp",EDGE,"1cb9c079-ea9b-4899-8069-e0e3048e911d.sketch_text.stroke-71"),sQuery(id+"FHMxAyK4CFUKdhS_1.wireOp",EDGE,"1cb9c079-ea9b-4899-8069-e0e3048e911d.sketch_text.stroke-72"),sQuery(id+"FHMxAyK4CFUKdhS_1.wireOp",EDGE,"1cb9c079-ea9b-4899-8069-e0e3048e911d.sketch_text.stroke-73"),sQuery(id+"FHMxAyK4CFUKdhS_1.wireOp",EDGE,"1cb9c079-ea9b-4899-8069-e0e3048e911d.sketch_text.stroke-74"),sQuery(id+"FHMxAyK4CFUKdhS_1.wireOp",EDGE,"1cb9c079-ea9b-4899-8069-e0e3048e911d.sketch_text.stroke-75"),sQuery(id+"FHMxAyK4CFUKdhS_1.wireOp",EDGE,"1cb9c079-ea9b-4899-8069-e0e3048e911d.sketch_text.stroke-76"),sQuery(id+"FHMxAyK4CFUKdhS_1.wireOp",EDGE,"1cb9c079-ea9b-4899-8069-e0e3048e911d.sketch_text.stroke-77"),sQuery(id+"FHMxAyK4CFUKdhS_1.wireOp",EDGE,"1cb9c079-ea9b-4899-8069-e0e3048e911d.sketch_text.stroke-78"),sQuery(id+"FHMxAyK4CFUKdhS_1.wireOp",EDGE,"1cb9c079-ea9b-4899-8069-e0e3048e911d.sketch_text.stroke-79"),sQuery(id+"FHMxAyK4CFUKdhS_1.wireOp",EDGE,"1cb9c079-ea9b-4899-8069-e0e3048e911d.sketch_text.stroke-80"),sQuery(id+"FHMxAyK4CFUKdhS_1.wireOp",EDGE,"1cb9c079-ea9b-4899-8069-e0e3048e911d.sketch_text.stroke-81"),sQuery(id+"FHMxAyK4CFUKdhS_1.wireOp",EDGE,"1cb9c079-ea9b-4899-8069-e0e3048e911d.sketch_text.stroke-82"),sQuery(id+"FHMxAyK4CFUKdhS_1.wireOp",EDGE,"1cb9c079-ea9b-4899-8069-e0e3048e911d.sketch_text.stroke-83"),sQuery(id+"FHMxAyK4CFUKdhS_1.wireOp",EDGE,"1cb9c079-ea9b-4899-8069-e0e3048e911d.sketch_text.stroke-84"),sQuery(id+"FHMxAyK4CFUKdhS_1.wireOp",EDGE,"1cb9c079-ea9b-4899-8069-e0e3048e911d.sketch_text.stroke-85"),sQuery(id+"FHMxAyK4CFUKdhS_1.wireOp",EDGE,"1cb9c079-ea9b-4899-8069-e0e3048e911d.sketch_text.stroke-86"),sQuery(id+"FHMxAyK4CFUKdhS_1.wireOp",EDGE,"1cb9c079-ea9b-4899-8069-e0e3048e911d.sketch_text.stroke-87"),sQuery(id+"FHMxAyK4CFUKdhS_1.wireOp",EDGE,"1cb9c079-ea9b-4899-8069-e0e3048e911d.sketch_text.stroke-88"),sQuery(id+"FHMxAyK4CFUKdhS_1.wireOp",EDGE,"1cb9c079-ea9b-4899-8069-e0e3048e911d.sketch_text.stroke-89"),sQuery(id+"FHMxAyK4CFUKdhS_1.wireOp",EDGE,"1cb9c079-ea9b-4899-8069-e0e3048e911d.sketch_text.stroke-90"),sQuery(id+"FHMxAyK4CFUKdhS_1.wireOp",EDGE,"1cb9c079-ea9b-4899-8069-e0e3048e911d.sketch_text.stroke-91"),sQuery(id+"FHMxAyK4CFUKdhS_1.wireOp",EDGE,"1cb9c079-ea9b-4899-8069-e0e3048e911d.sketch_text.stroke-92"),sQuery(id+"FHMxAyK4CFUKdhS_1.wireOp",EDGE,"1cb9c079-ea9b-4899-8069-e0e3048e911d.sketch_text.stroke-93"),sQuery(id+"FHMxAyK4CFUKdhS_1.wireOp",EDGE,"1cb9c079-ea9b-4899-8069-e0e3048e911d.sketch_text.stroke-94"),sQuery(id+"FHMxAyK4CFUKdhS_1.wireOp",EDGE,"1cb9c079-ea9b-4899-8069-e0e3048e911d.sketch_text.stroke-95"),sQuery(id+"FHMxAyK4CFUKdhS_1.wireOp",EDGE,"1cb9c079-ea9b-4899-8069-e0e3048e911d.sketch_text.stroke-96"),sQuery(id+"FHMxAyK4CFUKdhS_1.wireOp",EDGE,"1cb9c079-ea9b-4899-8069-e0e3048e911d.sketch_text.stroke-97"),sQuery(id+"FHMxAyK4CFUKdhS_1.wireOp",EDGE,"1cb9c079-ea9b-4899-8069-e0e3048e911d.sketch_text.stroke-103"),sQuery(id+"FHMxAyK4CFUKdhS_1.wireOp",EDGE,"1cb9c079-ea9b-4899-8069-e0e3048e911d.sketch_text.stroke-104"),sQuery(id+"FHMxAyK4CFUKdhS_1.wireOp",EDGE,"1cb9c079-ea9b-4899-8069-e0e3048e911d.sketch_text.stroke-105"),sQuery(id+"FHMxAyK4CFUKdhS_1.wireOp",EDGE,"1cb9c079-ea9b-4899-8069-e0e3048e911d.sketch_text.stroke-106"),sQuery(id+"FHMxAyK4CFUKdhS_1.wireOp",EDGE,"1cb9c079-ea9b-4899-8069-e0e3048e911d.sketch_text.stroke-107"),sQuery(id+"FHMxAyK4CFUKdhS_1.wireOp",EDGE,"1cb9c079-ea9b-4899-8069-e0e3048e911d.sketch_text.stroke-108"),sQuery(id+"FHMxAyK4CFUKdhS_1.wireOp",EDGE,"1cb9c079-ea9b-4899-8069-e0e3048e911d.sketch_text.stroke-109"),sQuery(id+"FHMxAyK4CFUKdhS_1.wireOp",EDGE,"1cb9c079-ea9b-4899-8069-e0e3048e911d.sketch_text.stroke-110"),sQuery(id+"FHMxAyK4CFUKdhS_1.wireOp",EDGE,"1cb9c079-ea9b-4899-8069-e0e3048e911d.sketch_text.stroke-111"),sQuery(id+"FHMxAyK4CFUKdhS_1.wireOp",EDGE,"1cb9c079-ea9b-4899-8069-e0e3048e911d.sketch_text.stroke-112"),sQuery(id+"FHMxAyK4CFUKdhS_1.wireOp",EDGE,"1cb9c079-ea9b-4899-8069-e0e3048e911d.sketch_text.stroke-113"),sQuery(id+"FHMxAyK4CFUKdhS_1.wireOp",EDGE,"1cb9c079-ea9b-4899-8069-e0e3048e911d.sketch_text.stroke-114"),sQuery(id+"FHMxAyK4CFUKdhS_1.wireOp",EDGE,"1cb9c079-ea9b-4899-8069-e0e3048e911d.sketch_text.stroke-115"),sQuery(id+"FHMxAyK4CFUKdhS_1.wireOp",EDGE,"1cb9c079-ea9b-4899-8069-e0e3048e911d.sketch_text.stroke-116"),sQuery(id+"FHMxAyK4CFUKdhS_1.wireOp",EDGE,"1cb9c079-ea9b-4899-8069-e0e3048e911d.sketch_text.stroke-117"),sQuery(id+"FHMxAyK4CFUKdhS_1.wireOp",EDGE,"1cb9c079-ea9b-4899-8069-e0e3048e911d.sketch_text.stroke-118"),sQuery(id+"FHMxAyK4CFUKdhS_1.wireOp",EDGE,"1cb9c079-ea9b-4899-8069-e0e3048e911d.sketch_text.stroke-119"),sQuery(id+"FHMxAyK4CFUKdhS_1.wireOp",EDGE,"1cb9c079-ea9b-4899-8069-e0e3048e911d.sketch_text.stroke-120"),sQuery(id+"FHMxAyK4CFUKdhS_1.wireOp",EDGE,"1cb9c079-ea9b-4899-8069-e0e3048e911d.sketch_text.stroke-121"),sQuery(id+"FHMxAyK4CFUKdhS_1.wireOp",EDGE,"1cb9c079-ea9b-4899-8069-e0e3048e911d.sketch_text.stroke-122"),sQuery(id+"FHMxAyK4CFUKdhS_1.wireOp",EDGE,"1cb9c079-ea9b-4899-8069-e0e3048e911d.sketch_text.stroke-123"),sQuery(id+"FHMxAyK4CFUKdhS_1.wireOp",EDGE,"1cb9c079-ea9b-4899-8069-e0e3048e911d.sketch_text.stroke-124"),sQuery(id+"FHMxAyK4CFUKdhS_1.wireOp",EDGE,"1cb9c079-ea9b-4899-8069-e0e3048e911d.sketch_text.stroke-125"),sQuery(id+"FHMxAyK4CFUKdhS_1.wireOp",EDGE,"1cb9c079-ea9b-4899-8069-e0e3048e911d.sketch_text.stroke-126"),sQuery(id+"FHMxAyK4CFUKdhS_1.wireOp",EDGE,"1cb9c079-ea9b-4899-8069-e0e3048e911d.sketch_text.stroke-127"),sQuery(id+"FHMxAyK4CFUKdhS_1.wireOp",EDGE,"1cb9c079-ea9b-4899-8069-e0e3048e911d.sketch_text.stroke-128"),sQuery(id+"FHMxAyK4CFUKdhS_1.wireOp",EDGE,"1cb9c079-ea9b-4899-8069-e0e3048e911d.sketch_text.stroke-129"),sQuery(id+"FHMxAyK4CFUKdhS_1.wireOp",EDGE,"1cb9c079-ea9b-4899-8069-e0e3048e911d.sketch_text.stroke-130"),sQuery(id+"FHMxAyK4CFUKdhS_1.wireOp",EDGE,"1cb9c079-ea9b-4899-8069-e0e3048e911d.sketch_text.stroke-131"),sQuery(id+"FHMxAyK4CFUKdhS_1.wireOp",EDGE,"1cb9c079-ea9b-4899-8069-e0e3048e911d.sketch_text.stroke-132"),sQuery(id+"FHMxAyK4CFUKdhS_1.wireOp",EDGE,"1cb9c079-ea9b-4899-8069-e0e3048e911d.sketch_text.stroke-133"),sQuery(id+"FHMxAyK4CFUKdhS_1.wireOp",EDGE,"1cb9c079-ea9b-4899-8069-e0e3048e911d.sketch_text.stroke-134"),sQuery(id+"FHMxAyK4CFUKdhS_1.wireOp",EDGE,"1cb9c079-ea9b-4899-8069-e0e3048e911d.sketch_text.stroke-135"),sQuery(id+"FHMxAyK4CFUKdhS_1.wireOp",EDGE,"1cb9c079-ea9b-4899-8069-e0e3048e911d.sketch_text.stroke-136"),sQuery(id+"FHMxAyK4CFUKdhS_1.wireOp",EDGE,"1cb9c079-ea9b-4899-8069-e0e3048e911d.sketch_text.stroke-137"),sQuery(id+"FHMxAyK4CFUKdhS_1.wireOp",EDGE,"1cb9c079-ea9b-4899-8069-e0e3048e911d.sketch_text.stroke-138"),sQuery(id+"FHMxAyK4CFUKdhS_1.wireOp",EDGE,"1cb9c079-ea9b-4899-8069-e0e3048e911d.sketch_text.stroke-139"),sQuery(id+"FHMxAyK4CFUKdhS_1.wireOp",EDGE,"1cb9c079-ea9b-4899-8069-e0e3048e911d.sketch_text.stroke-140"),sQuery(id+"FHMxAyK4CFUKdhS_1.wireOp",EDGE,"1cb9c079-ea9b-4899-8069-e0e3048e911d.sketch_text.stroke-141"),sQuery(id+"FHMxAyK4CFUKdhS_1.wireOp",EDGE,"1cb9c079-ea9b-4899-8069-e0e3048e911d.sketch_text.stroke-142"),sQuery(id+"FHMxAyK4CFUKdhS_1.wireOp",EDGE,"1cb9c079-ea9b-4899-8069-e0e3048e911d.sketch_text.stroke-143"),sQuery(id+"FHMxAyK4CFUKdhS_1.wireOp",EDGE,"1cb9c079-ea9b-4899-8069-e0e3048e911d.sketch_text.stroke-144"),sQuery(id+"FHMxAyK4CFUKdhS_1.wireOp",EDGE,"1cb9c079-ea9b-4899-8069-e0e3048e911d.sketch_text.stroke-145"),sQuery(id+"FHMxAyK4CFUKdhS_1.wireOp",EDGE,"1cb9c079-ea9b-4899-8069-e0e3048e911d.sketch_text.stroke-146"),sQuery(id+"FHMxAyK4CFUKdhS_1.wireOp",EDGE,"1cb9c079-ea9b-4899-8069-e0e3048e911d.sketch_text.stroke-147"),sQuery(id+"FHMxAyK4CFUKdhS_1.wireOp",EDGE,"1cb9c079-ea9b-4899-8069-e0e3048e911d.sketch_text.stroke-148"),sQuery(id+"FHMxAyK4CFUKdhS_1.wireOp",EDGE,"1cb9c079-ea9b-4899-8069-e0e3048e911d.sketch_text.stroke-149"),sQuery(id+"FHMxAyK4CFUKdhS_1.wireOp",EDGE,"1cb9c079-ea9b-4899-8069-e0e3048e911d.sketch_text.stroke-150"),sQuery(id+"FHMxAyK4CFUKdhS_1.wireOp",EDGE,"1cb9c079-ea9b-4899-8069-e0e3048e911d.sketch_text.stroke-151"),sQuery(id+"FHMxAyK4CFUKdhS_1.wireOp",EDGE,"1cb9c079-ea9b-4899-8069-e0e3048e911d.sketch_text.stroke-152"),sQuery(id+"FHMxAyK4CFUKdhS_1.wireOp",EDGE,"1cb9c079-ea9b-4899-8069-e0e3048e911d.sketch_text.stroke-153"),sQuery(id+"FHMxAyK4CFUKdhS_1.wireOp",EDGE,"1cb9c079-ea9b-4899-8069-e0e3048e911d.sketch_text.stroke-159"),sQuery(id+"FHMxAyK4CFUKdhS_1.wireOp",EDGE,"1cb9c079-ea9b-4899-8069-e0e3048e911d.sketch_text.stroke-160"),sQuery(id+"FHMxAyK4CFUKdhS_1.wireOp",EDGE,"1cb9c079-ea9b-4899-8069-e0e3048e911d.sketch_text.stroke-161"),sQuery(id+"FHMxAyK4CFUKdhS_1.wireOp",EDGE,"1cb9c079-ea9b-4899-8069-e0e3048e911d.sketch_text.stroke-162"),sQuery(id+"FHMxAyK4CFUKdhS_1.wireOp",EDGE,"1cb9c079-ea9b-4899-8069-e0e3048e911d.sketch_text.stroke-163"),sQuery(id+"FHMxAyK4CFUKdhS_1.wireOp",EDGE,"1cb9c079-ea9b-4899-8069-e0e3048e911d.sketch_text.stroke-164"),sQuery(id+"FHMxAyK4CFUKdhS_1.wireOp",EDGE,"1cb9c079-ea9b-4899-8069-e0e3048e911d.sketch_text.stroke-165"),sQuery(id+"FHMxAyK4CFUKdhS_1.wireOp",EDGE,"1cb9c079-ea9b-4899-8069-e0e3048e911d.sketch_text.stroke-166"),sQuery(id+"FHMxAyK4CFUKdhS_1.wireOp",EDGE,"1cb9c079-ea9b-4899-8069-e0e3048e911d.sketch_text.stroke-167"),sQuery(id+"FHMxAyK4CFUKdhS_1.wireOp",EDGE,"1cb9c079-ea9b-4899-8069-e0e3048e911d.sketch_text.stroke-168"),sQuery(id+"FHMxAyK4CFUKdhS_1.wireOp",EDGE,"1cb9c079-ea9b-4899-8069-e0e3048e911d.sketch_text.stroke-169"),sQuery(id+"FHMxAyK4CFUKdhS_1.wireOp",EDGE,"1cb9c079-ea9b-4899-8069-e0e3048e911d.sketch_text.stroke-170"),sQuery(id+"FHMxAyK4CFUKdhS_1.wireOp",EDGE,"1cb9c079-ea9b-4899-8069-e0e3048e911d.sketch_text.stroke-171"),sQuery(id+"FHMxAyK4CFUKdhS_1.wireOp",EDGE,"1cb9c079-ea9b-4899-8069-e0e3048e911d.sketch_text.stroke-172"),sQuery(id+"FHMxAyK4CFUKdhS_1.wireOp",EDGE,"1cb9c079-ea9b-4899-8069-e0e3048e911d.sketch_text.stroke-173"),sQuery(id+"FHMxAyK4CFUKdhS_1.wireOp",EDGE,"1cb9c079-ea9b-4899-8069-e0e3048e911d.sketch_text.stroke-174"),sQuery(id+"FHMxAyK4CFUKdhS_1.wireOp",EDGE,"1cb9c079-ea9b-4899-8069-e0e3048e911d.sketch_text.stroke-175"),sQuery(id+"FHMxAyK4CFUKdhS_1.wireOp",EDGE,"1cb9c079-ea9b-4899-8069-e0e3048e911d.sketch_text.stroke-176"),sQuery(id+"FHMxAyK4CFUKdhS_1.wireOp",EDGE,"1cb9c079-ea9b-4899-8069-e0e3048e911d.sketch_text.stroke-177"),sQuery(id+"FHMxAyK4CFUKdhS_1.wireOp",EDGE,"1cb9c079-ea9b-4899-8069-e0e3048e911d.sketch_text.stroke-178"),sQuery(id+"FHMxAyK4CFUKdhS_1.wireOp",EDGE,"1cb9c079-ea9b-4899-8069-e0e3048e911d.sketch_text.stroke-179"),sQuery(id+"FHMxAyK4CFUKdhS_1.wireOp",EDGE,"1cb9c079-ea9b-4899-8069-e0e3048e911d.sketch_text.stroke-180"),sQuery(id+"F2.wireOp",EDGE,"E26"),subQ2])],"isStart":true}),makeQuery(id+"F3.opExtrude","SWEPT_FACE",FACE,{"disambiguationData":[OSD([subQ2])]})]),OD(1.0)],"derivedFrom":makeQuery(id+"F1.opExtrude","CAP_EDGE",EDGE,{"disambiguationData":[OSD([subQ0])],"isStart":false})});}
            fillet(context, id + "F4", {"entities" : qUnion([Q0, Q1, Q2, Q3, Q4, Q5, Q6, Q7, Q8, Q9, Q10, Q11, Q12, Q13, Q14, Q15, Q16, Q17, Q18, Q19, Q20, Q21, Q22, Q23, Q24, Q25, Q26, Q27]), "radius" : 5.08 * mm, "tangentPropagation" : true, "allowEdgeOverflow" : false});
        }
    });
